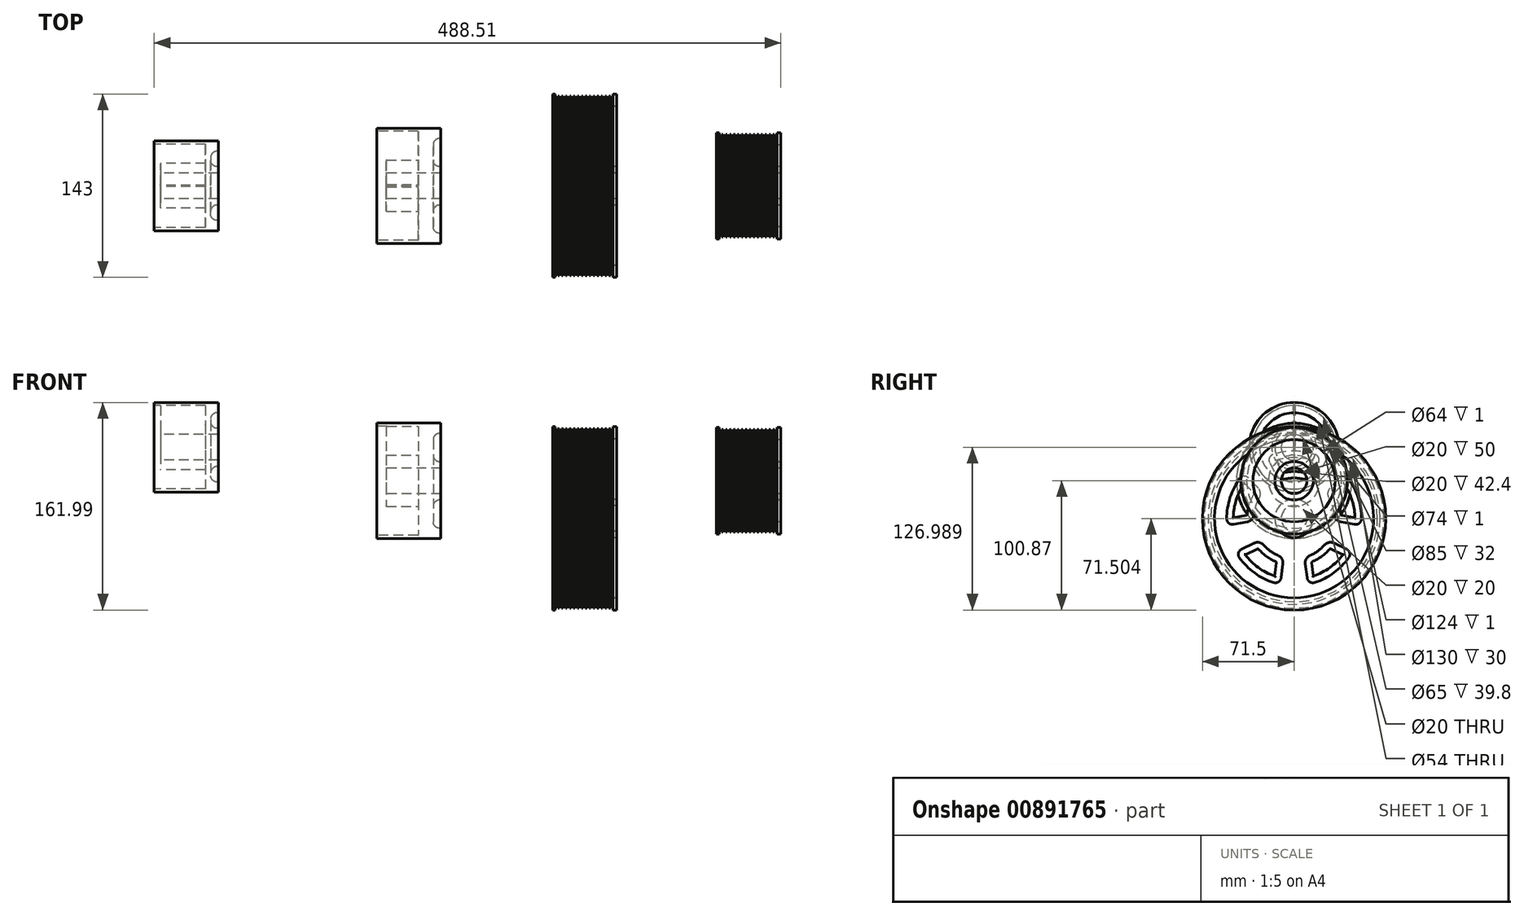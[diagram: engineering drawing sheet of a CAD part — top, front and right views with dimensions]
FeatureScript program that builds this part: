
annotation { "Feature Type Name" : "Feature", "Feature Type Description" : "" }
export const myFeature = defineFeature(function(context is Context, id is Id, definition is map)
    precondition{}
    {
        {
            var Q0;
            Q0=qCreatedBy(makeId("Front.planeOp"),FACE);
            var sketch = newSketch(context, id + "F0", { "sketchPlane" : qUnion([Q0])});
            skLineSegment(sketch, "E0", {"start": v(-106.98, 0) * mm, "end": v(107.53, 0) * mm, "construction": true});
            skLineSegment(sketch, "E1", {"start": v(107.53, 0) * mm, "end": v(107.53, 105.9) * mm, "construction": true});
            skPoint(sketch, "E2", {"position": v(107.53, 40) * mm});
            skPoint(sketch, "E3", {"position": v(57.53, 40) * mm});
            skPoint(sketch, "E4", {"position": v(107.53, 37) * mm});
            skPoint(sketch, "E5", {"position": v(57.53, 37) * mm});
            skPoint(sketch, "E6", {"position": v(107.53, 10) * mm});
            skPoint(sketch, "E7", {"position": v(57.53, 10) * mm});
            skLineSegment(sketch, "E8", {"start": v(57.53, 10) * mm, "end": v(107.53, 10) * mm});
            skLineSegment(sketch, "E9", {"start": v(57.53, 10) * mm, "end": v(57.53, 37) * mm});
            skLineSegment(sketch, "E10", {"start": v(107.53, 37) * mm, "end": v(57.53, 37) * mm});
            skLineSegment(sketch, "E11", {"start": v(57.53, 37) * mm, "end": v(57.53, 40) * mm});
            skLineSegment(sketch, "E12", {"start": v(107.53, 37) * mm, "end": v(107.53, 40) * mm});
            skPoint(sketch, "E13", {"position": v(101.53, 15) * mm});
            skPoint(sketch, "E14", {"position": v(101.53, 32) * mm});
            skLineSegment(sketch, "E15", {"start": v(106.53, 15) * mm, "end": v(107.53, 15) * mm});
            skLineSegment(sketch, "E16", {"start": v(107.53, 15) * mm, "end": v(107.53, 10) * mm});
            skLineSegment(sketch, "E17", {"start": v(101.53, 20) * mm, "end": v(101.53, 27) * mm});
            skLineSegment(sketch, "E18", {"start": v(107.53, 32) * mm, "end": v(107.53, 37) * mm});
            skLineSegment(sketch, "E19", {"start": v(106.53, 32) * mm, "end": v(107.53, 32) * mm});
            skArc(sketch, "E20.filletArc", {"start": v(106.53, 32) * mm, "mid": v(102.99, 30.54) * mm, "end": v(101.53, 27) * mm});
            skArc(sketch, "E21.filletArc", {"start": v(101.53, 20) * mm, "mid": v(102.99, 16.46) * mm, "end": v(106.53, 15) * mm});
            skLineSegment(sketch, "E22", {"start": v(59.53, 40) * mm, "end": v(59.94, 37) * mm});
            skLineSegment(sketch, "E23", {"start": v(59.94, 37) * mm, "end": v(60.94, 37) * mm});
            skLineSegment(sketch, "E24", {"start": v(105.64, 40) * mm, "end": v(105.53, 40) * mm});
            skLineSegment(sketch, "E25", {"start": v(60.94, 37) * mm, "end": v(61.6, 40) * mm});
            skPoint(sketch, "E25.endSnap0", {"position": v(58.53, 40) * mm});
            skLineSegment(sketch, "E26", {"start": v(61.6, 40) * mm, "end": v(62.6, 40) * mm});
            skLineSegment(sketch, "E27.1.0.0", {"start": v(62.6, 40) * mm, "end": v(63, 37) * mm});
            skLineSegment(sketch, "E27.1.0.1", {"start": v(63, 37) * mm, "end": v(64, 37) * mm});
            skLineSegment(sketch, "E27.1.0.2", {"start": v(64, 37) * mm, "end": v(64.67, 40) * mm});
            skLineSegment(sketch, "E27.1.0.3", {"start": v(64.67, 40) * mm, "end": v(65.67, 40) * mm});
            skLineSegment(sketch, "E27.2.0.0", {"start": v(65.67, 40) * mm, "end": v(66.08, 37) * mm});
            skLineSegment(sketch, "E27.2.0.1", {"start": v(66.08, 37) * mm, "end": v(67.08, 37) * mm});
            skLineSegment(sketch, "E27.2.0.2", {"start": v(67.08, 37) * mm, "end": v(67.75, 40) * mm});
            skLineSegment(sketch, "E27.2.0.3", {"start": v(67.75, 40) * mm, "end": v(68.75, 40) * mm});
            skLineSegment(sketch, "E27.3.0.0", {"start": v(68.75, 40) * mm, "end": v(69.16, 37) * mm});
            skLineSegment(sketch, "E27.3.0.1", {"start": v(69.16, 37) * mm, "end": v(70.16, 37) * mm});
            skLineSegment(sketch, "E27.3.0.2", {"start": v(70.16, 37) * mm, "end": v(70.82, 40) * mm});
            skLineSegment(sketch, "E27.3.0.3", {"start": v(70.82, 40) * mm, "end": v(71.82, 40) * mm});
            skLineSegment(sketch, "E27.4.0.0", {"start": v(71.82, 40) * mm, "end": v(72.23, 37) * mm});
            skLineSegment(sketch, "E27.4.0.1", {"start": v(72.23, 37) * mm, "end": v(73.23, 37) * mm});
            skLineSegment(sketch, "E27.4.0.2", {"start": v(73.23, 37) * mm, "end": v(73.9, 40) * mm});
            skLineSegment(sketch, "E27.4.0.3", {"start": v(73.9, 40) * mm, "end": v(74.9, 40) * mm});
            skLineSegment(sketch, "E27.5.0.0", {"start": v(74.9, 40) * mm, "end": v(75.3, 37) * mm});
            skLineSegment(sketch, "E27.5.0.1", {"start": v(75.3, 37) * mm, "end": v(76.3, 37) * mm});
            skLineSegment(sketch, "E27.5.0.2", {"start": v(76.3, 37) * mm, "end": v(76.97, 40) * mm});
            skLineSegment(sketch, "E27.5.0.3", {"start": v(76.97, 40) * mm, "end": v(77.97, 40) * mm});
            skLineSegment(sketch, "E27.6.0.0", {"start": v(77.97, 40) * mm, "end": v(78.38, 37) * mm});
            skLineSegment(sketch, "E27.6.0.1", {"start": v(78.38, 37) * mm, "end": v(79.38, 37) * mm});
            skLineSegment(sketch, "E27.6.0.2", {"start": v(79.38, 37) * mm, "end": v(80.05, 40) * mm});
            skLineSegment(sketch, "E27.6.0.3", {"start": v(80.05, 40) * mm, "end": v(81.05, 40) * mm});
            skLineSegment(sketch, "E27.7.0.0", {"start": v(81.05, 40) * mm, "end": v(81.46, 37) * mm});
            skLineSegment(sketch, "E27.7.0.1", {"start": v(81.46, 37) * mm, "end": v(82.46, 37) * mm});
            skLineSegment(sketch, "E27.7.0.2", {"start": v(82.46, 37) * mm, "end": v(83.12, 40) * mm});
            skLineSegment(sketch, "E27.7.0.3", {"start": v(83.12, 40) * mm, "end": v(84.12, 40) * mm});
            skLineSegment(sketch, "E27.8.0.0", {"start": v(84.12, 40) * mm, "end": v(84.53, 37) * mm});
            skLineSegment(sketch, "E27.8.0.1", {"start": v(84.53, 37) * mm, "end": v(85.53, 37) * mm});
            skLineSegment(sketch, "E27.8.0.2", {"start": v(85.53, 37) * mm, "end": v(86.2, 40) * mm});
            skLineSegment(sketch, "E27.8.0.3", {"start": v(86.2, 40) * mm, "end": v(87.2, 40) * mm});
            skLineSegment(sketch, "E27.9.0.0", {"start": v(87.2, 40) * mm, "end": v(87.6, 37) * mm});
            skLineSegment(sketch, "E27.9.0.1", {"start": v(87.6, 37) * mm, "end": v(88.6, 37) * mm});
            skLineSegment(sketch, "E27.9.0.2", {"start": v(88.6, 37) * mm, "end": v(89.27, 40) * mm});
            skLineSegment(sketch, "E27.9.0.3", {"start": v(89.27, 40) * mm, "end": v(90.27, 40) * mm});
            skLineSegment(sketch, "E27.10.0.0", {"start": v(90.27, 40) * mm, "end": v(90.68, 37) * mm});
            skLineSegment(sketch, "E27.10.0.1", {"start": v(90.68, 37) * mm, "end": v(91.68, 37) * mm});
            skLineSegment(sketch, "E27.10.0.2", {"start": v(91.68, 37) * mm, "end": v(92.34, 40) * mm});
            skLineSegment(sketch, "E27.10.0.3", {"start": v(92.34, 40) * mm, "end": v(93.34, 40) * mm});
            skLineSegment(sketch, "E27.11.0.0", {"start": v(93.34, 40) * mm, "end": v(93.75, 37) * mm});
            skLineSegment(sketch, "E27.11.0.1", {"start": v(93.75, 37) * mm, "end": v(94.75, 37) * mm});
            skLineSegment(sketch, "E27.11.0.2", {"start": v(94.75, 37) * mm, "end": v(95.42, 40) * mm});
            skLineSegment(sketch, "E27.11.0.3", {"start": v(95.42, 40) * mm, "end": v(96.42, 40) * mm});
            skLineSegment(sketch, "E27.12.0.0", {"start": v(96.42, 40) * mm, "end": v(96.83, 37) * mm});
            skLineSegment(sketch, "E27.12.0.1", {"start": v(96.83, 37) * mm, "end": v(97.83, 37) * mm});
            skLineSegment(sketch, "E27.12.0.2", {"start": v(97.83, 37) * mm, "end": v(98.5, 40) * mm});
            skLineSegment(sketch, "E27.12.0.3", {"start": v(98.5, 40) * mm, "end": v(99.5, 40) * mm});
            skLineSegment(sketch, "E27.13.0.0", {"start": v(99.5, 40) * mm, "end": v(99.9, 37) * mm});
            skLineSegment(sketch, "E27.13.0.1", {"start": v(99.9, 37) * mm, "end": v(100.9, 37) * mm});
            skLineSegment(sketch, "E27.13.0.2", {"start": v(100.9, 37) * mm, "end": v(101.57, 40) * mm});
            skLineSegment(sketch, "E27.13.0.3", {"start": v(101.57, 40) * mm, "end": v(102.57, 40) * mm});
            skLineSegment(sketch, "E27.14.0.0", {"start": v(102.57, 40) * mm, "end": v(102.98, 37) * mm});
            skLineSegment(sketch, "E27.14.0.1", {"start": v(102.98, 37) * mm, "end": v(103.98, 37) * mm});
            skLineSegment(sketch, "E27.14.0.2", {"start": v(103.98, 37) * mm, "end": v(104.64, 40) * mm});
            skLineSegment(sketch, "E27.14.0.3", {"start": v(105.53, 40) * mm, "end": v(105.64, 40) * mm});
            skLineSegment(sketch, "E27.direction1", {"start": v(59.94, 37) * mm, "end": v(63, 37) * mm, "construction": true});
            skLineSegment(sketch, "E28", {"start": v(-234.84, -29.37) * mm, "end": v(-20.34, -29.37) * mm, "construction": true});
            skLineSegment(sketch, "E29", {"start": v(-20.34, -29.37) * mm, "end": v(-20.34, 106.53) * mm, "construction": true});
            skPoint(sketch, "E30", {"position": v(-20.34, 40.63) * mm});
            skPoint(sketch, "E31", {"position": v(-70.34, 40.63) * mm});
            skPoint(sketch, "E32", {"position": v(-20.34, 37.63) * mm});
            skPoint(sketch, "E33", {"position": v(-70.34, 37.63) * mm});
            skPoint(sketch, "E34", {"position": v(-20.34, -19.37) * mm});
            skPoint(sketch, "E35", {"position": v(-70.34, -19.37) * mm});
            skLineSegment(sketch, "E36", {"start": v(-70.34, -19.37) * mm, "end": v(-20.34, -19.37) * mm});
            skLineSegment(sketch, "E37", {"start": v(-70.34, -19.37) * mm, "end": v(-70.34, 37.63) * mm});
            skLineSegment(sketch, "E38", {"start": v(-20.34, 37.63) * mm, "end": v(-70.34, 37.63) * mm});
            skLineSegment(sketch, "E39", {"start": v(-70.34, 37.63) * mm, "end": v(-70.34, 40.63) * mm});
            skLineSegment(sketch, "E40", {"start": v(-20.34, 37.63) * mm, "end": v(-20.34, 40.63) * mm});
            skPoint(sketch, "E41", {"position": v(-26.34, -14.37) * mm});
            skPoint(sketch, "E42", {"position": v(-26.34, 32.63) * mm});
            skLineSegment(sketch, "E43", {"start": v(-21.34, -14.37) * mm, "end": v(-20.34, -14.37) * mm});
            skLineSegment(sketch, "E44", {"start": v(-20.34, -14.37) * mm, "end": v(-20.34, -19.37) * mm});
            skLineSegment(sketch, "E45", {"start": v(-26.34, -9.37) * mm, "end": v(-26.34, 27.63) * mm});
            skLineSegment(sketch, "E46", {"start": v(-20.34, 32.63) * mm, "end": v(-20.34, 37.63) * mm});
            skLineSegment(sketch, "E47", {"start": v(-21.34, 32.63) * mm, "end": v(-20.34, 32.63) * mm});
            skArc(sketch, "E48.filletArc", {"start": v(-21.34, 32.63) * mm, "mid": v(-24.87, 31.17) * mm, "end": v(-26.34, 27.63) * mm});
            skArc(sketch, "E49.filletArc", {"start": v(-26.34, -9.37) * mm, "mid": v(-24.87, -12.9) * mm, "end": v(-21.34, -14.37) * mm});
            skLineSegment(sketch, "E50", {"start": v(-68.34, 40.63) * mm, "end": v(-67.93, 37.63) * mm});
            skLineSegment(sketch, "E51", {"start": v(-67.93, 37.63) * mm, "end": v(-66.93, 37.63) * mm});
            skLineSegment(sketch, "E52", {"start": v(-22.22, 40.63) * mm, "end": v(-22.34, 40.63) * mm});
            skLineSegment(sketch, "E53", {"start": v(-66.93, 37.63) * mm, "end": v(-66.26, 40.63) * mm});
            skPoint(sketch, "E53.endSnap0", {"position": v(-69.34, 40.63) * mm});
            skLineSegment(sketch, "E54", {"start": v(-66.26, 40.63) * mm, "end": v(-65.26, 40.63) * mm});
            skLineSegment(sketch, "E55.1.0.0", {"start": v(-65.26, 40.63) * mm, "end": v(-64.85, 37.63) * mm});
            skLineSegment(sketch, "E55.1.0.1", {"start": v(-64.85, 37.63) * mm, "end": v(-63.85, 37.63) * mm});
            skLineSegment(sketch, "E55.1.0.2", {"start": v(-63.85, 37.63) * mm, "end": v(-63.19, 40.63) * mm});
            skLineSegment(sketch, "E55.1.0.3", {"start": v(-63.19, 40.63) * mm, "end": v(-62.19, 40.63) * mm});
            skLineSegment(sketch, "E55.2.0.0", {"start": v(-62.19, 40.63) * mm, "end": v(-61.78, 37.63) * mm});
            skLineSegment(sketch, "E55.2.0.1", {"start": v(-61.78, 37.63) * mm, "end": v(-60.78, 37.63) * mm});
            skLineSegment(sketch, "E55.2.0.2", {"start": v(-60.78, 37.63) * mm, "end": v(-60.11, 40.63) * mm});
            skLineSegment(sketch, "E55.2.0.3", {"start": v(-60.11, 40.63) * mm, "end": v(-59.11, 40.63) * mm});
            skLineSegment(sketch, "E55.3.0.0", {"start": v(-59.11, 40.63) * mm, "end": v(-58.7, 37.63) * mm});
            skLineSegment(sketch, "E55.3.0.1", {"start": v(-58.7, 37.63) * mm, "end": v(-57.7, 37.63) * mm});
            skLineSegment(sketch, "E55.3.0.2", {"start": v(-57.7, 37.63) * mm, "end": v(-57.04, 40.63) * mm});
            skLineSegment(sketch, "E55.3.0.3", {"start": v(-57.04, 40.63) * mm, "end": v(-56.04, 40.63) * mm});
            skLineSegment(sketch, "E55.4.0.0", {"start": v(-56.04, 40.63) * mm, "end": v(-55.63, 37.63) * mm});
            skLineSegment(sketch, "E55.4.0.1", {"start": v(-55.63, 37.63) * mm, "end": v(-54.63, 37.63) * mm});
            skLineSegment(sketch, "E55.4.0.2", {"start": v(-54.63, 37.63) * mm, "end": v(-53.96, 40.63) * mm});
            skLineSegment(sketch, "E55.4.0.3", {"start": v(-53.96, 40.63) * mm, "end": v(-52.96, 40.63) * mm});
            skLineSegment(sketch, "E55.5.0.0", {"start": v(-52.96, 40.63) * mm, "end": v(-52.55, 37.63) * mm});
            skLineSegment(sketch, "E55.5.0.1", {"start": v(-52.55, 37.63) * mm, "end": v(-51.55, 37.63) * mm});
            skLineSegment(sketch, "E55.5.0.2", {"start": v(-51.55, 37.63) * mm, "end": v(-50.89, 40.63) * mm});
            skLineSegment(sketch, "E55.5.0.3", {"start": v(-50.89, 40.63) * mm, "end": v(-49.89, 40.63) * mm});
            skLineSegment(sketch, "E55.6.0.0", {"start": v(-49.89, 40.63) * mm, "end": v(-49.48, 37.63) * mm});
            skLineSegment(sketch, "E55.6.0.1", {"start": v(-49.48, 37.63) * mm, "end": v(-48.48, 37.63) * mm});
            skLineSegment(sketch, "E55.6.0.2", {"start": v(-48.48, 37.63) * mm, "end": v(-47.81, 40.63) * mm});
            skLineSegment(sketch, "E55.6.0.3", {"start": v(-47.81, 40.63) * mm, "end": v(-46.81, 40.63) * mm});
            skLineSegment(sketch, "E55.7.0.0", {"start": v(-46.81, 40.63) * mm, "end": v(-46.4, 37.63) * mm});
            skLineSegment(sketch, "E55.7.0.1", {"start": v(-46.4, 37.63) * mm, "end": v(-45.4, 37.63) * mm});
            skLineSegment(sketch, "E55.7.0.2", {"start": v(-45.4, 37.63) * mm, "end": v(-44.74, 40.63) * mm});
            skLineSegment(sketch, "E55.7.0.3", {"start": v(-44.74, 40.63) * mm, "end": v(-43.74, 40.63) * mm});
            skLineSegment(sketch, "E55.8.0.0", {"start": v(-43.74, 40.63) * mm, "end": v(-43.33, 37.63) * mm});
            skLineSegment(sketch, "E55.8.0.1", {"start": v(-43.33, 37.63) * mm, "end": v(-42.33, 37.63) * mm});
            skLineSegment(sketch, "E55.8.0.2", {"start": v(-42.33, 37.63) * mm, "end": v(-41.67, 40.63) * mm});
            skLineSegment(sketch, "E55.8.0.3", {"start": v(-41.67, 40.63) * mm, "end": v(-40.67, 40.63) * mm});
            skLineSegment(sketch, "E55.9.0.0", {"start": v(-40.67, 40.63) * mm, "end": v(-40.26, 37.63) * mm});
            skLineSegment(sketch, "E55.9.0.1", {"start": v(-40.26, 37.63) * mm, "end": v(-39.26, 37.63) * mm});
            skLineSegment(sketch, "E55.9.0.2", {"start": v(-39.26, 37.63) * mm, "end": v(-38.6, 40.63) * mm});
            skLineSegment(sketch, "E55.9.0.3", {"start": v(-38.6, 40.63) * mm, "end": v(-37.6, 40.63) * mm});
            skLineSegment(sketch, "E55.10.0.0", {"start": v(-37.6, 40.63) * mm, "end": v(-37.18, 37.63) * mm});
            skLineSegment(sketch, "E55.10.0.1", {"start": v(-37.18, 37.63) * mm, "end": v(-36.18, 37.63) * mm});
            skLineSegment(sketch, "E55.10.0.2", {"start": v(-36.18, 37.63) * mm, "end": v(-35.52, 40.63) * mm});
            skLineSegment(sketch, "E55.10.0.3", {"start": v(-35.52, 40.63) * mm, "end": v(-34.52, 40.63) * mm});
            skLineSegment(sketch, "E55.11.0.0", {"start": v(-34.52, 40.63) * mm, "end": v(-34.1, 37.63) * mm});
            skLineSegment(sketch, "E55.11.0.1", {"start": v(-34.1, 37.63) * mm, "end": v(-33.1, 37.63) * mm});
            skLineSegment(sketch, "E55.11.0.2", {"start": v(-33.1, 37.63) * mm, "end": v(-32.44, 40.63) * mm});
            skLineSegment(sketch, "E55.11.0.3", {"start": v(-32.44, 40.63) * mm, "end": v(-31.44, 40.63) * mm});
            skLineSegment(sketch, "E55.12.0.0", {"start": v(-31.44, 40.63) * mm, "end": v(-31.03, 37.63) * mm});
            skLineSegment(sketch, "E55.12.0.1", {"start": v(-31.03, 37.63) * mm, "end": v(-30.03, 37.63) * mm});
            skLineSegment(sketch, "E55.12.0.2", {"start": v(-30.03, 37.63) * mm, "end": v(-29.37, 40.63) * mm});
            skLineSegment(sketch, "E55.12.0.3", {"start": v(-29.37, 40.63) * mm, "end": v(-28.37, 40.63) * mm});
            skLineSegment(sketch, "E55.13.0.0", {"start": v(-28.37, 40.63) * mm, "end": v(-27.96, 37.63) * mm});
            skLineSegment(sketch, "E55.13.0.1", {"start": v(-27.96, 37.63) * mm, "end": v(-26.96, 37.63) * mm});
            skLineSegment(sketch, "E55.13.0.2", {"start": v(-26.96, 37.63) * mm, "end": v(-26.3, 40.63) * mm});
            skLineSegment(sketch, "E55.13.0.3", {"start": v(-26.3, 40.63) * mm, "end": v(-25.3, 40.63) * mm});
            skLineSegment(sketch, "E55.14.0.0", {"start": v(-25.3, 40.63) * mm, "end": v(-24.88, 37.63) * mm});
            skLineSegment(sketch, "E55.14.0.1", {"start": v(-24.88, 37.63) * mm, "end": v(-23.88, 37.63) * mm});
            skLineSegment(sketch, "E55.14.0.2", {"start": v(-23.88, 37.63) * mm, "end": v(-23.22, 40.63) * mm});
            skLineSegment(sketch, "E55.14.0.3", {"start": v(-22.34, 40.63) * mm, "end": v(-22.22, 40.63) * mm});
            skLineSegment(sketch, "E55.direction1", {"start": v(-67.93, 37.63) * mm, "end": v(-64.85, 37.63) * mm, "construction": true});
            skLineSegment(sketch, "E56", {"start": v(-371.94, 0) * mm, "end": v(-157.43, 0) * mm, "construction": true});
            skLineSegment(sketch, "E57", {"start": v(-157.43, 0) * mm, "end": v(-157.43, 105.9) * mm, "construction": true});
            skPoint(sketch, "E58", {"position": v(-157.43, 45) * mm});
            skPoint(sketch, "E59", {"position": v(-207.43, 45) * mm});
            skPoint(sketch, "E60", {"position": v(-157.43, 42) * mm});
            skPoint(sketch, "E61", {"position": v(-207.43, 42) * mm});
            skPoint(sketch, "E62", {"position": v(-157.43, 10) * mm});
            skPoint(sketch, "E63", {"position": v(-207.43, 10) * mm});
            skLineSegment(sketch, "E64", {"start": v(-207.43, 10) * mm, "end": v(-157.43, 10) * mm});
            skLineSegment(sketch, "E65", {"start": v(-207.43, 10) * mm, "end": v(-207.43, 42) * mm});
            skLineSegment(sketch, "E66", {"start": v(-157.43, 42) * mm, "end": v(-207.43, 42) * mm});
            skLineSegment(sketch, "E67", {"start": v(-207.43, 42) * mm, "end": v(-207.43, 45) * mm});
            skLineSegment(sketch, "E68", {"start": v(-157.43, 42) * mm, "end": v(-157.43, 45) * mm});
            skPoint(sketch, "E69", {"position": v(-163.43, 15) * mm});
            skPoint(sketch, "E70", {"position": v(-163.43, 37) * mm});
            skLineSegment(sketch, "E71", {"start": v(-158.43, 15) * mm, "end": v(-157.43, 15) * mm});
            skLineSegment(sketch, "E72", {"start": v(-157.43, 15) * mm, "end": v(-157.43, 10) * mm});
            skLineSegment(sketch, "E73", {"start": v(-163.43, 20) * mm, "end": v(-163.43, 32) * mm});
            skLineSegment(sketch, "E74", {"start": v(-157.43, 37) * mm, "end": v(-157.43, 42) * mm});
            skLineSegment(sketch, "E75", {"start": v(-158.43, 37) * mm, "end": v(-157.43, 37) * mm});
            skArc(sketch, "E76.filletArc", {"start": v(-158.43, 37) * mm, "mid": v(-161.97, 35.54) * mm, "end": v(-163.43, 32) * mm});
            skArc(sketch, "E77.filletArc", {"start": v(-163.43, 20) * mm, "mid": v(-161.97, 16.46) * mm, "end": v(-158.43, 15) * mm});
            skLineSegment(sketch, "E78", {"start": v(-207.43, 45) * mm, "end": v(-205.43, 45) * mm});
            skLineSegment(sketch, "E79", {"start": v(-205.43, 45) * mm, "end": v(-205.02, 42) * mm});
            skLineSegment(sketch, "E80", {"start": v(-205.02, 42) * mm, "end": v(-204.02, 42) * mm});
            skLineSegment(sketch, "E81", {"start": v(-157.43, 45) * mm, "end": v(-159.43, 45) * mm});
            skLineSegment(sketch, "E82", {"start": v(-204.02, 42) * mm, "end": v(-203.36, 45) * mm});
            skPoint(sketch, "E82.endSnap0", {"position": v(-206.43, 45) * mm});
            skLineSegment(sketch, "E83", {"start": v(-203.36, 45) * mm, "end": v(-202.36, 45) * mm});
            skLineSegment(sketch, "E84.1.0.0", {"start": v(-202.36, 45) * mm, "end": v(-201.95, 42) * mm});
            skLineSegment(sketch, "E84.1.0.1", {"start": v(-201.95, 42) * mm, "end": v(-200.95, 42) * mm});
            skLineSegment(sketch, "E84.1.0.2", {"start": v(-200.95, 42) * mm, "end": v(-200.29, 45) * mm});
            skLineSegment(sketch, "E84.1.0.3", {"start": v(-200.29, 45) * mm, "end": v(-199.29, 45) * mm});
            skLineSegment(sketch, "E84.2.0.0", {"start": v(-199.29, 45) * mm, "end": v(-198.88, 42) * mm});
            skLineSegment(sketch, "E84.2.0.1", {"start": v(-198.88, 42) * mm, "end": v(-197.88, 42) * mm});
            skLineSegment(sketch, "E84.2.0.2", {"start": v(-197.88, 42) * mm, "end": v(-197.21, 45) * mm});
            skLineSegment(sketch, "E84.2.0.3", {"start": v(-197.21, 45) * mm, "end": v(-196.21, 45) * mm});
            skLineSegment(sketch, "E84.3.0.0", {"start": v(-196.21, 45) * mm, "end": v(-195.8, 42) * mm});
            skLineSegment(sketch, "E84.3.0.1", {"start": v(-195.8, 42) * mm, "end": v(-194.8, 42) * mm});
            skLineSegment(sketch, "E84.3.0.2", {"start": v(-194.8, 42) * mm, "end": v(-194.14, 45) * mm});
            skLineSegment(sketch, "E84.3.0.3", {"start": v(-194.14, 45) * mm, "end": v(-193.14, 45) * mm});
            skLineSegment(sketch, "E84.4.0.0", {"start": v(-193.14, 45) * mm, "end": v(-192.73, 42) * mm});
            skLineSegment(sketch, "E84.4.0.1", {"start": v(-192.73, 42) * mm, "end": v(-191.73, 42) * mm});
            skLineSegment(sketch, "E84.4.0.2", {"start": v(-191.73, 42) * mm, "end": v(-191.06, 45) * mm});
            skLineSegment(sketch, "E84.4.0.3", {"start": v(-191.06, 45) * mm, "end": v(-190.06, 45) * mm});
            skLineSegment(sketch, "E84.5.0.0", {"start": v(-190.06, 45) * mm, "end": v(-189.65, 42) * mm});
            skLineSegment(sketch, "E84.5.0.1", {"start": v(-189.65, 42) * mm, "end": v(-188.65, 42) * mm});
            skLineSegment(sketch, "E84.5.0.2", {"start": v(-188.65, 42) * mm, "end": v(-187.99, 45) * mm});
            skLineSegment(sketch, "E84.5.0.3", {"start": v(-187.99, 45) * mm, "end": v(-186.99, 45) * mm});
            skLineSegment(sketch, "E84.6.0.0", {"start": v(-186.99, 45) * mm, "end": v(-186.58, 42) * mm});
            skLineSegment(sketch, "E84.6.0.1", {"start": v(-186.58, 42) * mm, "end": v(-185.58, 42) * mm});
            skLineSegment(sketch, "E84.6.0.2", {"start": v(-185.58, 42) * mm, "end": v(-184.91, 45) * mm});
            skLineSegment(sketch, "E84.6.0.3", {"start": v(-184.91, 45) * mm, "end": v(-183.91, 45) * mm});
            skLineSegment(sketch, "E84.7.0.0", {"start": v(-183.91, 45) * mm, "end": v(-183.5, 42) * mm});
            skLineSegment(sketch, "E84.7.0.1", {"start": v(-183.5, 42) * mm, "end": v(-182.5, 42) * mm});
            skLineSegment(sketch, "E84.7.0.2", {"start": v(-182.5, 42) * mm, "end": v(-181.84, 45) * mm});
            skLineSegment(sketch, "E84.7.0.3", {"start": v(-181.84, 45) * mm, "end": v(-180.84, 45) * mm});
            skLineSegment(sketch, "E84.8.0.0", {"start": v(-180.84, 45) * mm, "end": v(-180.43, 42) * mm});
            skLineSegment(sketch, "E84.8.0.1", {"start": v(-180.43, 42) * mm, "end": v(-179.43, 42) * mm});
            skLineSegment(sketch, "E84.8.0.2", {"start": v(-179.43, 42) * mm, "end": v(-178.76, 45) * mm});
            skLineSegment(sketch, "E84.8.0.3", {"start": v(-178.76, 45) * mm, "end": v(-177.76, 45) * mm});
            skLineSegment(sketch, "E84.9.0.0", {"start": v(-177.76, 45) * mm, "end": v(-177.35, 42) * mm});
            skLineSegment(sketch, "E84.9.0.1", {"start": v(-177.35, 42) * mm, "end": v(-176.35, 42) * mm});
            skLineSegment(sketch, "E84.9.0.2", {"start": v(-176.35, 42) * mm, "end": v(-175.7, 45) * mm});
            skLineSegment(sketch, "E84.9.0.3", {"start": v(-175.7, 45) * mm, "end": v(-174.7, 45) * mm});
            skLineSegment(sketch, "E84.10.0.0", {"start": v(-174.7, 45) * mm, "end": v(-174.28, 42) * mm});
            skLineSegment(sketch, "E84.10.0.1", {"start": v(-174.28, 42) * mm, "end": v(-173.28, 42) * mm});
            skLineSegment(sketch, "E84.10.0.2", {"start": v(-173.28, 42) * mm, "end": v(-172.62, 45) * mm});
            skLineSegment(sketch, "E84.10.0.3", {"start": v(-172.62, 45) * mm, "end": v(-171.62, 45) * mm});
            skLineSegment(sketch, "E84.11.0.0", {"start": v(-171.62, 45) * mm, "end": v(-171.2, 42) * mm});
            skLineSegment(sketch, "E84.11.0.1", {"start": v(-171.2, 42) * mm, "end": v(-170.2, 42) * mm});
            skLineSegment(sketch, "E84.11.0.2", {"start": v(-170.2, 42) * mm, "end": v(-169.54, 45) * mm});
            skLineSegment(sketch, "E84.11.0.3", {"start": v(-169.54, 45) * mm, "end": v(-168.54, 45) * mm});
            skLineSegment(sketch, "E84.12.0.0", {"start": v(-168.54, 45) * mm, "end": v(-168.13, 42) * mm});
            skLineSegment(sketch, "E84.12.0.1", {"start": v(-168.13, 42) * mm, "end": v(-167.13, 42) * mm});
            skLineSegment(sketch, "E84.12.0.2", {"start": v(-167.13, 42) * mm, "end": v(-166.47, 45) * mm});
            skLineSegment(sketch, "E84.12.0.3", {"start": v(-166.47, 45) * mm, "end": v(-165.47, 45) * mm});
            skLineSegment(sketch, "E84.13.0.0", {"start": v(-165.47, 45) * mm, "end": v(-165.06, 42) * mm});
            skLineSegment(sketch, "E84.13.0.1", {"start": v(-165.06, 42) * mm, "end": v(-164.06, 42) * mm});
            skLineSegment(sketch, "E84.13.0.2", {"start": v(-164.06, 42) * mm, "end": v(-163.4, 45) * mm});
            skLineSegment(sketch, "E84.13.0.3", {"start": v(-163.4, 45) * mm, "end": v(-162.4, 45) * mm});
            skLineSegment(sketch, "E84.14.0.0", {"start": v(-162.4, 45) * mm, "end": v(-161.98, 42) * mm});
            skLineSegment(sketch, "E84.14.0.1", {"start": v(-161.98, 42) * mm, "end": v(-160.98, 42) * mm});
            skLineSegment(sketch, "E84.14.0.2", {"start": v(-160.98, 42) * mm, "end": v(-160.32, 45) * mm});
            skLineSegment(sketch, "E84.14.0.3", {"start": v(-160.32, 45) * mm, "end": v(-159.32, 45) * mm});
            skLineSegment(sketch, "E84.direction1", {"start": v(-205.02, 42) * mm, "end": v(-201.95, 42) * mm, "construction": true});
            skLineSegment(sketch, "E85", {"start": v(-207.43, 45) * mm, "end": v(-160.32, 45) * mm});
            skLineSegment(sketch, "E86", {"start": v(-545.5, 26.12) * mm, "end": v(-330.98, 26.12) * mm, "construction": true});
            skLineSegment(sketch, "E87", {"start": v(-330.98, 26.12) * mm, "end": v(-330.98, 127.02) * mm, "construction": true});
            skPoint(sketch, "E88", {"position": v(-330.98, 61.12) * mm});
            skPoint(sketch, "E89", {"position": v(-380.98, 61.12) * mm});
            skPoint(sketch, "E90", {"position": v(-330.98, 58.12) * mm});
            skPoint(sketch, "E91", {"position": v(-380.98, 58.12) * mm});
            skPoint(sketch, "E92", {"position": v(-330.98, 36.12) * mm});
            skPoint(sketch, "E93", {"position": v(-380.98, 36.12) * mm});
            skLineSegment(sketch, "E94", {"start": v(-380.98, 36.12) * mm, "end": v(-330.98, 36.12) * mm});
            skLineSegment(sketch, "E95", {"start": v(-380.98, 36.12) * mm, "end": v(-380.98, 58.12) * mm});
            skLineSegment(sketch, "E96", {"start": v(-330.98, 58.12) * mm, "end": v(-380.98, 58.12) * mm});
            skLineSegment(sketch, "E97", {"start": v(-380.98, 58.12) * mm, "end": v(-380.98, 61.12) * mm});
            skLineSegment(sketch, "E98", {"start": v(-330.98, 58.12) * mm, "end": v(-330.98, 61.12) * mm});
            skPoint(sketch, "E99", {"position": v(-336.98, 41.12) * mm});
            skPoint(sketch, "E100", {"position": v(-336.98, 53.12) * mm});
            skLineSegment(sketch, "E101", {"start": v(-331.98, 41.12) * mm, "end": v(-330.98, 41.12) * mm});
            skLineSegment(sketch, "E102", {"start": v(-330.98, 41.12) * mm, "end": v(-330.98, 36.12) * mm});
            skLineSegment(sketch, "E103", {"start": v(-336.98, 46.12) * mm, "end": v(-336.98, 48.12) * mm});
            skLineSegment(sketch, "E104", {"start": v(-330.98, 53.12) * mm, "end": v(-330.98, 58.12) * mm});
            skLineSegment(sketch, "E105", {"start": v(-331.98, 53.12) * mm, "end": v(-330.98, 53.12) * mm});
            skArc(sketch, "E106.filletArc", {"start": v(-331.98, 53.12) * mm, "mid": v(-335.52, 51.65) * mm, "end": v(-336.98, 48.12) * mm});
            skArc(sketch, "E107.filletArc", {"start": v(-336.98, 46.12) * mm, "mid": v(-335.52, 42.58) * mm, "end": v(-331.98, 41.12) * mm});
            skLineSegment(sketch, "E108", {"start": v(-380.98, 61.12) * mm, "end": v(-378.98, 61.12) * mm});
            skLineSegment(sketch, "E109", {"start": v(-378.98, 61.12) * mm, "end": v(-378.57, 58.12) * mm});
            skLineSegment(sketch, "E110", {"start": v(-378.57, 58.12) * mm, "end": v(-377.57, 58.12) * mm});
            skLineSegment(sketch, "E111", {"start": v(-330.98, 61.12) * mm, "end": v(-332.98, 61.12) * mm});
            skLineSegment(sketch, "E112", {"start": v(-377.57, 58.12) * mm, "end": v(-376.9, 61.12) * mm});
            skPoint(sketch, "E112.endSnap0", {"position": v(-379.98, 61.12) * mm});
            skLineSegment(sketch, "E113", {"start": v(-376.9, 61.12) * mm, "end": v(-375.9, 61.12) * mm});
            skLineSegment(sketch, "E114.1.0.0", {"start": v(-375.9, 61.12) * mm, "end": v(-375.5, 58.12) * mm});
            skLineSegment(sketch, "E114.1.0.1", {"start": v(-375.5, 58.12) * mm, "end": v(-374.5, 58.12) * mm});
            skLineSegment(sketch, "E114.1.0.2", {"start": v(-374.5, 58.12) * mm, "end": v(-373.83, 61.12) * mm});
            skLineSegment(sketch, "E114.1.0.3", {"start": v(-373.83, 61.12) * mm, "end": v(-372.83, 61.12) * mm});
            skLineSegment(sketch, "E114.2.0.0", {"start": v(-372.83, 61.12) * mm, "end": v(-372.42, 58.12) * mm});
            skLineSegment(sketch, "E114.2.0.1", {"start": v(-372.42, 58.12) * mm, "end": v(-371.42, 58.12) * mm});
            skLineSegment(sketch, "E114.2.0.2", {"start": v(-371.42, 58.12) * mm, "end": v(-370.76, 61.12) * mm});
            skLineSegment(sketch, "E114.2.0.3", {"start": v(-370.76, 61.12) * mm, "end": v(-369.76, 61.12) * mm});
            skLineSegment(sketch, "E114.3.0.0", {"start": v(-369.76, 61.12) * mm, "end": v(-369.35, 58.12) * mm});
            skLineSegment(sketch, "E114.3.0.1", {"start": v(-369.35, 58.12) * mm, "end": v(-368.35, 58.12) * mm});
            skLineSegment(sketch, "E114.3.0.2", {"start": v(-368.35, 58.12) * mm, "end": v(-367.69, 61.12) * mm});
            skLineSegment(sketch, "E114.3.0.3", {"start": v(-367.69, 61.12) * mm, "end": v(-366.69, 61.12) * mm});
            skLineSegment(sketch, "E114.4.0.0", {"start": v(-366.69, 61.12) * mm, "end": v(-366.28, 58.12) * mm});
            skLineSegment(sketch, "E114.4.0.1", {"start": v(-366.28, 58.12) * mm, "end": v(-365.28, 58.12) * mm});
            skLineSegment(sketch, "E114.4.0.2", {"start": v(-365.28, 58.12) * mm, "end": v(-364.61, 61.12) * mm});
            skLineSegment(sketch, "E114.4.0.3", {"start": v(-364.61, 61.12) * mm, "end": v(-363.61, 61.12) * mm});
            skLineSegment(sketch, "E114.5.0.0", {"start": v(-363.61, 61.12) * mm, "end": v(-363.2, 58.12) * mm});
            skLineSegment(sketch, "E114.5.0.1", {"start": v(-363.2, 58.12) * mm, "end": v(-362.2, 58.12) * mm});
            skLineSegment(sketch, "E114.5.0.2", {"start": v(-362.2, 58.12) * mm, "end": v(-361.54, 61.12) * mm});
            skLineSegment(sketch, "E114.5.0.3", {"start": v(-361.54, 61.12) * mm, "end": v(-360.54, 61.12) * mm});
            skLineSegment(sketch, "E114.6.0.0", {"start": v(-360.54, 61.12) * mm, "end": v(-360.13, 58.12) * mm});
            skLineSegment(sketch, "E114.6.0.1", {"start": v(-360.13, 58.12) * mm, "end": v(-359.13, 58.12) * mm});
            skLineSegment(sketch, "E114.6.0.2", {"start": v(-359.13, 58.12) * mm, "end": v(-358.46, 61.12) * mm});
            skLineSegment(sketch, "E114.6.0.3", {"start": v(-358.46, 61.12) * mm, "end": v(-357.46, 61.12) * mm});
            skLineSegment(sketch, "E114.7.0.0", {"start": v(-357.46, 61.12) * mm, "end": v(-357.05, 58.12) * mm});
            skLineSegment(sketch, "E114.7.0.1", {"start": v(-357.05, 58.12) * mm, "end": v(-356.05, 58.12) * mm});
            skLineSegment(sketch, "E114.7.0.2", {"start": v(-356.05, 58.12) * mm, "end": v(-355.39, 61.12) * mm});
            skLineSegment(sketch, "E114.7.0.3", {"start": v(-355.39, 61.12) * mm, "end": v(-354.39, 61.12) * mm});
            skLineSegment(sketch, "E114.8.0.0", {"start": v(-354.39, 61.12) * mm, "end": v(-353.98, 58.12) * mm});
            skLineSegment(sketch, "E114.8.0.1", {"start": v(-353.98, 58.12) * mm, "end": v(-352.98, 58.12) * mm});
            skLineSegment(sketch, "E114.8.0.2", {"start": v(-352.98, 58.12) * mm, "end": v(-352.31, 61.12) * mm});
            skLineSegment(sketch, "E114.8.0.3", {"start": v(-352.31, 61.12) * mm, "end": v(-351.31, 61.12) * mm});
            skLineSegment(sketch, "E114.9.0.0", {"start": v(-351.31, 61.12) * mm, "end": v(-350.9, 58.12) * mm});
            skLineSegment(sketch, "E114.9.0.1", {"start": v(-350.9, 58.12) * mm, "end": v(-349.9, 58.12) * mm});
            skLineSegment(sketch, "E114.9.0.2", {"start": v(-349.9, 58.12) * mm, "end": v(-349.24, 61.12) * mm});
            skLineSegment(sketch, "E114.9.0.3", {"start": v(-349.24, 61.12) * mm, "end": v(-348.24, 61.12) * mm});
            skLineSegment(sketch, "E114.10.0.0", {"start": v(-348.24, 61.12) * mm, "end": v(-347.83, 58.12) * mm});
            skLineSegment(sketch, "E114.10.0.1", {"start": v(-347.83, 58.12) * mm, "end": v(-346.83, 58.12) * mm});
            skLineSegment(sketch, "E114.10.0.2", {"start": v(-346.83, 58.12) * mm, "end": v(-346.16, 61.12) * mm});
            skLineSegment(sketch, "E114.10.0.3", {"start": v(-346.16, 61.12) * mm, "end": v(-345.16, 61.12) * mm});
            skLineSegment(sketch, "E114.11.0.0", {"start": v(-345.16, 61.12) * mm, "end": v(-344.75, 58.12) * mm});
            skLineSegment(sketch, "E114.11.0.1", {"start": v(-344.75, 58.12) * mm, "end": v(-343.75, 58.12) * mm});
            skLineSegment(sketch, "E114.11.0.2", {"start": v(-343.75, 58.12) * mm, "end": v(-343.1, 61.12) * mm});
            skLineSegment(sketch, "E114.11.0.3", {"start": v(-343.1, 61.12) * mm, "end": v(-342.1, 61.12) * mm});
            skLineSegment(sketch, "E114.12.0.0", {"start": v(-342.1, 61.12) * mm, "end": v(-341.68, 58.12) * mm});
            skLineSegment(sketch, "E114.12.0.1", {"start": v(-341.68, 58.12) * mm, "end": v(-340.68, 58.12) * mm});
            skLineSegment(sketch, "E114.12.0.2", {"start": v(-340.68, 58.12) * mm, "end": v(-340.02, 61.12) * mm});
            skLineSegment(sketch, "E114.12.0.3", {"start": v(-340.02, 61.12) * mm, "end": v(-339.02, 61.12) * mm});
            skLineSegment(sketch, "E114.13.0.0", {"start": v(-339.02, 61.12) * mm, "end": v(-338.6, 58.12) * mm});
            skLineSegment(sketch, "E114.13.0.1", {"start": v(-338.6, 58.12) * mm, "end": v(-337.6, 58.12) * mm});
            skLineSegment(sketch, "E114.13.0.2", {"start": v(-337.6, 58.12) * mm, "end": v(-336.94, 61.12) * mm});
            skLineSegment(sketch, "E114.13.0.3", {"start": v(-336.94, 61.12) * mm, "end": v(-335.94, 61.12) * mm});
            skLineSegment(sketch, "E114.14.0.0", {"start": v(-335.94, 61.12) * mm, "end": v(-335.53, 58.12) * mm});
            skLineSegment(sketch, "E114.14.0.1", {"start": v(-335.53, 58.12) * mm, "end": v(-334.53, 58.12) * mm});
            skLineSegment(sketch, "E114.14.0.2", {"start": v(-334.53, 58.12) * mm, "end": v(-333.87, 61.12) * mm});
            skLineSegment(sketch, "E114.14.0.3", {"start": v(-333.87, 61.12) * mm, "end": v(-332.87, 61.12) * mm});
            skLineSegment(sketch, "E114.direction1", {"start": v(-378.57, 58.12) * mm, "end": v(-375.5, 58.12) * mm, "construction": true});
            skLineSegment(sketch, "E115", {"start": v(-380.98, 61.12) * mm, "end": v(-333.87, 61.12) * mm});
            skLineSegment(sketch, "E116", {"start": v(57.53, 40) * mm, "end": v(57.53, 41.5) * mm});
            skLineSegment(sketch, "E117", {"start": v(57.53, 41.5) * mm, "end": v(59.53, 41.5) * mm});
            skLineSegment(sketch, "E118", {"start": v(59.53, 41.5) * mm, "end": v(59.53, 40) * mm});
            skLineSegment(sketch, "E119", {"start": v(104.64, 40) * mm, "end": v(104.64, 41.5) * mm});
            skLineSegment(sketch, "E120", {"start": v(104.64, 41.5) * mm, "end": v(107.53, 41.5) * mm});
            skLineSegment(sketch, "E121", {"start": v(107.53, 41.5) * mm, "end": v(107.53, 40) * mm});
            skLineSegment(sketch, "E122", {"start": v(-70.34, 40.63) * mm, "end": v(-70.34, 42.13) * mm});
            skLineSegment(sketch, "E123", {"start": v(-70.34, 42.13) * mm, "end": v(-68.34, 42.13) * mm});
            skLineSegment(sketch, "E124", {"start": v(-68.34, 42.13) * mm, "end": v(-68.34, 40.63) * mm});
            skLineSegment(sketch, "E125", {"start": v(-23.22, 40.63) * mm, "end": v(-23.22, 42.13) * mm});
            skLineSegment(sketch, "E126", {"start": v(-23.22, 42.13) * mm, "end": v(-20.34, 42.13) * mm});
            skLineSegment(sketch, "E127", {"start": v(-20.34, 42.13) * mm, "end": v(-20.34, 40.63) * mm});
            skSolve(sketch);
        }
        {
            var Q0;
            Q0=makeQuery(id+"F0.imprint","IMPRINT",FACE,{"disambiguationData":[TD([[makeQuery(id+"F0.imprint","IMPRINT",EDGE,{"derivedFrom":sQuery(id+"F0.wireOp",EDGE,"E94")}),1.0]])]});
            var Q1;
            {var subQ4=sQuery(id+"F0.wireOp",EDGE,"E98");Q1=makeQuery(id+"F0.imprint","IMPRINT",FACE,{"disambiguationData":[TD([[makeQuery(id+"F0.imprint","IMPRINT",EDGE,{"derivedFrom":subQ4}),1.0]])]});}
            var Q2;
            {var subQ0=sQuery(id+"F0.wireOp",EDGE,"E114.14.0.0");Q2=makeQuery(id+"F0.imprint","IMPRINT",FACE,{"disambiguationData":[TD([[makeQuery(id+"F0.imprint","IMPRINT",EDGE,{"derivedFrom":subQ0}),1.0]])]});}
            var Q3;
            {var subQ0=sQuery(id+"F0.wireOp",EDGE,"E97");Q3=makeQuery(id+"F0.imprint","IMPRINT",FACE,{"disambiguationData":[TD([[makeQuery(id+"F0.imprint","IMPRINT",EDGE,{"derivedFrom":subQ0}),-1.0]])]});}
            var Q4;
            {var subQ0=sQuery(id+"F0.wireOp",EDGE,"E114.13.0.2");Q4=makeQuery(id+"F0.imprint","IMPRINT",FACE,{"disambiguationData":[TD([[makeQuery(id+"F0.imprint","IMPRINT",EDGE,{"derivedFrom":subQ0}),-1.0]])]});}
            var Q5;
            {var subQ0=sQuery(id+"F0.wireOp",EDGE,"E114.12.0.2");Q5=makeQuery(id+"F0.imprint","IMPRINT",FACE,{"disambiguationData":[TD([[makeQuery(id+"F0.imprint","IMPRINT",EDGE,{"derivedFrom":subQ0}),-1.0]])]});}
            var Q6;
            {var subQ0=sQuery(id+"F0.wireOp",EDGE,"E114.13.0.0");Q6=makeQuery(id+"F0.imprint","IMPRINT",FACE,{"disambiguationData":[TD([[makeQuery(id+"F0.imprint","IMPRINT",EDGE,{"derivedFrom":subQ0}),1.0]])]});}
            var Q7;
            {var subQ0=sQuery(id+"F0.wireOp",EDGE,"E109");Q7=makeQuery(id+"F0.imprint","IMPRINT",FACE,{"disambiguationData":[TD([[makeQuery(id+"F0.imprint","IMPRINT",EDGE,{"derivedFrom":subQ0}),1.0]])]});}
            var Q8;
            {var subQ0=sQuery(id+"F0.wireOp",EDGE,"E114.12.0.0");Q8=makeQuery(id+"F0.imprint","IMPRINT",FACE,{"disambiguationData":[TD([[makeQuery(id+"F0.imprint","IMPRINT",EDGE,{"derivedFrom":subQ0}),1.0]])]});}
            var Q9;
            {var subQ0=sQuery(id+"F0.wireOp",EDGE,"E112");Q9=makeQuery(id+"F0.imprint","IMPRINT",FACE,{"disambiguationData":[TD([[makeQuery(id+"F0.imprint","IMPRINT",EDGE,{"derivedFrom":subQ0}),-1.0]])]});}
            var Q10;
            {var subQ0=sQuery(id+"F0.wireOp",EDGE,"E114.6.0.2");Q10=makeQuery(id+"F0.imprint","IMPRINT",FACE,{"disambiguationData":[TD([[makeQuery(id+"F0.imprint","IMPRINT",EDGE,{"derivedFrom":subQ0}),-1.0]])]});}
            var Q11;
            {var subQ0=sQuery(id+"F0.wireOp",EDGE,"E114.11.0.2");Q11=makeQuery(id+"F0.imprint","IMPRINT",FACE,{"disambiguationData":[TD([[makeQuery(id+"F0.imprint","IMPRINT",EDGE,{"derivedFrom":subQ0}),-1.0]])]});}
            var Q12;
            {var subQ0=sQuery(id+"F0.wireOp",EDGE,"E114.1.0.0");Q12=makeQuery(id+"F0.imprint","IMPRINT",FACE,{"disambiguationData":[TD([[makeQuery(id+"F0.imprint","IMPRINT",EDGE,{"derivedFrom":subQ0}),1.0]])]});}
            var Q13;
            {var subQ0=sQuery(id+"F0.wireOp",EDGE,"E114.2.0.0");Q13=makeQuery(id+"F0.imprint","IMPRINT",FACE,{"disambiguationData":[TD([[makeQuery(id+"F0.imprint","IMPRINT",EDGE,{"derivedFrom":subQ0}),1.0]])]});}
            var Q14;
            {var subQ0=sQuery(id+"F0.wireOp",EDGE,"E114.10.0.2");Q14=makeQuery(id+"F0.imprint","IMPRINT",FACE,{"disambiguationData":[TD([[makeQuery(id+"F0.imprint","IMPRINT",EDGE,{"derivedFrom":subQ0}),-1.0]])]});}
            var Q15;
            {var subQ0=sQuery(id+"F0.wireOp",EDGE,"E114.8.0.2");Q15=makeQuery(id+"F0.imprint","IMPRINT",FACE,{"disambiguationData":[TD([[makeQuery(id+"F0.imprint","IMPRINT",EDGE,{"derivedFrom":subQ0}),-1.0]])]});}
            var Q16;
            {var subQ0=sQuery(id+"F0.wireOp",EDGE,"E114.5.0.2");Q16=makeQuery(id+"F0.imprint","IMPRINT",FACE,{"disambiguationData":[TD([[makeQuery(id+"F0.imprint","IMPRINT",EDGE,{"derivedFrom":subQ0}),-1.0]])]});}
            var Q17;
            {var subQ0=sQuery(id+"F0.wireOp",EDGE,"E114.10.0.0");Q17=makeQuery(id+"F0.imprint","IMPRINT",FACE,{"disambiguationData":[TD([[makeQuery(id+"F0.imprint","IMPRINT",EDGE,{"derivedFrom":subQ0}),1.0]])]});}
            var Q18;
            {var subQ0=sQuery(id+"F0.wireOp",EDGE,"E114.4.0.2");Q18=makeQuery(id+"F0.imprint","IMPRINT",FACE,{"disambiguationData":[TD([[makeQuery(id+"F0.imprint","IMPRINT",EDGE,{"derivedFrom":subQ0}),-1.0]])]});}
            var Q19;
            {var subQ0=sQuery(id+"F0.wireOp",EDGE,"E114.7.0.2");Q19=makeQuery(id+"F0.imprint","IMPRINT",FACE,{"disambiguationData":[TD([[makeQuery(id+"F0.imprint","IMPRINT",EDGE,{"derivedFrom":subQ0}),-1.0]])]});}
            var Q20;
            {var subQ0=sQuery(id+"F0.wireOp",EDGE,"E114.7.0.0");Q20=makeQuery(id+"F0.imprint","IMPRINT",FACE,{"disambiguationData":[TD([[makeQuery(id+"F0.imprint","IMPRINT",EDGE,{"derivedFrom":subQ0}),1.0]])]});}
            var Q21;
            {var subQ0=sQuery(id+"F0.wireOp",EDGE,"E114.9.0.2");Q21=makeQuery(id+"F0.imprint","IMPRINT",FACE,{"disambiguationData":[TD([[makeQuery(id+"F0.imprint","IMPRINT",EDGE,{"derivedFrom":subQ0}),-1.0]])]});}
            var Q22;
            {var subQ0=sQuery(id+"F0.wireOp",EDGE,"E114.4.0.0");Q22=makeQuery(id+"F0.imprint","IMPRINT",FACE,{"disambiguationData":[TD([[makeQuery(id+"F0.imprint","IMPRINT",EDGE,{"derivedFrom":subQ0}),1.0]])]});}
            var Q23;
            {var subQ0=sQuery(id+"F0.wireOp",EDGE,"E114.1.0.2");Q23=makeQuery(id+"F0.imprint","IMPRINT",FACE,{"disambiguationData":[TD([[makeQuery(id+"F0.imprint","IMPRINT",EDGE,{"derivedFrom":subQ0}),-1.0]])]});}
            var Q24;
            {var subQ0=sQuery(id+"F0.wireOp",EDGE,"E114.8.0.0");Q24=makeQuery(id+"F0.imprint","IMPRINT",FACE,{"disambiguationData":[TD([[makeQuery(id+"F0.imprint","IMPRINT",EDGE,{"derivedFrom":subQ0}),1.0]])]});}
            var Q25;
            {var subQ0=sQuery(id+"F0.wireOp",EDGE,"E114.6.0.0");Q25=makeQuery(id+"F0.imprint","IMPRINT",FACE,{"disambiguationData":[TD([[makeQuery(id+"F0.imprint","IMPRINT",EDGE,{"derivedFrom":subQ0}),1.0]])]});}
            var Q26;
            {var subQ0=sQuery(id+"F0.wireOp",EDGE,"E114.11.0.0");Q26=makeQuery(id+"F0.imprint","IMPRINT",FACE,{"disambiguationData":[TD([[makeQuery(id+"F0.imprint","IMPRINT",EDGE,{"derivedFrom":subQ0}),1.0]])]});}
            var Q27;
            {var subQ0=sQuery(id+"F0.wireOp",EDGE,"E114.3.0.2");Q27=makeQuery(id+"F0.imprint","IMPRINT",FACE,{"disambiguationData":[TD([[makeQuery(id+"F0.imprint","IMPRINT",EDGE,{"derivedFrom":subQ0}),-1.0]])]});}
            var Q28;
            {var subQ0=sQuery(id+"F0.wireOp",EDGE,"E114.5.0.0");Q28=makeQuery(id+"F0.imprint","IMPRINT",FACE,{"disambiguationData":[TD([[makeQuery(id+"F0.imprint","IMPRINT",EDGE,{"derivedFrom":subQ0}),1.0]])]});}
            var Q29;
            {var subQ0=sQuery(id+"F0.wireOp",EDGE,"E114.3.0.0");Q29=makeQuery(id+"F0.imprint","IMPRINT",FACE,{"disambiguationData":[TD([[makeQuery(id+"F0.imprint","IMPRINT",EDGE,{"derivedFrom":subQ0}),1.0]])]});}
            var Q30;
            {var subQ0=sQuery(id+"F0.wireOp",EDGE,"E114.9.0.0");Q30=makeQuery(id+"F0.imprint","IMPRINT",FACE,{"disambiguationData":[TD([[makeQuery(id+"F0.imprint","IMPRINT",EDGE,{"derivedFrom":subQ0}),1.0]])]});}
            var Q31;
            {var subQ0=sQuery(id+"F0.wireOp",EDGE,"E114.2.0.2");Q31=makeQuery(id+"F0.imprint","IMPRINT",FACE,{"disambiguationData":[TD([[makeQuery(id+"F0.imprint","IMPRINT",EDGE,{"derivedFrom":subQ0}),-1.0]])]});}
            var Q32;
            Q32=sQuery(id+"F0.wireOp",EDGE,"E86");
            revolve(context, id + "F1", {"surfaceOperationType" : NewSurfaceOperationType.NEW, "entities" : qUnion([Q0, Q1, Q2, Q3, Q4, Q5, Q6, Q7, Q8, Q9, Q10, Q11, Q12, Q13, Q14, Q15, Q16, Q17, Q18, Q19, Q20, Q21, Q22, Q23, Q24, Q25, Q26, Q27, Q28, Q29, Q30, Q31]), "axis" : qUnion([Q32]), "revolveType" : RevolveType.FULL});
        }
        {
            var Q0;
            Q0=makeQuery(id+"F0.imprint","IMPRINT",FACE,{"disambiguationData":[TD([[makeQuery(id+"F0.imprint","IMPRINT",EDGE,{"derivedFrom":sQuery(id+"F0.wireOp",EDGE,"E64")}),1.0]])]});
            var Q1;
            {var subQ4=sQuery(id+"F0.wireOp",EDGE,"E68");Q1=makeQuery(id+"F0.imprint","IMPRINT",FACE,{"disambiguationData":[TD([[makeQuery(id+"F0.imprint","IMPRINT",EDGE,{"derivedFrom":subQ4}),1.0]])]});}
            var Q2;
            {var subQ0=sQuery(id+"F0.wireOp",EDGE,"E84.14.0.0");Q2=makeQuery(id+"F0.imprint","IMPRINT",FACE,{"disambiguationData":[TD([[makeQuery(id+"F0.imprint","IMPRINT",EDGE,{"derivedFrom":subQ0}),1.0]])]});}
            var Q3;
            {var subQ0=sQuery(id+"F0.wireOp",EDGE,"E84.7.0.2");Q3=makeQuery(id+"F0.imprint","IMPRINT",FACE,{"disambiguationData":[TD([[makeQuery(id+"F0.imprint","IMPRINT",EDGE,{"derivedFrom":subQ0}),-1.0]])]});}
            var Q4;
            {var subQ0=sQuery(id+"F0.wireOp",EDGE,"E84.8.0.2");Q4=makeQuery(id+"F0.imprint","IMPRINT",FACE,{"disambiguationData":[TD([[makeQuery(id+"F0.imprint","IMPRINT",EDGE,{"derivedFrom":subQ0}),-1.0]])]});}
            var Q5;
            {var subQ0=sQuery(id+"F0.wireOp",EDGE,"E84.13.0.2");Q5=makeQuery(id+"F0.imprint","IMPRINT",FACE,{"disambiguationData":[TD([[makeQuery(id+"F0.imprint","IMPRINT",EDGE,{"derivedFrom":subQ0}),-1.0]])]});}
            var Q6;
            {var subQ0=sQuery(id+"F0.wireOp",EDGE,"E84.2.0.2");Q6=makeQuery(id+"F0.imprint","IMPRINT",FACE,{"disambiguationData":[TD([[makeQuery(id+"F0.imprint","IMPRINT",EDGE,{"derivedFrom":subQ0}),-1.0]])]});}
            var Q7;
            {var subQ0=sQuery(id+"F0.wireOp",EDGE,"E84.13.0.0");Q7=makeQuery(id+"F0.imprint","IMPRINT",FACE,{"disambiguationData":[TD([[makeQuery(id+"F0.imprint","IMPRINT",EDGE,{"derivedFrom":subQ0}),1.0]])]});}
            var Q8;
            {var subQ0=sQuery(id+"F0.wireOp",EDGE,"E84.9.0.2");Q8=makeQuery(id+"F0.imprint","IMPRINT",FACE,{"disambiguationData":[TD([[makeQuery(id+"F0.imprint","IMPRINT",EDGE,{"derivedFrom":subQ0}),-1.0]])]});}
            var Q9;
            {var subQ0=sQuery(id+"F0.wireOp",EDGE,"E84.9.0.0");Q9=makeQuery(id+"F0.imprint","IMPRINT",FACE,{"disambiguationData":[TD([[makeQuery(id+"F0.imprint","IMPRINT",EDGE,{"derivedFrom":subQ0}),1.0]])]});}
            var Q10;
            {var subQ0=sQuery(id+"F0.wireOp",EDGE,"E84.7.0.0");Q10=makeQuery(id+"F0.imprint","IMPRINT",FACE,{"disambiguationData":[TD([[makeQuery(id+"F0.imprint","IMPRINT",EDGE,{"derivedFrom":subQ0}),1.0]])]});}
            var Q11;
            {var subQ0=sQuery(id+"F0.wireOp",EDGE,"E84.8.0.0");Q11=makeQuery(id+"F0.imprint","IMPRINT",FACE,{"disambiguationData":[TD([[makeQuery(id+"F0.imprint","IMPRINT",EDGE,{"derivedFrom":subQ0}),1.0]])]});}
            var Q12;
            {var subQ0=sQuery(id+"F0.wireOp",EDGE,"E84.10.0.2");Q12=makeQuery(id+"F0.imprint","IMPRINT",FACE,{"disambiguationData":[TD([[makeQuery(id+"F0.imprint","IMPRINT",EDGE,{"derivedFrom":subQ0}),-1.0]])]});}
            var Q13;
            {var subQ0=sQuery(id+"F0.wireOp",EDGE,"E84.6.0.2");Q13=makeQuery(id+"F0.imprint","IMPRINT",FACE,{"disambiguationData":[TD([[makeQuery(id+"F0.imprint","IMPRINT",EDGE,{"derivedFrom":subQ0}),-1.0]])]});}
            var Q14;
            {var subQ0=sQuery(id+"F0.wireOp",EDGE,"E67");Q14=makeQuery(id+"F0.imprint","IMPRINT",FACE,{"disambiguationData":[TD([[makeQuery(id+"F0.imprint","IMPRINT",EDGE,{"derivedFrom":subQ0}),-1.0]])]});}
            var Q15;
            {var subQ0=sQuery(id+"F0.wireOp",EDGE,"E84.1.0.0");Q15=makeQuery(id+"F0.imprint","IMPRINT",FACE,{"disambiguationData":[TD([[makeQuery(id+"F0.imprint","IMPRINT",EDGE,{"derivedFrom":subQ0}),1.0]])]});}
            var Q16;
            {var subQ0=sQuery(id+"F0.wireOp",EDGE,"E84.4.0.0");Q16=makeQuery(id+"F0.imprint","IMPRINT",FACE,{"disambiguationData":[TD([[makeQuery(id+"F0.imprint","IMPRINT",EDGE,{"derivedFrom":subQ0}),1.0]])]});}
            var Q17;
            {var subQ0=sQuery(id+"F0.wireOp",EDGE,"E84.2.0.0");Q17=makeQuery(id+"F0.imprint","IMPRINT",FACE,{"disambiguationData":[TD([[makeQuery(id+"F0.imprint","IMPRINT",EDGE,{"derivedFrom":subQ0}),1.0]])]});}
            var Q18;
            {var subQ0=sQuery(id+"F0.wireOp",EDGE,"E84.11.0.2");Q18=makeQuery(id+"F0.imprint","IMPRINT",FACE,{"disambiguationData":[TD([[makeQuery(id+"F0.imprint","IMPRINT",EDGE,{"derivedFrom":subQ0}),-1.0]])]});}
            var Q19;
            {var subQ0=sQuery(id+"F0.wireOp",EDGE,"E84.10.0.0");Q19=makeQuery(id+"F0.imprint","IMPRINT",FACE,{"disambiguationData":[TD([[makeQuery(id+"F0.imprint","IMPRINT",EDGE,{"derivedFrom":subQ0}),1.0]])]});}
            var Q20;
            {var subQ0=sQuery(id+"F0.wireOp",EDGE,"E84.3.0.2");Q20=makeQuery(id+"F0.imprint","IMPRINT",FACE,{"disambiguationData":[TD([[makeQuery(id+"F0.imprint","IMPRINT",EDGE,{"derivedFrom":subQ0}),-1.0]])]});}
            var Q21;
            {var subQ0=sQuery(id+"F0.wireOp",EDGE,"E84.5.0.0");Q21=makeQuery(id+"F0.imprint","IMPRINT",FACE,{"disambiguationData":[TD([[makeQuery(id+"F0.imprint","IMPRINT",EDGE,{"derivedFrom":subQ0}),1.0]])]});}
            var Q22;
            {var subQ0=sQuery(id+"F0.wireOp",EDGE,"E84.12.0.2");Q22=makeQuery(id+"F0.imprint","IMPRINT",FACE,{"disambiguationData":[TD([[makeQuery(id+"F0.imprint","IMPRINT",EDGE,{"derivedFrom":subQ0}),-1.0]])]});}
            var Q23;
            {var subQ0=sQuery(id+"F0.wireOp",EDGE,"E79");Q23=makeQuery(id+"F0.imprint","IMPRINT",FACE,{"disambiguationData":[TD([[makeQuery(id+"F0.imprint","IMPRINT",EDGE,{"derivedFrom":subQ0}),1.0]])]});}
            var Q24;
            {var subQ0=sQuery(id+"F0.wireOp",EDGE,"E84.6.0.0");Q24=makeQuery(id+"F0.imprint","IMPRINT",FACE,{"disambiguationData":[TD([[makeQuery(id+"F0.imprint","IMPRINT",EDGE,{"derivedFrom":subQ0}),1.0]])]});}
            var Q25;
            {var subQ0=sQuery(id+"F0.wireOp",EDGE,"E84.3.0.0");Q25=makeQuery(id+"F0.imprint","IMPRINT",FACE,{"disambiguationData":[TD([[makeQuery(id+"F0.imprint","IMPRINT",EDGE,{"derivedFrom":subQ0}),1.0]])]});}
            var Q26;
            {var subQ0=sQuery(id+"F0.wireOp",EDGE,"E84.1.0.2");Q26=makeQuery(id+"F0.imprint","IMPRINT",FACE,{"disambiguationData":[TD([[makeQuery(id+"F0.imprint","IMPRINT",EDGE,{"derivedFrom":subQ0}),-1.0]])]});}
            var Q27;
            {var subQ0=sQuery(id+"F0.wireOp",EDGE,"E82");Q27=makeQuery(id+"F0.imprint","IMPRINT",FACE,{"disambiguationData":[TD([[makeQuery(id+"F0.imprint","IMPRINT",EDGE,{"derivedFrom":subQ0}),-1.0]])]});}
            var Q28;
            {var subQ0=sQuery(id+"F0.wireOp",EDGE,"E84.11.0.0");Q28=makeQuery(id+"F0.imprint","IMPRINT",FACE,{"disambiguationData":[TD([[makeQuery(id+"F0.imprint","IMPRINT",EDGE,{"derivedFrom":subQ0}),1.0]])]});}
            var Q29;
            {var subQ0=sQuery(id+"F0.wireOp",EDGE,"E84.12.0.0");Q29=makeQuery(id+"F0.imprint","IMPRINT",FACE,{"disambiguationData":[TD([[makeQuery(id+"F0.imprint","IMPRINT",EDGE,{"derivedFrom":subQ0}),1.0]])]});}
            var Q30;
            {var subQ0=sQuery(id+"F0.wireOp",EDGE,"E84.5.0.2");Q30=makeQuery(id+"F0.imprint","IMPRINT",FACE,{"disambiguationData":[TD([[makeQuery(id+"F0.imprint","IMPRINT",EDGE,{"derivedFrom":subQ0}),-1.0]])]});}
            var Q31;
            {var subQ0=sQuery(id+"F0.wireOp",EDGE,"E84.4.0.2");Q31=makeQuery(id+"F0.imprint","IMPRINT",FACE,{"disambiguationData":[TD([[makeQuery(id+"F0.imprint","IMPRINT",EDGE,{"derivedFrom":subQ0}),-1.0]])]});}
            var Q32;
            Q32=sQuery(id+"F0.wireOp",EDGE,"E56");
            revolve(context, id + "F2", {"surfaceOperationType" : NewSurfaceOperationType.NEW, "entities" : qUnion([Q0, Q1, Q2, Q3, Q4, Q5, Q6, Q7, Q8, Q9, Q10, Q11, Q12, Q13, Q14, Q15, Q16, Q17, Q18, Q19, Q20, Q21, Q22, Q23, Q24, Q25, Q26, Q27, Q28, Q29, Q30, Q31]), "axis" : qUnion([Q32]), "revolveType" : RevolveType.FULL});
        }
        {
            var Q0;
            Q0=makeQuery(id+"F0.imprint","IMPRINT",FACE,{"disambiguationData":[TD([[makeQuery(id+"F0.imprint","IMPRINT",EDGE,{"derivedFrom":sQuery(id+"F0.wireOp",EDGE,"E36")}),1.0]])]});
            var Q1;
            {var subQ1=sQuery(id+"F0.wireOp",EDGE,"E40");Q1=makeQuery(id+"F0.imprint","IMPRINT",FACE,{"disambiguationData":[TD([[makeQuery(id+"F0.imprint","IMPRINT",EDGE,{"derivedFrom":subQ1}),1.0]])]});}
            var Q2;
            {var subQ0=sQuery(id+"F0.wireOp",EDGE,"E55.10.0.2");Q2=makeQuery(id+"F0.imprint","IMPRINT",FACE,{"disambiguationData":[TD([[makeQuery(id+"F0.imprint","IMPRINT",EDGE,{"derivedFrom":subQ0}),-1.0]])]});}
            var Q3;
            {var subQ0=sQuery(id+"F0.wireOp",EDGE,"E55.13.0.2");Q3=makeQuery(id+"F0.imprint","IMPRINT",FACE,{"disambiguationData":[TD([[makeQuery(id+"F0.imprint","IMPRINT",EDGE,{"derivedFrom":subQ0}),-1.0]])]});}
            var Q4;
            {var subQ0=sQuery(id+"F0.wireOp",EDGE,"E55.12.0.2");Q4=makeQuery(id+"F0.imprint","IMPRINT",FACE,{"disambiguationData":[TD([[makeQuery(id+"F0.imprint","IMPRINT",EDGE,{"derivedFrom":subQ0}),-1.0]])]});}
            var Q5;
            {var subQ0=sQuery(id+"F0.wireOp",EDGE,"E39");Q5=makeQuery(id+"F0.imprint","IMPRINT",FACE,{"disambiguationData":[TD([[makeQuery(id+"F0.imprint","IMPRINT",EDGE,{"derivedFrom":subQ0}),-1.0]])]});}
            var Q6;
            {var subQ0=sQuery(id+"F0.wireOp",EDGE,"E55.11.0.2");Q6=makeQuery(id+"F0.imprint","IMPRINT",FACE,{"disambiguationData":[TD([[makeQuery(id+"F0.imprint","IMPRINT",EDGE,{"derivedFrom":subQ0}),-1.0]])]});}
            var Q7;
            {var subQ0=sQuery(id+"F0.wireOp",EDGE,"E55.4.0.2");Q7=makeQuery(id+"F0.imprint","IMPRINT",FACE,{"disambiguationData":[TD([[makeQuery(id+"F0.imprint","IMPRINT",EDGE,{"derivedFrom":subQ0}),-1.0]])]});}
            var Q8;
            {var subQ0=sQuery(id+"F0.wireOp",EDGE,"E55.8.0.2");Q8=makeQuery(id+"F0.imprint","IMPRINT",FACE,{"disambiguationData":[TD([[makeQuery(id+"F0.imprint","IMPRINT",EDGE,{"derivedFrom":subQ0}),-1.0]])]});}
            var Q9;
            {var subQ0=sQuery(id+"F0.wireOp",EDGE,"E55.9.0.2");Q9=makeQuery(id+"F0.imprint","IMPRINT",FACE,{"disambiguationData":[TD([[makeQuery(id+"F0.imprint","IMPRINT",EDGE,{"derivedFrom":subQ0}),-1.0]])]});}
            var Q10;
            {var subQ0=sQuery(id+"F0.wireOp",EDGE,"E55.7.0.2");Q10=makeQuery(id+"F0.imprint","IMPRINT",FACE,{"disambiguationData":[TD([[makeQuery(id+"F0.imprint","IMPRINT",EDGE,{"derivedFrom":subQ0}),-1.0]])]});}
            var Q11;
            {var subQ0=sQuery(id+"F0.wireOp",EDGE,"E55.5.0.2");Q11=makeQuery(id+"F0.imprint","IMPRINT",FACE,{"disambiguationData":[TD([[makeQuery(id+"F0.imprint","IMPRINT",EDGE,{"derivedFrom":subQ0}),-1.0]])]});}
            var Q12;
            {var subQ0=sQuery(id+"F0.wireOp",EDGE,"E55.6.0.2");Q12=makeQuery(id+"F0.imprint","IMPRINT",FACE,{"disambiguationData":[TD([[makeQuery(id+"F0.imprint","IMPRINT",EDGE,{"derivedFrom":subQ0}),-1.0]])]});}
            var Q13;
            {var subQ0=sQuery(id+"F0.wireOp",EDGE,"E55.3.0.2");Q13=makeQuery(id+"F0.imprint","IMPRINT",FACE,{"disambiguationData":[TD([[makeQuery(id+"F0.imprint","IMPRINT",EDGE,{"derivedFrom":subQ0}),-1.0]])]});}
            var Q14;
            {var subQ0=sQuery(id+"F0.wireOp",EDGE,"E55.1.0.2");Q14=makeQuery(id+"F0.imprint","IMPRINT",FACE,{"disambiguationData":[TD([[makeQuery(id+"F0.imprint","IMPRINT",EDGE,{"derivedFrom":subQ0}),-1.0]])]});}
            var Q15;
            {var subQ0=sQuery(id+"F0.wireOp",EDGE,"E53");Q15=makeQuery(id+"F0.imprint","IMPRINT",FACE,{"disambiguationData":[TD([[makeQuery(id+"F0.imprint","IMPRINT",EDGE,{"derivedFrom":subQ0}),-1.0]])]});}
            var Q16;
            {var subQ0=sQuery(id+"F0.wireOp",EDGE,"E55.2.0.2");Q16=makeQuery(id+"F0.imprint","IMPRINT",FACE,{"disambiguationData":[TD([[makeQuery(id+"F0.imprint","IMPRINT",EDGE,{"derivedFrom":subQ0}),-1.0]])]});}
            var Q17;
            Q17=sQuery(id+"F0.wireOp",EDGE,"E28");
            revolve(context, id + "F3", {"surfaceOperationType" : NewSurfaceOperationType.NEW, "entities" : qUnion([Q0, Q1, Q2, Q3, Q4, Q5, Q6, Q7, Q8, Q9, Q10, Q11, Q12, Q13, Q14, Q15, Q16]), "axis" : qUnion([Q17]), "revolveType" : RevolveType.FULL});
        }
        {
            var Q0;
            Q0=makeQuery(id+"F0.imprint","IMPRINT",FACE,{"disambiguationData":[TD([[makeQuery(id+"F0.imprint","IMPRINT",EDGE,{"derivedFrom":sQuery(id+"F0.wireOp",EDGE,"E8")}),1.0]])]});
            var Q1;
            {var subQ0=sQuery(id+"F0.wireOp",EDGE,"E11");Q1=makeQuery(id+"F0.imprint","IMPRINT",FACE,{"disambiguationData":[TD([[makeQuery(id+"F0.imprint","IMPRINT",EDGE,{"derivedFrom":subQ0}),-1.0]])]});}
            var Q2;
            {var subQ1=sQuery(id+"F0.wireOp",EDGE,"E12");Q2=makeQuery(id+"F0.imprint","IMPRINT",FACE,{"disambiguationData":[TD([[makeQuery(id+"F0.imprint","IMPRINT",EDGE,{"derivedFrom":subQ1}),1.0]])]});}
            var Q3;
            {var subQ0=sQuery(id+"F0.wireOp",EDGE,"E27.12.0.2");Q3=makeQuery(id+"F0.imprint","IMPRINT",FACE,{"disambiguationData":[TD([[makeQuery(id+"F0.imprint","IMPRINT",EDGE,{"derivedFrom":subQ0}),-1.0]])]});}
            var Q4;
            {var subQ0=sQuery(id+"F0.wireOp",EDGE,"E27.13.0.2");Q4=makeQuery(id+"F0.imprint","IMPRINT",FACE,{"disambiguationData":[TD([[makeQuery(id+"F0.imprint","IMPRINT",EDGE,{"derivedFrom":subQ0}),-1.0]])]});}
            var Q5;
            {var subQ0=sQuery(id+"F0.wireOp",EDGE,"E27.5.0.2");Q5=makeQuery(id+"F0.imprint","IMPRINT",FACE,{"disambiguationData":[TD([[makeQuery(id+"F0.imprint","IMPRINT",EDGE,{"derivedFrom":subQ0}),-1.0]])]});}
            var Q6;
            {var subQ0=sQuery(id+"F0.wireOp",EDGE,"E27.11.0.2");Q6=makeQuery(id+"F0.imprint","IMPRINT",FACE,{"disambiguationData":[TD([[makeQuery(id+"F0.imprint","IMPRINT",EDGE,{"derivedFrom":subQ0}),-1.0]])]});}
            var Q7;
            {var subQ0=sQuery(id+"F0.wireOp",EDGE,"E27.9.0.2");Q7=makeQuery(id+"F0.imprint","IMPRINT",FACE,{"disambiguationData":[TD([[makeQuery(id+"F0.imprint","IMPRINT",EDGE,{"derivedFrom":subQ0}),-1.0]])]});}
            var Q8;
            {var subQ0=sQuery(id+"F0.wireOp",EDGE,"E25");Q8=makeQuery(id+"F0.imprint","IMPRINT",FACE,{"disambiguationData":[TD([[makeQuery(id+"F0.imprint","IMPRINT",EDGE,{"derivedFrom":subQ0}),-1.0]])]});}
            var Q9;
            {var subQ0=sQuery(id+"F0.wireOp",EDGE,"E27.7.0.2");Q9=makeQuery(id+"F0.imprint","IMPRINT",FACE,{"disambiguationData":[TD([[makeQuery(id+"F0.imprint","IMPRINT",EDGE,{"derivedFrom":subQ0}),-1.0]])]});}
            var Q10;
            {var subQ0=sQuery(id+"F0.wireOp",EDGE,"E27.3.0.2");Q10=makeQuery(id+"F0.imprint","IMPRINT",FACE,{"disambiguationData":[TD([[makeQuery(id+"F0.imprint","IMPRINT",EDGE,{"derivedFrom":subQ0}),-1.0]])]});}
            var Q11;
            {var subQ0=sQuery(id+"F0.wireOp",EDGE,"E27.1.0.2");Q11=makeQuery(id+"F0.imprint","IMPRINT",FACE,{"disambiguationData":[TD([[makeQuery(id+"F0.imprint","IMPRINT",EDGE,{"derivedFrom":subQ0}),-1.0]])]});}
            var Q12;
            {var subQ0=sQuery(id+"F0.wireOp",EDGE,"E27.4.0.2");Q12=makeQuery(id+"F0.imprint","IMPRINT",FACE,{"disambiguationData":[TD([[makeQuery(id+"F0.imprint","IMPRINT",EDGE,{"derivedFrom":subQ0}),-1.0]])]});}
            var Q13;
            {var subQ0=sQuery(id+"F0.wireOp",EDGE,"E27.8.0.2");Q13=makeQuery(id+"F0.imprint","IMPRINT",FACE,{"disambiguationData":[TD([[makeQuery(id+"F0.imprint","IMPRINT",EDGE,{"derivedFrom":subQ0}),-1.0]])]});}
            var Q14;
            {var subQ0=sQuery(id+"F0.wireOp",EDGE,"E27.6.0.2");Q14=makeQuery(id+"F0.imprint","IMPRINT",FACE,{"disambiguationData":[TD([[makeQuery(id+"F0.imprint","IMPRINT",EDGE,{"derivedFrom":subQ0}),-1.0]])]});}
            var Q15;
            {var subQ0=sQuery(id+"F0.wireOp",EDGE,"E27.10.0.2");Q15=makeQuery(id+"F0.imprint","IMPRINT",FACE,{"disambiguationData":[TD([[makeQuery(id+"F0.imprint","IMPRINT",EDGE,{"derivedFrom":subQ0}),-1.0]])]});}
            var Q16;
            {var subQ0=sQuery(id+"F0.wireOp",EDGE,"E27.2.0.2");Q16=makeQuery(id+"F0.imprint","IMPRINT",FACE,{"disambiguationData":[TD([[makeQuery(id+"F0.imprint","IMPRINT",EDGE,{"derivedFrom":subQ0}),-1.0]])]});}
            var Q17;
            Q17=sQuery(id+"F0.wireOp",EDGE,"E0");
            revolve(context, id + "F4", {"surfaceOperationType" : NewSurfaceOperationType.NEW, "entities" : qUnion([Q0, Q1, Q2, Q3, Q4, Q5, Q6, Q7, Q8, Q9, Q10, Q11, Q12, Q13, Q14, Q15, Q16]), "axis" : qUnion([Q17]), "revolveType" : RevolveType.FULL});
        }
        {
            var Q0;
            Q0=makeQuery(id+"F3.opRevolve","SWEPT_FACE",FACE,{"disambiguationData":[OSD([sQuery(id+"F0.wireOp",EDGE,"E37"),sQuery(id+"F0.wireOp",EDGE,"E39")])]});
            var sketch = newSketch(context, id + "F5", { "sketchPlane" : qUnion([Q0])});
            skCircle(sketch, "E128.0", {"center": v(0, -29.37) * mm, "radius": 10 * mm});
            skCircle(sketch, "E129", {"center": v(0, -29.37) * mm, "radius": 65 * mm});
            skSolve(sketch);
        }
        {
            var Q0;
            Q0 = qSketchRegion(id + "F5", true);
            extrude(context, id + "F6", {"entities" : qUnion([Q0]), "operationType" : NewBodyOperationType.REMOVE, "oppositeDirection" : true, "depth" : 30 * mm, "offsetDistance" : 25 * mm});
        }
        {
            var Q0;
            Q0=makeQuery(id+"F3.opRevolve","SWEPT_FACE",FACE,{"disambiguationData":[OSD([sQuery(id+"F0.wireOp",EDGE,"E45")])]});
            var sketch = newSketch(context, id + "F7", { "sketchPlane" : qUnion([Q0])});
            skLineSegment(sketch, "E130", {"start": v(0, 27.63) * mm, "end": v(0, -86.37) * mm, "construction": true});
            skLineSegment(sketch, "E131", {"start": v(-57, -29.37) * mm, "end": v(57, -29.37) * mm, "construction": true});
            skPoint(sketch, "E131.startSnap0", {"position": v(0, -29.37) * mm});
            skCircle(sketch, "E132", {"center": v(0, -29.37) * mm, "radius": 52.5 * mm});
            skCircle(sketch, "E133", {"center": v(0, -29.37) * mm, "radius": 31.5 * mm});
            skLineSegment(sketch, "E134", {"start": v(-19.01, 14.05) * mm, "end": v(-13.83, 4.51) * mm});
            skArc(sketch, "E135", {"start": v(-16.47, 20.48) * mm, "mid": v(-19.25, 17.86) * mm, "end": v(-19.01, 14.05) * mm});
            skArc(sketch, "E136", {"start": v(-13.83, 4.51) * mm, "mid": v(-10.88, 1.78) * mm, "end": v(-6.89, 1.36) * mm});
            skPoint(sketch, "E137.orphan", {"position": v(-11.37, 0) * mm});
            skLineSegment(sketch, "E138.MirrorCS", {"start": v(19.01, 14.05) * mm, "end": v(13.83, 4.51) * mm});
            skArc(sketch, "E139.MirrorCS", {"start": v(16.47, 20.48) * mm, "mid": v(19.25, 17.86) * mm, "end": v(19.01, 14.05) * mm});
            skArc(sketch, "E140.MirrorCS", {"start": v(13.83, 4.51) * mm, "mid": v(10.88, 1.78) * mm, "end": v(6.89, 1.36) * mm});
            skLineSegment(sketch, "E141.1.0", {"start": v(-47.17, -34.03) * mm, "end": v(-36.5, -32.05) * mm});
            skArc(sketch, "E141.1.1", {"start": v(-52.5, -29.62) * mm, "mid": v(-50.87, -33.07) * mm, "end": v(-47.17, -34.03) * mm});
            skArc(sketch, "E141.1.2", {"start": v(-36.5, -32.05) * mm, "mid": v(-32.98, -30.1) * mm, "end": v(-31.35, -26.42) * mm});
            skArc(sketch, "E141.1.3", {"start": v(-27.95, -5.75) * mm, "mid": v(-26.25, -9.4) * mm, "end": v(-27.1, -13.32) * mm});
            skLineSegment(sketch, "E141.1.4", {"start": v(-35.42, 2.14) * mm, "end": v(-27.95, -5.75) * mm});
            skArc(sketch, "E141.1.5", {"start": v(-42.32, 1.7) * mm, "mid": v(-38.97, 3.53) * mm, "end": v(-35.42, 2.14) * mm});
            skLineSegment(sketch, "E141.2.0", {"start": v(-10.14, -75.67) * mm, "end": v(-8.73, -64.9) * mm});
            skArc(sketch, "E141.2.1", {"start": v(-15.98, -79.38) * mm, "mid": v(-12.2, -78.89) * mm, "end": v(-10.14, -75.67) * mm});
            skArc(sketch, "E141.2.2", {"start": v(-8.73, -64.9) * mm, "mid": v(-9.5, -60.96) * mm, "end": v(-12.5, -58.27) * mm});
            skArc(sketch, "E141.2.3", {"start": v(-31.1, -48.65) * mm, "mid": v(-27.1, -48.16) * mm, "end": v(-23.63, -50.18) * mm});
            skLineSegment(sketch, "E141.2.4", {"start": v(-40.9, -53.32) * mm, "end": v(-31.1, -48.65) * mm});
            skArc(sketch, "E141.2.5", {"start": v(-42.63, -60.01) * mm, "mid": v(-43.33, -56.26) * mm, "end": v(-40.9, -53.32) * mm});
            skLineSegment(sketch, "E141.3.0", {"start": v(40.9, -53.32) * mm, "end": v(31.1, -48.65) * mm});
            skArc(sketch, "E141.3.1", {"start": v(42.63, -60.01) * mm, "mid": v(43.33, -56.26) * mm, "end": v(40.9, -53.32) * mm});
            skArc(sketch, "E141.3.2", {"start": v(31.1, -48.65) * mm, "mid": v(27.1, -48.16) * mm, "end": v(23.63, -50.18) * mm});
            skArc(sketch, "E141.3.3", {"start": v(8.73, -64.9) * mm, "mid": v(9.5, -60.96) * mm, "end": v(12.5, -58.27) * mm});
            skLineSegment(sketch, "E141.3.4", {"start": v(10.14, -75.67) * mm, "end": v(8.73, -64.9) * mm});
            skArc(sketch, "E141.3.5", {"start": v(15.98, -79.38) * mm, "mid": v(12.2, -78.89) * mm, "end": v(10.14, -75.67) * mm});
            skLineSegment(sketch, "E141.4.0", {"start": v(35.42, 2.14) * mm, "end": v(27.95, -5.75) * mm});
            skArc(sketch, "E141.4.1", {"start": v(42.32, 1.7) * mm, "mid": v(38.97, 3.53) * mm, "end": v(35.42, 2.14) * mm});
            skArc(sketch, "E141.4.2", {"start": v(27.95, -5.75) * mm, "mid": v(26.25, -9.4) * mm, "end": v(27.1, -13.32) * mm});
            skArc(sketch, "E141.4.3", {"start": v(36.5, -32.05) * mm, "mid": v(32.98, -30.1) * mm, "end": v(31.35, -26.42) * mm});
            skLineSegment(sketch, "E141.4.4", {"start": v(47.17, -34.03) * mm, "end": v(36.5, -32.05) * mm});
            skArc(sketch, "E141.4.5", {"start": v(52.5, -29.62) * mm, "mid": v(50.87, -33.07) * mm, "end": v(47.17, -34.03) * mm});
            skSolve(sketch);
        }
        {
            var Q0;
            Q0=makeQuery(id+"F7.imprint","IMPRINT",FACE,{"disambiguationData":[TD([[makeQuery(id+"F7.imprint","IMPRINT",EDGE,{"derivedFrom":sQuery(id+"F7.wireOp",EDGE,"E134")}),1.0]])]});
            var Q1;
            Q1=makeQuery(id+"F7.imprint","IMPRINT",FACE,{"disambiguationData":[TD([[makeQuery(id+"F7.imprint","IMPRINT",EDGE,{"derivedFrom":sQuery(id+"F7.wireOp",EDGE,"E141.4.0")}),1.0]])]});
            var Q2;
            Q2=makeQuery(id+"F7.imprint","IMPRINT",FACE,{"disambiguationData":[TD([[makeQuery(id+"F7.imprint","IMPRINT",EDGE,{"derivedFrom":sQuery(id+"F7.wireOp",EDGE,"E141.3.0")}),1.0]])]});
            var Q3;
            Q3=makeQuery(id+"F7.imprint","IMPRINT",FACE,{"disambiguationData":[TD([[makeQuery(id+"F7.imprint","IMPRINT",EDGE,{"derivedFrom":sQuery(id+"F7.wireOp",EDGE,"E141.2.0")}),1.0]])]});
            var Q4;
            Q4=makeQuery(id+"F7.imprint","IMPRINT",FACE,{"disambiguationData":[TD([[makeQuery(id+"F7.imprint","IMPRINT",EDGE,{"derivedFrom":sQuery(id+"F7.wireOp",EDGE,"E141.1.0")}),1.0]])]});
            extrude(context, id + "F8", {"entities" : qUnion([Q0, Q1, Q2, Q3, Q4]), "operationType" : NewBodyOperationType.REMOVE, "oppositeDirection" : true, "depth" : 36.5 * mm, "offsetDistance" : 25 * mm, "hasDraft" : true, "draftAngle" : 20 * degree, "draftPullDirection" : true});
        }
        {
            var Q0;
            Q0=makeQuery(id+"F2.opRevolve","SWEPT_FACE",FACE,{"disambiguationData":[OSD([sQuery(id+"F0.wireOp",EDGE,"E65"),sQuery(id+"F0.wireOp",EDGE,"E67")])]});
            var sketch = newSketch(context, id + "F9", { "sketchPlane" : qUnion([Q0])});
            skCircle(sketch, "E142", {"center": v(0, 0) * mm, "radius": 42.5 * mm});
            skSolve(sketch);
        }
        {
            var Q0;
            Q0 = qSketchRegion(id + "F9", true);
            extrude(context, id + "F10", {"entities" : qUnion([Q0]), "operationType" : NewBodyOperationType.REMOVE, "oppositeDirection" : true, "depth" : 32.3 * mm, "offsetDistance" : 25 * mm});
        }
        {
            var Q0;
            Q0=makeQuery(id+"F10.boolean.opBoolean","COPY",FACE,{"derivedFrom":makeQuery(id+"F10.opExtrude","CAP_FACE",FACE,{"disambiguationData":[OSD([sQuery(id+"F9.wireOp",EDGE,"E142")])],"isStart":false})});
            var sketch = newSketch(context, id + "F11", { "sketchPlane" : qUnion([Q0])});
            skCircle(sketch, "E143", {"center": v(0, 0) * mm, "radius": 20 * mm});
            skCircle(sketch, "E144.0", {"center": v(0, 0) * mm, "radius": 10 * mm});
            skSolve(sketch);
        }
        {
            var Q0;
            Q0 = qSketchRegion(id + "F11", true);
            extrude(context, id + "F12", {"entities" : qUnion([Q0]), "operationType" : NewBodyOperationType.ADD, "depth" : 25 * mm, "offsetDistance" : 25 * mm});
        }
        {
            var Q0;
            Q0=makeQuery(id+"F10.boolean.opBoolean","COPY",FACE,{"derivedFrom":makeQuery(id+"F10.opExtrude","CAP_FACE",FACE,{"disambiguationData":[OSD([sQuery(id+"F9.wireOp",EDGE,"E142")])],"isStart":false})});
            var sketch = newSketch(context, id + "F13", { "sketchPlane" : qUnion([Q0])});
            skLineSegment(sketch, "E145", {"start": v(0, 42.5) * mm, "end": v(0, -42.5) * mm, "construction": true});
            skLineSegment(sketch, "E146", {"start": v(-42.5, 0) * mm, "end": v(42.5, 0) * mm, "construction": true});
            skLineSegment(sketch, "E147", {"start": v(-1, 42.49) * mm, "end": v(-0.37, 20) * mm});
            skLineSegment(sketch, "E148.MirrorCS", {"start": v(1, 42.49) * mm, "end": v(0.38, 20) * mm});
            skSolve(sketch);
        }
        {
            var Q0;
            {var subQ0=sQuery(id+"F13.wireOp",EDGE,"E147");Q0=makeQuery(id+"F13.imprint","IMPRINT",FACE,{"disambiguationData":[TD([[makeQuery(id+"F13.imprint","IMPRINT",EDGE,{"derivedFrom":subQ0}),1.0]])]});}
            var Q1;
            Q1=makeQuery(id+"F12.opExtrude","CAP_FACE",FACE,{"disambiguationData":[OSD([sQuery(id+"F11.wireOp",EDGE,"E143"),sQuery(id+"F11.wireOp",EDGE,"E144.0")])],"isStart":false});
            var Q2;
            Q2=makeQuery(id+"F2.opRevolve","SWEPT_BODY",BODY,{"disambiguationData":[OSD([sQuery(id+"F0.wireOp",EDGE,"E64"),sQuery(id+"F0.wireOp",EDGE,"E65"),sQuery(id+"F0.wireOp",EDGE,"E67"),sQuery(id+"F0.wireOp",EDGE,"E68"),sQuery(id+"F0.wireOp",EDGE,"E71"),sQuery(id+"F0.wireOp",EDGE,"E73"),sQuery(id+"F0.wireOp",EDGE,"E74"),sQuery(id+"F0.wireOp",EDGE,"E72"),sQuery(id+"F0.wireOp",EDGE,"E75"),sQuery(id+"F0.wireOp",EDGE,"E76.filletArc"),sQuery(id+"F0.wireOp",EDGE,"E77.filletArc"),sQuery(id+"F0.wireOp",EDGE,"E81"),sQuery(id+"F0.wireOp",EDGE,"E84.14.0.3"),sQuery(id+"F0.wireOp",EDGE,"E85")])]});
            extrude(context, id + "F14", {"entities" : qUnion([Q0]), "operationType" : NewBodyOperationType.ADD, "endBound" : BoundingType.UP_TO_SURFACE, "depth" : 25 * mm, "endBoundEntityFace" : qUnion([Q1]), "endBoundEntityBody" : qUnion([Q2]), "offsetDistance" : 25 * mm});
        }
        {
            var Q0;
            {var subQ0=sQuery(id+"F13.wireOp",EDGE,"E148.MirrorCS");var subQ1=sQuery(id+"F13.wireOp",EDGE,"E147");var subQ2=sQuery(id+"F11.wireOp",EDGE,"E143");var subQ3=sQuery(id+"F9.wireOp",EDGE,"E142");Q0=makeQuery(id+"FyYUAefgu6xEfva_4.49.F14.boolean.opBoolean","MERGE",FACE,{"derivedFrom":[makeQuery(id+"FyYUAefgu6xEfva_4.48.F14.boolean.opBoolean","MERGE",FACE,{"derivedFrom":[makeQuery(id+"FyYUAefgu6xEfva_4.47.F14.boolean.opBoolean","MERGE",FACE,{"derivedFrom":[makeQuery(id+"FyYUAefgu6xEfva_4.46.F14.boolean.opBoolean","MERGE",FACE,{"derivedFrom":[makeQuery(id+"FyYUAefgu6xEfva_4.45.F14.boolean.opBoolean","MERGE",FACE,{"derivedFrom":[makeQuery(id+"FyYUAefgu6xEfva_4.44.F14.boolean.opBoolean","MERGE",FACE,{"derivedFrom":[makeQuery(id+"FyYUAefgu6xEfva_4.43.F14.boolean.opBoolean","MERGE",FACE,{"derivedFrom":[makeQuery(id+"FyYUAefgu6xEfva_4.42.F14.boolean.opBoolean","MERGE",FACE,{"derivedFrom":[makeQuery(id+"FyYUAefgu6xEfva_4.41.F14.boolean.opBoolean","MERGE",FACE,{"derivedFrom":[makeQuery(id+"FyYUAefgu6xEfva_4.40.F14.boolean.opBoolean","MERGE",FACE,{"derivedFrom":[makeQuery(id+"FyYUAefgu6xEfva_4.39.F14.boolean.opBoolean","MERGE",FACE,{"derivedFrom":[makeQuery(id+"FyYUAefgu6xEfva_4.38.F14.boolean.opBoolean","MERGE",FACE,{"derivedFrom":[makeQuery(id+"FyYUAefgu6xEfva_4.37.F14.boolean.opBoolean","MERGE",FACE,{"derivedFrom":[makeQuery(id+"FyYUAefgu6xEfva_4.36.F14.boolean.opBoolean","MERGE",FACE,{"derivedFrom":[makeQuery(id+"FyYUAefgu6xEfva_4.35.F14.boolean.opBoolean","MERGE",FACE,{"derivedFrom":[makeQuery(id+"FyYUAefgu6xEfva_4.34.F14.boolean.opBoolean","MERGE",FACE,{"derivedFrom":[makeQuery(id+"FyYUAefgu6xEfva_4.33.F14.boolean.opBoolean","MERGE",FACE,{"derivedFrom":[makeQuery(id+"FyYUAefgu6xEfva_4.32.F14.boolean.opBoolean","MERGE",FACE,{"derivedFrom":[makeQuery(id+"FyYUAefgu6xEfva_4.31.F14.boolean.opBoolean","MERGE",FACE,{"derivedFrom":[makeQuery(id+"FyYUAefgu6xEfva_4.30.F14.boolean.opBoolean","MERGE",FACE,{"derivedFrom":[makeQuery(id+"FyYUAefgu6xEfva_4.29.F14.boolean.opBoolean","MERGE",FACE,{"derivedFrom":[makeQuery(id+"FyYUAefgu6xEfva_4.28.F14.boolean.opBoolean","MERGE",FACE,{"derivedFrom":[makeQuery(id+"FyYUAefgu6xEfva_4.27.F14.boolean.opBoolean","MERGE",FACE,{"derivedFrom":[makeQuery(id+"FyYUAefgu6xEfva_4.26.F14.boolean.opBoolean","MERGE",FACE,{"derivedFrom":[makeQuery(id+"FyYUAefgu6xEfva_4.25.F14.boolean.opBoolean","MERGE",FACE,{"derivedFrom":[makeQuery(id+"FyYUAefgu6xEfva_4.24.F14.boolean.opBoolean","MERGE",FACE,{"derivedFrom":[makeQuery(id+"FyYUAefgu6xEfva_4.23.F14.boolean.opBoolean","MERGE",FACE,{"derivedFrom":[makeQuery(id+"FyYUAefgu6xEfva_4.22.F14.boolean.opBoolean","MERGE",FACE,{"derivedFrom":[makeQuery(id+"FyYUAefgu6xEfva_4.21.F14.boolean.opBoolean","MERGE",FACE,{"derivedFrom":[makeQuery(id+"FyYUAefgu6xEfva_4.20.F14.boolean.opBoolean","MERGE",FACE,{"derivedFrom":[makeQuery(id+"FyYUAefgu6xEfva_4.19.F14.boolean.opBoolean","MERGE",FACE,{"derivedFrom":[makeQuery(id+"FyYUAefgu6xEfva_4.18.F14.boolean.opBoolean","MERGE",FACE,{"derivedFrom":[makeQuery(id+"FyYUAefgu6xEfva_4.17.F14.boolean.opBoolean","MERGE",FACE,{"derivedFrom":[makeQuery(id+"FyYUAefgu6xEfva_4.16.F14.boolean.opBoolean","MERGE",FACE,{"derivedFrom":[makeQuery(id+"FyYUAefgu6xEfva_4.15.F14.boolean.opBoolean","MERGE",FACE,{"derivedFrom":[makeQuery(id+"FyYUAefgu6xEfva_4.14.F14.boolean.opBoolean","MERGE",FACE,{"derivedFrom":[makeQuery(id+"FyYUAefgu6xEfva_4.13.F14.boolean.opBoolean","MERGE",FACE,{"derivedFrom":[makeQuery(id+"FyYUAefgu6xEfva_4.12.F14.boolean.opBoolean","MERGE",FACE,{"derivedFrom":[makeQuery(id+"FyYUAefgu6xEfva_4.11.F14.boolean.opBoolean","MERGE",FACE,{"derivedFrom":[makeQuery(id+"FyYUAefgu6xEfva_4.10.F14.boolean.opBoolean","MERGE",FACE,{"derivedFrom":[makeQuery(id+"FyYUAefgu6xEfva_4.9.F14.boolean.opBoolean","MERGE",FACE,{"derivedFrom":[makeQuery(id+"FyYUAefgu6xEfva_4.8.F14.boolean.opBoolean","MERGE",FACE,{"derivedFrom":[makeQuery(id+"FyYUAefgu6xEfva_4.7.F14.boolean.opBoolean","MERGE",FACE,{"derivedFrom":[makeQuery(id+"FyYUAefgu6xEfva_4.6.F14.boolean.opBoolean","MERGE",FACE,{"derivedFrom":[makeQuery(id+"FyYUAefgu6xEfva_4.5.F14.boolean.opBoolean","MERGE",FACE,{"derivedFrom":[makeQuery(id+"FyYUAefgu6xEfva_4.4.F14.boolean.opBoolean","MERGE",FACE,{"derivedFrom":[makeQuery(id+"FyYUAefgu6xEfva_4.3.F14.boolean.opBoolean","MERGE",FACE,{"derivedFrom":[makeQuery(id+"FyYUAefgu6xEfva_4.2.F14.boolean.opBoolean","MERGE",FACE,{"derivedFrom":[makeQuery(id+"FyYUAefgu6xEfva_4.1.F14.boolean.opBoolean","MERGE",FACE,{"derivedFrom":[makeQuery(id+"F14.boolean.opBoolean","MERGE",FACE,{"derivedFrom":[makeQuery(id+"F12.opExtrude","CAP_FACE",FACE,{"disambiguationData":[OSD([subQ2,sQuery(id+"F11.wireOp",EDGE,"E144.0")])],"isStart":false}),makeQuery(id+"F14.opExtrude","CAP_FACE",FACE,{"disambiguationData":[OSD([subQ3,subQ2,subQ1,subQ0])],"isStart":false})]}),makeQuery(id+"FyYUAefgu6xEfva_4.1.F14.opExtrude","CAP_FACE",FACE,{"disambiguationData":[OSD([subQ3,subQ2,subQ1,subQ0])],"isStart":false})]}),makeQuery(id+"FyYUAefgu6xEfva_4.2.F14.opExtrude","CAP_FACE",FACE,{"disambiguationData":[OSD([subQ3,subQ2,subQ1,subQ0])],"isStart":false})]}),makeQuery(id+"FyYUAefgu6xEfva_4.3.F14.opExtrude","CAP_FACE",FACE,{"disambiguationData":[OSD([subQ3,subQ2,subQ1,subQ0])],"isStart":false})]}),makeQuery(id+"FyYUAefgu6xEfva_4.4.F14.opExtrude","CAP_FACE",FACE,{"disambiguationData":[OSD([subQ3,subQ2,subQ1,subQ0])],"isStart":false})]}),makeQuery(id+"FyYUAefgu6xEfva_4.5.F14.opExtrude","CAP_FACE",FACE,{"disambiguationData":[OSD([subQ3,subQ2,subQ1,subQ0])],"isStart":false})]}),makeQuery(id+"FyYUAefgu6xEfva_4.6.F14.opExtrude","CAP_FACE",FACE,{"disambiguationData":[OSD([subQ3,subQ2,subQ1,subQ0])],"isStart":false})]}),makeQuery(id+"FyYUAefgu6xEfva_4.7.F14.opExtrude","CAP_FACE",FACE,{"disambiguationData":[OSD([subQ3,subQ2,subQ1,subQ0])],"isStart":false})]}),makeQuery(id+"FyYUAefgu6xEfva_4.8.F14.opExtrude","CAP_FACE",FACE,{"disambiguationData":[OSD([subQ3,subQ2,subQ1,subQ0])],"isStart":false})]}),makeQuery(id+"FyYUAefgu6xEfva_4.9.F14.opExtrude","CAP_FACE",FACE,{"disambiguationData":[OSD([subQ3,subQ2,subQ1,subQ0])],"isStart":false})]}),makeQuery(id+"FyYUAefgu6xEfva_4.10.F14.opExtrude","CAP_FACE",FACE,{"disambiguationData":[OSD([subQ3,subQ2,subQ1,subQ0])],"isStart":false})]}),makeQuery(id+"FyYUAefgu6xEfva_4.11.F14.opExtrude","CAP_FACE",FACE,{"disambiguationData":[OSD([subQ3,subQ2,subQ1,subQ0])],"isStart":false})]}),makeQuery(id+"FyYUAefgu6xEfva_4.12.F14.opExtrude","CAP_FACE",FACE,{"disambiguationData":[OSD([subQ3,subQ2,subQ1,subQ0])],"isStart":false})]}),makeQuery(id+"FyYUAefgu6xEfva_4.13.F14.opExtrude","CAP_FACE",FACE,{"disambiguationData":[OSD([subQ3,subQ2,subQ1,subQ0])],"isStart":false})]}),makeQuery(id+"FyYUAefgu6xEfva_4.14.F14.opExtrude","CAP_FACE",FACE,{"disambiguationData":[OSD([subQ3,subQ2,subQ1,subQ0])],"isStart":false})]}),makeQuery(id+"FyYUAefgu6xEfva_4.15.F14.opExtrude","CAP_FACE",FACE,{"disambiguationData":[OSD([subQ3,subQ2,subQ1,subQ0])],"isStart":false})]}),makeQuery(id+"FyYUAefgu6xEfva_4.16.F14.opExtrude","CAP_FACE",FACE,{"disambiguationData":[OSD([subQ3,subQ2,subQ1,subQ0])],"isStart":false})]}),makeQuery(id+"FyYUAefgu6xEfva_4.17.F14.opExtrude","CAP_FACE",FACE,{"disambiguationData":[OSD([subQ3,subQ2,subQ1,subQ0])],"isStart":false})]}),makeQuery(id+"FyYUAefgu6xEfva_4.18.F14.opExtrude","CAP_FACE",FACE,{"disambiguationData":[OSD([subQ3,subQ2,subQ1,subQ0])],"isStart":false})]}),makeQuery(id+"FyYUAefgu6xEfva_4.19.F14.opExtrude","CAP_FACE",FACE,{"disambiguationData":[OSD([subQ3,subQ2,subQ1,subQ0])],"isStart":false})]}),makeQuery(id+"FyYUAefgu6xEfva_4.20.F14.opExtrude","CAP_FACE",FACE,{"disambiguationData":[OSD([subQ3,subQ2,subQ1,subQ0])],"isStart":false})]}),makeQuery(id+"FyYUAefgu6xEfva_4.21.F14.opExtrude","CAP_FACE",FACE,{"disambiguationData":[OSD([subQ3,subQ2,subQ1,subQ0])],"isStart":false})]}),makeQuery(id+"FyYUAefgu6xEfva_4.22.F14.opExtrude","CAP_FACE",FACE,{"disambiguationData":[OSD([subQ3,subQ2,subQ1,subQ0])],"isStart":false})]}),makeQuery(id+"FyYUAefgu6xEfva_4.23.F14.opExtrude","CAP_FACE",FACE,{"disambiguationData":[OSD([subQ3,subQ2,subQ1,subQ0])],"isStart":false})]}),makeQuery(id+"FyYUAefgu6xEfva_4.24.F14.opExtrude","CAP_FACE",FACE,{"disambiguationData":[OSD([subQ3,subQ2,subQ1,subQ0])],"isStart":false})]}),makeQuery(id+"FyYUAefgu6xEfva_4.25.F14.opExtrude","CAP_FACE",FACE,{"disambiguationData":[OSD([subQ3,subQ2,subQ1,subQ0])],"isStart":false})]}),makeQuery(id+"FyYUAefgu6xEfva_4.26.F14.opExtrude","CAP_FACE",FACE,{"disambiguationData":[OSD([subQ3,subQ2,subQ1,subQ0])],"isStart":false})]}),makeQuery(id+"FyYUAefgu6xEfva_4.27.F14.opExtrude","CAP_FACE",FACE,{"disambiguationData":[OSD([subQ3,subQ2,subQ1,subQ0])],"isStart":false})]}),makeQuery(id+"FyYUAefgu6xEfva_4.28.F14.opExtrude","CAP_FACE",FACE,{"disambiguationData":[OSD([subQ3,subQ2,subQ1,subQ0])],"isStart":false})]}),makeQuery(id+"FyYUAefgu6xEfva_4.29.F14.opExtrude","CAP_FACE",FACE,{"disambiguationData":[OSD([subQ3,subQ2,subQ1,subQ0])],"isStart":false})]}),makeQuery(id+"FyYUAefgu6xEfva_4.30.F14.opExtrude","CAP_FACE",FACE,{"disambiguationData":[OSD([subQ3,subQ2,subQ1,subQ0])],"isStart":false})]}),makeQuery(id+"FyYUAefgu6xEfva_4.31.F14.opExtrude","CAP_FACE",FACE,{"disambiguationData":[OSD([subQ3,subQ2,subQ1,subQ0])],"isStart":false})]}),makeQuery(id+"FyYUAefgu6xEfva_4.32.F14.opExtrude","CAP_FACE",FACE,{"disambiguationData":[OSD([subQ3,subQ2,subQ1,subQ0])],"isStart":false})]}),makeQuery(id+"FyYUAefgu6xEfva_4.33.F14.opExtrude","CAP_FACE",FACE,{"disambiguationData":[OSD([subQ3,subQ2,subQ1,subQ0])],"isStart":false})]}),makeQuery(id+"FyYUAefgu6xEfva_4.34.F14.opExtrude","CAP_FACE",FACE,{"disambiguationData":[OSD([subQ3,subQ2,subQ1,subQ0])],"isStart":false})]}),makeQuery(id+"FyYUAefgu6xEfva_4.35.F14.opExtrude","CAP_FACE",FACE,{"disambiguationData":[OSD([subQ3,subQ2,subQ1,subQ0])],"isStart":false})]}),makeQuery(id+"FyYUAefgu6xEfva_4.36.F14.opExtrude","CAP_FACE",FACE,{"disambiguationData":[OSD([subQ3,subQ2,subQ1,subQ0])],"isStart":false})]}),makeQuery(id+"FyYUAefgu6xEfva_4.37.F14.opExtrude","CAP_FACE",FACE,{"disambiguationData":[OSD([subQ3,subQ2,subQ1,subQ0])],"isStart":false})]}),makeQuery(id+"FyYUAefgu6xEfva_4.38.F14.opExtrude","CAP_FACE",FACE,{"disambiguationData":[OSD([subQ3,subQ2,subQ1,subQ0])],"isStart":false})]}),makeQuery(id+"FyYUAefgu6xEfva_4.39.F14.opExtrude","CAP_FACE",FACE,{"disambiguationData":[OSD([subQ3,subQ2,subQ1,subQ0])],"isStart":false})]}),makeQuery(id+"FyYUAefgu6xEfva_4.40.F14.opExtrude","CAP_FACE",FACE,{"disambiguationData":[OSD([subQ3,subQ2,subQ1,subQ0])],"isStart":false})]}),makeQuery(id+"FyYUAefgu6xEfva_4.41.F14.opExtrude","CAP_FACE",FACE,{"disambiguationData":[OSD([subQ3,subQ2,subQ1,subQ0])],"isStart":false})]}),makeQuery(id+"FyYUAefgu6xEfva_4.42.F14.opExtrude","CAP_FACE",FACE,{"disambiguationData":[OSD([subQ3,subQ2,subQ1,subQ0])],"isStart":false})]}),makeQuery(id+"FyYUAefgu6xEfva_4.43.F14.opExtrude","CAP_FACE",FACE,{"disambiguationData":[OSD([subQ3,subQ2,subQ1,subQ0])],"isStart":false})]}),makeQuery(id+"FyYUAefgu6xEfva_4.44.F14.opExtrude","CAP_FACE",FACE,{"disambiguationData":[OSD([subQ3,subQ2,subQ1,subQ0])],"isStart":false})]}),makeQuery(id+"FyYUAefgu6xEfva_4.45.F14.opExtrude","CAP_FACE",FACE,{"disambiguationData":[OSD([subQ3,subQ2,subQ1,subQ0])],"isStart":false})]}),makeQuery(id+"FyYUAefgu6xEfva_4.46.F14.opExtrude","CAP_FACE",FACE,{"disambiguationData":[OSD([subQ3,subQ2,subQ1,subQ0])],"isStart":false})]}),makeQuery(id+"FyYUAefgu6xEfva_4.47.F14.opExtrude","CAP_FACE",FACE,{"disambiguationData":[OSD([subQ3,subQ2,subQ1,subQ0])],"isStart":false})]}),makeQuery(id+"FyYUAefgu6xEfva_4.48.F14.opExtrude","CAP_FACE",FACE,{"disambiguationData":[OSD([subQ3,subQ2,subQ1,subQ0])],"isStart":false})]}),makeQuery(id+"FyYUAefgu6xEfva_4.49.F14.opExtrude","CAP_FACE",FACE,{"disambiguationData":[OSD([subQ3,subQ2,subQ1,subQ0])],"isStart":false})]});}
            var Q1;
            Q1=makeQuery(id+"FyYUAefgu6xEfva_4.47.F14.opExtrude","CAP_EDGE",EDGE,{"disambiguationData":[OSD([sQuery(id+"F13.wireOp",EDGE,"E148.MirrorCS")])],"isStart":true});
            var Q2;
            {var subQ1=sQuery(id+"F11.wireOp",EDGE,"E143");var subQ4=makeQuery(id+"F14.opExtrude","SWEPT_FACE",FACE,{"disambiguationData":[OSD([sQuery(id+"F13.wireOp",EDGE,"E147")])]});Q2=makeQuery(id+"FyYUAefgu6xEfva_4.49.F14.boolean.opBoolean","SPLIT",EDGE,{"disambiguationData":[TD([subQ4])],"derivedFrom":makeQuery(id+"FyYUAefgu6xEfva_4.48.F14.boolean.opBoolean","SPLIT",EDGE,{"disambiguationData":[TD([subQ4])],"derivedFrom":makeQuery(id+"FyYUAefgu6xEfva_4.47.F14.boolean.opBoolean","SPLIT",EDGE,{"disambiguationData":[TD([subQ4])],"derivedFrom":makeQuery(id+"FyYUAefgu6xEfva_4.46.F14.boolean.opBoolean","SPLIT",EDGE,{"disambiguationData":[TD([subQ4])],"derivedFrom":makeQuery(id+"FyYUAefgu6xEfva_4.45.F14.boolean.opBoolean","SPLIT",EDGE,{"disambiguationData":[TD([subQ4])],"derivedFrom":makeQuery(id+"FyYUAefgu6xEfva_4.44.F14.boolean.opBoolean","SPLIT",EDGE,{"disambiguationData":[TD([subQ4])],"derivedFrom":makeQuery(id+"FyYUAefgu6xEfva_4.43.F14.boolean.opBoolean","SPLIT",EDGE,{"disambiguationData":[TD([subQ4])],"derivedFrom":makeQuery(id+"FyYUAefgu6xEfva_4.42.F14.boolean.opBoolean","SPLIT",EDGE,{"disambiguationData":[TD([subQ4])],"derivedFrom":makeQuery(id+"FyYUAefgu6xEfva_4.41.F14.boolean.opBoolean","SPLIT",EDGE,{"disambiguationData":[TD([subQ4])],"derivedFrom":makeQuery(id+"FyYUAefgu6xEfva_4.40.F14.boolean.opBoolean","SPLIT",EDGE,{"disambiguationData":[TD([subQ4])],"derivedFrom":makeQuery(id+"FyYUAefgu6xEfva_4.39.F14.boolean.opBoolean","SPLIT",EDGE,{"disambiguationData":[TD([subQ4])],"derivedFrom":makeQuery(id+"FyYUAefgu6xEfva_4.38.F14.boolean.opBoolean","SPLIT",EDGE,{"disambiguationData":[TD([subQ4])],"derivedFrom":makeQuery(id+"FyYUAefgu6xEfva_4.37.F14.boolean.opBoolean","SPLIT",EDGE,{"disambiguationData":[TD([subQ4])],"derivedFrom":makeQuery(id+"FyYUAefgu6xEfva_4.36.F14.boolean.opBoolean","SPLIT",EDGE,{"disambiguationData":[TD([subQ4])],"derivedFrom":makeQuery(id+"FyYUAefgu6xEfva_4.35.F14.boolean.opBoolean","SPLIT",EDGE,{"disambiguationData":[TD([subQ4])],"derivedFrom":makeQuery(id+"FyYUAefgu6xEfva_4.34.F14.boolean.opBoolean","SPLIT",EDGE,{"disambiguationData":[TD([subQ4])],"derivedFrom":makeQuery(id+"FyYUAefgu6xEfva_4.33.F14.boolean.opBoolean","SPLIT",EDGE,{"disambiguationData":[TD([subQ4])],"derivedFrom":makeQuery(id+"FyYUAefgu6xEfva_4.32.F14.boolean.opBoolean","SPLIT",EDGE,{"disambiguationData":[TD([subQ4])],"derivedFrom":makeQuery(id+"FyYUAefgu6xEfva_4.31.F14.boolean.opBoolean","SPLIT",EDGE,{"disambiguationData":[TD([subQ4])],"derivedFrom":makeQuery(id+"FyYUAefgu6xEfva_4.30.F14.boolean.opBoolean","SPLIT",EDGE,{"disambiguationData":[TD([subQ4])],"derivedFrom":makeQuery(id+"FyYUAefgu6xEfva_4.29.F14.boolean.opBoolean","SPLIT",EDGE,{"disambiguationData":[TD([subQ4])],"derivedFrom":makeQuery(id+"FyYUAefgu6xEfva_4.28.F14.boolean.opBoolean","SPLIT",EDGE,{"disambiguationData":[TD([subQ4])],"derivedFrom":makeQuery(id+"FyYUAefgu6xEfva_4.27.F14.boolean.opBoolean","SPLIT",EDGE,{"disambiguationData":[TD([subQ4])],"derivedFrom":makeQuery(id+"FyYUAefgu6xEfva_4.26.F14.boolean.opBoolean","SPLIT",EDGE,{"disambiguationData":[TD([subQ4])],"derivedFrom":makeQuery(id+"FyYUAefgu6xEfva_4.25.F14.boolean.opBoolean","SPLIT",EDGE,{"disambiguationData":[TD([subQ4])],"derivedFrom":makeQuery(id+"FyYUAefgu6xEfva_4.24.F14.boolean.opBoolean","SPLIT",EDGE,{"disambiguationData":[TD([subQ4])],"derivedFrom":makeQuery(id+"FyYUAefgu6xEfva_4.23.F14.boolean.opBoolean","SPLIT",EDGE,{"disambiguationData":[TD([subQ4])],"derivedFrom":makeQuery(id+"FyYUAefgu6xEfva_4.22.F14.boolean.opBoolean","SPLIT",EDGE,{"disambiguationData":[TD([subQ4])],"derivedFrom":makeQuery(id+"FyYUAefgu6xEfva_4.21.F14.boolean.opBoolean","SPLIT",EDGE,{"disambiguationData":[TD([subQ4])],"derivedFrom":makeQuery(id+"FyYUAefgu6xEfva_4.20.F14.boolean.opBoolean","SPLIT",EDGE,{"disambiguationData":[TD([subQ4])],"derivedFrom":makeQuery(id+"FyYUAefgu6xEfva_4.19.F14.boolean.opBoolean","SPLIT",EDGE,{"disambiguationData":[TD([subQ4])],"derivedFrom":makeQuery(id+"FyYUAefgu6xEfva_4.18.F14.boolean.opBoolean","SPLIT",EDGE,{"disambiguationData":[TD([subQ4])],"derivedFrom":makeQuery(id+"FyYUAefgu6xEfva_4.17.F14.boolean.opBoolean","SPLIT",EDGE,{"disambiguationData":[TD([subQ4])],"derivedFrom":makeQuery(id+"FyYUAefgu6xEfva_4.16.F14.boolean.opBoolean","SPLIT",EDGE,{"disambiguationData":[TD([subQ4])],"derivedFrom":makeQuery(id+"FyYUAefgu6xEfva_4.15.F14.boolean.opBoolean","SPLIT",EDGE,{"disambiguationData":[TD([subQ4])],"derivedFrom":makeQuery(id+"FyYUAefgu6xEfva_4.14.F14.boolean.opBoolean","SPLIT",EDGE,{"disambiguationData":[TD([subQ4])],"derivedFrom":makeQuery(id+"FyYUAefgu6xEfva_4.13.F14.boolean.opBoolean","SPLIT",EDGE,{"disambiguationData":[TD([subQ4])],"derivedFrom":makeQuery(id+"FyYUAefgu6xEfva_4.12.F14.boolean.opBoolean","SPLIT",EDGE,{"disambiguationData":[TD([subQ4])],"derivedFrom":makeQuery(id+"FyYUAefgu6xEfva_4.11.F14.boolean.opBoolean","SPLIT",EDGE,{"disambiguationData":[TD([subQ4])],"derivedFrom":makeQuery(id+"FyYUAefgu6xEfva_4.10.F14.boolean.opBoolean","SPLIT",EDGE,{"disambiguationData":[TD([subQ4])],"derivedFrom":makeQuery(id+"FyYUAefgu6xEfva_4.9.F14.boolean.opBoolean","SPLIT",EDGE,{"disambiguationData":[TD([subQ4])],"derivedFrom":makeQuery(id+"FyYUAefgu6xEfva_4.8.F14.boolean.opBoolean","SPLIT",EDGE,{"disambiguationData":[TD([subQ4])],"derivedFrom":makeQuery(id+"FyYUAefgu6xEfva_4.7.F14.boolean.opBoolean","SPLIT",EDGE,{"disambiguationData":[TD([subQ4])],"derivedFrom":makeQuery(id+"FyYUAefgu6xEfva_4.6.F14.boolean.opBoolean","SPLIT",EDGE,{"disambiguationData":[TD([subQ4])],"derivedFrom":makeQuery(id+"FyYUAefgu6xEfva_4.5.F14.boolean.opBoolean","SPLIT",EDGE,{"disambiguationData":[TD([subQ4])],"derivedFrom":makeQuery(id+"FyYUAefgu6xEfva_4.4.F14.boolean.opBoolean","SPLIT",EDGE,{"disambiguationData":[TD([subQ4])],"derivedFrom":makeQuery(id+"FyYUAefgu6xEfva_4.3.F14.boolean.opBoolean","SPLIT",EDGE,{"disambiguationData":[TD([subQ4])],"derivedFrom":makeQuery(id+"FyYUAefgu6xEfva_4.2.F14.boolean.opBoolean","SPLIT",EDGE,{"disambiguationData":[TD([subQ4])],"derivedFrom":makeQuery(id+"FyYUAefgu6xEfva_4.1.F14.boolean.opBoolean","SPLIT",EDGE,{"disambiguationData":[TD([subQ4])],"derivedFrom":makeQuery(id+"F12.opExtrude","CAP_EDGE",EDGE,{"disambiguationData":[OSD([subQ1])],"isStart":true})})})})})})})})})})})})})})})})})})})})})})})})})})})})})})})})})})})})})})})})})})})})})})})})})});}
            var Q3;
            {var subQ0=sQuery(id+"F9.wireOp",EDGE,"E142");var subQ4=makeQuery(id+"F14.opExtrude","SWEPT_FACE",FACE,{"disambiguationData":[OSD([sQuery(id+"F13.wireOp",EDGE,"E147")])]});Q3=makeQuery(id+"FyYUAefgu6xEfva_4.49.F14.boolean.opBoolean","SPLIT",FACE,{"disambiguationData":[TD([subQ4])],"derivedFrom":makeQuery(id+"FyYUAefgu6xEfva_4.48.F14.boolean.opBoolean","SPLIT",FACE,{"disambiguationData":[TD([subQ4])],"derivedFrom":makeQuery(id+"FyYUAefgu6xEfva_4.47.F14.boolean.opBoolean","SPLIT",FACE,{"disambiguationData":[TD([subQ4])],"derivedFrom":makeQuery(id+"FyYUAefgu6xEfva_4.46.F14.boolean.opBoolean","SPLIT",FACE,{"disambiguationData":[TD([subQ4])],"derivedFrom":makeQuery(id+"FyYUAefgu6xEfva_4.45.F14.boolean.opBoolean","SPLIT",FACE,{"disambiguationData":[TD([subQ4])],"derivedFrom":makeQuery(id+"FyYUAefgu6xEfva_4.44.F14.boolean.opBoolean","SPLIT",FACE,{"disambiguationData":[TD([subQ4])],"derivedFrom":makeQuery(id+"FyYUAefgu6xEfva_4.43.F14.boolean.opBoolean","SPLIT",FACE,{"disambiguationData":[TD([subQ4])],"derivedFrom":makeQuery(id+"FyYUAefgu6xEfva_4.42.F14.boolean.opBoolean","SPLIT",FACE,{"disambiguationData":[TD([subQ4])],"derivedFrom":makeQuery(id+"FyYUAefgu6xEfva_4.41.F14.boolean.opBoolean","SPLIT",FACE,{"disambiguationData":[TD([subQ4])],"derivedFrom":makeQuery(id+"FyYUAefgu6xEfva_4.40.F14.boolean.opBoolean","SPLIT",FACE,{"disambiguationData":[TD([subQ4])],"derivedFrom":makeQuery(id+"FyYUAefgu6xEfva_4.39.F14.boolean.opBoolean","SPLIT",FACE,{"disambiguationData":[TD([subQ4])],"derivedFrom":makeQuery(id+"FyYUAefgu6xEfva_4.38.F14.boolean.opBoolean","SPLIT",FACE,{"disambiguationData":[TD([subQ4])],"derivedFrom":makeQuery(id+"FyYUAefgu6xEfva_4.37.F14.boolean.opBoolean","SPLIT",FACE,{"disambiguationData":[TD([subQ4])],"derivedFrom":makeQuery(id+"FyYUAefgu6xEfva_4.36.F14.boolean.opBoolean","SPLIT",FACE,{"disambiguationData":[TD([subQ4])],"derivedFrom":makeQuery(id+"FyYUAefgu6xEfva_4.35.F14.boolean.opBoolean","SPLIT",FACE,{"disambiguationData":[TD([subQ4])],"derivedFrom":makeQuery(id+"FyYUAefgu6xEfva_4.34.F14.boolean.opBoolean","SPLIT",FACE,{"disambiguationData":[TD([subQ4])],"derivedFrom":makeQuery(id+"FyYUAefgu6xEfva_4.33.F14.boolean.opBoolean","SPLIT",FACE,{"disambiguationData":[TD([subQ4])],"derivedFrom":makeQuery(id+"FyYUAefgu6xEfva_4.32.F14.boolean.opBoolean","SPLIT",FACE,{"disambiguationData":[TD([subQ4])],"derivedFrom":makeQuery(id+"FyYUAefgu6xEfva_4.31.F14.boolean.opBoolean","SPLIT",FACE,{"disambiguationData":[TD([subQ4])],"derivedFrom":makeQuery(id+"FyYUAefgu6xEfva_4.30.F14.boolean.opBoolean","SPLIT",FACE,{"disambiguationData":[TD([subQ4])],"derivedFrom":makeQuery(id+"FyYUAefgu6xEfva_4.29.F14.boolean.opBoolean","SPLIT",FACE,{"disambiguationData":[TD([subQ4])],"derivedFrom":makeQuery(id+"FyYUAefgu6xEfva_4.28.F14.boolean.opBoolean","SPLIT",FACE,{"disambiguationData":[TD([subQ4])],"derivedFrom":makeQuery(id+"FyYUAefgu6xEfva_4.27.F14.boolean.opBoolean","SPLIT",FACE,{"disambiguationData":[TD([subQ4])],"derivedFrom":makeQuery(id+"FyYUAefgu6xEfva_4.26.F14.boolean.opBoolean","SPLIT",FACE,{"disambiguationData":[TD([subQ4])],"derivedFrom":makeQuery(id+"FyYUAefgu6xEfva_4.25.F14.boolean.opBoolean","SPLIT",FACE,{"disambiguationData":[TD([subQ4])],"derivedFrom":makeQuery(id+"FyYUAefgu6xEfva_4.24.F14.boolean.opBoolean","SPLIT",FACE,{"disambiguationData":[TD([subQ4])],"derivedFrom":makeQuery(id+"FyYUAefgu6xEfva_4.23.F14.boolean.opBoolean","SPLIT",FACE,{"disambiguationData":[TD([subQ4])],"derivedFrom":makeQuery(id+"FyYUAefgu6xEfva_4.22.F14.boolean.opBoolean","SPLIT",FACE,{"disambiguationData":[TD([subQ4])],"derivedFrom":makeQuery(id+"FyYUAefgu6xEfva_4.21.F14.boolean.opBoolean","SPLIT",FACE,{"disambiguationData":[TD([subQ4])],"derivedFrom":makeQuery(id+"FyYUAefgu6xEfva_4.20.F14.boolean.opBoolean","SPLIT",FACE,{"disambiguationData":[TD([subQ4])],"derivedFrom":makeQuery(id+"FyYUAefgu6xEfva_4.19.F14.boolean.opBoolean","SPLIT",FACE,{"disambiguationData":[TD([subQ4])],"derivedFrom":makeQuery(id+"FyYUAefgu6xEfva_4.18.F14.boolean.opBoolean","SPLIT",FACE,{"disambiguationData":[TD([subQ4])],"derivedFrom":makeQuery(id+"FyYUAefgu6xEfva_4.17.F14.boolean.opBoolean","SPLIT",FACE,{"disambiguationData":[TD([subQ4])],"derivedFrom":makeQuery(id+"FyYUAefgu6xEfva_4.16.F14.boolean.opBoolean","SPLIT",FACE,{"disambiguationData":[TD([subQ4])],"derivedFrom":makeQuery(id+"FyYUAefgu6xEfva_4.15.F14.boolean.opBoolean","SPLIT",FACE,{"disambiguationData":[TD([subQ4])],"derivedFrom":makeQuery(id+"FyYUAefgu6xEfva_4.14.F14.boolean.opBoolean","SPLIT",FACE,{"disambiguationData":[TD([subQ4])],"derivedFrom":makeQuery(id+"FyYUAefgu6xEfva_4.13.F14.boolean.opBoolean","SPLIT",FACE,{"disambiguationData":[TD([subQ4])],"derivedFrom":makeQuery(id+"FyYUAefgu6xEfva_4.12.F14.boolean.opBoolean","SPLIT",FACE,{"disambiguationData":[TD([subQ4])],"derivedFrom":makeQuery(id+"FyYUAefgu6xEfva_4.11.F14.boolean.opBoolean","SPLIT",FACE,{"disambiguationData":[TD([subQ4])],"derivedFrom":makeQuery(id+"FyYUAefgu6xEfva_4.10.F14.boolean.opBoolean","SPLIT",FACE,{"disambiguationData":[TD([subQ4])],"derivedFrom":makeQuery(id+"FyYUAefgu6xEfva_4.9.F14.boolean.opBoolean","SPLIT",FACE,{"disambiguationData":[TD([subQ4])],"derivedFrom":makeQuery(id+"FyYUAefgu6xEfva_4.8.F14.boolean.opBoolean","SPLIT",FACE,{"disambiguationData":[TD([subQ4])],"derivedFrom":makeQuery(id+"FyYUAefgu6xEfva_4.7.F14.boolean.opBoolean","SPLIT",FACE,{"disambiguationData":[TD([subQ4])],"derivedFrom":makeQuery(id+"FyYUAefgu6xEfva_4.6.F14.boolean.opBoolean","SPLIT",FACE,{"disambiguationData":[TD([subQ4])],"derivedFrom":makeQuery(id+"FyYUAefgu6xEfva_4.5.F14.boolean.opBoolean","SPLIT",FACE,{"disambiguationData":[TD([subQ4])],"derivedFrom":makeQuery(id+"FyYUAefgu6xEfva_4.4.F14.boolean.opBoolean","SPLIT",FACE,{"disambiguationData":[TD([subQ4])],"derivedFrom":makeQuery(id+"FyYUAefgu6xEfva_4.3.F14.boolean.opBoolean","SPLIT",FACE,{"disambiguationData":[TD([subQ4])],"derivedFrom":makeQuery(id+"FyYUAefgu6xEfva_4.2.F14.boolean.opBoolean","SPLIT",FACE,{"disambiguationData":[TD([subQ4])],"derivedFrom":makeQuery(id+"FyYUAefgu6xEfva_4.1.F14.boolean.opBoolean","SPLIT",FACE,{"disambiguationData":[TD([subQ4])],"derivedFrom":makeQuery(id+"F10.boolean.opBoolean","COPY",FACE,{"derivedFrom":makeQuery(id+"F10.opExtrude","CAP_FACE",FACE,{"disambiguationData":[OSD([subQ0])],"isStart":false})})})})})})})})})})})})})})})})})})})})})})})})})})})})})})})})})})})})})})})})})})})})})})})})})})});}
            var Q4;
            {var subQ0=sQuery(id+"F9.wireOp",EDGE,"E142");var subQ2=sQuery(id+"F13.wireOp",EDGE,"E147");var subQ4=sQuery(id+"F13.wireOp",EDGE,"E148.MirrorCS");var subQ5=makeQuery(id+"FyYUAefgu6xEfva_4.48.F14.opExtrude","SWEPT_FACE",FACE,{"disambiguationData":[OSD([subQ4])]});var subQ6=makeQuery(id+"F14.opExtrude","SWEPT_FACE",FACE,{"disambiguationData":[OSD([subQ2])]});Q4=makeQuery(id+"FyYUAefgu6xEfva_4.49.F14.boolean.opBoolean","SPLIT",FACE,{"disambiguationData":[TD([subQ5])],"derivedFrom":makeQuery(id+"FyYUAefgu6xEfva_4.48.F14.boolean.opBoolean","SPLIT",FACE,{"disambiguationData":[TD([subQ6])],"derivedFrom":makeQuery(id+"FyYUAefgu6xEfva_4.47.F14.boolean.opBoolean","SPLIT",FACE,{"disambiguationData":[TD([subQ6])],"derivedFrom":makeQuery(id+"FyYUAefgu6xEfva_4.46.F14.boolean.opBoolean","SPLIT",FACE,{"disambiguationData":[TD([subQ6])],"derivedFrom":makeQuery(id+"FyYUAefgu6xEfva_4.45.F14.boolean.opBoolean","SPLIT",FACE,{"disambiguationData":[TD([subQ6])],"derivedFrom":makeQuery(id+"FyYUAefgu6xEfva_4.44.F14.boolean.opBoolean","SPLIT",FACE,{"disambiguationData":[TD([subQ6])],"derivedFrom":makeQuery(id+"FyYUAefgu6xEfva_4.43.F14.boolean.opBoolean","SPLIT",FACE,{"disambiguationData":[TD([subQ6])],"derivedFrom":makeQuery(id+"FyYUAefgu6xEfva_4.42.F14.boolean.opBoolean","SPLIT",FACE,{"disambiguationData":[TD([subQ6])],"derivedFrom":makeQuery(id+"FyYUAefgu6xEfva_4.41.F14.boolean.opBoolean","SPLIT",FACE,{"disambiguationData":[TD([subQ6])],"derivedFrom":makeQuery(id+"FyYUAefgu6xEfva_4.40.F14.boolean.opBoolean","SPLIT",FACE,{"disambiguationData":[TD([subQ6])],"derivedFrom":makeQuery(id+"FyYUAefgu6xEfva_4.39.F14.boolean.opBoolean","SPLIT",FACE,{"disambiguationData":[TD([subQ6])],"derivedFrom":makeQuery(id+"FyYUAefgu6xEfva_4.38.F14.boolean.opBoolean","SPLIT",FACE,{"disambiguationData":[TD([subQ6])],"derivedFrom":makeQuery(id+"FyYUAefgu6xEfva_4.37.F14.boolean.opBoolean","SPLIT",FACE,{"disambiguationData":[TD([subQ6])],"derivedFrom":makeQuery(id+"FyYUAefgu6xEfva_4.36.F14.boolean.opBoolean","SPLIT",FACE,{"disambiguationData":[TD([subQ6])],"derivedFrom":makeQuery(id+"FyYUAefgu6xEfva_4.35.F14.boolean.opBoolean","SPLIT",FACE,{"disambiguationData":[TD([subQ6])],"derivedFrom":makeQuery(id+"FyYUAefgu6xEfva_4.34.F14.boolean.opBoolean","SPLIT",FACE,{"disambiguationData":[TD([subQ6])],"derivedFrom":makeQuery(id+"FyYUAefgu6xEfva_4.33.F14.boolean.opBoolean","SPLIT",FACE,{"disambiguationData":[TD([subQ6])],"derivedFrom":makeQuery(id+"FyYUAefgu6xEfva_4.32.F14.boolean.opBoolean","SPLIT",FACE,{"disambiguationData":[TD([subQ6])],"derivedFrom":makeQuery(id+"FyYUAefgu6xEfva_4.31.F14.boolean.opBoolean","SPLIT",FACE,{"disambiguationData":[TD([subQ6])],"derivedFrom":makeQuery(id+"FyYUAefgu6xEfva_4.30.F14.boolean.opBoolean","SPLIT",FACE,{"disambiguationData":[TD([subQ6])],"derivedFrom":makeQuery(id+"FyYUAefgu6xEfva_4.29.F14.boolean.opBoolean","SPLIT",FACE,{"disambiguationData":[TD([subQ6])],"derivedFrom":makeQuery(id+"FyYUAefgu6xEfva_4.28.F14.boolean.opBoolean","SPLIT",FACE,{"disambiguationData":[TD([subQ6])],"derivedFrom":makeQuery(id+"FyYUAefgu6xEfva_4.27.F14.boolean.opBoolean","SPLIT",FACE,{"disambiguationData":[TD([subQ6])],"derivedFrom":makeQuery(id+"FyYUAefgu6xEfva_4.26.F14.boolean.opBoolean","SPLIT",FACE,{"disambiguationData":[TD([subQ6])],"derivedFrom":makeQuery(id+"FyYUAefgu6xEfva_4.25.F14.boolean.opBoolean","SPLIT",FACE,{"disambiguationData":[TD([subQ6])],"derivedFrom":makeQuery(id+"FyYUAefgu6xEfva_4.24.F14.boolean.opBoolean","SPLIT",FACE,{"disambiguationData":[TD([subQ6])],"derivedFrom":makeQuery(id+"FyYUAefgu6xEfva_4.23.F14.boolean.opBoolean","SPLIT",FACE,{"disambiguationData":[TD([subQ6])],"derivedFrom":makeQuery(id+"FyYUAefgu6xEfva_4.22.F14.boolean.opBoolean","SPLIT",FACE,{"disambiguationData":[TD([subQ6])],"derivedFrom":makeQuery(id+"FyYUAefgu6xEfva_4.21.F14.boolean.opBoolean","SPLIT",FACE,{"disambiguationData":[TD([subQ6])],"derivedFrom":makeQuery(id+"FyYUAefgu6xEfva_4.20.F14.boolean.opBoolean","SPLIT",FACE,{"disambiguationData":[TD([subQ6])],"derivedFrom":makeQuery(id+"FyYUAefgu6xEfva_4.19.F14.boolean.opBoolean","SPLIT",FACE,{"disambiguationData":[TD([subQ6])],"derivedFrom":makeQuery(id+"FyYUAefgu6xEfva_4.18.F14.boolean.opBoolean","SPLIT",FACE,{"disambiguationData":[TD([subQ6])],"derivedFrom":makeQuery(id+"FyYUAefgu6xEfva_4.17.F14.boolean.opBoolean","SPLIT",FACE,{"disambiguationData":[TD([subQ6])],"derivedFrom":makeQuery(id+"FyYUAefgu6xEfva_4.16.F14.boolean.opBoolean","SPLIT",FACE,{"disambiguationData":[TD([subQ6])],"derivedFrom":makeQuery(id+"FyYUAefgu6xEfva_4.15.F14.boolean.opBoolean","SPLIT",FACE,{"disambiguationData":[TD([subQ6])],"derivedFrom":makeQuery(id+"FyYUAefgu6xEfva_4.14.F14.boolean.opBoolean","SPLIT",FACE,{"disambiguationData":[TD([subQ6])],"derivedFrom":makeQuery(id+"FyYUAefgu6xEfva_4.13.F14.boolean.opBoolean","SPLIT",FACE,{"disambiguationData":[TD([subQ6])],"derivedFrom":makeQuery(id+"FyYUAefgu6xEfva_4.12.F14.boolean.opBoolean","SPLIT",FACE,{"disambiguationData":[TD([subQ6])],"derivedFrom":makeQuery(id+"FyYUAefgu6xEfva_4.11.F14.boolean.opBoolean","SPLIT",FACE,{"disambiguationData":[TD([subQ6])],"derivedFrom":makeQuery(id+"FyYUAefgu6xEfva_4.10.F14.boolean.opBoolean","SPLIT",FACE,{"disambiguationData":[TD([subQ6])],"derivedFrom":makeQuery(id+"FyYUAefgu6xEfva_4.9.F14.boolean.opBoolean","SPLIT",FACE,{"disambiguationData":[TD([subQ6])],"derivedFrom":makeQuery(id+"FyYUAefgu6xEfva_4.8.F14.boolean.opBoolean","SPLIT",FACE,{"disambiguationData":[TD([subQ6])],"derivedFrom":makeQuery(id+"FyYUAefgu6xEfva_4.7.F14.boolean.opBoolean","SPLIT",FACE,{"disambiguationData":[TD([subQ6])],"derivedFrom":makeQuery(id+"FyYUAefgu6xEfva_4.6.F14.boolean.opBoolean","SPLIT",FACE,{"disambiguationData":[TD([subQ6])],"derivedFrom":makeQuery(id+"FyYUAefgu6xEfva_4.5.F14.boolean.opBoolean","SPLIT",FACE,{"disambiguationData":[TD([subQ6])],"derivedFrom":makeQuery(id+"FyYUAefgu6xEfva_4.4.F14.boolean.opBoolean","SPLIT",FACE,{"disambiguationData":[TD([subQ6])],"derivedFrom":makeQuery(id+"FyYUAefgu6xEfva_4.3.F14.boolean.opBoolean","SPLIT",FACE,{"disambiguationData":[TD([subQ6])],"derivedFrom":makeQuery(id+"FyYUAefgu6xEfva_4.2.F14.boolean.opBoolean","SPLIT",FACE,{"disambiguationData":[TD([subQ6])],"derivedFrom":makeQuery(id+"FyYUAefgu6xEfva_4.1.F14.boolean.opBoolean","SPLIT",FACE,{"disambiguationData":[TD([subQ6])],"derivedFrom":makeQuery(id+"F10.boolean.opBoolean","COPY",FACE,{"derivedFrom":makeQuery(id+"F10.opExtrude","CAP_FACE",FACE,{"disambiguationData":[OSD([subQ0])],"isStart":false})})})})})})})})})})})})})})})})})})})})})})})})})})})})})})})})})})})})})})})})})})})})})})})})})})});}
            var Q5;
            Q5=makeQuery(id+"F12.opExtrude","CAP_EDGE",EDGE,{"disambiguationData":[OSD([sQuery(id+"F11.wireOp",EDGE,"E144.0")])],"isStart":false});
            var Q6;
            Q6=makeQuery(id+"FyYUAefgu6xEfva_4.39.F14.opExtrude","CAP_EDGE",EDGE,{"disambiguationData":[OSD([sQuery(id+"F13.wireOp",EDGE,"E148.MirrorCS")])],"isStart":false});
            var Q7;
            Q7=makeQuery(id+"FyYUAefgu6xEfva_4.39.F14.opExtrude","CAP_EDGE",EDGE,{"disambiguationData":[OSD([sQuery(id+"F13.wireOp",EDGE,"E147")])],"isStart":false});
            var Q8;
            Q8=makeQuery(id+"FyYUAefgu6xEfva_4.38.F14.opExtrude","CAP_EDGE",EDGE,{"disambiguationData":[OSD([sQuery(id+"F13.wireOp",EDGE,"E148.MirrorCS")])],"isStart":false});
            var Q9;
            Q9=makeQuery(id+"FyYUAefgu6xEfva_4.37.F14.opExtrude","CAP_EDGE",EDGE,{"disambiguationData":[OSD([sQuery(id+"F13.wireOp",EDGE,"E148.MirrorCS")])],"isStart":false});
            var Q10;
            {var subQ0=sQuery(id+"F13.wireOp",EDGE,"E148.MirrorCS");var subQ1=sQuery(id+"F13.wireOp",EDGE,"E147");var subQ2=sQuery(id+"F11.wireOp",EDGE,"E143");var subQ24=makeQuery(id+"FyYUAefgu6xEfva_4.35.F14.opExtrude","SWEPT_FACE",FACE,{"disambiguationData":[OSD([subQ0])]});var subQ43=makeQuery(id+"F14.opExtrude","SWEPT_FACE",FACE,{"disambiguationData":[OSD([subQ1])]});Q10=makeQuery(id+"FyYUAefgu6xEfva_4.36.F14.boolean.opBoolean","SPLIT",EDGE,{"disambiguationData":[TD([subQ24])],"derivedFrom":makeQuery(id+"FyYUAefgu6xEfva_4.35.F14.boolean.opBoolean","SPLIT",EDGE,{"disambiguationData":[TD([subQ43])],"derivedFrom":makeQuery(id+"FyYUAefgu6xEfva_4.34.F14.boolean.opBoolean","SPLIT",EDGE,{"disambiguationData":[TD([subQ43])],"derivedFrom":makeQuery(id+"FyYUAefgu6xEfva_4.33.F14.boolean.opBoolean","SPLIT",EDGE,{"disambiguationData":[TD([subQ43])],"derivedFrom":makeQuery(id+"FyYUAefgu6xEfva_4.32.F14.boolean.opBoolean","SPLIT",EDGE,{"disambiguationData":[TD([subQ43])],"derivedFrom":makeQuery(id+"FyYUAefgu6xEfva_4.31.F14.boolean.opBoolean","SPLIT",EDGE,{"disambiguationData":[TD([subQ43])],"derivedFrom":makeQuery(id+"FyYUAefgu6xEfva_4.30.F14.boolean.opBoolean","SPLIT",EDGE,{"disambiguationData":[TD([subQ43])],"derivedFrom":makeQuery(id+"FyYUAefgu6xEfva_4.29.F14.boolean.opBoolean","SPLIT",EDGE,{"disambiguationData":[TD([subQ43])],"derivedFrom":makeQuery(id+"FyYUAefgu6xEfva_4.28.F14.boolean.opBoolean","SPLIT",EDGE,{"disambiguationData":[TD([subQ43])],"derivedFrom":makeQuery(id+"FyYUAefgu6xEfva_4.27.F14.boolean.opBoolean","SPLIT",EDGE,{"disambiguationData":[TD([subQ43])],"derivedFrom":makeQuery(id+"FyYUAefgu6xEfva_4.26.F14.boolean.opBoolean","SPLIT",EDGE,{"disambiguationData":[TD([subQ43])],"derivedFrom":makeQuery(id+"FyYUAefgu6xEfva_4.25.F14.boolean.opBoolean","SPLIT",EDGE,{"disambiguationData":[TD([subQ43])],"derivedFrom":makeQuery(id+"FyYUAefgu6xEfva_4.24.F14.boolean.opBoolean","SPLIT",EDGE,{"disambiguationData":[TD([subQ43])],"derivedFrom":makeQuery(id+"FyYUAefgu6xEfva_4.23.F14.boolean.opBoolean","SPLIT",EDGE,{"disambiguationData":[TD([subQ43])],"derivedFrom":makeQuery(id+"FyYUAefgu6xEfva_4.22.F14.boolean.opBoolean","SPLIT",EDGE,{"disambiguationData":[TD([subQ43])],"derivedFrom":makeQuery(id+"FyYUAefgu6xEfva_4.21.F14.boolean.opBoolean","SPLIT",EDGE,{"disambiguationData":[TD([subQ43])],"derivedFrom":makeQuery(id+"FyYUAefgu6xEfva_4.20.F14.boolean.opBoolean","SPLIT",EDGE,{"disambiguationData":[TD([subQ43])],"derivedFrom":makeQuery(id+"FyYUAefgu6xEfva_4.19.F14.boolean.opBoolean","SPLIT",EDGE,{"disambiguationData":[TD([subQ43])],"derivedFrom":makeQuery(id+"FyYUAefgu6xEfva_4.18.F14.boolean.opBoolean","SPLIT",EDGE,{"disambiguationData":[TD([subQ43])],"derivedFrom":makeQuery(id+"FyYUAefgu6xEfva_4.17.F14.boolean.opBoolean","SPLIT",EDGE,{"disambiguationData":[TD([subQ43])],"derivedFrom":makeQuery(id+"FyYUAefgu6xEfva_4.16.F14.boolean.opBoolean","SPLIT",EDGE,{"disambiguationData":[TD([subQ43])],"derivedFrom":makeQuery(id+"FyYUAefgu6xEfva_4.15.F14.boolean.opBoolean","SPLIT",EDGE,{"disambiguationData":[TD([subQ43])],"derivedFrom":makeQuery(id+"FyYUAefgu6xEfva_4.14.F14.boolean.opBoolean","SPLIT",EDGE,{"disambiguationData":[TD([subQ43])],"derivedFrom":makeQuery(id+"FyYUAefgu6xEfva_4.13.F14.boolean.opBoolean","SPLIT",EDGE,{"disambiguationData":[TD([subQ43])],"derivedFrom":makeQuery(id+"FyYUAefgu6xEfva_4.12.F14.boolean.opBoolean","SPLIT",EDGE,{"disambiguationData":[TD([subQ43])],"derivedFrom":makeQuery(id+"FyYUAefgu6xEfva_4.11.F14.boolean.opBoolean","SPLIT",EDGE,{"disambiguationData":[TD([subQ43])],"derivedFrom":makeQuery(id+"FyYUAefgu6xEfva_4.10.F14.boolean.opBoolean","SPLIT",EDGE,{"disambiguationData":[TD([subQ43])],"derivedFrom":makeQuery(id+"FyYUAefgu6xEfva_4.9.F14.boolean.opBoolean","SPLIT",EDGE,{"disambiguationData":[TD([subQ43])],"derivedFrom":makeQuery(id+"FyYUAefgu6xEfva_4.8.F14.boolean.opBoolean","SPLIT",EDGE,{"disambiguationData":[TD([subQ43])],"derivedFrom":makeQuery(id+"FyYUAefgu6xEfva_4.7.F14.boolean.opBoolean","SPLIT",EDGE,{"disambiguationData":[TD([subQ43])],"derivedFrom":makeQuery(id+"FyYUAefgu6xEfva_4.6.F14.boolean.opBoolean","SPLIT",EDGE,{"disambiguationData":[TD([subQ43])],"derivedFrom":makeQuery(id+"FyYUAefgu6xEfva_4.5.F14.boolean.opBoolean","SPLIT",EDGE,{"disambiguationData":[TD([subQ43])],"derivedFrom":makeQuery(id+"FyYUAefgu6xEfva_4.4.F14.boolean.opBoolean","SPLIT",EDGE,{"disambiguationData":[TD([subQ43])],"derivedFrom":makeQuery(id+"FyYUAefgu6xEfva_4.3.F14.boolean.opBoolean","SPLIT",EDGE,{"disambiguationData":[TD([subQ43])],"derivedFrom":makeQuery(id+"FyYUAefgu6xEfva_4.2.F14.boolean.opBoolean","SPLIT",EDGE,{"disambiguationData":[TD([subQ43])],"derivedFrom":makeQuery(id+"FyYUAefgu6xEfva_4.1.F14.boolean.opBoolean","SPLIT",EDGE,{"disambiguationData":[TD([subQ43])],"derivedFrom":makeQuery(id+"F12.opExtrude","CAP_EDGE",EDGE,{"disambiguationData":[OSD([subQ2])],"isStart":false})})})})})})})})})})})})})})})})})})})})})})})})})})})})})})})})})})})})});}
            var Q11;
            Q11=makeQuery(id+"FyYUAefgu6xEfva_4.41.F14.opExtrude","CAP_EDGE",EDGE,{"disambiguationData":[OSD([sQuery(id+"F13.wireOp",EDGE,"E148.MirrorCS")])],"isStart":false});
            var Q12;
            Q12=makeQuery(id+"FyYUAefgu6xEfva_4.41.F14.opExtrude","CAP_EDGE",EDGE,{"disambiguationData":[OSD([sQuery(id+"F13.wireOp",EDGE,"E147")])],"isStart":false});
            var Q13;
            Q13=makeQuery(id+"FyYUAefgu6xEfva_4.3.F14.opExtrude","CAP_EDGE",EDGE,{"disambiguationData":[OSD([sQuery(id+"F13.wireOp",EDGE,"E148.MirrorCS")])],"isStart":false});
            var Q14;
            Q14=makeQuery(id+"FyYUAefgu6xEfva_4.3.F14.opExtrude","CAP_EDGE",EDGE,{"disambiguationData":[OSD([sQuery(id+"F13.wireOp",EDGE,"E147")])],"isStart":false});
            var Q15;
            Q15=makeQuery(id+"FyYUAefgu6xEfva_4.2.F14.opExtrude","CAP_EDGE",EDGE,{"disambiguationData":[OSD([sQuery(id+"F13.wireOp",EDGE,"E148.MirrorCS")])],"isStart":false});
            var Q16;
            Q16=makeQuery(id+"FyYUAefgu6xEfva_4.2.F14.opExtrude","CAP_EDGE",EDGE,{"disambiguationData":[OSD([sQuery(id+"F13.wireOp",EDGE,"E147")])],"isStart":false});
            var Q17;
            {var subQ0=sQuery(id+"F13.wireOp",EDGE,"E148.MirrorCS");var subQ2=sQuery(id+"F11.wireOp",EDGE,"E143");Q17=makeQuery(id+"FyYUAefgu6xEfva_4.1.F14.boolean.opBoolean","SPLIT",EDGE,{"disambiguationData":[TD([makeQuery(id+"F14.opExtrude","SWEPT_FACE",FACE,{"disambiguationData":[OSD([subQ0])]})])],"derivedFrom":makeQuery(id+"F12.opExtrude","CAP_EDGE",EDGE,{"disambiguationData":[OSD([subQ2])],"isStart":false})});}
            var Q18;
            Q18=makeQuery(id+"FyYUAefgu6xEfva_4.40.F14.opExtrude","CAP_EDGE",EDGE,{"disambiguationData":[OSD([sQuery(id+"F13.wireOp",EDGE,"E148.MirrorCS")])],"isStart":false});
            var Q19;
            Q19=makeQuery(id+"FyYUAefgu6xEfva_4.8.F14.opExtrude","CAP_EDGE",EDGE,{"disambiguationData":[OSD([sQuery(id+"F13.wireOp",EDGE,"E148.MirrorCS")])],"isStart":false});
            var Q20;
            Q20=makeQuery(id+"FyYUAefgu6xEfva_4.8.F14.opExtrude","CAP_EDGE",EDGE,{"disambiguationData":[OSD([sQuery(id+"F13.wireOp",EDGE,"E147")])],"isStart":false});
            var Q21;
            Q21=makeQuery(id+"FyYUAefgu6xEfva_4.7.F14.opExtrude","CAP_EDGE",EDGE,{"disambiguationData":[OSD([sQuery(id+"F13.wireOp",EDGE,"E148.MirrorCS")])],"isStart":false});
            var Q22;
            Q22=makeQuery(id+"FyYUAefgu6xEfva_4.7.F14.opExtrude","CAP_EDGE",EDGE,{"disambiguationData":[OSD([sQuery(id+"F13.wireOp",EDGE,"E147")])],"isStart":false});
            var Q23;
            Q23=makeQuery(id+"FyYUAefgu6xEfva_4.6.F14.opExtrude","CAP_EDGE",EDGE,{"disambiguationData":[OSD([sQuery(id+"F13.wireOp",EDGE,"E148.MirrorCS")])],"isStart":false});
            var Q24;
            Q24=makeQuery(id+"FyYUAefgu6xEfva_4.6.F14.opExtrude","CAP_EDGE",EDGE,{"disambiguationData":[OSD([sQuery(id+"F13.wireOp",EDGE,"E147")])],"isStart":false});
            var Q25;
            Q25=makeQuery(id+"FyYUAefgu6xEfva_4.5.F14.opExtrude","CAP_EDGE",EDGE,{"disambiguationData":[OSD([sQuery(id+"F13.wireOp",EDGE,"E148.MirrorCS")])],"isStart":false});
            var Q26;
            Q26=makeQuery(id+"FyYUAefgu6xEfva_4.5.F14.opExtrude","CAP_EDGE",EDGE,{"disambiguationData":[OSD([sQuery(id+"F13.wireOp",EDGE,"E147")])],"isStart":false});
            var Q27;
            Q27=makeQuery(id+"FyYUAefgu6xEfva_4.4.F14.opExtrude","CAP_EDGE",EDGE,{"disambiguationData":[OSD([sQuery(id+"F13.wireOp",EDGE,"E148.MirrorCS")])],"isStart":false});
            var Q28;
            Q28=makeQuery(id+"FyYUAefgu6xEfva_4.4.F14.opExtrude","CAP_EDGE",EDGE,{"disambiguationData":[OSD([sQuery(id+"F13.wireOp",EDGE,"E147")])],"isStart":false});
            var Q29;
            Q29=makeQuery(id+"FyYUAefgu6xEfva_4.9.F14.opExtrude","CAP_EDGE",EDGE,{"disambiguationData":[OSD([sQuery(id+"F13.wireOp",EDGE,"E148.MirrorCS")])],"isStart":false});
            var Q30;
            Q30=makeQuery(id+"FyYUAefgu6xEfva_4.9.F14.opExtrude","CAP_EDGE",EDGE,{"disambiguationData":[OSD([sQuery(id+"F13.wireOp",EDGE,"E147")])],"isStart":false});
            var Q31;
            Q31=makeQuery(id+"FyYUAefgu6xEfva_4.10.F14.opExtrude","CAP_EDGE",EDGE,{"disambiguationData":[OSD([sQuery(id+"F13.wireOp",EDGE,"E147")])],"isStart":false});
            var Q32;
            Q32=makeQuery(id+"FyYUAefgu6xEfva_4.10.F14.opExtrude","CAP_EDGE",EDGE,{"disambiguationData":[OSD([sQuery(id+"F13.wireOp",EDGE,"E148.MirrorCS")])],"isStart":false});
            var Q33;
            Q33=makeQuery(id+"FyYUAefgu6xEfva_4.42.F14.opExtrude","CAP_EDGE",EDGE,{"disambiguationData":[OSD([sQuery(id+"F13.wireOp",EDGE,"E147")])],"isStart":false});
            var Q34;
            Q34=makeQuery(id+"FyYUAefgu6xEfva_4.42.F14.opExtrude","CAP_EDGE",EDGE,{"disambiguationData":[OSD([sQuery(id+"F13.wireOp",EDGE,"E148.MirrorCS")])],"isStart":false});
            var Q35;
            Q35=makeQuery(id+"FyYUAefgu6xEfva_4.11.F14.opExtrude","CAP_EDGE",EDGE,{"disambiguationData":[OSD([sQuery(id+"F13.wireOp",EDGE,"E147")])],"isStart":false});
            var Q36;
            Q36=makeQuery(id+"FyYUAefgu6xEfva_4.43.F14.opExtrude","CAP_EDGE",EDGE,{"disambiguationData":[OSD([sQuery(id+"F13.wireOp",EDGE,"E147")])],"isStart":false});
            var Q37;
            Q37=makeQuery(id+"FyYUAefgu6xEfva_4.43.F14.opExtrude","CAP_EDGE",EDGE,{"disambiguationData":[OSD([sQuery(id+"F13.wireOp",EDGE,"E148.MirrorCS")])],"isStart":false});
            var Q38;
            Q38=makeQuery(id+"FyYUAefgu6xEfva_4.44.F14.opExtrude","CAP_EDGE",EDGE,{"disambiguationData":[OSD([sQuery(id+"F13.wireOp",EDGE,"E147")])],"isStart":false});
            var Q39;
            Q39=makeQuery(id+"FyYUAefgu6xEfva_4.44.F14.opExtrude","CAP_EDGE",EDGE,{"disambiguationData":[OSD([sQuery(id+"F13.wireOp",EDGE,"E148.MirrorCS")])],"isStart":false});
            var Q40;
            Q40=makeQuery(id+"FyYUAefgu6xEfva_4.13.F14.opExtrude","CAP_EDGE",EDGE,{"disambiguationData":[OSD([sQuery(id+"F13.wireOp",EDGE,"E148.MirrorCS")])],"isStart":false});
            var Q41;
            Q41=makeQuery(id+"FyYUAefgu6xEfva_4.45.F14.opExtrude","CAP_EDGE",EDGE,{"disambiguationData":[OSD([sQuery(id+"F13.wireOp",EDGE,"E147")])],"isStart":false});
            var Q42;
            Q42=makeQuery(id+"FyYUAefgu6xEfva_4.45.F14.opExtrude","CAP_EDGE",EDGE,{"disambiguationData":[OSD([sQuery(id+"F13.wireOp",EDGE,"E148.MirrorCS")])],"isStart":false});
            var Q43;
            Q43=makeQuery(id+"FyYUAefgu6xEfva_4.45.F14.opExtrude","CAP_EDGE",EDGE,{"disambiguationData":[OSD([sQuery(id+"F13.wireOp",EDGE,"E148.MirrorCS")])],"isStart":true});
            var Q44;
            Q44=makeQuery(id+"FyYUAefgu6xEfva_4.46.F14.opExtrude","CAP_EDGE",EDGE,{"disambiguationData":[OSD([sQuery(id+"F13.wireOp",EDGE,"E148.MirrorCS")])],"isStart":false});
            var Q45;
            Q45=makeQuery(id+"FyYUAefgu6xEfva_4.15.F14.opExtrude","CAP_EDGE",EDGE,{"disambiguationData":[OSD([sQuery(id+"F13.wireOp",EDGE,"E147")])],"isStart":false});
            var Q46;
            Q46=makeQuery(id+"FyYUAefgu6xEfva_4.15.F14.opExtrude","CAP_EDGE",EDGE,{"disambiguationData":[OSD([sQuery(id+"F13.wireOp",EDGE,"E148.MirrorCS")])],"isStart":false});
            var Q47;
            Q47=makeQuery(id+"FyYUAefgu6xEfva_4.47.F14.opExtrude","CAP_EDGE",EDGE,{"disambiguationData":[OSD([sQuery(id+"F13.wireOp",EDGE,"E147")])],"isStart":false});
            var Q48;
            Q48=makeQuery(id+"FyYUAefgu6xEfva_4.47.F14.opExtrude","CAP_EDGE",EDGE,{"disambiguationData":[OSD([sQuery(id+"F13.wireOp",EDGE,"E148.MirrorCS")])],"isStart":false});
            var Q49;
            Q49=makeQuery(id+"FyYUAefgu6xEfva_4.16.F14.opExtrude","CAP_EDGE",EDGE,{"disambiguationData":[OSD([sQuery(id+"F13.wireOp",EDGE,"E147")])],"isStart":false});
            var Q50;
            Q50=makeQuery(id+"FyYUAefgu6xEfva_4.16.F14.opExtrude","CAP_EDGE",EDGE,{"disambiguationData":[OSD([sQuery(id+"F13.wireOp",EDGE,"E148.MirrorCS")])],"isStart":false});
            var Q51;
            Q51=makeQuery(id+"FyYUAefgu6xEfva_4.48.F14.opExtrude","CAP_EDGE",EDGE,{"disambiguationData":[OSD([sQuery(id+"F13.wireOp",EDGE,"E147")])],"isStart":false});
            var Q52;
            Q52=makeQuery(id+"FyYUAefgu6xEfva_4.48.F14.opExtrude","CAP_EDGE",EDGE,{"disambiguationData":[OSD([sQuery(id+"F13.wireOp",EDGE,"E148.MirrorCS")])],"isStart":false});
            var Q53;
            Q53=makeQuery(id+"FyYUAefgu6xEfva_4.16.F14.opExtrude","SWEPT_EDGE",EDGE,{"disambiguationData":[OSD([sQuery(id+"F9.wireOp",EDGE,"E142"),sQuery(id+"F13.wireOp",EDGE,"E147")])]});
            var Q54;
            Q54=makeQuery(id+"FyYUAefgu6xEfva_4.17.F14.opExtrude","CAP_EDGE",EDGE,{"disambiguationData":[OSD([sQuery(id+"F13.wireOp",EDGE,"E147")])],"isStart":false});
            var Q55;
            Q55=makeQuery(id+"FyYUAefgu6xEfva_4.17.F14.opExtrude","CAP_EDGE",EDGE,{"disambiguationData":[OSD([sQuery(id+"F13.wireOp",EDGE,"E148.MirrorCS")])],"isStart":false});
            var Q56;
            Q56=makeQuery(id+"FyYUAefgu6xEfva_4.49.F14.opExtrude","CAP_EDGE",EDGE,{"disambiguationData":[OSD([sQuery(id+"F13.wireOp",EDGE,"E148.MirrorCS")])],"isStart":false});
            var Q57;
            {var subQ0=sQuery(id+"F13.wireOp",EDGE,"E148.MirrorCS");var subQ1=sQuery(id+"F13.wireOp",EDGE,"E147");var subQ2=sQuery(id+"F11.wireOp",EDGE,"E143");var subQ8=makeQuery(id+"FyYUAefgu6xEfva_4.48.F14.opExtrude","SWEPT_FACE",FACE,{"disambiguationData":[OSD([subQ0])]});var subQ56=makeQuery(id+"F14.opExtrude","SWEPT_FACE",FACE,{"disambiguationData":[OSD([subQ1])]});Q57=makeQuery(id+"FyYUAefgu6xEfva_4.49.F14.boolean.opBoolean","SPLIT",EDGE,{"disambiguationData":[TD([subQ8])],"derivedFrom":makeQuery(id+"FyYUAefgu6xEfva_4.48.F14.boolean.opBoolean","SPLIT",EDGE,{"disambiguationData":[TD([subQ56])],"derivedFrom":makeQuery(id+"FyYUAefgu6xEfva_4.47.F14.boolean.opBoolean","SPLIT",EDGE,{"disambiguationData":[TD([subQ56])],"derivedFrom":makeQuery(id+"FyYUAefgu6xEfva_4.46.F14.boolean.opBoolean","SPLIT",EDGE,{"disambiguationData":[TD([subQ56])],"derivedFrom":makeQuery(id+"FyYUAefgu6xEfva_4.45.F14.boolean.opBoolean","SPLIT",EDGE,{"disambiguationData":[TD([subQ56])],"derivedFrom":makeQuery(id+"FyYUAefgu6xEfva_4.44.F14.boolean.opBoolean","SPLIT",EDGE,{"disambiguationData":[TD([subQ56])],"derivedFrom":makeQuery(id+"FyYUAefgu6xEfva_4.43.F14.boolean.opBoolean","SPLIT",EDGE,{"disambiguationData":[TD([subQ56])],"derivedFrom":makeQuery(id+"FyYUAefgu6xEfva_4.42.F14.boolean.opBoolean","SPLIT",EDGE,{"disambiguationData":[TD([subQ56])],"derivedFrom":makeQuery(id+"FyYUAefgu6xEfva_4.41.F14.boolean.opBoolean","SPLIT",EDGE,{"disambiguationData":[TD([subQ56])],"derivedFrom":makeQuery(id+"FyYUAefgu6xEfva_4.40.F14.boolean.opBoolean","SPLIT",EDGE,{"disambiguationData":[TD([subQ56])],"derivedFrom":makeQuery(id+"FyYUAefgu6xEfva_4.39.F14.boolean.opBoolean","SPLIT",EDGE,{"disambiguationData":[TD([subQ56])],"derivedFrom":makeQuery(id+"FyYUAefgu6xEfva_4.38.F14.boolean.opBoolean","SPLIT",EDGE,{"disambiguationData":[TD([subQ56])],"derivedFrom":makeQuery(id+"FyYUAefgu6xEfva_4.37.F14.boolean.opBoolean","SPLIT",EDGE,{"disambiguationData":[TD([subQ56])],"derivedFrom":makeQuery(id+"FyYUAefgu6xEfva_4.36.F14.boolean.opBoolean","SPLIT",EDGE,{"disambiguationData":[TD([subQ56])],"derivedFrom":makeQuery(id+"FyYUAefgu6xEfva_4.35.F14.boolean.opBoolean","SPLIT",EDGE,{"disambiguationData":[TD([subQ56])],"derivedFrom":makeQuery(id+"FyYUAefgu6xEfva_4.34.F14.boolean.opBoolean","SPLIT",EDGE,{"disambiguationData":[TD([subQ56])],"derivedFrom":makeQuery(id+"FyYUAefgu6xEfva_4.33.F14.boolean.opBoolean","SPLIT",EDGE,{"disambiguationData":[TD([subQ56])],"derivedFrom":makeQuery(id+"FyYUAefgu6xEfva_4.32.F14.boolean.opBoolean","SPLIT",EDGE,{"disambiguationData":[TD([subQ56])],"derivedFrom":makeQuery(id+"FyYUAefgu6xEfva_4.31.F14.boolean.opBoolean","SPLIT",EDGE,{"disambiguationData":[TD([subQ56])],"derivedFrom":makeQuery(id+"FyYUAefgu6xEfva_4.30.F14.boolean.opBoolean","SPLIT",EDGE,{"disambiguationData":[TD([subQ56])],"derivedFrom":makeQuery(id+"FyYUAefgu6xEfva_4.29.F14.boolean.opBoolean","SPLIT",EDGE,{"disambiguationData":[TD([subQ56])],"derivedFrom":makeQuery(id+"FyYUAefgu6xEfva_4.28.F14.boolean.opBoolean","SPLIT",EDGE,{"disambiguationData":[TD([subQ56])],"derivedFrom":makeQuery(id+"FyYUAefgu6xEfva_4.27.F14.boolean.opBoolean","SPLIT",EDGE,{"disambiguationData":[TD([subQ56])],"derivedFrom":makeQuery(id+"FyYUAefgu6xEfva_4.26.F14.boolean.opBoolean","SPLIT",EDGE,{"disambiguationData":[TD([subQ56])],"derivedFrom":makeQuery(id+"FyYUAefgu6xEfva_4.25.F14.boolean.opBoolean","SPLIT",EDGE,{"disambiguationData":[TD([subQ56])],"derivedFrom":makeQuery(id+"FyYUAefgu6xEfva_4.24.F14.boolean.opBoolean","SPLIT",EDGE,{"disambiguationData":[TD([subQ56])],"derivedFrom":makeQuery(id+"FyYUAefgu6xEfva_4.23.F14.boolean.opBoolean","SPLIT",EDGE,{"disambiguationData":[TD([subQ56])],"derivedFrom":makeQuery(id+"FyYUAefgu6xEfva_4.22.F14.boolean.opBoolean","SPLIT",EDGE,{"disambiguationData":[TD([subQ56])],"derivedFrom":makeQuery(id+"FyYUAefgu6xEfva_4.21.F14.boolean.opBoolean","SPLIT",EDGE,{"disambiguationData":[TD([subQ56])],"derivedFrom":makeQuery(id+"FyYUAefgu6xEfva_4.20.F14.boolean.opBoolean","SPLIT",EDGE,{"disambiguationData":[TD([subQ56])],"derivedFrom":makeQuery(id+"FyYUAefgu6xEfva_4.19.F14.boolean.opBoolean","SPLIT",EDGE,{"disambiguationData":[TD([subQ56])],"derivedFrom":makeQuery(id+"FyYUAefgu6xEfva_4.18.F14.boolean.opBoolean","SPLIT",EDGE,{"disambiguationData":[TD([subQ56])],"derivedFrom":makeQuery(id+"FyYUAefgu6xEfva_4.17.F14.boolean.opBoolean","SPLIT",EDGE,{"disambiguationData":[TD([subQ56])],"derivedFrom":makeQuery(id+"FyYUAefgu6xEfva_4.16.F14.boolean.opBoolean","SPLIT",EDGE,{"disambiguationData":[TD([subQ56])],"derivedFrom":makeQuery(id+"FyYUAefgu6xEfva_4.15.F14.boolean.opBoolean","SPLIT",EDGE,{"disambiguationData":[TD([subQ56])],"derivedFrom":makeQuery(id+"FyYUAefgu6xEfva_4.14.F14.boolean.opBoolean","SPLIT",EDGE,{"disambiguationData":[TD([subQ56])],"derivedFrom":makeQuery(id+"FyYUAefgu6xEfva_4.13.F14.boolean.opBoolean","SPLIT",EDGE,{"disambiguationData":[TD([subQ56])],"derivedFrom":makeQuery(id+"FyYUAefgu6xEfva_4.12.F14.boolean.opBoolean","SPLIT",EDGE,{"disambiguationData":[TD([subQ56])],"derivedFrom":makeQuery(id+"FyYUAefgu6xEfva_4.11.F14.boolean.opBoolean","SPLIT",EDGE,{"disambiguationData":[TD([subQ56])],"derivedFrom":makeQuery(id+"FyYUAefgu6xEfva_4.10.F14.boolean.opBoolean","SPLIT",EDGE,{"disambiguationData":[TD([subQ56])],"derivedFrom":makeQuery(id+"FyYUAefgu6xEfva_4.9.F14.boolean.opBoolean","SPLIT",EDGE,{"disambiguationData":[TD([subQ56])],"derivedFrom":makeQuery(id+"FyYUAefgu6xEfva_4.8.F14.boolean.opBoolean","SPLIT",EDGE,{"disambiguationData":[TD([subQ56])],"derivedFrom":makeQuery(id+"FyYUAefgu6xEfva_4.7.F14.boolean.opBoolean","SPLIT",EDGE,{"disambiguationData":[TD([subQ56])],"derivedFrom":makeQuery(id+"FyYUAefgu6xEfva_4.6.F14.boolean.opBoolean","SPLIT",EDGE,{"disambiguationData":[TD([subQ56])],"derivedFrom":makeQuery(id+"FyYUAefgu6xEfva_4.5.F14.boolean.opBoolean","SPLIT",EDGE,{"disambiguationData":[TD([subQ56])],"derivedFrom":makeQuery(id+"FyYUAefgu6xEfva_4.4.F14.boolean.opBoolean","SPLIT",EDGE,{"disambiguationData":[TD([subQ56])],"derivedFrom":makeQuery(id+"FyYUAefgu6xEfva_4.3.F14.boolean.opBoolean","SPLIT",EDGE,{"disambiguationData":[TD([subQ56])],"derivedFrom":makeQuery(id+"FyYUAefgu6xEfva_4.2.F14.boolean.opBoolean","SPLIT",EDGE,{"disambiguationData":[TD([subQ56])],"derivedFrom":makeQuery(id+"FyYUAefgu6xEfva_4.1.F14.boolean.opBoolean","SPLIT",EDGE,{"disambiguationData":[TD([subQ56])],"derivedFrom":makeQuery(id+"F12.opExtrude","CAP_EDGE",EDGE,{"disambiguationData":[OSD([subQ2])],"isStart":false})})})})})})})})})})})})})})})})})})})})})})})})})})})})})})})})})})})})})})})})})})})})})})})})})});}
            var Q58;
            Q58=makeQuery(id+"FyYUAefgu6xEfva_4.18.F14.opExtrude","CAP_EDGE",EDGE,{"disambiguationData":[OSD([sQuery(id+"F13.wireOp",EDGE,"E147")])],"isStart":false});
            var Q59;
            Q59=makeQuery(id+"FyYUAefgu6xEfva_4.18.F14.opExtrude","CAP_EDGE",EDGE,{"disambiguationData":[OSD([sQuery(id+"F13.wireOp",EDGE,"E148.MirrorCS")])],"isStart":false});
            var Q60;
            Q60=makeQuery(id+"FyYUAefgu6xEfva_4.18.F14.opExtrude","SWEPT_EDGE",EDGE,{"disambiguationData":[OSD([sQuery(id+"F9.wireOp",EDGE,"E142"),sQuery(id+"F13.wireOp",EDGE,"E147")])]});
            var Q61;
            Q61=makeQuery(id+"FyYUAefgu6xEfva_4.19.F14.opExtrude","CAP_EDGE",EDGE,{"disambiguationData":[OSD([sQuery(id+"F13.wireOp",EDGE,"E147")])],"isStart":false});
            var Q62;
            Q62=makeQuery(id+"FyYUAefgu6xEfva_4.19.F14.opExtrude","CAP_EDGE",EDGE,{"disambiguationData":[OSD([sQuery(id+"F13.wireOp",EDGE,"E148.MirrorCS")])],"isStart":false});
            var Q63;
            Q63=makeQuery(id+"FyYUAefgu6xEfva_4.20.F14.opExtrude","CAP_EDGE",EDGE,{"disambiguationData":[OSD([sQuery(id+"F13.wireOp",EDGE,"E147")])],"isStart":false});
            var Q64;
            Q64=makeQuery(id+"FyYUAefgu6xEfva_4.20.F14.opExtrude","CAP_EDGE",EDGE,{"disambiguationData":[OSD([sQuery(id+"F13.wireOp",EDGE,"E148.MirrorCS")])],"isStart":false});
            var Q65;
            Q65=makeQuery(id+"FyYUAefgu6xEfva_4.21.F14.opExtrude","CAP_EDGE",EDGE,{"disambiguationData":[OSD([sQuery(id+"F13.wireOp",EDGE,"E148.MirrorCS")])],"isStart":false});
            var Q66;
            Q66=makeQuery(id+"FyYUAefgu6xEfva_4.21.F14.opExtrude","CAP_EDGE",EDGE,{"disambiguationData":[OSD([sQuery(id+"F9.wireOp",EDGE,"E142")])],"isStart":false});
            var Q67;
            Q67=makeQuery(id+"FyYUAefgu6xEfva_4.22.F14.opExtrude","CAP_EDGE",EDGE,{"disambiguationData":[OSD([sQuery(id+"F13.wireOp",EDGE,"E147")])],"isStart":false});
            var Q68;
            Q68=makeQuery(id+"FyYUAefgu6xEfva_4.22.F14.opExtrude","CAP_EDGE",EDGE,{"disambiguationData":[OSD([sQuery(id+"F13.wireOp",EDGE,"E148.MirrorCS")])],"isStart":false});
            var Q69;
            Q69=makeQuery(id+"FyYUAefgu6xEfva_4.23.F14.opExtrude","SWEPT_EDGE",EDGE,{"disambiguationData":[OSD([sQuery(id+"F9.wireOp",EDGE,"E142"),sQuery(id+"F13.wireOp",EDGE,"E147")])]});
            var Q70;
            Q70=makeQuery(id+"FyYUAefgu6xEfva_4.24.F14.opExtrude","CAP_EDGE",EDGE,{"disambiguationData":[OSD([sQuery(id+"F13.wireOp",EDGE,"E148.MirrorCS")])],"isStart":false});
            var Q71;
            Q71=makeQuery(id+"FyYUAefgu6xEfva_4.25.F14.opExtrude","CAP_EDGE",EDGE,{"disambiguationData":[OSD([sQuery(id+"F13.wireOp",EDGE,"E147")])],"isStart":false});
            var Q72;
            Q72=makeQuery(id+"FyYUAefgu6xEfva_4.25.F14.opExtrude","CAP_EDGE",EDGE,{"disambiguationData":[OSD([sQuery(id+"F13.wireOp",EDGE,"E148.MirrorCS")])],"isStart":false});
            var Q73;
            Q73=makeQuery(id+"FyYUAefgu6xEfva_4.26.F14.opExtrude","CAP_EDGE",EDGE,{"disambiguationData":[OSD([sQuery(id+"F13.wireOp",EDGE,"E148.MirrorCS")])],"isStart":false});
            var Q74;
            Q74=makeQuery(id+"FyYUAefgu6xEfva_4.27.F14.opExtrude","CAP_EDGE",EDGE,{"disambiguationData":[OSD([sQuery(id+"F13.wireOp",EDGE,"E147")])],"isStart":false});
            var Q75;
            Q75=makeQuery(id+"FyYUAefgu6xEfva_4.27.F14.opExtrude","CAP_EDGE",EDGE,{"disambiguationData":[OSD([sQuery(id+"F13.wireOp",EDGE,"E148.MirrorCS")])],"isStart":false});
            var Q76;
            Q76=makeQuery(id+"FyYUAefgu6xEfva_4.28.F14.opExtrude","CAP_EDGE",EDGE,{"disambiguationData":[OSD([sQuery(id+"F13.wireOp",EDGE,"E147")])],"isStart":false});
            var Q77;
            Q77=makeQuery(id+"FyYUAefgu6xEfva_4.28.F14.opExtrude","CAP_EDGE",EDGE,{"disambiguationData":[OSD([sQuery(id+"F13.wireOp",EDGE,"E148.MirrorCS")])],"isStart":false});
            var Q78;
            Q78=makeQuery(id+"FyYUAefgu6xEfva_4.29.F14.opExtrude","CAP_EDGE",EDGE,{"disambiguationData":[OSD([sQuery(id+"F13.wireOp",EDGE,"E147")])],"isStart":false});
            var Q79;
            Q79=makeQuery(id+"FyYUAefgu6xEfva_4.29.F14.opExtrude","CAP_EDGE",EDGE,{"disambiguationData":[OSD([sQuery(id+"F13.wireOp",EDGE,"E148.MirrorCS")])],"isStart":false});
            var Q80;
            Q80=makeQuery(id+"FyYUAefgu6xEfva_4.30.F14.opExtrude","CAP_EDGE",EDGE,{"disambiguationData":[OSD([sQuery(id+"F13.wireOp",EDGE,"E147")])],"isStart":false});
            var Q81;
            Q81=makeQuery(id+"FyYUAefgu6xEfva_4.30.F14.opExtrude","CAP_EDGE",EDGE,{"disambiguationData":[OSD([sQuery(id+"F13.wireOp",EDGE,"E148.MirrorCS")])],"isStart":false});
            var Q82;
            Q82=makeQuery(id+"FyYUAefgu6xEfva_4.31.F14.opExtrude","CAP_EDGE",EDGE,{"disambiguationData":[OSD([sQuery(id+"F13.wireOp",EDGE,"E147")])],"isStart":false});
            var Q83;
            Q83=makeQuery(id+"FyYUAefgu6xEfva_4.31.F14.opExtrude","CAP_EDGE",EDGE,{"disambiguationData":[OSD([sQuery(id+"F13.wireOp",EDGE,"E148.MirrorCS")])],"isStart":false});
            var Q84;
            Q84=makeQuery(id+"FyYUAefgu6xEfva_4.32.F14.opExtrude","CAP_EDGE",EDGE,{"disambiguationData":[OSD([sQuery(id+"F13.wireOp",EDGE,"E147")])],"isStart":false});
            var Q85;
            Q85=makeQuery(id+"FyYUAefgu6xEfva_4.32.F14.opExtrude","CAP_EDGE",EDGE,{"disambiguationData":[OSD([sQuery(id+"F13.wireOp",EDGE,"E148.MirrorCS")])],"isStart":false});
            var Q86;
            Q86=makeQuery(id+"FyYUAefgu6xEfva_4.33.F14.opExtrude","CAP_EDGE",EDGE,{"disambiguationData":[OSD([sQuery(id+"F13.wireOp",EDGE,"E147")])],"isStart":false});
            var Q87;
            Q87=makeQuery(id+"FyYUAefgu6xEfva_4.33.F14.opExtrude","CAP_EDGE",EDGE,{"disambiguationData":[OSD([sQuery(id+"F13.wireOp",EDGE,"E148.MirrorCS")])],"isStart":false});
            var Q88;
            Q88=makeQuery(id+"FyYUAefgu6xEfva_4.34.F14.opExtrude","CAP_EDGE",EDGE,{"disambiguationData":[OSD([sQuery(id+"F13.wireOp",EDGE,"E148.MirrorCS")])],"isStart":false});
            var Q89;
            Q89=makeQuery(id+"FyYUAefgu6xEfva_4.35.F14.opExtrude","CAP_EDGE",EDGE,{"disambiguationData":[OSD([sQuery(id+"F13.wireOp",EDGE,"E148.MirrorCS")])],"isStart":false});
            var Q90;
            Q90=makeQuery(id+"F14.opExtrude","CAP_EDGE",EDGE,{"disambiguationData":[OSD([sQuery(id+"F13.wireOp",EDGE,"E147")])],"isStart":false});
            var Q91;
            Q91=makeQuery(id+"F2.opRevolve","SWEPT_EDGE",EDGE,{"disambiguationData":[OSD([sQuery(id+"F0.wireOp",EDGE,"E73"),sQuery(id+"F0.wireOp",EDGE,"E77.filletArc")])]});
            var Q92;
            Q92=makeQuery(id+"F14.opExtrude","CAP_EDGE",EDGE,{"disambiguationData":[OSD([sQuery(id+"F13.wireOp",EDGE,"E148.MirrorCS")])],"isStart":false});
            var Q93;
            Q93=makeQuery(id+"FyYUAefgu6xEfva_4.39.F14.opExtrude","SWEPT_EDGE",EDGE,{"disambiguationData":[OSD([sQuery(id+"F11.wireOp",EDGE,"E143"),sQuery(id+"F13.wireOp",EDGE,"E147")])]});
            var Q94;
            Q94=makeQuery(id+"FyYUAefgu6xEfva_4.39.F14.opExtrude","SWEPT_EDGE",EDGE,{"disambiguationData":[OSD([sQuery(id+"F9.wireOp",EDGE,"E142"),sQuery(id+"F13.wireOp",EDGE,"E148.MirrorCS")])]});
            var Q95;
            Q95=makeQuery(id+"FyYUAefgu6xEfva_4.39.F14.opExtrude","SWEPT_EDGE",EDGE,{"disambiguationData":[OSD([sQuery(id+"F11.wireOp",EDGE,"E143"),sQuery(id+"F13.wireOp",EDGE,"E148.MirrorCS")])]});
            var Q96;
            Q96=makeQuery(id+"FyYUAefgu6xEfva_4.39.F14.opExtrude","SWEPT_EDGE",EDGE,{"disambiguationData":[OSD([sQuery(id+"F9.wireOp",EDGE,"E142"),sQuery(id+"F13.wireOp",EDGE,"E147")])]});
            var Q97;
            {var subQ0=sQuery(id+"F13.wireOp",EDGE,"E148.MirrorCS");var subQ1=sQuery(id+"F13.wireOp",EDGE,"E147");var subQ2=sQuery(id+"F11.wireOp",EDGE,"E143");var subQ21=makeQuery(id+"FyYUAefgu6xEfva_4.37.F14.opExtrude","SWEPT_FACE",FACE,{"disambiguationData":[OSD([subQ0])]});var subQ45=makeQuery(id+"F14.opExtrude","SWEPT_FACE",FACE,{"disambiguationData":[OSD([subQ1])]});Q97=makeQuery(id+"FyYUAefgu6xEfva_4.38.F14.boolean.opBoolean","SPLIT",EDGE,{"disambiguationData":[TD([subQ21])],"derivedFrom":makeQuery(id+"FyYUAefgu6xEfva_4.37.F14.boolean.opBoolean","SPLIT",EDGE,{"disambiguationData":[TD([subQ45])],"derivedFrom":makeQuery(id+"FyYUAefgu6xEfva_4.36.F14.boolean.opBoolean","SPLIT",EDGE,{"disambiguationData":[TD([subQ45])],"derivedFrom":makeQuery(id+"FyYUAefgu6xEfva_4.35.F14.boolean.opBoolean","SPLIT",EDGE,{"disambiguationData":[TD([subQ45])],"derivedFrom":makeQuery(id+"FyYUAefgu6xEfva_4.34.F14.boolean.opBoolean","SPLIT",EDGE,{"disambiguationData":[TD([subQ45])],"derivedFrom":makeQuery(id+"FyYUAefgu6xEfva_4.33.F14.boolean.opBoolean","SPLIT",EDGE,{"disambiguationData":[TD([subQ45])],"derivedFrom":makeQuery(id+"FyYUAefgu6xEfva_4.32.F14.boolean.opBoolean","SPLIT",EDGE,{"disambiguationData":[TD([subQ45])],"derivedFrom":makeQuery(id+"FyYUAefgu6xEfva_4.31.F14.boolean.opBoolean","SPLIT",EDGE,{"disambiguationData":[TD([subQ45])],"derivedFrom":makeQuery(id+"FyYUAefgu6xEfva_4.30.F14.boolean.opBoolean","SPLIT",EDGE,{"disambiguationData":[TD([subQ45])],"derivedFrom":makeQuery(id+"FyYUAefgu6xEfva_4.29.F14.boolean.opBoolean","SPLIT",EDGE,{"disambiguationData":[TD([subQ45])],"derivedFrom":makeQuery(id+"FyYUAefgu6xEfva_4.28.F14.boolean.opBoolean","SPLIT",EDGE,{"disambiguationData":[TD([subQ45])],"derivedFrom":makeQuery(id+"FyYUAefgu6xEfva_4.27.F14.boolean.opBoolean","SPLIT",EDGE,{"disambiguationData":[TD([subQ45])],"derivedFrom":makeQuery(id+"FyYUAefgu6xEfva_4.26.F14.boolean.opBoolean","SPLIT",EDGE,{"disambiguationData":[TD([subQ45])],"derivedFrom":makeQuery(id+"FyYUAefgu6xEfva_4.25.F14.boolean.opBoolean","SPLIT",EDGE,{"disambiguationData":[TD([subQ45])],"derivedFrom":makeQuery(id+"FyYUAefgu6xEfva_4.24.F14.boolean.opBoolean","SPLIT",EDGE,{"disambiguationData":[TD([subQ45])],"derivedFrom":makeQuery(id+"FyYUAefgu6xEfva_4.23.F14.boolean.opBoolean","SPLIT",EDGE,{"disambiguationData":[TD([subQ45])],"derivedFrom":makeQuery(id+"FyYUAefgu6xEfva_4.22.F14.boolean.opBoolean","SPLIT",EDGE,{"disambiguationData":[TD([subQ45])],"derivedFrom":makeQuery(id+"FyYUAefgu6xEfva_4.21.F14.boolean.opBoolean","SPLIT",EDGE,{"disambiguationData":[TD([subQ45])],"derivedFrom":makeQuery(id+"FyYUAefgu6xEfva_4.20.F14.boolean.opBoolean","SPLIT",EDGE,{"disambiguationData":[TD([subQ45])],"derivedFrom":makeQuery(id+"FyYUAefgu6xEfva_4.19.F14.boolean.opBoolean","SPLIT",EDGE,{"disambiguationData":[TD([subQ45])],"derivedFrom":makeQuery(id+"FyYUAefgu6xEfva_4.18.F14.boolean.opBoolean","SPLIT",EDGE,{"disambiguationData":[TD([subQ45])],"derivedFrom":makeQuery(id+"FyYUAefgu6xEfva_4.17.F14.boolean.opBoolean","SPLIT",EDGE,{"disambiguationData":[TD([subQ45])],"derivedFrom":makeQuery(id+"FyYUAefgu6xEfva_4.16.F14.boolean.opBoolean","SPLIT",EDGE,{"disambiguationData":[TD([subQ45])],"derivedFrom":makeQuery(id+"FyYUAefgu6xEfva_4.15.F14.boolean.opBoolean","SPLIT",EDGE,{"disambiguationData":[TD([subQ45])],"derivedFrom":makeQuery(id+"FyYUAefgu6xEfva_4.14.F14.boolean.opBoolean","SPLIT",EDGE,{"disambiguationData":[TD([subQ45])],"derivedFrom":makeQuery(id+"FyYUAefgu6xEfva_4.13.F14.boolean.opBoolean","SPLIT",EDGE,{"disambiguationData":[TD([subQ45])],"derivedFrom":makeQuery(id+"FyYUAefgu6xEfva_4.12.F14.boolean.opBoolean","SPLIT",EDGE,{"disambiguationData":[TD([subQ45])],"derivedFrom":makeQuery(id+"FyYUAefgu6xEfva_4.11.F14.boolean.opBoolean","SPLIT",EDGE,{"disambiguationData":[TD([subQ45])],"derivedFrom":makeQuery(id+"FyYUAefgu6xEfva_4.10.F14.boolean.opBoolean","SPLIT",EDGE,{"disambiguationData":[TD([subQ45])],"derivedFrom":makeQuery(id+"FyYUAefgu6xEfva_4.9.F14.boolean.opBoolean","SPLIT",EDGE,{"disambiguationData":[TD([subQ45])],"derivedFrom":makeQuery(id+"FyYUAefgu6xEfva_4.8.F14.boolean.opBoolean","SPLIT",EDGE,{"disambiguationData":[TD([subQ45])],"derivedFrom":makeQuery(id+"FyYUAefgu6xEfva_4.7.F14.boolean.opBoolean","SPLIT",EDGE,{"disambiguationData":[TD([subQ45])],"derivedFrom":makeQuery(id+"FyYUAefgu6xEfva_4.6.F14.boolean.opBoolean","SPLIT",EDGE,{"disambiguationData":[TD([subQ45])],"derivedFrom":makeQuery(id+"FyYUAefgu6xEfva_4.5.F14.boolean.opBoolean","SPLIT",EDGE,{"disambiguationData":[TD([subQ45])],"derivedFrom":makeQuery(id+"FyYUAefgu6xEfva_4.4.F14.boolean.opBoolean","SPLIT",EDGE,{"disambiguationData":[TD([subQ45])],"derivedFrom":makeQuery(id+"FyYUAefgu6xEfva_4.3.F14.boolean.opBoolean","SPLIT",EDGE,{"disambiguationData":[TD([subQ45])],"derivedFrom":makeQuery(id+"FyYUAefgu6xEfva_4.2.F14.boolean.opBoolean","SPLIT",EDGE,{"disambiguationData":[TD([subQ45])],"derivedFrom":makeQuery(id+"FyYUAefgu6xEfva_4.1.F14.boolean.opBoolean","SPLIT",EDGE,{"disambiguationData":[TD([subQ45])],"derivedFrom":makeQuery(id+"F12.opExtrude","CAP_EDGE",EDGE,{"disambiguationData":[OSD([subQ2])],"isStart":false})})})})})})})})})})})})})})})})})})})})})})})})})})})})})})})})})})})})})})});}
            var Q98;
            {var subQ0=sQuery(id+"F9.wireOp",EDGE,"E142");var subQ3=sQuery(id+"F13.wireOp",EDGE,"E148.MirrorCS");var subQ4=makeQuery(id+"FyYUAefgu6xEfva_4.37.F14.opExtrude","SWEPT_FACE",FACE,{"disambiguationData":[OSD([subQ3])]});var subQ5=sQuery(id+"F13.wireOp",EDGE,"E147");var subQ6=makeQuery(id+"F14.opExtrude","SWEPT_FACE",FACE,{"disambiguationData":[OSD([subQ5])]});Q98=makeQuery(id+"FyYUAefgu6xEfva_4.38.F14.boolean.opBoolean","SPLIT",EDGE,{"disambiguationData":[TD([subQ4])],"derivedFrom":makeQuery(id+"FyYUAefgu6xEfva_4.37.F14.boolean.opBoolean","SPLIT",EDGE,{"disambiguationData":[TD([subQ6])],"derivedFrom":makeQuery(id+"FyYUAefgu6xEfva_4.36.F14.boolean.opBoolean","SPLIT",EDGE,{"disambiguationData":[TD([subQ6])],"derivedFrom":makeQuery(id+"FyYUAefgu6xEfva_4.35.F14.boolean.opBoolean","SPLIT",EDGE,{"disambiguationData":[TD([subQ6])],"derivedFrom":makeQuery(id+"FyYUAefgu6xEfva_4.34.F14.boolean.opBoolean","SPLIT",EDGE,{"disambiguationData":[TD([subQ6])],"derivedFrom":makeQuery(id+"FyYUAefgu6xEfva_4.33.F14.boolean.opBoolean","SPLIT",EDGE,{"disambiguationData":[TD([subQ6])],"derivedFrom":makeQuery(id+"FyYUAefgu6xEfva_4.32.F14.boolean.opBoolean","SPLIT",EDGE,{"disambiguationData":[TD([subQ6])],"derivedFrom":makeQuery(id+"FyYUAefgu6xEfva_4.31.F14.boolean.opBoolean","SPLIT",EDGE,{"disambiguationData":[TD([subQ6])],"derivedFrom":makeQuery(id+"FyYUAefgu6xEfva_4.30.F14.boolean.opBoolean","SPLIT",EDGE,{"disambiguationData":[TD([subQ6])],"derivedFrom":makeQuery(id+"FyYUAefgu6xEfva_4.29.F14.boolean.opBoolean","SPLIT",EDGE,{"disambiguationData":[TD([subQ6])],"derivedFrom":makeQuery(id+"FyYUAefgu6xEfva_4.28.F14.boolean.opBoolean","SPLIT",EDGE,{"disambiguationData":[TD([subQ6])],"derivedFrom":makeQuery(id+"FyYUAefgu6xEfva_4.27.F14.boolean.opBoolean","SPLIT",EDGE,{"disambiguationData":[TD([subQ6])],"derivedFrom":makeQuery(id+"FyYUAefgu6xEfva_4.26.F14.boolean.opBoolean","SPLIT",EDGE,{"disambiguationData":[TD([subQ6])],"derivedFrom":makeQuery(id+"FyYUAefgu6xEfva_4.25.F14.boolean.opBoolean","SPLIT",EDGE,{"disambiguationData":[TD([subQ6])],"derivedFrom":makeQuery(id+"FyYUAefgu6xEfva_4.24.F14.boolean.opBoolean","SPLIT",EDGE,{"disambiguationData":[TD([subQ6])],"derivedFrom":makeQuery(id+"FyYUAefgu6xEfva_4.23.F14.boolean.opBoolean","SPLIT",EDGE,{"disambiguationData":[TD([subQ6])],"derivedFrom":makeQuery(id+"FyYUAefgu6xEfva_4.22.F14.boolean.opBoolean","SPLIT",EDGE,{"disambiguationData":[TD([subQ6])],"derivedFrom":makeQuery(id+"FyYUAefgu6xEfva_4.21.F14.boolean.opBoolean","SPLIT",EDGE,{"disambiguationData":[TD([subQ6])],"derivedFrom":makeQuery(id+"FyYUAefgu6xEfva_4.20.F14.boolean.opBoolean","SPLIT",EDGE,{"disambiguationData":[TD([subQ6])],"derivedFrom":makeQuery(id+"FyYUAefgu6xEfva_4.19.F14.boolean.opBoolean","SPLIT",EDGE,{"disambiguationData":[TD([subQ6])],"derivedFrom":makeQuery(id+"FyYUAefgu6xEfva_4.18.F14.boolean.opBoolean","SPLIT",EDGE,{"disambiguationData":[TD([subQ6])],"derivedFrom":makeQuery(id+"FyYUAefgu6xEfva_4.17.F14.boolean.opBoolean","SPLIT",EDGE,{"disambiguationData":[TD([subQ6])],"derivedFrom":makeQuery(id+"FyYUAefgu6xEfva_4.16.F14.boolean.opBoolean","SPLIT",EDGE,{"disambiguationData":[TD([subQ6])],"derivedFrom":makeQuery(id+"FyYUAefgu6xEfva_4.15.F14.boolean.opBoolean","SPLIT",EDGE,{"disambiguationData":[TD([subQ6])],"derivedFrom":makeQuery(id+"FyYUAefgu6xEfva_4.14.F14.boolean.opBoolean","SPLIT",EDGE,{"disambiguationData":[TD([subQ6])],"derivedFrom":makeQuery(id+"FyYUAefgu6xEfva_4.13.F14.boolean.opBoolean","SPLIT",EDGE,{"disambiguationData":[TD([subQ6])],"derivedFrom":makeQuery(id+"FyYUAefgu6xEfva_4.12.F14.boolean.opBoolean","SPLIT",EDGE,{"disambiguationData":[TD([subQ6])],"derivedFrom":makeQuery(id+"FyYUAefgu6xEfva_4.11.F14.boolean.opBoolean","SPLIT",EDGE,{"disambiguationData":[TD([subQ6])],"derivedFrom":makeQuery(id+"FyYUAefgu6xEfva_4.10.F14.boolean.opBoolean","SPLIT",EDGE,{"disambiguationData":[TD([subQ6])],"derivedFrom":makeQuery(id+"FyYUAefgu6xEfva_4.9.F14.boolean.opBoolean","SPLIT",EDGE,{"disambiguationData":[TD([subQ6])],"derivedFrom":makeQuery(id+"FyYUAefgu6xEfva_4.8.F14.boolean.opBoolean","SPLIT",EDGE,{"disambiguationData":[TD([subQ6])],"derivedFrom":makeQuery(id+"FyYUAefgu6xEfva_4.7.F14.boolean.opBoolean","SPLIT",EDGE,{"disambiguationData":[TD([subQ6])],"derivedFrom":makeQuery(id+"FyYUAefgu6xEfva_4.6.F14.boolean.opBoolean","SPLIT",EDGE,{"disambiguationData":[TD([subQ6])],"derivedFrom":makeQuery(id+"FyYUAefgu6xEfva_4.5.F14.boolean.opBoolean","SPLIT",EDGE,{"disambiguationData":[TD([subQ6])],"derivedFrom":makeQuery(id+"FyYUAefgu6xEfva_4.4.F14.boolean.opBoolean","SPLIT",EDGE,{"disambiguationData":[TD([subQ6])],"derivedFrom":makeQuery(id+"FyYUAefgu6xEfva_4.3.F14.boolean.opBoolean","SPLIT",EDGE,{"disambiguationData":[TD([subQ6])],"derivedFrom":makeQuery(id+"FyYUAefgu6xEfva_4.2.F14.boolean.opBoolean","SPLIT",EDGE,{"disambiguationData":[TD([subQ6])],"derivedFrom":makeQuery(id+"FyYUAefgu6xEfva_4.1.F14.boolean.opBoolean","SPLIT",EDGE,{"disambiguationData":[TD([subQ6])],"derivedFrom":makeQuery(id+"F10.boolean.opBoolean","COPY",EDGE,{"derivedFrom":makeQuery(id+"F10.opExtrude","CAP_EDGE",EDGE,{"disambiguationData":[OSD([subQ0])],"isStart":false})})})})})})})})})})})})})})})})})})})})})})})})})})})})})})})})})})})})})})})});}
            var Q99;
            Q99=makeQuery(id+"FyYUAefgu6xEfva_4.38.F14.opExtrude","CAP_EDGE",EDGE,{"disambiguationData":[OSD([sQuery(id+"F9.wireOp",EDGE,"E142")])],"isStart":false});
            var Q100;
            Q100=makeQuery(id+"FyYUAefgu6xEfva_4.38.F14.opExtrude","SWEPT_EDGE",EDGE,{"disambiguationData":[OSD([sQuery(id+"F11.wireOp",EDGE,"E143"),sQuery(id+"F13.wireOp",EDGE,"E148.MirrorCS")])]});
            var Q101;
            Q101=makeQuery(id+"FyYUAefgu6xEfva_4.38.F14.opExtrude","SWEPT_EDGE",EDGE,{"disambiguationData":[OSD([sQuery(id+"F9.wireOp",EDGE,"E142"),sQuery(id+"F13.wireOp",EDGE,"E148.MirrorCS")])]});
            var Q102;
            Q102=makeQuery(id+"FyYUAefgu6xEfva_4.38.F14.opExtrude","SWEPT_EDGE",EDGE,{"disambiguationData":[OSD([sQuery(id+"F9.wireOp",EDGE,"E142"),sQuery(id+"F13.wireOp",EDGE,"E147")])]});
            var Q103;
            Q103=makeQuery(id+"FyYUAefgu6xEfva_4.38.F14.opExtrude","CAP_EDGE",EDGE,{"disambiguationData":[OSD([sQuery(id+"F13.wireOp",EDGE,"E147")])],"isStart":false});
            var Q104;
            {var subQ0=sQuery(id+"F13.wireOp",EDGE,"E148.MirrorCS");var subQ1=sQuery(id+"F13.wireOp",EDGE,"E147");var subQ2=sQuery(id+"F11.wireOp",EDGE,"E143");var subQ25=makeQuery(id+"FyYUAefgu6xEfva_4.36.F14.opExtrude","SWEPT_FACE",FACE,{"disambiguationData":[OSD([subQ0])]});var subQ44=makeQuery(id+"F14.opExtrude","SWEPT_FACE",FACE,{"disambiguationData":[OSD([subQ1])]});Q104=makeQuery(id+"FyYUAefgu6xEfva_4.37.F14.boolean.opBoolean","SPLIT",EDGE,{"disambiguationData":[TD([subQ25])],"derivedFrom":makeQuery(id+"FyYUAefgu6xEfva_4.36.F14.boolean.opBoolean","SPLIT",EDGE,{"disambiguationData":[TD([subQ44])],"derivedFrom":makeQuery(id+"FyYUAefgu6xEfva_4.35.F14.boolean.opBoolean","SPLIT",EDGE,{"disambiguationData":[TD([subQ44])],"derivedFrom":makeQuery(id+"FyYUAefgu6xEfva_4.34.F14.boolean.opBoolean","SPLIT",EDGE,{"disambiguationData":[TD([subQ44])],"derivedFrom":makeQuery(id+"FyYUAefgu6xEfva_4.33.F14.boolean.opBoolean","SPLIT",EDGE,{"disambiguationData":[TD([subQ44])],"derivedFrom":makeQuery(id+"FyYUAefgu6xEfva_4.32.F14.boolean.opBoolean","SPLIT",EDGE,{"disambiguationData":[TD([subQ44])],"derivedFrom":makeQuery(id+"FyYUAefgu6xEfva_4.31.F14.boolean.opBoolean","SPLIT",EDGE,{"disambiguationData":[TD([subQ44])],"derivedFrom":makeQuery(id+"FyYUAefgu6xEfva_4.30.F14.boolean.opBoolean","SPLIT",EDGE,{"disambiguationData":[TD([subQ44])],"derivedFrom":makeQuery(id+"FyYUAefgu6xEfva_4.29.F14.boolean.opBoolean","SPLIT",EDGE,{"disambiguationData":[TD([subQ44])],"derivedFrom":makeQuery(id+"FyYUAefgu6xEfva_4.28.F14.boolean.opBoolean","SPLIT",EDGE,{"disambiguationData":[TD([subQ44])],"derivedFrom":makeQuery(id+"FyYUAefgu6xEfva_4.27.F14.boolean.opBoolean","SPLIT",EDGE,{"disambiguationData":[TD([subQ44])],"derivedFrom":makeQuery(id+"FyYUAefgu6xEfva_4.26.F14.boolean.opBoolean","SPLIT",EDGE,{"disambiguationData":[TD([subQ44])],"derivedFrom":makeQuery(id+"FyYUAefgu6xEfva_4.25.F14.boolean.opBoolean","SPLIT",EDGE,{"disambiguationData":[TD([subQ44])],"derivedFrom":makeQuery(id+"FyYUAefgu6xEfva_4.24.F14.boolean.opBoolean","SPLIT",EDGE,{"disambiguationData":[TD([subQ44])],"derivedFrom":makeQuery(id+"FyYUAefgu6xEfva_4.23.F14.boolean.opBoolean","SPLIT",EDGE,{"disambiguationData":[TD([subQ44])],"derivedFrom":makeQuery(id+"FyYUAefgu6xEfva_4.22.F14.boolean.opBoolean","SPLIT",EDGE,{"disambiguationData":[TD([subQ44])],"derivedFrom":makeQuery(id+"FyYUAefgu6xEfva_4.21.F14.boolean.opBoolean","SPLIT",EDGE,{"disambiguationData":[TD([subQ44])],"derivedFrom":makeQuery(id+"FyYUAefgu6xEfva_4.20.F14.boolean.opBoolean","SPLIT",EDGE,{"disambiguationData":[TD([subQ44])],"derivedFrom":makeQuery(id+"FyYUAefgu6xEfva_4.19.F14.boolean.opBoolean","SPLIT",EDGE,{"disambiguationData":[TD([subQ44])],"derivedFrom":makeQuery(id+"FyYUAefgu6xEfva_4.18.F14.boolean.opBoolean","SPLIT",EDGE,{"disambiguationData":[TD([subQ44])],"derivedFrom":makeQuery(id+"FyYUAefgu6xEfva_4.17.F14.boolean.opBoolean","SPLIT",EDGE,{"disambiguationData":[TD([subQ44])],"derivedFrom":makeQuery(id+"FyYUAefgu6xEfva_4.16.F14.boolean.opBoolean","SPLIT",EDGE,{"disambiguationData":[TD([subQ44])],"derivedFrom":makeQuery(id+"FyYUAefgu6xEfva_4.15.F14.boolean.opBoolean","SPLIT",EDGE,{"disambiguationData":[TD([subQ44])],"derivedFrom":makeQuery(id+"FyYUAefgu6xEfva_4.14.F14.boolean.opBoolean","SPLIT",EDGE,{"disambiguationData":[TD([subQ44])],"derivedFrom":makeQuery(id+"FyYUAefgu6xEfva_4.13.F14.boolean.opBoolean","SPLIT",EDGE,{"disambiguationData":[TD([subQ44])],"derivedFrom":makeQuery(id+"FyYUAefgu6xEfva_4.12.F14.boolean.opBoolean","SPLIT",EDGE,{"disambiguationData":[TD([subQ44])],"derivedFrom":makeQuery(id+"FyYUAefgu6xEfva_4.11.F14.boolean.opBoolean","SPLIT",EDGE,{"disambiguationData":[TD([subQ44])],"derivedFrom":makeQuery(id+"FyYUAefgu6xEfva_4.10.F14.boolean.opBoolean","SPLIT",EDGE,{"disambiguationData":[TD([subQ44])],"derivedFrom":makeQuery(id+"FyYUAefgu6xEfva_4.9.F14.boolean.opBoolean","SPLIT",EDGE,{"disambiguationData":[TD([subQ44])],"derivedFrom":makeQuery(id+"FyYUAefgu6xEfva_4.8.F14.boolean.opBoolean","SPLIT",EDGE,{"disambiguationData":[TD([subQ44])],"derivedFrom":makeQuery(id+"FyYUAefgu6xEfva_4.7.F14.boolean.opBoolean","SPLIT",EDGE,{"disambiguationData":[TD([subQ44])],"derivedFrom":makeQuery(id+"FyYUAefgu6xEfva_4.6.F14.boolean.opBoolean","SPLIT",EDGE,{"disambiguationData":[TD([subQ44])],"derivedFrom":makeQuery(id+"FyYUAefgu6xEfva_4.5.F14.boolean.opBoolean","SPLIT",EDGE,{"disambiguationData":[TD([subQ44])],"derivedFrom":makeQuery(id+"FyYUAefgu6xEfva_4.4.F14.boolean.opBoolean","SPLIT",EDGE,{"disambiguationData":[TD([subQ44])],"derivedFrom":makeQuery(id+"FyYUAefgu6xEfva_4.3.F14.boolean.opBoolean","SPLIT",EDGE,{"disambiguationData":[TD([subQ44])],"derivedFrom":makeQuery(id+"FyYUAefgu6xEfva_4.2.F14.boolean.opBoolean","SPLIT",EDGE,{"disambiguationData":[TD([subQ44])],"derivedFrom":makeQuery(id+"FyYUAefgu6xEfva_4.1.F14.boolean.opBoolean","SPLIT",EDGE,{"disambiguationData":[TD([subQ44])],"derivedFrom":makeQuery(id+"F12.opExtrude","CAP_EDGE",EDGE,{"disambiguationData":[OSD([subQ2])],"isStart":false})})})})})})})})})})})})})})})})})})})})})})})})})})})})})})})})})})})})})});}
            var Q105;
            {var subQ0=sQuery(id+"F9.wireOp",EDGE,"E142");var subQ3=sQuery(id+"F13.wireOp",EDGE,"E147");var subQ4=sQuery(id+"F13.wireOp",EDGE,"E148.MirrorCS");var subQ5=makeQuery(id+"FyYUAefgu6xEfva_4.36.F14.opExtrude","SWEPT_FACE",FACE,{"disambiguationData":[OSD([subQ4])]});var subQ6=makeQuery(id+"F14.opExtrude","SWEPT_FACE",FACE,{"disambiguationData":[OSD([subQ3])]});Q105=makeQuery(id+"FyYUAefgu6xEfva_4.37.F14.boolean.opBoolean","SPLIT",EDGE,{"disambiguationData":[TD([subQ5])],"derivedFrom":makeQuery(id+"FyYUAefgu6xEfva_4.36.F14.boolean.opBoolean","SPLIT",EDGE,{"disambiguationData":[TD([subQ6])],"derivedFrom":makeQuery(id+"FyYUAefgu6xEfva_4.35.F14.boolean.opBoolean","SPLIT",EDGE,{"disambiguationData":[TD([subQ6])],"derivedFrom":makeQuery(id+"FyYUAefgu6xEfva_4.34.F14.boolean.opBoolean","SPLIT",EDGE,{"disambiguationData":[TD([subQ6])],"derivedFrom":makeQuery(id+"FyYUAefgu6xEfva_4.33.F14.boolean.opBoolean","SPLIT",EDGE,{"disambiguationData":[TD([subQ6])],"derivedFrom":makeQuery(id+"FyYUAefgu6xEfva_4.32.F14.boolean.opBoolean","SPLIT",EDGE,{"disambiguationData":[TD([subQ6])],"derivedFrom":makeQuery(id+"FyYUAefgu6xEfva_4.31.F14.boolean.opBoolean","SPLIT",EDGE,{"disambiguationData":[TD([subQ6])],"derivedFrom":makeQuery(id+"FyYUAefgu6xEfva_4.30.F14.boolean.opBoolean","SPLIT",EDGE,{"disambiguationData":[TD([subQ6])],"derivedFrom":makeQuery(id+"FyYUAefgu6xEfva_4.29.F14.boolean.opBoolean","SPLIT",EDGE,{"disambiguationData":[TD([subQ6])],"derivedFrom":makeQuery(id+"FyYUAefgu6xEfva_4.28.F14.boolean.opBoolean","SPLIT",EDGE,{"disambiguationData":[TD([subQ6])],"derivedFrom":makeQuery(id+"FyYUAefgu6xEfva_4.27.F14.boolean.opBoolean","SPLIT",EDGE,{"disambiguationData":[TD([subQ6])],"derivedFrom":makeQuery(id+"FyYUAefgu6xEfva_4.26.F14.boolean.opBoolean","SPLIT",EDGE,{"disambiguationData":[TD([subQ6])],"derivedFrom":makeQuery(id+"FyYUAefgu6xEfva_4.25.F14.boolean.opBoolean","SPLIT",EDGE,{"disambiguationData":[TD([subQ6])],"derivedFrom":makeQuery(id+"FyYUAefgu6xEfva_4.24.F14.boolean.opBoolean","SPLIT",EDGE,{"disambiguationData":[TD([subQ6])],"derivedFrom":makeQuery(id+"FyYUAefgu6xEfva_4.23.F14.boolean.opBoolean","SPLIT",EDGE,{"disambiguationData":[TD([subQ6])],"derivedFrom":makeQuery(id+"FyYUAefgu6xEfva_4.22.F14.boolean.opBoolean","SPLIT",EDGE,{"disambiguationData":[TD([subQ6])],"derivedFrom":makeQuery(id+"FyYUAefgu6xEfva_4.21.F14.boolean.opBoolean","SPLIT",EDGE,{"disambiguationData":[TD([subQ6])],"derivedFrom":makeQuery(id+"FyYUAefgu6xEfva_4.20.F14.boolean.opBoolean","SPLIT",EDGE,{"disambiguationData":[TD([subQ6])],"derivedFrom":makeQuery(id+"FyYUAefgu6xEfva_4.19.F14.boolean.opBoolean","SPLIT",EDGE,{"disambiguationData":[TD([subQ6])],"derivedFrom":makeQuery(id+"FyYUAefgu6xEfva_4.18.F14.boolean.opBoolean","SPLIT",EDGE,{"disambiguationData":[TD([subQ6])],"derivedFrom":makeQuery(id+"FyYUAefgu6xEfva_4.17.F14.boolean.opBoolean","SPLIT",EDGE,{"disambiguationData":[TD([subQ6])],"derivedFrom":makeQuery(id+"FyYUAefgu6xEfva_4.16.F14.boolean.opBoolean","SPLIT",EDGE,{"disambiguationData":[TD([subQ6])],"derivedFrom":makeQuery(id+"FyYUAefgu6xEfva_4.15.F14.boolean.opBoolean","SPLIT",EDGE,{"disambiguationData":[TD([subQ6])],"derivedFrom":makeQuery(id+"FyYUAefgu6xEfva_4.14.F14.boolean.opBoolean","SPLIT",EDGE,{"disambiguationData":[TD([subQ6])],"derivedFrom":makeQuery(id+"FyYUAefgu6xEfva_4.13.F14.boolean.opBoolean","SPLIT",EDGE,{"disambiguationData":[TD([subQ6])],"derivedFrom":makeQuery(id+"FyYUAefgu6xEfva_4.12.F14.boolean.opBoolean","SPLIT",EDGE,{"disambiguationData":[TD([subQ6])],"derivedFrom":makeQuery(id+"FyYUAefgu6xEfva_4.11.F14.boolean.opBoolean","SPLIT",EDGE,{"disambiguationData":[TD([subQ6])],"derivedFrom":makeQuery(id+"FyYUAefgu6xEfva_4.10.F14.boolean.opBoolean","SPLIT",EDGE,{"disambiguationData":[TD([subQ6])],"derivedFrom":makeQuery(id+"FyYUAefgu6xEfva_4.9.F14.boolean.opBoolean","SPLIT",EDGE,{"disambiguationData":[TD([subQ6])],"derivedFrom":makeQuery(id+"FyYUAefgu6xEfva_4.8.F14.boolean.opBoolean","SPLIT",EDGE,{"disambiguationData":[TD([subQ6])],"derivedFrom":makeQuery(id+"FyYUAefgu6xEfva_4.7.F14.boolean.opBoolean","SPLIT",EDGE,{"disambiguationData":[TD([subQ6])],"derivedFrom":makeQuery(id+"FyYUAefgu6xEfva_4.6.F14.boolean.opBoolean","SPLIT",EDGE,{"disambiguationData":[TD([subQ6])],"derivedFrom":makeQuery(id+"FyYUAefgu6xEfva_4.5.F14.boolean.opBoolean","SPLIT",EDGE,{"disambiguationData":[TD([subQ6])],"derivedFrom":makeQuery(id+"FyYUAefgu6xEfva_4.4.F14.boolean.opBoolean","SPLIT",EDGE,{"disambiguationData":[TD([subQ6])],"derivedFrom":makeQuery(id+"FyYUAefgu6xEfva_4.3.F14.boolean.opBoolean","SPLIT",EDGE,{"disambiguationData":[TD([subQ6])],"derivedFrom":makeQuery(id+"FyYUAefgu6xEfva_4.2.F14.boolean.opBoolean","SPLIT",EDGE,{"disambiguationData":[TD([subQ6])],"derivedFrom":makeQuery(id+"FyYUAefgu6xEfva_4.1.F14.boolean.opBoolean","SPLIT",EDGE,{"disambiguationData":[TD([subQ6])],"derivedFrom":makeQuery(id+"F10.boolean.opBoolean","COPY",EDGE,{"derivedFrom":makeQuery(id+"F10.opExtrude","CAP_EDGE",EDGE,{"disambiguationData":[OSD([subQ0])],"isStart":false})})})})})})})})})})})})})})})})})})})})})})})})})})})})})})})})})})})})})})});}
            var Q106;
            Q106=makeQuery(id+"FyYUAefgu6xEfva_4.37.F14.opExtrude","CAP_EDGE",EDGE,{"disambiguationData":[OSD([sQuery(id+"F9.wireOp",EDGE,"E142")])],"isStart":false});
            var Q107;
            Q107=makeQuery(id+"FyYUAefgu6xEfva_4.37.F14.opExtrude","SWEPT_EDGE",EDGE,{"disambiguationData":[OSD([sQuery(id+"F11.wireOp",EDGE,"E143"),sQuery(id+"F13.wireOp",EDGE,"E148.MirrorCS")])]});
            var Q108;
            Q108=makeQuery(id+"FyYUAefgu6xEfva_4.37.F14.opExtrude","SWEPT_EDGE",EDGE,{"disambiguationData":[OSD([sQuery(id+"F9.wireOp",EDGE,"E142"),sQuery(id+"F13.wireOp",EDGE,"E148.MirrorCS")])]});
            var Q109;
            Q109=makeQuery(id+"FyYUAefgu6xEfva_4.37.F14.opExtrude","SWEPT_EDGE",EDGE,{"disambiguationData":[OSD([sQuery(id+"F9.wireOp",EDGE,"E142"),sQuery(id+"F13.wireOp",EDGE,"E147")])]});
            var Q110;
            Q110=makeQuery(id+"FyYUAefgu6xEfva_4.37.F14.opExtrude","CAP_EDGE",EDGE,{"disambiguationData":[OSD([sQuery(id+"F13.wireOp",EDGE,"E147")])],"isStart":false});
            var Q111;
            Q111=makeQuery(id+"FyYUAefgu6xEfva_4.36.F14.opExtrude","CAP_EDGE",EDGE,{"disambiguationData":[OSD([sQuery(id+"F9.wireOp",EDGE,"E142")])],"isStart":false});
            var Q112;
            Q112=makeQuery(id+"FyYUAefgu6xEfva_4.36.F14.opExtrude","SWEPT_EDGE",EDGE,{"disambiguationData":[OSD([sQuery(id+"F9.wireOp",EDGE,"E142"),sQuery(id+"F13.wireOp",EDGE,"E148.MirrorCS")])]});
            var Q113;
            Q113=makeQuery(id+"FyYUAefgu6xEfva_4.36.F14.opExtrude","SWEPT_EDGE",EDGE,{"disambiguationData":[OSD([sQuery(id+"F9.wireOp",EDGE,"E142"),sQuery(id+"F13.wireOp",EDGE,"E147")])]});
            var Q114;
            Q114=makeQuery(id+"FyYUAefgu6xEfva_4.36.F14.opExtrude","CAP_EDGE",EDGE,{"disambiguationData":[OSD([sQuery(id+"F13.wireOp",EDGE,"E148.MirrorCS")])],"isStart":false});
            var Q115;
            Q115=makeQuery(id+"FyYUAefgu6xEfva_4.36.F14.opExtrude","CAP_EDGE",EDGE,{"disambiguationData":[OSD([sQuery(id+"F13.wireOp",EDGE,"E147")])],"isStart":false});
            var Q116;
            {var subQ0=sQuery(id+"F13.wireOp",EDGE,"E148.MirrorCS");var subQ1=sQuery(id+"F13.wireOp",EDGE,"E147");var subQ2=sQuery(id+"F11.wireOp",EDGE,"E143");var subQ16=makeQuery(id+"FyYUAefgu6xEfva_4.40.F14.opExtrude","SWEPT_FACE",FACE,{"disambiguationData":[OSD([subQ0])]});var subQ48=makeQuery(id+"F14.opExtrude","SWEPT_FACE",FACE,{"disambiguationData":[OSD([subQ1])]});Q116=makeQuery(id+"FyYUAefgu6xEfva_4.41.F14.boolean.opBoolean","SPLIT",EDGE,{"disambiguationData":[TD([subQ16])],"derivedFrom":makeQuery(id+"FyYUAefgu6xEfva_4.40.F14.boolean.opBoolean","SPLIT",EDGE,{"disambiguationData":[TD([subQ48])],"derivedFrom":makeQuery(id+"FyYUAefgu6xEfva_4.39.F14.boolean.opBoolean","SPLIT",EDGE,{"disambiguationData":[TD([subQ48])],"derivedFrom":makeQuery(id+"FyYUAefgu6xEfva_4.38.F14.boolean.opBoolean","SPLIT",EDGE,{"disambiguationData":[TD([subQ48])],"derivedFrom":makeQuery(id+"FyYUAefgu6xEfva_4.37.F14.boolean.opBoolean","SPLIT",EDGE,{"disambiguationData":[TD([subQ48])],"derivedFrom":makeQuery(id+"FyYUAefgu6xEfva_4.36.F14.boolean.opBoolean","SPLIT",EDGE,{"disambiguationData":[TD([subQ48])],"derivedFrom":makeQuery(id+"FyYUAefgu6xEfva_4.35.F14.boolean.opBoolean","SPLIT",EDGE,{"disambiguationData":[TD([subQ48])],"derivedFrom":makeQuery(id+"FyYUAefgu6xEfva_4.34.F14.boolean.opBoolean","SPLIT",EDGE,{"disambiguationData":[TD([subQ48])],"derivedFrom":makeQuery(id+"FyYUAefgu6xEfva_4.33.F14.boolean.opBoolean","SPLIT",EDGE,{"disambiguationData":[TD([subQ48])],"derivedFrom":makeQuery(id+"FyYUAefgu6xEfva_4.32.F14.boolean.opBoolean","SPLIT",EDGE,{"disambiguationData":[TD([subQ48])],"derivedFrom":makeQuery(id+"FyYUAefgu6xEfva_4.31.F14.boolean.opBoolean","SPLIT",EDGE,{"disambiguationData":[TD([subQ48])],"derivedFrom":makeQuery(id+"FyYUAefgu6xEfva_4.30.F14.boolean.opBoolean","SPLIT",EDGE,{"disambiguationData":[TD([subQ48])],"derivedFrom":makeQuery(id+"FyYUAefgu6xEfva_4.29.F14.boolean.opBoolean","SPLIT",EDGE,{"disambiguationData":[TD([subQ48])],"derivedFrom":makeQuery(id+"FyYUAefgu6xEfva_4.28.F14.boolean.opBoolean","SPLIT",EDGE,{"disambiguationData":[TD([subQ48])],"derivedFrom":makeQuery(id+"FyYUAefgu6xEfva_4.27.F14.boolean.opBoolean","SPLIT",EDGE,{"disambiguationData":[TD([subQ48])],"derivedFrom":makeQuery(id+"FyYUAefgu6xEfva_4.26.F14.boolean.opBoolean","SPLIT",EDGE,{"disambiguationData":[TD([subQ48])],"derivedFrom":makeQuery(id+"FyYUAefgu6xEfva_4.25.F14.boolean.opBoolean","SPLIT",EDGE,{"disambiguationData":[TD([subQ48])],"derivedFrom":makeQuery(id+"FyYUAefgu6xEfva_4.24.F14.boolean.opBoolean","SPLIT",EDGE,{"disambiguationData":[TD([subQ48])],"derivedFrom":makeQuery(id+"FyYUAefgu6xEfva_4.23.F14.boolean.opBoolean","SPLIT",EDGE,{"disambiguationData":[TD([subQ48])],"derivedFrom":makeQuery(id+"FyYUAefgu6xEfva_4.22.F14.boolean.opBoolean","SPLIT",EDGE,{"disambiguationData":[TD([subQ48])],"derivedFrom":makeQuery(id+"FyYUAefgu6xEfva_4.21.F14.boolean.opBoolean","SPLIT",EDGE,{"disambiguationData":[TD([subQ48])],"derivedFrom":makeQuery(id+"FyYUAefgu6xEfva_4.20.F14.boolean.opBoolean","SPLIT",EDGE,{"disambiguationData":[TD([subQ48])],"derivedFrom":makeQuery(id+"FyYUAefgu6xEfva_4.19.F14.boolean.opBoolean","SPLIT",EDGE,{"disambiguationData":[TD([subQ48])],"derivedFrom":makeQuery(id+"FyYUAefgu6xEfva_4.18.F14.boolean.opBoolean","SPLIT",EDGE,{"disambiguationData":[TD([subQ48])],"derivedFrom":makeQuery(id+"FyYUAefgu6xEfva_4.17.F14.boolean.opBoolean","SPLIT",EDGE,{"disambiguationData":[TD([subQ48])],"derivedFrom":makeQuery(id+"FyYUAefgu6xEfva_4.16.F14.boolean.opBoolean","SPLIT",EDGE,{"disambiguationData":[TD([subQ48])],"derivedFrom":makeQuery(id+"FyYUAefgu6xEfva_4.15.F14.boolean.opBoolean","SPLIT",EDGE,{"disambiguationData":[TD([subQ48])],"derivedFrom":makeQuery(id+"FyYUAefgu6xEfva_4.14.F14.boolean.opBoolean","SPLIT",EDGE,{"disambiguationData":[TD([subQ48])],"derivedFrom":makeQuery(id+"FyYUAefgu6xEfva_4.13.F14.boolean.opBoolean","SPLIT",EDGE,{"disambiguationData":[TD([subQ48])],"derivedFrom":makeQuery(id+"FyYUAefgu6xEfva_4.12.F14.boolean.opBoolean","SPLIT",EDGE,{"disambiguationData":[TD([subQ48])],"derivedFrom":makeQuery(id+"FyYUAefgu6xEfva_4.11.F14.boolean.opBoolean","SPLIT",EDGE,{"disambiguationData":[TD([subQ48])],"derivedFrom":makeQuery(id+"FyYUAefgu6xEfva_4.10.F14.boolean.opBoolean","SPLIT",EDGE,{"disambiguationData":[TD([subQ48])],"derivedFrom":makeQuery(id+"FyYUAefgu6xEfva_4.9.F14.boolean.opBoolean","SPLIT",EDGE,{"disambiguationData":[TD([subQ48])],"derivedFrom":makeQuery(id+"FyYUAefgu6xEfva_4.8.F14.boolean.opBoolean","SPLIT",EDGE,{"disambiguationData":[TD([subQ48])],"derivedFrom":makeQuery(id+"FyYUAefgu6xEfva_4.7.F14.boolean.opBoolean","SPLIT",EDGE,{"disambiguationData":[TD([subQ48])],"derivedFrom":makeQuery(id+"FyYUAefgu6xEfva_4.6.F14.boolean.opBoolean","SPLIT",EDGE,{"disambiguationData":[TD([subQ48])],"derivedFrom":makeQuery(id+"FyYUAefgu6xEfva_4.5.F14.boolean.opBoolean","SPLIT",EDGE,{"disambiguationData":[TD([subQ48])],"derivedFrom":makeQuery(id+"FyYUAefgu6xEfva_4.4.F14.boolean.opBoolean","SPLIT",EDGE,{"disambiguationData":[TD([subQ48])],"derivedFrom":makeQuery(id+"FyYUAefgu6xEfva_4.3.F14.boolean.opBoolean","SPLIT",EDGE,{"disambiguationData":[TD([subQ48])],"derivedFrom":makeQuery(id+"FyYUAefgu6xEfva_4.2.F14.boolean.opBoolean","SPLIT",EDGE,{"disambiguationData":[TD([subQ48])],"derivedFrom":makeQuery(id+"FyYUAefgu6xEfva_4.1.F14.boolean.opBoolean","SPLIT",EDGE,{"disambiguationData":[TD([subQ48])],"derivedFrom":makeQuery(id+"F12.opExtrude","CAP_EDGE",EDGE,{"disambiguationData":[OSD([subQ2])],"isStart":false})})})})})})})})})})})})})})})})})})})})})})})})})})})})})})})})})})})})})})})})})});}
            var Q117;
            {var subQ0=sQuery(id+"F9.wireOp",EDGE,"E142");var subQ2=sQuery(id+"F13.wireOp",EDGE,"E148.MirrorCS");var subQ3=makeQuery(id+"FyYUAefgu6xEfva_4.40.F14.opExtrude","SWEPT_FACE",FACE,{"disambiguationData":[OSD([subQ2])]});var subQ5=sQuery(id+"F13.wireOp",EDGE,"E147");var subQ6=makeQuery(id+"F14.opExtrude","SWEPT_FACE",FACE,{"disambiguationData":[OSD([subQ5])]});Q117=makeQuery(id+"FyYUAefgu6xEfva_4.41.F14.boolean.opBoolean","SPLIT",EDGE,{"disambiguationData":[TD([subQ3])],"derivedFrom":makeQuery(id+"FyYUAefgu6xEfva_4.40.F14.boolean.opBoolean","SPLIT",EDGE,{"disambiguationData":[TD([subQ6])],"derivedFrom":makeQuery(id+"FyYUAefgu6xEfva_4.39.F14.boolean.opBoolean","SPLIT",EDGE,{"disambiguationData":[TD([subQ6])],"derivedFrom":makeQuery(id+"FyYUAefgu6xEfva_4.38.F14.boolean.opBoolean","SPLIT",EDGE,{"disambiguationData":[TD([subQ6])],"derivedFrom":makeQuery(id+"FyYUAefgu6xEfva_4.37.F14.boolean.opBoolean","SPLIT",EDGE,{"disambiguationData":[TD([subQ6])],"derivedFrom":makeQuery(id+"FyYUAefgu6xEfva_4.36.F14.boolean.opBoolean","SPLIT",EDGE,{"disambiguationData":[TD([subQ6])],"derivedFrom":makeQuery(id+"FyYUAefgu6xEfva_4.35.F14.boolean.opBoolean","SPLIT",EDGE,{"disambiguationData":[TD([subQ6])],"derivedFrom":makeQuery(id+"FyYUAefgu6xEfva_4.34.F14.boolean.opBoolean","SPLIT",EDGE,{"disambiguationData":[TD([subQ6])],"derivedFrom":makeQuery(id+"FyYUAefgu6xEfva_4.33.F14.boolean.opBoolean","SPLIT",EDGE,{"disambiguationData":[TD([subQ6])],"derivedFrom":makeQuery(id+"FyYUAefgu6xEfva_4.32.F14.boolean.opBoolean","SPLIT",EDGE,{"disambiguationData":[TD([subQ6])],"derivedFrom":makeQuery(id+"FyYUAefgu6xEfva_4.31.F14.boolean.opBoolean","SPLIT",EDGE,{"disambiguationData":[TD([subQ6])],"derivedFrom":makeQuery(id+"FyYUAefgu6xEfva_4.30.F14.boolean.opBoolean","SPLIT",EDGE,{"disambiguationData":[TD([subQ6])],"derivedFrom":makeQuery(id+"FyYUAefgu6xEfva_4.29.F14.boolean.opBoolean","SPLIT",EDGE,{"disambiguationData":[TD([subQ6])],"derivedFrom":makeQuery(id+"FyYUAefgu6xEfva_4.28.F14.boolean.opBoolean","SPLIT",EDGE,{"disambiguationData":[TD([subQ6])],"derivedFrom":makeQuery(id+"FyYUAefgu6xEfva_4.27.F14.boolean.opBoolean","SPLIT",EDGE,{"disambiguationData":[TD([subQ6])],"derivedFrom":makeQuery(id+"FyYUAefgu6xEfva_4.26.F14.boolean.opBoolean","SPLIT",EDGE,{"disambiguationData":[TD([subQ6])],"derivedFrom":makeQuery(id+"FyYUAefgu6xEfva_4.25.F14.boolean.opBoolean","SPLIT",EDGE,{"disambiguationData":[TD([subQ6])],"derivedFrom":makeQuery(id+"FyYUAefgu6xEfva_4.24.F14.boolean.opBoolean","SPLIT",EDGE,{"disambiguationData":[TD([subQ6])],"derivedFrom":makeQuery(id+"FyYUAefgu6xEfva_4.23.F14.boolean.opBoolean","SPLIT",EDGE,{"disambiguationData":[TD([subQ6])],"derivedFrom":makeQuery(id+"FyYUAefgu6xEfva_4.22.F14.boolean.opBoolean","SPLIT",EDGE,{"disambiguationData":[TD([subQ6])],"derivedFrom":makeQuery(id+"FyYUAefgu6xEfva_4.21.F14.boolean.opBoolean","SPLIT",EDGE,{"disambiguationData":[TD([subQ6])],"derivedFrom":makeQuery(id+"FyYUAefgu6xEfva_4.20.F14.boolean.opBoolean","SPLIT",EDGE,{"disambiguationData":[TD([subQ6])],"derivedFrom":makeQuery(id+"FyYUAefgu6xEfva_4.19.F14.boolean.opBoolean","SPLIT",EDGE,{"disambiguationData":[TD([subQ6])],"derivedFrom":makeQuery(id+"FyYUAefgu6xEfva_4.18.F14.boolean.opBoolean","SPLIT",EDGE,{"disambiguationData":[TD([subQ6])],"derivedFrom":makeQuery(id+"FyYUAefgu6xEfva_4.17.F14.boolean.opBoolean","SPLIT",EDGE,{"disambiguationData":[TD([subQ6])],"derivedFrom":makeQuery(id+"FyYUAefgu6xEfva_4.16.F14.boolean.opBoolean","SPLIT",EDGE,{"disambiguationData":[TD([subQ6])],"derivedFrom":makeQuery(id+"FyYUAefgu6xEfva_4.15.F14.boolean.opBoolean","SPLIT",EDGE,{"disambiguationData":[TD([subQ6])],"derivedFrom":makeQuery(id+"FyYUAefgu6xEfva_4.14.F14.boolean.opBoolean","SPLIT",EDGE,{"disambiguationData":[TD([subQ6])],"derivedFrom":makeQuery(id+"FyYUAefgu6xEfva_4.13.F14.boolean.opBoolean","SPLIT",EDGE,{"disambiguationData":[TD([subQ6])],"derivedFrom":makeQuery(id+"FyYUAefgu6xEfva_4.12.F14.boolean.opBoolean","SPLIT",EDGE,{"disambiguationData":[TD([subQ6])],"derivedFrom":makeQuery(id+"FyYUAefgu6xEfva_4.11.F14.boolean.opBoolean","SPLIT",EDGE,{"disambiguationData":[TD([subQ6])],"derivedFrom":makeQuery(id+"FyYUAefgu6xEfva_4.10.F14.boolean.opBoolean","SPLIT",EDGE,{"disambiguationData":[TD([subQ6])],"derivedFrom":makeQuery(id+"FyYUAefgu6xEfva_4.9.F14.boolean.opBoolean","SPLIT",EDGE,{"disambiguationData":[TD([subQ6])],"derivedFrom":makeQuery(id+"FyYUAefgu6xEfva_4.8.F14.boolean.opBoolean","SPLIT",EDGE,{"disambiguationData":[TD([subQ6])],"derivedFrom":makeQuery(id+"FyYUAefgu6xEfva_4.7.F14.boolean.opBoolean","SPLIT",EDGE,{"disambiguationData":[TD([subQ6])],"derivedFrom":makeQuery(id+"FyYUAefgu6xEfva_4.6.F14.boolean.opBoolean","SPLIT",EDGE,{"disambiguationData":[TD([subQ6])],"derivedFrom":makeQuery(id+"FyYUAefgu6xEfva_4.5.F14.boolean.opBoolean","SPLIT",EDGE,{"disambiguationData":[TD([subQ6])],"derivedFrom":makeQuery(id+"FyYUAefgu6xEfva_4.4.F14.boolean.opBoolean","SPLIT",EDGE,{"disambiguationData":[TD([subQ6])],"derivedFrom":makeQuery(id+"FyYUAefgu6xEfva_4.3.F14.boolean.opBoolean","SPLIT",EDGE,{"disambiguationData":[TD([subQ6])],"derivedFrom":makeQuery(id+"FyYUAefgu6xEfva_4.2.F14.boolean.opBoolean","SPLIT",EDGE,{"disambiguationData":[TD([subQ6])],"derivedFrom":makeQuery(id+"FyYUAefgu6xEfva_4.1.F14.boolean.opBoolean","SPLIT",EDGE,{"disambiguationData":[TD([subQ6])],"derivedFrom":makeQuery(id+"F10.boolean.opBoolean","COPY",EDGE,{"derivedFrom":makeQuery(id+"F10.opExtrude","CAP_EDGE",EDGE,{"disambiguationData":[OSD([subQ0])],"isStart":false})})})})})})})})})})})})})})})})})})})})})})})})})})})})})})})})})})})})})})})})})})});}
            var Q118;
            Q118=makeQuery(id+"FyYUAefgu6xEfva_4.41.F14.opExtrude","CAP_EDGE",EDGE,{"disambiguationData":[OSD([sQuery(id+"F9.wireOp",EDGE,"E142")])],"isStart":false});
            var Q119;
            Q119=makeQuery(id+"FyYUAefgu6xEfva_4.41.F14.opExtrude","CAP_EDGE",EDGE,{"disambiguationData":[OSD([sQuery(id+"F13.wireOp",EDGE,"E148.MirrorCS")])],"isStart":true});
            var Q120;
            Q120=makeQuery(id+"FyYUAefgu6xEfva_4.41.F14.opExtrude","CAP_EDGE",EDGE,{"disambiguationData":[OSD([sQuery(id+"F13.wireOp",EDGE,"E147")])],"isStart":true});
            var Q121;
            Q121=makeQuery(id+"FyYUAefgu6xEfva_4.41.F14.opExtrude","SWEPT_EDGE",EDGE,{"disambiguationData":[OSD([sQuery(id+"F11.wireOp",EDGE,"E143"),sQuery(id+"F13.wireOp",EDGE,"E148.MirrorCS")])]});
            var Q122;
            Q122=makeQuery(id+"FyYUAefgu6xEfva_4.41.F14.opExtrude","SWEPT_EDGE",EDGE,{"disambiguationData":[OSD([sQuery(id+"F9.wireOp",EDGE,"E142"),sQuery(id+"F13.wireOp",EDGE,"E148.MirrorCS")])]});
            var Q123;
            Q123=makeQuery(id+"FyYUAefgu6xEfva_4.41.F14.opExtrude","SWEPT_EDGE",EDGE,{"disambiguationData":[OSD([sQuery(id+"F11.wireOp",EDGE,"E143"),sQuery(id+"F13.wireOp",EDGE,"E147")])]});
            var Q124;
            Q124=makeQuery(id+"FyYUAefgu6xEfva_4.41.F14.opExtrude","SWEPT_EDGE",EDGE,{"disambiguationData":[OSD([sQuery(id+"F9.wireOp",EDGE,"E142"),sQuery(id+"F13.wireOp",EDGE,"E147")])]});
            var Q125;
            {var subQ1=sQuery(id+"F11.wireOp",EDGE,"E143");var subQ3=sQuery(id+"F13.wireOp",EDGE,"E147");var subQ4=sQuery(id+"F13.wireOp",EDGE,"E148.MirrorCS");var subQ5=makeQuery(id+"FyYUAefgu6xEfva_4.2.F14.opExtrude","SWEPT_FACE",FACE,{"disambiguationData":[OSD([subQ4])]});var subQ6=makeQuery(id+"F14.opExtrude","SWEPT_FACE",FACE,{"disambiguationData":[OSD([subQ3])]});Q125=makeQuery(id+"FyYUAefgu6xEfva_4.3.F14.boolean.opBoolean","SPLIT",EDGE,{"disambiguationData":[TD([subQ5])],"derivedFrom":makeQuery(id+"FyYUAefgu6xEfva_4.2.F14.boolean.opBoolean","SPLIT",EDGE,{"disambiguationData":[TD([subQ6])],"derivedFrom":makeQuery(id+"FyYUAefgu6xEfva_4.1.F14.boolean.opBoolean","SPLIT",EDGE,{"disambiguationData":[TD([subQ6])],"derivedFrom":makeQuery(id+"F12.opExtrude","CAP_EDGE",EDGE,{"disambiguationData":[OSD([subQ1])],"isStart":true})})})});}
            var Q126;
            {var subQ0=sQuery(id+"F13.wireOp",EDGE,"E148.MirrorCS");var subQ1=sQuery(id+"F13.wireOp",EDGE,"E147");var subQ2=sQuery(id+"F11.wireOp",EDGE,"E143");var subQ7=makeQuery(id+"FyYUAefgu6xEfva_4.2.F14.opExtrude","SWEPT_FACE",FACE,{"disambiguationData":[OSD([subQ0])]});var subQ10=makeQuery(id+"F14.opExtrude","SWEPT_FACE",FACE,{"disambiguationData":[OSD([subQ1])]});Q126=makeQuery(id+"FyYUAefgu6xEfva_4.3.F14.boolean.opBoolean","SPLIT",EDGE,{"disambiguationData":[TD([subQ7])],"derivedFrom":makeQuery(id+"FyYUAefgu6xEfva_4.2.F14.boolean.opBoolean","SPLIT",EDGE,{"disambiguationData":[TD([subQ10])],"derivedFrom":makeQuery(id+"FyYUAefgu6xEfva_4.1.F14.boolean.opBoolean","SPLIT",EDGE,{"disambiguationData":[TD([subQ10])],"derivedFrom":makeQuery(id+"F12.opExtrude","CAP_EDGE",EDGE,{"disambiguationData":[OSD([subQ2])],"isStart":false})})})});}
            var Q127;
            {var subQ0=sQuery(id+"F9.wireOp",EDGE,"E142");var subQ3=sQuery(id+"F13.wireOp",EDGE,"E148.MirrorCS");var subQ4=makeQuery(id+"FyYUAefgu6xEfva_4.2.F14.opExtrude","SWEPT_FACE",FACE,{"disambiguationData":[OSD([subQ3])]});var subQ5=sQuery(id+"F13.wireOp",EDGE,"E147");var subQ6=makeQuery(id+"F14.opExtrude","SWEPT_FACE",FACE,{"disambiguationData":[OSD([subQ5])]});Q127=makeQuery(id+"FyYUAefgu6xEfva_4.3.F14.boolean.opBoolean","SPLIT",EDGE,{"disambiguationData":[TD([subQ4])],"derivedFrom":makeQuery(id+"FyYUAefgu6xEfva_4.2.F14.boolean.opBoolean","SPLIT",EDGE,{"disambiguationData":[TD([subQ6])],"derivedFrom":makeQuery(id+"FyYUAefgu6xEfva_4.1.F14.boolean.opBoolean","SPLIT",EDGE,{"disambiguationData":[TD([subQ6])],"derivedFrom":makeQuery(id+"F10.boolean.opBoolean","COPY",EDGE,{"derivedFrom":makeQuery(id+"F10.opExtrude","CAP_EDGE",EDGE,{"disambiguationData":[OSD([subQ0])],"isStart":false})})})})});}
            var Q128;
            Q128=makeQuery(id+"FyYUAefgu6xEfva_4.3.F14.opExtrude","CAP_EDGE",EDGE,{"disambiguationData":[OSD([sQuery(id+"F13.wireOp",EDGE,"E148.MirrorCS")])],"isStart":true});
            var Q129;
            Q129=makeQuery(id+"FyYUAefgu6xEfva_4.3.F14.opExtrude","CAP_EDGE",EDGE,{"disambiguationData":[OSD([sQuery(id+"F13.wireOp",EDGE,"E147")])],"isStart":true});
            var Q130;
            Q130=makeQuery(id+"FyYUAefgu6xEfva_4.3.F14.opExtrude","SWEPT_EDGE",EDGE,{"disambiguationData":[OSD([sQuery(id+"F11.wireOp",EDGE,"E143"),sQuery(id+"F13.wireOp",EDGE,"E148.MirrorCS")])]});
            var Q131;
            Q131=makeQuery(id+"FyYUAefgu6xEfva_4.3.F14.opExtrude","SWEPT_EDGE",EDGE,{"disambiguationData":[OSD([sQuery(id+"F9.wireOp",EDGE,"E142"),sQuery(id+"F13.wireOp",EDGE,"E148.MirrorCS")])]});
            var Q132;
            Q132=makeQuery(id+"FyYUAefgu6xEfva_4.3.F14.opExtrude","SWEPT_EDGE",EDGE,{"disambiguationData":[OSD([sQuery(id+"F11.wireOp",EDGE,"E143"),sQuery(id+"F13.wireOp",EDGE,"E147")])]});
            var Q133;
            Q133=makeQuery(id+"FyYUAefgu6xEfva_4.3.F14.opExtrude","SWEPT_EDGE",EDGE,{"disambiguationData":[OSD([sQuery(id+"F9.wireOp",EDGE,"E142"),sQuery(id+"F13.wireOp",EDGE,"E147")])]});
            var Q134;
            {var subQ0=sQuery(id+"F13.wireOp",EDGE,"E148.MirrorCS");var subQ1=sQuery(id+"F13.wireOp",EDGE,"E147");var subQ2=sQuery(id+"F11.wireOp",EDGE,"E143");var subQ8=makeQuery(id+"FyYUAefgu6xEfva_4.1.F14.opExtrude","SWEPT_FACE",FACE,{"disambiguationData":[OSD([subQ0])]});Q134=makeQuery(id+"FyYUAefgu6xEfva_4.2.F14.boolean.opBoolean","SPLIT",EDGE,{"disambiguationData":[TD([subQ8])],"derivedFrom":makeQuery(id+"FyYUAefgu6xEfva_4.1.F14.boolean.opBoolean","SPLIT",EDGE,{"disambiguationData":[TD([makeQuery(id+"F14.opExtrude","SWEPT_FACE",FACE,{"disambiguationData":[OSD([subQ1])]})])],"derivedFrom":makeQuery(id+"F12.opExtrude","CAP_EDGE",EDGE,{"disambiguationData":[OSD([subQ2])],"isStart":false})})});}
            var Q135;
            {var subQ0=sQuery(id+"F9.wireOp",EDGE,"E142");var subQ3=sQuery(id+"F13.wireOp",EDGE,"E147");var subQ4=makeQuery(id+"FyYUAefgu6xEfva_4.1.F14.opExtrude","SWEPT_FACE",FACE,{"disambiguationData":[OSD([sQuery(id+"F13.wireOp",EDGE,"E148.MirrorCS")])]});Q135=makeQuery(id+"FyYUAefgu6xEfva_4.2.F14.boolean.opBoolean","SPLIT",EDGE,{"disambiguationData":[TD([subQ4])],"derivedFrom":makeQuery(id+"FyYUAefgu6xEfva_4.1.F14.boolean.opBoolean","SPLIT",EDGE,{"disambiguationData":[TD([makeQuery(id+"F14.opExtrude","SWEPT_FACE",FACE,{"disambiguationData":[OSD([subQ3])]})])],"derivedFrom":makeQuery(id+"F10.boolean.opBoolean","COPY",EDGE,{"derivedFrom":makeQuery(id+"F10.opExtrude","CAP_EDGE",EDGE,{"disambiguationData":[OSD([subQ0])],"isStart":false})})})});}
            var Q136;
            Q136=makeQuery(id+"FyYUAefgu6xEfva_4.2.F14.opExtrude","CAP_EDGE",EDGE,{"disambiguationData":[OSD([sQuery(id+"F9.wireOp",EDGE,"E142")])],"isStart":false});
            var Q137;
            Q137=makeQuery(id+"FyYUAefgu6xEfva_4.2.F14.opExtrude","CAP_EDGE",EDGE,{"disambiguationData":[OSD([sQuery(id+"F13.wireOp",EDGE,"E148.MirrorCS")])],"isStart":true});
            var Q138;
            Q138=makeQuery(id+"FyYUAefgu6xEfva_4.2.F14.opExtrude","SWEPT_EDGE",EDGE,{"disambiguationData":[OSD([sQuery(id+"F11.wireOp",EDGE,"E143"),sQuery(id+"F13.wireOp",EDGE,"E148.MirrorCS")])]});
            var Q139;
            Q139=makeQuery(id+"FyYUAefgu6xEfva_4.2.F14.opExtrude","SWEPT_EDGE",EDGE,{"disambiguationData":[OSD([sQuery(id+"F9.wireOp",EDGE,"E142"),sQuery(id+"F13.wireOp",EDGE,"E148.MirrorCS")])]});
            var Q140;
            Q140=makeQuery(id+"FyYUAefgu6xEfva_4.2.F14.opExtrude","SWEPT_EDGE",EDGE,{"disambiguationData":[OSD([sQuery(id+"F11.wireOp",EDGE,"E143"),sQuery(id+"F13.wireOp",EDGE,"E147")])]});
            var Q141;
            Q141=makeQuery(id+"FyYUAefgu6xEfva_4.2.F14.opExtrude","SWEPT_EDGE",EDGE,{"disambiguationData":[OSD([sQuery(id+"F9.wireOp",EDGE,"E142"),sQuery(id+"F13.wireOp",EDGE,"E147")])]});
            var Q142;
            Q142=makeQuery(id+"FyYUAefgu6xEfva_4.40.F14.opExtrude","SWEPT_EDGE",EDGE,{"disambiguationData":[OSD([sQuery(id+"F9.wireOp",EDGE,"E142"),sQuery(id+"F13.wireOp",EDGE,"E148.MirrorCS")])]});
            var Q143;
            {var subQ0=sQuery(id+"F9.wireOp",EDGE,"E142");Q143=makeQuery(id+"FyYUAefgu6xEfva_4.1.F14.boolean.opBoolean","SPLIT",EDGE,{"disambiguationData":[TD([makeQuery(id+"F14.opExtrude","SWEPT_FACE",FACE,{"disambiguationData":[OSD([sQuery(id+"F13.wireOp",EDGE,"E148.MirrorCS")])]})])],"derivedFrom":makeQuery(id+"F10.boolean.opBoolean","COPY",EDGE,{"derivedFrom":makeQuery(id+"F10.opExtrude","CAP_EDGE",EDGE,{"disambiguationData":[OSD([subQ0])],"isStart":false})})});}
            var Q144;
            Q144=makeQuery(id+"FyYUAefgu6xEfva_4.1.F14.opExtrude","CAP_EDGE",EDGE,{"disambiguationData":[OSD([sQuery(id+"F9.wireOp",EDGE,"E142")])],"isStart":false});
            var Q145;
            Q145=makeQuery(id+"FyYUAefgu6xEfva_4.40.F14.opExtrude","SWEPT_EDGE",EDGE,{"disambiguationData":[OSD([sQuery(id+"F9.wireOp",EDGE,"E142"),sQuery(id+"F13.wireOp",EDGE,"E147")])]});
            var Q146;
            Q146=makeQuery(id+"FyYUAefgu6xEfva_4.40.F14.opExtrude","CAP_EDGE",EDGE,{"disambiguationData":[OSD([sQuery(id+"F13.wireOp",EDGE,"E147")])],"isStart":false});
            var Q147;
            {var subQ0=sQuery(id+"F9.wireOp",EDGE,"E142");var subQ2=sQuery(id+"F13.wireOp",EDGE,"E147");var subQ4=sQuery(id+"F13.wireOp",EDGE,"E148.MirrorCS");var subQ5=makeQuery(id+"FyYUAefgu6xEfva_4.38.F14.opExtrude","SWEPT_FACE",FACE,{"disambiguationData":[OSD([subQ4])]});var subQ6=makeQuery(id+"F14.opExtrude","SWEPT_FACE",FACE,{"disambiguationData":[OSD([subQ2])]});Q147=makeQuery(id+"FyYUAefgu6xEfva_4.39.F14.boolean.opBoolean","SPLIT",EDGE,{"disambiguationData":[TD([subQ5])],"derivedFrom":makeQuery(id+"FyYUAefgu6xEfva_4.38.F14.boolean.opBoolean","SPLIT",EDGE,{"disambiguationData":[TD([subQ6])],"derivedFrom":makeQuery(id+"FyYUAefgu6xEfva_4.37.F14.boolean.opBoolean","SPLIT",EDGE,{"disambiguationData":[TD([subQ6])],"derivedFrom":makeQuery(id+"FyYUAefgu6xEfva_4.36.F14.boolean.opBoolean","SPLIT",EDGE,{"disambiguationData":[TD([subQ6])],"derivedFrom":makeQuery(id+"FyYUAefgu6xEfva_4.35.F14.boolean.opBoolean","SPLIT",EDGE,{"disambiguationData":[TD([subQ6])],"derivedFrom":makeQuery(id+"FyYUAefgu6xEfva_4.34.F14.boolean.opBoolean","SPLIT",EDGE,{"disambiguationData":[TD([subQ6])],"derivedFrom":makeQuery(id+"FyYUAefgu6xEfva_4.33.F14.boolean.opBoolean","SPLIT",EDGE,{"disambiguationData":[TD([subQ6])],"derivedFrom":makeQuery(id+"FyYUAefgu6xEfva_4.32.F14.boolean.opBoolean","SPLIT",EDGE,{"disambiguationData":[TD([subQ6])],"derivedFrom":makeQuery(id+"FyYUAefgu6xEfva_4.31.F14.boolean.opBoolean","SPLIT",EDGE,{"disambiguationData":[TD([subQ6])],"derivedFrom":makeQuery(id+"FyYUAefgu6xEfva_4.30.F14.boolean.opBoolean","SPLIT",EDGE,{"disambiguationData":[TD([subQ6])],"derivedFrom":makeQuery(id+"FyYUAefgu6xEfva_4.29.F14.boolean.opBoolean","SPLIT",EDGE,{"disambiguationData":[TD([subQ6])],"derivedFrom":makeQuery(id+"FyYUAefgu6xEfva_4.28.F14.boolean.opBoolean","SPLIT",EDGE,{"disambiguationData":[TD([subQ6])],"derivedFrom":makeQuery(id+"FyYUAefgu6xEfva_4.27.F14.boolean.opBoolean","SPLIT",EDGE,{"disambiguationData":[TD([subQ6])],"derivedFrom":makeQuery(id+"FyYUAefgu6xEfva_4.26.F14.boolean.opBoolean","SPLIT",EDGE,{"disambiguationData":[TD([subQ6])],"derivedFrom":makeQuery(id+"FyYUAefgu6xEfva_4.25.F14.boolean.opBoolean","SPLIT",EDGE,{"disambiguationData":[TD([subQ6])],"derivedFrom":makeQuery(id+"FyYUAefgu6xEfva_4.24.F14.boolean.opBoolean","SPLIT",EDGE,{"disambiguationData":[TD([subQ6])],"derivedFrom":makeQuery(id+"FyYUAefgu6xEfva_4.23.F14.boolean.opBoolean","SPLIT",EDGE,{"disambiguationData":[TD([subQ6])],"derivedFrom":makeQuery(id+"FyYUAefgu6xEfva_4.22.F14.boolean.opBoolean","SPLIT",EDGE,{"disambiguationData":[TD([subQ6])],"derivedFrom":makeQuery(id+"FyYUAefgu6xEfva_4.21.F14.boolean.opBoolean","SPLIT",EDGE,{"disambiguationData":[TD([subQ6])],"derivedFrom":makeQuery(id+"FyYUAefgu6xEfva_4.20.F14.boolean.opBoolean","SPLIT",EDGE,{"disambiguationData":[TD([subQ6])],"derivedFrom":makeQuery(id+"FyYUAefgu6xEfva_4.19.F14.boolean.opBoolean","SPLIT",EDGE,{"disambiguationData":[TD([subQ6])],"derivedFrom":makeQuery(id+"FyYUAefgu6xEfva_4.18.F14.boolean.opBoolean","SPLIT",EDGE,{"disambiguationData":[TD([subQ6])],"derivedFrom":makeQuery(id+"FyYUAefgu6xEfva_4.17.F14.boolean.opBoolean","SPLIT",EDGE,{"disambiguationData":[TD([subQ6])],"derivedFrom":makeQuery(id+"FyYUAefgu6xEfva_4.16.F14.boolean.opBoolean","SPLIT",EDGE,{"disambiguationData":[TD([subQ6])],"derivedFrom":makeQuery(id+"FyYUAefgu6xEfva_4.15.F14.boolean.opBoolean","SPLIT",EDGE,{"disambiguationData":[TD([subQ6])],"derivedFrom":makeQuery(id+"FyYUAefgu6xEfva_4.14.F14.boolean.opBoolean","SPLIT",EDGE,{"disambiguationData":[TD([subQ6])],"derivedFrom":makeQuery(id+"FyYUAefgu6xEfva_4.13.F14.boolean.opBoolean","SPLIT",EDGE,{"disambiguationData":[TD([subQ6])],"derivedFrom":makeQuery(id+"FyYUAefgu6xEfva_4.12.F14.boolean.opBoolean","SPLIT",EDGE,{"disambiguationData":[TD([subQ6])],"derivedFrom":makeQuery(id+"FyYUAefgu6xEfva_4.11.F14.boolean.opBoolean","SPLIT",EDGE,{"disambiguationData":[TD([subQ6])],"derivedFrom":makeQuery(id+"FyYUAefgu6xEfva_4.10.F14.boolean.opBoolean","SPLIT",EDGE,{"disambiguationData":[TD([subQ6])],"derivedFrom":makeQuery(id+"FyYUAefgu6xEfva_4.9.F14.boolean.opBoolean","SPLIT",EDGE,{"disambiguationData":[TD([subQ6])],"derivedFrom":makeQuery(id+"FyYUAefgu6xEfva_4.8.F14.boolean.opBoolean","SPLIT",EDGE,{"disambiguationData":[TD([subQ6])],"derivedFrom":makeQuery(id+"FyYUAefgu6xEfva_4.7.F14.boolean.opBoolean","SPLIT",EDGE,{"disambiguationData":[TD([subQ6])],"derivedFrom":makeQuery(id+"FyYUAefgu6xEfva_4.6.F14.boolean.opBoolean","SPLIT",EDGE,{"disambiguationData":[TD([subQ6])],"derivedFrom":makeQuery(id+"FyYUAefgu6xEfva_4.5.F14.boolean.opBoolean","SPLIT",EDGE,{"disambiguationData":[TD([subQ6])],"derivedFrom":makeQuery(id+"FyYUAefgu6xEfva_4.4.F14.boolean.opBoolean","SPLIT",EDGE,{"disambiguationData":[TD([subQ6])],"derivedFrom":makeQuery(id+"FyYUAefgu6xEfva_4.3.F14.boolean.opBoolean","SPLIT",EDGE,{"disambiguationData":[TD([subQ6])],"derivedFrom":makeQuery(id+"FyYUAefgu6xEfva_4.2.F14.boolean.opBoolean","SPLIT",EDGE,{"disambiguationData":[TD([subQ6])],"derivedFrom":makeQuery(id+"FyYUAefgu6xEfva_4.1.F14.boolean.opBoolean","SPLIT",EDGE,{"disambiguationData":[TD([subQ6])],"derivedFrom":makeQuery(id+"F10.boolean.opBoolean","COPY",EDGE,{"derivedFrom":makeQuery(id+"F10.opExtrude","CAP_EDGE",EDGE,{"disambiguationData":[OSD([subQ0])],"isStart":false})})})})})})})})})})})})})})})})})})})})})})})})})})})})})})})})})})})})})})})})});}
            var Q148;
            Q148=makeQuery(id+"FyYUAefgu6xEfva_4.1.F14.opExtrude","CAP_EDGE",EDGE,{"disambiguationData":[OSD([sQuery(id+"F13.wireOp",EDGE,"E148.MirrorCS")])],"isStart":true});
            var Q149;
            Q149=makeQuery(id+"FyYUAefgu6xEfva_4.1.F14.opExtrude","CAP_EDGE",EDGE,{"disambiguationData":[OSD([sQuery(id+"F13.wireOp",EDGE,"E147")])],"isStart":true});
            var Q150;
            Q150=makeQuery(id+"FyYUAefgu6xEfva_4.1.F14.opExtrude","SWEPT_EDGE",EDGE,{"disambiguationData":[OSD([sQuery(id+"F11.wireOp",EDGE,"E143"),sQuery(id+"F13.wireOp",EDGE,"E148.MirrorCS")])]});
            var Q151;
            Q151=makeQuery(id+"FyYUAefgu6xEfva_4.1.F14.opExtrude","SWEPT_EDGE",EDGE,{"disambiguationData":[OSD([sQuery(id+"F9.wireOp",EDGE,"E142"),sQuery(id+"F13.wireOp",EDGE,"E148.MirrorCS")])]});
            var Q152;
            Q152=makeQuery(id+"FyYUAefgu6xEfva_4.1.F14.opExtrude","SWEPT_EDGE",EDGE,{"disambiguationData":[OSD([sQuery(id+"F11.wireOp",EDGE,"E143"),sQuery(id+"F13.wireOp",EDGE,"E147")])]});
            var Q153;
            Q153=makeQuery(id+"FyYUAefgu6xEfva_4.1.F14.opExtrude","SWEPT_EDGE",EDGE,{"disambiguationData":[OSD([sQuery(id+"F9.wireOp",EDGE,"E142"),sQuery(id+"F13.wireOp",EDGE,"E147")])]});
            var Q154;
            Q154=makeQuery(id+"FyYUAefgu6xEfva_4.1.F14.opExtrude","CAP_EDGE",EDGE,{"disambiguationData":[OSD([sQuery(id+"F13.wireOp",EDGE,"E148.MirrorCS")])],"isStart":false});
            var Q155;
            Q155=makeQuery(id+"FyYUAefgu6xEfva_4.1.F14.opExtrude","CAP_EDGE",EDGE,{"disambiguationData":[OSD([sQuery(id+"F13.wireOp",EDGE,"E147")])],"isStart":false});
            var Q156;
            {var subQ0=sQuery(id+"F13.wireOp",EDGE,"E148.MirrorCS");var subQ1=sQuery(id+"F13.wireOp",EDGE,"E147");var subQ2=sQuery(id+"F11.wireOp",EDGE,"E143");var subQ14=makeQuery(id+"FyYUAefgu6xEfva_4.7.F14.opExtrude","SWEPT_FACE",FACE,{"disambiguationData":[OSD([subQ0])]});var subQ15=makeQuery(id+"F14.opExtrude","SWEPT_FACE",FACE,{"disambiguationData":[OSD([subQ1])]});Q156=makeQuery(id+"FyYUAefgu6xEfva_4.8.F14.boolean.opBoolean","SPLIT",EDGE,{"disambiguationData":[TD([subQ14])],"derivedFrom":makeQuery(id+"FyYUAefgu6xEfva_4.7.F14.boolean.opBoolean","SPLIT",EDGE,{"disambiguationData":[TD([subQ15])],"derivedFrom":makeQuery(id+"FyYUAefgu6xEfva_4.6.F14.boolean.opBoolean","SPLIT",EDGE,{"disambiguationData":[TD([subQ15])],"derivedFrom":makeQuery(id+"FyYUAefgu6xEfva_4.5.F14.boolean.opBoolean","SPLIT",EDGE,{"disambiguationData":[TD([subQ15])],"derivedFrom":makeQuery(id+"FyYUAefgu6xEfva_4.4.F14.boolean.opBoolean","SPLIT",EDGE,{"disambiguationData":[TD([subQ15])],"derivedFrom":makeQuery(id+"FyYUAefgu6xEfva_4.3.F14.boolean.opBoolean","SPLIT",EDGE,{"disambiguationData":[TD([subQ15])],"derivedFrom":makeQuery(id+"FyYUAefgu6xEfva_4.2.F14.boolean.opBoolean","SPLIT",EDGE,{"disambiguationData":[TD([subQ15])],"derivedFrom":makeQuery(id+"FyYUAefgu6xEfva_4.1.F14.boolean.opBoolean","SPLIT",EDGE,{"disambiguationData":[TD([subQ15])],"derivedFrom":makeQuery(id+"F12.opExtrude","CAP_EDGE",EDGE,{"disambiguationData":[OSD([subQ2])],"isStart":false})})})})})})})})});}
            var Q157;
            {var subQ0=sQuery(id+"F9.wireOp",EDGE,"E142");var subQ3=sQuery(id+"F13.wireOp",EDGE,"E148.MirrorCS");var subQ4=makeQuery(id+"FyYUAefgu6xEfva_4.7.F14.opExtrude","SWEPT_FACE",FACE,{"disambiguationData":[OSD([subQ3])]});var subQ5=sQuery(id+"F13.wireOp",EDGE,"E147");var subQ6=makeQuery(id+"F14.opExtrude","SWEPT_FACE",FACE,{"disambiguationData":[OSD([subQ5])]});Q157=makeQuery(id+"FyYUAefgu6xEfva_4.8.F14.boolean.opBoolean","SPLIT",EDGE,{"disambiguationData":[TD([subQ4])],"derivedFrom":makeQuery(id+"FyYUAefgu6xEfva_4.7.F14.boolean.opBoolean","SPLIT",EDGE,{"disambiguationData":[TD([subQ6])],"derivedFrom":makeQuery(id+"FyYUAefgu6xEfva_4.6.F14.boolean.opBoolean","SPLIT",EDGE,{"disambiguationData":[TD([subQ6])],"derivedFrom":makeQuery(id+"FyYUAefgu6xEfva_4.5.F14.boolean.opBoolean","SPLIT",EDGE,{"disambiguationData":[TD([subQ6])],"derivedFrom":makeQuery(id+"FyYUAefgu6xEfva_4.4.F14.boolean.opBoolean","SPLIT",EDGE,{"disambiguationData":[TD([subQ6])],"derivedFrom":makeQuery(id+"FyYUAefgu6xEfva_4.3.F14.boolean.opBoolean","SPLIT",EDGE,{"disambiguationData":[TD([subQ6])],"derivedFrom":makeQuery(id+"FyYUAefgu6xEfva_4.2.F14.boolean.opBoolean","SPLIT",EDGE,{"disambiguationData":[TD([subQ6])],"derivedFrom":makeQuery(id+"FyYUAefgu6xEfva_4.1.F14.boolean.opBoolean","SPLIT",EDGE,{"disambiguationData":[TD([subQ6])],"derivedFrom":makeQuery(id+"F10.boolean.opBoolean","COPY",EDGE,{"derivedFrom":makeQuery(id+"F10.opExtrude","CAP_EDGE",EDGE,{"disambiguationData":[OSD([subQ0])],"isStart":false})})})})})})})})})});}
            var Q158;
            Q158=makeQuery(id+"FyYUAefgu6xEfva_4.8.F14.opExtrude","CAP_EDGE",EDGE,{"disambiguationData":[OSD([sQuery(id+"F9.wireOp",EDGE,"E142")])],"isStart":false});
            var Q159;
            Q159=makeQuery(id+"FyYUAefgu6xEfva_4.8.F14.opExtrude","SWEPT_EDGE",EDGE,{"disambiguationData":[OSD([sQuery(id+"F11.wireOp",EDGE,"E143"),sQuery(id+"F13.wireOp",EDGE,"E147")])]});
            var Q160;
            Q160=makeQuery(id+"FyYUAefgu6xEfva_4.8.F14.opExtrude","SWEPT_EDGE",EDGE,{"disambiguationData":[OSD([sQuery(id+"F9.wireOp",EDGE,"E142"),sQuery(id+"F13.wireOp",EDGE,"E147")])]});
            var Q161;
            {var subQ0=sQuery(id+"F13.wireOp",EDGE,"E148.MirrorCS");var subQ1=sQuery(id+"F13.wireOp",EDGE,"E147");var subQ2=sQuery(id+"F11.wireOp",EDGE,"E143");var subQ8=makeQuery(id+"FyYUAefgu6xEfva_4.6.F14.opExtrude","SWEPT_FACE",FACE,{"disambiguationData":[OSD([subQ0])]});var subQ14=makeQuery(id+"F14.opExtrude","SWEPT_FACE",FACE,{"disambiguationData":[OSD([subQ1])]});Q161=makeQuery(id+"FyYUAefgu6xEfva_4.7.F14.boolean.opBoolean","SPLIT",EDGE,{"disambiguationData":[TD([subQ8])],"derivedFrom":makeQuery(id+"FyYUAefgu6xEfva_4.6.F14.boolean.opBoolean","SPLIT",EDGE,{"disambiguationData":[TD([subQ14])],"derivedFrom":makeQuery(id+"FyYUAefgu6xEfva_4.5.F14.boolean.opBoolean","SPLIT",EDGE,{"disambiguationData":[TD([subQ14])],"derivedFrom":makeQuery(id+"FyYUAefgu6xEfva_4.4.F14.boolean.opBoolean","SPLIT",EDGE,{"disambiguationData":[TD([subQ14])],"derivedFrom":makeQuery(id+"FyYUAefgu6xEfva_4.3.F14.boolean.opBoolean","SPLIT",EDGE,{"disambiguationData":[TD([subQ14])],"derivedFrom":makeQuery(id+"FyYUAefgu6xEfva_4.2.F14.boolean.opBoolean","SPLIT",EDGE,{"disambiguationData":[TD([subQ14])],"derivedFrom":makeQuery(id+"FyYUAefgu6xEfva_4.1.F14.boolean.opBoolean","SPLIT",EDGE,{"disambiguationData":[TD([subQ14])],"derivedFrom":makeQuery(id+"F12.opExtrude","CAP_EDGE",EDGE,{"disambiguationData":[OSD([subQ2])],"isStart":false})})})})})})})});}
            var Q162;
            {var subQ0=sQuery(id+"F9.wireOp",EDGE,"E142");var subQ3=sQuery(id+"F13.wireOp",EDGE,"E147");var subQ4=sQuery(id+"F13.wireOp",EDGE,"E148.MirrorCS");var subQ5=makeQuery(id+"FyYUAefgu6xEfva_4.6.F14.opExtrude","SWEPT_FACE",FACE,{"disambiguationData":[OSD([subQ4])]});var subQ6=makeQuery(id+"F14.opExtrude","SWEPT_FACE",FACE,{"disambiguationData":[OSD([subQ3])]});Q162=makeQuery(id+"FyYUAefgu6xEfva_4.7.F14.boolean.opBoolean","SPLIT",EDGE,{"disambiguationData":[TD([subQ5])],"derivedFrom":makeQuery(id+"FyYUAefgu6xEfva_4.6.F14.boolean.opBoolean","SPLIT",EDGE,{"disambiguationData":[TD([subQ6])],"derivedFrom":makeQuery(id+"FyYUAefgu6xEfva_4.5.F14.boolean.opBoolean","SPLIT",EDGE,{"disambiguationData":[TD([subQ6])],"derivedFrom":makeQuery(id+"FyYUAefgu6xEfva_4.4.F14.boolean.opBoolean","SPLIT",EDGE,{"disambiguationData":[TD([subQ6])],"derivedFrom":makeQuery(id+"FyYUAefgu6xEfva_4.3.F14.boolean.opBoolean","SPLIT",EDGE,{"disambiguationData":[TD([subQ6])],"derivedFrom":makeQuery(id+"FyYUAefgu6xEfva_4.2.F14.boolean.opBoolean","SPLIT",EDGE,{"disambiguationData":[TD([subQ6])],"derivedFrom":makeQuery(id+"FyYUAefgu6xEfva_4.1.F14.boolean.opBoolean","SPLIT",EDGE,{"disambiguationData":[TD([subQ6])],"derivedFrom":makeQuery(id+"F10.boolean.opBoolean","COPY",EDGE,{"derivedFrom":makeQuery(id+"F10.opExtrude","CAP_EDGE",EDGE,{"disambiguationData":[OSD([subQ0])],"isStart":false})})})})})})})})});}
            var Q163;
            Q163=makeQuery(id+"FyYUAefgu6xEfva_4.7.F14.opExtrude","CAP_EDGE",EDGE,{"disambiguationData":[OSD([sQuery(id+"F9.wireOp",EDGE,"E142")])],"isStart":false});
            var Q164;
            Q164=makeQuery(id+"FyYUAefgu6xEfva_4.7.F14.opExtrude","CAP_EDGE",EDGE,{"disambiguationData":[OSD([sQuery(id+"F13.wireOp",EDGE,"E148.MirrorCS")])],"isStart":true});
            var Q165;
            Q165=makeQuery(id+"FyYUAefgu6xEfva_4.7.F14.opExtrude","CAP_EDGE",EDGE,{"disambiguationData":[OSD([sQuery(id+"F13.wireOp",EDGE,"E147")])],"isStart":true});
            var Q166;
            Q166=makeQuery(id+"FyYUAefgu6xEfva_4.7.F14.opExtrude","SWEPT_EDGE",EDGE,{"disambiguationData":[OSD([sQuery(id+"F11.wireOp",EDGE,"E143"),sQuery(id+"F13.wireOp",EDGE,"E148.MirrorCS")])]});
            var Q167;
            Q167=makeQuery(id+"FyYUAefgu6xEfva_4.7.F14.opExtrude","SWEPT_EDGE",EDGE,{"disambiguationData":[OSD([sQuery(id+"F11.wireOp",EDGE,"E143"),sQuery(id+"F13.wireOp",EDGE,"E147")])]});
            var Q168;
            Q168=makeQuery(id+"FyYUAefgu6xEfva_4.7.F14.opExtrude","SWEPT_EDGE",EDGE,{"disambiguationData":[OSD([sQuery(id+"F9.wireOp",EDGE,"E142"),sQuery(id+"F13.wireOp",EDGE,"E147")])]});
            var Q169;
            {var subQ0=sQuery(id+"F13.wireOp",EDGE,"E148.MirrorCS");var subQ1=sQuery(id+"F13.wireOp",EDGE,"E147");var subQ2=sQuery(id+"F11.wireOp",EDGE,"E143");var subQ26=makeQuery(id+"FyYUAefgu6xEfva_4.38.F14.opExtrude","SWEPT_FACE",FACE,{"disambiguationData":[OSD([subQ0])]});var subQ46=makeQuery(id+"F14.opExtrude","SWEPT_FACE",FACE,{"disambiguationData":[OSD([subQ1])]});Q169=makeQuery(id+"FyYUAefgu6xEfva_4.39.F14.boolean.opBoolean","SPLIT",EDGE,{"disambiguationData":[TD([subQ26])],"derivedFrom":makeQuery(id+"FyYUAefgu6xEfva_4.38.F14.boolean.opBoolean","SPLIT",EDGE,{"disambiguationData":[TD([subQ46])],"derivedFrom":makeQuery(id+"FyYUAefgu6xEfva_4.37.F14.boolean.opBoolean","SPLIT",EDGE,{"disambiguationData":[TD([subQ46])],"derivedFrom":makeQuery(id+"FyYUAefgu6xEfva_4.36.F14.boolean.opBoolean","SPLIT",EDGE,{"disambiguationData":[TD([subQ46])],"derivedFrom":makeQuery(id+"FyYUAefgu6xEfva_4.35.F14.boolean.opBoolean","SPLIT",EDGE,{"disambiguationData":[TD([subQ46])],"derivedFrom":makeQuery(id+"FyYUAefgu6xEfva_4.34.F14.boolean.opBoolean","SPLIT",EDGE,{"disambiguationData":[TD([subQ46])],"derivedFrom":makeQuery(id+"FyYUAefgu6xEfva_4.33.F14.boolean.opBoolean","SPLIT",EDGE,{"disambiguationData":[TD([subQ46])],"derivedFrom":makeQuery(id+"FyYUAefgu6xEfva_4.32.F14.boolean.opBoolean","SPLIT",EDGE,{"disambiguationData":[TD([subQ46])],"derivedFrom":makeQuery(id+"FyYUAefgu6xEfva_4.31.F14.boolean.opBoolean","SPLIT",EDGE,{"disambiguationData":[TD([subQ46])],"derivedFrom":makeQuery(id+"FyYUAefgu6xEfva_4.30.F14.boolean.opBoolean","SPLIT",EDGE,{"disambiguationData":[TD([subQ46])],"derivedFrom":makeQuery(id+"FyYUAefgu6xEfva_4.29.F14.boolean.opBoolean","SPLIT",EDGE,{"disambiguationData":[TD([subQ46])],"derivedFrom":makeQuery(id+"FyYUAefgu6xEfva_4.28.F14.boolean.opBoolean","SPLIT",EDGE,{"disambiguationData":[TD([subQ46])],"derivedFrom":makeQuery(id+"FyYUAefgu6xEfva_4.27.F14.boolean.opBoolean","SPLIT",EDGE,{"disambiguationData":[TD([subQ46])],"derivedFrom":makeQuery(id+"FyYUAefgu6xEfva_4.26.F14.boolean.opBoolean","SPLIT",EDGE,{"disambiguationData":[TD([subQ46])],"derivedFrom":makeQuery(id+"FyYUAefgu6xEfva_4.25.F14.boolean.opBoolean","SPLIT",EDGE,{"disambiguationData":[TD([subQ46])],"derivedFrom":makeQuery(id+"FyYUAefgu6xEfva_4.24.F14.boolean.opBoolean","SPLIT",EDGE,{"disambiguationData":[TD([subQ46])],"derivedFrom":makeQuery(id+"FyYUAefgu6xEfva_4.23.F14.boolean.opBoolean","SPLIT",EDGE,{"disambiguationData":[TD([subQ46])],"derivedFrom":makeQuery(id+"FyYUAefgu6xEfva_4.22.F14.boolean.opBoolean","SPLIT",EDGE,{"disambiguationData":[TD([subQ46])],"derivedFrom":makeQuery(id+"FyYUAefgu6xEfva_4.21.F14.boolean.opBoolean","SPLIT",EDGE,{"disambiguationData":[TD([subQ46])],"derivedFrom":makeQuery(id+"FyYUAefgu6xEfva_4.20.F14.boolean.opBoolean","SPLIT",EDGE,{"disambiguationData":[TD([subQ46])],"derivedFrom":makeQuery(id+"FyYUAefgu6xEfva_4.19.F14.boolean.opBoolean","SPLIT",EDGE,{"disambiguationData":[TD([subQ46])],"derivedFrom":makeQuery(id+"FyYUAefgu6xEfva_4.18.F14.boolean.opBoolean","SPLIT",EDGE,{"disambiguationData":[TD([subQ46])],"derivedFrom":makeQuery(id+"FyYUAefgu6xEfva_4.17.F14.boolean.opBoolean","SPLIT",EDGE,{"disambiguationData":[TD([subQ46])],"derivedFrom":makeQuery(id+"FyYUAefgu6xEfva_4.16.F14.boolean.opBoolean","SPLIT",EDGE,{"disambiguationData":[TD([subQ46])],"derivedFrom":makeQuery(id+"FyYUAefgu6xEfva_4.15.F14.boolean.opBoolean","SPLIT",EDGE,{"disambiguationData":[TD([subQ46])],"derivedFrom":makeQuery(id+"FyYUAefgu6xEfva_4.14.F14.boolean.opBoolean","SPLIT",EDGE,{"disambiguationData":[TD([subQ46])],"derivedFrom":makeQuery(id+"FyYUAefgu6xEfva_4.13.F14.boolean.opBoolean","SPLIT",EDGE,{"disambiguationData":[TD([subQ46])],"derivedFrom":makeQuery(id+"FyYUAefgu6xEfva_4.12.F14.boolean.opBoolean","SPLIT",EDGE,{"disambiguationData":[TD([subQ46])],"derivedFrom":makeQuery(id+"FyYUAefgu6xEfva_4.11.F14.boolean.opBoolean","SPLIT",EDGE,{"disambiguationData":[TD([subQ46])],"derivedFrom":makeQuery(id+"FyYUAefgu6xEfva_4.10.F14.boolean.opBoolean","SPLIT",EDGE,{"disambiguationData":[TD([subQ46])],"derivedFrom":makeQuery(id+"FyYUAefgu6xEfva_4.9.F14.boolean.opBoolean","SPLIT",EDGE,{"disambiguationData":[TD([subQ46])],"derivedFrom":makeQuery(id+"FyYUAefgu6xEfva_4.8.F14.boolean.opBoolean","SPLIT",EDGE,{"disambiguationData":[TD([subQ46])],"derivedFrom":makeQuery(id+"FyYUAefgu6xEfva_4.7.F14.boolean.opBoolean","SPLIT",EDGE,{"disambiguationData":[TD([subQ46])],"derivedFrom":makeQuery(id+"FyYUAefgu6xEfva_4.6.F14.boolean.opBoolean","SPLIT",EDGE,{"disambiguationData":[TD([subQ46])],"derivedFrom":makeQuery(id+"FyYUAefgu6xEfva_4.5.F14.boolean.opBoolean","SPLIT",EDGE,{"disambiguationData":[TD([subQ46])],"derivedFrom":makeQuery(id+"FyYUAefgu6xEfva_4.4.F14.boolean.opBoolean","SPLIT",EDGE,{"disambiguationData":[TD([subQ46])],"derivedFrom":makeQuery(id+"FyYUAefgu6xEfva_4.3.F14.boolean.opBoolean","SPLIT",EDGE,{"disambiguationData":[TD([subQ46])],"derivedFrom":makeQuery(id+"FyYUAefgu6xEfva_4.2.F14.boolean.opBoolean","SPLIT",EDGE,{"disambiguationData":[TD([subQ46])],"derivedFrom":makeQuery(id+"FyYUAefgu6xEfva_4.1.F14.boolean.opBoolean","SPLIT",EDGE,{"disambiguationData":[TD([subQ46])],"derivedFrom":makeQuery(id+"F12.opExtrude","CAP_EDGE",EDGE,{"disambiguationData":[OSD([subQ2])],"isStart":false})})})})})})})})})})})})})})})})})})})})})})})})})})})})})})})})})})})})})})})});}
            var Q170;
            Q170=makeQuery(id+"FyYUAefgu6xEfva_4.39.F14.opExtrude","CAP_EDGE",EDGE,{"disambiguationData":[OSD([sQuery(id+"F9.wireOp",EDGE,"E142")])],"isStart":false});
            var Q171;
            {var subQ0=sQuery(id+"F13.wireOp",EDGE,"E148.MirrorCS");var subQ1=sQuery(id+"F13.wireOp",EDGE,"E147");var subQ2=sQuery(id+"F11.wireOp",EDGE,"E143");var subQ11=makeQuery(id+"FyYUAefgu6xEfva_4.5.F14.opExtrude","SWEPT_FACE",FACE,{"disambiguationData":[OSD([subQ0])]});var subQ13=makeQuery(id+"F14.opExtrude","SWEPT_FACE",FACE,{"disambiguationData":[OSD([subQ1])]});Q171=makeQuery(id+"FyYUAefgu6xEfva_4.6.F14.boolean.opBoolean","SPLIT",EDGE,{"disambiguationData":[TD([subQ11])],"derivedFrom":makeQuery(id+"FyYUAefgu6xEfva_4.5.F14.boolean.opBoolean","SPLIT",EDGE,{"disambiguationData":[TD([subQ13])],"derivedFrom":makeQuery(id+"FyYUAefgu6xEfva_4.4.F14.boolean.opBoolean","SPLIT",EDGE,{"disambiguationData":[TD([subQ13])],"derivedFrom":makeQuery(id+"FyYUAefgu6xEfva_4.3.F14.boolean.opBoolean","SPLIT",EDGE,{"disambiguationData":[TD([subQ13])],"derivedFrom":makeQuery(id+"FyYUAefgu6xEfva_4.2.F14.boolean.opBoolean","SPLIT",EDGE,{"disambiguationData":[TD([subQ13])],"derivedFrom":makeQuery(id+"FyYUAefgu6xEfva_4.1.F14.boolean.opBoolean","SPLIT",EDGE,{"disambiguationData":[TD([subQ13])],"derivedFrom":makeQuery(id+"F12.opExtrude","CAP_EDGE",EDGE,{"disambiguationData":[OSD([subQ2])],"isStart":false})})})})})})});}
            var Q172;
            {var subQ0=sQuery(id+"F9.wireOp",EDGE,"E142");var subQ2=sQuery(id+"F13.wireOp",EDGE,"E148.MirrorCS");var subQ3=makeQuery(id+"FyYUAefgu6xEfva_4.5.F14.opExtrude","SWEPT_FACE",FACE,{"disambiguationData":[OSD([subQ2])]});var subQ5=sQuery(id+"F13.wireOp",EDGE,"E147");var subQ6=makeQuery(id+"F14.opExtrude","SWEPT_FACE",FACE,{"disambiguationData":[OSD([subQ5])]});Q172=makeQuery(id+"FyYUAefgu6xEfva_4.6.F14.boolean.opBoolean","SPLIT",EDGE,{"disambiguationData":[TD([subQ3])],"derivedFrom":makeQuery(id+"FyYUAefgu6xEfva_4.5.F14.boolean.opBoolean","SPLIT",EDGE,{"disambiguationData":[TD([subQ6])],"derivedFrom":makeQuery(id+"FyYUAefgu6xEfva_4.4.F14.boolean.opBoolean","SPLIT",EDGE,{"disambiguationData":[TD([subQ6])],"derivedFrom":makeQuery(id+"FyYUAefgu6xEfva_4.3.F14.boolean.opBoolean","SPLIT",EDGE,{"disambiguationData":[TD([subQ6])],"derivedFrom":makeQuery(id+"FyYUAefgu6xEfva_4.2.F14.boolean.opBoolean","SPLIT",EDGE,{"disambiguationData":[TD([subQ6])],"derivedFrom":makeQuery(id+"FyYUAefgu6xEfva_4.1.F14.boolean.opBoolean","SPLIT",EDGE,{"disambiguationData":[TD([subQ6])],"derivedFrom":makeQuery(id+"F10.boolean.opBoolean","COPY",EDGE,{"derivedFrom":makeQuery(id+"F10.opExtrude","CAP_EDGE",EDGE,{"disambiguationData":[OSD([subQ0])],"isStart":false})})})})})})})});}
            var Q173;
            Q173=makeQuery(id+"FyYUAefgu6xEfva_4.6.F14.opExtrude","CAP_EDGE",EDGE,{"disambiguationData":[OSD([sQuery(id+"F9.wireOp",EDGE,"E142")])],"isStart":false});
            var Q174;
            Q174=makeQuery(id+"FyYUAefgu6xEfva_4.6.F14.opExtrude","CAP_EDGE",EDGE,{"disambiguationData":[OSD([sQuery(id+"F13.wireOp",EDGE,"E148.MirrorCS")])],"isStart":true});
            var Q175;
            Q175=makeQuery(id+"FyYUAefgu6xEfva_4.6.F14.opExtrude","SWEPT_EDGE",EDGE,{"disambiguationData":[OSD([sQuery(id+"F11.wireOp",EDGE,"E143"),sQuery(id+"F13.wireOp",EDGE,"E148.MirrorCS")])]});
            var Q176;
            Q176=makeQuery(id+"FyYUAefgu6xEfva_4.6.F14.opExtrude","SWEPT_EDGE",EDGE,{"disambiguationData":[OSD([sQuery(id+"F9.wireOp",EDGE,"E142"),sQuery(id+"F13.wireOp",EDGE,"E148.MirrorCS")])]});
            var Q177;
            Q177=makeQuery(id+"FyYUAefgu6xEfva_4.6.F14.opExtrude","SWEPT_EDGE",EDGE,{"disambiguationData":[OSD([sQuery(id+"F9.wireOp",EDGE,"E142"),sQuery(id+"F13.wireOp",EDGE,"E147")])]});
            var Q178;
            {var subQ0=sQuery(id+"F13.wireOp",EDGE,"E148.MirrorCS");var subQ1=sQuery(id+"F13.wireOp",EDGE,"E147");var subQ2=sQuery(id+"F11.wireOp",EDGE,"E143");var subQ6=makeQuery(id+"FyYUAefgu6xEfva_4.4.F14.opExtrude","SWEPT_FACE",FACE,{"disambiguationData":[OSD([subQ0])]});var subQ12=makeQuery(id+"F14.opExtrude","SWEPT_FACE",FACE,{"disambiguationData":[OSD([subQ1])]});Q178=makeQuery(id+"FyYUAefgu6xEfva_4.5.F14.boolean.opBoolean","SPLIT",EDGE,{"disambiguationData":[TD([subQ6])],"derivedFrom":makeQuery(id+"FyYUAefgu6xEfva_4.4.F14.boolean.opBoolean","SPLIT",EDGE,{"disambiguationData":[TD([subQ12])],"derivedFrom":makeQuery(id+"FyYUAefgu6xEfva_4.3.F14.boolean.opBoolean","SPLIT",EDGE,{"disambiguationData":[TD([subQ12])],"derivedFrom":makeQuery(id+"FyYUAefgu6xEfva_4.2.F14.boolean.opBoolean","SPLIT",EDGE,{"disambiguationData":[TD([subQ12])],"derivedFrom":makeQuery(id+"FyYUAefgu6xEfva_4.1.F14.boolean.opBoolean","SPLIT",EDGE,{"disambiguationData":[TD([subQ12])],"derivedFrom":makeQuery(id+"F12.opExtrude","CAP_EDGE",EDGE,{"disambiguationData":[OSD([subQ2])],"isStart":false})})})})})});}
            var Q179;
            {var subQ0=sQuery(id+"F9.wireOp",EDGE,"E142");var subQ3=sQuery(id+"F13.wireOp",EDGE,"E148.MirrorCS");var subQ4=makeQuery(id+"FyYUAefgu6xEfva_4.4.F14.opExtrude","SWEPT_FACE",FACE,{"disambiguationData":[OSD([subQ3])]});var subQ5=sQuery(id+"F13.wireOp",EDGE,"E147");var subQ6=makeQuery(id+"F14.opExtrude","SWEPT_FACE",FACE,{"disambiguationData":[OSD([subQ5])]});Q179=makeQuery(id+"FyYUAefgu6xEfva_4.5.F14.boolean.opBoolean","SPLIT",EDGE,{"disambiguationData":[TD([subQ4])],"derivedFrom":makeQuery(id+"FyYUAefgu6xEfva_4.4.F14.boolean.opBoolean","SPLIT",EDGE,{"disambiguationData":[TD([subQ6])],"derivedFrom":makeQuery(id+"FyYUAefgu6xEfva_4.3.F14.boolean.opBoolean","SPLIT",EDGE,{"disambiguationData":[TD([subQ6])],"derivedFrom":makeQuery(id+"FyYUAefgu6xEfva_4.2.F14.boolean.opBoolean","SPLIT",EDGE,{"disambiguationData":[TD([subQ6])],"derivedFrom":makeQuery(id+"FyYUAefgu6xEfva_4.1.F14.boolean.opBoolean","SPLIT",EDGE,{"disambiguationData":[TD([subQ6])],"derivedFrom":makeQuery(id+"F10.boolean.opBoolean","COPY",EDGE,{"derivedFrom":makeQuery(id+"F10.opExtrude","CAP_EDGE",EDGE,{"disambiguationData":[OSD([subQ0])],"isStart":false})})})})})})});}
            var Q180;
            Q180=makeQuery(id+"FyYUAefgu6xEfva_4.5.F14.opExtrude","CAP_EDGE",EDGE,{"disambiguationData":[OSD([sQuery(id+"F13.wireOp",EDGE,"E148.MirrorCS")])],"isStart":true});
            var Q181;
            Q181=makeQuery(id+"FyYUAefgu6xEfva_4.5.F14.opExtrude","CAP_EDGE",EDGE,{"disambiguationData":[OSD([sQuery(id+"F13.wireOp",EDGE,"E147")])],"isStart":true});
            var Q182;
            Q182=makeQuery(id+"FyYUAefgu6xEfva_4.5.F14.opExtrude","SWEPT_EDGE",EDGE,{"disambiguationData":[OSD([sQuery(id+"F11.wireOp",EDGE,"E143"),sQuery(id+"F13.wireOp",EDGE,"E148.MirrorCS")])]});
            var Q183;
            Q183=makeQuery(id+"FyYUAefgu6xEfva_4.5.F14.opExtrude","SWEPT_EDGE",EDGE,{"disambiguationData":[OSD([sQuery(id+"F9.wireOp",EDGE,"E142"),sQuery(id+"F13.wireOp",EDGE,"E147")])]});
            var Q184;
            {var subQ0=sQuery(id+"F13.wireOp",EDGE,"E148.MirrorCS");var subQ1=sQuery(id+"F13.wireOp",EDGE,"E147");var subQ2=sQuery(id+"F11.wireOp",EDGE,"E143");var subQ10=makeQuery(id+"FyYUAefgu6xEfva_4.3.F14.opExtrude","SWEPT_FACE",FACE,{"disambiguationData":[OSD([subQ0])]});var subQ11=makeQuery(id+"F14.opExtrude","SWEPT_FACE",FACE,{"disambiguationData":[OSD([subQ1])]});Q184=makeQuery(id+"FyYUAefgu6xEfva_4.4.F14.boolean.opBoolean","SPLIT",EDGE,{"disambiguationData":[TD([subQ10])],"derivedFrom":makeQuery(id+"FyYUAefgu6xEfva_4.3.F14.boolean.opBoolean","SPLIT",EDGE,{"disambiguationData":[TD([subQ11])],"derivedFrom":makeQuery(id+"FyYUAefgu6xEfva_4.2.F14.boolean.opBoolean","SPLIT",EDGE,{"disambiguationData":[TD([subQ11])],"derivedFrom":makeQuery(id+"FyYUAefgu6xEfva_4.1.F14.boolean.opBoolean","SPLIT",EDGE,{"disambiguationData":[TD([subQ11])],"derivedFrom":makeQuery(id+"F12.opExtrude","CAP_EDGE",EDGE,{"disambiguationData":[OSD([subQ2])],"isStart":false})})})})});}
            var Q185;
            {var subQ0=sQuery(id+"F9.wireOp",EDGE,"E142");var subQ2=sQuery(id+"F13.wireOp",EDGE,"E147");var subQ4=sQuery(id+"F13.wireOp",EDGE,"E148.MirrorCS");var subQ5=makeQuery(id+"FyYUAefgu6xEfva_4.3.F14.opExtrude","SWEPT_FACE",FACE,{"disambiguationData":[OSD([subQ4])]});var subQ6=makeQuery(id+"F14.opExtrude","SWEPT_FACE",FACE,{"disambiguationData":[OSD([subQ2])]});Q185=makeQuery(id+"FyYUAefgu6xEfva_4.4.F14.boolean.opBoolean","SPLIT",EDGE,{"disambiguationData":[TD([subQ5])],"derivedFrom":makeQuery(id+"FyYUAefgu6xEfva_4.3.F14.boolean.opBoolean","SPLIT",EDGE,{"disambiguationData":[TD([subQ6])],"derivedFrom":makeQuery(id+"FyYUAefgu6xEfva_4.2.F14.boolean.opBoolean","SPLIT",EDGE,{"disambiguationData":[TD([subQ6])],"derivedFrom":makeQuery(id+"FyYUAefgu6xEfva_4.1.F14.boolean.opBoolean","SPLIT",EDGE,{"disambiguationData":[TD([subQ6])],"derivedFrom":makeQuery(id+"F10.boolean.opBoolean","COPY",EDGE,{"derivedFrom":makeQuery(id+"F10.opExtrude","CAP_EDGE",EDGE,{"disambiguationData":[OSD([subQ0])],"isStart":false})})})})})});}
            var Q186;
            Q186=makeQuery(id+"FyYUAefgu6xEfva_4.4.F14.opExtrude","CAP_EDGE",EDGE,{"disambiguationData":[OSD([sQuery(id+"F9.wireOp",EDGE,"E142")])],"isStart":false});
            var Q187;
            Q187=makeQuery(id+"FyYUAefgu6xEfva_4.4.F14.opExtrude","CAP_EDGE",EDGE,{"disambiguationData":[OSD([sQuery(id+"F13.wireOp",EDGE,"E148.MirrorCS")])],"isStart":true});
            var Q188;
            Q188=makeQuery(id+"FyYUAefgu6xEfva_4.4.F14.opExtrude","CAP_EDGE",EDGE,{"disambiguationData":[OSD([sQuery(id+"F13.wireOp",EDGE,"E147")])],"isStart":true});
            var Q189;
            Q189=makeQuery(id+"FyYUAefgu6xEfva_4.4.F14.opExtrude","SWEPT_EDGE",EDGE,{"disambiguationData":[OSD([sQuery(id+"F11.wireOp",EDGE,"E143"),sQuery(id+"F13.wireOp",EDGE,"E148.MirrorCS")])]});
            var Q190;
            Q190=makeQuery(id+"FyYUAefgu6xEfva_4.4.F14.opExtrude","SWEPT_EDGE",EDGE,{"disambiguationData":[OSD([sQuery(id+"F9.wireOp",EDGE,"E142"),sQuery(id+"F13.wireOp",EDGE,"E148.MirrorCS")])]});
            var Q191;
            Q191=makeQuery(id+"FyYUAefgu6xEfva_4.4.F14.opExtrude","SWEPT_EDGE",EDGE,{"disambiguationData":[OSD([sQuery(id+"F11.wireOp",EDGE,"E143"),sQuery(id+"F13.wireOp",EDGE,"E147")])]});
            var Q192;
            Q192=makeQuery(id+"FyYUAefgu6xEfva_4.4.F14.opExtrude","SWEPT_EDGE",EDGE,{"disambiguationData":[OSD([sQuery(id+"F9.wireOp",EDGE,"E142"),sQuery(id+"F13.wireOp",EDGE,"E147")])]});
            var Q193;
            {var subQ0=sQuery(id+"F13.wireOp",EDGE,"E148.MirrorCS");var subQ1=sQuery(id+"F13.wireOp",EDGE,"E147");var subQ2=sQuery(id+"F11.wireOp",EDGE,"E143");var subQ15=makeQuery(id+"FyYUAefgu6xEfva_4.8.F14.opExtrude","SWEPT_FACE",FACE,{"disambiguationData":[OSD([subQ0])]});var subQ16=makeQuery(id+"F14.opExtrude","SWEPT_FACE",FACE,{"disambiguationData":[OSD([subQ1])]});Q193=makeQuery(id+"FyYUAefgu6xEfva_4.9.F14.boolean.opBoolean","SPLIT",EDGE,{"disambiguationData":[TD([subQ15])],"derivedFrom":makeQuery(id+"FyYUAefgu6xEfva_4.8.F14.boolean.opBoolean","SPLIT",EDGE,{"disambiguationData":[TD([subQ16])],"derivedFrom":makeQuery(id+"FyYUAefgu6xEfva_4.7.F14.boolean.opBoolean","SPLIT",EDGE,{"disambiguationData":[TD([subQ16])],"derivedFrom":makeQuery(id+"FyYUAefgu6xEfva_4.6.F14.boolean.opBoolean","SPLIT",EDGE,{"disambiguationData":[TD([subQ16])],"derivedFrom":makeQuery(id+"FyYUAefgu6xEfva_4.5.F14.boolean.opBoolean","SPLIT",EDGE,{"disambiguationData":[TD([subQ16])],"derivedFrom":makeQuery(id+"FyYUAefgu6xEfva_4.4.F14.boolean.opBoolean","SPLIT",EDGE,{"disambiguationData":[TD([subQ16])],"derivedFrom":makeQuery(id+"FyYUAefgu6xEfva_4.3.F14.boolean.opBoolean","SPLIT",EDGE,{"disambiguationData":[TD([subQ16])],"derivedFrom":makeQuery(id+"FyYUAefgu6xEfva_4.2.F14.boolean.opBoolean","SPLIT",EDGE,{"disambiguationData":[TD([subQ16])],"derivedFrom":makeQuery(id+"FyYUAefgu6xEfva_4.1.F14.boolean.opBoolean","SPLIT",EDGE,{"disambiguationData":[TD([subQ16])],"derivedFrom":makeQuery(id+"F12.opExtrude","CAP_EDGE",EDGE,{"disambiguationData":[OSD([subQ2])],"isStart":false})})})})})})})})})});}
            var Q194;
            {var subQ0=sQuery(id+"F9.wireOp",EDGE,"E142");var subQ2=sQuery(id+"F13.wireOp",EDGE,"E147");var subQ4=sQuery(id+"F13.wireOp",EDGE,"E148.MirrorCS");var subQ5=makeQuery(id+"FyYUAefgu6xEfva_4.8.F14.opExtrude","SWEPT_FACE",FACE,{"disambiguationData":[OSD([subQ4])]});var subQ6=makeQuery(id+"F14.opExtrude","SWEPT_FACE",FACE,{"disambiguationData":[OSD([subQ2])]});Q194=makeQuery(id+"FyYUAefgu6xEfva_4.9.F14.boolean.opBoolean","SPLIT",EDGE,{"disambiguationData":[TD([subQ5])],"derivedFrom":makeQuery(id+"FyYUAefgu6xEfva_4.8.F14.boolean.opBoolean","SPLIT",EDGE,{"disambiguationData":[TD([subQ6])],"derivedFrom":makeQuery(id+"FyYUAefgu6xEfva_4.7.F14.boolean.opBoolean","SPLIT",EDGE,{"disambiguationData":[TD([subQ6])],"derivedFrom":makeQuery(id+"FyYUAefgu6xEfva_4.6.F14.boolean.opBoolean","SPLIT",EDGE,{"disambiguationData":[TD([subQ6])],"derivedFrom":makeQuery(id+"FyYUAefgu6xEfva_4.5.F14.boolean.opBoolean","SPLIT",EDGE,{"disambiguationData":[TD([subQ6])],"derivedFrom":makeQuery(id+"FyYUAefgu6xEfva_4.4.F14.boolean.opBoolean","SPLIT",EDGE,{"disambiguationData":[TD([subQ6])],"derivedFrom":makeQuery(id+"FyYUAefgu6xEfva_4.3.F14.boolean.opBoolean","SPLIT",EDGE,{"disambiguationData":[TD([subQ6])],"derivedFrom":makeQuery(id+"FyYUAefgu6xEfva_4.2.F14.boolean.opBoolean","SPLIT",EDGE,{"disambiguationData":[TD([subQ6])],"derivedFrom":makeQuery(id+"FyYUAefgu6xEfva_4.1.F14.boolean.opBoolean","SPLIT",EDGE,{"disambiguationData":[TD([subQ6])],"derivedFrom":makeQuery(id+"F10.boolean.opBoolean","COPY",EDGE,{"derivedFrom":makeQuery(id+"F10.opExtrude","CAP_EDGE",EDGE,{"disambiguationData":[OSD([subQ0])],"isStart":false})})})})})})})})})})});}
            var Q195;
            Q195=makeQuery(id+"FyYUAefgu6xEfva_4.9.F14.opExtrude","CAP_EDGE",EDGE,{"disambiguationData":[OSD([sQuery(id+"F9.wireOp",EDGE,"E142")])],"isStart":false});
            var Q196;
            Q196=makeQuery(id+"FyYUAefgu6xEfva_4.9.F14.opExtrude","SWEPT_EDGE",EDGE,{"disambiguationData":[OSD([sQuery(id+"F11.wireOp",EDGE,"E143"),sQuery(id+"F13.wireOp",EDGE,"E148.MirrorCS")])]});
            var Q197;
            Q197=makeQuery(id+"FyYUAefgu6xEfva_4.9.F14.opExtrude","SWEPT_EDGE",EDGE,{"disambiguationData":[OSD([sQuery(id+"F9.wireOp",EDGE,"E142"),sQuery(id+"F13.wireOp",EDGE,"E148.MirrorCS")])]});
            var Q198;
            Q198=makeQuery(id+"FyYUAefgu6xEfva_4.9.F14.opExtrude","SWEPT_EDGE",EDGE,{"disambiguationData":[OSD([sQuery(id+"F11.wireOp",EDGE,"E143"),sQuery(id+"F13.wireOp",EDGE,"E147")])]});
            var Q199;
            Q199=makeQuery(id+"FyYUAefgu6xEfva_4.9.F14.opExtrude","SWEPT_EDGE",EDGE,{"disambiguationData":[OSD([sQuery(id+"F9.wireOp",EDGE,"E142"),sQuery(id+"F13.wireOp",EDGE,"E147")])]});
            var Q200;
            Q200=makeQuery(id+"F14.opExtrude","CAP_EDGE",EDGE,{"disambiguationData":[OSD([sQuery(id+"F9.wireOp",EDGE,"E142")])],"isStart":false});
            var Q201;
            Q201=makeQuery(id+"F14.opExtrude","CAP_EDGE",EDGE,{"disambiguationData":[OSD([sQuery(id+"F13.wireOp",EDGE,"E148.MirrorCS")])],"isStart":true});
            var Q202;
            Q202=makeQuery(id+"F14.opExtrude","CAP_EDGE",EDGE,{"disambiguationData":[OSD([sQuery(id+"F13.wireOp",EDGE,"E147")])],"isStart":true});
            var Q203;
            Q203=makeQuery(id+"F14.opExtrude","SWEPT_EDGE",EDGE,{"disambiguationData":[OSD([sQuery(id+"F9.wireOp",EDGE,"E142"),sQuery(id+"F13.wireOp",EDGE,"E148.MirrorCS")])]});
            var Q204;
            Q204=makeQuery(id+"F14.opExtrude","SWEPT_EDGE",EDGE,{"disambiguationData":[OSD([sQuery(id+"F11.wireOp",EDGE,"E143"),sQuery(id+"F13.wireOp",EDGE,"E147")])]});
            var Q205;
            Q205=makeQuery(id+"F14.opExtrude","SWEPT_EDGE",EDGE,{"disambiguationData":[OSD([sQuery(id+"F9.wireOp",EDGE,"E142"),sQuery(id+"F13.wireOp",EDGE,"E147")])]});
            var Q206;
            Q206=makeQuery(id+"FyYUAefgu6xEfva_4.40.F14.opExtrude","SWEPT_EDGE",EDGE,{"disambiguationData":[OSD([sQuery(id+"F11.wireOp",EDGE,"E143"),sQuery(id+"F13.wireOp",EDGE,"E148.MirrorCS")])]});
            var Q207;
            Q207=makeQuery(id+"FyYUAefgu6xEfva_4.40.F14.opExtrude","CAP_EDGE",EDGE,{"disambiguationData":[OSD([sQuery(id+"F13.wireOp",EDGE,"E147")])],"isStart":true});
            var Q208;
            Q208=makeQuery(id+"FyYUAefgu6xEfva_4.40.F14.opExtrude","CAP_EDGE",EDGE,{"disambiguationData":[OSD([sQuery(id+"F9.wireOp",EDGE,"E142")])],"isStart":false});
            var Q209;
            {var subQ0=sQuery(id+"F9.wireOp",EDGE,"E142");var subQ3=sQuery(id+"F13.wireOp",EDGE,"E148.MirrorCS");var subQ4=makeQuery(id+"FyYUAefgu6xEfva_4.39.F14.opExtrude","SWEPT_FACE",FACE,{"disambiguationData":[OSD([subQ3])]});var subQ5=sQuery(id+"F13.wireOp",EDGE,"E147");var subQ6=makeQuery(id+"F14.opExtrude","SWEPT_FACE",FACE,{"disambiguationData":[OSD([subQ5])]});Q209=makeQuery(id+"FyYUAefgu6xEfva_4.40.F14.boolean.opBoolean","SPLIT",EDGE,{"disambiguationData":[TD([subQ4])],"derivedFrom":makeQuery(id+"FyYUAefgu6xEfva_4.39.F14.boolean.opBoolean","SPLIT",EDGE,{"disambiguationData":[TD([subQ6])],"derivedFrom":makeQuery(id+"FyYUAefgu6xEfva_4.38.F14.boolean.opBoolean","SPLIT",EDGE,{"disambiguationData":[TD([subQ6])],"derivedFrom":makeQuery(id+"FyYUAefgu6xEfva_4.37.F14.boolean.opBoolean","SPLIT",EDGE,{"disambiguationData":[TD([subQ6])],"derivedFrom":makeQuery(id+"FyYUAefgu6xEfva_4.36.F14.boolean.opBoolean","SPLIT",EDGE,{"disambiguationData":[TD([subQ6])],"derivedFrom":makeQuery(id+"FyYUAefgu6xEfva_4.35.F14.boolean.opBoolean","SPLIT",EDGE,{"disambiguationData":[TD([subQ6])],"derivedFrom":makeQuery(id+"FyYUAefgu6xEfva_4.34.F14.boolean.opBoolean","SPLIT",EDGE,{"disambiguationData":[TD([subQ6])],"derivedFrom":makeQuery(id+"FyYUAefgu6xEfva_4.33.F14.boolean.opBoolean","SPLIT",EDGE,{"disambiguationData":[TD([subQ6])],"derivedFrom":makeQuery(id+"FyYUAefgu6xEfva_4.32.F14.boolean.opBoolean","SPLIT",EDGE,{"disambiguationData":[TD([subQ6])],"derivedFrom":makeQuery(id+"FyYUAefgu6xEfva_4.31.F14.boolean.opBoolean","SPLIT",EDGE,{"disambiguationData":[TD([subQ6])],"derivedFrom":makeQuery(id+"FyYUAefgu6xEfva_4.30.F14.boolean.opBoolean","SPLIT",EDGE,{"disambiguationData":[TD([subQ6])],"derivedFrom":makeQuery(id+"FyYUAefgu6xEfva_4.29.F14.boolean.opBoolean","SPLIT",EDGE,{"disambiguationData":[TD([subQ6])],"derivedFrom":makeQuery(id+"FyYUAefgu6xEfva_4.28.F14.boolean.opBoolean","SPLIT",EDGE,{"disambiguationData":[TD([subQ6])],"derivedFrom":makeQuery(id+"FyYUAefgu6xEfva_4.27.F14.boolean.opBoolean","SPLIT",EDGE,{"disambiguationData":[TD([subQ6])],"derivedFrom":makeQuery(id+"FyYUAefgu6xEfva_4.26.F14.boolean.opBoolean","SPLIT",EDGE,{"disambiguationData":[TD([subQ6])],"derivedFrom":makeQuery(id+"FyYUAefgu6xEfva_4.25.F14.boolean.opBoolean","SPLIT",EDGE,{"disambiguationData":[TD([subQ6])],"derivedFrom":makeQuery(id+"FyYUAefgu6xEfva_4.24.F14.boolean.opBoolean","SPLIT",EDGE,{"disambiguationData":[TD([subQ6])],"derivedFrom":makeQuery(id+"FyYUAefgu6xEfva_4.23.F14.boolean.opBoolean","SPLIT",EDGE,{"disambiguationData":[TD([subQ6])],"derivedFrom":makeQuery(id+"FyYUAefgu6xEfva_4.22.F14.boolean.opBoolean","SPLIT",EDGE,{"disambiguationData":[TD([subQ6])],"derivedFrom":makeQuery(id+"FyYUAefgu6xEfva_4.21.F14.boolean.opBoolean","SPLIT",EDGE,{"disambiguationData":[TD([subQ6])],"derivedFrom":makeQuery(id+"FyYUAefgu6xEfva_4.20.F14.boolean.opBoolean","SPLIT",EDGE,{"disambiguationData":[TD([subQ6])],"derivedFrom":makeQuery(id+"FyYUAefgu6xEfva_4.19.F14.boolean.opBoolean","SPLIT",EDGE,{"disambiguationData":[TD([subQ6])],"derivedFrom":makeQuery(id+"FyYUAefgu6xEfva_4.18.F14.boolean.opBoolean","SPLIT",EDGE,{"disambiguationData":[TD([subQ6])],"derivedFrom":makeQuery(id+"FyYUAefgu6xEfva_4.17.F14.boolean.opBoolean","SPLIT",EDGE,{"disambiguationData":[TD([subQ6])],"derivedFrom":makeQuery(id+"FyYUAefgu6xEfva_4.16.F14.boolean.opBoolean","SPLIT",EDGE,{"disambiguationData":[TD([subQ6])],"derivedFrom":makeQuery(id+"FyYUAefgu6xEfva_4.15.F14.boolean.opBoolean","SPLIT",EDGE,{"disambiguationData":[TD([subQ6])],"derivedFrom":makeQuery(id+"FyYUAefgu6xEfva_4.14.F14.boolean.opBoolean","SPLIT",EDGE,{"disambiguationData":[TD([subQ6])],"derivedFrom":makeQuery(id+"FyYUAefgu6xEfva_4.13.F14.boolean.opBoolean","SPLIT",EDGE,{"disambiguationData":[TD([subQ6])],"derivedFrom":makeQuery(id+"FyYUAefgu6xEfva_4.12.F14.boolean.opBoolean","SPLIT",EDGE,{"disambiguationData":[TD([subQ6])],"derivedFrom":makeQuery(id+"FyYUAefgu6xEfva_4.11.F14.boolean.opBoolean","SPLIT",EDGE,{"disambiguationData":[TD([subQ6])],"derivedFrom":makeQuery(id+"FyYUAefgu6xEfva_4.10.F14.boolean.opBoolean","SPLIT",EDGE,{"disambiguationData":[TD([subQ6])],"derivedFrom":makeQuery(id+"FyYUAefgu6xEfva_4.9.F14.boolean.opBoolean","SPLIT",EDGE,{"disambiguationData":[TD([subQ6])],"derivedFrom":makeQuery(id+"FyYUAefgu6xEfva_4.8.F14.boolean.opBoolean","SPLIT",EDGE,{"disambiguationData":[TD([subQ6])],"derivedFrom":makeQuery(id+"FyYUAefgu6xEfva_4.7.F14.boolean.opBoolean","SPLIT",EDGE,{"disambiguationData":[TD([subQ6])],"derivedFrom":makeQuery(id+"FyYUAefgu6xEfva_4.6.F14.boolean.opBoolean","SPLIT",EDGE,{"disambiguationData":[TD([subQ6])],"derivedFrom":makeQuery(id+"FyYUAefgu6xEfva_4.5.F14.boolean.opBoolean","SPLIT",EDGE,{"disambiguationData":[TD([subQ6])],"derivedFrom":makeQuery(id+"FyYUAefgu6xEfva_4.4.F14.boolean.opBoolean","SPLIT",EDGE,{"disambiguationData":[TD([subQ6])],"derivedFrom":makeQuery(id+"FyYUAefgu6xEfva_4.3.F14.boolean.opBoolean","SPLIT",EDGE,{"disambiguationData":[TD([subQ6])],"derivedFrom":makeQuery(id+"FyYUAefgu6xEfva_4.2.F14.boolean.opBoolean","SPLIT",EDGE,{"disambiguationData":[TD([subQ6])],"derivedFrom":makeQuery(id+"FyYUAefgu6xEfva_4.1.F14.boolean.opBoolean","SPLIT",EDGE,{"disambiguationData":[TD([subQ6])],"derivedFrom":makeQuery(id+"F10.boolean.opBoolean","COPY",EDGE,{"derivedFrom":makeQuery(id+"F10.opExtrude","CAP_EDGE",EDGE,{"disambiguationData":[OSD([subQ0])],"isStart":false})})})})})})})})})})})})})})})})})})})})})})})})})})})})})})})})})})})})})})})})})});}
            var Q210;
            {var subQ0=sQuery(id+"F13.wireOp",EDGE,"E148.MirrorCS");var subQ1=sQuery(id+"F13.wireOp",EDGE,"E147");var subQ2=sQuery(id+"F11.wireOp",EDGE,"E143");var subQ17=makeQuery(id+"FyYUAefgu6xEfva_4.39.F14.opExtrude","SWEPT_FACE",FACE,{"disambiguationData":[OSD([subQ0])]});var subQ47=makeQuery(id+"F14.opExtrude","SWEPT_FACE",FACE,{"disambiguationData":[OSD([subQ1])]});Q210=makeQuery(id+"FyYUAefgu6xEfva_4.40.F14.boolean.opBoolean","SPLIT",EDGE,{"disambiguationData":[TD([subQ17])],"derivedFrom":makeQuery(id+"FyYUAefgu6xEfva_4.39.F14.boolean.opBoolean","SPLIT",EDGE,{"disambiguationData":[TD([subQ47])],"derivedFrom":makeQuery(id+"FyYUAefgu6xEfva_4.38.F14.boolean.opBoolean","SPLIT",EDGE,{"disambiguationData":[TD([subQ47])],"derivedFrom":makeQuery(id+"FyYUAefgu6xEfva_4.37.F14.boolean.opBoolean","SPLIT",EDGE,{"disambiguationData":[TD([subQ47])],"derivedFrom":makeQuery(id+"FyYUAefgu6xEfva_4.36.F14.boolean.opBoolean","SPLIT",EDGE,{"disambiguationData":[TD([subQ47])],"derivedFrom":makeQuery(id+"FyYUAefgu6xEfva_4.35.F14.boolean.opBoolean","SPLIT",EDGE,{"disambiguationData":[TD([subQ47])],"derivedFrom":makeQuery(id+"FyYUAefgu6xEfva_4.34.F14.boolean.opBoolean","SPLIT",EDGE,{"disambiguationData":[TD([subQ47])],"derivedFrom":makeQuery(id+"FyYUAefgu6xEfva_4.33.F14.boolean.opBoolean","SPLIT",EDGE,{"disambiguationData":[TD([subQ47])],"derivedFrom":makeQuery(id+"FyYUAefgu6xEfva_4.32.F14.boolean.opBoolean","SPLIT",EDGE,{"disambiguationData":[TD([subQ47])],"derivedFrom":makeQuery(id+"FyYUAefgu6xEfva_4.31.F14.boolean.opBoolean","SPLIT",EDGE,{"disambiguationData":[TD([subQ47])],"derivedFrom":makeQuery(id+"FyYUAefgu6xEfva_4.30.F14.boolean.opBoolean","SPLIT",EDGE,{"disambiguationData":[TD([subQ47])],"derivedFrom":makeQuery(id+"FyYUAefgu6xEfva_4.29.F14.boolean.opBoolean","SPLIT",EDGE,{"disambiguationData":[TD([subQ47])],"derivedFrom":makeQuery(id+"FyYUAefgu6xEfva_4.28.F14.boolean.opBoolean","SPLIT",EDGE,{"disambiguationData":[TD([subQ47])],"derivedFrom":makeQuery(id+"FyYUAefgu6xEfva_4.27.F14.boolean.opBoolean","SPLIT",EDGE,{"disambiguationData":[TD([subQ47])],"derivedFrom":makeQuery(id+"FyYUAefgu6xEfva_4.26.F14.boolean.opBoolean","SPLIT",EDGE,{"disambiguationData":[TD([subQ47])],"derivedFrom":makeQuery(id+"FyYUAefgu6xEfva_4.25.F14.boolean.opBoolean","SPLIT",EDGE,{"disambiguationData":[TD([subQ47])],"derivedFrom":makeQuery(id+"FyYUAefgu6xEfva_4.24.F14.boolean.opBoolean","SPLIT",EDGE,{"disambiguationData":[TD([subQ47])],"derivedFrom":makeQuery(id+"FyYUAefgu6xEfva_4.23.F14.boolean.opBoolean","SPLIT",EDGE,{"disambiguationData":[TD([subQ47])],"derivedFrom":makeQuery(id+"FyYUAefgu6xEfva_4.22.F14.boolean.opBoolean","SPLIT",EDGE,{"disambiguationData":[TD([subQ47])],"derivedFrom":makeQuery(id+"FyYUAefgu6xEfva_4.21.F14.boolean.opBoolean","SPLIT",EDGE,{"disambiguationData":[TD([subQ47])],"derivedFrom":makeQuery(id+"FyYUAefgu6xEfva_4.20.F14.boolean.opBoolean","SPLIT",EDGE,{"disambiguationData":[TD([subQ47])],"derivedFrom":makeQuery(id+"FyYUAefgu6xEfva_4.19.F14.boolean.opBoolean","SPLIT",EDGE,{"disambiguationData":[TD([subQ47])],"derivedFrom":makeQuery(id+"FyYUAefgu6xEfva_4.18.F14.boolean.opBoolean","SPLIT",EDGE,{"disambiguationData":[TD([subQ47])],"derivedFrom":makeQuery(id+"FyYUAefgu6xEfva_4.17.F14.boolean.opBoolean","SPLIT",EDGE,{"disambiguationData":[TD([subQ47])],"derivedFrom":makeQuery(id+"FyYUAefgu6xEfva_4.16.F14.boolean.opBoolean","SPLIT",EDGE,{"disambiguationData":[TD([subQ47])],"derivedFrom":makeQuery(id+"FyYUAefgu6xEfva_4.15.F14.boolean.opBoolean","SPLIT",EDGE,{"disambiguationData":[TD([subQ47])],"derivedFrom":makeQuery(id+"FyYUAefgu6xEfva_4.14.F14.boolean.opBoolean","SPLIT",EDGE,{"disambiguationData":[TD([subQ47])],"derivedFrom":makeQuery(id+"FyYUAefgu6xEfva_4.13.F14.boolean.opBoolean","SPLIT",EDGE,{"disambiguationData":[TD([subQ47])],"derivedFrom":makeQuery(id+"FyYUAefgu6xEfva_4.12.F14.boolean.opBoolean","SPLIT",EDGE,{"disambiguationData":[TD([subQ47])],"derivedFrom":makeQuery(id+"FyYUAefgu6xEfva_4.11.F14.boolean.opBoolean","SPLIT",EDGE,{"disambiguationData":[TD([subQ47])],"derivedFrom":makeQuery(id+"FyYUAefgu6xEfva_4.10.F14.boolean.opBoolean","SPLIT",EDGE,{"disambiguationData":[TD([subQ47])],"derivedFrom":makeQuery(id+"FyYUAefgu6xEfva_4.9.F14.boolean.opBoolean","SPLIT",EDGE,{"disambiguationData":[TD([subQ47])],"derivedFrom":makeQuery(id+"FyYUAefgu6xEfva_4.8.F14.boolean.opBoolean","SPLIT",EDGE,{"disambiguationData":[TD([subQ47])],"derivedFrom":makeQuery(id+"FyYUAefgu6xEfva_4.7.F14.boolean.opBoolean","SPLIT",EDGE,{"disambiguationData":[TD([subQ47])],"derivedFrom":makeQuery(id+"FyYUAefgu6xEfva_4.6.F14.boolean.opBoolean","SPLIT",EDGE,{"disambiguationData":[TD([subQ47])],"derivedFrom":makeQuery(id+"FyYUAefgu6xEfva_4.5.F14.boolean.opBoolean","SPLIT",EDGE,{"disambiguationData":[TD([subQ47])],"derivedFrom":makeQuery(id+"FyYUAefgu6xEfva_4.4.F14.boolean.opBoolean","SPLIT",EDGE,{"disambiguationData":[TD([subQ47])],"derivedFrom":makeQuery(id+"FyYUAefgu6xEfva_4.3.F14.boolean.opBoolean","SPLIT",EDGE,{"disambiguationData":[TD([subQ47])],"derivedFrom":makeQuery(id+"FyYUAefgu6xEfva_4.2.F14.boolean.opBoolean","SPLIT",EDGE,{"disambiguationData":[TD([subQ47])],"derivedFrom":makeQuery(id+"FyYUAefgu6xEfva_4.1.F14.boolean.opBoolean","SPLIT",EDGE,{"disambiguationData":[TD([subQ47])],"derivedFrom":makeQuery(id+"F12.opExtrude","CAP_EDGE",EDGE,{"disambiguationData":[OSD([subQ2])],"isStart":false})})})})})})})})})})})})})})})})})})})})})})})})})})})})})})})})})})})})})})})})});}
            var Q211;
            Q211=makeQuery(id+"FyYUAefgu6xEfva_4.10.F14.opExtrude","SWEPT_EDGE",EDGE,{"disambiguationData":[OSD([sQuery(id+"F9.wireOp",EDGE,"E142"),sQuery(id+"F13.wireOp",EDGE,"E147")])]});
            var Q212;
            Q212=makeQuery(id+"FyYUAefgu6xEfva_4.10.F14.opExtrude","SWEPT_EDGE",EDGE,{"disambiguationData":[OSD([sQuery(id+"F11.wireOp",EDGE,"E143"),sQuery(id+"F13.wireOp",EDGE,"E147")])]});
            var Q213;
            Q213=makeQuery(id+"FyYUAefgu6xEfva_4.10.F14.opExtrude","SWEPT_EDGE",EDGE,{"disambiguationData":[OSD([sQuery(id+"F11.wireOp",EDGE,"E143"),sQuery(id+"F13.wireOp",EDGE,"E148.MirrorCS")])]});
            var Q214;
            Q214=makeQuery(id+"FyYUAefgu6xEfva_4.10.F14.opExtrude","CAP_EDGE",EDGE,{"disambiguationData":[OSD([sQuery(id+"F9.wireOp",EDGE,"E142")])],"isStart":false});
            var Q215;
            {var subQ0=sQuery(id+"F9.wireOp",EDGE,"E142");var subQ3=sQuery(id+"F13.wireOp",EDGE,"E148.MirrorCS");var subQ4=makeQuery(id+"FyYUAefgu6xEfva_4.9.F14.opExtrude","SWEPT_FACE",FACE,{"disambiguationData":[OSD([subQ3])]});var subQ5=sQuery(id+"F13.wireOp",EDGE,"E147");var subQ6=makeQuery(id+"F14.opExtrude","SWEPT_FACE",FACE,{"disambiguationData":[OSD([subQ5])]});Q215=makeQuery(id+"FyYUAefgu6xEfva_4.10.F14.boolean.opBoolean","SPLIT",EDGE,{"disambiguationData":[TD([subQ4])],"derivedFrom":makeQuery(id+"FyYUAefgu6xEfva_4.9.F14.boolean.opBoolean","SPLIT",EDGE,{"disambiguationData":[TD([subQ6])],"derivedFrom":makeQuery(id+"FyYUAefgu6xEfva_4.8.F14.boolean.opBoolean","SPLIT",EDGE,{"disambiguationData":[TD([subQ6])],"derivedFrom":makeQuery(id+"FyYUAefgu6xEfva_4.7.F14.boolean.opBoolean","SPLIT",EDGE,{"disambiguationData":[TD([subQ6])],"derivedFrom":makeQuery(id+"FyYUAefgu6xEfva_4.6.F14.boolean.opBoolean","SPLIT",EDGE,{"disambiguationData":[TD([subQ6])],"derivedFrom":makeQuery(id+"FyYUAefgu6xEfva_4.5.F14.boolean.opBoolean","SPLIT",EDGE,{"disambiguationData":[TD([subQ6])],"derivedFrom":makeQuery(id+"FyYUAefgu6xEfva_4.4.F14.boolean.opBoolean","SPLIT",EDGE,{"disambiguationData":[TD([subQ6])],"derivedFrom":makeQuery(id+"FyYUAefgu6xEfva_4.3.F14.boolean.opBoolean","SPLIT",EDGE,{"disambiguationData":[TD([subQ6])],"derivedFrom":makeQuery(id+"FyYUAefgu6xEfva_4.2.F14.boolean.opBoolean","SPLIT",EDGE,{"disambiguationData":[TD([subQ6])],"derivedFrom":makeQuery(id+"FyYUAefgu6xEfva_4.1.F14.boolean.opBoolean","SPLIT",EDGE,{"disambiguationData":[TD([subQ6])],"derivedFrom":makeQuery(id+"F10.boolean.opBoolean","COPY",EDGE,{"derivedFrom":makeQuery(id+"F10.opExtrude","CAP_EDGE",EDGE,{"disambiguationData":[OSD([subQ0])],"isStart":false})})})})})})})})})})})});}
            var Q216;
            {var subQ0=sQuery(id+"F13.wireOp",EDGE,"E148.MirrorCS");var subQ1=sQuery(id+"F13.wireOp",EDGE,"E147");var subQ2=sQuery(id+"F11.wireOp",EDGE,"E143");var subQ16=makeQuery(id+"FyYUAefgu6xEfva_4.9.F14.opExtrude","SWEPT_FACE",FACE,{"disambiguationData":[OSD([subQ0])]});var subQ17=makeQuery(id+"F14.opExtrude","SWEPT_FACE",FACE,{"disambiguationData":[OSD([subQ1])]});Q216=makeQuery(id+"FyYUAefgu6xEfva_4.10.F14.boolean.opBoolean","SPLIT",EDGE,{"disambiguationData":[TD([subQ16])],"derivedFrom":makeQuery(id+"FyYUAefgu6xEfva_4.9.F14.boolean.opBoolean","SPLIT",EDGE,{"disambiguationData":[TD([subQ17])],"derivedFrom":makeQuery(id+"FyYUAefgu6xEfva_4.8.F14.boolean.opBoolean","SPLIT",EDGE,{"disambiguationData":[TD([subQ17])],"derivedFrom":makeQuery(id+"FyYUAefgu6xEfva_4.7.F14.boolean.opBoolean","SPLIT",EDGE,{"disambiguationData":[TD([subQ17])],"derivedFrom":makeQuery(id+"FyYUAefgu6xEfva_4.6.F14.boolean.opBoolean","SPLIT",EDGE,{"disambiguationData":[TD([subQ17])],"derivedFrom":makeQuery(id+"FyYUAefgu6xEfva_4.5.F14.boolean.opBoolean","SPLIT",EDGE,{"disambiguationData":[TD([subQ17])],"derivedFrom":makeQuery(id+"FyYUAefgu6xEfva_4.4.F14.boolean.opBoolean","SPLIT",EDGE,{"disambiguationData":[TD([subQ17])],"derivedFrom":makeQuery(id+"FyYUAefgu6xEfva_4.3.F14.boolean.opBoolean","SPLIT",EDGE,{"disambiguationData":[TD([subQ17])],"derivedFrom":makeQuery(id+"FyYUAefgu6xEfva_4.2.F14.boolean.opBoolean","SPLIT",EDGE,{"disambiguationData":[TD([subQ17])],"derivedFrom":makeQuery(id+"FyYUAefgu6xEfva_4.1.F14.boolean.opBoolean","SPLIT",EDGE,{"disambiguationData":[TD([subQ17])],"derivedFrom":makeQuery(id+"F12.opExtrude","CAP_EDGE",EDGE,{"disambiguationData":[OSD([subQ2])],"isStart":false})})})})})})})})})})});}
            var Q217;
            Q217=makeQuery(id+"FyYUAefgu6xEfva_4.42.F14.opExtrude","SWEPT_EDGE",EDGE,{"disambiguationData":[OSD([sQuery(id+"F9.wireOp",EDGE,"E142"),sQuery(id+"F13.wireOp",EDGE,"E147")])]});
            var Q218;
            Q218=makeQuery(id+"FyYUAefgu6xEfva_4.42.F14.opExtrude","SWEPT_EDGE",EDGE,{"disambiguationData":[OSD([sQuery(id+"F11.wireOp",EDGE,"E143"),sQuery(id+"F13.wireOp",EDGE,"E147")])]});
            var Q219;
            Q219=makeQuery(id+"FyYUAefgu6xEfva_4.42.F14.opExtrude","SWEPT_EDGE",EDGE,{"disambiguationData":[OSD([sQuery(id+"F9.wireOp",EDGE,"E142"),sQuery(id+"F13.wireOp",EDGE,"E148.MirrorCS")])]});
            var Q220;
            Q220=makeQuery(id+"FyYUAefgu6xEfva_4.42.F14.opExtrude","SWEPT_EDGE",EDGE,{"disambiguationData":[OSD([sQuery(id+"F11.wireOp",EDGE,"E143"),sQuery(id+"F13.wireOp",EDGE,"E148.MirrorCS")])]});
            var Q221;
            Q221=makeQuery(id+"FyYUAefgu6xEfva_4.42.F14.opExtrude","CAP_EDGE",EDGE,{"disambiguationData":[OSD([sQuery(id+"F13.wireOp",EDGE,"E147")])],"isStart":true});
            var Q222;
            Q222=makeQuery(id+"FyYUAefgu6xEfva_4.42.F14.opExtrude","CAP_EDGE",EDGE,{"disambiguationData":[OSD([sQuery(id+"F13.wireOp",EDGE,"E148.MirrorCS")])],"isStart":true});
            var Q223;
            {var subQ0=sQuery(id+"F9.wireOp",EDGE,"E142");var subQ3=sQuery(id+"F13.wireOp",EDGE,"E147");var subQ4=sQuery(id+"F13.wireOp",EDGE,"E148.MirrorCS");var subQ5=makeQuery(id+"FyYUAefgu6xEfva_4.41.F14.opExtrude","SWEPT_FACE",FACE,{"disambiguationData":[OSD([subQ4])]});var subQ6=makeQuery(id+"F14.opExtrude","SWEPT_FACE",FACE,{"disambiguationData":[OSD([subQ3])]});Q223=makeQuery(id+"FyYUAefgu6xEfva_4.42.F14.boolean.opBoolean","SPLIT",EDGE,{"disambiguationData":[TD([subQ5])],"derivedFrom":makeQuery(id+"FyYUAefgu6xEfva_4.41.F14.boolean.opBoolean","SPLIT",EDGE,{"disambiguationData":[TD([subQ6])],"derivedFrom":makeQuery(id+"FyYUAefgu6xEfva_4.40.F14.boolean.opBoolean","SPLIT",EDGE,{"disambiguationData":[TD([subQ6])],"derivedFrom":makeQuery(id+"FyYUAefgu6xEfva_4.39.F14.boolean.opBoolean","SPLIT",EDGE,{"disambiguationData":[TD([subQ6])],"derivedFrom":makeQuery(id+"FyYUAefgu6xEfva_4.38.F14.boolean.opBoolean","SPLIT",EDGE,{"disambiguationData":[TD([subQ6])],"derivedFrom":makeQuery(id+"FyYUAefgu6xEfva_4.37.F14.boolean.opBoolean","SPLIT",EDGE,{"disambiguationData":[TD([subQ6])],"derivedFrom":makeQuery(id+"FyYUAefgu6xEfva_4.36.F14.boolean.opBoolean","SPLIT",EDGE,{"disambiguationData":[TD([subQ6])],"derivedFrom":makeQuery(id+"FyYUAefgu6xEfva_4.35.F14.boolean.opBoolean","SPLIT",EDGE,{"disambiguationData":[TD([subQ6])],"derivedFrom":makeQuery(id+"FyYUAefgu6xEfva_4.34.F14.boolean.opBoolean","SPLIT",EDGE,{"disambiguationData":[TD([subQ6])],"derivedFrom":makeQuery(id+"FyYUAefgu6xEfva_4.33.F14.boolean.opBoolean","SPLIT",EDGE,{"disambiguationData":[TD([subQ6])],"derivedFrom":makeQuery(id+"FyYUAefgu6xEfva_4.32.F14.boolean.opBoolean","SPLIT",EDGE,{"disambiguationData":[TD([subQ6])],"derivedFrom":makeQuery(id+"FyYUAefgu6xEfva_4.31.F14.boolean.opBoolean","SPLIT",EDGE,{"disambiguationData":[TD([subQ6])],"derivedFrom":makeQuery(id+"FyYUAefgu6xEfva_4.30.F14.boolean.opBoolean","SPLIT",EDGE,{"disambiguationData":[TD([subQ6])],"derivedFrom":makeQuery(id+"FyYUAefgu6xEfva_4.29.F14.boolean.opBoolean","SPLIT",EDGE,{"disambiguationData":[TD([subQ6])],"derivedFrom":makeQuery(id+"FyYUAefgu6xEfva_4.28.F14.boolean.opBoolean","SPLIT",EDGE,{"disambiguationData":[TD([subQ6])],"derivedFrom":makeQuery(id+"FyYUAefgu6xEfva_4.27.F14.boolean.opBoolean","SPLIT",EDGE,{"disambiguationData":[TD([subQ6])],"derivedFrom":makeQuery(id+"FyYUAefgu6xEfva_4.26.F14.boolean.opBoolean","SPLIT",EDGE,{"disambiguationData":[TD([subQ6])],"derivedFrom":makeQuery(id+"FyYUAefgu6xEfva_4.25.F14.boolean.opBoolean","SPLIT",EDGE,{"disambiguationData":[TD([subQ6])],"derivedFrom":makeQuery(id+"FyYUAefgu6xEfva_4.24.F14.boolean.opBoolean","SPLIT",EDGE,{"disambiguationData":[TD([subQ6])],"derivedFrom":makeQuery(id+"FyYUAefgu6xEfva_4.23.F14.boolean.opBoolean","SPLIT",EDGE,{"disambiguationData":[TD([subQ6])],"derivedFrom":makeQuery(id+"FyYUAefgu6xEfva_4.22.F14.boolean.opBoolean","SPLIT",EDGE,{"disambiguationData":[TD([subQ6])],"derivedFrom":makeQuery(id+"FyYUAefgu6xEfva_4.21.F14.boolean.opBoolean","SPLIT",EDGE,{"disambiguationData":[TD([subQ6])],"derivedFrom":makeQuery(id+"FyYUAefgu6xEfva_4.20.F14.boolean.opBoolean","SPLIT",EDGE,{"disambiguationData":[TD([subQ6])],"derivedFrom":makeQuery(id+"FyYUAefgu6xEfva_4.19.F14.boolean.opBoolean","SPLIT",EDGE,{"disambiguationData":[TD([subQ6])],"derivedFrom":makeQuery(id+"FyYUAefgu6xEfva_4.18.F14.boolean.opBoolean","SPLIT",EDGE,{"disambiguationData":[TD([subQ6])],"derivedFrom":makeQuery(id+"FyYUAefgu6xEfva_4.17.F14.boolean.opBoolean","SPLIT",EDGE,{"disambiguationData":[TD([subQ6])],"derivedFrom":makeQuery(id+"FyYUAefgu6xEfva_4.16.F14.boolean.opBoolean","SPLIT",EDGE,{"disambiguationData":[TD([subQ6])],"derivedFrom":makeQuery(id+"FyYUAefgu6xEfva_4.15.F14.boolean.opBoolean","SPLIT",EDGE,{"disambiguationData":[TD([subQ6])],"derivedFrom":makeQuery(id+"FyYUAefgu6xEfva_4.14.F14.boolean.opBoolean","SPLIT",EDGE,{"disambiguationData":[TD([subQ6])],"derivedFrom":makeQuery(id+"FyYUAefgu6xEfva_4.13.F14.boolean.opBoolean","SPLIT",EDGE,{"disambiguationData":[TD([subQ6])],"derivedFrom":makeQuery(id+"FyYUAefgu6xEfva_4.12.F14.boolean.opBoolean","SPLIT",EDGE,{"disambiguationData":[TD([subQ6])],"derivedFrom":makeQuery(id+"FyYUAefgu6xEfva_4.11.F14.boolean.opBoolean","SPLIT",EDGE,{"disambiguationData":[TD([subQ6])],"derivedFrom":makeQuery(id+"FyYUAefgu6xEfva_4.10.F14.boolean.opBoolean","SPLIT",EDGE,{"disambiguationData":[TD([subQ6])],"derivedFrom":makeQuery(id+"FyYUAefgu6xEfva_4.9.F14.boolean.opBoolean","SPLIT",EDGE,{"disambiguationData":[TD([subQ6])],"derivedFrom":makeQuery(id+"FyYUAefgu6xEfva_4.8.F14.boolean.opBoolean","SPLIT",EDGE,{"disambiguationData":[TD([subQ6])],"derivedFrom":makeQuery(id+"FyYUAefgu6xEfva_4.7.F14.boolean.opBoolean","SPLIT",EDGE,{"disambiguationData":[TD([subQ6])],"derivedFrom":makeQuery(id+"FyYUAefgu6xEfva_4.6.F14.boolean.opBoolean","SPLIT",EDGE,{"disambiguationData":[TD([subQ6])],"derivedFrom":makeQuery(id+"FyYUAefgu6xEfva_4.5.F14.boolean.opBoolean","SPLIT",EDGE,{"disambiguationData":[TD([subQ6])],"derivedFrom":makeQuery(id+"FyYUAefgu6xEfva_4.4.F14.boolean.opBoolean","SPLIT",EDGE,{"disambiguationData":[TD([subQ6])],"derivedFrom":makeQuery(id+"FyYUAefgu6xEfva_4.3.F14.boolean.opBoolean","SPLIT",EDGE,{"disambiguationData":[TD([subQ6])],"derivedFrom":makeQuery(id+"FyYUAefgu6xEfva_4.2.F14.boolean.opBoolean","SPLIT",EDGE,{"disambiguationData":[TD([subQ6])],"derivedFrom":makeQuery(id+"FyYUAefgu6xEfva_4.1.F14.boolean.opBoolean","SPLIT",EDGE,{"disambiguationData":[TD([subQ6])],"derivedFrom":makeQuery(id+"F10.boolean.opBoolean","COPY",EDGE,{"derivedFrom":makeQuery(id+"F10.opExtrude","CAP_EDGE",EDGE,{"disambiguationData":[OSD([subQ0])],"isStart":false})})})})})})})})})})})})})})})})})})})})})})})})})})})})})})})})})})})})})})})})})})})});}
            var Q224;
            {var subQ0=sQuery(id+"F13.wireOp",EDGE,"E148.MirrorCS");var subQ1=sQuery(id+"F13.wireOp",EDGE,"E147");var subQ2=sQuery(id+"F11.wireOp",EDGE,"E143");var subQ13=makeQuery(id+"FyYUAefgu6xEfva_4.41.F14.opExtrude","SWEPT_FACE",FACE,{"disambiguationData":[OSD([subQ0])]});var subQ49=makeQuery(id+"F14.opExtrude","SWEPT_FACE",FACE,{"disambiguationData":[OSD([subQ1])]});Q224=makeQuery(id+"FyYUAefgu6xEfva_4.42.F14.boolean.opBoolean","SPLIT",EDGE,{"disambiguationData":[TD([subQ13])],"derivedFrom":makeQuery(id+"FyYUAefgu6xEfva_4.41.F14.boolean.opBoolean","SPLIT",EDGE,{"disambiguationData":[TD([subQ49])],"derivedFrom":makeQuery(id+"FyYUAefgu6xEfva_4.40.F14.boolean.opBoolean","SPLIT",EDGE,{"disambiguationData":[TD([subQ49])],"derivedFrom":makeQuery(id+"FyYUAefgu6xEfva_4.39.F14.boolean.opBoolean","SPLIT",EDGE,{"disambiguationData":[TD([subQ49])],"derivedFrom":makeQuery(id+"FyYUAefgu6xEfva_4.38.F14.boolean.opBoolean","SPLIT",EDGE,{"disambiguationData":[TD([subQ49])],"derivedFrom":makeQuery(id+"FyYUAefgu6xEfva_4.37.F14.boolean.opBoolean","SPLIT",EDGE,{"disambiguationData":[TD([subQ49])],"derivedFrom":makeQuery(id+"FyYUAefgu6xEfva_4.36.F14.boolean.opBoolean","SPLIT",EDGE,{"disambiguationData":[TD([subQ49])],"derivedFrom":makeQuery(id+"FyYUAefgu6xEfva_4.35.F14.boolean.opBoolean","SPLIT",EDGE,{"disambiguationData":[TD([subQ49])],"derivedFrom":makeQuery(id+"FyYUAefgu6xEfva_4.34.F14.boolean.opBoolean","SPLIT",EDGE,{"disambiguationData":[TD([subQ49])],"derivedFrom":makeQuery(id+"FyYUAefgu6xEfva_4.33.F14.boolean.opBoolean","SPLIT",EDGE,{"disambiguationData":[TD([subQ49])],"derivedFrom":makeQuery(id+"FyYUAefgu6xEfva_4.32.F14.boolean.opBoolean","SPLIT",EDGE,{"disambiguationData":[TD([subQ49])],"derivedFrom":makeQuery(id+"FyYUAefgu6xEfva_4.31.F14.boolean.opBoolean","SPLIT",EDGE,{"disambiguationData":[TD([subQ49])],"derivedFrom":makeQuery(id+"FyYUAefgu6xEfva_4.30.F14.boolean.opBoolean","SPLIT",EDGE,{"disambiguationData":[TD([subQ49])],"derivedFrom":makeQuery(id+"FyYUAefgu6xEfva_4.29.F14.boolean.opBoolean","SPLIT",EDGE,{"disambiguationData":[TD([subQ49])],"derivedFrom":makeQuery(id+"FyYUAefgu6xEfva_4.28.F14.boolean.opBoolean","SPLIT",EDGE,{"disambiguationData":[TD([subQ49])],"derivedFrom":makeQuery(id+"FyYUAefgu6xEfva_4.27.F14.boolean.opBoolean","SPLIT",EDGE,{"disambiguationData":[TD([subQ49])],"derivedFrom":makeQuery(id+"FyYUAefgu6xEfva_4.26.F14.boolean.opBoolean","SPLIT",EDGE,{"disambiguationData":[TD([subQ49])],"derivedFrom":makeQuery(id+"FyYUAefgu6xEfva_4.25.F14.boolean.opBoolean","SPLIT",EDGE,{"disambiguationData":[TD([subQ49])],"derivedFrom":makeQuery(id+"FyYUAefgu6xEfva_4.24.F14.boolean.opBoolean","SPLIT",EDGE,{"disambiguationData":[TD([subQ49])],"derivedFrom":makeQuery(id+"FyYUAefgu6xEfva_4.23.F14.boolean.opBoolean","SPLIT",EDGE,{"disambiguationData":[TD([subQ49])],"derivedFrom":makeQuery(id+"FyYUAefgu6xEfva_4.22.F14.boolean.opBoolean","SPLIT",EDGE,{"disambiguationData":[TD([subQ49])],"derivedFrom":makeQuery(id+"FyYUAefgu6xEfva_4.21.F14.boolean.opBoolean","SPLIT",EDGE,{"disambiguationData":[TD([subQ49])],"derivedFrom":makeQuery(id+"FyYUAefgu6xEfva_4.20.F14.boolean.opBoolean","SPLIT",EDGE,{"disambiguationData":[TD([subQ49])],"derivedFrom":makeQuery(id+"FyYUAefgu6xEfva_4.19.F14.boolean.opBoolean","SPLIT",EDGE,{"disambiguationData":[TD([subQ49])],"derivedFrom":makeQuery(id+"FyYUAefgu6xEfva_4.18.F14.boolean.opBoolean","SPLIT",EDGE,{"disambiguationData":[TD([subQ49])],"derivedFrom":makeQuery(id+"FyYUAefgu6xEfva_4.17.F14.boolean.opBoolean","SPLIT",EDGE,{"disambiguationData":[TD([subQ49])],"derivedFrom":makeQuery(id+"FyYUAefgu6xEfva_4.16.F14.boolean.opBoolean","SPLIT",EDGE,{"disambiguationData":[TD([subQ49])],"derivedFrom":makeQuery(id+"FyYUAefgu6xEfva_4.15.F14.boolean.opBoolean","SPLIT",EDGE,{"disambiguationData":[TD([subQ49])],"derivedFrom":makeQuery(id+"FyYUAefgu6xEfva_4.14.F14.boolean.opBoolean","SPLIT",EDGE,{"disambiguationData":[TD([subQ49])],"derivedFrom":makeQuery(id+"FyYUAefgu6xEfva_4.13.F14.boolean.opBoolean","SPLIT",EDGE,{"disambiguationData":[TD([subQ49])],"derivedFrom":makeQuery(id+"FyYUAefgu6xEfva_4.12.F14.boolean.opBoolean","SPLIT",EDGE,{"disambiguationData":[TD([subQ49])],"derivedFrom":makeQuery(id+"FyYUAefgu6xEfva_4.11.F14.boolean.opBoolean","SPLIT",EDGE,{"disambiguationData":[TD([subQ49])],"derivedFrom":makeQuery(id+"FyYUAefgu6xEfva_4.10.F14.boolean.opBoolean","SPLIT",EDGE,{"disambiguationData":[TD([subQ49])],"derivedFrom":makeQuery(id+"FyYUAefgu6xEfva_4.9.F14.boolean.opBoolean","SPLIT",EDGE,{"disambiguationData":[TD([subQ49])],"derivedFrom":makeQuery(id+"FyYUAefgu6xEfva_4.8.F14.boolean.opBoolean","SPLIT",EDGE,{"disambiguationData":[TD([subQ49])],"derivedFrom":makeQuery(id+"FyYUAefgu6xEfva_4.7.F14.boolean.opBoolean","SPLIT",EDGE,{"disambiguationData":[TD([subQ49])],"derivedFrom":makeQuery(id+"FyYUAefgu6xEfva_4.6.F14.boolean.opBoolean","SPLIT",EDGE,{"disambiguationData":[TD([subQ49])],"derivedFrom":makeQuery(id+"FyYUAefgu6xEfva_4.5.F14.boolean.opBoolean","SPLIT",EDGE,{"disambiguationData":[TD([subQ49])],"derivedFrom":makeQuery(id+"FyYUAefgu6xEfva_4.4.F14.boolean.opBoolean","SPLIT",EDGE,{"disambiguationData":[TD([subQ49])],"derivedFrom":makeQuery(id+"FyYUAefgu6xEfva_4.3.F14.boolean.opBoolean","SPLIT",EDGE,{"disambiguationData":[TD([subQ49])],"derivedFrom":makeQuery(id+"FyYUAefgu6xEfva_4.2.F14.boolean.opBoolean","SPLIT",EDGE,{"disambiguationData":[TD([subQ49])],"derivedFrom":makeQuery(id+"FyYUAefgu6xEfva_4.1.F14.boolean.opBoolean","SPLIT",EDGE,{"disambiguationData":[TD([subQ49])],"derivedFrom":makeQuery(id+"F12.opExtrude","CAP_EDGE",EDGE,{"disambiguationData":[OSD([subQ2])],"isStart":false})})})})})})})})})})})})})})})})})})})})})})})})})})})})})})})})})})})})})})})})})})});}
            var Q225;
            Q225=makeQuery(id+"FyYUAefgu6xEfva_4.11.F14.opExtrude","CAP_EDGE",EDGE,{"disambiguationData":[OSD([sQuery(id+"F13.wireOp",EDGE,"E148.MirrorCS")])],"isStart":false});
            var Q226;
            Q226=makeQuery(id+"FyYUAefgu6xEfva_4.11.F14.opExtrude","SWEPT_EDGE",EDGE,{"disambiguationData":[OSD([sQuery(id+"F9.wireOp",EDGE,"E142"),sQuery(id+"F13.wireOp",EDGE,"E147")])]});
            var Q227;
            Q227=makeQuery(id+"FyYUAefgu6xEfva_4.11.F14.opExtrude","SWEPT_EDGE",EDGE,{"disambiguationData":[OSD([sQuery(id+"F11.wireOp",EDGE,"E143"),sQuery(id+"F13.wireOp",EDGE,"E147")])]});
            var Q228;
            Q228=makeQuery(id+"FyYUAefgu6xEfva_4.11.F14.opExtrude","CAP_EDGE",EDGE,{"disambiguationData":[OSD([sQuery(id+"F9.wireOp",EDGE,"E142")])],"isStart":false});
            var Q229;
            {var subQ0=sQuery(id+"F9.wireOp",EDGE,"E142");var subQ2=sQuery(id+"F13.wireOp",EDGE,"E148.MirrorCS");var subQ3=makeQuery(id+"FyYUAefgu6xEfva_4.10.F14.opExtrude","SWEPT_FACE",FACE,{"disambiguationData":[OSD([subQ2])]});var subQ5=sQuery(id+"F13.wireOp",EDGE,"E147");var subQ6=makeQuery(id+"F14.opExtrude","SWEPT_FACE",FACE,{"disambiguationData":[OSD([subQ5])]});Q229=makeQuery(id+"FyYUAefgu6xEfva_4.11.F14.boolean.opBoolean","SPLIT",EDGE,{"disambiguationData":[TD([subQ3])],"derivedFrom":makeQuery(id+"FyYUAefgu6xEfva_4.10.F14.boolean.opBoolean","SPLIT",EDGE,{"disambiguationData":[TD([subQ6])],"derivedFrom":makeQuery(id+"FyYUAefgu6xEfva_4.9.F14.boolean.opBoolean","SPLIT",EDGE,{"disambiguationData":[TD([subQ6])],"derivedFrom":makeQuery(id+"FyYUAefgu6xEfva_4.8.F14.boolean.opBoolean","SPLIT",EDGE,{"disambiguationData":[TD([subQ6])],"derivedFrom":makeQuery(id+"FyYUAefgu6xEfva_4.7.F14.boolean.opBoolean","SPLIT",EDGE,{"disambiguationData":[TD([subQ6])],"derivedFrom":makeQuery(id+"FyYUAefgu6xEfva_4.6.F14.boolean.opBoolean","SPLIT",EDGE,{"disambiguationData":[TD([subQ6])],"derivedFrom":makeQuery(id+"FyYUAefgu6xEfva_4.5.F14.boolean.opBoolean","SPLIT",EDGE,{"disambiguationData":[TD([subQ6])],"derivedFrom":makeQuery(id+"FyYUAefgu6xEfva_4.4.F14.boolean.opBoolean","SPLIT",EDGE,{"disambiguationData":[TD([subQ6])],"derivedFrom":makeQuery(id+"FyYUAefgu6xEfva_4.3.F14.boolean.opBoolean","SPLIT",EDGE,{"disambiguationData":[TD([subQ6])],"derivedFrom":makeQuery(id+"FyYUAefgu6xEfva_4.2.F14.boolean.opBoolean","SPLIT",EDGE,{"disambiguationData":[TD([subQ6])],"derivedFrom":makeQuery(id+"FyYUAefgu6xEfva_4.1.F14.boolean.opBoolean","SPLIT",EDGE,{"disambiguationData":[TD([subQ6])],"derivedFrom":makeQuery(id+"F10.boolean.opBoolean","COPY",EDGE,{"derivedFrom":makeQuery(id+"F10.opExtrude","CAP_EDGE",EDGE,{"disambiguationData":[OSD([subQ0])],"isStart":false})})})})})})})})})})})})});}
            var Q230;
            {var subQ0=sQuery(id+"F13.wireOp",EDGE,"E148.MirrorCS");var subQ1=sQuery(id+"F13.wireOp",EDGE,"E147");var subQ2=sQuery(id+"F11.wireOp",EDGE,"E143");var subQ17=makeQuery(id+"FyYUAefgu6xEfva_4.10.F14.opExtrude","SWEPT_FACE",FACE,{"disambiguationData":[OSD([subQ0])]});var subQ18=makeQuery(id+"F14.opExtrude","SWEPT_FACE",FACE,{"disambiguationData":[OSD([subQ1])]});Q230=makeQuery(id+"FyYUAefgu6xEfva_4.11.F14.boolean.opBoolean","SPLIT",EDGE,{"disambiguationData":[TD([subQ17])],"derivedFrom":makeQuery(id+"FyYUAefgu6xEfva_4.10.F14.boolean.opBoolean","SPLIT",EDGE,{"disambiguationData":[TD([subQ18])],"derivedFrom":makeQuery(id+"FyYUAefgu6xEfva_4.9.F14.boolean.opBoolean","SPLIT",EDGE,{"disambiguationData":[TD([subQ18])],"derivedFrom":makeQuery(id+"FyYUAefgu6xEfva_4.8.F14.boolean.opBoolean","SPLIT",EDGE,{"disambiguationData":[TD([subQ18])],"derivedFrom":makeQuery(id+"FyYUAefgu6xEfva_4.7.F14.boolean.opBoolean","SPLIT",EDGE,{"disambiguationData":[TD([subQ18])],"derivedFrom":makeQuery(id+"FyYUAefgu6xEfva_4.6.F14.boolean.opBoolean","SPLIT",EDGE,{"disambiguationData":[TD([subQ18])],"derivedFrom":makeQuery(id+"FyYUAefgu6xEfva_4.5.F14.boolean.opBoolean","SPLIT",EDGE,{"disambiguationData":[TD([subQ18])],"derivedFrom":makeQuery(id+"FyYUAefgu6xEfva_4.4.F14.boolean.opBoolean","SPLIT",EDGE,{"disambiguationData":[TD([subQ18])],"derivedFrom":makeQuery(id+"FyYUAefgu6xEfva_4.3.F14.boolean.opBoolean","SPLIT",EDGE,{"disambiguationData":[TD([subQ18])],"derivedFrom":makeQuery(id+"FyYUAefgu6xEfva_4.2.F14.boolean.opBoolean","SPLIT",EDGE,{"disambiguationData":[TD([subQ18])],"derivedFrom":makeQuery(id+"FyYUAefgu6xEfva_4.1.F14.boolean.opBoolean","SPLIT",EDGE,{"disambiguationData":[TD([subQ18])],"derivedFrom":makeQuery(id+"F12.opExtrude","CAP_EDGE",EDGE,{"disambiguationData":[OSD([subQ2])],"isStart":false})})})})})})})})})})})});}
            var Q231;
            Q231=makeQuery(id+"FyYUAefgu6xEfva_4.43.F14.opExtrude","SWEPT_EDGE",EDGE,{"disambiguationData":[OSD([sQuery(id+"F9.wireOp",EDGE,"E142"),sQuery(id+"F13.wireOp",EDGE,"E147")])]});
            var Q232;
            Q232=makeQuery(id+"FyYUAefgu6xEfva_4.43.F14.opExtrude","SWEPT_EDGE",EDGE,{"disambiguationData":[OSD([sQuery(id+"F11.wireOp",EDGE,"E143"),sQuery(id+"F13.wireOp",EDGE,"E147")])]});
            var Q233;
            Q233=makeQuery(id+"FyYUAefgu6xEfva_4.43.F14.opExtrude","SWEPT_EDGE",EDGE,{"disambiguationData":[OSD([sQuery(id+"F9.wireOp",EDGE,"E142"),sQuery(id+"F13.wireOp",EDGE,"E148.MirrorCS")])]});
            var Q234;
            Q234=makeQuery(id+"FyYUAefgu6xEfva_4.43.F14.opExtrude","SWEPT_EDGE",EDGE,{"disambiguationData":[OSD([sQuery(id+"F11.wireOp",EDGE,"E143"),sQuery(id+"F13.wireOp",EDGE,"E148.MirrorCS")])]});
            var Q235;
            Q235=makeQuery(id+"FyYUAefgu6xEfva_4.43.F14.opExtrude","CAP_EDGE",EDGE,{"disambiguationData":[OSD([sQuery(id+"F13.wireOp",EDGE,"E147")])],"isStart":true});
            var Q236;
            {var subQ0=sQuery(id+"F9.wireOp",EDGE,"E142");var subQ3=sQuery(id+"F13.wireOp",EDGE,"E148.MirrorCS");var subQ4=makeQuery(id+"FyYUAefgu6xEfva_4.42.F14.opExtrude","SWEPT_FACE",FACE,{"disambiguationData":[OSD([subQ3])]});var subQ5=sQuery(id+"F13.wireOp",EDGE,"E147");var subQ6=makeQuery(id+"F14.opExtrude","SWEPT_FACE",FACE,{"disambiguationData":[OSD([subQ5])]});Q236=makeQuery(id+"FyYUAefgu6xEfva_4.43.F14.boolean.opBoolean","SPLIT",EDGE,{"disambiguationData":[TD([subQ4])],"derivedFrom":makeQuery(id+"FyYUAefgu6xEfva_4.42.F14.boolean.opBoolean","SPLIT",EDGE,{"disambiguationData":[TD([subQ6])],"derivedFrom":makeQuery(id+"FyYUAefgu6xEfva_4.41.F14.boolean.opBoolean","SPLIT",EDGE,{"disambiguationData":[TD([subQ6])],"derivedFrom":makeQuery(id+"FyYUAefgu6xEfva_4.40.F14.boolean.opBoolean","SPLIT",EDGE,{"disambiguationData":[TD([subQ6])],"derivedFrom":makeQuery(id+"FyYUAefgu6xEfva_4.39.F14.boolean.opBoolean","SPLIT",EDGE,{"disambiguationData":[TD([subQ6])],"derivedFrom":makeQuery(id+"FyYUAefgu6xEfva_4.38.F14.boolean.opBoolean","SPLIT",EDGE,{"disambiguationData":[TD([subQ6])],"derivedFrom":makeQuery(id+"FyYUAefgu6xEfva_4.37.F14.boolean.opBoolean","SPLIT",EDGE,{"disambiguationData":[TD([subQ6])],"derivedFrom":makeQuery(id+"FyYUAefgu6xEfva_4.36.F14.boolean.opBoolean","SPLIT",EDGE,{"disambiguationData":[TD([subQ6])],"derivedFrom":makeQuery(id+"FyYUAefgu6xEfva_4.35.F14.boolean.opBoolean","SPLIT",EDGE,{"disambiguationData":[TD([subQ6])],"derivedFrom":makeQuery(id+"FyYUAefgu6xEfva_4.34.F14.boolean.opBoolean","SPLIT",EDGE,{"disambiguationData":[TD([subQ6])],"derivedFrom":makeQuery(id+"FyYUAefgu6xEfva_4.33.F14.boolean.opBoolean","SPLIT",EDGE,{"disambiguationData":[TD([subQ6])],"derivedFrom":makeQuery(id+"FyYUAefgu6xEfva_4.32.F14.boolean.opBoolean","SPLIT",EDGE,{"disambiguationData":[TD([subQ6])],"derivedFrom":makeQuery(id+"FyYUAefgu6xEfva_4.31.F14.boolean.opBoolean","SPLIT",EDGE,{"disambiguationData":[TD([subQ6])],"derivedFrom":makeQuery(id+"FyYUAefgu6xEfva_4.30.F14.boolean.opBoolean","SPLIT",EDGE,{"disambiguationData":[TD([subQ6])],"derivedFrom":makeQuery(id+"FyYUAefgu6xEfva_4.29.F14.boolean.opBoolean","SPLIT",EDGE,{"disambiguationData":[TD([subQ6])],"derivedFrom":makeQuery(id+"FyYUAefgu6xEfva_4.28.F14.boolean.opBoolean","SPLIT",EDGE,{"disambiguationData":[TD([subQ6])],"derivedFrom":makeQuery(id+"FyYUAefgu6xEfva_4.27.F14.boolean.opBoolean","SPLIT",EDGE,{"disambiguationData":[TD([subQ6])],"derivedFrom":makeQuery(id+"FyYUAefgu6xEfva_4.26.F14.boolean.opBoolean","SPLIT",EDGE,{"disambiguationData":[TD([subQ6])],"derivedFrom":makeQuery(id+"FyYUAefgu6xEfva_4.25.F14.boolean.opBoolean","SPLIT",EDGE,{"disambiguationData":[TD([subQ6])],"derivedFrom":makeQuery(id+"FyYUAefgu6xEfva_4.24.F14.boolean.opBoolean","SPLIT",EDGE,{"disambiguationData":[TD([subQ6])],"derivedFrom":makeQuery(id+"FyYUAefgu6xEfva_4.23.F14.boolean.opBoolean","SPLIT",EDGE,{"disambiguationData":[TD([subQ6])],"derivedFrom":makeQuery(id+"FyYUAefgu6xEfva_4.22.F14.boolean.opBoolean","SPLIT",EDGE,{"disambiguationData":[TD([subQ6])],"derivedFrom":makeQuery(id+"FyYUAefgu6xEfva_4.21.F14.boolean.opBoolean","SPLIT",EDGE,{"disambiguationData":[TD([subQ6])],"derivedFrom":makeQuery(id+"FyYUAefgu6xEfva_4.20.F14.boolean.opBoolean","SPLIT",EDGE,{"disambiguationData":[TD([subQ6])],"derivedFrom":makeQuery(id+"FyYUAefgu6xEfva_4.19.F14.boolean.opBoolean","SPLIT",EDGE,{"disambiguationData":[TD([subQ6])],"derivedFrom":makeQuery(id+"FyYUAefgu6xEfva_4.18.F14.boolean.opBoolean","SPLIT",EDGE,{"disambiguationData":[TD([subQ6])],"derivedFrom":makeQuery(id+"FyYUAefgu6xEfva_4.17.F14.boolean.opBoolean","SPLIT",EDGE,{"disambiguationData":[TD([subQ6])],"derivedFrom":makeQuery(id+"FyYUAefgu6xEfva_4.16.F14.boolean.opBoolean","SPLIT",EDGE,{"disambiguationData":[TD([subQ6])],"derivedFrom":makeQuery(id+"FyYUAefgu6xEfva_4.15.F14.boolean.opBoolean","SPLIT",EDGE,{"disambiguationData":[TD([subQ6])],"derivedFrom":makeQuery(id+"FyYUAefgu6xEfva_4.14.F14.boolean.opBoolean","SPLIT",EDGE,{"disambiguationData":[TD([subQ6])],"derivedFrom":makeQuery(id+"FyYUAefgu6xEfva_4.13.F14.boolean.opBoolean","SPLIT",EDGE,{"disambiguationData":[TD([subQ6])],"derivedFrom":makeQuery(id+"FyYUAefgu6xEfva_4.12.F14.boolean.opBoolean","SPLIT",EDGE,{"disambiguationData":[TD([subQ6])],"derivedFrom":makeQuery(id+"FyYUAefgu6xEfva_4.11.F14.boolean.opBoolean","SPLIT",EDGE,{"disambiguationData":[TD([subQ6])],"derivedFrom":makeQuery(id+"FyYUAefgu6xEfva_4.10.F14.boolean.opBoolean","SPLIT",EDGE,{"disambiguationData":[TD([subQ6])],"derivedFrom":makeQuery(id+"FyYUAefgu6xEfva_4.9.F14.boolean.opBoolean","SPLIT",EDGE,{"disambiguationData":[TD([subQ6])],"derivedFrom":makeQuery(id+"FyYUAefgu6xEfva_4.8.F14.boolean.opBoolean","SPLIT",EDGE,{"disambiguationData":[TD([subQ6])],"derivedFrom":makeQuery(id+"FyYUAefgu6xEfva_4.7.F14.boolean.opBoolean","SPLIT",EDGE,{"disambiguationData":[TD([subQ6])],"derivedFrom":makeQuery(id+"FyYUAefgu6xEfva_4.6.F14.boolean.opBoolean","SPLIT",EDGE,{"disambiguationData":[TD([subQ6])],"derivedFrom":makeQuery(id+"FyYUAefgu6xEfva_4.5.F14.boolean.opBoolean","SPLIT",EDGE,{"disambiguationData":[TD([subQ6])],"derivedFrom":makeQuery(id+"FyYUAefgu6xEfva_4.4.F14.boolean.opBoolean","SPLIT",EDGE,{"disambiguationData":[TD([subQ6])],"derivedFrom":makeQuery(id+"FyYUAefgu6xEfva_4.3.F14.boolean.opBoolean","SPLIT",EDGE,{"disambiguationData":[TD([subQ6])],"derivedFrom":makeQuery(id+"FyYUAefgu6xEfva_4.2.F14.boolean.opBoolean","SPLIT",EDGE,{"disambiguationData":[TD([subQ6])],"derivedFrom":makeQuery(id+"FyYUAefgu6xEfva_4.1.F14.boolean.opBoolean","SPLIT",EDGE,{"disambiguationData":[TD([subQ6])],"derivedFrom":makeQuery(id+"F10.boolean.opBoolean","COPY",EDGE,{"derivedFrom":makeQuery(id+"F10.opExtrude","CAP_EDGE",EDGE,{"disambiguationData":[OSD([subQ0])],"isStart":false})})})})})})})})})})})})})})})})})})})})})})})})})})})})})})})})})})})})})})})})})})})})});}
            var Q237;
            {var subQ0=sQuery(id+"F13.wireOp",EDGE,"E148.MirrorCS");var subQ1=sQuery(id+"F13.wireOp",EDGE,"E147");var subQ2=sQuery(id+"F11.wireOp",EDGE,"E143");var subQ13=makeQuery(id+"FyYUAefgu6xEfva_4.42.F14.opExtrude","SWEPT_FACE",FACE,{"disambiguationData":[OSD([subQ0])]});var subQ50=makeQuery(id+"F14.opExtrude","SWEPT_FACE",FACE,{"disambiguationData":[OSD([subQ1])]});Q237=makeQuery(id+"FyYUAefgu6xEfva_4.43.F14.boolean.opBoolean","SPLIT",EDGE,{"disambiguationData":[TD([subQ13])],"derivedFrom":makeQuery(id+"FyYUAefgu6xEfva_4.42.F14.boolean.opBoolean","SPLIT",EDGE,{"disambiguationData":[TD([subQ50])],"derivedFrom":makeQuery(id+"FyYUAefgu6xEfva_4.41.F14.boolean.opBoolean","SPLIT",EDGE,{"disambiguationData":[TD([subQ50])],"derivedFrom":makeQuery(id+"FyYUAefgu6xEfva_4.40.F14.boolean.opBoolean","SPLIT",EDGE,{"disambiguationData":[TD([subQ50])],"derivedFrom":makeQuery(id+"FyYUAefgu6xEfva_4.39.F14.boolean.opBoolean","SPLIT",EDGE,{"disambiguationData":[TD([subQ50])],"derivedFrom":makeQuery(id+"FyYUAefgu6xEfva_4.38.F14.boolean.opBoolean","SPLIT",EDGE,{"disambiguationData":[TD([subQ50])],"derivedFrom":makeQuery(id+"FyYUAefgu6xEfva_4.37.F14.boolean.opBoolean","SPLIT",EDGE,{"disambiguationData":[TD([subQ50])],"derivedFrom":makeQuery(id+"FyYUAefgu6xEfva_4.36.F14.boolean.opBoolean","SPLIT",EDGE,{"disambiguationData":[TD([subQ50])],"derivedFrom":makeQuery(id+"FyYUAefgu6xEfva_4.35.F14.boolean.opBoolean","SPLIT",EDGE,{"disambiguationData":[TD([subQ50])],"derivedFrom":makeQuery(id+"FyYUAefgu6xEfva_4.34.F14.boolean.opBoolean","SPLIT",EDGE,{"disambiguationData":[TD([subQ50])],"derivedFrom":makeQuery(id+"FyYUAefgu6xEfva_4.33.F14.boolean.opBoolean","SPLIT",EDGE,{"disambiguationData":[TD([subQ50])],"derivedFrom":makeQuery(id+"FyYUAefgu6xEfva_4.32.F14.boolean.opBoolean","SPLIT",EDGE,{"disambiguationData":[TD([subQ50])],"derivedFrom":makeQuery(id+"FyYUAefgu6xEfva_4.31.F14.boolean.opBoolean","SPLIT",EDGE,{"disambiguationData":[TD([subQ50])],"derivedFrom":makeQuery(id+"FyYUAefgu6xEfva_4.30.F14.boolean.opBoolean","SPLIT",EDGE,{"disambiguationData":[TD([subQ50])],"derivedFrom":makeQuery(id+"FyYUAefgu6xEfva_4.29.F14.boolean.opBoolean","SPLIT",EDGE,{"disambiguationData":[TD([subQ50])],"derivedFrom":makeQuery(id+"FyYUAefgu6xEfva_4.28.F14.boolean.opBoolean","SPLIT",EDGE,{"disambiguationData":[TD([subQ50])],"derivedFrom":makeQuery(id+"FyYUAefgu6xEfva_4.27.F14.boolean.opBoolean","SPLIT",EDGE,{"disambiguationData":[TD([subQ50])],"derivedFrom":makeQuery(id+"FyYUAefgu6xEfva_4.26.F14.boolean.opBoolean","SPLIT",EDGE,{"disambiguationData":[TD([subQ50])],"derivedFrom":makeQuery(id+"FyYUAefgu6xEfva_4.25.F14.boolean.opBoolean","SPLIT",EDGE,{"disambiguationData":[TD([subQ50])],"derivedFrom":makeQuery(id+"FyYUAefgu6xEfva_4.24.F14.boolean.opBoolean","SPLIT",EDGE,{"disambiguationData":[TD([subQ50])],"derivedFrom":makeQuery(id+"FyYUAefgu6xEfva_4.23.F14.boolean.opBoolean","SPLIT",EDGE,{"disambiguationData":[TD([subQ50])],"derivedFrom":makeQuery(id+"FyYUAefgu6xEfva_4.22.F14.boolean.opBoolean","SPLIT",EDGE,{"disambiguationData":[TD([subQ50])],"derivedFrom":makeQuery(id+"FyYUAefgu6xEfva_4.21.F14.boolean.opBoolean","SPLIT",EDGE,{"disambiguationData":[TD([subQ50])],"derivedFrom":makeQuery(id+"FyYUAefgu6xEfva_4.20.F14.boolean.opBoolean","SPLIT",EDGE,{"disambiguationData":[TD([subQ50])],"derivedFrom":makeQuery(id+"FyYUAefgu6xEfva_4.19.F14.boolean.opBoolean","SPLIT",EDGE,{"disambiguationData":[TD([subQ50])],"derivedFrom":makeQuery(id+"FyYUAefgu6xEfva_4.18.F14.boolean.opBoolean","SPLIT",EDGE,{"disambiguationData":[TD([subQ50])],"derivedFrom":makeQuery(id+"FyYUAefgu6xEfva_4.17.F14.boolean.opBoolean","SPLIT",EDGE,{"disambiguationData":[TD([subQ50])],"derivedFrom":makeQuery(id+"FyYUAefgu6xEfva_4.16.F14.boolean.opBoolean","SPLIT",EDGE,{"disambiguationData":[TD([subQ50])],"derivedFrom":makeQuery(id+"FyYUAefgu6xEfva_4.15.F14.boolean.opBoolean","SPLIT",EDGE,{"disambiguationData":[TD([subQ50])],"derivedFrom":makeQuery(id+"FyYUAefgu6xEfva_4.14.F14.boolean.opBoolean","SPLIT",EDGE,{"disambiguationData":[TD([subQ50])],"derivedFrom":makeQuery(id+"FyYUAefgu6xEfva_4.13.F14.boolean.opBoolean","SPLIT",EDGE,{"disambiguationData":[TD([subQ50])],"derivedFrom":makeQuery(id+"FyYUAefgu6xEfva_4.12.F14.boolean.opBoolean","SPLIT",EDGE,{"disambiguationData":[TD([subQ50])],"derivedFrom":makeQuery(id+"FyYUAefgu6xEfva_4.11.F14.boolean.opBoolean","SPLIT",EDGE,{"disambiguationData":[TD([subQ50])],"derivedFrom":makeQuery(id+"FyYUAefgu6xEfva_4.10.F14.boolean.opBoolean","SPLIT",EDGE,{"disambiguationData":[TD([subQ50])],"derivedFrom":makeQuery(id+"FyYUAefgu6xEfva_4.9.F14.boolean.opBoolean","SPLIT",EDGE,{"disambiguationData":[TD([subQ50])],"derivedFrom":makeQuery(id+"FyYUAefgu6xEfva_4.8.F14.boolean.opBoolean","SPLIT",EDGE,{"disambiguationData":[TD([subQ50])],"derivedFrom":makeQuery(id+"FyYUAefgu6xEfva_4.7.F14.boolean.opBoolean","SPLIT",EDGE,{"disambiguationData":[TD([subQ50])],"derivedFrom":makeQuery(id+"FyYUAefgu6xEfva_4.6.F14.boolean.opBoolean","SPLIT",EDGE,{"disambiguationData":[TD([subQ50])],"derivedFrom":makeQuery(id+"FyYUAefgu6xEfva_4.5.F14.boolean.opBoolean","SPLIT",EDGE,{"disambiguationData":[TD([subQ50])],"derivedFrom":makeQuery(id+"FyYUAefgu6xEfva_4.4.F14.boolean.opBoolean","SPLIT",EDGE,{"disambiguationData":[TD([subQ50])],"derivedFrom":makeQuery(id+"FyYUAefgu6xEfva_4.3.F14.boolean.opBoolean","SPLIT",EDGE,{"disambiguationData":[TD([subQ50])],"derivedFrom":makeQuery(id+"FyYUAefgu6xEfva_4.2.F14.boolean.opBoolean","SPLIT",EDGE,{"disambiguationData":[TD([subQ50])],"derivedFrom":makeQuery(id+"FyYUAefgu6xEfva_4.1.F14.boolean.opBoolean","SPLIT",EDGE,{"disambiguationData":[TD([subQ50])],"derivedFrom":makeQuery(id+"F12.opExtrude","CAP_EDGE",EDGE,{"disambiguationData":[OSD([subQ2])],"isStart":false})})})})})})})})})})})})})})})})})})})})})})})})})})})})})})})})})})})})})})})})})})})});}
            var Q238;
            Q238=makeQuery(id+"FyYUAefgu6xEfva_4.12.F14.opExtrude","CAP_EDGE",EDGE,{"disambiguationData":[OSD([sQuery(id+"F13.wireOp",EDGE,"E147")])],"isStart":false});
            var Q239;
            Q239=makeQuery(id+"FyYUAefgu6xEfva_4.12.F14.opExtrude","CAP_EDGE",EDGE,{"disambiguationData":[OSD([sQuery(id+"F13.wireOp",EDGE,"E148.MirrorCS")])],"isStart":false});
            var Q240;
            Q240=makeQuery(id+"FyYUAefgu6xEfva_4.12.F14.opExtrude","SWEPT_EDGE",EDGE,{"disambiguationData":[OSD([sQuery(id+"F9.wireOp",EDGE,"E142"),sQuery(id+"F13.wireOp",EDGE,"E147")])]});
            var Q241;
            Q241=makeQuery(id+"FyYUAefgu6xEfva_4.12.F14.opExtrude","CAP_EDGE",EDGE,{"disambiguationData":[OSD([sQuery(id+"F9.wireOp",EDGE,"E142")])],"isStart":false});
            var Q242;
            {var subQ0=sQuery(id+"F13.wireOp",EDGE,"E148.MirrorCS");var subQ1=sQuery(id+"F13.wireOp",EDGE,"E147");var subQ2=sQuery(id+"F11.wireOp",EDGE,"E143");var subQ18=makeQuery(id+"FyYUAefgu6xEfva_4.11.F14.opExtrude","SWEPT_FACE",FACE,{"disambiguationData":[OSD([subQ0])]});var subQ19=makeQuery(id+"F14.opExtrude","SWEPT_FACE",FACE,{"disambiguationData":[OSD([subQ1])]});Q242=makeQuery(id+"FyYUAefgu6xEfva_4.12.F14.boolean.opBoolean","SPLIT",EDGE,{"disambiguationData":[TD([subQ18])],"derivedFrom":makeQuery(id+"FyYUAefgu6xEfva_4.11.F14.boolean.opBoolean","SPLIT",EDGE,{"disambiguationData":[TD([subQ19])],"derivedFrom":makeQuery(id+"FyYUAefgu6xEfva_4.10.F14.boolean.opBoolean","SPLIT",EDGE,{"disambiguationData":[TD([subQ19])],"derivedFrom":makeQuery(id+"FyYUAefgu6xEfva_4.9.F14.boolean.opBoolean","SPLIT",EDGE,{"disambiguationData":[TD([subQ19])],"derivedFrom":makeQuery(id+"FyYUAefgu6xEfva_4.8.F14.boolean.opBoolean","SPLIT",EDGE,{"disambiguationData":[TD([subQ19])],"derivedFrom":makeQuery(id+"FyYUAefgu6xEfva_4.7.F14.boolean.opBoolean","SPLIT",EDGE,{"disambiguationData":[TD([subQ19])],"derivedFrom":makeQuery(id+"FyYUAefgu6xEfva_4.6.F14.boolean.opBoolean","SPLIT",EDGE,{"disambiguationData":[TD([subQ19])],"derivedFrom":makeQuery(id+"FyYUAefgu6xEfva_4.5.F14.boolean.opBoolean","SPLIT",EDGE,{"disambiguationData":[TD([subQ19])],"derivedFrom":makeQuery(id+"FyYUAefgu6xEfva_4.4.F14.boolean.opBoolean","SPLIT",EDGE,{"disambiguationData":[TD([subQ19])],"derivedFrom":makeQuery(id+"FyYUAefgu6xEfva_4.3.F14.boolean.opBoolean","SPLIT",EDGE,{"disambiguationData":[TD([subQ19])],"derivedFrom":makeQuery(id+"FyYUAefgu6xEfva_4.2.F14.boolean.opBoolean","SPLIT",EDGE,{"disambiguationData":[TD([subQ19])],"derivedFrom":makeQuery(id+"FyYUAefgu6xEfva_4.1.F14.boolean.opBoolean","SPLIT",EDGE,{"disambiguationData":[TD([subQ19])],"derivedFrom":makeQuery(id+"F12.opExtrude","CAP_EDGE",EDGE,{"disambiguationData":[OSD([subQ2])],"isStart":false})})})})})})})})})})})})});}
            var Q243;
            Q243=makeQuery(id+"FyYUAefgu6xEfva_4.44.F14.opExtrude","SWEPT_EDGE",EDGE,{"disambiguationData":[OSD([sQuery(id+"F9.wireOp",EDGE,"E142"),sQuery(id+"F13.wireOp",EDGE,"E147")])]});
            var Q244;
            Q244=makeQuery(id+"FyYUAefgu6xEfva_4.44.F14.opExtrude","SWEPT_EDGE",EDGE,{"disambiguationData":[OSD([sQuery(id+"F11.wireOp",EDGE,"E143"),sQuery(id+"F13.wireOp",EDGE,"E147")])]});
            var Q245;
            Q245=makeQuery(id+"FyYUAefgu6xEfva_4.44.F14.opExtrude","SWEPT_EDGE",EDGE,{"disambiguationData":[OSD([sQuery(id+"F9.wireOp",EDGE,"E142"),sQuery(id+"F13.wireOp",EDGE,"E148.MirrorCS")])]});
            var Q246;
            Q246=makeQuery(id+"FyYUAefgu6xEfva_4.44.F14.opExtrude","SWEPT_EDGE",EDGE,{"disambiguationData":[OSD([sQuery(id+"F11.wireOp",EDGE,"E143"),sQuery(id+"F13.wireOp",EDGE,"E148.MirrorCS")])]});
            var Q247;
            Q247=makeQuery(id+"FyYUAefgu6xEfva_4.44.F14.opExtrude","CAP_EDGE",EDGE,{"disambiguationData":[OSD([sQuery(id+"F13.wireOp",EDGE,"E147")])],"isStart":true});
            var Q248;
            Q248=makeQuery(id+"FyYUAefgu6xEfva_4.44.F14.opExtrude","CAP_EDGE",EDGE,{"disambiguationData":[OSD([sQuery(id+"F13.wireOp",EDGE,"E148.MirrorCS")])],"isStart":true});
            var Q249;
            {var subQ0=sQuery(id+"F9.wireOp",EDGE,"E142");var subQ2=sQuery(id+"F13.wireOp",EDGE,"E147");var subQ4=sQuery(id+"F13.wireOp",EDGE,"E148.MirrorCS");var subQ5=makeQuery(id+"FyYUAefgu6xEfva_4.43.F14.opExtrude","SWEPT_FACE",FACE,{"disambiguationData":[OSD([subQ4])]});var subQ6=makeQuery(id+"F14.opExtrude","SWEPT_FACE",FACE,{"disambiguationData":[OSD([subQ2])]});Q249=makeQuery(id+"FyYUAefgu6xEfva_4.44.F14.boolean.opBoolean","SPLIT",EDGE,{"disambiguationData":[TD([subQ5])],"derivedFrom":makeQuery(id+"FyYUAefgu6xEfva_4.43.F14.boolean.opBoolean","SPLIT",EDGE,{"disambiguationData":[TD([subQ6])],"derivedFrom":makeQuery(id+"FyYUAefgu6xEfva_4.42.F14.boolean.opBoolean","SPLIT",EDGE,{"disambiguationData":[TD([subQ6])],"derivedFrom":makeQuery(id+"FyYUAefgu6xEfva_4.41.F14.boolean.opBoolean","SPLIT",EDGE,{"disambiguationData":[TD([subQ6])],"derivedFrom":makeQuery(id+"FyYUAefgu6xEfva_4.40.F14.boolean.opBoolean","SPLIT",EDGE,{"disambiguationData":[TD([subQ6])],"derivedFrom":makeQuery(id+"FyYUAefgu6xEfva_4.39.F14.boolean.opBoolean","SPLIT",EDGE,{"disambiguationData":[TD([subQ6])],"derivedFrom":makeQuery(id+"FyYUAefgu6xEfva_4.38.F14.boolean.opBoolean","SPLIT",EDGE,{"disambiguationData":[TD([subQ6])],"derivedFrom":makeQuery(id+"FyYUAefgu6xEfva_4.37.F14.boolean.opBoolean","SPLIT",EDGE,{"disambiguationData":[TD([subQ6])],"derivedFrom":makeQuery(id+"FyYUAefgu6xEfva_4.36.F14.boolean.opBoolean","SPLIT",EDGE,{"disambiguationData":[TD([subQ6])],"derivedFrom":makeQuery(id+"FyYUAefgu6xEfva_4.35.F14.boolean.opBoolean","SPLIT",EDGE,{"disambiguationData":[TD([subQ6])],"derivedFrom":makeQuery(id+"FyYUAefgu6xEfva_4.34.F14.boolean.opBoolean","SPLIT",EDGE,{"disambiguationData":[TD([subQ6])],"derivedFrom":makeQuery(id+"FyYUAefgu6xEfva_4.33.F14.boolean.opBoolean","SPLIT",EDGE,{"disambiguationData":[TD([subQ6])],"derivedFrom":makeQuery(id+"FyYUAefgu6xEfva_4.32.F14.boolean.opBoolean","SPLIT",EDGE,{"disambiguationData":[TD([subQ6])],"derivedFrom":makeQuery(id+"FyYUAefgu6xEfva_4.31.F14.boolean.opBoolean","SPLIT",EDGE,{"disambiguationData":[TD([subQ6])],"derivedFrom":makeQuery(id+"FyYUAefgu6xEfva_4.30.F14.boolean.opBoolean","SPLIT",EDGE,{"disambiguationData":[TD([subQ6])],"derivedFrom":makeQuery(id+"FyYUAefgu6xEfva_4.29.F14.boolean.opBoolean","SPLIT",EDGE,{"disambiguationData":[TD([subQ6])],"derivedFrom":makeQuery(id+"FyYUAefgu6xEfva_4.28.F14.boolean.opBoolean","SPLIT",EDGE,{"disambiguationData":[TD([subQ6])],"derivedFrom":makeQuery(id+"FyYUAefgu6xEfva_4.27.F14.boolean.opBoolean","SPLIT",EDGE,{"disambiguationData":[TD([subQ6])],"derivedFrom":makeQuery(id+"FyYUAefgu6xEfva_4.26.F14.boolean.opBoolean","SPLIT",EDGE,{"disambiguationData":[TD([subQ6])],"derivedFrom":makeQuery(id+"FyYUAefgu6xEfva_4.25.F14.boolean.opBoolean","SPLIT",EDGE,{"disambiguationData":[TD([subQ6])],"derivedFrom":makeQuery(id+"FyYUAefgu6xEfva_4.24.F14.boolean.opBoolean","SPLIT",EDGE,{"disambiguationData":[TD([subQ6])],"derivedFrom":makeQuery(id+"FyYUAefgu6xEfva_4.23.F14.boolean.opBoolean","SPLIT",EDGE,{"disambiguationData":[TD([subQ6])],"derivedFrom":makeQuery(id+"FyYUAefgu6xEfva_4.22.F14.boolean.opBoolean","SPLIT",EDGE,{"disambiguationData":[TD([subQ6])],"derivedFrom":makeQuery(id+"FyYUAefgu6xEfva_4.21.F14.boolean.opBoolean","SPLIT",EDGE,{"disambiguationData":[TD([subQ6])],"derivedFrom":makeQuery(id+"FyYUAefgu6xEfva_4.20.F14.boolean.opBoolean","SPLIT",EDGE,{"disambiguationData":[TD([subQ6])],"derivedFrom":makeQuery(id+"FyYUAefgu6xEfva_4.19.F14.boolean.opBoolean","SPLIT",EDGE,{"disambiguationData":[TD([subQ6])],"derivedFrom":makeQuery(id+"FyYUAefgu6xEfva_4.18.F14.boolean.opBoolean","SPLIT",EDGE,{"disambiguationData":[TD([subQ6])],"derivedFrom":makeQuery(id+"FyYUAefgu6xEfva_4.17.F14.boolean.opBoolean","SPLIT",EDGE,{"disambiguationData":[TD([subQ6])],"derivedFrom":makeQuery(id+"FyYUAefgu6xEfva_4.16.F14.boolean.opBoolean","SPLIT",EDGE,{"disambiguationData":[TD([subQ6])],"derivedFrom":makeQuery(id+"FyYUAefgu6xEfva_4.15.F14.boolean.opBoolean","SPLIT",EDGE,{"disambiguationData":[TD([subQ6])],"derivedFrom":makeQuery(id+"FyYUAefgu6xEfva_4.14.F14.boolean.opBoolean","SPLIT",EDGE,{"disambiguationData":[TD([subQ6])],"derivedFrom":makeQuery(id+"FyYUAefgu6xEfva_4.13.F14.boolean.opBoolean","SPLIT",EDGE,{"disambiguationData":[TD([subQ6])],"derivedFrom":makeQuery(id+"FyYUAefgu6xEfva_4.12.F14.boolean.opBoolean","SPLIT",EDGE,{"disambiguationData":[TD([subQ6])],"derivedFrom":makeQuery(id+"FyYUAefgu6xEfva_4.11.F14.boolean.opBoolean","SPLIT",EDGE,{"disambiguationData":[TD([subQ6])],"derivedFrom":makeQuery(id+"FyYUAefgu6xEfva_4.10.F14.boolean.opBoolean","SPLIT",EDGE,{"disambiguationData":[TD([subQ6])],"derivedFrom":makeQuery(id+"FyYUAefgu6xEfva_4.9.F14.boolean.opBoolean","SPLIT",EDGE,{"disambiguationData":[TD([subQ6])],"derivedFrom":makeQuery(id+"FyYUAefgu6xEfva_4.8.F14.boolean.opBoolean","SPLIT",EDGE,{"disambiguationData":[TD([subQ6])],"derivedFrom":makeQuery(id+"FyYUAefgu6xEfva_4.7.F14.boolean.opBoolean","SPLIT",EDGE,{"disambiguationData":[TD([subQ6])],"derivedFrom":makeQuery(id+"FyYUAefgu6xEfva_4.6.F14.boolean.opBoolean","SPLIT",EDGE,{"disambiguationData":[TD([subQ6])],"derivedFrom":makeQuery(id+"FyYUAefgu6xEfva_4.5.F14.boolean.opBoolean","SPLIT",EDGE,{"disambiguationData":[TD([subQ6])],"derivedFrom":makeQuery(id+"FyYUAefgu6xEfva_4.4.F14.boolean.opBoolean","SPLIT",EDGE,{"disambiguationData":[TD([subQ6])],"derivedFrom":makeQuery(id+"FyYUAefgu6xEfva_4.3.F14.boolean.opBoolean","SPLIT",EDGE,{"disambiguationData":[TD([subQ6])],"derivedFrom":makeQuery(id+"FyYUAefgu6xEfva_4.2.F14.boolean.opBoolean","SPLIT",EDGE,{"disambiguationData":[TD([subQ6])],"derivedFrom":makeQuery(id+"FyYUAefgu6xEfva_4.1.F14.boolean.opBoolean","SPLIT",EDGE,{"disambiguationData":[TD([subQ6])],"derivedFrom":makeQuery(id+"F10.boolean.opBoolean","COPY",EDGE,{"derivedFrom":makeQuery(id+"F10.opExtrude","CAP_EDGE",EDGE,{"disambiguationData":[OSD([subQ0])],"isStart":false})})})})})})})})})})})})})})})})})})})})})})})})})})})})})})})})})})})})})})})})})})})})})});}
            var Q250;
            {var subQ0=sQuery(id+"F13.wireOp",EDGE,"E148.MirrorCS");var subQ1=sQuery(id+"F13.wireOp",EDGE,"E147");var subQ2=sQuery(id+"F11.wireOp",EDGE,"E143");var subQ13=makeQuery(id+"FyYUAefgu6xEfva_4.43.F14.opExtrude","SWEPT_FACE",FACE,{"disambiguationData":[OSD([subQ0])]});var subQ51=makeQuery(id+"F14.opExtrude","SWEPT_FACE",FACE,{"disambiguationData":[OSD([subQ1])]});Q250=makeQuery(id+"FyYUAefgu6xEfva_4.44.F14.boolean.opBoolean","SPLIT",EDGE,{"disambiguationData":[TD([subQ13])],"derivedFrom":makeQuery(id+"FyYUAefgu6xEfva_4.43.F14.boolean.opBoolean","SPLIT",EDGE,{"disambiguationData":[TD([subQ51])],"derivedFrom":makeQuery(id+"FyYUAefgu6xEfva_4.42.F14.boolean.opBoolean","SPLIT",EDGE,{"disambiguationData":[TD([subQ51])],"derivedFrom":makeQuery(id+"FyYUAefgu6xEfva_4.41.F14.boolean.opBoolean","SPLIT",EDGE,{"disambiguationData":[TD([subQ51])],"derivedFrom":makeQuery(id+"FyYUAefgu6xEfva_4.40.F14.boolean.opBoolean","SPLIT",EDGE,{"disambiguationData":[TD([subQ51])],"derivedFrom":makeQuery(id+"FyYUAefgu6xEfva_4.39.F14.boolean.opBoolean","SPLIT",EDGE,{"disambiguationData":[TD([subQ51])],"derivedFrom":makeQuery(id+"FyYUAefgu6xEfva_4.38.F14.boolean.opBoolean","SPLIT",EDGE,{"disambiguationData":[TD([subQ51])],"derivedFrom":makeQuery(id+"FyYUAefgu6xEfva_4.37.F14.boolean.opBoolean","SPLIT",EDGE,{"disambiguationData":[TD([subQ51])],"derivedFrom":makeQuery(id+"FyYUAefgu6xEfva_4.36.F14.boolean.opBoolean","SPLIT",EDGE,{"disambiguationData":[TD([subQ51])],"derivedFrom":makeQuery(id+"FyYUAefgu6xEfva_4.35.F14.boolean.opBoolean","SPLIT",EDGE,{"disambiguationData":[TD([subQ51])],"derivedFrom":makeQuery(id+"FyYUAefgu6xEfva_4.34.F14.boolean.opBoolean","SPLIT",EDGE,{"disambiguationData":[TD([subQ51])],"derivedFrom":makeQuery(id+"FyYUAefgu6xEfva_4.33.F14.boolean.opBoolean","SPLIT",EDGE,{"disambiguationData":[TD([subQ51])],"derivedFrom":makeQuery(id+"FyYUAefgu6xEfva_4.32.F14.boolean.opBoolean","SPLIT",EDGE,{"disambiguationData":[TD([subQ51])],"derivedFrom":makeQuery(id+"FyYUAefgu6xEfva_4.31.F14.boolean.opBoolean","SPLIT",EDGE,{"disambiguationData":[TD([subQ51])],"derivedFrom":makeQuery(id+"FyYUAefgu6xEfva_4.30.F14.boolean.opBoolean","SPLIT",EDGE,{"disambiguationData":[TD([subQ51])],"derivedFrom":makeQuery(id+"FyYUAefgu6xEfva_4.29.F14.boolean.opBoolean","SPLIT",EDGE,{"disambiguationData":[TD([subQ51])],"derivedFrom":makeQuery(id+"FyYUAefgu6xEfva_4.28.F14.boolean.opBoolean","SPLIT",EDGE,{"disambiguationData":[TD([subQ51])],"derivedFrom":makeQuery(id+"FyYUAefgu6xEfva_4.27.F14.boolean.opBoolean","SPLIT",EDGE,{"disambiguationData":[TD([subQ51])],"derivedFrom":makeQuery(id+"FyYUAefgu6xEfva_4.26.F14.boolean.opBoolean","SPLIT",EDGE,{"disambiguationData":[TD([subQ51])],"derivedFrom":makeQuery(id+"FyYUAefgu6xEfva_4.25.F14.boolean.opBoolean","SPLIT",EDGE,{"disambiguationData":[TD([subQ51])],"derivedFrom":makeQuery(id+"FyYUAefgu6xEfva_4.24.F14.boolean.opBoolean","SPLIT",EDGE,{"disambiguationData":[TD([subQ51])],"derivedFrom":makeQuery(id+"FyYUAefgu6xEfva_4.23.F14.boolean.opBoolean","SPLIT",EDGE,{"disambiguationData":[TD([subQ51])],"derivedFrom":makeQuery(id+"FyYUAefgu6xEfva_4.22.F14.boolean.opBoolean","SPLIT",EDGE,{"disambiguationData":[TD([subQ51])],"derivedFrom":makeQuery(id+"FyYUAefgu6xEfva_4.21.F14.boolean.opBoolean","SPLIT",EDGE,{"disambiguationData":[TD([subQ51])],"derivedFrom":makeQuery(id+"FyYUAefgu6xEfva_4.20.F14.boolean.opBoolean","SPLIT",EDGE,{"disambiguationData":[TD([subQ51])],"derivedFrom":makeQuery(id+"FyYUAefgu6xEfva_4.19.F14.boolean.opBoolean","SPLIT",EDGE,{"disambiguationData":[TD([subQ51])],"derivedFrom":makeQuery(id+"FyYUAefgu6xEfva_4.18.F14.boolean.opBoolean","SPLIT",EDGE,{"disambiguationData":[TD([subQ51])],"derivedFrom":makeQuery(id+"FyYUAefgu6xEfva_4.17.F14.boolean.opBoolean","SPLIT",EDGE,{"disambiguationData":[TD([subQ51])],"derivedFrom":makeQuery(id+"FyYUAefgu6xEfva_4.16.F14.boolean.opBoolean","SPLIT",EDGE,{"disambiguationData":[TD([subQ51])],"derivedFrom":makeQuery(id+"FyYUAefgu6xEfva_4.15.F14.boolean.opBoolean","SPLIT",EDGE,{"disambiguationData":[TD([subQ51])],"derivedFrom":makeQuery(id+"FyYUAefgu6xEfva_4.14.F14.boolean.opBoolean","SPLIT",EDGE,{"disambiguationData":[TD([subQ51])],"derivedFrom":makeQuery(id+"FyYUAefgu6xEfva_4.13.F14.boolean.opBoolean","SPLIT",EDGE,{"disambiguationData":[TD([subQ51])],"derivedFrom":makeQuery(id+"FyYUAefgu6xEfva_4.12.F14.boolean.opBoolean","SPLIT",EDGE,{"disambiguationData":[TD([subQ51])],"derivedFrom":makeQuery(id+"FyYUAefgu6xEfva_4.11.F14.boolean.opBoolean","SPLIT",EDGE,{"disambiguationData":[TD([subQ51])],"derivedFrom":makeQuery(id+"FyYUAefgu6xEfva_4.10.F14.boolean.opBoolean","SPLIT",EDGE,{"disambiguationData":[TD([subQ51])],"derivedFrom":makeQuery(id+"FyYUAefgu6xEfva_4.9.F14.boolean.opBoolean","SPLIT",EDGE,{"disambiguationData":[TD([subQ51])],"derivedFrom":makeQuery(id+"FyYUAefgu6xEfva_4.8.F14.boolean.opBoolean","SPLIT",EDGE,{"disambiguationData":[TD([subQ51])],"derivedFrom":makeQuery(id+"FyYUAefgu6xEfva_4.7.F14.boolean.opBoolean","SPLIT",EDGE,{"disambiguationData":[TD([subQ51])],"derivedFrom":makeQuery(id+"FyYUAefgu6xEfva_4.6.F14.boolean.opBoolean","SPLIT",EDGE,{"disambiguationData":[TD([subQ51])],"derivedFrom":makeQuery(id+"FyYUAefgu6xEfva_4.5.F14.boolean.opBoolean","SPLIT",EDGE,{"disambiguationData":[TD([subQ51])],"derivedFrom":makeQuery(id+"FyYUAefgu6xEfva_4.4.F14.boolean.opBoolean","SPLIT",EDGE,{"disambiguationData":[TD([subQ51])],"derivedFrom":makeQuery(id+"FyYUAefgu6xEfva_4.3.F14.boolean.opBoolean","SPLIT",EDGE,{"disambiguationData":[TD([subQ51])],"derivedFrom":makeQuery(id+"FyYUAefgu6xEfva_4.2.F14.boolean.opBoolean","SPLIT",EDGE,{"disambiguationData":[TD([subQ51])],"derivedFrom":makeQuery(id+"FyYUAefgu6xEfva_4.1.F14.boolean.opBoolean","SPLIT",EDGE,{"disambiguationData":[TD([subQ51])],"derivedFrom":makeQuery(id+"F12.opExtrude","CAP_EDGE",EDGE,{"disambiguationData":[OSD([subQ2])],"isStart":false})})})})})})})})})})})})})})})})})})})})})})})})})})})})})})})})})})})})})})})})})})})})});}
            var Q251;
            Q251=makeQuery(id+"FyYUAefgu6xEfva_4.13.F14.opExtrude","CAP_EDGE",EDGE,{"disambiguationData":[OSD([sQuery(id+"F13.wireOp",EDGE,"E147")])],"isStart":false});
            var Q252;
            Q252=makeQuery(id+"FyYUAefgu6xEfva_4.13.F14.opExtrude","SWEPT_EDGE",EDGE,{"disambiguationData":[OSD([sQuery(id+"F9.wireOp",EDGE,"E142"),sQuery(id+"F13.wireOp",EDGE,"E147")])]});
            var Q253;
            Q253=makeQuery(id+"FyYUAefgu6xEfva_4.13.F14.opExtrude","SWEPT_EDGE",EDGE,{"disambiguationData":[OSD([sQuery(id+"F9.wireOp",EDGE,"E142"),sQuery(id+"F13.wireOp",EDGE,"E148.MirrorCS")])]});
            var Q254;
            Q254=makeQuery(id+"FyYUAefgu6xEfva_4.13.F14.opExtrude","SWEPT_EDGE",EDGE,{"disambiguationData":[OSD([sQuery(id+"F11.wireOp",EDGE,"E143"),sQuery(id+"F13.wireOp",EDGE,"E148.MirrorCS")])]});
            var Q255;
            Q255=makeQuery(id+"FyYUAefgu6xEfva_4.13.F14.opExtrude","CAP_EDGE",EDGE,{"disambiguationData":[OSD([sQuery(id+"F9.wireOp",EDGE,"E142")])],"isStart":false});
            var Q256;
            {var subQ0=sQuery(id+"F13.wireOp",EDGE,"E148.MirrorCS");var subQ1=sQuery(id+"F13.wireOp",EDGE,"E147");var subQ2=sQuery(id+"F11.wireOp",EDGE,"E143");var subQ12=makeQuery(id+"FyYUAefgu6xEfva_4.12.F14.opExtrude","SWEPT_FACE",FACE,{"disambiguationData":[OSD([subQ0])]});var subQ20=makeQuery(id+"F14.opExtrude","SWEPT_FACE",FACE,{"disambiguationData":[OSD([subQ1])]});Q256=makeQuery(id+"FyYUAefgu6xEfva_4.13.F14.boolean.opBoolean","SPLIT",EDGE,{"disambiguationData":[TD([subQ12])],"derivedFrom":makeQuery(id+"FyYUAefgu6xEfva_4.12.F14.boolean.opBoolean","SPLIT",EDGE,{"disambiguationData":[TD([subQ20])],"derivedFrom":makeQuery(id+"FyYUAefgu6xEfva_4.11.F14.boolean.opBoolean","SPLIT",EDGE,{"disambiguationData":[TD([subQ20])],"derivedFrom":makeQuery(id+"FyYUAefgu6xEfva_4.10.F14.boolean.opBoolean","SPLIT",EDGE,{"disambiguationData":[TD([subQ20])],"derivedFrom":makeQuery(id+"FyYUAefgu6xEfva_4.9.F14.boolean.opBoolean","SPLIT",EDGE,{"disambiguationData":[TD([subQ20])],"derivedFrom":makeQuery(id+"FyYUAefgu6xEfva_4.8.F14.boolean.opBoolean","SPLIT",EDGE,{"disambiguationData":[TD([subQ20])],"derivedFrom":makeQuery(id+"FyYUAefgu6xEfva_4.7.F14.boolean.opBoolean","SPLIT",EDGE,{"disambiguationData":[TD([subQ20])],"derivedFrom":makeQuery(id+"FyYUAefgu6xEfva_4.6.F14.boolean.opBoolean","SPLIT",EDGE,{"disambiguationData":[TD([subQ20])],"derivedFrom":makeQuery(id+"FyYUAefgu6xEfva_4.5.F14.boolean.opBoolean","SPLIT",EDGE,{"disambiguationData":[TD([subQ20])],"derivedFrom":makeQuery(id+"FyYUAefgu6xEfva_4.4.F14.boolean.opBoolean","SPLIT",EDGE,{"disambiguationData":[TD([subQ20])],"derivedFrom":makeQuery(id+"FyYUAefgu6xEfva_4.3.F14.boolean.opBoolean","SPLIT",EDGE,{"disambiguationData":[TD([subQ20])],"derivedFrom":makeQuery(id+"FyYUAefgu6xEfva_4.2.F14.boolean.opBoolean","SPLIT",EDGE,{"disambiguationData":[TD([subQ20])],"derivedFrom":makeQuery(id+"FyYUAefgu6xEfva_4.1.F14.boolean.opBoolean","SPLIT",EDGE,{"disambiguationData":[TD([subQ20])],"derivedFrom":makeQuery(id+"F12.opExtrude","CAP_EDGE",EDGE,{"disambiguationData":[OSD([subQ2])],"isStart":false})})})})})})})})})})})})})});}
            var Q257;
            Q257=makeQuery(id+"FyYUAefgu6xEfva_4.45.F14.opExtrude","SWEPT_EDGE",EDGE,{"disambiguationData":[OSD([sQuery(id+"F9.wireOp",EDGE,"E142"),sQuery(id+"F13.wireOp",EDGE,"E147")])]});
            var Q258;
            Q258=makeQuery(id+"FyYUAefgu6xEfva_4.45.F14.opExtrude","SWEPT_EDGE",EDGE,{"disambiguationData":[OSD([sQuery(id+"F11.wireOp",EDGE,"E143"),sQuery(id+"F13.wireOp",EDGE,"E147")])]});
            var Q259;
            Q259=makeQuery(id+"FyYUAefgu6xEfva_4.45.F14.opExtrude","SWEPT_EDGE",EDGE,{"disambiguationData":[OSD([sQuery(id+"F9.wireOp",EDGE,"E142"),sQuery(id+"F13.wireOp",EDGE,"E148.MirrorCS")])]});
            var Q260;
            Q260=makeQuery(id+"FyYUAefgu6xEfva_4.45.F14.opExtrude","SWEPT_EDGE",EDGE,{"disambiguationData":[OSD([sQuery(id+"F11.wireOp",EDGE,"E143"),sQuery(id+"F13.wireOp",EDGE,"E148.MirrorCS")])]});
            var Q261;
            Q261=makeQuery(id+"FyYUAefgu6xEfva_4.45.F14.opExtrude","CAP_EDGE",EDGE,{"disambiguationData":[OSD([sQuery(id+"F13.wireOp",EDGE,"E147")])],"isStart":true});
            var Q262;
            {var subQ0=sQuery(id+"F9.wireOp",EDGE,"E142");var subQ3=sQuery(id+"F13.wireOp",EDGE,"E148.MirrorCS");var subQ4=makeQuery(id+"FyYUAefgu6xEfva_4.44.F14.opExtrude","SWEPT_FACE",FACE,{"disambiguationData":[OSD([subQ3])]});var subQ5=sQuery(id+"F13.wireOp",EDGE,"E147");var subQ6=makeQuery(id+"F14.opExtrude","SWEPT_FACE",FACE,{"disambiguationData":[OSD([subQ5])]});Q262=makeQuery(id+"FyYUAefgu6xEfva_4.45.F14.boolean.opBoolean","SPLIT",EDGE,{"disambiguationData":[TD([subQ4])],"derivedFrom":makeQuery(id+"FyYUAefgu6xEfva_4.44.F14.boolean.opBoolean","SPLIT",EDGE,{"disambiguationData":[TD([subQ6])],"derivedFrom":makeQuery(id+"FyYUAefgu6xEfva_4.43.F14.boolean.opBoolean","SPLIT",EDGE,{"disambiguationData":[TD([subQ6])],"derivedFrom":makeQuery(id+"FyYUAefgu6xEfva_4.42.F14.boolean.opBoolean","SPLIT",EDGE,{"disambiguationData":[TD([subQ6])],"derivedFrom":makeQuery(id+"FyYUAefgu6xEfva_4.41.F14.boolean.opBoolean","SPLIT",EDGE,{"disambiguationData":[TD([subQ6])],"derivedFrom":makeQuery(id+"FyYUAefgu6xEfva_4.40.F14.boolean.opBoolean","SPLIT",EDGE,{"disambiguationData":[TD([subQ6])],"derivedFrom":makeQuery(id+"FyYUAefgu6xEfva_4.39.F14.boolean.opBoolean","SPLIT",EDGE,{"disambiguationData":[TD([subQ6])],"derivedFrom":makeQuery(id+"FyYUAefgu6xEfva_4.38.F14.boolean.opBoolean","SPLIT",EDGE,{"disambiguationData":[TD([subQ6])],"derivedFrom":makeQuery(id+"FyYUAefgu6xEfva_4.37.F14.boolean.opBoolean","SPLIT",EDGE,{"disambiguationData":[TD([subQ6])],"derivedFrom":makeQuery(id+"FyYUAefgu6xEfva_4.36.F14.boolean.opBoolean","SPLIT",EDGE,{"disambiguationData":[TD([subQ6])],"derivedFrom":makeQuery(id+"FyYUAefgu6xEfva_4.35.F14.boolean.opBoolean","SPLIT",EDGE,{"disambiguationData":[TD([subQ6])],"derivedFrom":makeQuery(id+"FyYUAefgu6xEfva_4.34.F14.boolean.opBoolean","SPLIT",EDGE,{"disambiguationData":[TD([subQ6])],"derivedFrom":makeQuery(id+"FyYUAefgu6xEfva_4.33.F14.boolean.opBoolean","SPLIT",EDGE,{"disambiguationData":[TD([subQ6])],"derivedFrom":makeQuery(id+"FyYUAefgu6xEfva_4.32.F14.boolean.opBoolean","SPLIT",EDGE,{"disambiguationData":[TD([subQ6])],"derivedFrom":makeQuery(id+"FyYUAefgu6xEfva_4.31.F14.boolean.opBoolean","SPLIT",EDGE,{"disambiguationData":[TD([subQ6])],"derivedFrom":makeQuery(id+"FyYUAefgu6xEfva_4.30.F14.boolean.opBoolean","SPLIT",EDGE,{"disambiguationData":[TD([subQ6])],"derivedFrom":makeQuery(id+"FyYUAefgu6xEfva_4.29.F14.boolean.opBoolean","SPLIT",EDGE,{"disambiguationData":[TD([subQ6])],"derivedFrom":makeQuery(id+"FyYUAefgu6xEfva_4.28.F14.boolean.opBoolean","SPLIT",EDGE,{"disambiguationData":[TD([subQ6])],"derivedFrom":makeQuery(id+"FyYUAefgu6xEfva_4.27.F14.boolean.opBoolean","SPLIT",EDGE,{"disambiguationData":[TD([subQ6])],"derivedFrom":makeQuery(id+"FyYUAefgu6xEfva_4.26.F14.boolean.opBoolean","SPLIT",EDGE,{"disambiguationData":[TD([subQ6])],"derivedFrom":makeQuery(id+"FyYUAefgu6xEfva_4.25.F14.boolean.opBoolean","SPLIT",EDGE,{"disambiguationData":[TD([subQ6])],"derivedFrom":makeQuery(id+"FyYUAefgu6xEfva_4.24.F14.boolean.opBoolean","SPLIT",EDGE,{"disambiguationData":[TD([subQ6])],"derivedFrom":makeQuery(id+"FyYUAefgu6xEfva_4.23.F14.boolean.opBoolean","SPLIT",EDGE,{"disambiguationData":[TD([subQ6])],"derivedFrom":makeQuery(id+"FyYUAefgu6xEfva_4.22.F14.boolean.opBoolean","SPLIT",EDGE,{"disambiguationData":[TD([subQ6])],"derivedFrom":makeQuery(id+"FyYUAefgu6xEfva_4.21.F14.boolean.opBoolean","SPLIT",EDGE,{"disambiguationData":[TD([subQ6])],"derivedFrom":makeQuery(id+"FyYUAefgu6xEfva_4.20.F14.boolean.opBoolean","SPLIT",EDGE,{"disambiguationData":[TD([subQ6])],"derivedFrom":makeQuery(id+"FyYUAefgu6xEfva_4.19.F14.boolean.opBoolean","SPLIT",EDGE,{"disambiguationData":[TD([subQ6])],"derivedFrom":makeQuery(id+"FyYUAefgu6xEfva_4.18.F14.boolean.opBoolean","SPLIT",EDGE,{"disambiguationData":[TD([subQ6])],"derivedFrom":makeQuery(id+"FyYUAefgu6xEfva_4.17.F14.boolean.opBoolean","SPLIT",EDGE,{"disambiguationData":[TD([subQ6])],"derivedFrom":makeQuery(id+"FyYUAefgu6xEfva_4.16.F14.boolean.opBoolean","SPLIT",EDGE,{"disambiguationData":[TD([subQ6])],"derivedFrom":makeQuery(id+"FyYUAefgu6xEfva_4.15.F14.boolean.opBoolean","SPLIT",EDGE,{"disambiguationData":[TD([subQ6])],"derivedFrom":makeQuery(id+"FyYUAefgu6xEfva_4.14.F14.boolean.opBoolean","SPLIT",EDGE,{"disambiguationData":[TD([subQ6])],"derivedFrom":makeQuery(id+"FyYUAefgu6xEfva_4.13.F14.boolean.opBoolean","SPLIT",EDGE,{"disambiguationData":[TD([subQ6])],"derivedFrom":makeQuery(id+"FyYUAefgu6xEfva_4.12.F14.boolean.opBoolean","SPLIT",EDGE,{"disambiguationData":[TD([subQ6])],"derivedFrom":makeQuery(id+"FyYUAefgu6xEfva_4.11.F14.boolean.opBoolean","SPLIT",EDGE,{"disambiguationData":[TD([subQ6])],"derivedFrom":makeQuery(id+"FyYUAefgu6xEfva_4.10.F14.boolean.opBoolean","SPLIT",EDGE,{"disambiguationData":[TD([subQ6])],"derivedFrom":makeQuery(id+"FyYUAefgu6xEfva_4.9.F14.boolean.opBoolean","SPLIT",EDGE,{"disambiguationData":[TD([subQ6])],"derivedFrom":makeQuery(id+"FyYUAefgu6xEfva_4.8.F14.boolean.opBoolean","SPLIT",EDGE,{"disambiguationData":[TD([subQ6])],"derivedFrom":makeQuery(id+"FyYUAefgu6xEfva_4.7.F14.boolean.opBoolean","SPLIT",EDGE,{"disambiguationData":[TD([subQ6])],"derivedFrom":makeQuery(id+"FyYUAefgu6xEfva_4.6.F14.boolean.opBoolean","SPLIT",EDGE,{"disambiguationData":[TD([subQ6])],"derivedFrom":makeQuery(id+"FyYUAefgu6xEfva_4.5.F14.boolean.opBoolean","SPLIT",EDGE,{"disambiguationData":[TD([subQ6])],"derivedFrom":makeQuery(id+"FyYUAefgu6xEfva_4.4.F14.boolean.opBoolean","SPLIT",EDGE,{"disambiguationData":[TD([subQ6])],"derivedFrom":makeQuery(id+"FyYUAefgu6xEfva_4.3.F14.boolean.opBoolean","SPLIT",EDGE,{"disambiguationData":[TD([subQ6])],"derivedFrom":makeQuery(id+"FyYUAefgu6xEfva_4.2.F14.boolean.opBoolean","SPLIT",EDGE,{"disambiguationData":[TD([subQ6])],"derivedFrom":makeQuery(id+"FyYUAefgu6xEfva_4.1.F14.boolean.opBoolean","SPLIT",EDGE,{"disambiguationData":[TD([subQ6])],"derivedFrom":makeQuery(id+"F10.boolean.opBoolean","COPY",EDGE,{"derivedFrom":makeQuery(id+"F10.opExtrude","CAP_EDGE",EDGE,{"disambiguationData":[OSD([subQ0])],"isStart":false})})})})})})})})})})})})})})})})})})})})})})})})})})})})})})})})})})})})})})})})})})})})})})});}
            var Q263;
            {var subQ0=sQuery(id+"F13.wireOp",EDGE,"E148.MirrorCS");var subQ1=sQuery(id+"F13.wireOp",EDGE,"E147");var subQ2=sQuery(id+"F11.wireOp",EDGE,"E143");var subQ12=makeQuery(id+"FyYUAefgu6xEfva_4.44.F14.opExtrude","SWEPT_FACE",FACE,{"disambiguationData":[OSD([subQ0])]});var subQ52=makeQuery(id+"F14.opExtrude","SWEPT_FACE",FACE,{"disambiguationData":[OSD([subQ1])]});Q263=makeQuery(id+"FyYUAefgu6xEfva_4.45.F14.boolean.opBoolean","SPLIT",EDGE,{"disambiguationData":[TD([subQ12])],"derivedFrom":makeQuery(id+"FyYUAefgu6xEfva_4.44.F14.boolean.opBoolean","SPLIT",EDGE,{"disambiguationData":[TD([subQ52])],"derivedFrom":makeQuery(id+"FyYUAefgu6xEfva_4.43.F14.boolean.opBoolean","SPLIT",EDGE,{"disambiguationData":[TD([subQ52])],"derivedFrom":makeQuery(id+"FyYUAefgu6xEfva_4.42.F14.boolean.opBoolean","SPLIT",EDGE,{"disambiguationData":[TD([subQ52])],"derivedFrom":makeQuery(id+"FyYUAefgu6xEfva_4.41.F14.boolean.opBoolean","SPLIT",EDGE,{"disambiguationData":[TD([subQ52])],"derivedFrom":makeQuery(id+"FyYUAefgu6xEfva_4.40.F14.boolean.opBoolean","SPLIT",EDGE,{"disambiguationData":[TD([subQ52])],"derivedFrom":makeQuery(id+"FyYUAefgu6xEfva_4.39.F14.boolean.opBoolean","SPLIT",EDGE,{"disambiguationData":[TD([subQ52])],"derivedFrom":makeQuery(id+"FyYUAefgu6xEfva_4.38.F14.boolean.opBoolean","SPLIT",EDGE,{"disambiguationData":[TD([subQ52])],"derivedFrom":makeQuery(id+"FyYUAefgu6xEfva_4.37.F14.boolean.opBoolean","SPLIT",EDGE,{"disambiguationData":[TD([subQ52])],"derivedFrom":makeQuery(id+"FyYUAefgu6xEfva_4.36.F14.boolean.opBoolean","SPLIT",EDGE,{"disambiguationData":[TD([subQ52])],"derivedFrom":makeQuery(id+"FyYUAefgu6xEfva_4.35.F14.boolean.opBoolean","SPLIT",EDGE,{"disambiguationData":[TD([subQ52])],"derivedFrom":makeQuery(id+"FyYUAefgu6xEfva_4.34.F14.boolean.opBoolean","SPLIT",EDGE,{"disambiguationData":[TD([subQ52])],"derivedFrom":makeQuery(id+"FyYUAefgu6xEfva_4.33.F14.boolean.opBoolean","SPLIT",EDGE,{"disambiguationData":[TD([subQ52])],"derivedFrom":makeQuery(id+"FyYUAefgu6xEfva_4.32.F14.boolean.opBoolean","SPLIT",EDGE,{"disambiguationData":[TD([subQ52])],"derivedFrom":makeQuery(id+"FyYUAefgu6xEfva_4.31.F14.boolean.opBoolean","SPLIT",EDGE,{"disambiguationData":[TD([subQ52])],"derivedFrom":makeQuery(id+"FyYUAefgu6xEfva_4.30.F14.boolean.opBoolean","SPLIT",EDGE,{"disambiguationData":[TD([subQ52])],"derivedFrom":makeQuery(id+"FyYUAefgu6xEfva_4.29.F14.boolean.opBoolean","SPLIT",EDGE,{"disambiguationData":[TD([subQ52])],"derivedFrom":makeQuery(id+"FyYUAefgu6xEfva_4.28.F14.boolean.opBoolean","SPLIT",EDGE,{"disambiguationData":[TD([subQ52])],"derivedFrom":makeQuery(id+"FyYUAefgu6xEfva_4.27.F14.boolean.opBoolean","SPLIT",EDGE,{"disambiguationData":[TD([subQ52])],"derivedFrom":makeQuery(id+"FyYUAefgu6xEfva_4.26.F14.boolean.opBoolean","SPLIT",EDGE,{"disambiguationData":[TD([subQ52])],"derivedFrom":makeQuery(id+"FyYUAefgu6xEfva_4.25.F14.boolean.opBoolean","SPLIT",EDGE,{"disambiguationData":[TD([subQ52])],"derivedFrom":makeQuery(id+"FyYUAefgu6xEfva_4.24.F14.boolean.opBoolean","SPLIT",EDGE,{"disambiguationData":[TD([subQ52])],"derivedFrom":makeQuery(id+"FyYUAefgu6xEfva_4.23.F14.boolean.opBoolean","SPLIT",EDGE,{"disambiguationData":[TD([subQ52])],"derivedFrom":makeQuery(id+"FyYUAefgu6xEfva_4.22.F14.boolean.opBoolean","SPLIT",EDGE,{"disambiguationData":[TD([subQ52])],"derivedFrom":makeQuery(id+"FyYUAefgu6xEfva_4.21.F14.boolean.opBoolean","SPLIT",EDGE,{"disambiguationData":[TD([subQ52])],"derivedFrom":makeQuery(id+"FyYUAefgu6xEfva_4.20.F14.boolean.opBoolean","SPLIT",EDGE,{"disambiguationData":[TD([subQ52])],"derivedFrom":makeQuery(id+"FyYUAefgu6xEfva_4.19.F14.boolean.opBoolean","SPLIT",EDGE,{"disambiguationData":[TD([subQ52])],"derivedFrom":makeQuery(id+"FyYUAefgu6xEfva_4.18.F14.boolean.opBoolean","SPLIT",EDGE,{"disambiguationData":[TD([subQ52])],"derivedFrom":makeQuery(id+"FyYUAefgu6xEfva_4.17.F14.boolean.opBoolean","SPLIT",EDGE,{"disambiguationData":[TD([subQ52])],"derivedFrom":makeQuery(id+"FyYUAefgu6xEfva_4.16.F14.boolean.opBoolean","SPLIT",EDGE,{"disambiguationData":[TD([subQ52])],"derivedFrom":makeQuery(id+"FyYUAefgu6xEfva_4.15.F14.boolean.opBoolean","SPLIT",EDGE,{"disambiguationData":[TD([subQ52])],"derivedFrom":makeQuery(id+"FyYUAefgu6xEfva_4.14.F14.boolean.opBoolean","SPLIT",EDGE,{"disambiguationData":[TD([subQ52])],"derivedFrom":makeQuery(id+"FyYUAefgu6xEfva_4.13.F14.boolean.opBoolean","SPLIT",EDGE,{"disambiguationData":[TD([subQ52])],"derivedFrom":makeQuery(id+"FyYUAefgu6xEfva_4.12.F14.boolean.opBoolean","SPLIT",EDGE,{"disambiguationData":[TD([subQ52])],"derivedFrom":makeQuery(id+"FyYUAefgu6xEfva_4.11.F14.boolean.opBoolean","SPLIT",EDGE,{"disambiguationData":[TD([subQ52])],"derivedFrom":makeQuery(id+"FyYUAefgu6xEfva_4.10.F14.boolean.opBoolean","SPLIT",EDGE,{"disambiguationData":[TD([subQ52])],"derivedFrom":makeQuery(id+"FyYUAefgu6xEfva_4.9.F14.boolean.opBoolean","SPLIT",EDGE,{"disambiguationData":[TD([subQ52])],"derivedFrom":makeQuery(id+"FyYUAefgu6xEfva_4.8.F14.boolean.opBoolean","SPLIT",EDGE,{"disambiguationData":[TD([subQ52])],"derivedFrom":makeQuery(id+"FyYUAefgu6xEfva_4.7.F14.boolean.opBoolean","SPLIT",EDGE,{"disambiguationData":[TD([subQ52])],"derivedFrom":makeQuery(id+"FyYUAefgu6xEfva_4.6.F14.boolean.opBoolean","SPLIT",EDGE,{"disambiguationData":[TD([subQ52])],"derivedFrom":makeQuery(id+"FyYUAefgu6xEfva_4.5.F14.boolean.opBoolean","SPLIT",EDGE,{"disambiguationData":[TD([subQ52])],"derivedFrom":makeQuery(id+"FyYUAefgu6xEfva_4.4.F14.boolean.opBoolean","SPLIT",EDGE,{"disambiguationData":[TD([subQ52])],"derivedFrom":makeQuery(id+"FyYUAefgu6xEfva_4.3.F14.boolean.opBoolean","SPLIT",EDGE,{"disambiguationData":[TD([subQ52])],"derivedFrom":makeQuery(id+"FyYUAefgu6xEfva_4.2.F14.boolean.opBoolean","SPLIT",EDGE,{"disambiguationData":[TD([subQ52])],"derivedFrom":makeQuery(id+"FyYUAefgu6xEfva_4.1.F14.boolean.opBoolean","SPLIT",EDGE,{"disambiguationData":[TD([subQ52])],"derivedFrom":makeQuery(id+"F12.opExtrude","CAP_EDGE",EDGE,{"disambiguationData":[OSD([subQ2])],"isStart":false})})})})})})})})})})})})})})})})})})})})})})})})})})})})})})})})})})})})})})})})})})})})})});}
            var Q264;
            Q264=makeQuery(id+"FyYUAefgu6xEfva_4.14.F14.opExtrude","CAP_EDGE",EDGE,{"disambiguationData":[OSD([sQuery(id+"F13.wireOp",EDGE,"E147")])],"isStart":false});
            var Q265;
            Q265=makeQuery(id+"FyYUAefgu6xEfva_4.14.F14.opExtrude","CAP_EDGE",EDGE,{"disambiguationData":[OSD([sQuery(id+"F13.wireOp",EDGE,"E148.MirrorCS")])],"isStart":false});
            var Q266;
            Q266=makeQuery(id+"FyYUAefgu6xEfva_4.46.F14.opExtrude","CAP_EDGE",EDGE,{"disambiguationData":[OSD([sQuery(id+"F13.wireOp",EDGE,"E147")])],"isStart":false});
            var Q267;
            Q267=makeQuery(id+"FyYUAefgu6xEfva_4.14.F14.opExtrude","SWEPT_EDGE",EDGE,{"disambiguationData":[OSD([sQuery(id+"F9.wireOp",EDGE,"E142"),sQuery(id+"F13.wireOp",EDGE,"E147")])]});
            var Q268;
            Q268=makeQuery(id+"FyYUAefgu6xEfva_4.14.F14.opExtrude","SWEPT_EDGE",EDGE,{"disambiguationData":[OSD([sQuery(id+"F11.wireOp",EDGE,"E143"),sQuery(id+"F13.wireOp",EDGE,"E147")])]});
            var Q269;
            Q269=makeQuery(id+"FyYUAefgu6xEfva_4.14.F14.opExtrude","CAP_EDGE",EDGE,{"disambiguationData":[OSD([sQuery(id+"F9.wireOp",EDGE,"E142")])],"isStart":false});
            var Q270;
            {var subQ0=sQuery(id+"F13.wireOp",EDGE,"E148.MirrorCS");var subQ1=sQuery(id+"F13.wireOp",EDGE,"E147");var subQ2=sQuery(id+"F11.wireOp",EDGE,"E143");var subQ20=makeQuery(id+"FyYUAefgu6xEfva_4.13.F14.opExtrude","SWEPT_FACE",FACE,{"disambiguationData":[OSD([subQ0])]});var subQ21=makeQuery(id+"F14.opExtrude","SWEPT_FACE",FACE,{"disambiguationData":[OSD([subQ1])]});Q270=makeQuery(id+"FyYUAefgu6xEfva_4.14.F14.boolean.opBoolean","SPLIT",EDGE,{"disambiguationData":[TD([subQ20])],"derivedFrom":makeQuery(id+"FyYUAefgu6xEfva_4.13.F14.boolean.opBoolean","SPLIT",EDGE,{"disambiguationData":[TD([subQ21])],"derivedFrom":makeQuery(id+"FyYUAefgu6xEfva_4.12.F14.boolean.opBoolean","SPLIT",EDGE,{"disambiguationData":[TD([subQ21])],"derivedFrom":makeQuery(id+"FyYUAefgu6xEfva_4.11.F14.boolean.opBoolean","SPLIT",EDGE,{"disambiguationData":[TD([subQ21])],"derivedFrom":makeQuery(id+"FyYUAefgu6xEfva_4.10.F14.boolean.opBoolean","SPLIT",EDGE,{"disambiguationData":[TD([subQ21])],"derivedFrom":makeQuery(id+"FyYUAefgu6xEfva_4.9.F14.boolean.opBoolean","SPLIT",EDGE,{"disambiguationData":[TD([subQ21])],"derivedFrom":makeQuery(id+"FyYUAefgu6xEfva_4.8.F14.boolean.opBoolean","SPLIT",EDGE,{"disambiguationData":[TD([subQ21])],"derivedFrom":makeQuery(id+"FyYUAefgu6xEfva_4.7.F14.boolean.opBoolean","SPLIT",EDGE,{"disambiguationData":[TD([subQ21])],"derivedFrom":makeQuery(id+"FyYUAefgu6xEfva_4.6.F14.boolean.opBoolean","SPLIT",EDGE,{"disambiguationData":[TD([subQ21])],"derivedFrom":makeQuery(id+"FyYUAefgu6xEfva_4.5.F14.boolean.opBoolean","SPLIT",EDGE,{"disambiguationData":[TD([subQ21])],"derivedFrom":makeQuery(id+"FyYUAefgu6xEfva_4.4.F14.boolean.opBoolean","SPLIT",EDGE,{"disambiguationData":[TD([subQ21])],"derivedFrom":makeQuery(id+"FyYUAefgu6xEfva_4.3.F14.boolean.opBoolean","SPLIT",EDGE,{"disambiguationData":[TD([subQ21])],"derivedFrom":makeQuery(id+"FyYUAefgu6xEfva_4.2.F14.boolean.opBoolean","SPLIT",EDGE,{"disambiguationData":[TD([subQ21])],"derivedFrom":makeQuery(id+"FyYUAefgu6xEfva_4.1.F14.boolean.opBoolean","SPLIT",EDGE,{"disambiguationData":[TD([subQ21])],"derivedFrom":makeQuery(id+"F12.opExtrude","CAP_EDGE",EDGE,{"disambiguationData":[OSD([subQ2])],"isStart":false})})})})})})})})})})})})})})});}
            var Q271;
            Q271=makeQuery(id+"FyYUAefgu6xEfva_4.46.F14.opExtrude","SWEPT_EDGE",EDGE,{"disambiguationData":[OSD([sQuery(id+"F9.wireOp",EDGE,"E142"),sQuery(id+"F13.wireOp",EDGE,"E147")])]});
            var Q272;
            Q272=makeQuery(id+"FyYUAefgu6xEfva_4.46.F14.opExtrude","SWEPT_EDGE",EDGE,{"disambiguationData":[OSD([sQuery(id+"F11.wireOp",EDGE,"E143"),sQuery(id+"F13.wireOp",EDGE,"E147")])]});
            var Q273;
            Q273=makeQuery(id+"FyYUAefgu6xEfva_4.46.F14.opExtrude","SWEPT_EDGE",EDGE,{"disambiguationData":[OSD([sQuery(id+"F9.wireOp",EDGE,"E142"),sQuery(id+"F13.wireOp",EDGE,"E148.MirrorCS")])]});
            var Q274;
            Q274=makeQuery(id+"FyYUAefgu6xEfva_4.46.F14.opExtrude","SWEPT_EDGE",EDGE,{"disambiguationData":[OSD([sQuery(id+"F11.wireOp",EDGE,"E143"),sQuery(id+"F13.wireOp",EDGE,"E148.MirrorCS")])]});
            var Q275;
            Q275=makeQuery(id+"FyYUAefgu6xEfva_4.46.F14.opExtrude","CAP_EDGE",EDGE,{"disambiguationData":[OSD([sQuery(id+"F13.wireOp",EDGE,"E147")])],"isStart":true});
            var Q276;
            Q276=makeQuery(id+"FyYUAefgu6xEfva_4.46.F14.opExtrude","CAP_EDGE",EDGE,{"disambiguationData":[OSD([sQuery(id+"F13.wireOp",EDGE,"E148.MirrorCS")])],"isStart":true});
            var Q277;
            Q277=makeQuery(id+"FyYUAefgu6xEfva_4.46.F14.opExtrude","CAP_EDGE",EDGE,{"disambiguationData":[OSD([sQuery(id+"F9.wireOp",EDGE,"E142")])],"isStart":false});
            var Q278;
            {var subQ0=sQuery(id+"F9.wireOp",EDGE,"E142");var subQ2=sQuery(id+"F13.wireOp",EDGE,"E148.MirrorCS");var subQ3=makeQuery(id+"FyYUAefgu6xEfva_4.45.F14.opExtrude","SWEPT_FACE",FACE,{"disambiguationData":[OSD([subQ2])]});var subQ5=sQuery(id+"F13.wireOp",EDGE,"E147");var subQ6=makeQuery(id+"F14.opExtrude","SWEPT_FACE",FACE,{"disambiguationData":[OSD([subQ5])]});Q278=makeQuery(id+"FyYUAefgu6xEfva_4.46.F14.boolean.opBoolean","SPLIT",EDGE,{"disambiguationData":[TD([subQ3])],"derivedFrom":makeQuery(id+"FyYUAefgu6xEfva_4.45.F14.boolean.opBoolean","SPLIT",EDGE,{"disambiguationData":[TD([subQ6])],"derivedFrom":makeQuery(id+"FyYUAefgu6xEfva_4.44.F14.boolean.opBoolean","SPLIT",EDGE,{"disambiguationData":[TD([subQ6])],"derivedFrom":makeQuery(id+"FyYUAefgu6xEfva_4.43.F14.boolean.opBoolean","SPLIT",EDGE,{"disambiguationData":[TD([subQ6])],"derivedFrom":makeQuery(id+"FyYUAefgu6xEfva_4.42.F14.boolean.opBoolean","SPLIT",EDGE,{"disambiguationData":[TD([subQ6])],"derivedFrom":makeQuery(id+"FyYUAefgu6xEfva_4.41.F14.boolean.opBoolean","SPLIT",EDGE,{"disambiguationData":[TD([subQ6])],"derivedFrom":makeQuery(id+"FyYUAefgu6xEfva_4.40.F14.boolean.opBoolean","SPLIT",EDGE,{"disambiguationData":[TD([subQ6])],"derivedFrom":makeQuery(id+"FyYUAefgu6xEfva_4.39.F14.boolean.opBoolean","SPLIT",EDGE,{"disambiguationData":[TD([subQ6])],"derivedFrom":makeQuery(id+"FyYUAefgu6xEfva_4.38.F14.boolean.opBoolean","SPLIT",EDGE,{"disambiguationData":[TD([subQ6])],"derivedFrom":makeQuery(id+"FyYUAefgu6xEfva_4.37.F14.boolean.opBoolean","SPLIT",EDGE,{"disambiguationData":[TD([subQ6])],"derivedFrom":makeQuery(id+"FyYUAefgu6xEfva_4.36.F14.boolean.opBoolean","SPLIT",EDGE,{"disambiguationData":[TD([subQ6])],"derivedFrom":makeQuery(id+"FyYUAefgu6xEfva_4.35.F14.boolean.opBoolean","SPLIT",EDGE,{"disambiguationData":[TD([subQ6])],"derivedFrom":makeQuery(id+"FyYUAefgu6xEfva_4.34.F14.boolean.opBoolean","SPLIT",EDGE,{"disambiguationData":[TD([subQ6])],"derivedFrom":makeQuery(id+"FyYUAefgu6xEfva_4.33.F14.boolean.opBoolean","SPLIT",EDGE,{"disambiguationData":[TD([subQ6])],"derivedFrom":makeQuery(id+"FyYUAefgu6xEfva_4.32.F14.boolean.opBoolean","SPLIT",EDGE,{"disambiguationData":[TD([subQ6])],"derivedFrom":makeQuery(id+"FyYUAefgu6xEfva_4.31.F14.boolean.opBoolean","SPLIT",EDGE,{"disambiguationData":[TD([subQ6])],"derivedFrom":makeQuery(id+"FyYUAefgu6xEfva_4.30.F14.boolean.opBoolean","SPLIT",EDGE,{"disambiguationData":[TD([subQ6])],"derivedFrom":makeQuery(id+"FyYUAefgu6xEfva_4.29.F14.boolean.opBoolean","SPLIT",EDGE,{"disambiguationData":[TD([subQ6])],"derivedFrom":makeQuery(id+"FyYUAefgu6xEfva_4.28.F14.boolean.opBoolean","SPLIT",EDGE,{"disambiguationData":[TD([subQ6])],"derivedFrom":makeQuery(id+"FyYUAefgu6xEfva_4.27.F14.boolean.opBoolean","SPLIT",EDGE,{"disambiguationData":[TD([subQ6])],"derivedFrom":makeQuery(id+"FyYUAefgu6xEfva_4.26.F14.boolean.opBoolean","SPLIT",EDGE,{"disambiguationData":[TD([subQ6])],"derivedFrom":makeQuery(id+"FyYUAefgu6xEfva_4.25.F14.boolean.opBoolean","SPLIT",EDGE,{"disambiguationData":[TD([subQ6])],"derivedFrom":makeQuery(id+"FyYUAefgu6xEfva_4.24.F14.boolean.opBoolean","SPLIT",EDGE,{"disambiguationData":[TD([subQ6])],"derivedFrom":makeQuery(id+"FyYUAefgu6xEfva_4.23.F14.boolean.opBoolean","SPLIT",EDGE,{"disambiguationData":[TD([subQ6])],"derivedFrom":makeQuery(id+"FyYUAefgu6xEfva_4.22.F14.boolean.opBoolean","SPLIT",EDGE,{"disambiguationData":[TD([subQ6])],"derivedFrom":makeQuery(id+"FyYUAefgu6xEfva_4.21.F14.boolean.opBoolean","SPLIT",EDGE,{"disambiguationData":[TD([subQ6])],"derivedFrom":makeQuery(id+"FyYUAefgu6xEfva_4.20.F14.boolean.opBoolean","SPLIT",EDGE,{"disambiguationData":[TD([subQ6])],"derivedFrom":makeQuery(id+"FyYUAefgu6xEfva_4.19.F14.boolean.opBoolean","SPLIT",EDGE,{"disambiguationData":[TD([subQ6])],"derivedFrom":makeQuery(id+"FyYUAefgu6xEfva_4.18.F14.boolean.opBoolean","SPLIT",EDGE,{"disambiguationData":[TD([subQ6])],"derivedFrom":makeQuery(id+"FyYUAefgu6xEfva_4.17.F14.boolean.opBoolean","SPLIT",EDGE,{"disambiguationData":[TD([subQ6])],"derivedFrom":makeQuery(id+"FyYUAefgu6xEfva_4.16.F14.boolean.opBoolean","SPLIT",EDGE,{"disambiguationData":[TD([subQ6])],"derivedFrom":makeQuery(id+"FyYUAefgu6xEfva_4.15.F14.boolean.opBoolean","SPLIT",EDGE,{"disambiguationData":[TD([subQ6])],"derivedFrom":makeQuery(id+"FyYUAefgu6xEfva_4.14.F14.boolean.opBoolean","SPLIT",EDGE,{"disambiguationData":[TD([subQ6])],"derivedFrom":makeQuery(id+"FyYUAefgu6xEfva_4.13.F14.boolean.opBoolean","SPLIT",EDGE,{"disambiguationData":[TD([subQ6])],"derivedFrom":makeQuery(id+"FyYUAefgu6xEfva_4.12.F14.boolean.opBoolean","SPLIT",EDGE,{"disambiguationData":[TD([subQ6])],"derivedFrom":makeQuery(id+"FyYUAefgu6xEfva_4.11.F14.boolean.opBoolean","SPLIT",EDGE,{"disambiguationData":[TD([subQ6])],"derivedFrom":makeQuery(id+"FyYUAefgu6xEfva_4.10.F14.boolean.opBoolean","SPLIT",EDGE,{"disambiguationData":[TD([subQ6])],"derivedFrom":makeQuery(id+"FyYUAefgu6xEfva_4.9.F14.boolean.opBoolean","SPLIT",EDGE,{"disambiguationData":[TD([subQ6])],"derivedFrom":makeQuery(id+"FyYUAefgu6xEfva_4.8.F14.boolean.opBoolean","SPLIT",EDGE,{"disambiguationData":[TD([subQ6])],"derivedFrom":makeQuery(id+"FyYUAefgu6xEfva_4.7.F14.boolean.opBoolean","SPLIT",EDGE,{"disambiguationData":[TD([subQ6])],"derivedFrom":makeQuery(id+"FyYUAefgu6xEfva_4.6.F14.boolean.opBoolean","SPLIT",EDGE,{"disambiguationData":[TD([subQ6])],"derivedFrom":makeQuery(id+"FyYUAefgu6xEfva_4.5.F14.boolean.opBoolean","SPLIT",EDGE,{"disambiguationData":[TD([subQ6])],"derivedFrom":makeQuery(id+"FyYUAefgu6xEfva_4.4.F14.boolean.opBoolean","SPLIT",EDGE,{"disambiguationData":[TD([subQ6])],"derivedFrom":makeQuery(id+"FyYUAefgu6xEfva_4.3.F14.boolean.opBoolean","SPLIT",EDGE,{"disambiguationData":[TD([subQ6])],"derivedFrom":makeQuery(id+"FyYUAefgu6xEfva_4.2.F14.boolean.opBoolean","SPLIT",EDGE,{"disambiguationData":[TD([subQ6])],"derivedFrom":makeQuery(id+"FyYUAefgu6xEfva_4.1.F14.boolean.opBoolean","SPLIT",EDGE,{"disambiguationData":[TD([subQ6])],"derivedFrom":makeQuery(id+"F10.boolean.opBoolean","COPY",EDGE,{"derivedFrom":makeQuery(id+"F10.opExtrude","CAP_EDGE",EDGE,{"disambiguationData":[OSD([subQ0])],"isStart":false})})})})})})})})})})})})})})})})})})})})})})})})})})})})})})})})})})})})})})})})})})})})})})})});}
            var Q279;
            {var subQ0=sQuery(id+"F13.wireOp",EDGE,"E148.MirrorCS");var subQ1=sQuery(id+"F13.wireOp",EDGE,"E147");var subQ2=sQuery(id+"F11.wireOp",EDGE,"E143");var subQ11=makeQuery(id+"FyYUAefgu6xEfva_4.45.F14.opExtrude","SWEPT_FACE",FACE,{"disambiguationData":[OSD([subQ0])]});var subQ53=makeQuery(id+"F14.opExtrude","SWEPT_FACE",FACE,{"disambiguationData":[OSD([subQ1])]});Q279=makeQuery(id+"FyYUAefgu6xEfva_4.46.F14.boolean.opBoolean","SPLIT",EDGE,{"disambiguationData":[TD([subQ11])],"derivedFrom":makeQuery(id+"FyYUAefgu6xEfva_4.45.F14.boolean.opBoolean","SPLIT",EDGE,{"disambiguationData":[TD([subQ53])],"derivedFrom":makeQuery(id+"FyYUAefgu6xEfva_4.44.F14.boolean.opBoolean","SPLIT",EDGE,{"disambiguationData":[TD([subQ53])],"derivedFrom":makeQuery(id+"FyYUAefgu6xEfva_4.43.F14.boolean.opBoolean","SPLIT",EDGE,{"disambiguationData":[TD([subQ53])],"derivedFrom":makeQuery(id+"FyYUAefgu6xEfva_4.42.F14.boolean.opBoolean","SPLIT",EDGE,{"disambiguationData":[TD([subQ53])],"derivedFrom":makeQuery(id+"FyYUAefgu6xEfva_4.41.F14.boolean.opBoolean","SPLIT",EDGE,{"disambiguationData":[TD([subQ53])],"derivedFrom":makeQuery(id+"FyYUAefgu6xEfva_4.40.F14.boolean.opBoolean","SPLIT",EDGE,{"disambiguationData":[TD([subQ53])],"derivedFrom":makeQuery(id+"FyYUAefgu6xEfva_4.39.F14.boolean.opBoolean","SPLIT",EDGE,{"disambiguationData":[TD([subQ53])],"derivedFrom":makeQuery(id+"FyYUAefgu6xEfva_4.38.F14.boolean.opBoolean","SPLIT",EDGE,{"disambiguationData":[TD([subQ53])],"derivedFrom":makeQuery(id+"FyYUAefgu6xEfva_4.37.F14.boolean.opBoolean","SPLIT",EDGE,{"disambiguationData":[TD([subQ53])],"derivedFrom":makeQuery(id+"FyYUAefgu6xEfva_4.36.F14.boolean.opBoolean","SPLIT",EDGE,{"disambiguationData":[TD([subQ53])],"derivedFrom":makeQuery(id+"FyYUAefgu6xEfva_4.35.F14.boolean.opBoolean","SPLIT",EDGE,{"disambiguationData":[TD([subQ53])],"derivedFrom":makeQuery(id+"FyYUAefgu6xEfva_4.34.F14.boolean.opBoolean","SPLIT",EDGE,{"disambiguationData":[TD([subQ53])],"derivedFrom":makeQuery(id+"FyYUAefgu6xEfva_4.33.F14.boolean.opBoolean","SPLIT",EDGE,{"disambiguationData":[TD([subQ53])],"derivedFrom":makeQuery(id+"FyYUAefgu6xEfva_4.32.F14.boolean.opBoolean","SPLIT",EDGE,{"disambiguationData":[TD([subQ53])],"derivedFrom":makeQuery(id+"FyYUAefgu6xEfva_4.31.F14.boolean.opBoolean","SPLIT",EDGE,{"disambiguationData":[TD([subQ53])],"derivedFrom":makeQuery(id+"FyYUAefgu6xEfva_4.30.F14.boolean.opBoolean","SPLIT",EDGE,{"disambiguationData":[TD([subQ53])],"derivedFrom":makeQuery(id+"FyYUAefgu6xEfva_4.29.F14.boolean.opBoolean","SPLIT",EDGE,{"disambiguationData":[TD([subQ53])],"derivedFrom":makeQuery(id+"FyYUAefgu6xEfva_4.28.F14.boolean.opBoolean","SPLIT",EDGE,{"disambiguationData":[TD([subQ53])],"derivedFrom":makeQuery(id+"FyYUAefgu6xEfva_4.27.F14.boolean.opBoolean","SPLIT",EDGE,{"disambiguationData":[TD([subQ53])],"derivedFrom":makeQuery(id+"FyYUAefgu6xEfva_4.26.F14.boolean.opBoolean","SPLIT",EDGE,{"disambiguationData":[TD([subQ53])],"derivedFrom":makeQuery(id+"FyYUAefgu6xEfva_4.25.F14.boolean.opBoolean","SPLIT",EDGE,{"disambiguationData":[TD([subQ53])],"derivedFrom":makeQuery(id+"FyYUAefgu6xEfva_4.24.F14.boolean.opBoolean","SPLIT",EDGE,{"disambiguationData":[TD([subQ53])],"derivedFrom":makeQuery(id+"FyYUAefgu6xEfva_4.23.F14.boolean.opBoolean","SPLIT",EDGE,{"disambiguationData":[TD([subQ53])],"derivedFrom":makeQuery(id+"FyYUAefgu6xEfva_4.22.F14.boolean.opBoolean","SPLIT",EDGE,{"disambiguationData":[TD([subQ53])],"derivedFrom":makeQuery(id+"FyYUAefgu6xEfva_4.21.F14.boolean.opBoolean","SPLIT",EDGE,{"disambiguationData":[TD([subQ53])],"derivedFrom":makeQuery(id+"FyYUAefgu6xEfva_4.20.F14.boolean.opBoolean","SPLIT",EDGE,{"disambiguationData":[TD([subQ53])],"derivedFrom":makeQuery(id+"FyYUAefgu6xEfva_4.19.F14.boolean.opBoolean","SPLIT",EDGE,{"disambiguationData":[TD([subQ53])],"derivedFrom":makeQuery(id+"FyYUAefgu6xEfva_4.18.F14.boolean.opBoolean","SPLIT",EDGE,{"disambiguationData":[TD([subQ53])],"derivedFrom":makeQuery(id+"FyYUAefgu6xEfva_4.17.F14.boolean.opBoolean","SPLIT",EDGE,{"disambiguationData":[TD([subQ53])],"derivedFrom":makeQuery(id+"FyYUAefgu6xEfva_4.16.F14.boolean.opBoolean","SPLIT",EDGE,{"disambiguationData":[TD([subQ53])],"derivedFrom":makeQuery(id+"FyYUAefgu6xEfva_4.15.F14.boolean.opBoolean","SPLIT",EDGE,{"disambiguationData":[TD([subQ53])],"derivedFrom":makeQuery(id+"FyYUAefgu6xEfva_4.14.F14.boolean.opBoolean","SPLIT",EDGE,{"disambiguationData":[TD([subQ53])],"derivedFrom":makeQuery(id+"FyYUAefgu6xEfva_4.13.F14.boolean.opBoolean","SPLIT",EDGE,{"disambiguationData":[TD([subQ53])],"derivedFrom":makeQuery(id+"FyYUAefgu6xEfva_4.12.F14.boolean.opBoolean","SPLIT",EDGE,{"disambiguationData":[TD([subQ53])],"derivedFrom":makeQuery(id+"FyYUAefgu6xEfva_4.11.F14.boolean.opBoolean","SPLIT",EDGE,{"disambiguationData":[TD([subQ53])],"derivedFrom":makeQuery(id+"FyYUAefgu6xEfva_4.10.F14.boolean.opBoolean","SPLIT",EDGE,{"disambiguationData":[TD([subQ53])],"derivedFrom":makeQuery(id+"FyYUAefgu6xEfva_4.9.F14.boolean.opBoolean","SPLIT",EDGE,{"disambiguationData":[TD([subQ53])],"derivedFrom":makeQuery(id+"FyYUAefgu6xEfva_4.8.F14.boolean.opBoolean","SPLIT",EDGE,{"disambiguationData":[TD([subQ53])],"derivedFrom":makeQuery(id+"FyYUAefgu6xEfva_4.7.F14.boolean.opBoolean","SPLIT",EDGE,{"disambiguationData":[TD([subQ53])],"derivedFrom":makeQuery(id+"FyYUAefgu6xEfva_4.6.F14.boolean.opBoolean","SPLIT",EDGE,{"disambiguationData":[TD([subQ53])],"derivedFrom":makeQuery(id+"FyYUAefgu6xEfva_4.5.F14.boolean.opBoolean","SPLIT",EDGE,{"disambiguationData":[TD([subQ53])],"derivedFrom":makeQuery(id+"FyYUAefgu6xEfva_4.4.F14.boolean.opBoolean","SPLIT",EDGE,{"disambiguationData":[TD([subQ53])],"derivedFrom":makeQuery(id+"FyYUAefgu6xEfva_4.3.F14.boolean.opBoolean","SPLIT",EDGE,{"disambiguationData":[TD([subQ53])],"derivedFrom":makeQuery(id+"FyYUAefgu6xEfva_4.2.F14.boolean.opBoolean","SPLIT",EDGE,{"disambiguationData":[TD([subQ53])],"derivedFrom":makeQuery(id+"FyYUAefgu6xEfva_4.1.F14.boolean.opBoolean","SPLIT",EDGE,{"disambiguationData":[TD([subQ53])],"derivedFrom":makeQuery(id+"F12.opExtrude","CAP_EDGE",EDGE,{"disambiguationData":[OSD([subQ2])],"isStart":false})})})})})})})})})})})})})})})})})})})})})})})})})})})})})})})})})})})})})})})})})})})})})})});}
            var Q280;
            Q280=makeQuery(id+"FyYUAefgu6xEfva_4.15.F14.opExtrude","SWEPT_EDGE",EDGE,{"disambiguationData":[OSD([sQuery(id+"F9.wireOp",EDGE,"E142"),sQuery(id+"F13.wireOp",EDGE,"E147")])]});
            var Q281;
            Q281=makeQuery(id+"FyYUAefgu6xEfva_4.15.F14.opExtrude","SWEPT_EDGE",EDGE,{"disambiguationData":[OSD([sQuery(id+"F11.wireOp",EDGE,"E143"),sQuery(id+"F13.wireOp",EDGE,"E147")])]});
            var Q282;
            Q282=makeQuery(id+"FyYUAefgu6xEfva_4.15.F14.opExtrude","SWEPT_EDGE",EDGE,{"disambiguationData":[OSD([sQuery(id+"F9.wireOp",EDGE,"E142"),sQuery(id+"F13.wireOp",EDGE,"E148.MirrorCS")])]});
            var Q283;
            Q283=makeQuery(id+"FyYUAefgu6xEfva_4.15.F14.opExtrude","SWEPT_EDGE",EDGE,{"disambiguationData":[OSD([sQuery(id+"F11.wireOp",EDGE,"E143"),sQuery(id+"F13.wireOp",EDGE,"E148.MirrorCS")])]});
            var Q284;
            Q284=makeQuery(id+"FyYUAefgu6xEfva_4.15.F14.opExtrude","CAP_EDGE",EDGE,{"disambiguationData":[OSD([sQuery(id+"F9.wireOp",EDGE,"E142")])],"isStart":false});
            var Q285;
            {var subQ0=sQuery(id+"F13.wireOp",EDGE,"E148.MirrorCS");var subQ1=sQuery(id+"F13.wireOp",EDGE,"E147");var subQ2=sQuery(id+"F11.wireOp",EDGE,"E143");var subQ13=makeQuery(id+"FyYUAefgu6xEfva_4.14.F14.opExtrude","SWEPT_FACE",FACE,{"disambiguationData":[OSD([subQ0])]});var subQ22=makeQuery(id+"F14.opExtrude","SWEPT_FACE",FACE,{"disambiguationData":[OSD([subQ1])]});Q285=makeQuery(id+"FyYUAefgu6xEfva_4.15.F14.boolean.opBoolean","SPLIT",EDGE,{"disambiguationData":[TD([subQ13])],"derivedFrom":makeQuery(id+"FyYUAefgu6xEfva_4.14.F14.boolean.opBoolean","SPLIT",EDGE,{"disambiguationData":[TD([subQ22])],"derivedFrom":makeQuery(id+"FyYUAefgu6xEfva_4.13.F14.boolean.opBoolean","SPLIT",EDGE,{"disambiguationData":[TD([subQ22])],"derivedFrom":makeQuery(id+"FyYUAefgu6xEfva_4.12.F14.boolean.opBoolean","SPLIT",EDGE,{"disambiguationData":[TD([subQ22])],"derivedFrom":makeQuery(id+"FyYUAefgu6xEfva_4.11.F14.boolean.opBoolean","SPLIT",EDGE,{"disambiguationData":[TD([subQ22])],"derivedFrom":makeQuery(id+"FyYUAefgu6xEfva_4.10.F14.boolean.opBoolean","SPLIT",EDGE,{"disambiguationData":[TD([subQ22])],"derivedFrom":makeQuery(id+"FyYUAefgu6xEfva_4.9.F14.boolean.opBoolean","SPLIT",EDGE,{"disambiguationData":[TD([subQ22])],"derivedFrom":makeQuery(id+"FyYUAefgu6xEfva_4.8.F14.boolean.opBoolean","SPLIT",EDGE,{"disambiguationData":[TD([subQ22])],"derivedFrom":makeQuery(id+"FyYUAefgu6xEfva_4.7.F14.boolean.opBoolean","SPLIT",EDGE,{"disambiguationData":[TD([subQ22])],"derivedFrom":makeQuery(id+"FyYUAefgu6xEfva_4.6.F14.boolean.opBoolean","SPLIT",EDGE,{"disambiguationData":[TD([subQ22])],"derivedFrom":makeQuery(id+"FyYUAefgu6xEfva_4.5.F14.boolean.opBoolean","SPLIT",EDGE,{"disambiguationData":[TD([subQ22])],"derivedFrom":makeQuery(id+"FyYUAefgu6xEfva_4.4.F14.boolean.opBoolean","SPLIT",EDGE,{"disambiguationData":[TD([subQ22])],"derivedFrom":makeQuery(id+"FyYUAefgu6xEfva_4.3.F14.boolean.opBoolean","SPLIT",EDGE,{"disambiguationData":[TD([subQ22])],"derivedFrom":makeQuery(id+"FyYUAefgu6xEfva_4.2.F14.boolean.opBoolean","SPLIT",EDGE,{"disambiguationData":[TD([subQ22])],"derivedFrom":makeQuery(id+"FyYUAefgu6xEfva_4.1.F14.boolean.opBoolean","SPLIT",EDGE,{"disambiguationData":[TD([subQ22])],"derivedFrom":makeQuery(id+"F12.opExtrude","CAP_EDGE",EDGE,{"disambiguationData":[OSD([subQ2])],"isStart":false})})})})})})})})})})})})})})})});}
            var Q286;
            Q286=makeQuery(id+"FyYUAefgu6xEfva_4.47.F14.opExtrude","SWEPT_EDGE",EDGE,{"disambiguationData":[OSD([sQuery(id+"F9.wireOp",EDGE,"E142"),sQuery(id+"F13.wireOp",EDGE,"E147")])]});
            var Q287;
            Q287=makeQuery(id+"FyYUAefgu6xEfva_4.47.F14.opExtrude","SWEPT_EDGE",EDGE,{"disambiguationData":[OSD([sQuery(id+"F11.wireOp",EDGE,"E143"),sQuery(id+"F13.wireOp",EDGE,"E147")])]});
            var Q288;
            Q288=makeQuery(id+"FyYUAefgu6xEfva_4.47.F14.opExtrude","SWEPT_EDGE",EDGE,{"disambiguationData":[OSD([sQuery(id+"F9.wireOp",EDGE,"E142"),sQuery(id+"F13.wireOp",EDGE,"E148.MirrorCS")])]});
            var Q289;
            Q289=makeQuery(id+"FyYUAefgu6xEfva_4.47.F14.opExtrude","SWEPT_EDGE",EDGE,{"disambiguationData":[OSD([sQuery(id+"F11.wireOp",EDGE,"E143"),sQuery(id+"F13.wireOp",EDGE,"E148.MirrorCS")])]});
            var Q290;
            Q290=makeQuery(id+"FyYUAefgu6xEfva_4.47.F14.opExtrude","CAP_EDGE",EDGE,{"disambiguationData":[OSD([sQuery(id+"F13.wireOp",EDGE,"E147")])],"isStart":true});
            var Q291;
            {var subQ0=sQuery(id+"F9.wireOp",EDGE,"E142");var subQ3=sQuery(id+"F13.wireOp",EDGE,"E147");var subQ4=sQuery(id+"F13.wireOp",EDGE,"E148.MirrorCS");var subQ5=makeQuery(id+"FyYUAefgu6xEfva_4.46.F14.opExtrude","SWEPT_FACE",FACE,{"disambiguationData":[OSD([subQ4])]});var subQ6=makeQuery(id+"F14.opExtrude","SWEPT_FACE",FACE,{"disambiguationData":[OSD([subQ3])]});Q291=makeQuery(id+"FyYUAefgu6xEfva_4.47.F14.boolean.opBoolean","SPLIT",EDGE,{"disambiguationData":[TD([subQ5])],"derivedFrom":makeQuery(id+"FyYUAefgu6xEfva_4.46.F14.boolean.opBoolean","SPLIT",EDGE,{"disambiguationData":[TD([subQ6])],"derivedFrom":makeQuery(id+"FyYUAefgu6xEfva_4.45.F14.boolean.opBoolean","SPLIT",EDGE,{"disambiguationData":[TD([subQ6])],"derivedFrom":makeQuery(id+"FyYUAefgu6xEfva_4.44.F14.boolean.opBoolean","SPLIT",EDGE,{"disambiguationData":[TD([subQ6])],"derivedFrom":makeQuery(id+"FyYUAefgu6xEfva_4.43.F14.boolean.opBoolean","SPLIT",EDGE,{"disambiguationData":[TD([subQ6])],"derivedFrom":makeQuery(id+"FyYUAefgu6xEfva_4.42.F14.boolean.opBoolean","SPLIT",EDGE,{"disambiguationData":[TD([subQ6])],"derivedFrom":makeQuery(id+"FyYUAefgu6xEfva_4.41.F14.boolean.opBoolean","SPLIT",EDGE,{"disambiguationData":[TD([subQ6])],"derivedFrom":makeQuery(id+"FyYUAefgu6xEfva_4.40.F14.boolean.opBoolean","SPLIT",EDGE,{"disambiguationData":[TD([subQ6])],"derivedFrom":makeQuery(id+"FyYUAefgu6xEfva_4.39.F14.boolean.opBoolean","SPLIT",EDGE,{"disambiguationData":[TD([subQ6])],"derivedFrom":makeQuery(id+"FyYUAefgu6xEfva_4.38.F14.boolean.opBoolean","SPLIT",EDGE,{"disambiguationData":[TD([subQ6])],"derivedFrom":makeQuery(id+"FyYUAefgu6xEfva_4.37.F14.boolean.opBoolean","SPLIT",EDGE,{"disambiguationData":[TD([subQ6])],"derivedFrom":makeQuery(id+"FyYUAefgu6xEfva_4.36.F14.boolean.opBoolean","SPLIT",EDGE,{"disambiguationData":[TD([subQ6])],"derivedFrom":makeQuery(id+"FyYUAefgu6xEfva_4.35.F14.boolean.opBoolean","SPLIT",EDGE,{"disambiguationData":[TD([subQ6])],"derivedFrom":makeQuery(id+"FyYUAefgu6xEfva_4.34.F14.boolean.opBoolean","SPLIT",EDGE,{"disambiguationData":[TD([subQ6])],"derivedFrom":makeQuery(id+"FyYUAefgu6xEfva_4.33.F14.boolean.opBoolean","SPLIT",EDGE,{"disambiguationData":[TD([subQ6])],"derivedFrom":makeQuery(id+"FyYUAefgu6xEfva_4.32.F14.boolean.opBoolean","SPLIT",EDGE,{"disambiguationData":[TD([subQ6])],"derivedFrom":makeQuery(id+"FyYUAefgu6xEfva_4.31.F14.boolean.opBoolean","SPLIT",EDGE,{"disambiguationData":[TD([subQ6])],"derivedFrom":makeQuery(id+"FyYUAefgu6xEfva_4.30.F14.boolean.opBoolean","SPLIT",EDGE,{"disambiguationData":[TD([subQ6])],"derivedFrom":makeQuery(id+"FyYUAefgu6xEfva_4.29.F14.boolean.opBoolean","SPLIT",EDGE,{"disambiguationData":[TD([subQ6])],"derivedFrom":makeQuery(id+"FyYUAefgu6xEfva_4.28.F14.boolean.opBoolean","SPLIT",EDGE,{"disambiguationData":[TD([subQ6])],"derivedFrom":makeQuery(id+"FyYUAefgu6xEfva_4.27.F14.boolean.opBoolean","SPLIT",EDGE,{"disambiguationData":[TD([subQ6])],"derivedFrom":makeQuery(id+"FyYUAefgu6xEfva_4.26.F14.boolean.opBoolean","SPLIT",EDGE,{"disambiguationData":[TD([subQ6])],"derivedFrom":makeQuery(id+"FyYUAefgu6xEfva_4.25.F14.boolean.opBoolean","SPLIT",EDGE,{"disambiguationData":[TD([subQ6])],"derivedFrom":makeQuery(id+"FyYUAefgu6xEfva_4.24.F14.boolean.opBoolean","SPLIT",EDGE,{"disambiguationData":[TD([subQ6])],"derivedFrom":makeQuery(id+"FyYUAefgu6xEfva_4.23.F14.boolean.opBoolean","SPLIT",EDGE,{"disambiguationData":[TD([subQ6])],"derivedFrom":makeQuery(id+"FyYUAefgu6xEfva_4.22.F14.boolean.opBoolean","SPLIT",EDGE,{"disambiguationData":[TD([subQ6])],"derivedFrom":makeQuery(id+"FyYUAefgu6xEfva_4.21.F14.boolean.opBoolean","SPLIT",EDGE,{"disambiguationData":[TD([subQ6])],"derivedFrom":makeQuery(id+"FyYUAefgu6xEfva_4.20.F14.boolean.opBoolean","SPLIT",EDGE,{"disambiguationData":[TD([subQ6])],"derivedFrom":makeQuery(id+"FyYUAefgu6xEfva_4.19.F14.boolean.opBoolean","SPLIT",EDGE,{"disambiguationData":[TD([subQ6])],"derivedFrom":makeQuery(id+"FyYUAefgu6xEfva_4.18.F14.boolean.opBoolean","SPLIT",EDGE,{"disambiguationData":[TD([subQ6])],"derivedFrom":makeQuery(id+"FyYUAefgu6xEfva_4.17.F14.boolean.opBoolean","SPLIT",EDGE,{"disambiguationData":[TD([subQ6])],"derivedFrom":makeQuery(id+"FyYUAefgu6xEfva_4.16.F14.boolean.opBoolean","SPLIT",EDGE,{"disambiguationData":[TD([subQ6])],"derivedFrom":makeQuery(id+"FyYUAefgu6xEfva_4.15.F14.boolean.opBoolean","SPLIT",EDGE,{"disambiguationData":[TD([subQ6])],"derivedFrom":makeQuery(id+"FyYUAefgu6xEfva_4.14.F14.boolean.opBoolean","SPLIT",EDGE,{"disambiguationData":[TD([subQ6])],"derivedFrom":makeQuery(id+"FyYUAefgu6xEfva_4.13.F14.boolean.opBoolean","SPLIT",EDGE,{"disambiguationData":[TD([subQ6])],"derivedFrom":makeQuery(id+"FyYUAefgu6xEfva_4.12.F14.boolean.opBoolean","SPLIT",EDGE,{"disambiguationData":[TD([subQ6])],"derivedFrom":makeQuery(id+"FyYUAefgu6xEfva_4.11.F14.boolean.opBoolean","SPLIT",EDGE,{"disambiguationData":[TD([subQ6])],"derivedFrom":makeQuery(id+"FyYUAefgu6xEfva_4.10.F14.boolean.opBoolean","SPLIT",EDGE,{"disambiguationData":[TD([subQ6])],"derivedFrom":makeQuery(id+"FyYUAefgu6xEfva_4.9.F14.boolean.opBoolean","SPLIT",EDGE,{"disambiguationData":[TD([subQ6])],"derivedFrom":makeQuery(id+"FyYUAefgu6xEfva_4.8.F14.boolean.opBoolean","SPLIT",EDGE,{"disambiguationData":[TD([subQ6])],"derivedFrom":makeQuery(id+"FyYUAefgu6xEfva_4.7.F14.boolean.opBoolean","SPLIT",EDGE,{"disambiguationData":[TD([subQ6])],"derivedFrom":makeQuery(id+"FyYUAefgu6xEfva_4.6.F14.boolean.opBoolean","SPLIT",EDGE,{"disambiguationData":[TD([subQ6])],"derivedFrom":makeQuery(id+"FyYUAefgu6xEfva_4.5.F14.boolean.opBoolean","SPLIT",EDGE,{"disambiguationData":[TD([subQ6])],"derivedFrom":makeQuery(id+"FyYUAefgu6xEfva_4.4.F14.boolean.opBoolean","SPLIT",EDGE,{"disambiguationData":[TD([subQ6])],"derivedFrom":makeQuery(id+"FyYUAefgu6xEfva_4.3.F14.boolean.opBoolean","SPLIT",EDGE,{"disambiguationData":[TD([subQ6])],"derivedFrom":makeQuery(id+"FyYUAefgu6xEfva_4.2.F14.boolean.opBoolean","SPLIT",EDGE,{"disambiguationData":[TD([subQ6])],"derivedFrom":makeQuery(id+"FyYUAefgu6xEfva_4.1.F14.boolean.opBoolean","SPLIT",EDGE,{"disambiguationData":[TD([subQ6])],"derivedFrom":makeQuery(id+"F10.boolean.opBoolean","COPY",EDGE,{"derivedFrom":makeQuery(id+"F10.opExtrude","CAP_EDGE",EDGE,{"disambiguationData":[OSD([subQ0])],"isStart":false})})})})})})})})})})})})})})})})})})})})})})})})})})})})})})})})})})})})})})})})})})})})})})})})});}
            var Q292;
            {var subQ0=sQuery(id+"F13.wireOp",EDGE,"E148.MirrorCS");var subQ1=sQuery(id+"F13.wireOp",EDGE,"E147");var subQ2=sQuery(id+"F11.wireOp",EDGE,"E143");var subQ10=makeQuery(id+"FyYUAefgu6xEfva_4.46.F14.opExtrude","SWEPT_FACE",FACE,{"disambiguationData":[OSD([subQ0])]});var subQ54=makeQuery(id+"F14.opExtrude","SWEPT_FACE",FACE,{"disambiguationData":[OSD([subQ1])]});Q292=makeQuery(id+"FyYUAefgu6xEfva_4.47.F14.boolean.opBoolean","SPLIT",EDGE,{"disambiguationData":[TD([subQ10])],"derivedFrom":makeQuery(id+"FyYUAefgu6xEfva_4.46.F14.boolean.opBoolean","SPLIT",EDGE,{"disambiguationData":[TD([subQ54])],"derivedFrom":makeQuery(id+"FyYUAefgu6xEfva_4.45.F14.boolean.opBoolean","SPLIT",EDGE,{"disambiguationData":[TD([subQ54])],"derivedFrom":makeQuery(id+"FyYUAefgu6xEfva_4.44.F14.boolean.opBoolean","SPLIT",EDGE,{"disambiguationData":[TD([subQ54])],"derivedFrom":makeQuery(id+"FyYUAefgu6xEfva_4.43.F14.boolean.opBoolean","SPLIT",EDGE,{"disambiguationData":[TD([subQ54])],"derivedFrom":makeQuery(id+"FyYUAefgu6xEfva_4.42.F14.boolean.opBoolean","SPLIT",EDGE,{"disambiguationData":[TD([subQ54])],"derivedFrom":makeQuery(id+"FyYUAefgu6xEfva_4.41.F14.boolean.opBoolean","SPLIT",EDGE,{"disambiguationData":[TD([subQ54])],"derivedFrom":makeQuery(id+"FyYUAefgu6xEfva_4.40.F14.boolean.opBoolean","SPLIT",EDGE,{"disambiguationData":[TD([subQ54])],"derivedFrom":makeQuery(id+"FyYUAefgu6xEfva_4.39.F14.boolean.opBoolean","SPLIT",EDGE,{"disambiguationData":[TD([subQ54])],"derivedFrom":makeQuery(id+"FyYUAefgu6xEfva_4.38.F14.boolean.opBoolean","SPLIT",EDGE,{"disambiguationData":[TD([subQ54])],"derivedFrom":makeQuery(id+"FyYUAefgu6xEfva_4.37.F14.boolean.opBoolean","SPLIT",EDGE,{"disambiguationData":[TD([subQ54])],"derivedFrom":makeQuery(id+"FyYUAefgu6xEfva_4.36.F14.boolean.opBoolean","SPLIT",EDGE,{"disambiguationData":[TD([subQ54])],"derivedFrom":makeQuery(id+"FyYUAefgu6xEfva_4.35.F14.boolean.opBoolean","SPLIT",EDGE,{"disambiguationData":[TD([subQ54])],"derivedFrom":makeQuery(id+"FyYUAefgu6xEfva_4.34.F14.boolean.opBoolean","SPLIT",EDGE,{"disambiguationData":[TD([subQ54])],"derivedFrom":makeQuery(id+"FyYUAefgu6xEfva_4.33.F14.boolean.opBoolean","SPLIT",EDGE,{"disambiguationData":[TD([subQ54])],"derivedFrom":makeQuery(id+"FyYUAefgu6xEfva_4.32.F14.boolean.opBoolean","SPLIT",EDGE,{"disambiguationData":[TD([subQ54])],"derivedFrom":makeQuery(id+"FyYUAefgu6xEfva_4.31.F14.boolean.opBoolean","SPLIT",EDGE,{"disambiguationData":[TD([subQ54])],"derivedFrom":makeQuery(id+"FyYUAefgu6xEfva_4.30.F14.boolean.opBoolean","SPLIT",EDGE,{"disambiguationData":[TD([subQ54])],"derivedFrom":makeQuery(id+"FyYUAefgu6xEfva_4.29.F14.boolean.opBoolean","SPLIT",EDGE,{"disambiguationData":[TD([subQ54])],"derivedFrom":makeQuery(id+"FyYUAefgu6xEfva_4.28.F14.boolean.opBoolean","SPLIT",EDGE,{"disambiguationData":[TD([subQ54])],"derivedFrom":makeQuery(id+"FyYUAefgu6xEfva_4.27.F14.boolean.opBoolean","SPLIT",EDGE,{"disambiguationData":[TD([subQ54])],"derivedFrom":makeQuery(id+"FyYUAefgu6xEfva_4.26.F14.boolean.opBoolean","SPLIT",EDGE,{"disambiguationData":[TD([subQ54])],"derivedFrom":makeQuery(id+"FyYUAefgu6xEfva_4.25.F14.boolean.opBoolean","SPLIT",EDGE,{"disambiguationData":[TD([subQ54])],"derivedFrom":makeQuery(id+"FyYUAefgu6xEfva_4.24.F14.boolean.opBoolean","SPLIT",EDGE,{"disambiguationData":[TD([subQ54])],"derivedFrom":makeQuery(id+"FyYUAefgu6xEfva_4.23.F14.boolean.opBoolean","SPLIT",EDGE,{"disambiguationData":[TD([subQ54])],"derivedFrom":makeQuery(id+"FyYUAefgu6xEfva_4.22.F14.boolean.opBoolean","SPLIT",EDGE,{"disambiguationData":[TD([subQ54])],"derivedFrom":makeQuery(id+"FyYUAefgu6xEfva_4.21.F14.boolean.opBoolean","SPLIT",EDGE,{"disambiguationData":[TD([subQ54])],"derivedFrom":makeQuery(id+"FyYUAefgu6xEfva_4.20.F14.boolean.opBoolean","SPLIT",EDGE,{"disambiguationData":[TD([subQ54])],"derivedFrom":makeQuery(id+"FyYUAefgu6xEfva_4.19.F14.boolean.opBoolean","SPLIT",EDGE,{"disambiguationData":[TD([subQ54])],"derivedFrom":makeQuery(id+"FyYUAefgu6xEfva_4.18.F14.boolean.opBoolean","SPLIT",EDGE,{"disambiguationData":[TD([subQ54])],"derivedFrom":makeQuery(id+"FyYUAefgu6xEfva_4.17.F14.boolean.opBoolean","SPLIT",EDGE,{"disambiguationData":[TD([subQ54])],"derivedFrom":makeQuery(id+"FyYUAefgu6xEfva_4.16.F14.boolean.opBoolean","SPLIT",EDGE,{"disambiguationData":[TD([subQ54])],"derivedFrom":makeQuery(id+"FyYUAefgu6xEfva_4.15.F14.boolean.opBoolean","SPLIT",EDGE,{"disambiguationData":[TD([subQ54])],"derivedFrom":makeQuery(id+"FyYUAefgu6xEfva_4.14.F14.boolean.opBoolean","SPLIT",EDGE,{"disambiguationData":[TD([subQ54])],"derivedFrom":makeQuery(id+"FyYUAefgu6xEfva_4.13.F14.boolean.opBoolean","SPLIT",EDGE,{"disambiguationData":[TD([subQ54])],"derivedFrom":makeQuery(id+"FyYUAefgu6xEfva_4.12.F14.boolean.opBoolean","SPLIT",EDGE,{"disambiguationData":[TD([subQ54])],"derivedFrom":makeQuery(id+"FyYUAefgu6xEfva_4.11.F14.boolean.opBoolean","SPLIT",EDGE,{"disambiguationData":[TD([subQ54])],"derivedFrom":makeQuery(id+"FyYUAefgu6xEfva_4.10.F14.boolean.opBoolean","SPLIT",EDGE,{"disambiguationData":[TD([subQ54])],"derivedFrom":makeQuery(id+"FyYUAefgu6xEfva_4.9.F14.boolean.opBoolean","SPLIT",EDGE,{"disambiguationData":[TD([subQ54])],"derivedFrom":makeQuery(id+"FyYUAefgu6xEfva_4.8.F14.boolean.opBoolean","SPLIT",EDGE,{"disambiguationData":[TD([subQ54])],"derivedFrom":makeQuery(id+"FyYUAefgu6xEfva_4.7.F14.boolean.opBoolean","SPLIT",EDGE,{"disambiguationData":[TD([subQ54])],"derivedFrom":makeQuery(id+"FyYUAefgu6xEfva_4.6.F14.boolean.opBoolean","SPLIT",EDGE,{"disambiguationData":[TD([subQ54])],"derivedFrom":makeQuery(id+"FyYUAefgu6xEfva_4.5.F14.boolean.opBoolean","SPLIT",EDGE,{"disambiguationData":[TD([subQ54])],"derivedFrom":makeQuery(id+"FyYUAefgu6xEfva_4.4.F14.boolean.opBoolean","SPLIT",EDGE,{"disambiguationData":[TD([subQ54])],"derivedFrom":makeQuery(id+"FyYUAefgu6xEfva_4.3.F14.boolean.opBoolean","SPLIT",EDGE,{"disambiguationData":[TD([subQ54])],"derivedFrom":makeQuery(id+"FyYUAefgu6xEfva_4.2.F14.boolean.opBoolean","SPLIT",EDGE,{"disambiguationData":[TD([subQ54])],"derivedFrom":makeQuery(id+"FyYUAefgu6xEfva_4.1.F14.boolean.opBoolean","SPLIT",EDGE,{"disambiguationData":[TD([subQ54])],"derivedFrom":makeQuery(id+"F12.opExtrude","CAP_EDGE",EDGE,{"disambiguationData":[OSD([subQ2])],"isStart":false})})})})})})})})})})})})})})})})})})})})})})})})})})})})})})})})})})})})})})})})})})})})})})})});}
            var Q293;
            Q293=makeQuery(id+"FyYUAefgu6xEfva_4.16.F14.opExtrude","SWEPT_EDGE",EDGE,{"disambiguationData":[OSD([sQuery(id+"F11.wireOp",EDGE,"E143"),sQuery(id+"F13.wireOp",EDGE,"E147")])]});
            var Q294;
            Q294=makeQuery(id+"FyYUAefgu6xEfva_4.16.F14.opExtrude","SWEPT_EDGE",EDGE,{"disambiguationData":[OSD([sQuery(id+"F9.wireOp",EDGE,"E142"),sQuery(id+"F13.wireOp",EDGE,"E148.MirrorCS")])]});
            var Q295;
            Q295=makeQuery(id+"FyYUAefgu6xEfva_4.16.F14.opExtrude","SWEPT_EDGE",EDGE,{"disambiguationData":[OSD([sQuery(id+"F11.wireOp",EDGE,"E143"),sQuery(id+"F13.wireOp",EDGE,"E148.MirrorCS")])]});
            var Q296;
            Q296=makeQuery(id+"FyYUAefgu6xEfva_4.16.F14.opExtrude","CAP_EDGE",EDGE,{"disambiguationData":[OSD([sQuery(id+"F13.wireOp",EDGE,"E148.MirrorCS")])],"isStart":true});
            var Q297;
            Q297=makeQuery(id+"FyYUAefgu6xEfva_4.16.F14.opExtrude","CAP_EDGE",EDGE,{"disambiguationData":[OSD([sQuery(id+"F9.wireOp",EDGE,"E142")])],"isStart":false});
            var Q298;
            {var subQ0=sQuery(id+"F9.wireOp",EDGE,"E142");var subQ2=sQuery(id+"F13.wireOp",EDGE,"E148.MirrorCS");var subQ3=makeQuery(id+"FyYUAefgu6xEfva_4.15.F14.opExtrude","SWEPT_FACE",FACE,{"disambiguationData":[OSD([subQ2])]});var subQ5=sQuery(id+"F13.wireOp",EDGE,"E147");var subQ6=makeQuery(id+"F14.opExtrude","SWEPT_FACE",FACE,{"disambiguationData":[OSD([subQ5])]});Q298=makeQuery(id+"FyYUAefgu6xEfva_4.16.F14.boolean.opBoolean","SPLIT",EDGE,{"disambiguationData":[TD([subQ3])],"derivedFrom":makeQuery(id+"FyYUAefgu6xEfva_4.15.F14.boolean.opBoolean","SPLIT",EDGE,{"disambiguationData":[TD([subQ6])],"derivedFrom":makeQuery(id+"FyYUAefgu6xEfva_4.14.F14.boolean.opBoolean","SPLIT",EDGE,{"disambiguationData":[TD([subQ6])],"derivedFrom":makeQuery(id+"FyYUAefgu6xEfva_4.13.F14.boolean.opBoolean","SPLIT",EDGE,{"disambiguationData":[TD([subQ6])],"derivedFrom":makeQuery(id+"FyYUAefgu6xEfva_4.12.F14.boolean.opBoolean","SPLIT",EDGE,{"disambiguationData":[TD([subQ6])],"derivedFrom":makeQuery(id+"FyYUAefgu6xEfva_4.11.F14.boolean.opBoolean","SPLIT",EDGE,{"disambiguationData":[TD([subQ6])],"derivedFrom":makeQuery(id+"FyYUAefgu6xEfva_4.10.F14.boolean.opBoolean","SPLIT",EDGE,{"disambiguationData":[TD([subQ6])],"derivedFrom":makeQuery(id+"FyYUAefgu6xEfva_4.9.F14.boolean.opBoolean","SPLIT",EDGE,{"disambiguationData":[TD([subQ6])],"derivedFrom":makeQuery(id+"FyYUAefgu6xEfva_4.8.F14.boolean.opBoolean","SPLIT",EDGE,{"disambiguationData":[TD([subQ6])],"derivedFrom":makeQuery(id+"FyYUAefgu6xEfva_4.7.F14.boolean.opBoolean","SPLIT",EDGE,{"disambiguationData":[TD([subQ6])],"derivedFrom":makeQuery(id+"FyYUAefgu6xEfva_4.6.F14.boolean.opBoolean","SPLIT",EDGE,{"disambiguationData":[TD([subQ6])],"derivedFrom":makeQuery(id+"FyYUAefgu6xEfva_4.5.F14.boolean.opBoolean","SPLIT",EDGE,{"disambiguationData":[TD([subQ6])],"derivedFrom":makeQuery(id+"FyYUAefgu6xEfva_4.4.F14.boolean.opBoolean","SPLIT",EDGE,{"disambiguationData":[TD([subQ6])],"derivedFrom":makeQuery(id+"FyYUAefgu6xEfva_4.3.F14.boolean.opBoolean","SPLIT",EDGE,{"disambiguationData":[TD([subQ6])],"derivedFrom":makeQuery(id+"FyYUAefgu6xEfva_4.2.F14.boolean.opBoolean","SPLIT",EDGE,{"disambiguationData":[TD([subQ6])],"derivedFrom":makeQuery(id+"FyYUAefgu6xEfva_4.1.F14.boolean.opBoolean","SPLIT",EDGE,{"disambiguationData":[TD([subQ6])],"derivedFrom":makeQuery(id+"F10.boolean.opBoolean","COPY",EDGE,{"derivedFrom":makeQuery(id+"F10.opExtrude","CAP_EDGE",EDGE,{"disambiguationData":[OSD([subQ0])],"isStart":false})})})})})})})})})})})})})})})})})});}
            var Q299;
            {var subQ0=sQuery(id+"F13.wireOp",EDGE,"E148.MirrorCS");var subQ1=sQuery(id+"F13.wireOp",EDGE,"E147");var subQ2=sQuery(id+"F11.wireOp",EDGE,"E143");var subQ14=makeQuery(id+"FyYUAefgu6xEfva_4.15.F14.opExtrude","SWEPT_FACE",FACE,{"disambiguationData":[OSD([subQ0])]});var subQ23=makeQuery(id+"F14.opExtrude","SWEPT_FACE",FACE,{"disambiguationData":[OSD([subQ1])]});Q299=makeQuery(id+"FyYUAefgu6xEfva_4.16.F14.boolean.opBoolean","SPLIT",EDGE,{"disambiguationData":[TD([subQ14])],"derivedFrom":makeQuery(id+"FyYUAefgu6xEfva_4.15.F14.boolean.opBoolean","SPLIT",EDGE,{"disambiguationData":[TD([subQ23])],"derivedFrom":makeQuery(id+"FyYUAefgu6xEfva_4.14.F14.boolean.opBoolean","SPLIT",EDGE,{"disambiguationData":[TD([subQ23])],"derivedFrom":makeQuery(id+"FyYUAefgu6xEfva_4.13.F14.boolean.opBoolean","SPLIT",EDGE,{"disambiguationData":[TD([subQ23])],"derivedFrom":makeQuery(id+"FyYUAefgu6xEfva_4.12.F14.boolean.opBoolean","SPLIT",EDGE,{"disambiguationData":[TD([subQ23])],"derivedFrom":makeQuery(id+"FyYUAefgu6xEfva_4.11.F14.boolean.opBoolean","SPLIT",EDGE,{"disambiguationData":[TD([subQ23])],"derivedFrom":makeQuery(id+"FyYUAefgu6xEfva_4.10.F14.boolean.opBoolean","SPLIT",EDGE,{"disambiguationData":[TD([subQ23])],"derivedFrom":makeQuery(id+"FyYUAefgu6xEfva_4.9.F14.boolean.opBoolean","SPLIT",EDGE,{"disambiguationData":[TD([subQ23])],"derivedFrom":makeQuery(id+"FyYUAefgu6xEfva_4.8.F14.boolean.opBoolean","SPLIT",EDGE,{"disambiguationData":[TD([subQ23])],"derivedFrom":makeQuery(id+"FyYUAefgu6xEfva_4.7.F14.boolean.opBoolean","SPLIT",EDGE,{"disambiguationData":[TD([subQ23])],"derivedFrom":makeQuery(id+"FyYUAefgu6xEfva_4.6.F14.boolean.opBoolean","SPLIT",EDGE,{"disambiguationData":[TD([subQ23])],"derivedFrom":makeQuery(id+"FyYUAefgu6xEfva_4.5.F14.boolean.opBoolean","SPLIT",EDGE,{"disambiguationData":[TD([subQ23])],"derivedFrom":makeQuery(id+"FyYUAefgu6xEfva_4.4.F14.boolean.opBoolean","SPLIT",EDGE,{"disambiguationData":[TD([subQ23])],"derivedFrom":makeQuery(id+"FyYUAefgu6xEfva_4.3.F14.boolean.opBoolean","SPLIT",EDGE,{"disambiguationData":[TD([subQ23])],"derivedFrom":makeQuery(id+"FyYUAefgu6xEfva_4.2.F14.boolean.opBoolean","SPLIT",EDGE,{"disambiguationData":[TD([subQ23])],"derivedFrom":makeQuery(id+"FyYUAefgu6xEfva_4.1.F14.boolean.opBoolean","SPLIT",EDGE,{"disambiguationData":[TD([subQ23])],"derivedFrom":makeQuery(id+"F12.opExtrude","CAP_EDGE",EDGE,{"disambiguationData":[OSD([subQ2])],"isStart":false})})})})})})})})})})})})})})})})});}
            var Q300;
            Q300=makeQuery(id+"FyYUAefgu6xEfva_4.48.F14.opExtrude","SWEPT_EDGE",EDGE,{"disambiguationData":[OSD([sQuery(id+"F9.wireOp",EDGE,"E142"),sQuery(id+"F13.wireOp",EDGE,"E147")])]});
            var Q301;
            Q301=makeQuery(id+"FyYUAefgu6xEfva_4.48.F14.opExtrude","SWEPT_EDGE",EDGE,{"disambiguationData":[OSD([sQuery(id+"F11.wireOp",EDGE,"E143"),sQuery(id+"F13.wireOp",EDGE,"E147")])]});
            var Q302;
            Q302=makeQuery(id+"FyYUAefgu6xEfva_4.48.F14.opExtrude","SWEPT_EDGE",EDGE,{"disambiguationData":[OSD([sQuery(id+"F9.wireOp",EDGE,"E142"),sQuery(id+"F13.wireOp",EDGE,"E148.MirrorCS")])]});
            var Q303;
            Q303=makeQuery(id+"FyYUAefgu6xEfva_4.48.F14.opExtrude","SWEPT_EDGE",EDGE,{"disambiguationData":[OSD([sQuery(id+"F11.wireOp",EDGE,"E143"),sQuery(id+"F13.wireOp",EDGE,"E148.MirrorCS")])]});
            var Q304;
            Q304=makeQuery(id+"FyYUAefgu6xEfva_4.48.F14.opExtrude","CAP_EDGE",EDGE,{"disambiguationData":[OSD([sQuery(id+"F13.wireOp",EDGE,"E147")])],"isStart":true});
            var Q305;
            Q305=makeQuery(id+"FyYUAefgu6xEfva_4.48.F14.opExtrude","CAP_EDGE",EDGE,{"disambiguationData":[OSD([sQuery(id+"F13.wireOp",EDGE,"E148.MirrorCS")])],"isStart":true});
            var Q306;
            Q306=makeQuery(id+"FyYUAefgu6xEfva_4.48.F14.opExtrude","CAP_EDGE",EDGE,{"disambiguationData":[OSD([sQuery(id+"F9.wireOp",EDGE,"E142")])],"isStart":false});
            var Q307;
            {var subQ0=sQuery(id+"F9.wireOp",EDGE,"E142");var subQ3=sQuery(id+"F13.wireOp",EDGE,"E148.MirrorCS");var subQ4=makeQuery(id+"FyYUAefgu6xEfva_4.47.F14.opExtrude","SWEPT_FACE",FACE,{"disambiguationData":[OSD([subQ3])]});var subQ5=sQuery(id+"F13.wireOp",EDGE,"E147");var subQ6=makeQuery(id+"F14.opExtrude","SWEPT_FACE",FACE,{"disambiguationData":[OSD([subQ5])]});Q307=makeQuery(id+"FyYUAefgu6xEfva_4.48.F14.boolean.opBoolean","SPLIT",EDGE,{"disambiguationData":[TD([subQ4])],"derivedFrom":makeQuery(id+"FyYUAefgu6xEfva_4.47.F14.boolean.opBoolean","SPLIT",EDGE,{"disambiguationData":[TD([subQ6])],"derivedFrom":makeQuery(id+"FyYUAefgu6xEfva_4.46.F14.boolean.opBoolean","SPLIT",EDGE,{"disambiguationData":[TD([subQ6])],"derivedFrom":makeQuery(id+"FyYUAefgu6xEfva_4.45.F14.boolean.opBoolean","SPLIT",EDGE,{"disambiguationData":[TD([subQ6])],"derivedFrom":makeQuery(id+"FyYUAefgu6xEfva_4.44.F14.boolean.opBoolean","SPLIT",EDGE,{"disambiguationData":[TD([subQ6])],"derivedFrom":makeQuery(id+"FyYUAefgu6xEfva_4.43.F14.boolean.opBoolean","SPLIT",EDGE,{"disambiguationData":[TD([subQ6])],"derivedFrom":makeQuery(id+"FyYUAefgu6xEfva_4.42.F14.boolean.opBoolean","SPLIT",EDGE,{"disambiguationData":[TD([subQ6])],"derivedFrom":makeQuery(id+"FyYUAefgu6xEfva_4.41.F14.boolean.opBoolean","SPLIT",EDGE,{"disambiguationData":[TD([subQ6])],"derivedFrom":makeQuery(id+"FyYUAefgu6xEfva_4.40.F14.boolean.opBoolean","SPLIT",EDGE,{"disambiguationData":[TD([subQ6])],"derivedFrom":makeQuery(id+"FyYUAefgu6xEfva_4.39.F14.boolean.opBoolean","SPLIT",EDGE,{"disambiguationData":[TD([subQ6])],"derivedFrom":makeQuery(id+"FyYUAefgu6xEfva_4.38.F14.boolean.opBoolean","SPLIT",EDGE,{"disambiguationData":[TD([subQ6])],"derivedFrom":makeQuery(id+"FyYUAefgu6xEfva_4.37.F14.boolean.opBoolean","SPLIT",EDGE,{"disambiguationData":[TD([subQ6])],"derivedFrom":makeQuery(id+"FyYUAefgu6xEfva_4.36.F14.boolean.opBoolean","SPLIT",EDGE,{"disambiguationData":[TD([subQ6])],"derivedFrom":makeQuery(id+"FyYUAefgu6xEfva_4.35.F14.boolean.opBoolean","SPLIT",EDGE,{"disambiguationData":[TD([subQ6])],"derivedFrom":makeQuery(id+"FyYUAefgu6xEfva_4.34.F14.boolean.opBoolean","SPLIT",EDGE,{"disambiguationData":[TD([subQ6])],"derivedFrom":makeQuery(id+"FyYUAefgu6xEfva_4.33.F14.boolean.opBoolean","SPLIT",EDGE,{"disambiguationData":[TD([subQ6])],"derivedFrom":makeQuery(id+"FyYUAefgu6xEfva_4.32.F14.boolean.opBoolean","SPLIT",EDGE,{"disambiguationData":[TD([subQ6])],"derivedFrom":makeQuery(id+"FyYUAefgu6xEfva_4.31.F14.boolean.opBoolean","SPLIT",EDGE,{"disambiguationData":[TD([subQ6])],"derivedFrom":makeQuery(id+"FyYUAefgu6xEfva_4.30.F14.boolean.opBoolean","SPLIT",EDGE,{"disambiguationData":[TD([subQ6])],"derivedFrom":makeQuery(id+"FyYUAefgu6xEfva_4.29.F14.boolean.opBoolean","SPLIT",EDGE,{"disambiguationData":[TD([subQ6])],"derivedFrom":makeQuery(id+"FyYUAefgu6xEfva_4.28.F14.boolean.opBoolean","SPLIT",EDGE,{"disambiguationData":[TD([subQ6])],"derivedFrom":makeQuery(id+"FyYUAefgu6xEfva_4.27.F14.boolean.opBoolean","SPLIT",EDGE,{"disambiguationData":[TD([subQ6])],"derivedFrom":makeQuery(id+"FyYUAefgu6xEfva_4.26.F14.boolean.opBoolean","SPLIT",EDGE,{"disambiguationData":[TD([subQ6])],"derivedFrom":makeQuery(id+"FyYUAefgu6xEfva_4.25.F14.boolean.opBoolean","SPLIT",EDGE,{"disambiguationData":[TD([subQ6])],"derivedFrom":makeQuery(id+"FyYUAefgu6xEfva_4.24.F14.boolean.opBoolean","SPLIT",EDGE,{"disambiguationData":[TD([subQ6])],"derivedFrom":makeQuery(id+"FyYUAefgu6xEfva_4.23.F14.boolean.opBoolean","SPLIT",EDGE,{"disambiguationData":[TD([subQ6])],"derivedFrom":makeQuery(id+"FyYUAefgu6xEfva_4.22.F14.boolean.opBoolean","SPLIT",EDGE,{"disambiguationData":[TD([subQ6])],"derivedFrom":makeQuery(id+"FyYUAefgu6xEfva_4.21.F14.boolean.opBoolean","SPLIT",EDGE,{"disambiguationData":[TD([subQ6])],"derivedFrom":makeQuery(id+"FyYUAefgu6xEfva_4.20.F14.boolean.opBoolean","SPLIT",EDGE,{"disambiguationData":[TD([subQ6])],"derivedFrom":makeQuery(id+"FyYUAefgu6xEfva_4.19.F14.boolean.opBoolean","SPLIT",EDGE,{"disambiguationData":[TD([subQ6])],"derivedFrom":makeQuery(id+"FyYUAefgu6xEfva_4.18.F14.boolean.opBoolean","SPLIT",EDGE,{"disambiguationData":[TD([subQ6])],"derivedFrom":makeQuery(id+"FyYUAefgu6xEfva_4.17.F14.boolean.opBoolean","SPLIT",EDGE,{"disambiguationData":[TD([subQ6])],"derivedFrom":makeQuery(id+"FyYUAefgu6xEfva_4.16.F14.boolean.opBoolean","SPLIT",EDGE,{"disambiguationData":[TD([subQ6])],"derivedFrom":makeQuery(id+"FyYUAefgu6xEfva_4.15.F14.boolean.opBoolean","SPLIT",EDGE,{"disambiguationData":[TD([subQ6])],"derivedFrom":makeQuery(id+"FyYUAefgu6xEfva_4.14.F14.boolean.opBoolean","SPLIT",EDGE,{"disambiguationData":[TD([subQ6])],"derivedFrom":makeQuery(id+"FyYUAefgu6xEfva_4.13.F14.boolean.opBoolean","SPLIT",EDGE,{"disambiguationData":[TD([subQ6])],"derivedFrom":makeQuery(id+"FyYUAefgu6xEfva_4.12.F14.boolean.opBoolean","SPLIT",EDGE,{"disambiguationData":[TD([subQ6])],"derivedFrom":makeQuery(id+"FyYUAefgu6xEfva_4.11.F14.boolean.opBoolean","SPLIT",EDGE,{"disambiguationData":[TD([subQ6])],"derivedFrom":makeQuery(id+"FyYUAefgu6xEfva_4.10.F14.boolean.opBoolean","SPLIT",EDGE,{"disambiguationData":[TD([subQ6])],"derivedFrom":makeQuery(id+"FyYUAefgu6xEfva_4.9.F14.boolean.opBoolean","SPLIT",EDGE,{"disambiguationData":[TD([subQ6])],"derivedFrom":makeQuery(id+"FyYUAefgu6xEfva_4.8.F14.boolean.opBoolean","SPLIT",EDGE,{"disambiguationData":[TD([subQ6])],"derivedFrom":makeQuery(id+"FyYUAefgu6xEfva_4.7.F14.boolean.opBoolean","SPLIT",EDGE,{"disambiguationData":[TD([subQ6])],"derivedFrom":makeQuery(id+"FyYUAefgu6xEfva_4.6.F14.boolean.opBoolean","SPLIT",EDGE,{"disambiguationData":[TD([subQ6])],"derivedFrom":makeQuery(id+"FyYUAefgu6xEfva_4.5.F14.boolean.opBoolean","SPLIT",EDGE,{"disambiguationData":[TD([subQ6])],"derivedFrom":makeQuery(id+"FyYUAefgu6xEfva_4.4.F14.boolean.opBoolean","SPLIT",EDGE,{"disambiguationData":[TD([subQ6])],"derivedFrom":makeQuery(id+"FyYUAefgu6xEfva_4.3.F14.boolean.opBoolean","SPLIT",EDGE,{"disambiguationData":[TD([subQ6])],"derivedFrom":makeQuery(id+"FyYUAefgu6xEfva_4.2.F14.boolean.opBoolean","SPLIT",EDGE,{"disambiguationData":[TD([subQ6])],"derivedFrom":makeQuery(id+"FyYUAefgu6xEfva_4.1.F14.boolean.opBoolean","SPLIT",EDGE,{"disambiguationData":[TD([subQ6])],"derivedFrom":makeQuery(id+"F10.boolean.opBoolean","COPY",EDGE,{"derivedFrom":makeQuery(id+"F10.opExtrude","CAP_EDGE",EDGE,{"disambiguationData":[OSD([subQ0])],"isStart":false})})})})})})})})})})})})})})})})})})})})})})})})})})})})})})})})})})})})})})})})})})})})})})})})})});}
            var Q308;
            {var subQ0=sQuery(id+"F13.wireOp",EDGE,"E148.MirrorCS");var subQ1=sQuery(id+"F13.wireOp",EDGE,"E147");var subQ2=sQuery(id+"F11.wireOp",EDGE,"E143");var subQ9=makeQuery(id+"FyYUAefgu6xEfva_4.47.F14.opExtrude","SWEPT_FACE",FACE,{"disambiguationData":[OSD([subQ0])]});var subQ55=makeQuery(id+"F14.opExtrude","SWEPT_FACE",FACE,{"disambiguationData":[OSD([subQ1])]});Q308=makeQuery(id+"FyYUAefgu6xEfva_4.48.F14.boolean.opBoolean","SPLIT",EDGE,{"disambiguationData":[TD([subQ9])],"derivedFrom":makeQuery(id+"FyYUAefgu6xEfva_4.47.F14.boolean.opBoolean","SPLIT",EDGE,{"disambiguationData":[TD([subQ55])],"derivedFrom":makeQuery(id+"FyYUAefgu6xEfva_4.46.F14.boolean.opBoolean","SPLIT",EDGE,{"disambiguationData":[TD([subQ55])],"derivedFrom":makeQuery(id+"FyYUAefgu6xEfva_4.45.F14.boolean.opBoolean","SPLIT",EDGE,{"disambiguationData":[TD([subQ55])],"derivedFrom":makeQuery(id+"FyYUAefgu6xEfva_4.44.F14.boolean.opBoolean","SPLIT",EDGE,{"disambiguationData":[TD([subQ55])],"derivedFrom":makeQuery(id+"FyYUAefgu6xEfva_4.43.F14.boolean.opBoolean","SPLIT",EDGE,{"disambiguationData":[TD([subQ55])],"derivedFrom":makeQuery(id+"FyYUAefgu6xEfva_4.42.F14.boolean.opBoolean","SPLIT",EDGE,{"disambiguationData":[TD([subQ55])],"derivedFrom":makeQuery(id+"FyYUAefgu6xEfva_4.41.F14.boolean.opBoolean","SPLIT",EDGE,{"disambiguationData":[TD([subQ55])],"derivedFrom":makeQuery(id+"FyYUAefgu6xEfva_4.40.F14.boolean.opBoolean","SPLIT",EDGE,{"disambiguationData":[TD([subQ55])],"derivedFrom":makeQuery(id+"FyYUAefgu6xEfva_4.39.F14.boolean.opBoolean","SPLIT",EDGE,{"disambiguationData":[TD([subQ55])],"derivedFrom":makeQuery(id+"FyYUAefgu6xEfva_4.38.F14.boolean.opBoolean","SPLIT",EDGE,{"disambiguationData":[TD([subQ55])],"derivedFrom":makeQuery(id+"FyYUAefgu6xEfva_4.37.F14.boolean.opBoolean","SPLIT",EDGE,{"disambiguationData":[TD([subQ55])],"derivedFrom":makeQuery(id+"FyYUAefgu6xEfva_4.36.F14.boolean.opBoolean","SPLIT",EDGE,{"disambiguationData":[TD([subQ55])],"derivedFrom":makeQuery(id+"FyYUAefgu6xEfva_4.35.F14.boolean.opBoolean","SPLIT",EDGE,{"disambiguationData":[TD([subQ55])],"derivedFrom":makeQuery(id+"FyYUAefgu6xEfva_4.34.F14.boolean.opBoolean","SPLIT",EDGE,{"disambiguationData":[TD([subQ55])],"derivedFrom":makeQuery(id+"FyYUAefgu6xEfva_4.33.F14.boolean.opBoolean","SPLIT",EDGE,{"disambiguationData":[TD([subQ55])],"derivedFrom":makeQuery(id+"FyYUAefgu6xEfva_4.32.F14.boolean.opBoolean","SPLIT",EDGE,{"disambiguationData":[TD([subQ55])],"derivedFrom":makeQuery(id+"FyYUAefgu6xEfva_4.31.F14.boolean.opBoolean","SPLIT",EDGE,{"disambiguationData":[TD([subQ55])],"derivedFrom":makeQuery(id+"FyYUAefgu6xEfva_4.30.F14.boolean.opBoolean","SPLIT",EDGE,{"disambiguationData":[TD([subQ55])],"derivedFrom":makeQuery(id+"FyYUAefgu6xEfva_4.29.F14.boolean.opBoolean","SPLIT",EDGE,{"disambiguationData":[TD([subQ55])],"derivedFrom":makeQuery(id+"FyYUAefgu6xEfva_4.28.F14.boolean.opBoolean","SPLIT",EDGE,{"disambiguationData":[TD([subQ55])],"derivedFrom":makeQuery(id+"FyYUAefgu6xEfva_4.27.F14.boolean.opBoolean","SPLIT",EDGE,{"disambiguationData":[TD([subQ55])],"derivedFrom":makeQuery(id+"FyYUAefgu6xEfva_4.26.F14.boolean.opBoolean","SPLIT",EDGE,{"disambiguationData":[TD([subQ55])],"derivedFrom":makeQuery(id+"FyYUAefgu6xEfva_4.25.F14.boolean.opBoolean","SPLIT",EDGE,{"disambiguationData":[TD([subQ55])],"derivedFrom":makeQuery(id+"FyYUAefgu6xEfva_4.24.F14.boolean.opBoolean","SPLIT",EDGE,{"disambiguationData":[TD([subQ55])],"derivedFrom":makeQuery(id+"FyYUAefgu6xEfva_4.23.F14.boolean.opBoolean","SPLIT",EDGE,{"disambiguationData":[TD([subQ55])],"derivedFrom":makeQuery(id+"FyYUAefgu6xEfva_4.22.F14.boolean.opBoolean","SPLIT",EDGE,{"disambiguationData":[TD([subQ55])],"derivedFrom":makeQuery(id+"FyYUAefgu6xEfva_4.21.F14.boolean.opBoolean","SPLIT",EDGE,{"disambiguationData":[TD([subQ55])],"derivedFrom":makeQuery(id+"FyYUAefgu6xEfva_4.20.F14.boolean.opBoolean","SPLIT",EDGE,{"disambiguationData":[TD([subQ55])],"derivedFrom":makeQuery(id+"FyYUAefgu6xEfva_4.19.F14.boolean.opBoolean","SPLIT",EDGE,{"disambiguationData":[TD([subQ55])],"derivedFrom":makeQuery(id+"FyYUAefgu6xEfva_4.18.F14.boolean.opBoolean","SPLIT",EDGE,{"disambiguationData":[TD([subQ55])],"derivedFrom":makeQuery(id+"FyYUAefgu6xEfva_4.17.F14.boolean.opBoolean","SPLIT",EDGE,{"disambiguationData":[TD([subQ55])],"derivedFrom":makeQuery(id+"FyYUAefgu6xEfva_4.16.F14.boolean.opBoolean","SPLIT",EDGE,{"disambiguationData":[TD([subQ55])],"derivedFrom":makeQuery(id+"FyYUAefgu6xEfva_4.15.F14.boolean.opBoolean","SPLIT",EDGE,{"disambiguationData":[TD([subQ55])],"derivedFrom":makeQuery(id+"FyYUAefgu6xEfva_4.14.F14.boolean.opBoolean","SPLIT",EDGE,{"disambiguationData":[TD([subQ55])],"derivedFrom":makeQuery(id+"FyYUAefgu6xEfva_4.13.F14.boolean.opBoolean","SPLIT",EDGE,{"disambiguationData":[TD([subQ55])],"derivedFrom":makeQuery(id+"FyYUAefgu6xEfva_4.12.F14.boolean.opBoolean","SPLIT",EDGE,{"disambiguationData":[TD([subQ55])],"derivedFrom":makeQuery(id+"FyYUAefgu6xEfva_4.11.F14.boolean.opBoolean","SPLIT",EDGE,{"disambiguationData":[TD([subQ55])],"derivedFrom":makeQuery(id+"FyYUAefgu6xEfva_4.10.F14.boolean.opBoolean","SPLIT",EDGE,{"disambiguationData":[TD([subQ55])],"derivedFrom":makeQuery(id+"FyYUAefgu6xEfva_4.9.F14.boolean.opBoolean","SPLIT",EDGE,{"disambiguationData":[TD([subQ55])],"derivedFrom":makeQuery(id+"FyYUAefgu6xEfva_4.8.F14.boolean.opBoolean","SPLIT",EDGE,{"disambiguationData":[TD([subQ55])],"derivedFrom":makeQuery(id+"FyYUAefgu6xEfva_4.7.F14.boolean.opBoolean","SPLIT",EDGE,{"disambiguationData":[TD([subQ55])],"derivedFrom":makeQuery(id+"FyYUAefgu6xEfva_4.6.F14.boolean.opBoolean","SPLIT",EDGE,{"disambiguationData":[TD([subQ55])],"derivedFrom":makeQuery(id+"FyYUAefgu6xEfva_4.5.F14.boolean.opBoolean","SPLIT",EDGE,{"disambiguationData":[TD([subQ55])],"derivedFrom":makeQuery(id+"FyYUAefgu6xEfva_4.4.F14.boolean.opBoolean","SPLIT",EDGE,{"disambiguationData":[TD([subQ55])],"derivedFrom":makeQuery(id+"FyYUAefgu6xEfva_4.3.F14.boolean.opBoolean","SPLIT",EDGE,{"disambiguationData":[TD([subQ55])],"derivedFrom":makeQuery(id+"FyYUAefgu6xEfva_4.2.F14.boolean.opBoolean","SPLIT",EDGE,{"disambiguationData":[TD([subQ55])],"derivedFrom":makeQuery(id+"FyYUAefgu6xEfva_4.1.F14.boolean.opBoolean","SPLIT",EDGE,{"disambiguationData":[TD([subQ55])],"derivedFrom":makeQuery(id+"F12.opExtrude","CAP_EDGE",EDGE,{"disambiguationData":[OSD([subQ2])],"isStart":false})})})})})})})})})})})})})})})})})})})})})})})})})})})})})})})})})})})})})})})})})})})})})})})})});}
            var Q309;
            Q309=makeQuery(id+"FyYUAefgu6xEfva_4.49.F14.opExtrude","CAP_EDGE",EDGE,{"disambiguationData":[OSD([sQuery(id+"F13.wireOp",EDGE,"E147")])],"isStart":false});
            var Q310;
            Q310=makeQuery(id+"FyYUAefgu6xEfva_4.17.F14.opExtrude","SWEPT_EDGE",EDGE,{"disambiguationData":[OSD([sQuery(id+"F9.wireOp",EDGE,"E142"),sQuery(id+"F13.wireOp",EDGE,"E147")])]});
            var Q311;
            Q311=makeQuery(id+"FyYUAefgu6xEfva_4.17.F14.opExtrude","SWEPT_EDGE",EDGE,{"disambiguationData":[OSD([sQuery(id+"F9.wireOp",EDGE,"E142"),sQuery(id+"F13.wireOp",EDGE,"E148.MirrorCS")])]});
            var Q312;
            Q312=makeQuery(id+"FyYUAefgu6xEfva_4.17.F14.opExtrude","SWEPT_EDGE",EDGE,{"disambiguationData":[OSD([sQuery(id+"F11.wireOp",EDGE,"E143"),sQuery(id+"F13.wireOp",EDGE,"E148.MirrorCS")])]});
            var Q313;
            Q313=makeQuery(id+"FyYUAefgu6xEfva_4.17.F14.opExtrude","CAP_EDGE",EDGE,{"disambiguationData":[OSD([sQuery(id+"F13.wireOp",EDGE,"E148.MirrorCS")])],"isStart":true});
            var Q314;
            Q314=makeQuery(id+"FyYUAefgu6xEfva_4.17.F14.opExtrude","CAP_EDGE",EDGE,{"disambiguationData":[OSD([sQuery(id+"F9.wireOp",EDGE,"E142")])],"isStart":false});
            var Q315;
            {var subQ0=sQuery(id+"F13.wireOp",EDGE,"E148.MirrorCS");var subQ1=sQuery(id+"F13.wireOp",EDGE,"E147");var subQ2=sQuery(id+"F11.wireOp",EDGE,"E143");var subQ10=makeQuery(id+"FyYUAefgu6xEfva_4.16.F14.opExtrude","SWEPT_FACE",FACE,{"disambiguationData":[OSD([subQ0])]});var subQ24=makeQuery(id+"F14.opExtrude","SWEPT_FACE",FACE,{"disambiguationData":[OSD([subQ1])]});Q315=makeQuery(id+"FyYUAefgu6xEfva_4.17.F14.boolean.opBoolean","SPLIT",EDGE,{"disambiguationData":[TD([subQ10])],"derivedFrom":makeQuery(id+"FyYUAefgu6xEfva_4.16.F14.boolean.opBoolean","SPLIT",EDGE,{"disambiguationData":[TD([subQ24])],"derivedFrom":makeQuery(id+"FyYUAefgu6xEfva_4.15.F14.boolean.opBoolean","SPLIT",EDGE,{"disambiguationData":[TD([subQ24])],"derivedFrom":makeQuery(id+"FyYUAefgu6xEfva_4.14.F14.boolean.opBoolean","SPLIT",EDGE,{"disambiguationData":[TD([subQ24])],"derivedFrom":makeQuery(id+"FyYUAefgu6xEfva_4.13.F14.boolean.opBoolean","SPLIT",EDGE,{"disambiguationData":[TD([subQ24])],"derivedFrom":makeQuery(id+"FyYUAefgu6xEfva_4.12.F14.boolean.opBoolean","SPLIT",EDGE,{"disambiguationData":[TD([subQ24])],"derivedFrom":makeQuery(id+"FyYUAefgu6xEfva_4.11.F14.boolean.opBoolean","SPLIT",EDGE,{"disambiguationData":[TD([subQ24])],"derivedFrom":makeQuery(id+"FyYUAefgu6xEfva_4.10.F14.boolean.opBoolean","SPLIT",EDGE,{"disambiguationData":[TD([subQ24])],"derivedFrom":makeQuery(id+"FyYUAefgu6xEfva_4.9.F14.boolean.opBoolean","SPLIT",EDGE,{"disambiguationData":[TD([subQ24])],"derivedFrom":makeQuery(id+"FyYUAefgu6xEfva_4.8.F14.boolean.opBoolean","SPLIT",EDGE,{"disambiguationData":[TD([subQ24])],"derivedFrom":makeQuery(id+"FyYUAefgu6xEfva_4.7.F14.boolean.opBoolean","SPLIT",EDGE,{"disambiguationData":[TD([subQ24])],"derivedFrom":makeQuery(id+"FyYUAefgu6xEfva_4.6.F14.boolean.opBoolean","SPLIT",EDGE,{"disambiguationData":[TD([subQ24])],"derivedFrom":makeQuery(id+"FyYUAefgu6xEfva_4.5.F14.boolean.opBoolean","SPLIT",EDGE,{"disambiguationData":[TD([subQ24])],"derivedFrom":makeQuery(id+"FyYUAefgu6xEfva_4.4.F14.boolean.opBoolean","SPLIT",EDGE,{"disambiguationData":[TD([subQ24])],"derivedFrom":makeQuery(id+"FyYUAefgu6xEfva_4.3.F14.boolean.opBoolean","SPLIT",EDGE,{"disambiguationData":[TD([subQ24])],"derivedFrom":makeQuery(id+"FyYUAefgu6xEfva_4.2.F14.boolean.opBoolean","SPLIT",EDGE,{"disambiguationData":[TD([subQ24])],"derivedFrom":makeQuery(id+"FyYUAefgu6xEfva_4.1.F14.boolean.opBoolean","SPLIT",EDGE,{"disambiguationData":[TD([subQ24])],"derivedFrom":makeQuery(id+"F12.opExtrude","CAP_EDGE",EDGE,{"disambiguationData":[OSD([subQ2])],"isStart":false})})})})})})})})})})})})})})})})})});}
            var Q316;
            Q316=makeQuery(id+"FyYUAefgu6xEfva_4.49.F14.opExtrude","SWEPT_EDGE",EDGE,{"disambiguationData":[OSD([sQuery(id+"F9.wireOp",EDGE,"E142"),sQuery(id+"F13.wireOp",EDGE,"E147")])]});
            var Q317;
            Q317=makeQuery(id+"FyYUAefgu6xEfva_4.49.F14.opExtrude","SWEPT_EDGE",EDGE,{"disambiguationData":[OSD([sQuery(id+"F11.wireOp",EDGE,"E143"),sQuery(id+"F13.wireOp",EDGE,"E147")])]});
            var Q318;
            Q318=makeQuery(id+"FyYUAefgu6xEfva_4.49.F14.opExtrude","SWEPT_EDGE",EDGE,{"disambiguationData":[OSD([sQuery(id+"F9.wireOp",EDGE,"E142"),sQuery(id+"F13.wireOp",EDGE,"E148.MirrorCS")])]});
            var Q319;
            Q319=makeQuery(id+"FyYUAefgu6xEfva_4.49.F14.opExtrude","SWEPT_EDGE",EDGE,{"disambiguationData":[OSD([sQuery(id+"F11.wireOp",EDGE,"E143"),sQuery(id+"F13.wireOp",EDGE,"E148.MirrorCS")])]});
            var Q320;
            Q320=makeQuery(id+"FyYUAefgu6xEfva_4.49.F14.opExtrude","CAP_EDGE",EDGE,{"disambiguationData":[OSD([sQuery(id+"F13.wireOp",EDGE,"E147")])],"isStart":true});
            var Q321;
            Q321=makeQuery(id+"FyYUAefgu6xEfva_4.49.F14.opExtrude","CAP_EDGE",EDGE,{"disambiguationData":[OSD([sQuery(id+"F13.wireOp",EDGE,"E148.MirrorCS")])],"isStart":true});
            var Q322;
            {var subQ0=sQuery(id+"F9.wireOp",EDGE,"E142");var subQ3=makeQuery(id+"F14.opExtrude","SWEPT_FACE",FACE,{"disambiguationData":[OSD([sQuery(id+"F13.wireOp",EDGE,"E147")])]});Q322=makeQuery(id+"FyYUAefgu6xEfva_4.49.F14.boolean.opBoolean","SPLIT",EDGE,{"disambiguationData":[TD([subQ3])],"derivedFrom":makeQuery(id+"FyYUAefgu6xEfva_4.48.F14.boolean.opBoolean","SPLIT",EDGE,{"disambiguationData":[TD([subQ3])],"derivedFrom":makeQuery(id+"FyYUAefgu6xEfva_4.47.F14.boolean.opBoolean","SPLIT",EDGE,{"disambiguationData":[TD([subQ3])],"derivedFrom":makeQuery(id+"FyYUAefgu6xEfva_4.46.F14.boolean.opBoolean","SPLIT",EDGE,{"disambiguationData":[TD([subQ3])],"derivedFrom":makeQuery(id+"FyYUAefgu6xEfva_4.45.F14.boolean.opBoolean","SPLIT",EDGE,{"disambiguationData":[TD([subQ3])],"derivedFrom":makeQuery(id+"FyYUAefgu6xEfva_4.44.F14.boolean.opBoolean","SPLIT",EDGE,{"disambiguationData":[TD([subQ3])],"derivedFrom":makeQuery(id+"FyYUAefgu6xEfva_4.43.F14.boolean.opBoolean","SPLIT",EDGE,{"disambiguationData":[TD([subQ3])],"derivedFrom":makeQuery(id+"FyYUAefgu6xEfva_4.42.F14.boolean.opBoolean","SPLIT",EDGE,{"disambiguationData":[TD([subQ3])],"derivedFrom":makeQuery(id+"FyYUAefgu6xEfva_4.41.F14.boolean.opBoolean","SPLIT",EDGE,{"disambiguationData":[TD([subQ3])],"derivedFrom":makeQuery(id+"FyYUAefgu6xEfva_4.40.F14.boolean.opBoolean","SPLIT",EDGE,{"disambiguationData":[TD([subQ3])],"derivedFrom":makeQuery(id+"FyYUAefgu6xEfva_4.39.F14.boolean.opBoolean","SPLIT",EDGE,{"disambiguationData":[TD([subQ3])],"derivedFrom":makeQuery(id+"FyYUAefgu6xEfva_4.38.F14.boolean.opBoolean","SPLIT",EDGE,{"disambiguationData":[TD([subQ3])],"derivedFrom":makeQuery(id+"FyYUAefgu6xEfva_4.37.F14.boolean.opBoolean","SPLIT",EDGE,{"disambiguationData":[TD([subQ3])],"derivedFrom":makeQuery(id+"FyYUAefgu6xEfva_4.36.F14.boolean.opBoolean","SPLIT",EDGE,{"disambiguationData":[TD([subQ3])],"derivedFrom":makeQuery(id+"FyYUAefgu6xEfva_4.35.F14.boolean.opBoolean","SPLIT",EDGE,{"disambiguationData":[TD([subQ3])],"derivedFrom":makeQuery(id+"FyYUAefgu6xEfva_4.34.F14.boolean.opBoolean","SPLIT",EDGE,{"disambiguationData":[TD([subQ3])],"derivedFrom":makeQuery(id+"FyYUAefgu6xEfva_4.33.F14.boolean.opBoolean","SPLIT",EDGE,{"disambiguationData":[TD([subQ3])],"derivedFrom":makeQuery(id+"FyYUAefgu6xEfva_4.32.F14.boolean.opBoolean","SPLIT",EDGE,{"disambiguationData":[TD([subQ3])],"derivedFrom":makeQuery(id+"FyYUAefgu6xEfva_4.31.F14.boolean.opBoolean","SPLIT",EDGE,{"disambiguationData":[TD([subQ3])],"derivedFrom":makeQuery(id+"FyYUAefgu6xEfva_4.30.F14.boolean.opBoolean","SPLIT",EDGE,{"disambiguationData":[TD([subQ3])],"derivedFrom":makeQuery(id+"FyYUAefgu6xEfva_4.29.F14.boolean.opBoolean","SPLIT",EDGE,{"disambiguationData":[TD([subQ3])],"derivedFrom":makeQuery(id+"FyYUAefgu6xEfva_4.28.F14.boolean.opBoolean","SPLIT",EDGE,{"disambiguationData":[TD([subQ3])],"derivedFrom":makeQuery(id+"FyYUAefgu6xEfva_4.27.F14.boolean.opBoolean","SPLIT",EDGE,{"disambiguationData":[TD([subQ3])],"derivedFrom":makeQuery(id+"FyYUAefgu6xEfva_4.26.F14.boolean.opBoolean","SPLIT",EDGE,{"disambiguationData":[TD([subQ3])],"derivedFrom":makeQuery(id+"FyYUAefgu6xEfva_4.25.F14.boolean.opBoolean","SPLIT",EDGE,{"disambiguationData":[TD([subQ3])],"derivedFrom":makeQuery(id+"FyYUAefgu6xEfva_4.24.F14.boolean.opBoolean","SPLIT",EDGE,{"disambiguationData":[TD([subQ3])],"derivedFrom":makeQuery(id+"FyYUAefgu6xEfva_4.23.F14.boolean.opBoolean","SPLIT",EDGE,{"disambiguationData":[TD([subQ3])],"derivedFrom":makeQuery(id+"FyYUAefgu6xEfva_4.22.F14.boolean.opBoolean","SPLIT",EDGE,{"disambiguationData":[TD([subQ3])],"derivedFrom":makeQuery(id+"FyYUAefgu6xEfva_4.21.F14.boolean.opBoolean","SPLIT",EDGE,{"disambiguationData":[TD([subQ3])],"derivedFrom":makeQuery(id+"FyYUAefgu6xEfva_4.20.F14.boolean.opBoolean","SPLIT",EDGE,{"disambiguationData":[TD([subQ3])],"derivedFrom":makeQuery(id+"FyYUAefgu6xEfva_4.19.F14.boolean.opBoolean","SPLIT",EDGE,{"disambiguationData":[TD([subQ3])],"derivedFrom":makeQuery(id+"FyYUAefgu6xEfva_4.18.F14.boolean.opBoolean","SPLIT",EDGE,{"disambiguationData":[TD([subQ3])],"derivedFrom":makeQuery(id+"FyYUAefgu6xEfva_4.17.F14.boolean.opBoolean","SPLIT",EDGE,{"disambiguationData":[TD([subQ3])],"derivedFrom":makeQuery(id+"FyYUAefgu6xEfva_4.16.F14.boolean.opBoolean","SPLIT",EDGE,{"disambiguationData":[TD([subQ3])],"derivedFrom":makeQuery(id+"FyYUAefgu6xEfva_4.15.F14.boolean.opBoolean","SPLIT",EDGE,{"disambiguationData":[TD([subQ3])],"derivedFrom":makeQuery(id+"FyYUAefgu6xEfva_4.14.F14.boolean.opBoolean","SPLIT",EDGE,{"disambiguationData":[TD([subQ3])],"derivedFrom":makeQuery(id+"FyYUAefgu6xEfva_4.13.F14.boolean.opBoolean","SPLIT",EDGE,{"disambiguationData":[TD([subQ3])],"derivedFrom":makeQuery(id+"FyYUAefgu6xEfva_4.12.F14.boolean.opBoolean","SPLIT",EDGE,{"disambiguationData":[TD([subQ3])],"derivedFrom":makeQuery(id+"FyYUAefgu6xEfva_4.11.F14.boolean.opBoolean","SPLIT",EDGE,{"disambiguationData":[TD([subQ3])],"derivedFrom":makeQuery(id+"FyYUAefgu6xEfva_4.10.F14.boolean.opBoolean","SPLIT",EDGE,{"disambiguationData":[TD([subQ3])],"derivedFrom":makeQuery(id+"FyYUAefgu6xEfva_4.9.F14.boolean.opBoolean","SPLIT",EDGE,{"disambiguationData":[TD([subQ3])],"derivedFrom":makeQuery(id+"FyYUAefgu6xEfva_4.8.F14.boolean.opBoolean","SPLIT",EDGE,{"disambiguationData":[TD([subQ3])],"derivedFrom":makeQuery(id+"FyYUAefgu6xEfva_4.7.F14.boolean.opBoolean","SPLIT",EDGE,{"disambiguationData":[TD([subQ3])],"derivedFrom":makeQuery(id+"FyYUAefgu6xEfva_4.6.F14.boolean.opBoolean","SPLIT",EDGE,{"disambiguationData":[TD([subQ3])],"derivedFrom":makeQuery(id+"FyYUAefgu6xEfva_4.5.F14.boolean.opBoolean","SPLIT",EDGE,{"disambiguationData":[TD([subQ3])],"derivedFrom":makeQuery(id+"FyYUAefgu6xEfva_4.4.F14.boolean.opBoolean","SPLIT",EDGE,{"disambiguationData":[TD([subQ3])],"derivedFrom":makeQuery(id+"FyYUAefgu6xEfva_4.3.F14.boolean.opBoolean","SPLIT",EDGE,{"disambiguationData":[TD([subQ3])],"derivedFrom":makeQuery(id+"FyYUAefgu6xEfva_4.2.F14.boolean.opBoolean","SPLIT",EDGE,{"disambiguationData":[TD([subQ3])],"derivedFrom":makeQuery(id+"FyYUAefgu6xEfva_4.1.F14.boolean.opBoolean","SPLIT",EDGE,{"disambiguationData":[TD([subQ3])],"derivedFrom":makeQuery(id+"F10.boolean.opBoolean","COPY",EDGE,{"derivedFrom":makeQuery(id+"F10.opExtrude","CAP_EDGE",EDGE,{"disambiguationData":[OSD([subQ0])],"isStart":false})})})})})})})})})})})})})})})})})})})})})})})})})})})})})})})})})})})})})})})})})})})})})})})})})})});}
            var Q323;
            {var subQ0=sQuery(id+"F9.wireOp",EDGE,"E142");var subQ2=sQuery(id+"F13.wireOp",EDGE,"E147");var subQ4=sQuery(id+"F13.wireOp",EDGE,"E148.MirrorCS");var subQ5=makeQuery(id+"FyYUAefgu6xEfva_4.48.F14.opExtrude","SWEPT_FACE",FACE,{"disambiguationData":[OSD([subQ4])]});var subQ6=makeQuery(id+"F14.opExtrude","SWEPT_FACE",FACE,{"disambiguationData":[OSD([subQ2])]});Q323=makeQuery(id+"FyYUAefgu6xEfva_4.49.F14.boolean.opBoolean","SPLIT",EDGE,{"disambiguationData":[TD([subQ5])],"derivedFrom":makeQuery(id+"FyYUAefgu6xEfva_4.48.F14.boolean.opBoolean","SPLIT",EDGE,{"disambiguationData":[TD([subQ6])],"derivedFrom":makeQuery(id+"FyYUAefgu6xEfva_4.47.F14.boolean.opBoolean","SPLIT",EDGE,{"disambiguationData":[TD([subQ6])],"derivedFrom":makeQuery(id+"FyYUAefgu6xEfva_4.46.F14.boolean.opBoolean","SPLIT",EDGE,{"disambiguationData":[TD([subQ6])],"derivedFrom":makeQuery(id+"FyYUAefgu6xEfva_4.45.F14.boolean.opBoolean","SPLIT",EDGE,{"disambiguationData":[TD([subQ6])],"derivedFrom":makeQuery(id+"FyYUAefgu6xEfva_4.44.F14.boolean.opBoolean","SPLIT",EDGE,{"disambiguationData":[TD([subQ6])],"derivedFrom":makeQuery(id+"FyYUAefgu6xEfva_4.43.F14.boolean.opBoolean","SPLIT",EDGE,{"disambiguationData":[TD([subQ6])],"derivedFrom":makeQuery(id+"FyYUAefgu6xEfva_4.42.F14.boolean.opBoolean","SPLIT",EDGE,{"disambiguationData":[TD([subQ6])],"derivedFrom":makeQuery(id+"FyYUAefgu6xEfva_4.41.F14.boolean.opBoolean","SPLIT",EDGE,{"disambiguationData":[TD([subQ6])],"derivedFrom":makeQuery(id+"FyYUAefgu6xEfva_4.40.F14.boolean.opBoolean","SPLIT",EDGE,{"disambiguationData":[TD([subQ6])],"derivedFrom":makeQuery(id+"FyYUAefgu6xEfva_4.39.F14.boolean.opBoolean","SPLIT",EDGE,{"disambiguationData":[TD([subQ6])],"derivedFrom":makeQuery(id+"FyYUAefgu6xEfva_4.38.F14.boolean.opBoolean","SPLIT",EDGE,{"disambiguationData":[TD([subQ6])],"derivedFrom":makeQuery(id+"FyYUAefgu6xEfva_4.37.F14.boolean.opBoolean","SPLIT",EDGE,{"disambiguationData":[TD([subQ6])],"derivedFrom":makeQuery(id+"FyYUAefgu6xEfva_4.36.F14.boolean.opBoolean","SPLIT",EDGE,{"disambiguationData":[TD([subQ6])],"derivedFrom":makeQuery(id+"FyYUAefgu6xEfva_4.35.F14.boolean.opBoolean","SPLIT",EDGE,{"disambiguationData":[TD([subQ6])],"derivedFrom":makeQuery(id+"FyYUAefgu6xEfva_4.34.F14.boolean.opBoolean","SPLIT",EDGE,{"disambiguationData":[TD([subQ6])],"derivedFrom":makeQuery(id+"FyYUAefgu6xEfva_4.33.F14.boolean.opBoolean","SPLIT",EDGE,{"disambiguationData":[TD([subQ6])],"derivedFrom":makeQuery(id+"FyYUAefgu6xEfva_4.32.F14.boolean.opBoolean","SPLIT",EDGE,{"disambiguationData":[TD([subQ6])],"derivedFrom":makeQuery(id+"FyYUAefgu6xEfva_4.31.F14.boolean.opBoolean","SPLIT",EDGE,{"disambiguationData":[TD([subQ6])],"derivedFrom":makeQuery(id+"FyYUAefgu6xEfva_4.30.F14.boolean.opBoolean","SPLIT",EDGE,{"disambiguationData":[TD([subQ6])],"derivedFrom":makeQuery(id+"FyYUAefgu6xEfva_4.29.F14.boolean.opBoolean","SPLIT",EDGE,{"disambiguationData":[TD([subQ6])],"derivedFrom":makeQuery(id+"FyYUAefgu6xEfva_4.28.F14.boolean.opBoolean","SPLIT",EDGE,{"disambiguationData":[TD([subQ6])],"derivedFrom":makeQuery(id+"FyYUAefgu6xEfva_4.27.F14.boolean.opBoolean","SPLIT",EDGE,{"disambiguationData":[TD([subQ6])],"derivedFrom":makeQuery(id+"FyYUAefgu6xEfva_4.26.F14.boolean.opBoolean","SPLIT",EDGE,{"disambiguationData":[TD([subQ6])],"derivedFrom":makeQuery(id+"FyYUAefgu6xEfva_4.25.F14.boolean.opBoolean","SPLIT",EDGE,{"disambiguationData":[TD([subQ6])],"derivedFrom":makeQuery(id+"FyYUAefgu6xEfva_4.24.F14.boolean.opBoolean","SPLIT",EDGE,{"disambiguationData":[TD([subQ6])],"derivedFrom":makeQuery(id+"FyYUAefgu6xEfva_4.23.F14.boolean.opBoolean","SPLIT",EDGE,{"disambiguationData":[TD([subQ6])],"derivedFrom":makeQuery(id+"FyYUAefgu6xEfva_4.22.F14.boolean.opBoolean","SPLIT",EDGE,{"disambiguationData":[TD([subQ6])],"derivedFrom":makeQuery(id+"FyYUAefgu6xEfva_4.21.F14.boolean.opBoolean","SPLIT",EDGE,{"disambiguationData":[TD([subQ6])],"derivedFrom":makeQuery(id+"FyYUAefgu6xEfva_4.20.F14.boolean.opBoolean","SPLIT",EDGE,{"disambiguationData":[TD([subQ6])],"derivedFrom":makeQuery(id+"FyYUAefgu6xEfva_4.19.F14.boolean.opBoolean","SPLIT",EDGE,{"disambiguationData":[TD([subQ6])],"derivedFrom":makeQuery(id+"FyYUAefgu6xEfva_4.18.F14.boolean.opBoolean","SPLIT",EDGE,{"disambiguationData":[TD([subQ6])],"derivedFrom":makeQuery(id+"FyYUAefgu6xEfva_4.17.F14.boolean.opBoolean","SPLIT",EDGE,{"disambiguationData":[TD([subQ6])],"derivedFrom":makeQuery(id+"FyYUAefgu6xEfva_4.16.F14.boolean.opBoolean","SPLIT",EDGE,{"disambiguationData":[TD([subQ6])],"derivedFrom":makeQuery(id+"FyYUAefgu6xEfva_4.15.F14.boolean.opBoolean","SPLIT",EDGE,{"disambiguationData":[TD([subQ6])],"derivedFrom":makeQuery(id+"FyYUAefgu6xEfva_4.14.F14.boolean.opBoolean","SPLIT",EDGE,{"disambiguationData":[TD([subQ6])],"derivedFrom":makeQuery(id+"FyYUAefgu6xEfva_4.13.F14.boolean.opBoolean","SPLIT",EDGE,{"disambiguationData":[TD([subQ6])],"derivedFrom":makeQuery(id+"FyYUAefgu6xEfva_4.12.F14.boolean.opBoolean","SPLIT",EDGE,{"disambiguationData":[TD([subQ6])],"derivedFrom":makeQuery(id+"FyYUAefgu6xEfva_4.11.F14.boolean.opBoolean","SPLIT",EDGE,{"disambiguationData":[TD([subQ6])],"derivedFrom":makeQuery(id+"FyYUAefgu6xEfva_4.10.F14.boolean.opBoolean","SPLIT",EDGE,{"disambiguationData":[TD([subQ6])],"derivedFrom":makeQuery(id+"FyYUAefgu6xEfva_4.9.F14.boolean.opBoolean","SPLIT",EDGE,{"disambiguationData":[TD([subQ6])],"derivedFrom":makeQuery(id+"FyYUAefgu6xEfva_4.8.F14.boolean.opBoolean","SPLIT",EDGE,{"disambiguationData":[TD([subQ6])],"derivedFrom":makeQuery(id+"FyYUAefgu6xEfva_4.7.F14.boolean.opBoolean","SPLIT",EDGE,{"disambiguationData":[TD([subQ6])],"derivedFrom":makeQuery(id+"FyYUAefgu6xEfva_4.6.F14.boolean.opBoolean","SPLIT",EDGE,{"disambiguationData":[TD([subQ6])],"derivedFrom":makeQuery(id+"FyYUAefgu6xEfva_4.5.F14.boolean.opBoolean","SPLIT",EDGE,{"disambiguationData":[TD([subQ6])],"derivedFrom":makeQuery(id+"FyYUAefgu6xEfva_4.4.F14.boolean.opBoolean","SPLIT",EDGE,{"disambiguationData":[TD([subQ6])],"derivedFrom":makeQuery(id+"FyYUAefgu6xEfva_4.3.F14.boolean.opBoolean","SPLIT",EDGE,{"disambiguationData":[TD([subQ6])],"derivedFrom":makeQuery(id+"FyYUAefgu6xEfva_4.2.F14.boolean.opBoolean","SPLIT",EDGE,{"disambiguationData":[TD([subQ6])],"derivedFrom":makeQuery(id+"FyYUAefgu6xEfva_4.1.F14.boolean.opBoolean","SPLIT",EDGE,{"disambiguationData":[TD([subQ6])],"derivedFrom":makeQuery(id+"F10.boolean.opBoolean","COPY",EDGE,{"derivedFrom":makeQuery(id+"F10.opExtrude","CAP_EDGE",EDGE,{"disambiguationData":[OSD([subQ0])],"isStart":false})})})})})})})})})})})})})})})})})})})})})})})})})})})})})})})})})})})})})})})})})})})})})})})})})})});}
            var Q324;
            {var subQ1=sQuery(id+"F13.wireOp",EDGE,"E147");var subQ2=sQuery(id+"F11.wireOp",EDGE,"E143");var subQ45=makeQuery(id+"F14.opExtrude","SWEPT_FACE",FACE,{"disambiguationData":[OSD([subQ1])]});Q324=makeQuery(id+"FyYUAefgu6xEfva_4.49.F14.boolean.opBoolean","SPLIT",EDGE,{"disambiguationData":[TD([subQ45])],"derivedFrom":makeQuery(id+"FyYUAefgu6xEfva_4.48.F14.boolean.opBoolean","SPLIT",EDGE,{"disambiguationData":[TD([subQ45])],"derivedFrom":makeQuery(id+"FyYUAefgu6xEfva_4.47.F14.boolean.opBoolean","SPLIT",EDGE,{"disambiguationData":[TD([subQ45])],"derivedFrom":makeQuery(id+"FyYUAefgu6xEfva_4.46.F14.boolean.opBoolean","SPLIT",EDGE,{"disambiguationData":[TD([subQ45])],"derivedFrom":makeQuery(id+"FyYUAefgu6xEfva_4.45.F14.boolean.opBoolean","SPLIT",EDGE,{"disambiguationData":[TD([subQ45])],"derivedFrom":makeQuery(id+"FyYUAefgu6xEfva_4.44.F14.boolean.opBoolean","SPLIT",EDGE,{"disambiguationData":[TD([subQ45])],"derivedFrom":makeQuery(id+"FyYUAefgu6xEfva_4.43.F14.boolean.opBoolean","SPLIT",EDGE,{"disambiguationData":[TD([subQ45])],"derivedFrom":makeQuery(id+"FyYUAefgu6xEfva_4.42.F14.boolean.opBoolean","SPLIT",EDGE,{"disambiguationData":[TD([subQ45])],"derivedFrom":makeQuery(id+"FyYUAefgu6xEfva_4.41.F14.boolean.opBoolean","SPLIT",EDGE,{"disambiguationData":[TD([subQ45])],"derivedFrom":makeQuery(id+"FyYUAefgu6xEfva_4.40.F14.boolean.opBoolean","SPLIT",EDGE,{"disambiguationData":[TD([subQ45])],"derivedFrom":makeQuery(id+"FyYUAefgu6xEfva_4.39.F14.boolean.opBoolean","SPLIT",EDGE,{"disambiguationData":[TD([subQ45])],"derivedFrom":makeQuery(id+"FyYUAefgu6xEfva_4.38.F14.boolean.opBoolean","SPLIT",EDGE,{"disambiguationData":[TD([subQ45])],"derivedFrom":makeQuery(id+"FyYUAefgu6xEfva_4.37.F14.boolean.opBoolean","SPLIT",EDGE,{"disambiguationData":[TD([subQ45])],"derivedFrom":makeQuery(id+"FyYUAefgu6xEfva_4.36.F14.boolean.opBoolean","SPLIT",EDGE,{"disambiguationData":[TD([subQ45])],"derivedFrom":makeQuery(id+"FyYUAefgu6xEfva_4.35.F14.boolean.opBoolean","SPLIT",EDGE,{"disambiguationData":[TD([subQ45])],"derivedFrom":makeQuery(id+"FyYUAefgu6xEfva_4.34.F14.boolean.opBoolean","SPLIT",EDGE,{"disambiguationData":[TD([subQ45])],"derivedFrom":makeQuery(id+"FyYUAefgu6xEfva_4.33.F14.boolean.opBoolean","SPLIT",EDGE,{"disambiguationData":[TD([subQ45])],"derivedFrom":makeQuery(id+"FyYUAefgu6xEfva_4.32.F14.boolean.opBoolean","SPLIT",EDGE,{"disambiguationData":[TD([subQ45])],"derivedFrom":makeQuery(id+"FyYUAefgu6xEfva_4.31.F14.boolean.opBoolean","SPLIT",EDGE,{"disambiguationData":[TD([subQ45])],"derivedFrom":makeQuery(id+"FyYUAefgu6xEfva_4.30.F14.boolean.opBoolean","SPLIT",EDGE,{"disambiguationData":[TD([subQ45])],"derivedFrom":makeQuery(id+"FyYUAefgu6xEfva_4.29.F14.boolean.opBoolean","SPLIT",EDGE,{"disambiguationData":[TD([subQ45])],"derivedFrom":makeQuery(id+"FyYUAefgu6xEfva_4.28.F14.boolean.opBoolean","SPLIT",EDGE,{"disambiguationData":[TD([subQ45])],"derivedFrom":makeQuery(id+"FyYUAefgu6xEfva_4.27.F14.boolean.opBoolean","SPLIT",EDGE,{"disambiguationData":[TD([subQ45])],"derivedFrom":makeQuery(id+"FyYUAefgu6xEfva_4.26.F14.boolean.opBoolean","SPLIT",EDGE,{"disambiguationData":[TD([subQ45])],"derivedFrom":makeQuery(id+"FyYUAefgu6xEfva_4.25.F14.boolean.opBoolean","SPLIT",EDGE,{"disambiguationData":[TD([subQ45])],"derivedFrom":makeQuery(id+"FyYUAefgu6xEfva_4.24.F14.boolean.opBoolean","SPLIT",EDGE,{"disambiguationData":[TD([subQ45])],"derivedFrom":makeQuery(id+"FyYUAefgu6xEfva_4.23.F14.boolean.opBoolean","SPLIT",EDGE,{"disambiguationData":[TD([subQ45])],"derivedFrom":makeQuery(id+"FyYUAefgu6xEfva_4.22.F14.boolean.opBoolean","SPLIT",EDGE,{"disambiguationData":[TD([subQ45])],"derivedFrom":makeQuery(id+"FyYUAefgu6xEfva_4.21.F14.boolean.opBoolean","SPLIT",EDGE,{"disambiguationData":[TD([subQ45])],"derivedFrom":makeQuery(id+"FyYUAefgu6xEfva_4.20.F14.boolean.opBoolean","SPLIT",EDGE,{"disambiguationData":[TD([subQ45])],"derivedFrom":makeQuery(id+"FyYUAefgu6xEfva_4.19.F14.boolean.opBoolean","SPLIT",EDGE,{"disambiguationData":[TD([subQ45])],"derivedFrom":makeQuery(id+"FyYUAefgu6xEfva_4.18.F14.boolean.opBoolean","SPLIT",EDGE,{"disambiguationData":[TD([subQ45])],"derivedFrom":makeQuery(id+"FyYUAefgu6xEfva_4.17.F14.boolean.opBoolean","SPLIT",EDGE,{"disambiguationData":[TD([subQ45])],"derivedFrom":makeQuery(id+"FyYUAefgu6xEfva_4.16.F14.boolean.opBoolean","SPLIT",EDGE,{"disambiguationData":[TD([subQ45])],"derivedFrom":makeQuery(id+"FyYUAefgu6xEfva_4.15.F14.boolean.opBoolean","SPLIT",EDGE,{"disambiguationData":[TD([subQ45])],"derivedFrom":makeQuery(id+"FyYUAefgu6xEfva_4.14.F14.boolean.opBoolean","SPLIT",EDGE,{"disambiguationData":[TD([subQ45])],"derivedFrom":makeQuery(id+"FyYUAefgu6xEfva_4.13.F14.boolean.opBoolean","SPLIT",EDGE,{"disambiguationData":[TD([subQ45])],"derivedFrom":makeQuery(id+"FyYUAefgu6xEfva_4.12.F14.boolean.opBoolean","SPLIT",EDGE,{"disambiguationData":[TD([subQ45])],"derivedFrom":makeQuery(id+"FyYUAefgu6xEfva_4.11.F14.boolean.opBoolean","SPLIT",EDGE,{"disambiguationData":[TD([subQ45])],"derivedFrom":makeQuery(id+"FyYUAefgu6xEfva_4.10.F14.boolean.opBoolean","SPLIT",EDGE,{"disambiguationData":[TD([subQ45])],"derivedFrom":makeQuery(id+"FyYUAefgu6xEfva_4.9.F14.boolean.opBoolean","SPLIT",EDGE,{"disambiguationData":[TD([subQ45])],"derivedFrom":makeQuery(id+"FyYUAefgu6xEfva_4.8.F14.boolean.opBoolean","SPLIT",EDGE,{"disambiguationData":[TD([subQ45])],"derivedFrom":makeQuery(id+"FyYUAefgu6xEfva_4.7.F14.boolean.opBoolean","SPLIT",EDGE,{"disambiguationData":[TD([subQ45])],"derivedFrom":makeQuery(id+"FyYUAefgu6xEfva_4.6.F14.boolean.opBoolean","SPLIT",EDGE,{"disambiguationData":[TD([subQ45])],"derivedFrom":makeQuery(id+"FyYUAefgu6xEfva_4.5.F14.boolean.opBoolean","SPLIT",EDGE,{"disambiguationData":[TD([subQ45])],"derivedFrom":makeQuery(id+"FyYUAefgu6xEfva_4.4.F14.boolean.opBoolean","SPLIT",EDGE,{"disambiguationData":[TD([subQ45])],"derivedFrom":makeQuery(id+"FyYUAefgu6xEfva_4.3.F14.boolean.opBoolean","SPLIT",EDGE,{"disambiguationData":[TD([subQ45])],"derivedFrom":makeQuery(id+"FyYUAefgu6xEfva_4.2.F14.boolean.opBoolean","SPLIT",EDGE,{"disambiguationData":[TD([subQ45])],"derivedFrom":makeQuery(id+"FyYUAefgu6xEfva_4.1.F14.boolean.opBoolean","SPLIT",EDGE,{"disambiguationData":[TD([subQ45])],"derivedFrom":makeQuery(id+"F12.opExtrude","CAP_EDGE",EDGE,{"disambiguationData":[OSD([subQ2])],"isStart":false})})})})})})})})})})})})})})})})})})})})})})})})})})})})})})})})})})})})})})})})})})})})})})})})})});}
            var Q325;
            Q325=makeQuery(id+"FyYUAefgu6xEfva_4.18.F14.opExtrude","SWEPT_EDGE",EDGE,{"disambiguationData":[OSD([sQuery(id+"F11.wireOp",EDGE,"E143"),sQuery(id+"F13.wireOp",EDGE,"E147")])]});
            var Q326;
            Q326=makeQuery(id+"FyYUAefgu6xEfva_4.18.F14.opExtrude","SWEPT_EDGE",EDGE,{"disambiguationData":[OSD([sQuery(id+"F9.wireOp",EDGE,"E142"),sQuery(id+"F13.wireOp",EDGE,"E148.MirrorCS")])]});
            var Q327;
            Q327=makeQuery(id+"FyYUAefgu6xEfva_4.18.F14.opExtrude","SWEPT_EDGE",EDGE,{"disambiguationData":[OSD([sQuery(id+"F11.wireOp",EDGE,"E143"),sQuery(id+"F13.wireOp",EDGE,"E148.MirrorCS")])]});
            var Q328;
            Q328=makeQuery(id+"FyYUAefgu6xEfva_4.18.F14.opExtrude","CAP_EDGE",EDGE,{"disambiguationData":[OSD([sQuery(id+"F9.wireOp",EDGE,"E142")])],"isStart":false});
            var Q329;
            {var subQ0=sQuery(id+"F13.wireOp",EDGE,"E148.MirrorCS");var subQ1=sQuery(id+"F13.wireOp",EDGE,"E147");var subQ2=sQuery(id+"F11.wireOp",EDGE,"E143");var subQ16=makeQuery(id+"FyYUAefgu6xEfva_4.17.F14.opExtrude","SWEPT_FACE",FACE,{"disambiguationData":[OSD([subQ0])]});var subQ25=makeQuery(id+"F14.opExtrude","SWEPT_FACE",FACE,{"disambiguationData":[OSD([subQ1])]});Q329=makeQuery(id+"FyYUAefgu6xEfva_4.18.F14.boolean.opBoolean","SPLIT",EDGE,{"disambiguationData":[TD([subQ16])],"derivedFrom":makeQuery(id+"FyYUAefgu6xEfva_4.17.F14.boolean.opBoolean","SPLIT",EDGE,{"disambiguationData":[TD([subQ25])],"derivedFrom":makeQuery(id+"FyYUAefgu6xEfva_4.16.F14.boolean.opBoolean","SPLIT",EDGE,{"disambiguationData":[TD([subQ25])],"derivedFrom":makeQuery(id+"FyYUAefgu6xEfva_4.15.F14.boolean.opBoolean","SPLIT",EDGE,{"disambiguationData":[TD([subQ25])],"derivedFrom":makeQuery(id+"FyYUAefgu6xEfva_4.14.F14.boolean.opBoolean","SPLIT",EDGE,{"disambiguationData":[TD([subQ25])],"derivedFrom":makeQuery(id+"FyYUAefgu6xEfva_4.13.F14.boolean.opBoolean","SPLIT",EDGE,{"disambiguationData":[TD([subQ25])],"derivedFrom":makeQuery(id+"FyYUAefgu6xEfva_4.12.F14.boolean.opBoolean","SPLIT",EDGE,{"disambiguationData":[TD([subQ25])],"derivedFrom":makeQuery(id+"FyYUAefgu6xEfva_4.11.F14.boolean.opBoolean","SPLIT",EDGE,{"disambiguationData":[TD([subQ25])],"derivedFrom":makeQuery(id+"FyYUAefgu6xEfva_4.10.F14.boolean.opBoolean","SPLIT",EDGE,{"disambiguationData":[TD([subQ25])],"derivedFrom":makeQuery(id+"FyYUAefgu6xEfva_4.9.F14.boolean.opBoolean","SPLIT",EDGE,{"disambiguationData":[TD([subQ25])],"derivedFrom":makeQuery(id+"FyYUAefgu6xEfva_4.8.F14.boolean.opBoolean","SPLIT",EDGE,{"disambiguationData":[TD([subQ25])],"derivedFrom":makeQuery(id+"FyYUAefgu6xEfva_4.7.F14.boolean.opBoolean","SPLIT",EDGE,{"disambiguationData":[TD([subQ25])],"derivedFrom":makeQuery(id+"FyYUAefgu6xEfva_4.6.F14.boolean.opBoolean","SPLIT",EDGE,{"disambiguationData":[TD([subQ25])],"derivedFrom":makeQuery(id+"FyYUAefgu6xEfva_4.5.F14.boolean.opBoolean","SPLIT",EDGE,{"disambiguationData":[TD([subQ25])],"derivedFrom":makeQuery(id+"FyYUAefgu6xEfva_4.4.F14.boolean.opBoolean","SPLIT",EDGE,{"disambiguationData":[TD([subQ25])],"derivedFrom":makeQuery(id+"FyYUAefgu6xEfva_4.3.F14.boolean.opBoolean","SPLIT",EDGE,{"disambiguationData":[TD([subQ25])],"derivedFrom":makeQuery(id+"FyYUAefgu6xEfva_4.2.F14.boolean.opBoolean","SPLIT",EDGE,{"disambiguationData":[TD([subQ25])],"derivedFrom":makeQuery(id+"FyYUAefgu6xEfva_4.1.F14.boolean.opBoolean","SPLIT",EDGE,{"disambiguationData":[TD([subQ25])],"derivedFrom":makeQuery(id+"F12.opExtrude","CAP_EDGE",EDGE,{"disambiguationData":[OSD([subQ2])],"isStart":false})})})})})})})})})})})})})})})})})})});}
            var Q330;
            Q330=makeQuery(id+"FyYUAefgu6xEfva_4.19.F14.opExtrude","SWEPT_EDGE",EDGE,{"disambiguationData":[OSD([sQuery(id+"F9.wireOp",EDGE,"E142"),sQuery(id+"F13.wireOp",EDGE,"E147")])]});
            var Q331;
            Q331=makeQuery(id+"FyYUAefgu6xEfva_4.19.F14.opExtrude","SWEPT_EDGE",EDGE,{"disambiguationData":[OSD([sQuery(id+"F11.wireOp",EDGE,"E143"),sQuery(id+"F13.wireOp",EDGE,"E147")])]});
            var Q332;
            Q332=makeQuery(id+"FyYUAefgu6xEfva_4.19.F14.opExtrude","SWEPT_EDGE",EDGE,{"disambiguationData":[OSD([sQuery(id+"F9.wireOp",EDGE,"E142"),sQuery(id+"F13.wireOp",EDGE,"E148.MirrorCS")])]});
            var Q333;
            Q333=makeQuery(id+"FyYUAefgu6xEfva_4.19.F14.opExtrude","SWEPT_EDGE",EDGE,{"disambiguationData":[OSD([sQuery(id+"F11.wireOp",EDGE,"E143"),sQuery(id+"F13.wireOp",EDGE,"E148.MirrorCS")])]});
            var Q334;
            Q334=makeQuery(id+"FyYUAefgu6xEfva_4.19.F14.opExtrude","CAP_EDGE",EDGE,{"disambiguationData":[OSD([sQuery(id+"F13.wireOp",EDGE,"E148.MirrorCS")])],"isStart":true});
            var Q335;
            Q335=makeQuery(id+"FyYUAefgu6xEfva_4.19.F14.opExtrude","CAP_EDGE",EDGE,{"disambiguationData":[OSD([sQuery(id+"F9.wireOp",EDGE,"E142")])],"isStart":false});
            var Q336;
            {var subQ0=sQuery(id+"F13.wireOp",EDGE,"E148.MirrorCS");var subQ1=sQuery(id+"F13.wireOp",EDGE,"E147");var subQ2=sQuery(id+"F11.wireOp",EDGE,"E143");var subQ22=makeQuery(id+"FyYUAefgu6xEfva_4.18.F14.opExtrude","SWEPT_FACE",FACE,{"disambiguationData":[OSD([subQ0])]});var subQ26=makeQuery(id+"F14.opExtrude","SWEPT_FACE",FACE,{"disambiguationData":[OSD([subQ1])]});Q336=makeQuery(id+"FyYUAefgu6xEfva_4.19.F14.boolean.opBoolean","SPLIT",EDGE,{"disambiguationData":[TD([subQ22])],"derivedFrom":makeQuery(id+"FyYUAefgu6xEfva_4.18.F14.boolean.opBoolean","SPLIT",EDGE,{"disambiguationData":[TD([subQ26])],"derivedFrom":makeQuery(id+"FyYUAefgu6xEfva_4.17.F14.boolean.opBoolean","SPLIT",EDGE,{"disambiguationData":[TD([subQ26])],"derivedFrom":makeQuery(id+"FyYUAefgu6xEfva_4.16.F14.boolean.opBoolean","SPLIT",EDGE,{"disambiguationData":[TD([subQ26])],"derivedFrom":makeQuery(id+"FyYUAefgu6xEfva_4.15.F14.boolean.opBoolean","SPLIT",EDGE,{"disambiguationData":[TD([subQ26])],"derivedFrom":makeQuery(id+"FyYUAefgu6xEfva_4.14.F14.boolean.opBoolean","SPLIT",EDGE,{"disambiguationData":[TD([subQ26])],"derivedFrom":makeQuery(id+"FyYUAefgu6xEfva_4.13.F14.boolean.opBoolean","SPLIT",EDGE,{"disambiguationData":[TD([subQ26])],"derivedFrom":makeQuery(id+"FyYUAefgu6xEfva_4.12.F14.boolean.opBoolean","SPLIT",EDGE,{"disambiguationData":[TD([subQ26])],"derivedFrom":makeQuery(id+"FyYUAefgu6xEfva_4.11.F14.boolean.opBoolean","SPLIT",EDGE,{"disambiguationData":[TD([subQ26])],"derivedFrom":makeQuery(id+"FyYUAefgu6xEfva_4.10.F14.boolean.opBoolean","SPLIT",EDGE,{"disambiguationData":[TD([subQ26])],"derivedFrom":makeQuery(id+"FyYUAefgu6xEfva_4.9.F14.boolean.opBoolean","SPLIT",EDGE,{"disambiguationData":[TD([subQ26])],"derivedFrom":makeQuery(id+"FyYUAefgu6xEfva_4.8.F14.boolean.opBoolean","SPLIT",EDGE,{"disambiguationData":[TD([subQ26])],"derivedFrom":makeQuery(id+"FyYUAefgu6xEfva_4.7.F14.boolean.opBoolean","SPLIT",EDGE,{"disambiguationData":[TD([subQ26])],"derivedFrom":makeQuery(id+"FyYUAefgu6xEfva_4.6.F14.boolean.opBoolean","SPLIT",EDGE,{"disambiguationData":[TD([subQ26])],"derivedFrom":makeQuery(id+"FyYUAefgu6xEfva_4.5.F14.boolean.opBoolean","SPLIT",EDGE,{"disambiguationData":[TD([subQ26])],"derivedFrom":makeQuery(id+"FyYUAefgu6xEfva_4.4.F14.boolean.opBoolean","SPLIT",EDGE,{"disambiguationData":[TD([subQ26])],"derivedFrom":makeQuery(id+"FyYUAefgu6xEfva_4.3.F14.boolean.opBoolean","SPLIT",EDGE,{"disambiguationData":[TD([subQ26])],"derivedFrom":makeQuery(id+"FyYUAefgu6xEfva_4.2.F14.boolean.opBoolean","SPLIT",EDGE,{"disambiguationData":[TD([subQ26])],"derivedFrom":makeQuery(id+"FyYUAefgu6xEfva_4.1.F14.boolean.opBoolean","SPLIT",EDGE,{"disambiguationData":[TD([subQ26])],"derivedFrom":makeQuery(id+"F12.opExtrude","CAP_EDGE",EDGE,{"disambiguationData":[OSD([subQ2])],"isStart":false})})})})})})})})})})})})})})})})})})})});}
            var Q337;
            Q337=makeQuery(id+"FyYUAefgu6xEfva_4.20.F14.opExtrude","SWEPT_EDGE",EDGE,{"disambiguationData":[OSD([sQuery(id+"F9.wireOp",EDGE,"E142"),sQuery(id+"F13.wireOp",EDGE,"E147")])]});
            var Q338;
            Q338=makeQuery(id+"FyYUAefgu6xEfva_4.20.F14.opExtrude","SWEPT_EDGE",EDGE,{"disambiguationData":[OSD([sQuery(id+"F11.wireOp",EDGE,"E143"),sQuery(id+"F13.wireOp",EDGE,"E147")])]});
            var Q339;
            Q339=makeQuery(id+"FyYUAefgu6xEfva_4.20.F14.opExtrude","SWEPT_EDGE",EDGE,{"disambiguationData":[OSD([sQuery(id+"F9.wireOp",EDGE,"E142"),sQuery(id+"F13.wireOp",EDGE,"E148.MirrorCS")])]});
            var Q340;
            Q340=makeQuery(id+"FyYUAefgu6xEfva_4.20.F14.opExtrude","SWEPT_EDGE",EDGE,{"disambiguationData":[OSD([sQuery(id+"F11.wireOp",EDGE,"E143"),sQuery(id+"F13.wireOp",EDGE,"E148.MirrorCS")])]});
            var Q341;
            Q341=makeQuery(id+"FyYUAefgu6xEfva_4.20.F14.opExtrude","CAP_EDGE",EDGE,{"disambiguationData":[OSD([sQuery(id+"F13.wireOp",EDGE,"E147")])],"isStart":true});
            var Q342;
            Q342=makeQuery(id+"FyYUAefgu6xEfva_4.20.F14.opExtrude","CAP_EDGE",EDGE,{"disambiguationData":[OSD([sQuery(id+"F13.wireOp",EDGE,"E148.MirrorCS")])],"isStart":true});
            var Q343;
            Q343=makeQuery(id+"FyYUAefgu6xEfva_4.20.F14.opExtrude","CAP_EDGE",EDGE,{"disambiguationData":[OSD([sQuery(id+"F9.wireOp",EDGE,"E142")])],"isStart":false});
            var Q344;
            {var subQ0=sQuery(id+"F13.wireOp",EDGE,"E148.MirrorCS");var subQ1=sQuery(id+"F13.wireOp",EDGE,"E147");var subQ2=sQuery(id+"F11.wireOp",EDGE,"E143");var subQ26=makeQuery(id+"FyYUAefgu6xEfva_4.19.F14.opExtrude","SWEPT_FACE",FACE,{"disambiguationData":[OSD([subQ0])]});var subQ27=makeQuery(id+"F14.opExtrude","SWEPT_FACE",FACE,{"disambiguationData":[OSD([subQ1])]});Q344=makeQuery(id+"FyYUAefgu6xEfva_4.20.F14.boolean.opBoolean","SPLIT",EDGE,{"disambiguationData":[TD([subQ26])],"derivedFrom":makeQuery(id+"FyYUAefgu6xEfva_4.19.F14.boolean.opBoolean","SPLIT",EDGE,{"disambiguationData":[TD([subQ27])],"derivedFrom":makeQuery(id+"FyYUAefgu6xEfva_4.18.F14.boolean.opBoolean","SPLIT",EDGE,{"disambiguationData":[TD([subQ27])],"derivedFrom":makeQuery(id+"FyYUAefgu6xEfva_4.17.F14.boolean.opBoolean","SPLIT",EDGE,{"disambiguationData":[TD([subQ27])],"derivedFrom":makeQuery(id+"FyYUAefgu6xEfva_4.16.F14.boolean.opBoolean","SPLIT",EDGE,{"disambiguationData":[TD([subQ27])],"derivedFrom":makeQuery(id+"FyYUAefgu6xEfva_4.15.F14.boolean.opBoolean","SPLIT",EDGE,{"disambiguationData":[TD([subQ27])],"derivedFrom":makeQuery(id+"FyYUAefgu6xEfva_4.14.F14.boolean.opBoolean","SPLIT",EDGE,{"disambiguationData":[TD([subQ27])],"derivedFrom":makeQuery(id+"FyYUAefgu6xEfva_4.13.F14.boolean.opBoolean","SPLIT",EDGE,{"disambiguationData":[TD([subQ27])],"derivedFrom":makeQuery(id+"FyYUAefgu6xEfva_4.12.F14.boolean.opBoolean","SPLIT",EDGE,{"disambiguationData":[TD([subQ27])],"derivedFrom":makeQuery(id+"FyYUAefgu6xEfva_4.11.F14.boolean.opBoolean","SPLIT",EDGE,{"disambiguationData":[TD([subQ27])],"derivedFrom":makeQuery(id+"FyYUAefgu6xEfva_4.10.F14.boolean.opBoolean","SPLIT",EDGE,{"disambiguationData":[TD([subQ27])],"derivedFrom":makeQuery(id+"FyYUAefgu6xEfva_4.9.F14.boolean.opBoolean","SPLIT",EDGE,{"disambiguationData":[TD([subQ27])],"derivedFrom":makeQuery(id+"FyYUAefgu6xEfva_4.8.F14.boolean.opBoolean","SPLIT",EDGE,{"disambiguationData":[TD([subQ27])],"derivedFrom":makeQuery(id+"FyYUAefgu6xEfva_4.7.F14.boolean.opBoolean","SPLIT",EDGE,{"disambiguationData":[TD([subQ27])],"derivedFrom":makeQuery(id+"FyYUAefgu6xEfva_4.6.F14.boolean.opBoolean","SPLIT",EDGE,{"disambiguationData":[TD([subQ27])],"derivedFrom":makeQuery(id+"FyYUAefgu6xEfva_4.5.F14.boolean.opBoolean","SPLIT",EDGE,{"disambiguationData":[TD([subQ27])],"derivedFrom":makeQuery(id+"FyYUAefgu6xEfva_4.4.F14.boolean.opBoolean","SPLIT",EDGE,{"disambiguationData":[TD([subQ27])],"derivedFrom":makeQuery(id+"FyYUAefgu6xEfva_4.3.F14.boolean.opBoolean","SPLIT",EDGE,{"disambiguationData":[TD([subQ27])],"derivedFrom":makeQuery(id+"FyYUAefgu6xEfva_4.2.F14.boolean.opBoolean","SPLIT",EDGE,{"disambiguationData":[TD([subQ27])],"derivedFrom":makeQuery(id+"FyYUAefgu6xEfva_4.1.F14.boolean.opBoolean","SPLIT",EDGE,{"disambiguationData":[TD([subQ27])],"derivedFrom":makeQuery(id+"F12.opExtrude","CAP_EDGE",EDGE,{"disambiguationData":[OSD([subQ2])],"isStart":false})})})})})})})})})})})})})})})})})})})})});}
            var Q345;
            Q345=makeQuery(id+"FyYUAefgu6xEfva_4.21.F14.opExtrude","CAP_EDGE",EDGE,{"disambiguationData":[OSD([sQuery(id+"F13.wireOp",EDGE,"E147")])],"isStart":false});
            var Q346;
            Q346=makeQuery(id+"FyYUAefgu6xEfva_4.21.F14.opExtrude","SWEPT_EDGE",EDGE,{"disambiguationData":[OSD([sQuery(id+"F9.wireOp",EDGE,"E142"),sQuery(id+"F13.wireOp",EDGE,"E147")])]});
            var Q347;
            Q347=makeQuery(id+"FyYUAefgu6xEfva_4.21.F14.opExtrude","SWEPT_EDGE",EDGE,{"disambiguationData":[OSD([sQuery(id+"F11.wireOp",EDGE,"E143"),sQuery(id+"F13.wireOp",EDGE,"E148.MirrorCS")])]});
            var Q348;
            Q348=makeQuery(id+"FyYUAefgu6xEfva_4.21.F14.opExtrude","CAP_EDGE",EDGE,{"disambiguationData":[OSD([sQuery(id+"F13.wireOp",EDGE,"E147")])],"isStart":true});
            var Q349;
            Q349=makeQuery(id+"FyYUAefgu6xEfva_4.21.F14.opExtrude","CAP_EDGE",EDGE,{"disambiguationData":[OSD([sQuery(id+"F13.wireOp",EDGE,"E148.MirrorCS")])],"isStart":true});
            var Q350;
            {var subQ0=sQuery(id+"F9.wireOp",EDGE,"E142");var subQ2=sQuery(id+"F13.wireOp",EDGE,"E148.MirrorCS");var subQ3=makeQuery(id+"FyYUAefgu6xEfva_4.20.F14.opExtrude","SWEPT_FACE",FACE,{"disambiguationData":[OSD([subQ2])]});var subQ5=sQuery(id+"F13.wireOp",EDGE,"E147");var subQ6=makeQuery(id+"F14.opExtrude","SWEPT_FACE",FACE,{"disambiguationData":[OSD([subQ5])]});Q350=makeQuery(id+"FyYUAefgu6xEfva_4.21.F14.boolean.opBoolean","SPLIT",EDGE,{"disambiguationData":[TD([subQ3])],"derivedFrom":makeQuery(id+"FyYUAefgu6xEfva_4.20.F14.boolean.opBoolean","SPLIT",EDGE,{"disambiguationData":[TD([subQ6])],"derivedFrom":makeQuery(id+"FyYUAefgu6xEfva_4.19.F14.boolean.opBoolean","SPLIT",EDGE,{"disambiguationData":[TD([subQ6])],"derivedFrom":makeQuery(id+"FyYUAefgu6xEfva_4.18.F14.boolean.opBoolean","SPLIT",EDGE,{"disambiguationData":[TD([subQ6])],"derivedFrom":makeQuery(id+"FyYUAefgu6xEfva_4.17.F14.boolean.opBoolean","SPLIT",EDGE,{"disambiguationData":[TD([subQ6])],"derivedFrom":makeQuery(id+"FyYUAefgu6xEfva_4.16.F14.boolean.opBoolean","SPLIT",EDGE,{"disambiguationData":[TD([subQ6])],"derivedFrom":makeQuery(id+"FyYUAefgu6xEfva_4.15.F14.boolean.opBoolean","SPLIT",EDGE,{"disambiguationData":[TD([subQ6])],"derivedFrom":makeQuery(id+"FyYUAefgu6xEfva_4.14.F14.boolean.opBoolean","SPLIT",EDGE,{"disambiguationData":[TD([subQ6])],"derivedFrom":makeQuery(id+"FyYUAefgu6xEfva_4.13.F14.boolean.opBoolean","SPLIT",EDGE,{"disambiguationData":[TD([subQ6])],"derivedFrom":makeQuery(id+"FyYUAefgu6xEfva_4.12.F14.boolean.opBoolean","SPLIT",EDGE,{"disambiguationData":[TD([subQ6])],"derivedFrom":makeQuery(id+"FyYUAefgu6xEfva_4.11.F14.boolean.opBoolean","SPLIT",EDGE,{"disambiguationData":[TD([subQ6])],"derivedFrom":makeQuery(id+"FyYUAefgu6xEfva_4.10.F14.boolean.opBoolean","SPLIT",EDGE,{"disambiguationData":[TD([subQ6])],"derivedFrom":makeQuery(id+"FyYUAefgu6xEfva_4.9.F14.boolean.opBoolean","SPLIT",EDGE,{"disambiguationData":[TD([subQ6])],"derivedFrom":makeQuery(id+"FyYUAefgu6xEfva_4.8.F14.boolean.opBoolean","SPLIT",EDGE,{"disambiguationData":[TD([subQ6])],"derivedFrom":makeQuery(id+"FyYUAefgu6xEfva_4.7.F14.boolean.opBoolean","SPLIT",EDGE,{"disambiguationData":[TD([subQ6])],"derivedFrom":makeQuery(id+"FyYUAefgu6xEfva_4.6.F14.boolean.opBoolean","SPLIT",EDGE,{"disambiguationData":[TD([subQ6])],"derivedFrom":makeQuery(id+"FyYUAefgu6xEfva_4.5.F14.boolean.opBoolean","SPLIT",EDGE,{"disambiguationData":[TD([subQ6])],"derivedFrom":makeQuery(id+"FyYUAefgu6xEfva_4.4.F14.boolean.opBoolean","SPLIT",EDGE,{"disambiguationData":[TD([subQ6])],"derivedFrom":makeQuery(id+"FyYUAefgu6xEfva_4.3.F14.boolean.opBoolean","SPLIT",EDGE,{"disambiguationData":[TD([subQ6])],"derivedFrom":makeQuery(id+"FyYUAefgu6xEfva_4.2.F14.boolean.opBoolean","SPLIT",EDGE,{"disambiguationData":[TD([subQ6])],"derivedFrom":makeQuery(id+"FyYUAefgu6xEfva_4.1.F14.boolean.opBoolean","SPLIT",EDGE,{"disambiguationData":[TD([subQ6])],"derivedFrom":makeQuery(id+"F10.boolean.opBoolean","COPY",EDGE,{"derivedFrom":makeQuery(id+"F10.opExtrude","CAP_EDGE",EDGE,{"disambiguationData":[OSD([subQ0])],"isStart":false})})})})})})})})})})})})})})})})})})})})})})});}
            var Q351;
            {var subQ0=sQuery(id+"F13.wireOp",EDGE,"E148.MirrorCS");var subQ1=sQuery(id+"F13.wireOp",EDGE,"E147");var subQ2=sQuery(id+"F11.wireOp",EDGE,"E143");var subQ27=makeQuery(id+"FyYUAefgu6xEfva_4.20.F14.opExtrude","SWEPT_FACE",FACE,{"disambiguationData":[OSD([subQ0])]});var subQ28=makeQuery(id+"F14.opExtrude","SWEPT_FACE",FACE,{"disambiguationData":[OSD([subQ1])]});Q351=makeQuery(id+"FyYUAefgu6xEfva_4.21.F14.boolean.opBoolean","SPLIT",EDGE,{"disambiguationData":[TD([subQ27])],"derivedFrom":makeQuery(id+"FyYUAefgu6xEfva_4.20.F14.boolean.opBoolean","SPLIT",EDGE,{"disambiguationData":[TD([subQ28])],"derivedFrom":makeQuery(id+"FyYUAefgu6xEfva_4.19.F14.boolean.opBoolean","SPLIT",EDGE,{"disambiguationData":[TD([subQ28])],"derivedFrom":makeQuery(id+"FyYUAefgu6xEfva_4.18.F14.boolean.opBoolean","SPLIT",EDGE,{"disambiguationData":[TD([subQ28])],"derivedFrom":makeQuery(id+"FyYUAefgu6xEfva_4.17.F14.boolean.opBoolean","SPLIT",EDGE,{"disambiguationData":[TD([subQ28])],"derivedFrom":makeQuery(id+"FyYUAefgu6xEfva_4.16.F14.boolean.opBoolean","SPLIT",EDGE,{"disambiguationData":[TD([subQ28])],"derivedFrom":makeQuery(id+"FyYUAefgu6xEfva_4.15.F14.boolean.opBoolean","SPLIT",EDGE,{"disambiguationData":[TD([subQ28])],"derivedFrom":makeQuery(id+"FyYUAefgu6xEfva_4.14.F14.boolean.opBoolean","SPLIT",EDGE,{"disambiguationData":[TD([subQ28])],"derivedFrom":makeQuery(id+"FyYUAefgu6xEfva_4.13.F14.boolean.opBoolean","SPLIT",EDGE,{"disambiguationData":[TD([subQ28])],"derivedFrom":makeQuery(id+"FyYUAefgu6xEfva_4.12.F14.boolean.opBoolean","SPLIT",EDGE,{"disambiguationData":[TD([subQ28])],"derivedFrom":makeQuery(id+"FyYUAefgu6xEfva_4.11.F14.boolean.opBoolean","SPLIT",EDGE,{"disambiguationData":[TD([subQ28])],"derivedFrom":makeQuery(id+"FyYUAefgu6xEfva_4.10.F14.boolean.opBoolean","SPLIT",EDGE,{"disambiguationData":[TD([subQ28])],"derivedFrom":makeQuery(id+"FyYUAefgu6xEfva_4.9.F14.boolean.opBoolean","SPLIT",EDGE,{"disambiguationData":[TD([subQ28])],"derivedFrom":makeQuery(id+"FyYUAefgu6xEfva_4.8.F14.boolean.opBoolean","SPLIT",EDGE,{"disambiguationData":[TD([subQ28])],"derivedFrom":makeQuery(id+"FyYUAefgu6xEfva_4.7.F14.boolean.opBoolean","SPLIT",EDGE,{"disambiguationData":[TD([subQ28])],"derivedFrom":makeQuery(id+"FyYUAefgu6xEfva_4.6.F14.boolean.opBoolean","SPLIT",EDGE,{"disambiguationData":[TD([subQ28])],"derivedFrom":makeQuery(id+"FyYUAefgu6xEfva_4.5.F14.boolean.opBoolean","SPLIT",EDGE,{"disambiguationData":[TD([subQ28])],"derivedFrom":makeQuery(id+"FyYUAefgu6xEfva_4.4.F14.boolean.opBoolean","SPLIT",EDGE,{"disambiguationData":[TD([subQ28])],"derivedFrom":makeQuery(id+"FyYUAefgu6xEfva_4.3.F14.boolean.opBoolean","SPLIT",EDGE,{"disambiguationData":[TD([subQ28])],"derivedFrom":makeQuery(id+"FyYUAefgu6xEfva_4.2.F14.boolean.opBoolean","SPLIT",EDGE,{"disambiguationData":[TD([subQ28])],"derivedFrom":makeQuery(id+"FyYUAefgu6xEfva_4.1.F14.boolean.opBoolean","SPLIT",EDGE,{"disambiguationData":[TD([subQ28])],"derivedFrom":makeQuery(id+"F12.opExtrude","CAP_EDGE",EDGE,{"disambiguationData":[OSD([subQ2])],"isStart":false})})})})})})})})})})})})})})})})})})})})})});}
            var Q352;
            Q352=makeQuery(id+"FyYUAefgu6xEfva_4.22.F14.opExtrude","SWEPT_EDGE",EDGE,{"disambiguationData":[OSD([sQuery(id+"F9.wireOp",EDGE,"E142"),sQuery(id+"F13.wireOp",EDGE,"E147")])]});
            var Q353;
            Q353=makeQuery(id+"FyYUAefgu6xEfva_4.22.F14.opExtrude","SWEPT_EDGE",EDGE,{"disambiguationData":[OSD([sQuery(id+"F11.wireOp",EDGE,"E143"),sQuery(id+"F13.wireOp",EDGE,"E147")])]});
            var Q354;
            Q354=makeQuery(id+"FyYUAefgu6xEfva_4.22.F14.opExtrude","SWEPT_EDGE",EDGE,{"disambiguationData":[OSD([sQuery(id+"F9.wireOp",EDGE,"E142"),sQuery(id+"F13.wireOp",EDGE,"E148.MirrorCS")])]});
            var Q355;
            Q355=makeQuery(id+"FyYUAefgu6xEfva_4.22.F14.opExtrude","SWEPT_EDGE",EDGE,{"disambiguationData":[OSD([sQuery(id+"F11.wireOp",EDGE,"E143"),sQuery(id+"F13.wireOp",EDGE,"E148.MirrorCS")])]});
            var Q356;
            Q356=makeQuery(id+"FyYUAefgu6xEfva_4.22.F14.opExtrude","CAP_EDGE",EDGE,{"disambiguationData":[OSD([sQuery(id+"F13.wireOp",EDGE,"E147")])],"isStart":true});
            var Q357;
            Q357=makeQuery(id+"FyYUAefgu6xEfva_4.22.F14.opExtrude","CAP_EDGE",EDGE,{"disambiguationData":[OSD([sQuery(id+"F13.wireOp",EDGE,"E148.MirrorCS")])],"isStart":true});
            var Q358;
            Q358=makeQuery(id+"FyYUAefgu6xEfva_4.22.F14.opExtrude","CAP_EDGE",EDGE,{"disambiguationData":[OSD([sQuery(id+"F9.wireOp",EDGE,"E142")])],"isStart":false});
            var Q359;
            {var subQ0=sQuery(id+"F9.wireOp",EDGE,"E142");var subQ3=sQuery(id+"F13.wireOp",EDGE,"E147");var subQ4=sQuery(id+"F13.wireOp",EDGE,"E148.MirrorCS");var subQ5=makeQuery(id+"FyYUAefgu6xEfva_4.21.F14.opExtrude","SWEPT_FACE",FACE,{"disambiguationData":[OSD([subQ4])]});var subQ6=makeQuery(id+"F14.opExtrude","SWEPT_FACE",FACE,{"disambiguationData":[OSD([subQ3])]});Q359=makeQuery(id+"FyYUAefgu6xEfva_4.22.F14.boolean.opBoolean","SPLIT",EDGE,{"disambiguationData":[TD([subQ5])],"derivedFrom":makeQuery(id+"FyYUAefgu6xEfva_4.21.F14.boolean.opBoolean","SPLIT",EDGE,{"disambiguationData":[TD([subQ6])],"derivedFrom":makeQuery(id+"FyYUAefgu6xEfva_4.20.F14.boolean.opBoolean","SPLIT",EDGE,{"disambiguationData":[TD([subQ6])],"derivedFrom":makeQuery(id+"FyYUAefgu6xEfva_4.19.F14.boolean.opBoolean","SPLIT",EDGE,{"disambiguationData":[TD([subQ6])],"derivedFrom":makeQuery(id+"FyYUAefgu6xEfva_4.18.F14.boolean.opBoolean","SPLIT",EDGE,{"disambiguationData":[TD([subQ6])],"derivedFrom":makeQuery(id+"FyYUAefgu6xEfva_4.17.F14.boolean.opBoolean","SPLIT",EDGE,{"disambiguationData":[TD([subQ6])],"derivedFrom":makeQuery(id+"FyYUAefgu6xEfva_4.16.F14.boolean.opBoolean","SPLIT",EDGE,{"disambiguationData":[TD([subQ6])],"derivedFrom":makeQuery(id+"FyYUAefgu6xEfva_4.15.F14.boolean.opBoolean","SPLIT",EDGE,{"disambiguationData":[TD([subQ6])],"derivedFrom":makeQuery(id+"FyYUAefgu6xEfva_4.14.F14.boolean.opBoolean","SPLIT",EDGE,{"disambiguationData":[TD([subQ6])],"derivedFrom":makeQuery(id+"FyYUAefgu6xEfva_4.13.F14.boolean.opBoolean","SPLIT",EDGE,{"disambiguationData":[TD([subQ6])],"derivedFrom":makeQuery(id+"FyYUAefgu6xEfva_4.12.F14.boolean.opBoolean","SPLIT",EDGE,{"disambiguationData":[TD([subQ6])],"derivedFrom":makeQuery(id+"FyYUAefgu6xEfva_4.11.F14.boolean.opBoolean","SPLIT",EDGE,{"disambiguationData":[TD([subQ6])],"derivedFrom":makeQuery(id+"FyYUAefgu6xEfva_4.10.F14.boolean.opBoolean","SPLIT",EDGE,{"disambiguationData":[TD([subQ6])],"derivedFrom":makeQuery(id+"FyYUAefgu6xEfva_4.9.F14.boolean.opBoolean","SPLIT",EDGE,{"disambiguationData":[TD([subQ6])],"derivedFrom":makeQuery(id+"FyYUAefgu6xEfva_4.8.F14.boolean.opBoolean","SPLIT",EDGE,{"disambiguationData":[TD([subQ6])],"derivedFrom":makeQuery(id+"FyYUAefgu6xEfva_4.7.F14.boolean.opBoolean","SPLIT",EDGE,{"disambiguationData":[TD([subQ6])],"derivedFrom":makeQuery(id+"FyYUAefgu6xEfva_4.6.F14.boolean.opBoolean","SPLIT",EDGE,{"disambiguationData":[TD([subQ6])],"derivedFrom":makeQuery(id+"FyYUAefgu6xEfva_4.5.F14.boolean.opBoolean","SPLIT",EDGE,{"disambiguationData":[TD([subQ6])],"derivedFrom":makeQuery(id+"FyYUAefgu6xEfva_4.4.F14.boolean.opBoolean","SPLIT",EDGE,{"disambiguationData":[TD([subQ6])],"derivedFrom":makeQuery(id+"FyYUAefgu6xEfva_4.3.F14.boolean.opBoolean","SPLIT",EDGE,{"disambiguationData":[TD([subQ6])],"derivedFrom":makeQuery(id+"FyYUAefgu6xEfva_4.2.F14.boolean.opBoolean","SPLIT",EDGE,{"disambiguationData":[TD([subQ6])],"derivedFrom":makeQuery(id+"FyYUAefgu6xEfva_4.1.F14.boolean.opBoolean","SPLIT",EDGE,{"disambiguationData":[TD([subQ6])],"derivedFrom":makeQuery(id+"F10.boolean.opBoolean","COPY",EDGE,{"derivedFrom":makeQuery(id+"F10.opExtrude","CAP_EDGE",EDGE,{"disambiguationData":[OSD([subQ0])],"isStart":false})})})})})})})})})})})})})})})})})})})})})})})});}
            var Q360;
            {var subQ0=sQuery(id+"F13.wireOp",EDGE,"E148.MirrorCS");var subQ1=sQuery(id+"F13.wireOp",EDGE,"E147");var subQ2=sQuery(id+"F11.wireOp",EDGE,"E143");var subQ28=makeQuery(id+"FyYUAefgu6xEfva_4.21.F14.opExtrude","SWEPT_FACE",FACE,{"disambiguationData":[OSD([subQ0])]});var subQ29=makeQuery(id+"F14.opExtrude","SWEPT_FACE",FACE,{"disambiguationData":[OSD([subQ1])]});Q360=makeQuery(id+"FyYUAefgu6xEfva_4.22.F14.boolean.opBoolean","SPLIT",EDGE,{"disambiguationData":[TD([subQ28])],"derivedFrom":makeQuery(id+"FyYUAefgu6xEfva_4.21.F14.boolean.opBoolean","SPLIT",EDGE,{"disambiguationData":[TD([subQ29])],"derivedFrom":makeQuery(id+"FyYUAefgu6xEfva_4.20.F14.boolean.opBoolean","SPLIT",EDGE,{"disambiguationData":[TD([subQ29])],"derivedFrom":makeQuery(id+"FyYUAefgu6xEfva_4.19.F14.boolean.opBoolean","SPLIT",EDGE,{"disambiguationData":[TD([subQ29])],"derivedFrom":makeQuery(id+"FyYUAefgu6xEfva_4.18.F14.boolean.opBoolean","SPLIT",EDGE,{"disambiguationData":[TD([subQ29])],"derivedFrom":makeQuery(id+"FyYUAefgu6xEfva_4.17.F14.boolean.opBoolean","SPLIT",EDGE,{"disambiguationData":[TD([subQ29])],"derivedFrom":makeQuery(id+"FyYUAefgu6xEfva_4.16.F14.boolean.opBoolean","SPLIT",EDGE,{"disambiguationData":[TD([subQ29])],"derivedFrom":makeQuery(id+"FyYUAefgu6xEfva_4.15.F14.boolean.opBoolean","SPLIT",EDGE,{"disambiguationData":[TD([subQ29])],"derivedFrom":makeQuery(id+"FyYUAefgu6xEfva_4.14.F14.boolean.opBoolean","SPLIT",EDGE,{"disambiguationData":[TD([subQ29])],"derivedFrom":makeQuery(id+"FyYUAefgu6xEfva_4.13.F14.boolean.opBoolean","SPLIT",EDGE,{"disambiguationData":[TD([subQ29])],"derivedFrom":makeQuery(id+"FyYUAefgu6xEfva_4.12.F14.boolean.opBoolean","SPLIT",EDGE,{"disambiguationData":[TD([subQ29])],"derivedFrom":makeQuery(id+"FyYUAefgu6xEfva_4.11.F14.boolean.opBoolean","SPLIT",EDGE,{"disambiguationData":[TD([subQ29])],"derivedFrom":makeQuery(id+"FyYUAefgu6xEfva_4.10.F14.boolean.opBoolean","SPLIT",EDGE,{"disambiguationData":[TD([subQ29])],"derivedFrom":makeQuery(id+"FyYUAefgu6xEfva_4.9.F14.boolean.opBoolean","SPLIT",EDGE,{"disambiguationData":[TD([subQ29])],"derivedFrom":makeQuery(id+"FyYUAefgu6xEfva_4.8.F14.boolean.opBoolean","SPLIT",EDGE,{"disambiguationData":[TD([subQ29])],"derivedFrom":makeQuery(id+"FyYUAefgu6xEfva_4.7.F14.boolean.opBoolean","SPLIT",EDGE,{"disambiguationData":[TD([subQ29])],"derivedFrom":makeQuery(id+"FyYUAefgu6xEfva_4.6.F14.boolean.opBoolean","SPLIT",EDGE,{"disambiguationData":[TD([subQ29])],"derivedFrom":makeQuery(id+"FyYUAefgu6xEfva_4.5.F14.boolean.opBoolean","SPLIT",EDGE,{"disambiguationData":[TD([subQ29])],"derivedFrom":makeQuery(id+"FyYUAefgu6xEfva_4.4.F14.boolean.opBoolean","SPLIT",EDGE,{"disambiguationData":[TD([subQ29])],"derivedFrom":makeQuery(id+"FyYUAefgu6xEfva_4.3.F14.boolean.opBoolean","SPLIT",EDGE,{"disambiguationData":[TD([subQ29])],"derivedFrom":makeQuery(id+"FyYUAefgu6xEfva_4.2.F14.boolean.opBoolean","SPLIT",EDGE,{"disambiguationData":[TD([subQ29])],"derivedFrom":makeQuery(id+"FyYUAefgu6xEfva_4.1.F14.boolean.opBoolean","SPLIT",EDGE,{"disambiguationData":[TD([subQ29])],"derivedFrom":makeQuery(id+"F12.opExtrude","CAP_EDGE",EDGE,{"disambiguationData":[OSD([subQ2])],"isStart":false})})})})})})})})})})})})})})})})})})})})})})});}
            var Q361;
            Q361=makeQuery(id+"FyYUAefgu6xEfva_4.23.F14.opExtrude","CAP_EDGE",EDGE,{"disambiguationData":[OSD([sQuery(id+"F13.wireOp",EDGE,"E147")])],"isStart":false});
            var Q362;
            Q362=makeQuery(id+"FyYUAefgu6xEfva_4.23.F14.opExtrude","CAP_EDGE",EDGE,{"disambiguationData":[OSD([sQuery(id+"F13.wireOp",EDGE,"E148.MirrorCS")])],"isStart":false});
            var Q363;
            Q363=makeQuery(id+"FyYUAefgu6xEfva_4.23.F14.opExtrude","CAP_EDGE",EDGE,{"disambiguationData":[OSD([sQuery(id+"F13.wireOp",EDGE,"E147")])],"isStart":true});
            var Q364;
            Q364=makeQuery(id+"FyYUAefgu6xEfva_4.23.F14.opExtrude","CAP_EDGE",EDGE,{"disambiguationData":[OSD([sQuery(id+"F9.wireOp",EDGE,"E142")])],"isStart":false});
            var Q365;
            {var subQ0=sQuery(id+"F9.wireOp",EDGE,"E142");var subQ3=sQuery(id+"F13.wireOp",EDGE,"E148.MirrorCS");var subQ4=makeQuery(id+"FyYUAefgu6xEfva_4.22.F14.opExtrude","SWEPT_FACE",FACE,{"disambiguationData":[OSD([subQ3])]});var subQ5=sQuery(id+"F13.wireOp",EDGE,"E147");var subQ6=makeQuery(id+"F14.opExtrude","SWEPT_FACE",FACE,{"disambiguationData":[OSD([subQ5])]});Q365=makeQuery(id+"FyYUAefgu6xEfva_4.23.F14.boolean.opBoolean","SPLIT",EDGE,{"disambiguationData":[TD([subQ4])],"derivedFrom":makeQuery(id+"FyYUAefgu6xEfva_4.22.F14.boolean.opBoolean","SPLIT",EDGE,{"disambiguationData":[TD([subQ6])],"derivedFrom":makeQuery(id+"FyYUAefgu6xEfva_4.21.F14.boolean.opBoolean","SPLIT",EDGE,{"disambiguationData":[TD([subQ6])],"derivedFrom":makeQuery(id+"FyYUAefgu6xEfva_4.20.F14.boolean.opBoolean","SPLIT",EDGE,{"disambiguationData":[TD([subQ6])],"derivedFrom":makeQuery(id+"FyYUAefgu6xEfva_4.19.F14.boolean.opBoolean","SPLIT",EDGE,{"disambiguationData":[TD([subQ6])],"derivedFrom":makeQuery(id+"FyYUAefgu6xEfva_4.18.F14.boolean.opBoolean","SPLIT",EDGE,{"disambiguationData":[TD([subQ6])],"derivedFrom":makeQuery(id+"FyYUAefgu6xEfva_4.17.F14.boolean.opBoolean","SPLIT",EDGE,{"disambiguationData":[TD([subQ6])],"derivedFrom":makeQuery(id+"FyYUAefgu6xEfva_4.16.F14.boolean.opBoolean","SPLIT",EDGE,{"disambiguationData":[TD([subQ6])],"derivedFrom":makeQuery(id+"FyYUAefgu6xEfva_4.15.F14.boolean.opBoolean","SPLIT",EDGE,{"disambiguationData":[TD([subQ6])],"derivedFrom":makeQuery(id+"FyYUAefgu6xEfva_4.14.F14.boolean.opBoolean","SPLIT",EDGE,{"disambiguationData":[TD([subQ6])],"derivedFrom":makeQuery(id+"FyYUAefgu6xEfva_4.13.F14.boolean.opBoolean","SPLIT",EDGE,{"disambiguationData":[TD([subQ6])],"derivedFrom":makeQuery(id+"FyYUAefgu6xEfva_4.12.F14.boolean.opBoolean","SPLIT",EDGE,{"disambiguationData":[TD([subQ6])],"derivedFrom":makeQuery(id+"FyYUAefgu6xEfva_4.11.F14.boolean.opBoolean","SPLIT",EDGE,{"disambiguationData":[TD([subQ6])],"derivedFrom":makeQuery(id+"FyYUAefgu6xEfva_4.10.F14.boolean.opBoolean","SPLIT",EDGE,{"disambiguationData":[TD([subQ6])],"derivedFrom":makeQuery(id+"FyYUAefgu6xEfva_4.9.F14.boolean.opBoolean","SPLIT",EDGE,{"disambiguationData":[TD([subQ6])],"derivedFrom":makeQuery(id+"FyYUAefgu6xEfva_4.8.F14.boolean.opBoolean","SPLIT",EDGE,{"disambiguationData":[TD([subQ6])],"derivedFrom":makeQuery(id+"FyYUAefgu6xEfva_4.7.F14.boolean.opBoolean","SPLIT",EDGE,{"disambiguationData":[TD([subQ6])],"derivedFrom":makeQuery(id+"FyYUAefgu6xEfva_4.6.F14.boolean.opBoolean","SPLIT",EDGE,{"disambiguationData":[TD([subQ6])],"derivedFrom":makeQuery(id+"FyYUAefgu6xEfva_4.5.F14.boolean.opBoolean","SPLIT",EDGE,{"disambiguationData":[TD([subQ6])],"derivedFrom":makeQuery(id+"FyYUAefgu6xEfva_4.4.F14.boolean.opBoolean","SPLIT",EDGE,{"disambiguationData":[TD([subQ6])],"derivedFrom":makeQuery(id+"FyYUAefgu6xEfva_4.3.F14.boolean.opBoolean","SPLIT",EDGE,{"disambiguationData":[TD([subQ6])],"derivedFrom":makeQuery(id+"FyYUAefgu6xEfva_4.2.F14.boolean.opBoolean","SPLIT",EDGE,{"disambiguationData":[TD([subQ6])],"derivedFrom":makeQuery(id+"FyYUAefgu6xEfva_4.1.F14.boolean.opBoolean","SPLIT",EDGE,{"disambiguationData":[TD([subQ6])],"derivedFrom":makeQuery(id+"F10.boolean.opBoolean","COPY",EDGE,{"derivedFrom":makeQuery(id+"F10.opExtrude","CAP_EDGE",EDGE,{"disambiguationData":[OSD([subQ0])],"isStart":false})})})})})})})})})})})})})})})})})})})})})})})})});}
            var Q366;
            {var subQ0=sQuery(id+"F13.wireOp",EDGE,"E148.MirrorCS");var subQ1=sQuery(id+"F13.wireOp",EDGE,"E147");var subQ2=sQuery(id+"F11.wireOp",EDGE,"E143");var subQ29=makeQuery(id+"FyYUAefgu6xEfva_4.22.F14.opExtrude","SWEPT_FACE",FACE,{"disambiguationData":[OSD([subQ0])]});var subQ30=makeQuery(id+"F14.opExtrude","SWEPT_FACE",FACE,{"disambiguationData":[OSD([subQ1])]});Q366=makeQuery(id+"FyYUAefgu6xEfva_4.23.F14.boolean.opBoolean","SPLIT",EDGE,{"disambiguationData":[TD([subQ29])],"derivedFrom":makeQuery(id+"FyYUAefgu6xEfva_4.22.F14.boolean.opBoolean","SPLIT",EDGE,{"disambiguationData":[TD([subQ30])],"derivedFrom":makeQuery(id+"FyYUAefgu6xEfva_4.21.F14.boolean.opBoolean","SPLIT",EDGE,{"disambiguationData":[TD([subQ30])],"derivedFrom":makeQuery(id+"FyYUAefgu6xEfva_4.20.F14.boolean.opBoolean","SPLIT",EDGE,{"disambiguationData":[TD([subQ30])],"derivedFrom":makeQuery(id+"FyYUAefgu6xEfva_4.19.F14.boolean.opBoolean","SPLIT",EDGE,{"disambiguationData":[TD([subQ30])],"derivedFrom":makeQuery(id+"FyYUAefgu6xEfva_4.18.F14.boolean.opBoolean","SPLIT",EDGE,{"disambiguationData":[TD([subQ30])],"derivedFrom":makeQuery(id+"FyYUAefgu6xEfva_4.17.F14.boolean.opBoolean","SPLIT",EDGE,{"disambiguationData":[TD([subQ30])],"derivedFrom":makeQuery(id+"FyYUAefgu6xEfva_4.16.F14.boolean.opBoolean","SPLIT",EDGE,{"disambiguationData":[TD([subQ30])],"derivedFrom":makeQuery(id+"FyYUAefgu6xEfva_4.15.F14.boolean.opBoolean","SPLIT",EDGE,{"disambiguationData":[TD([subQ30])],"derivedFrom":makeQuery(id+"FyYUAefgu6xEfva_4.14.F14.boolean.opBoolean","SPLIT",EDGE,{"disambiguationData":[TD([subQ30])],"derivedFrom":makeQuery(id+"FyYUAefgu6xEfva_4.13.F14.boolean.opBoolean","SPLIT",EDGE,{"disambiguationData":[TD([subQ30])],"derivedFrom":makeQuery(id+"FyYUAefgu6xEfva_4.12.F14.boolean.opBoolean","SPLIT",EDGE,{"disambiguationData":[TD([subQ30])],"derivedFrom":makeQuery(id+"FyYUAefgu6xEfva_4.11.F14.boolean.opBoolean","SPLIT",EDGE,{"disambiguationData":[TD([subQ30])],"derivedFrom":makeQuery(id+"FyYUAefgu6xEfva_4.10.F14.boolean.opBoolean","SPLIT",EDGE,{"disambiguationData":[TD([subQ30])],"derivedFrom":makeQuery(id+"FyYUAefgu6xEfva_4.9.F14.boolean.opBoolean","SPLIT",EDGE,{"disambiguationData":[TD([subQ30])],"derivedFrom":makeQuery(id+"FyYUAefgu6xEfva_4.8.F14.boolean.opBoolean","SPLIT",EDGE,{"disambiguationData":[TD([subQ30])],"derivedFrom":makeQuery(id+"FyYUAefgu6xEfva_4.7.F14.boolean.opBoolean","SPLIT",EDGE,{"disambiguationData":[TD([subQ30])],"derivedFrom":makeQuery(id+"FyYUAefgu6xEfva_4.6.F14.boolean.opBoolean","SPLIT",EDGE,{"disambiguationData":[TD([subQ30])],"derivedFrom":makeQuery(id+"FyYUAefgu6xEfva_4.5.F14.boolean.opBoolean","SPLIT",EDGE,{"disambiguationData":[TD([subQ30])],"derivedFrom":makeQuery(id+"FyYUAefgu6xEfva_4.4.F14.boolean.opBoolean","SPLIT",EDGE,{"disambiguationData":[TD([subQ30])],"derivedFrom":makeQuery(id+"FyYUAefgu6xEfva_4.3.F14.boolean.opBoolean","SPLIT",EDGE,{"disambiguationData":[TD([subQ30])],"derivedFrom":makeQuery(id+"FyYUAefgu6xEfva_4.2.F14.boolean.opBoolean","SPLIT",EDGE,{"disambiguationData":[TD([subQ30])],"derivedFrom":makeQuery(id+"FyYUAefgu6xEfva_4.1.F14.boolean.opBoolean","SPLIT",EDGE,{"disambiguationData":[TD([subQ30])],"derivedFrom":makeQuery(id+"F12.opExtrude","CAP_EDGE",EDGE,{"disambiguationData":[OSD([subQ2])],"isStart":false})})})})})})})})})})})})})})})})})})})})})})})});}
            var Q367;
            Q367=makeQuery(id+"FyYUAefgu6xEfva_4.24.F14.opExtrude","CAP_EDGE",EDGE,{"disambiguationData":[OSD([sQuery(id+"F13.wireOp",EDGE,"E147")])],"isStart":false});
            var Q368;
            Q368=makeQuery(id+"FyYUAefgu6xEfva_4.24.F14.opExtrude","SWEPT_EDGE",EDGE,{"disambiguationData":[OSD([sQuery(id+"F9.wireOp",EDGE,"E142"),sQuery(id+"F13.wireOp",EDGE,"E147")])]});
            var Q369;
            Q369=makeQuery(id+"FyYUAefgu6xEfva_4.24.F14.opExtrude","SWEPT_EDGE",EDGE,{"disambiguationData":[OSD([sQuery(id+"F11.wireOp",EDGE,"E143"),sQuery(id+"F13.wireOp",EDGE,"E147")])]});
            var Q370;
            Q370=makeQuery(id+"FyYUAefgu6xEfva_4.24.F14.opExtrude","SWEPT_EDGE",EDGE,{"disambiguationData":[OSD([sQuery(id+"F9.wireOp",EDGE,"E142"),sQuery(id+"F13.wireOp",EDGE,"E148.MirrorCS")])]});
            var Q371;
            Q371=makeQuery(id+"FyYUAefgu6xEfva_4.24.F14.opExtrude","SWEPT_EDGE",EDGE,{"disambiguationData":[OSD([sQuery(id+"F11.wireOp",EDGE,"E143"),sQuery(id+"F13.wireOp",EDGE,"E148.MirrorCS")])]});
            var Q372;
            Q372=makeQuery(id+"FyYUAefgu6xEfva_4.24.F14.opExtrude","CAP_EDGE",EDGE,{"disambiguationData":[OSD([sQuery(id+"F13.wireOp",EDGE,"E147")])],"isStart":true});
            var Q373;
            Q373=makeQuery(id+"FyYUAefgu6xEfva_4.24.F14.opExtrude","CAP_EDGE",EDGE,{"disambiguationData":[OSD([sQuery(id+"F13.wireOp",EDGE,"E148.MirrorCS")])],"isStart":true});
            var Q374;
            Q374=makeQuery(id+"FyYUAefgu6xEfva_4.24.F14.opExtrude","CAP_EDGE",EDGE,{"disambiguationData":[OSD([sQuery(id+"F9.wireOp",EDGE,"E142")])],"isStart":false});
            var Q375;
            {var subQ0=sQuery(id+"F9.wireOp",EDGE,"E142");var subQ2=sQuery(id+"F13.wireOp",EDGE,"E147");var subQ4=sQuery(id+"F13.wireOp",EDGE,"E148.MirrorCS");var subQ5=makeQuery(id+"FyYUAefgu6xEfva_4.23.F14.opExtrude","SWEPT_FACE",FACE,{"disambiguationData":[OSD([subQ4])]});var subQ6=makeQuery(id+"F14.opExtrude","SWEPT_FACE",FACE,{"disambiguationData":[OSD([subQ2])]});Q375=makeQuery(id+"FyYUAefgu6xEfva_4.24.F14.boolean.opBoolean","SPLIT",EDGE,{"disambiguationData":[TD([subQ5])],"derivedFrom":makeQuery(id+"FyYUAefgu6xEfva_4.23.F14.boolean.opBoolean","SPLIT",EDGE,{"disambiguationData":[TD([subQ6])],"derivedFrom":makeQuery(id+"FyYUAefgu6xEfva_4.22.F14.boolean.opBoolean","SPLIT",EDGE,{"disambiguationData":[TD([subQ6])],"derivedFrom":makeQuery(id+"FyYUAefgu6xEfva_4.21.F14.boolean.opBoolean","SPLIT",EDGE,{"disambiguationData":[TD([subQ6])],"derivedFrom":makeQuery(id+"FyYUAefgu6xEfva_4.20.F14.boolean.opBoolean","SPLIT",EDGE,{"disambiguationData":[TD([subQ6])],"derivedFrom":makeQuery(id+"FyYUAefgu6xEfva_4.19.F14.boolean.opBoolean","SPLIT",EDGE,{"disambiguationData":[TD([subQ6])],"derivedFrom":makeQuery(id+"FyYUAefgu6xEfva_4.18.F14.boolean.opBoolean","SPLIT",EDGE,{"disambiguationData":[TD([subQ6])],"derivedFrom":makeQuery(id+"FyYUAefgu6xEfva_4.17.F14.boolean.opBoolean","SPLIT",EDGE,{"disambiguationData":[TD([subQ6])],"derivedFrom":makeQuery(id+"FyYUAefgu6xEfva_4.16.F14.boolean.opBoolean","SPLIT",EDGE,{"disambiguationData":[TD([subQ6])],"derivedFrom":makeQuery(id+"FyYUAefgu6xEfva_4.15.F14.boolean.opBoolean","SPLIT",EDGE,{"disambiguationData":[TD([subQ6])],"derivedFrom":makeQuery(id+"FyYUAefgu6xEfva_4.14.F14.boolean.opBoolean","SPLIT",EDGE,{"disambiguationData":[TD([subQ6])],"derivedFrom":makeQuery(id+"FyYUAefgu6xEfva_4.13.F14.boolean.opBoolean","SPLIT",EDGE,{"disambiguationData":[TD([subQ6])],"derivedFrom":makeQuery(id+"FyYUAefgu6xEfva_4.12.F14.boolean.opBoolean","SPLIT",EDGE,{"disambiguationData":[TD([subQ6])],"derivedFrom":makeQuery(id+"FyYUAefgu6xEfva_4.11.F14.boolean.opBoolean","SPLIT",EDGE,{"disambiguationData":[TD([subQ6])],"derivedFrom":makeQuery(id+"FyYUAefgu6xEfva_4.10.F14.boolean.opBoolean","SPLIT",EDGE,{"disambiguationData":[TD([subQ6])],"derivedFrom":makeQuery(id+"FyYUAefgu6xEfva_4.9.F14.boolean.opBoolean","SPLIT",EDGE,{"disambiguationData":[TD([subQ6])],"derivedFrom":makeQuery(id+"FyYUAefgu6xEfva_4.8.F14.boolean.opBoolean","SPLIT",EDGE,{"disambiguationData":[TD([subQ6])],"derivedFrom":makeQuery(id+"FyYUAefgu6xEfva_4.7.F14.boolean.opBoolean","SPLIT",EDGE,{"disambiguationData":[TD([subQ6])],"derivedFrom":makeQuery(id+"FyYUAefgu6xEfva_4.6.F14.boolean.opBoolean","SPLIT",EDGE,{"disambiguationData":[TD([subQ6])],"derivedFrom":makeQuery(id+"FyYUAefgu6xEfva_4.5.F14.boolean.opBoolean","SPLIT",EDGE,{"disambiguationData":[TD([subQ6])],"derivedFrom":makeQuery(id+"FyYUAefgu6xEfva_4.4.F14.boolean.opBoolean","SPLIT",EDGE,{"disambiguationData":[TD([subQ6])],"derivedFrom":makeQuery(id+"FyYUAefgu6xEfva_4.3.F14.boolean.opBoolean","SPLIT",EDGE,{"disambiguationData":[TD([subQ6])],"derivedFrom":makeQuery(id+"FyYUAefgu6xEfva_4.2.F14.boolean.opBoolean","SPLIT",EDGE,{"disambiguationData":[TD([subQ6])],"derivedFrom":makeQuery(id+"FyYUAefgu6xEfva_4.1.F14.boolean.opBoolean","SPLIT",EDGE,{"disambiguationData":[TD([subQ6])],"derivedFrom":makeQuery(id+"F10.boolean.opBoolean","COPY",EDGE,{"derivedFrom":makeQuery(id+"F10.opExtrude","CAP_EDGE",EDGE,{"disambiguationData":[OSD([subQ0])],"isStart":false})})})})})})})})})})})})})})})})})})})})})})})})})});}
            var Q376;
            {var subQ0=sQuery(id+"F13.wireOp",EDGE,"E148.MirrorCS");var subQ1=sQuery(id+"F13.wireOp",EDGE,"E147");var subQ2=sQuery(id+"F11.wireOp",EDGE,"E143");var subQ30=makeQuery(id+"FyYUAefgu6xEfva_4.23.F14.opExtrude","SWEPT_FACE",FACE,{"disambiguationData":[OSD([subQ0])]});var subQ31=makeQuery(id+"F14.opExtrude","SWEPT_FACE",FACE,{"disambiguationData":[OSD([subQ1])]});Q376=makeQuery(id+"FyYUAefgu6xEfva_4.24.F14.boolean.opBoolean","SPLIT",EDGE,{"disambiguationData":[TD([subQ30])],"derivedFrom":makeQuery(id+"FyYUAefgu6xEfva_4.23.F14.boolean.opBoolean","SPLIT",EDGE,{"disambiguationData":[TD([subQ31])],"derivedFrom":makeQuery(id+"FyYUAefgu6xEfva_4.22.F14.boolean.opBoolean","SPLIT",EDGE,{"disambiguationData":[TD([subQ31])],"derivedFrom":makeQuery(id+"FyYUAefgu6xEfva_4.21.F14.boolean.opBoolean","SPLIT",EDGE,{"disambiguationData":[TD([subQ31])],"derivedFrom":makeQuery(id+"FyYUAefgu6xEfva_4.20.F14.boolean.opBoolean","SPLIT",EDGE,{"disambiguationData":[TD([subQ31])],"derivedFrom":makeQuery(id+"FyYUAefgu6xEfva_4.19.F14.boolean.opBoolean","SPLIT",EDGE,{"disambiguationData":[TD([subQ31])],"derivedFrom":makeQuery(id+"FyYUAefgu6xEfva_4.18.F14.boolean.opBoolean","SPLIT",EDGE,{"disambiguationData":[TD([subQ31])],"derivedFrom":makeQuery(id+"FyYUAefgu6xEfva_4.17.F14.boolean.opBoolean","SPLIT",EDGE,{"disambiguationData":[TD([subQ31])],"derivedFrom":makeQuery(id+"FyYUAefgu6xEfva_4.16.F14.boolean.opBoolean","SPLIT",EDGE,{"disambiguationData":[TD([subQ31])],"derivedFrom":makeQuery(id+"FyYUAefgu6xEfva_4.15.F14.boolean.opBoolean","SPLIT",EDGE,{"disambiguationData":[TD([subQ31])],"derivedFrom":makeQuery(id+"FyYUAefgu6xEfva_4.14.F14.boolean.opBoolean","SPLIT",EDGE,{"disambiguationData":[TD([subQ31])],"derivedFrom":makeQuery(id+"FyYUAefgu6xEfva_4.13.F14.boolean.opBoolean","SPLIT",EDGE,{"disambiguationData":[TD([subQ31])],"derivedFrom":makeQuery(id+"FyYUAefgu6xEfva_4.12.F14.boolean.opBoolean","SPLIT",EDGE,{"disambiguationData":[TD([subQ31])],"derivedFrom":makeQuery(id+"FyYUAefgu6xEfva_4.11.F14.boolean.opBoolean","SPLIT",EDGE,{"disambiguationData":[TD([subQ31])],"derivedFrom":makeQuery(id+"FyYUAefgu6xEfva_4.10.F14.boolean.opBoolean","SPLIT",EDGE,{"disambiguationData":[TD([subQ31])],"derivedFrom":makeQuery(id+"FyYUAefgu6xEfva_4.9.F14.boolean.opBoolean","SPLIT",EDGE,{"disambiguationData":[TD([subQ31])],"derivedFrom":makeQuery(id+"FyYUAefgu6xEfva_4.8.F14.boolean.opBoolean","SPLIT",EDGE,{"disambiguationData":[TD([subQ31])],"derivedFrom":makeQuery(id+"FyYUAefgu6xEfva_4.7.F14.boolean.opBoolean","SPLIT",EDGE,{"disambiguationData":[TD([subQ31])],"derivedFrom":makeQuery(id+"FyYUAefgu6xEfva_4.6.F14.boolean.opBoolean","SPLIT",EDGE,{"disambiguationData":[TD([subQ31])],"derivedFrom":makeQuery(id+"FyYUAefgu6xEfva_4.5.F14.boolean.opBoolean","SPLIT",EDGE,{"disambiguationData":[TD([subQ31])],"derivedFrom":makeQuery(id+"FyYUAefgu6xEfva_4.4.F14.boolean.opBoolean","SPLIT",EDGE,{"disambiguationData":[TD([subQ31])],"derivedFrom":makeQuery(id+"FyYUAefgu6xEfva_4.3.F14.boolean.opBoolean","SPLIT",EDGE,{"disambiguationData":[TD([subQ31])],"derivedFrom":makeQuery(id+"FyYUAefgu6xEfva_4.2.F14.boolean.opBoolean","SPLIT",EDGE,{"disambiguationData":[TD([subQ31])],"derivedFrom":makeQuery(id+"FyYUAefgu6xEfva_4.1.F14.boolean.opBoolean","SPLIT",EDGE,{"disambiguationData":[TD([subQ31])],"derivedFrom":makeQuery(id+"F12.opExtrude","CAP_EDGE",EDGE,{"disambiguationData":[OSD([subQ2])],"isStart":false})})})})})})})})})})})})})})})})})})})})})})})})});}
            var Q377;
            Q377=makeQuery(id+"FyYUAefgu6xEfva_4.25.F14.opExtrude","SWEPT_EDGE",EDGE,{"disambiguationData":[OSD([sQuery(id+"F9.wireOp",EDGE,"E142"),sQuery(id+"F13.wireOp",EDGE,"E147")])]});
            var Q378;
            Q378=makeQuery(id+"FyYUAefgu6xEfva_4.25.F14.opExtrude","SWEPT_EDGE",EDGE,{"disambiguationData":[OSD([sQuery(id+"F11.wireOp",EDGE,"E143"),sQuery(id+"F13.wireOp",EDGE,"E147")])]});
            var Q379;
            Q379=makeQuery(id+"FyYUAefgu6xEfva_4.25.F14.opExtrude","SWEPT_EDGE",EDGE,{"disambiguationData":[OSD([sQuery(id+"F9.wireOp",EDGE,"E142"),sQuery(id+"F13.wireOp",EDGE,"E148.MirrorCS")])]});
            var Q380;
            Q380=makeQuery(id+"FyYUAefgu6xEfva_4.25.F14.opExtrude","SWEPT_EDGE",EDGE,{"disambiguationData":[OSD([sQuery(id+"F11.wireOp",EDGE,"E143"),sQuery(id+"F13.wireOp",EDGE,"E148.MirrorCS")])]});
            var Q381;
            Q381=makeQuery(id+"FyYUAefgu6xEfva_4.25.F14.opExtrude","CAP_EDGE",EDGE,{"disambiguationData":[OSD([sQuery(id+"F13.wireOp",EDGE,"E148.MirrorCS")])],"isStart":true});
            var Q382;
            Q382=makeQuery(id+"FyYUAefgu6xEfva_4.25.F14.opExtrude","CAP_EDGE",EDGE,{"disambiguationData":[OSD([sQuery(id+"F9.wireOp",EDGE,"E142")])],"isStart":false});
            var Q383;
            {var subQ0=sQuery(id+"F9.wireOp",EDGE,"E142");var subQ3=sQuery(id+"F13.wireOp",EDGE,"E148.MirrorCS");var subQ4=makeQuery(id+"FyYUAefgu6xEfva_4.24.F14.opExtrude","SWEPT_FACE",FACE,{"disambiguationData":[OSD([subQ3])]});var subQ5=sQuery(id+"F13.wireOp",EDGE,"E147");var subQ6=makeQuery(id+"F14.opExtrude","SWEPT_FACE",FACE,{"disambiguationData":[OSD([subQ5])]});Q383=makeQuery(id+"FyYUAefgu6xEfva_4.25.F14.boolean.opBoolean","SPLIT",EDGE,{"disambiguationData":[TD([subQ4])],"derivedFrom":makeQuery(id+"FyYUAefgu6xEfva_4.24.F14.boolean.opBoolean","SPLIT",EDGE,{"disambiguationData":[TD([subQ6])],"derivedFrom":makeQuery(id+"FyYUAefgu6xEfva_4.23.F14.boolean.opBoolean","SPLIT",EDGE,{"disambiguationData":[TD([subQ6])],"derivedFrom":makeQuery(id+"FyYUAefgu6xEfva_4.22.F14.boolean.opBoolean","SPLIT",EDGE,{"disambiguationData":[TD([subQ6])],"derivedFrom":makeQuery(id+"FyYUAefgu6xEfva_4.21.F14.boolean.opBoolean","SPLIT",EDGE,{"disambiguationData":[TD([subQ6])],"derivedFrom":makeQuery(id+"FyYUAefgu6xEfva_4.20.F14.boolean.opBoolean","SPLIT",EDGE,{"disambiguationData":[TD([subQ6])],"derivedFrom":makeQuery(id+"FyYUAefgu6xEfva_4.19.F14.boolean.opBoolean","SPLIT",EDGE,{"disambiguationData":[TD([subQ6])],"derivedFrom":makeQuery(id+"FyYUAefgu6xEfva_4.18.F14.boolean.opBoolean","SPLIT",EDGE,{"disambiguationData":[TD([subQ6])],"derivedFrom":makeQuery(id+"FyYUAefgu6xEfva_4.17.F14.boolean.opBoolean","SPLIT",EDGE,{"disambiguationData":[TD([subQ6])],"derivedFrom":makeQuery(id+"FyYUAefgu6xEfva_4.16.F14.boolean.opBoolean","SPLIT",EDGE,{"disambiguationData":[TD([subQ6])],"derivedFrom":makeQuery(id+"FyYUAefgu6xEfva_4.15.F14.boolean.opBoolean","SPLIT",EDGE,{"disambiguationData":[TD([subQ6])],"derivedFrom":makeQuery(id+"FyYUAefgu6xEfva_4.14.F14.boolean.opBoolean","SPLIT",EDGE,{"disambiguationData":[TD([subQ6])],"derivedFrom":makeQuery(id+"FyYUAefgu6xEfva_4.13.F14.boolean.opBoolean","SPLIT",EDGE,{"disambiguationData":[TD([subQ6])],"derivedFrom":makeQuery(id+"FyYUAefgu6xEfva_4.12.F14.boolean.opBoolean","SPLIT",EDGE,{"disambiguationData":[TD([subQ6])],"derivedFrom":makeQuery(id+"FyYUAefgu6xEfva_4.11.F14.boolean.opBoolean","SPLIT",EDGE,{"disambiguationData":[TD([subQ6])],"derivedFrom":makeQuery(id+"FyYUAefgu6xEfva_4.10.F14.boolean.opBoolean","SPLIT",EDGE,{"disambiguationData":[TD([subQ6])],"derivedFrom":makeQuery(id+"FyYUAefgu6xEfva_4.9.F14.boolean.opBoolean","SPLIT",EDGE,{"disambiguationData":[TD([subQ6])],"derivedFrom":makeQuery(id+"FyYUAefgu6xEfva_4.8.F14.boolean.opBoolean","SPLIT",EDGE,{"disambiguationData":[TD([subQ6])],"derivedFrom":makeQuery(id+"FyYUAefgu6xEfva_4.7.F14.boolean.opBoolean","SPLIT",EDGE,{"disambiguationData":[TD([subQ6])],"derivedFrom":makeQuery(id+"FyYUAefgu6xEfva_4.6.F14.boolean.opBoolean","SPLIT",EDGE,{"disambiguationData":[TD([subQ6])],"derivedFrom":makeQuery(id+"FyYUAefgu6xEfva_4.5.F14.boolean.opBoolean","SPLIT",EDGE,{"disambiguationData":[TD([subQ6])],"derivedFrom":makeQuery(id+"FyYUAefgu6xEfva_4.4.F14.boolean.opBoolean","SPLIT",EDGE,{"disambiguationData":[TD([subQ6])],"derivedFrom":makeQuery(id+"FyYUAefgu6xEfva_4.3.F14.boolean.opBoolean","SPLIT",EDGE,{"disambiguationData":[TD([subQ6])],"derivedFrom":makeQuery(id+"FyYUAefgu6xEfva_4.2.F14.boolean.opBoolean","SPLIT",EDGE,{"disambiguationData":[TD([subQ6])],"derivedFrom":makeQuery(id+"FyYUAefgu6xEfva_4.1.F14.boolean.opBoolean","SPLIT",EDGE,{"disambiguationData":[TD([subQ6])],"derivedFrom":makeQuery(id+"F10.boolean.opBoolean","COPY",EDGE,{"derivedFrom":makeQuery(id+"F10.opExtrude","CAP_EDGE",EDGE,{"disambiguationData":[OSD([subQ0])],"isStart":false})})})})})})})})})})})})})})})})})})})})})})})})})})});}
            var Q384;
            {var subQ0=sQuery(id+"F13.wireOp",EDGE,"E148.MirrorCS");var subQ1=sQuery(id+"F13.wireOp",EDGE,"E147");var subQ2=sQuery(id+"F11.wireOp",EDGE,"E143");var subQ31=makeQuery(id+"FyYUAefgu6xEfva_4.24.F14.opExtrude","SWEPT_FACE",FACE,{"disambiguationData":[OSD([subQ0])]});var subQ32=makeQuery(id+"F14.opExtrude","SWEPT_FACE",FACE,{"disambiguationData":[OSD([subQ1])]});Q384=makeQuery(id+"FyYUAefgu6xEfva_4.25.F14.boolean.opBoolean","SPLIT",EDGE,{"disambiguationData":[TD([subQ31])],"derivedFrom":makeQuery(id+"FyYUAefgu6xEfva_4.24.F14.boolean.opBoolean","SPLIT",EDGE,{"disambiguationData":[TD([subQ32])],"derivedFrom":makeQuery(id+"FyYUAefgu6xEfva_4.23.F14.boolean.opBoolean","SPLIT",EDGE,{"disambiguationData":[TD([subQ32])],"derivedFrom":makeQuery(id+"FyYUAefgu6xEfva_4.22.F14.boolean.opBoolean","SPLIT",EDGE,{"disambiguationData":[TD([subQ32])],"derivedFrom":makeQuery(id+"FyYUAefgu6xEfva_4.21.F14.boolean.opBoolean","SPLIT",EDGE,{"disambiguationData":[TD([subQ32])],"derivedFrom":makeQuery(id+"FyYUAefgu6xEfva_4.20.F14.boolean.opBoolean","SPLIT",EDGE,{"disambiguationData":[TD([subQ32])],"derivedFrom":makeQuery(id+"FyYUAefgu6xEfva_4.19.F14.boolean.opBoolean","SPLIT",EDGE,{"disambiguationData":[TD([subQ32])],"derivedFrom":makeQuery(id+"FyYUAefgu6xEfva_4.18.F14.boolean.opBoolean","SPLIT",EDGE,{"disambiguationData":[TD([subQ32])],"derivedFrom":makeQuery(id+"FyYUAefgu6xEfva_4.17.F14.boolean.opBoolean","SPLIT",EDGE,{"disambiguationData":[TD([subQ32])],"derivedFrom":makeQuery(id+"FyYUAefgu6xEfva_4.16.F14.boolean.opBoolean","SPLIT",EDGE,{"disambiguationData":[TD([subQ32])],"derivedFrom":makeQuery(id+"FyYUAefgu6xEfva_4.15.F14.boolean.opBoolean","SPLIT",EDGE,{"disambiguationData":[TD([subQ32])],"derivedFrom":makeQuery(id+"FyYUAefgu6xEfva_4.14.F14.boolean.opBoolean","SPLIT",EDGE,{"disambiguationData":[TD([subQ32])],"derivedFrom":makeQuery(id+"FyYUAefgu6xEfva_4.13.F14.boolean.opBoolean","SPLIT",EDGE,{"disambiguationData":[TD([subQ32])],"derivedFrom":makeQuery(id+"FyYUAefgu6xEfva_4.12.F14.boolean.opBoolean","SPLIT",EDGE,{"disambiguationData":[TD([subQ32])],"derivedFrom":makeQuery(id+"FyYUAefgu6xEfva_4.11.F14.boolean.opBoolean","SPLIT",EDGE,{"disambiguationData":[TD([subQ32])],"derivedFrom":makeQuery(id+"FyYUAefgu6xEfva_4.10.F14.boolean.opBoolean","SPLIT",EDGE,{"disambiguationData":[TD([subQ32])],"derivedFrom":makeQuery(id+"FyYUAefgu6xEfva_4.9.F14.boolean.opBoolean","SPLIT",EDGE,{"disambiguationData":[TD([subQ32])],"derivedFrom":makeQuery(id+"FyYUAefgu6xEfva_4.8.F14.boolean.opBoolean","SPLIT",EDGE,{"disambiguationData":[TD([subQ32])],"derivedFrom":makeQuery(id+"FyYUAefgu6xEfva_4.7.F14.boolean.opBoolean","SPLIT",EDGE,{"disambiguationData":[TD([subQ32])],"derivedFrom":makeQuery(id+"FyYUAefgu6xEfva_4.6.F14.boolean.opBoolean","SPLIT",EDGE,{"disambiguationData":[TD([subQ32])],"derivedFrom":makeQuery(id+"FyYUAefgu6xEfva_4.5.F14.boolean.opBoolean","SPLIT",EDGE,{"disambiguationData":[TD([subQ32])],"derivedFrom":makeQuery(id+"FyYUAefgu6xEfva_4.4.F14.boolean.opBoolean","SPLIT",EDGE,{"disambiguationData":[TD([subQ32])],"derivedFrom":makeQuery(id+"FyYUAefgu6xEfva_4.3.F14.boolean.opBoolean","SPLIT",EDGE,{"disambiguationData":[TD([subQ32])],"derivedFrom":makeQuery(id+"FyYUAefgu6xEfva_4.2.F14.boolean.opBoolean","SPLIT",EDGE,{"disambiguationData":[TD([subQ32])],"derivedFrom":makeQuery(id+"FyYUAefgu6xEfva_4.1.F14.boolean.opBoolean","SPLIT",EDGE,{"disambiguationData":[TD([subQ32])],"derivedFrom":makeQuery(id+"F12.opExtrude","CAP_EDGE",EDGE,{"disambiguationData":[OSD([subQ2])],"isStart":false})})})})})})})})})})})})})})})})})})})})})})})})})});}
            var Q385;
            Q385=makeQuery(id+"FyYUAefgu6xEfva_4.26.F14.opExtrude","CAP_EDGE",EDGE,{"disambiguationData":[OSD([sQuery(id+"F13.wireOp",EDGE,"E147")])],"isStart":false});
            var Q386;
            Q386=makeQuery(id+"FyYUAefgu6xEfva_4.26.F14.opExtrude","SWEPT_EDGE",EDGE,{"disambiguationData":[OSD([sQuery(id+"F9.wireOp",EDGE,"E142"),sQuery(id+"F13.wireOp",EDGE,"E147")])]});
            var Q387;
            Q387=makeQuery(id+"FyYUAefgu6xEfva_4.26.F14.opExtrude","SWEPT_EDGE",EDGE,{"disambiguationData":[OSD([sQuery(id+"F11.wireOp",EDGE,"E143"),sQuery(id+"F13.wireOp",EDGE,"E147")])]});
            var Q388;
            Q388=makeQuery(id+"FyYUAefgu6xEfva_4.26.F14.opExtrude","SWEPT_EDGE",EDGE,{"disambiguationData":[OSD([sQuery(id+"F9.wireOp",EDGE,"E142"),sQuery(id+"F13.wireOp",EDGE,"E148.MirrorCS")])]});
            var Q389;
            Q389=makeQuery(id+"FyYUAefgu6xEfva_4.26.F14.opExtrude","SWEPT_EDGE",EDGE,{"disambiguationData":[OSD([sQuery(id+"F11.wireOp",EDGE,"E143"),sQuery(id+"F13.wireOp",EDGE,"E148.MirrorCS")])]});
            var Q390;
            Q390=makeQuery(id+"FyYUAefgu6xEfva_4.26.F14.opExtrude","CAP_EDGE",EDGE,{"disambiguationData":[OSD([sQuery(id+"F13.wireOp",EDGE,"E147")])],"isStart":true});
            var Q391;
            Q391=makeQuery(id+"FyYUAefgu6xEfva_4.26.F14.opExtrude","CAP_EDGE",EDGE,{"disambiguationData":[OSD([sQuery(id+"F13.wireOp",EDGE,"E148.MirrorCS")])],"isStart":true});
            var Q392;
            Q392=makeQuery(id+"FyYUAefgu6xEfva_4.26.F14.opExtrude","CAP_EDGE",EDGE,{"disambiguationData":[OSD([sQuery(id+"F9.wireOp",EDGE,"E142")])],"isStart":false});
            var Q393;
            {var subQ0=sQuery(id+"F9.wireOp",EDGE,"E142");var subQ2=sQuery(id+"F13.wireOp",EDGE,"E148.MirrorCS");var subQ3=makeQuery(id+"FyYUAefgu6xEfva_4.25.F14.opExtrude","SWEPT_FACE",FACE,{"disambiguationData":[OSD([subQ2])]});var subQ5=sQuery(id+"F13.wireOp",EDGE,"E147");var subQ6=makeQuery(id+"F14.opExtrude","SWEPT_FACE",FACE,{"disambiguationData":[OSD([subQ5])]});Q393=makeQuery(id+"FyYUAefgu6xEfva_4.26.F14.boolean.opBoolean","SPLIT",EDGE,{"disambiguationData":[TD([subQ3])],"derivedFrom":makeQuery(id+"FyYUAefgu6xEfva_4.25.F14.boolean.opBoolean","SPLIT",EDGE,{"disambiguationData":[TD([subQ6])],"derivedFrom":makeQuery(id+"FyYUAefgu6xEfva_4.24.F14.boolean.opBoolean","SPLIT",EDGE,{"disambiguationData":[TD([subQ6])],"derivedFrom":makeQuery(id+"FyYUAefgu6xEfva_4.23.F14.boolean.opBoolean","SPLIT",EDGE,{"disambiguationData":[TD([subQ6])],"derivedFrom":makeQuery(id+"FyYUAefgu6xEfva_4.22.F14.boolean.opBoolean","SPLIT",EDGE,{"disambiguationData":[TD([subQ6])],"derivedFrom":makeQuery(id+"FyYUAefgu6xEfva_4.21.F14.boolean.opBoolean","SPLIT",EDGE,{"disambiguationData":[TD([subQ6])],"derivedFrom":makeQuery(id+"FyYUAefgu6xEfva_4.20.F14.boolean.opBoolean","SPLIT",EDGE,{"disambiguationData":[TD([subQ6])],"derivedFrom":makeQuery(id+"FyYUAefgu6xEfva_4.19.F14.boolean.opBoolean","SPLIT",EDGE,{"disambiguationData":[TD([subQ6])],"derivedFrom":makeQuery(id+"FyYUAefgu6xEfva_4.18.F14.boolean.opBoolean","SPLIT",EDGE,{"disambiguationData":[TD([subQ6])],"derivedFrom":makeQuery(id+"FyYUAefgu6xEfva_4.17.F14.boolean.opBoolean","SPLIT",EDGE,{"disambiguationData":[TD([subQ6])],"derivedFrom":makeQuery(id+"FyYUAefgu6xEfva_4.16.F14.boolean.opBoolean","SPLIT",EDGE,{"disambiguationData":[TD([subQ6])],"derivedFrom":makeQuery(id+"FyYUAefgu6xEfva_4.15.F14.boolean.opBoolean","SPLIT",EDGE,{"disambiguationData":[TD([subQ6])],"derivedFrom":makeQuery(id+"FyYUAefgu6xEfva_4.14.F14.boolean.opBoolean","SPLIT",EDGE,{"disambiguationData":[TD([subQ6])],"derivedFrom":makeQuery(id+"FyYUAefgu6xEfva_4.13.F14.boolean.opBoolean","SPLIT",EDGE,{"disambiguationData":[TD([subQ6])],"derivedFrom":makeQuery(id+"FyYUAefgu6xEfva_4.12.F14.boolean.opBoolean","SPLIT",EDGE,{"disambiguationData":[TD([subQ6])],"derivedFrom":makeQuery(id+"FyYUAefgu6xEfva_4.11.F14.boolean.opBoolean","SPLIT",EDGE,{"disambiguationData":[TD([subQ6])],"derivedFrom":makeQuery(id+"FyYUAefgu6xEfva_4.10.F14.boolean.opBoolean","SPLIT",EDGE,{"disambiguationData":[TD([subQ6])],"derivedFrom":makeQuery(id+"FyYUAefgu6xEfva_4.9.F14.boolean.opBoolean","SPLIT",EDGE,{"disambiguationData":[TD([subQ6])],"derivedFrom":makeQuery(id+"FyYUAefgu6xEfva_4.8.F14.boolean.opBoolean","SPLIT",EDGE,{"disambiguationData":[TD([subQ6])],"derivedFrom":makeQuery(id+"FyYUAefgu6xEfva_4.7.F14.boolean.opBoolean","SPLIT",EDGE,{"disambiguationData":[TD([subQ6])],"derivedFrom":makeQuery(id+"FyYUAefgu6xEfva_4.6.F14.boolean.opBoolean","SPLIT",EDGE,{"disambiguationData":[TD([subQ6])],"derivedFrom":makeQuery(id+"FyYUAefgu6xEfva_4.5.F14.boolean.opBoolean","SPLIT",EDGE,{"disambiguationData":[TD([subQ6])],"derivedFrom":makeQuery(id+"FyYUAefgu6xEfva_4.4.F14.boolean.opBoolean","SPLIT",EDGE,{"disambiguationData":[TD([subQ6])],"derivedFrom":makeQuery(id+"FyYUAefgu6xEfva_4.3.F14.boolean.opBoolean","SPLIT",EDGE,{"disambiguationData":[TD([subQ6])],"derivedFrom":makeQuery(id+"FyYUAefgu6xEfva_4.2.F14.boolean.opBoolean","SPLIT",EDGE,{"disambiguationData":[TD([subQ6])],"derivedFrom":makeQuery(id+"FyYUAefgu6xEfva_4.1.F14.boolean.opBoolean","SPLIT",EDGE,{"disambiguationData":[TD([subQ6])],"derivedFrom":makeQuery(id+"F10.boolean.opBoolean","COPY",EDGE,{"derivedFrom":makeQuery(id+"F10.opExtrude","CAP_EDGE",EDGE,{"disambiguationData":[OSD([subQ0])],"isStart":false})})})})})})})})})})})})})})})})})})})})})})})})})})})});}
            var Q394;
            {var subQ0=sQuery(id+"F13.wireOp",EDGE,"E148.MirrorCS");var subQ1=sQuery(id+"F13.wireOp",EDGE,"E147");var subQ2=sQuery(id+"F11.wireOp",EDGE,"E143");var subQ32=makeQuery(id+"FyYUAefgu6xEfva_4.25.F14.opExtrude","SWEPT_FACE",FACE,{"disambiguationData":[OSD([subQ0])]});var subQ33=makeQuery(id+"F14.opExtrude","SWEPT_FACE",FACE,{"disambiguationData":[OSD([subQ1])]});Q394=makeQuery(id+"FyYUAefgu6xEfva_4.26.F14.boolean.opBoolean","SPLIT",EDGE,{"disambiguationData":[TD([subQ32])],"derivedFrom":makeQuery(id+"FyYUAefgu6xEfva_4.25.F14.boolean.opBoolean","SPLIT",EDGE,{"disambiguationData":[TD([subQ33])],"derivedFrom":makeQuery(id+"FyYUAefgu6xEfva_4.24.F14.boolean.opBoolean","SPLIT",EDGE,{"disambiguationData":[TD([subQ33])],"derivedFrom":makeQuery(id+"FyYUAefgu6xEfva_4.23.F14.boolean.opBoolean","SPLIT",EDGE,{"disambiguationData":[TD([subQ33])],"derivedFrom":makeQuery(id+"FyYUAefgu6xEfva_4.22.F14.boolean.opBoolean","SPLIT",EDGE,{"disambiguationData":[TD([subQ33])],"derivedFrom":makeQuery(id+"FyYUAefgu6xEfva_4.21.F14.boolean.opBoolean","SPLIT",EDGE,{"disambiguationData":[TD([subQ33])],"derivedFrom":makeQuery(id+"FyYUAefgu6xEfva_4.20.F14.boolean.opBoolean","SPLIT",EDGE,{"disambiguationData":[TD([subQ33])],"derivedFrom":makeQuery(id+"FyYUAefgu6xEfva_4.19.F14.boolean.opBoolean","SPLIT",EDGE,{"disambiguationData":[TD([subQ33])],"derivedFrom":makeQuery(id+"FyYUAefgu6xEfva_4.18.F14.boolean.opBoolean","SPLIT",EDGE,{"disambiguationData":[TD([subQ33])],"derivedFrom":makeQuery(id+"FyYUAefgu6xEfva_4.17.F14.boolean.opBoolean","SPLIT",EDGE,{"disambiguationData":[TD([subQ33])],"derivedFrom":makeQuery(id+"FyYUAefgu6xEfva_4.16.F14.boolean.opBoolean","SPLIT",EDGE,{"disambiguationData":[TD([subQ33])],"derivedFrom":makeQuery(id+"FyYUAefgu6xEfva_4.15.F14.boolean.opBoolean","SPLIT",EDGE,{"disambiguationData":[TD([subQ33])],"derivedFrom":makeQuery(id+"FyYUAefgu6xEfva_4.14.F14.boolean.opBoolean","SPLIT",EDGE,{"disambiguationData":[TD([subQ33])],"derivedFrom":makeQuery(id+"FyYUAefgu6xEfva_4.13.F14.boolean.opBoolean","SPLIT",EDGE,{"disambiguationData":[TD([subQ33])],"derivedFrom":makeQuery(id+"FyYUAefgu6xEfva_4.12.F14.boolean.opBoolean","SPLIT",EDGE,{"disambiguationData":[TD([subQ33])],"derivedFrom":makeQuery(id+"FyYUAefgu6xEfva_4.11.F14.boolean.opBoolean","SPLIT",EDGE,{"disambiguationData":[TD([subQ33])],"derivedFrom":makeQuery(id+"FyYUAefgu6xEfva_4.10.F14.boolean.opBoolean","SPLIT",EDGE,{"disambiguationData":[TD([subQ33])],"derivedFrom":makeQuery(id+"FyYUAefgu6xEfva_4.9.F14.boolean.opBoolean","SPLIT",EDGE,{"disambiguationData":[TD([subQ33])],"derivedFrom":makeQuery(id+"FyYUAefgu6xEfva_4.8.F14.boolean.opBoolean","SPLIT",EDGE,{"disambiguationData":[TD([subQ33])],"derivedFrom":makeQuery(id+"FyYUAefgu6xEfva_4.7.F14.boolean.opBoolean","SPLIT",EDGE,{"disambiguationData":[TD([subQ33])],"derivedFrom":makeQuery(id+"FyYUAefgu6xEfva_4.6.F14.boolean.opBoolean","SPLIT",EDGE,{"disambiguationData":[TD([subQ33])],"derivedFrom":makeQuery(id+"FyYUAefgu6xEfva_4.5.F14.boolean.opBoolean","SPLIT",EDGE,{"disambiguationData":[TD([subQ33])],"derivedFrom":makeQuery(id+"FyYUAefgu6xEfva_4.4.F14.boolean.opBoolean","SPLIT",EDGE,{"disambiguationData":[TD([subQ33])],"derivedFrom":makeQuery(id+"FyYUAefgu6xEfva_4.3.F14.boolean.opBoolean","SPLIT",EDGE,{"disambiguationData":[TD([subQ33])],"derivedFrom":makeQuery(id+"FyYUAefgu6xEfva_4.2.F14.boolean.opBoolean","SPLIT",EDGE,{"disambiguationData":[TD([subQ33])],"derivedFrom":makeQuery(id+"FyYUAefgu6xEfva_4.1.F14.boolean.opBoolean","SPLIT",EDGE,{"disambiguationData":[TD([subQ33])],"derivedFrom":makeQuery(id+"F12.opExtrude","CAP_EDGE",EDGE,{"disambiguationData":[OSD([subQ2])],"isStart":false})})})})})})})})})})})})})})})})})})})})})})})})})})});}
            var Q395;
            Q395=makeQuery(id+"FyYUAefgu6xEfva_4.27.F14.opExtrude","SWEPT_EDGE",EDGE,{"disambiguationData":[OSD([sQuery(id+"F9.wireOp",EDGE,"E142"),sQuery(id+"F13.wireOp",EDGE,"E147")])]});
            var Q396;
            Q396=makeQuery(id+"FyYUAefgu6xEfva_4.27.F14.opExtrude","SWEPT_EDGE",EDGE,{"disambiguationData":[OSD([sQuery(id+"F11.wireOp",EDGE,"E143"),sQuery(id+"F13.wireOp",EDGE,"E147")])]});
            var Q397;
            Q397=makeQuery(id+"FyYUAefgu6xEfva_4.27.F14.opExtrude","SWEPT_EDGE",EDGE,{"disambiguationData":[OSD([sQuery(id+"F9.wireOp",EDGE,"E142"),sQuery(id+"F13.wireOp",EDGE,"E148.MirrorCS")])]});
            var Q398;
            Q398=makeQuery(id+"FyYUAefgu6xEfva_4.27.F14.opExtrude","SWEPT_EDGE",EDGE,{"disambiguationData":[OSD([sQuery(id+"F11.wireOp",EDGE,"E143"),sQuery(id+"F13.wireOp",EDGE,"E148.MirrorCS")])]});
            var Q399;
            Q399=makeQuery(id+"FyYUAefgu6xEfva_4.27.F14.opExtrude","CAP_EDGE",EDGE,{"disambiguationData":[OSD([sQuery(id+"F13.wireOp",EDGE,"E148.MirrorCS")])],"isStart":true});
            var Q400;
            Q400=makeQuery(id+"FyYUAefgu6xEfva_4.27.F14.opExtrude","CAP_EDGE",EDGE,{"disambiguationData":[OSD([sQuery(id+"F9.wireOp",EDGE,"E142")])],"isStart":false});
            var Q401;
            {var subQ0=sQuery(id+"F13.wireOp",EDGE,"E148.MirrorCS");var subQ1=sQuery(id+"F13.wireOp",EDGE,"E147");var subQ2=sQuery(id+"F11.wireOp",EDGE,"E143");var subQ33=makeQuery(id+"FyYUAefgu6xEfva_4.26.F14.opExtrude","SWEPT_FACE",FACE,{"disambiguationData":[OSD([subQ0])]});var subQ34=makeQuery(id+"F14.opExtrude","SWEPT_FACE",FACE,{"disambiguationData":[OSD([subQ1])]});Q401=makeQuery(id+"FyYUAefgu6xEfva_4.27.F14.boolean.opBoolean","SPLIT",EDGE,{"disambiguationData":[TD([subQ33])],"derivedFrom":makeQuery(id+"FyYUAefgu6xEfva_4.26.F14.boolean.opBoolean","SPLIT",EDGE,{"disambiguationData":[TD([subQ34])],"derivedFrom":makeQuery(id+"FyYUAefgu6xEfva_4.25.F14.boolean.opBoolean","SPLIT",EDGE,{"disambiguationData":[TD([subQ34])],"derivedFrom":makeQuery(id+"FyYUAefgu6xEfva_4.24.F14.boolean.opBoolean","SPLIT",EDGE,{"disambiguationData":[TD([subQ34])],"derivedFrom":makeQuery(id+"FyYUAefgu6xEfva_4.23.F14.boolean.opBoolean","SPLIT",EDGE,{"disambiguationData":[TD([subQ34])],"derivedFrom":makeQuery(id+"FyYUAefgu6xEfva_4.22.F14.boolean.opBoolean","SPLIT",EDGE,{"disambiguationData":[TD([subQ34])],"derivedFrom":makeQuery(id+"FyYUAefgu6xEfva_4.21.F14.boolean.opBoolean","SPLIT",EDGE,{"disambiguationData":[TD([subQ34])],"derivedFrom":makeQuery(id+"FyYUAefgu6xEfva_4.20.F14.boolean.opBoolean","SPLIT",EDGE,{"disambiguationData":[TD([subQ34])],"derivedFrom":makeQuery(id+"FyYUAefgu6xEfva_4.19.F14.boolean.opBoolean","SPLIT",EDGE,{"disambiguationData":[TD([subQ34])],"derivedFrom":makeQuery(id+"FyYUAefgu6xEfva_4.18.F14.boolean.opBoolean","SPLIT",EDGE,{"disambiguationData":[TD([subQ34])],"derivedFrom":makeQuery(id+"FyYUAefgu6xEfva_4.17.F14.boolean.opBoolean","SPLIT",EDGE,{"disambiguationData":[TD([subQ34])],"derivedFrom":makeQuery(id+"FyYUAefgu6xEfva_4.16.F14.boolean.opBoolean","SPLIT",EDGE,{"disambiguationData":[TD([subQ34])],"derivedFrom":makeQuery(id+"FyYUAefgu6xEfva_4.15.F14.boolean.opBoolean","SPLIT",EDGE,{"disambiguationData":[TD([subQ34])],"derivedFrom":makeQuery(id+"FyYUAefgu6xEfva_4.14.F14.boolean.opBoolean","SPLIT",EDGE,{"disambiguationData":[TD([subQ34])],"derivedFrom":makeQuery(id+"FyYUAefgu6xEfva_4.13.F14.boolean.opBoolean","SPLIT",EDGE,{"disambiguationData":[TD([subQ34])],"derivedFrom":makeQuery(id+"FyYUAefgu6xEfva_4.12.F14.boolean.opBoolean","SPLIT",EDGE,{"disambiguationData":[TD([subQ34])],"derivedFrom":makeQuery(id+"FyYUAefgu6xEfva_4.11.F14.boolean.opBoolean","SPLIT",EDGE,{"disambiguationData":[TD([subQ34])],"derivedFrom":makeQuery(id+"FyYUAefgu6xEfva_4.10.F14.boolean.opBoolean","SPLIT",EDGE,{"disambiguationData":[TD([subQ34])],"derivedFrom":makeQuery(id+"FyYUAefgu6xEfva_4.9.F14.boolean.opBoolean","SPLIT",EDGE,{"disambiguationData":[TD([subQ34])],"derivedFrom":makeQuery(id+"FyYUAefgu6xEfva_4.8.F14.boolean.opBoolean","SPLIT",EDGE,{"disambiguationData":[TD([subQ34])],"derivedFrom":makeQuery(id+"FyYUAefgu6xEfva_4.7.F14.boolean.opBoolean","SPLIT",EDGE,{"disambiguationData":[TD([subQ34])],"derivedFrom":makeQuery(id+"FyYUAefgu6xEfva_4.6.F14.boolean.opBoolean","SPLIT",EDGE,{"disambiguationData":[TD([subQ34])],"derivedFrom":makeQuery(id+"FyYUAefgu6xEfva_4.5.F14.boolean.opBoolean","SPLIT",EDGE,{"disambiguationData":[TD([subQ34])],"derivedFrom":makeQuery(id+"FyYUAefgu6xEfva_4.4.F14.boolean.opBoolean","SPLIT",EDGE,{"disambiguationData":[TD([subQ34])],"derivedFrom":makeQuery(id+"FyYUAefgu6xEfva_4.3.F14.boolean.opBoolean","SPLIT",EDGE,{"disambiguationData":[TD([subQ34])],"derivedFrom":makeQuery(id+"FyYUAefgu6xEfva_4.2.F14.boolean.opBoolean","SPLIT",EDGE,{"disambiguationData":[TD([subQ34])],"derivedFrom":makeQuery(id+"FyYUAefgu6xEfva_4.1.F14.boolean.opBoolean","SPLIT",EDGE,{"disambiguationData":[TD([subQ34])],"derivedFrom":makeQuery(id+"F12.opExtrude","CAP_EDGE",EDGE,{"disambiguationData":[OSD([subQ2])],"isStart":false})})})})})})})})})})})})})})})})})})})})})})})})})})})});}
            var Q402;
            Q402=makeQuery(id+"FyYUAefgu6xEfva_4.28.F14.opExtrude","SWEPT_EDGE",EDGE,{"disambiguationData":[OSD([sQuery(id+"F9.wireOp",EDGE,"E142"),sQuery(id+"F13.wireOp",EDGE,"E147")])]});
            var Q403;
            Q403=makeQuery(id+"FyYUAefgu6xEfva_4.28.F14.opExtrude","SWEPT_EDGE",EDGE,{"disambiguationData":[OSD([sQuery(id+"F11.wireOp",EDGE,"E143"),sQuery(id+"F13.wireOp",EDGE,"E147")])]});
            var Q404;
            Q404=makeQuery(id+"FyYUAefgu6xEfva_4.28.F14.opExtrude","SWEPT_EDGE",EDGE,{"disambiguationData":[OSD([sQuery(id+"F9.wireOp",EDGE,"E142"),sQuery(id+"F13.wireOp",EDGE,"E148.MirrorCS")])]});
            var Q405;
            Q405=makeQuery(id+"FyYUAefgu6xEfva_4.28.F14.opExtrude","SWEPT_EDGE",EDGE,{"disambiguationData":[OSD([sQuery(id+"F11.wireOp",EDGE,"E143"),sQuery(id+"F13.wireOp",EDGE,"E148.MirrorCS")])]});
            var Q406;
            Q406=makeQuery(id+"FyYUAefgu6xEfva_4.28.F14.opExtrude","CAP_EDGE",EDGE,{"disambiguationData":[OSD([sQuery(id+"F13.wireOp",EDGE,"E147")])],"isStart":true});
            var Q407;
            Q407=makeQuery(id+"FyYUAefgu6xEfva_4.28.F14.opExtrude","CAP_EDGE",EDGE,{"disambiguationData":[OSD([sQuery(id+"F13.wireOp",EDGE,"E148.MirrorCS")])],"isStart":true});
            var Q408;
            Q408=makeQuery(id+"FyYUAefgu6xEfva_4.28.F14.opExtrude","CAP_EDGE",EDGE,{"disambiguationData":[OSD([sQuery(id+"F9.wireOp",EDGE,"E142")])],"isStart":false});
            var Q409;
            {var subQ0=sQuery(id+"F9.wireOp",EDGE,"E142");var subQ3=sQuery(id+"F13.wireOp",EDGE,"E148.MirrorCS");var subQ4=makeQuery(id+"FyYUAefgu6xEfva_4.27.F14.opExtrude","SWEPT_FACE",FACE,{"disambiguationData":[OSD([subQ3])]});var subQ5=sQuery(id+"F13.wireOp",EDGE,"E147");var subQ6=makeQuery(id+"F14.opExtrude","SWEPT_FACE",FACE,{"disambiguationData":[OSD([subQ5])]});Q409=makeQuery(id+"FyYUAefgu6xEfva_4.28.F14.boolean.opBoolean","SPLIT",EDGE,{"disambiguationData":[TD([subQ4])],"derivedFrom":makeQuery(id+"FyYUAefgu6xEfva_4.27.F14.boolean.opBoolean","SPLIT",EDGE,{"disambiguationData":[TD([subQ6])],"derivedFrom":makeQuery(id+"FyYUAefgu6xEfva_4.26.F14.boolean.opBoolean","SPLIT",EDGE,{"disambiguationData":[TD([subQ6])],"derivedFrom":makeQuery(id+"FyYUAefgu6xEfva_4.25.F14.boolean.opBoolean","SPLIT",EDGE,{"disambiguationData":[TD([subQ6])],"derivedFrom":makeQuery(id+"FyYUAefgu6xEfva_4.24.F14.boolean.opBoolean","SPLIT",EDGE,{"disambiguationData":[TD([subQ6])],"derivedFrom":makeQuery(id+"FyYUAefgu6xEfva_4.23.F14.boolean.opBoolean","SPLIT",EDGE,{"disambiguationData":[TD([subQ6])],"derivedFrom":makeQuery(id+"FyYUAefgu6xEfva_4.22.F14.boolean.opBoolean","SPLIT",EDGE,{"disambiguationData":[TD([subQ6])],"derivedFrom":makeQuery(id+"FyYUAefgu6xEfva_4.21.F14.boolean.opBoolean","SPLIT",EDGE,{"disambiguationData":[TD([subQ6])],"derivedFrom":makeQuery(id+"FyYUAefgu6xEfva_4.20.F14.boolean.opBoolean","SPLIT",EDGE,{"disambiguationData":[TD([subQ6])],"derivedFrom":makeQuery(id+"FyYUAefgu6xEfva_4.19.F14.boolean.opBoolean","SPLIT",EDGE,{"disambiguationData":[TD([subQ6])],"derivedFrom":makeQuery(id+"FyYUAefgu6xEfva_4.18.F14.boolean.opBoolean","SPLIT",EDGE,{"disambiguationData":[TD([subQ6])],"derivedFrom":makeQuery(id+"FyYUAefgu6xEfva_4.17.F14.boolean.opBoolean","SPLIT",EDGE,{"disambiguationData":[TD([subQ6])],"derivedFrom":makeQuery(id+"FyYUAefgu6xEfva_4.16.F14.boolean.opBoolean","SPLIT",EDGE,{"disambiguationData":[TD([subQ6])],"derivedFrom":makeQuery(id+"FyYUAefgu6xEfva_4.15.F14.boolean.opBoolean","SPLIT",EDGE,{"disambiguationData":[TD([subQ6])],"derivedFrom":makeQuery(id+"FyYUAefgu6xEfva_4.14.F14.boolean.opBoolean","SPLIT",EDGE,{"disambiguationData":[TD([subQ6])],"derivedFrom":makeQuery(id+"FyYUAefgu6xEfva_4.13.F14.boolean.opBoolean","SPLIT",EDGE,{"disambiguationData":[TD([subQ6])],"derivedFrom":makeQuery(id+"FyYUAefgu6xEfva_4.12.F14.boolean.opBoolean","SPLIT",EDGE,{"disambiguationData":[TD([subQ6])],"derivedFrom":makeQuery(id+"FyYUAefgu6xEfva_4.11.F14.boolean.opBoolean","SPLIT",EDGE,{"disambiguationData":[TD([subQ6])],"derivedFrom":makeQuery(id+"FyYUAefgu6xEfva_4.10.F14.boolean.opBoolean","SPLIT",EDGE,{"disambiguationData":[TD([subQ6])],"derivedFrom":makeQuery(id+"FyYUAefgu6xEfva_4.9.F14.boolean.opBoolean","SPLIT",EDGE,{"disambiguationData":[TD([subQ6])],"derivedFrom":makeQuery(id+"FyYUAefgu6xEfva_4.8.F14.boolean.opBoolean","SPLIT",EDGE,{"disambiguationData":[TD([subQ6])],"derivedFrom":makeQuery(id+"FyYUAefgu6xEfva_4.7.F14.boolean.opBoolean","SPLIT",EDGE,{"disambiguationData":[TD([subQ6])],"derivedFrom":makeQuery(id+"FyYUAefgu6xEfva_4.6.F14.boolean.opBoolean","SPLIT",EDGE,{"disambiguationData":[TD([subQ6])],"derivedFrom":makeQuery(id+"FyYUAefgu6xEfva_4.5.F14.boolean.opBoolean","SPLIT",EDGE,{"disambiguationData":[TD([subQ6])],"derivedFrom":makeQuery(id+"FyYUAefgu6xEfva_4.4.F14.boolean.opBoolean","SPLIT",EDGE,{"disambiguationData":[TD([subQ6])],"derivedFrom":makeQuery(id+"FyYUAefgu6xEfva_4.3.F14.boolean.opBoolean","SPLIT",EDGE,{"disambiguationData":[TD([subQ6])],"derivedFrom":makeQuery(id+"FyYUAefgu6xEfva_4.2.F14.boolean.opBoolean","SPLIT",EDGE,{"disambiguationData":[TD([subQ6])],"derivedFrom":makeQuery(id+"FyYUAefgu6xEfva_4.1.F14.boolean.opBoolean","SPLIT",EDGE,{"disambiguationData":[TD([subQ6])],"derivedFrom":makeQuery(id+"F10.boolean.opBoolean","COPY",EDGE,{"derivedFrom":makeQuery(id+"F10.opExtrude","CAP_EDGE",EDGE,{"disambiguationData":[OSD([subQ0])],"isStart":false})})})})})})})})})})})})})})})})})})})})})})})})})})})})})});}
            var Q410;
            {var subQ0=sQuery(id+"F13.wireOp",EDGE,"E148.MirrorCS");var subQ1=sQuery(id+"F13.wireOp",EDGE,"E147");var subQ2=sQuery(id+"F11.wireOp",EDGE,"E143");var subQ34=makeQuery(id+"FyYUAefgu6xEfva_4.27.F14.opExtrude","SWEPT_FACE",FACE,{"disambiguationData":[OSD([subQ0])]});var subQ35=makeQuery(id+"F14.opExtrude","SWEPT_FACE",FACE,{"disambiguationData":[OSD([subQ1])]});Q410=makeQuery(id+"FyYUAefgu6xEfva_4.28.F14.boolean.opBoolean","SPLIT",EDGE,{"disambiguationData":[TD([subQ34])],"derivedFrom":makeQuery(id+"FyYUAefgu6xEfva_4.27.F14.boolean.opBoolean","SPLIT",EDGE,{"disambiguationData":[TD([subQ35])],"derivedFrom":makeQuery(id+"FyYUAefgu6xEfva_4.26.F14.boolean.opBoolean","SPLIT",EDGE,{"disambiguationData":[TD([subQ35])],"derivedFrom":makeQuery(id+"FyYUAefgu6xEfva_4.25.F14.boolean.opBoolean","SPLIT",EDGE,{"disambiguationData":[TD([subQ35])],"derivedFrom":makeQuery(id+"FyYUAefgu6xEfva_4.24.F14.boolean.opBoolean","SPLIT",EDGE,{"disambiguationData":[TD([subQ35])],"derivedFrom":makeQuery(id+"FyYUAefgu6xEfva_4.23.F14.boolean.opBoolean","SPLIT",EDGE,{"disambiguationData":[TD([subQ35])],"derivedFrom":makeQuery(id+"FyYUAefgu6xEfva_4.22.F14.boolean.opBoolean","SPLIT",EDGE,{"disambiguationData":[TD([subQ35])],"derivedFrom":makeQuery(id+"FyYUAefgu6xEfva_4.21.F14.boolean.opBoolean","SPLIT",EDGE,{"disambiguationData":[TD([subQ35])],"derivedFrom":makeQuery(id+"FyYUAefgu6xEfva_4.20.F14.boolean.opBoolean","SPLIT",EDGE,{"disambiguationData":[TD([subQ35])],"derivedFrom":makeQuery(id+"FyYUAefgu6xEfva_4.19.F14.boolean.opBoolean","SPLIT",EDGE,{"disambiguationData":[TD([subQ35])],"derivedFrom":makeQuery(id+"FyYUAefgu6xEfva_4.18.F14.boolean.opBoolean","SPLIT",EDGE,{"disambiguationData":[TD([subQ35])],"derivedFrom":makeQuery(id+"FyYUAefgu6xEfva_4.17.F14.boolean.opBoolean","SPLIT",EDGE,{"disambiguationData":[TD([subQ35])],"derivedFrom":makeQuery(id+"FyYUAefgu6xEfva_4.16.F14.boolean.opBoolean","SPLIT",EDGE,{"disambiguationData":[TD([subQ35])],"derivedFrom":makeQuery(id+"FyYUAefgu6xEfva_4.15.F14.boolean.opBoolean","SPLIT",EDGE,{"disambiguationData":[TD([subQ35])],"derivedFrom":makeQuery(id+"FyYUAefgu6xEfva_4.14.F14.boolean.opBoolean","SPLIT",EDGE,{"disambiguationData":[TD([subQ35])],"derivedFrom":makeQuery(id+"FyYUAefgu6xEfva_4.13.F14.boolean.opBoolean","SPLIT",EDGE,{"disambiguationData":[TD([subQ35])],"derivedFrom":makeQuery(id+"FyYUAefgu6xEfva_4.12.F14.boolean.opBoolean","SPLIT",EDGE,{"disambiguationData":[TD([subQ35])],"derivedFrom":makeQuery(id+"FyYUAefgu6xEfva_4.11.F14.boolean.opBoolean","SPLIT",EDGE,{"disambiguationData":[TD([subQ35])],"derivedFrom":makeQuery(id+"FyYUAefgu6xEfva_4.10.F14.boolean.opBoolean","SPLIT",EDGE,{"disambiguationData":[TD([subQ35])],"derivedFrom":makeQuery(id+"FyYUAefgu6xEfva_4.9.F14.boolean.opBoolean","SPLIT",EDGE,{"disambiguationData":[TD([subQ35])],"derivedFrom":makeQuery(id+"FyYUAefgu6xEfva_4.8.F14.boolean.opBoolean","SPLIT",EDGE,{"disambiguationData":[TD([subQ35])],"derivedFrom":makeQuery(id+"FyYUAefgu6xEfva_4.7.F14.boolean.opBoolean","SPLIT",EDGE,{"disambiguationData":[TD([subQ35])],"derivedFrom":makeQuery(id+"FyYUAefgu6xEfva_4.6.F14.boolean.opBoolean","SPLIT",EDGE,{"disambiguationData":[TD([subQ35])],"derivedFrom":makeQuery(id+"FyYUAefgu6xEfva_4.5.F14.boolean.opBoolean","SPLIT",EDGE,{"disambiguationData":[TD([subQ35])],"derivedFrom":makeQuery(id+"FyYUAefgu6xEfva_4.4.F14.boolean.opBoolean","SPLIT",EDGE,{"disambiguationData":[TD([subQ35])],"derivedFrom":makeQuery(id+"FyYUAefgu6xEfva_4.3.F14.boolean.opBoolean","SPLIT",EDGE,{"disambiguationData":[TD([subQ35])],"derivedFrom":makeQuery(id+"FyYUAefgu6xEfva_4.2.F14.boolean.opBoolean","SPLIT",EDGE,{"disambiguationData":[TD([subQ35])],"derivedFrom":makeQuery(id+"FyYUAefgu6xEfva_4.1.F14.boolean.opBoolean","SPLIT",EDGE,{"disambiguationData":[TD([subQ35])],"derivedFrom":makeQuery(id+"F12.opExtrude","CAP_EDGE",EDGE,{"disambiguationData":[OSD([subQ2])],"isStart":false})})})})})})})})})})})})})})})})})})})})})})})})})})})})});}
            var Q411;
            {var subQ1=sQuery(id+"F11.wireOp",EDGE,"E143");var subQ3=sQuery(id+"F13.wireOp",EDGE,"E147");var subQ4=sQuery(id+"F13.wireOp",EDGE,"E148.MirrorCS");var subQ5=makeQuery(id+"FyYUAefgu6xEfva_4.27.F14.opExtrude","SWEPT_FACE",FACE,{"disambiguationData":[OSD([subQ4])]});var subQ6=makeQuery(id+"F14.opExtrude","SWEPT_FACE",FACE,{"disambiguationData":[OSD([subQ3])]});Q411=makeQuery(id+"FyYUAefgu6xEfva_4.28.F14.boolean.opBoolean","SPLIT",EDGE,{"disambiguationData":[TD([subQ5])],"derivedFrom":makeQuery(id+"FyYUAefgu6xEfva_4.27.F14.boolean.opBoolean","SPLIT",EDGE,{"disambiguationData":[TD([subQ6])],"derivedFrom":makeQuery(id+"FyYUAefgu6xEfva_4.26.F14.boolean.opBoolean","SPLIT",EDGE,{"disambiguationData":[TD([subQ6])],"derivedFrom":makeQuery(id+"FyYUAefgu6xEfva_4.25.F14.boolean.opBoolean","SPLIT",EDGE,{"disambiguationData":[TD([subQ6])],"derivedFrom":makeQuery(id+"FyYUAefgu6xEfva_4.24.F14.boolean.opBoolean","SPLIT",EDGE,{"disambiguationData":[TD([subQ6])],"derivedFrom":makeQuery(id+"FyYUAefgu6xEfva_4.23.F14.boolean.opBoolean","SPLIT",EDGE,{"disambiguationData":[TD([subQ6])],"derivedFrom":makeQuery(id+"FyYUAefgu6xEfva_4.22.F14.boolean.opBoolean","SPLIT",EDGE,{"disambiguationData":[TD([subQ6])],"derivedFrom":makeQuery(id+"FyYUAefgu6xEfva_4.21.F14.boolean.opBoolean","SPLIT",EDGE,{"disambiguationData":[TD([subQ6])],"derivedFrom":makeQuery(id+"FyYUAefgu6xEfva_4.20.F14.boolean.opBoolean","SPLIT",EDGE,{"disambiguationData":[TD([subQ6])],"derivedFrom":makeQuery(id+"FyYUAefgu6xEfva_4.19.F14.boolean.opBoolean","SPLIT",EDGE,{"disambiguationData":[TD([subQ6])],"derivedFrom":makeQuery(id+"FyYUAefgu6xEfva_4.18.F14.boolean.opBoolean","SPLIT",EDGE,{"disambiguationData":[TD([subQ6])],"derivedFrom":makeQuery(id+"FyYUAefgu6xEfva_4.17.F14.boolean.opBoolean","SPLIT",EDGE,{"disambiguationData":[TD([subQ6])],"derivedFrom":makeQuery(id+"FyYUAefgu6xEfva_4.16.F14.boolean.opBoolean","SPLIT",EDGE,{"disambiguationData":[TD([subQ6])],"derivedFrom":makeQuery(id+"FyYUAefgu6xEfva_4.15.F14.boolean.opBoolean","SPLIT",EDGE,{"disambiguationData":[TD([subQ6])],"derivedFrom":makeQuery(id+"FyYUAefgu6xEfva_4.14.F14.boolean.opBoolean","SPLIT",EDGE,{"disambiguationData":[TD([subQ6])],"derivedFrom":makeQuery(id+"FyYUAefgu6xEfva_4.13.F14.boolean.opBoolean","SPLIT",EDGE,{"disambiguationData":[TD([subQ6])],"derivedFrom":makeQuery(id+"FyYUAefgu6xEfva_4.12.F14.boolean.opBoolean","SPLIT",EDGE,{"disambiguationData":[TD([subQ6])],"derivedFrom":makeQuery(id+"FyYUAefgu6xEfva_4.11.F14.boolean.opBoolean","SPLIT",EDGE,{"disambiguationData":[TD([subQ6])],"derivedFrom":makeQuery(id+"FyYUAefgu6xEfva_4.10.F14.boolean.opBoolean","SPLIT",EDGE,{"disambiguationData":[TD([subQ6])],"derivedFrom":makeQuery(id+"FyYUAefgu6xEfva_4.9.F14.boolean.opBoolean","SPLIT",EDGE,{"disambiguationData":[TD([subQ6])],"derivedFrom":makeQuery(id+"FyYUAefgu6xEfva_4.8.F14.boolean.opBoolean","SPLIT",EDGE,{"disambiguationData":[TD([subQ6])],"derivedFrom":makeQuery(id+"FyYUAefgu6xEfva_4.7.F14.boolean.opBoolean","SPLIT",EDGE,{"disambiguationData":[TD([subQ6])],"derivedFrom":makeQuery(id+"FyYUAefgu6xEfva_4.6.F14.boolean.opBoolean","SPLIT",EDGE,{"disambiguationData":[TD([subQ6])],"derivedFrom":makeQuery(id+"FyYUAefgu6xEfva_4.5.F14.boolean.opBoolean","SPLIT",EDGE,{"disambiguationData":[TD([subQ6])],"derivedFrom":makeQuery(id+"FyYUAefgu6xEfva_4.4.F14.boolean.opBoolean","SPLIT",EDGE,{"disambiguationData":[TD([subQ6])],"derivedFrom":makeQuery(id+"FyYUAefgu6xEfva_4.3.F14.boolean.opBoolean","SPLIT",EDGE,{"disambiguationData":[TD([subQ6])],"derivedFrom":makeQuery(id+"FyYUAefgu6xEfva_4.2.F14.boolean.opBoolean","SPLIT",EDGE,{"disambiguationData":[TD([subQ6])],"derivedFrom":makeQuery(id+"FyYUAefgu6xEfva_4.1.F14.boolean.opBoolean","SPLIT",EDGE,{"disambiguationData":[TD([subQ6])],"derivedFrom":makeQuery(id+"F12.opExtrude","CAP_EDGE",EDGE,{"disambiguationData":[OSD([subQ1])],"isStart":true})})})})})})})})})})})})})})})})})})})})})})})})})})})})});}
            var Q412;
            Q412=makeQuery(id+"FyYUAefgu6xEfva_4.29.F14.opExtrude","SWEPT_EDGE",EDGE,{"disambiguationData":[OSD([sQuery(id+"F9.wireOp",EDGE,"E142"),sQuery(id+"F13.wireOp",EDGE,"E147")])]});
            var Q413;
            Q413=makeQuery(id+"FyYUAefgu6xEfva_4.29.F14.opExtrude","SWEPT_EDGE",EDGE,{"disambiguationData":[OSD([sQuery(id+"F11.wireOp",EDGE,"E143"),sQuery(id+"F13.wireOp",EDGE,"E147")])]});
            var Q414;
            Q414=makeQuery(id+"FyYUAefgu6xEfva_4.29.F14.opExtrude","SWEPT_EDGE",EDGE,{"disambiguationData":[OSD([sQuery(id+"F9.wireOp",EDGE,"E142"),sQuery(id+"F13.wireOp",EDGE,"E148.MirrorCS")])]});
            var Q415;
            Q415=makeQuery(id+"FyYUAefgu6xEfva_4.29.F14.opExtrude","SWEPT_EDGE",EDGE,{"disambiguationData":[OSD([sQuery(id+"F11.wireOp",EDGE,"E143"),sQuery(id+"F13.wireOp",EDGE,"E148.MirrorCS")])]});
            var Q416;
            Q416=makeQuery(id+"FyYUAefgu6xEfva_4.29.F14.opExtrude","CAP_EDGE",EDGE,{"disambiguationData":[OSD([sQuery(id+"F13.wireOp",EDGE,"E147")])],"isStart":true});
            var Q417;
            Q417=makeQuery(id+"FyYUAefgu6xEfva_4.29.F14.opExtrude","CAP_EDGE",EDGE,{"disambiguationData":[OSD([sQuery(id+"F13.wireOp",EDGE,"E148.MirrorCS")])],"isStart":true});
            var Q418;
            Q418=makeQuery(id+"FyYUAefgu6xEfva_4.29.F14.opExtrude","CAP_EDGE",EDGE,{"disambiguationData":[OSD([sQuery(id+"F9.wireOp",EDGE,"E142")])],"isStart":false});
            var Q419;
            {var subQ0=sQuery(id+"F9.wireOp",EDGE,"E142");var subQ2=sQuery(id+"F13.wireOp",EDGE,"E147");var subQ4=sQuery(id+"F13.wireOp",EDGE,"E148.MirrorCS");var subQ5=makeQuery(id+"FyYUAefgu6xEfva_4.28.F14.opExtrude","SWEPT_FACE",FACE,{"disambiguationData":[OSD([subQ4])]});var subQ6=makeQuery(id+"F14.opExtrude","SWEPT_FACE",FACE,{"disambiguationData":[OSD([subQ2])]});Q419=makeQuery(id+"FyYUAefgu6xEfva_4.29.F14.boolean.opBoolean","SPLIT",EDGE,{"disambiguationData":[TD([subQ5])],"derivedFrom":makeQuery(id+"FyYUAefgu6xEfva_4.28.F14.boolean.opBoolean","SPLIT",EDGE,{"disambiguationData":[TD([subQ6])],"derivedFrom":makeQuery(id+"FyYUAefgu6xEfva_4.27.F14.boolean.opBoolean","SPLIT",EDGE,{"disambiguationData":[TD([subQ6])],"derivedFrom":makeQuery(id+"FyYUAefgu6xEfva_4.26.F14.boolean.opBoolean","SPLIT",EDGE,{"disambiguationData":[TD([subQ6])],"derivedFrom":makeQuery(id+"FyYUAefgu6xEfva_4.25.F14.boolean.opBoolean","SPLIT",EDGE,{"disambiguationData":[TD([subQ6])],"derivedFrom":makeQuery(id+"FyYUAefgu6xEfva_4.24.F14.boolean.opBoolean","SPLIT",EDGE,{"disambiguationData":[TD([subQ6])],"derivedFrom":makeQuery(id+"FyYUAefgu6xEfva_4.23.F14.boolean.opBoolean","SPLIT",EDGE,{"disambiguationData":[TD([subQ6])],"derivedFrom":makeQuery(id+"FyYUAefgu6xEfva_4.22.F14.boolean.opBoolean","SPLIT",EDGE,{"disambiguationData":[TD([subQ6])],"derivedFrom":makeQuery(id+"FyYUAefgu6xEfva_4.21.F14.boolean.opBoolean","SPLIT",EDGE,{"disambiguationData":[TD([subQ6])],"derivedFrom":makeQuery(id+"FyYUAefgu6xEfva_4.20.F14.boolean.opBoolean","SPLIT",EDGE,{"disambiguationData":[TD([subQ6])],"derivedFrom":makeQuery(id+"FyYUAefgu6xEfva_4.19.F14.boolean.opBoolean","SPLIT",EDGE,{"disambiguationData":[TD([subQ6])],"derivedFrom":makeQuery(id+"FyYUAefgu6xEfva_4.18.F14.boolean.opBoolean","SPLIT",EDGE,{"disambiguationData":[TD([subQ6])],"derivedFrom":makeQuery(id+"FyYUAefgu6xEfva_4.17.F14.boolean.opBoolean","SPLIT",EDGE,{"disambiguationData":[TD([subQ6])],"derivedFrom":makeQuery(id+"FyYUAefgu6xEfva_4.16.F14.boolean.opBoolean","SPLIT",EDGE,{"disambiguationData":[TD([subQ6])],"derivedFrom":makeQuery(id+"FyYUAefgu6xEfva_4.15.F14.boolean.opBoolean","SPLIT",EDGE,{"disambiguationData":[TD([subQ6])],"derivedFrom":makeQuery(id+"FyYUAefgu6xEfva_4.14.F14.boolean.opBoolean","SPLIT",EDGE,{"disambiguationData":[TD([subQ6])],"derivedFrom":makeQuery(id+"FyYUAefgu6xEfva_4.13.F14.boolean.opBoolean","SPLIT",EDGE,{"disambiguationData":[TD([subQ6])],"derivedFrom":makeQuery(id+"FyYUAefgu6xEfva_4.12.F14.boolean.opBoolean","SPLIT",EDGE,{"disambiguationData":[TD([subQ6])],"derivedFrom":makeQuery(id+"FyYUAefgu6xEfva_4.11.F14.boolean.opBoolean","SPLIT",EDGE,{"disambiguationData":[TD([subQ6])],"derivedFrom":makeQuery(id+"FyYUAefgu6xEfva_4.10.F14.boolean.opBoolean","SPLIT",EDGE,{"disambiguationData":[TD([subQ6])],"derivedFrom":makeQuery(id+"FyYUAefgu6xEfva_4.9.F14.boolean.opBoolean","SPLIT",EDGE,{"disambiguationData":[TD([subQ6])],"derivedFrom":makeQuery(id+"FyYUAefgu6xEfva_4.8.F14.boolean.opBoolean","SPLIT",EDGE,{"disambiguationData":[TD([subQ6])],"derivedFrom":makeQuery(id+"FyYUAefgu6xEfva_4.7.F14.boolean.opBoolean","SPLIT",EDGE,{"disambiguationData":[TD([subQ6])],"derivedFrom":makeQuery(id+"FyYUAefgu6xEfva_4.6.F14.boolean.opBoolean","SPLIT",EDGE,{"disambiguationData":[TD([subQ6])],"derivedFrom":makeQuery(id+"FyYUAefgu6xEfva_4.5.F14.boolean.opBoolean","SPLIT",EDGE,{"disambiguationData":[TD([subQ6])],"derivedFrom":makeQuery(id+"FyYUAefgu6xEfva_4.4.F14.boolean.opBoolean","SPLIT",EDGE,{"disambiguationData":[TD([subQ6])],"derivedFrom":makeQuery(id+"FyYUAefgu6xEfva_4.3.F14.boolean.opBoolean","SPLIT",EDGE,{"disambiguationData":[TD([subQ6])],"derivedFrom":makeQuery(id+"FyYUAefgu6xEfva_4.2.F14.boolean.opBoolean","SPLIT",EDGE,{"disambiguationData":[TD([subQ6])],"derivedFrom":makeQuery(id+"FyYUAefgu6xEfva_4.1.F14.boolean.opBoolean","SPLIT",EDGE,{"disambiguationData":[TD([subQ6])],"derivedFrom":makeQuery(id+"F10.boolean.opBoolean","COPY",EDGE,{"derivedFrom":makeQuery(id+"F10.opExtrude","CAP_EDGE",EDGE,{"disambiguationData":[OSD([subQ0])],"isStart":false})})})})})})})})})})})})})})})})})})})})})})})})})})})})})})});}
            var Q420;
            {var subQ0=sQuery(id+"F13.wireOp",EDGE,"E148.MirrorCS");var subQ1=sQuery(id+"F13.wireOp",EDGE,"E147");var subQ2=sQuery(id+"F11.wireOp",EDGE,"E143");var subQ35=makeQuery(id+"FyYUAefgu6xEfva_4.28.F14.opExtrude","SWEPT_FACE",FACE,{"disambiguationData":[OSD([subQ0])]});var subQ36=makeQuery(id+"F14.opExtrude","SWEPT_FACE",FACE,{"disambiguationData":[OSD([subQ1])]});Q420=makeQuery(id+"FyYUAefgu6xEfva_4.29.F14.boolean.opBoolean","SPLIT",EDGE,{"disambiguationData":[TD([subQ35])],"derivedFrom":makeQuery(id+"FyYUAefgu6xEfva_4.28.F14.boolean.opBoolean","SPLIT",EDGE,{"disambiguationData":[TD([subQ36])],"derivedFrom":makeQuery(id+"FyYUAefgu6xEfva_4.27.F14.boolean.opBoolean","SPLIT",EDGE,{"disambiguationData":[TD([subQ36])],"derivedFrom":makeQuery(id+"FyYUAefgu6xEfva_4.26.F14.boolean.opBoolean","SPLIT",EDGE,{"disambiguationData":[TD([subQ36])],"derivedFrom":makeQuery(id+"FyYUAefgu6xEfva_4.25.F14.boolean.opBoolean","SPLIT",EDGE,{"disambiguationData":[TD([subQ36])],"derivedFrom":makeQuery(id+"FyYUAefgu6xEfva_4.24.F14.boolean.opBoolean","SPLIT",EDGE,{"disambiguationData":[TD([subQ36])],"derivedFrom":makeQuery(id+"FyYUAefgu6xEfva_4.23.F14.boolean.opBoolean","SPLIT",EDGE,{"disambiguationData":[TD([subQ36])],"derivedFrom":makeQuery(id+"FyYUAefgu6xEfva_4.22.F14.boolean.opBoolean","SPLIT",EDGE,{"disambiguationData":[TD([subQ36])],"derivedFrom":makeQuery(id+"FyYUAefgu6xEfva_4.21.F14.boolean.opBoolean","SPLIT",EDGE,{"disambiguationData":[TD([subQ36])],"derivedFrom":makeQuery(id+"FyYUAefgu6xEfva_4.20.F14.boolean.opBoolean","SPLIT",EDGE,{"disambiguationData":[TD([subQ36])],"derivedFrom":makeQuery(id+"FyYUAefgu6xEfva_4.19.F14.boolean.opBoolean","SPLIT",EDGE,{"disambiguationData":[TD([subQ36])],"derivedFrom":makeQuery(id+"FyYUAefgu6xEfva_4.18.F14.boolean.opBoolean","SPLIT",EDGE,{"disambiguationData":[TD([subQ36])],"derivedFrom":makeQuery(id+"FyYUAefgu6xEfva_4.17.F14.boolean.opBoolean","SPLIT",EDGE,{"disambiguationData":[TD([subQ36])],"derivedFrom":makeQuery(id+"FyYUAefgu6xEfva_4.16.F14.boolean.opBoolean","SPLIT",EDGE,{"disambiguationData":[TD([subQ36])],"derivedFrom":makeQuery(id+"FyYUAefgu6xEfva_4.15.F14.boolean.opBoolean","SPLIT",EDGE,{"disambiguationData":[TD([subQ36])],"derivedFrom":makeQuery(id+"FyYUAefgu6xEfva_4.14.F14.boolean.opBoolean","SPLIT",EDGE,{"disambiguationData":[TD([subQ36])],"derivedFrom":makeQuery(id+"FyYUAefgu6xEfva_4.13.F14.boolean.opBoolean","SPLIT",EDGE,{"disambiguationData":[TD([subQ36])],"derivedFrom":makeQuery(id+"FyYUAefgu6xEfva_4.12.F14.boolean.opBoolean","SPLIT",EDGE,{"disambiguationData":[TD([subQ36])],"derivedFrom":makeQuery(id+"FyYUAefgu6xEfva_4.11.F14.boolean.opBoolean","SPLIT",EDGE,{"disambiguationData":[TD([subQ36])],"derivedFrom":makeQuery(id+"FyYUAefgu6xEfva_4.10.F14.boolean.opBoolean","SPLIT",EDGE,{"disambiguationData":[TD([subQ36])],"derivedFrom":makeQuery(id+"FyYUAefgu6xEfva_4.9.F14.boolean.opBoolean","SPLIT",EDGE,{"disambiguationData":[TD([subQ36])],"derivedFrom":makeQuery(id+"FyYUAefgu6xEfva_4.8.F14.boolean.opBoolean","SPLIT",EDGE,{"disambiguationData":[TD([subQ36])],"derivedFrom":makeQuery(id+"FyYUAefgu6xEfva_4.7.F14.boolean.opBoolean","SPLIT",EDGE,{"disambiguationData":[TD([subQ36])],"derivedFrom":makeQuery(id+"FyYUAefgu6xEfva_4.6.F14.boolean.opBoolean","SPLIT",EDGE,{"disambiguationData":[TD([subQ36])],"derivedFrom":makeQuery(id+"FyYUAefgu6xEfva_4.5.F14.boolean.opBoolean","SPLIT",EDGE,{"disambiguationData":[TD([subQ36])],"derivedFrom":makeQuery(id+"FyYUAefgu6xEfva_4.4.F14.boolean.opBoolean","SPLIT",EDGE,{"disambiguationData":[TD([subQ36])],"derivedFrom":makeQuery(id+"FyYUAefgu6xEfva_4.3.F14.boolean.opBoolean","SPLIT",EDGE,{"disambiguationData":[TD([subQ36])],"derivedFrom":makeQuery(id+"FyYUAefgu6xEfva_4.2.F14.boolean.opBoolean","SPLIT",EDGE,{"disambiguationData":[TD([subQ36])],"derivedFrom":makeQuery(id+"FyYUAefgu6xEfva_4.1.F14.boolean.opBoolean","SPLIT",EDGE,{"disambiguationData":[TD([subQ36])],"derivedFrom":makeQuery(id+"F12.opExtrude","CAP_EDGE",EDGE,{"disambiguationData":[OSD([subQ2])],"isStart":false})})})})})})})})})})})})})})})})})})})})})})})})})})})})})});}
            var Q421;
            Q421=makeQuery(id+"FyYUAefgu6xEfva_4.30.F14.opExtrude","SWEPT_EDGE",EDGE,{"disambiguationData":[OSD([sQuery(id+"F9.wireOp",EDGE,"E142"),sQuery(id+"F13.wireOp",EDGE,"E147")])]});
            var Q422;
            Q422=makeQuery(id+"FyYUAefgu6xEfva_4.30.F14.opExtrude","SWEPT_EDGE",EDGE,{"disambiguationData":[OSD([sQuery(id+"F11.wireOp",EDGE,"E143"),sQuery(id+"F13.wireOp",EDGE,"E147")])]});
            var Q423;
            Q423=makeQuery(id+"FyYUAefgu6xEfva_4.30.F14.opExtrude","SWEPT_EDGE",EDGE,{"disambiguationData":[OSD([sQuery(id+"F9.wireOp",EDGE,"E142"),sQuery(id+"F13.wireOp",EDGE,"E148.MirrorCS")])]});
            var Q424;
            Q424=makeQuery(id+"FyYUAefgu6xEfva_4.30.F14.opExtrude","SWEPT_EDGE",EDGE,{"disambiguationData":[OSD([sQuery(id+"F11.wireOp",EDGE,"E143"),sQuery(id+"F13.wireOp",EDGE,"E148.MirrorCS")])]});
            var Q425;
            Q425=makeQuery(id+"FyYUAefgu6xEfva_4.30.F14.opExtrude","CAP_EDGE",EDGE,{"disambiguationData":[OSD([sQuery(id+"F13.wireOp",EDGE,"E147")])],"isStart":true});
            var Q426;
            Q426=makeQuery(id+"FyYUAefgu6xEfva_4.30.F14.opExtrude","CAP_EDGE",EDGE,{"disambiguationData":[OSD([sQuery(id+"F13.wireOp",EDGE,"E148.MirrorCS")])],"isStart":true});
            var Q427;
            Q427=makeQuery(id+"FyYUAefgu6xEfva_4.30.F14.opExtrude","CAP_EDGE",EDGE,{"disambiguationData":[OSD([sQuery(id+"F9.wireOp",EDGE,"E142")])],"isStart":false});
            var Q428;
            {var subQ0=sQuery(id+"F9.wireOp",EDGE,"E142");var subQ3=sQuery(id+"F13.wireOp",EDGE,"E148.MirrorCS");var subQ4=makeQuery(id+"FyYUAefgu6xEfva_4.29.F14.opExtrude","SWEPT_FACE",FACE,{"disambiguationData":[OSD([subQ3])]});var subQ5=sQuery(id+"F13.wireOp",EDGE,"E147");var subQ6=makeQuery(id+"F14.opExtrude","SWEPT_FACE",FACE,{"disambiguationData":[OSD([subQ5])]});Q428=makeQuery(id+"FyYUAefgu6xEfva_4.30.F14.boolean.opBoolean","SPLIT",EDGE,{"disambiguationData":[TD([subQ4])],"derivedFrom":makeQuery(id+"FyYUAefgu6xEfva_4.29.F14.boolean.opBoolean","SPLIT",EDGE,{"disambiguationData":[TD([subQ6])],"derivedFrom":makeQuery(id+"FyYUAefgu6xEfva_4.28.F14.boolean.opBoolean","SPLIT",EDGE,{"disambiguationData":[TD([subQ6])],"derivedFrom":makeQuery(id+"FyYUAefgu6xEfva_4.27.F14.boolean.opBoolean","SPLIT",EDGE,{"disambiguationData":[TD([subQ6])],"derivedFrom":makeQuery(id+"FyYUAefgu6xEfva_4.26.F14.boolean.opBoolean","SPLIT",EDGE,{"disambiguationData":[TD([subQ6])],"derivedFrom":makeQuery(id+"FyYUAefgu6xEfva_4.25.F14.boolean.opBoolean","SPLIT",EDGE,{"disambiguationData":[TD([subQ6])],"derivedFrom":makeQuery(id+"FyYUAefgu6xEfva_4.24.F14.boolean.opBoolean","SPLIT",EDGE,{"disambiguationData":[TD([subQ6])],"derivedFrom":makeQuery(id+"FyYUAefgu6xEfva_4.23.F14.boolean.opBoolean","SPLIT",EDGE,{"disambiguationData":[TD([subQ6])],"derivedFrom":makeQuery(id+"FyYUAefgu6xEfva_4.22.F14.boolean.opBoolean","SPLIT",EDGE,{"disambiguationData":[TD([subQ6])],"derivedFrom":makeQuery(id+"FyYUAefgu6xEfva_4.21.F14.boolean.opBoolean","SPLIT",EDGE,{"disambiguationData":[TD([subQ6])],"derivedFrom":makeQuery(id+"FyYUAefgu6xEfva_4.20.F14.boolean.opBoolean","SPLIT",EDGE,{"disambiguationData":[TD([subQ6])],"derivedFrom":makeQuery(id+"FyYUAefgu6xEfva_4.19.F14.boolean.opBoolean","SPLIT",EDGE,{"disambiguationData":[TD([subQ6])],"derivedFrom":makeQuery(id+"FyYUAefgu6xEfva_4.18.F14.boolean.opBoolean","SPLIT",EDGE,{"disambiguationData":[TD([subQ6])],"derivedFrom":makeQuery(id+"FyYUAefgu6xEfva_4.17.F14.boolean.opBoolean","SPLIT",EDGE,{"disambiguationData":[TD([subQ6])],"derivedFrom":makeQuery(id+"FyYUAefgu6xEfva_4.16.F14.boolean.opBoolean","SPLIT",EDGE,{"disambiguationData":[TD([subQ6])],"derivedFrom":makeQuery(id+"FyYUAefgu6xEfva_4.15.F14.boolean.opBoolean","SPLIT",EDGE,{"disambiguationData":[TD([subQ6])],"derivedFrom":makeQuery(id+"FyYUAefgu6xEfva_4.14.F14.boolean.opBoolean","SPLIT",EDGE,{"disambiguationData":[TD([subQ6])],"derivedFrom":makeQuery(id+"FyYUAefgu6xEfva_4.13.F14.boolean.opBoolean","SPLIT",EDGE,{"disambiguationData":[TD([subQ6])],"derivedFrom":makeQuery(id+"FyYUAefgu6xEfva_4.12.F14.boolean.opBoolean","SPLIT",EDGE,{"disambiguationData":[TD([subQ6])],"derivedFrom":makeQuery(id+"FyYUAefgu6xEfva_4.11.F14.boolean.opBoolean","SPLIT",EDGE,{"disambiguationData":[TD([subQ6])],"derivedFrom":makeQuery(id+"FyYUAefgu6xEfva_4.10.F14.boolean.opBoolean","SPLIT",EDGE,{"disambiguationData":[TD([subQ6])],"derivedFrom":makeQuery(id+"FyYUAefgu6xEfva_4.9.F14.boolean.opBoolean","SPLIT",EDGE,{"disambiguationData":[TD([subQ6])],"derivedFrom":makeQuery(id+"FyYUAefgu6xEfva_4.8.F14.boolean.opBoolean","SPLIT",EDGE,{"disambiguationData":[TD([subQ6])],"derivedFrom":makeQuery(id+"FyYUAefgu6xEfva_4.7.F14.boolean.opBoolean","SPLIT",EDGE,{"disambiguationData":[TD([subQ6])],"derivedFrom":makeQuery(id+"FyYUAefgu6xEfva_4.6.F14.boolean.opBoolean","SPLIT",EDGE,{"disambiguationData":[TD([subQ6])],"derivedFrom":makeQuery(id+"FyYUAefgu6xEfva_4.5.F14.boolean.opBoolean","SPLIT",EDGE,{"disambiguationData":[TD([subQ6])],"derivedFrom":makeQuery(id+"FyYUAefgu6xEfva_4.4.F14.boolean.opBoolean","SPLIT",EDGE,{"disambiguationData":[TD([subQ6])],"derivedFrom":makeQuery(id+"FyYUAefgu6xEfva_4.3.F14.boolean.opBoolean","SPLIT",EDGE,{"disambiguationData":[TD([subQ6])],"derivedFrom":makeQuery(id+"FyYUAefgu6xEfva_4.2.F14.boolean.opBoolean","SPLIT",EDGE,{"disambiguationData":[TD([subQ6])],"derivedFrom":makeQuery(id+"FyYUAefgu6xEfva_4.1.F14.boolean.opBoolean","SPLIT",EDGE,{"disambiguationData":[TD([subQ6])],"derivedFrom":makeQuery(id+"F10.boolean.opBoolean","COPY",EDGE,{"derivedFrom":makeQuery(id+"F10.opExtrude","CAP_EDGE",EDGE,{"disambiguationData":[OSD([subQ0])],"isStart":false})})})})})})})})})})})})})})})})})})})})})})})})})})})})})})})});}
            var Q429;
            {var subQ0=sQuery(id+"F13.wireOp",EDGE,"E148.MirrorCS");var subQ1=sQuery(id+"F13.wireOp",EDGE,"E147");var subQ2=sQuery(id+"F11.wireOp",EDGE,"E143");var subQ20=makeQuery(id+"FyYUAefgu6xEfva_4.29.F14.opExtrude","SWEPT_FACE",FACE,{"disambiguationData":[OSD([subQ0])]});var subQ37=makeQuery(id+"F14.opExtrude","SWEPT_FACE",FACE,{"disambiguationData":[OSD([subQ1])]});Q429=makeQuery(id+"FyYUAefgu6xEfva_4.30.F14.boolean.opBoolean","SPLIT",EDGE,{"disambiguationData":[TD([subQ20])],"derivedFrom":makeQuery(id+"FyYUAefgu6xEfva_4.29.F14.boolean.opBoolean","SPLIT",EDGE,{"disambiguationData":[TD([subQ37])],"derivedFrom":makeQuery(id+"FyYUAefgu6xEfva_4.28.F14.boolean.opBoolean","SPLIT",EDGE,{"disambiguationData":[TD([subQ37])],"derivedFrom":makeQuery(id+"FyYUAefgu6xEfva_4.27.F14.boolean.opBoolean","SPLIT",EDGE,{"disambiguationData":[TD([subQ37])],"derivedFrom":makeQuery(id+"FyYUAefgu6xEfva_4.26.F14.boolean.opBoolean","SPLIT",EDGE,{"disambiguationData":[TD([subQ37])],"derivedFrom":makeQuery(id+"FyYUAefgu6xEfva_4.25.F14.boolean.opBoolean","SPLIT",EDGE,{"disambiguationData":[TD([subQ37])],"derivedFrom":makeQuery(id+"FyYUAefgu6xEfva_4.24.F14.boolean.opBoolean","SPLIT",EDGE,{"disambiguationData":[TD([subQ37])],"derivedFrom":makeQuery(id+"FyYUAefgu6xEfva_4.23.F14.boolean.opBoolean","SPLIT",EDGE,{"disambiguationData":[TD([subQ37])],"derivedFrom":makeQuery(id+"FyYUAefgu6xEfva_4.22.F14.boolean.opBoolean","SPLIT",EDGE,{"disambiguationData":[TD([subQ37])],"derivedFrom":makeQuery(id+"FyYUAefgu6xEfva_4.21.F14.boolean.opBoolean","SPLIT",EDGE,{"disambiguationData":[TD([subQ37])],"derivedFrom":makeQuery(id+"FyYUAefgu6xEfva_4.20.F14.boolean.opBoolean","SPLIT",EDGE,{"disambiguationData":[TD([subQ37])],"derivedFrom":makeQuery(id+"FyYUAefgu6xEfva_4.19.F14.boolean.opBoolean","SPLIT",EDGE,{"disambiguationData":[TD([subQ37])],"derivedFrom":makeQuery(id+"FyYUAefgu6xEfva_4.18.F14.boolean.opBoolean","SPLIT",EDGE,{"disambiguationData":[TD([subQ37])],"derivedFrom":makeQuery(id+"FyYUAefgu6xEfva_4.17.F14.boolean.opBoolean","SPLIT",EDGE,{"disambiguationData":[TD([subQ37])],"derivedFrom":makeQuery(id+"FyYUAefgu6xEfva_4.16.F14.boolean.opBoolean","SPLIT",EDGE,{"disambiguationData":[TD([subQ37])],"derivedFrom":makeQuery(id+"FyYUAefgu6xEfva_4.15.F14.boolean.opBoolean","SPLIT",EDGE,{"disambiguationData":[TD([subQ37])],"derivedFrom":makeQuery(id+"FyYUAefgu6xEfva_4.14.F14.boolean.opBoolean","SPLIT",EDGE,{"disambiguationData":[TD([subQ37])],"derivedFrom":makeQuery(id+"FyYUAefgu6xEfva_4.13.F14.boolean.opBoolean","SPLIT",EDGE,{"disambiguationData":[TD([subQ37])],"derivedFrom":makeQuery(id+"FyYUAefgu6xEfva_4.12.F14.boolean.opBoolean","SPLIT",EDGE,{"disambiguationData":[TD([subQ37])],"derivedFrom":makeQuery(id+"FyYUAefgu6xEfva_4.11.F14.boolean.opBoolean","SPLIT",EDGE,{"disambiguationData":[TD([subQ37])],"derivedFrom":makeQuery(id+"FyYUAefgu6xEfva_4.10.F14.boolean.opBoolean","SPLIT",EDGE,{"disambiguationData":[TD([subQ37])],"derivedFrom":makeQuery(id+"FyYUAefgu6xEfva_4.9.F14.boolean.opBoolean","SPLIT",EDGE,{"disambiguationData":[TD([subQ37])],"derivedFrom":makeQuery(id+"FyYUAefgu6xEfva_4.8.F14.boolean.opBoolean","SPLIT",EDGE,{"disambiguationData":[TD([subQ37])],"derivedFrom":makeQuery(id+"FyYUAefgu6xEfva_4.7.F14.boolean.opBoolean","SPLIT",EDGE,{"disambiguationData":[TD([subQ37])],"derivedFrom":makeQuery(id+"FyYUAefgu6xEfva_4.6.F14.boolean.opBoolean","SPLIT",EDGE,{"disambiguationData":[TD([subQ37])],"derivedFrom":makeQuery(id+"FyYUAefgu6xEfva_4.5.F14.boolean.opBoolean","SPLIT",EDGE,{"disambiguationData":[TD([subQ37])],"derivedFrom":makeQuery(id+"FyYUAefgu6xEfva_4.4.F14.boolean.opBoolean","SPLIT",EDGE,{"disambiguationData":[TD([subQ37])],"derivedFrom":makeQuery(id+"FyYUAefgu6xEfva_4.3.F14.boolean.opBoolean","SPLIT",EDGE,{"disambiguationData":[TD([subQ37])],"derivedFrom":makeQuery(id+"FyYUAefgu6xEfva_4.2.F14.boolean.opBoolean","SPLIT",EDGE,{"disambiguationData":[TD([subQ37])],"derivedFrom":makeQuery(id+"FyYUAefgu6xEfva_4.1.F14.boolean.opBoolean","SPLIT",EDGE,{"disambiguationData":[TD([subQ37])],"derivedFrom":makeQuery(id+"F12.opExtrude","CAP_EDGE",EDGE,{"disambiguationData":[OSD([subQ2])],"isStart":false})})})})})})})})})})})})})})})})})})})})})})})})})})})})})})});}
            var Q430;
            Q430=makeQuery(id+"FyYUAefgu6xEfva_4.31.F14.opExtrude","SWEPT_EDGE",EDGE,{"disambiguationData":[OSD([sQuery(id+"F9.wireOp",EDGE,"E142"),sQuery(id+"F13.wireOp",EDGE,"E147")])]});
            var Q431;
            Q431=makeQuery(id+"FyYUAefgu6xEfva_4.31.F14.opExtrude","SWEPT_EDGE",EDGE,{"disambiguationData":[OSD([sQuery(id+"F11.wireOp",EDGE,"E143"),sQuery(id+"F13.wireOp",EDGE,"E147")])]});
            var Q432;
            Q432=makeQuery(id+"FyYUAefgu6xEfva_4.31.F14.opExtrude","SWEPT_EDGE",EDGE,{"disambiguationData":[OSD([sQuery(id+"F9.wireOp",EDGE,"E142"),sQuery(id+"F13.wireOp",EDGE,"E148.MirrorCS")])]});
            var Q433;
            Q433=makeQuery(id+"FyYUAefgu6xEfva_4.31.F14.opExtrude","SWEPT_EDGE",EDGE,{"disambiguationData":[OSD([sQuery(id+"F11.wireOp",EDGE,"E143"),sQuery(id+"F13.wireOp",EDGE,"E148.MirrorCS")])]});
            var Q434;
            Q434=makeQuery(id+"FyYUAefgu6xEfva_4.31.F14.opExtrude","CAP_EDGE",EDGE,{"disambiguationData":[OSD([sQuery(id+"F9.wireOp",EDGE,"E142")])],"isStart":false});
            var Q435;
            {var subQ0=sQuery(id+"F9.wireOp",EDGE,"E142");var subQ2=sQuery(id+"F13.wireOp",EDGE,"E148.MirrorCS");var subQ3=makeQuery(id+"FyYUAefgu6xEfva_4.30.F14.opExtrude","SWEPT_FACE",FACE,{"disambiguationData":[OSD([subQ2])]});var subQ5=sQuery(id+"F13.wireOp",EDGE,"E147");var subQ6=makeQuery(id+"F14.opExtrude","SWEPT_FACE",FACE,{"disambiguationData":[OSD([subQ5])]});Q435=makeQuery(id+"FyYUAefgu6xEfva_4.31.F14.boolean.opBoolean","SPLIT",EDGE,{"disambiguationData":[TD([subQ3])],"derivedFrom":makeQuery(id+"FyYUAefgu6xEfva_4.30.F14.boolean.opBoolean","SPLIT",EDGE,{"disambiguationData":[TD([subQ6])],"derivedFrom":makeQuery(id+"FyYUAefgu6xEfva_4.29.F14.boolean.opBoolean","SPLIT",EDGE,{"disambiguationData":[TD([subQ6])],"derivedFrom":makeQuery(id+"FyYUAefgu6xEfva_4.28.F14.boolean.opBoolean","SPLIT",EDGE,{"disambiguationData":[TD([subQ6])],"derivedFrom":makeQuery(id+"FyYUAefgu6xEfva_4.27.F14.boolean.opBoolean","SPLIT",EDGE,{"disambiguationData":[TD([subQ6])],"derivedFrom":makeQuery(id+"FyYUAefgu6xEfva_4.26.F14.boolean.opBoolean","SPLIT",EDGE,{"disambiguationData":[TD([subQ6])],"derivedFrom":makeQuery(id+"FyYUAefgu6xEfva_4.25.F14.boolean.opBoolean","SPLIT",EDGE,{"disambiguationData":[TD([subQ6])],"derivedFrom":makeQuery(id+"FyYUAefgu6xEfva_4.24.F14.boolean.opBoolean","SPLIT",EDGE,{"disambiguationData":[TD([subQ6])],"derivedFrom":makeQuery(id+"FyYUAefgu6xEfva_4.23.F14.boolean.opBoolean","SPLIT",EDGE,{"disambiguationData":[TD([subQ6])],"derivedFrom":makeQuery(id+"FyYUAefgu6xEfva_4.22.F14.boolean.opBoolean","SPLIT",EDGE,{"disambiguationData":[TD([subQ6])],"derivedFrom":makeQuery(id+"FyYUAefgu6xEfva_4.21.F14.boolean.opBoolean","SPLIT",EDGE,{"disambiguationData":[TD([subQ6])],"derivedFrom":makeQuery(id+"FyYUAefgu6xEfva_4.20.F14.boolean.opBoolean","SPLIT",EDGE,{"disambiguationData":[TD([subQ6])],"derivedFrom":makeQuery(id+"FyYUAefgu6xEfva_4.19.F14.boolean.opBoolean","SPLIT",EDGE,{"disambiguationData":[TD([subQ6])],"derivedFrom":makeQuery(id+"FyYUAefgu6xEfva_4.18.F14.boolean.opBoolean","SPLIT",EDGE,{"disambiguationData":[TD([subQ6])],"derivedFrom":makeQuery(id+"FyYUAefgu6xEfva_4.17.F14.boolean.opBoolean","SPLIT",EDGE,{"disambiguationData":[TD([subQ6])],"derivedFrom":makeQuery(id+"FyYUAefgu6xEfva_4.16.F14.boolean.opBoolean","SPLIT",EDGE,{"disambiguationData":[TD([subQ6])],"derivedFrom":makeQuery(id+"FyYUAefgu6xEfva_4.15.F14.boolean.opBoolean","SPLIT",EDGE,{"disambiguationData":[TD([subQ6])],"derivedFrom":makeQuery(id+"FyYUAefgu6xEfva_4.14.F14.boolean.opBoolean","SPLIT",EDGE,{"disambiguationData":[TD([subQ6])],"derivedFrom":makeQuery(id+"FyYUAefgu6xEfva_4.13.F14.boolean.opBoolean","SPLIT",EDGE,{"disambiguationData":[TD([subQ6])],"derivedFrom":makeQuery(id+"FyYUAefgu6xEfva_4.12.F14.boolean.opBoolean","SPLIT",EDGE,{"disambiguationData":[TD([subQ6])],"derivedFrom":makeQuery(id+"FyYUAefgu6xEfva_4.11.F14.boolean.opBoolean","SPLIT",EDGE,{"disambiguationData":[TD([subQ6])],"derivedFrom":makeQuery(id+"FyYUAefgu6xEfva_4.10.F14.boolean.opBoolean","SPLIT",EDGE,{"disambiguationData":[TD([subQ6])],"derivedFrom":makeQuery(id+"FyYUAefgu6xEfva_4.9.F14.boolean.opBoolean","SPLIT",EDGE,{"disambiguationData":[TD([subQ6])],"derivedFrom":makeQuery(id+"FyYUAefgu6xEfva_4.8.F14.boolean.opBoolean","SPLIT",EDGE,{"disambiguationData":[TD([subQ6])],"derivedFrom":makeQuery(id+"FyYUAefgu6xEfva_4.7.F14.boolean.opBoolean","SPLIT",EDGE,{"disambiguationData":[TD([subQ6])],"derivedFrom":makeQuery(id+"FyYUAefgu6xEfva_4.6.F14.boolean.opBoolean","SPLIT",EDGE,{"disambiguationData":[TD([subQ6])],"derivedFrom":makeQuery(id+"FyYUAefgu6xEfva_4.5.F14.boolean.opBoolean","SPLIT",EDGE,{"disambiguationData":[TD([subQ6])],"derivedFrom":makeQuery(id+"FyYUAefgu6xEfva_4.4.F14.boolean.opBoolean","SPLIT",EDGE,{"disambiguationData":[TD([subQ6])],"derivedFrom":makeQuery(id+"FyYUAefgu6xEfva_4.3.F14.boolean.opBoolean","SPLIT",EDGE,{"disambiguationData":[TD([subQ6])],"derivedFrom":makeQuery(id+"FyYUAefgu6xEfva_4.2.F14.boolean.opBoolean","SPLIT",EDGE,{"disambiguationData":[TD([subQ6])],"derivedFrom":makeQuery(id+"FyYUAefgu6xEfva_4.1.F14.boolean.opBoolean","SPLIT",EDGE,{"disambiguationData":[TD([subQ6])],"derivedFrom":makeQuery(id+"F10.boolean.opBoolean","COPY",EDGE,{"derivedFrom":makeQuery(id+"F10.opExtrude","CAP_EDGE",EDGE,{"disambiguationData":[OSD([subQ0])],"isStart":false})})})})})})})})})})})})})})})})})})})})})})})})})})})})})})})})});}
            var Q436;
            {var subQ0=sQuery(id+"F13.wireOp",EDGE,"E148.MirrorCS");var subQ1=sQuery(id+"F13.wireOp",EDGE,"E147");var subQ2=sQuery(id+"F11.wireOp",EDGE,"E143");var subQ37=makeQuery(id+"FyYUAefgu6xEfva_4.30.F14.opExtrude","SWEPT_FACE",FACE,{"disambiguationData":[OSD([subQ0])]});var subQ38=makeQuery(id+"F14.opExtrude","SWEPT_FACE",FACE,{"disambiguationData":[OSD([subQ1])]});Q436=makeQuery(id+"FyYUAefgu6xEfva_4.31.F14.boolean.opBoolean","SPLIT",EDGE,{"disambiguationData":[TD([subQ37])],"derivedFrom":makeQuery(id+"FyYUAefgu6xEfva_4.30.F14.boolean.opBoolean","SPLIT",EDGE,{"disambiguationData":[TD([subQ38])],"derivedFrom":makeQuery(id+"FyYUAefgu6xEfva_4.29.F14.boolean.opBoolean","SPLIT",EDGE,{"disambiguationData":[TD([subQ38])],"derivedFrom":makeQuery(id+"FyYUAefgu6xEfva_4.28.F14.boolean.opBoolean","SPLIT",EDGE,{"disambiguationData":[TD([subQ38])],"derivedFrom":makeQuery(id+"FyYUAefgu6xEfva_4.27.F14.boolean.opBoolean","SPLIT",EDGE,{"disambiguationData":[TD([subQ38])],"derivedFrom":makeQuery(id+"FyYUAefgu6xEfva_4.26.F14.boolean.opBoolean","SPLIT",EDGE,{"disambiguationData":[TD([subQ38])],"derivedFrom":makeQuery(id+"FyYUAefgu6xEfva_4.25.F14.boolean.opBoolean","SPLIT",EDGE,{"disambiguationData":[TD([subQ38])],"derivedFrom":makeQuery(id+"FyYUAefgu6xEfva_4.24.F14.boolean.opBoolean","SPLIT",EDGE,{"disambiguationData":[TD([subQ38])],"derivedFrom":makeQuery(id+"FyYUAefgu6xEfva_4.23.F14.boolean.opBoolean","SPLIT",EDGE,{"disambiguationData":[TD([subQ38])],"derivedFrom":makeQuery(id+"FyYUAefgu6xEfva_4.22.F14.boolean.opBoolean","SPLIT",EDGE,{"disambiguationData":[TD([subQ38])],"derivedFrom":makeQuery(id+"FyYUAefgu6xEfva_4.21.F14.boolean.opBoolean","SPLIT",EDGE,{"disambiguationData":[TD([subQ38])],"derivedFrom":makeQuery(id+"FyYUAefgu6xEfva_4.20.F14.boolean.opBoolean","SPLIT",EDGE,{"disambiguationData":[TD([subQ38])],"derivedFrom":makeQuery(id+"FyYUAefgu6xEfva_4.19.F14.boolean.opBoolean","SPLIT",EDGE,{"disambiguationData":[TD([subQ38])],"derivedFrom":makeQuery(id+"FyYUAefgu6xEfva_4.18.F14.boolean.opBoolean","SPLIT",EDGE,{"disambiguationData":[TD([subQ38])],"derivedFrom":makeQuery(id+"FyYUAefgu6xEfva_4.17.F14.boolean.opBoolean","SPLIT",EDGE,{"disambiguationData":[TD([subQ38])],"derivedFrom":makeQuery(id+"FyYUAefgu6xEfva_4.16.F14.boolean.opBoolean","SPLIT",EDGE,{"disambiguationData":[TD([subQ38])],"derivedFrom":makeQuery(id+"FyYUAefgu6xEfva_4.15.F14.boolean.opBoolean","SPLIT",EDGE,{"disambiguationData":[TD([subQ38])],"derivedFrom":makeQuery(id+"FyYUAefgu6xEfva_4.14.F14.boolean.opBoolean","SPLIT",EDGE,{"disambiguationData":[TD([subQ38])],"derivedFrom":makeQuery(id+"FyYUAefgu6xEfva_4.13.F14.boolean.opBoolean","SPLIT",EDGE,{"disambiguationData":[TD([subQ38])],"derivedFrom":makeQuery(id+"FyYUAefgu6xEfva_4.12.F14.boolean.opBoolean","SPLIT",EDGE,{"disambiguationData":[TD([subQ38])],"derivedFrom":makeQuery(id+"FyYUAefgu6xEfva_4.11.F14.boolean.opBoolean","SPLIT",EDGE,{"disambiguationData":[TD([subQ38])],"derivedFrom":makeQuery(id+"FyYUAefgu6xEfva_4.10.F14.boolean.opBoolean","SPLIT",EDGE,{"disambiguationData":[TD([subQ38])],"derivedFrom":makeQuery(id+"FyYUAefgu6xEfva_4.9.F14.boolean.opBoolean","SPLIT",EDGE,{"disambiguationData":[TD([subQ38])],"derivedFrom":makeQuery(id+"FyYUAefgu6xEfva_4.8.F14.boolean.opBoolean","SPLIT",EDGE,{"disambiguationData":[TD([subQ38])],"derivedFrom":makeQuery(id+"FyYUAefgu6xEfva_4.7.F14.boolean.opBoolean","SPLIT",EDGE,{"disambiguationData":[TD([subQ38])],"derivedFrom":makeQuery(id+"FyYUAefgu6xEfva_4.6.F14.boolean.opBoolean","SPLIT",EDGE,{"disambiguationData":[TD([subQ38])],"derivedFrom":makeQuery(id+"FyYUAefgu6xEfva_4.5.F14.boolean.opBoolean","SPLIT",EDGE,{"disambiguationData":[TD([subQ38])],"derivedFrom":makeQuery(id+"FyYUAefgu6xEfva_4.4.F14.boolean.opBoolean","SPLIT",EDGE,{"disambiguationData":[TD([subQ38])],"derivedFrom":makeQuery(id+"FyYUAefgu6xEfva_4.3.F14.boolean.opBoolean","SPLIT",EDGE,{"disambiguationData":[TD([subQ38])],"derivedFrom":makeQuery(id+"FyYUAefgu6xEfva_4.2.F14.boolean.opBoolean","SPLIT",EDGE,{"disambiguationData":[TD([subQ38])],"derivedFrom":makeQuery(id+"FyYUAefgu6xEfva_4.1.F14.boolean.opBoolean","SPLIT",EDGE,{"disambiguationData":[TD([subQ38])],"derivedFrom":makeQuery(id+"F12.opExtrude","CAP_EDGE",EDGE,{"disambiguationData":[OSD([subQ2])],"isStart":false})})})})})})})})})})})})})})})})})})})})})})})})})})})})})})})});}
            var Q437;
            Q437=makeQuery(id+"FyYUAefgu6xEfva_4.32.F14.opExtrude","SWEPT_EDGE",EDGE,{"disambiguationData":[OSD([sQuery(id+"F9.wireOp",EDGE,"E142"),sQuery(id+"F13.wireOp",EDGE,"E147")])]});
            var Q438;
            Q438=makeQuery(id+"FyYUAefgu6xEfva_4.32.F14.opExtrude","SWEPT_EDGE",EDGE,{"disambiguationData":[OSD([sQuery(id+"F11.wireOp",EDGE,"E143"),sQuery(id+"F13.wireOp",EDGE,"E147")])]});
            var Q439;
            Q439=makeQuery(id+"FyYUAefgu6xEfva_4.32.F14.opExtrude","SWEPT_EDGE",EDGE,{"disambiguationData":[OSD([sQuery(id+"F9.wireOp",EDGE,"E142"),sQuery(id+"F13.wireOp",EDGE,"E148.MirrorCS")])]});
            var Q440;
            Q440=makeQuery(id+"FyYUAefgu6xEfva_4.32.F14.opExtrude","SWEPT_EDGE",EDGE,{"disambiguationData":[OSD([sQuery(id+"F11.wireOp",EDGE,"E143"),sQuery(id+"F13.wireOp",EDGE,"E148.MirrorCS")])]});
            var Q441;
            Q441=makeQuery(id+"FyYUAefgu6xEfva_4.32.F14.opExtrude","CAP_EDGE",EDGE,{"disambiguationData":[OSD([sQuery(id+"F13.wireOp",EDGE,"E147")])],"isStart":true});
            var Q442;
            Q442=makeQuery(id+"FyYUAefgu6xEfva_4.32.F14.opExtrude","CAP_EDGE",EDGE,{"disambiguationData":[OSD([sQuery(id+"F13.wireOp",EDGE,"E148.MirrorCS")])],"isStart":true});
            var Q443;
            Q443=makeQuery(id+"FyYUAefgu6xEfva_4.32.F14.opExtrude","CAP_EDGE",EDGE,{"disambiguationData":[OSD([sQuery(id+"F9.wireOp",EDGE,"E142")])],"isStart":false});
            var Q444;
            {var subQ0=sQuery(id+"F13.wireOp",EDGE,"E148.MirrorCS");var subQ1=sQuery(id+"F13.wireOp",EDGE,"E147");var subQ2=sQuery(id+"F11.wireOp",EDGE,"E143");var subQ19=makeQuery(id+"FyYUAefgu6xEfva_4.31.F14.opExtrude","SWEPT_FACE",FACE,{"disambiguationData":[OSD([subQ0])]});var subQ39=makeQuery(id+"F14.opExtrude","SWEPT_FACE",FACE,{"disambiguationData":[OSD([subQ1])]});Q444=makeQuery(id+"FyYUAefgu6xEfva_4.32.F14.boolean.opBoolean","SPLIT",EDGE,{"disambiguationData":[TD([subQ19])],"derivedFrom":makeQuery(id+"FyYUAefgu6xEfva_4.31.F14.boolean.opBoolean","SPLIT",EDGE,{"disambiguationData":[TD([subQ39])],"derivedFrom":makeQuery(id+"FyYUAefgu6xEfva_4.30.F14.boolean.opBoolean","SPLIT",EDGE,{"disambiguationData":[TD([subQ39])],"derivedFrom":makeQuery(id+"FyYUAefgu6xEfva_4.29.F14.boolean.opBoolean","SPLIT",EDGE,{"disambiguationData":[TD([subQ39])],"derivedFrom":makeQuery(id+"FyYUAefgu6xEfva_4.28.F14.boolean.opBoolean","SPLIT",EDGE,{"disambiguationData":[TD([subQ39])],"derivedFrom":makeQuery(id+"FyYUAefgu6xEfva_4.27.F14.boolean.opBoolean","SPLIT",EDGE,{"disambiguationData":[TD([subQ39])],"derivedFrom":makeQuery(id+"FyYUAefgu6xEfva_4.26.F14.boolean.opBoolean","SPLIT",EDGE,{"disambiguationData":[TD([subQ39])],"derivedFrom":makeQuery(id+"FyYUAefgu6xEfva_4.25.F14.boolean.opBoolean","SPLIT",EDGE,{"disambiguationData":[TD([subQ39])],"derivedFrom":makeQuery(id+"FyYUAefgu6xEfva_4.24.F14.boolean.opBoolean","SPLIT",EDGE,{"disambiguationData":[TD([subQ39])],"derivedFrom":makeQuery(id+"FyYUAefgu6xEfva_4.23.F14.boolean.opBoolean","SPLIT",EDGE,{"disambiguationData":[TD([subQ39])],"derivedFrom":makeQuery(id+"FyYUAefgu6xEfva_4.22.F14.boolean.opBoolean","SPLIT",EDGE,{"disambiguationData":[TD([subQ39])],"derivedFrom":makeQuery(id+"FyYUAefgu6xEfva_4.21.F14.boolean.opBoolean","SPLIT",EDGE,{"disambiguationData":[TD([subQ39])],"derivedFrom":makeQuery(id+"FyYUAefgu6xEfva_4.20.F14.boolean.opBoolean","SPLIT",EDGE,{"disambiguationData":[TD([subQ39])],"derivedFrom":makeQuery(id+"FyYUAefgu6xEfva_4.19.F14.boolean.opBoolean","SPLIT",EDGE,{"disambiguationData":[TD([subQ39])],"derivedFrom":makeQuery(id+"FyYUAefgu6xEfva_4.18.F14.boolean.opBoolean","SPLIT",EDGE,{"disambiguationData":[TD([subQ39])],"derivedFrom":makeQuery(id+"FyYUAefgu6xEfva_4.17.F14.boolean.opBoolean","SPLIT",EDGE,{"disambiguationData":[TD([subQ39])],"derivedFrom":makeQuery(id+"FyYUAefgu6xEfva_4.16.F14.boolean.opBoolean","SPLIT",EDGE,{"disambiguationData":[TD([subQ39])],"derivedFrom":makeQuery(id+"FyYUAefgu6xEfva_4.15.F14.boolean.opBoolean","SPLIT",EDGE,{"disambiguationData":[TD([subQ39])],"derivedFrom":makeQuery(id+"FyYUAefgu6xEfva_4.14.F14.boolean.opBoolean","SPLIT",EDGE,{"disambiguationData":[TD([subQ39])],"derivedFrom":makeQuery(id+"FyYUAefgu6xEfva_4.13.F14.boolean.opBoolean","SPLIT",EDGE,{"disambiguationData":[TD([subQ39])],"derivedFrom":makeQuery(id+"FyYUAefgu6xEfva_4.12.F14.boolean.opBoolean","SPLIT",EDGE,{"disambiguationData":[TD([subQ39])],"derivedFrom":makeQuery(id+"FyYUAefgu6xEfva_4.11.F14.boolean.opBoolean","SPLIT",EDGE,{"disambiguationData":[TD([subQ39])],"derivedFrom":makeQuery(id+"FyYUAefgu6xEfva_4.10.F14.boolean.opBoolean","SPLIT",EDGE,{"disambiguationData":[TD([subQ39])],"derivedFrom":makeQuery(id+"FyYUAefgu6xEfva_4.9.F14.boolean.opBoolean","SPLIT",EDGE,{"disambiguationData":[TD([subQ39])],"derivedFrom":makeQuery(id+"FyYUAefgu6xEfva_4.8.F14.boolean.opBoolean","SPLIT",EDGE,{"disambiguationData":[TD([subQ39])],"derivedFrom":makeQuery(id+"FyYUAefgu6xEfva_4.7.F14.boolean.opBoolean","SPLIT",EDGE,{"disambiguationData":[TD([subQ39])],"derivedFrom":makeQuery(id+"FyYUAefgu6xEfva_4.6.F14.boolean.opBoolean","SPLIT",EDGE,{"disambiguationData":[TD([subQ39])],"derivedFrom":makeQuery(id+"FyYUAefgu6xEfva_4.5.F14.boolean.opBoolean","SPLIT",EDGE,{"disambiguationData":[TD([subQ39])],"derivedFrom":makeQuery(id+"FyYUAefgu6xEfva_4.4.F14.boolean.opBoolean","SPLIT",EDGE,{"disambiguationData":[TD([subQ39])],"derivedFrom":makeQuery(id+"FyYUAefgu6xEfva_4.3.F14.boolean.opBoolean","SPLIT",EDGE,{"disambiguationData":[TD([subQ39])],"derivedFrom":makeQuery(id+"FyYUAefgu6xEfva_4.2.F14.boolean.opBoolean","SPLIT",EDGE,{"disambiguationData":[TD([subQ39])],"derivedFrom":makeQuery(id+"FyYUAefgu6xEfva_4.1.F14.boolean.opBoolean","SPLIT",EDGE,{"disambiguationData":[TD([subQ39])],"derivedFrom":makeQuery(id+"F12.opExtrude","CAP_EDGE",EDGE,{"disambiguationData":[OSD([subQ2])],"isStart":false})})})})})})})})})})})})})})})})})})})})})})})})})})})})})})})})});}
            var Q445;
            Q445=makeQuery(id+"FyYUAefgu6xEfva_4.33.F14.opExtrude","SWEPT_EDGE",EDGE,{"disambiguationData":[OSD([sQuery(id+"F9.wireOp",EDGE,"E142"),sQuery(id+"F13.wireOp",EDGE,"E147")])]});
            var Q446;
            Q446=makeQuery(id+"FyYUAefgu6xEfva_4.33.F14.opExtrude","SWEPT_EDGE",EDGE,{"disambiguationData":[OSD([sQuery(id+"F11.wireOp",EDGE,"E143"),sQuery(id+"F13.wireOp",EDGE,"E147")])]});
            var Q447;
            Q447=makeQuery(id+"FyYUAefgu6xEfva_4.33.F14.opExtrude","SWEPT_EDGE",EDGE,{"disambiguationData":[OSD([sQuery(id+"F9.wireOp",EDGE,"E142"),sQuery(id+"F13.wireOp",EDGE,"E148.MirrorCS")])]});
            var Q448;
            Q448=makeQuery(id+"FyYUAefgu6xEfva_4.33.F14.opExtrude","SWEPT_EDGE",EDGE,{"disambiguationData":[OSD([sQuery(id+"F11.wireOp",EDGE,"E143"),sQuery(id+"F13.wireOp",EDGE,"E148.MirrorCS")])]});
            var Q449;
            Q449=makeQuery(id+"FyYUAefgu6xEfva_4.33.F14.opExtrude","CAP_EDGE",EDGE,{"disambiguationData":[OSD([sQuery(id+"F9.wireOp",EDGE,"E142")])],"isStart":false});
            var Q450;
            {var subQ0=sQuery(id+"F9.wireOp",EDGE,"E142");var subQ3=sQuery(id+"F13.wireOp",EDGE,"E148.MirrorCS");var subQ4=makeQuery(id+"FyYUAefgu6xEfva_4.32.F14.opExtrude","SWEPT_FACE",FACE,{"disambiguationData":[OSD([subQ3])]});var subQ5=sQuery(id+"F13.wireOp",EDGE,"E147");var subQ6=makeQuery(id+"F14.opExtrude","SWEPT_FACE",FACE,{"disambiguationData":[OSD([subQ5])]});Q450=makeQuery(id+"FyYUAefgu6xEfva_4.33.F14.boolean.opBoolean","SPLIT",EDGE,{"disambiguationData":[TD([subQ4])],"derivedFrom":makeQuery(id+"FyYUAefgu6xEfva_4.32.F14.boolean.opBoolean","SPLIT",EDGE,{"disambiguationData":[TD([subQ6])],"derivedFrom":makeQuery(id+"FyYUAefgu6xEfva_4.31.F14.boolean.opBoolean","SPLIT",EDGE,{"disambiguationData":[TD([subQ6])],"derivedFrom":makeQuery(id+"FyYUAefgu6xEfva_4.30.F14.boolean.opBoolean","SPLIT",EDGE,{"disambiguationData":[TD([subQ6])],"derivedFrom":makeQuery(id+"FyYUAefgu6xEfva_4.29.F14.boolean.opBoolean","SPLIT",EDGE,{"disambiguationData":[TD([subQ6])],"derivedFrom":makeQuery(id+"FyYUAefgu6xEfva_4.28.F14.boolean.opBoolean","SPLIT",EDGE,{"disambiguationData":[TD([subQ6])],"derivedFrom":makeQuery(id+"FyYUAefgu6xEfva_4.27.F14.boolean.opBoolean","SPLIT",EDGE,{"disambiguationData":[TD([subQ6])],"derivedFrom":makeQuery(id+"FyYUAefgu6xEfva_4.26.F14.boolean.opBoolean","SPLIT",EDGE,{"disambiguationData":[TD([subQ6])],"derivedFrom":makeQuery(id+"FyYUAefgu6xEfva_4.25.F14.boolean.opBoolean","SPLIT",EDGE,{"disambiguationData":[TD([subQ6])],"derivedFrom":makeQuery(id+"FyYUAefgu6xEfva_4.24.F14.boolean.opBoolean","SPLIT",EDGE,{"disambiguationData":[TD([subQ6])],"derivedFrom":makeQuery(id+"FyYUAefgu6xEfva_4.23.F14.boolean.opBoolean","SPLIT",EDGE,{"disambiguationData":[TD([subQ6])],"derivedFrom":makeQuery(id+"FyYUAefgu6xEfva_4.22.F14.boolean.opBoolean","SPLIT",EDGE,{"disambiguationData":[TD([subQ6])],"derivedFrom":makeQuery(id+"FyYUAefgu6xEfva_4.21.F14.boolean.opBoolean","SPLIT",EDGE,{"disambiguationData":[TD([subQ6])],"derivedFrom":makeQuery(id+"FyYUAefgu6xEfva_4.20.F14.boolean.opBoolean","SPLIT",EDGE,{"disambiguationData":[TD([subQ6])],"derivedFrom":makeQuery(id+"FyYUAefgu6xEfva_4.19.F14.boolean.opBoolean","SPLIT",EDGE,{"disambiguationData":[TD([subQ6])],"derivedFrom":makeQuery(id+"FyYUAefgu6xEfva_4.18.F14.boolean.opBoolean","SPLIT",EDGE,{"disambiguationData":[TD([subQ6])],"derivedFrom":makeQuery(id+"FyYUAefgu6xEfva_4.17.F14.boolean.opBoolean","SPLIT",EDGE,{"disambiguationData":[TD([subQ6])],"derivedFrom":makeQuery(id+"FyYUAefgu6xEfva_4.16.F14.boolean.opBoolean","SPLIT",EDGE,{"disambiguationData":[TD([subQ6])],"derivedFrom":makeQuery(id+"FyYUAefgu6xEfva_4.15.F14.boolean.opBoolean","SPLIT",EDGE,{"disambiguationData":[TD([subQ6])],"derivedFrom":makeQuery(id+"FyYUAefgu6xEfva_4.14.F14.boolean.opBoolean","SPLIT",EDGE,{"disambiguationData":[TD([subQ6])],"derivedFrom":makeQuery(id+"FyYUAefgu6xEfva_4.13.F14.boolean.opBoolean","SPLIT",EDGE,{"disambiguationData":[TD([subQ6])],"derivedFrom":makeQuery(id+"FyYUAefgu6xEfva_4.12.F14.boolean.opBoolean","SPLIT",EDGE,{"disambiguationData":[TD([subQ6])],"derivedFrom":makeQuery(id+"FyYUAefgu6xEfva_4.11.F14.boolean.opBoolean","SPLIT",EDGE,{"disambiguationData":[TD([subQ6])],"derivedFrom":makeQuery(id+"FyYUAefgu6xEfva_4.10.F14.boolean.opBoolean","SPLIT",EDGE,{"disambiguationData":[TD([subQ6])],"derivedFrom":makeQuery(id+"FyYUAefgu6xEfva_4.9.F14.boolean.opBoolean","SPLIT",EDGE,{"disambiguationData":[TD([subQ6])],"derivedFrom":makeQuery(id+"FyYUAefgu6xEfva_4.8.F14.boolean.opBoolean","SPLIT",EDGE,{"disambiguationData":[TD([subQ6])],"derivedFrom":makeQuery(id+"FyYUAefgu6xEfva_4.7.F14.boolean.opBoolean","SPLIT",EDGE,{"disambiguationData":[TD([subQ6])],"derivedFrom":makeQuery(id+"FyYUAefgu6xEfva_4.6.F14.boolean.opBoolean","SPLIT",EDGE,{"disambiguationData":[TD([subQ6])],"derivedFrom":makeQuery(id+"FyYUAefgu6xEfva_4.5.F14.boolean.opBoolean","SPLIT",EDGE,{"disambiguationData":[TD([subQ6])],"derivedFrom":makeQuery(id+"FyYUAefgu6xEfva_4.4.F14.boolean.opBoolean","SPLIT",EDGE,{"disambiguationData":[TD([subQ6])],"derivedFrom":makeQuery(id+"FyYUAefgu6xEfva_4.3.F14.boolean.opBoolean","SPLIT",EDGE,{"disambiguationData":[TD([subQ6])],"derivedFrom":makeQuery(id+"FyYUAefgu6xEfva_4.2.F14.boolean.opBoolean","SPLIT",EDGE,{"disambiguationData":[TD([subQ6])],"derivedFrom":makeQuery(id+"FyYUAefgu6xEfva_4.1.F14.boolean.opBoolean","SPLIT",EDGE,{"disambiguationData":[TD([subQ6])],"derivedFrom":makeQuery(id+"F10.boolean.opBoolean","COPY",EDGE,{"derivedFrom":makeQuery(id+"F10.opExtrude","CAP_EDGE",EDGE,{"disambiguationData":[OSD([subQ0])],"isStart":false})})})})})})})})})})})})})})})})})})})})})})})})})})})})})})})})})})});}
            var Q451;
            {var subQ0=sQuery(id+"F13.wireOp",EDGE,"E148.MirrorCS");var subQ1=sQuery(id+"F13.wireOp",EDGE,"E147");var subQ2=sQuery(id+"F11.wireOp",EDGE,"E143");var subQ18=makeQuery(id+"FyYUAefgu6xEfva_4.32.F14.opExtrude","SWEPT_FACE",FACE,{"disambiguationData":[OSD([subQ0])]});var subQ40=makeQuery(id+"F14.opExtrude","SWEPT_FACE",FACE,{"disambiguationData":[OSD([subQ1])]});Q451=makeQuery(id+"FyYUAefgu6xEfva_4.33.F14.boolean.opBoolean","SPLIT",EDGE,{"disambiguationData":[TD([subQ18])],"derivedFrom":makeQuery(id+"FyYUAefgu6xEfva_4.32.F14.boolean.opBoolean","SPLIT",EDGE,{"disambiguationData":[TD([subQ40])],"derivedFrom":makeQuery(id+"FyYUAefgu6xEfva_4.31.F14.boolean.opBoolean","SPLIT",EDGE,{"disambiguationData":[TD([subQ40])],"derivedFrom":makeQuery(id+"FyYUAefgu6xEfva_4.30.F14.boolean.opBoolean","SPLIT",EDGE,{"disambiguationData":[TD([subQ40])],"derivedFrom":makeQuery(id+"FyYUAefgu6xEfva_4.29.F14.boolean.opBoolean","SPLIT",EDGE,{"disambiguationData":[TD([subQ40])],"derivedFrom":makeQuery(id+"FyYUAefgu6xEfva_4.28.F14.boolean.opBoolean","SPLIT",EDGE,{"disambiguationData":[TD([subQ40])],"derivedFrom":makeQuery(id+"FyYUAefgu6xEfva_4.27.F14.boolean.opBoolean","SPLIT",EDGE,{"disambiguationData":[TD([subQ40])],"derivedFrom":makeQuery(id+"FyYUAefgu6xEfva_4.26.F14.boolean.opBoolean","SPLIT",EDGE,{"disambiguationData":[TD([subQ40])],"derivedFrom":makeQuery(id+"FyYUAefgu6xEfva_4.25.F14.boolean.opBoolean","SPLIT",EDGE,{"disambiguationData":[TD([subQ40])],"derivedFrom":makeQuery(id+"FyYUAefgu6xEfva_4.24.F14.boolean.opBoolean","SPLIT",EDGE,{"disambiguationData":[TD([subQ40])],"derivedFrom":makeQuery(id+"FyYUAefgu6xEfva_4.23.F14.boolean.opBoolean","SPLIT",EDGE,{"disambiguationData":[TD([subQ40])],"derivedFrom":makeQuery(id+"FyYUAefgu6xEfva_4.22.F14.boolean.opBoolean","SPLIT",EDGE,{"disambiguationData":[TD([subQ40])],"derivedFrom":makeQuery(id+"FyYUAefgu6xEfva_4.21.F14.boolean.opBoolean","SPLIT",EDGE,{"disambiguationData":[TD([subQ40])],"derivedFrom":makeQuery(id+"FyYUAefgu6xEfva_4.20.F14.boolean.opBoolean","SPLIT",EDGE,{"disambiguationData":[TD([subQ40])],"derivedFrom":makeQuery(id+"FyYUAefgu6xEfva_4.19.F14.boolean.opBoolean","SPLIT",EDGE,{"disambiguationData":[TD([subQ40])],"derivedFrom":makeQuery(id+"FyYUAefgu6xEfva_4.18.F14.boolean.opBoolean","SPLIT",EDGE,{"disambiguationData":[TD([subQ40])],"derivedFrom":makeQuery(id+"FyYUAefgu6xEfva_4.17.F14.boolean.opBoolean","SPLIT",EDGE,{"disambiguationData":[TD([subQ40])],"derivedFrom":makeQuery(id+"FyYUAefgu6xEfva_4.16.F14.boolean.opBoolean","SPLIT",EDGE,{"disambiguationData":[TD([subQ40])],"derivedFrom":makeQuery(id+"FyYUAefgu6xEfva_4.15.F14.boolean.opBoolean","SPLIT",EDGE,{"disambiguationData":[TD([subQ40])],"derivedFrom":makeQuery(id+"FyYUAefgu6xEfva_4.14.F14.boolean.opBoolean","SPLIT",EDGE,{"disambiguationData":[TD([subQ40])],"derivedFrom":makeQuery(id+"FyYUAefgu6xEfva_4.13.F14.boolean.opBoolean","SPLIT",EDGE,{"disambiguationData":[TD([subQ40])],"derivedFrom":makeQuery(id+"FyYUAefgu6xEfva_4.12.F14.boolean.opBoolean","SPLIT",EDGE,{"disambiguationData":[TD([subQ40])],"derivedFrom":makeQuery(id+"FyYUAefgu6xEfva_4.11.F14.boolean.opBoolean","SPLIT",EDGE,{"disambiguationData":[TD([subQ40])],"derivedFrom":makeQuery(id+"FyYUAefgu6xEfva_4.10.F14.boolean.opBoolean","SPLIT",EDGE,{"disambiguationData":[TD([subQ40])],"derivedFrom":makeQuery(id+"FyYUAefgu6xEfva_4.9.F14.boolean.opBoolean","SPLIT",EDGE,{"disambiguationData":[TD([subQ40])],"derivedFrom":makeQuery(id+"FyYUAefgu6xEfva_4.8.F14.boolean.opBoolean","SPLIT",EDGE,{"disambiguationData":[TD([subQ40])],"derivedFrom":makeQuery(id+"FyYUAefgu6xEfva_4.7.F14.boolean.opBoolean","SPLIT",EDGE,{"disambiguationData":[TD([subQ40])],"derivedFrom":makeQuery(id+"FyYUAefgu6xEfva_4.6.F14.boolean.opBoolean","SPLIT",EDGE,{"disambiguationData":[TD([subQ40])],"derivedFrom":makeQuery(id+"FyYUAefgu6xEfva_4.5.F14.boolean.opBoolean","SPLIT",EDGE,{"disambiguationData":[TD([subQ40])],"derivedFrom":makeQuery(id+"FyYUAefgu6xEfva_4.4.F14.boolean.opBoolean","SPLIT",EDGE,{"disambiguationData":[TD([subQ40])],"derivedFrom":makeQuery(id+"FyYUAefgu6xEfva_4.3.F14.boolean.opBoolean","SPLIT",EDGE,{"disambiguationData":[TD([subQ40])],"derivedFrom":makeQuery(id+"FyYUAefgu6xEfva_4.2.F14.boolean.opBoolean","SPLIT",EDGE,{"disambiguationData":[TD([subQ40])],"derivedFrom":makeQuery(id+"FyYUAefgu6xEfva_4.1.F14.boolean.opBoolean","SPLIT",EDGE,{"disambiguationData":[TD([subQ40])],"derivedFrom":makeQuery(id+"F12.opExtrude","CAP_EDGE",EDGE,{"disambiguationData":[OSD([subQ2])],"isStart":false})})})})})})})})})})})})})})})})})})})})})})})})})})})})})})})})})});}
            var Q452;
            Q452=makeQuery(id+"FyYUAefgu6xEfva_4.34.F14.opExtrude","CAP_EDGE",EDGE,{"disambiguationData":[OSD([sQuery(id+"F13.wireOp",EDGE,"E147")])],"isStart":false});
            var Q453;
            Q453=makeQuery(id+"FyYUAefgu6xEfva_4.34.F14.opExtrude","SWEPT_EDGE",EDGE,{"disambiguationData":[OSD([sQuery(id+"F9.wireOp",EDGE,"E142"),sQuery(id+"F13.wireOp",EDGE,"E147")])]});
            var Q454;
            Q454=makeQuery(id+"FyYUAefgu6xEfva_4.34.F14.opExtrude","SWEPT_EDGE",EDGE,{"disambiguationData":[OSD([sQuery(id+"F9.wireOp",EDGE,"E142"),sQuery(id+"F13.wireOp",EDGE,"E148.MirrorCS")])]});
            var Q455;
            Q455=makeQuery(id+"FyYUAefgu6xEfva_4.34.F14.opExtrude","SWEPT_EDGE",EDGE,{"disambiguationData":[OSD([sQuery(id+"F11.wireOp",EDGE,"E143"),sQuery(id+"F13.wireOp",EDGE,"E148.MirrorCS")])]});
            var Q456;
            Q456=makeQuery(id+"FyYUAefgu6xEfva_4.34.F14.opExtrude","CAP_EDGE",EDGE,{"disambiguationData":[OSD([sQuery(id+"F13.wireOp",EDGE,"E147")])],"isStart":true});
            var Q457;
            Q457=makeQuery(id+"FyYUAefgu6xEfva_4.34.F14.opExtrude","CAP_EDGE",EDGE,{"disambiguationData":[OSD([sQuery(id+"F13.wireOp",EDGE,"E148.MirrorCS")])],"isStart":true});
            var Q458;
            Q458=makeQuery(id+"FyYUAefgu6xEfva_4.34.F14.opExtrude","CAP_EDGE",EDGE,{"disambiguationData":[OSD([sQuery(id+"F9.wireOp",EDGE,"E142")])],"isStart":false});
            var Q459;
            {var subQ0=sQuery(id+"F13.wireOp",EDGE,"E148.MirrorCS");var subQ1=sQuery(id+"F13.wireOp",EDGE,"E147");var subQ2=sQuery(id+"F11.wireOp",EDGE,"E143");var subQ22=makeQuery(id+"FyYUAefgu6xEfva_4.33.F14.opExtrude","SWEPT_FACE",FACE,{"disambiguationData":[OSD([subQ0])]});var subQ41=makeQuery(id+"F14.opExtrude","SWEPT_FACE",FACE,{"disambiguationData":[OSD([subQ1])]});Q459=makeQuery(id+"FyYUAefgu6xEfva_4.34.F14.boolean.opBoolean","SPLIT",EDGE,{"disambiguationData":[TD([subQ22])],"derivedFrom":makeQuery(id+"FyYUAefgu6xEfva_4.33.F14.boolean.opBoolean","SPLIT",EDGE,{"disambiguationData":[TD([subQ41])],"derivedFrom":makeQuery(id+"FyYUAefgu6xEfva_4.32.F14.boolean.opBoolean","SPLIT",EDGE,{"disambiguationData":[TD([subQ41])],"derivedFrom":makeQuery(id+"FyYUAefgu6xEfva_4.31.F14.boolean.opBoolean","SPLIT",EDGE,{"disambiguationData":[TD([subQ41])],"derivedFrom":makeQuery(id+"FyYUAefgu6xEfva_4.30.F14.boolean.opBoolean","SPLIT",EDGE,{"disambiguationData":[TD([subQ41])],"derivedFrom":makeQuery(id+"FyYUAefgu6xEfva_4.29.F14.boolean.opBoolean","SPLIT",EDGE,{"disambiguationData":[TD([subQ41])],"derivedFrom":makeQuery(id+"FyYUAefgu6xEfva_4.28.F14.boolean.opBoolean","SPLIT",EDGE,{"disambiguationData":[TD([subQ41])],"derivedFrom":makeQuery(id+"FyYUAefgu6xEfva_4.27.F14.boolean.opBoolean","SPLIT",EDGE,{"disambiguationData":[TD([subQ41])],"derivedFrom":makeQuery(id+"FyYUAefgu6xEfva_4.26.F14.boolean.opBoolean","SPLIT",EDGE,{"disambiguationData":[TD([subQ41])],"derivedFrom":makeQuery(id+"FyYUAefgu6xEfva_4.25.F14.boolean.opBoolean","SPLIT",EDGE,{"disambiguationData":[TD([subQ41])],"derivedFrom":makeQuery(id+"FyYUAefgu6xEfva_4.24.F14.boolean.opBoolean","SPLIT",EDGE,{"disambiguationData":[TD([subQ41])],"derivedFrom":makeQuery(id+"FyYUAefgu6xEfva_4.23.F14.boolean.opBoolean","SPLIT",EDGE,{"disambiguationData":[TD([subQ41])],"derivedFrom":makeQuery(id+"FyYUAefgu6xEfva_4.22.F14.boolean.opBoolean","SPLIT",EDGE,{"disambiguationData":[TD([subQ41])],"derivedFrom":makeQuery(id+"FyYUAefgu6xEfva_4.21.F14.boolean.opBoolean","SPLIT",EDGE,{"disambiguationData":[TD([subQ41])],"derivedFrom":makeQuery(id+"FyYUAefgu6xEfva_4.20.F14.boolean.opBoolean","SPLIT",EDGE,{"disambiguationData":[TD([subQ41])],"derivedFrom":makeQuery(id+"FyYUAefgu6xEfva_4.19.F14.boolean.opBoolean","SPLIT",EDGE,{"disambiguationData":[TD([subQ41])],"derivedFrom":makeQuery(id+"FyYUAefgu6xEfva_4.18.F14.boolean.opBoolean","SPLIT",EDGE,{"disambiguationData":[TD([subQ41])],"derivedFrom":makeQuery(id+"FyYUAefgu6xEfva_4.17.F14.boolean.opBoolean","SPLIT",EDGE,{"disambiguationData":[TD([subQ41])],"derivedFrom":makeQuery(id+"FyYUAefgu6xEfva_4.16.F14.boolean.opBoolean","SPLIT",EDGE,{"disambiguationData":[TD([subQ41])],"derivedFrom":makeQuery(id+"FyYUAefgu6xEfva_4.15.F14.boolean.opBoolean","SPLIT",EDGE,{"disambiguationData":[TD([subQ41])],"derivedFrom":makeQuery(id+"FyYUAefgu6xEfva_4.14.F14.boolean.opBoolean","SPLIT",EDGE,{"disambiguationData":[TD([subQ41])],"derivedFrom":makeQuery(id+"FyYUAefgu6xEfva_4.13.F14.boolean.opBoolean","SPLIT",EDGE,{"disambiguationData":[TD([subQ41])],"derivedFrom":makeQuery(id+"FyYUAefgu6xEfva_4.12.F14.boolean.opBoolean","SPLIT",EDGE,{"disambiguationData":[TD([subQ41])],"derivedFrom":makeQuery(id+"FyYUAefgu6xEfva_4.11.F14.boolean.opBoolean","SPLIT",EDGE,{"disambiguationData":[TD([subQ41])],"derivedFrom":makeQuery(id+"FyYUAefgu6xEfva_4.10.F14.boolean.opBoolean","SPLIT",EDGE,{"disambiguationData":[TD([subQ41])],"derivedFrom":makeQuery(id+"FyYUAefgu6xEfva_4.9.F14.boolean.opBoolean","SPLIT",EDGE,{"disambiguationData":[TD([subQ41])],"derivedFrom":makeQuery(id+"FyYUAefgu6xEfva_4.8.F14.boolean.opBoolean","SPLIT",EDGE,{"disambiguationData":[TD([subQ41])],"derivedFrom":makeQuery(id+"FyYUAefgu6xEfva_4.7.F14.boolean.opBoolean","SPLIT",EDGE,{"disambiguationData":[TD([subQ41])],"derivedFrom":makeQuery(id+"FyYUAefgu6xEfva_4.6.F14.boolean.opBoolean","SPLIT",EDGE,{"disambiguationData":[TD([subQ41])],"derivedFrom":makeQuery(id+"FyYUAefgu6xEfva_4.5.F14.boolean.opBoolean","SPLIT",EDGE,{"disambiguationData":[TD([subQ41])],"derivedFrom":makeQuery(id+"FyYUAefgu6xEfva_4.4.F14.boolean.opBoolean","SPLIT",EDGE,{"disambiguationData":[TD([subQ41])],"derivedFrom":makeQuery(id+"FyYUAefgu6xEfva_4.3.F14.boolean.opBoolean","SPLIT",EDGE,{"disambiguationData":[TD([subQ41])],"derivedFrom":makeQuery(id+"FyYUAefgu6xEfva_4.2.F14.boolean.opBoolean","SPLIT",EDGE,{"disambiguationData":[TD([subQ41])],"derivedFrom":makeQuery(id+"FyYUAefgu6xEfva_4.1.F14.boolean.opBoolean","SPLIT",EDGE,{"disambiguationData":[TD([subQ41])],"derivedFrom":makeQuery(id+"F12.opExtrude","CAP_EDGE",EDGE,{"disambiguationData":[OSD([subQ2])],"isStart":false})})})})})})})})})})})})})})})})})})})})})})})})})})})})})})})})})})});}
            var Q460;
            Q460=makeQuery(id+"FyYUAefgu6xEfva_4.35.F14.opExtrude","CAP_EDGE",EDGE,{"disambiguationData":[OSD([sQuery(id+"F13.wireOp",EDGE,"E147")])],"isStart":false});
            var Q461;
            Q461=makeQuery(id+"FyYUAefgu6xEfva_4.35.F14.opExtrude","SWEPT_EDGE",EDGE,{"disambiguationData":[OSD([sQuery(id+"F9.wireOp",EDGE,"E142"),sQuery(id+"F13.wireOp",EDGE,"E147")])]});
            var Q462;
            Q462=makeQuery(id+"FyYUAefgu6xEfva_4.35.F14.opExtrude","SWEPT_EDGE",EDGE,{"disambiguationData":[OSD([sQuery(id+"F9.wireOp",EDGE,"E142"),sQuery(id+"F13.wireOp",EDGE,"E148.MirrorCS")])]});
            var Q463;
            Q463=makeQuery(id+"FyYUAefgu6xEfva_4.35.F14.opExtrude","SWEPT_EDGE",EDGE,{"disambiguationData":[OSD([sQuery(id+"F11.wireOp",EDGE,"E143"),sQuery(id+"F13.wireOp",EDGE,"E148.MirrorCS")])]});
            var Q464;
            Q464=makeQuery(id+"FyYUAefgu6xEfva_4.35.F14.opExtrude","CAP_EDGE",EDGE,{"disambiguationData":[OSD([sQuery(id+"F13.wireOp",EDGE,"E147")])],"isStart":true});
            var Q465;
            Q465=makeQuery(id+"FyYUAefgu6xEfva_4.35.F14.opExtrude","CAP_EDGE",EDGE,{"disambiguationData":[OSD([sQuery(id+"F13.wireOp",EDGE,"E148.MirrorCS")])],"isStart":true});
            var Q466;
            Q466=makeQuery(id+"FyYUAefgu6xEfva_4.35.F14.opExtrude","CAP_EDGE",EDGE,{"disambiguationData":[OSD([sQuery(id+"F9.wireOp",EDGE,"E142")])],"isStart":false});
            var Q467;
            Q467=makeQuery(id+"FyYUAefgu6xEfva_4.39.F14.opExtrude","CAP_EDGE",EDGE,{"disambiguationData":[OSD([sQuery(id+"F13.wireOp",EDGE,"E148.MirrorCS")])],"isStart":true});
            var Q468;
            Q468=makeQuery(id+"FyYUAefgu6xEfva_4.39.F14.opExtrude","CAP_EDGE",EDGE,{"disambiguationData":[OSD([sQuery(id+"F13.wireOp",EDGE,"E147")])],"isStart":true});
            var Q469;
            {var subQ1=sQuery(id+"F11.wireOp",EDGE,"E143");var subQ3=sQuery(id+"F13.wireOp",EDGE,"E147");var subQ4=sQuery(id+"F13.wireOp",EDGE,"E148.MirrorCS");var subQ5=makeQuery(id+"FyYUAefgu6xEfva_4.37.F14.opExtrude","SWEPT_FACE",FACE,{"disambiguationData":[OSD([subQ4])]});var subQ6=makeQuery(id+"F14.opExtrude","SWEPT_FACE",FACE,{"disambiguationData":[OSD([subQ3])]});Q469=makeQuery(id+"FyYUAefgu6xEfva_4.38.F14.boolean.opBoolean","SPLIT",EDGE,{"disambiguationData":[TD([subQ5])],"derivedFrom":makeQuery(id+"FyYUAefgu6xEfva_4.37.F14.boolean.opBoolean","SPLIT",EDGE,{"disambiguationData":[TD([subQ6])],"derivedFrom":makeQuery(id+"FyYUAefgu6xEfva_4.36.F14.boolean.opBoolean","SPLIT",EDGE,{"disambiguationData":[TD([subQ6])],"derivedFrom":makeQuery(id+"FyYUAefgu6xEfva_4.35.F14.boolean.opBoolean","SPLIT",EDGE,{"disambiguationData":[TD([subQ6])],"derivedFrom":makeQuery(id+"FyYUAefgu6xEfva_4.34.F14.boolean.opBoolean","SPLIT",EDGE,{"disambiguationData":[TD([subQ6])],"derivedFrom":makeQuery(id+"FyYUAefgu6xEfva_4.33.F14.boolean.opBoolean","SPLIT",EDGE,{"disambiguationData":[TD([subQ6])],"derivedFrom":makeQuery(id+"FyYUAefgu6xEfva_4.32.F14.boolean.opBoolean","SPLIT",EDGE,{"disambiguationData":[TD([subQ6])],"derivedFrom":makeQuery(id+"FyYUAefgu6xEfva_4.31.F14.boolean.opBoolean","SPLIT",EDGE,{"disambiguationData":[TD([subQ6])],"derivedFrom":makeQuery(id+"FyYUAefgu6xEfva_4.30.F14.boolean.opBoolean","SPLIT",EDGE,{"disambiguationData":[TD([subQ6])],"derivedFrom":makeQuery(id+"FyYUAefgu6xEfva_4.29.F14.boolean.opBoolean","SPLIT",EDGE,{"disambiguationData":[TD([subQ6])],"derivedFrom":makeQuery(id+"FyYUAefgu6xEfva_4.28.F14.boolean.opBoolean","SPLIT",EDGE,{"disambiguationData":[TD([subQ6])],"derivedFrom":makeQuery(id+"FyYUAefgu6xEfva_4.27.F14.boolean.opBoolean","SPLIT",EDGE,{"disambiguationData":[TD([subQ6])],"derivedFrom":makeQuery(id+"FyYUAefgu6xEfva_4.26.F14.boolean.opBoolean","SPLIT",EDGE,{"disambiguationData":[TD([subQ6])],"derivedFrom":makeQuery(id+"FyYUAefgu6xEfva_4.25.F14.boolean.opBoolean","SPLIT",EDGE,{"disambiguationData":[TD([subQ6])],"derivedFrom":makeQuery(id+"FyYUAefgu6xEfva_4.24.F14.boolean.opBoolean","SPLIT",EDGE,{"disambiguationData":[TD([subQ6])],"derivedFrom":makeQuery(id+"FyYUAefgu6xEfva_4.23.F14.boolean.opBoolean","SPLIT",EDGE,{"disambiguationData":[TD([subQ6])],"derivedFrom":makeQuery(id+"FyYUAefgu6xEfva_4.22.F14.boolean.opBoolean","SPLIT",EDGE,{"disambiguationData":[TD([subQ6])],"derivedFrom":makeQuery(id+"FyYUAefgu6xEfva_4.21.F14.boolean.opBoolean","SPLIT",EDGE,{"disambiguationData":[TD([subQ6])],"derivedFrom":makeQuery(id+"FyYUAefgu6xEfva_4.20.F14.boolean.opBoolean","SPLIT",EDGE,{"disambiguationData":[TD([subQ6])],"derivedFrom":makeQuery(id+"FyYUAefgu6xEfva_4.19.F14.boolean.opBoolean","SPLIT",EDGE,{"disambiguationData":[TD([subQ6])],"derivedFrom":makeQuery(id+"FyYUAefgu6xEfva_4.18.F14.boolean.opBoolean","SPLIT",EDGE,{"disambiguationData":[TD([subQ6])],"derivedFrom":makeQuery(id+"FyYUAefgu6xEfva_4.17.F14.boolean.opBoolean","SPLIT",EDGE,{"disambiguationData":[TD([subQ6])],"derivedFrom":makeQuery(id+"FyYUAefgu6xEfva_4.16.F14.boolean.opBoolean","SPLIT",EDGE,{"disambiguationData":[TD([subQ6])],"derivedFrom":makeQuery(id+"FyYUAefgu6xEfva_4.15.F14.boolean.opBoolean","SPLIT",EDGE,{"disambiguationData":[TD([subQ6])],"derivedFrom":makeQuery(id+"FyYUAefgu6xEfva_4.14.F14.boolean.opBoolean","SPLIT",EDGE,{"disambiguationData":[TD([subQ6])],"derivedFrom":makeQuery(id+"FyYUAefgu6xEfva_4.13.F14.boolean.opBoolean","SPLIT",EDGE,{"disambiguationData":[TD([subQ6])],"derivedFrom":makeQuery(id+"FyYUAefgu6xEfva_4.12.F14.boolean.opBoolean","SPLIT",EDGE,{"disambiguationData":[TD([subQ6])],"derivedFrom":makeQuery(id+"FyYUAefgu6xEfva_4.11.F14.boolean.opBoolean","SPLIT",EDGE,{"disambiguationData":[TD([subQ6])],"derivedFrom":makeQuery(id+"FyYUAefgu6xEfva_4.10.F14.boolean.opBoolean","SPLIT",EDGE,{"disambiguationData":[TD([subQ6])],"derivedFrom":makeQuery(id+"FyYUAefgu6xEfva_4.9.F14.boolean.opBoolean","SPLIT",EDGE,{"disambiguationData":[TD([subQ6])],"derivedFrom":makeQuery(id+"FyYUAefgu6xEfva_4.8.F14.boolean.opBoolean","SPLIT",EDGE,{"disambiguationData":[TD([subQ6])],"derivedFrom":makeQuery(id+"FyYUAefgu6xEfva_4.7.F14.boolean.opBoolean","SPLIT",EDGE,{"disambiguationData":[TD([subQ6])],"derivedFrom":makeQuery(id+"FyYUAefgu6xEfva_4.6.F14.boolean.opBoolean","SPLIT",EDGE,{"disambiguationData":[TD([subQ6])],"derivedFrom":makeQuery(id+"FyYUAefgu6xEfva_4.5.F14.boolean.opBoolean","SPLIT",EDGE,{"disambiguationData":[TD([subQ6])],"derivedFrom":makeQuery(id+"FyYUAefgu6xEfva_4.4.F14.boolean.opBoolean","SPLIT",EDGE,{"disambiguationData":[TD([subQ6])],"derivedFrom":makeQuery(id+"FyYUAefgu6xEfva_4.3.F14.boolean.opBoolean","SPLIT",EDGE,{"disambiguationData":[TD([subQ6])],"derivedFrom":makeQuery(id+"FyYUAefgu6xEfva_4.2.F14.boolean.opBoolean","SPLIT",EDGE,{"disambiguationData":[TD([subQ6])],"derivedFrom":makeQuery(id+"FyYUAefgu6xEfva_4.1.F14.boolean.opBoolean","SPLIT",EDGE,{"disambiguationData":[TD([subQ6])],"derivedFrom":makeQuery(id+"F12.opExtrude","CAP_EDGE",EDGE,{"disambiguationData":[OSD([subQ1])],"isStart":true})})})})})})})})})})})})})})})})})})})})})})})})})})})})})})})})})})})})})})});}
            var Q470;
            Q470=makeQuery(id+"FyYUAefgu6xEfva_4.38.F14.opExtrude","CAP_EDGE",EDGE,{"disambiguationData":[OSD([sQuery(id+"F13.wireOp",EDGE,"E148.MirrorCS")])],"isStart":true});
            var Q471;
            Q471=makeQuery(id+"FyYUAefgu6xEfva_4.38.F14.opExtrude","CAP_EDGE",EDGE,{"disambiguationData":[OSD([sQuery(id+"F13.wireOp",EDGE,"E147")])],"isStart":true});
            var Q472;
            Q472=makeQuery(id+"FyYUAefgu6xEfva_4.38.F14.opExtrude","SWEPT_EDGE",EDGE,{"disambiguationData":[OSD([sQuery(id+"F11.wireOp",EDGE,"E143"),sQuery(id+"F13.wireOp",EDGE,"E147")])]});
            var Q473;
            Q473=makeQuery(id+"FyYUAefgu6xEfva_4.37.F14.opExtrude","CAP_EDGE",EDGE,{"disambiguationData":[OSD([sQuery(id+"F13.wireOp",EDGE,"E148.MirrorCS")])],"isStart":true});
            var Q474;
            Q474=makeQuery(id+"FyYUAefgu6xEfva_4.37.F14.opExtrude","CAP_EDGE",EDGE,{"disambiguationData":[OSD([sQuery(id+"F13.wireOp",EDGE,"E147")])],"isStart":true});
            var Q475;
            Q475=makeQuery(id+"FyYUAefgu6xEfva_4.37.F14.opExtrude","SWEPT_EDGE",EDGE,{"disambiguationData":[OSD([sQuery(id+"F11.wireOp",EDGE,"E143"),sQuery(id+"F13.wireOp",EDGE,"E147")])]});
            var Q476;
            {var subQ0=sQuery(id+"F9.wireOp",EDGE,"E142");var subQ2=sQuery(id+"F13.wireOp",EDGE,"E148.MirrorCS");var subQ3=makeQuery(id+"FyYUAefgu6xEfva_4.35.F14.opExtrude","SWEPT_FACE",FACE,{"disambiguationData":[OSD([subQ2])]});var subQ5=sQuery(id+"F13.wireOp",EDGE,"E147");var subQ6=makeQuery(id+"F14.opExtrude","SWEPT_FACE",FACE,{"disambiguationData":[OSD([subQ5])]});Q476=makeQuery(id+"FyYUAefgu6xEfva_4.36.F14.boolean.opBoolean","SPLIT",EDGE,{"disambiguationData":[TD([subQ3])],"derivedFrom":makeQuery(id+"FyYUAefgu6xEfva_4.35.F14.boolean.opBoolean","SPLIT",EDGE,{"disambiguationData":[TD([subQ6])],"derivedFrom":makeQuery(id+"FyYUAefgu6xEfva_4.34.F14.boolean.opBoolean","SPLIT",EDGE,{"disambiguationData":[TD([subQ6])],"derivedFrom":makeQuery(id+"FyYUAefgu6xEfva_4.33.F14.boolean.opBoolean","SPLIT",EDGE,{"disambiguationData":[TD([subQ6])],"derivedFrom":makeQuery(id+"FyYUAefgu6xEfva_4.32.F14.boolean.opBoolean","SPLIT",EDGE,{"disambiguationData":[TD([subQ6])],"derivedFrom":makeQuery(id+"FyYUAefgu6xEfva_4.31.F14.boolean.opBoolean","SPLIT",EDGE,{"disambiguationData":[TD([subQ6])],"derivedFrom":makeQuery(id+"FyYUAefgu6xEfva_4.30.F14.boolean.opBoolean","SPLIT",EDGE,{"disambiguationData":[TD([subQ6])],"derivedFrom":makeQuery(id+"FyYUAefgu6xEfva_4.29.F14.boolean.opBoolean","SPLIT",EDGE,{"disambiguationData":[TD([subQ6])],"derivedFrom":makeQuery(id+"FyYUAefgu6xEfva_4.28.F14.boolean.opBoolean","SPLIT",EDGE,{"disambiguationData":[TD([subQ6])],"derivedFrom":makeQuery(id+"FyYUAefgu6xEfva_4.27.F14.boolean.opBoolean","SPLIT",EDGE,{"disambiguationData":[TD([subQ6])],"derivedFrom":makeQuery(id+"FyYUAefgu6xEfva_4.26.F14.boolean.opBoolean","SPLIT",EDGE,{"disambiguationData":[TD([subQ6])],"derivedFrom":makeQuery(id+"FyYUAefgu6xEfva_4.25.F14.boolean.opBoolean","SPLIT",EDGE,{"disambiguationData":[TD([subQ6])],"derivedFrom":makeQuery(id+"FyYUAefgu6xEfva_4.24.F14.boolean.opBoolean","SPLIT",EDGE,{"disambiguationData":[TD([subQ6])],"derivedFrom":makeQuery(id+"FyYUAefgu6xEfva_4.23.F14.boolean.opBoolean","SPLIT",EDGE,{"disambiguationData":[TD([subQ6])],"derivedFrom":makeQuery(id+"FyYUAefgu6xEfva_4.22.F14.boolean.opBoolean","SPLIT",EDGE,{"disambiguationData":[TD([subQ6])],"derivedFrom":makeQuery(id+"FyYUAefgu6xEfva_4.21.F14.boolean.opBoolean","SPLIT",EDGE,{"disambiguationData":[TD([subQ6])],"derivedFrom":makeQuery(id+"FyYUAefgu6xEfva_4.20.F14.boolean.opBoolean","SPLIT",EDGE,{"disambiguationData":[TD([subQ6])],"derivedFrom":makeQuery(id+"FyYUAefgu6xEfva_4.19.F14.boolean.opBoolean","SPLIT",EDGE,{"disambiguationData":[TD([subQ6])],"derivedFrom":makeQuery(id+"FyYUAefgu6xEfva_4.18.F14.boolean.opBoolean","SPLIT",EDGE,{"disambiguationData":[TD([subQ6])],"derivedFrom":makeQuery(id+"FyYUAefgu6xEfva_4.17.F14.boolean.opBoolean","SPLIT",EDGE,{"disambiguationData":[TD([subQ6])],"derivedFrom":makeQuery(id+"FyYUAefgu6xEfva_4.16.F14.boolean.opBoolean","SPLIT",EDGE,{"disambiguationData":[TD([subQ6])],"derivedFrom":makeQuery(id+"FyYUAefgu6xEfva_4.15.F14.boolean.opBoolean","SPLIT",EDGE,{"disambiguationData":[TD([subQ6])],"derivedFrom":makeQuery(id+"FyYUAefgu6xEfva_4.14.F14.boolean.opBoolean","SPLIT",EDGE,{"disambiguationData":[TD([subQ6])],"derivedFrom":makeQuery(id+"FyYUAefgu6xEfva_4.13.F14.boolean.opBoolean","SPLIT",EDGE,{"disambiguationData":[TD([subQ6])],"derivedFrom":makeQuery(id+"FyYUAefgu6xEfva_4.12.F14.boolean.opBoolean","SPLIT",EDGE,{"disambiguationData":[TD([subQ6])],"derivedFrom":makeQuery(id+"FyYUAefgu6xEfva_4.11.F14.boolean.opBoolean","SPLIT",EDGE,{"disambiguationData":[TD([subQ6])],"derivedFrom":makeQuery(id+"FyYUAefgu6xEfva_4.10.F14.boolean.opBoolean","SPLIT",EDGE,{"disambiguationData":[TD([subQ6])],"derivedFrom":makeQuery(id+"FyYUAefgu6xEfva_4.9.F14.boolean.opBoolean","SPLIT",EDGE,{"disambiguationData":[TD([subQ6])],"derivedFrom":makeQuery(id+"FyYUAefgu6xEfva_4.8.F14.boolean.opBoolean","SPLIT",EDGE,{"disambiguationData":[TD([subQ6])],"derivedFrom":makeQuery(id+"FyYUAefgu6xEfva_4.7.F14.boolean.opBoolean","SPLIT",EDGE,{"disambiguationData":[TD([subQ6])],"derivedFrom":makeQuery(id+"FyYUAefgu6xEfva_4.6.F14.boolean.opBoolean","SPLIT",EDGE,{"disambiguationData":[TD([subQ6])],"derivedFrom":makeQuery(id+"FyYUAefgu6xEfva_4.5.F14.boolean.opBoolean","SPLIT",EDGE,{"disambiguationData":[TD([subQ6])],"derivedFrom":makeQuery(id+"FyYUAefgu6xEfva_4.4.F14.boolean.opBoolean","SPLIT",EDGE,{"disambiguationData":[TD([subQ6])],"derivedFrom":makeQuery(id+"FyYUAefgu6xEfva_4.3.F14.boolean.opBoolean","SPLIT",EDGE,{"disambiguationData":[TD([subQ6])],"derivedFrom":makeQuery(id+"FyYUAefgu6xEfva_4.2.F14.boolean.opBoolean","SPLIT",EDGE,{"disambiguationData":[TD([subQ6])],"derivedFrom":makeQuery(id+"FyYUAefgu6xEfva_4.1.F14.boolean.opBoolean","SPLIT",EDGE,{"disambiguationData":[TD([subQ6])],"derivedFrom":makeQuery(id+"F10.boolean.opBoolean","COPY",EDGE,{"derivedFrom":makeQuery(id+"F10.opExtrude","CAP_EDGE",EDGE,{"disambiguationData":[OSD([subQ0])],"isStart":false})})})})})})})})})})})})})})})})})})})})})})})})})})})})})})})})})})})})})});}
            var Q477;
            Q477=makeQuery(id+"FyYUAefgu6xEfva_4.36.F14.opExtrude","CAP_EDGE",EDGE,{"disambiguationData":[OSD([sQuery(id+"F13.wireOp",EDGE,"E148.MirrorCS")])],"isStart":true});
            var Q478;
            Q478=makeQuery(id+"FyYUAefgu6xEfva_4.36.F14.opExtrude","CAP_EDGE",EDGE,{"disambiguationData":[OSD([sQuery(id+"F13.wireOp",EDGE,"E147")])],"isStart":true});
            var Q479;
            Q479=makeQuery(id+"FyYUAefgu6xEfva_4.36.F14.opExtrude","SWEPT_EDGE",EDGE,{"disambiguationData":[OSD([sQuery(id+"F11.wireOp",EDGE,"E143"),sQuery(id+"F13.wireOp",EDGE,"E148.MirrorCS")])]});
            var Q480;
            Q480=makeQuery(id+"FyYUAefgu6xEfva_4.36.F14.opExtrude","SWEPT_EDGE",EDGE,{"disambiguationData":[OSD([sQuery(id+"F11.wireOp",EDGE,"E143"),sQuery(id+"F13.wireOp",EDGE,"E147")])]});
            var Q481;
            {var subQ1=sQuery(id+"F11.wireOp",EDGE,"E143");var subQ3=sQuery(id+"F13.wireOp",EDGE,"E148.MirrorCS");var subQ4=makeQuery(id+"FyYUAefgu6xEfva_4.40.F14.opExtrude","SWEPT_FACE",FACE,{"disambiguationData":[OSD([subQ3])]});var subQ5=sQuery(id+"F13.wireOp",EDGE,"E147");var subQ6=makeQuery(id+"F14.opExtrude","SWEPT_FACE",FACE,{"disambiguationData":[OSD([subQ5])]});Q481=makeQuery(id+"FyYUAefgu6xEfva_4.41.F14.boolean.opBoolean","SPLIT",EDGE,{"disambiguationData":[TD([subQ4])],"derivedFrom":makeQuery(id+"FyYUAefgu6xEfva_4.40.F14.boolean.opBoolean","SPLIT",EDGE,{"disambiguationData":[TD([subQ6])],"derivedFrom":makeQuery(id+"FyYUAefgu6xEfva_4.39.F14.boolean.opBoolean","SPLIT",EDGE,{"disambiguationData":[TD([subQ6])],"derivedFrom":makeQuery(id+"FyYUAefgu6xEfva_4.38.F14.boolean.opBoolean","SPLIT",EDGE,{"disambiguationData":[TD([subQ6])],"derivedFrom":makeQuery(id+"FyYUAefgu6xEfva_4.37.F14.boolean.opBoolean","SPLIT",EDGE,{"disambiguationData":[TD([subQ6])],"derivedFrom":makeQuery(id+"FyYUAefgu6xEfva_4.36.F14.boolean.opBoolean","SPLIT",EDGE,{"disambiguationData":[TD([subQ6])],"derivedFrom":makeQuery(id+"FyYUAefgu6xEfva_4.35.F14.boolean.opBoolean","SPLIT",EDGE,{"disambiguationData":[TD([subQ6])],"derivedFrom":makeQuery(id+"FyYUAefgu6xEfva_4.34.F14.boolean.opBoolean","SPLIT",EDGE,{"disambiguationData":[TD([subQ6])],"derivedFrom":makeQuery(id+"FyYUAefgu6xEfva_4.33.F14.boolean.opBoolean","SPLIT",EDGE,{"disambiguationData":[TD([subQ6])],"derivedFrom":makeQuery(id+"FyYUAefgu6xEfva_4.32.F14.boolean.opBoolean","SPLIT",EDGE,{"disambiguationData":[TD([subQ6])],"derivedFrom":makeQuery(id+"FyYUAefgu6xEfva_4.31.F14.boolean.opBoolean","SPLIT",EDGE,{"disambiguationData":[TD([subQ6])],"derivedFrom":makeQuery(id+"FyYUAefgu6xEfva_4.30.F14.boolean.opBoolean","SPLIT",EDGE,{"disambiguationData":[TD([subQ6])],"derivedFrom":makeQuery(id+"FyYUAefgu6xEfva_4.29.F14.boolean.opBoolean","SPLIT",EDGE,{"disambiguationData":[TD([subQ6])],"derivedFrom":makeQuery(id+"FyYUAefgu6xEfva_4.28.F14.boolean.opBoolean","SPLIT",EDGE,{"disambiguationData":[TD([subQ6])],"derivedFrom":makeQuery(id+"FyYUAefgu6xEfva_4.27.F14.boolean.opBoolean","SPLIT",EDGE,{"disambiguationData":[TD([subQ6])],"derivedFrom":makeQuery(id+"FyYUAefgu6xEfva_4.26.F14.boolean.opBoolean","SPLIT",EDGE,{"disambiguationData":[TD([subQ6])],"derivedFrom":makeQuery(id+"FyYUAefgu6xEfva_4.25.F14.boolean.opBoolean","SPLIT",EDGE,{"disambiguationData":[TD([subQ6])],"derivedFrom":makeQuery(id+"FyYUAefgu6xEfva_4.24.F14.boolean.opBoolean","SPLIT",EDGE,{"disambiguationData":[TD([subQ6])],"derivedFrom":makeQuery(id+"FyYUAefgu6xEfva_4.23.F14.boolean.opBoolean","SPLIT",EDGE,{"disambiguationData":[TD([subQ6])],"derivedFrom":makeQuery(id+"FyYUAefgu6xEfva_4.22.F14.boolean.opBoolean","SPLIT",EDGE,{"disambiguationData":[TD([subQ6])],"derivedFrom":makeQuery(id+"FyYUAefgu6xEfva_4.21.F14.boolean.opBoolean","SPLIT",EDGE,{"disambiguationData":[TD([subQ6])],"derivedFrom":makeQuery(id+"FyYUAefgu6xEfva_4.20.F14.boolean.opBoolean","SPLIT",EDGE,{"disambiguationData":[TD([subQ6])],"derivedFrom":makeQuery(id+"FyYUAefgu6xEfva_4.19.F14.boolean.opBoolean","SPLIT",EDGE,{"disambiguationData":[TD([subQ6])],"derivedFrom":makeQuery(id+"FyYUAefgu6xEfva_4.18.F14.boolean.opBoolean","SPLIT",EDGE,{"disambiguationData":[TD([subQ6])],"derivedFrom":makeQuery(id+"FyYUAefgu6xEfva_4.17.F14.boolean.opBoolean","SPLIT",EDGE,{"disambiguationData":[TD([subQ6])],"derivedFrom":makeQuery(id+"FyYUAefgu6xEfva_4.16.F14.boolean.opBoolean","SPLIT",EDGE,{"disambiguationData":[TD([subQ6])],"derivedFrom":makeQuery(id+"FyYUAefgu6xEfva_4.15.F14.boolean.opBoolean","SPLIT",EDGE,{"disambiguationData":[TD([subQ6])],"derivedFrom":makeQuery(id+"FyYUAefgu6xEfva_4.14.F14.boolean.opBoolean","SPLIT",EDGE,{"disambiguationData":[TD([subQ6])],"derivedFrom":makeQuery(id+"FyYUAefgu6xEfva_4.13.F14.boolean.opBoolean","SPLIT",EDGE,{"disambiguationData":[TD([subQ6])],"derivedFrom":makeQuery(id+"FyYUAefgu6xEfva_4.12.F14.boolean.opBoolean","SPLIT",EDGE,{"disambiguationData":[TD([subQ6])],"derivedFrom":makeQuery(id+"FyYUAefgu6xEfva_4.11.F14.boolean.opBoolean","SPLIT",EDGE,{"disambiguationData":[TD([subQ6])],"derivedFrom":makeQuery(id+"FyYUAefgu6xEfva_4.10.F14.boolean.opBoolean","SPLIT",EDGE,{"disambiguationData":[TD([subQ6])],"derivedFrom":makeQuery(id+"FyYUAefgu6xEfva_4.9.F14.boolean.opBoolean","SPLIT",EDGE,{"disambiguationData":[TD([subQ6])],"derivedFrom":makeQuery(id+"FyYUAefgu6xEfva_4.8.F14.boolean.opBoolean","SPLIT",EDGE,{"disambiguationData":[TD([subQ6])],"derivedFrom":makeQuery(id+"FyYUAefgu6xEfva_4.7.F14.boolean.opBoolean","SPLIT",EDGE,{"disambiguationData":[TD([subQ6])],"derivedFrom":makeQuery(id+"FyYUAefgu6xEfva_4.6.F14.boolean.opBoolean","SPLIT",EDGE,{"disambiguationData":[TD([subQ6])],"derivedFrom":makeQuery(id+"FyYUAefgu6xEfva_4.5.F14.boolean.opBoolean","SPLIT",EDGE,{"disambiguationData":[TD([subQ6])],"derivedFrom":makeQuery(id+"FyYUAefgu6xEfva_4.4.F14.boolean.opBoolean","SPLIT",EDGE,{"disambiguationData":[TD([subQ6])],"derivedFrom":makeQuery(id+"FyYUAefgu6xEfva_4.3.F14.boolean.opBoolean","SPLIT",EDGE,{"disambiguationData":[TD([subQ6])],"derivedFrom":makeQuery(id+"FyYUAefgu6xEfva_4.2.F14.boolean.opBoolean","SPLIT",EDGE,{"disambiguationData":[TD([subQ6])],"derivedFrom":makeQuery(id+"FyYUAefgu6xEfva_4.1.F14.boolean.opBoolean","SPLIT",EDGE,{"disambiguationData":[TD([subQ6])],"derivedFrom":makeQuery(id+"F12.opExtrude","CAP_EDGE",EDGE,{"disambiguationData":[OSD([subQ1])],"isStart":true})})})})})})})})})})})})})})})})})})})})})})})})})})})})})})})})})})})})})})})})})});}
            var Q482;
            Q482=makeQuery(id+"FyYUAefgu6xEfva_4.3.F14.opExtrude","CAP_EDGE",EDGE,{"disambiguationData":[OSD([sQuery(id+"F9.wireOp",EDGE,"E142")])],"isStart":false});
            var Q483;
            {var subQ1=sQuery(id+"F13.wireOp",EDGE,"E147");var subQ2=sQuery(id+"F11.wireOp",EDGE,"E143");var subQ4=makeQuery(id+"FyYUAefgu6xEfva_4.1.F14.opExtrude","SWEPT_FACE",FACE,{"disambiguationData":[OSD([sQuery(id+"F13.wireOp",EDGE,"E148.MirrorCS")])]});Q483=makeQuery(id+"FyYUAefgu6xEfva_4.2.F14.boolean.opBoolean","SPLIT",EDGE,{"disambiguationData":[TD([subQ4])],"derivedFrom":makeQuery(id+"FyYUAefgu6xEfva_4.1.F14.boolean.opBoolean","SPLIT",EDGE,{"disambiguationData":[TD([makeQuery(id+"F14.opExtrude","SWEPT_FACE",FACE,{"disambiguationData":[OSD([subQ1])]})])],"derivedFrom":makeQuery(id+"F12.opExtrude","CAP_EDGE",EDGE,{"disambiguationData":[OSD([subQ2])],"isStart":true})})});}
            var Q484;
            Q484=makeQuery(id+"FyYUAefgu6xEfva_4.2.F14.opExtrude","CAP_EDGE",EDGE,{"disambiguationData":[OSD([sQuery(id+"F13.wireOp",EDGE,"E147")])],"isStart":true});
            var Q485;
            Q485=makeQuery(id+"FyYUAefgu6xEfva_4.40.F14.opExtrude","SWEPT_EDGE",EDGE,{"disambiguationData":[OSD([sQuery(id+"F11.wireOp",EDGE,"E143"),sQuery(id+"F13.wireOp",EDGE,"E147")])]});
            var Q486;
            {var subQ0=sQuery(id+"F11.wireOp",EDGE,"E143");Q486=makeQuery(id+"FyYUAefgu6xEfva_4.1.F14.boolean.opBoolean","SPLIT",EDGE,{"disambiguationData":[TD([makeQuery(id+"F14.opExtrude","SWEPT_FACE",FACE,{"disambiguationData":[OSD([sQuery(id+"F13.wireOp",EDGE,"E148.MirrorCS")])]})])],"derivedFrom":makeQuery(id+"F12.opExtrude","CAP_EDGE",EDGE,{"disambiguationData":[OSD([subQ0])],"isStart":true})});}
            var Q487;
            {var subQ1=sQuery(id+"F13.wireOp",EDGE,"E148.MirrorCS");var subQ2=makeQuery(id+"FyYUAefgu6xEfva_4.38.F14.opExtrude","SWEPT_FACE",FACE,{"disambiguationData":[OSD([subQ1])]});var subQ3=sQuery(id+"F11.wireOp",EDGE,"E143");var subQ5=sQuery(id+"F13.wireOp",EDGE,"E147");var subQ6=makeQuery(id+"F14.opExtrude","SWEPT_FACE",FACE,{"disambiguationData":[OSD([subQ5])]});Q487=makeQuery(id+"FyYUAefgu6xEfva_4.39.F14.boolean.opBoolean","SPLIT",EDGE,{"disambiguationData":[TD([subQ2])],"derivedFrom":makeQuery(id+"FyYUAefgu6xEfva_4.38.F14.boolean.opBoolean","SPLIT",EDGE,{"disambiguationData":[TD([subQ6])],"derivedFrom":makeQuery(id+"FyYUAefgu6xEfva_4.37.F14.boolean.opBoolean","SPLIT",EDGE,{"disambiguationData":[TD([subQ6])],"derivedFrom":makeQuery(id+"FyYUAefgu6xEfva_4.36.F14.boolean.opBoolean","SPLIT",EDGE,{"disambiguationData":[TD([subQ6])],"derivedFrom":makeQuery(id+"FyYUAefgu6xEfva_4.35.F14.boolean.opBoolean","SPLIT",EDGE,{"disambiguationData":[TD([subQ6])],"derivedFrom":makeQuery(id+"FyYUAefgu6xEfva_4.34.F14.boolean.opBoolean","SPLIT",EDGE,{"disambiguationData":[TD([subQ6])],"derivedFrom":makeQuery(id+"FyYUAefgu6xEfva_4.33.F14.boolean.opBoolean","SPLIT",EDGE,{"disambiguationData":[TD([subQ6])],"derivedFrom":makeQuery(id+"FyYUAefgu6xEfva_4.32.F14.boolean.opBoolean","SPLIT",EDGE,{"disambiguationData":[TD([subQ6])],"derivedFrom":makeQuery(id+"FyYUAefgu6xEfva_4.31.F14.boolean.opBoolean","SPLIT",EDGE,{"disambiguationData":[TD([subQ6])],"derivedFrom":makeQuery(id+"FyYUAefgu6xEfva_4.30.F14.boolean.opBoolean","SPLIT",EDGE,{"disambiguationData":[TD([subQ6])],"derivedFrom":makeQuery(id+"FyYUAefgu6xEfva_4.29.F14.boolean.opBoolean","SPLIT",EDGE,{"disambiguationData":[TD([subQ6])],"derivedFrom":makeQuery(id+"FyYUAefgu6xEfva_4.28.F14.boolean.opBoolean","SPLIT",EDGE,{"disambiguationData":[TD([subQ6])],"derivedFrom":makeQuery(id+"FyYUAefgu6xEfva_4.27.F14.boolean.opBoolean","SPLIT",EDGE,{"disambiguationData":[TD([subQ6])],"derivedFrom":makeQuery(id+"FyYUAefgu6xEfva_4.26.F14.boolean.opBoolean","SPLIT",EDGE,{"disambiguationData":[TD([subQ6])],"derivedFrom":makeQuery(id+"FyYUAefgu6xEfva_4.25.F14.boolean.opBoolean","SPLIT",EDGE,{"disambiguationData":[TD([subQ6])],"derivedFrom":makeQuery(id+"FyYUAefgu6xEfva_4.24.F14.boolean.opBoolean","SPLIT",EDGE,{"disambiguationData":[TD([subQ6])],"derivedFrom":makeQuery(id+"FyYUAefgu6xEfva_4.23.F14.boolean.opBoolean","SPLIT",EDGE,{"disambiguationData":[TD([subQ6])],"derivedFrom":makeQuery(id+"FyYUAefgu6xEfva_4.22.F14.boolean.opBoolean","SPLIT",EDGE,{"disambiguationData":[TD([subQ6])],"derivedFrom":makeQuery(id+"FyYUAefgu6xEfva_4.21.F14.boolean.opBoolean","SPLIT",EDGE,{"disambiguationData":[TD([subQ6])],"derivedFrom":makeQuery(id+"FyYUAefgu6xEfva_4.20.F14.boolean.opBoolean","SPLIT",EDGE,{"disambiguationData":[TD([subQ6])],"derivedFrom":makeQuery(id+"FyYUAefgu6xEfva_4.19.F14.boolean.opBoolean","SPLIT",EDGE,{"disambiguationData":[TD([subQ6])],"derivedFrom":makeQuery(id+"FyYUAefgu6xEfva_4.18.F14.boolean.opBoolean","SPLIT",EDGE,{"disambiguationData":[TD([subQ6])],"derivedFrom":makeQuery(id+"FyYUAefgu6xEfva_4.17.F14.boolean.opBoolean","SPLIT",EDGE,{"disambiguationData":[TD([subQ6])],"derivedFrom":makeQuery(id+"FyYUAefgu6xEfva_4.16.F14.boolean.opBoolean","SPLIT",EDGE,{"disambiguationData":[TD([subQ6])],"derivedFrom":makeQuery(id+"FyYUAefgu6xEfva_4.15.F14.boolean.opBoolean","SPLIT",EDGE,{"disambiguationData":[TD([subQ6])],"derivedFrom":makeQuery(id+"FyYUAefgu6xEfva_4.14.F14.boolean.opBoolean","SPLIT",EDGE,{"disambiguationData":[TD([subQ6])],"derivedFrom":makeQuery(id+"FyYUAefgu6xEfva_4.13.F14.boolean.opBoolean","SPLIT",EDGE,{"disambiguationData":[TD([subQ6])],"derivedFrom":makeQuery(id+"FyYUAefgu6xEfva_4.12.F14.boolean.opBoolean","SPLIT",EDGE,{"disambiguationData":[TD([subQ6])],"derivedFrom":makeQuery(id+"FyYUAefgu6xEfva_4.11.F14.boolean.opBoolean","SPLIT",EDGE,{"disambiguationData":[TD([subQ6])],"derivedFrom":makeQuery(id+"FyYUAefgu6xEfva_4.10.F14.boolean.opBoolean","SPLIT",EDGE,{"disambiguationData":[TD([subQ6])],"derivedFrom":makeQuery(id+"FyYUAefgu6xEfva_4.9.F14.boolean.opBoolean","SPLIT",EDGE,{"disambiguationData":[TD([subQ6])],"derivedFrom":makeQuery(id+"FyYUAefgu6xEfva_4.8.F14.boolean.opBoolean","SPLIT",EDGE,{"disambiguationData":[TD([subQ6])],"derivedFrom":makeQuery(id+"FyYUAefgu6xEfva_4.7.F14.boolean.opBoolean","SPLIT",EDGE,{"disambiguationData":[TD([subQ6])],"derivedFrom":makeQuery(id+"FyYUAefgu6xEfva_4.6.F14.boolean.opBoolean","SPLIT",EDGE,{"disambiguationData":[TD([subQ6])],"derivedFrom":makeQuery(id+"FyYUAefgu6xEfva_4.5.F14.boolean.opBoolean","SPLIT",EDGE,{"disambiguationData":[TD([subQ6])],"derivedFrom":makeQuery(id+"FyYUAefgu6xEfva_4.4.F14.boolean.opBoolean","SPLIT",EDGE,{"disambiguationData":[TD([subQ6])],"derivedFrom":makeQuery(id+"FyYUAefgu6xEfva_4.3.F14.boolean.opBoolean","SPLIT",EDGE,{"disambiguationData":[TD([subQ6])],"derivedFrom":makeQuery(id+"FyYUAefgu6xEfva_4.2.F14.boolean.opBoolean","SPLIT",EDGE,{"disambiguationData":[TD([subQ6])],"derivedFrom":makeQuery(id+"FyYUAefgu6xEfva_4.1.F14.boolean.opBoolean","SPLIT",EDGE,{"disambiguationData":[TD([subQ6])],"derivedFrom":makeQuery(id+"F12.opExtrude","CAP_EDGE",EDGE,{"disambiguationData":[OSD([subQ3])],"isStart":true})})})})})})})})})})})})})})})})})})})})})})})})})})})})})})})})})})})})})})})});}
            var Q488;
            Q488=makeQuery(id+"FyYUAefgu6xEfva_4.8.F14.opExtrude","CAP_EDGE",EDGE,{"disambiguationData":[OSD([sQuery(id+"F13.wireOp",EDGE,"E148.MirrorCS")])],"isStart":true});
            var Q489;
            Q489=makeQuery(id+"FyYUAefgu6xEfva_4.8.F14.opExtrude","CAP_EDGE",EDGE,{"disambiguationData":[OSD([sQuery(id+"F13.wireOp",EDGE,"E147")])],"isStart":true});
            var Q490;
            Q490=makeQuery(id+"FyYUAefgu6xEfva_4.8.F14.opExtrude","SWEPT_EDGE",EDGE,{"disambiguationData":[OSD([sQuery(id+"F11.wireOp",EDGE,"E143"),sQuery(id+"F13.wireOp",EDGE,"E148.MirrorCS")])]});
            var Q491;
            Q491=makeQuery(id+"FyYUAefgu6xEfva_4.8.F14.opExtrude","SWEPT_EDGE",EDGE,{"disambiguationData":[OSD([sQuery(id+"F9.wireOp",EDGE,"E142"),sQuery(id+"F13.wireOp",EDGE,"E148.MirrorCS")])]});
            var Q492;
            {var subQ1=sQuery(id+"F13.wireOp",EDGE,"E147");var subQ2=sQuery(id+"F11.wireOp",EDGE,"E143");var subQ4=sQuery(id+"F13.wireOp",EDGE,"E148.MirrorCS");var subQ5=makeQuery(id+"FyYUAefgu6xEfva_4.6.F14.opExtrude","SWEPT_FACE",FACE,{"disambiguationData":[OSD([subQ4])]});var subQ6=makeQuery(id+"F14.opExtrude","SWEPT_FACE",FACE,{"disambiguationData":[OSD([subQ1])]});Q492=makeQuery(id+"FyYUAefgu6xEfva_4.7.F14.boolean.opBoolean","SPLIT",EDGE,{"disambiguationData":[TD([subQ5])],"derivedFrom":makeQuery(id+"FyYUAefgu6xEfva_4.6.F14.boolean.opBoolean","SPLIT",EDGE,{"disambiguationData":[TD([subQ6])],"derivedFrom":makeQuery(id+"FyYUAefgu6xEfva_4.5.F14.boolean.opBoolean","SPLIT",EDGE,{"disambiguationData":[TD([subQ6])],"derivedFrom":makeQuery(id+"FyYUAefgu6xEfva_4.4.F14.boolean.opBoolean","SPLIT",EDGE,{"disambiguationData":[TD([subQ6])],"derivedFrom":makeQuery(id+"FyYUAefgu6xEfva_4.3.F14.boolean.opBoolean","SPLIT",EDGE,{"disambiguationData":[TD([subQ6])],"derivedFrom":makeQuery(id+"FyYUAefgu6xEfva_4.2.F14.boolean.opBoolean","SPLIT",EDGE,{"disambiguationData":[TD([subQ6])],"derivedFrom":makeQuery(id+"FyYUAefgu6xEfva_4.1.F14.boolean.opBoolean","SPLIT",EDGE,{"disambiguationData":[TD([subQ6])],"derivedFrom":makeQuery(id+"F12.opExtrude","CAP_EDGE",EDGE,{"disambiguationData":[OSD([subQ2])],"isStart":true})})})})})})})});}
            var Q493;
            Q493=makeQuery(id+"FyYUAefgu6xEfva_4.7.F14.opExtrude","SWEPT_EDGE",EDGE,{"disambiguationData":[OSD([sQuery(id+"F9.wireOp",EDGE,"E142"),sQuery(id+"F13.wireOp",EDGE,"E148.MirrorCS")])]});
            var Q494;
            Q494=makeQuery(id+"FyYUAefgu6xEfva_4.6.F14.opExtrude","CAP_EDGE",EDGE,{"disambiguationData":[OSD([sQuery(id+"F13.wireOp",EDGE,"E147")])],"isStart":true});
            var Q495;
            Q495=makeQuery(id+"FyYUAefgu6xEfva_4.6.F14.opExtrude","SWEPT_EDGE",EDGE,{"disambiguationData":[OSD([sQuery(id+"F11.wireOp",EDGE,"E143"),sQuery(id+"F13.wireOp",EDGE,"E147")])]});
            var Q496;
            {var subQ1=sQuery(id+"F11.wireOp",EDGE,"E143");var subQ3=sQuery(id+"F13.wireOp",EDGE,"E148.MirrorCS");var subQ4=makeQuery(id+"FyYUAefgu6xEfva_4.4.F14.opExtrude","SWEPT_FACE",FACE,{"disambiguationData":[OSD([subQ3])]});var subQ5=sQuery(id+"F13.wireOp",EDGE,"E147");var subQ6=makeQuery(id+"F14.opExtrude","SWEPT_FACE",FACE,{"disambiguationData":[OSD([subQ5])]});Q496=makeQuery(id+"FyYUAefgu6xEfva_4.5.F14.boolean.opBoolean","SPLIT",EDGE,{"disambiguationData":[TD([subQ4])],"derivedFrom":makeQuery(id+"FyYUAefgu6xEfva_4.4.F14.boolean.opBoolean","SPLIT",EDGE,{"disambiguationData":[TD([subQ6])],"derivedFrom":makeQuery(id+"FyYUAefgu6xEfva_4.3.F14.boolean.opBoolean","SPLIT",EDGE,{"disambiguationData":[TD([subQ6])],"derivedFrom":makeQuery(id+"FyYUAefgu6xEfva_4.2.F14.boolean.opBoolean","SPLIT",EDGE,{"disambiguationData":[TD([subQ6])],"derivedFrom":makeQuery(id+"FyYUAefgu6xEfva_4.1.F14.boolean.opBoolean","SPLIT",EDGE,{"disambiguationData":[TD([subQ6])],"derivedFrom":makeQuery(id+"F12.opExtrude","CAP_EDGE",EDGE,{"disambiguationData":[OSD([subQ1])],"isStart":true})})})})})});}
            var Q497;
            Q497=makeQuery(id+"FyYUAefgu6xEfva_4.5.F14.opExtrude","CAP_EDGE",EDGE,{"disambiguationData":[OSD([sQuery(id+"F9.wireOp",EDGE,"E142")])],"isStart":false});
            var Q498;
            Q498=makeQuery(id+"FyYUAefgu6xEfva_4.5.F14.opExtrude","SWEPT_EDGE",EDGE,{"disambiguationData":[OSD([sQuery(id+"F9.wireOp",EDGE,"E142"),sQuery(id+"F13.wireOp",EDGE,"E148.MirrorCS")])]});
            var Q499;
            Q499=makeQuery(id+"FyYUAefgu6xEfva_4.5.F14.opExtrude","SWEPT_EDGE",EDGE,{"disambiguationData":[OSD([sQuery(id+"F11.wireOp",EDGE,"E143"),sQuery(id+"F13.wireOp",EDGE,"E147")])]});
            var Q500;
            {var subQ1=sQuery(id+"F13.wireOp",EDGE,"E148.MirrorCS");var subQ2=makeQuery(id+"FyYUAefgu6xEfva_4.3.F14.opExtrude","SWEPT_FACE",FACE,{"disambiguationData":[OSD([subQ1])]});var subQ3=sQuery(id+"F11.wireOp",EDGE,"E143");var subQ5=sQuery(id+"F13.wireOp",EDGE,"E147");var subQ6=makeQuery(id+"F14.opExtrude","SWEPT_FACE",FACE,{"disambiguationData":[OSD([subQ5])]});Q500=makeQuery(id+"FyYUAefgu6xEfva_4.4.F14.boolean.opBoolean","SPLIT",EDGE,{"disambiguationData":[TD([subQ2])],"derivedFrom":makeQuery(id+"FyYUAefgu6xEfva_4.3.F14.boolean.opBoolean","SPLIT",EDGE,{"disambiguationData":[TD([subQ6])],"derivedFrom":makeQuery(id+"FyYUAefgu6xEfva_4.2.F14.boolean.opBoolean","SPLIT",EDGE,{"disambiguationData":[TD([subQ6])],"derivedFrom":makeQuery(id+"FyYUAefgu6xEfva_4.1.F14.boolean.opBoolean","SPLIT",EDGE,{"disambiguationData":[TD([subQ6])],"derivedFrom":makeQuery(id+"F12.opExtrude","CAP_EDGE",EDGE,{"disambiguationData":[OSD([subQ3])],"isStart":true})})})})});}
            var Q501;
            Q501=makeQuery(id+"FyYUAefgu6xEfva_4.9.F14.opExtrude","CAP_EDGE",EDGE,{"disambiguationData":[OSD([sQuery(id+"F13.wireOp",EDGE,"E148.MirrorCS")])],"isStart":true});
            var Q502;
            Q502=makeQuery(id+"FyYUAefgu6xEfva_4.9.F14.opExtrude","CAP_EDGE",EDGE,{"disambiguationData":[OSD([sQuery(id+"F13.wireOp",EDGE,"E147")])],"isStart":true});
            var Q503;
            Q503=makeQuery(id+"F14.opExtrude","SWEPT_EDGE",EDGE,{"disambiguationData":[OSD([sQuery(id+"F11.wireOp",EDGE,"E143"),sQuery(id+"F13.wireOp",EDGE,"E148.MirrorCS")])]});
            var Q504;
            Q504=makeQuery(id+"FyYUAefgu6xEfva_4.40.F14.opExtrude","CAP_EDGE",EDGE,{"disambiguationData":[OSD([sQuery(id+"F13.wireOp",EDGE,"E148.MirrorCS")])],"isStart":true});
            var Q505;
            {var subQ1=sQuery(id+"F11.wireOp",EDGE,"E143");var subQ3=sQuery(id+"F13.wireOp",EDGE,"E148.MirrorCS");var subQ4=makeQuery(id+"FyYUAefgu6xEfva_4.39.F14.opExtrude","SWEPT_FACE",FACE,{"disambiguationData":[OSD([subQ3])]});var subQ5=sQuery(id+"F13.wireOp",EDGE,"E147");var subQ6=makeQuery(id+"F14.opExtrude","SWEPT_FACE",FACE,{"disambiguationData":[OSD([subQ5])]});Q505=makeQuery(id+"FyYUAefgu6xEfva_4.40.F14.boolean.opBoolean","SPLIT",EDGE,{"disambiguationData":[TD([subQ4])],"derivedFrom":makeQuery(id+"FyYUAefgu6xEfva_4.39.F14.boolean.opBoolean","SPLIT",EDGE,{"disambiguationData":[TD([subQ6])],"derivedFrom":makeQuery(id+"FyYUAefgu6xEfva_4.38.F14.boolean.opBoolean","SPLIT",EDGE,{"disambiguationData":[TD([subQ6])],"derivedFrom":makeQuery(id+"FyYUAefgu6xEfva_4.37.F14.boolean.opBoolean","SPLIT",EDGE,{"disambiguationData":[TD([subQ6])],"derivedFrom":makeQuery(id+"FyYUAefgu6xEfva_4.36.F14.boolean.opBoolean","SPLIT",EDGE,{"disambiguationData":[TD([subQ6])],"derivedFrom":makeQuery(id+"FyYUAefgu6xEfva_4.35.F14.boolean.opBoolean","SPLIT",EDGE,{"disambiguationData":[TD([subQ6])],"derivedFrom":makeQuery(id+"FyYUAefgu6xEfva_4.34.F14.boolean.opBoolean","SPLIT",EDGE,{"disambiguationData":[TD([subQ6])],"derivedFrom":makeQuery(id+"FyYUAefgu6xEfva_4.33.F14.boolean.opBoolean","SPLIT",EDGE,{"disambiguationData":[TD([subQ6])],"derivedFrom":makeQuery(id+"FyYUAefgu6xEfva_4.32.F14.boolean.opBoolean","SPLIT",EDGE,{"disambiguationData":[TD([subQ6])],"derivedFrom":makeQuery(id+"FyYUAefgu6xEfva_4.31.F14.boolean.opBoolean","SPLIT",EDGE,{"disambiguationData":[TD([subQ6])],"derivedFrom":makeQuery(id+"FyYUAefgu6xEfva_4.30.F14.boolean.opBoolean","SPLIT",EDGE,{"disambiguationData":[TD([subQ6])],"derivedFrom":makeQuery(id+"FyYUAefgu6xEfva_4.29.F14.boolean.opBoolean","SPLIT",EDGE,{"disambiguationData":[TD([subQ6])],"derivedFrom":makeQuery(id+"FyYUAefgu6xEfva_4.28.F14.boolean.opBoolean","SPLIT",EDGE,{"disambiguationData":[TD([subQ6])],"derivedFrom":makeQuery(id+"FyYUAefgu6xEfva_4.27.F14.boolean.opBoolean","SPLIT",EDGE,{"disambiguationData":[TD([subQ6])],"derivedFrom":makeQuery(id+"FyYUAefgu6xEfva_4.26.F14.boolean.opBoolean","SPLIT",EDGE,{"disambiguationData":[TD([subQ6])],"derivedFrom":makeQuery(id+"FyYUAefgu6xEfva_4.25.F14.boolean.opBoolean","SPLIT",EDGE,{"disambiguationData":[TD([subQ6])],"derivedFrom":makeQuery(id+"FyYUAefgu6xEfva_4.24.F14.boolean.opBoolean","SPLIT",EDGE,{"disambiguationData":[TD([subQ6])],"derivedFrom":makeQuery(id+"FyYUAefgu6xEfva_4.23.F14.boolean.opBoolean","SPLIT",EDGE,{"disambiguationData":[TD([subQ6])],"derivedFrom":makeQuery(id+"FyYUAefgu6xEfva_4.22.F14.boolean.opBoolean","SPLIT",EDGE,{"disambiguationData":[TD([subQ6])],"derivedFrom":makeQuery(id+"FyYUAefgu6xEfva_4.21.F14.boolean.opBoolean","SPLIT",EDGE,{"disambiguationData":[TD([subQ6])],"derivedFrom":makeQuery(id+"FyYUAefgu6xEfva_4.20.F14.boolean.opBoolean","SPLIT",EDGE,{"disambiguationData":[TD([subQ6])],"derivedFrom":makeQuery(id+"FyYUAefgu6xEfva_4.19.F14.boolean.opBoolean","SPLIT",EDGE,{"disambiguationData":[TD([subQ6])],"derivedFrom":makeQuery(id+"FyYUAefgu6xEfva_4.18.F14.boolean.opBoolean","SPLIT",EDGE,{"disambiguationData":[TD([subQ6])],"derivedFrom":makeQuery(id+"FyYUAefgu6xEfva_4.17.F14.boolean.opBoolean","SPLIT",EDGE,{"disambiguationData":[TD([subQ6])],"derivedFrom":makeQuery(id+"FyYUAefgu6xEfva_4.16.F14.boolean.opBoolean","SPLIT",EDGE,{"disambiguationData":[TD([subQ6])],"derivedFrom":makeQuery(id+"FyYUAefgu6xEfva_4.15.F14.boolean.opBoolean","SPLIT",EDGE,{"disambiguationData":[TD([subQ6])],"derivedFrom":makeQuery(id+"FyYUAefgu6xEfva_4.14.F14.boolean.opBoolean","SPLIT",EDGE,{"disambiguationData":[TD([subQ6])],"derivedFrom":makeQuery(id+"FyYUAefgu6xEfva_4.13.F14.boolean.opBoolean","SPLIT",EDGE,{"disambiguationData":[TD([subQ6])],"derivedFrom":makeQuery(id+"FyYUAefgu6xEfva_4.12.F14.boolean.opBoolean","SPLIT",EDGE,{"disambiguationData":[TD([subQ6])],"derivedFrom":makeQuery(id+"FyYUAefgu6xEfva_4.11.F14.boolean.opBoolean","SPLIT",EDGE,{"disambiguationData":[TD([subQ6])],"derivedFrom":makeQuery(id+"FyYUAefgu6xEfva_4.10.F14.boolean.opBoolean","SPLIT",EDGE,{"disambiguationData":[TD([subQ6])],"derivedFrom":makeQuery(id+"FyYUAefgu6xEfva_4.9.F14.boolean.opBoolean","SPLIT",EDGE,{"disambiguationData":[TD([subQ6])],"derivedFrom":makeQuery(id+"FyYUAefgu6xEfva_4.8.F14.boolean.opBoolean","SPLIT",EDGE,{"disambiguationData":[TD([subQ6])],"derivedFrom":makeQuery(id+"FyYUAefgu6xEfva_4.7.F14.boolean.opBoolean","SPLIT",EDGE,{"disambiguationData":[TD([subQ6])],"derivedFrom":makeQuery(id+"FyYUAefgu6xEfva_4.6.F14.boolean.opBoolean","SPLIT",EDGE,{"disambiguationData":[TD([subQ6])],"derivedFrom":makeQuery(id+"FyYUAefgu6xEfva_4.5.F14.boolean.opBoolean","SPLIT",EDGE,{"disambiguationData":[TD([subQ6])],"derivedFrom":makeQuery(id+"FyYUAefgu6xEfva_4.4.F14.boolean.opBoolean","SPLIT",EDGE,{"disambiguationData":[TD([subQ6])],"derivedFrom":makeQuery(id+"FyYUAefgu6xEfva_4.3.F14.boolean.opBoolean","SPLIT",EDGE,{"disambiguationData":[TD([subQ6])],"derivedFrom":makeQuery(id+"FyYUAefgu6xEfva_4.2.F14.boolean.opBoolean","SPLIT",EDGE,{"disambiguationData":[TD([subQ6])],"derivedFrom":makeQuery(id+"FyYUAefgu6xEfva_4.1.F14.boolean.opBoolean","SPLIT",EDGE,{"disambiguationData":[TD([subQ6])],"derivedFrom":makeQuery(id+"F12.opExtrude","CAP_EDGE",EDGE,{"disambiguationData":[OSD([subQ1])],"isStart":true})})})})})})})})})})})})})})})})})})})})})})})})})})})})})})})})})})})})})})})})});}
            var Q506;
            Q506=makeQuery(id+"FyYUAefgu6xEfva_4.10.F14.opExtrude","SWEPT_EDGE",EDGE,{"disambiguationData":[OSD([sQuery(id+"F9.wireOp",EDGE,"E142"),sQuery(id+"F13.wireOp",EDGE,"E148.MirrorCS")])]});
            var Q507;
            Q507=makeQuery(id+"FyYUAefgu6xEfva_4.10.F14.opExtrude","CAP_EDGE",EDGE,{"disambiguationData":[OSD([sQuery(id+"F13.wireOp",EDGE,"E147")])],"isStart":true});
            var Q508;
            Q508=makeQuery(id+"FyYUAefgu6xEfva_4.10.F14.opExtrude","CAP_EDGE",EDGE,{"disambiguationData":[OSD([sQuery(id+"F13.wireOp",EDGE,"E148.MirrorCS")])],"isStart":true});
            var Q509;
            Q509=makeQuery(id+"FyYUAefgu6xEfva_4.42.F14.opExtrude","CAP_EDGE",EDGE,{"disambiguationData":[OSD([sQuery(id+"F9.wireOp",EDGE,"E142")])],"isStart":false});
            var Q510;
            {var subQ1=sQuery(id+"F13.wireOp",EDGE,"E147");var subQ2=sQuery(id+"F11.wireOp",EDGE,"E143");var subQ4=sQuery(id+"F13.wireOp",EDGE,"E148.MirrorCS");var subQ5=makeQuery(id+"FyYUAefgu6xEfva_4.41.F14.opExtrude","SWEPT_FACE",FACE,{"disambiguationData":[OSD([subQ4])]});var subQ6=makeQuery(id+"F14.opExtrude","SWEPT_FACE",FACE,{"disambiguationData":[OSD([subQ1])]});Q510=makeQuery(id+"FyYUAefgu6xEfva_4.42.F14.boolean.opBoolean","SPLIT",EDGE,{"disambiguationData":[TD([subQ5])],"derivedFrom":makeQuery(id+"FyYUAefgu6xEfva_4.41.F14.boolean.opBoolean","SPLIT",EDGE,{"disambiguationData":[TD([subQ6])],"derivedFrom":makeQuery(id+"FyYUAefgu6xEfva_4.40.F14.boolean.opBoolean","SPLIT",EDGE,{"disambiguationData":[TD([subQ6])],"derivedFrom":makeQuery(id+"FyYUAefgu6xEfva_4.39.F14.boolean.opBoolean","SPLIT",EDGE,{"disambiguationData":[TD([subQ6])],"derivedFrom":makeQuery(id+"FyYUAefgu6xEfva_4.38.F14.boolean.opBoolean","SPLIT",EDGE,{"disambiguationData":[TD([subQ6])],"derivedFrom":makeQuery(id+"FyYUAefgu6xEfva_4.37.F14.boolean.opBoolean","SPLIT",EDGE,{"disambiguationData":[TD([subQ6])],"derivedFrom":makeQuery(id+"FyYUAefgu6xEfva_4.36.F14.boolean.opBoolean","SPLIT",EDGE,{"disambiguationData":[TD([subQ6])],"derivedFrom":makeQuery(id+"FyYUAefgu6xEfva_4.35.F14.boolean.opBoolean","SPLIT",EDGE,{"disambiguationData":[TD([subQ6])],"derivedFrom":makeQuery(id+"FyYUAefgu6xEfva_4.34.F14.boolean.opBoolean","SPLIT",EDGE,{"disambiguationData":[TD([subQ6])],"derivedFrom":makeQuery(id+"FyYUAefgu6xEfva_4.33.F14.boolean.opBoolean","SPLIT",EDGE,{"disambiguationData":[TD([subQ6])],"derivedFrom":makeQuery(id+"FyYUAefgu6xEfva_4.32.F14.boolean.opBoolean","SPLIT",EDGE,{"disambiguationData":[TD([subQ6])],"derivedFrom":makeQuery(id+"FyYUAefgu6xEfva_4.31.F14.boolean.opBoolean","SPLIT",EDGE,{"disambiguationData":[TD([subQ6])],"derivedFrom":makeQuery(id+"FyYUAefgu6xEfva_4.30.F14.boolean.opBoolean","SPLIT",EDGE,{"disambiguationData":[TD([subQ6])],"derivedFrom":makeQuery(id+"FyYUAefgu6xEfva_4.29.F14.boolean.opBoolean","SPLIT",EDGE,{"disambiguationData":[TD([subQ6])],"derivedFrom":makeQuery(id+"FyYUAefgu6xEfva_4.28.F14.boolean.opBoolean","SPLIT",EDGE,{"disambiguationData":[TD([subQ6])],"derivedFrom":makeQuery(id+"FyYUAefgu6xEfva_4.27.F14.boolean.opBoolean","SPLIT",EDGE,{"disambiguationData":[TD([subQ6])],"derivedFrom":makeQuery(id+"FyYUAefgu6xEfva_4.26.F14.boolean.opBoolean","SPLIT",EDGE,{"disambiguationData":[TD([subQ6])],"derivedFrom":makeQuery(id+"FyYUAefgu6xEfva_4.25.F14.boolean.opBoolean","SPLIT",EDGE,{"disambiguationData":[TD([subQ6])],"derivedFrom":makeQuery(id+"FyYUAefgu6xEfva_4.24.F14.boolean.opBoolean","SPLIT",EDGE,{"disambiguationData":[TD([subQ6])],"derivedFrom":makeQuery(id+"FyYUAefgu6xEfva_4.23.F14.boolean.opBoolean","SPLIT",EDGE,{"disambiguationData":[TD([subQ6])],"derivedFrom":makeQuery(id+"FyYUAefgu6xEfva_4.22.F14.boolean.opBoolean","SPLIT",EDGE,{"disambiguationData":[TD([subQ6])],"derivedFrom":makeQuery(id+"FyYUAefgu6xEfva_4.21.F14.boolean.opBoolean","SPLIT",EDGE,{"disambiguationData":[TD([subQ6])],"derivedFrom":makeQuery(id+"FyYUAefgu6xEfva_4.20.F14.boolean.opBoolean","SPLIT",EDGE,{"disambiguationData":[TD([subQ6])],"derivedFrom":makeQuery(id+"FyYUAefgu6xEfva_4.19.F14.boolean.opBoolean","SPLIT",EDGE,{"disambiguationData":[TD([subQ6])],"derivedFrom":makeQuery(id+"FyYUAefgu6xEfva_4.18.F14.boolean.opBoolean","SPLIT",EDGE,{"disambiguationData":[TD([subQ6])],"derivedFrom":makeQuery(id+"FyYUAefgu6xEfva_4.17.F14.boolean.opBoolean","SPLIT",EDGE,{"disambiguationData":[TD([subQ6])],"derivedFrom":makeQuery(id+"FyYUAefgu6xEfva_4.16.F14.boolean.opBoolean","SPLIT",EDGE,{"disambiguationData":[TD([subQ6])],"derivedFrom":makeQuery(id+"FyYUAefgu6xEfva_4.15.F14.boolean.opBoolean","SPLIT",EDGE,{"disambiguationData":[TD([subQ6])],"derivedFrom":makeQuery(id+"FyYUAefgu6xEfva_4.14.F14.boolean.opBoolean","SPLIT",EDGE,{"disambiguationData":[TD([subQ6])],"derivedFrom":makeQuery(id+"FyYUAefgu6xEfva_4.13.F14.boolean.opBoolean","SPLIT",EDGE,{"disambiguationData":[TD([subQ6])],"derivedFrom":makeQuery(id+"FyYUAefgu6xEfva_4.12.F14.boolean.opBoolean","SPLIT",EDGE,{"disambiguationData":[TD([subQ6])],"derivedFrom":makeQuery(id+"FyYUAefgu6xEfva_4.11.F14.boolean.opBoolean","SPLIT",EDGE,{"disambiguationData":[TD([subQ6])],"derivedFrom":makeQuery(id+"FyYUAefgu6xEfva_4.10.F14.boolean.opBoolean","SPLIT",EDGE,{"disambiguationData":[TD([subQ6])],"derivedFrom":makeQuery(id+"FyYUAefgu6xEfva_4.9.F14.boolean.opBoolean","SPLIT",EDGE,{"disambiguationData":[TD([subQ6])],"derivedFrom":makeQuery(id+"FyYUAefgu6xEfva_4.8.F14.boolean.opBoolean","SPLIT",EDGE,{"disambiguationData":[TD([subQ6])],"derivedFrom":makeQuery(id+"FyYUAefgu6xEfva_4.7.F14.boolean.opBoolean","SPLIT",EDGE,{"disambiguationData":[TD([subQ6])],"derivedFrom":makeQuery(id+"FyYUAefgu6xEfva_4.6.F14.boolean.opBoolean","SPLIT",EDGE,{"disambiguationData":[TD([subQ6])],"derivedFrom":makeQuery(id+"FyYUAefgu6xEfva_4.5.F14.boolean.opBoolean","SPLIT",EDGE,{"disambiguationData":[TD([subQ6])],"derivedFrom":makeQuery(id+"FyYUAefgu6xEfva_4.4.F14.boolean.opBoolean","SPLIT",EDGE,{"disambiguationData":[TD([subQ6])],"derivedFrom":makeQuery(id+"FyYUAefgu6xEfva_4.3.F14.boolean.opBoolean","SPLIT",EDGE,{"disambiguationData":[TD([subQ6])],"derivedFrom":makeQuery(id+"FyYUAefgu6xEfva_4.2.F14.boolean.opBoolean","SPLIT",EDGE,{"disambiguationData":[TD([subQ6])],"derivedFrom":makeQuery(id+"FyYUAefgu6xEfva_4.1.F14.boolean.opBoolean","SPLIT",EDGE,{"disambiguationData":[TD([subQ6])],"derivedFrom":makeQuery(id+"F12.opExtrude","CAP_EDGE",EDGE,{"disambiguationData":[OSD([subQ2])],"isStart":true})})})})})})})})})})})})})})})})})})})})})})})})})})})})})})})})})})})})})})})})})})});}
            var Q511;
            Q511=makeQuery(id+"FyYUAefgu6xEfva_4.11.F14.opExtrude","SWEPT_EDGE",EDGE,{"disambiguationData":[OSD([sQuery(id+"F9.wireOp",EDGE,"E142"),sQuery(id+"F13.wireOp",EDGE,"E148.MirrorCS")])]});
            var Q512;
            Q512=makeQuery(id+"FyYUAefgu6xEfva_4.11.F14.opExtrude","SWEPT_EDGE",EDGE,{"disambiguationData":[OSD([sQuery(id+"F11.wireOp",EDGE,"E143"),sQuery(id+"F13.wireOp",EDGE,"E148.MirrorCS")])]});
            var Q513;
            Q513=makeQuery(id+"FyYUAefgu6xEfva_4.11.F14.opExtrude","CAP_EDGE",EDGE,{"disambiguationData":[OSD([sQuery(id+"F13.wireOp",EDGE,"E147")])],"isStart":true});
            var Q514;
            Q514=makeQuery(id+"FyYUAefgu6xEfva_4.43.F14.opExtrude","CAP_EDGE",EDGE,{"disambiguationData":[OSD([sQuery(id+"F13.wireOp",EDGE,"E148.MirrorCS")])],"isStart":true});
            var Q515;
            Q515=makeQuery(id+"FyYUAefgu6xEfva_4.43.F14.opExtrude","CAP_EDGE",EDGE,{"disambiguationData":[OSD([sQuery(id+"F9.wireOp",EDGE,"E142")])],"isStart":false});
            var Q516;
            {var subQ1=sQuery(id+"F11.wireOp",EDGE,"E143");var subQ3=sQuery(id+"F13.wireOp",EDGE,"E147");var subQ4=sQuery(id+"F13.wireOp",EDGE,"E148.MirrorCS");var subQ5=makeQuery(id+"FyYUAefgu6xEfva_4.42.F14.opExtrude","SWEPT_FACE",FACE,{"disambiguationData":[OSD([subQ4])]});var subQ6=makeQuery(id+"F14.opExtrude","SWEPT_FACE",FACE,{"disambiguationData":[OSD([subQ3])]});Q516=makeQuery(id+"FyYUAefgu6xEfva_4.43.F14.boolean.opBoolean","SPLIT",EDGE,{"disambiguationData":[TD([subQ5])],"derivedFrom":makeQuery(id+"FyYUAefgu6xEfva_4.42.F14.boolean.opBoolean","SPLIT",EDGE,{"disambiguationData":[TD([subQ6])],"derivedFrom":makeQuery(id+"FyYUAefgu6xEfva_4.41.F14.boolean.opBoolean","SPLIT",EDGE,{"disambiguationData":[TD([subQ6])],"derivedFrom":makeQuery(id+"FyYUAefgu6xEfva_4.40.F14.boolean.opBoolean","SPLIT",EDGE,{"disambiguationData":[TD([subQ6])],"derivedFrom":makeQuery(id+"FyYUAefgu6xEfva_4.39.F14.boolean.opBoolean","SPLIT",EDGE,{"disambiguationData":[TD([subQ6])],"derivedFrom":makeQuery(id+"FyYUAefgu6xEfva_4.38.F14.boolean.opBoolean","SPLIT",EDGE,{"disambiguationData":[TD([subQ6])],"derivedFrom":makeQuery(id+"FyYUAefgu6xEfva_4.37.F14.boolean.opBoolean","SPLIT",EDGE,{"disambiguationData":[TD([subQ6])],"derivedFrom":makeQuery(id+"FyYUAefgu6xEfva_4.36.F14.boolean.opBoolean","SPLIT",EDGE,{"disambiguationData":[TD([subQ6])],"derivedFrom":makeQuery(id+"FyYUAefgu6xEfva_4.35.F14.boolean.opBoolean","SPLIT",EDGE,{"disambiguationData":[TD([subQ6])],"derivedFrom":makeQuery(id+"FyYUAefgu6xEfva_4.34.F14.boolean.opBoolean","SPLIT",EDGE,{"disambiguationData":[TD([subQ6])],"derivedFrom":makeQuery(id+"FyYUAefgu6xEfva_4.33.F14.boolean.opBoolean","SPLIT",EDGE,{"disambiguationData":[TD([subQ6])],"derivedFrom":makeQuery(id+"FyYUAefgu6xEfva_4.32.F14.boolean.opBoolean","SPLIT",EDGE,{"disambiguationData":[TD([subQ6])],"derivedFrom":makeQuery(id+"FyYUAefgu6xEfva_4.31.F14.boolean.opBoolean","SPLIT",EDGE,{"disambiguationData":[TD([subQ6])],"derivedFrom":makeQuery(id+"FyYUAefgu6xEfva_4.30.F14.boolean.opBoolean","SPLIT",EDGE,{"disambiguationData":[TD([subQ6])],"derivedFrom":makeQuery(id+"FyYUAefgu6xEfva_4.29.F14.boolean.opBoolean","SPLIT",EDGE,{"disambiguationData":[TD([subQ6])],"derivedFrom":makeQuery(id+"FyYUAefgu6xEfva_4.28.F14.boolean.opBoolean","SPLIT",EDGE,{"disambiguationData":[TD([subQ6])],"derivedFrom":makeQuery(id+"FyYUAefgu6xEfva_4.27.F14.boolean.opBoolean","SPLIT",EDGE,{"disambiguationData":[TD([subQ6])],"derivedFrom":makeQuery(id+"FyYUAefgu6xEfva_4.26.F14.boolean.opBoolean","SPLIT",EDGE,{"disambiguationData":[TD([subQ6])],"derivedFrom":makeQuery(id+"FyYUAefgu6xEfva_4.25.F14.boolean.opBoolean","SPLIT",EDGE,{"disambiguationData":[TD([subQ6])],"derivedFrom":makeQuery(id+"FyYUAefgu6xEfva_4.24.F14.boolean.opBoolean","SPLIT",EDGE,{"disambiguationData":[TD([subQ6])],"derivedFrom":makeQuery(id+"FyYUAefgu6xEfva_4.23.F14.boolean.opBoolean","SPLIT",EDGE,{"disambiguationData":[TD([subQ6])],"derivedFrom":makeQuery(id+"FyYUAefgu6xEfva_4.22.F14.boolean.opBoolean","SPLIT",EDGE,{"disambiguationData":[TD([subQ6])],"derivedFrom":makeQuery(id+"FyYUAefgu6xEfva_4.21.F14.boolean.opBoolean","SPLIT",EDGE,{"disambiguationData":[TD([subQ6])],"derivedFrom":makeQuery(id+"FyYUAefgu6xEfva_4.20.F14.boolean.opBoolean","SPLIT",EDGE,{"disambiguationData":[TD([subQ6])],"derivedFrom":makeQuery(id+"FyYUAefgu6xEfva_4.19.F14.boolean.opBoolean","SPLIT",EDGE,{"disambiguationData":[TD([subQ6])],"derivedFrom":makeQuery(id+"FyYUAefgu6xEfva_4.18.F14.boolean.opBoolean","SPLIT",EDGE,{"disambiguationData":[TD([subQ6])],"derivedFrom":makeQuery(id+"FyYUAefgu6xEfva_4.17.F14.boolean.opBoolean","SPLIT",EDGE,{"disambiguationData":[TD([subQ6])],"derivedFrom":makeQuery(id+"FyYUAefgu6xEfva_4.16.F14.boolean.opBoolean","SPLIT",EDGE,{"disambiguationData":[TD([subQ6])],"derivedFrom":makeQuery(id+"FyYUAefgu6xEfva_4.15.F14.boolean.opBoolean","SPLIT",EDGE,{"disambiguationData":[TD([subQ6])],"derivedFrom":makeQuery(id+"FyYUAefgu6xEfva_4.14.F14.boolean.opBoolean","SPLIT",EDGE,{"disambiguationData":[TD([subQ6])],"derivedFrom":makeQuery(id+"FyYUAefgu6xEfva_4.13.F14.boolean.opBoolean","SPLIT",EDGE,{"disambiguationData":[TD([subQ6])],"derivedFrom":makeQuery(id+"FyYUAefgu6xEfva_4.12.F14.boolean.opBoolean","SPLIT",EDGE,{"disambiguationData":[TD([subQ6])],"derivedFrom":makeQuery(id+"FyYUAefgu6xEfva_4.11.F14.boolean.opBoolean","SPLIT",EDGE,{"disambiguationData":[TD([subQ6])],"derivedFrom":makeQuery(id+"FyYUAefgu6xEfva_4.10.F14.boolean.opBoolean","SPLIT",EDGE,{"disambiguationData":[TD([subQ6])],"derivedFrom":makeQuery(id+"FyYUAefgu6xEfva_4.9.F14.boolean.opBoolean","SPLIT",EDGE,{"disambiguationData":[TD([subQ6])],"derivedFrom":makeQuery(id+"FyYUAefgu6xEfva_4.8.F14.boolean.opBoolean","SPLIT",EDGE,{"disambiguationData":[TD([subQ6])],"derivedFrom":makeQuery(id+"FyYUAefgu6xEfva_4.7.F14.boolean.opBoolean","SPLIT",EDGE,{"disambiguationData":[TD([subQ6])],"derivedFrom":makeQuery(id+"FyYUAefgu6xEfva_4.6.F14.boolean.opBoolean","SPLIT",EDGE,{"disambiguationData":[TD([subQ6])],"derivedFrom":makeQuery(id+"FyYUAefgu6xEfva_4.5.F14.boolean.opBoolean","SPLIT",EDGE,{"disambiguationData":[TD([subQ6])],"derivedFrom":makeQuery(id+"FyYUAefgu6xEfva_4.4.F14.boolean.opBoolean","SPLIT",EDGE,{"disambiguationData":[TD([subQ6])],"derivedFrom":makeQuery(id+"FyYUAefgu6xEfva_4.3.F14.boolean.opBoolean","SPLIT",EDGE,{"disambiguationData":[TD([subQ6])],"derivedFrom":makeQuery(id+"FyYUAefgu6xEfva_4.2.F14.boolean.opBoolean","SPLIT",EDGE,{"disambiguationData":[TD([subQ6])],"derivedFrom":makeQuery(id+"FyYUAefgu6xEfva_4.1.F14.boolean.opBoolean","SPLIT",EDGE,{"disambiguationData":[TD([subQ6])],"derivedFrom":makeQuery(id+"F12.opExtrude","CAP_EDGE",EDGE,{"disambiguationData":[OSD([subQ1])],"isStart":true})})})})})})})})})})})})})})})})})})})})})})})})})})})})})})})})})})})})})})})})})})})});}
            var Q517;
            Q517=makeQuery(id+"FyYUAefgu6xEfva_4.12.F14.opExtrude","SWEPT_EDGE",EDGE,{"disambiguationData":[OSD([sQuery(id+"F11.wireOp",EDGE,"E143"),sQuery(id+"F13.wireOp",EDGE,"E147")])]});
            var Q518;
            Q518=makeQuery(id+"FyYUAefgu6xEfva_4.12.F14.opExtrude","SWEPT_EDGE",EDGE,{"disambiguationData":[OSD([sQuery(id+"F9.wireOp",EDGE,"E142"),sQuery(id+"F13.wireOp",EDGE,"E148.MirrorCS")])]});
            var Q519;
            Q519=makeQuery(id+"FyYUAefgu6xEfva_4.12.F14.opExtrude","SWEPT_EDGE",EDGE,{"disambiguationData":[OSD([sQuery(id+"F11.wireOp",EDGE,"E143"),sQuery(id+"F13.wireOp",EDGE,"E148.MirrorCS")])]});
            var Q520;
            {var subQ0=sQuery(id+"F9.wireOp",EDGE,"E142");var subQ3=sQuery(id+"F13.wireOp",EDGE,"E147");var subQ4=sQuery(id+"F13.wireOp",EDGE,"E148.MirrorCS");var subQ5=makeQuery(id+"FyYUAefgu6xEfva_4.11.F14.opExtrude","SWEPT_FACE",FACE,{"disambiguationData":[OSD([subQ4])]});var subQ6=makeQuery(id+"F14.opExtrude","SWEPT_FACE",FACE,{"disambiguationData":[OSD([subQ3])]});Q520=makeQuery(id+"FyYUAefgu6xEfva_4.12.F14.boolean.opBoolean","SPLIT",EDGE,{"disambiguationData":[TD([subQ5])],"derivedFrom":makeQuery(id+"FyYUAefgu6xEfva_4.11.F14.boolean.opBoolean","SPLIT",EDGE,{"disambiguationData":[TD([subQ6])],"derivedFrom":makeQuery(id+"FyYUAefgu6xEfva_4.10.F14.boolean.opBoolean","SPLIT",EDGE,{"disambiguationData":[TD([subQ6])],"derivedFrom":makeQuery(id+"FyYUAefgu6xEfva_4.9.F14.boolean.opBoolean","SPLIT",EDGE,{"disambiguationData":[TD([subQ6])],"derivedFrom":makeQuery(id+"FyYUAefgu6xEfva_4.8.F14.boolean.opBoolean","SPLIT",EDGE,{"disambiguationData":[TD([subQ6])],"derivedFrom":makeQuery(id+"FyYUAefgu6xEfva_4.7.F14.boolean.opBoolean","SPLIT",EDGE,{"disambiguationData":[TD([subQ6])],"derivedFrom":makeQuery(id+"FyYUAefgu6xEfva_4.6.F14.boolean.opBoolean","SPLIT",EDGE,{"disambiguationData":[TD([subQ6])],"derivedFrom":makeQuery(id+"FyYUAefgu6xEfva_4.5.F14.boolean.opBoolean","SPLIT",EDGE,{"disambiguationData":[TD([subQ6])],"derivedFrom":makeQuery(id+"FyYUAefgu6xEfva_4.4.F14.boolean.opBoolean","SPLIT",EDGE,{"disambiguationData":[TD([subQ6])],"derivedFrom":makeQuery(id+"FyYUAefgu6xEfva_4.3.F14.boolean.opBoolean","SPLIT",EDGE,{"disambiguationData":[TD([subQ6])],"derivedFrom":makeQuery(id+"FyYUAefgu6xEfva_4.2.F14.boolean.opBoolean","SPLIT",EDGE,{"disambiguationData":[TD([subQ6])],"derivedFrom":makeQuery(id+"FyYUAefgu6xEfva_4.1.F14.boolean.opBoolean","SPLIT",EDGE,{"disambiguationData":[TD([subQ6])],"derivedFrom":makeQuery(id+"F10.boolean.opBoolean","COPY",EDGE,{"derivedFrom":makeQuery(id+"F10.opExtrude","CAP_EDGE",EDGE,{"disambiguationData":[OSD([subQ0])],"isStart":false})})})})})})})})})})})})})});}
            var Q521;
            {var subQ1=sQuery(id+"F13.wireOp",EDGE,"E147");var subQ2=sQuery(id+"F11.wireOp",EDGE,"E143");var subQ4=sQuery(id+"F13.wireOp",EDGE,"E148.MirrorCS");var subQ5=makeQuery(id+"FyYUAefgu6xEfva_4.11.F14.opExtrude","SWEPT_FACE",FACE,{"disambiguationData":[OSD([subQ4])]});var subQ6=makeQuery(id+"F14.opExtrude","SWEPT_FACE",FACE,{"disambiguationData":[OSD([subQ1])]});Q521=makeQuery(id+"FyYUAefgu6xEfva_4.12.F14.boolean.opBoolean","SPLIT",EDGE,{"disambiguationData":[TD([subQ5])],"derivedFrom":makeQuery(id+"FyYUAefgu6xEfva_4.11.F14.boolean.opBoolean","SPLIT",EDGE,{"disambiguationData":[TD([subQ6])],"derivedFrom":makeQuery(id+"FyYUAefgu6xEfva_4.10.F14.boolean.opBoolean","SPLIT",EDGE,{"disambiguationData":[TD([subQ6])],"derivedFrom":makeQuery(id+"FyYUAefgu6xEfva_4.9.F14.boolean.opBoolean","SPLIT",EDGE,{"disambiguationData":[TD([subQ6])],"derivedFrom":makeQuery(id+"FyYUAefgu6xEfva_4.8.F14.boolean.opBoolean","SPLIT",EDGE,{"disambiguationData":[TD([subQ6])],"derivedFrom":makeQuery(id+"FyYUAefgu6xEfva_4.7.F14.boolean.opBoolean","SPLIT",EDGE,{"disambiguationData":[TD([subQ6])],"derivedFrom":makeQuery(id+"FyYUAefgu6xEfva_4.6.F14.boolean.opBoolean","SPLIT",EDGE,{"disambiguationData":[TD([subQ6])],"derivedFrom":makeQuery(id+"FyYUAefgu6xEfva_4.5.F14.boolean.opBoolean","SPLIT",EDGE,{"disambiguationData":[TD([subQ6])],"derivedFrom":makeQuery(id+"FyYUAefgu6xEfva_4.4.F14.boolean.opBoolean","SPLIT",EDGE,{"disambiguationData":[TD([subQ6])],"derivedFrom":makeQuery(id+"FyYUAefgu6xEfva_4.3.F14.boolean.opBoolean","SPLIT",EDGE,{"disambiguationData":[TD([subQ6])],"derivedFrom":makeQuery(id+"FyYUAefgu6xEfva_4.2.F14.boolean.opBoolean","SPLIT",EDGE,{"disambiguationData":[TD([subQ6])],"derivedFrom":makeQuery(id+"FyYUAefgu6xEfva_4.1.F14.boolean.opBoolean","SPLIT",EDGE,{"disambiguationData":[TD([subQ6])],"derivedFrom":makeQuery(id+"F12.opExtrude","CAP_EDGE",EDGE,{"disambiguationData":[OSD([subQ2])],"isStart":true})})})})})})})})})})})})});}
            var Q522;
            Q522=makeQuery(id+"FyYUAefgu6xEfva_4.44.F14.opExtrude","CAP_EDGE",EDGE,{"disambiguationData":[OSD([sQuery(id+"F9.wireOp",EDGE,"E142")])],"isStart":false});
            var Q523;
            {var subQ1=sQuery(id+"F13.wireOp",EDGE,"E148.MirrorCS");var subQ2=makeQuery(id+"FyYUAefgu6xEfva_4.43.F14.opExtrude","SWEPT_FACE",FACE,{"disambiguationData":[OSD([subQ1])]});var subQ3=sQuery(id+"F11.wireOp",EDGE,"E143");var subQ5=sQuery(id+"F13.wireOp",EDGE,"E147");var subQ6=makeQuery(id+"F14.opExtrude","SWEPT_FACE",FACE,{"disambiguationData":[OSD([subQ5])]});Q523=makeQuery(id+"FyYUAefgu6xEfva_4.44.F14.boolean.opBoolean","SPLIT",EDGE,{"disambiguationData":[TD([subQ2])],"derivedFrom":makeQuery(id+"FyYUAefgu6xEfva_4.43.F14.boolean.opBoolean","SPLIT",EDGE,{"disambiguationData":[TD([subQ6])],"derivedFrom":makeQuery(id+"FyYUAefgu6xEfva_4.42.F14.boolean.opBoolean","SPLIT",EDGE,{"disambiguationData":[TD([subQ6])],"derivedFrom":makeQuery(id+"FyYUAefgu6xEfva_4.41.F14.boolean.opBoolean","SPLIT",EDGE,{"disambiguationData":[TD([subQ6])],"derivedFrom":makeQuery(id+"FyYUAefgu6xEfva_4.40.F14.boolean.opBoolean","SPLIT",EDGE,{"disambiguationData":[TD([subQ6])],"derivedFrom":makeQuery(id+"FyYUAefgu6xEfva_4.39.F14.boolean.opBoolean","SPLIT",EDGE,{"disambiguationData":[TD([subQ6])],"derivedFrom":makeQuery(id+"FyYUAefgu6xEfva_4.38.F14.boolean.opBoolean","SPLIT",EDGE,{"disambiguationData":[TD([subQ6])],"derivedFrom":makeQuery(id+"FyYUAefgu6xEfva_4.37.F14.boolean.opBoolean","SPLIT",EDGE,{"disambiguationData":[TD([subQ6])],"derivedFrom":makeQuery(id+"FyYUAefgu6xEfva_4.36.F14.boolean.opBoolean","SPLIT",EDGE,{"disambiguationData":[TD([subQ6])],"derivedFrom":makeQuery(id+"FyYUAefgu6xEfva_4.35.F14.boolean.opBoolean","SPLIT",EDGE,{"disambiguationData":[TD([subQ6])],"derivedFrom":makeQuery(id+"FyYUAefgu6xEfva_4.34.F14.boolean.opBoolean","SPLIT",EDGE,{"disambiguationData":[TD([subQ6])],"derivedFrom":makeQuery(id+"FyYUAefgu6xEfva_4.33.F14.boolean.opBoolean","SPLIT",EDGE,{"disambiguationData":[TD([subQ6])],"derivedFrom":makeQuery(id+"FyYUAefgu6xEfva_4.32.F14.boolean.opBoolean","SPLIT",EDGE,{"disambiguationData":[TD([subQ6])],"derivedFrom":makeQuery(id+"FyYUAefgu6xEfva_4.31.F14.boolean.opBoolean","SPLIT",EDGE,{"disambiguationData":[TD([subQ6])],"derivedFrom":makeQuery(id+"FyYUAefgu6xEfva_4.30.F14.boolean.opBoolean","SPLIT",EDGE,{"disambiguationData":[TD([subQ6])],"derivedFrom":makeQuery(id+"FyYUAefgu6xEfva_4.29.F14.boolean.opBoolean","SPLIT",EDGE,{"disambiguationData":[TD([subQ6])],"derivedFrom":makeQuery(id+"FyYUAefgu6xEfva_4.28.F14.boolean.opBoolean","SPLIT",EDGE,{"disambiguationData":[TD([subQ6])],"derivedFrom":makeQuery(id+"FyYUAefgu6xEfva_4.27.F14.boolean.opBoolean","SPLIT",EDGE,{"disambiguationData":[TD([subQ6])],"derivedFrom":makeQuery(id+"FyYUAefgu6xEfva_4.26.F14.boolean.opBoolean","SPLIT",EDGE,{"disambiguationData":[TD([subQ6])],"derivedFrom":makeQuery(id+"FyYUAefgu6xEfva_4.25.F14.boolean.opBoolean","SPLIT",EDGE,{"disambiguationData":[TD([subQ6])],"derivedFrom":makeQuery(id+"FyYUAefgu6xEfva_4.24.F14.boolean.opBoolean","SPLIT",EDGE,{"disambiguationData":[TD([subQ6])],"derivedFrom":makeQuery(id+"FyYUAefgu6xEfva_4.23.F14.boolean.opBoolean","SPLIT",EDGE,{"disambiguationData":[TD([subQ6])],"derivedFrom":makeQuery(id+"FyYUAefgu6xEfva_4.22.F14.boolean.opBoolean","SPLIT",EDGE,{"disambiguationData":[TD([subQ6])],"derivedFrom":makeQuery(id+"FyYUAefgu6xEfva_4.21.F14.boolean.opBoolean","SPLIT",EDGE,{"disambiguationData":[TD([subQ6])],"derivedFrom":makeQuery(id+"FyYUAefgu6xEfva_4.20.F14.boolean.opBoolean","SPLIT",EDGE,{"disambiguationData":[TD([subQ6])],"derivedFrom":makeQuery(id+"FyYUAefgu6xEfva_4.19.F14.boolean.opBoolean","SPLIT",EDGE,{"disambiguationData":[TD([subQ6])],"derivedFrom":makeQuery(id+"FyYUAefgu6xEfva_4.18.F14.boolean.opBoolean","SPLIT",EDGE,{"disambiguationData":[TD([subQ6])],"derivedFrom":makeQuery(id+"FyYUAefgu6xEfva_4.17.F14.boolean.opBoolean","SPLIT",EDGE,{"disambiguationData":[TD([subQ6])],"derivedFrom":makeQuery(id+"FyYUAefgu6xEfva_4.16.F14.boolean.opBoolean","SPLIT",EDGE,{"disambiguationData":[TD([subQ6])],"derivedFrom":makeQuery(id+"FyYUAefgu6xEfva_4.15.F14.boolean.opBoolean","SPLIT",EDGE,{"disambiguationData":[TD([subQ6])],"derivedFrom":makeQuery(id+"FyYUAefgu6xEfva_4.14.F14.boolean.opBoolean","SPLIT",EDGE,{"disambiguationData":[TD([subQ6])],"derivedFrom":makeQuery(id+"FyYUAefgu6xEfva_4.13.F14.boolean.opBoolean","SPLIT",EDGE,{"disambiguationData":[TD([subQ6])],"derivedFrom":makeQuery(id+"FyYUAefgu6xEfva_4.12.F14.boolean.opBoolean","SPLIT",EDGE,{"disambiguationData":[TD([subQ6])],"derivedFrom":makeQuery(id+"FyYUAefgu6xEfva_4.11.F14.boolean.opBoolean","SPLIT",EDGE,{"disambiguationData":[TD([subQ6])],"derivedFrom":makeQuery(id+"FyYUAefgu6xEfva_4.10.F14.boolean.opBoolean","SPLIT",EDGE,{"disambiguationData":[TD([subQ6])],"derivedFrom":makeQuery(id+"FyYUAefgu6xEfva_4.9.F14.boolean.opBoolean","SPLIT",EDGE,{"disambiguationData":[TD([subQ6])],"derivedFrom":makeQuery(id+"FyYUAefgu6xEfva_4.8.F14.boolean.opBoolean","SPLIT",EDGE,{"disambiguationData":[TD([subQ6])],"derivedFrom":makeQuery(id+"FyYUAefgu6xEfva_4.7.F14.boolean.opBoolean","SPLIT",EDGE,{"disambiguationData":[TD([subQ6])],"derivedFrom":makeQuery(id+"FyYUAefgu6xEfva_4.6.F14.boolean.opBoolean","SPLIT",EDGE,{"disambiguationData":[TD([subQ6])],"derivedFrom":makeQuery(id+"FyYUAefgu6xEfva_4.5.F14.boolean.opBoolean","SPLIT",EDGE,{"disambiguationData":[TD([subQ6])],"derivedFrom":makeQuery(id+"FyYUAefgu6xEfva_4.4.F14.boolean.opBoolean","SPLIT",EDGE,{"disambiguationData":[TD([subQ6])],"derivedFrom":makeQuery(id+"FyYUAefgu6xEfva_4.3.F14.boolean.opBoolean","SPLIT",EDGE,{"disambiguationData":[TD([subQ6])],"derivedFrom":makeQuery(id+"FyYUAefgu6xEfva_4.2.F14.boolean.opBoolean","SPLIT",EDGE,{"disambiguationData":[TD([subQ6])],"derivedFrom":makeQuery(id+"FyYUAefgu6xEfva_4.1.F14.boolean.opBoolean","SPLIT",EDGE,{"disambiguationData":[TD([subQ6])],"derivedFrom":makeQuery(id+"F12.opExtrude","CAP_EDGE",EDGE,{"disambiguationData":[OSD([subQ3])],"isStart":true})})})})})})})})})})})})})})})})})})})})})})})})})})})})})})})})})})})})})})})})})})})})});}
            var Q524;
            Q524=makeQuery(id+"FyYUAefgu6xEfva_4.13.F14.opExtrude","SWEPT_EDGE",EDGE,{"disambiguationData":[OSD([sQuery(id+"F11.wireOp",EDGE,"E143"),sQuery(id+"F13.wireOp",EDGE,"E147")])]});
            var Q525;
            Q525=makeQuery(id+"FyYUAefgu6xEfva_4.13.F14.opExtrude","CAP_EDGE",EDGE,{"disambiguationData":[OSD([sQuery(id+"F13.wireOp",EDGE,"E148.MirrorCS")])],"isStart":true});
            var Q526;
            {var subQ0=sQuery(id+"F9.wireOp",EDGE,"E142");var subQ3=sQuery(id+"F13.wireOp",EDGE,"E148.MirrorCS");var subQ4=makeQuery(id+"FyYUAefgu6xEfva_4.12.F14.opExtrude","SWEPT_FACE",FACE,{"disambiguationData":[OSD([subQ3])]});var subQ5=sQuery(id+"F13.wireOp",EDGE,"E147");var subQ6=makeQuery(id+"F14.opExtrude","SWEPT_FACE",FACE,{"disambiguationData":[OSD([subQ5])]});Q526=makeQuery(id+"FyYUAefgu6xEfva_4.13.F14.boolean.opBoolean","SPLIT",EDGE,{"disambiguationData":[TD([subQ4])],"derivedFrom":makeQuery(id+"FyYUAefgu6xEfva_4.12.F14.boolean.opBoolean","SPLIT",EDGE,{"disambiguationData":[TD([subQ6])],"derivedFrom":makeQuery(id+"FyYUAefgu6xEfva_4.11.F14.boolean.opBoolean","SPLIT",EDGE,{"disambiguationData":[TD([subQ6])],"derivedFrom":makeQuery(id+"FyYUAefgu6xEfva_4.10.F14.boolean.opBoolean","SPLIT",EDGE,{"disambiguationData":[TD([subQ6])],"derivedFrom":makeQuery(id+"FyYUAefgu6xEfva_4.9.F14.boolean.opBoolean","SPLIT",EDGE,{"disambiguationData":[TD([subQ6])],"derivedFrom":makeQuery(id+"FyYUAefgu6xEfva_4.8.F14.boolean.opBoolean","SPLIT",EDGE,{"disambiguationData":[TD([subQ6])],"derivedFrom":makeQuery(id+"FyYUAefgu6xEfva_4.7.F14.boolean.opBoolean","SPLIT",EDGE,{"disambiguationData":[TD([subQ6])],"derivedFrom":makeQuery(id+"FyYUAefgu6xEfva_4.6.F14.boolean.opBoolean","SPLIT",EDGE,{"disambiguationData":[TD([subQ6])],"derivedFrom":makeQuery(id+"FyYUAefgu6xEfva_4.5.F14.boolean.opBoolean","SPLIT",EDGE,{"disambiguationData":[TD([subQ6])],"derivedFrom":makeQuery(id+"FyYUAefgu6xEfva_4.4.F14.boolean.opBoolean","SPLIT",EDGE,{"disambiguationData":[TD([subQ6])],"derivedFrom":makeQuery(id+"FyYUAefgu6xEfva_4.3.F14.boolean.opBoolean","SPLIT",EDGE,{"disambiguationData":[TD([subQ6])],"derivedFrom":makeQuery(id+"FyYUAefgu6xEfva_4.2.F14.boolean.opBoolean","SPLIT",EDGE,{"disambiguationData":[TD([subQ6])],"derivedFrom":makeQuery(id+"FyYUAefgu6xEfva_4.1.F14.boolean.opBoolean","SPLIT",EDGE,{"disambiguationData":[TD([subQ6])],"derivedFrom":makeQuery(id+"F10.boolean.opBoolean","COPY",EDGE,{"derivedFrom":makeQuery(id+"F10.opExtrude","CAP_EDGE",EDGE,{"disambiguationData":[OSD([subQ0])],"isStart":false})})})})})})})})})})})})})})});}
            var Q527;
            Q527=makeQuery(id+"FyYUAefgu6xEfva_4.45.F14.opExtrude","CAP_EDGE",EDGE,{"disambiguationData":[OSD([sQuery(id+"F9.wireOp",EDGE,"E142")])],"isStart":false});
            var Q528;
            {var subQ1=sQuery(id+"F11.wireOp",EDGE,"E143");var subQ3=sQuery(id+"F13.wireOp",EDGE,"E148.MirrorCS");var subQ4=makeQuery(id+"FyYUAefgu6xEfva_4.44.F14.opExtrude","SWEPT_FACE",FACE,{"disambiguationData":[OSD([subQ3])]});var subQ5=sQuery(id+"F13.wireOp",EDGE,"E147");var subQ6=makeQuery(id+"F14.opExtrude","SWEPT_FACE",FACE,{"disambiguationData":[OSD([subQ5])]});Q528=makeQuery(id+"FyYUAefgu6xEfva_4.45.F14.boolean.opBoolean","SPLIT",EDGE,{"disambiguationData":[TD([subQ4])],"derivedFrom":makeQuery(id+"FyYUAefgu6xEfva_4.44.F14.boolean.opBoolean","SPLIT",EDGE,{"disambiguationData":[TD([subQ6])],"derivedFrom":makeQuery(id+"FyYUAefgu6xEfva_4.43.F14.boolean.opBoolean","SPLIT",EDGE,{"disambiguationData":[TD([subQ6])],"derivedFrom":makeQuery(id+"FyYUAefgu6xEfva_4.42.F14.boolean.opBoolean","SPLIT",EDGE,{"disambiguationData":[TD([subQ6])],"derivedFrom":makeQuery(id+"FyYUAefgu6xEfva_4.41.F14.boolean.opBoolean","SPLIT",EDGE,{"disambiguationData":[TD([subQ6])],"derivedFrom":makeQuery(id+"FyYUAefgu6xEfva_4.40.F14.boolean.opBoolean","SPLIT",EDGE,{"disambiguationData":[TD([subQ6])],"derivedFrom":makeQuery(id+"FyYUAefgu6xEfva_4.39.F14.boolean.opBoolean","SPLIT",EDGE,{"disambiguationData":[TD([subQ6])],"derivedFrom":makeQuery(id+"FyYUAefgu6xEfva_4.38.F14.boolean.opBoolean","SPLIT",EDGE,{"disambiguationData":[TD([subQ6])],"derivedFrom":makeQuery(id+"FyYUAefgu6xEfva_4.37.F14.boolean.opBoolean","SPLIT",EDGE,{"disambiguationData":[TD([subQ6])],"derivedFrom":makeQuery(id+"FyYUAefgu6xEfva_4.36.F14.boolean.opBoolean","SPLIT",EDGE,{"disambiguationData":[TD([subQ6])],"derivedFrom":makeQuery(id+"FyYUAefgu6xEfva_4.35.F14.boolean.opBoolean","SPLIT",EDGE,{"disambiguationData":[TD([subQ6])],"derivedFrom":makeQuery(id+"FyYUAefgu6xEfva_4.34.F14.boolean.opBoolean","SPLIT",EDGE,{"disambiguationData":[TD([subQ6])],"derivedFrom":makeQuery(id+"FyYUAefgu6xEfva_4.33.F14.boolean.opBoolean","SPLIT",EDGE,{"disambiguationData":[TD([subQ6])],"derivedFrom":makeQuery(id+"FyYUAefgu6xEfva_4.32.F14.boolean.opBoolean","SPLIT",EDGE,{"disambiguationData":[TD([subQ6])],"derivedFrom":makeQuery(id+"FyYUAefgu6xEfva_4.31.F14.boolean.opBoolean","SPLIT",EDGE,{"disambiguationData":[TD([subQ6])],"derivedFrom":makeQuery(id+"FyYUAefgu6xEfva_4.30.F14.boolean.opBoolean","SPLIT",EDGE,{"disambiguationData":[TD([subQ6])],"derivedFrom":makeQuery(id+"FyYUAefgu6xEfva_4.29.F14.boolean.opBoolean","SPLIT",EDGE,{"disambiguationData":[TD([subQ6])],"derivedFrom":makeQuery(id+"FyYUAefgu6xEfva_4.28.F14.boolean.opBoolean","SPLIT",EDGE,{"disambiguationData":[TD([subQ6])],"derivedFrom":makeQuery(id+"FyYUAefgu6xEfva_4.27.F14.boolean.opBoolean","SPLIT",EDGE,{"disambiguationData":[TD([subQ6])],"derivedFrom":makeQuery(id+"FyYUAefgu6xEfva_4.26.F14.boolean.opBoolean","SPLIT",EDGE,{"disambiguationData":[TD([subQ6])],"derivedFrom":makeQuery(id+"FyYUAefgu6xEfva_4.25.F14.boolean.opBoolean","SPLIT",EDGE,{"disambiguationData":[TD([subQ6])],"derivedFrom":makeQuery(id+"FyYUAefgu6xEfva_4.24.F14.boolean.opBoolean","SPLIT",EDGE,{"disambiguationData":[TD([subQ6])],"derivedFrom":makeQuery(id+"FyYUAefgu6xEfva_4.23.F14.boolean.opBoolean","SPLIT",EDGE,{"disambiguationData":[TD([subQ6])],"derivedFrom":makeQuery(id+"FyYUAefgu6xEfva_4.22.F14.boolean.opBoolean","SPLIT",EDGE,{"disambiguationData":[TD([subQ6])],"derivedFrom":makeQuery(id+"FyYUAefgu6xEfva_4.21.F14.boolean.opBoolean","SPLIT",EDGE,{"disambiguationData":[TD([subQ6])],"derivedFrom":makeQuery(id+"FyYUAefgu6xEfva_4.20.F14.boolean.opBoolean","SPLIT",EDGE,{"disambiguationData":[TD([subQ6])],"derivedFrom":makeQuery(id+"FyYUAefgu6xEfva_4.19.F14.boolean.opBoolean","SPLIT",EDGE,{"disambiguationData":[TD([subQ6])],"derivedFrom":makeQuery(id+"FyYUAefgu6xEfva_4.18.F14.boolean.opBoolean","SPLIT",EDGE,{"disambiguationData":[TD([subQ6])],"derivedFrom":makeQuery(id+"FyYUAefgu6xEfva_4.17.F14.boolean.opBoolean","SPLIT",EDGE,{"disambiguationData":[TD([subQ6])],"derivedFrom":makeQuery(id+"FyYUAefgu6xEfva_4.16.F14.boolean.opBoolean","SPLIT",EDGE,{"disambiguationData":[TD([subQ6])],"derivedFrom":makeQuery(id+"FyYUAefgu6xEfva_4.15.F14.boolean.opBoolean","SPLIT",EDGE,{"disambiguationData":[TD([subQ6])],"derivedFrom":makeQuery(id+"FyYUAefgu6xEfva_4.14.F14.boolean.opBoolean","SPLIT",EDGE,{"disambiguationData":[TD([subQ6])],"derivedFrom":makeQuery(id+"FyYUAefgu6xEfva_4.13.F14.boolean.opBoolean","SPLIT",EDGE,{"disambiguationData":[TD([subQ6])],"derivedFrom":makeQuery(id+"FyYUAefgu6xEfva_4.12.F14.boolean.opBoolean","SPLIT",EDGE,{"disambiguationData":[TD([subQ6])],"derivedFrom":makeQuery(id+"FyYUAefgu6xEfva_4.11.F14.boolean.opBoolean","SPLIT",EDGE,{"disambiguationData":[TD([subQ6])],"derivedFrom":makeQuery(id+"FyYUAefgu6xEfva_4.10.F14.boolean.opBoolean","SPLIT",EDGE,{"disambiguationData":[TD([subQ6])],"derivedFrom":makeQuery(id+"FyYUAefgu6xEfva_4.9.F14.boolean.opBoolean","SPLIT",EDGE,{"disambiguationData":[TD([subQ6])],"derivedFrom":makeQuery(id+"FyYUAefgu6xEfva_4.8.F14.boolean.opBoolean","SPLIT",EDGE,{"disambiguationData":[TD([subQ6])],"derivedFrom":makeQuery(id+"FyYUAefgu6xEfva_4.7.F14.boolean.opBoolean","SPLIT",EDGE,{"disambiguationData":[TD([subQ6])],"derivedFrom":makeQuery(id+"FyYUAefgu6xEfva_4.6.F14.boolean.opBoolean","SPLIT",EDGE,{"disambiguationData":[TD([subQ6])],"derivedFrom":makeQuery(id+"FyYUAefgu6xEfva_4.5.F14.boolean.opBoolean","SPLIT",EDGE,{"disambiguationData":[TD([subQ6])],"derivedFrom":makeQuery(id+"FyYUAefgu6xEfva_4.4.F14.boolean.opBoolean","SPLIT",EDGE,{"disambiguationData":[TD([subQ6])],"derivedFrom":makeQuery(id+"FyYUAefgu6xEfva_4.3.F14.boolean.opBoolean","SPLIT",EDGE,{"disambiguationData":[TD([subQ6])],"derivedFrom":makeQuery(id+"FyYUAefgu6xEfva_4.2.F14.boolean.opBoolean","SPLIT",EDGE,{"disambiguationData":[TD([subQ6])],"derivedFrom":makeQuery(id+"FyYUAefgu6xEfva_4.1.F14.boolean.opBoolean","SPLIT",EDGE,{"disambiguationData":[TD([subQ6])],"derivedFrom":makeQuery(id+"F12.opExtrude","CAP_EDGE",EDGE,{"disambiguationData":[OSD([subQ1])],"isStart":true})})})})})})})})})})})})})})})})})})})})})})})})})})})})})})})})})})})})})})})})})})})})})});}
            var Q529;
            Q529=makeQuery(id+"FyYUAefgu6xEfva_4.14.F14.opExtrude","SWEPT_EDGE",EDGE,{"disambiguationData":[OSD([sQuery(id+"F9.wireOp",EDGE,"E142"),sQuery(id+"F13.wireOp",EDGE,"E148.MirrorCS")])]});
            var Q530;
            Q530=makeQuery(id+"FyYUAefgu6xEfva_4.14.F14.opExtrude","SWEPT_EDGE",EDGE,{"disambiguationData":[OSD([sQuery(id+"F11.wireOp",EDGE,"E143"),sQuery(id+"F13.wireOp",EDGE,"E148.MirrorCS")])]});
            var Q531;
            Q531=makeQuery(id+"FyYUAefgu6xEfva_4.14.F14.opExtrude","CAP_EDGE",EDGE,{"disambiguationData":[OSD([sQuery(id+"F13.wireOp",EDGE,"E147")])],"isStart":true});
            var Q532;
            Q532=makeQuery(id+"FyYUAefgu6xEfva_4.14.F14.opExtrude","CAP_EDGE",EDGE,{"disambiguationData":[OSD([sQuery(id+"F13.wireOp",EDGE,"E148.MirrorCS")])],"isStart":true});
            var Q533;
            {var subQ0=sQuery(id+"F9.wireOp",EDGE,"E142");var subQ2=sQuery(id+"F13.wireOp",EDGE,"E147");var subQ4=sQuery(id+"F13.wireOp",EDGE,"E148.MirrorCS");var subQ5=makeQuery(id+"FyYUAefgu6xEfva_4.13.F14.opExtrude","SWEPT_FACE",FACE,{"disambiguationData":[OSD([subQ4])]});var subQ6=makeQuery(id+"F14.opExtrude","SWEPT_FACE",FACE,{"disambiguationData":[OSD([subQ2])]});Q533=makeQuery(id+"FyYUAefgu6xEfva_4.14.F14.boolean.opBoolean","SPLIT",EDGE,{"disambiguationData":[TD([subQ5])],"derivedFrom":makeQuery(id+"FyYUAefgu6xEfva_4.13.F14.boolean.opBoolean","SPLIT",EDGE,{"disambiguationData":[TD([subQ6])],"derivedFrom":makeQuery(id+"FyYUAefgu6xEfva_4.12.F14.boolean.opBoolean","SPLIT",EDGE,{"disambiguationData":[TD([subQ6])],"derivedFrom":makeQuery(id+"FyYUAefgu6xEfva_4.11.F14.boolean.opBoolean","SPLIT",EDGE,{"disambiguationData":[TD([subQ6])],"derivedFrom":makeQuery(id+"FyYUAefgu6xEfva_4.10.F14.boolean.opBoolean","SPLIT",EDGE,{"disambiguationData":[TD([subQ6])],"derivedFrom":makeQuery(id+"FyYUAefgu6xEfva_4.9.F14.boolean.opBoolean","SPLIT",EDGE,{"disambiguationData":[TD([subQ6])],"derivedFrom":makeQuery(id+"FyYUAefgu6xEfva_4.8.F14.boolean.opBoolean","SPLIT",EDGE,{"disambiguationData":[TD([subQ6])],"derivedFrom":makeQuery(id+"FyYUAefgu6xEfva_4.7.F14.boolean.opBoolean","SPLIT",EDGE,{"disambiguationData":[TD([subQ6])],"derivedFrom":makeQuery(id+"FyYUAefgu6xEfva_4.6.F14.boolean.opBoolean","SPLIT",EDGE,{"disambiguationData":[TD([subQ6])],"derivedFrom":makeQuery(id+"FyYUAefgu6xEfva_4.5.F14.boolean.opBoolean","SPLIT",EDGE,{"disambiguationData":[TD([subQ6])],"derivedFrom":makeQuery(id+"FyYUAefgu6xEfva_4.4.F14.boolean.opBoolean","SPLIT",EDGE,{"disambiguationData":[TD([subQ6])],"derivedFrom":makeQuery(id+"FyYUAefgu6xEfva_4.3.F14.boolean.opBoolean","SPLIT",EDGE,{"disambiguationData":[TD([subQ6])],"derivedFrom":makeQuery(id+"FyYUAefgu6xEfva_4.2.F14.boolean.opBoolean","SPLIT",EDGE,{"disambiguationData":[TD([subQ6])],"derivedFrom":makeQuery(id+"FyYUAefgu6xEfva_4.1.F14.boolean.opBoolean","SPLIT",EDGE,{"disambiguationData":[TD([subQ6])],"derivedFrom":makeQuery(id+"F10.boolean.opBoolean","COPY",EDGE,{"derivedFrom":makeQuery(id+"F10.opExtrude","CAP_EDGE",EDGE,{"disambiguationData":[OSD([subQ0])],"isStart":false})})})})})})})})})})})})})})})});}
            var Q534;
            {var subQ1=sQuery(id+"F11.wireOp",EDGE,"E143");var subQ3=sQuery(id+"F13.wireOp",EDGE,"E148.MirrorCS");var subQ4=makeQuery(id+"FyYUAefgu6xEfva_4.45.F14.opExtrude","SWEPT_FACE",FACE,{"disambiguationData":[OSD([subQ3])]});var subQ5=sQuery(id+"F13.wireOp",EDGE,"E147");var subQ6=makeQuery(id+"F14.opExtrude","SWEPT_FACE",FACE,{"disambiguationData":[OSD([subQ5])]});Q534=makeQuery(id+"FyYUAefgu6xEfva_4.46.F14.boolean.opBoolean","SPLIT",EDGE,{"disambiguationData":[TD([subQ4])],"derivedFrom":makeQuery(id+"FyYUAefgu6xEfva_4.45.F14.boolean.opBoolean","SPLIT",EDGE,{"disambiguationData":[TD([subQ6])],"derivedFrom":makeQuery(id+"FyYUAefgu6xEfva_4.44.F14.boolean.opBoolean","SPLIT",EDGE,{"disambiguationData":[TD([subQ6])],"derivedFrom":makeQuery(id+"FyYUAefgu6xEfva_4.43.F14.boolean.opBoolean","SPLIT",EDGE,{"disambiguationData":[TD([subQ6])],"derivedFrom":makeQuery(id+"FyYUAefgu6xEfva_4.42.F14.boolean.opBoolean","SPLIT",EDGE,{"disambiguationData":[TD([subQ6])],"derivedFrom":makeQuery(id+"FyYUAefgu6xEfva_4.41.F14.boolean.opBoolean","SPLIT",EDGE,{"disambiguationData":[TD([subQ6])],"derivedFrom":makeQuery(id+"FyYUAefgu6xEfva_4.40.F14.boolean.opBoolean","SPLIT",EDGE,{"disambiguationData":[TD([subQ6])],"derivedFrom":makeQuery(id+"FyYUAefgu6xEfva_4.39.F14.boolean.opBoolean","SPLIT",EDGE,{"disambiguationData":[TD([subQ6])],"derivedFrom":makeQuery(id+"FyYUAefgu6xEfva_4.38.F14.boolean.opBoolean","SPLIT",EDGE,{"disambiguationData":[TD([subQ6])],"derivedFrom":makeQuery(id+"FyYUAefgu6xEfva_4.37.F14.boolean.opBoolean","SPLIT",EDGE,{"disambiguationData":[TD([subQ6])],"derivedFrom":makeQuery(id+"FyYUAefgu6xEfva_4.36.F14.boolean.opBoolean","SPLIT",EDGE,{"disambiguationData":[TD([subQ6])],"derivedFrom":makeQuery(id+"FyYUAefgu6xEfva_4.35.F14.boolean.opBoolean","SPLIT",EDGE,{"disambiguationData":[TD([subQ6])],"derivedFrom":makeQuery(id+"FyYUAefgu6xEfva_4.34.F14.boolean.opBoolean","SPLIT",EDGE,{"disambiguationData":[TD([subQ6])],"derivedFrom":makeQuery(id+"FyYUAefgu6xEfva_4.33.F14.boolean.opBoolean","SPLIT",EDGE,{"disambiguationData":[TD([subQ6])],"derivedFrom":makeQuery(id+"FyYUAefgu6xEfva_4.32.F14.boolean.opBoolean","SPLIT",EDGE,{"disambiguationData":[TD([subQ6])],"derivedFrom":makeQuery(id+"FyYUAefgu6xEfva_4.31.F14.boolean.opBoolean","SPLIT",EDGE,{"disambiguationData":[TD([subQ6])],"derivedFrom":makeQuery(id+"FyYUAefgu6xEfva_4.30.F14.boolean.opBoolean","SPLIT",EDGE,{"disambiguationData":[TD([subQ6])],"derivedFrom":makeQuery(id+"FyYUAefgu6xEfva_4.29.F14.boolean.opBoolean","SPLIT",EDGE,{"disambiguationData":[TD([subQ6])],"derivedFrom":makeQuery(id+"FyYUAefgu6xEfva_4.28.F14.boolean.opBoolean","SPLIT",EDGE,{"disambiguationData":[TD([subQ6])],"derivedFrom":makeQuery(id+"FyYUAefgu6xEfva_4.27.F14.boolean.opBoolean","SPLIT",EDGE,{"disambiguationData":[TD([subQ6])],"derivedFrom":makeQuery(id+"FyYUAefgu6xEfva_4.26.F14.boolean.opBoolean","SPLIT",EDGE,{"disambiguationData":[TD([subQ6])],"derivedFrom":makeQuery(id+"FyYUAefgu6xEfva_4.25.F14.boolean.opBoolean","SPLIT",EDGE,{"disambiguationData":[TD([subQ6])],"derivedFrom":makeQuery(id+"FyYUAefgu6xEfva_4.24.F14.boolean.opBoolean","SPLIT",EDGE,{"disambiguationData":[TD([subQ6])],"derivedFrom":makeQuery(id+"FyYUAefgu6xEfva_4.23.F14.boolean.opBoolean","SPLIT",EDGE,{"disambiguationData":[TD([subQ6])],"derivedFrom":makeQuery(id+"FyYUAefgu6xEfva_4.22.F14.boolean.opBoolean","SPLIT",EDGE,{"disambiguationData":[TD([subQ6])],"derivedFrom":makeQuery(id+"FyYUAefgu6xEfva_4.21.F14.boolean.opBoolean","SPLIT",EDGE,{"disambiguationData":[TD([subQ6])],"derivedFrom":makeQuery(id+"FyYUAefgu6xEfva_4.20.F14.boolean.opBoolean","SPLIT",EDGE,{"disambiguationData":[TD([subQ6])],"derivedFrom":makeQuery(id+"FyYUAefgu6xEfva_4.19.F14.boolean.opBoolean","SPLIT",EDGE,{"disambiguationData":[TD([subQ6])],"derivedFrom":makeQuery(id+"FyYUAefgu6xEfva_4.18.F14.boolean.opBoolean","SPLIT",EDGE,{"disambiguationData":[TD([subQ6])],"derivedFrom":makeQuery(id+"FyYUAefgu6xEfva_4.17.F14.boolean.opBoolean","SPLIT",EDGE,{"disambiguationData":[TD([subQ6])],"derivedFrom":makeQuery(id+"FyYUAefgu6xEfva_4.16.F14.boolean.opBoolean","SPLIT",EDGE,{"disambiguationData":[TD([subQ6])],"derivedFrom":makeQuery(id+"FyYUAefgu6xEfva_4.15.F14.boolean.opBoolean","SPLIT",EDGE,{"disambiguationData":[TD([subQ6])],"derivedFrom":makeQuery(id+"FyYUAefgu6xEfva_4.14.F14.boolean.opBoolean","SPLIT",EDGE,{"disambiguationData":[TD([subQ6])],"derivedFrom":makeQuery(id+"FyYUAefgu6xEfva_4.13.F14.boolean.opBoolean","SPLIT",EDGE,{"disambiguationData":[TD([subQ6])],"derivedFrom":makeQuery(id+"FyYUAefgu6xEfva_4.12.F14.boolean.opBoolean","SPLIT",EDGE,{"disambiguationData":[TD([subQ6])],"derivedFrom":makeQuery(id+"FyYUAefgu6xEfva_4.11.F14.boolean.opBoolean","SPLIT",EDGE,{"disambiguationData":[TD([subQ6])],"derivedFrom":makeQuery(id+"FyYUAefgu6xEfva_4.10.F14.boolean.opBoolean","SPLIT",EDGE,{"disambiguationData":[TD([subQ6])],"derivedFrom":makeQuery(id+"FyYUAefgu6xEfva_4.9.F14.boolean.opBoolean","SPLIT",EDGE,{"disambiguationData":[TD([subQ6])],"derivedFrom":makeQuery(id+"FyYUAefgu6xEfva_4.8.F14.boolean.opBoolean","SPLIT",EDGE,{"disambiguationData":[TD([subQ6])],"derivedFrom":makeQuery(id+"FyYUAefgu6xEfva_4.7.F14.boolean.opBoolean","SPLIT",EDGE,{"disambiguationData":[TD([subQ6])],"derivedFrom":makeQuery(id+"FyYUAefgu6xEfva_4.6.F14.boolean.opBoolean","SPLIT",EDGE,{"disambiguationData":[TD([subQ6])],"derivedFrom":makeQuery(id+"FyYUAefgu6xEfva_4.5.F14.boolean.opBoolean","SPLIT",EDGE,{"disambiguationData":[TD([subQ6])],"derivedFrom":makeQuery(id+"FyYUAefgu6xEfva_4.4.F14.boolean.opBoolean","SPLIT",EDGE,{"disambiguationData":[TD([subQ6])],"derivedFrom":makeQuery(id+"FyYUAefgu6xEfva_4.3.F14.boolean.opBoolean","SPLIT",EDGE,{"disambiguationData":[TD([subQ6])],"derivedFrom":makeQuery(id+"FyYUAefgu6xEfva_4.2.F14.boolean.opBoolean","SPLIT",EDGE,{"disambiguationData":[TD([subQ6])],"derivedFrom":makeQuery(id+"FyYUAefgu6xEfva_4.1.F14.boolean.opBoolean","SPLIT",EDGE,{"disambiguationData":[TD([subQ6])],"derivedFrom":makeQuery(id+"F12.opExtrude","CAP_EDGE",EDGE,{"disambiguationData":[OSD([subQ1])],"isStart":true})})})})})})})})})})})})})})})})})})})})})})})})})})})})})})})})})})})})})})})})})})})})})})});}
            var Q535;
            Q535=makeQuery(id+"FyYUAefgu6xEfva_4.15.F14.opExtrude","CAP_EDGE",EDGE,{"disambiguationData":[OSD([sQuery(id+"F13.wireOp",EDGE,"E147")])],"isStart":true});
            var Q536;
            Q536=makeQuery(id+"FyYUAefgu6xEfva_4.15.F14.opExtrude","CAP_EDGE",EDGE,{"disambiguationData":[OSD([sQuery(id+"F13.wireOp",EDGE,"E148.MirrorCS")])],"isStart":true});
            var Q537;
            {var subQ0=sQuery(id+"F9.wireOp",EDGE,"E142");var subQ3=sQuery(id+"F13.wireOp",EDGE,"E148.MirrorCS");var subQ4=makeQuery(id+"FyYUAefgu6xEfva_4.14.F14.opExtrude","SWEPT_FACE",FACE,{"disambiguationData":[OSD([subQ3])]});var subQ5=sQuery(id+"F13.wireOp",EDGE,"E147");var subQ6=makeQuery(id+"F14.opExtrude","SWEPT_FACE",FACE,{"disambiguationData":[OSD([subQ5])]});Q537=makeQuery(id+"FyYUAefgu6xEfva_4.15.F14.boolean.opBoolean","SPLIT",EDGE,{"disambiguationData":[TD([subQ4])],"derivedFrom":makeQuery(id+"FyYUAefgu6xEfva_4.14.F14.boolean.opBoolean","SPLIT",EDGE,{"disambiguationData":[TD([subQ6])],"derivedFrom":makeQuery(id+"FyYUAefgu6xEfva_4.13.F14.boolean.opBoolean","SPLIT",EDGE,{"disambiguationData":[TD([subQ6])],"derivedFrom":makeQuery(id+"FyYUAefgu6xEfva_4.12.F14.boolean.opBoolean","SPLIT",EDGE,{"disambiguationData":[TD([subQ6])],"derivedFrom":makeQuery(id+"FyYUAefgu6xEfva_4.11.F14.boolean.opBoolean","SPLIT",EDGE,{"disambiguationData":[TD([subQ6])],"derivedFrom":makeQuery(id+"FyYUAefgu6xEfva_4.10.F14.boolean.opBoolean","SPLIT",EDGE,{"disambiguationData":[TD([subQ6])],"derivedFrom":makeQuery(id+"FyYUAefgu6xEfva_4.9.F14.boolean.opBoolean","SPLIT",EDGE,{"disambiguationData":[TD([subQ6])],"derivedFrom":makeQuery(id+"FyYUAefgu6xEfva_4.8.F14.boolean.opBoolean","SPLIT",EDGE,{"disambiguationData":[TD([subQ6])],"derivedFrom":makeQuery(id+"FyYUAefgu6xEfva_4.7.F14.boolean.opBoolean","SPLIT",EDGE,{"disambiguationData":[TD([subQ6])],"derivedFrom":makeQuery(id+"FyYUAefgu6xEfva_4.6.F14.boolean.opBoolean","SPLIT",EDGE,{"disambiguationData":[TD([subQ6])],"derivedFrom":makeQuery(id+"FyYUAefgu6xEfva_4.5.F14.boolean.opBoolean","SPLIT",EDGE,{"disambiguationData":[TD([subQ6])],"derivedFrom":makeQuery(id+"FyYUAefgu6xEfva_4.4.F14.boolean.opBoolean","SPLIT",EDGE,{"disambiguationData":[TD([subQ6])],"derivedFrom":makeQuery(id+"FyYUAefgu6xEfva_4.3.F14.boolean.opBoolean","SPLIT",EDGE,{"disambiguationData":[TD([subQ6])],"derivedFrom":makeQuery(id+"FyYUAefgu6xEfva_4.2.F14.boolean.opBoolean","SPLIT",EDGE,{"disambiguationData":[TD([subQ6])],"derivedFrom":makeQuery(id+"FyYUAefgu6xEfva_4.1.F14.boolean.opBoolean","SPLIT",EDGE,{"disambiguationData":[TD([subQ6])],"derivedFrom":makeQuery(id+"F10.boolean.opBoolean","COPY",EDGE,{"derivedFrom":makeQuery(id+"F10.opExtrude","CAP_EDGE",EDGE,{"disambiguationData":[OSD([subQ0])],"isStart":false})})})})})})})})})})})})})})})})});}
            var Q538;
            {var subQ1=sQuery(id+"F11.wireOp",EDGE,"E143");var subQ3=sQuery(id+"F13.wireOp",EDGE,"E148.MirrorCS");var subQ4=makeQuery(id+"FyYUAefgu6xEfva_4.14.F14.opExtrude","SWEPT_FACE",FACE,{"disambiguationData":[OSD([subQ3])]});var subQ5=sQuery(id+"F13.wireOp",EDGE,"E147");var subQ6=makeQuery(id+"F14.opExtrude","SWEPT_FACE",FACE,{"disambiguationData":[OSD([subQ5])]});Q538=makeQuery(id+"FyYUAefgu6xEfva_4.15.F14.boolean.opBoolean","SPLIT",EDGE,{"disambiguationData":[TD([subQ4])],"derivedFrom":makeQuery(id+"FyYUAefgu6xEfva_4.14.F14.boolean.opBoolean","SPLIT",EDGE,{"disambiguationData":[TD([subQ6])],"derivedFrom":makeQuery(id+"FyYUAefgu6xEfva_4.13.F14.boolean.opBoolean","SPLIT",EDGE,{"disambiguationData":[TD([subQ6])],"derivedFrom":makeQuery(id+"FyYUAefgu6xEfva_4.12.F14.boolean.opBoolean","SPLIT",EDGE,{"disambiguationData":[TD([subQ6])],"derivedFrom":makeQuery(id+"FyYUAefgu6xEfva_4.11.F14.boolean.opBoolean","SPLIT",EDGE,{"disambiguationData":[TD([subQ6])],"derivedFrom":makeQuery(id+"FyYUAefgu6xEfva_4.10.F14.boolean.opBoolean","SPLIT",EDGE,{"disambiguationData":[TD([subQ6])],"derivedFrom":makeQuery(id+"FyYUAefgu6xEfva_4.9.F14.boolean.opBoolean","SPLIT",EDGE,{"disambiguationData":[TD([subQ6])],"derivedFrom":makeQuery(id+"FyYUAefgu6xEfva_4.8.F14.boolean.opBoolean","SPLIT",EDGE,{"disambiguationData":[TD([subQ6])],"derivedFrom":makeQuery(id+"FyYUAefgu6xEfva_4.7.F14.boolean.opBoolean","SPLIT",EDGE,{"disambiguationData":[TD([subQ6])],"derivedFrom":makeQuery(id+"FyYUAefgu6xEfva_4.6.F14.boolean.opBoolean","SPLIT",EDGE,{"disambiguationData":[TD([subQ6])],"derivedFrom":makeQuery(id+"FyYUAefgu6xEfva_4.5.F14.boolean.opBoolean","SPLIT",EDGE,{"disambiguationData":[TD([subQ6])],"derivedFrom":makeQuery(id+"FyYUAefgu6xEfva_4.4.F14.boolean.opBoolean","SPLIT",EDGE,{"disambiguationData":[TD([subQ6])],"derivedFrom":makeQuery(id+"FyYUAefgu6xEfva_4.3.F14.boolean.opBoolean","SPLIT",EDGE,{"disambiguationData":[TD([subQ6])],"derivedFrom":makeQuery(id+"FyYUAefgu6xEfva_4.2.F14.boolean.opBoolean","SPLIT",EDGE,{"disambiguationData":[TD([subQ6])],"derivedFrom":makeQuery(id+"FyYUAefgu6xEfva_4.1.F14.boolean.opBoolean","SPLIT",EDGE,{"disambiguationData":[TD([subQ6])],"derivedFrom":makeQuery(id+"F12.opExtrude","CAP_EDGE",EDGE,{"disambiguationData":[OSD([subQ1])],"isStart":true})})})})})})})})})})})})})})})});}
            var Q539;
            Q539=makeQuery(id+"FyYUAefgu6xEfva_4.47.F14.opExtrude","CAP_EDGE",EDGE,{"disambiguationData":[OSD([sQuery(id+"F9.wireOp",EDGE,"E142")])],"isStart":false});
            var Q540;
            {var subQ1=sQuery(id+"F13.wireOp",EDGE,"E147");var subQ2=sQuery(id+"F11.wireOp",EDGE,"E143");var subQ4=sQuery(id+"F13.wireOp",EDGE,"E148.MirrorCS");var subQ5=makeQuery(id+"FyYUAefgu6xEfva_4.46.F14.opExtrude","SWEPT_FACE",FACE,{"disambiguationData":[OSD([subQ4])]});var subQ6=makeQuery(id+"F14.opExtrude","SWEPT_FACE",FACE,{"disambiguationData":[OSD([subQ1])]});Q540=makeQuery(id+"FyYUAefgu6xEfva_4.47.F14.boolean.opBoolean","SPLIT",EDGE,{"disambiguationData":[TD([subQ5])],"derivedFrom":makeQuery(id+"FyYUAefgu6xEfva_4.46.F14.boolean.opBoolean","SPLIT",EDGE,{"disambiguationData":[TD([subQ6])],"derivedFrom":makeQuery(id+"FyYUAefgu6xEfva_4.45.F14.boolean.opBoolean","SPLIT",EDGE,{"disambiguationData":[TD([subQ6])],"derivedFrom":makeQuery(id+"FyYUAefgu6xEfva_4.44.F14.boolean.opBoolean","SPLIT",EDGE,{"disambiguationData":[TD([subQ6])],"derivedFrom":makeQuery(id+"FyYUAefgu6xEfva_4.43.F14.boolean.opBoolean","SPLIT",EDGE,{"disambiguationData":[TD([subQ6])],"derivedFrom":makeQuery(id+"FyYUAefgu6xEfva_4.42.F14.boolean.opBoolean","SPLIT",EDGE,{"disambiguationData":[TD([subQ6])],"derivedFrom":makeQuery(id+"FyYUAefgu6xEfva_4.41.F14.boolean.opBoolean","SPLIT",EDGE,{"disambiguationData":[TD([subQ6])],"derivedFrom":makeQuery(id+"FyYUAefgu6xEfva_4.40.F14.boolean.opBoolean","SPLIT",EDGE,{"disambiguationData":[TD([subQ6])],"derivedFrom":makeQuery(id+"FyYUAefgu6xEfva_4.39.F14.boolean.opBoolean","SPLIT",EDGE,{"disambiguationData":[TD([subQ6])],"derivedFrom":makeQuery(id+"FyYUAefgu6xEfva_4.38.F14.boolean.opBoolean","SPLIT",EDGE,{"disambiguationData":[TD([subQ6])],"derivedFrom":makeQuery(id+"FyYUAefgu6xEfva_4.37.F14.boolean.opBoolean","SPLIT",EDGE,{"disambiguationData":[TD([subQ6])],"derivedFrom":makeQuery(id+"FyYUAefgu6xEfva_4.36.F14.boolean.opBoolean","SPLIT",EDGE,{"disambiguationData":[TD([subQ6])],"derivedFrom":makeQuery(id+"FyYUAefgu6xEfva_4.35.F14.boolean.opBoolean","SPLIT",EDGE,{"disambiguationData":[TD([subQ6])],"derivedFrom":makeQuery(id+"FyYUAefgu6xEfva_4.34.F14.boolean.opBoolean","SPLIT",EDGE,{"disambiguationData":[TD([subQ6])],"derivedFrom":makeQuery(id+"FyYUAefgu6xEfva_4.33.F14.boolean.opBoolean","SPLIT",EDGE,{"disambiguationData":[TD([subQ6])],"derivedFrom":makeQuery(id+"FyYUAefgu6xEfva_4.32.F14.boolean.opBoolean","SPLIT",EDGE,{"disambiguationData":[TD([subQ6])],"derivedFrom":makeQuery(id+"FyYUAefgu6xEfva_4.31.F14.boolean.opBoolean","SPLIT",EDGE,{"disambiguationData":[TD([subQ6])],"derivedFrom":makeQuery(id+"FyYUAefgu6xEfva_4.30.F14.boolean.opBoolean","SPLIT",EDGE,{"disambiguationData":[TD([subQ6])],"derivedFrom":makeQuery(id+"FyYUAefgu6xEfva_4.29.F14.boolean.opBoolean","SPLIT",EDGE,{"disambiguationData":[TD([subQ6])],"derivedFrom":makeQuery(id+"FyYUAefgu6xEfva_4.28.F14.boolean.opBoolean","SPLIT",EDGE,{"disambiguationData":[TD([subQ6])],"derivedFrom":makeQuery(id+"FyYUAefgu6xEfva_4.27.F14.boolean.opBoolean","SPLIT",EDGE,{"disambiguationData":[TD([subQ6])],"derivedFrom":makeQuery(id+"FyYUAefgu6xEfva_4.26.F14.boolean.opBoolean","SPLIT",EDGE,{"disambiguationData":[TD([subQ6])],"derivedFrom":makeQuery(id+"FyYUAefgu6xEfva_4.25.F14.boolean.opBoolean","SPLIT",EDGE,{"disambiguationData":[TD([subQ6])],"derivedFrom":makeQuery(id+"FyYUAefgu6xEfva_4.24.F14.boolean.opBoolean","SPLIT",EDGE,{"disambiguationData":[TD([subQ6])],"derivedFrom":makeQuery(id+"FyYUAefgu6xEfva_4.23.F14.boolean.opBoolean","SPLIT",EDGE,{"disambiguationData":[TD([subQ6])],"derivedFrom":makeQuery(id+"FyYUAefgu6xEfva_4.22.F14.boolean.opBoolean","SPLIT",EDGE,{"disambiguationData":[TD([subQ6])],"derivedFrom":makeQuery(id+"FyYUAefgu6xEfva_4.21.F14.boolean.opBoolean","SPLIT",EDGE,{"disambiguationData":[TD([subQ6])],"derivedFrom":makeQuery(id+"FyYUAefgu6xEfva_4.20.F14.boolean.opBoolean","SPLIT",EDGE,{"disambiguationData":[TD([subQ6])],"derivedFrom":makeQuery(id+"FyYUAefgu6xEfva_4.19.F14.boolean.opBoolean","SPLIT",EDGE,{"disambiguationData":[TD([subQ6])],"derivedFrom":makeQuery(id+"FyYUAefgu6xEfva_4.18.F14.boolean.opBoolean","SPLIT",EDGE,{"disambiguationData":[TD([subQ6])],"derivedFrom":makeQuery(id+"FyYUAefgu6xEfva_4.17.F14.boolean.opBoolean","SPLIT",EDGE,{"disambiguationData":[TD([subQ6])],"derivedFrom":makeQuery(id+"FyYUAefgu6xEfva_4.16.F14.boolean.opBoolean","SPLIT",EDGE,{"disambiguationData":[TD([subQ6])],"derivedFrom":makeQuery(id+"FyYUAefgu6xEfva_4.15.F14.boolean.opBoolean","SPLIT",EDGE,{"disambiguationData":[TD([subQ6])],"derivedFrom":makeQuery(id+"FyYUAefgu6xEfva_4.14.F14.boolean.opBoolean","SPLIT",EDGE,{"disambiguationData":[TD([subQ6])],"derivedFrom":makeQuery(id+"FyYUAefgu6xEfva_4.13.F14.boolean.opBoolean","SPLIT",EDGE,{"disambiguationData":[TD([subQ6])],"derivedFrom":makeQuery(id+"FyYUAefgu6xEfva_4.12.F14.boolean.opBoolean","SPLIT",EDGE,{"disambiguationData":[TD([subQ6])],"derivedFrom":makeQuery(id+"FyYUAefgu6xEfva_4.11.F14.boolean.opBoolean","SPLIT",EDGE,{"disambiguationData":[TD([subQ6])],"derivedFrom":makeQuery(id+"FyYUAefgu6xEfva_4.10.F14.boolean.opBoolean","SPLIT",EDGE,{"disambiguationData":[TD([subQ6])],"derivedFrom":makeQuery(id+"FyYUAefgu6xEfva_4.9.F14.boolean.opBoolean","SPLIT",EDGE,{"disambiguationData":[TD([subQ6])],"derivedFrom":makeQuery(id+"FyYUAefgu6xEfva_4.8.F14.boolean.opBoolean","SPLIT",EDGE,{"disambiguationData":[TD([subQ6])],"derivedFrom":makeQuery(id+"FyYUAefgu6xEfva_4.7.F14.boolean.opBoolean","SPLIT",EDGE,{"disambiguationData":[TD([subQ6])],"derivedFrom":makeQuery(id+"FyYUAefgu6xEfva_4.6.F14.boolean.opBoolean","SPLIT",EDGE,{"disambiguationData":[TD([subQ6])],"derivedFrom":makeQuery(id+"FyYUAefgu6xEfva_4.5.F14.boolean.opBoolean","SPLIT",EDGE,{"disambiguationData":[TD([subQ6])],"derivedFrom":makeQuery(id+"FyYUAefgu6xEfva_4.4.F14.boolean.opBoolean","SPLIT",EDGE,{"disambiguationData":[TD([subQ6])],"derivedFrom":makeQuery(id+"FyYUAefgu6xEfva_4.3.F14.boolean.opBoolean","SPLIT",EDGE,{"disambiguationData":[TD([subQ6])],"derivedFrom":makeQuery(id+"FyYUAefgu6xEfva_4.2.F14.boolean.opBoolean","SPLIT",EDGE,{"disambiguationData":[TD([subQ6])],"derivedFrom":makeQuery(id+"FyYUAefgu6xEfva_4.1.F14.boolean.opBoolean","SPLIT",EDGE,{"disambiguationData":[TD([subQ6])],"derivedFrom":makeQuery(id+"F12.opExtrude","CAP_EDGE",EDGE,{"disambiguationData":[OSD([subQ2])],"isStart":true})})})})})})})})})})})})})})})})})})})})})})})})})})})})})})})})})})})})})})})})})})})})})})})});}
            var Q541;
            Q541=makeQuery(id+"FyYUAefgu6xEfva_4.16.F14.opExtrude","CAP_EDGE",EDGE,{"disambiguationData":[OSD([sQuery(id+"F13.wireOp",EDGE,"E147")])],"isStart":true});
            var Q542;
            {var subQ1=sQuery(id+"F11.wireOp",EDGE,"E143");var subQ3=sQuery(id+"F13.wireOp",EDGE,"E148.MirrorCS");var subQ4=makeQuery(id+"FyYUAefgu6xEfva_4.15.F14.opExtrude","SWEPT_FACE",FACE,{"disambiguationData":[OSD([subQ3])]});var subQ5=sQuery(id+"F13.wireOp",EDGE,"E147");var subQ6=makeQuery(id+"F14.opExtrude","SWEPT_FACE",FACE,{"disambiguationData":[OSD([subQ5])]});Q542=makeQuery(id+"FyYUAefgu6xEfva_4.16.F14.boolean.opBoolean","SPLIT",EDGE,{"disambiguationData":[TD([subQ4])],"derivedFrom":makeQuery(id+"FyYUAefgu6xEfva_4.15.F14.boolean.opBoolean","SPLIT",EDGE,{"disambiguationData":[TD([subQ6])],"derivedFrom":makeQuery(id+"FyYUAefgu6xEfva_4.14.F14.boolean.opBoolean","SPLIT",EDGE,{"disambiguationData":[TD([subQ6])],"derivedFrom":makeQuery(id+"FyYUAefgu6xEfva_4.13.F14.boolean.opBoolean","SPLIT",EDGE,{"disambiguationData":[TD([subQ6])],"derivedFrom":makeQuery(id+"FyYUAefgu6xEfva_4.12.F14.boolean.opBoolean","SPLIT",EDGE,{"disambiguationData":[TD([subQ6])],"derivedFrom":makeQuery(id+"FyYUAefgu6xEfva_4.11.F14.boolean.opBoolean","SPLIT",EDGE,{"disambiguationData":[TD([subQ6])],"derivedFrom":makeQuery(id+"FyYUAefgu6xEfva_4.10.F14.boolean.opBoolean","SPLIT",EDGE,{"disambiguationData":[TD([subQ6])],"derivedFrom":makeQuery(id+"FyYUAefgu6xEfva_4.9.F14.boolean.opBoolean","SPLIT",EDGE,{"disambiguationData":[TD([subQ6])],"derivedFrom":makeQuery(id+"FyYUAefgu6xEfva_4.8.F14.boolean.opBoolean","SPLIT",EDGE,{"disambiguationData":[TD([subQ6])],"derivedFrom":makeQuery(id+"FyYUAefgu6xEfva_4.7.F14.boolean.opBoolean","SPLIT",EDGE,{"disambiguationData":[TD([subQ6])],"derivedFrom":makeQuery(id+"FyYUAefgu6xEfva_4.6.F14.boolean.opBoolean","SPLIT",EDGE,{"disambiguationData":[TD([subQ6])],"derivedFrom":makeQuery(id+"FyYUAefgu6xEfva_4.5.F14.boolean.opBoolean","SPLIT",EDGE,{"disambiguationData":[TD([subQ6])],"derivedFrom":makeQuery(id+"FyYUAefgu6xEfva_4.4.F14.boolean.opBoolean","SPLIT",EDGE,{"disambiguationData":[TD([subQ6])],"derivedFrom":makeQuery(id+"FyYUAefgu6xEfva_4.3.F14.boolean.opBoolean","SPLIT",EDGE,{"disambiguationData":[TD([subQ6])],"derivedFrom":makeQuery(id+"FyYUAefgu6xEfva_4.2.F14.boolean.opBoolean","SPLIT",EDGE,{"disambiguationData":[TD([subQ6])],"derivedFrom":makeQuery(id+"FyYUAefgu6xEfva_4.1.F14.boolean.opBoolean","SPLIT",EDGE,{"disambiguationData":[TD([subQ6])],"derivedFrom":makeQuery(id+"F12.opExtrude","CAP_EDGE",EDGE,{"disambiguationData":[OSD([subQ1])],"isStart":true})})})})})})})})})})})})})})})})});}
            var Q543;
            {var subQ1=sQuery(id+"F11.wireOp",EDGE,"E143");var subQ3=sQuery(id+"F13.wireOp",EDGE,"E147");var subQ4=sQuery(id+"F13.wireOp",EDGE,"E148.MirrorCS");var subQ5=makeQuery(id+"FyYUAefgu6xEfva_4.47.F14.opExtrude","SWEPT_FACE",FACE,{"disambiguationData":[OSD([subQ4])]});var subQ6=makeQuery(id+"F14.opExtrude","SWEPT_FACE",FACE,{"disambiguationData":[OSD([subQ3])]});Q543=makeQuery(id+"FyYUAefgu6xEfva_4.48.F14.boolean.opBoolean","SPLIT",EDGE,{"disambiguationData":[TD([subQ5])],"derivedFrom":makeQuery(id+"FyYUAefgu6xEfva_4.47.F14.boolean.opBoolean","SPLIT",EDGE,{"disambiguationData":[TD([subQ6])],"derivedFrom":makeQuery(id+"FyYUAefgu6xEfva_4.46.F14.boolean.opBoolean","SPLIT",EDGE,{"disambiguationData":[TD([subQ6])],"derivedFrom":makeQuery(id+"FyYUAefgu6xEfva_4.45.F14.boolean.opBoolean","SPLIT",EDGE,{"disambiguationData":[TD([subQ6])],"derivedFrom":makeQuery(id+"FyYUAefgu6xEfva_4.44.F14.boolean.opBoolean","SPLIT",EDGE,{"disambiguationData":[TD([subQ6])],"derivedFrom":makeQuery(id+"FyYUAefgu6xEfva_4.43.F14.boolean.opBoolean","SPLIT",EDGE,{"disambiguationData":[TD([subQ6])],"derivedFrom":makeQuery(id+"FyYUAefgu6xEfva_4.42.F14.boolean.opBoolean","SPLIT",EDGE,{"disambiguationData":[TD([subQ6])],"derivedFrom":makeQuery(id+"FyYUAefgu6xEfva_4.41.F14.boolean.opBoolean","SPLIT",EDGE,{"disambiguationData":[TD([subQ6])],"derivedFrom":makeQuery(id+"FyYUAefgu6xEfva_4.40.F14.boolean.opBoolean","SPLIT",EDGE,{"disambiguationData":[TD([subQ6])],"derivedFrom":makeQuery(id+"FyYUAefgu6xEfva_4.39.F14.boolean.opBoolean","SPLIT",EDGE,{"disambiguationData":[TD([subQ6])],"derivedFrom":makeQuery(id+"FyYUAefgu6xEfva_4.38.F14.boolean.opBoolean","SPLIT",EDGE,{"disambiguationData":[TD([subQ6])],"derivedFrom":makeQuery(id+"FyYUAefgu6xEfva_4.37.F14.boolean.opBoolean","SPLIT",EDGE,{"disambiguationData":[TD([subQ6])],"derivedFrom":makeQuery(id+"FyYUAefgu6xEfva_4.36.F14.boolean.opBoolean","SPLIT",EDGE,{"disambiguationData":[TD([subQ6])],"derivedFrom":makeQuery(id+"FyYUAefgu6xEfva_4.35.F14.boolean.opBoolean","SPLIT",EDGE,{"disambiguationData":[TD([subQ6])],"derivedFrom":makeQuery(id+"FyYUAefgu6xEfva_4.34.F14.boolean.opBoolean","SPLIT",EDGE,{"disambiguationData":[TD([subQ6])],"derivedFrom":makeQuery(id+"FyYUAefgu6xEfva_4.33.F14.boolean.opBoolean","SPLIT",EDGE,{"disambiguationData":[TD([subQ6])],"derivedFrom":makeQuery(id+"FyYUAefgu6xEfva_4.32.F14.boolean.opBoolean","SPLIT",EDGE,{"disambiguationData":[TD([subQ6])],"derivedFrom":makeQuery(id+"FyYUAefgu6xEfva_4.31.F14.boolean.opBoolean","SPLIT",EDGE,{"disambiguationData":[TD([subQ6])],"derivedFrom":makeQuery(id+"FyYUAefgu6xEfva_4.30.F14.boolean.opBoolean","SPLIT",EDGE,{"disambiguationData":[TD([subQ6])],"derivedFrom":makeQuery(id+"FyYUAefgu6xEfva_4.29.F14.boolean.opBoolean","SPLIT",EDGE,{"disambiguationData":[TD([subQ6])],"derivedFrom":makeQuery(id+"FyYUAefgu6xEfva_4.28.F14.boolean.opBoolean","SPLIT",EDGE,{"disambiguationData":[TD([subQ6])],"derivedFrom":makeQuery(id+"FyYUAefgu6xEfva_4.27.F14.boolean.opBoolean","SPLIT",EDGE,{"disambiguationData":[TD([subQ6])],"derivedFrom":makeQuery(id+"FyYUAefgu6xEfva_4.26.F14.boolean.opBoolean","SPLIT",EDGE,{"disambiguationData":[TD([subQ6])],"derivedFrom":makeQuery(id+"FyYUAefgu6xEfva_4.25.F14.boolean.opBoolean","SPLIT",EDGE,{"disambiguationData":[TD([subQ6])],"derivedFrom":makeQuery(id+"FyYUAefgu6xEfva_4.24.F14.boolean.opBoolean","SPLIT",EDGE,{"disambiguationData":[TD([subQ6])],"derivedFrom":makeQuery(id+"FyYUAefgu6xEfva_4.23.F14.boolean.opBoolean","SPLIT",EDGE,{"disambiguationData":[TD([subQ6])],"derivedFrom":makeQuery(id+"FyYUAefgu6xEfva_4.22.F14.boolean.opBoolean","SPLIT",EDGE,{"disambiguationData":[TD([subQ6])],"derivedFrom":makeQuery(id+"FyYUAefgu6xEfva_4.21.F14.boolean.opBoolean","SPLIT",EDGE,{"disambiguationData":[TD([subQ6])],"derivedFrom":makeQuery(id+"FyYUAefgu6xEfva_4.20.F14.boolean.opBoolean","SPLIT",EDGE,{"disambiguationData":[TD([subQ6])],"derivedFrom":makeQuery(id+"FyYUAefgu6xEfva_4.19.F14.boolean.opBoolean","SPLIT",EDGE,{"disambiguationData":[TD([subQ6])],"derivedFrom":makeQuery(id+"FyYUAefgu6xEfva_4.18.F14.boolean.opBoolean","SPLIT",EDGE,{"disambiguationData":[TD([subQ6])],"derivedFrom":makeQuery(id+"FyYUAefgu6xEfva_4.17.F14.boolean.opBoolean","SPLIT",EDGE,{"disambiguationData":[TD([subQ6])],"derivedFrom":makeQuery(id+"FyYUAefgu6xEfva_4.16.F14.boolean.opBoolean","SPLIT",EDGE,{"disambiguationData":[TD([subQ6])],"derivedFrom":makeQuery(id+"FyYUAefgu6xEfva_4.15.F14.boolean.opBoolean","SPLIT",EDGE,{"disambiguationData":[TD([subQ6])],"derivedFrom":makeQuery(id+"FyYUAefgu6xEfva_4.14.F14.boolean.opBoolean","SPLIT",EDGE,{"disambiguationData":[TD([subQ6])],"derivedFrom":makeQuery(id+"FyYUAefgu6xEfva_4.13.F14.boolean.opBoolean","SPLIT",EDGE,{"disambiguationData":[TD([subQ6])],"derivedFrom":makeQuery(id+"FyYUAefgu6xEfva_4.12.F14.boolean.opBoolean","SPLIT",EDGE,{"disambiguationData":[TD([subQ6])],"derivedFrom":makeQuery(id+"FyYUAefgu6xEfva_4.11.F14.boolean.opBoolean","SPLIT",EDGE,{"disambiguationData":[TD([subQ6])],"derivedFrom":makeQuery(id+"FyYUAefgu6xEfva_4.10.F14.boolean.opBoolean","SPLIT",EDGE,{"disambiguationData":[TD([subQ6])],"derivedFrom":makeQuery(id+"FyYUAefgu6xEfva_4.9.F14.boolean.opBoolean","SPLIT",EDGE,{"disambiguationData":[TD([subQ6])],"derivedFrom":makeQuery(id+"FyYUAefgu6xEfva_4.8.F14.boolean.opBoolean","SPLIT",EDGE,{"disambiguationData":[TD([subQ6])],"derivedFrom":makeQuery(id+"FyYUAefgu6xEfva_4.7.F14.boolean.opBoolean","SPLIT",EDGE,{"disambiguationData":[TD([subQ6])],"derivedFrom":makeQuery(id+"FyYUAefgu6xEfva_4.6.F14.boolean.opBoolean","SPLIT",EDGE,{"disambiguationData":[TD([subQ6])],"derivedFrom":makeQuery(id+"FyYUAefgu6xEfva_4.5.F14.boolean.opBoolean","SPLIT",EDGE,{"disambiguationData":[TD([subQ6])],"derivedFrom":makeQuery(id+"FyYUAefgu6xEfva_4.4.F14.boolean.opBoolean","SPLIT",EDGE,{"disambiguationData":[TD([subQ6])],"derivedFrom":makeQuery(id+"FyYUAefgu6xEfva_4.3.F14.boolean.opBoolean","SPLIT",EDGE,{"disambiguationData":[TD([subQ6])],"derivedFrom":makeQuery(id+"FyYUAefgu6xEfva_4.2.F14.boolean.opBoolean","SPLIT",EDGE,{"disambiguationData":[TD([subQ6])],"derivedFrom":makeQuery(id+"FyYUAefgu6xEfva_4.1.F14.boolean.opBoolean","SPLIT",EDGE,{"disambiguationData":[TD([subQ6])],"derivedFrom":makeQuery(id+"F12.opExtrude","CAP_EDGE",EDGE,{"disambiguationData":[OSD([subQ1])],"isStart":true})})})})})})})})})})})})})})})})})})})})})})})})})})})})})})})})})})})})})})})})})})})})})})})})});}
            var Q544;
            Q544=makeQuery(id+"FyYUAefgu6xEfva_4.17.F14.opExtrude","SWEPT_EDGE",EDGE,{"disambiguationData":[OSD([sQuery(id+"F11.wireOp",EDGE,"E143"),sQuery(id+"F13.wireOp",EDGE,"E147")])]});
            var Q545;
            Q545=makeQuery(id+"FyYUAefgu6xEfva_4.17.F14.opExtrude","CAP_EDGE",EDGE,{"disambiguationData":[OSD([sQuery(id+"F13.wireOp",EDGE,"E147")])],"isStart":true});
            var Q546;
            {var subQ0=sQuery(id+"F9.wireOp",EDGE,"E142");var subQ3=sQuery(id+"F13.wireOp",EDGE,"E147");var subQ4=sQuery(id+"F13.wireOp",EDGE,"E148.MirrorCS");var subQ5=makeQuery(id+"FyYUAefgu6xEfva_4.16.F14.opExtrude","SWEPT_FACE",FACE,{"disambiguationData":[OSD([subQ4])]});var subQ6=makeQuery(id+"F14.opExtrude","SWEPT_FACE",FACE,{"disambiguationData":[OSD([subQ3])]});Q546=makeQuery(id+"FyYUAefgu6xEfva_4.17.F14.boolean.opBoolean","SPLIT",EDGE,{"disambiguationData":[TD([subQ5])],"derivedFrom":makeQuery(id+"FyYUAefgu6xEfva_4.16.F14.boolean.opBoolean","SPLIT",EDGE,{"disambiguationData":[TD([subQ6])],"derivedFrom":makeQuery(id+"FyYUAefgu6xEfva_4.15.F14.boolean.opBoolean","SPLIT",EDGE,{"disambiguationData":[TD([subQ6])],"derivedFrom":makeQuery(id+"FyYUAefgu6xEfva_4.14.F14.boolean.opBoolean","SPLIT",EDGE,{"disambiguationData":[TD([subQ6])],"derivedFrom":makeQuery(id+"FyYUAefgu6xEfva_4.13.F14.boolean.opBoolean","SPLIT",EDGE,{"disambiguationData":[TD([subQ6])],"derivedFrom":makeQuery(id+"FyYUAefgu6xEfva_4.12.F14.boolean.opBoolean","SPLIT",EDGE,{"disambiguationData":[TD([subQ6])],"derivedFrom":makeQuery(id+"FyYUAefgu6xEfva_4.11.F14.boolean.opBoolean","SPLIT",EDGE,{"disambiguationData":[TD([subQ6])],"derivedFrom":makeQuery(id+"FyYUAefgu6xEfva_4.10.F14.boolean.opBoolean","SPLIT",EDGE,{"disambiguationData":[TD([subQ6])],"derivedFrom":makeQuery(id+"FyYUAefgu6xEfva_4.9.F14.boolean.opBoolean","SPLIT",EDGE,{"disambiguationData":[TD([subQ6])],"derivedFrom":makeQuery(id+"FyYUAefgu6xEfva_4.8.F14.boolean.opBoolean","SPLIT",EDGE,{"disambiguationData":[TD([subQ6])],"derivedFrom":makeQuery(id+"FyYUAefgu6xEfva_4.7.F14.boolean.opBoolean","SPLIT",EDGE,{"disambiguationData":[TD([subQ6])],"derivedFrom":makeQuery(id+"FyYUAefgu6xEfva_4.6.F14.boolean.opBoolean","SPLIT",EDGE,{"disambiguationData":[TD([subQ6])],"derivedFrom":makeQuery(id+"FyYUAefgu6xEfva_4.5.F14.boolean.opBoolean","SPLIT",EDGE,{"disambiguationData":[TD([subQ6])],"derivedFrom":makeQuery(id+"FyYUAefgu6xEfva_4.4.F14.boolean.opBoolean","SPLIT",EDGE,{"disambiguationData":[TD([subQ6])],"derivedFrom":makeQuery(id+"FyYUAefgu6xEfva_4.3.F14.boolean.opBoolean","SPLIT",EDGE,{"disambiguationData":[TD([subQ6])],"derivedFrom":makeQuery(id+"FyYUAefgu6xEfva_4.2.F14.boolean.opBoolean","SPLIT",EDGE,{"disambiguationData":[TD([subQ6])],"derivedFrom":makeQuery(id+"FyYUAefgu6xEfva_4.1.F14.boolean.opBoolean","SPLIT",EDGE,{"disambiguationData":[TD([subQ6])],"derivedFrom":makeQuery(id+"F10.boolean.opBoolean","COPY",EDGE,{"derivedFrom":makeQuery(id+"F10.opExtrude","CAP_EDGE",EDGE,{"disambiguationData":[OSD([subQ0])],"isStart":false})})})})})})})})})})})})})})})})})})});}
            var Q547;
            {var subQ1=sQuery(id+"F13.wireOp",EDGE,"E147");var subQ2=sQuery(id+"F11.wireOp",EDGE,"E143");var subQ4=sQuery(id+"F13.wireOp",EDGE,"E148.MirrorCS");var subQ5=makeQuery(id+"FyYUAefgu6xEfva_4.16.F14.opExtrude","SWEPT_FACE",FACE,{"disambiguationData":[OSD([subQ4])]});var subQ6=makeQuery(id+"F14.opExtrude","SWEPT_FACE",FACE,{"disambiguationData":[OSD([subQ1])]});Q547=makeQuery(id+"FyYUAefgu6xEfva_4.17.F14.boolean.opBoolean","SPLIT",EDGE,{"disambiguationData":[TD([subQ5])],"derivedFrom":makeQuery(id+"FyYUAefgu6xEfva_4.16.F14.boolean.opBoolean","SPLIT",EDGE,{"disambiguationData":[TD([subQ6])],"derivedFrom":makeQuery(id+"FyYUAefgu6xEfva_4.15.F14.boolean.opBoolean","SPLIT",EDGE,{"disambiguationData":[TD([subQ6])],"derivedFrom":makeQuery(id+"FyYUAefgu6xEfva_4.14.F14.boolean.opBoolean","SPLIT",EDGE,{"disambiguationData":[TD([subQ6])],"derivedFrom":makeQuery(id+"FyYUAefgu6xEfva_4.13.F14.boolean.opBoolean","SPLIT",EDGE,{"disambiguationData":[TD([subQ6])],"derivedFrom":makeQuery(id+"FyYUAefgu6xEfva_4.12.F14.boolean.opBoolean","SPLIT",EDGE,{"disambiguationData":[TD([subQ6])],"derivedFrom":makeQuery(id+"FyYUAefgu6xEfva_4.11.F14.boolean.opBoolean","SPLIT",EDGE,{"disambiguationData":[TD([subQ6])],"derivedFrom":makeQuery(id+"FyYUAefgu6xEfva_4.10.F14.boolean.opBoolean","SPLIT",EDGE,{"disambiguationData":[TD([subQ6])],"derivedFrom":makeQuery(id+"FyYUAefgu6xEfva_4.9.F14.boolean.opBoolean","SPLIT",EDGE,{"disambiguationData":[TD([subQ6])],"derivedFrom":makeQuery(id+"FyYUAefgu6xEfva_4.8.F14.boolean.opBoolean","SPLIT",EDGE,{"disambiguationData":[TD([subQ6])],"derivedFrom":makeQuery(id+"FyYUAefgu6xEfva_4.7.F14.boolean.opBoolean","SPLIT",EDGE,{"disambiguationData":[TD([subQ6])],"derivedFrom":makeQuery(id+"FyYUAefgu6xEfva_4.6.F14.boolean.opBoolean","SPLIT",EDGE,{"disambiguationData":[TD([subQ6])],"derivedFrom":makeQuery(id+"FyYUAefgu6xEfva_4.5.F14.boolean.opBoolean","SPLIT",EDGE,{"disambiguationData":[TD([subQ6])],"derivedFrom":makeQuery(id+"FyYUAefgu6xEfva_4.4.F14.boolean.opBoolean","SPLIT",EDGE,{"disambiguationData":[TD([subQ6])],"derivedFrom":makeQuery(id+"FyYUAefgu6xEfva_4.3.F14.boolean.opBoolean","SPLIT",EDGE,{"disambiguationData":[TD([subQ6])],"derivedFrom":makeQuery(id+"FyYUAefgu6xEfva_4.2.F14.boolean.opBoolean","SPLIT",EDGE,{"disambiguationData":[TD([subQ6])],"derivedFrom":makeQuery(id+"FyYUAefgu6xEfva_4.1.F14.boolean.opBoolean","SPLIT",EDGE,{"disambiguationData":[TD([subQ6])],"derivedFrom":makeQuery(id+"F12.opExtrude","CAP_EDGE",EDGE,{"disambiguationData":[OSD([subQ2])],"isStart":true})})})})})})})})})})})})})})})})})});}
            var Q548;
            Q548=makeQuery(id+"FyYUAefgu6xEfva_4.49.F14.opExtrude","CAP_EDGE",EDGE,{"disambiguationData":[OSD([sQuery(id+"F9.wireOp",EDGE,"E142")])],"isStart":false});
            var Q549;
            {var subQ1=sQuery(id+"F13.wireOp",EDGE,"E148.MirrorCS");var subQ2=makeQuery(id+"FyYUAefgu6xEfva_4.48.F14.opExtrude","SWEPT_FACE",FACE,{"disambiguationData":[OSD([subQ1])]});var subQ3=sQuery(id+"F11.wireOp",EDGE,"E143");var subQ5=sQuery(id+"F13.wireOp",EDGE,"E147");var subQ6=makeQuery(id+"F14.opExtrude","SWEPT_FACE",FACE,{"disambiguationData":[OSD([subQ5])]});Q549=makeQuery(id+"FyYUAefgu6xEfva_4.49.F14.boolean.opBoolean","SPLIT",EDGE,{"disambiguationData":[TD([subQ2])],"derivedFrom":makeQuery(id+"FyYUAefgu6xEfva_4.48.F14.boolean.opBoolean","SPLIT",EDGE,{"disambiguationData":[TD([subQ6])],"derivedFrom":makeQuery(id+"FyYUAefgu6xEfva_4.47.F14.boolean.opBoolean","SPLIT",EDGE,{"disambiguationData":[TD([subQ6])],"derivedFrom":makeQuery(id+"FyYUAefgu6xEfva_4.46.F14.boolean.opBoolean","SPLIT",EDGE,{"disambiguationData":[TD([subQ6])],"derivedFrom":makeQuery(id+"FyYUAefgu6xEfva_4.45.F14.boolean.opBoolean","SPLIT",EDGE,{"disambiguationData":[TD([subQ6])],"derivedFrom":makeQuery(id+"FyYUAefgu6xEfva_4.44.F14.boolean.opBoolean","SPLIT",EDGE,{"disambiguationData":[TD([subQ6])],"derivedFrom":makeQuery(id+"FyYUAefgu6xEfva_4.43.F14.boolean.opBoolean","SPLIT",EDGE,{"disambiguationData":[TD([subQ6])],"derivedFrom":makeQuery(id+"FyYUAefgu6xEfva_4.42.F14.boolean.opBoolean","SPLIT",EDGE,{"disambiguationData":[TD([subQ6])],"derivedFrom":makeQuery(id+"FyYUAefgu6xEfva_4.41.F14.boolean.opBoolean","SPLIT",EDGE,{"disambiguationData":[TD([subQ6])],"derivedFrom":makeQuery(id+"FyYUAefgu6xEfva_4.40.F14.boolean.opBoolean","SPLIT",EDGE,{"disambiguationData":[TD([subQ6])],"derivedFrom":makeQuery(id+"FyYUAefgu6xEfva_4.39.F14.boolean.opBoolean","SPLIT",EDGE,{"disambiguationData":[TD([subQ6])],"derivedFrom":makeQuery(id+"FyYUAefgu6xEfva_4.38.F14.boolean.opBoolean","SPLIT",EDGE,{"disambiguationData":[TD([subQ6])],"derivedFrom":makeQuery(id+"FyYUAefgu6xEfva_4.37.F14.boolean.opBoolean","SPLIT",EDGE,{"disambiguationData":[TD([subQ6])],"derivedFrom":makeQuery(id+"FyYUAefgu6xEfva_4.36.F14.boolean.opBoolean","SPLIT",EDGE,{"disambiguationData":[TD([subQ6])],"derivedFrom":makeQuery(id+"FyYUAefgu6xEfva_4.35.F14.boolean.opBoolean","SPLIT",EDGE,{"disambiguationData":[TD([subQ6])],"derivedFrom":makeQuery(id+"FyYUAefgu6xEfva_4.34.F14.boolean.opBoolean","SPLIT",EDGE,{"disambiguationData":[TD([subQ6])],"derivedFrom":makeQuery(id+"FyYUAefgu6xEfva_4.33.F14.boolean.opBoolean","SPLIT",EDGE,{"disambiguationData":[TD([subQ6])],"derivedFrom":makeQuery(id+"FyYUAefgu6xEfva_4.32.F14.boolean.opBoolean","SPLIT",EDGE,{"disambiguationData":[TD([subQ6])],"derivedFrom":makeQuery(id+"FyYUAefgu6xEfva_4.31.F14.boolean.opBoolean","SPLIT",EDGE,{"disambiguationData":[TD([subQ6])],"derivedFrom":makeQuery(id+"FyYUAefgu6xEfva_4.30.F14.boolean.opBoolean","SPLIT",EDGE,{"disambiguationData":[TD([subQ6])],"derivedFrom":makeQuery(id+"FyYUAefgu6xEfva_4.29.F14.boolean.opBoolean","SPLIT",EDGE,{"disambiguationData":[TD([subQ6])],"derivedFrom":makeQuery(id+"FyYUAefgu6xEfva_4.28.F14.boolean.opBoolean","SPLIT",EDGE,{"disambiguationData":[TD([subQ6])],"derivedFrom":makeQuery(id+"FyYUAefgu6xEfva_4.27.F14.boolean.opBoolean","SPLIT",EDGE,{"disambiguationData":[TD([subQ6])],"derivedFrom":makeQuery(id+"FyYUAefgu6xEfva_4.26.F14.boolean.opBoolean","SPLIT",EDGE,{"disambiguationData":[TD([subQ6])],"derivedFrom":makeQuery(id+"FyYUAefgu6xEfva_4.25.F14.boolean.opBoolean","SPLIT",EDGE,{"disambiguationData":[TD([subQ6])],"derivedFrom":makeQuery(id+"FyYUAefgu6xEfva_4.24.F14.boolean.opBoolean","SPLIT",EDGE,{"disambiguationData":[TD([subQ6])],"derivedFrom":makeQuery(id+"FyYUAefgu6xEfva_4.23.F14.boolean.opBoolean","SPLIT",EDGE,{"disambiguationData":[TD([subQ6])],"derivedFrom":makeQuery(id+"FyYUAefgu6xEfva_4.22.F14.boolean.opBoolean","SPLIT",EDGE,{"disambiguationData":[TD([subQ6])],"derivedFrom":makeQuery(id+"FyYUAefgu6xEfva_4.21.F14.boolean.opBoolean","SPLIT",EDGE,{"disambiguationData":[TD([subQ6])],"derivedFrom":makeQuery(id+"FyYUAefgu6xEfva_4.20.F14.boolean.opBoolean","SPLIT",EDGE,{"disambiguationData":[TD([subQ6])],"derivedFrom":makeQuery(id+"FyYUAefgu6xEfva_4.19.F14.boolean.opBoolean","SPLIT",EDGE,{"disambiguationData":[TD([subQ6])],"derivedFrom":makeQuery(id+"FyYUAefgu6xEfva_4.18.F14.boolean.opBoolean","SPLIT",EDGE,{"disambiguationData":[TD([subQ6])],"derivedFrom":makeQuery(id+"FyYUAefgu6xEfva_4.17.F14.boolean.opBoolean","SPLIT",EDGE,{"disambiguationData":[TD([subQ6])],"derivedFrom":makeQuery(id+"FyYUAefgu6xEfva_4.16.F14.boolean.opBoolean","SPLIT",EDGE,{"disambiguationData":[TD([subQ6])],"derivedFrom":makeQuery(id+"FyYUAefgu6xEfva_4.15.F14.boolean.opBoolean","SPLIT",EDGE,{"disambiguationData":[TD([subQ6])],"derivedFrom":makeQuery(id+"FyYUAefgu6xEfva_4.14.F14.boolean.opBoolean","SPLIT",EDGE,{"disambiguationData":[TD([subQ6])],"derivedFrom":makeQuery(id+"FyYUAefgu6xEfva_4.13.F14.boolean.opBoolean","SPLIT",EDGE,{"disambiguationData":[TD([subQ6])],"derivedFrom":makeQuery(id+"FyYUAefgu6xEfva_4.12.F14.boolean.opBoolean","SPLIT",EDGE,{"disambiguationData":[TD([subQ6])],"derivedFrom":makeQuery(id+"FyYUAefgu6xEfva_4.11.F14.boolean.opBoolean","SPLIT",EDGE,{"disambiguationData":[TD([subQ6])],"derivedFrom":makeQuery(id+"FyYUAefgu6xEfva_4.10.F14.boolean.opBoolean","SPLIT",EDGE,{"disambiguationData":[TD([subQ6])],"derivedFrom":makeQuery(id+"FyYUAefgu6xEfva_4.9.F14.boolean.opBoolean","SPLIT",EDGE,{"disambiguationData":[TD([subQ6])],"derivedFrom":makeQuery(id+"FyYUAefgu6xEfva_4.8.F14.boolean.opBoolean","SPLIT",EDGE,{"disambiguationData":[TD([subQ6])],"derivedFrom":makeQuery(id+"FyYUAefgu6xEfva_4.7.F14.boolean.opBoolean","SPLIT",EDGE,{"disambiguationData":[TD([subQ6])],"derivedFrom":makeQuery(id+"FyYUAefgu6xEfva_4.6.F14.boolean.opBoolean","SPLIT",EDGE,{"disambiguationData":[TD([subQ6])],"derivedFrom":makeQuery(id+"FyYUAefgu6xEfva_4.5.F14.boolean.opBoolean","SPLIT",EDGE,{"disambiguationData":[TD([subQ6])],"derivedFrom":makeQuery(id+"FyYUAefgu6xEfva_4.4.F14.boolean.opBoolean","SPLIT",EDGE,{"disambiguationData":[TD([subQ6])],"derivedFrom":makeQuery(id+"FyYUAefgu6xEfva_4.3.F14.boolean.opBoolean","SPLIT",EDGE,{"disambiguationData":[TD([subQ6])],"derivedFrom":makeQuery(id+"FyYUAefgu6xEfva_4.2.F14.boolean.opBoolean","SPLIT",EDGE,{"disambiguationData":[TD([subQ6])],"derivedFrom":makeQuery(id+"FyYUAefgu6xEfva_4.1.F14.boolean.opBoolean","SPLIT",EDGE,{"disambiguationData":[TD([subQ6])],"derivedFrom":makeQuery(id+"F12.opExtrude","CAP_EDGE",EDGE,{"disambiguationData":[OSD([subQ3])],"isStart":true})})})})})})})})})})})})})})})})})})})})})})})})})})})})})})})})})})})})})})})})})})})})})})})})})});}
            var Q550;
            Q550=makeQuery(id+"FyYUAefgu6xEfva_4.18.F14.opExtrude","CAP_EDGE",EDGE,{"disambiguationData":[OSD([sQuery(id+"F13.wireOp",EDGE,"E147")])],"isStart":true});
            var Q551;
            Q551=makeQuery(id+"FyYUAefgu6xEfva_4.18.F14.opExtrude","CAP_EDGE",EDGE,{"disambiguationData":[OSD([sQuery(id+"F13.wireOp",EDGE,"E148.MirrorCS")])],"isStart":true});
            var Q552;
            {var subQ0=sQuery(id+"F9.wireOp",EDGE,"E142");var subQ3=sQuery(id+"F13.wireOp",EDGE,"E148.MirrorCS");var subQ4=makeQuery(id+"FyYUAefgu6xEfva_4.17.F14.opExtrude","SWEPT_FACE",FACE,{"disambiguationData":[OSD([subQ3])]});var subQ5=sQuery(id+"F13.wireOp",EDGE,"E147");var subQ6=makeQuery(id+"F14.opExtrude","SWEPT_FACE",FACE,{"disambiguationData":[OSD([subQ5])]});Q552=makeQuery(id+"FyYUAefgu6xEfva_4.18.F14.boolean.opBoolean","SPLIT",EDGE,{"disambiguationData":[TD([subQ4])],"derivedFrom":makeQuery(id+"FyYUAefgu6xEfva_4.17.F14.boolean.opBoolean","SPLIT",EDGE,{"disambiguationData":[TD([subQ6])],"derivedFrom":makeQuery(id+"FyYUAefgu6xEfva_4.16.F14.boolean.opBoolean","SPLIT",EDGE,{"disambiguationData":[TD([subQ6])],"derivedFrom":makeQuery(id+"FyYUAefgu6xEfva_4.15.F14.boolean.opBoolean","SPLIT",EDGE,{"disambiguationData":[TD([subQ6])],"derivedFrom":makeQuery(id+"FyYUAefgu6xEfva_4.14.F14.boolean.opBoolean","SPLIT",EDGE,{"disambiguationData":[TD([subQ6])],"derivedFrom":makeQuery(id+"FyYUAefgu6xEfva_4.13.F14.boolean.opBoolean","SPLIT",EDGE,{"disambiguationData":[TD([subQ6])],"derivedFrom":makeQuery(id+"FyYUAefgu6xEfva_4.12.F14.boolean.opBoolean","SPLIT",EDGE,{"disambiguationData":[TD([subQ6])],"derivedFrom":makeQuery(id+"FyYUAefgu6xEfva_4.11.F14.boolean.opBoolean","SPLIT",EDGE,{"disambiguationData":[TD([subQ6])],"derivedFrom":makeQuery(id+"FyYUAefgu6xEfva_4.10.F14.boolean.opBoolean","SPLIT",EDGE,{"disambiguationData":[TD([subQ6])],"derivedFrom":makeQuery(id+"FyYUAefgu6xEfva_4.9.F14.boolean.opBoolean","SPLIT",EDGE,{"disambiguationData":[TD([subQ6])],"derivedFrom":makeQuery(id+"FyYUAefgu6xEfva_4.8.F14.boolean.opBoolean","SPLIT",EDGE,{"disambiguationData":[TD([subQ6])],"derivedFrom":makeQuery(id+"FyYUAefgu6xEfva_4.7.F14.boolean.opBoolean","SPLIT",EDGE,{"disambiguationData":[TD([subQ6])],"derivedFrom":makeQuery(id+"FyYUAefgu6xEfva_4.6.F14.boolean.opBoolean","SPLIT",EDGE,{"disambiguationData":[TD([subQ6])],"derivedFrom":makeQuery(id+"FyYUAefgu6xEfva_4.5.F14.boolean.opBoolean","SPLIT",EDGE,{"disambiguationData":[TD([subQ6])],"derivedFrom":makeQuery(id+"FyYUAefgu6xEfva_4.4.F14.boolean.opBoolean","SPLIT",EDGE,{"disambiguationData":[TD([subQ6])],"derivedFrom":makeQuery(id+"FyYUAefgu6xEfva_4.3.F14.boolean.opBoolean","SPLIT",EDGE,{"disambiguationData":[TD([subQ6])],"derivedFrom":makeQuery(id+"FyYUAefgu6xEfva_4.2.F14.boolean.opBoolean","SPLIT",EDGE,{"disambiguationData":[TD([subQ6])],"derivedFrom":makeQuery(id+"FyYUAefgu6xEfva_4.1.F14.boolean.opBoolean","SPLIT",EDGE,{"disambiguationData":[TD([subQ6])],"derivedFrom":makeQuery(id+"F10.boolean.opBoolean","COPY",EDGE,{"derivedFrom":makeQuery(id+"F10.opExtrude","CAP_EDGE",EDGE,{"disambiguationData":[OSD([subQ0])],"isStart":false})})})})})})})})})})})})})})})})})})})});}
            var Q553;
            {var subQ1=sQuery(id+"F11.wireOp",EDGE,"E143");var subQ3=sQuery(id+"F13.wireOp",EDGE,"E147");var subQ4=sQuery(id+"F13.wireOp",EDGE,"E148.MirrorCS");var subQ5=makeQuery(id+"FyYUAefgu6xEfva_4.17.F14.opExtrude","SWEPT_FACE",FACE,{"disambiguationData":[OSD([subQ4])]});var subQ6=makeQuery(id+"F14.opExtrude","SWEPT_FACE",FACE,{"disambiguationData":[OSD([subQ3])]});Q553=makeQuery(id+"FyYUAefgu6xEfva_4.18.F14.boolean.opBoolean","SPLIT",EDGE,{"disambiguationData":[TD([subQ5])],"derivedFrom":makeQuery(id+"FyYUAefgu6xEfva_4.17.F14.boolean.opBoolean","SPLIT",EDGE,{"disambiguationData":[TD([subQ6])],"derivedFrom":makeQuery(id+"FyYUAefgu6xEfva_4.16.F14.boolean.opBoolean","SPLIT",EDGE,{"disambiguationData":[TD([subQ6])],"derivedFrom":makeQuery(id+"FyYUAefgu6xEfva_4.15.F14.boolean.opBoolean","SPLIT",EDGE,{"disambiguationData":[TD([subQ6])],"derivedFrom":makeQuery(id+"FyYUAefgu6xEfva_4.14.F14.boolean.opBoolean","SPLIT",EDGE,{"disambiguationData":[TD([subQ6])],"derivedFrom":makeQuery(id+"FyYUAefgu6xEfva_4.13.F14.boolean.opBoolean","SPLIT",EDGE,{"disambiguationData":[TD([subQ6])],"derivedFrom":makeQuery(id+"FyYUAefgu6xEfva_4.12.F14.boolean.opBoolean","SPLIT",EDGE,{"disambiguationData":[TD([subQ6])],"derivedFrom":makeQuery(id+"FyYUAefgu6xEfva_4.11.F14.boolean.opBoolean","SPLIT",EDGE,{"disambiguationData":[TD([subQ6])],"derivedFrom":makeQuery(id+"FyYUAefgu6xEfva_4.10.F14.boolean.opBoolean","SPLIT",EDGE,{"disambiguationData":[TD([subQ6])],"derivedFrom":makeQuery(id+"FyYUAefgu6xEfva_4.9.F14.boolean.opBoolean","SPLIT",EDGE,{"disambiguationData":[TD([subQ6])],"derivedFrom":makeQuery(id+"FyYUAefgu6xEfva_4.8.F14.boolean.opBoolean","SPLIT",EDGE,{"disambiguationData":[TD([subQ6])],"derivedFrom":makeQuery(id+"FyYUAefgu6xEfva_4.7.F14.boolean.opBoolean","SPLIT",EDGE,{"disambiguationData":[TD([subQ6])],"derivedFrom":makeQuery(id+"FyYUAefgu6xEfva_4.6.F14.boolean.opBoolean","SPLIT",EDGE,{"disambiguationData":[TD([subQ6])],"derivedFrom":makeQuery(id+"FyYUAefgu6xEfva_4.5.F14.boolean.opBoolean","SPLIT",EDGE,{"disambiguationData":[TD([subQ6])],"derivedFrom":makeQuery(id+"FyYUAefgu6xEfva_4.4.F14.boolean.opBoolean","SPLIT",EDGE,{"disambiguationData":[TD([subQ6])],"derivedFrom":makeQuery(id+"FyYUAefgu6xEfva_4.3.F14.boolean.opBoolean","SPLIT",EDGE,{"disambiguationData":[TD([subQ6])],"derivedFrom":makeQuery(id+"FyYUAefgu6xEfva_4.2.F14.boolean.opBoolean","SPLIT",EDGE,{"disambiguationData":[TD([subQ6])],"derivedFrom":makeQuery(id+"FyYUAefgu6xEfva_4.1.F14.boolean.opBoolean","SPLIT",EDGE,{"disambiguationData":[TD([subQ6])],"derivedFrom":makeQuery(id+"F12.opExtrude","CAP_EDGE",EDGE,{"disambiguationData":[OSD([subQ1])],"isStart":true})})})})})})})})})})})})})})})})})})});}
            var Q554;
            Q554=makeQuery(id+"FyYUAefgu6xEfva_4.19.F14.opExtrude","CAP_EDGE",EDGE,{"disambiguationData":[OSD([sQuery(id+"F13.wireOp",EDGE,"E147")])],"isStart":true});
            var Q555;
            {var subQ0=sQuery(id+"F9.wireOp",EDGE,"E142");var subQ2=sQuery(id+"F13.wireOp",EDGE,"E147");var subQ4=sQuery(id+"F13.wireOp",EDGE,"E148.MirrorCS");var subQ5=makeQuery(id+"FyYUAefgu6xEfva_4.18.F14.opExtrude","SWEPT_FACE",FACE,{"disambiguationData":[OSD([subQ4])]});var subQ6=makeQuery(id+"F14.opExtrude","SWEPT_FACE",FACE,{"disambiguationData":[OSD([subQ2])]});Q555=makeQuery(id+"FyYUAefgu6xEfva_4.19.F14.boolean.opBoolean","SPLIT",EDGE,{"disambiguationData":[TD([subQ5])],"derivedFrom":makeQuery(id+"FyYUAefgu6xEfva_4.18.F14.boolean.opBoolean","SPLIT",EDGE,{"disambiguationData":[TD([subQ6])],"derivedFrom":makeQuery(id+"FyYUAefgu6xEfva_4.17.F14.boolean.opBoolean","SPLIT",EDGE,{"disambiguationData":[TD([subQ6])],"derivedFrom":makeQuery(id+"FyYUAefgu6xEfva_4.16.F14.boolean.opBoolean","SPLIT",EDGE,{"disambiguationData":[TD([subQ6])],"derivedFrom":makeQuery(id+"FyYUAefgu6xEfva_4.15.F14.boolean.opBoolean","SPLIT",EDGE,{"disambiguationData":[TD([subQ6])],"derivedFrom":makeQuery(id+"FyYUAefgu6xEfva_4.14.F14.boolean.opBoolean","SPLIT",EDGE,{"disambiguationData":[TD([subQ6])],"derivedFrom":makeQuery(id+"FyYUAefgu6xEfva_4.13.F14.boolean.opBoolean","SPLIT",EDGE,{"disambiguationData":[TD([subQ6])],"derivedFrom":makeQuery(id+"FyYUAefgu6xEfva_4.12.F14.boolean.opBoolean","SPLIT",EDGE,{"disambiguationData":[TD([subQ6])],"derivedFrom":makeQuery(id+"FyYUAefgu6xEfva_4.11.F14.boolean.opBoolean","SPLIT",EDGE,{"disambiguationData":[TD([subQ6])],"derivedFrom":makeQuery(id+"FyYUAefgu6xEfva_4.10.F14.boolean.opBoolean","SPLIT",EDGE,{"disambiguationData":[TD([subQ6])],"derivedFrom":makeQuery(id+"FyYUAefgu6xEfva_4.9.F14.boolean.opBoolean","SPLIT",EDGE,{"disambiguationData":[TD([subQ6])],"derivedFrom":makeQuery(id+"FyYUAefgu6xEfva_4.8.F14.boolean.opBoolean","SPLIT",EDGE,{"disambiguationData":[TD([subQ6])],"derivedFrom":makeQuery(id+"FyYUAefgu6xEfva_4.7.F14.boolean.opBoolean","SPLIT",EDGE,{"disambiguationData":[TD([subQ6])],"derivedFrom":makeQuery(id+"FyYUAefgu6xEfva_4.6.F14.boolean.opBoolean","SPLIT",EDGE,{"disambiguationData":[TD([subQ6])],"derivedFrom":makeQuery(id+"FyYUAefgu6xEfva_4.5.F14.boolean.opBoolean","SPLIT",EDGE,{"disambiguationData":[TD([subQ6])],"derivedFrom":makeQuery(id+"FyYUAefgu6xEfva_4.4.F14.boolean.opBoolean","SPLIT",EDGE,{"disambiguationData":[TD([subQ6])],"derivedFrom":makeQuery(id+"FyYUAefgu6xEfva_4.3.F14.boolean.opBoolean","SPLIT",EDGE,{"disambiguationData":[TD([subQ6])],"derivedFrom":makeQuery(id+"FyYUAefgu6xEfva_4.2.F14.boolean.opBoolean","SPLIT",EDGE,{"disambiguationData":[TD([subQ6])],"derivedFrom":makeQuery(id+"FyYUAefgu6xEfva_4.1.F14.boolean.opBoolean","SPLIT",EDGE,{"disambiguationData":[TD([subQ6])],"derivedFrom":makeQuery(id+"F10.boolean.opBoolean","COPY",EDGE,{"derivedFrom":makeQuery(id+"F10.opExtrude","CAP_EDGE",EDGE,{"disambiguationData":[OSD([subQ0])],"isStart":false})})})})})})})})})})})})})})})})})})})})});}
            var Q556;
            {var subQ1=sQuery(id+"F13.wireOp",EDGE,"E148.MirrorCS");var subQ2=makeQuery(id+"FyYUAefgu6xEfva_4.18.F14.opExtrude","SWEPT_FACE",FACE,{"disambiguationData":[OSD([subQ1])]});var subQ3=sQuery(id+"F11.wireOp",EDGE,"E143");var subQ5=sQuery(id+"F13.wireOp",EDGE,"E147");var subQ6=makeQuery(id+"F14.opExtrude","SWEPT_FACE",FACE,{"disambiguationData":[OSD([subQ5])]});Q556=makeQuery(id+"FyYUAefgu6xEfva_4.19.F14.boolean.opBoolean","SPLIT",EDGE,{"disambiguationData":[TD([subQ2])],"derivedFrom":makeQuery(id+"FyYUAefgu6xEfva_4.18.F14.boolean.opBoolean","SPLIT",EDGE,{"disambiguationData":[TD([subQ6])],"derivedFrom":makeQuery(id+"FyYUAefgu6xEfva_4.17.F14.boolean.opBoolean","SPLIT",EDGE,{"disambiguationData":[TD([subQ6])],"derivedFrom":makeQuery(id+"FyYUAefgu6xEfva_4.16.F14.boolean.opBoolean","SPLIT",EDGE,{"disambiguationData":[TD([subQ6])],"derivedFrom":makeQuery(id+"FyYUAefgu6xEfva_4.15.F14.boolean.opBoolean","SPLIT",EDGE,{"disambiguationData":[TD([subQ6])],"derivedFrom":makeQuery(id+"FyYUAefgu6xEfva_4.14.F14.boolean.opBoolean","SPLIT",EDGE,{"disambiguationData":[TD([subQ6])],"derivedFrom":makeQuery(id+"FyYUAefgu6xEfva_4.13.F14.boolean.opBoolean","SPLIT",EDGE,{"disambiguationData":[TD([subQ6])],"derivedFrom":makeQuery(id+"FyYUAefgu6xEfva_4.12.F14.boolean.opBoolean","SPLIT",EDGE,{"disambiguationData":[TD([subQ6])],"derivedFrom":makeQuery(id+"FyYUAefgu6xEfva_4.11.F14.boolean.opBoolean","SPLIT",EDGE,{"disambiguationData":[TD([subQ6])],"derivedFrom":makeQuery(id+"FyYUAefgu6xEfva_4.10.F14.boolean.opBoolean","SPLIT",EDGE,{"disambiguationData":[TD([subQ6])],"derivedFrom":makeQuery(id+"FyYUAefgu6xEfva_4.9.F14.boolean.opBoolean","SPLIT",EDGE,{"disambiguationData":[TD([subQ6])],"derivedFrom":makeQuery(id+"FyYUAefgu6xEfva_4.8.F14.boolean.opBoolean","SPLIT",EDGE,{"disambiguationData":[TD([subQ6])],"derivedFrom":makeQuery(id+"FyYUAefgu6xEfva_4.7.F14.boolean.opBoolean","SPLIT",EDGE,{"disambiguationData":[TD([subQ6])],"derivedFrom":makeQuery(id+"FyYUAefgu6xEfva_4.6.F14.boolean.opBoolean","SPLIT",EDGE,{"disambiguationData":[TD([subQ6])],"derivedFrom":makeQuery(id+"FyYUAefgu6xEfva_4.5.F14.boolean.opBoolean","SPLIT",EDGE,{"disambiguationData":[TD([subQ6])],"derivedFrom":makeQuery(id+"FyYUAefgu6xEfva_4.4.F14.boolean.opBoolean","SPLIT",EDGE,{"disambiguationData":[TD([subQ6])],"derivedFrom":makeQuery(id+"FyYUAefgu6xEfva_4.3.F14.boolean.opBoolean","SPLIT",EDGE,{"disambiguationData":[TD([subQ6])],"derivedFrom":makeQuery(id+"FyYUAefgu6xEfva_4.2.F14.boolean.opBoolean","SPLIT",EDGE,{"disambiguationData":[TD([subQ6])],"derivedFrom":makeQuery(id+"FyYUAefgu6xEfva_4.1.F14.boolean.opBoolean","SPLIT",EDGE,{"disambiguationData":[TD([subQ6])],"derivedFrom":makeQuery(id+"F12.opExtrude","CAP_EDGE",EDGE,{"disambiguationData":[OSD([subQ3])],"isStart":true})})})})})})})})})})})})})})})})})})})});}
            var Q557;
            {var subQ0=sQuery(id+"F9.wireOp",EDGE,"E142");var subQ3=sQuery(id+"F13.wireOp",EDGE,"E148.MirrorCS");var subQ4=makeQuery(id+"FyYUAefgu6xEfva_4.19.F14.opExtrude","SWEPT_FACE",FACE,{"disambiguationData":[OSD([subQ3])]});var subQ5=sQuery(id+"F13.wireOp",EDGE,"E147");var subQ6=makeQuery(id+"F14.opExtrude","SWEPT_FACE",FACE,{"disambiguationData":[OSD([subQ5])]});Q557=makeQuery(id+"FyYUAefgu6xEfva_4.20.F14.boolean.opBoolean","SPLIT",EDGE,{"disambiguationData":[TD([subQ4])],"derivedFrom":makeQuery(id+"FyYUAefgu6xEfva_4.19.F14.boolean.opBoolean","SPLIT",EDGE,{"disambiguationData":[TD([subQ6])],"derivedFrom":makeQuery(id+"FyYUAefgu6xEfva_4.18.F14.boolean.opBoolean","SPLIT",EDGE,{"disambiguationData":[TD([subQ6])],"derivedFrom":makeQuery(id+"FyYUAefgu6xEfva_4.17.F14.boolean.opBoolean","SPLIT",EDGE,{"disambiguationData":[TD([subQ6])],"derivedFrom":makeQuery(id+"FyYUAefgu6xEfva_4.16.F14.boolean.opBoolean","SPLIT",EDGE,{"disambiguationData":[TD([subQ6])],"derivedFrom":makeQuery(id+"FyYUAefgu6xEfva_4.15.F14.boolean.opBoolean","SPLIT",EDGE,{"disambiguationData":[TD([subQ6])],"derivedFrom":makeQuery(id+"FyYUAefgu6xEfva_4.14.F14.boolean.opBoolean","SPLIT",EDGE,{"disambiguationData":[TD([subQ6])],"derivedFrom":makeQuery(id+"FyYUAefgu6xEfva_4.13.F14.boolean.opBoolean","SPLIT",EDGE,{"disambiguationData":[TD([subQ6])],"derivedFrom":makeQuery(id+"FyYUAefgu6xEfva_4.12.F14.boolean.opBoolean","SPLIT",EDGE,{"disambiguationData":[TD([subQ6])],"derivedFrom":makeQuery(id+"FyYUAefgu6xEfva_4.11.F14.boolean.opBoolean","SPLIT",EDGE,{"disambiguationData":[TD([subQ6])],"derivedFrom":makeQuery(id+"FyYUAefgu6xEfva_4.10.F14.boolean.opBoolean","SPLIT",EDGE,{"disambiguationData":[TD([subQ6])],"derivedFrom":makeQuery(id+"FyYUAefgu6xEfva_4.9.F14.boolean.opBoolean","SPLIT",EDGE,{"disambiguationData":[TD([subQ6])],"derivedFrom":makeQuery(id+"FyYUAefgu6xEfva_4.8.F14.boolean.opBoolean","SPLIT",EDGE,{"disambiguationData":[TD([subQ6])],"derivedFrom":makeQuery(id+"FyYUAefgu6xEfva_4.7.F14.boolean.opBoolean","SPLIT",EDGE,{"disambiguationData":[TD([subQ6])],"derivedFrom":makeQuery(id+"FyYUAefgu6xEfva_4.6.F14.boolean.opBoolean","SPLIT",EDGE,{"disambiguationData":[TD([subQ6])],"derivedFrom":makeQuery(id+"FyYUAefgu6xEfva_4.5.F14.boolean.opBoolean","SPLIT",EDGE,{"disambiguationData":[TD([subQ6])],"derivedFrom":makeQuery(id+"FyYUAefgu6xEfva_4.4.F14.boolean.opBoolean","SPLIT",EDGE,{"disambiguationData":[TD([subQ6])],"derivedFrom":makeQuery(id+"FyYUAefgu6xEfva_4.3.F14.boolean.opBoolean","SPLIT",EDGE,{"disambiguationData":[TD([subQ6])],"derivedFrom":makeQuery(id+"FyYUAefgu6xEfva_4.2.F14.boolean.opBoolean","SPLIT",EDGE,{"disambiguationData":[TD([subQ6])],"derivedFrom":makeQuery(id+"FyYUAefgu6xEfva_4.1.F14.boolean.opBoolean","SPLIT",EDGE,{"disambiguationData":[TD([subQ6])],"derivedFrom":makeQuery(id+"F10.boolean.opBoolean","COPY",EDGE,{"derivedFrom":makeQuery(id+"F10.opExtrude","CAP_EDGE",EDGE,{"disambiguationData":[OSD([subQ0])],"isStart":false})})})})})})})})})})})})})})})})})})})})})});}
            var Q558;
            {var subQ1=sQuery(id+"F11.wireOp",EDGE,"E143");var subQ3=sQuery(id+"F13.wireOp",EDGE,"E148.MirrorCS");var subQ4=makeQuery(id+"FyYUAefgu6xEfva_4.19.F14.opExtrude","SWEPT_FACE",FACE,{"disambiguationData":[OSD([subQ3])]});var subQ5=sQuery(id+"F13.wireOp",EDGE,"E147");var subQ6=makeQuery(id+"F14.opExtrude","SWEPT_FACE",FACE,{"disambiguationData":[OSD([subQ5])]});Q558=makeQuery(id+"FyYUAefgu6xEfva_4.20.F14.boolean.opBoolean","SPLIT",EDGE,{"disambiguationData":[TD([subQ4])],"derivedFrom":makeQuery(id+"FyYUAefgu6xEfva_4.19.F14.boolean.opBoolean","SPLIT",EDGE,{"disambiguationData":[TD([subQ6])],"derivedFrom":makeQuery(id+"FyYUAefgu6xEfva_4.18.F14.boolean.opBoolean","SPLIT",EDGE,{"disambiguationData":[TD([subQ6])],"derivedFrom":makeQuery(id+"FyYUAefgu6xEfva_4.17.F14.boolean.opBoolean","SPLIT",EDGE,{"disambiguationData":[TD([subQ6])],"derivedFrom":makeQuery(id+"FyYUAefgu6xEfva_4.16.F14.boolean.opBoolean","SPLIT",EDGE,{"disambiguationData":[TD([subQ6])],"derivedFrom":makeQuery(id+"FyYUAefgu6xEfva_4.15.F14.boolean.opBoolean","SPLIT",EDGE,{"disambiguationData":[TD([subQ6])],"derivedFrom":makeQuery(id+"FyYUAefgu6xEfva_4.14.F14.boolean.opBoolean","SPLIT",EDGE,{"disambiguationData":[TD([subQ6])],"derivedFrom":makeQuery(id+"FyYUAefgu6xEfva_4.13.F14.boolean.opBoolean","SPLIT",EDGE,{"disambiguationData":[TD([subQ6])],"derivedFrom":makeQuery(id+"FyYUAefgu6xEfva_4.12.F14.boolean.opBoolean","SPLIT",EDGE,{"disambiguationData":[TD([subQ6])],"derivedFrom":makeQuery(id+"FyYUAefgu6xEfva_4.11.F14.boolean.opBoolean","SPLIT",EDGE,{"disambiguationData":[TD([subQ6])],"derivedFrom":makeQuery(id+"FyYUAefgu6xEfva_4.10.F14.boolean.opBoolean","SPLIT",EDGE,{"disambiguationData":[TD([subQ6])],"derivedFrom":makeQuery(id+"FyYUAefgu6xEfva_4.9.F14.boolean.opBoolean","SPLIT",EDGE,{"disambiguationData":[TD([subQ6])],"derivedFrom":makeQuery(id+"FyYUAefgu6xEfva_4.8.F14.boolean.opBoolean","SPLIT",EDGE,{"disambiguationData":[TD([subQ6])],"derivedFrom":makeQuery(id+"FyYUAefgu6xEfva_4.7.F14.boolean.opBoolean","SPLIT",EDGE,{"disambiguationData":[TD([subQ6])],"derivedFrom":makeQuery(id+"FyYUAefgu6xEfva_4.6.F14.boolean.opBoolean","SPLIT",EDGE,{"disambiguationData":[TD([subQ6])],"derivedFrom":makeQuery(id+"FyYUAefgu6xEfva_4.5.F14.boolean.opBoolean","SPLIT",EDGE,{"disambiguationData":[TD([subQ6])],"derivedFrom":makeQuery(id+"FyYUAefgu6xEfva_4.4.F14.boolean.opBoolean","SPLIT",EDGE,{"disambiguationData":[TD([subQ6])],"derivedFrom":makeQuery(id+"FyYUAefgu6xEfva_4.3.F14.boolean.opBoolean","SPLIT",EDGE,{"disambiguationData":[TD([subQ6])],"derivedFrom":makeQuery(id+"FyYUAefgu6xEfva_4.2.F14.boolean.opBoolean","SPLIT",EDGE,{"disambiguationData":[TD([subQ6])],"derivedFrom":makeQuery(id+"FyYUAefgu6xEfva_4.1.F14.boolean.opBoolean","SPLIT",EDGE,{"disambiguationData":[TD([subQ6])],"derivedFrom":makeQuery(id+"F12.opExtrude","CAP_EDGE",EDGE,{"disambiguationData":[OSD([subQ1])],"isStart":true})})})})})})})})})})})})})})})})})})})})});}
            var Q559;
            Q559=makeQuery(id+"FyYUAefgu6xEfva_4.21.F14.opExtrude","SWEPT_EDGE",EDGE,{"disambiguationData":[OSD([sQuery(id+"F11.wireOp",EDGE,"E143"),sQuery(id+"F13.wireOp",EDGE,"E147")])]});
            var Q560;
            Q560=makeQuery(id+"FyYUAefgu6xEfva_4.21.F14.opExtrude","SWEPT_EDGE",EDGE,{"disambiguationData":[OSD([sQuery(id+"F9.wireOp",EDGE,"E142"),sQuery(id+"F13.wireOp",EDGE,"E148.MirrorCS")])]});
            var Q561;
            {var subQ1=sQuery(id+"F11.wireOp",EDGE,"E143");var subQ3=sQuery(id+"F13.wireOp",EDGE,"E148.MirrorCS");var subQ4=makeQuery(id+"FyYUAefgu6xEfva_4.20.F14.opExtrude","SWEPT_FACE",FACE,{"disambiguationData":[OSD([subQ3])]});var subQ5=sQuery(id+"F13.wireOp",EDGE,"E147");var subQ6=makeQuery(id+"F14.opExtrude","SWEPT_FACE",FACE,{"disambiguationData":[OSD([subQ5])]});Q561=makeQuery(id+"FyYUAefgu6xEfva_4.21.F14.boolean.opBoolean","SPLIT",EDGE,{"disambiguationData":[TD([subQ4])],"derivedFrom":makeQuery(id+"FyYUAefgu6xEfva_4.20.F14.boolean.opBoolean","SPLIT",EDGE,{"disambiguationData":[TD([subQ6])],"derivedFrom":makeQuery(id+"FyYUAefgu6xEfva_4.19.F14.boolean.opBoolean","SPLIT",EDGE,{"disambiguationData":[TD([subQ6])],"derivedFrom":makeQuery(id+"FyYUAefgu6xEfva_4.18.F14.boolean.opBoolean","SPLIT",EDGE,{"disambiguationData":[TD([subQ6])],"derivedFrom":makeQuery(id+"FyYUAefgu6xEfva_4.17.F14.boolean.opBoolean","SPLIT",EDGE,{"disambiguationData":[TD([subQ6])],"derivedFrom":makeQuery(id+"FyYUAefgu6xEfva_4.16.F14.boolean.opBoolean","SPLIT",EDGE,{"disambiguationData":[TD([subQ6])],"derivedFrom":makeQuery(id+"FyYUAefgu6xEfva_4.15.F14.boolean.opBoolean","SPLIT",EDGE,{"disambiguationData":[TD([subQ6])],"derivedFrom":makeQuery(id+"FyYUAefgu6xEfva_4.14.F14.boolean.opBoolean","SPLIT",EDGE,{"disambiguationData":[TD([subQ6])],"derivedFrom":makeQuery(id+"FyYUAefgu6xEfva_4.13.F14.boolean.opBoolean","SPLIT",EDGE,{"disambiguationData":[TD([subQ6])],"derivedFrom":makeQuery(id+"FyYUAefgu6xEfva_4.12.F14.boolean.opBoolean","SPLIT",EDGE,{"disambiguationData":[TD([subQ6])],"derivedFrom":makeQuery(id+"FyYUAefgu6xEfva_4.11.F14.boolean.opBoolean","SPLIT",EDGE,{"disambiguationData":[TD([subQ6])],"derivedFrom":makeQuery(id+"FyYUAefgu6xEfva_4.10.F14.boolean.opBoolean","SPLIT",EDGE,{"disambiguationData":[TD([subQ6])],"derivedFrom":makeQuery(id+"FyYUAefgu6xEfva_4.9.F14.boolean.opBoolean","SPLIT",EDGE,{"disambiguationData":[TD([subQ6])],"derivedFrom":makeQuery(id+"FyYUAefgu6xEfva_4.8.F14.boolean.opBoolean","SPLIT",EDGE,{"disambiguationData":[TD([subQ6])],"derivedFrom":makeQuery(id+"FyYUAefgu6xEfva_4.7.F14.boolean.opBoolean","SPLIT",EDGE,{"disambiguationData":[TD([subQ6])],"derivedFrom":makeQuery(id+"FyYUAefgu6xEfva_4.6.F14.boolean.opBoolean","SPLIT",EDGE,{"disambiguationData":[TD([subQ6])],"derivedFrom":makeQuery(id+"FyYUAefgu6xEfva_4.5.F14.boolean.opBoolean","SPLIT",EDGE,{"disambiguationData":[TD([subQ6])],"derivedFrom":makeQuery(id+"FyYUAefgu6xEfva_4.4.F14.boolean.opBoolean","SPLIT",EDGE,{"disambiguationData":[TD([subQ6])],"derivedFrom":makeQuery(id+"FyYUAefgu6xEfva_4.3.F14.boolean.opBoolean","SPLIT",EDGE,{"disambiguationData":[TD([subQ6])],"derivedFrom":makeQuery(id+"FyYUAefgu6xEfva_4.2.F14.boolean.opBoolean","SPLIT",EDGE,{"disambiguationData":[TD([subQ6])],"derivedFrom":makeQuery(id+"FyYUAefgu6xEfva_4.1.F14.boolean.opBoolean","SPLIT",EDGE,{"disambiguationData":[TD([subQ6])],"derivedFrom":makeQuery(id+"F12.opExtrude","CAP_EDGE",EDGE,{"disambiguationData":[OSD([subQ1])],"isStart":true})})})})})})})})})})})})})})})})})})})})})});}
            var Q562;
            {var subQ1=sQuery(id+"F13.wireOp",EDGE,"E147");var subQ2=sQuery(id+"F11.wireOp",EDGE,"E143");var subQ4=sQuery(id+"F13.wireOp",EDGE,"E148.MirrorCS");var subQ5=makeQuery(id+"FyYUAefgu6xEfva_4.21.F14.opExtrude","SWEPT_FACE",FACE,{"disambiguationData":[OSD([subQ4])]});var subQ6=makeQuery(id+"F14.opExtrude","SWEPT_FACE",FACE,{"disambiguationData":[OSD([subQ1])]});Q562=makeQuery(id+"FyYUAefgu6xEfva_4.22.F14.boolean.opBoolean","SPLIT",EDGE,{"disambiguationData":[TD([subQ5])],"derivedFrom":makeQuery(id+"FyYUAefgu6xEfva_4.21.F14.boolean.opBoolean","SPLIT",EDGE,{"disambiguationData":[TD([subQ6])],"derivedFrom":makeQuery(id+"FyYUAefgu6xEfva_4.20.F14.boolean.opBoolean","SPLIT",EDGE,{"disambiguationData":[TD([subQ6])],"derivedFrom":makeQuery(id+"FyYUAefgu6xEfva_4.19.F14.boolean.opBoolean","SPLIT",EDGE,{"disambiguationData":[TD([subQ6])],"derivedFrom":makeQuery(id+"FyYUAefgu6xEfva_4.18.F14.boolean.opBoolean","SPLIT",EDGE,{"disambiguationData":[TD([subQ6])],"derivedFrom":makeQuery(id+"FyYUAefgu6xEfva_4.17.F14.boolean.opBoolean","SPLIT",EDGE,{"disambiguationData":[TD([subQ6])],"derivedFrom":makeQuery(id+"FyYUAefgu6xEfva_4.16.F14.boolean.opBoolean","SPLIT",EDGE,{"disambiguationData":[TD([subQ6])],"derivedFrom":makeQuery(id+"FyYUAefgu6xEfva_4.15.F14.boolean.opBoolean","SPLIT",EDGE,{"disambiguationData":[TD([subQ6])],"derivedFrom":makeQuery(id+"FyYUAefgu6xEfva_4.14.F14.boolean.opBoolean","SPLIT",EDGE,{"disambiguationData":[TD([subQ6])],"derivedFrom":makeQuery(id+"FyYUAefgu6xEfva_4.13.F14.boolean.opBoolean","SPLIT",EDGE,{"disambiguationData":[TD([subQ6])],"derivedFrom":makeQuery(id+"FyYUAefgu6xEfva_4.12.F14.boolean.opBoolean","SPLIT",EDGE,{"disambiguationData":[TD([subQ6])],"derivedFrom":makeQuery(id+"FyYUAefgu6xEfva_4.11.F14.boolean.opBoolean","SPLIT",EDGE,{"disambiguationData":[TD([subQ6])],"derivedFrom":makeQuery(id+"FyYUAefgu6xEfva_4.10.F14.boolean.opBoolean","SPLIT",EDGE,{"disambiguationData":[TD([subQ6])],"derivedFrom":makeQuery(id+"FyYUAefgu6xEfva_4.9.F14.boolean.opBoolean","SPLIT",EDGE,{"disambiguationData":[TD([subQ6])],"derivedFrom":makeQuery(id+"FyYUAefgu6xEfva_4.8.F14.boolean.opBoolean","SPLIT",EDGE,{"disambiguationData":[TD([subQ6])],"derivedFrom":makeQuery(id+"FyYUAefgu6xEfva_4.7.F14.boolean.opBoolean","SPLIT",EDGE,{"disambiguationData":[TD([subQ6])],"derivedFrom":makeQuery(id+"FyYUAefgu6xEfva_4.6.F14.boolean.opBoolean","SPLIT",EDGE,{"disambiguationData":[TD([subQ6])],"derivedFrom":makeQuery(id+"FyYUAefgu6xEfva_4.5.F14.boolean.opBoolean","SPLIT",EDGE,{"disambiguationData":[TD([subQ6])],"derivedFrom":makeQuery(id+"FyYUAefgu6xEfva_4.4.F14.boolean.opBoolean","SPLIT",EDGE,{"disambiguationData":[TD([subQ6])],"derivedFrom":makeQuery(id+"FyYUAefgu6xEfva_4.3.F14.boolean.opBoolean","SPLIT",EDGE,{"disambiguationData":[TD([subQ6])],"derivedFrom":makeQuery(id+"FyYUAefgu6xEfva_4.2.F14.boolean.opBoolean","SPLIT",EDGE,{"disambiguationData":[TD([subQ6])],"derivedFrom":makeQuery(id+"FyYUAefgu6xEfva_4.1.F14.boolean.opBoolean","SPLIT",EDGE,{"disambiguationData":[TD([subQ6])],"derivedFrom":makeQuery(id+"F12.opExtrude","CAP_EDGE",EDGE,{"disambiguationData":[OSD([subQ2])],"isStart":true})})})})})})})})})})})})})})})})})})})})})})});}
            var Q563;
            Q563=makeQuery(id+"FyYUAefgu6xEfva_4.23.F14.opExtrude","SWEPT_EDGE",EDGE,{"disambiguationData":[OSD([sQuery(id+"F11.wireOp",EDGE,"E143"),sQuery(id+"F13.wireOp",EDGE,"E147")])]});
            var Q564;
            Q564=makeQuery(id+"FyYUAefgu6xEfva_4.23.F14.opExtrude","SWEPT_EDGE",EDGE,{"disambiguationData":[OSD([sQuery(id+"F9.wireOp",EDGE,"E142"),sQuery(id+"F13.wireOp",EDGE,"E148.MirrorCS")])]});
            var Q565;
            Q565=makeQuery(id+"FyYUAefgu6xEfva_4.23.F14.opExtrude","SWEPT_EDGE",EDGE,{"disambiguationData":[OSD([sQuery(id+"F11.wireOp",EDGE,"E143"),sQuery(id+"F13.wireOp",EDGE,"E148.MirrorCS")])]});
            var Q566;
            Q566=makeQuery(id+"FyYUAefgu6xEfva_4.23.F14.opExtrude","CAP_EDGE",EDGE,{"disambiguationData":[OSD([sQuery(id+"F13.wireOp",EDGE,"E148.MirrorCS")])],"isStart":true});
            var Q567;
            {var subQ1=sQuery(id+"F11.wireOp",EDGE,"E143");var subQ3=sQuery(id+"F13.wireOp",EDGE,"E147");var subQ4=sQuery(id+"F13.wireOp",EDGE,"E148.MirrorCS");var subQ5=makeQuery(id+"FyYUAefgu6xEfva_4.22.F14.opExtrude","SWEPT_FACE",FACE,{"disambiguationData":[OSD([subQ4])]});var subQ6=makeQuery(id+"F14.opExtrude","SWEPT_FACE",FACE,{"disambiguationData":[OSD([subQ3])]});Q567=makeQuery(id+"FyYUAefgu6xEfva_4.23.F14.boolean.opBoolean","SPLIT",EDGE,{"disambiguationData":[TD([subQ5])],"derivedFrom":makeQuery(id+"FyYUAefgu6xEfva_4.22.F14.boolean.opBoolean","SPLIT",EDGE,{"disambiguationData":[TD([subQ6])],"derivedFrom":makeQuery(id+"FyYUAefgu6xEfva_4.21.F14.boolean.opBoolean","SPLIT",EDGE,{"disambiguationData":[TD([subQ6])],"derivedFrom":makeQuery(id+"FyYUAefgu6xEfva_4.20.F14.boolean.opBoolean","SPLIT",EDGE,{"disambiguationData":[TD([subQ6])],"derivedFrom":makeQuery(id+"FyYUAefgu6xEfva_4.19.F14.boolean.opBoolean","SPLIT",EDGE,{"disambiguationData":[TD([subQ6])],"derivedFrom":makeQuery(id+"FyYUAefgu6xEfva_4.18.F14.boolean.opBoolean","SPLIT",EDGE,{"disambiguationData":[TD([subQ6])],"derivedFrom":makeQuery(id+"FyYUAefgu6xEfva_4.17.F14.boolean.opBoolean","SPLIT",EDGE,{"disambiguationData":[TD([subQ6])],"derivedFrom":makeQuery(id+"FyYUAefgu6xEfva_4.16.F14.boolean.opBoolean","SPLIT",EDGE,{"disambiguationData":[TD([subQ6])],"derivedFrom":makeQuery(id+"FyYUAefgu6xEfva_4.15.F14.boolean.opBoolean","SPLIT",EDGE,{"disambiguationData":[TD([subQ6])],"derivedFrom":makeQuery(id+"FyYUAefgu6xEfva_4.14.F14.boolean.opBoolean","SPLIT",EDGE,{"disambiguationData":[TD([subQ6])],"derivedFrom":makeQuery(id+"FyYUAefgu6xEfva_4.13.F14.boolean.opBoolean","SPLIT",EDGE,{"disambiguationData":[TD([subQ6])],"derivedFrom":makeQuery(id+"FyYUAefgu6xEfva_4.12.F14.boolean.opBoolean","SPLIT",EDGE,{"disambiguationData":[TD([subQ6])],"derivedFrom":makeQuery(id+"FyYUAefgu6xEfva_4.11.F14.boolean.opBoolean","SPLIT",EDGE,{"disambiguationData":[TD([subQ6])],"derivedFrom":makeQuery(id+"FyYUAefgu6xEfva_4.10.F14.boolean.opBoolean","SPLIT",EDGE,{"disambiguationData":[TD([subQ6])],"derivedFrom":makeQuery(id+"FyYUAefgu6xEfva_4.9.F14.boolean.opBoolean","SPLIT",EDGE,{"disambiguationData":[TD([subQ6])],"derivedFrom":makeQuery(id+"FyYUAefgu6xEfva_4.8.F14.boolean.opBoolean","SPLIT",EDGE,{"disambiguationData":[TD([subQ6])],"derivedFrom":makeQuery(id+"FyYUAefgu6xEfva_4.7.F14.boolean.opBoolean","SPLIT",EDGE,{"disambiguationData":[TD([subQ6])],"derivedFrom":makeQuery(id+"FyYUAefgu6xEfva_4.6.F14.boolean.opBoolean","SPLIT",EDGE,{"disambiguationData":[TD([subQ6])],"derivedFrom":makeQuery(id+"FyYUAefgu6xEfva_4.5.F14.boolean.opBoolean","SPLIT",EDGE,{"disambiguationData":[TD([subQ6])],"derivedFrom":makeQuery(id+"FyYUAefgu6xEfva_4.4.F14.boolean.opBoolean","SPLIT",EDGE,{"disambiguationData":[TD([subQ6])],"derivedFrom":makeQuery(id+"FyYUAefgu6xEfva_4.3.F14.boolean.opBoolean","SPLIT",EDGE,{"disambiguationData":[TD([subQ6])],"derivedFrom":makeQuery(id+"FyYUAefgu6xEfva_4.2.F14.boolean.opBoolean","SPLIT",EDGE,{"disambiguationData":[TD([subQ6])],"derivedFrom":makeQuery(id+"FyYUAefgu6xEfva_4.1.F14.boolean.opBoolean","SPLIT",EDGE,{"disambiguationData":[TD([subQ6])],"derivedFrom":makeQuery(id+"F12.opExtrude","CAP_EDGE",EDGE,{"disambiguationData":[OSD([subQ1])],"isStart":true})})})})})})})})})})})})})})})})})})})})})})})});}
            var Q568;
            {var subQ1=sQuery(id+"F13.wireOp",EDGE,"E148.MirrorCS");var subQ2=makeQuery(id+"FyYUAefgu6xEfva_4.23.F14.opExtrude","SWEPT_FACE",FACE,{"disambiguationData":[OSD([subQ1])]});var subQ3=sQuery(id+"F11.wireOp",EDGE,"E143");var subQ5=sQuery(id+"F13.wireOp",EDGE,"E147");var subQ6=makeQuery(id+"F14.opExtrude","SWEPT_FACE",FACE,{"disambiguationData":[OSD([subQ5])]});Q568=makeQuery(id+"FyYUAefgu6xEfva_4.24.F14.boolean.opBoolean","SPLIT",EDGE,{"disambiguationData":[TD([subQ2])],"derivedFrom":makeQuery(id+"FyYUAefgu6xEfva_4.23.F14.boolean.opBoolean","SPLIT",EDGE,{"disambiguationData":[TD([subQ6])],"derivedFrom":makeQuery(id+"FyYUAefgu6xEfva_4.22.F14.boolean.opBoolean","SPLIT",EDGE,{"disambiguationData":[TD([subQ6])],"derivedFrom":makeQuery(id+"FyYUAefgu6xEfva_4.21.F14.boolean.opBoolean","SPLIT",EDGE,{"disambiguationData":[TD([subQ6])],"derivedFrom":makeQuery(id+"FyYUAefgu6xEfva_4.20.F14.boolean.opBoolean","SPLIT",EDGE,{"disambiguationData":[TD([subQ6])],"derivedFrom":makeQuery(id+"FyYUAefgu6xEfva_4.19.F14.boolean.opBoolean","SPLIT",EDGE,{"disambiguationData":[TD([subQ6])],"derivedFrom":makeQuery(id+"FyYUAefgu6xEfva_4.18.F14.boolean.opBoolean","SPLIT",EDGE,{"disambiguationData":[TD([subQ6])],"derivedFrom":makeQuery(id+"FyYUAefgu6xEfva_4.17.F14.boolean.opBoolean","SPLIT",EDGE,{"disambiguationData":[TD([subQ6])],"derivedFrom":makeQuery(id+"FyYUAefgu6xEfva_4.16.F14.boolean.opBoolean","SPLIT",EDGE,{"disambiguationData":[TD([subQ6])],"derivedFrom":makeQuery(id+"FyYUAefgu6xEfva_4.15.F14.boolean.opBoolean","SPLIT",EDGE,{"disambiguationData":[TD([subQ6])],"derivedFrom":makeQuery(id+"FyYUAefgu6xEfva_4.14.F14.boolean.opBoolean","SPLIT",EDGE,{"disambiguationData":[TD([subQ6])],"derivedFrom":makeQuery(id+"FyYUAefgu6xEfva_4.13.F14.boolean.opBoolean","SPLIT",EDGE,{"disambiguationData":[TD([subQ6])],"derivedFrom":makeQuery(id+"FyYUAefgu6xEfva_4.12.F14.boolean.opBoolean","SPLIT",EDGE,{"disambiguationData":[TD([subQ6])],"derivedFrom":makeQuery(id+"FyYUAefgu6xEfva_4.11.F14.boolean.opBoolean","SPLIT",EDGE,{"disambiguationData":[TD([subQ6])],"derivedFrom":makeQuery(id+"FyYUAefgu6xEfva_4.10.F14.boolean.opBoolean","SPLIT",EDGE,{"disambiguationData":[TD([subQ6])],"derivedFrom":makeQuery(id+"FyYUAefgu6xEfva_4.9.F14.boolean.opBoolean","SPLIT",EDGE,{"disambiguationData":[TD([subQ6])],"derivedFrom":makeQuery(id+"FyYUAefgu6xEfva_4.8.F14.boolean.opBoolean","SPLIT",EDGE,{"disambiguationData":[TD([subQ6])],"derivedFrom":makeQuery(id+"FyYUAefgu6xEfva_4.7.F14.boolean.opBoolean","SPLIT",EDGE,{"disambiguationData":[TD([subQ6])],"derivedFrom":makeQuery(id+"FyYUAefgu6xEfva_4.6.F14.boolean.opBoolean","SPLIT",EDGE,{"disambiguationData":[TD([subQ6])],"derivedFrom":makeQuery(id+"FyYUAefgu6xEfva_4.5.F14.boolean.opBoolean","SPLIT",EDGE,{"disambiguationData":[TD([subQ6])],"derivedFrom":makeQuery(id+"FyYUAefgu6xEfva_4.4.F14.boolean.opBoolean","SPLIT",EDGE,{"disambiguationData":[TD([subQ6])],"derivedFrom":makeQuery(id+"FyYUAefgu6xEfva_4.3.F14.boolean.opBoolean","SPLIT",EDGE,{"disambiguationData":[TD([subQ6])],"derivedFrom":makeQuery(id+"FyYUAefgu6xEfva_4.2.F14.boolean.opBoolean","SPLIT",EDGE,{"disambiguationData":[TD([subQ6])],"derivedFrom":makeQuery(id+"FyYUAefgu6xEfva_4.1.F14.boolean.opBoolean","SPLIT",EDGE,{"disambiguationData":[TD([subQ6])],"derivedFrom":makeQuery(id+"F12.opExtrude","CAP_EDGE",EDGE,{"disambiguationData":[OSD([subQ3])],"isStart":true})})})})})})})})})})})})})})})})})})})})})})})})});}
            var Q569;
            Q569=makeQuery(id+"FyYUAefgu6xEfva_4.25.F14.opExtrude","CAP_EDGE",EDGE,{"disambiguationData":[OSD([sQuery(id+"F13.wireOp",EDGE,"E147")])],"isStart":true});
            var Q570;
            {var subQ1=sQuery(id+"F11.wireOp",EDGE,"E143");var subQ3=sQuery(id+"F13.wireOp",EDGE,"E148.MirrorCS");var subQ4=makeQuery(id+"FyYUAefgu6xEfva_4.24.F14.opExtrude","SWEPT_FACE",FACE,{"disambiguationData":[OSD([subQ3])]});var subQ5=sQuery(id+"F13.wireOp",EDGE,"E147");var subQ6=makeQuery(id+"F14.opExtrude","SWEPT_FACE",FACE,{"disambiguationData":[OSD([subQ5])]});Q570=makeQuery(id+"FyYUAefgu6xEfva_4.25.F14.boolean.opBoolean","SPLIT",EDGE,{"disambiguationData":[TD([subQ4])],"derivedFrom":makeQuery(id+"FyYUAefgu6xEfva_4.24.F14.boolean.opBoolean","SPLIT",EDGE,{"disambiguationData":[TD([subQ6])],"derivedFrom":makeQuery(id+"FyYUAefgu6xEfva_4.23.F14.boolean.opBoolean","SPLIT",EDGE,{"disambiguationData":[TD([subQ6])],"derivedFrom":makeQuery(id+"FyYUAefgu6xEfva_4.22.F14.boolean.opBoolean","SPLIT",EDGE,{"disambiguationData":[TD([subQ6])],"derivedFrom":makeQuery(id+"FyYUAefgu6xEfva_4.21.F14.boolean.opBoolean","SPLIT",EDGE,{"disambiguationData":[TD([subQ6])],"derivedFrom":makeQuery(id+"FyYUAefgu6xEfva_4.20.F14.boolean.opBoolean","SPLIT",EDGE,{"disambiguationData":[TD([subQ6])],"derivedFrom":makeQuery(id+"FyYUAefgu6xEfva_4.19.F14.boolean.opBoolean","SPLIT",EDGE,{"disambiguationData":[TD([subQ6])],"derivedFrom":makeQuery(id+"FyYUAefgu6xEfva_4.18.F14.boolean.opBoolean","SPLIT",EDGE,{"disambiguationData":[TD([subQ6])],"derivedFrom":makeQuery(id+"FyYUAefgu6xEfva_4.17.F14.boolean.opBoolean","SPLIT",EDGE,{"disambiguationData":[TD([subQ6])],"derivedFrom":makeQuery(id+"FyYUAefgu6xEfva_4.16.F14.boolean.opBoolean","SPLIT",EDGE,{"disambiguationData":[TD([subQ6])],"derivedFrom":makeQuery(id+"FyYUAefgu6xEfva_4.15.F14.boolean.opBoolean","SPLIT",EDGE,{"disambiguationData":[TD([subQ6])],"derivedFrom":makeQuery(id+"FyYUAefgu6xEfva_4.14.F14.boolean.opBoolean","SPLIT",EDGE,{"disambiguationData":[TD([subQ6])],"derivedFrom":makeQuery(id+"FyYUAefgu6xEfva_4.13.F14.boolean.opBoolean","SPLIT",EDGE,{"disambiguationData":[TD([subQ6])],"derivedFrom":makeQuery(id+"FyYUAefgu6xEfva_4.12.F14.boolean.opBoolean","SPLIT",EDGE,{"disambiguationData":[TD([subQ6])],"derivedFrom":makeQuery(id+"FyYUAefgu6xEfva_4.11.F14.boolean.opBoolean","SPLIT",EDGE,{"disambiguationData":[TD([subQ6])],"derivedFrom":makeQuery(id+"FyYUAefgu6xEfva_4.10.F14.boolean.opBoolean","SPLIT",EDGE,{"disambiguationData":[TD([subQ6])],"derivedFrom":makeQuery(id+"FyYUAefgu6xEfva_4.9.F14.boolean.opBoolean","SPLIT",EDGE,{"disambiguationData":[TD([subQ6])],"derivedFrom":makeQuery(id+"FyYUAefgu6xEfva_4.8.F14.boolean.opBoolean","SPLIT",EDGE,{"disambiguationData":[TD([subQ6])],"derivedFrom":makeQuery(id+"FyYUAefgu6xEfva_4.7.F14.boolean.opBoolean","SPLIT",EDGE,{"disambiguationData":[TD([subQ6])],"derivedFrom":makeQuery(id+"FyYUAefgu6xEfva_4.6.F14.boolean.opBoolean","SPLIT",EDGE,{"disambiguationData":[TD([subQ6])],"derivedFrom":makeQuery(id+"FyYUAefgu6xEfva_4.5.F14.boolean.opBoolean","SPLIT",EDGE,{"disambiguationData":[TD([subQ6])],"derivedFrom":makeQuery(id+"FyYUAefgu6xEfva_4.4.F14.boolean.opBoolean","SPLIT",EDGE,{"disambiguationData":[TD([subQ6])],"derivedFrom":makeQuery(id+"FyYUAefgu6xEfva_4.3.F14.boolean.opBoolean","SPLIT",EDGE,{"disambiguationData":[TD([subQ6])],"derivedFrom":makeQuery(id+"FyYUAefgu6xEfva_4.2.F14.boolean.opBoolean","SPLIT",EDGE,{"disambiguationData":[TD([subQ6])],"derivedFrom":makeQuery(id+"FyYUAefgu6xEfva_4.1.F14.boolean.opBoolean","SPLIT",EDGE,{"disambiguationData":[TD([subQ6])],"derivedFrom":makeQuery(id+"F12.opExtrude","CAP_EDGE",EDGE,{"disambiguationData":[OSD([subQ1])],"isStart":true})})})})})})})})})})})})})})})})})})})})})})})})})});}
            var Q571;
            {var subQ1=sQuery(id+"F11.wireOp",EDGE,"E143");var subQ3=sQuery(id+"F13.wireOp",EDGE,"E148.MirrorCS");var subQ4=makeQuery(id+"FyYUAefgu6xEfva_4.25.F14.opExtrude","SWEPT_FACE",FACE,{"disambiguationData":[OSD([subQ3])]});var subQ5=sQuery(id+"F13.wireOp",EDGE,"E147");var subQ6=makeQuery(id+"F14.opExtrude","SWEPT_FACE",FACE,{"disambiguationData":[OSD([subQ5])]});Q571=makeQuery(id+"FyYUAefgu6xEfva_4.26.F14.boolean.opBoolean","SPLIT",EDGE,{"disambiguationData":[TD([subQ4])],"derivedFrom":makeQuery(id+"FyYUAefgu6xEfva_4.25.F14.boolean.opBoolean","SPLIT",EDGE,{"disambiguationData":[TD([subQ6])],"derivedFrom":makeQuery(id+"FyYUAefgu6xEfva_4.24.F14.boolean.opBoolean","SPLIT",EDGE,{"disambiguationData":[TD([subQ6])],"derivedFrom":makeQuery(id+"FyYUAefgu6xEfva_4.23.F14.boolean.opBoolean","SPLIT",EDGE,{"disambiguationData":[TD([subQ6])],"derivedFrom":makeQuery(id+"FyYUAefgu6xEfva_4.22.F14.boolean.opBoolean","SPLIT",EDGE,{"disambiguationData":[TD([subQ6])],"derivedFrom":makeQuery(id+"FyYUAefgu6xEfva_4.21.F14.boolean.opBoolean","SPLIT",EDGE,{"disambiguationData":[TD([subQ6])],"derivedFrom":makeQuery(id+"FyYUAefgu6xEfva_4.20.F14.boolean.opBoolean","SPLIT",EDGE,{"disambiguationData":[TD([subQ6])],"derivedFrom":makeQuery(id+"FyYUAefgu6xEfva_4.19.F14.boolean.opBoolean","SPLIT",EDGE,{"disambiguationData":[TD([subQ6])],"derivedFrom":makeQuery(id+"FyYUAefgu6xEfva_4.18.F14.boolean.opBoolean","SPLIT",EDGE,{"disambiguationData":[TD([subQ6])],"derivedFrom":makeQuery(id+"FyYUAefgu6xEfva_4.17.F14.boolean.opBoolean","SPLIT",EDGE,{"disambiguationData":[TD([subQ6])],"derivedFrom":makeQuery(id+"FyYUAefgu6xEfva_4.16.F14.boolean.opBoolean","SPLIT",EDGE,{"disambiguationData":[TD([subQ6])],"derivedFrom":makeQuery(id+"FyYUAefgu6xEfva_4.15.F14.boolean.opBoolean","SPLIT",EDGE,{"disambiguationData":[TD([subQ6])],"derivedFrom":makeQuery(id+"FyYUAefgu6xEfva_4.14.F14.boolean.opBoolean","SPLIT",EDGE,{"disambiguationData":[TD([subQ6])],"derivedFrom":makeQuery(id+"FyYUAefgu6xEfva_4.13.F14.boolean.opBoolean","SPLIT",EDGE,{"disambiguationData":[TD([subQ6])],"derivedFrom":makeQuery(id+"FyYUAefgu6xEfva_4.12.F14.boolean.opBoolean","SPLIT",EDGE,{"disambiguationData":[TD([subQ6])],"derivedFrom":makeQuery(id+"FyYUAefgu6xEfva_4.11.F14.boolean.opBoolean","SPLIT",EDGE,{"disambiguationData":[TD([subQ6])],"derivedFrom":makeQuery(id+"FyYUAefgu6xEfva_4.10.F14.boolean.opBoolean","SPLIT",EDGE,{"disambiguationData":[TD([subQ6])],"derivedFrom":makeQuery(id+"FyYUAefgu6xEfva_4.9.F14.boolean.opBoolean","SPLIT",EDGE,{"disambiguationData":[TD([subQ6])],"derivedFrom":makeQuery(id+"FyYUAefgu6xEfva_4.8.F14.boolean.opBoolean","SPLIT",EDGE,{"disambiguationData":[TD([subQ6])],"derivedFrom":makeQuery(id+"FyYUAefgu6xEfva_4.7.F14.boolean.opBoolean","SPLIT",EDGE,{"disambiguationData":[TD([subQ6])],"derivedFrom":makeQuery(id+"FyYUAefgu6xEfva_4.6.F14.boolean.opBoolean","SPLIT",EDGE,{"disambiguationData":[TD([subQ6])],"derivedFrom":makeQuery(id+"FyYUAefgu6xEfva_4.5.F14.boolean.opBoolean","SPLIT",EDGE,{"disambiguationData":[TD([subQ6])],"derivedFrom":makeQuery(id+"FyYUAefgu6xEfva_4.4.F14.boolean.opBoolean","SPLIT",EDGE,{"disambiguationData":[TD([subQ6])],"derivedFrom":makeQuery(id+"FyYUAefgu6xEfva_4.3.F14.boolean.opBoolean","SPLIT",EDGE,{"disambiguationData":[TD([subQ6])],"derivedFrom":makeQuery(id+"FyYUAefgu6xEfva_4.2.F14.boolean.opBoolean","SPLIT",EDGE,{"disambiguationData":[TD([subQ6])],"derivedFrom":makeQuery(id+"FyYUAefgu6xEfva_4.1.F14.boolean.opBoolean","SPLIT",EDGE,{"disambiguationData":[TD([subQ6])],"derivedFrom":makeQuery(id+"F12.opExtrude","CAP_EDGE",EDGE,{"disambiguationData":[OSD([subQ1])],"isStart":true})})})})})})})})})})})})})})})})})})})})})})})})})})});}
            var Q572;
            Q572=makeQuery(id+"FyYUAefgu6xEfva_4.27.F14.opExtrude","CAP_EDGE",EDGE,{"disambiguationData":[OSD([sQuery(id+"F13.wireOp",EDGE,"E147")])],"isStart":true});
            var Q573;
            {var subQ0=sQuery(id+"F9.wireOp",EDGE,"E142");var subQ3=sQuery(id+"F13.wireOp",EDGE,"E147");var subQ4=sQuery(id+"F13.wireOp",EDGE,"E148.MirrorCS");var subQ5=makeQuery(id+"FyYUAefgu6xEfva_4.26.F14.opExtrude","SWEPT_FACE",FACE,{"disambiguationData":[OSD([subQ4])]});var subQ6=makeQuery(id+"F14.opExtrude","SWEPT_FACE",FACE,{"disambiguationData":[OSD([subQ3])]});Q573=makeQuery(id+"FyYUAefgu6xEfva_4.27.F14.boolean.opBoolean","SPLIT",EDGE,{"disambiguationData":[TD([subQ5])],"derivedFrom":makeQuery(id+"FyYUAefgu6xEfva_4.26.F14.boolean.opBoolean","SPLIT",EDGE,{"disambiguationData":[TD([subQ6])],"derivedFrom":makeQuery(id+"FyYUAefgu6xEfva_4.25.F14.boolean.opBoolean","SPLIT",EDGE,{"disambiguationData":[TD([subQ6])],"derivedFrom":makeQuery(id+"FyYUAefgu6xEfva_4.24.F14.boolean.opBoolean","SPLIT",EDGE,{"disambiguationData":[TD([subQ6])],"derivedFrom":makeQuery(id+"FyYUAefgu6xEfva_4.23.F14.boolean.opBoolean","SPLIT",EDGE,{"disambiguationData":[TD([subQ6])],"derivedFrom":makeQuery(id+"FyYUAefgu6xEfva_4.22.F14.boolean.opBoolean","SPLIT",EDGE,{"disambiguationData":[TD([subQ6])],"derivedFrom":makeQuery(id+"FyYUAefgu6xEfva_4.21.F14.boolean.opBoolean","SPLIT",EDGE,{"disambiguationData":[TD([subQ6])],"derivedFrom":makeQuery(id+"FyYUAefgu6xEfva_4.20.F14.boolean.opBoolean","SPLIT",EDGE,{"disambiguationData":[TD([subQ6])],"derivedFrom":makeQuery(id+"FyYUAefgu6xEfva_4.19.F14.boolean.opBoolean","SPLIT",EDGE,{"disambiguationData":[TD([subQ6])],"derivedFrom":makeQuery(id+"FyYUAefgu6xEfva_4.18.F14.boolean.opBoolean","SPLIT",EDGE,{"disambiguationData":[TD([subQ6])],"derivedFrom":makeQuery(id+"FyYUAefgu6xEfva_4.17.F14.boolean.opBoolean","SPLIT",EDGE,{"disambiguationData":[TD([subQ6])],"derivedFrom":makeQuery(id+"FyYUAefgu6xEfva_4.16.F14.boolean.opBoolean","SPLIT",EDGE,{"disambiguationData":[TD([subQ6])],"derivedFrom":makeQuery(id+"FyYUAefgu6xEfva_4.15.F14.boolean.opBoolean","SPLIT",EDGE,{"disambiguationData":[TD([subQ6])],"derivedFrom":makeQuery(id+"FyYUAefgu6xEfva_4.14.F14.boolean.opBoolean","SPLIT",EDGE,{"disambiguationData":[TD([subQ6])],"derivedFrom":makeQuery(id+"FyYUAefgu6xEfva_4.13.F14.boolean.opBoolean","SPLIT",EDGE,{"disambiguationData":[TD([subQ6])],"derivedFrom":makeQuery(id+"FyYUAefgu6xEfva_4.12.F14.boolean.opBoolean","SPLIT",EDGE,{"disambiguationData":[TD([subQ6])],"derivedFrom":makeQuery(id+"FyYUAefgu6xEfva_4.11.F14.boolean.opBoolean","SPLIT",EDGE,{"disambiguationData":[TD([subQ6])],"derivedFrom":makeQuery(id+"FyYUAefgu6xEfva_4.10.F14.boolean.opBoolean","SPLIT",EDGE,{"disambiguationData":[TD([subQ6])],"derivedFrom":makeQuery(id+"FyYUAefgu6xEfva_4.9.F14.boolean.opBoolean","SPLIT",EDGE,{"disambiguationData":[TD([subQ6])],"derivedFrom":makeQuery(id+"FyYUAefgu6xEfva_4.8.F14.boolean.opBoolean","SPLIT",EDGE,{"disambiguationData":[TD([subQ6])],"derivedFrom":makeQuery(id+"FyYUAefgu6xEfva_4.7.F14.boolean.opBoolean","SPLIT",EDGE,{"disambiguationData":[TD([subQ6])],"derivedFrom":makeQuery(id+"FyYUAefgu6xEfva_4.6.F14.boolean.opBoolean","SPLIT",EDGE,{"disambiguationData":[TD([subQ6])],"derivedFrom":makeQuery(id+"FyYUAefgu6xEfva_4.5.F14.boolean.opBoolean","SPLIT",EDGE,{"disambiguationData":[TD([subQ6])],"derivedFrom":makeQuery(id+"FyYUAefgu6xEfva_4.4.F14.boolean.opBoolean","SPLIT",EDGE,{"disambiguationData":[TD([subQ6])],"derivedFrom":makeQuery(id+"FyYUAefgu6xEfva_4.3.F14.boolean.opBoolean","SPLIT",EDGE,{"disambiguationData":[TD([subQ6])],"derivedFrom":makeQuery(id+"FyYUAefgu6xEfva_4.2.F14.boolean.opBoolean","SPLIT",EDGE,{"disambiguationData":[TD([subQ6])],"derivedFrom":makeQuery(id+"FyYUAefgu6xEfva_4.1.F14.boolean.opBoolean","SPLIT",EDGE,{"disambiguationData":[TD([subQ6])],"derivedFrom":makeQuery(id+"F10.boolean.opBoolean","COPY",EDGE,{"derivedFrom":makeQuery(id+"F10.opExtrude","CAP_EDGE",EDGE,{"disambiguationData":[OSD([subQ0])],"isStart":false})})})})})})})})})})})})})})})})})})})})})})})})})})})})});}
            var Q574;
            {var subQ1=sQuery(id+"F13.wireOp",EDGE,"E147");var subQ2=sQuery(id+"F11.wireOp",EDGE,"E143");var subQ4=sQuery(id+"F13.wireOp",EDGE,"E148.MirrorCS");var subQ5=makeQuery(id+"FyYUAefgu6xEfva_4.26.F14.opExtrude","SWEPT_FACE",FACE,{"disambiguationData":[OSD([subQ4])]});var subQ6=makeQuery(id+"F14.opExtrude","SWEPT_FACE",FACE,{"disambiguationData":[OSD([subQ1])]});Q574=makeQuery(id+"FyYUAefgu6xEfva_4.27.F14.boolean.opBoolean","SPLIT",EDGE,{"disambiguationData":[TD([subQ5])],"derivedFrom":makeQuery(id+"FyYUAefgu6xEfva_4.26.F14.boolean.opBoolean","SPLIT",EDGE,{"disambiguationData":[TD([subQ6])],"derivedFrom":makeQuery(id+"FyYUAefgu6xEfva_4.25.F14.boolean.opBoolean","SPLIT",EDGE,{"disambiguationData":[TD([subQ6])],"derivedFrom":makeQuery(id+"FyYUAefgu6xEfva_4.24.F14.boolean.opBoolean","SPLIT",EDGE,{"disambiguationData":[TD([subQ6])],"derivedFrom":makeQuery(id+"FyYUAefgu6xEfva_4.23.F14.boolean.opBoolean","SPLIT",EDGE,{"disambiguationData":[TD([subQ6])],"derivedFrom":makeQuery(id+"FyYUAefgu6xEfva_4.22.F14.boolean.opBoolean","SPLIT",EDGE,{"disambiguationData":[TD([subQ6])],"derivedFrom":makeQuery(id+"FyYUAefgu6xEfva_4.21.F14.boolean.opBoolean","SPLIT",EDGE,{"disambiguationData":[TD([subQ6])],"derivedFrom":makeQuery(id+"FyYUAefgu6xEfva_4.20.F14.boolean.opBoolean","SPLIT",EDGE,{"disambiguationData":[TD([subQ6])],"derivedFrom":makeQuery(id+"FyYUAefgu6xEfva_4.19.F14.boolean.opBoolean","SPLIT",EDGE,{"disambiguationData":[TD([subQ6])],"derivedFrom":makeQuery(id+"FyYUAefgu6xEfva_4.18.F14.boolean.opBoolean","SPLIT",EDGE,{"disambiguationData":[TD([subQ6])],"derivedFrom":makeQuery(id+"FyYUAefgu6xEfva_4.17.F14.boolean.opBoolean","SPLIT",EDGE,{"disambiguationData":[TD([subQ6])],"derivedFrom":makeQuery(id+"FyYUAefgu6xEfva_4.16.F14.boolean.opBoolean","SPLIT",EDGE,{"disambiguationData":[TD([subQ6])],"derivedFrom":makeQuery(id+"FyYUAefgu6xEfva_4.15.F14.boolean.opBoolean","SPLIT",EDGE,{"disambiguationData":[TD([subQ6])],"derivedFrom":makeQuery(id+"FyYUAefgu6xEfva_4.14.F14.boolean.opBoolean","SPLIT",EDGE,{"disambiguationData":[TD([subQ6])],"derivedFrom":makeQuery(id+"FyYUAefgu6xEfva_4.13.F14.boolean.opBoolean","SPLIT",EDGE,{"disambiguationData":[TD([subQ6])],"derivedFrom":makeQuery(id+"FyYUAefgu6xEfva_4.12.F14.boolean.opBoolean","SPLIT",EDGE,{"disambiguationData":[TD([subQ6])],"derivedFrom":makeQuery(id+"FyYUAefgu6xEfva_4.11.F14.boolean.opBoolean","SPLIT",EDGE,{"disambiguationData":[TD([subQ6])],"derivedFrom":makeQuery(id+"FyYUAefgu6xEfva_4.10.F14.boolean.opBoolean","SPLIT",EDGE,{"disambiguationData":[TD([subQ6])],"derivedFrom":makeQuery(id+"FyYUAefgu6xEfva_4.9.F14.boolean.opBoolean","SPLIT",EDGE,{"disambiguationData":[TD([subQ6])],"derivedFrom":makeQuery(id+"FyYUAefgu6xEfva_4.8.F14.boolean.opBoolean","SPLIT",EDGE,{"disambiguationData":[TD([subQ6])],"derivedFrom":makeQuery(id+"FyYUAefgu6xEfva_4.7.F14.boolean.opBoolean","SPLIT",EDGE,{"disambiguationData":[TD([subQ6])],"derivedFrom":makeQuery(id+"FyYUAefgu6xEfva_4.6.F14.boolean.opBoolean","SPLIT",EDGE,{"disambiguationData":[TD([subQ6])],"derivedFrom":makeQuery(id+"FyYUAefgu6xEfva_4.5.F14.boolean.opBoolean","SPLIT",EDGE,{"disambiguationData":[TD([subQ6])],"derivedFrom":makeQuery(id+"FyYUAefgu6xEfva_4.4.F14.boolean.opBoolean","SPLIT",EDGE,{"disambiguationData":[TD([subQ6])],"derivedFrom":makeQuery(id+"FyYUAefgu6xEfva_4.3.F14.boolean.opBoolean","SPLIT",EDGE,{"disambiguationData":[TD([subQ6])],"derivedFrom":makeQuery(id+"FyYUAefgu6xEfva_4.2.F14.boolean.opBoolean","SPLIT",EDGE,{"disambiguationData":[TD([subQ6])],"derivedFrom":makeQuery(id+"FyYUAefgu6xEfva_4.1.F14.boolean.opBoolean","SPLIT",EDGE,{"disambiguationData":[TD([subQ6])],"derivedFrom":makeQuery(id+"F12.opExtrude","CAP_EDGE",EDGE,{"disambiguationData":[OSD([subQ2])],"isStart":true})})})})})})})})})})})})})})})})})})})})})})})})})})})});}
            var Q575;
            {var subQ1=sQuery(id+"F13.wireOp",EDGE,"E148.MirrorCS");var subQ2=makeQuery(id+"FyYUAefgu6xEfva_4.28.F14.opExtrude","SWEPT_FACE",FACE,{"disambiguationData":[OSD([subQ1])]});var subQ3=sQuery(id+"F11.wireOp",EDGE,"E143");var subQ5=sQuery(id+"F13.wireOp",EDGE,"E147");var subQ6=makeQuery(id+"F14.opExtrude","SWEPT_FACE",FACE,{"disambiguationData":[OSD([subQ5])]});Q575=makeQuery(id+"FyYUAefgu6xEfva_4.29.F14.boolean.opBoolean","SPLIT",EDGE,{"disambiguationData":[TD([subQ2])],"derivedFrom":makeQuery(id+"FyYUAefgu6xEfva_4.28.F14.boolean.opBoolean","SPLIT",EDGE,{"disambiguationData":[TD([subQ6])],"derivedFrom":makeQuery(id+"FyYUAefgu6xEfva_4.27.F14.boolean.opBoolean","SPLIT",EDGE,{"disambiguationData":[TD([subQ6])],"derivedFrom":makeQuery(id+"FyYUAefgu6xEfva_4.26.F14.boolean.opBoolean","SPLIT",EDGE,{"disambiguationData":[TD([subQ6])],"derivedFrom":makeQuery(id+"FyYUAefgu6xEfva_4.25.F14.boolean.opBoolean","SPLIT",EDGE,{"disambiguationData":[TD([subQ6])],"derivedFrom":makeQuery(id+"FyYUAefgu6xEfva_4.24.F14.boolean.opBoolean","SPLIT",EDGE,{"disambiguationData":[TD([subQ6])],"derivedFrom":makeQuery(id+"FyYUAefgu6xEfva_4.23.F14.boolean.opBoolean","SPLIT",EDGE,{"disambiguationData":[TD([subQ6])],"derivedFrom":makeQuery(id+"FyYUAefgu6xEfva_4.22.F14.boolean.opBoolean","SPLIT",EDGE,{"disambiguationData":[TD([subQ6])],"derivedFrom":makeQuery(id+"FyYUAefgu6xEfva_4.21.F14.boolean.opBoolean","SPLIT",EDGE,{"disambiguationData":[TD([subQ6])],"derivedFrom":makeQuery(id+"FyYUAefgu6xEfva_4.20.F14.boolean.opBoolean","SPLIT",EDGE,{"disambiguationData":[TD([subQ6])],"derivedFrom":makeQuery(id+"FyYUAefgu6xEfva_4.19.F14.boolean.opBoolean","SPLIT",EDGE,{"disambiguationData":[TD([subQ6])],"derivedFrom":makeQuery(id+"FyYUAefgu6xEfva_4.18.F14.boolean.opBoolean","SPLIT",EDGE,{"disambiguationData":[TD([subQ6])],"derivedFrom":makeQuery(id+"FyYUAefgu6xEfva_4.17.F14.boolean.opBoolean","SPLIT",EDGE,{"disambiguationData":[TD([subQ6])],"derivedFrom":makeQuery(id+"FyYUAefgu6xEfva_4.16.F14.boolean.opBoolean","SPLIT",EDGE,{"disambiguationData":[TD([subQ6])],"derivedFrom":makeQuery(id+"FyYUAefgu6xEfva_4.15.F14.boolean.opBoolean","SPLIT",EDGE,{"disambiguationData":[TD([subQ6])],"derivedFrom":makeQuery(id+"FyYUAefgu6xEfva_4.14.F14.boolean.opBoolean","SPLIT",EDGE,{"disambiguationData":[TD([subQ6])],"derivedFrom":makeQuery(id+"FyYUAefgu6xEfva_4.13.F14.boolean.opBoolean","SPLIT",EDGE,{"disambiguationData":[TD([subQ6])],"derivedFrom":makeQuery(id+"FyYUAefgu6xEfva_4.12.F14.boolean.opBoolean","SPLIT",EDGE,{"disambiguationData":[TD([subQ6])],"derivedFrom":makeQuery(id+"FyYUAefgu6xEfva_4.11.F14.boolean.opBoolean","SPLIT",EDGE,{"disambiguationData":[TD([subQ6])],"derivedFrom":makeQuery(id+"FyYUAefgu6xEfva_4.10.F14.boolean.opBoolean","SPLIT",EDGE,{"disambiguationData":[TD([subQ6])],"derivedFrom":makeQuery(id+"FyYUAefgu6xEfva_4.9.F14.boolean.opBoolean","SPLIT",EDGE,{"disambiguationData":[TD([subQ6])],"derivedFrom":makeQuery(id+"FyYUAefgu6xEfva_4.8.F14.boolean.opBoolean","SPLIT",EDGE,{"disambiguationData":[TD([subQ6])],"derivedFrom":makeQuery(id+"FyYUAefgu6xEfva_4.7.F14.boolean.opBoolean","SPLIT",EDGE,{"disambiguationData":[TD([subQ6])],"derivedFrom":makeQuery(id+"FyYUAefgu6xEfva_4.6.F14.boolean.opBoolean","SPLIT",EDGE,{"disambiguationData":[TD([subQ6])],"derivedFrom":makeQuery(id+"FyYUAefgu6xEfva_4.5.F14.boolean.opBoolean","SPLIT",EDGE,{"disambiguationData":[TD([subQ6])],"derivedFrom":makeQuery(id+"FyYUAefgu6xEfva_4.4.F14.boolean.opBoolean","SPLIT",EDGE,{"disambiguationData":[TD([subQ6])],"derivedFrom":makeQuery(id+"FyYUAefgu6xEfva_4.3.F14.boolean.opBoolean","SPLIT",EDGE,{"disambiguationData":[TD([subQ6])],"derivedFrom":makeQuery(id+"FyYUAefgu6xEfva_4.2.F14.boolean.opBoolean","SPLIT",EDGE,{"disambiguationData":[TD([subQ6])],"derivedFrom":makeQuery(id+"FyYUAefgu6xEfva_4.1.F14.boolean.opBoolean","SPLIT",EDGE,{"disambiguationData":[TD([subQ6])],"derivedFrom":makeQuery(id+"F12.opExtrude","CAP_EDGE",EDGE,{"disambiguationData":[OSD([subQ3])],"isStart":true})})})})})})})})})})})})})})})})})})})})})})})})})})})})})});}
            var Q576;
            {var subQ1=sQuery(id+"F11.wireOp",EDGE,"E143");var subQ3=sQuery(id+"F13.wireOp",EDGE,"E148.MirrorCS");var subQ4=makeQuery(id+"FyYUAefgu6xEfva_4.29.F14.opExtrude","SWEPT_FACE",FACE,{"disambiguationData":[OSD([subQ3])]});var subQ5=sQuery(id+"F13.wireOp",EDGE,"E147");var subQ6=makeQuery(id+"F14.opExtrude","SWEPT_FACE",FACE,{"disambiguationData":[OSD([subQ5])]});Q576=makeQuery(id+"FyYUAefgu6xEfva_4.30.F14.boolean.opBoolean","SPLIT",EDGE,{"disambiguationData":[TD([subQ4])],"derivedFrom":makeQuery(id+"FyYUAefgu6xEfva_4.29.F14.boolean.opBoolean","SPLIT",EDGE,{"disambiguationData":[TD([subQ6])],"derivedFrom":makeQuery(id+"FyYUAefgu6xEfva_4.28.F14.boolean.opBoolean","SPLIT",EDGE,{"disambiguationData":[TD([subQ6])],"derivedFrom":makeQuery(id+"FyYUAefgu6xEfva_4.27.F14.boolean.opBoolean","SPLIT",EDGE,{"disambiguationData":[TD([subQ6])],"derivedFrom":makeQuery(id+"FyYUAefgu6xEfva_4.26.F14.boolean.opBoolean","SPLIT",EDGE,{"disambiguationData":[TD([subQ6])],"derivedFrom":makeQuery(id+"FyYUAefgu6xEfva_4.25.F14.boolean.opBoolean","SPLIT",EDGE,{"disambiguationData":[TD([subQ6])],"derivedFrom":makeQuery(id+"FyYUAefgu6xEfva_4.24.F14.boolean.opBoolean","SPLIT",EDGE,{"disambiguationData":[TD([subQ6])],"derivedFrom":makeQuery(id+"FyYUAefgu6xEfva_4.23.F14.boolean.opBoolean","SPLIT",EDGE,{"disambiguationData":[TD([subQ6])],"derivedFrom":makeQuery(id+"FyYUAefgu6xEfva_4.22.F14.boolean.opBoolean","SPLIT",EDGE,{"disambiguationData":[TD([subQ6])],"derivedFrom":makeQuery(id+"FyYUAefgu6xEfva_4.21.F14.boolean.opBoolean","SPLIT",EDGE,{"disambiguationData":[TD([subQ6])],"derivedFrom":makeQuery(id+"FyYUAefgu6xEfva_4.20.F14.boolean.opBoolean","SPLIT",EDGE,{"disambiguationData":[TD([subQ6])],"derivedFrom":makeQuery(id+"FyYUAefgu6xEfva_4.19.F14.boolean.opBoolean","SPLIT",EDGE,{"disambiguationData":[TD([subQ6])],"derivedFrom":makeQuery(id+"FyYUAefgu6xEfva_4.18.F14.boolean.opBoolean","SPLIT",EDGE,{"disambiguationData":[TD([subQ6])],"derivedFrom":makeQuery(id+"FyYUAefgu6xEfva_4.17.F14.boolean.opBoolean","SPLIT",EDGE,{"disambiguationData":[TD([subQ6])],"derivedFrom":makeQuery(id+"FyYUAefgu6xEfva_4.16.F14.boolean.opBoolean","SPLIT",EDGE,{"disambiguationData":[TD([subQ6])],"derivedFrom":makeQuery(id+"FyYUAefgu6xEfva_4.15.F14.boolean.opBoolean","SPLIT",EDGE,{"disambiguationData":[TD([subQ6])],"derivedFrom":makeQuery(id+"FyYUAefgu6xEfva_4.14.F14.boolean.opBoolean","SPLIT",EDGE,{"disambiguationData":[TD([subQ6])],"derivedFrom":makeQuery(id+"FyYUAefgu6xEfva_4.13.F14.boolean.opBoolean","SPLIT",EDGE,{"disambiguationData":[TD([subQ6])],"derivedFrom":makeQuery(id+"FyYUAefgu6xEfva_4.12.F14.boolean.opBoolean","SPLIT",EDGE,{"disambiguationData":[TD([subQ6])],"derivedFrom":makeQuery(id+"FyYUAefgu6xEfva_4.11.F14.boolean.opBoolean","SPLIT",EDGE,{"disambiguationData":[TD([subQ6])],"derivedFrom":makeQuery(id+"FyYUAefgu6xEfva_4.10.F14.boolean.opBoolean","SPLIT",EDGE,{"disambiguationData":[TD([subQ6])],"derivedFrom":makeQuery(id+"FyYUAefgu6xEfva_4.9.F14.boolean.opBoolean","SPLIT",EDGE,{"disambiguationData":[TD([subQ6])],"derivedFrom":makeQuery(id+"FyYUAefgu6xEfva_4.8.F14.boolean.opBoolean","SPLIT",EDGE,{"disambiguationData":[TD([subQ6])],"derivedFrom":makeQuery(id+"FyYUAefgu6xEfva_4.7.F14.boolean.opBoolean","SPLIT",EDGE,{"disambiguationData":[TD([subQ6])],"derivedFrom":makeQuery(id+"FyYUAefgu6xEfva_4.6.F14.boolean.opBoolean","SPLIT",EDGE,{"disambiguationData":[TD([subQ6])],"derivedFrom":makeQuery(id+"FyYUAefgu6xEfva_4.5.F14.boolean.opBoolean","SPLIT",EDGE,{"disambiguationData":[TD([subQ6])],"derivedFrom":makeQuery(id+"FyYUAefgu6xEfva_4.4.F14.boolean.opBoolean","SPLIT",EDGE,{"disambiguationData":[TD([subQ6])],"derivedFrom":makeQuery(id+"FyYUAefgu6xEfva_4.3.F14.boolean.opBoolean","SPLIT",EDGE,{"disambiguationData":[TD([subQ6])],"derivedFrom":makeQuery(id+"FyYUAefgu6xEfva_4.2.F14.boolean.opBoolean","SPLIT",EDGE,{"disambiguationData":[TD([subQ6])],"derivedFrom":makeQuery(id+"FyYUAefgu6xEfva_4.1.F14.boolean.opBoolean","SPLIT",EDGE,{"disambiguationData":[TD([subQ6])],"derivedFrom":makeQuery(id+"F12.opExtrude","CAP_EDGE",EDGE,{"disambiguationData":[OSD([subQ1])],"isStart":true})})})})})})})})})})})})})})})})})})})})})})})})})})})})})})});}
            var Q577;
            Q577=makeQuery(id+"FyYUAefgu6xEfva_4.31.F14.opExtrude","CAP_EDGE",EDGE,{"disambiguationData":[OSD([sQuery(id+"F13.wireOp",EDGE,"E147")])],"isStart":true});
            var Q578;
            Q578=makeQuery(id+"FyYUAefgu6xEfva_4.31.F14.opExtrude","CAP_EDGE",EDGE,{"disambiguationData":[OSD([sQuery(id+"F13.wireOp",EDGE,"E148.MirrorCS")])],"isStart":true});
            var Q579;
            {var subQ1=sQuery(id+"F11.wireOp",EDGE,"E143");var subQ3=sQuery(id+"F13.wireOp",EDGE,"E148.MirrorCS");var subQ4=makeQuery(id+"FyYUAefgu6xEfva_4.30.F14.opExtrude","SWEPT_FACE",FACE,{"disambiguationData":[OSD([subQ3])]});var subQ5=sQuery(id+"F13.wireOp",EDGE,"E147");var subQ6=makeQuery(id+"F14.opExtrude","SWEPT_FACE",FACE,{"disambiguationData":[OSD([subQ5])]});Q579=makeQuery(id+"FyYUAefgu6xEfva_4.31.F14.boolean.opBoolean","SPLIT",EDGE,{"disambiguationData":[TD([subQ4])],"derivedFrom":makeQuery(id+"FyYUAefgu6xEfva_4.30.F14.boolean.opBoolean","SPLIT",EDGE,{"disambiguationData":[TD([subQ6])],"derivedFrom":makeQuery(id+"FyYUAefgu6xEfva_4.29.F14.boolean.opBoolean","SPLIT",EDGE,{"disambiguationData":[TD([subQ6])],"derivedFrom":makeQuery(id+"FyYUAefgu6xEfva_4.28.F14.boolean.opBoolean","SPLIT",EDGE,{"disambiguationData":[TD([subQ6])],"derivedFrom":makeQuery(id+"FyYUAefgu6xEfva_4.27.F14.boolean.opBoolean","SPLIT",EDGE,{"disambiguationData":[TD([subQ6])],"derivedFrom":makeQuery(id+"FyYUAefgu6xEfva_4.26.F14.boolean.opBoolean","SPLIT",EDGE,{"disambiguationData":[TD([subQ6])],"derivedFrom":makeQuery(id+"FyYUAefgu6xEfva_4.25.F14.boolean.opBoolean","SPLIT",EDGE,{"disambiguationData":[TD([subQ6])],"derivedFrom":makeQuery(id+"FyYUAefgu6xEfva_4.24.F14.boolean.opBoolean","SPLIT",EDGE,{"disambiguationData":[TD([subQ6])],"derivedFrom":makeQuery(id+"FyYUAefgu6xEfva_4.23.F14.boolean.opBoolean","SPLIT",EDGE,{"disambiguationData":[TD([subQ6])],"derivedFrom":makeQuery(id+"FyYUAefgu6xEfva_4.22.F14.boolean.opBoolean","SPLIT",EDGE,{"disambiguationData":[TD([subQ6])],"derivedFrom":makeQuery(id+"FyYUAefgu6xEfva_4.21.F14.boolean.opBoolean","SPLIT",EDGE,{"disambiguationData":[TD([subQ6])],"derivedFrom":makeQuery(id+"FyYUAefgu6xEfva_4.20.F14.boolean.opBoolean","SPLIT",EDGE,{"disambiguationData":[TD([subQ6])],"derivedFrom":makeQuery(id+"FyYUAefgu6xEfva_4.19.F14.boolean.opBoolean","SPLIT",EDGE,{"disambiguationData":[TD([subQ6])],"derivedFrom":makeQuery(id+"FyYUAefgu6xEfva_4.18.F14.boolean.opBoolean","SPLIT",EDGE,{"disambiguationData":[TD([subQ6])],"derivedFrom":makeQuery(id+"FyYUAefgu6xEfva_4.17.F14.boolean.opBoolean","SPLIT",EDGE,{"disambiguationData":[TD([subQ6])],"derivedFrom":makeQuery(id+"FyYUAefgu6xEfva_4.16.F14.boolean.opBoolean","SPLIT",EDGE,{"disambiguationData":[TD([subQ6])],"derivedFrom":makeQuery(id+"FyYUAefgu6xEfva_4.15.F14.boolean.opBoolean","SPLIT",EDGE,{"disambiguationData":[TD([subQ6])],"derivedFrom":makeQuery(id+"FyYUAefgu6xEfva_4.14.F14.boolean.opBoolean","SPLIT",EDGE,{"disambiguationData":[TD([subQ6])],"derivedFrom":makeQuery(id+"FyYUAefgu6xEfva_4.13.F14.boolean.opBoolean","SPLIT",EDGE,{"disambiguationData":[TD([subQ6])],"derivedFrom":makeQuery(id+"FyYUAefgu6xEfva_4.12.F14.boolean.opBoolean","SPLIT",EDGE,{"disambiguationData":[TD([subQ6])],"derivedFrom":makeQuery(id+"FyYUAefgu6xEfva_4.11.F14.boolean.opBoolean","SPLIT",EDGE,{"disambiguationData":[TD([subQ6])],"derivedFrom":makeQuery(id+"FyYUAefgu6xEfva_4.10.F14.boolean.opBoolean","SPLIT",EDGE,{"disambiguationData":[TD([subQ6])],"derivedFrom":makeQuery(id+"FyYUAefgu6xEfva_4.9.F14.boolean.opBoolean","SPLIT",EDGE,{"disambiguationData":[TD([subQ6])],"derivedFrom":makeQuery(id+"FyYUAefgu6xEfva_4.8.F14.boolean.opBoolean","SPLIT",EDGE,{"disambiguationData":[TD([subQ6])],"derivedFrom":makeQuery(id+"FyYUAefgu6xEfva_4.7.F14.boolean.opBoolean","SPLIT",EDGE,{"disambiguationData":[TD([subQ6])],"derivedFrom":makeQuery(id+"FyYUAefgu6xEfva_4.6.F14.boolean.opBoolean","SPLIT",EDGE,{"disambiguationData":[TD([subQ6])],"derivedFrom":makeQuery(id+"FyYUAefgu6xEfva_4.5.F14.boolean.opBoolean","SPLIT",EDGE,{"disambiguationData":[TD([subQ6])],"derivedFrom":makeQuery(id+"FyYUAefgu6xEfva_4.4.F14.boolean.opBoolean","SPLIT",EDGE,{"disambiguationData":[TD([subQ6])],"derivedFrom":makeQuery(id+"FyYUAefgu6xEfva_4.3.F14.boolean.opBoolean","SPLIT",EDGE,{"disambiguationData":[TD([subQ6])],"derivedFrom":makeQuery(id+"FyYUAefgu6xEfva_4.2.F14.boolean.opBoolean","SPLIT",EDGE,{"disambiguationData":[TD([subQ6])],"derivedFrom":makeQuery(id+"FyYUAefgu6xEfva_4.1.F14.boolean.opBoolean","SPLIT",EDGE,{"disambiguationData":[TD([subQ6])],"derivedFrom":makeQuery(id+"F12.opExtrude","CAP_EDGE",EDGE,{"disambiguationData":[OSD([subQ1])],"isStart":true})})})})})})})})})})})})})})})})})})})})})})})})})})})})})})})});}
            var Q580;
            {var subQ0=sQuery(id+"F9.wireOp",EDGE,"E142");var subQ3=sQuery(id+"F13.wireOp",EDGE,"E147");var subQ4=sQuery(id+"F13.wireOp",EDGE,"E148.MirrorCS");var subQ5=makeQuery(id+"FyYUAefgu6xEfva_4.31.F14.opExtrude","SWEPT_FACE",FACE,{"disambiguationData":[OSD([subQ4])]});var subQ6=makeQuery(id+"F14.opExtrude","SWEPT_FACE",FACE,{"disambiguationData":[OSD([subQ3])]});Q580=makeQuery(id+"FyYUAefgu6xEfva_4.32.F14.boolean.opBoolean","SPLIT",EDGE,{"disambiguationData":[TD([subQ5])],"derivedFrom":makeQuery(id+"FyYUAefgu6xEfva_4.31.F14.boolean.opBoolean","SPLIT",EDGE,{"disambiguationData":[TD([subQ6])],"derivedFrom":makeQuery(id+"FyYUAefgu6xEfva_4.30.F14.boolean.opBoolean","SPLIT",EDGE,{"disambiguationData":[TD([subQ6])],"derivedFrom":makeQuery(id+"FyYUAefgu6xEfva_4.29.F14.boolean.opBoolean","SPLIT",EDGE,{"disambiguationData":[TD([subQ6])],"derivedFrom":makeQuery(id+"FyYUAefgu6xEfva_4.28.F14.boolean.opBoolean","SPLIT",EDGE,{"disambiguationData":[TD([subQ6])],"derivedFrom":makeQuery(id+"FyYUAefgu6xEfva_4.27.F14.boolean.opBoolean","SPLIT",EDGE,{"disambiguationData":[TD([subQ6])],"derivedFrom":makeQuery(id+"FyYUAefgu6xEfva_4.26.F14.boolean.opBoolean","SPLIT",EDGE,{"disambiguationData":[TD([subQ6])],"derivedFrom":makeQuery(id+"FyYUAefgu6xEfva_4.25.F14.boolean.opBoolean","SPLIT",EDGE,{"disambiguationData":[TD([subQ6])],"derivedFrom":makeQuery(id+"FyYUAefgu6xEfva_4.24.F14.boolean.opBoolean","SPLIT",EDGE,{"disambiguationData":[TD([subQ6])],"derivedFrom":makeQuery(id+"FyYUAefgu6xEfva_4.23.F14.boolean.opBoolean","SPLIT",EDGE,{"disambiguationData":[TD([subQ6])],"derivedFrom":makeQuery(id+"FyYUAefgu6xEfva_4.22.F14.boolean.opBoolean","SPLIT",EDGE,{"disambiguationData":[TD([subQ6])],"derivedFrom":makeQuery(id+"FyYUAefgu6xEfva_4.21.F14.boolean.opBoolean","SPLIT",EDGE,{"disambiguationData":[TD([subQ6])],"derivedFrom":makeQuery(id+"FyYUAefgu6xEfva_4.20.F14.boolean.opBoolean","SPLIT",EDGE,{"disambiguationData":[TD([subQ6])],"derivedFrom":makeQuery(id+"FyYUAefgu6xEfva_4.19.F14.boolean.opBoolean","SPLIT",EDGE,{"disambiguationData":[TD([subQ6])],"derivedFrom":makeQuery(id+"FyYUAefgu6xEfva_4.18.F14.boolean.opBoolean","SPLIT",EDGE,{"disambiguationData":[TD([subQ6])],"derivedFrom":makeQuery(id+"FyYUAefgu6xEfva_4.17.F14.boolean.opBoolean","SPLIT",EDGE,{"disambiguationData":[TD([subQ6])],"derivedFrom":makeQuery(id+"FyYUAefgu6xEfva_4.16.F14.boolean.opBoolean","SPLIT",EDGE,{"disambiguationData":[TD([subQ6])],"derivedFrom":makeQuery(id+"FyYUAefgu6xEfva_4.15.F14.boolean.opBoolean","SPLIT",EDGE,{"disambiguationData":[TD([subQ6])],"derivedFrom":makeQuery(id+"FyYUAefgu6xEfva_4.14.F14.boolean.opBoolean","SPLIT",EDGE,{"disambiguationData":[TD([subQ6])],"derivedFrom":makeQuery(id+"FyYUAefgu6xEfva_4.13.F14.boolean.opBoolean","SPLIT",EDGE,{"disambiguationData":[TD([subQ6])],"derivedFrom":makeQuery(id+"FyYUAefgu6xEfva_4.12.F14.boolean.opBoolean","SPLIT",EDGE,{"disambiguationData":[TD([subQ6])],"derivedFrom":makeQuery(id+"FyYUAefgu6xEfva_4.11.F14.boolean.opBoolean","SPLIT",EDGE,{"disambiguationData":[TD([subQ6])],"derivedFrom":makeQuery(id+"FyYUAefgu6xEfva_4.10.F14.boolean.opBoolean","SPLIT",EDGE,{"disambiguationData":[TD([subQ6])],"derivedFrom":makeQuery(id+"FyYUAefgu6xEfva_4.9.F14.boolean.opBoolean","SPLIT",EDGE,{"disambiguationData":[TD([subQ6])],"derivedFrom":makeQuery(id+"FyYUAefgu6xEfva_4.8.F14.boolean.opBoolean","SPLIT",EDGE,{"disambiguationData":[TD([subQ6])],"derivedFrom":makeQuery(id+"FyYUAefgu6xEfva_4.7.F14.boolean.opBoolean","SPLIT",EDGE,{"disambiguationData":[TD([subQ6])],"derivedFrom":makeQuery(id+"FyYUAefgu6xEfva_4.6.F14.boolean.opBoolean","SPLIT",EDGE,{"disambiguationData":[TD([subQ6])],"derivedFrom":makeQuery(id+"FyYUAefgu6xEfva_4.5.F14.boolean.opBoolean","SPLIT",EDGE,{"disambiguationData":[TD([subQ6])],"derivedFrom":makeQuery(id+"FyYUAefgu6xEfva_4.4.F14.boolean.opBoolean","SPLIT",EDGE,{"disambiguationData":[TD([subQ6])],"derivedFrom":makeQuery(id+"FyYUAefgu6xEfva_4.3.F14.boolean.opBoolean","SPLIT",EDGE,{"disambiguationData":[TD([subQ6])],"derivedFrom":makeQuery(id+"FyYUAefgu6xEfva_4.2.F14.boolean.opBoolean","SPLIT",EDGE,{"disambiguationData":[TD([subQ6])],"derivedFrom":makeQuery(id+"FyYUAefgu6xEfva_4.1.F14.boolean.opBoolean","SPLIT",EDGE,{"disambiguationData":[TD([subQ6])],"derivedFrom":makeQuery(id+"F10.boolean.opBoolean","COPY",EDGE,{"derivedFrom":makeQuery(id+"F10.opExtrude","CAP_EDGE",EDGE,{"disambiguationData":[OSD([subQ0])],"isStart":false})})})})})})})})})})})})})})})})})})})})})})})})})})})})})})})})})});}
            var Q581;
            {var subQ1=sQuery(id+"F13.wireOp",EDGE,"E147");var subQ2=sQuery(id+"F11.wireOp",EDGE,"E143");var subQ4=sQuery(id+"F13.wireOp",EDGE,"E148.MirrorCS");var subQ5=makeQuery(id+"FyYUAefgu6xEfva_4.31.F14.opExtrude","SWEPT_FACE",FACE,{"disambiguationData":[OSD([subQ4])]});var subQ6=makeQuery(id+"F14.opExtrude","SWEPT_FACE",FACE,{"disambiguationData":[OSD([subQ1])]});Q581=makeQuery(id+"FyYUAefgu6xEfva_4.32.F14.boolean.opBoolean","SPLIT",EDGE,{"disambiguationData":[TD([subQ5])],"derivedFrom":makeQuery(id+"FyYUAefgu6xEfva_4.31.F14.boolean.opBoolean","SPLIT",EDGE,{"disambiguationData":[TD([subQ6])],"derivedFrom":makeQuery(id+"FyYUAefgu6xEfva_4.30.F14.boolean.opBoolean","SPLIT",EDGE,{"disambiguationData":[TD([subQ6])],"derivedFrom":makeQuery(id+"FyYUAefgu6xEfva_4.29.F14.boolean.opBoolean","SPLIT",EDGE,{"disambiguationData":[TD([subQ6])],"derivedFrom":makeQuery(id+"FyYUAefgu6xEfva_4.28.F14.boolean.opBoolean","SPLIT",EDGE,{"disambiguationData":[TD([subQ6])],"derivedFrom":makeQuery(id+"FyYUAefgu6xEfva_4.27.F14.boolean.opBoolean","SPLIT",EDGE,{"disambiguationData":[TD([subQ6])],"derivedFrom":makeQuery(id+"FyYUAefgu6xEfva_4.26.F14.boolean.opBoolean","SPLIT",EDGE,{"disambiguationData":[TD([subQ6])],"derivedFrom":makeQuery(id+"FyYUAefgu6xEfva_4.25.F14.boolean.opBoolean","SPLIT",EDGE,{"disambiguationData":[TD([subQ6])],"derivedFrom":makeQuery(id+"FyYUAefgu6xEfva_4.24.F14.boolean.opBoolean","SPLIT",EDGE,{"disambiguationData":[TD([subQ6])],"derivedFrom":makeQuery(id+"FyYUAefgu6xEfva_4.23.F14.boolean.opBoolean","SPLIT",EDGE,{"disambiguationData":[TD([subQ6])],"derivedFrom":makeQuery(id+"FyYUAefgu6xEfva_4.22.F14.boolean.opBoolean","SPLIT",EDGE,{"disambiguationData":[TD([subQ6])],"derivedFrom":makeQuery(id+"FyYUAefgu6xEfva_4.21.F14.boolean.opBoolean","SPLIT",EDGE,{"disambiguationData":[TD([subQ6])],"derivedFrom":makeQuery(id+"FyYUAefgu6xEfva_4.20.F14.boolean.opBoolean","SPLIT",EDGE,{"disambiguationData":[TD([subQ6])],"derivedFrom":makeQuery(id+"FyYUAefgu6xEfva_4.19.F14.boolean.opBoolean","SPLIT",EDGE,{"disambiguationData":[TD([subQ6])],"derivedFrom":makeQuery(id+"FyYUAefgu6xEfva_4.18.F14.boolean.opBoolean","SPLIT",EDGE,{"disambiguationData":[TD([subQ6])],"derivedFrom":makeQuery(id+"FyYUAefgu6xEfva_4.17.F14.boolean.opBoolean","SPLIT",EDGE,{"disambiguationData":[TD([subQ6])],"derivedFrom":makeQuery(id+"FyYUAefgu6xEfva_4.16.F14.boolean.opBoolean","SPLIT",EDGE,{"disambiguationData":[TD([subQ6])],"derivedFrom":makeQuery(id+"FyYUAefgu6xEfva_4.15.F14.boolean.opBoolean","SPLIT",EDGE,{"disambiguationData":[TD([subQ6])],"derivedFrom":makeQuery(id+"FyYUAefgu6xEfva_4.14.F14.boolean.opBoolean","SPLIT",EDGE,{"disambiguationData":[TD([subQ6])],"derivedFrom":makeQuery(id+"FyYUAefgu6xEfva_4.13.F14.boolean.opBoolean","SPLIT",EDGE,{"disambiguationData":[TD([subQ6])],"derivedFrom":makeQuery(id+"FyYUAefgu6xEfva_4.12.F14.boolean.opBoolean","SPLIT",EDGE,{"disambiguationData":[TD([subQ6])],"derivedFrom":makeQuery(id+"FyYUAefgu6xEfva_4.11.F14.boolean.opBoolean","SPLIT",EDGE,{"disambiguationData":[TD([subQ6])],"derivedFrom":makeQuery(id+"FyYUAefgu6xEfva_4.10.F14.boolean.opBoolean","SPLIT",EDGE,{"disambiguationData":[TD([subQ6])],"derivedFrom":makeQuery(id+"FyYUAefgu6xEfva_4.9.F14.boolean.opBoolean","SPLIT",EDGE,{"disambiguationData":[TD([subQ6])],"derivedFrom":makeQuery(id+"FyYUAefgu6xEfva_4.8.F14.boolean.opBoolean","SPLIT",EDGE,{"disambiguationData":[TD([subQ6])],"derivedFrom":makeQuery(id+"FyYUAefgu6xEfva_4.7.F14.boolean.opBoolean","SPLIT",EDGE,{"disambiguationData":[TD([subQ6])],"derivedFrom":makeQuery(id+"FyYUAefgu6xEfva_4.6.F14.boolean.opBoolean","SPLIT",EDGE,{"disambiguationData":[TD([subQ6])],"derivedFrom":makeQuery(id+"FyYUAefgu6xEfva_4.5.F14.boolean.opBoolean","SPLIT",EDGE,{"disambiguationData":[TD([subQ6])],"derivedFrom":makeQuery(id+"FyYUAefgu6xEfva_4.4.F14.boolean.opBoolean","SPLIT",EDGE,{"disambiguationData":[TD([subQ6])],"derivedFrom":makeQuery(id+"FyYUAefgu6xEfva_4.3.F14.boolean.opBoolean","SPLIT",EDGE,{"disambiguationData":[TD([subQ6])],"derivedFrom":makeQuery(id+"FyYUAefgu6xEfva_4.2.F14.boolean.opBoolean","SPLIT",EDGE,{"disambiguationData":[TD([subQ6])],"derivedFrom":makeQuery(id+"FyYUAefgu6xEfva_4.1.F14.boolean.opBoolean","SPLIT",EDGE,{"disambiguationData":[TD([subQ6])],"derivedFrom":makeQuery(id+"F12.opExtrude","CAP_EDGE",EDGE,{"disambiguationData":[OSD([subQ2])],"isStart":true})})})})})})})})})})})})})})})})})})})})})})})})})})})})})})})})});}
            var Q582;
            Q582=makeQuery(id+"FyYUAefgu6xEfva_4.33.F14.opExtrude","CAP_EDGE",EDGE,{"disambiguationData":[OSD([sQuery(id+"F13.wireOp",EDGE,"E147")])],"isStart":true});
            var Q583;
            Q583=makeQuery(id+"FyYUAefgu6xEfva_4.33.F14.opExtrude","CAP_EDGE",EDGE,{"disambiguationData":[OSD([sQuery(id+"F13.wireOp",EDGE,"E148.MirrorCS")])],"isStart":true});
            var Q584;
            {var subQ1=sQuery(id+"F11.wireOp",EDGE,"E143");var subQ3=sQuery(id+"F13.wireOp",EDGE,"E147");var subQ4=sQuery(id+"F13.wireOp",EDGE,"E148.MirrorCS");var subQ5=makeQuery(id+"FyYUAefgu6xEfva_4.32.F14.opExtrude","SWEPT_FACE",FACE,{"disambiguationData":[OSD([subQ4])]});var subQ6=makeQuery(id+"F14.opExtrude","SWEPT_FACE",FACE,{"disambiguationData":[OSD([subQ3])]});Q584=makeQuery(id+"FyYUAefgu6xEfva_4.33.F14.boolean.opBoolean","SPLIT",EDGE,{"disambiguationData":[TD([subQ5])],"derivedFrom":makeQuery(id+"FyYUAefgu6xEfva_4.32.F14.boolean.opBoolean","SPLIT",EDGE,{"disambiguationData":[TD([subQ6])],"derivedFrom":makeQuery(id+"FyYUAefgu6xEfva_4.31.F14.boolean.opBoolean","SPLIT",EDGE,{"disambiguationData":[TD([subQ6])],"derivedFrom":makeQuery(id+"FyYUAefgu6xEfva_4.30.F14.boolean.opBoolean","SPLIT",EDGE,{"disambiguationData":[TD([subQ6])],"derivedFrom":makeQuery(id+"FyYUAefgu6xEfva_4.29.F14.boolean.opBoolean","SPLIT",EDGE,{"disambiguationData":[TD([subQ6])],"derivedFrom":makeQuery(id+"FyYUAefgu6xEfva_4.28.F14.boolean.opBoolean","SPLIT",EDGE,{"disambiguationData":[TD([subQ6])],"derivedFrom":makeQuery(id+"FyYUAefgu6xEfva_4.27.F14.boolean.opBoolean","SPLIT",EDGE,{"disambiguationData":[TD([subQ6])],"derivedFrom":makeQuery(id+"FyYUAefgu6xEfva_4.26.F14.boolean.opBoolean","SPLIT",EDGE,{"disambiguationData":[TD([subQ6])],"derivedFrom":makeQuery(id+"FyYUAefgu6xEfva_4.25.F14.boolean.opBoolean","SPLIT",EDGE,{"disambiguationData":[TD([subQ6])],"derivedFrom":makeQuery(id+"FyYUAefgu6xEfva_4.24.F14.boolean.opBoolean","SPLIT",EDGE,{"disambiguationData":[TD([subQ6])],"derivedFrom":makeQuery(id+"FyYUAefgu6xEfva_4.23.F14.boolean.opBoolean","SPLIT",EDGE,{"disambiguationData":[TD([subQ6])],"derivedFrom":makeQuery(id+"FyYUAefgu6xEfva_4.22.F14.boolean.opBoolean","SPLIT",EDGE,{"disambiguationData":[TD([subQ6])],"derivedFrom":makeQuery(id+"FyYUAefgu6xEfva_4.21.F14.boolean.opBoolean","SPLIT",EDGE,{"disambiguationData":[TD([subQ6])],"derivedFrom":makeQuery(id+"FyYUAefgu6xEfva_4.20.F14.boolean.opBoolean","SPLIT",EDGE,{"disambiguationData":[TD([subQ6])],"derivedFrom":makeQuery(id+"FyYUAefgu6xEfva_4.19.F14.boolean.opBoolean","SPLIT",EDGE,{"disambiguationData":[TD([subQ6])],"derivedFrom":makeQuery(id+"FyYUAefgu6xEfva_4.18.F14.boolean.opBoolean","SPLIT",EDGE,{"disambiguationData":[TD([subQ6])],"derivedFrom":makeQuery(id+"FyYUAefgu6xEfva_4.17.F14.boolean.opBoolean","SPLIT",EDGE,{"disambiguationData":[TD([subQ6])],"derivedFrom":makeQuery(id+"FyYUAefgu6xEfva_4.16.F14.boolean.opBoolean","SPLIT",EDGE,{"disambiguationData":[TD([subQ6])],"derivedFrom":makeQuery(id+"FyYUAefgu6xEfva_4.15.F14.boolean.opBoolean","SPLIT",EDGE,{"disambiguationData":[TD([subQ6])],"derivedFrom":makeQuery(id+"FyYUAefgu6xEfva_4.14.F14.boolean.opBoolean","SPLIT",EDGE,{"disambiguationData":[TD([subQ6])],"derivedFrom":makeQuery(id+"FyYUAefgu6xEfva_4.13.F14.boolean.opBoolean","SPLIT",EDGE,{"disambiguationData":[TD([subQ6])],"derivedFrom":makeQuery(id+"FyYUAefgu6xEfva_4.12.F14.boolean.opBoolean","SPLIT",EDGE,{"disambiguationData":[TD([subQ6])],"derivedFrom":makeQuery(id+"FyYUAefgu6xEfva_4.11.F14.boolean.opBoolean","SPLIT",EDGE,{"disambiguationData":[TD([subQ6])],"derivedFrom":makeQuery(id+"FyYUAefgu6xEfva_4.10.F14.boolean.opBoolean","SPLIT",EDGE,{"disambiguationData":[TD([subQ6])],"derivedFrom":makeQuery(id+"FyYUAefgu6xEfva_4.9.F14.boolean.opBoolean","SPLIT",EDGE,{"disambiguationData":[TD([subQ6])],"derivedFrom":makeQuery(id+"FyYUAefgu6xEfva_4.8.F14.boolean.opBoolean","SPLIT",EDGE,{"disambiguationData":[TD([subQ6])],"derivedFrom":makeQuery(id+"FyYUAefgu6xEfva_4.7.F14.boolean.opBoolean","SPLIT",EDGE,{"disambiguationData":[TD([subQ6])],"derivedFrom":makeQuery(id+"FyYUAefgu6xEfva_4.6.F14.boolean.opBoolean","SPLIT",EDGE,{"disambiguationData":[TD([subQ6])],"derivedFrom":makeQuery(id+"FyYUAefgu6xEfva_4.5.F14.boolean.opBoolean","SPLIT",EDGE,{"disambiguationData":[TD([subQ6])],"derivedFrom":makeQuery(id+"FyYUAefgu6xEfva_4.4.F14.boolean.opBoolean","SPLIT",EDGE,{"disambiguationData":[TD([subQ6])],"derivedFrom":makeQuery(id+"FyYUAefgu6xEfva_4.3.F14.boolean.opBoolean","SPLIT",EDGE,{"disambiguationData":[TD([subQ6])],"derivedFrom":makeQuery(id+"FyYUAefgu6xEfva_4.2.F14.boolean.opBoolean","SPLIT",EDGE,{"disambiguationData":[TD([subQ6])],"derivedFrom":makeQuery(id+"FyYUAefgu6xEfva_4.1.F14.boolean.opBoolean","SPLIT",EDGE,{"disambiguationData":[TD([subQ6])],"derivedFrom":makeQuery(id+"F12.opExtrude","CAP_EDGE",EDGE,{"disambiguationData":[OSD([subQ1])],"isStart":true})})})})})})})})})})})})})})})})})})})})})})})})})})})})})})})})})});}
            var Q585;
            Q585=makeQuery(id+"FyYUAefgu6xEfva_4.34.F14.opExtrude","SWEPT_EDGE",EDGE,{"disambiguationData":[OSD([sQuery(id+"F11.wireOp",EDGE,"E143"),sQuery(id+"F13.wireOp",EDGE,"E147")])]});
            var Q586;
            {var subQ0=sQuery(id+"F9.wireOp",EDGE,"E142");var subQ2=sQuery(id+"F13.wireOp",EDGE,"E147");var subQ4=sQuery(id+"F13.wireOp",EDGE,"E148.MirrorCS");var subQ5=makeQuery(id+"FyYUAefgu6xEfva_4.33.F14.opExtrude","SWEPT_FACE",FACE,{"disambiguationData":[OSD([subQ4])]});var subQ6=makeQuery(id+"F14.opExtrude","SWEPT_FACE",FACE,{"disambiguationData":[OSD([subQ2])]});Q586=makeQuery(id+"FyYUAefgu6xEfva_4.34.F14.boolean.opBoolean","SPLIT",EDGE,{"disambiguationData":[TD([subQ5])],"derivedFrom":makeQuery(id+"FyYUAefgu6xEfva_4.33.F14.boolean.opBoolean","SPLIT",EDGE,{"disambiguationData":[TD([subQ6])],"derivedFrom":makeQuery(id+"FyYUAefgu6xEfva_4.32.F14.boolean.opBoolean","SPLIT",EDGE,{"disambiguationData":[TD([subQ6])],"derivedFrom":makeQuery(id+"FyYUAefgu6xEfva_4.31.F14.boolean.opBoolean","SPLIT",EDGE,{"disambiguationData":[TD([subQ6])],"derivedFrom":makeQuery(id+"FyYUAefgu6xEfva_4.30.F14.boolean.opBoolean","SPLIT",EDGE,{"disambiguationData":[TD([subQ6])],"derivedFrom":makeQuery(id+"FyYUAefgu6xEfva_4.29.F14.boolean.opBoolean","SPLIT",EDGE,{"disambiguationData":[TD([subQ6])],"derivedFrom":makeQuery(id+"FyYUAefgu6xEfva_4.28.F14.boolean.opBoolean","SPLIT",EDGE,{"disambiguationData":[TD([subQ6])],"derivedFrom":makeQuery(id+"FyYUAefgu6xEfva_4.27.F14.boolean.opBoolean","SPLIT",EDGE,{"disambiguationData":[TD([subQ6])],"derivedFrom":makeQuery(id+"FyYUAefgu6xEfva_4.26.F14.boolean.opBoolean","SPLIT",EDGE,{"disambiguationData":[TD([subQ6])],"derivedFrom":makeQuery(id+"FyYUAefgu6xEfva_4.25.F14.boolean.opBoolean","SPLIT",EDGE,{"disambiguationData":[TD([subQ6])],"derivedFrom":makeQuery(id+"FyYUAefgu6xEfva_4.24.F14.boolean.opBoolean","SPLIT",EDGE,{"disambiguationData":[TD([subQ6])],"derivedFrom":makeQuery(id+"FyYUAefgu6xEfva_4.23.F14.boolean.opBoolean","SPLIT",EDGE,{"disambiguationData":[TD([subQ6])],"derivedFrom":makeQuery(id+"FyYUAefgu6xEfva_4.22.F14.boolean.opBoolean","SPLIT",EDGE,{"disambiguationData":[TD([subQ6])],"derivedFrom":makeQuery(id+"FyYUAefgu6xEfva_4.21.F14.boolean.opBoolean","SPLIT",EDGE,{"disambiguationData":[TD([subQ6])],"derivedFrom":makeQuery(id+"FyYUAefgu6xEfva_4.20.F14.boolean.opBoolean","SPLIT",EDGE,{"disambiguationData":[TD([subQ6])],"derivedFrom":makeQuery(id+"FyYUAefgu6xEfva_4.19.F14.boolean.opBoolean","SPLIT",EDGE,{"disambiguationData":[TD([subQ6])],"derivedFrom":makeQuery(id+"FyYUAefgu6xEfva_4.18.F14.boolean.opBoolean","SPLIT",EDGE,{"disambiguationData":[TD([subQ6])],"derivedFrom":makeQuery(id+"FyYUAefgu6xEfva_4.17.F14.boolean.opBoolean","SPLIT",EDGE,{"disambiguationData":[TD([subQ6])],"derivedFrom":makeQuery(id+"FyYUAefgu6xEfva_4.16.F14.boolean.opBoolean","SPLIT",EDGE,{"disambiguationData":[TD([subQ6])],"derivedFrom":makeQuery(id+"FyYUAefgu6xEfva_4.15.F14.boolean.opBoolean","SPLIT",EDGE,{"disambiguationData":[TD([subQ6])],"derivedFrom":makeQuery(id+"FyYUAefgu6xEfva_4.14.F14.boolean.opBoolean","SPLIT",EDGE,{"disambiguationData":[TD([subQ6])],"derivedFrom":makeQuery(id+"FyYUAefgu6xEfva_4.13.F14.boolean.opBoolean","SPLIT",EDGE,{"disambiguationData":[TD([subQ6])],"derivedFrom":makeQuery(id+"FyYUAefgu6xEfva_4.12.F14.boolean.opBoolean","SPLIT",EDGE,{"disambiguationData":[TD([subQ6])],"derivedFrom":makeQuery(id+"FyYUAefgu6xEfva_4.11.F14.boolean.opBoolean","SPLIT",EDGE,{"disambiguationData":[TD([subQ6])],"derivedFrom":makeQuery(id+"FyYUAefgu6xEfva_4.10.F14.boolean.opBoolean","SPLIT",EDGE,{"disambiguationData":[TD([subQ6])],"derivedFrom":makeQuery(id+"FyYUAefgu6xEfva_4.9.F14.boolean.opBoolean","SPLIT",EDGE,{"disambiguationData":[TD([subQ6])],"derivedFrom":makeQuery(id+"FyYUAefgu6xEfva_4.8.F14.boolean.opBoolean","SPLIT",EDGE,{"disambiguationData":[TD([subQ6])],"derivedFrom":makeQuery(id+"FyYUAefgu6xEfva_4.7.F14.boolean.opBoolean","SPLIT",EDGE,{"disambiguationData":[TD([subQ6])],"derivedFrom":makeQuery(id+"FyYUAefgu6xEfva_4.6.F14.boolean.opBoolean","SPLIT",EDGE,{"disambiguationData":[TD([subQ6])],"derivedFrom":makeQuery(id+"FyYUAefgu6xEfva_4.5.F14.boolean.opBoolean","SPLIT",EDGE,{"disambiguationData":[TD([subQ6])],"derivedFrom":makeQuery(id+"FyYUAefgu6xEfva_4.4.F14.boolean.opBoolean","SPLIT",EDGE,{"disambiguationData":[TD([subQ6])],"derivedFrom":makeQuery(id+"FyYUAefgu6xEfva_4.3.F14.boolean.opBoolean","SPLIT",EDGE,{"disambiguationData":[TD([subQ6])],"derivedFrom":makeQuery(id+"FyYUAefgu6xEfva_4.2.F14.boolean.opBoolean","SPLIT",EDGE,{"disambiguationData":[TD([subQ6])],"derivedFrom":makeQuery(id+"FyYUAefgu6xEfva_4.1.F14.boolean.opBoolean","SPLIT",EDGE,{"disambiguationData":[TD([subQ6])],"derivedFrom":makeQuery(id+"F10.boolean.opBoolean","COPY",EDGE,{"derivedFrom":makeQuery(id+"F10.opExtrude","CAP_EDGE",EDGE,{"disambiguationData":[OSD([subQ0])],"isStart":false})})})})})})})})})})})})})})})})})})})})})})})})})})})})})})})})})})})});}
            var Q587;
            {var subQ1=sQuery(id+"F13.wireOp",EDGE,"E148.MirrorCS");var subQ2=makeQuery(id+"FyYUAefgu6xEfva_4.33.F14.opExtrude","SWEPT_FACE",FACE,{"disambiguationData":[OSD([subQ1])]});var subQ3=sQuery(id+"F11.wireOp",EDGE,"E143");var subQ5=sQuery(id+"F13.wireOp",EDGE,"E147");var subQ6=makeQuery(id+"F14.opExtrude","SWEPT_FACE",FACE,{"disambiguationData":[OSD([subQ5])]});Q587=makeQuery(id+"FyYUAefgu6xEfva_4.34.F14.boolean.opBoolean","SPLIT",EDGE,{"disambiguationData":[TD([subQ2])],"derivedFrom":makeQuery(id+"FyYUAefgu6xEfva_4.33.F14.boolean.opBoolean","SPLIT",EDGE,{"disambiguationData":[TD([subQ6])],"derivedFrom":makeQuery(id+"FyYUAefgu6xEfva_4.32.F14.boolean.opBoolean","SPLIT",EDGE,{"disambiguationData":[TD([subQ6])],"derivedFrom":makeQuery(id+"FyYUAefgu6xEfva_4.31.F14.boolean.opBoolean","SPLIT",EDGE,{"disambiguationData":[TD([subQ6])],"derivedFrom":makeQuery(id+"FyYUAefgu6xEfva_4.30.F14.boolean.opBoolean","SPLIT",EDGE,{"disambiguationData":[TD([subQ6])],"derivedFrom":makeQuery(id+"FyYUAefgu6xEfva_4.29.F14.boolean.opBoolean","SPLIT",EDGE,{"disambiguationData":[TD([subQ6])],"derivedFrom":makeQuery(id+"FyYUAefgu6xEfva_4.28.F14.boolean.opBoolean","SPLIT",EDGE,{"disambiguationData":[TD([subQ6])],"derivedFrom":makeQuery(id+"FyYUAefgu6xEfva_4.27.F14.boolean.opBoolean","SPLIT",EDGE,{"disambiguationData":[TD([subQ6])],"derivedFrom":makeQuery(id+"FyYUAefgu6xEfva_4.26.F14.boolean.opBoolean","SPLIT",EDGE,{"disambiguationData":[TD([subQ6])],"derivedFrom":makeQuery(id+"FyYUAefgu6xEfva_4.25.F14.boolean.opBoolean","SPLIT",EDGE,{"disambiguationData":[TD([subQ6])],"derivedFrom":makeQuery(id+"FyYUAefgu6xEfva_4.24.F14.boolean.opBoolean","SPLIT",EDGE,{"disambiguationData":[TD([subQ6])],"derivedFrom":makeQuery(id+"FyYUAefgu6xEfva_4.23.F14.boolean.opBoolean","SPLIT",EDGE,{"disambiguationData":[TD([subQ6])],"derivedFrom":makeQuery(id+"FyYUAefgu6xEfva_4.22.F14.boolean.opBoolean","SPLIT",EDGE,{"disambiguationData":[TD([subQ6])],"derivedFrom":makeQuery(id+"FyYUAefgu6xEfva_4.21.F14.boolean.opBoolean","SPLIT",EDGE,{"disambiguationData":[TD([subQ6])],"derivedFrom":makeQuery(id+"FyYUAefgu6xEfva_4.20.F14.boolean.opBoolean","SPLIT",EDGE,{"disambiguationData":[TD([subQ6])],"derivedFrom":makeQuery(id+"FyYUAefgu6xEfva_4.19.F14.boolean.opBoolean","SPLIT",EDGE,{"disambiguationData":[TD([subQ6])],"derivedFrom":makeQuery(id+"FyYUAefgu6xEfva_4.18.F14.boolean.opBoolean","SPLIT",EDGE,{"disambiguationData":[TD([subQ6])],"derivedFrom":makeQuery(id+"FyYUAefgu6xEfva_4.17.F14.boolean.opBoolean","SPLIT",EDGE,{"disambiguationData":[TD([subQ6])],"derivedFrom":makeQuery(id+"FyYUAefgu6xEfva_4.16.F14.boolean.opBoolean","SPLIT",EDGE,{"disambiguationData":[TD([subQ6])],"derivedFrom":makeQuery(id+"FyYUAefgu6xEfva_4.15.F14.boolean.opBoolean","SPLIT",EDGE,{"disambiguationData":[TD([subQ6])],"derivedFrom":makeQuery(id+"FyYUAefgu6xEfva_4.14.F14.boolean.opBoolean","SPLIT",EDGE,{"disambiguationData":[TD([subQ6])],"derivedFrom":makeQuery(id+"FyYUAefgu6xEfva_4.13.F14.boolean.opBoolean","SPLIT",EDGE,{"disambiguationData":[TD([subQ6])],"derivedFrom":makeQuery(id+"FyYUAefgu6xEfva_4.12.F14.boolean.opBoolean","SPLIT",EDGE,{"disambiguationData":[TD([subQ6])],"derivedFrom":makeQuery(id+"FyYUAefgu6xEfva_4.11.F14.boolean.opBoolean","SPLIT",EDGE,{"disambiguationData":[TD([subQ6])],"derivedFrom":makeQuery(id+"FyYUAefgu6xEfva_4.10.F14.boolean.opBoolean","SPLIT",EDGE,{"disambiguationData":[TD([subQ6])],"derivedFrom":makeQuery(id+"FyYUAefgu6xEfva_4.9.F14.boolean.opBoolean","SPLIT",EDGE,{"disambiguationData":[TD([subQ6])],"derivedFrom":makeQuery(id+"FyYUAefgu6xEfva_4.8.F14.boolean.opBoolean","SPLIT",EDGE,{"disambiguationData":[TD([subQ6])],"derivedFrom":makeQuery(id+"FyYUAefgu6xEfva_4.7.F14.boolean.opBoolean","SPLIT",EDGE,{"disambiguationData":[TD([subQ6])],"derivedFrom":makeQuery(id+"FyYUAefgu6xEfva_4.6.F14.boolean.opBoolean","SPLIT",EDGE,{"disambiguationData":[TD([subQ6])],"derivedFrom":makeQuery(id+"FyYUAefgu6xEfva_4.5.F14.boolean.opBoolean","SPLIT",EDGE,{"disambiguationData":[TD([subQ6])],"derivedFrom":makeQuery(id+"FyYUAefgu6xEfva_4.4.F14.boolean.opBoolean","SPLIT",EDGE,{"disambiguationData":[TD([subQ6])],"derivedFrom":makeQuery(id+"FyYUAefgu6xEfva_4.3.F14.boolean.opBoolean","SPLIT",EDGE,{"disambiguationData":[TD([subQ6])],"derivedFrom":makeQuery(id+"FyYUAefgu6xEfva_4.2.F14.boolean.opBoolean","SPLIT",EDGE,{"disambiguationData":[TD([subQ6])],"derivedFrom":makeQuery(id+"FyYUAefgu6xEfva_4.1.F14.boolean.opBoolean","SPLIT",EDGE,{"disambiguationData":[TD([subQ6])],"derivedFrom":makeQuery(id+"F12.opExtrude","CAP_EDGE",EDGE,{"disambiguationData":[OSD([subQ3])],"isStart":true})})})})})})})})})})})})})})})})})})})})})})})})})})})})})})})})})})});}
            var Q588;
            Q588=makeQuery(id+"FyYUAefgu6xEfva_4.35.F14.opExtrude","SWEPT_EDGE",EDGE,{"disambiguationData":[OSD([sQuery(id+"F11.wireOp",EDGE,"E143"),sQuery(id+"F13.wireOp",EDGE,"E147")])]});
            var Q589;
            {var subQ0=sQuery(id+"F9.wireOp",EDGE,"E142");var subQ3=sQuery(id+"F13.wireOp",EDGE,"E148.MirrorCS");var subQ4=makeQuery(id+"FyYUAefgu6xEfva_4.34.F14.opExtrude","SWEPT_FACE",FACE,{"disambiguationData":[OSD([subQ3])]});var subQ5=sQuery(id+"F13.wireOp",EDGE,"E147");var subQ6=makeQuery(id+"F14.opExtrude","SWEPT_FACE",FACE,{"disambiguationData":[OSD([subQ5])]});Q589=makeQuery(id+"FyYUAefgu6xEfva_4.35.F14.boolean.opBoolean","SPLIT",EDGE,{"disambiguationData":[TD([subQ4])],"derivedFrom":makeQuery(id+"FyYUAefgu6xEfva_4.34.F14.boolean.opBoolean","SPLIT",EDGE,{"disambiguationData":[TD([subQ6])],"derivedFrom":makeQuery(id+"FyYUAefgu6xEfva_4.33.F14.boolean.opBoolean","SPLIT",EDGE,{"disambiguationData":[TD([subQ6])],"derivedFrom":makeQuery(id+"FyYUAefgu6xEfva_4.32.F14.boolean.opBoolean","SPLIT",EDGE,{"disambiguationData":[TD([subQ6])],"derivedFrom":makeQuery(id+"FyYUAefgu6xEfva_4.31.F14.boolean.opBoolean","SPLIT",EDGE,{"disambiguationData":[TD([subQ6])],"derivedFrom":makeQuery(id+"FyYUAefgu6xEfva_4.30.F14.boolean.opBoolean","SPLIT",EDGE,{"disambiguationData":[TD([subQ6])],"derivedFrom":makeQuery(id+"FyYUAefgu6xEfva_4.29.F14.boolean.opBoolean","SPLIT",EDGE,{"disambiguationData":[TD([subQ6])],"derivedFrom":makeQuery(id+"FyYUAefgu6xEfva_4.28.F14.boolean.opBoolean","SPLIT",EDGE,{"disambiguationData":[TD([subQ6])],"derivedFrom":makeQuery(id+"FyYUAefgu6xEfva_4.27.F14.boolean.opBoolean","SPLIT",EDGE,{"disambiguationData":[TD([subQ6])],"derivedFrom":makeQuery(id+"FyYUAefgu6xEfva_4.26.F14.boolean.opBoolean","SPLIT",EDGE,{"disambiguationData":[TD([subQ6])],"derivedFrom":makeQuery(id+"FyYUAefgu6xEfva_4.25.F14.boolean.opBoolean","SPLIT",EDGE,{"disambiguationData":[TD([subQ6])],"derivedFrom":makeQuery(id+"FyYUAefgu6xEfva_4.24.F14.boolean.opBoolean","SPLIT",EDGE,{"disambiguationData":[TD([subQ6])],"derivedFrom":makeQuery(id+"FyYUAefgu6xEfva_4.23.F14.boolean.opBoolean","SPLIT",EDGE,{"disambiguationData":[TD([subQ6])],"derivedFrom":makeQuery(id+"FyYUAefgu6xEfva_4.22.F14.boolean.opBoolean","SPLIT",EDGE,{"disambiguationData":[TD([subQ6])],"derivedFrom":makeQuery(id+"FyYUAefgu6xEfva_4.21.F14.boolean.opBoolean","SPLIT",EDGE,{"disambiguationData":[TD([subQ6])],"derivedFrom":makeQuery(id+"FyYUAefgu6xEfva_4.20.F14.boolean.opBoolean","SPLIT",EDGE,{"disambiguationData":[TD([subQ6])],"derivedFrom":makeQuery(id+"FyYUAefgu6xEfva_4.19.F14.boolean.opBoolean","SPLIT",EDGE,{"disambiguationData":[TD([subQ6])],"derivedFrom":makeQuery(id+"FyYUAefgu6xEfva_4.18.F14.boolean.opBoolean","SPLIT",EDGE,{"disambiguationData":[TD([subQ6])],"derivedFrom":makeQuery(id+"FyYUAefgu6xEfva_4.17.F14.boolean.opBoolean","SPLIT",EDGE,{"disambiguationData":[TD([subQ6])],"derivedFrom":makeQuery(id+"FyYUAefgu6xEfva_4.16.F14.boolean.opBoolean","SPLIT",EDGE,{"disambiguationData":[TD([subQ6])],"derivedFrom":makeQuery(id+"FyYUAefgu6xEfva_4.15.F14.boolean.opBoolean","SPLIT",EDGE,{"disambiguationData":[TD([subQ6])],"derivedFrom":makeQuery(id+"FyYUAefgu6xEfva_4.14.F14.boolean.opBoolean","SPLIT",EDGE,{"disambiguationData":[TD([subQ6])],"derivedFrom":makeQuery(id+"FyYUAefgu6xEfva_4.13.F14.boolean.opBoolean","SPLIT",EDGE,{"disambiguationData":[TD([subQ6])],"derivedFrom":makeQuery(id+"FyYUAefgu6xEfva_4.12.F14.boolean.opBoolean","SPLIT",EDGE,{"disambiguationData":[TD([subQ6])],"derivedFrom":makeQuery(id+"FyYUAefgu6xEfva_4.11.F14.boolean.opBoolean","SPLIT",EDGE,{"disambiguationData":[TD([subQ6])],"derivedFrom":makeQuery(id+"FyYUAefgu6xEfva_4.10.F14.boolean.opBoolean","SPLIT",EDGE,{"disambiguationData":[TD([subQ6])],"derivedFrom":makeQuery(id+"FyYUAefgu6xEfva_4.9.F14.boolean.opBoolean","SPLIT",EDGE,{"disambiguationData":[TD([subQ6])],"derivedFrom":makeQuery(id+"FyYUAefgu6xEfva_4.8.F14.boolean.opBoolean","SPLIT",EDGE,{"disambiguationData":[TD([subQ6])],"derivedFrom":makeQuery(id+"FyYUAefgu6xEfva_4.7.F14.boolean.opBoolean","SPLIT",EDGE,{"disambiguationData":[TD([subQ6])],"derivedFrom":makeQuery(id+"FyYUAefgu6xEfva_4.6.F14.boolean.opBoolean","SPLIT",EDGE,{"disambiguationData":[TD([subQ6])],"derivedFrom":makeQuery(id+"FyYUAefgu6xEfva_4.5.F14.boolean.opBoolean","SPLIT",EDGE,{"disambiguationData":[TD([subQ6])],"derivedFrom":makeQuery(id+"FyYUAefgu6xEfva_4.4.F14.boolean.opBoolean","SPLIT",EDGE,{"disambiguationData":[TD([subQ6])],"derivedFrom":makeQuery(id+"FyYUAefgu6xEfva_4.3.F14.boolean.opBoolean","SPLIT",EDGE,{"disambiguationData":[TD([subQ6])],"derivedFrom":makeQuery(id+"FyYUAefgu6xEfva_4.2.F14.boolean.opBoolean","SPLIT",EDGE,{"disambiguationData":[TD([subQ6])],"derivedFrom":makeQuery(id+"FyYUAefgu6xEfva_4.1.F14.boolean.opBoolean","SPLIT",EDGE,{"disambiguationData":[TD([subQ6])],"derivedFrom":makeQuery(id+"F10.boolean.opBoolean","COPY",EDGE,{"derivedFrom":makeQuery(id+"F10.opExtrude","CAP_EDGE",EDGE,{"disambiguationData":[OSD([subQ0])],"isStart":false})})})})})})})})})})})})})})})})})})})})})})})})})})})})})})})})})})})})});}
            var Q590;
            {var subQ0=sQuery(id+"F13.wireOp",EDGE,"E148.MirrorCS");var subQ1=sQuery(id+"F13.wireOp",EDGE,"E147");var subQ2=sQuery(id+"F11.wireOp",EDGE,"E143");var subQ23=makeQuery(id+"FyYUAefgu6xEfva_4.34.F14.opExtrude","SWEPT_FACE",FACE,{"disambiguationData":[OSD([subQ0])]});var subQ42=makeQuery(id+"F14.opExtrude","SWEPT_FACE",FACE,{"disambiguationData":[OSD([subQ1])]});Q590=makeQuery(id+"FyYUAefgu6xEfva_4.35.F14.boolean.opBoolean","SPLIT",EDGE,{"disambiguationData":[TD([subQ23])],"derivedFrom":makeQuery(id+"FyYUAefgu6xEfva_4.34.F14.boolean.opBoolean","SPLIT",EDGE,{"disambiguationData":[TD([subQ42])],"derivedFrom":makeQuery(id+"FyYUAefgu6xEfva_4.33.F14.boolean.opBoolean","SPLIT",EDGE,{"disambiguationData":[TD([subQ42])],"derivedFrom":makeQuery(id+"FyYUAefgu6xEfva_4.32.F14.boolean.opBoolean","SPLIT",EDGE,{"disambiguationData":[TD([subQ42])],"derivedFrom":makeQuery(id+"FyYUAefgu6xEfva_4.31.F14.boolean.opBoolean","SPLIT",EDGE,{"disambiguationData":[TD([subQ42])],"derivedFrom":makeQuery(id+"FyYUAefgu6xEfva_4.30.F14.boolean.opBoolean","SPLIT",EDGE,{"disambiguationData":[TD([subQ42])],"derivedFrom":makeQuery(id+"FyYUAefgu6xEfva_4.29.F14.boolean.opBoolean","SPLIT",EDGE,{"disambiguationData":[TD([subQ42])],"derivedFrom":makeQuery(id+"FyYUAefgu6xEfva_4.28.F14.boolean.opBoolean","SPLIT",EDGE,{"disambiguationData":[TD([subQ42])],"derivedFrom":makeQuery(id+"FyYUAefgu6xEfva_4.27.F14.boolean.opBoolean","SPLIT",EDGE,{"disambiguationData":[TD([subQ42])],"derivedFrom":makeQuery(id+"FyYUAefgu6xEfva_4.26.F14.boolean.opBoolean","SPLIT",EDGE,{"disambiguationData":[TD([subQ42])],"derivedFrom":makeQuery(id+"FyYUAefgu6xEfva_4.25.F14.boolean.opBoolean","SPLIT",EDGE,{"disambiguationData":[TD([subQ42])],"derivedFrom":makeQuery(id+"FyYUAefgu6xEfva_4.24.F14.boolean.opBoolean","SPLIT",EDGE,{"disambiguationData":[TD([subQ42])],"derivedFrom":makeQuery(id+"FyYUAefgu6xEfva_4.23.F14.boolean.opBoolean","SPLIT",EDGE,{"disambiguationData":[TD([subQ42])],"derivedFrom":makeQuery(id+"FyYUAefgu6xEfva_4.22.F14.boolean.opBoolean","SPLIT",EDGE,{"disambiguationData":[TD([subQ42])],"derivedFrom":makeQuery(id+"FyYUAefgu6xEfva_4.21.F14.boolean.opBoolean","SPLIT",EDGE,{"disambiguationData":[TD([subQ42])],"derivedFrom":makeQuery(id+"FyYUAefgu6xEfva_4.20.F14.boolean.opBoolean","SPLIT",EDGE,{"disambiguationData":[TD([subQ42])],"derivedFrom":makeQuery(id+"FyYUAefgu6xEfva_4.19.F14.boolean.opBoolean","SPLIT",EDGE,{"disambiguationData":[TD([subQ42])],"derivedFrom":makeQuery(id+"FyYUAefgu6xEfva_4.18.F14.boolean.opBoolean","SPLIT",EDGE,{"disambiguationData":[TD([subQ42])],"derivedFrom":makeQuery(id+"FyYUAefgu6xEfva_4.17.F14.boolean.opBoolean","SPLIT",EDGE,{"disambiguationData":[TD([subQ42])],"derivedFrom":makeQuery(id+"FyYUAefgu6xEfva_4.16.F14.boolean.opBoolean","SPLIT",EDGE,{"disambiguationData":[TD([subQ42])],"derivedFrom":makeQuery(id+"FyYUAefgu6xEfva_4.15.F14.boolean.opBoolean","SPLIT",EDGE,{"disambiguationData":[TD([subQ42])],"derivedFrom":makeQuery(id+"FyYUAefgu6xEfva_4.14.F14.boolean.opBoolean","SPLIT",EDGE,{"disambiguationData":[TD([subQ42])],"derivedFrom":makeQuery(id+"FyYUAefgu6xEfva_4.13.F14.boolean.opBoolean","SPLIT",EDGE,{"disambiguationData":[TD([subQ42])],"derivedFrom":makeQuery(id+"FyYUAefgu6xEfva_4.12.F14.boolean.opBoolean","SPLIT",EDGE,{"disambiguationData":[TD([subQ42])],"derivedFrom":makeQuery(id+"FyYUAefgu6xEfva_4.11.F14.boolean.opBoolean","SPLIT",EDGE,{"disambiguationData":[TD([subQ42])],"derivedFrom":makeQuery(id+"FyYUAefgu6xEfva_4.10.F14.boolean.opBoolean","SPLIT",EDGE,{"disambiguationData":[TD([subQ42])],"derivedFrom":makeQuery(id+"FyYUAefgu6xEfva_4.9.F14.boolean.opBoolean","SPLIT",EDGE,{"disambiguationData":[TD([subQ42])],"derivedFrom":makeQuery(id+"FyYUAefgu6xEfva_4.8.F14.boolean.opBoolean","SPLIT",EDGE,{"disambiguationData":[TD([subQ42])],"derivedFrom":makeQuery(id+"FyYUAefgu6xEfva_4.7.F14.boolean.opBoolean","SPLIT",EDGE,{"disambiguationData":[TD([subQ42])],"derivedFrom":makeQuery(id+"FyYUAefgu6xEfva_4.6.F14.boolean.opBoolean","SPLIT",EDGE,{"disambiguationData":[TD([subQ42])],"derivedFrom":makeQuery(id+"FyYUAefgu6xEfva_4.5.F14.boolean.opBoolean","SPLIT",EDGE,{"disambiguationData":[TD([subQ42])],"derivedFrom":makeQuery(id+"FyYUAefgu6xEfva_4.4.F14.boolean.opBoolean","SPLIT",EDGE,{"disambiguationData":[TD([subQ42])],"derivedFrom":makeQuery(id+"FyYUAefgu6xEfva_4.3.F14.boolean.opBoolean","SPLIT",EDGE,{"disambiguationData":[TD([subQ42])],"derivedFrom":makeQuery(id+"FyYUAefgu6xEfva_4.2.F14.boolean.opBoolean","SPLIT",EDGE,{"disambiguationData":[TD([subQ42])],"derivedFrom":makeQuery(id+"FyYUAefgu6xEfva_4.1.F14.boolean.opBoolean","SPLIT",EDGE,{"disambiguationData":[TD([subQ42])],"derivedFrom":makeQuery(id+"F12.opExtrude","CAP_EDGE",EDGE,{"disambiguationData":[OSD([subQ2])],"isStart":false})})})})})})})})})})})})})})})})})})})})})})})})})})})})})})})})})})})});}
            var Q591;
            {var subQ1=sQuery(id+"F11.wireOp",EDGE,"E143");var subQ3=sQuery(id+"F13.wireOp",EDGE,"E148.MirrorCS");var subQ4=makeQuery(id+"FyYUAefgu6xEfva_4.34.F14.opExtrude","SWEPT_FACE",FACE,{"disambiguationData":[OSD([subQ3])]});var subQ5=sQuery(id+"F13.wireOp",EDGE,"E147");var subQ6=makeQuery(id+"F14.opExtrude","SWEPT_FACE",FACE,{"disambiguationData":[OSD([subQ5])]});Q591=makeQuery(id+"FyYUAefgu6xEfva_4.35.F14.boolean.opBoolean","SPLIT",EDGE,{"disambiguationData":[TD([subQ4])],"derivedFrom":makeQuery(id+"FyYUAefgu6xEfva_4.34.F14.boolean.opBoolean","SPLIT",EDGE,{"disambiguationData":[TD([subQ6])],"derivedFrom":makeQuery(id+"FyYUAefgu6xEfva_4.33.F14.boolean.opBoolean","SPLIT",EDGE,{"disambiguationData":[TD([subQ6])],"derivedFrom":makeQuery(id+"FyYUAefgu6xEfva_4.32.F14.boolean.opBoolean","SPLIT",EDGE,{"disambiguationData":[TD([subQ6])],"derivedFrom":makeQuery(id+"FyYUAefgu6xEfva_4.31.F14.boolean.opBoolean","SPLIT",EDGE,{"disambiguationData":[TD([subQ6])],"derivedFrom":makeQuery(id+"FyYUAefgu6xEfva_4.30.F14.boolean.opBoolean","SPLIT",EDGE,{"disambiguationData":[TD([subQ6])],"derivedFrom":makeQuery(id+"FyYUAefgu6xEfva_4.29.F14.boolean.opBoolean","SPLIT",EDGE,{"disambiguationData":[TD([subQ6])],"derivedFrom":makeQuery(id+"FyYUAefgu6xEfva_4.28.F14.boolean.opBoolean","SPLIT",EDGE,{"disambiguationData":[TD([subQ6])],"derivedFrom":makeQuery(id+"FyYUAefgu6xEfva_4.27.F14.boolean.opBoolean","SPLIT",EDGE,{"disambiguationData":[TD([subQ6])],"derivedFrom":makeQuery(id+"FyYUAefgu6xEfva_4.26.F14.boolean.opBoolean","SPLIT",EDGE,{"disambiguationData":[TD([subQ6])],"derivedFrom":makeQuery(id+"FyYUAefgu6xEfva_4.25.F14.boolean.opBoolean","SPLIT",EDGE,{"disambiguationData":[TD([subQ6])],"derivedFrom":makeQuery(id+"FyYUAefgu6xEfva_4.24.F14.boolean.opBoolean","SPLIT",EDGE,{"disambiguationData":[TD([subQ6])],"derivedFrom":makeQuery(id+"FyYUAefgu6xEfva_4.23.F14.boolean.opBoolean","SPLIT",EDGE,{"disambiguationData":[TD([subQ6])],"derivedFrom":makeQuery(id+"FyYUAefgu6xEfva_4.22.F14.boolean.opBoolean","SPLIT",EDGE,{"disambiguationData":[TD([subQ6])],"derivedFrom":makeQuery(id+"FyYUAefgu6xEfva_4.21.F14.boolean.opBoolean","SPLIT",EDGE,{"disambiguationData":[TD([subQ6])],"derivedFrom":makeQuery(id+"FyYUAefgu6xEfva_4.20.F14.boolean.opBoolean","SPLIT",EDGE,{"disambiguationData":[TD([subQ6])],"derivedFrom":makeQuery(id+"FyYUAefgu6xEfva_4.19.F14.boolean.opBoolean","SPLIT",EDGE,{"disambiguationData":[TD([subQ6])],"derivedFrom":makeQuery(id+"FyYUAefgu6xEfva_4.18.F14.boolean.opBoolean","SPLIT",EDGE,{"disambiguationData":[TD([subQ6])],"derivedFrom":makeQuery(id+"FyYUAefgu6xEfva_4.17.F14.boolean.opBoolean","SPLIT",EDGE,{"disambiguationData":[TD([subQ6])],"derivedFrom":makeQuery(id+"FyYUAefgu6xEfva_4.16.F14.boolean.opBoolean","SPLIT",EDGE,{"disambiguationData":[TD([subQ6])],"derivedFrom":makeQuery(id+"FyYUAefgu6xEfva_4.15.F14.boolean.opBoolean","SPLIT",EDGE,{"disambiguationData":[TD([subQ6])],"derivedFrom":makeQuery(id+"FyYUAefgu6xEfva_4.14.F14.boolean.opBoolean","SPLIT",EDGE,{"disambiguationData":[TD([subQ6])],"derivedFrom":makeQuery(id+"FyYUAefgu6xEfva_4.13.F14.boolean.opBoolean","SPLIT",EDGE,{"disambiguationData":[TD([subQ6])],"derivedFrom":makeQuery(id+"FyYUAefgu6xEfva_4.12.F14.boolean.opBoolean","SPLIT",EDGE,{"disambiguationData":[TD([subQ6])],"derivedFrom":makeQuery(id+"FyYUAefgu6xEfva_4.11.F14.boolean.opBoolean","SPLIT",EDGE,{"disambiguationData":[TD([subQ6])],"derivedFrom":makeQuery(id+"FyYUAefgu6xEfva_4.10.F14.boolean.opBoolean","SPLIT",EDGE,{"disambiguationData":[TD([subQ6])],"derivedFrom":makeQuery(id+"FyYUAefgu6xEfva_4.9.F14.boolean.opBoolean","SPLIT",EDGE,{"disambiguationData":[TD([subQ6])],"derivedFrom":makeQuery(id+"FyYUAefgu6xEfva_4.8.F14.boolean.opBoolean","SPLIT",EDGE,{"disambiguationData":[TD([subQ6])],"derivedFrom":makeQuery(id+"FyYUAefgu6xEfva_4.7.F14.boolean.opBoolean","SPLIT",EDGE,{"disambiguationData":[TD([subQ6])],"derivedFrom":makeQuery(id+"FyYUAefgu6xEfva_4.6.F14.boolean.opBoolean","SPLIT",EDGE,{"disambiguationData":[TD([subQ6])],"derivedFrom":makeQuery(id+"FyYUAefgu6xEfva_4.5.F14.boolean.opBoolean","SPLIT",EDGE,{"disambiguationData":[TD([subQ6])],"derivedFrom":makeQuery(id+"FyYUAefgu6xEfva_4.4.F14.boolean.opBoolean","SPLIT",EDGE,{"disambiguationData":[TD([subQ6])],"derivedFrom":makeQuery(id+"FyYUAefgu6xEfva_4.3.F14.boolean.opBoolean","SPLIT",EDGE,{"disambiguationData":[TD([subQ6])],"derivedFrom":makeQuery(id+"FyYUAefgu6xEfva_4.2.F14.boolean.opBoolean","SPLIT",EDGE,{"disambiguationData":[TD([subQ6])],"derivedFrom":makeQuery(id+"FyYUAefgu6xEfva_4.1.F14.boolean.opBoolean","SPLIT",EDGE,{"disambiguationData":[TD([subQ6])],"derivedFrom":makeQuery(id+"F12.opExtrude","CAP_EDGE",EDGE,{"disambiguationData":[OSD([subQ1])],"isStart":true})})})})})})})})})})})})})})})})})})})})})})})})})})})})})})})})})})})});}
            var Q592;
            {var subQ1=sQuery(id+"F13.wireOp",EDGE,"E147");var subQ2=sQuery(id+"F11.wireOp",EDGE,"E143");var subQ4=sQuery(id+"F13.wireOp",EDGE,"E148.MirrorCS");var subQ5=makeQuery(id+"FyYUAefgu6xEfva_4.36.F14.opExtrude","SWEPT_FACE",FACE,{"disambiguationData":[OSD([subQ4])]});var subQ6=makeQuery(id+"F14.opExtrude","SWEPT_FACE",FACE,{"disambiguationData":[OSD([subQ1])]});Q592=makeQuery(id+"FyYUAefgu6xEfva_4.37.F14.boolean.opBoolean","SPLIT",EDGE,{"disambiguationData":[TD([subQ5])],"derivedFrom":makeQuery(id+"FyYUAefgu6xEfva_4.36.F14.boolean.opBoolean","SPLIT",EDGE,{"disambiguationData":[TD([subQ6])],"derivedFrom":makeQuery(id+"FyYUAefgu6xEfva_4.35.F14.boolean.opBoolean","SPLIT",EDGE,{"disambiguationData":[TD([subQ6])],"derivedFrom":makeQuery(id+"FyYUAefgu6xEfva_4.34.F14.boolean.opBoolean","SPLIT",EDGE,{"disambiguationData":[TD([subQ6])],"derivedFrom":makeQuery(id+"FyYUAefgu6xEfva_4.33.F14.boolean.opBoolean","SPLIT",EDGE,{"disambiguationData":[TD([subQ6])],"derivedFrom":makeQuery(id+"FyYUAefgu6xEfva_4.32.F14.boolean.opBoolean","SPLIT",EDGE,{"disambiguationData":[TD([subQ6])],"derivedFrom":makeQuery(id+"FyYUAefgu6xEfva_4.31.F14.boolean.opBoolean","SPLIT",EDGE,{"disambiguationData":[TD([subQ6])],"derivedFrom":makeQuery(id+"FyYUAefgu6xEfva_4.30.F14.boolean.opBoolean","SPLIT",EDGE,{"disambiguationData":[TD([subQ6])],"derivedFrom":makeQuery(id+"FyYUAefgu6xEfva_4.29.F14.boolean.opBoolean","SPLIT",EDGE,{"disambiguationData":[TD([subQ6])],"derivedFrom":makeQuery(id+"FyYUAefgu6xEfva_4.28.F14.boolean.opBoolean","SPLIT",EDGE,{"disambiguationData":[TD([subQ6])],"derivedFrom":makeQuery(id+"FyYUAefgu6xEfva_4.27.F14.boolean.opBoolean","SPLIT",EDGE,{"disambiguationData":[TD([subQ6])],"derivedFrom":makeQuery(id+"FyYUAefgu6xEfva_4.26.F14.boolean.opBoolean","SPLIT",EDGE,{"disambiguationData":[TD([subQ6])],"derivedFrom":makeQuery(id+"FyYUAefgu6xEfva_4.25.F14.boolean.opBoolean","SPLIT",EDGE,{"disambiguationData":[TD([subQ6])],"derivedFrom":makeQuery(id+"FyYUAefgu6xEfva_4.24.F14.boolean.opBoolean","SPLIT",EDGE,{"disambiguationData":[TD([subQ6])],"derivedFrom":makeQuery(id+"FyYUAefgu6xEfva_4.23.F14.boolean.opBoolean","SPLIT",EDGE,{"disambiguationData":[TD([subQ6])],"derivedFrom":makeQuery(id+"FyYUAefgu6xEfva_4.22.F14.boolean.opBoolean","SPLIT",EDGE,{"disambiguationData":[TD([subQ6])],"derivedFrom":makeQuery(id+"FyYUAefgu6xEfva_4.21.F14.boolean.opBoolean","SPLIT",EDGE,{"disambiguationData":[TD([subQ6])],"derivedFrom":makeQuery(id+"FyYUAefgu6xEfva_4.20.F14.boolean.opBoolean","SPLIT",EDGE,{"disambiguationData":[TD([subQ6])],"derivedFrom":makeQuery(id+"FyYUAefgu6xEfva_4.19.F14.boolean.opBoolean","SPLIT",EDGE,{"disambiguationData":[TD([subQ6])],"derivedFrom":makeQuery(id+"FyYUAefgu6xEfva_4.18.F14.boolean.opBoolean","SPLIT",EDGE,{"disambiguationData":[TD([subQ6])],"derivedFrom":makeQuery(id+"FyYUAefgu6xEfva_4.17.F14.boolean.opBoolean","SPLIT",EDGE,{"disambiguationData":[TD([subQ6])],"derivedFrom":makeQuery(id+"FyYUAefgu6xEfva_4.16.F14.boolean.opBoolean","SPLIT",EDGE,{"disambiguationData":[TD([subQ6])],"derivedFrom":makeQuery(id+"FyYUAefgu6xEfva_4.15.F14.boolean.opBoolean","SPLIT",EDGE,{"disambiguationData":[TD([subQ6])],"derivedFrom":makeQuery(id+"FyYUAefgu6xEfva_4.14.F14.boolean.opBoolean","SPLIT",EDGE,{"disambiguationData":[TD([subQ6])],"derivedFrom":makeQuery(id+"FyYUAefgu6xEfva_4.13.F14.boolean.opBoolean","SPLIT",EDGE,{"disambiguationData":[TD([subQ6])],"derivedFrom":makeQuery(id+"FyYUAefgu6xEfva_4.12.F14.boolean.opBoolean","SPLIT",EDGE,{"disambiguationData":[TD([subQ6])],"derivedFrom":makeQuery(id+"FyYUAefgu6xEfva_4.11.F14.boolean.opBoolean","SPLIT",EDGE,{"disambiguationData":[TD([subQ6])],"derivedFrom":makeQuery(id+"FyYUAefgu6xEfva_4.10.F14.boolean.opBoolean","SPLIT",EDGE,{"disambiguationData":[TD([subQ6])],"derivedFrom":makeQuery(id+"FyYUAefgu6xEfva_4.9.F14.boolean.opBoolean","SPLIT",EDGE,{"disambiguationData":[TD([subQ6])],"derivedFrom":makeQuery(id+"FyYUAefgu6xEfva_4.8.F14.boolean.opBoolean","SPLIT",EDGE,{"disambiguationData":[TD([subQ6])],"derivedFrom":makeQuery(id+"FyYUAefgu6xEfva_4.7.F14.boolean.opBoolean","SPLIT",EDGE,{"disambiguationData":[TD([subQ6])],"derivedFrom":makeQuery(id+"FyYUAefgu6xEfva_4.6.F14.boolean.opBoolean","SPLIT",EDGE,{"disambiguationData":[TD([subQ6])],"derivedFrom":makeQuery(id+"FyYUAefgu6xEfva_4.5.F14.boolean.opBoolean","SPLIT",EDGE,{"disambiguationData":[TD([subQ6])],"derivedFrom":makeQuery(id+"FyYUAefgu6xEfva_4.4.F14.boolean.opBoolean","SPLIT",EDGE,{"disambiguationData":[TD([subQ6])],"derivedFrom":makeQuery(id+"FyYUAefgu6xEfva_4.3.F14.boolean.opBoolean","SPLIT",EDGE,{"disambiguationData":[TD([subQ6])],"derivedFrom":makeQuery(id+"FyYUAefgu6xEfva_4.2.F14.boolean.opBoolean","SPLIT",EDGE,{"disambiguationData":[TD([subQ6])],"derivedFrom":makeQuery(id+"FyYUAefgu6xEfva_4.1.F14.boolean.opBoolean","SPLIT",EDGE,{"disambiguationData":[TD([subQ6])],"derivedFrom":makeQuery(id+"F12.opExtrude","CAP_EDGE",EDGE,{"disambiguationData":[OSD([subQ2])],"isStart":true})})})})})})})})})})})})})})})})})})})})})})})})})})})})})})})})})})})})})});}
            var Q593;
            {var subQ1=sQuery(id+"F11.wireOp",EDGE,"E143");var subQ3=sQuery(id+"F13.wireOp",EDGE,"E148.MirrorCS");var subQ4=makeQuery(id+"FyYUAefgu6xEfva_4.35.F14.opExtrude","SWEPT_FACE",FACE,{"disambiguationData":[OSD([subQ3])]});var subQ5=sQuery(id+"F13.wireOp",EDGE,"E147");var subQ6=makeQuery(id+"F14.opExtrude","SWEPT_FACE",FACE,{"disambiguationData":[OSD([subQ5])]});Q593=makeQuery(id+"FyYUAefgu6xEfva_4.36.F14.boolean.opBoolean","SPLIT",EDGE,{"disambiguationData":[TD([subQ4])],"derivedFrom":makeQuery(id+"FyYUAefgu6xEfva_4.35.F14.boolean.opBoolean","SPLIT",EDGE,{"disambiguationData":[TD([subQ6])],"derivedFrom":makeQuery(id+"FyYUAefgu6xEfva_4.34.F14.boolean.opBoolean","SPLIT",EDGE,{"disambiguationData":[TD([subQ6])],"derivedFrom":makeQuery(id+"FyYUAefgu6xEfva_4.33.F14.boolean.opBoolean","SPLIT",EDGE,{"disambiguationData":[TD([subQ6])],"derivedFrom":makeQuery(id+"FyYUAefgu6xEfva_4.32.F14.boolean.opBoolean","SPLIT",EDGE,{"disambiguationData":[TD([subQ6])],"derivedFrom":makeQuery(id+"FyYUAefgu6xEfva_4.31.F14.boolean.opBoolean","SPLIT",EDGE,{"disambiguationData":[TD([subQ6])],"derivedFrom":makeQuery(id+"FyYUAefgu6xEfva_4.30.F14.boolean.opBoolean","SPLIT",EDGE,{"disambiguationData":[TD([subQ6])],"derivedFrom":makeQuery(id+"FyYUAefgu6xEfva_4.29.F14.boolean.opBoolean","SPLIT",EDGE,{"disambiguationData":[TD([subQ6])],"derivedFrom":makeQuery(id+"FyYUAefgu6xEfva_4.28.F14.boolean.opBoolean","SPLIT",EDGE,{"disambiguationData":[TD([subQ6])],"derivedFrom":makeQuery(id+"FyYUAefgu6xEfva_4.27.F14.boolean.opBoolean","SPLIT",EDGE,{"disambiguationData":[TD([subQ6])],"derivedFrom":makeQuery(id+"FyYUAefgu6xEfva_4.26.F14.boolean.opBoolean","SPLIT",EDGE,{"disambiguationData":[TD([subQ6])],"derivedFrom":makeQuery(id+"FyYUAefgu6xEfva_4.25.F14.boolean.opBoolean","SPLIT",EDGE,{"disambiguationData":[TD([subQ6])],"derivedFrom":makeQuery(id+"FyYUAefgu6xEfva_4.24.F14.boolean.opBoolean","SPLIT",EDGE,{"disambiguationData":[TD([subQ6])],"derivedFrom":makeQuery(id+"FyYUAefgu6xEfva_4.23.F14.boolean.opBoolean","SPLIT",EDGE,{"disambiguationData":[TD([subQ6])],"derivedFrom":makeQuery(id+"FyYUAefgu6xEfva_4.22.F14.boolean.opBoolean","SPLIT",EDGE,{"disambiguationData":[TD([subQ6])],"derivedFrom":makeQuery(id+"FyYUAefgu6xEfva_4.21.F14.boolean.opBoolean","SPLIT",EDGE,{"disambiguationData":[TD([subQ6])],"derivedFrom":makeQuery(id+"FyYUAefgu6xEfva_4.20.F14.boolean.opBoolean","SPLIT",EDGE,{"disambiguationData":[TD([subQ6])],"derivedFrom":makeQuery(id+"FyYUAefgu6xEfva_4.19.F14.boolean.opBoolean","SPLIT",EDGE,{"disambiguationData":[TD([subQ6])],"derivedFrom":makeQuery(id+"FyYUAefgu6xEfva_4.18.F14.boolean.opBoolean","SPLIT",EDGE,{"disambiguationData":[TD([subQ6])],"derivedFrom":makeQuery(id+"FyYUAefgu6xEfva_4.17.F14.boolean.opBoolean","SPLIT",EDGE,{"disambiguationData":[TD([subQ6])],"derivedFrom":makeQuery(id+"FyYUAefgu6xEfva_4.16.F14.boolean.opBoolean","SPLIT",EDGE,{"disambiguationData":[TD([subQ6])],"derivedFrom":makeQuery(id+"FyYUAefgu6xEfva_4.15.F14.boolean.opBoolean","SPLIT",EDGE,{"disambiguationData":[TD([subQ6])],"derivedFrom":makeQuery(id+"FyYUAefgu6xEfva_4.14.F14.boolean.opBoolean","SPLIT",EDGE,{"disambiguationData":[TD([subQ6])],"derivedFrom":makeQuery(id+"FyYUAefgu6xEfva_4.13.F14.boolean.opBoolean","SPLIT",EDGE,{"disambiguationData":[TD([subQ6])],"derivedFrom":makeQuery(id+"FyYUAefgu6xEfva_4.12.F14.boolean.opBoolean","SPLIT",EDGE,{"disambiguationData":[TD([subQ6])],"derivedFrom":makeQuery(id+"FyYUAefgu6xEfva_4.11.F14.boolean.opBoolean","SPLIT",EDGE,{"disambiguationData":[TD([subQ6])],"derivedFrom":makeQuery(id+"FyYUAefgu6xEfva_4.10.F14.boolean.opBoolean","SPLIT",EDGE,{"disambiguationData":[TD([subQ6])],"derivedFrom":makeQuery(id+"FyYUAefgu6xEfva_4.9.F14.boolean.opBoolean","SPLIT",EDGE,{"disambiguationData":[TD([subQ6])],"derivedFrom":makeQuery(id+"FyYUAefgu6xEfva_4.8.F14.boolean.opBoolean","SPLIT",EDGE,{"disambiguationData":[TD([subQ6])],"derivedFrom":makeQuery(id+"FyYUAefgu6xEfva_4.7.F14.boolean.opBoolean","SPLIT",EDGE,{"disambiguationData":[TD([subQ6])],"derivedFrom":makeQuery(id+"FyYUAefgu6xEfva_4.6.F14.boolean.opBoolean","SPLIT",EDGE,{"disambiguationData":[TD([subQ6])],"derivedFrom":makeQuery(id+"FyYUAefgu6xEfva_4.5.F14.boolean.opBoolean","SPLIT",EDGE,{"disambiguationData":[TD([subQ6])],"derivedFrom":makeQuery(id+"FyYUAefgu6xEfva_4.4.F14.boolean.opBoolean","SPLIT",EDGE,{"disambiguationData":[TD([subQ6])],"derivedFrom":makeQuery(id+"FyYUAefgu6xEfva_4.3.F14.boolean.opBoolean","SPLIT",EDGE,{"disambiguationData":[TD([subQ6])],"derivedFrom":makeQuery(id+"FyYUAefgu6xEfva_4.2.F14.boolean.opBoolean","SPLIT",EDGE,{"disambiguationData":[TD([subQ6])],"derivedFrom":makeQuery(id+"FyYUAefgu6xEfva_4.1.F14.boolean.opBoolean","SPLIT",EDGE,{"disambiguationData":[TD([subQ6])],"derivedFrom":makeQuery(id+"F12.opExtrude","CAP_EDGE",EDGE,{"disambiguationData":[OSD([subQ1])],"isStart":true})})})})})})})})})})})})})})})})})})})})})})})})})})})})})})})})})})})})});}
            var Q594;
            {var subQ1=sQuery(id+"F11.wireOp",EDGE,"E143");var subQ3=sQuery(id+"F13.wireOp",EDGE,"E147");var subQ4=sQuery(id+"F13.wireOp",EDGE,"E148.MirrorCS");var subQ5=makeQuery(id+"FyYUAefgu6xEfva_4.7.F14.opExtrude","SWEPT_FACE",FACE,{"disambiguationData":[OSD([subQ4])]});var subQ6=makeQuery(id+"F14.opExtrude","SWEPT_FACE",FACE,{"disambiguationData":[OSD([subQ3])]});Q594=makeQuery(id+"FyYUAefgu6xEfva_4.8.F14.boolean.opBoolean","SPLIT",EDGE,{"disambiguationData":[TD([subQ5])],"derivedFrom":makeQuery(id+"FyYUAefgu6xEfva_4.7.F14.boolean.opBoolean","SPLIT",EDGE,{"disambiguationData":[TD([subQ6])],"derivedFrom":makeQuery(id+"FyYUAefgu6xEfva_4.6.F14.boolean.opBoolean","SPLIT",EDGE,{"disambiguationData":[TD([subQ6])],"derivedFrom":makeQuery(id+"FyYUAefgu6xEfva_4.5.F14.boolean.opBoolean","SPLIT",EDGE,{"disambiguationData":[TD([subQ6])],"derivedFrom":makeQuery(id+"FyYUAefgu6xEfva_4.4.F14.boolean.opBoolean","SPLIT",EDGE,{"disambiguationData":[TD([subQ6])],"derivedFrom":makeQuery(id+"FyYUAefgu6xEfva_4.3.F14.boolean.opBoolean","SPLIT",EDGE,{"disambiguationData":[TD([subQ6])],"derivedFrom":makeQuery(id+"FyYUAefgu6xEfva_4.2.F14.boolean.opBoolean","SPLIT",EDGE,{"disambiguationData":[TD([subQ6])],"derivedFrom":makeQuery(id+"FyYUAefgu6xEfva_4.1.F14.boolean.opBoolean","SPLIT",EDGE,{"disambiguationData":[TD([subQ6])],"derivedFrom":makeQuery(id+"F12.opExtrude","CAP_EDGE",EDGE,{"disambiguationData":[OSD([subQ1])],"isStart":true})})})})})})})})});}
            var Q595;
            {var subQ1=sQuery(id+"F11.wireOp",EDGE,"E143");var subQ3=sQuery(id+"F13.wireOp",EDGE,"E148.MirrorCS");var subQ4=makeQuery(id+"FyYUAefgu6xEfva_4.5.F14.opExtrude","SWEPT_FACE",FACE,{"disambiguationData":[OSD([subQ3])]});var subQ5=sQuery(id+"F13.wireOp",EDGE,"E147");var subQ6=makeQuery(id+"F14.opExtrude","SWEPT_FACE",FACE,{"disambiguationData":[OSD([subQ5])]});Q595=makeQuery(id+"FyYUAefgu6xEfva_4.6.F14.boolean.opBoolean","SPLIT",EDGE,{"disambiguationData":[TD([subQ4])],"derivedFrom":makeQuery(id+"FyYUAefgu6xEfva_4.5.F14.boolean.opBoolean","SPLIT",EDGE,{"disambiguationData":[TD([subQ6])],"derivedFrom":makeQuery(id+"FyYUAefgu6xEfva_4.4.F14.boolean.opBoolean","SPLIT",EDGE,{"disambiguationData":[TD([subQ6])],"derivedFrom":makeQuery(id+"FyYUAefgu6xEfva_4.3.F14.boolean.opBoolean","SPLIT",EDGE,{"disambiguationData":[TD([subQ6])],"derivedFrom":makeQuery(id+"FyYUAefgu6xEfva_4.2.F14.boolean.opBoolean","SPLIT",EDGE,{"disambiguationData":[TD([subQ6])],"derivedFrom":makeQuery(id+"FyYUAefgu6xEfva_4.1.F14.boolean.opBoolean","SPLIT",EDGE,{"disambiguationData":[TD([subQ6])],"derivedFrom":makeQuery(id+"F12.opExtrude","CAP_EDGE",EDGE,{"disambiguationData":[OSD([subQ1])],"isStart":true})})})})})})});}
            var Q596;
            {var subQ1=sQuery(id+"F13.wireOp",EDGE,"E148.MirrorCS");var subQ2=makeQuery(id+"FyYUAefgu6xEfva_4.8.F14.opExtrude","SWEPT_FACE",FACE,{"disambiguationData":[OSD([subQ1])]});var subQ3=sQuery(id+"F11.wireOp",EDGE,"E143");var subQ5=sQuery(id+"F13.wireOp",EDGE,"E147");var subQ6=makeQuery(id+"F14.opExtrude","SWEPT_FACE",FACE,{"disambiguationData":[OSD([subQ5])]});Q596=makeQuery(id+"FyYUAefgu6xEfva_4.9.F14.boolean.opBoolean","SPLIT",EDGE,{"disambiguationData":[TD([subQ2])],"derivedFrom":makeQuery(id+"FyYUAefgu6xEfva_4.8.F14.boolean.opBoolean","SPLIT",EDGE,{"disambiguationData":[TD([subQ6])],"derivedFrom":makeQuery(id+"FyYUAefgu6xEfva_4.7.F14.boolean.opBoolean","SPLIT",EDGE,{"disambiguationData":[TD([subQ6])],"derivedFrom":makeQuery(id+"FyYUAefgu6xEfva_4.6.F14.boolean.opBoolean","SPLIT",EDGE,{"disambiguationData":[TD([subQ6])],"derivedFrom":makeQuery(id+"FyYUAefgu6xEfva_4.5.F14.boolean.opBoolean","SPLIT",EDGE,{"disambiguationData":[TD([subQ6])],"derivedFrom":makeQuery(id+"FyYUAefgu6xEfva_4.4.F14.boolean.opBoolean","SPLIT",EDGE,{"disambiguationData":[TD([subQ6])],"derivedFrom":makeQuery(id+"FyYUAefgu6xEfva_4.3.F14.boolean.opBoolean","SPLIT",EDGE,{"disambiguationData":[TD([subQ6])],"derivedFrom":makeQuery(id+"FyYUAefgu6xEfva_4.2.F14.boolean.opBoolean","SPLIT",EDGE,{"disambiguationData":[TD([subQ6])],"derivedFrom":makeQuery(id+"FyYUAefgu6xEfva_4.1.F14.boolean.opBoolean","SPLIT",EDGE,{"disambiguationData":[TD([subQ6])],"derivedFrom":makeQuery(id+"F12.opExtrude","CAP_EDGE",EDGE,{"disambiguationData":[OSD([subQ3])],"isStart":true})})})})})})})})})});}
            var Q597;
            {var subQ1=sQuery(id+"F11.wireOp",EDGE,"E143");var subQ3=sQuery(id+"F13.wireOp",EDGE,"E148.MirrorCS");var subQ4=makeQuery(id+"FyYUAefgu6xEfva_4.9.F14.opExtrude","SWEPT_FACE",FACE,{"disambiguationData":[OSD([subQ3])]});var subQ5=sQuery(id+"F13.wireOp",EDGE,"E147");var subQ6=makeQuery(id+"F14.opExtrude","SWEPT_FACE",FACE,{"disambiguationData":[OSD([subQ5])]});Q597=makeQuery(id+"FyYUAefgu6xEfva_4.10.F14.boolean.opBoolean","SPLIT",EDGE,{"disambiguationData":[TD([subQ4])],"derivedFrom":makeQuery(id+"FyYUAefgu6xEfva_4.9.F14.boolean.opBoolean","SPLIT",EDGE,{"disambiguationData":[TD([subQ6])],"derivedFrom":makeQuery(id+"FyYUAefgu6xEfva_4.8.F14.boolean.opBoolean","SPLIT",EDGE,{"disambiguationData":[TD([subQ6])],"derivedFrom":makeQuery(id+"FyYUAefgu6xEfva_4.7.F14.boolean.opBoolean","SPLIT",EDGE,{"disambiguationData":[TD([subQ6])],"derivedFrom":makeQuery(id+"FyYUAefgu6xEfva_4.6.F14.boolean.opBoolean","SPLIT",EDGE,{"disambiguationData":[TD([subQ6])],"derivedFrom":makeQuery(id+"FyYUAefgu6xEfva_4.5.F14.boolean.opBoolean","SPLIT",EDGE,{"disambiguationData":[TD([subQ6])],"derivedFrom":makeQuery(id+"FyYUAefgu6xEfva_4.4.F14.boolean.opBoolean","SPLIT",EDGE,{"disambiguationData":[TD([subQ6])],"derivedFrom":makeQuery(id+"FyYUAefgu6xEfva_4.3.F14.boolean.opBoolean","SPLIT",EDGE,{"disambiguationData":[TD([subQ6])],"derivedFrom":makeQuery(id+"FyYUAefgu6xEfva_4.2.F14.boolean.opBoolean","SPLIT",EDGE,{"disambiguationData":[TD([subQ6])],"derivedFrom":makeQuery(id+"FyYUAefgu6xEfva_4.1.F14.boolean.opBoolean","SPLIT",EDGE,{"disambiguationData":[TD([subQ6])],"derivedFrom":makeQuery(id+"F12.opExtrude","CAP_EDGE",EDGE,{"disambiguationData":[OSD([subQ1])],"isStart":true})})})})})})})})})})});}
            var Q598;
            Q598=makeQuery(id+"FyYUAefgu6xEfva_4.11.F14.opExtrude","CAP_EDGE",EDGE,{"disambiguationData":[OSD([sQuery(id+"F13.wireOp",EDGE,"E148.MirrorCS")])],"isStart":true});
            var Q599;
            {var subQ1=sQuery(id+"F11.wireOp",EDGE,"E143");var subQ3=sQuery(id+"F13.wireOp",EDGE,"E148.MirrorCS");var subQ4=makeQuery(id+"FyYUAefgu6xEfva_4.10.F14.opExtrude","SWEPT_FACE",FACE,{"disambiguationData":[OSD([subQ3])]});var subQ5=sQuery(id+"F13.wireOp",EDGE,"E147");var subQ6=makeQuery(id+"F14.opExtrude","SWEPT_FACE",FACE,{"disambiguationData":[OSD([subQ5])]});Q599=makeQuery(id+"FyYUAefgu6xEfva_4.11.F14.boolean.opBoolean","SPLIT",EDGE,{"disambiguationData":[TD([subQ4])],"derivedFrom":makeQuery(id+"FyYUAefgu6xEfva_4.10.F14.boolean.opBoolean","SPLIT",EDGE,{"disambiguationData":[TD([subQ6])],"derivedFrom":makeQuery(id+"FyYUAefgu6xEfva_4.9.F14.boolean.opBoolean","SPLIT",EDGE,{"disambiguationData":[TD([subQ6])],"derivedFrom":makeQuery(id+"FyYUAefgu6xEfva_4.8.F14.boolean.opBoolean","SPLIT",EDGE,{"disambiguationData":[TD([subQ6])],"derivedFrom":makeQuery(id+"FyYUAefgu6xEfva_4.7.F14.boolean.opBoolean","SPLIT",EDGE,{"disambiguationData":[TD([subQ6])],"derivedFrom":makeQuery(id+"FyYUAefgu6xEfva_4.6.F14.boolean.opBoolean","SPLIT",EDGE,{"disambiguationData":[TD([subQ6])],"derivedFrom":makeQuery(id+"FyYUAefgu6xEfva_4.5.F14.boolean.opBoolean","SPLIT",EDGE,{"disambiguationData":[TD([subQ6])],"derivedFrom":makeQuery(id+"FyYUAefgu6xEfva_4.4.F14.boolean.opBoolean","SPLIT",EDGE,{"disambiguationData":[TD([subQ6])],"derivedFrom":makeQuery(id+"FyYUAefgu6xEfva_4.3.F14.boolean.opBoolean","SPLIT",EDGE,{"disambiguationData":[TD([subQ6])],"derivedFrom":makeQuery(id+"FyYUAefgu6xEfva_4.2.F14.boolean.opBoolean","SPLIT",EDGE,{"disambiguationData":[TD([subQ6])],"derivedFrom":makeQuery(id+"FyYUAefgu6xEfva_4.1.F14.boolean.opBoolean","SPLIT",EDGE,{"disambiguationData":[TD([subQ6])],"derivedFrom":makeQuery(id+"F12.opExtrude","CAP_EDGE",EDGE,{"disambiguationData":[OSD([subQ1])],"isStart":true})})})})})})})})})})})});}
            var Q600;
            Q600=makeQuery(id+"FyYUAefgu6xEfva_4.12.F14.opExtrude","CAP_EDGE",EDGE,{"disambiguationData":[OSD([sQuery(id+"F13.wireOp",EDGE,"E147")])],"isStart":true});
            var Q601;
            Q601=makeQuery(id+"FyYUAefgu6xEfva_4.12.F14.opExtrude","CAP_EDGE",EDGE,{"disambiguationData":[OSD([sQuery(id+"F13.wireOp",EDGE,"E148.MirrorCS")])],"isStart":true});
            var Q602;
            Q602=makeQuery(id+"FyYUAefgu6xEfva_4.13.F14.opExtrude","CAP_EDGE",EDGE,{"disambiguationData":[OSD([sQuery(id+"F13.wireOp",EDGE,"E147")])],"isStart":true});
            var Q603;
            {var subQ1=sQuery(id+"F11.wireOp",EDGE,"E143");var subQ3=sQuery(id+"F13.wireOp",EDGE,"E147");var subQ4=sQuery(id+"F13.wireOp",EDGE,"E148.MirrorCS");var subQ5=makeQuery(id+"FyYUAefgu6xEfva_4.12.F14.opExtrude","SWEPT_FACE",FACE,{"disambiguationData":[OSD([subQ4])]});var subQ6=makeQuery(id+"F14.opExtrude","SWEPT_FACE",FACE,{"disambiguationData":[OSD([subQ3])]});Q603=makeQuery(id+"FyYUAefgu6xEfva_4.13.F14.boolean.opBoolean","SPLIT",EDGE,{"disambiguationData":[TD([subQ5])],"derivedFrom":makeQuery(id+"FyYUAefgu6xEfva_4.12.F14.boolean.opBoolean","SPLIT",EDGE,{"disambiguationData":[TD([subQ6])],"derivedFrom":makeQuery(id+"FyYUAefgu6xEfva_4.11.F14.boolean.opBoolean","SPLIT",EDGE,{"disambiguationData":[TD([subQ6])],"derivedFrom":makeQuery(id+"FyYUAefgu6xEfva_4.10.F14.boolean.opBoolean","SPLIT",EDGE,{"disambiguationData":[TD([subQ6])],"derivedFrom":makeQuery(id+"FyYUAefgu6xEfva_4.9.F14.boolean.opBoolean","SPLIT",EDGE,{"disambiguationData":[TD([subQ6])],"derivedFrom":makeQuery(id+"FyYUAefgu6xEfva_4.8.F14.boolean.opBoolean","SPLIT",EDGE,{"disambiguationData":[TD([subQ6])],"derivedFrom":makeQuery(id+"FyYUAefgu6xEfva_4.7.F14.boolean.opBoolean","SPLIT",EDGE,{"disambiguationData":[TD([subQ6])],"derivedFrom":makeQuery(id+"FyYUAefgu6xEfva_4.6.F14.boolean.opBoolean","SPLIT",EDGE,{"disambiguationData":[TD([subQ6])],"derivedFrom":makeQuery(id+"FyYUAefgu6xEfva_4.5.F14.boolean.opBoolean","SPLIT",EDGE,{"disambiguationData":[TD([subQ6])],"derivedFrom":makeQuery(id+"FyYUAefgu6xEfva_4.4.F14.boolean.opBoolean","SPLIT",EDGE,{"disambiguationData":[TD([subQ6])],"derivedFrom":makeQuery(id+"FyYUAefgu6xEfva_4.3.F14.boolean.opBoolean","SPLIT",EDGE,{"disambiguationData":[TD([subQ6])],"derivedFrom":makeQuery(id+"FyYUAefgu6xEfva_4.2.F14.boolean.opBoolean","SPLIT",EDGE,{"disambiguationData":[TD([subQ6])],"derivedFrom":makeQuery(id+"FyYUAefgu6xEfva_4.1.F14.boolean.opBoolean","SPLIT",EDGE,{"disambiguationData":[TD([subQ6])],"derivedFrom":makeQuery(id+"F12.opExtrude","CAP_EDGE",EDGE,{"disambiguationData":[OSD([subQ1])],"isStart":true})})})})})})})})})})})})})});}
            var Q604;
            {var subQ1=sQuery(id+"F13.wireOp",EDGE,"E148.MirrorCS");var subQ2=makeQuery(id+"FyYUAefgu6xEfva_4.13.F14.opExtrude","SWEPT_FACE",FACE,{"disambiguationData":[OSD([subQ1])]});var subQ3=sQuery(id+"F11.wireOp",EDGE,"E143");var subQ5=sQuery(id+"F13.wireOp",EDGE,"E147");var subQ6=makeQuery(id+"F14.opExtrude","SWEPT_FACE",FACE,{"disambiguationData":[OSD([subQ5])]});Q604=makeQuery(id+"FyYUAefgu6xEfva_4.14.F14.boolean.opBoolean","SPLIT",EDGE,{"disambiguationData":[TD([subQ2])],"derivedFrom":makeQuery(id+"FyYUAefgu6xEfva_4.13.F14.boolean.opBoolean","SPLIT",EDGE,{"disambiguationData":[TD([subQ6])],"derivedFrom":makeQuery(id+"FyYUAefgu6xEfva_4.12.F14.boolean.opBoolean","SPLIT",EDGE,{"disambiguationData":[TD([subQ6])],"derivedFrom":makeQuery(id+"FyYUAefgu6xEfva_4.11.F14.boolean.opBoolean","SPLIT",EDGE,{"disambiguationData":[TD([subQ6])],"derivedFrom":makeQuery(id+"FyYUAefgu6xEfva_4.10.F14.boolean.opBoolean","SPLIT",EDGE,{"disambiguationData":[TD([subQ6])],"derivedFrom":makeQuery(id+"FyYUAefgu6xEfva_4.9.F14.boolean.opBoolean","SPLIT",EDGE,{"disambiguationData":[TD([subQ6])],"derivedFrom":makeQuery(id+"FyYUAefgu6xEfva_4.8.F14.boolean.opBoolean","SPLIT",EDGE,{"disambiguationData":[TD([subQ6])],"derivedFrom":makeQuery(id+"FyYUAefgu6xEfva_4.7.F14.boolean.opBoolean","SPLIT",EDGE,{"disambiguationData":[TD([subQ6])],"derivedFrom":makeQuery(id+"FyYUAefgu6xEfva_4.6.F14.boolean.opBoolean","SPLIT",EDGE,{"disambiguationData":[TD([subQ6])],"derivedFrom":makeQuery(id+"FyYUAefgu6xEfva_4.5.F14.boolean.opBoolean","SPLIT",EDGE,{"disambiguationData":[TD([subQ6])],"derivedFrom":makeQuery(id+"FyYUAefgu6xEfva_4.4.F14.boolean.opBoolean","SPLIT",EDGE,{"disambiguationData":[TD([subQ6])],"derivedFrom":makeQuery(id+"FyYUAefgu6xEfva_4.3.F14.boolean.opBoolean","SPLIT",EDGE,{"disambiguationData":[TD([subQ6])],"derivedFrom":makeQuery(id+"FyYUAefgu6xEfva_4.2.F14.boolean.opBoolean","SPLIT",EDGE,{"disambiguationData":[TD([subQ6])],"derivedFrom":makeQuery(id+"FyYUAefgu6xEfva_4.1.F14.boolean.opBoolean","SPLIT",EDGE,{"disambiguationData":[TD([subQ6])],"derivedFrom":makeQuery(id+"F12.opExtrude","CAP_EDGE",EDGE,{"disambiguationData":[OSD([subQ3])],"isStart":true})})})})})})})})})})})})})})});}
            var Q605;
            Q605=makeQuery(id+"F2.opRevolve","SWEPT_EDGE",EDGE,{"disambiguationData":[OSD([sQuery(id+"F0.wireOp",EDGE,"E71"),sQuery(id+"F0.wireOp",EDGE,"E77.filletArc")])]});
            fillet(context, id + "F15", {"entities" : qUnion([Q0, Q1, Q2, Q3, Q4, Q5, Q6, Q7, Q8, Q9, Q10, Q11, Q12, Q13, Q14, Q15, Q16, Q17, Q18, Q19, Q20, Q21, Q22, Q23, Q24, Q25, Q26, Q27, Q28, Q29, Q30, Q31, Q32, Q33, Q34, Q35, Q36, Q37, Q38, Q39, Q40, Q41, Q42, Q43, Q44, Q45, Q46, Q47, Q48, Q49, Q50, Q51, Q52, Q53, Q54, Q55, Q56, Q57, Q58, Q59, Q60, Q61, Q62, Q63, Q64, Q65, Q66, Q67, Q68, Q69, Q70, Q71, Q72, Q73, Q74, Q75, Q76, Q77, Q78, Q79, Q80, Q81, Q82, Q83, Q84, Q85, Q86, Q87, Q88, Q89, Q90, Q91, Q92, Q93, Q94, Q95, Q96, Q97, Q98, Q99, Q100, Q101, Q102, Q103, Q104, Q105, Q106, Q107, Q108, Q109, Q110, Q111, Q112, Q113, Q114, Q115, Q116, Q117, Q118, Q119, Q120, Q121, Q122, Q123, Q124, Q125, Q126, Q127, Q128, Q129, Q130, Q131, Q132, Q133, Q134, Q135, Q136, Q137, Q138, Q139, Q140, Q141, Q142, Q143, Q144, Q145, Q146, Q147, Q148, Q149, Q150, Q151, Q152, Q153, Q154, Q155, Q156, Q157, Q158, Q159, Q160, Q161, Q162, Q163, Q164, Q165, Q166, Q167, Q168, Q169, Q170, Q171, Q172, Q173, Q174, Q175, Q176, Q177, Q178, Q179, Q180, Q181, Q182, Q183, Q184, Q185, Q186, Q187, Q188, Q189, Q190, Q191, Q192, Q193, Q194, Q195, Q196, Q197, Q198, Q199, Q200, Q201, Q202, Q203, Q204, Q205, Q206, Q207, Q208, Q209, Q210, Q211, Q212, Q213, Q214, Q215, Q216, Q217, Q218, Q219, Q220, Q221, Q222, Q223, Q224, Q225, Q226, Q227, Q228, Q229, Q230, Q231, Q232, Q233, Q234, Q235, Q236, Q237, Q238, Q239, Q240, Q241, Q242, Q243, Q244, Q245, Q246, Q247, Q248, Q249, Q250, Q251, Q252, Q253, Q254, Q255, Q256, Q257, Q258, Q259, Q260, Q261, Q262, Q263, Q264, Q265, Q266, Q267, Q268, Q269, Q270, Q271, Q272, Q273, Q274, Q275, Q276, Q277, Q278, Q279, Q280, Q281, Q282, Q283, Q284, Q285, Q286, Q287, Q288, Q289, Q290, Q291, Q292, Q293, Q294, Q295, Q296, Q297, Q298, Q299, Q300, Q301, Q302, Q303, Q304, Q305, Q306, Q307, Q308, Q309, Q310, Q311, Q312, Q313, Q314, Q315, Q316, Q317, Q318, Q319, Q320, Q321, Q322, Q323, Q324, Q325, Q326, Q327, Q328, Q329, Q330, Q331, Q332, Q333, Q334, Q335, Q336, Q337, Q338, Q339, Q340, Q341, Q342, Q343, Q344, Q345, Q346, Q347, Q348, Q349, Q350, Q351, Q352, Q353, Q354, Q355, Q356, Q357, Q358, Q359, Q360, Q361, Q362, Q363, Q364, Q365, Q366, Q367, Q368, Q369, Q370, Q371, Q372, Q373, Q374, Q375, Q376, Q377, Q378, Q379, Q380, Q381, Q382, Q383, Q384, Q385, Q386, Q387, Q388, Q389, Q390, Q391, Q392, Q393, Q394, Q395, Q396, Q397, Q398, Q399, Q400, Q401, Q402, Q403, Q404, Q405, Q406, Q407, Q408, Q409, Q410, Q411, Q412, Q413, Q414, Q415, Q416, Q417, Q418, Q419, Q420, Q421, Q422, Q423, Q424, Q425, Q426, Q427, Q428, Q429, Q430, Q431, Q432, Q433, Q434, Q435, Q436, Q437, Q438, Q439, Q440, Q441, Q442, Q443, Q444, Q445, Q446, Q447, Q448, Q449, Q450, Q451, Q452, Q453, Q454, Q455, Q456, Q457, Q458, Q459, Q460, Q461, Q462, Q463, Q464, Q465, Q466, Q467, Q468, Q469, Q470, Q471, Q472, Q473, Q474, Q475, Q476, Q477, Q478, Q479, Q480, Q481, Q482, Q483, Q484, Q485, Q486, Q487, Q488, Q489, Q490, Q491, Q492, Q493, Q494, Q495, Q496, Q497, Q498, Q499, Q500, Q501, Q502, Q503, Q504, Q505, Q506, Q507, Q508, Q509, Q510, Q511, Q512, Q513, Q514, Q515, Q516, Q517, Q518, Q519, Q520, Q521, Q522, Q523, Q524, Q525, Q526, Q527, Q528, Q529, Q530, Q531, Q532, Q533, Q534, Q535, Q536, Q537, Q538, Q539, Q540, Q541, Q542, Q543, Q544, Q545, Q546, Q547, Q548, Q549, Q550, Q551, Q552, Q553, Q554, Q555, Q556, Q557, Q558, Q559, Q560, Q561, Q562, Q563, Q564, Q565, Q566, Q567, Q568, Q569, Q570, Q571, Q572, Q573, Q574, Q575, Q576, Q577, Q578, Q579, Q580, Q581, Q582, Q583, Q584, Q585, Q586, Q587, Q588, Q589, Q590, Q591, Q592, Q593, Q594, Q595, Q596, Q597, Q598, Q599, Q600, Q601, Q602, Q603, Q604, Q605]), "radius" : .3 * mm, "tangentPropagation" : true, "allowEdgeOverflow" : false});
        }
        {
            var Q0;
            Q0=makeQuery(id+"F1.opRevolve","SWEPT_FACE",FACE,{"disambiguationData":[OSD([sQuery(id+"F0.wireOp",EDGE,"E95"),sQuery(id+"F0.wireOp",EDGE,"E97")])]});
            var sketch = newSketch(context, id + "F16", { "sketchPlane" : qUnion([Q0])});
            skCircle(sketch, "E149.0", {"center": v(0, 26.12) * mm, "radius": 35 * mm});
            skCircle(sketch, "E150.0", {"center": v(0, 26.12) * mm, "radius": 10 * mm});
            skCircle(sketch, "E151", {"center": v(0, 26.12) * mm, "radius": 17.5 * mm});
            skCircle(sketch, "E152", {"center": v(0, 26.12) * mm, "radius": 32.5 * mm});
            skSolve(sketch);
        }
        {
            var Q0;
            Q0=makeQuery(id+"F16.imprint","IMPRINT",FACE,{"disambiguationData":[TD([[makeQuery(id+"F16.imprint","IMPRINT",EDGE,{"derivedFrom":sQuery(id+"F16.wireOp",EDGE,"E151")}),-1.0]])]});
            extrude(context, id + "F17", {"entities" : qUnion([Q0]), "operationType" : NewBodyOperationType.REMOVE, "oppositeDirection" : true, "depth" : 40 * mm, "offsetDistance" : 25 * mm});
        }
        {
            var Q0;
            Q0=makeQuery(id+"F17.boolean.opBoolean","SPLIT",FACE,{"disambiguationData":[TD([makeQuery(id+"F1.opRevolve","SWEPT_FACE",FACE,{"disambiguationData":[OSD([sQuery(id+"F0.wireOp",EDGE,"E94")])]})])],"derivedFrom":makeQuery(id+"F1.opRevolve","SWEPT_FACE",FACE,{"disambiguationData":[OSD([sQuery(id+"F0.wireOp",EDGE,"E95"),sQuery(id+"F0.wireOp",EDGE,"E97")])]})});
            extrude(context, id + "F18", {"entities" : qUnion([Q0]), "operationType" : NewBodyOperationType.REMOVE, "oppositeDirection" : true, "depth" : 5 * mm, "offsetDistance" : 25 * mm});
        }
        {
            var Q0;
            Q0=makeQuery(id+"F17.boolean.opBoolean","COPY",FACE,{"derivedFrom":makeQuery(id+"F17.opExtrude","CAP_FACE",FACE,{"disambiguationData":[OSD([sQuery(id+"F16.wireOp",EDGE,"E151"),sQuery(id+"F16.wireOp",EDGE,"E152")])],"isStart":false})});
            var sketch = newSketch(context, id + "F19", { "sketchPlane" : qUnion([Q0])});
            skCircle(sketch, "E153.0", {"center": v(0, 26.12) * mm, "radius": 32.5 * mm, "construction": true});
            skCircle(sketch, "E154.0", {"center": v(0, 26.12) * mm, "radius": 17.5 * mm, "construction": true});
            skLineSegment(sketch, "E155", {"start": v(0, 58.62) * mm, "end": v(0, -6.38) * mm, "construction": true});
            skLineSegment(sketch, "E156", {"start": v(-32.5, 26.12) * mm, "end": v(32.5, 26.12) * mm, "construction": true});
            skLineSegment(sketch, "E157", {"start": v(-0.75, 58.6) * mm, "end": v(-0.5, 43.61) * mm});
            skLineSegment(sketch, "E158.MirrorCS", {"start": v(0.75, 58.6) * mm, "end": v(0.5, 43.61) * mm});
            skSolve(sketch);
        }
        {
            var Q0;
            {var subQ0=sQuery(id+"F19.wireOp",EDGE,"E157");Q0=makeQuery(id+"F19.imprint","IMPRINT",FACE,{"disambiguationData":[TD([[makeQuery(id+"F19.imprint","IMPRINT",EDGE,{"derivedFrom":subQ0}),1.0]])]});}
            var Q1;
            Q1=makeQuery(id+"F18.boolean.opBoolean","COPY",FACE,{"derivedFrom":makeQuery(id+"F18.opExtrude","CAP_FACE",FACE,{"disambiguationData":[OSD([sQuery(id+"F0.wireOp",EDGE,"E95"),sQuery(id+"F0.wireOp",EDGE,"E97")])],"isStart":false})});
            extrude(context, id + "F20", {"entities" : qUnion([Q0]), "operationType" : NewBodyOperationType.ADD, "endBound" : BoundingType.UP_TO_SURFACE, "depth" : 25 * mm, "endBoundEntityFace" : qUnion([Q1]), "offsetDistance" : 25 * mm});
        }
        {
            var Q0;
            Q0=makeQuery(id+"F1.opRevolve","SWEPT_FACE",FACE,{"disambiguationData":[OSD([sQuery(id+"F0.wireOp",EDGE,"E102")])]});
            var Q1;
            Q1=makeQuery(id+"F1.opRevolve","SWEPT_FACE",FACE,{"disambiguationData":[OSD([sQuery(id+"F0.wireOp",EDGE,"E107.filletArc")])]});
            var Q2;
            {var subQ0=sQuery(id+"F16.wireOp",EDGE,"E151");var subQ2=sQuery(id+"F16.wireOp",EDGE,"E152");var subQ4=sQuery(id+"F19.wireOp",EDGE,"E158.MirrorCS");var subQ5=makeQuery(id+"F0Hq7nSFAMYVZvY_4.17.F20.opExtrude","SWEPT_FACE",FACE,{"disambiguationData":[OSD([subQ4])]});var subQ6=sQuery(id+"F19.wireOp",EDGE,"E157");var subQ7=makeQuery(id+"F20.opExtrude","SWEPT_FACE",FACE,{"disambiguationData":[OSD([subQ6])]});Q2=makeQuery(id+"F0Hq7nSFAMYVZvY_4.18.F20.boolean.opBoolean","SPLIT",FACE,{"disambiguationData":[TD([subQ5])],"derivedFrom":makeQuery(id+"F0Hq7nSFAMYVZvY_4.17.F20.boolean.opBoolean","SPLIT",FACE,{"disambiguationData":[TD([subQ7])],"derivedFrom":makeQuery(id+"F0Hq7nSFAMYVZvY_4.16.F20.boolean.opBoolean","SPLIT",FACE,{"disambiguationData":[TD([subQ7])],"derivedFrom":makeQuery(id+"F0Hq7nSFAMYVZvY_4.15.F20.boolean.opBoolean","SPLIT",FACE,{"disambiguationData":[TD([subQ7])],"derivedFrom":makeQuery(id+"F0Hq7nSFAMYVZvY_4.14.F20.boolean.opBoolean","SPLIT",FACE,{"disambiguationData":[TD([subQ7])],"derivedFrom":makeQuery(id+"F0Hq7nSFAMYVZvY_4.13.F20.boolean.opBoolean","SPLIT",FACE,{"disambiguationData":[TD([subQ7])],"derivedFrom":makeQuery(id+"F0Hq7nSFAMYVZvY_4.12.F20.boolean.opBoolean","SPLIT",FACE,{"disambiguationData":[TD([subQ7])],"derivedFrom":makeQuery(id+"F0Hq7nSFAMYVZvY_4.11.F20.boolean.opBoolean","SPLIT",FACE,{"disambiguationData":[TD([subQ7])],"derivedFrom":makeQuery(id+"F0Hq7nSFAMYVZvY_4.10.F20.boolean.opBoolean","SPLIT",FACE,{"disambiguationData":[TD([subQ7])],"derivedFrom":makeQuery(id+"F0Hq7nSFAMYVZvY_4.9.F20.boolean.opBoolean","SPLIT",FACE,{"disambiguationData":[TD([subQ7])],"derivedFrom":makeQuery(id+"F0Hq7nSFAMYVZvY_4.8.F20.boolean.opBoolean","SPLIT",FACE,{"disambiguationData":[TD([subQ7])],"derivedFrom":makeQuery(id+"F0Hq7nSFAMYVZvY_4.7.F20.boolean.opBoolean","SPLIT",FACE,{"disambiguationData":[TD([subQ7])],"derivedFrom":makeQuery(id+"F0Hq7nSFAMYVZvY_4.6.F20.boolean.opBoolean","SPLIT",FACE,{"disambiguationData":[TD([subQ7])],"derivedFrom":makeQuery(id+"F0Hq7nSFAMYVZvY_4.5.F20.boolean.opBoolean","SPLIT",FACE,{"disambiguationData":[TD([subQ7])],"derivedFrom":makeQuery(id+"F0Hq7nSFAMYVZvY_4.4.F20.boolean.opBoolean","SPLIT",FACE,{"disambiguationData":[TD([subQ7])],"derivedFrom":makeQuery(id+"F0Hq7nSFAMYVZvY_4.3.F20.boolean.opBoolean","SPLIT",FACE,{"disambiguationData":[TD([subQ7])],"derivedFrom":makeQuery(id+"F0Hq7nSFAMYVZvY_4.2.F20.boolean.opBoolean","SPLIT",FACE,{"disambiguationData":[TD([subQ7])],"derivedFrom":makeQuery(id+"F0Hq7nSFAMYVZvY_4.1.F20.boolean.opBoolean","SPLIT",FACE,{"disambiguationData":[TD([subQ7])],"derivedFrom":makeQuery(id+"F17.boolean.opBoolean","COPY",FACE,{"derivedFrom":makeQuery(id+"F17.opExtrude","CAP_FACE",FACE,{"disambiguationData":[OSD([subQ0,subQ2])],"isStart":false})})})})})})})})})})})})})})})})})})})});}
            var Q3;
            Q3=makeQuery(id+"F18.boolean.opBoolean","COPY",EDGE,{"derivedFrom":makeQuery(id+"F18.opExtrude","CAP_EDGE",EDGE,{"disambiguationData":[OSD([sQuery(id+"F0.wireOp",EDGE,"E94"),sQuery(id+"F0.wireOp",EDGE,"E95")])],"isStart":false})});
            var Q4;
            Q4=makeQuery(id+"F20.opExtrude","SWEPT_FACE",FACE,{"disambiguationData":[OSD([sQuery(id+"F19.wireOp",EDGE,"E157")])]});
            var Q5;
            Q5=makeQuery(id+"F20.opExtrude","SWEPT_FACE",FACE,{"disambiguationData":[OSD([sQuery(id+"F19.wireOp",EDGE,"E158.MirrorCS")])]});
            var Q6;
            Q6=makeQuery(id+"F20.opExtrude","CAP_EDGE",EDGE,{"disambiguationData":[OSD([sQuery(id+"F19.wireOp",EDGE,"E158.MirrorCS")])],"isStart":false});
            var Q7;
            {var subQ0=sQuery(id+"F16.wireOp",EDGE,"E151");var subQ2=sQuery(id+"F16.wireOp",EDGE,"E152");var subQ4=sQuery(id+"F19.wireOp",EDGE,"E157");var subQ5=sQuery(id+"F19.wireOp",EDGE,"E158.MirrorCS");var subQ6=makeQuery(id+"F0Hq7nSFAMYVZvY_4.15.F20.opExtrude","SWEPT_FACE",FACE,{"disambiguationData":[OSD([subQ5])]});var subQ7=makeQuery(id+"F20.opExtrude","SWEPT_FACE",FACE,{"disambiguationData":[OSD([subQ4])]});Q7=makeQuery(id+"F0Hq7nSFAMYVZvY_4.16.F20.boolean.opBoolean","SPLIT",FACE,{"disambiguationData":[TD([subQ6])],"derivedFrom":makeQuery(id+"F0Hq7nSFAMYVZvY_4.15.F20.boolean.opBoolean","SPLIT",FACE,{"disambiguationData":[TD([subQ7])],"derivedFrom":makeQuery(id+"F0Hq7nSFAMYVZvY_4.14.F20.boolean.opBoolean","SPLIT",FACE,{"disambiguationData":[TD([subQ7])],"derivedFrom":makeQuery(id+"F0Hq7nSFAMYVZvY_4.13.F20.boolean.opBoolean","SPLIT",FACE,{"disambiguationData":[TD([subQ7])],"derivedFrom":makeQuery(id+"F0Hq7nSFAMYVZvY_4.12.F20.boolean.opBoolean","SPLIT",FACE,{"disambiguationData":[TD([subQ7])],"derivedFrom":makeQuery(id+"F0Hq7nSFAMYVZvY_4.11.F20.boolean.opBoolean","SPLIT",FACE,{"disambiguationData":[TD([subQ7])],"derivedFrom":makeQuery(id+"F0Hq7nSFAMYVZvY_4.10.F20.boolean.opBoolean","SPLIT",FACE,{"disambiguationData":[TD([subQ7])],"derivedFrom":makeQuery(id+"F0Hq7nSFAMYVZvY_4.9.F20.boolean.opBoolean","SPLIT",FACE,{"disambiguationData":[TD([subQ7])],"derivedFrom":makeQuery(id+"F0Hq7nSFAMYVZvY_4.8.F20.boolean.opBoolean","SPLIT",FACE,{"disambiguationData":[TD([subQ7])],"derivedFrom":makeQuery(id+"F0Hq7nSFAMYVZvY_4.7.F20.boolean.opBoolean","SPLIT",FACE,{"disambiguationData":[TD([subQ7])],"derivedFrom":makeQuery(id+"F0Hq7nSFAMYVZvY_4.6.F20.boolean.opBoolean","SPLIT",FACE,{"disambiguationData":[TD([subQ7])],"derivedFrom":makeQuery(id+"F0Hq7nSFAMYVZvY_4.5.F20.boolean.opBoolean","SPLIT",FACE,{"disambiguationData":[TD([subQ7])],"derivedFrom":makeQuery(id+"F0Hq7nSFAMYVZvY_4.4.F20.boolean.opBoolean","SPLIT",FACE,{"disambiguationData":[TD([subQ7])],"derivedFrom":makeQuery(id+"F0Hq7nSFAMYVZvY_4.3.F20.boolean.opBoolean","SPLIT",FACE,{"disambiguationData":[TD([subQ7])],"derivedFrom":makeQuery(id+"F0Hq7nSFAMYVZvY_4.2.F20.boolean.opBoolean","SPLIT",FACE,{"disambiguationData":[TD([subQ7])],"derivedFrom":makeQuery(id+"F0Hq7nSFAMYVZvY_4.1.F20.boolean.opBoolean","SPLIT",FACE,{"disambiguationData":[TD([subQ7])],"derivedFrom":makeQuery(id+"F17.boolean.opBoolean","COPY",FACE,{"derivedFrom":makeQuery(id+"F17.opExtrude","CAP_FACE",FACE,{"disambiguationData":[OSD([subQ0,subQ2])],"isStart":false})})})})})})})})})})})})})})})})})});}
            var Q8;
            {var subQ0=sQuery(id+"F19.wireOp",EDGE,"E158.MirrorCS");var subQ1=sQuery(id+"F19.wireOp",EDGE,"E157");var subQ3=sQuery(id+"F16.wireOp",EDGE,"E151");var subQ15=makeQuery(id+"F0Hq7nSFAMYVZvY_4.17.F20.opExtrude","SWEPT_FACE",FACE,{"disambiguationData":[OSD([subQ0])]});var subQ25=makeQuery(id+"F20.opExtrude","SWEPT_FACE",FACE,{"disambiguationData":[OSD([subQ1])]});Q8=makeQuery(id+"F0Hq7nSFAMYVZvY_4.18.F20.boolean.opBoolean","SPLIT",EDGE,{"disambiguationData":[TD([subQ15])],"derivedFrom":makeQuery(id+"F0Hq7nSFAMYVZvY_4.17.F20.boolean.opBoolean","SPLIT",EDGE,{"disambiguationData":[TD([subQ25])],"derivedFrom":makeQuery(id+"F0Hq7nSFAMYVZvY_4.16.F20.boolean.opBoolean","SPLIT",EDGE,{"disambiguationData":[TD([subQ25])],"derivedFrom":makeQuery(id+"F0Hq7nSFAMYVZvY_4.15.F20.boolean.opBoolean","SPLIT",EDGE,{"disambiguationData":[TD([subQ25])],"derivedFrom":makeQuery(id+"F0Hq7nSFAMYVZvY_4.14.F20.boolean.opBoolean","SPLIT",EDGE,{"disambiguationData":[TD([subQ25])],"derivedFrom":makeQuery(id+"F0Hq7nSFAMYVZvY_4.13.F20.boolean.opBoolean","SPLIT",EDGE,{"disambiguationData":[TD([subQ25])],"derivedFrom":makeQuery(id+"F0Hq7nSFAMYVZvY_4.12.F20.boolean.opBoolean","SPLIT",EDGE,{"disambiguationData":[TD([subQ25])],"derivedFrom":makeQuery(id+"F0Hq7nSFAMYVZvY_4.11.F20.boolean.opBoolean","SPLIT",EDGE,{"disambiguationData":[TD([subQ25])],"derivedFrom":makeQuery(id+"F0Hq7nSFAMYVZvY_4.10.F20.boolean.opBoolean","SPLIT",EDGE,{"disambiguationData":[TD([subQ25])],"derivedFrom":makeQuery(id+"F0Hq7nSFAMYVZvY_4.9.F20.boolean.opBoolean","SPLIT",EDGE,{"disambiguationData":[TD([subQ25])],"derivedFrom":makeQuery(id+"F0Hq7nSFAMYVZvY_4.8.F20.boolean.opBoolean","SPLIT",EDGE,{"disambiguationData":[TD([subQ25])],"derivedFrom":makeQuery(id+"F0Hq7nSFAMYVZvY_4.7.F20.boolean.opBoolean","SPLIT",EDGE,{"disambiguationData":[TD([subQ25])],"derivedFrom":makeQuery(id+"F0Hq7nSFAMYVZvY_4.6.F20.boolean.opBoolean","SPLIT",EDGE,{"disambiguationData":[TD([subQ25])],"derivedFrom":makeQuery(id+"F0Hq7nSFAMYVZvY_4.5.F20.boolean.opBoolean","SPLIT",EDGE,{"disambiguationData":[TD([subQ25])],"derivedFrom":makeQuery(id+"F0Hq7nSFAMYVZvY_4.4.F20.boolean.opBoolean","SPLIT",EDGE,{"disambiguationData":[TD([subQ25])],"derivedFrom":makeQuery(id+"F0Hq7nSFAMYVZvY_4.3.F20.boolean.opBoolean","SPLIT",EDGE,{"disambiguationData":[TD([subQ25])],"derivedFrom":makeQuery(id+"F0Hq7nSFAMYVZvY_4.2.F20.boolean.opBoolean","SPLIT",EDGE,{"disambiguationData":[TD([subQ25])],"derivedFrom":makeQuery(id+"F0Hq7nSFAMYVZvY_4.1.F20.boolean.opBoolean","SPLIT",EDGE,{"disambiguationData":[TD([subQ25])],"derivedFrom":makeQuery(id+"F18.boolean.opBoolean","COPY",EDGE,{"derivedFrom":makeQuery(id+"F18.opExtrude","CAP_EDGE",EDGE,{"disambiguationData":[OSD([subQ3])],"isStart":false})})})})})})})})})})})})})})})})})})})});}
            var Q9;
            {var subQ0=sQuery(id+"F19.wireOp",EDGE,"E158.MirrorCS");var subQ1=sQuery(id+"F19.wireOp",EDGE,"E157");var subQ3=sQuery(id+"F16.wireOp",EDGE,"E151");var subQ19=makeQuery(id+"F0Hq7nSFAMYVZvY_4.12.F20.opExtrude","SWEPT_FACE",FACE,{"disambiguationData":[OSD([subQ0])]});var subQ20=makeQuery(id+"F20.opExtrude","SWEPT_FACE",FACE,{"disambiguationData":[OSD([subQ1])]});Q9=makeQuery(id+"F0Hq7nSFAMYVZvY_4.13.F20.boolean.opBoolean","SPLIT",FACE,{"disambiguationData":[TD([subQ19])],"derivedFrom":makeQuery(id+"F0Hq7nSFAMYVZvY_4.12.F20.boolean.opBoolean","SPLIT",FACE,{"disambiguationData":[TD([subQ20])],"derivedFrom":makeQuery(id+"F0Hq7nSFAMYVZvY_4.11.F20.boolean.opBoolean","SPLIT",FACE,{"disambiguationData":[TD([subQ20])],"derivedFrom":makeQuery(id+"F0Hq7nSFAMYVZvY_4.10.F20.boolean.opBoolean","SPLIT",FACE,{"disambiguationData":[TD([subQ20])],"derivedFrom":makeQuery(id+"F0Hq7nSFAMYVZvY_4.9.F20.boolean.opBoolean","SPLIT",FACE,{"disambiguationData":[TD([subQ20])],"derivedFrom":makeQuery(id+"F0Hq7nSFAMYVZvY_4.8.F20.boolean.opBoolean","SPLIT",FACE,{"disambiguationData":[TD([subQ20])],"derivedFrom":makeQuery(id+"F0Hq7nSFAMYVZvY_4.7.F20.boolean.opBoolean","SPLIT",FACE,{"disambiguationData":[TD([subQ20])],"derivedFrom":makeQuery(id+"F0Hq7nSFAMYVZvY_4.6.F20.boolean.opBoolean","SPLIT",FACE,{"disambiguationData":[TD([subQ20])],"derivedFrom":makeQuery(id+"F0Hq7nSFAMYVZvY_4.5.F20.boolean.opBoolean","SPLIT",FACE,{"disambiguationData":[TD([subQ20])],"derivedFrom":makeQuery(id+"F0Hq7nSFAMYVZvY_4.4.F20.boolean.opBoolean","SPLIT",FACE,{"disambiguationData":[TD([subQ20])],"derivedFrom":makeQuery(id+"F0Hq7nSFAMYVZvY_4.3.F20.boolean.opBoolean","SPLIT",FACE,{"disambiguationData":[TD([subQ20])],"derivedFrom":makeQuery(id+"F0Hq7nSFAMYVZvY_4.2.F20.boolean.opBoolean","SPLIT",FACE,{"disambiguationData":[TD([subQ20])],"derivedFrom":makeQuery(id+"F0Hq7nSFAMYVZvY_4.1.F20.boolean.opBoolean","SPLIT",FACE,{"disambiguationData":[TD([subQ20])],"derivedFrom":makeQuery(id+"F17.boolean.opBoolean","COPY",FACE,{"derivedFrom":makeQuery(id+"F17.opExtrude","SWEPT_FACE",FACE,{"disambiguationData":[OSD([subQ3])]})})})})})})})})})})})})})})});}
            var Q10;
            {var subQ0=sQuery(id+"F19.wireOp",EDGE,"E158.MirrorCS");var subQ1=sQuery(id+"F19.wireOp",EDGE,"E157");var subQ3=sQuery(id+"F16.wireOp",EDGE,"E151");var subQ16=makeQuery(id+"F0Hq7nSFAMYVZvY_4.17.F20.opExtrude","SWEPT_FACE",FACE,{"disambiguationData":[OSD([subQ0])]});var subQ25=makeQuery(id+"F20.opExtrude","SWEPT_FACE",FACE,{"disambiguationData":[OSD([subQ1])]});Q10=makeQuery(id+"F0Hq7nSFAMYVZvY_4.18.F20.boolean.opBoolean","SPLIT",FACE,{"disambiguationData":[TD([subQ16])],"derivedFrom":makeQuery(id+"F0Hq7nSFAMYVZvY_4.17.F20.boolean.opBoolean","SPLIT",FACE,{"disambiguationData":[TD([subQ25])],"derivedFrom":makeQuery(id+"F0Hq7nSFAMYVZvY_4.16.F20.boolean.opBoolean","SPLIT",FACE,{"disambiguationData":[TD([subQ25])],"derivedFrom":makeQuery(id+"F0Hq7nSFAMYVZvY_4.15.F20.boolean.opBoolean","SPLIT",FACE,{"disambiguationData":[TD([subQ25])],"derivedFrom":makeQuery(id+"F0Hq7nSFAMYVZvY_4.14.F20.boolean.opBoolean","SPLIT",FACE,{"disambiguationData":[TD([subQ25])],"derivedFrom":makeQuery(id+"F0Hq7nSFAMYVZvY_4.13.F20.boolean.opBoolean","SPLIT",FACE,{"disambiguationData":[TD([subQ25])],"derivedFrom":makeQuery(id+"F0Hq7nSFAMYVZvY_4.12.F20.boolean.opBoolean","SPLIT",FACE,{"disambiguationData":[TD([subQ25])],"derivedFrom":makeQuery(id+"F0Hq7nSFAMYVZvY_4.11.F20.boolean.opBoolean","SPLIT",FACE,{"disambiguationData":[TD([subQ25])],"derivedFrom":makeQuery(id+"F0Hq7nSFAMYVZvY_4.10.F20.boolean.opBoolean","SPLIT",FACE,{"disambiguationData":[TD([subQ25])],"derivedFrom":makeQuery(id+"F0Hq7nSFAMYVZvY_4.9.F20.boolean.opBoolean","SPLIT",FACE,{"disambiguationData":[TD([subQ25])],"derivedFrom":makeQuery(id+"F0Hq7nSFAMYVZvY_4.8.F20.boolean.opBoolean","SPLIT",FACE,{"disambiguationData":[TD([subQ25])],"derivedFrom":makeQuery(id+"F0Hq7nSFAMYVZvY_4.7.F20.boolean.opBoolean","SPLIT",FACE,{"disambiguationData":[TD([subQ25])],"derivedFrom":makeQuery(id+"F0Hq7nSFAMYVZvY_4.6.F20.boolean.opBoolean","SPLIT",FACE,{"disambiguationData":[TD([subQ25])],"derivedFrom":makeQuery(id+"F0Hq7nSFAMYVZvY_4.5.F20.boolean.opBoolean","SPLIT",FACE,{"disambiguationData":[TD([subQ25])],"derivedFrom":makeQuery(id+"F0Hq7nSFAMYVZvY_4.4.F20.boolean.opBoolean","SPLIT",FACE,{"disambiguationData":[TD([subQ25])],"derivedFrom":makeQuery(id+"F0Hq7nSFAMYVZvY_4.3.F20.boolean.opBoolean","SPLIT",FACE,{"disambiguationData":[TD([subQ25])],"derivedFrom":makeQuery(id+"F0Hq7nSFAMYVZvY_4.2.F20.boolean.opBoolean","SPLIT",FACE,{"disambiguationData":[TD([subQ25])],"derivedFrom":makeQuery(id+"F0Hq7nSFAMYVZvY_4.1.F20.boolean.opBoolean","SPLIT",FACE,{"disambiguationData":[TD([subQ25])],"derivedFrom":makeQuery(id+"F17.boolean.opBoolean","COPY",FACE,{"derivedFrom":makeQuery(id+"F17.opExtrude","SWEPT_FACE",FACE,{"disambiguationData":[OSD([subQ3])]})})})})})})})})})})})})})})})})})})})});}
            var Q11;
            Q11=makeQuery(id+"F0Hq7nSFAMYVZvY_4.19.F20.opExtrude","SWEPT_FACE",FACE,{"disambiguationData":[OSD([sQuery(id+"F19.wireOp",EDGE,"E158.MirrorCS")])]});
            var Q12;
            Q12=makeQuery(id+"F1.opRevolve","SWEPT_FACE",FACE,{"disambiguationData":[OSD([sQuery(id+"F0.wireOp",EDGE,"E94")])]});
            var Q13;
            {var subQ0=sQuery(id+"F16.wireOp",EDGE,"E151");var subQ3=sQuery(id+"F19.wireOp",EDGE,"E157");var subQ4=sQuery(id+"F19.wireOp",EDGE,"E158.MirrorCS");var subQ5=makeQuery(id+"F0Hq7nSFAMYVZvY_4.17.F20.opExtrude","SWEPT_FACE",FACE,{"disambiguationData":[OSD([subQ4])]});var subQ6=makeQuery(id+"F20.opExtrude","SWEPT_FACE",FACE,{"disambiguationData":[OSD([subQ3])]});Q13=makeQuery(id+"F0Hq7nSFAMYVZvY_4.18.F20.boolean.opBoolean","SPLIT",EDGE,{"disambiguationData":[TD([subQ5])],"derivedFrom":makeQuery(id+"F0Hq7nSFAMYVZvY_4.17.F20.boolean.opBoolean","SPLIT",EDGE,{"disambiguationData":[TD([subQ6])],"derivedFrom":makeQuery(id+"F0Hq7nSFAMYVZvY_4.16.F20.boolean.opBoolean","SPLIT",EDGE,{"disambiguationData":[TD([subQ6])],"derivedFrom":makeQuery(id+"F0Hq7nSFAMYVZvY_4.15.F20.boolean.opBoolean","SPLIT",EDGE,{"disambiguationData":[TD([subQ6])],"derivedFrom":makeQuery(id+"F0Hq7nSFAMYVZvY_4.14.F20.boolean.opBoolean","SPLIT",EDGE,{"disambiguationData":[TD([subQ6])],"derivedFrom":makeQuery(id+"F0Hq7nSFAMYVZvY_4.13.F20.boolean.opBoolean","SPLIT",EDGE,{"disambiguationData":[TD([subQ6])],"derivedFrom":makeQuery(id+"F0Hq7nSFAMYVZvY_4.12.F20.boolean.opBoolean","SPLIT",EDGE,{"disambiguationData":[TD([subQ6])],"derivedFrom":makeQuery(id+"F0Hq7nSFAMYVZvY_4.11.F20.boolean.opBoolean","SPLIT",EDGE,{"disambiguationData":[TD([subQ6])],"derivedFrom":makeQuery(id+"F0Hq7nSFAMYVZvY_4.10.F20.boolean.opBoolean","SPLIT",EDGE,{"disambiguationData":[TD([subQ6])],"derivedFrom":makeQuery(id+"F0Hq7nSFAMYVZvY_4.9.F20.boolean.opBoolean","SPLIT",EDGE,{"disambiguationData":[TD([subQ6])],"derivedFrom":makeQuery(id+"F0Hq7nSFAMYVZvY_4.8.F20.boolean.opBoolean","SPLIT",EDGE,{"disambiguationData":[TD([subQ6])],"derivedFrom":makeQuery(id+"F0Hq7nSFAMYVZvY_4.7.F20.boolean.opBoolean","SPLIT",EDGE,{"disambiguationData":[TD([subQ6])],"derivedFrom":makeQuery(id+"F0Hq7nSFAMYVZvY_4.6.F20.boolean.opBoolean","SPLIT",EDGE,{"disambiguationData":[TD([subQ6])],"derivedFrom":makeQuery(id+"F0Hq7nSFAMYVZvY_4.5.F20.boolean.opBoolean","SPLIT",EDGE,{"disambiguationData":[TD([subQ6])],"derivedFrom":makeQuery(id+"F0Hq7nSFAMYVZvY_4.4.F20.boolean.opBoolean","SPLIT",EDGE,{"disambiguationData":[TD([subQ6])],"derivedFrom":makeQuery(id+"F0Hq7nSFAMYVZvY_4.3.F20.boolean.opBoolean","SPLIT",EDGE,{"disambiguationData":[TD([subQ6])],"derivedFrom":makeQuery(id+"F0Hq7nSFAMYVZvY_4.2.F20.boolean.opBoolean","SPLIT",EDGE,{"disambiguationData":[TD([subQ6])],"derivedFrom":makeQuery(id+"F0Hq7nSFAMYVZvY_4.1.F20.boolean.opBoolean","SPLIT",EDGE,{"disambiguationData":[TD([subQ6])],"derivedFrom":makeQuery(id+"F17.boolean.opBoolean","COPY",EDGE,{"derivedFrom":makeQuery(id+"F17.opExtrude","CAP_EDGE",EDGE,{"disambiguationData":[OSD([subQ0])],"isStart":false})})})})})})})})})})})})})})})})})})})});}
            var Q14;
            {var subQ0=sQuery(id+"F16.wireOp",EDGE,"E151");var subQ2=sQuery(id+"F16.wireOp",EDGE,"E152");var subQ4=sQuery(id+"F19.wireOp",EDGE,"E158.MirrorCS");var subQ5=makeQuery(id+"F0Hq7nSFAMYVZvY_4.12.F20.opExtrude","SWEPT_FACE",FACE,{"disambiguationData":[OSD([subQ4])]});var subQ6=sQuery(id+"F19.wireOp",EDGE,"E157");var subQ7=makeQuery(id+"F20.opExtrude","SWEPT_FACE",FACE,{"disambiguationData":[OSD([subQ6])]});Q14=makeQuery(id+"F0Hq7nSFAMYVZvY_4.13.F20.boolean.opBoolean","SPLIT",FACE,{"disambiguationData":[TD([subQ5])],"derivedFrom":makeQuery(id+"F0Hq7nSFAMYVZvY_4.12.F20.boolean.opBoolean","SPLIT",FACE,{"disambiguationData":[TD([subQ7])],"derivedFrom":makeQuery(id+"F0Hq7nSFAMYVZvY_4.11.F20.boolean.opBoolean","SPLIT",FACE,{"disambiguationData":[TD([subQ7])],"derivedFrom":makeQuery(id+"F0Hq7nSFAMYVZvY_4.10.F20.boolean.opBoolean","SPLIT",FACE,{"disambiguationData":[TD([subQ7])],"derivedFrom":makeQuery(id+"F0Hq7nSFAMYVZvY_4.9.F20.boolean.opBoolean","SPLIT",FACE,{"disambiguationData":[TD([subQ7])],"derivedFrom":makeQuery(id+"F0Hq7nSFAMYVZvY_4.8.F20.boolean.opBoolean","SPLIT",FACE,{"disambiguationData":[TD([subQ7])],"derivedFrom":makeQuery(id+"F0Hq7nSFAMYVZvY_4.7.F20.boolean.opBoolean","SPLIT",FACE,{"disambiguationData":[TD([subQ7])],"derivedFrom":makeQuery(id+"F0Hq7nSFAMYVZvY_4.6.F20.boolean.opBoolean","SPLIT",FACE,{"disambiguationData":[TD([subQ7])],"derivedFrom":makeQuery(id+"F0Hq7nSFAMYVZvY_4.5.F20.boolean.opBoolean","SPLIT",FACE,{"disambiguationData":[TD([subQ7])],"derivedFrom":makeQuery(id+"F0Hq7nSFAMYVZvY_4.4.F20.boolean.opBoolean","SPLIT",FACE,{"disambiguationData":[TD([subQ7])],"derivedFrom":makeQuery(id+"F0Hq7nSFAMYVZvY_4.3.F20.boolean.opBoolean","SPLIT",FACE,{"disambiguationData":[TD([subQ7])],"derivedFrom":makeQuery(id+"F0Hq7nSFAMYVZvY_4.2.F20.boolean.opBoolean","SPLIT",FACE,{"disambiguationData":[TD([subQ7])],"derivedFrom":makeQuery(id+"F0Hq7nSFAMYVZvY_4.1.F20.boolean.opBoolean","SPLIT",FACE,{"disambiguationData":[TD([subQ7])],"derivedFrom":makeQuery(id+"F17.boolean.opBoolean","COPY",FACE,{"derivedFrom":makeQuery(id+"F17.opExtrude","CAP_FACE",FACE,{"disambiguationData":[OSD([subQ0,subQ2])],"isStart":false})})})})})})})})})})})})})})});}
            var Q15;
            Q15=makeQuery(id+"F0Hq7nSFAMYVZvY_4.19.F20.opExtrude","SWEPT_FACE",FACE,{"disambiguationData":[OSD([sQuery(id+"F19.wireOp",EDGE,"E157")])]});
            var Q16;
            {var subQ0=sQuery(id+"F16.wireOp",EDGE,"E151");var subQ2=sQuery(id+"F19.wireOp",EDGE,"E157");var subQ3=sQuery(id+"F16.wireOp",EDGE,"E152");var subQ5=sQuery(id+"F19.wireOp",EDGE,"E158.MirrorCS");var subQ6=makeQuery(id+"F0Hq7nSFAMYVZvY_4.14.F20.opExtrude","SWEPT_FACE",FACE,{"disambiguationData":[OSD([subQ5])]});var subQ7=makeQuery(id+"F20.opExtrude","SWEPT_FACE",FACE,{"disambiguationData":[OSD([subQ2])]});Q16=makeQuery(id+"F0Hq7nSFAMYVZvY_4.15.F20.boolean.opBoolean","SPLIT",FACE,{"disambiguationData":[TD([subQ6])],"derivedFrom":makeQuery(id+"F0Hq7nSFAMYVZvY_4.14.F20.boolean.opBoolean","SPLIT",FACE,{"disambiguationData":[TD([subQ7])],"derivedFrom":makeQuery(id+"F0Hq7nSFAMYVZvY_4.13.F20.boolean.opBoolean","SPLIT",FACE,{"disambiguationData":[TD([subQ7])],"derivedFrom":makeQuery(id+"F0Hq7nSFAMYVZvY_4.12.F20.boolean.opBoolean","SPLIT",FACE,{"disambiguationData":[TD([subQ7])],"derivedFrom":makeQuery(id+"F0Hq7nSFAMYVZvY_4.11.F20.boolean.opBoolean","SPLIT",FACE,{"disambiguationData":[TD([subQ7])],"derivedFrom":makeQuery(id+"F0Hq7nSFAMYVZvY_4.10.F20.boolean.opBoolean","SPLIT",FACE,{"disambiguationData":[TD([subQ7])],"derivedFrom":makeQuery(id+"F0Hq7nSFAMYVZvY_4.9.F20.boolean.opBoolean","SPLIT",FACE,{"disambiguationData":[TD([subQ7])],"derivedFrom":makeQuery(id+"F0Hq7nSFAMYVZvY_4.8.F20.boolean.opBoolean","SPLIT",FACE,{"disambiguationData":[TD([subQ7])],"derivedFrom":makeQuery(id+"F0Hq7nSFAMYVZvY_4.7.F20.boolean.opBoolean","SPLIT",FACE,{"disambiguationData":[TD([subQ7])],"derivedFrom":makeQuery(id+"F0Hq7nSFAMYVZvY_4.6.F20.boolean.opBoolean","SPLIT",FACE,{"disambiguationData":[TD([subQ7])],"derivedFrom":makeQuery(id+"F0Hq7nSFAMYVZvY_4.5.F20.boolean.opBoolean","SPLIT",FACE,{"disambiguationData":[TD([subQ7])],"derivedFrom":makeQuery(id+"F0Hq7nSFAMYVZvY_4.4.F20.boolean.opBoolean","SPLIT",FACE,{"disambiguationData":[TD([subQ7])],"derivedFrom":makeQuery(id+"F0Hq7nSFAMYVZvY_4.3.F20.boolean.opBoolean","SPLIT",FACE,{"disambiguationData":[TD([subQ7])],"derivedFrom":makeQuery(id+"F0Hq7nSFAMYVZvY_4.2.F20.boolean.opBoolean","SPLIT",FACE,{"disambiguationData":[TD([subQ7])],"derivedFrom":makeQuery(id+"F0Hq7nSFAMYVZvY_4.1.F20.boolean.opBoolean","SPLIT",FACE,{"disambiguationData":[TD([subQ7])],"derivedFrom":makeQuery(id+"F17.boolean.opBoolean","COPY",FACE,{"derivedFrom":makeQuery(id+"F17.opExtrude","CAP_FACE",FACE,{"disambiguationData":[OSD([subQ0,subQ3])],"isStart":false})})})})})})})})})})})})})})})})});}
            var Q17;
            Q17=makeQuery(id+"F0Hq7nSFAMYVZvY_4.14.F20.opExtrude","CAP_EDGE",EDGE,{"disambiguationData":[OSD([sQuery(id+"F19.wireOp",EDGE,"E158.MirrorCS")])],"isStart":true});
            var Q18;
            {var subQ0=sQuery(id+"F19.wireOp",EDGE,"E158.MirrorCS");var subQ1=sQuery(id+"F19.wireOp",EDGE,"E157");var subQ3=sQuery(id+"F16.wireOp",EDGE,"E151");var subQ20=makeQuery(id+"F0Hq7nSFAMYVZvY_4.13.F20.opExtrude","SWEPT_FACE",FACE,{"disambiguationData":[OSD([subQ0])]});var subQ21=makeQuery(id+"F20.opExtrude","SWEPT_FACE",FACE,{"disambiguationData":[OSD([subQ1])]});Q18=makeQuery(id+"F0Hq7nSFAMYVZvY_4.14.F20.boolean.opBoolean","SPLIT",FACE,{"disambiguationData":[TD([subQ20])],"derivedFrom":makeQuery(id+"F0Hq7nSFAMYVZvY_4.13.F20.boolean.opBoolean","SPLIT",FACE,{"disambiguationData":[TD([subQ21])],"derivedFrom":makeQuery(id+"F0Hq7nSFAMYVZvY_4.12.F20.boolean.opBoolean","SPLIT",FACE,{"disambiguationData":[TD([subQ21])],"derivedFrom":makeQuery(id+"F0Hq7nSFAMYVZvY_4.11.F20.boolean.opBoolean","SPLIT",FACE,{"disambiguationData":[TD([subQ21])],"derivedFrom":makeQuery(id+"F0Hq7nSFAMYVZvY_4.10.F20.boolean.opBoolean","SPLIT",FACE,{"disambiguationData":[TD([subQ21])],"derivedFrom":makeQuery(id+"F0Hq7nSFAMYVZvY_4.9.F20.boolean.opBoolean","SPLIT",FACE,{"disambiguationData":[TD([subQ21])],"derivedFrom":makeQuery(id+"F0Hq7nSFAMYVZvY_4.8.F20.boolean.opBoolean","SPLIT",FACE,{"disambiguationData":[TD([subQ21])],"derivedFrom":makeQuery(id+"F0Hq7nSFAMYVZvY_4.7.F20.boolean.opBoolean","SPLIT",FACE,{"disambiguationData":[TD([subQ21])],"derivedFrom":makeQuery(id+"F0Hq7nSFAMYVZvY_4.6.F20.boolean.opBoolean","SPLIT",FACE,{"disambiguationData":[TD([subQ21])],"derivedFrom":makeQuery(id+"F0Hq7nSFAMYVZvY_4.5.F20.boolean.opBoolean","SPLIT",FACE,{"disambiguationData":[TD([subQ21])],"derivedFrom":makeQuery(id+"F0Hq7nSFAMYVZvY_4.4.F20.boolean.opBoolean","SPLIT",FACE,{"disambiguationData":[TD([subQ21])],"derivedFrom":makeQuery(id+"F0Hq7nSFAMYVZvY_4.3.F20.boolean.opBoolean","SPLIT",FACE,{"disambiguationData":[TD([subQ21])],"derivedFrom":makeQuery(id+"F0Hq7nSFAMYVZvY_4.2.F20.boolean.opBoolean","SPLIT",FACE,{"disambiguationData":[TD([subQ21])],"derivedFrom":makeQuery(id+"F0Hq7nSFAMYVZvY_4.1.F20.boolean.opBoolean","SPLIT",FACE,{"disambiguationData":[TD([subQ21])],"derivedFrom":makeQuery(id+"F17.boolean.opBoolean","COPY",FACE,{"derivedFrom":makeQuery(id+"F17.opExtrude","SWEPT_FACE",FACE,{"disambiguationData":[OSD([subQ3])]})})})})})})})})})})})})})})})});}
            var Q19;
            {var subQ0=sQuery(id+"F16.wireOp",EDGE,"E151");var subQ2=sQuery(id+"F19.wireOp",EDGE,"E158.MirrorCS");var subQ3=makeQuery(id+"F0Hq7nSFAMYVZvY_4.16.F20.opExtrude","SWEPT_FACE",FACE,{"disambiguationData":[OSD([subQ2])]});var subQ5=sQuery(id+"F19.wireOp",EDGE,"E157");var subQ6=makeQuery(id+"F20.opExtrude","SWEPT_FACE",FACE,{"disambiguationData":[OSD([subQ5])]});Q19=makeQuery(id+"F0Hq7nSFAMYVZvY_4.17.F20.boolean.opBoolean","SPLIT",EDGE,{"disambiguationData":[TD([subQ3])],"derivedFrom":makeQuery(id+"F0Hq7nSFAMYVZvY_4.16.F20.boolean.opBoolean","SPLIT",EDGE,{"disambiguationData":[TD([subQ6])],"derivedFrom":makeQuery(id+"F0Hq7nSFAMYVZvY_4.15.F20.boolean.opBoolean","SPLIT",EDGE,{"disambiguationData":[TD([subQ6])],"derivedFrom":makeQuery(id+"F0Hq7nSFAMYVZvY_4.14.F20.boolean.opBoolean","SPLIT",EDGE,{"disambiguationData":[TD([subQ6])],"derivedFrom":makeQuery(id+"F0Hq7nSFAMYVZvY_4.13.F20.boolean.opBoolean","SPLIT",EDGE,{"disambiguationData":[TD([subQ6])],"derivedFrom":makeQuery(id+"F0Hq7nSFAMYVZvY_4.12.F20.boolean.opBoolean","SPLIT",EDGE,{"disambiguationData":[TD([subQ6])],"derivedFrom":makeQuery(id+"F0Hq7nSFAMYVZvY_4.11.F20.boolean.opBoolean","SPLIT",EDGE,{"disambiguationData":[TD([subQ6])],"derivedFrom":makeQuery(id+"F0Hq7nSFAMYVZvY_4.10.F20.boolean.opBoolean","SPLIT",EDGE,{"disambiguationData":[TD([subQ6])],"derivedFrom":makeQuery(id+"F0Hq7nSFAMYVZvY_4.9.F20.boolean.opBoolean","SPLIT",EDGE,{"disambiguationData":[TD([subQ6])],"derivedFrom":makeQuery(id+"F0Hq7nSFAMYVZvY_4.8.F20.boolean.opBoolean","SPLIT",EDGE,{"disambiguationData":[TD([subQ6])],"derivedFrom":makeQuery(id+"F0Hq7nSFAMYVZvY_4.7.F20.boolean.opBoolean","SPLIT",EDGE,{"disambiguationData":[TD([subQ6])],"derivedFrom":makeQuery(id+"F0Hq7nSFAMYVZvY_4.6.F20.boolean.opBoolean","SPLIT",EDGE,{"disambiguationData":[TD([subQ6])],"derivedFrom":makeQuery(id+"F0Hq7nSFAMYVZvY_4.5.F20.boolean.opBoolean","SPLIT",EDGE,{"disambiguationData":[TD([subQ6])],"derivedFrom":makeQuery(id+"F0Hq7nSFAMYVZvY_4.4.F20.boolean.opBoolean","SPLIT",EDGE,{"disambiguationData":[TD([subQ6])],"derivedFrom":makeQuery(id+"F0Hq7nSFAMYVZvY_4.3.F20.boolean.opBoolean","SPLIT",EDGE,{"disambiguationData":[TD([subQ6])],"derivedFrom":makeQuery(id+"F0Hq7nSFAMYVZvY_4.2.F20.boolean.opBoolean","SPLIT",EDGE,{"disambiguationData":[TD([subQ6])],"derivedFrom":makeQuery(id+"F0Hq7nSFAMYVZvY_4.1.F20.boolean.opBoolean","SPLIT",EDGE,{"disambiguationData":[TD([subQ6])],"derivedFrom":makeQuery(id+"F17.boolean.opBoolean","COPY",EDGE,{"derivedFrom":makeQuery(id+"F17.opExtrude","CAP_EDGE",EDGE,{"disambiguationData":[OSD([subQ0])],"isStart":false})})})})})})})})})})})})})})})})})})});}
            var Q20;
            {var subQ0=sQuery(id+"F16.wireOp",EDGE,"E151");var subQ2=sQuery(id+"F19.wireOp",EDGE,"E158.MirrorCS");var subQ3=makeQuery(id+"F0Hq7nSFAMYVZvY_4.16.F20.opExtrude","SWEPT_FACE",FACE,{"disambiguationData":[OSD([subQ2])]});var subQ4=sQuery(id+"F16.wireOp",EDGE,"E152");var subQ6=sQuery(id+"F19.wireOp",EDGE,"E157");var subQ7=makeQuery(id+"F20.opExtrude","SWEPT_FACE",FACE,{"disambiguationData":[OSD([subQ6])]});Q20=makeQuery(id+"F0Hq7nSFAMYVZvY_4.17.F20.boolean.opBoolean","SPLIT",FACE,{"disambiguationData":[TD([subQ3])],"derivedFrom":makeQuery(id+"F0Hq7nSFAMYVZvY_4.16.F20.boolean.opBoolean","SPLIT",FACE,{"disambiguationData":[TD([subQ7])],"derivedFrom":makeQuery(id+"F0Hq7nSFAMYVZvY_4.15.F20.boolean.opBoolean","SPLIT",FACE,{"disambiguationData":[TD([subQ7])],"derivedFrom":makeQuery(id+"F0Hq7nSFAMYVZvY_4.14.F20.boolean.opBoolean","SPLIT",FACE,{"disambiguationData":[TD([subQ7])],"derivedFrom":makeQuery(id+"F0Hq7nSFAMYVZvY_4.13.F20.boolean.opBoolean","SPLIT",FACE,{"disambiguationData":[TD([subQ7])],"derivedFrom":makeQuery(id+"F0Hq7nSFAMYVZvY_4.12.F20.boolean.opBoolean","SPLIT",FACE,{"disambiguationData":[TD([subQ7])],"derivedFrom":makeQuery(id+"F0Hq7nSFAMYVZvY_4.11.F20.boolean.opBoolean","SPLIT",FACE,{"disambiguationData":[TD([subQ7])],"derivedFrom":makeQuery(id+"F0Hq7nSFAMYVZvY_4.10.F20.boolean.opBoolean","SPLIT",FACE,{"disambiguationData":[TD([subQ7])],"derivedFrom":makeQuery(id+"F0Hq7nSFAMYVZvY_4.9.F20.boolean.opBoolean","SPLIT",FACE,{"disambiguationData":[TD([subQ7])],"derivedFrom":makeQuery(id+"F0Hq7nSFAMYVZvY_4.8.F20.boolean.opBoolean","SPLIT",FACE,{"disambiguationData":[TD([subQ7])],"derivedFrom":makeQuery(id+"F0Hq7nSFAMYVZvY_4.7.F20.boolean.opBoolean","SPLIT",FACE,{"disambiguationData":[TD([subQ7])],"derivedFrom":makeQuery(id+"F0Hq7nSFAMYVZvY_4.6.F20.boolean.opBoolean","SPLIT",FACE,{"disambiguationData":[TD([subQ7])],"derivedFrom":makeQuery(id+"F0Hq7nSFAMYVZvY_4.5.F20.boolean.opBoolean","SPLIT",FACE,{"disambiguationData":[TD([subQ7])],"derivedFrom":makeQuery(id+"F0Hq7nSFAMYVZvY_4.4.F20.boolean.opBoolean","SPLIT",FACE,{"disambiguationData":[TD([subQ7])],"derivedFrom":makeQuery(id+"F0Hq7nSFAMYVZvY_4.3.F20.boolean.opBoolean","SPLIT",FACE,{"disambiguationData":[TD([subQ7])],"derivedFrom":makeQuery(id+"F0Hq7nSFAMYVZvY_4.2.F20.boolean.opBoolean","SPLIT",FACE,{"disambiguationData":[TD([subQ7])],"derivedFrom":makeQuery(id+"F0Hq7nSFAMYVZvY_4.1.F20.boolean.opBoolean","SPLIT",FACE,{"disambiguationData":[TD([subQ7])],"derivedFrom":makeQuery(id+"F17.boolean.opBoolean","COPY",FACE,{"derivedFrom":makeQuery(id+"F17.opExtrude","CAP_FACE",FACE,{"disambiguationData":[OSD([subQ0,subQ4])],"isStart":false})})})})})})})})})})})})})})})})})})});}
            var Q21;
            {var subQ0=sQuery(id+"F19.wireOp",EDGE,"E158.MirrorCS");var subQ1=sQuery(id+"F19.wireOp",EDGE,"E157");var subQ3=sQuery(id+"F16.wireOp",EDGE,"E151");var subQ9=makeQuery(id+"F0Hq7nSFAMYVZvY_4.16.F20.opExtrude","SWEPT_FACE",FACE,{"disambiguationData":[OSD([subQ0])]});var subQ24=makeQuery(id+"F20.opExtrude","SWEPT_FACE",FACE,{"disambiguationData":[OSD([subQ1])]});Q21=makeQuery(id+"F0Hq7nSFAMYVZvY_4.17.F20.boolean.opBoolean","SPLIT",FACE,{"disambiguationData":[TD([subQ9])],"derivedFrom":makeQuery(id+"F0Hq7nSFAMYVZvY_4.16.F20.boolean.opBoolean","SPLIT",FACE,{"disambiguationData":[TD([subQ24])],"derivedFrom":makeQuery(id+"F0Hq7nSFAMYVZvY_4.15.F20.boolean.opBoolean","SPLIT",FACE,{"disambiguationData":[TD([subQ24])],"derivedFrom":makeQuery(id+"F0Hq7nSFAMYVZvY_4.14.F20.boolean.opBoolean","SPLIT",FACE,{"disambiguationData":[TD([subQ24])],"derivedFrom":makeQuery(id+"F0Hq7nSFAMYVZvY_4.13.F20.boolean.opBoolean","SPLIT",FACE,{"disambiguationData":[TD([subQ24])],"derivedFrom":makeQuery(id+"F0Hq7nSFAMYVZvY_4.12.F20.boolean.opBoolean","SPLIT",FACE,{"disambiguationData":[TD([subQ24])],"derivedFrom":makeQuery(id+"F0Hq7nSFAMYVZvY_4.11.F20.boolean.opBoolean","SPLIT",FACE,{"disambiguationData":[TD([subQ24])],"derivedFrom":makeQuery(id+"F0Hq7nSFAMYVZvY_4.10.F20.boolean.opBoolean","SPLIT",FACE,{"disambiguationData":[TD([subQ24])],"derivedFrom":makeQuery(id+"F0Hq7nSFAMYVZvY_4.9.F20.boolean.opBoolean","SPLIT",FACE,{"disambiguationData":[TD([subQ24])],"derivedFrom":makeQuery(id+"F0Hq7nSFAMYVZvY_4.8.F20.boolean.opBoolean","SPLIT",FACE,{"disambiguationData":[TD([subQ24])],"derivedFrom":makeQuery(id+"F0Hq7nSFAMYVZvY_4.7.F20.boolean.opBoolean","SPLIT",FACE,{"disambiguationData":[TD([subQ24])],"derivedFrom":makeQuery(id+"F0Hq7nSFAMYVZvY_4.6.F20.boolean.opBoolean","SPLIT",FACE,{"disambiguationData":[TD([subQ24])],"derivedFrom":makeQuery(id+"F0Hq7nSFAMYVZvY_4.5.F20.boolean.opBoolean","SPLIT",FACE,{"disambiguationData":[TD([subQ24])],"derivedFrom":makeQuery(id+"F0Hq7nSFAMYVZvY_4.4.F20.boolean.opBoolean","SPLIT",FACE,{"disambiguationData":[TD([subQ24])],"derivedFrom":makeQuery(id+"F0Hq7nSFAMYVZvY_4.3.F20.boolean.opBoolean","SPLIT",FACE,{"disambiguationData":[TD([subQ24])],"derivedFrom":makeQuery(id+"F0Hq7nSFAMYVZvY_4.2.F20.boolean.opBoolean","SPLIT",FACE,{"disambiguationData":[TD([subQ24])],"derivedFrom":makeQuery(id+"F0Hq7nSFAMYVZvY_4.1.F20.boolean.opBoolean","SPLIT",FACE,{"disambiguationData":[TD([subQ24])],"derivedFrom":makeQuery(id+"F17.boolean.opBoolean","COPY",FACE,{"derivedFrom":makeQuery(id+"F17.opExtrude","SWEPT_FACE",FACE,{"disambiguationData":[OSD([subQ3])]})})})})})})})})})})})})})})})})})})});}
            var Q22;
            Q22=makeQuery(id+"F0Hq7nSFAMYVZvY_4.17.F20.opExtrude","CAP_EDGE",EDGE,{"disambiguationData":[OSD([sQuery(id+"F19.wireOp",EDGE,"E157")])],"isStart":false});
            var Q23;
            Q23=makeQuery(id+"F0Hq7nSFAMYVZvY_4.17.F20.opExtrude","SWEPT_FACE",FACE,{"disambiguationData":[OSD([sQuery(id+"F19.wireOp",EDGE,"E158.MirrorCS")])]});
            var Q24;
            Q24=makeQuery(id+"F0Hq7nSFAMYVZvY_4.16.F20.opExtrude","SWEPT_FACE",FACE,{"disambiguationData":[OSD([sQuery(id+"F19.wireOp",EDGE,"E157")])]});
            var Q25;
            {var subQ0=sQuery(id+"F16.wireOp",EDGE,"E151");var subQ2=sQuery(id+"F19.wireOp",EDGE,"E157");var subQ4=sQuery(id+"F19.wireOp",EDGE,"E158.MirrorCS");var subQ5=makeQuery(id+"F0Hq7nSFAMYVZvY_4.14.F20.opExtrude","SWEPT_FACE",FACE,{"disambiguationData":[OSD([subQ4])]});var subQ6=makeQuery(id+"F20.opExtrude","SWEPT_FACE",FACE,{"disambiguationData":[OSD([subQ2])]});Q25=makeQuery(id+"F0Hq7nSFAMYVZvY_4.15.F20.boolean.opBoolean","SPLIT",EDGE,{"disambiguationData":[TD([subQ5])],"derivedFrom":makeQuery(id+"F0Hq7nSFAMYVZvY_4.14.F20.boolean.opBoolean","SPLIT",EDGE,{"disambiguationData":[TD([subQ6])],"derivedFrom":makeQuery(id+"F0Hq7nSFAMYVZvY_4.13.F20.boolean.opBoolean","SPLIT",EDGE,{"disambiguationData":[TD([subQ6])],"derivedFrom":makeQuery(id+"F0Hq7nSFAMYVZvY_4.12.F20.boolean.opBoolean","SPLIT",EDGE,{"disambiguationData":[TD([subQ6])],"derivedFrom":makeQuery(id+"F0Hq7nSFAMYVZvY_4.11.F20.boolean.opBoolean","SPLIT",EDGE,{"disambiguationData":[TD([subQ6])],"derivedFrom":makeQuery(id+"F0Hq7nSFAMYVZvY_4.10.F20.boolean.opBoolean","SPLIT",EDGE,{"disambiguationData":[TD([subQ6])],"derivedFrom":makeQuery(id+"F0Hq7nSFAMYVZvY_4.9.F20.boolean.opBoolean","SPLIT",EDGE,{"disambiguationData":[TD([subQ6])],"derivedFrom":makeQuery(id+"F0Hq7nSFAMYVZvY_4.8.F20.boolean.opBoolean","SPLIT",EDGE,{"disambiguationData":[TD([subQ6])],"derivedFrom":makeQuery(id+"F0Hq7nSFAMYVZvY_4.7.F20.boolean.opBoolean","SPLIT",EDGE,{"disambiguationData":[TD([subQ6])],"derivedFrom":makeQuery(id+"F0Hq7nSFAMYVZvY_4.6.F20.boolean.opBoolean","SPLIT",EDGE,{"disambiguationData":[TD([subQ6])],"derivedFrom":makeQuery(id+"F0Hq7nSFAMYVZvY_4.5.F20.boolean.opBoolean","SPLIT",EDGE,{"disambiguationData":[TD([subQ6])],"derivedFrom":makeQuery(id+"F0Hq7nSFAMYVZvY_4.4.F20.boolean.opBoolean","SPLIT",EDGE,{"disambiguationData":[TD([subQ6])],"derivedFrom":makeQuery(id+"F0Hq7nSFAMYVZvY_4.3.F20.boolean.opBoolean","SPLIT",EDGE,{"disambiguationData":[TD([subQ6])],"derivedFrom":makeQuery(id+"F0Hq7nSFAMYVZvY_4.2.F20.boolean.opBoolean","SPLIT",EDGE,{"disambiguationData":[TD([subQ6])],"derivedFrom":makeQuery(id+"F0Hq7nSFAMYVZvY_4.1.F20.boolean.opBoolean","SPLIT",EDGE,{"disambiguationData":[TD([subQ6])],"derivedFrom":makeQuery(id+"F17.boolean.opBoolean","COPY",EDGE,{"derivedFrom":makeQuery(id+"F17.opExtrude","CAP_EDGE",EDGE,{"disambiguationData":[OSD([subQ0])],"isStart":false})})})})})})})})})})})})})})})})});}
            var Q26;
            Q26=makeQuery(id+"F0Hq7nSFAMYVZvY_4.16.F20.opExtrude","CAP_EDGE",EDGE,{"disambiguationData":[OSD([sQuery(id+"F19.wireOp",EDGE,"E158.MirrorCS")])],"isStart":false});
            var Q27;
            {var subQ0=sQuery(id+"F19.wireOp",EDGE,"E158.MirrorCS");var subQ1=sQuery(id+"F19.wireOp",EDGE,"E157");var subQ3=sQuery(id+"F16.wireOp",EDGE,"E151");var subQ12=makeQuery(id+"F0Hq7nSFAMYVZvY_4.14.F20.opExtrude","SWEPT_FACE",FACE,{"disambiguationData":[OSD([subQ0])]});var subQ22=makeQuery(id+"F20.opExtrude","SWEPT_FACE",FACE,{"disambiguationData":[OSD([subQ1])]});Q27=makeQuery(id+"F0Hq7nSFAMYVZvY_4.15.F20.boolean.opBoolean","SPLIT",FACE,{"disambiguationData":[TD([subQ12])],"derivedFrom":makeQuery(id+"F0Hq7nSFAMYVZvY_4.14.F20.boolean.opBoolean","SPLIT",FACE,{"disambiguationData":[TD([subQ22])],"derivedFrom":makeQuery(id+"F0Hq7nSFAMYVZvY_4.13.F20.boolean.opBoolean","SPLIT",FACE,{"disambiguationData":[TD([subQ22])],"derivedFrom":makeQuery(id+"F0Hq7nSFAMYVZvY_4.12.F20.boolean.opBoolean","SPLIT",FACE,{"disambiguationData":[TD([subQ22])],"derivedFrom":makeQuery(id+"F0Hq7nSFAMYVZvY_4.11.F20.boolean.opBoolean","SPLIT",FACE,{"disambiguationData":[TD([subQ22])],"derivedFrom":makeQuery(id+"F0Hq7nSFAMYVZvY_4.10.F20.boolean.opBoolean","SPLIT",FACE,{"disambiguationData":[TD([subQ22])],"derivedFrom":makeQuery(id+"F0Hq7nSFAMYVZvY_4.9.F20.boolean.opBoolean","SPLIT",FACE,{"disambiguationData":[TD([subQ22])],"derivedFrom":makeQuery(id+"F0Hq7nSFAMYVZvY_4.8.F20.boolean.opBoolean","SPLIT",FACE,{"disambiguationData":[TD([subQ22])],"derivedFrom":makeQuery(id+"F0Hq7nSFAMYVZvY_4.7.F20.boolean.opBoolean","SPLIT",FACE,{"disambiguationData":[TD([subQ22])],"derivedFrom":makeQuery(id+"F0Hq7nSFAMYVZvY_4.6.F20.boolean.opBoolean","SPLIT",FACE,{"disambiguationData":[TD([subQ22])],"derivedFrom":makeQuery(id+"F0Hq7nSFAMYVZvY_4.5.F20.boolean.opBoolean","SPLIT",FACE,{"disambiguationData":[TD([subQ22])],"derivedFrom":makeQuery(id+"F0Hq7nSFAMYVZvY_4.4.F20.boolean.opBoolean","SPLIT",FACE,{"disambiguationData":[TD([subQ22])],"derivedFrom":makeQuery(id+"F0Hq7nSFAMYVZvY_4.3.F20.boolean.opBoolean","SPLIT",FACE,{"disambiguationData":[TD([subQ22])],"derivedFrom":makeQuery(id+"F0Hq7nSFAMYVZvY_4.2.F20.boolean.opBoolean","SPLIT",FACE,{"disambiguationData":[TD([subQ22])],"derivedFrom":makeQuery(id+"F0Hq7nSFAMYVZvY_4.1.F20.boolean.opBoolean","SPLIT",FACE,{"disambiguationData":[TD([subQ22])],"derivedFrom":makeQuery(id+"F17.boolean.opBoolean","COPY",FACE,{"derivedFrom":makeQuery(id+"F17.opExtrude","SWEPT_FACE",FACE,{"disambiguationData":[OSD([subQ3])]})})})})})})})})})})})})})})})})});}
            var Q28;
            Q28=makeQuery(id+"F0Hq7nSFAMYVZvY_4.16.F20.opExtrude","CAP_EDGE",EDGE,{"disambiguationData":[OSD([sQuery(id+"F19.wireOp",EDGE,"E158.MirrorCS")])],"isStart":true});
            var Q29;
            Q29=makeQuery(id+"F0Hq7nSFAMYVZvY_4.14.F20.opExtrude","CAP_EDGE",EDGE,{"disambiguationData":[OSD([sQuery(id+"F19.wireOp",EDGE,"E157")])],"isStart":false});
            var Q30;
            Q30=makeQuery(id+"F0Hq7nSFAMYVZvY_4.14.F20.opExtrude","SWEPT_FACE",FACE,{"disambiguationData":[OSD([sQuery(id+"F19.wireOp",EDGE,"E157")])]});
            var Q31;
            Q31=makeQuery(id+"F0Hq7nSFAMYVZvY_4.14.F20.opExtrude","SWEPT_FACE",FACE,{"disambiguationData":[OSD([sQuery(id+"F19.wireOp",EDGE,"E158.MirrorCS")])]});
            var Q32;
            {var subQ0=sQuery(id+"F19.wireOp",EDGE,"E158.MirrorCS");var subQ1=sQuery(id+"F19.wireOp",EDGE,"E157");var subQ3=sQuery(id+"F16.wireOp",EDGE,"E151");var subQ16=makeQuery(id+"F0Hq7nSFAMYVZvY_4.15.F20.opExtrude","SWEPT_FACE",FACE,{"disambiguationData":[OSD([subQ0])]});var subQ23=makeQuery(id+"F20.opExtrude","SWEPT_FACE",FACE,{"disambiguationData":[OSD([subQ1])]});Q32=makeQuery(id+"F0Hq7nSFAMYVZvY_4.16.F20.boolean.opBoolean","SPLIT",EDGE,{"disambiguationData":[TD([subQ16])],"derivedFrom":makeQuery(id+"F0Hq7nSFAMYVZvY_4.15.F20.boolean.opBoolean","SPLIT",EDGE,{"disambiguationData":[TD([subQ23])],"derivedFrom":makeQuery(id+"F0Hq7nSFAMYVZvY_4.14.F20.boolean.opBoolean","SPLIT",EDGE,{"disambiguationData":[TD([subQ23])],"derivedFrom":makeQuery(id+"F0Hq7nSFAMYVZvY_4.13.F20.boolean.opBoolean","SPLIT",EDGE,{"disambiguationData":[TD([subQ23])],"derivedFrom":makeQuery(id+"F0Hq7nSFAMYVZvY_4.12.F20.boolean.opBoolean","SPLIT",EDGE,{"disambiguationData":[TD([subQ23])],"derivedFrom":makeQuery(id+"F0Hq7nSFAMYVZvY_4.11.F20.boolean.opBoolean","SPLIT",EDGE,{"disambiguationData":[TD([subQ23])],"derivedFrom":makeQuery(id+"F0Hq7nSFAMYVZvY_4.10.F20.boolean.opBoolean","SPLIT",EDGE,{"disambiguationData":[TD([subQ23])],"derivedFrom":makeQuery(id+"F0Hq7nSFAMYVZvY_4.9.F20.boolean.opBoolean","SPLIT",EDGE,{"disambiguationData":[TD([subQ23])],"derivedFrom":makeQuery(id+"F0Hq7nSFAMYVZvY_4.8.F20.boolean.opBoolean","SPLIT",EDGE,{"disambiguationData":[TD([subQ23])],"derivedFrom":makeQuery(id+"F0Hq7nSFAMYVZvY_4.7.F20.boolean.opBoolean","SPLIT",EDGE,{"disambiguationData":[TD([subQ23])],"derivedFrom":makeQuery(id+"F0Hq7nSFAMYVZvY_4.6.F20.boolean.opBoolean","SPLIT",EDGE,{"disambiguationData":[TD([subQ23])],"derivedFrom":makeQuery(id+"F0Hq7nSFAMYVZvY_4.5.F20.boolean.opBoolean","SPLIT",EDGE,{"disambiguationData":[TD([subQ23])],"derivedFrom":makeQuery(id+"F0Hq7nSFAMYVZvY_4.4.F20.boolean.opBoolean","SPLIT",EDGE,{"disambiguationData":[TD([subQ23])],"derivedFrom":makeQuery(id+"F0Hq7nSFAMYVZvY_4.3.F20.boolean.opBoolean","SPLIT",EDGE,{"disambiguationData":[TD([subQ23])],"derivedFrom":makeQuery(id+"F0Hq7nSFAMYVZvY_4.2.F20.boolean.opBoolean","SPLIT",EDGE,{"disambiguationData":[TD([subQ23])],"derivedFrom":makeQuery(id+"F0Hq7nSFAMYVZvY_4.1.F20.boolean.opBoolean","SPLIT",EDGE,{"disambiguationData":[TD([subQ23])],"derivedFrom":makeQuery(id+"F18.boolean.opBoolean","COPY",EDGE,{"derivedFrom":makeQuery(id+"F18.opExtrude","CAP_EDGE",EDGE,{"disambiguationData":[OSD([subQ3])],"isStart":false})})})})})})})})})})})})})})})})})});}
            var Q33;
            {var subQ0=sQuery(id+"F16.wireOp",EDGE,"E151");var subQ3=sQuery(id+"F19.wireOp",EDGE,"E158.MirrorCS");var subQ4=makeQuery(id+"F0Hq7nSFAMYVZvY_4.15.F20.opExtrude","SWEPT_FACE",FACE,{"disambiguationData":[OSD([subQ3])]});var subQ5=sQuery(id+"F19.wireOp",EDGE,"E157");var subQ6=makeQuery(id+"F20.opExtrude","SWEPT_FACE",FACE,{"disambiguationData":[OSD([subQ5])]});Q33=makeQuery(id+"F0Hq7nSFAMYVZvY_4.16.F20.boolean.opBoolean","SPLIT",EDGE,{"disambiguationData":[TD([subQ4])],"derivedFrom":makeQuery(id+"F0Hq7nSFAMYVZvY_4.15.F20.boolean.opBoolean","SPLIT",EDGE,{"disambiguationData":[TD([subQ6])],"derivedFrom":makeQuery(id+"F0Hq7nSFAMYVZvY_4.14.F20.boolean.opBoolean","SPLIT",EDGE,{"disambiguationData":[TD([subQ6])],"derivedFrom":makeQuery(id+"F0Hq7nSFAMYVZvY_4.13.F20.boolean.opBoolean","SPLIT",EDGE,{"disambiguationData":[TD([subQ6])],"derivedFrom":makeQuery(id+"F0Hq7nSFAMYVZvY_4.12.F20.boolean.opBoolean","SPLIT",EDGE,{"disambiguationData":[TD([subQ6])],"derivedFrom":makeQuery(id+"F0Hq7nSFAMYVZvY_4.11.F20.boolean.opBoolean","SPLIT",EDGE,{"disambiguationData":[TD([subQ6])],"derivedFrom":makeQuery(id+"F0Hq7nSFAMYVZvY_4.10.F20.boolean.opBoolean","SPLIT",EDGE,{"disambiguationData":[TD([subQ6])],"derivedFrom":makeQuery(id+"F0Hq7nSFAMYVZvY_4.9.F20.boolean.opBoolean","SPLIT",EDGE,{"disambiguationData":[TD([subQ6])],"derivedFrom":makeQuery(id+"F0Hq7nSFAMYVZvY_4.8.F20.boolean.opBoolean","SPLIT",EDGE,{"disambiguationData":[TD([subQ6])],"derivedFrom":makeQuery(id+"F0Hq7nSFAMYVZvY_4.7.F20.boolean.opBoolean","SPLIT",EDGE,{"disambiguationData":[TD([subQ6])],"derivedFrom":makeQuery(id+"F0Hq7nSFAMYVZvY_4.6.F20.boolean.opBoolean","SPLIT",EDGE,{"disambiguationData":[TD([subQ6])],"derivedFrom":makeQuery(id+"F0Hq7nSFAMYVZvY_4.5.F20.boolean.opBoolean","SPLIT",EDGE,{"disambiguationData":[TD([subQ6])],"derivedFrom":makeQuery(id+"F0Hq7nSFAMYVZvY_4.4.F20.boolean.opBoolean","SPLIT",EDGE,{"disambiguationData":[TD([subQ6])],"derivedFrom":makeQuery(id+"F0Hq7nSFAMYVZvY_4.3.F20.boolean.opBoolean","SPLIT",EDGE,{"disambiguationData":[TD([subQ6])],"derivedFrom":makeQuery(id+"F0Hq7nSFAMYVZvY_4.2.F20.boolean.opBoolean","SPLIT",EDGE,{"disambiguationData":[TD([subQ6])],"derivedFrom":makeQuery(id+"F0Hq7nSFAMYVZvY_4.1.F20.boolean.opBoolean","SPLIT",EDGE,{"disambiguationData":[TD([subQ6])],"derivedFrom":makeQuery(id+"F17.boolean.opBoolean","COPY",EDGE,{"derivedFrom":makeQuery(id+"F17.opExtrude","CAP_EDGE",EDGE,{"disambiguationData":[OSD([subQ0])],"isStart":false})})})})})})})})})})})})})})})})})});}
            var Q34;
            Q34=makeQuery(id+"F0Hq7nSFAMYVZvY_4.15.F20.opExtrude","CAP_EDGE",EDGE,{"disambiguationData":[OSD([sQuery(id+"F19.wireOp",EDGE,"E158.MirrorCS")])],"isStart":false});
            var Q35;
            Q35=makeQuery(id+"F0Hq7nSFAMYVZvY_4.15.F20.opExtrude","CAP_EDGE",EDGE,{"disambiguationData":[OSD([sQuery(id+"F19.wireOp",EDGE,"E157")])],"isStart":false});
            var Q36;
            {var subQ0=sQuery(id+"F19.wireOp",EDGE,"E158.MirrorCS");var subQ1=sQuery(id+"F19.wireOp",EDGE,"E157");var subQ3=sQuery(id+"F16.wireOp",EDGE,"E151");var subQ20=makeQuery(id+"F0Hq7nSFAMYVZvY_4.13.F20.opExtrude","SWEPT_FACE",FACE,{"disambiguationData":[OSD([subQ0])]});var subQ21=makeQuery(id+"F20.opExtrude","SWEPT_FACE",FACE,{"disambiguationData":[OSD([subQ1])]});Q36=makeQuery(id+"F0Hq7nSFAMYVZvY_4.14.F20.boolean.opBoolean","SPLIT",EDGE,{"disambiguationData":[TD([subQ20])],"derivedFrom":makeQuery(id+"F0Hq7nSFAMYVZvY_4.13.F20.boolean.opBoolean","SPLIT",EDGE,{"disambiguationData":[TD([subQ21])],"derivedFrom":makeQuery(id+"F0Hq7nSFAMYVZvY_4.12.F20.boolean.opBoolean","SPLIT",EDGE,{"disambiguationData":[TD([subQ21])],"derivedFrom":makeQuery(id+"F0Hq7nSFAMYVZvY_4.11.F20.boolean.opBoolean","SPLIT",EDGE,{"disambiguationData":[TD([subQ21])],"derivedFrom":makeQuery(id+"F0Hq7nSFAMYVZvY_4.10.F20.boolean.opBoolean","SPLIT",EDGE,{"disambiguationData":[TD([subQ21])],"derivedFrom":makeQuery(id+"F0Hq7nSFAMYVZvY_4.9.F20.boolean.opBoolean","SPLIT",EDGE,{"disambiguationData":[TD([subQ21])],"derivedFrom":makeQuery(id+"F0Hq7nSFAMYVZvY_4.8.F20.boolean.opBoolean","SPLIT",EDGE,{"disambiguationData":[TD([subQ21])],"derivedFrom":makeQuery(id+"F0Hq7nSFAMYVZvY_4.7.F20.boolean.opBoolean","SPLIT",EDGE,{"disambiguationData":[TD([subQ21])],"derivedFrom":makeQuery(id+"F0Hq7nSFAMYVZvY_4.6.F20.boolean.opBoolean","SPLIT",EDGE,{"disambiguationData":[TD([subQ21])],"derivedFrom":makeQuery(id+"F0Hq7nSFAMYVZvY_4.5.F20.boolean.opBoolean","SPLIT",EDGE,{"disambiguationData":[TD([subQ21])],"derivedFrom":makeQuery(id+"F0Hq7nSFAMYVZvY_4.4.F20.boolean.opBoolean","SPLIT",EDGE,{"disambiguationData":[TD([subQ21])],"derivedFrom":makeQuery(id+"F0Hq7nSFAMYVZvY_4.3.F20.boolean.opBoolean","SPLIT",EDGE,{"disambiguationData":[TD([subQ21])],"derivedFrom":makeQuery(id+"F0Hq7nSFAMYVZvY_4.2.F20.boolean.opBoolean","SPLIT",EDGE,{"disambiguationData":[TD([subQ21])],"derivedFrom":makeQuery(id+"F0Hq7nSFAMYVZvY_4.1.F20.boolean.opBoolean","SPLIT",EDGE,{"disambiguationData":[TD([subQ21])],"derivedFrom":makeQuery(id+"F18.boolean.opBoolean","COPY",EDGE,{"derivedFrom":makeQuery(id+"F18.opExtrude","CAP_EDGE",EDGE,{"disambiguationData":[OSD([subQ3])],"isStart":false})})})})})})})})})})})})})})})});}
            var Q37;
            Q37=makeQuery(id+"F0Hq7nSFAMYVZvY_4.15.F20.opExtrude","SWEPT_FACE",FACE,{"disambiguationData":[OSD([sQuery(id+"F19.wireOp",EDGE,"E158.MirrorCS")])]});
            var Q38;
            Q38=makeQuery(id+"F0Hq7nSFAMYVZvY_4.15.F20.opExtrude","SWEPT_FACE",FACE,{"disambiguationData":[OSD([sQuery(id+"F19.wireOp",EDGE,"E157")])]});
            var Q39;
            {var subQ0=sQuery(id+"F16.wireOp",EDGE,"E151");var subQ3=sQuery(id+"F19.wireOp",EDGE,"E158.MirrorCS");var subQ4=makeQuery(id+"F0Hq7nSFAMYVZvY_4.13.F20.opExtrude","SWEPT_FACE",FACE,{"disambiguationData":[OSD([subQ3])]});var subQ5=sQuery(id+"F19.wireOp",EDGE,"E157");var subQ6=makeQuery(id+"F20.opExtrude","SWEPT_FACE",FACE,{"disambiguationData":[OSD([subQ5])]});Q39=makeQuery(id+"F0Hq7nSFAMYVZvY_4.14.F20.boolean.opBoolean","SPLIT",EDGE,{"disambiguationData":[TD([subQ4])],"derivedFrom":makeQuery(id+"F0Hq7nSFAMYVZvY_4.13.F20.boolean.opBoolean","SPLIT",EDGE,{"disambiguationData":[TD([subQ6])],"derivedFrom":makeQuery(id+"F0Hq7nSFAMYVZvY_4.12.F20.boolean.opBoolean","SPLIT",EDGE,{"disambiguationData":[TD([subQ6])],"derivedFrom":makeQuery(id+"F0Hq7nSFAMYVZvY_4.11.F20.boolean.opBoolean","SPLIT",EDGE,{"disambiguationData":[TD([subQ6])],"derivedFrom":makeQuery(id+"F0Hq7nSFAMYVZvY_4.10.F20.boolean.opBoolean","SPLIT",EDGE,{"disambiguationData":[TD([subQ6])],"derivedFrom":makeQuery(id+"F0Hq7nSFAMYVZvY_4.9.F20.boolean.opBoolean","SPLIT",EDGE,{"disambiguationData":[TD([subQ6])],"derivedFrom":makeQuery(id+"F0Hq7nSFAMYVZvY_4.8.F20.boolean.opBoolean","SPLIT",EDGE,{"disambiguationData":[TD([subQ6])],"derivedFrom":makeQuery(id+"F0Hq7nSFAMYVZvY_4.7.F20.boolean.opBoolean","SPLIT",EDGE,{"disambiguationData":[TD([subQ6])],"derivedFrom":makeQuery(id+"F0Hq7nSFAMYVZvY_4.6.F20.boolean.opBoolean","SPLIT",EDGE,{"disambiguationData":[TD([subQ6])],"derivedFrom":makeQuery(id+"F0Hq7nSFAMYVZvY_4.5.F20.boolean.opBoolean","SPLIT",EDGE,{"disambiguationData":[TD([subQ6])],"derivedFrom":makeQuery(id+"F0Hq7nSFAMYVZvY_4.4.F20.boolean.opBoolean","SPLIT",EDGE,{"disambiguationData":[TD([subQ6])],"derivedFrom":makeQuery(id+"F0Hq7nSFAMYVZvY_4.3.F20.boolean.opBoolean","SPLIT",EDGE,{"disambiguationData":[TD([subQ6])],"derivedFrom":makeQuery(id+"F0Hq7nSFAMYVZvY_4.2.F20.boolean.opBoolean","SPLIT",EDGE,{"disambiguationData":[TD([subQ6])],"derivedFrom":makeQuery(id+"F0Hq7nSFAMYVZvY_4.1.F20.boolean.opBoolean","SPLIT",EDGE,{"disambiguationData":[TD([subQ6])],"derivedFrom":makeQuery(id+"F17.boolean.opBoolean","COPY",EDGE,{"derivedFrom":makeQuery(id+"F17.opExtrude","CAP_EDGE",EDGE,{"disambiguationData":[OSD([subQ0])],"isStart":false})})})})})})})})})})})})})})})});}
            var Q40;
            Q40=makeQuery(id+"F0Hq7nSFAMYVZvY_4.14.F20.opExtrude","CAP_EDGE",EDGE,{"disambiguationData":[OSD([sQuery(id+"F19.wireOp",EDGE,"E158.MirrorCS")])],"isStart":false});
            var Q41;
            {var subQ0=sQuery(id+"F16.wireOp",EDGE,"E151");var subQ2=sQuery(id+"F16.wireOp",EDGE,"E152");var subQ4=sQuery(id+"F19.wireOp",EDGE,"E158.MirrorCS");var subQ5=makeQuery(id+"F0Hq7nSFAMYVZvY_4.13.F20.opExtrude","SWEPT_FACE",FACE,{"disambiguationData":[OSD([subQ4])]});var subQ6=sQuery(id+"F19.wireOp",EDGE,"E157");var subQ7=makeQuery(id+"F20.opExtrude","SWEPT_FACE",FACE,{"disambiguationData":[OSD([subQ6])]});Q41=makeQuery(id+"F0Hq7nSFAMYVZvY_4.14.F20.boolean.opBoolean","SPLIT",FACE,{"disambiguationData":[TD([subQ5])],"derivedFrom":makeQuery(id+"F0Hq7nSFAMYVZvY_4.13.F20.boolean.opBoolean","SPLIT",FACE,{"disambiguationData":[TD([subQ7])],"derivedFrom":makeQuery(id+"F0Hq7nSFAMYVZvY_4.12.F20.boolean.opBoolean","SPLIT",FACE,{"disambiguationData":[TD([subQ7])],"derivedFrom":makeQuery(id+"F0Hq7nSFAMYVZvY_4.11.F20.boolean.opBoolean","SPLIT",FACE,{"disambiguationData":[TD([subQ7])],"derivedFrom":makeQuery(id+"F0Hq7nSFAMYVZvY_4.10.F20.boolean.opBoolean","SPLIT",FACE,{"disambiguationData":[TD([subQ7])],"derivedFrom":makeQuery(id+"F0Hq7nSFAMYVZvY_4.9.F20.boolean.opBoolean","SPLIT",FACE,{"disambiguationData":[TD([subQ7])],"derivedFrom":makeQuery(id+"F0Hq7nSFAMYVZvY_4.8.F20.boolean.opBoolean","SPLIT",FACE,{"disambiguationData":[TD([subQ7])],"derivedFrom":makeQuery(id+"F0Hq7nSFAMYVZvY_4.7.F20.boolean.opBoolean","SPLIT",FACE,{"disambiguationData":[TD([subQ7])],"derivedFrom":makeQuery(id+"F0Hq7nSFAMYVZvY_4.6.F20.boolean.opBoolean","SPLIT",FACE,{"disambiguationData":[TD([subQ7])],"derivedFrom":makeQuery(id+"F0Hq7nSFAMYVZvY_4.5.F20.boolean.opBoolean","SPLIT",FACE,{"disambiguationData":[TD([subQ7])],"derivedFrom":makeQuery(id+"F0Hq7nSFAMYVZvY_4.4.F20.boolean.opBoolean","SPLIT",FACE,{"disambiguationData":[TD([subQ7])],"derivedFrom":makeQuery(id+"F0Hq7nSFAMYVZvY_4.3.F20.boolean.opBoolean","SPLIT",FACE,{"disambiguationData":[TD([subQ7])],"derivedFrom":makeQuery(id+"F0Hq7nSFAMYVZvY_4.2.F20.boolean.opBoolean","SPLIT",FACE,{"disambiguationData":[TD([subQ7])],"derivedFrom":makeQuery(id+"F0Hq7nSFAMYVZvY_4.1.F20.boolean.opBoolean","SPLIT",FACE,{"disambiguationData":[TD([subQ7])],"derivedFrom":makeQuery(id+"F17.boolean.opBoolean","COPY",FACE,{"derivedFrom":makeQuery(id+"F17.opExtrude","CAP_FACE",FACE,{"disambiguationData":[OSD([subQ0,subQ2])],"isStart":false})})})})})})})})})})})})})})})});}
            var Q42;
            {var subQ0=sQuery(id+"F19.wireOp",EDGE,"E158.MirrorCS");var subQ1=sQuery(id+"F19.wireOp",EDGE,"E157");var subQ3=sQuery(id+"F16.wireOp",EDGE,"E151");var subQ10=makeQuery(id+"F0Hq7nSFAMYVZvY_4.16.F20.opExtrude","SWEPT_FACE",FACE,{"disambiguationData":[OSD([subQ0])]});var subQ24=makeQuery(id+"F20.opExtrude","SWEPT_FACE",FACE,{"disambiguationData":[OSD([subQ1])]});Q42=makeQuery(id+"F0Hq7nSFAMYVZvY_4.17.F20.boolean.opBoolean","SPLIT",EDGE,{"disambiguationData":[TD([subQ10])],"derivedFrom":makeQuery(id+"F0Hq7nSFAMYVZvY_4.16.F20.boolean.opBoolean","SPLIT",EDGE,{"disambiguationData":[TD([subQ24])],"derivedFrom":makeQuery(id+"F0Hq7nSFAMYVZvY_4.15.F20.boolean.opBoolean","SPLIT",EDGE,{"disambiguationData":[TD([subQ24])],"derivedFrom":makeQuery(id+"F0Hq7nSFAMYVZvY_4.14.F20.boolean.opBoolean","SPLIT",EDGE,{"disambiguationData":[TD([subQ24])],"derivedFrom":makeQuery(id+"F0Hq7nSFAMYVZvY_4.13.F20.boolean.opBoolean","SPLIT",EDGE,{"disambiguationData":[TD([subQ24])],"derivedFrom":makeQuery(id+"F0Hq7nSFAMYVZvY_4.12.F20.boolean.opBoolean","SPLIT",EDGE,{"disambiguationData":[TD([subQ24])],"derivedFrom":makeQuery(id+"F0Hq7nSFAMYVZvY_4.11.F20.boolean.opBoolean","SPLIT",EDGE,{"disambiguationData":[TD([subQ24])],"derivedFrom":makeQuery(id+"F0Hq7nSFAMYVZvY_4.10.F20.boolean.opBoolean","SPLIT",EDGE,{"disambiguationData":[TD([subQ24])],"derivedFrom":makeQuery(id+"F0Hq7nSFAMYVZvY_4.9.F20.boolean.opBoolean","SPLIT",EDGE,{"disambiguationData":[TD([subQ24])],"derivedFrom":makeQuery(id+"F0Hq7nSFAMYVZvY_4.8.F20.boolean.opBoolean","SPLIT",EDGE,{"disambiguationData":[TD([subQ24])],"derivedFrom":makeQuery(id+"F0Hq7nSFAMYVZvY_4.7.F20.boolean.opBoolean","SPLIT",EDGE,{"disambiguationData":[TD([subQ24])],"derivedFrom":makeQuery(id+"F0Hq7nSFAMYVZvY_4.6.F20.boolean.opBoolean","SPLIT",EDGE,{"disambiguationData":[TD([subQ24])],"derivedFrom":makeQuery(id+"F0Hq7nSFAMYVZvY_4.5.F20.boolean.opBoolean","SPLIT",EDGE,{"disambiguationData":[TD([subQ24])],"derivedFrom":makeQuery(id+"F0Hq7nSFAMYVZvY_4.4.F20.boolean.opBoolean","SPLIT",EDGE,{"disambiguationData":[TD([subQ24])],"derivedFrom":makeQuery(id+"F0Hq7nSFAMYVZvY_4.3.F20.boolean.opBoolean","SPLIT",EDGE,{"disambiguationData":[TD([subQ24])],"derivedFrom":makeQuery(id+"F0Hq7nSFAMYVZvY_4.2.F20.boolean.opBoolean","SPLIT",EDGE,{"disambiguationData":[TD([subQ24])],"derivedFrom":makeQuery(id+"F0Hq7nSFAMYVZvY_4.1.F20.boolean.opBoolean","SPLIT",EDGE,{"disambiguationData":[TD([subQ24])],"derivedFrom":makeQuery(id+"F18.boolean.opBoolean","COPY",EDGE,{"derivedFrom":makeQuery(id+"F18.opExtrude","CAP_EDGE",EDGE,{"disambiguationData":[OSD([subQ3])],"isStart":false})})})})})})})})})})})})})})})})})})});}
            var Q43;
            Q43=makeQuery(id+"F0Hq7nSFAMYVZvY_4.17.F20.opExtrude","CAP_EDGE",EDGE,{"disambiguationData":[OSD([sQuery(id+"F19.wireOp",EDGE,"E158.MirrorCS")])],"isStart":false});
            var Q44;
            Q44=makeQuery(id+"F0Hq7nSFAMYVZvY_4.17.F20.opExtrude","SWEPT_FACE",FACE,{"disambiguationData":[OSD([sQuery(id+"F19.wireOp",EDGE,"E157")])]});
            var Q45;
            {var subQ0=sQuery(id+"F19.wireOp",EDGE,"E158.MirrorCS");var subQ1=sQuery(id+"F19.wireOp",EDGE,"E157");var subQ3=sQuery(id+"F16.wireOp",EDGE,"E151");var subQ13=makeQuery(id+"F0Hq7nSFAMYVZvY_4.14.F20.opExtrude","SWEPT_FACE",FACE,{"disambiguationData":[OSD([subQ0])]});var subQ22=makeQuery(id+"F20.opExtrude","SWEPT_FACE",FACE,{"disambiguationData":[OSD([subQ1])]});Q45=makeQuery(id+"F0Hq7nSFAMYVZvY_4.15.F20.boolean.opBoolean","SPLIT",EDGE,{"disambiguationData":[TD([subQ13])],"derivedFrom":makeQuery(id+"F0Hq7nSFAMYVZvY_4.14.F20.boolean.opBoolean","SPLIT",EDGE,{"disambiguationData":[TD([subQ22])],"derivedFrom":makeQuery(id+"F0Hq7nSFAMYVZvY_4.13.F20.boolean.opBoolean","SPLIT",EDGE,{"disambiguationData":[TD([subQ22])],"derivedFrom":makeQuery(id+"F0Hq7nSFAMYVZvY_4.12.F20.boolean.opBoolean","SPLIT",EDGE,{"disambiguationData":[TD([subQ22])],"derivedFrom":makeQuery(id+"F0Hq7nSFAMYVZvY_4.11.F20.boolean.opBoolean","SPLIT",EDGE,{"disambiguationData":[TD([subQ22])],"derivedFrom":makeQuery(id+"F0Hq7nSFAMYVZvY_4.10.F20.boolean.opBoolean","SPLIT",EDGE,{"disambiguationData":[TD([subQ22])],"derivedFrom":makeQuery(id+"F0Hq7nSFAMYVZvY_4.9.F20.boolean.opBoolean","SPLIT",EDGE,{"disambiguationData":[TD([subQ22])],"derivedFrom":makeQuery(id+"F0Hq7nSFAMYVZvY_4.8.F20.boolean.opBoolean","SPLIT",EDGE,{"disambiguationData":[TD([subQ22])],"derivedFrom":makeQuery(id+"F0Hq7nSFAMYVZvY_4.7.F20.boolean.opBoolean","SPLIT",EDGE,{"disambiguationData":[TD([subQ22])],"derivedFrom":makeQuery(id+"F0Hq7nSFAMYVZvY_4.6.F20.boolean.opBoolean","SPLIT",EDGE,{"disambiguationData":[TD([subQ22])],"derivedFrom":makeQuery(id+"F0Hq7nSFAMYVZvY_4.5.F20.boolean.opBoolean","SPLIT",EDGE,{"disambiguationData":[TD([subQ22])],"derivedFrom":makeQuery(id+"F0Hq7nSFAMYVZvY_4.4.F20.boolean.opBoolean","SPLIT",EDGE,{"disambiguationData":[TD([subQ22])],"derivedFrom":makeQuery(id+"F0Hq7nSFAMYVZvY_4.3.F20.boolean.opBoolean","SPLIT",EDGE,{"disambiguationData":[TD([subQ22])],"derivedFrom":makeQuery(id+"F0Hq7nSFAMYVZvY_4.2.F20.boolean.opBoolean","SPLIT",EDGE,{"disambiguationData":[TD([subQ22])],"derivedFrom":makeQuery(id+"F0Hq7nSFAMYVZvY_4.1.F20.boolean.opBoolean","SPLIT",EDGE,{"disambiguationData":[TD([subQ22])],"derivedFrom":makeQuery(id+"F18.boolean.opBoolean","COPY",EDGE,{"derivedFrom":makeQuery(id+"F18.opExtrude","CAP_EDGE",EDGE,{"disambiguationData":[OSD([subQ3])],"isStart":false})})})})})})})})})})})})})})})})});}
            var Q46;
            Q46=makeQuery(id+"F0Hq7nSFAMYVZvY_4.16.F20.opExtrude","SWEPT_FACE",FACE,{"disambiguationData":[OSD([sQuery(id+"F19.wireOp",EDGE,"E158.MirrorCS")])]});
            var Q47;
            Q47=makeQuery(id+"F0Hq7nSFAMYVZvY_4.16.F20.opExtrude","CAP_EDGE",EDGE,{"disambiguationData":[OSD([sQuery(id+"F19.wireOp",EDGE,"E157")])],"isStart":false});
            var Q48;
            Q48=makeQuery(id+"F0Hq7nSFAMYVZvY_4.15.F20.opExtrude","CAP_EDGE",EDGE,{"disambiguationData":[OSD([sQuery(id+"F19.wireOp",EDGE,"E158.MirrorCS")])],"isStart":true});
            var Q49;
            {var subQ0=sQuery(id+"F19.wireOp",EDGE,"E158.MirrorCS");var subQ1=sQuery(id+"F19.wireOp",EDGE,"E157");var subQ3=sQuery(id+"F16.wireOp",EDGE,"E151");var subQ15=makeQuery(id+"F0Hq7nSFAMYVZvY_4.15.F20.opExtrude","SWEPT_FACE",FACE,{"disambiguationData":[OSD([subQ0])]});var subQ23=makeQuery(id+"F20.opExtrude","SWEPT_FACE",FACE,{"disambiguationData":[OSD([subQ1])]});Q49=makeQuery(id+"F0Hq7nSFAMYVZvY_4.16.F20.boolean.opBoolean","SPLIT",FACE,{"disambiguationData":[TD([subQ15])],"derivedFrom":makeQuery(id+"F0Hq7nSFAMYVZvY_4.15.F20.boolean.opBoolean","SPLIT",FACE,{"disambiguationData":[TD([subQ23])],"derivedFrom":makeQuery(id+"F0Hq7nSFAMYVZvY_4.14.F20.boolean.opBoolean","SPLIT",FACE,{"disambiguationData":[TD([subQ23])],"derivedFrom":makeQuery(id+"F0Hq7nSFAMYVZvY_4.13.F20.boolean.opBoolean","SPLIT",FACE,{"disambiguationData":[TD([subQ23])],"derivedFrom":makeQuery(id+"F0Hq7nSFAMYVZvY_4.12.F20.boolean.opBoolean","SPLIT",FACE,{"disambiguationData":[TD([subQ23])],"derivedFrom":makeQuery(id+"F0Hq7nSFAMYVZvY_4.11.F20.boolean.opBoolean","SPLIT",FACE,{"disambiguationData":[TD([subQ23])],"derivedFrom":makeQuery(id+"F0Hq7nSFAMYVZvY_4.10.F20.boolean.opBoolean","SPLIT",FACE,{"disambiguationData":[TD([subQ23])],"derivedFrom":makeQuery(id+"F0Hq7nSFAMYVZvY_4.9.F20.boolean.opBoolean","SPLIT",FACE,{"disambiguationData":[TD([subQ23])],"derivedFrom":makeQuery(id+"F0Hq7nSFAMYVZvY_4.8.F20.boolean.opBoolean","SPLIT",FACE,{"disambiguationData":[TD([subQ23])],"derivedFrom":makeQuery(id+"F0Hq7nSFAMYVZvY_4.7.F20.boolean.opBoolean","SPLIT",FACE,{"disambiguationData":[TD([subQ23])],"derivedFrom":makeQuery(id+"F0Hq7nSFAMYVZvY_4.6.F20.boolean.opBoolean","SPLIT",FACE,{"disambiguationData":[TD([subQ23])],"derivedFrom":makeQuery(id+"F0Hq7nSFAMYVZvY_4.5.F20.boolean.opBoolean","SPLIT",FACE,{"disambiguationData":[TD([subQ23])],"derivedFrom":makeQuery(id+"F0Hq7nSFAMYVZvY_4.4.F20.boolean.opBoolean","SPLIT",FACE,{"disambiguationData":[TD([subQ23])],"derivedFrom":makeQuery(id+"F0Hq7nSFAMYVZvY_4.3.F20.boolean.opBoolean","SPLIT",FACE,{"disambiguationData":[TD([subQ23])],"derivedFrom":makeQuery(id+"F0Hq7nSFAMYVZvY_4.2.F20.boolean.opBoolean","SPLIT",FACE,{"disambiguationData":[TD([subQ23])],"derivedFrom":makeQuery(id+"F0Hq7nSFAMYVZvY_4.1.F20.boolean.opBoolean","SPLIT",FACE,{"disambiguationData":[TD([subQ23])],"derivedFrom":makeQuery(id+"F17.boolean.opBoolean","COPY",FACE,{"derivedFrom":makeQuery(id+"F17.opExtrude","SWEPT_FACE",FACE,{"disambiguationData":[OSD([subQ3])]})})})})})})})})})})})})})})})})})});}
            var Q50;
            Q50=makeQuery(id+"F0Hq7nSFAMYVZvY_4.18.F20.opExtrude","SWEPT_FACE",FACE,{"disambiguationData":[OSD([sQuery(id+"F19.wireOp",EDGE,"E157")])]});
            var Q51;
            Q51=makeQuery(id+"F0Hq7nSFAMYVZvY_4.18.F20.opExtrude","SWEPT_FACE",FACE,{"disambiguationData":[OSD([sQuery(id+"F19.wireOp",EDGE,"E158.MirrorCS")])]});
            var Q52;
            Q52=makeQuery(id+"F0Hq7nSFAMYVZvY_4.18.F20.opExtrude","CAP_EDGE",EDGE,{"disambiguationData":[OSD([sQuery(id+"F19.wireOp",EDGE,"E157")])],"isStart":false});
            var Q53;
            Q53=makeQuery(id+"F0Hq7nSFAMYVZvY_4.18.F20.opExtrude","CAP_EDGE",EDGE,{"disambiguationData":[OSD([sQuery(id+"F19.wireOp",EDGE,"E158.MirrorCS")])],"isStart":false});
            var Q54;
            {var subQ0=sQuery(id+"F16.wireOp",EDGE,"E151");var subQ2=sQuery(id+"F16.wireOp",EDGE,"E152");var subQ4=sQuery(id+"F19.wireOp",EDGE,"E158.MirrorCS");var subQ5=makeQuery(id+"F0Hq7nSFAMYVZvY_4.18.F20.opExtrude","SWEPT_FACE",FACE,{"disambiguationData":[OSD([subQ4])]});var subQ6=sQuery(id+"F19.wireOp",EDGE,"E157");var subQ7=makeQuery(id+"F20.opExtrude","SWEPT_FACE",FACE,{"disambiguationData":[OSD([subQ6])]});Q54=makeQuery(id+"F0Hq7nSFAMYVZvY_4.19.F20.boolean.opBoolean","SPLIT",FACE,{"disambiguationData":[TD([subQ5])],"derivedFrom":makeQuery(id+"F0Hq7nSFAMYVZvY_4.18.F20.boolean.opBoolean","SPLIT",FACE,{"disambiguationData":[TD([subQ7])],"derivedFrom":makeQuery(id+"F0Hq7nSFAMYVZvY_4.17.F20.boolean.opBoolean","SPLIT",FACE,{"disambiguationData":[TD([subQ7])],"derivedFrom":makeQuery(id+"F0Hq7nSFAMYVZvY_4.16.F20.boolean.opBoolean","SPLIT",FACE,{"disambiguationData":[TD([subQ7])],"derivedFrom":makeQuery(id+"F0Hq7nSFAMYVZvY_4.15.F20.boolean.opBoolean","SPLIT",FACE,{"disambiguationData":[TD([subQ7])],"derivedFrom":makeQuery(id+"F0Hq7nSFAMYVZvY_4.14.F20.boolean.opBoolean","SPLIT",FACE,{"disambiguationData":[TD([subQ7])],"derivedFrom":makeQuery(id+"F0Hq7nSFAMYVZvY_4.13.F20.boolean.opBoolean","SPLIT",FACE,{"disambiguationData":[TD([subQ7])],"derivedFrom":makeQuery(id+"F0Hq7nSFAMYVZvY_4.12.F20.boolean.opBoolean","SPLIT",FACE,{"disambiguationData":[TD([subQ7])],"derivedFrom":makeQuery(id+"F0Hq7nSFAMYVZvY_4.11.F20.boolean.opBoolean","SPLIT",FACE,{"disambiguationData":[TD([subQ7])],"derivedFrom":makeQuery(id+"F0Hq7nSFAMYVZvY_4.10.F20.boolean.opBoolean","SPLIT",FACE,{"disambiguationData":[TD([subQ7])],"derivedFrom":makeQuery(id+"F0Hq7nSFAMYVZvY_4.9.F20.boolean.opBoolean","SPLIT",FACE,{"disambiguationData":[TD([subQ7])],"derivedFrom":makeQuery(id+"F0Hq7nSFAMYVZvY_4.8.F20.boolean.opBoolean","SPLIT",FACE,{"disambiguationData":[TD([subQ7])],"derivedFrom":makeQuery(id+"F0Hq7nSFAMYVZvY_4.7.F20.boolean.opBoolean","SPLIT",FACE,{"disambiguationData":[TD([subQ7])],"derivedFrom":makeQuery(id+"F0Hq7nSFAMYVZvY_4.6.F20.boolean.opBoolean","SPLIT",FACE,{"disambiguationData":[TD([subQ7])],"derivedFrom":makeQuery(id+"F0Hq7nSFAMYVZvY_4.5.F20.boolean.opBoolean","SPLIT",FACE,{"disambiguationData":[TD([subQ7])],"derivedFrom":makeQuery(id+"F0Hq7nSFAMYVZvY_4.4.F20.boolean.opBoolean","SPLIT",FACE,{"disambiguationData":[TD([subQ7])],"derivedFrom":makeQuery(id+"F0Hq7nSFAMYVZvY_4.3.F20.boolean.opBoolean","SPLIT",FACE,{"disambiguationData":[TD([subQ7])],"derivedFrom":makeQuery(id+"F0Hq7nSFAMYVZvY_4.2.F20.boolean.opBoolean","SPLIT",FACE,{"disambiguationData":[TD([subQ7])],"derivedFrom":makeQuery(id+"F0Hq7nSFAMYVZvY_4.1.F20.boolean.opBoolean","SPLIT",FACE,{"disambiguationData":[TD([subQ7])],"derivedFrom":makeQuery(id+"F17.boolean.opBoolean","COPY",FACE,{"derivedFrom":makeQuery(id+"F17.opExtrude","CAP_FACE",FACE,{"disambiguationData":[OSD([subQ0,subQ2])],"isStart":false})})})})})})})})})})})})})})})})})})})})});}
            var Q55;
            {var subQ0=sQuery(id+"F19.wireOp",EDGE,"E158.MirrorCS");var subQ1=sQuery(id+"F19.wireOp",EDGE,"E157");var subQ3=sQuery(id+"F16.wireOp",EDGE,"E151");var subQ23=makeQuery(id+"F0Hq7nSFAMYVZvY_4.18.F20.opExtrude","SWEPT_FACE",FACE,{"disambiguationData":[OSD([subQ0])]});var subQ26=makeQuery(id+"F20.opExtrude","SWEPT_FACE",FACE,{"disambiguationData":[OSD([subQ1])]});Q55=makeQuery(id+"F0Hq7nSFAMYVZvY_4.19.F20.boolean.opBoolean","SPLIT",FACE,{"disambiguationData":[TD([subQ23])],"derivedFrom":makeQuery(id+"F0Hq7nSFAMYVZvY_4.18.F20.boolean.opBoolean","SPLIT",FACE,{"disambiguationData":[TD([subQ26])],"derivedFrom":makeQuery(id+"F0Hq7nSFAMYVZvY_4.17.F20.boolean.opBoolean","SPLIT",FACE,{"disambiguationData":[TD([subQ26])],"derivedFrom":makeQuery(id+"F0Hq7nSFAMYVZvY_4.16.F20.boolean.opBoolean","SPLIT",FACE,{"disambiguationData":[TD([subQ26])],"derivedFrom":makeQuery(id+"F0Hq7nSFAMYVZvY_4.15.F20.boolean.opBoolean","SPLIT",FACE,{"disambiguationData":[TD([subQ26])],"derivedFrom":makeQuery(id+"F0Hq7nSFAMYVZvY_4.14.F20.boolean.opBoolean","SPLIT",FACE,{"disambiguationData":[TD([subQ26])],"derivedFrom":makeQuery(id+"F0Hq7nSFAMYVZvY_4.13.F20.boolean.opBoolean","SPLIT",FACE,{"disambiguationData":[TD([subQ26])],"derivedFrom":makeQuery(id+"F0Hq7nSFAMYVZvY_4.12.F20.boolean.opBoolean","SPLIT",FACE,{"disambiguationData":[TD([subQ26])],"derivedFrom":makeQuery(id+"F0Hq7nSFAMYVZvY_4.11.F20.boolean.opBoolean","SPLIT",FACE,{"disambiguationData":[TD([subQ26])],"derivedFrom":makeQuery(id+"F0Hq7nSFAMYVZvY_4.10.F20.boolean.opBoolean","SPLIT",FACE,{"disambiguationData":[TD([subQ26])],"derivedFrom":makeQuery(id+"F0Hq7nSFAMYVZvY_4.9.F20.boolean.opBoolean","SPLIT",FACE,{"disambiguationData":[TD([subQ26])],"derivedFrom":makeQuery(id+"F0Hq7nSFAMYVZvY_4.8.F20.boolean.opBoolean","SPLIT",FACE,{"disambiguationData":[TD([subQ26])],"derivedFrom":makeQuery(id+"F0Hq7nSFAMYVZvY_4.7.F20.boolean.opBoolean","SPLIT",FACE,{"disambiguationData":[TD([subQ26])],"derivedFrom":makeQuery(id+"F0Hq7nSFAMYVZvY_4.6.F20.boolean.opBoolean","SPLIT",FACE,{"disambiguationData":[TD([subQ26])],"derivedFrom":makeQuery(id+"F0Hq7nSFAMYVZvY_4.5.F20.boolean.opBoolean","SPLIT",FACE,{"disambiguationData":[TD([subQ26])],"derivedFrom":makeQuery(id+"F0Hq7nSFAMYVZvY_4.4.F20.boolean.opBoolean","SPLIT",FACE,{"disambiguationData":[TD([subQ26])],"derivedFrom":makeQuery(id+"F0Hq7nSFAMYVZvY_4.3.F20.boolean.opBoolean","SPLIT",FACE,{"disambiguationData":[TD([subQ26])],"derivedFrom":makeQuery(id+"F0Hq7nSFAMYVZvY_4.2.F20.boolean.opBoolean","SPLIT",FACE,{"disambiguationData":[TD([subQ26])],"derivedFrom":makeQuery(id+"F0Hq7nSFAMYVZvY_4.1.F20.boolean.opBoolean","SPLIT",FACE,{"disambiguationData":[TD([subQ26])],"derivedFrom":makeQuery(id+"F17.boolean.opBoolean","COPY",FACE,{"derivedFrom":makeQuery(id+"F17.opExtrude","SWEPT_FACE",FACE,{"disambiguationData":[OSD([subQ3])]})})})})})})})})})})})})})})})})})})})})});}
            var Q56;
            {var subQ0=sQuery(id+"F16.wireOp",EDGE,"E151");var subQ3=sQuery(id+"F19.wireOp",EDGE,"E158.MirrorCS");var subQ4=makeQuery(id+"F0Hq7nSFAMYVZvY_4.18.F20.opExtrude","SWEPT_FACE",FACE,{"disambiguationData":[OSD([subQ3])]});var subQ5=sQuery(id+"F19.wireOp",EDGE,"E157");var subQ6=makeQuery(id+"F20.opExtrude","SWEPT_FACE",FACE,{"disambiguationData":[OSD([subQ5])]});Q56=makeQuery(id+"F0Hq7nSFAMYVZvY_4.19.F20.boolean.opBoolean","SPLIT",EDGE,{"disambiguationData":[TD([subQ4])],"derivedFrom":makeQuery(id+"F0Hq7nSFAMYVZvY_4.18.F20.boolean.opBoolean","SPLIT",EDGE,{"disambiguationData":[TD([subQ6])],"derivedFrom":makeQuery(id+"F0Hq7nSFAMYVZvY_4.17.F20.boolean.opBoolean","SPLIT",EDGE,{"disambiguationData":[TD([subQ6])],"derivedFrom":makeQuery(id+"F0Hq7nSFAMYVZvY_4.16.F20.boolean.opBoolean","SPLIT",EDGE,{"disambiguationData":[TD([subQ6])],"derivedFrom":makeQuery(id+"F0Hq7nSFAMYVZvY_4.15.F20.boolean.opBoolean","SPLIT",EDGE,{"disambiguationData":[TD([subQ6])],"derivedFrom":makeQuery(id+"F0Hq7nSFAMYVZvY_4.14.F20.boolean.opBoolean","SPLIT",EDGE,{"disambiguationData":[TD([subQ6])],"derivedFrom":makeQuery(id+"F0Hq7nSFAMYVZvY_4.13.F20.boolean.opBoolean","SPLIT",EDGE,{"disambiguationData":[TD([subQ6])],"derivedFrom":makeQuery(id+"F0Hq7nSFAMYVZvY_4.12.F20.boolean.opBoolean","SPLIT",EDGE,{"disambiguationData":[TD([subQ6])],"derivedFrom":makeQuery(id+"F0Hq7nSFAMYVZvY_4.11.F20.boolean.opBoolean","SPLIT",EDGE,{"disambiguationData":[TD([subQ6])],"derivedFrom":makeQuery(id+"F0Hq7nSFAMYVZvY_4.10.F20.boolean.opBoolean","SPLIT",EDGE,{"disambiguationData":[TD([subQ6])],"derivedFrom":makeQuery(id+"F0Hq7nSFAMYVZvY_4.9.F20.boolean.opBoolean","SPLIT",EDGE,{"disambiguationData":[TD([subQ6])],"derivedFrom":makeQuery(id+"F0Hq7nSFAMYVZvY_4.8.F20.boolean.opBoolean","SPLIT",EDGE,{"disambiguationData":[TD([subQ6])],"derivedFrom":makeQuery(id+"F0Hq7nSFAMYVZvY_4.7.F20.boolean.opBoolean","SPLIT",EDGE,{"disambiguationData":[TD([subQ6])],"derivedFrom":makeQuery(id+"F0Hq7nSFAMYVZvY_4.6.F20.boolean.opBoolean","SPLIT",EDGE,{"disambiguationData":[TD([subQ6])],"derivedFrom":makeQuery(id+"F0Hq7nSFAMYVZvY_4.5.F20.boolean.opBoolean","SPLIT",EDGE,{"disambiguationData":[TD([subQ6])],"derivedFrom":makeQuery(id+"F0Hq7nSFAMYVZvY_4.4.F20.boolean.opBoolean","SPLIT",EDGE,{"disambiguationData":[TD([subQ6])],"derivedFrom":makeQuery(id+"F0Hq7nSFAMYVZvY_4.3.F20.boolean.opBoolean","SPLIT",EDGE,{"disambiguationData":[TD([subQ6])],"derivedFrom":makeQuery(id+"F0Hq7nSFAMYVZvY_4.2.F20.boolean.opBoolean","SPLIT",EDGE,{"disambiguationData":[TD([subQ6])],"derivedFrom":makeQuery(id+"F0Hq7nSFAMYVZvY_4.1.F20.boolean.opBoolean","SPLIT",EDGE,{"disambiguationData":[TD([subQ6])],"derivedFrom":makeQuery(id+"F17.boolean.opBoolean","COPY",EDGE,{"derivedFrom":makeQuery(id+"F17.opExtrude","CAP_EDGE",EDGE,{"disambiguationData":[OSD([subQ0])],"isStart":false})})})})})})})})})})})})})})})})})})})})});}
            var Q57;
            {var subQ0=sQuery(id+"F19.wireOp",EDGE,"E158.MirrorCS");var subQ1=sQuery(id+"F19.wireOp",EDGE,"E157");var subQ3=sQuery(id+"F16.wireOp",EDGE,"E151");var subQ21=makeQuery(id+"F0Hq7nSFAMYVZvY_4.18.F20.opExtrude","SWEPT_FACE",FACE,{"disambiguationData":[OSD([subQ0])]});var subQ26=makeQuery(id+"F20.opExtrude","SWEPT_FACE",FACE,{"disambiguationData":[OSD([subQ1])]});Q57=makeQuery(id+"F0Hq7nSFAMYVZvY_4.19.F20.boolean.opBoolean","SPLIT",EDGE,{"disambiguationData":[TD([subQ21])],"derivedFrom":makeQuery(id+"F0Hq7nSFAMYVZvY_4.18.F20.boolean.opBoolean","SPLIT",EDGE,{"disambiguationData":[TD([subQ26])],"derivedFrom":makeQuery(id+"F0Hq7nSFAMYVZvY_4.17.F20.boolean.opBoolean","SPLIT",EDGE,{"disambiguationData":[TD([subQ26])],"derivedFrom":makeQuery(id+"F0Hq7nSFAMYVZvY_4.16.F20.boolean.opBoolean","SPLIT",EDGE,{"disambiguationData":[TD([subQ26])],"derivedFrom":makeQuery(id+"F0Hq7nSFAMYVZvY_4.15.F20.boolean.opBoolean","SPLIT",EDGE,{"disambiguationData":[TD([subQ26])],"derivedFrom":makeQuery(id+"F0Hq7nSFAMYVZvY_4.14.F20.boolean.opBoolean","SPLIT",EDGE,{"disambiguationData":[TD([subQ26])],"derivedFrom":makeQuery(id+"F0Hq7nSFAMYVZvY_4.13.F20.boolean.opBoolean","SPLIT",EDGE,{"disambiguationData":[TD([subQ26])],"derivedFrom":makeQuery(id+"F0Hq7nSFAMYVZvY_4.12.F20.boolean.opBoolean","SPLIT",EDGE,{"disambiguationData":[TD([subQ26])],"derivedFrom":makeQuery(id+"F0Hq7nSFAMYVZvY_4.11.F20.boolean.opBoolean","SPLIT",EDGE,{"disambiguationData":[TD([subQ26])],"derivedFrom":makeQuery(id+"F0Hq7nSFAMYVZvY_4.10.F20.boolean.opBoolean","SPLIT",EDGE,{"disambiguationData":[TD([subQ26])],"derivedFrom":makeQuery(id+"F0Hq7nSFAMYVZvY_4.9.F20.boolean.opBoolean","SPLIT",EDGE,{"disambiguationData":[TD([subQ26])],"derivedFrom":makeQuery(id+"F0Hq7nSFAMYVZvY_4.8.F20.boolean.opBoolean","SPLIT",EDGE,{"disambiguationData":[TD([subQ26])],"derivedFrom":makeQuery(id+"F0Hq7nSFAMYVZvY_4.7.F20.boolean.opBoolean","SPLIT",EDGE,{"disambiguationData":[TD([subQ26])],"derivedFrom":makeQuery(id+"F0Hq7nSFAMYVZvY_4.6.F20.boolean.opBoolean","SPLIT",EDGE,{"disambiguationData":[TD([subQ26])],"derivedFrom":makeQuery(id+"F0Hq7nSFAMYVZvY_4.5.F20.boolean.opBoolean","SPLIT",EDGE,{"disambiguationData":[TD([subQ26])],"derivedFrom":makeQuery(id+"F0Hq7nSFAMYVZvY_4.4.F20.boolean.opBoolean","SPLIT",EDGE,{"disambiguationData":[TD([subQ26])],"derivedFrom":makeQuery(id+"F0Hq7nSFAMYVZvY_4.3.F20.boolean.opBoolean","SPLIT",EDGE,{"disambiguationData":[TD([subQ26])],"derivedFrom":makeQuery(id+"F0Hq7nSFAMYVZvY_4.2.F20.boolean.opBoolean","SPLIT",EDGE,{"disambiguationData":[TD([subQ26])],"derivedFrom":makeQuery(id+"F0Hq7nSFAMYVZvY_4.1.F20.boolean.opBoolean","SPLIT",EDGE,{"disambiguationData":[TD([subQ26])],"derivedFrom":makeQuery(id+"F18.boolean.opBoolean","COPY",EDGE,{"derivedFrom":makeQuery(id+"F18.opExtrude","CAP_EDGE",EDGE,{"disambiguationData":[OSD([subQ3])],"isStart":false})})})})})})})})})})})})})})})})})})})})});}
            var Q58;
            Q58=makeQuery(id+"F0Hq7nSFAMYVZvY_4.20.F20.opExtrude","SWEPT_FACE",FACE,{"disambiguationData":[OSD([sQuery(id+"F19.wireOp",EDGE,"E157")])]});
            var Q59;
            Q59=makeQuery(id+"F0Hq7nSFAMYVZvY_4.20.F20.opExtrude","SWEPT_FACE",FACE,{"disambiguationData":[OSD([sQuery(id+"F19.wireOp",EDGE,"E158.MirrorCS")])]});
            var Q60;
            {var subQ0=sQuery(id+"F16.wireOp",EDGE,"E151");var subQ2=sQuery(id+"F19.wireOp",EDGE,"E157");var subQ3=sQuery(id+"F16.wireOp",EDGE,"E152");var subQ5=sQuery(id+"F19.wireOp",EDGE,"E158.MirrorCS");var subQ6=makeQuery(id+"F0Hq7nSFAMYVZvY_4.19.F20.opExtrude","SWEPT_FACE",FACE,{"disambiguationData":[OSD([subQ5])]});var subQ7=makeQuery(id+"F20.opExtrude","SWEPT_FACE",FACE,{"disambiguationData":[OSD([subQ2])]});Q60=makeQuery(id+"F0Hq7nSFAMYVZvY_4.20.F20.boolean.opBoolean","SPLIT",FACE,{"disambiguationData":[TD([subQ6])],"derivedFrom":makeQuery(id+"F0Hq7nSFAMYVZvY_4.19.F20.boolean.opBoolean","SPLIT",FACE,{"disambiguationData":[TD([subQ7])],"derivedFrom":makeQuery(id+"F0Hq7nSFAMYVZvY_4.18.F20.boolean.opBoolean","SPLIT",FACE,{"disambiguationData":[TD([subQ7])],"derivedFrom":makeQuery(id+"F0Hq7nSFAMYVZvY_4.17.F20.boolean.opBoolean","SPLIT",FACE,{"disambiguationData":[TD([subQ7])],"derivedFrom":makeQuery(id+"F0Hq7nSFAMYVZvY_4.16.F20.boolean.opBoolean","SPLIT",FACE,{"disambiguationData":[TD([subQ7])],"derivedFrom":makeQuery(id+"F0Hq7nSFAMYVZvY_4.15.F20.boolean.opBoolean","SPLIT",FACE,{"disambiguationData":[TD([subQ7])],"derivedFrom":makeQuery(id+"F0Hq7nSFAMYVZvY_4.14.F20.boolean.opBoolean","SPLIT",FACE,{"disambiguationData":[TD([subQ7])],"derivedFrom":makeQuery(id+"F0Hq7nSFAMYVZvY_4.13.F20.boolean.opBoolean","SPLIT",FACE,{"disambiguationData":[TD([subQ7])],"derivedFrom":makeQuery(id+"F0Hq7nSFAMYVZvY_4.12.F20.boolean.opBoolean","SPLIT",FACE,{"disambiguationData":[TD([subQ7])],"derivedFrom":makeQuery(id+"F0Hq7nSFAMYVZvY_4.11.F20.boolean.opBoolean","SPLIT",FACE,{"disambiguationData":[TD([subQ7])],"derivedFrom":makeQuery(id+"F0Hq7nSFAMYVZvY_4.10.F20.boolean.opBoolean","SPLIT",FACE,{"disambiguationData":[TD([subQ7])],"derivedFrom":makeQuery(id+"F0Hq7nSFAMYVZvY_4.9.F20.boolean.opBoolean","SPLIT",FACE,{"disambiguationData":[TD([subQ7])],"derivedFrom":makeQuery(id+"F0Hq7nSFAMYVZvY_4.8.F20.boolean.opBoolean","SPLIT",FACE,{"disambiguationData":[TD([subQ7])],"derivedFrom":makeQuery(id+"F0Hq7nSFAMYVZvY_4.7.F20.boolean.opBoolean","SPLIT",FACE,{"disambiguationData":[TD([subQ7])],"derivedFrom":makeQuery(id+"F0Hq7nSFAMYVZvY_4.6.F20.boolean.opBoolean","SPLIT",FACE,{"disambiguationData":[TD([subQ7])],"derivedFrom":makeQuery(id+"F0Hq7nSFAMYVZvY_4.5.F20.boolean.opBoolean","SPLIT",FACE,{"disambiguationData":[TD([subQ7])],"derivedFrom":makeQuery(id+"F0Hq7nSFAMYVZvY_4.4.F20.boolean.opBoolean","SPLIT",FACE,{"disambiguationData":[TD([subQ7])],"derivedFrom":makeQuery(id+"F0Hq7nSFAMYVZvY_4.3.F20.boolean.opBoolean","SPLIT",FACE,{"disambiguationData":[TD([subQ7])],"derivedFrom":makeQuery(id+"F0Hq7nSFAMYVZvY_4.2.F20.boolean.opBoolean","SPLIT",FACE,{"disambiguationData":[TD([subQ7])],"derivedFrom":makeQuery(id+"F0Hq7nSFAMYVZvY_4.1.F20.boolean.opBoolean","SPLIT",FACE,{"disambiguationData":[TD([subQ7])],"derivedFrom":makeQuery(id+"F17.boolean.opBoolean","COPY",FACE,{"derivedFrom":makeQuery(id+"F17.opExtrude","CAP_FACE",FACE,{"disambiguationData":[OSD([subQ0,subQ3])],"isStart":false})})})})})})})})})})})})})})})})})})})})})});}
            var Q61;
            {var subQ0=sQuery(id+"F19.wireOp",EDGE,"E158.MirrorCS");var subQ1=sQuery(id+"F19.wireOp",EDGE,"E157");var subQ3=sQuery(id+"F16.wireOp",EDGE,"E151");var subQ26=makeQuery(id+"F0Hq7nSFAMYVZvY_4.19.F20.opExtrude","SWEPT_FACE",FACE,{"disambiguationData":[OSD([subQ0])]});var subQ27=makeQuery(id+"F20.opExtrude","SWEPT_FACE",FACE,{"disambiguationData":[OSD([subQ1])]});Q61=makeQuery(id+"F0Hq7nSFAMYVZvY_4.20.F20.boolean.opBoolean","SPLIT",FACE,{"disambiguationData":[TD([subQ26])],"derivedFrom":makeQuery(id+"F0Hq7nSFAMYVZvY_4.19.F20.boolean.opBoolean","SPLIT",FACE,{"disambiguationData":[TD([subQ27])],"derivedFrom":makeQuery(id+"F0Hq7nSFAMYVZvY_4.18.F20.boolean.opBoolean","SPLIT",FACE,{"disambiguationData":[TD([subQ27])],"derivedFrom":makeQuery(id+"F0Hq7nSFAMYVZvY_4.17.F20.boolean.opBoolean","SPLIT",FACE,{"disambiguationData":[TD([subQ27])],"derivedFrom":makeQuery(id+"F0Hq7nSFAMYVZvY_4.16.F20.boolean.opBoolean","SPLIT",FACE,{"disambiguationData":[TD([subQ27])],"derivedFrom":makeQuery(id+"F0Hq7nSFAMYVZvY_4.15.F20.boolean.opBoolean","SPLIT",FACE,{"disambiguationData":[TD([subQ27])],"derivedFrom":makeQuery(id+"F0Hq7nSFAMYVZvY_4.14.F20.boolean.opBoolean","SPLIT",FACE,{"disambiguationData":[TD([subQ27])],"derivedFrom":makeQuery(id+"F0Hq7nSFAMYVZvY_4.13.F20.boolean.opBoolean","SPLIT",FACE,{"disambiguationData":[TD([subQ27])],"derivedFrom":makeQuery(id+"F0Hq7nSFAMYVZvY_4.12.F20.boolean.opBoolean","SPLIT",FACE,{"disambiguationData":[TD([subQ27])],"derivedFrom":makeQuery(id+"F0Hq7nSFAMYVZvY_4.11.F20.boolean.opBoolean","SPLIT",FACE,{"disambiguationData":[TD([subQ27])],"derivedFrom":makeQuery(id+"F0Hq7nSFAMYVZvY_4.10.F20.boolean.opBoolean","SPLIT",FACE,{"disambiguationData":[TD([subQ27])],"derivedFrom":makeQuery(id+"F0Hq7nSFAMYVZvY_4.9.F20.boolean.opBoolean","SPLIT",FACE,{"disambiguationData":[TD([subQ27])],"derivedFrom":makeQuery(id+"F0Hq7nSFAMYVZvY_4.8.F20.boolean.opBoolean","SPLIT",FACE,{"disambiguationData":[TD([subQ27])],"derivedFrom":makeQuery(id+"F0Hq7nSFAMYVZvY_4.7.F20.boolean.opBoolean","SPLIT",FACE,{"disambiguationData":[TD([subQ27])],"derivedFrom":makeQuery(id+"F0Hq7nSFAMYVZvY_4.6.F20.boolean.opBoolean","SPLIT",FACE,{"disambiguationData":[TD([subQ27])],"derivedFrom":makeQuery(id+"F0Hq7nSFAMYVZvY_4.5.F20.boolean.opBoolean","SPLIT",FACE,{"disambiguationData":[TD([subQ27])],"derivedFrom":makeQuery(id+"F0Hq7nSFAMYVZvY_4.4.F20.boolean.opBoolean","SPLIT",FACE,{"disambiguationData":[TD([subQ27])],"derivedFrom":makeQuery(id+"F0Hq7nSFAMYVZvY_4.3.F20.boolean.opBoolean","SPLIT",FACE,{"disambiguationData":[TD([subQ27])],"derivedFrom":makeQuery(id+"F0Hq7nSFAMYVZvY_4.2.F20.boolean.opBoolean","SPLIT",FACE,{"disambiguationData":[TD([subQ27])],"derivedFrom":makeQuery(id+"F0Hq7nSFAMYVZvY_4.1.F20.boolean.opBoolean","SPLIT",FACE,{"disambiguationData":[TD([subQ27])],"derivedFrom":makeQuery(id+"F17.boolean.opBoolean","COPY",FACE,{"derivedFrom":makeQuery(id+"F17.opExtrude","SWEPT_FACE",FACE,{"disambiguationData":[OSD([subQ3])]})})})})})})})})})})})})})})})})})})})})})});}
            var Q62;
            {var subQ0=sQuery(id+"F16.wireOp",EDGE,"E151");var subQ2=sQuery(id+"F19.wireOp",EDGE,"E157");var subQ4=sQuery(id+"F19.wireOp",EDGE,"E158.MirrorCS");var subQ5=makeQuery(id+"F0Hq7nSFAMYVZvY_4.19.F20.opExtrude","SWEPT_FACE",FACE,{"disambiguationData":[OSD([subQ4])]});var subQ6=makeQuery(id+"F20.opExtrude","SWEPT_FACE",FACE,{"disambiguationData":[OSD([subQ2])]});Q62=makeQuery(id+"F0Hq7nSFAMYVZvY_4.20.F20.boolean.opBoolean","SPLIT",EDGE,{"disambiguationData":[TD([subQ5])],"derivedFrom":makeQuery(id+"F0Hq7nSFAMYVZvY_4.19.F20.boolean.opBoolean","SPLIT",EDGE,{"disambiguationData":[TD([subQ6])],"derivedFrom":makeQuery(id+"F0Hq7nSFAMYVZvY_4.18.F20.boolean.opBoolean","SPLIT",EDGE,{"disambiguationData":[TD([subQ6])],"derivedFrom":makeQuery(id+"F0Hq7nSFAMYVZvY_4.17.F20.boolean.opBoolean","SPLIT",EDGE,{"disambiguationData":[TD([subQ6])],"derivedFrom":makeQuery(id+"F0Hq7nSFAMYVZvY_4.16.F20.boolean.opBoolean","SPLIT",EDGE,{"disambiguationData":[TD([subQ6])],"derivedFrom":makeQuery(id+"F0Hq7nSFAMYVZvY_4.15.F20.boolean.opBoolean","SPLIT",EDGE,{"disambiguationData":[TD([subQ6])],"derivedFrom":makeQuery(id+"F0Hq7nSFAMYVZvY_4.14.F20.boolean.opBoolean","SPLIT",EDGE,{"disambiguationData":[TD([subQ6])],"derivedFrom":makeQuery(id+"F0Hq7nSFAMYVZvY_4.13.F20.boolean.opBoolean","SPLIT",EDGE,{"disambiguationData":[TD([subQ6])],"derivedFrom":makeQuery(id+"F0Hq7nSFAMYVZvY_4.12.F20.boolean.opBoolean","SPLIT",EDGE,{"disambiguationData":[TD([subQ6])],"derivedFrom":makeQuery(id+"F0Hq7nSFAMYVZvY_4.11.F20.boolean.opBoolean","SPLIT",EDGE,{"disambiguationData":[TD([subQ6])],"derivedFrom":makeQuery(id+"F0Hq7nSFAMYVZvY_4.10.F20.boolean.opBoolean","SPLIT",EDGE,{"disambiguationData":[TD([subQ6])],"derivedFrom":makeQuery(id+"F0Hq7nSFAMYVZvY_4.9.F20.boolean.opBoolean","SPLIT",EDGE,{"disambiguationData":[TD([subQ6])],"derivedFrom":makeQuery(id+"F0Hq7nSFAMYVZvY_4.8.F20.boolean.opBoolean","SPLIT",EDGE,{"disambiguationData":[TD([subQ6])],"derivedFrom":makeQuery(id+"F0Hq7nSFAMYVZvY_4.7.F20.boolean.opBoolean","SPLIT",EDGE,{"disambiguationData":[TD([subQ6])],"derivedFrom":makeQuery(id+"F0Hq7nSFAMYVZvY_4.6.F20.boolean.opBoolean","SPLIT",EDGE,{"disambiguationData":[TD([subQ6])],"derivedFrom":makeQuery(id+"F0Hq7nSFAMYVZvY_4.5.F20.boolean.opBoolean","SPLIT",EDGE,{"disambiguationData":[TD([subQ6])],"derivedFrom":makeQuery(id+"F0Hq7nSFAMYVZvY_4.4.F20.boolean.opBoolean","SPLIT",EDGE,{"disambiguationData":[TD([subQ6])],"derivedFrom":makeQuery(id+"F0Hq7nSFAMYVZvY_4.3.F20.boolean.opBoolean","SPLIT",EDGE,{"disambiguationData":[TD([subQ6])],"derivedFrom":makeQuery(id+"F0Hq7nSFAMYVZvY_4.2.F20.boolean.opBoolean","SPLIT",EDGE,{"disambiguationData":[TD([subQ6])],"derivedFrom":makeQuery(id+"F0Hq7nSFAMYVZvY_4.1.F20.boolean.opBoolean","SPLIT",EDGE,{"disambiguationData":[TD([subQ6])],"derivedFrom":makeQuery(id+"F17.boolean.opBoolean","COPY",EDGE,{"derivedFrom":makeQuery(id+"F17.opExtrude","CAP_EDGE",EDGE,{"disambiguationData":[OSD([subQ0])],"isStart":false})})})})})})})})})})})})})})})})})})})})})});}
            var Q63;
            {var subQ0=sQuery(id+"F19.wireOp",EDGE,"E158.MirrorCS");var subQ1=sQuery(id+"F19.wireOp",EDGE,"E157");var subQ3=sQuery(id+"F16.wireOp",EDGE,"E151");var subQ26=makeQuery(id+"F0Hq7nSFAMYVZvY_4.19.F20.opExtrude","SWEPT_FACE",FACE,{"disambiguationData":[OSD([subQ0])]});var subQ27=makeQuery(id+"F20.opExtrude","SWEPT_FACE",FACE,{"disambiguationData":[OSD([subQ1])]});Q63=makeQuery(id+"F0Hq7nSFAMYVZvY_4.20.F20.boolean.opBoolean","SPLIT",EDGE,{"disambiguationData":[TD([subQ26])],"derivedFrom":makeQuery(id+"F0Hq7nSFAMYVZvY_4.19.F20.boolean.opBoolean","SPLIT",EDGE,{"disambiguationData":[TD([subQ27])],"derivedFrom":makeQuery(id+"F0Hq7nSFAMYVZvY_4.18.F20.boolean.opBoolean","SPLIT",EDGE,{"disambiguationData":[TD([subQ27])],"derivedFrom":makeQuery(id+"F0Hq7nSFAMYVZvY_4.17.F20.boolean.opBoolean","SPLIT",EDGE,{"disambiguationData":[TD([subQ27])],"derivedFrom":makeQuery(id+"F0Hq7nSFAMYVZvY_4.16.F20.boolean.opBoolean","SPLIT",EDGE,{"disambiguationData":[TD([subQ27])],"derivedFrom":makeQuery(id+"F0Hq7nSFAMYVZvY_4.15.F20.boolean.opBoolean","SPLIT",EDGE,{"disambiguationData":[TD([subQ27])],"derivedFrom":makeQuery(id+"F0Hq7nSFAMYVZvY_4.14.F20.boolean.opBoolean","SPLIT",EDGE,{"disambiguationData":[TD([subQ27])],"derivedFrom":makeQuery(id+"F0Hq7nSFAMYVZvY_4.13.F20.boolean.opBoolean","SPLIT",EDGE,{"disambiguationData":[TD([subQ27])],"derivedFrom":makeQuery(id+"F0Hq7nSFAMYVZvY_4.12.F20.boolean.opBoolean","SPLIT",EDGE,{"disambiguationData":[TD([subQ27])],"derivedFrom":makeQuery(id+"F0Hq7nSFAMYVZvY_4.11.F20.boolean.opBoolean","SPLIT",EDGE,{"disambiguationData":[TD([subQ27])],"derivedFrom":makeQuery(id+"F0Hq7nSFAMYVZvY_4.10.F20.boolean.opBoolean","SPLIT",EDGE,{"disambiguationData":[TD([subQ27])],"derivedFrom":makeQuery(id+"F0Hq7nSFAMYVZvY_4.9.F20.boolean.opBoolean","SPLIT",EDGE,{"disambiguationData":[TD([subQ27])],"derivedFrom":makeQuery(id+"F0Hq7nSFAMYVZvY_4.8.F20.boolean.opBoolean","SPLIT",EDGE,{"disambiguationData":[TD([subQ27])],"derivedFrom":makeQuery(id+"F0Hq7nSFAMYVZvY_4.7.F20.boolean.opBoolean","SPLIT",EDGE,{"disambiguationData":[TD([subQ27])],"derivedFrom":makeQuery(id+"F0Hq7nSFAMYVZvY_4.6.F20.boolean.opBoolean","SPLIT",EDGE,{"disambiguationData":[TD([subQ27])],"derivedFrom":makeQuery(id+"F0Hq7nSFAMYVZvY_4.5.F20.boolean.opBoolean","SPLIT",EDGE,{"disambiguationData":[TD([subQ27])],"derivedFrom":makeQuery(id+"F0Hq7nSFAMYVZvY_4.4.F20.boolean.opBoolean","SPLIT",EDGE,{"disambiguationData":[TD([subQ27])],"derivedFrom":makeQuery(id+"F0Hq7nSFAMYVZvY_4.3.F20.boolean.opBoolean","SPLIT",EDGE,{"disambiguationData":[TD([subQ27])],"derivedFrom":makeQuery(id+"F0Hq7nSFAMYVZvY_4.2.F20.boolean.opBoolean","SPLIT",EDGE,{"disambiguationData":[TD([subQ27])],"derivedFrom":makeQuery(id+"F0Hq7nSFAMYVZvY_4.1.F20.boolean.opBoolean","SPLIT",EDGE,{"disambiguationData":[TD([subQ27])],"derivedFrom":makeQuery(id+"F18.boolean.opBoolean","COPY",EDGE,{"derivedFrom":makeQuery(id+"F18.opExtrude","CAP_EDGE",EDGE,{"disambiguationData":[OSD([subQ3])],"isStart":false})})})})})})})})})})})})})})})})})})})})})});}
            var Q64;
            Q64=makeQuery(id+"F0Hq7nSFAMYVZvY_4.21.F20.opExtrude","SWEPT_FACE",FACE,{"disambiguationData":[OSD([sQuery(id+"F19.wireOp",EDGE,"E157")])]});
            var Q65;
            Q65=makeQuery(id+"F0Hq7nSFAMYVZvY_4.21.F20.opExtrude","SWEPT_FACE",FACE,{"disambiguationData":[OSD([sQuery(id+"F19.wireOp",EDGE,"E158.MirrorCS")])]});
            var Q66;
            Q66=makeQuery(id+"F0Hq7nSFAMYVZvY_4.21.F20.opExtrude","CAP_EDGE",EDGE,{"disambiguationData":[OSD([sQuery(id+"F19.wireOp",EDGE,"E158.MirrorCS")])],"isStart":false});
            var Q67;
            {var subQ0=sQuery(id+"F16.wireOp",EDGE,"E151");var subQ2=sQuery(id+"F16.wireOp",EDGE,"E152");var subQ4=sQuery(id+"F19.wireOp",EDGE,"E157");var subQ5=sQuery(id+"F19.wireOp",EDGE,"E158.MirrorCS");var subQ6=makeQuery(id+"F0Hq7nSFAMYVZvY_4.20.F20.opExtrude","SWEPT_FACE",FACE,{"disambiguationData":[OSD([subQ5])]});var subQ7=makeQuery(id+"F20.opExtrude","SWEPT_FACE",FACE,{"disambiguationData":[OSD([subQ4])]});Q67=makeQuery(id+"F0Hq7nSFAMYVZvY_4.21.F20.boolean.opBoolean","SPLIT",FACE,{"disambiguationData":[TD([subQ6])],"derivedFrom":makeQuery(id+"F0Hq7nSFAMYVZvY_4.20.F20.boolean.opBoolean","SPLIT",FACE,{"disambiguationData":[TD([subQ7])],"derivedFrom":makeQuery(id+"F0Hq7nSFAMYVZvY_4.19.F20.boolean.opBoolean","SPLIT",FACE,{"disambiguationData":[TD([subQ7])],"derivedFrom":makeQuery(id+"F0Hq7nSFAMYVZvY_4.18.F20.boolean.opBoolean","SPLIT",FACE,{"disambiguationData":[TD([subQ7])],"derivedFrom":makeQuery(id+"F0Hq7nSFAMYVZvY_4.17.F20.boolean.opBoolean","SPLIT",FACE,{"disambiguationData":[TD([subQ7])],"derivedFrom":makeQuery(id+"F0Hq7nSFAMYVZvY_4.16.F20.boolean.opBoolean","SPLIT",FACE,{"disambiguationData":[TD([subQ7])],"derivedFrom":makeQuery(id+"F0Hq7nSFAMYVZvY_4.15.F20.boolean.opBoolean","SPLIT",FACE,{"disambiguationData":[TD([subQ7])],"derivedFrom":makeQuery(id+"F0Hq7nSFAMYVZvY_4.14.F20.boolean.opBoolean","SPLIT",FACE,{"disambiguationData":[TD([subQ7])],"derivedFrom":makeQuery(id+"F0Hq7nSFAMYVZvY_4.13.F20.boolean.opBoolean","SPLIT",FACE,{"disambiguationData":[TD([subQ7])],"derivedFrom":makeQuery(id+"F0Hq7nSFAMYVZvY_4.12.F20.boolean.opBoolean","SPLIT",FACE,{"disambiguationData":[TD([subQ7])],"derivedFrom":makeQuery(id+"F0Hq7nSFAMYVZvY_4.11.F20.boolean.opBoolean","SPLIT",FACE,{"disambiguationData":[TD([subQ7])],"derivedFrom":makeQuery(id+"F0Hq7nSFAMYVZvY_4.10.F20.boolean.opBoolean","SPLIT",FACE,{"disambiguationData":[TD([subQ7])],"derivedFrom":makeQuery(id+"F0Hq7nSFAMYVZvY_4.9.F20.boolean.opBoolean","SPLIT",FACE,{"disambiguationData":[TD([subQ7])],"derivedFrom":makeQuery(id+"F0Hq7nSFAMYVZvY_4.8.F20.boolean.opBoolean","SPLIT",FACE,{"disambiguationData":[TD([subQ7])],"derivedFrom":makeQuery(id+"F0Hq7nSFAMYVZvY_4.7.F20.boolean.opBoolean","SPLIT",FACE,{"disambiguationData":[TD([subQ7])],"derivedFrom":makeQuery(id+"F0Hq7nSFAMYVZvY_4.6.F20.boolean.opBoolean","SPLIT",FACE,{"disambiguationData":[TD([subQ7])],"derivedFrom":makeQuery(id+"F0Hq7nSFAMYVZvY_4.5.F20.boolean.opBoolean","SPLIT",FACE,{"disambiguationData":[TD([subQ7])],"derivedFrom":makeQuery(id+"F0Hq7nSFAMYVZvY_4.4.F20.boolean.opBoolean","SPLIT",FACE,{"disambiguationData":[TD([subQ7])],"derivedFrom":makeQuery(id+"F0Hq7nSFAMYVZvY_4.3.F20.boolean.opBoolean","SPLIT",FACE,{"disambiguationData":[TD([subQ7])],"derivedFrom":makeQuery(id+"F0Hq7nSFAMYVZvY_4.2.F20.boolean.opBoolean","SPLIT",FACE,{"disambiguationData":[TD([subQ7])],"derivedFrom":makeQuery(id+"F0Hq7nSFAMYVZvY_4.1.F20.boolean.opBoolean","SPLIT",FACE,{"disambiguationData":[TD([subQ7])],"derivedFrom":makeQuery(id+"F17.boolean.opBoolean","COPY",FACE,{"derivedFrom":makeQuery(id+"F17.opExtrude","CAP_FACE",FACE,{"disambiguationData":[OSD([subQ0,subQ2])],"isStart":false})})})})})})})})})})})})})})})})})})})})})})});}
            var Q68;
            {var subQ0=sQuery(id+"F19.wireOp",EDGE,"E158.MirrorCS");var subQ1=sQuery(id+"F19.wireOp",EDGE,"E157");var subQ3=sQuery(id+"F16.wireOp",EDGE,"E151");var subQ27=makeQuery(id+"F0Hq7nSFAMYVZvY_4.20.F20.opExtrude","SWEPT_FACE",FACE,{"disambiguationData":[OSD([subQ0])]});var subQ28=makeQuery(id+"F20.opExtrude","SWEPT_FACE",FACE,{"disambiguationData":[OSD([subQ1])]});Q68=makeQuery(id+"F0Hq7nSFAMYVZvY_4.21.F20.boolean.opBoolean","SPLIT",FACE,{"disambiguationData":[TD([subQ27])],"derivedFrom":makeQuery(id+"F0Hq7nSFAMYVZvY_4.20.F20.boolean.opBoolean","SPLIT",FACE,{"disambiguationData":[TD([subQ28])],"derivedFrom":makeQuery(id+"F0Hq7nSFAMYVZvY_4.19.F20.boolean.opBoolean","SPLIT",FACE,{"disambiguationData":[TD([subQ28])],"derivedFrom":makeQuery(id+"F0Hq7nSFAMYVZvY_4.18.F20.boolean.opBoolean","SPLIT",FACE,{"disambiguationData":[TD([subQ28])],"derivedFrom":makeQuery(id+"F0Hq7nSFAMYVZvY_4.17.F20.boolean.opBoolean","SPLIT",FACE,{"disambiguationData":[TD([subQ28])],"derivedFrom":makeQuery(id+"F0Hq7nSFAMYVZvY_4.16.F20.boolean.opBoolean","SPLIT",FACE,{"disambiguationData":[TD([subQ28])],"derivedFrom":makeQuery(id+"F0Hq7nSFAMYVZvY_4.15.F20.boolean.opBoolean","SPLIT",FACE,{"disambiguationData":[TD([subQ28])],"derivedFrom":makeQuery(id+"F0Hq7nSFAMYVZvY_4.14.F20.boolean.opBoolean","SPLIT",FACE,{"disambiguationData":[TD([subQ28])],"derivedFrom":makeQuery(id+"F0Hq7nSFAMYVZvY_4.13.F20.boolean.opBoolean","SPLIT",FACE,{"disambiguationData":[TD([subQ28])],"derivedFrom":makeQuery(id+"F0Hq7nSFAMYVZvY_4.12.F20.boolean.opBoolean","SPLIT",FACE,{"disambiguationData":[TD([subQ28])],"derivedFrom":makeQuery(id+"F0Hq7nSFAMYVZvY_4.11.F20.boolean.opBoolean","SPLIT",FACE,{"disambiguationData":[TD([subQ28])],"derivedFrom":makeQuery(id+"F0Hq7nSFAMYVZvY_4.10.F20.boolean.opBoolean","SPLIT",FACE,{"disambiguationData":[TD([subQ28])],"derivedFrom":makeQuery(id+"F0Hq7nSFAMYVZvY_4.9.F20.boolean.opBoolean","SPLIT",FACE,{"disambiguationData":[TD([subQ28])],"derivedFrom":makeQuery(id+"F0Hq7nSFAMYVZvY_4.8.F20.boolean.opBoolean","SPLIT",FACE,{"disambiguationData":[TD([subQ28])],"derivedFrom":makeQuery(id+"F0Hq7nSFAMYVZvY_4.7.F20.boolean.opBoolean","SPLIT",FACE,{"disambiguationData":[TD([subQ28])],"derivedFrom":makeQuery(id+"F0Hq7nSFAMYVZvY_4.6.F20.boolean.opBoolean","SPLIT",FACE,{"disambiguationData":[TD([subQ28])],"derivedFrom":makeQuery(id+"F0Hq7nSFAMYVZvY_4.5.F20.boolean.opBoolean","SPLIT",FACE,{"disambiguationData":[TD([subQ28])],"derivedFrom":makeQuery(id+"F0Hq7nSFAMYVZvY_4.4.F20.boolean.opBoolean","SPLIT",FACE,{"disambiguationData":[TD([subQ28])],"derivedFrom":makeQuery(id+"F0Hq7nSFAMYVZvY_4.3.F20.boolean.opBoolean","SPLIT",FACE,{"disambiguationData":[TD([subQ28])],"derivedFrom":makeQuery(id+"F0Hq7nSFAMYVZvY_4.2.F20.boolean.opBoolean","SPLIT",FACE,{"disambiguationData":[TD([subQ28])],"derivedFrom":makeQuery(id+"F0Hq7nSFAMYVZvY_4.1.F20.boolean.opBoolean","SPLIT",FACE,{"disambiguationData":[TD([subQ28])],"derivedFrom":makeQuery(id+"F17.boolean.opBoolean","COPY",FACE,{"derivedFrom":makeQuery(id+"F17.opExtrude","SWEPT_FACE",FACE,{"disambiguationData":[OSD([subQ3])]})})})})})})})})})})})})})})})})})})})})})})});}
            var Q69;
            {var subQ0=sQuery(id+"F16.wireOp",EDGE,"E151");var subQ3=sQuery(id+"F19.wireOp",EDGE,"E158.MirrorCS");var subQ4=makeQuery(id+"F0Hq7nSFAMYVZvY_4.20.F20.opExtrude","SWEPT_FACE",FACE,{"disambiguationData":[OSD([subQ3])]});var subQ5=sQuery(id+"F19.wireOp",EDGE,"E157");var subQ6=makeQuery(id+"F20.opExtrude","SWEPT_FACE",FACE,{"disambiguationData":[OSD([subQ5])]});Q69=makeQuery(id+"F0Hq7nSFAMYVZvY_4.21.F20.boolean.opBoolean","SPLIT",EDGE,{"disambiguationData":[TD([subQ4])],"derivedFrom":makeQuery(id+"F0Hq7nSFAMYVZvY_4.20.F20.boolean.opBoolean","SPLIT",EDGE,{"disambiguationData":[TD([subQ6])],"derivedFrom":makeQuery(id+"F0Hq7nSFAMYVZvY_4.19.F20.boolean.opBoolean","SPLIT",EDGE,{"disambiguationData":[TD([subQ6])],"derivedFrom":makeQuery(id+"F0Hq7nSFAMYVZvY_4.18.F20.boolean.opBoolean","SPLIT",EDGE,{"disambiguationData":[TD([subQ6])],"derivedFrom":makeQuery(id+"F0Hq7nSFAMYVZvY_4.17.F20.boolean.opBoolean","SPLIT",EDGE,{"disambiguationData":[TD([subQ6])],"derivedFrom":makeQuery(id+"F0Hq7nSFAMYVZvY_4.16.F20.boolean.opBoolean","SPLIT",EDGE,{"disambiguationData":[TD([subQ6])],"derivedFrom":makeQuery(id+"F0Hq7nSFAMYVZvY_4.15.F20.boolean.opBoolean","SPLIT",EDGE,{"disambiguationData":[TD([subQ6])],"derivedFrom":makeQuery(id+"F0Hq7nSFAMYVZvY_4.14.F20.boolean.opBoolean","SPLIT",EDGE,{"disambiguationData":[TD([subQ6])],"derivedFrom":makeQuery(id+"F0Hq7nSFAMYVZvY_4.13.F20.boolean.opBoolean","SPLIT",EDGE,{"disambiguationData":[TD([subQ6])],"derivedFrom":makeQuery(id+"F0Hq7nSFAMYVZvY_4.12.F20.boolean.opBoolean","SPLIT",EDGE,{"disambiguationData":[TD([subQ6])],"derivedFrom":makeQuery(id+"F0Hq7nSFAMYVZvY_4.11.F20.boolean.opBoolean","SPLIT",EDGE,{"disambiguationData":[TD([subQ6])],"derivedFrom":makeQuery(id+"F0Hq7nSFAMYVZvY_4.10.F20.boolean.opBoolean","SPLIT",EDGE,{"disambiguationData":[TD([subQ6])],"derivedFrom":makeQuery(id+"F0Hq7nSFAMYVZvY_4.9.F20.boolean.opBoolean","SPLIT",EDGE,{"disambiguationData":[TD([subQ6])],"derivedFrom":makeQuery(id+"F0Hq7nSFAMYVZvY_4.8.F20.boolean.opBoolean","SPLIT",EDGE,{"disambiguationData":[TD([subQ6])],"derivedFrom":makeQuery(id+"F0Hq7nSFAMYVZvY_4.7.F20.boolean.opBoolean","SPLIT",EDGE,{"disambiguationData":[TD([subQ6])],"derivedFrom":makeQuery(id+"F0Hq7nSFAMYVZvY_4.6.F20.boolean.opBoolean","SPLIT",EDGE,{"disambiguationData":[TD([subQ6])],"derivedFrom":makeQuery(id+"F0Hq7nSFAMYVZvY_4.5.F20.boolean.opBoolean","SPLIT",EDGE,{"disambiguationData":[TD([subQ6])],"derivedFrom":makeQuery(id+"F0Hq7nSFAMYVZvY_4.4.F20.boolean.opBoolean","SPLIT",EDGE,{"disambiguationData":[TD([subQ6])],"derivedFrom":makeQuery(id+"F0Hq7nSFAMYVZvY_4.3.F20.boolean.opBoolean","SPLIT",EDGE,{"disambiguationData":[TD([subQ6])],"derivedFrom":makeQuery(id+"F0Hq7nSFAMYVZvY_4.2.F20.boolean.opBoolean","SPLIT",EDGE,{"disambiguationData":[TD([subQ6])],"derivedFrom":makeQuery(id+"F0Hq7nSFAMYVZvY_4.1.F20.boolean.opBoolean","SPLIT",EDGE,{"disambiguationData":[TD([subQ6])],"derivedFrom":makeQuery(id+"F17.boolean.opBoolean","COPY",EDGE,{"derivedFrom":makeQuery(id+"F17.opExtrude","CAP_EDGE",EDGE,{"disambiguationData":[OSD([subQ0])],"isStart":false})})})})})})})})})})})})})})})})})})})})})})});}
            var Q70;
            Q70=makeQuery(id+"F0Hq7nSFAMYVZvY_4.22.F20.opExtrude","SWEPT_FACE",FACE,{"disambiguationData":[OSD([sQuery(id+"F19.wireOp",EDGE,"E157")])]});
            var Q71;
            Q71=makeQuery(id+"F0Hq7nSFAMYVZvY_4.22.F20.opExtrude","CAP_EDGE",EDGE,{"disambiguationData":[OSD([sQuery(id+"F19.wireOp",EDGE,"E158.MirrorCS")])],"isStart":false});
            var Q72;
            {var subQ0=sQuery(id+"F16.wireOp",EDGE,"E151");var subQ2=sQuery(id+"F19.wireOp",EDGE,"E158.MirrorCS");var subQ3=makeQuery(id+"F0Hq7nSFAMYVZvY_4.21.F20.opExtrude","SWEPT_FACE",FACE,{"disambiguationData":[OSD([subQ2])]});var subQ4=sQuery(id+"F16.wireOp",EDGE,"E152");var subQ6=sQuery(id+"F19.wireOp",EDGE,"E157");var subQ7=makeQuery(id+"F20.opExtrude","SWEPT_FACE",FACE,{"disambiguationData":[OSD([subQ6])]});Q72=makeQuery(id+"F0Hq7nSFAMYVZvY_4.22.F20.boolean.opBoolean","SPLIT",FACE,{"disambiguationData":[TD([subQ3])],"derivedFrom":makeQuery(id+"F0Hq7nSFAMYVZvY_4.21.F20.boolean.opBoolean","SPLIT",FACE,{"disambiguationData":[TD([subQ7])],"derivedFrom":makeQuery(id+"F0Hq7nSFAMYVZvY_4.20.F20.boolean.opBoolean","SPLIT",FACE,{"disambiguationData":[TD([subQ7])],"derivedFrom":makeQuery(id+"F0Hq7nSFAMYVZvY_4.19.F20.boolean.opBoolean","SPLIT",FACE,{"disambiguationData":[TD([subQ7])],"derivedFrom":makeQuery(id+"F0Hq7nSFAMYVZvY_4.18.F20.boolean.opBoolean","SPLIT",FACE,{"disambiguationData":[TD([subQ7])],"derivedFrom":makeQuery(id+"F0Hq7nSFAMYVZvY_4.17.F20.boolean.opBoolean","SPLIT",FACE,{"disambiguationData":[TD([subQ7])],"derivedFrom":makeQuery(id+"F0Hq7nSFAMYVZvY_4.16.F20.boolean.opBoolean","SPLIT",FACE,{"disambiguationData":[TD([subQ7])],"derivedFrom":makeQuery(id+"F0Hq7nSFAMYVZvY_4.15.F20.boolean.opBoolean","SPLIT",FACE,{"disambiguationData":[TD([subQ7])],"derivedFrom":makeQuery(id+"F0Hq7nSFAMYVZvY_4.14.F20.boolean.opBoolean","SPLIT",FACE,{"disambiguationData":[TD([subQ7])],"derivedFrom":makeQuery(id+"F0Hq7nSFAMYVZvY_4.13.F20.boolean.opBoolean","SPLIT",FACE,{"disambiguationData":[TD([subQ7])],"derivedFrom":makeQuery(id+"F0Hq7nSFAMYVZvY_4.12.F20.boolean.opBoolean","SPLIT",FACE,{"disambiguationData":[TD([subQ7])],"derivedFrom":makeQuery(id+"F0Hq7nSFAMYVZvY_4.11.F20.boolean.opBoolean","SPLIT",FACE,{"disambiguationData":[TD([subQ7])],"derivedFrom":makeQuery(id+"F0Hq7nSFAMYVZvY_4.10.F20.boolean.opBoolean","SPLIT",FACE,{"disambiguationData":[TD([subQ7])],"derivedFrom":makeQuery(id+"F0Hq7nSFAMYVZvY_4.9.F20.boolean.opBoolean","SPLIT",FACE,{"disambiguationData":[TD([subQ7])],"derivedFrom":makeQuery(id+"F0Hq7nSFAMYVZvY_4.8.F20.boolean.opBoolean","SPLIT",FACE,{"disambiguationData":[TD([subQ7])],"derivedFrom":makeQuery(id+"F0Hq7nSFAMYVZvY_4.7.F20.boolean.opBoolean","SPLIT",FACE,{"disambiguationData":[TD([subQ7])],"derivedFrom":makeQuery(id+"F0Hq7nSFAMYVZvY_4.6.F20.boolean.opBoolean","SPLIT",FACE,{"disambiguationData":[TD([subQ7])],"derivedFrom":makeQuery(id+"F0Hq7nSFAMYVZvY_4.5.F20.boolean.opBoolean","SPLIT",FACE,{"disambiguationData":[TD([subQ7])],"derivedFrom":makeQuery(id+"F0Hq7nSFAMYVZvY_4.4.F20.boolean.opBoolean","SPLIT",FACE,{"disambiguationData":[TD([subQ7])],"derivedFrom":makeQuery(id+"F0Hq7nSFAMYVZvY_4.3.F20.boolean.opBoolean","SPLIT",FACE,{"disambiguationData":[TD([subQ7])],"derivedFrom":makeQuery(id+"F0Hq7nSFAMYVZvY_4.2.F20.boolean.opBoolean","SPLIT",FACE,{"disambiguationData":[TD([subQ7])],"derivedFrom":makeQuery(id+"F0Hq7nSFAMYVZvY_4.1.F20.boolean.opBoolean","SPLIT",FACE,{"disambiguationData":[TD([subQ7])],"derivedFrom":makeQuery(id+"F17.boolean.opBoolean","COPY",FACE,{"derivedFrom":makeQuery(id+"F17.opExtrude","CAP_FACE",FACE,{"disambiguationData":[OSD([subQ0,subQ4])],"isStart":false})})})})})})})})})})})})})})})})})})})})})})})});}
            var Q73;
            {var subQ0=sQuery(id+"F19.wireOp",EDGE,"E158.MirrorCS");var subQ1=sQuery(id+"F19.wireOp",EDGE,"E157");var subQ3=sQuery(id+"F16.wireOp",EDGE,"E151");var subQ18=makeQuery(id+"F0Hq7nSFAMYVZvY_4.21.F20.opExtrude","SWEPT_FACE",FACE,{"disambiguationData":[OSD([subQ0])]});var subQ29=makeQuery(id+"F20.opExtrude","SWEPT_FACE",FACE,{"disambiguationData":[OSD([subQ1])]});Q73=makeQuery(id+"F0Hq7nSFAMYVZvY_4.22.F20.boolean.opBoolean","SPLIT",FACE,{"disambiguationData":[TD([subQ18])],"derivedFrom":makeQuery(id+"F0Hq7nSFAMYVZvY_4.21.F20.boolean.opBoolean","SPLIT",FACE,{"disambiguationData":[TD([subQ29])],"derivedFrom":makeQuery(id+"F0Hq7nSFAMYVZvY_4.20.F20.boolean.opBoolean","SPLIT",FACE,{"disambiguationData":[TD([subQ29])],"derivedFrom":makeQuery(id+"F0Hq7nSFAMYVZvY_4.19.F20.boolean.opBoolean","SPLIT",FACE,{"disambiguationData":[TD([subQ29])],"derivedFrom":makeQuery(id+"F0Hq7nSFAMYVZvY_4.18.F20.boolean.opBoolean","SPLIT",FACE,{"disambiguationData":[TD([subQ29])],"derivedFrom":makeQuery(id+"F0Hq7nSFAMYVZvY_4.17.F20.boolean.opBoolean","SPLIT",FACE,{"disambiguationData":[TD([subQ29])],"derivedFrom":makeQuery(id+"F0Hq7nSFAMYVZvY_4.16.F20.boolean.opBoolean","SPLIT",FACE,{"disambiguationData":[TD([subQ29])],"derivedFrom":makeQuery(id+"F0Hq7nSFAMYVZvY_4.15.F20.boolean.opBoolean","SPLIT",FACE,{"disambiguationData":[TD([subQ29])],"derivedFrom":makeQuery(id+"F0Hq7nSFAMYVZvY_4.14.F20.boolean.opBoolean","SPLIT",FACE,{"disambiguationData":[TD([subQ29])],"derivedFrom":makeQuery(id+"F0Hq7nSFAMYVZvY_4.13.F20.boolean.opBoolean","SPLIT",FACE,{"disambiguationData":[TD([subQ29])],"derivedFrom":makeQuery(id+"F0Hq7nSFAMYVZvY_4.12.F20.boolean.opBoolean","SPLIT",FACE,{"disambiguationData":[TD([subQ29])],"derivedFrom":makeQuery(id+"F0Hq7nSFAMYVZvY_4.11.F20.boolean.opBoolean","SPLIT",FACE,{"disambiguationData":[TD([subQ29])],"derivedFrom":makeQuery(id+"F0Hq7nSFAMYVZvY_4.10.F20.boolean.opBoolean","SPLIT",FACE,{"disambiguationData":[TD([subQ29])],"derivedFrom":makeQuery(id+"F0Hq7nSFAMYVZvY_4.9.F20.boolean.opBoolean","SPLIT",FACE,{"disambiguationData":[TD([subQ29])],"derivedFrom":makeQuery(id+"F0Hq7nSFAMYVZvY_4.8.F20.boolean.opBoolean","SPLIT",FACE,{"disambiguationData":[TD([subQ29])],"derivedFrom":makeQuery(id+"F0Hq7nSFAMYVZvY_4.7.F20.boolean.opBoolean","SPLIT",FACE,{"disambiguationData":[TD([subQ29])],"derivedFrom":makeQuery(id+"F0Hq7nSFAMYVZvY_4.6.F20.boolean.opBoolean","SPLIT",FACE,{"disambiguationData":[TD([subQ29])],"derivedFrom":makeQuery(id+"F0Hq7nSFAMYVZvY_4.5.F20.boolean.opBoolean","SPLIT",FACE,{"disambiguationData":[TD([subQ29])],"derivedFrom":makeQuery(id+"F0Hq7nSFAMYVZvY_4.4.F20.boolean.opBoolean","SPLIT",FACE,{"disambiguationData":[TD([subQ29])],"derivedFrom":makeQuery(id+"F0Hq7nSFAMYVZvY_4.3.F20.boolean.opBoolean","SPLIT",FACE,{"disambiguationData":[TD([subQ29])],"derivedFrom":makeQuery(id+"F0Hq7nSFAMYVZvY_4.2.F20.boolean.opBoolean","SPLIT",FACE,{"disambiguationData":[TD([subQ29])],"derivedFrom":makeQuery(id+"F0Hq7nSFAMYVZvY_4.1.F20.boolean.opBoolean","SPLIT",FACE,{"disambiguationData":[TD([subQ29])],"derivedFrom":makeQuery(id+"F17.boolean.opBoolean","COPY",FACE,{"derivedFrom":makeQuery(id+"F17.opExtrude","SWEPT_FACE",FACE,{"disambiguationData":[OSD([subQ3])]})})})})})})})})})})})})})})})})})})})})})})})});}
            var Q74;
            {var subQ0=sQuery(id+"F16.wireOp",EDGE,"E151");var subQ2=sQuery(id+"F19.wireOp",EDGE,"E158.MirrorCS");var subQ3=makeQuery(id+"F0Hq7nSFAMYVZvY_4.21.F20.opExtrude","SWEPT_FACE",FACE,{"disambiguationData":[OSD([subQ2])]});var subQ5=sQuery(id+"F19.wireOp",EDGE,"E157");var subQ6=makeQuery(id+"F20.opExtrude","SWEPT_FACE",FACE,{"disambiguationData":[OSD([subQ5])]});Q74=makeQuery(id+"F0Hq7nSFAMYVZvY_4.22.F20.boolean.opBoolean","SPLIT",EDGE,{"disambiguationData":[TD([subQ3])],"derivedFrom":makeQuery(id+"F0Hq7nSFAMYVZvY_4.21.F20.boolean.opBoolean","SPLIT",EDGE,{"disambiguationData":[TD([subQ6])],"derivedFrom":makeQuery(id+"F0Hq7nSFAMYVZvY_4.20.F20.boolean.opBoolean","SPLIT",EDGE,{"disambiguationData":[TD([subQ6])],"derivedFrom":makeQuery(id+"F0Hq7nSFAMYVZvY_4.19.F20.boolean.opBoolean","SPLIT",EDGE,{"disambiguationData":[TD([subQ6])],"derivedFrom":makeQuery(id+"F0Hq7nSFAMYVZvY_4.18.F20.boolean.opBoolean","SPLIT",EDGE,{"disambiguationData":[TD([subQ6])],"derivedFrom":makeQuery(id+"F0Hq7nSFAMYVZvY_4.17.F20.boolean.opBoolean","SPLIT",EDGE,{"disambiguationData":[TD([subQ6])],"derivedFrom":makeQuery(id+"F0Hq7nSFAMYVZvY_4.16.F20.boolean.opBoolean","SPLIT",EDGE,{"disambiguationData":[TD([subQ6])],"derivedFrom":makeQuery(id+"F0Hq7nSFAMYVZvY_4.15.F20.boolean.opBoolean","SPLIT",EDGE,{"disambiguationData":[TD([subQ6])],"derivedFrom":makeQuery(id+"F0Hq7nSFAMYVZvY_4.14.F20.boolean.opBoolean","SPLIT",EDGE,{"disambiguationData":[TD([subQ6])],"derivedFrom":makeQuery(id+"F0Hq7nSFAMYVZvY_4.13.F20.boolean.opBoolean","SPLIT",EDGE,{"disambiguationData":[TD([subQ6])],"derivedFrom":makeQuery(id+"F0Hq7nSFAMYVZvY_4.12.F20.boolean.opBoolean","SPLIT",EDGE,{"disambiguationData":[TD([subQ6])],"derivedFrom":makeQuery(id+"F0Hq7nSFAMYVZvY_4.11.F20.boolean.opBoolean","SPLIT",EDGE,{"disambiguationData":[TD([subQ6])],"derivedFrom":makeQuery(id+"F0Hq7nSFAMYVZvY_4.10.F20.boolean.opBoolean","SPLIT",EDGE,{"disambiguationData":[TD([subQ6])],"derivedFrom":makeQuery(id+"F0Hq7nSFAMYVZvY_4.9.F20.boolean.opBoolean","SPLIT",EDGE,{"disambiguationData":[TD([subQ6])],"derivedFrom":makeQuery(id+"F0Hq7nSFAMYVZvY_4.8.F20.boolean.opBoolean","SPLIT",EDGE,{"disambiguationData":[TD([subQ6])],"derivedFrom":makeQuery(id+"F0Hq7nSFAMYVZvY_4.7.F20.boolean.opBoolean","SPLIT",EDGE,{"disambiguationData":[TD([subQ6])],"derivedFrom":makeQuery(id+"F0Hq7nSFAMYVZvY_4.6.F20.boolean.opBoolean","SPLIT",EDGE,{"disambiguationData":[TD([subQ6])],"derivedFrom":makeQuery(id+"F0Hq7nSFAMYVZvY_4.5.F20.boolean.opBoolean","SPLIT",EDGE,{"disambiguationData":[TD([subQ6])],"derivedFrom":makeQuery(id+"F0Hq7nSFAMYVZvY_4.4.F20.boolean.opBoolean","SPLIT",EDGE,{"disambiguationData":[TD([subQ6])],"derivedFrom":makeQuery(id+"F0Hq7nSFAMYVZvY_4.3.F20.boolean.opBoolean","SPLIT",EDGE,{"disambiguationData":[TD([subQ6])],"derivedFrom":makeQuery(id+"F0Hq7nSFAMYVZvY_4.2.F20.boolean.opBoolean","SPLIT",EDGE,{"disambiguationData":[TD([subQ6])],"derivedFrom":makeQuery(id+"F0Hq7nSFAMYVZvY_4.1.F20.boolean.opBoolean","SPLIT",EDGE,{"disambiguationData":[TD([subQ6])],"derivedFrom":makeQuery(id+"F17.boolean.opBoolean","COPY",EDGE,{"derivedFrom":makeQuery(id+"F17.opExtrude","CAP_EDGE",EDGE,{"disambiguationData":[OSD([subQ0])],"isStart":false})})})})})})})})})})})})})})})})})})})})})})})});}
            var Q75;
            Q75=makeQuery(id+"F0Hq7nSFAMYVZvY_4.23.F20.opExtrude","SWEPT_FACE",FACE,{"disambiguationData":[OSD([sQuery(id+"F19.wireOp",EDGE,"E157")])]});
            var Q76;
            Q76=makeQuery(id+"F0Hq7nSFAMYVZvY_4.23.F20.opExtrude","CAP_EDGE",EDGE,{"disambiguationData":[OSD([sQuery(id+"F19.wireOp",EDGE,"E158.MirrorCS")])],"isStart":false});
            var Q77;
            {var subQ0=sQuery(id+"F16.wireOp",EDGE,"E151");var subQ2=sQuery(id+"F16.wireOp",EDGE,"E152");var subQ4=sQuery(id+"F19.wireOp",EDGE,"E158.MirrorCS");var subQ5=makeQuery(id+"F0Hq7nSFAMYVZvY_4.22.F20.opExtrude","SWEPT_FACE",FACE,{"disambiguationData":[OSD([subQ4])]});var subQ6=sQuery(id+"F19.wireOp",EDGE,"E157");var subQ7=makeQuery(id+"F20.opExtrude","SWEPT_FACE",FACE,{"disambiguationData":[OSD([subQ6])]});Q77=makeQuery(id+"F0Hq7nSFAMYVZvY_4.23.F20.boolean.opBoolean","SPLIT",FACE,{"disambiguationData":[TD([subQ5])],"derivedFrom":makeQuery(id+"F0Hq7nSFAMYVZvY_4.22.F20.boolean.opBoolean","SPLIT",FACE,{"disambiguationData":[TD([subQ7])],"derivedFrom":makeQuery(id+"F0Hq7nSFAMYVZvY_4.21.F20.boolean.opBoolean","SPLIT",FACE,{"disambiguationData":[TD([subQ7])],"derivedFrom":makeQuery(id+"F0Hq7nSFAMYVZvY_4.20.F20.boolean.opBoolean","SPLIT",FACE,{"disambiguationData":[TD([subQ7])],"derivedFrom":makeQuery(id+"F0Hq7nSFAMYVZvY_4.19.F20.boolean.opBoolean","SPLIT",FACE,{"disambiguationData":[TD([subQ7])],"derivedFrom":makeQuery(id+"F0Hq7nSFAMYVZvY_4.18.F20.boolean.opBoolean","SPLIT",FACE,{"disambiguationData":[TD([subQ7])],"derivedFrom":makeQuery(id+"F0Hq7nSFAMYVZvY_4.17.F20.boolean.opBoolean","SPLIT",FACE,{"disambiguationData":[TD([subQ7])],"derivedFrom":makeQuery(id+"F0Hq7nSFAMYVZvY_4.16.F20.boolean.opBoolean","SPLIT",FACE,{"disambiguationData":[TD([subQ7])],"derivedFrom":makeQuery(id+"F0Hq7nSFAMYVZvY_4.15.F20.boolean.opBoolean","SPLIT",FACE,{"disambiguationData":[TD([subQ7])],"derivedFrom":makeQuery(id+"F0Hq7nSFAMYVZvY_4.14.F20.boolean.opBoolean","SPLIT",FACE,{"disambiguationData":[TD([subQ7])],"derivedFrom":makeQuery(id+"F0Hq7nSFAMYVZvY_4.13.F20.boolean.opBoolean","SPLIT",FACE,{"disambiguationData":[TD([subQ7])],"derivedFrom":makeQuery(id+"F0Hq7nSFAMYVZvY_4.12.F20.boolean.opBoolean","SPLIT",FACE,{"disambiguationData":[TD([subQ7])],"derivedFrom":makeQuery(id+"F0Hq7nSFAMYVZvY_4.11.F20.boolean.opBoolean","SPLIT",FACE,{"disambiguationData":[TD([subQ7])],"derivedFrom":makeQuery(id+"F0Hq7nSFAMYVZvY_4.10.F20.boolean.opBoolean","SPLIT",FACE,{"disambiguationData":[TD([subQ7])],"derivedFrom":makeQuery(id+"F0Hq7nSFAMYVZvY_4.9.F20.boolean.opBoolean","SPLIT",FACE,{"disambiguationData":[TD([subQ7])],"derivedFrom":makeQuery(id+"F0Hq7nSFAMYVZvY_4.8.F20.boolean.opBoolean","SPLIT",FACE,{"disambiguationData":[TD([subQ7])],"derivedFrom":makeQuery(id+"F0Hq7nSFAMYVZvY_4.7.F20.boolean.opBoolean","SPLIT",FACE,{"disambiguationData":[TD([subQ7])],"derivedFrom":makeQuery(id+"F0Hq7nSFAMYVZvY_4.6.F20.boolean.opBoolean","SPLIT",FACE,{"disambiguationData":[TD([subQ7])],"derivedFrom":makeQuery(id+"F0Hq7nSFAMYVZvY_4.5.F20.boolean.opBoolean","SPLIT",FACE,{"disambiguationData":[TD([subQ7])],"derivedFrom":makeQuery(id+"F0Hq7nSFAMYVZvY_4.4.F20.boolean.opBoolean","SPLIT",FACE,{"disambiguationData":[TD([subQ7])],"derivedFrom":makeQuery(id+"F0Hq7nSFAMYVZvY_4.3.F20.boolean.opBoolean","SPLIT",FACE,{"disambiguationData":[TD([subQ7])],"derivedFrom":makeQuery(id+"F0Hq7nSFAMYVZvY_4.2.F20.boolean.opBoolean","SPLIT",FACE,{"disambiguationData":[TD([subQ7])],"derivedFrom":makeQuery(id+"F0Hq7nSFAMYVZvY_4.1.F20.boolean.opBoolean","SPLIT",FACE,{"disambiguationData":[TD([subQ7])],"derivedFrom":makeQuery(id+"F17.boolean.opBoolean","COPY",FACE,{"derivedFrom":makeQuery(id+"F17.opExtrude","CAP_FACE",FACE,{"disambiguationData":[OSD([subQ0,subQ2])],"isStart":false})})})})})})})})})})})})})})})})})})})})})})})})});}
            var Q78;
            {var subQ0=sQuery(id+"F19.wireOp",EDGE,"E158.MirrorCS");var subQ1=sQuery(id+"F19.wireOp",EDGE,"E157");var subQ3=sQuery(id+"F16.wireOp",EDGE,"E151");var subQ29=makeQuery(id+"F0Hq7nSFAMYVZvY_4.22.F20.opExtrude","SWEPT_FACE",FACE,{"disambiguationData":[OSD([subQ0])]});var subQ30=makeQuery(id+"F20.opExtrude","SWEPT_FACE",FACE,{"disambiguationData":[OSD([subQ1])]});Q78=makeQuery(id+"F0Hq7nSFAMYVZvY_4.23.F20.boolean.opBoolean","SPLIT",FACE,{"disambiguationData":[TD([subQ29])],"derivedFrom":makeQuery(id+"F0Hq7nSFAMYVZvY_4.22.F20.boolean.opBoolean","SPLIT",FACE,{"disambiguationData":[TD([subQ30])],"derivedFrom":makeQuery(id+"F0Hq7nSFAMYVZvY_4.21.F20.boolean.opBoolean","SPLIT",FACE,{"disambiguationData":[TD([subQ30])],"derivedFrom":makeQuery(id+"F0Hq7nSFAMYVZvY_4.20.F20.boolean.opBoolean","SPLIT",FACE,{"disambiguationData":[TD([subQ30])],"derivedFrom":makeQuery(id+"F0Hq7nSFAMYVZvY_4.19.F20.boolean.opBoolean","SPLIT",FACE,{"disambiguationData":[TD([subQ30])],"derivedFrom":makeQuery(id+"F0Hq7nSFAMYVZvY_4.18.F20.boolean.opBoolean","SPLIT",FACE,{"disambiguationData":[TD([subQ30])],"derivedFrom":makeQuery(id+"F0Hq7nSFAMYVZvY_4.17.F20.boolean.opBoolean","SPLIT",FACE,{"disambiguationData":[TD([subQ30])],"derivedFrom":makeQuery(id+"F0Hq7nSFAMYVZvY_4.16.F20.boolean.opBoolean","SPLIT",FACE,{"disambiguationData":[TD([subQ30])],"derivedFrom":makeQuery(id+"F0Hq7nSFAMYVZvY_4.15.F20.boolean.opBoolean","SPLIT",FACE,{"disambiguationData":[TD([subQ30])],"derivedFrom":makeQuery(id+"F0Hq7nSFAMYVZvY_4.14.F20.boolean.opBoolean","SPLIT",FACE,{"disambiguationData":[TD([subQ30])],"derivedFrom":makeQuery(id+"F0Hq7nSFAMYVZvY_4.13.F20.boolean.opBoolean","SPLIT",FACE,{"disambiguationData":[TD([subQ30])],"derivedFrom":makeQuery(id+"F0Hq7nSFAMYVZvY_4.12.F20.boolean.opBoolean","SPLIT",FACE,{"disambiguationData":[TD([subQ30])],"derivedFrom":makeQuery(id+"F0Hq7nSFAMYVZvY_4.11.F20.boolean.opBoolean","SPLIT",FACE,{"disambiguationData":[TD([subQ30])],"derivedFrom":makeQuery(id+"F0Hq7nSFAMYVZvY_4.10.F20.boolean.opBoolean","SPLIT",FACE,{"disambiguationData":[TD([subQ30])],"derivedFrom":makeQuery(id+"F0Hq7nSFAMYVZvY_4.9.F20.boolean.opBoolean","SPLIT",FACE,{"disambiguationData":[TD([subQ30])],"derivedFrom":makeQuery(id+"F0Hq7nSFAMYVZvY_4.8.F20.boolean.opBoolean","SPLIT",FACE,{"disambiguationData":[TD([subQ30])],"derivedFrom":makeQuery(id+"F0Hq7nSFAMYVZvY_4.7.F20.boolean.opBoolean","SPLIT",FACE,{"disambiguationData":[TD([subQ30])],"derivedFrom":makeQuery(id+"F0Hq7nSFAMYVZvY_4.6.F20.boolean.opBoolean","SPLIT",FACE,{"disambiguationData":[TD([subQ30])],"derivedFrom":makeQuery(id+"F0Hq7nSFAMYVZvY_4.5.F20.boolean.opBoolean","SPLIT",FACE,{"disambiguationData":[TD([subQ30])],"derivedFrom":makeQuery(id+"F0Hq7nSFAMYVZvY_4.4.F20.boolean.opBoolean","SPLIT",FACE,{"disambiguationData":[TD([subQ30])],"derivedFrom":makeQuery(id+"F0Hq7nSFAMYVZvY_4.3.F20.boolean.opBoolean","SPLIT",FACE,{"disambiguationData":[TD([subQ30])],"derivedFrom":makeQuery(id+"F0Hq7nSFAMYVZvY_4.2.F20.boolean.opBoolean","SPLIT",FACE,{"disambiguationData":[TD([subQ30])],"derivedFrom":makeQuery(id+"F0Hq7nSFAMYVZvY_4.1.F20.boolean.opBoolean","SPLIT",FACE,{"disambiguationData":[TD([subQ30])],"derivedFrom":makeQuery(id+"F17.boolean.opBoolean","COPY",FACE,{"derivedFrom":makeQuery(id+"F17.opExtrude","SWEPT_FACE",FACE,{"disambiguationData":[OSD([subQ3])]})})})})})})})})})})})})})})})})})})})})})})})})});}
            var Q79;
            {var subQ0=sQuery(id+"F16.wireOp",EDGE,"E151");var subQ3=sQuery(id+"F19.wireOp",EDGE,"E157");var subQ4=sQuery(id+"F19.wireOp",EDGE,"E158.MirrorCS");var subQ5=makeQuery(id+"F0Hq7nSFAMYVZvY_4.22.F20.opExtrude","SWEPT_FACE",FACE,{"disambiguationData":[OSD([subQ4])]});var subQ6=makeQuery(id+"F20.opExtrude","SWEPT_FACE",FACE,{"disambiguationData":[OSD([subQ3])]});Q79=makeQuery(id+"F0Hq7nSFAMYVZvY_4.23.F20.boolean.opBoolean","SPLIT",EDGE,{"disambiguationData":[TD([subQ5])],"derivedFrom":makeQuery(id+"F0Hq7nSFAMYVZvY_4.22.F20.boolean.opBoolean","SPLIT",EDGE,{"disambiguationData":[TD([subQ6])],"derivedFrom":makeQuery(id+"F0Hq7nSFAMYVZvY_4.21.F20.boolean.opBoolean","SPLIT",EDGE,{"disambiguationData":[TD([subQ6])],"derivedFrom":makeQuery(id+"F0Hq7nSFAMYVZvY_4.20.F20.boolean.opBoolean","SPLIT",EDGE,{"disambiguationData":[TD([subQ6])],"derivedFrom":makeQuery(id+"F0Hq7nSFAMYVZvY_4.19.F20.boolean.opBoolean","SPLIT",EDGE,{"disambiguationData":[TD([subQ6])],"derivedFrom":makeQuery(id+"F0Hq7nSFAMYVZvY_4.18.F20.boolean.opBoolean","SPLIT",EDGE,{"disambiguationData":[TD([subQ6])],"derivedFrom":makeQuery(id+"F0Hq7nSFAMYVZvY_4.17.F20.boolean.opBoolean","SPLIT",EDGE,{"disambiguationData":[TD([subQ6])],"derivedFrom":makeQuery(id+"F0Hq7nSFAMYVZvY_4.16.F20.boolean.opBoolean","SPLIT",EDGE,{"disambiguationData":[TD([subQ6])],"derivedFrom":makeQuery(id+"F0Hq7nSFAMYVZvY_4.15.F20.boolean.opBoolean","SPLIT",EDGE,{"disambiguationData":[TD([subQ6])],"derivedFrom":makeQuery(id+"F0Hq7nSFAMYVZvY_4.14.F20.boolean.opBoolean","SPLIT",EDGE,{"disambiguationData":[TD([subQ6])],"derivedFrom":makeQuery(id+"F0Hq7nSFAMYVZvY_4.13.F20.boolean.opBoolean","SPLIT",EDGE,{"disambiguationData":[TD([subQ6])],"derivedFrom":makeQuery(id+"F0Hq7nSFAMYVZvY_4.12.F20.boolean.opBoolean","SPLIT",EDGE,{"disambiguationData":[TD([subQ6])],"derivedFrom":makeQuery(id+"F0Hq7nSFAMYVZvY_4.11.F20.boolean.opBoolean","SPLIT",EDGE,{"disambiguationData":[TD([subQ6])],"derivedFrom":makeQuery(id+"F0Hq7nSFAMYVZvY_4.10.F20.boolean.opBoolean","SPLIT",EDGE,{"disambiguationData":[TD([subQ6])],"derivedFrom":makeQuery(id+"F0Hq7nSFAMYVZvY_4.9.F20.boolean.opBoolean","SPLIT",EDGE,{"disambiguationData":[TD([subQ6])],"derivedFrom":makeQuery(id+"F0Hq7nSFAMYVZvY_4.8.F20.boolean.opBoolean","SPLIT",EDGE,{"disambiguationData":[TD([subQ6])],"derivedFrom":makeQuery(id+"F0Hq7nSFAMYVZvY_4.7.F20.boolean.opBoolean","SPLIT",EDGE,{"disambiguationData":[TD([subQ6])],"derivedFrom":makeQuery(id+"F0Hq7nSFAMYVZvY_4.6.F20.boolean.opBoolean","SPLIT",EDGE,{"disambiguationData":[TD([subQ6])],"derivedFrom":makeQuery(id+"F0Hq7nSFAMYVZvY_4.5.F20.boolean.opBoolean","SPLIT",EDGE,{"disambiguationData":[TD([subQ6])],"derivedFrom":makeQuery(id+"F0Hq7nSFAMYVZvY_4.4.F20.boolean.opBoolean","SPLIT",EDGE,{"disambiguationData":[TD([subQ6])],"derivedFrom":makeQuery(id+"F0Hq7nSFAMYVZvY_4.3.F20.boolean.opBoolean","SPLIT",EDGE,{"disambiguationData":[TD([subQ6])],"derivedFrom":makeQuery(id+"F0Hq7nSFAMYVZvY_4.2.F20.boolean.opBoolean","SPLIT",EDGE,{"disambiguationData":[TD([subQ6])],"derivedFrom":makeQuery(id+"F0Hq7nSFAMYVZvY_4.1.F20.boolean.opBoolean","SPLIT",EDGE,{"disambiguationData":[TD([subQ6])],"derivedFrom":makeQuery(id+"F17.boolean.opBoolean","COPY",EDGE,{"derivedFrom":makeQuery(id+"F17.opExtrude","CAP_EDGE",EDGE,{"disambiguationData":[OSD([subQ0])],"isStart":false})})})})})})})})})})})})})})})})})})})})})})})})});}
            var Q80;
            Q80=makeQuery(id+"F0Hq7nSFAMYVZvY_4.24.F20.opExtrude","SWEPT_FACE",FACE,{"disambiguationData":[OSD([sQuery(id+"F19.wireOp",EDGE,"E157")])]});
            var Q81;
            Q81=makeQuery(id+"F0Hq7nSFAMYVZvY_4.24.F20.opExtrude","SWEPT_FACE",FACE,{"disambiguationData":[OSD([sQuery(id+"F19.wireOp",EDGE,"E158.MirrorCS")])]});
            var Q82;
            Q82=makeQuery(id+"F0Hq7nSFAMYVZvY_4.24.F20.opExtrude","CAP_EDGE",EDGE,{"disambiguationData":[OSD([sQuery(id+"F19.wireOp",EDGE,"E157")])],"isStart":false});
            var Q83;
            Q83=makeQuery(id+"F0Hq7nSFAMYVZvY_4.24.F20.opExtrude","CAP_EDGE",EDGE,{"disambiguationData":[OSD([sQuery(id+"F19.wireOp",EDGE,"E158.MirrorCS")])],"isStart":false});
            var Q84;
            {var subQ0=sQuery(id+"F16.wireOp",EDGE,"E151");var subQ2=sQuery(id+"F16.wireOp",EDGE,"E152");var subQ4=sQuery(id+"F19.wireOp",EDGE,"E158.MirrorCS");var subQ5=makeQuery(id+"F0Hq7nSFAMYVZvY_4.23.F20.opExtrude","SWEPT_FACE",FACE,{"disambiguationData":[OSD([subQ4])]});var subQ6=sQuery(id+"F19.wireOp",EDGE,"E157");var subQ7=makeQuery(id+"F20.opExtrude","SWEPT_FACE",FACE,{"disambiguationData":[OSD([subQ6])]});Q84=makeQuery(id+"F0Hq7nSFAMYVZvY_4.24.F20.boolean.opBoolean","SPLIT",FACE,{"disambiguationData":[TD([subQ5])],"derivedFrom":makeQuery(id+"F0Hq7nSFAMYVZvY_4.23.F20.boolean.opBoolean","SPLIT",FACE,{"disambiguationData":[TD([subQ7])],"derivedFrom":makeQuery(id+"F0Hq7nSFAMYVZvY_4.22.F20.boolean.opBoolean","SPLIT",FACE,{"disambiguationData":[TD([subQ7])],"derivedFrom":makeQuery(id+"F0Hq7nSFAMYVZvY_4.21.F20.boolean.opBoolean","SPLIT",FACE,{"disambiguationData":[TD([subQ7])],"derivedFrom":makeQuery(id+"F0Hq7nSFAMYVZvY_4.20.F20.boolean.opBoolean","SPLIT",FACE,{"disambiguationData":[TD([subQ7])],"derivedFrom":makeQuery(id+"F0Hq7nSFAMYVZvY_4.19.F20.boolean.opBoolean","SPLIT",FACE,{"disambiguationData":[TD([subQ7])],"derivedFrom":makeQuery(id+"F0Hq7nSFAMYVZvY_4.18.F20.boolean.opBoolean","SPLIT",FACE,{"disambiguationData":[TD([subQ7])],"derivedFrom":makeQuery(id+"F0Hq7nSFAMYVZvY_4.17.F20.boolean.opBoolean","SPLIT",FACE,{"disambiguationData":[TD([subQ7])],"derivedFrom":makeQuery(id+"F0Hq7nSFAMYVZvY_4.16.F20.boolean.opBoolean","SPLIT",FACE,{"disambiguationData":[TD([subQ7])],"derivedFrom":makeQuery(id+"F0Hq7nSFAMYVZvY_4.15.F20.boolean.opBoolean","SPLIT",FACE,{"disambiguationData":[TD([subQ7])],"derivedFrom":makeQuery(id+"F0Hq7nSFAMYVZvY_4.14.F20.boolean.opBoolean","SPLIT",FACE,{"disambiguationData":[TD([subQ7])],"derivedFrom":makeQuery(id+"F0Hq7nSFAMYVZvY_4.13.F20.boolean.opBoolean","SPLIT",FACE,{"disambiguationData":[TD([subQ7])],"derivedFrom":makeQuery(id+"F0Hq7nSFAMYVZvY_4.12.F20.boolean.opBoolean","SPLIT",FACE,{"disambiguationData":[TD([subQ7])],"derivedFrom":makeQuery(id+"F0Hq7nSFAMYVZvY_4.11.F20.boolean.opBoolean","SPLIT",FACE,{"disambiguationData":[TD([subQ7])],"derivedFrom":makeQuery(id+"F0Hq7nSFAMYVZvY_4.10.F20.boolean.opBoolean","SPLIT",FACE,{"disambiguationData":[TD([subQ7])],"derivedFrom":makeQuery(id+"F0Hq7nSFAMYVZvY_4.9.F20.boolean.opBoolean","SPLIT",FACE,{"disambiguationData":[TD([subQ7])],"derivedFrom":makeQuery(id+"F0Hq7nSFAMYVZvY_4.8.F20.boolean.opBoolean","SPLIT",FACE,{"disambiguationData":[TD([subQ7])],"derivedFrom":makeQuery(id+"F0Hq7nSFAMYVZvY_4.7.F20.boolean.opBoolean","SPLIT",FACE,{"disambiguationData":[TD([subQ7])],"derivedFrom":makeQuery(id+"F0Hq7nSFAMYVZvY_4.6.F20.boolean.opBoolean","SPLIT",FACE,{"disambiguationData":[TD([subQ7])],"derivedFrom":makeQuery(id+"F0Hq7nSFAMYVZvY_4.5.F20.boolean.opBoolean","SPLIT",FACE,{"disambiguationData":[TD([subQ7])],"derivedFrom":makeQuery(id+"F0Hq7nSFAMYVZvY_4.4.F20.boolean.opBoolean","SPLIT",FACE,{"disambiguationData":[TD([subQ7])],"derivedFrom":makeQuery(id+"F0Hq7nSFAMYVZvY_4.3.F20.boolean.opBoolean","SPLIT",FACE,{"disambiguationData":[TD([subQ7])],"derivedFrom":makeQuery(id+"F0Hq7nSFAMYVZvY_4.2.F20.boolean.opBoolean","SPLIT",FACE,{"disambiguationData":[TD([subQ7])],"derivedFrom":makeQuery(id+"F0Hq7nSFAMYVZvY_4.1.F20.boolean.opBoolean","SPLIT",FACE,{"disambiguationData":[TD([subQ7])],"derivedFrom":makeQuery(id+"F17.boolean.opBoolean","COPY",FACE,{"derivedFrom":makeQuery(id+"F17.opExtrude","CAP_FACE",FACE,{"disambiguationData":[OSD([subQ0,subQ2])],"isStart":false})})})})})})})})})})})})})})})})})})})})})})})})})});}
            var Q85;
            Q85=makeQuery(id+"F0Hq7nSFAMYVZvY_4.24.F20.opExtrude","CAP_EDGE",EDGE,{"disambiguationData":[OSD([sQuery(id+"F19.wireOp",EDGE,"E157")])],"isStart":true});
            var Q86;
            {var subQ0=sQuery(id+"F19.wireOp",EDGE,"E158.MirrorCS");var subQ1=sQuery(id+"F19.wireOp",EDGE,"E157");var subQ3=sQuery(id+"F16.wireOp",EDGE,"E151");var subQ30=makeQuery(id+"F0Hq7nSFAMYVZvY_4.23.F20.opExtrude","SWEPT_FACE",FACE,{"disambiguationData":[OSD([subQ0])]});var subQ31=makeQuery(id+"F20.opExtrude","SWEPT_FACE",FACE,{"disambiguationData":[OSD([subQ1])]});Q86=makeQuery(id+"F0Hq7nSFAMYVZvY_4.24.F20.boolean.opBoolean","SPLIT",FACE,{"disambiguationData":[TD([subQ30])],"derivedFrom":makeQuery(id+"F0Hq7nSFAMYVZvY_4.23.F20.boolean.opBoolean","SPLIT",FACE,{"disambiguationData":[TD([subQ31])],"derivedFrom":makeQuery(id+"F0Hq7nSFAMYVZvY_4.22.F20.boolean.opBoolean","SPLIT",FACE,{"disambiguationData":[TD([subQ31])],"derivedFrom":makeQuery(id+"F0Hq7nSFAMYVZvY_4.21.F20.boolean.opBoolean","SPLIT",FACE,{"disambiguationData":[TD([subQ31])],"derivedFrom":makeQuery(id+"F0Hq7nSFAMYVZvY_4.20.F20.boolean.opBoolean","SPLIT",FACE,{"disambiguationData":[TD([subQ31])],"derivedFrom":makeQuery(id+"F0Hq7nSFAMYVZvY_4.19.F20.boolean.opBoolean","SPLIT",FACE,{"disambiguationData":[TD([subQ31])],"derivedFrom":makeQuery(id+"F0Hq7nSFAMYVZvY_4.18.F20.boolean.opBoolean","SPLIT",FACE,{"disambiguationData":[TD([subQ31])],"derivedFrom":makeQuery(id+"F0Hq7nSFAMYVZvY_4.17.F20.boolean.opBoolean","SPLIT",FACE,{"disambiguationData":[TD([subQ31])],"derivedFrom":makeQuery(id+"F0Hq7nSFAMYVZvY_4.16.F20.boolean.opBoolean","SPLIT",FACE,{"disambiguationData":[TD([subQ31])],"derivedFrom":makeQuery(id+"F0Hq7nSFAMYVZvY_4.15.F20.boolean.opBoolean","SPLIT",FACE,{"disambiguationData":[TD([subQ31])],"derivedFrom":makeQuery(id+"F0Hq7nSFAMYVZvY_4.14.F20.boolean.opBoolean","SPLIT",FACE,{"disambiguationData":[TD([subQ31])],"derivedFrom":makeQuery(id+"F0Hq7nSFAMYVZvY_4.13.F20.boolean.opBoolean","SPLIT",FACE,{"disambiguationData":[TD([subQ31])],"derivedFrom":makeQuery(id+"F0Hq7nSFAMYVZvY_4.12.F20.boolean.opBoolean","SPLIT",FACE,{"disambiguationData":[TD([subQ31])],"derivedFrom":makeQuery(id+"F0Hq7nSFAMYVZvY_4.11.F20.boolean.opBoolean","SPLIT",FACE,{"disambiguationData":[TD([subQ31])],"derivedFrom":makeQuery(id+"F0Hq7nSFAMYVZvY_4.10.F20.boolean.opBoolean","SPLIT",FACE,{"disambiguationData":[TD([subQ31])],"derivedFrom":makeQuery(id+"F0Hq7nSFAMYVZvY_4.9.F20.boolean.opBoolean","SPLIT",FACE,{"disambiguationData":[TD([subQ31])],"derivedFrom":makeQuery(id+"F0Hq7nSFAMYVZvY_4.8.F20.boolean.opBoolean","SPLIT",FACE,{"disambiguationData":[TD([subQ31])],"derivedFrom":makeQuery(id+"F0Hq7nSFAMYVZvY_4.7.F20.boolean.opBoolean","SPLIT",FACE,{"disambiguationData":[TD([subQ31])],"derivedFrom":makeQuery(id+"F0Hq7nSFAMYVZvY_4.6.F20.boolean.opBoolean","SPLIT",FACE,{"disambiguationData":[TD([subQ31])],"derivedFrom":makeQuery(id+"F0Hq7nSFAMYVZvY_4.5.F20.boolean.opBoolean","SPLIT",FACE,{"disambiguationData":[TD([subQ31])],"derivedFrom":makeQuery(id+"F0Hq7nSFAMYVZvY_4.4.F20.boolean.opBoolean","SPLIT",FACE,{"disambiguationData":[TD([subQ31])],"derivedFrom":makeQuery(id+"F0Hq7nSFAMYVZvY_4.3.F20.boolean.opBoolean","SPLIT",FACE,{"disambiguationData":[TD([subQ31])],"derivedFrom":makeQuery(id+"F0Hq7nSFAMYVZvY_4.2.F20.boolean.opBoolean","SPLIT",FACE,{"disambiguationData":[TD([subQ31])],"derivedFrom":makeQuery(id+"F0Hq7nSFAMYVZvY_4.1.F20.boolean.opBoolean","SPLIT",FACE,{"disambiguationData":[TD([subQ31])],"derivedFrom":makeQuery(id+"F17.boolean.opBoolean","COPY",FACE,{"derivedFrom":makeQuery(id+"F17.opExtrude","SWEPT_FACE",FACE,{"disambiguationData":[OSD([subQ3])]})})})})})})})})})})})})})})})})})})})})})})})})})});}
            var Q87;
            {var subQ0=sQuery(id+"F16.wireOp",EDGE,"E151");var subQ3=sQuery(id+"F19.wireOp",EDGE,"E158.MirrorCS");var subQ4=makeQuery(id+"F0Hq7nSFAMYVZvY_4.23.F20.opExtrude","SWEPT_FACE",FACE,{"disambiguationData":[OSD([subQ3])]});var subQ5=sQuery(id+"F19.wireOp",EDGE,"E157");var subQ6=makeQuery(id+"F20.opExtrude","SWEPT_FACE",FACE,{"disambiguationData":[OSD([subQ5])]});Q87=makeQuery(id+"F0Hq7nSFAMYVZvY_4.24.F20.boolean.opBoolean","SPLIT",EDGE,{"disambiguationData":[TD([subQ4])],"derivedFrom":makeQuery(id+"F0Hq7nSFAMYVZvY_4.23.F20.boolean.opBoolean","SPLIT",EDGE,{"disambiguationData":[TD([subQ6])],"derivedFrom":makeQuery(id+"F0Hq7nSFAMYVZvY_4.22.F20.boolean.opBoolean","SPLIT",EDGE,{"disambiguationData":[TD([subQ6])],"derivedFrom":makeQuery(id+"F0Hq7nSFAMYVZvY_4.21.F20.boolean.opBoolean","SPLIT",EDGE,{"disambiguationData":[TD([subQ6])],"derivedFrom":makeQuery(id+"F0Hq7nSFAMYVZvY_4.20.F20.boolean.opBoolean","SPLIT",EDGE,{"disambiguationData":[TD([subQ6])],"derivedFrom":makeQuery(id+"F0Hq7nSFAMYVZvY_4.19.F20.boolean.opBoolean","SPLIT",EDGE,{"disambiguationData":[TD([subQ6])],"derivedFrom":makeQuery(id+"F0Hq7nSFAMYVZvY_4.18.F20.boolean.opBoolean","SPLIT",EDGE,{"disambiguationData":[TD([subQ6])],"derivedFrom":makeQuery(id+"F0Hq7nSFAMYVZvY_4.17.F20.boolean.opBoolean","SPLIT",EDGE,{"disambiguationData":[TD([subQ6])],"derivedFrom":makeQuery(id+"F0Hq7nSFAMYVZvY_4.16.F20.boolean.opBoolean","SPLIT",EDGE,{"disambiguationData":[TD([subQ6])],"derivedFrom":makeQuery(id+"F0Hq7nSFAMYVZvY_4.15.F20.boolean.opBoolean","SPLIT",EDGE,{"disambiguationData":[TD([subQ6])],"derivedFrom":makeQuery(id+"F0Hq7nSFAMYVZvY_4.14.F20.boolean.opBoolean","SPLIT",EDGE,{"disambiguationData":[TD([subQ6])],"derivedFrom":makeQuery(id+"F0Hq7nSFAMYVZvY_4.13.F20.boolean.opBoolean","SPLIT",EDGE,{"disambiguationData":[TD([subQ6])],"derivedFrom":makeQuery(id+"F0Hq7nSFAMYVZvY_4.12.F20.boolean.opBoolean","SPLIT",EDGE,{"disambiguationData":[TD([subQ6])],"derivedFrom":makeQuery(id+"F0Hq7nSFAMYVZvY_4.11.F20.boolean.opBoolean","SPLIT",EDGE,{"disambiguationData":[TD([subQ6])],"derivedFrom":makeQuery(id+"F0Hq7nSFAMYVZvY_4.10.F20.boolean.opBoolean","SPLIT",EDGE,{"disambiguationData":[TD([subQ6])],"derivedFrom":makeQuery(id+"F0Hq7nSFAMYVZvY_4.9.F20.boolean.opBoolean","SPLIT",EDGE,{"disambiguationData":[TD([subQ6])],"derivedFrom":makeQuery(id+"F0Hq7nSFAMYVZvY_4.8.F20.boolean.opBoolean","SPLIT",EDGE,{"disambiguationData":[TD([subQ6])],"derivedFrom":makeQuery(id+"F0Hq7nSFAMYVZvY_4.7.F20.boolean.opBoolean","SPLIT",EDGE,{"disambiguationData":[TD([subQ6])],"derivedFrom":makeQuery(id+"F0Hq7nSFAMYVZvY_4.6.F20.boolean.opBoolean","SPLIT",EDGE,{"disambiguationData":[TD([subQ6])],"derivedFrom":makeQuery(id+"F0Hq7nSFAMYVZvY_4.5.F20.boolean.opBoolean","SPLIT",EDGE,{"disambiguationData":[TD([subQ6])],"derivedFrom":makeQuery(id+"F0Hq7nSFAMYVZvY_4.4.F20.boolean.opBoolean","SPLIT",EDGE,{"disambiguationData":[TD([subQ6])],"derivedFrom":makeQuery(id+"F0Hq7nSFAMYVZvY_4.3.F20.boolean.opBoolean","SPLIT",EDGE,{"disambiguationData":[TD([subQ6])],"derivedFrom":makeQuery(id+"F0Hq7nSFAMYVZvY_4.2.F20.boolean.opBoolean","SPLIT",EDGE,{"disambiguationData":[TD([subQ6])],"derivedFrom":makeQuery(id+"F0Hq7nSFAMYVZvY_4.1.F20.boolean.opBoolean","SPLIT",EDGE,{"disambiguationData":[TD([subQ6])],"derivedFrom":makeQuery(id+"F17.boolean.opBoolean","COPY",EDGE,{"derivedFrom":makeQuery(id+"F17.opExtrude","CAP_EDGE",EDGE,{"disambiguationData":[OSD([subQ0])],"isStart":false})})})})})})})})})})})})})})})})})})})})})})})})})});}
            var Q88;
            {var subQ0=sQuery(id+"F19.wireOp",EDGE,"E158.MirrorCS");var subQ1=sQuery(id+"F19.wireOp",EDGE,"E157");var subQ3=sQuery(id+"F16.wireOp",EDGE,"E151");var subQ30=makeQuery(id+"F0Hq7nSFAMYVZvY_4.23.F20.opExtrude","SWEPT_FACE",FACE,{"disambiguationData":[OSD([subQ0])]});var subQ31=makeQuery(id+"F20.opExtrude","SWEPT_FACE",FACE,{"disambiguationData":[OSD([subQ1])]});Q88=makeQuery(id+"F0Hq7nSFAMYVZvY_4.24.F20.boolean.opBoolean","SPLIT",EDGE,{"disambiguationData":[TD([subQ30])],"derivedFrom":makeQuery(id+"F0Hq7nSFAMYVZvY_4.23.F20.boolean.opBoolean","SPLIT",EDGE,{"disambiguationData":[TD([subQ31])],"derivedFrom":makeQuery(id+"F0Hq7nSFAMYVZvY_4.22.F20.boolean.opBoolean","SPLIT",EDGE,{"disambiguationData":[TD([subQ31])],"derivedFrom":makeQuery(id+"F0Hq7nSFAMYVZvY_4.21.F20.boolean.opBoolean","SPLIT",EDGE,{"disambiguationData":[TD([subQ31])],"derivedFrom":makeQuery(id+"F0Hq7nSFAMYVZvY_4.20.F20.boolean.opBoolean","SPLIT",EDGE,{"disambiguationData":[TD([subQ31])],"derivedFrom":makeQuery(id+"F0Hq7nSFAMYVZvY_4.19.F20.boolean.opBoolean","SPLIT",EDGE,{"disambiguationData":[TD([subQ31])],"derivedFrom":makeQuery(id+"F0Hq7nSFAMYVZvY_4.18.F20.boolean.opBoolean","SPLIT",EDGE,{"disambiguationData":[TD([subQ31])],"derivedFrom":makeQuery(id+"F0Hq7nSFAMYVZvY_4.17.F20.boolean.opBoolean","SPLIT",EDGE,{"disambiguationData":[TD([subQ31])],"derivedFrom":makeQuery(id+"F0Hq7nSFAMYVZvY_4.16.F20.boolean.opBoolean","SPLIT",EDGE,{"disambiguationData":[TD([subQ31])],"derivedFrom":makeQuery(id+"F0Hq7nSFAMYVZvY_4.15.F20.boolean.opBoolean","SPLIT",EDGE,{"disambiguationData":[TD([subQ31])],"derivedFrom":makeQuery(id+"F0Hq7nSFAMYVZvY_4.14.F20.boolean.opBoolean","SPLIT",EDGE,{"disambiguationData":[TD([subQ31])],"derivedFrom":makeQuery(id+"F0Hq7nSFAMYVZvY_4.13.F20.boolean.opBoolean","SPLIT",EDGE,{"disambiguationData":[TD([subQ31])],"derivedFrom":makeQuery(id+"F0Hq7nSFAMYVZvY_4.12.F20.boolean.opBoolean","SPLIT",EDGE,{"disambiguationData":[TD([subQ31])],"derivedFrom":makeQuery(id+"F0Hq7nSFAMYVZvY_4.11.F20.boolean.opBoolean","SPLIT",EDGE,{"disambiguationData":[TD([subQ31])],"derivedFrom":makeQuery(id+"F0Hq7nSFAMYVZvY_4.10.F20.boolean.opBoolean","SPLIT",EDGE,{"disambiguationData":[TD([subQ31])],"derivedFrom":makeQuery(id+"F0Hq7nSFAMYVZvY_4.9.F20.boolean.opBoolean","SPLIT",EDGE,{"disambiguationData":[TD([subQ31])],"derivedFrom":makeQuery(id+"F0Hq7nSFAMYVZvY_4.8.F20.boolean.opBoolean","SPLIT",EDGE,{"disambiguationData":[TD([subQ31])],"derivedFrom":makeQuery(id+"F0Hq7nSFAMYVZvY_4.7.F20.boolean.opBoolean","SPLIT",EDGE,{"disambiguationData":[TD([subQ31])],"derivedFrom":makeQuery(id+"F0Hq7nSFAMYVZvY_4.6.F20.boolean.opBoolean","SPLIT",EDGE,{"disambiguationData":[TD([subQ31])],"derivedFrom":makeQuery(id+"F0Hq7nSFAMYVZvY_4.5.F20.boolean.opBoolean","SPLIT",EDGE,{"disambiguationData":[TD([subQ31])],"derivedFrom":makeQuery(id+"F0Hq7nSFAMYVZvY_4.4.F20.boolean.opBoolean","SPLIT",EDGE,{"disambiguationData":[TD([subQ31])],"derivedFrom":makeQuery(id+"F0Hq7nSFAMYVZvY_4.3.F20.boolean.opBoolean","SPLIT",EDGE,{"disambiguationData":[TD([subQ31])],"derivedFrom":makeQuery(id+"F0Hq7nSFAMYVZvY_4.2.F20.boolean.opBoolean","SPLIT",EDGE,{"disambiguationData":[TD([subQ31])],"derivedFrom":makeQuery(id+"F0Hq7nSFAMYVZvY_4.1.F20.boolean.opBoolean","SPLIT",EDGE,{"disambiguationData":[TD([subQ31])],"derivedFrom":makeQuery(id+"F18.boolean.opBoolean","COPY",EDGE,{"derivedFrom":makeQuery(id+"F18.opExtrude","CAP_EDGE",EDGE,{"disambiguationData":[OSD([subQ3])],"isStart":false})})})})})})})})})})})})})})})})})})})})})})})})})});}
            var Q89;
            Q89=makeQuery(id+"F0Hq7nSFAMYVZvY_4.25.F20.opExtrude","SWEPT_FACE",FACE,{"disambiguationData":[OSD([sQuery(id+"F19.wireOp",EDGE,"E157")])]});
            var Q90;
            Q90=makeQuery(id+"F0Hq7nSFAMYVZvY_4.25.F20.opExtrude","CAP_EDGE",EDGE,{"disambiguationData":[OSD([sQuery(id+"F19.wireOp",EDGE,"E157")])],"isStart":false});
            var Q91;
            Q91=makeQuery(id+"F0Hq7nSFAMYVZvY_4.25.F20.opExtrude","CAP_EDGE",EDGE,{"disambiguationData":[OSD([sQuery(id+"F19.wireOp",EDGE,"E158.MirrorCS")])],"isStart":false});
            var Q92;
            {var subQ0=sQuery(id+"F16.wireOp",EDGE,"E151");var subQ2=sQuery(id+"F19.wireOp",EDGE,"E157");var subQ3=sQuery(id+"F16.wireOp",EDGE,"E152");var subQ5=sQuery(id+"F19.wireOp",EDGE,"E158.MirrorCS");var subQ6=makeQuery(id+"F0Hq7nSFAMYVZvY_4.24.F20.opExtrude","SWEPT_FACE",FACE,{"disambiguationData":[OSD([subQ5])]});var subQ7=makeQuery(id+"F20.opExtrude","SWEPT_FACE",FACE,{"disambiguationData":[OSD([subQ2])]});Q92=makeQuery(id+"F0Hq7nSFAMYVZvY_4.25.F20.boolean.opBoolean","SPLIT",FACE,{"disambiguationData":[TD([subQ6])],"derivedFrom":makeQuery(id+"F0Hq7nSFAMYVZvY_4.24.F20.boolean.opBoolean","SPLIT",FACE,{"disambiguationData":[TD([subQ7])],"derivedFrom":makeQuery(id+"F0Hq7nSFAMYVZvY_4.23.F20.boolean.opBoolean","SPLIT",FACE,{"disambiguationData":[TD([subQ7])],"derivedFrom":makeQuery(id+"F0Hq7nSFAMYVZvY_4.22.F20.boolean.opBoolean","SPLIT",FACE,{"disambiguationData":[TD([subQ7])],"derivedFrom":makeQuery(id+"F0Hq7nSFAMYVZvY_4.21.F20.boolean.opBoolean","SPLIT",FACE,{"disambiguationData":[TD([subQ7])],"derivedFrom":makeQuery(id+"F0Hq7nSFAMYVZvY_4.20.F20.boolean.opBoolean","SPLIT",FACE,{"disambiguationData":[TD([subQ7])],"derivedFrom":makeQuery(id+"F0Hq7nSFAMYVZvY_4.19.F20.boolean.opBoolean","SPLIT",FACE,{"disambiguationData":[TD([subQ7])],"derivedFrom":makeQuery(id+"F0Hq7nSFAMYVZvY_4.18.F20.boolean.opBoolean","SPLIT",FACE,{"disambiguationData":[TD([subQ7])],"derivedFrom":makeQuery(id+"F0Hq7nSFAMYVZvY_4.17.F20.boolean.opBoolean","SPLIT",FACE,{"disambiguationData":[TD([subQ7])],"derivedFrom":makeQuery(id+"F0Hq7nSFAMYVZvY_4.16.F20.boolean.opBoolean","SPLIT",FACE,{"disambiguationData":[TD([subQ7])],"derivedFrom":makeQuery(id+"F0Hq7nSFAMYVZvY_4.15.F20.boolean.opBoolean","SPLIT",FACE,{"disambiguationData":[TD([subQ7])],"derivedFrom":makeQuery(id+"F0Hq7nSFAMYVZvY_4.14.F20.boolean.opBoolean","SPLIT",FACE,{"disambiguationData":[TD([subQ7])],"derivedFrom":makeQuery(id+"F0Hq7nSFAMYVZvY_4.13.F20.boolean.opBoolean","SPLIT",FACE,{"disambiguationData":[TD([subQ7])],"derivedFrom":makeQuery(id+"F0Hq7nSFAMYVZvY_4.12.F20.boolean.opBoolean","SPLIT",FACE,{"disambiguationData":[TD([subQ7])],"derivedFrom":makeQuery(id+"F0Hq7nSFAMYVZvY_4.11.F20.boolean.opBoolean","SPLIT",FACE,{"disambiguationData":[TD([subQ7])],"derivedFrom":makeQuery(id+"F0Hq7nSFAMYVZvY_4.10.F20.boolean.opBoolean","SPLIT",FACE,{"disambiguationData":[TD([subQ7])],"derivedFrom":makeQuery(id+"F0Hq7nSFAMYVZvY_4.9.F20.boolean.opBoolean","SPLIT",FACE,{"disambiguationData":[TD([subQ7])],"derivedFrom":makeQuery(id+"F0Hq7nSFAMYVZvY_4.8.F20.boolean.opBoolean","SPLIT",FACE,{"disambiguationData":[TD([subQ7])],"derivedFrom":makeQuery(id+"F0Hq7nSFAMYVZvY_4.7.F20.boolean.opBoolean","SPLIT",FACE,{"disambiguationData":[TD([subQ7])],"derivedFrom":makeQuery(id+"F0Hq7nSFAMYVZvY_4.6.F20.boolean.opBoolean","SPLIT",FACE,{"disambiguationData":[TD([subQ7])],"derivedFrom":makeQuery(id+"F0Hq7nSFAMYVZvY_4.5.F20.boolean.opBoolean","SPLIT",FACE,{"disambiguationData":[TD([subQ7])],"derivedFrom":makeQuery(id+"F0Hq7nSFAMYVZvY_4.4.F20.boolean.opBoolean","SPLIT",FACE,{"disambiguationData":[TD([subQ7])],"derivedFrom":makeQuery(id+"F0Hq7nSFAMYVZvY_4.3.F20.boolean.opBoolean","SPLIT",FACE,{"disambiguationData":[TD([subQ7])],"derivedFrom":makeQuery(id+"F0Hq7nSFAMYVZvY_4.2.F20.boolean.opBoolean","SPLIT",FACE,{"disambiguationData":[TD([subQ7])],"derivedFrom":makeQuery(id+"F0Hq7nSFAMYVZvY_4.1.F20.boolean.opBoolean","SPLIT",FACE,{"disambiguationData":[TD([subQ7])],"derivedFrom":makeQuery(id+"F17.boolean.opBoolean","COPY",FACE,{"derivedFrom":makeQuery(id+"F17.opExtrude","CAP_FACE",FACE,{"disambiguationData":[OSD([subQ0,subQ3])],"isStart":false})})})})})})})})})})})})})})})})})})})})})})})})})})});}
            var Q93;
            Q93=makeQuery(id+"F0Hq7nSFAMYVZvY_4.25.F20.opExtrude","CAP_EDGE",EDGE,{"disambiguationData":[OSD([sQuery(id+"F19.wireOp",EDGE,"E157")])],"isStart":true});
            var Q94;
            {var subQ0=sQuery(id+"F19.wireOp",EDGE,"E158.MirrorCS");var subQ1=sQuery(id+"F19.wireOp",EDGE,"E157");var subQ3=sQuery(id+"F16.wireOp",EDGE,"E151");var subQ31=makeQuery(id+"F0Hq7nSFAMYVZvY_4.24.F20.opExtrude","SWEPT_FACE",FACE,{"disambiguationData":[OSD([subQ0])]});var subQ32=makeQuery(id+"F20.opExtrude","SWEPT_FACE",FACE,{"disambiguationData":[OSD([subQ1])]});Q94=makeQuery(id+"F0Hq7nSFAMYVZvY_4.25.F20.boolean.opBoolean","SPLIT",FACE,{"disambiguationData":[TD([subQ31])],"derivedFrom":makeQuery(id+"F0Hq7nSFAMYVZvY_4.24.F20.boolean.opBoolean","SPLIT",FACE,{"disambiguationData":[TD([subQ32])],"derivedFrom":makeQuery(id+"F0Hq7nSFAMYVZvY_4.23.F20.boolean.opBoolean","SPLIT",FACE,{"disambiguationData":[TD([subQ32])],"derivedFrom":makeQuery(id+"F0Hq7nSFAMYVZvY_4.22.F20.boolean.opBoolean","SPLIT",FACE,{"disambiguationData":[TD([subQ32])],"derivedFrom":makeQuery(id+"F0Hq7nSFAMYVZvY_4.21.F20.boolean.opBoolean","SPLIT",FACE,{"disambiguationData":[TD([subQ32])],"derivedFrom":makeQuery(id+"F0Hq7nSFAMYVZvY_4.20.F20.boolean.opBoolean","SPLIT",FACE,{"disambiguationData":[TD([subQ32])],"derivedFrom":makeQuery(id+"F0Hq7nSFAMYVZvY_4.19.F20.boolean.opBoolean","SPLIT",FACE,{"disambiguationData":[TD([subQ32])],"derivedFrom":makeQuery(id+"F0Hq7nSFAMYVZvY_4.18.F20.boolean.opBoolean","SPLIT",FACE,{"disambiguationData":[TD([subQ32])],"derivedFrom":makeQuery(id+"F0Hq7nSFAMYVZvY_4.17.F20.boolean.opBoolean","SPLIT",FACE,{"disambiguationData":[TD([subQ32])],"derivedFrom":makeQuery(id+"F0Hq7nSFAMYVZvY_4.16.F20.boolean.opBoolean","SPLIT",FACE,{"disambiguationData":[TD([subQ32])],"derivedFrom":makeQuery(id+"F0Hq7nSFAMYVZvY_4.15.F20.boolean.opBoolean","SPLIT",FACE,{"disambiguationData":[TD([subQ32])],"derivedFrom":makeQuery(id+"F0Hq7nSFAMYVZvY_4.14.F20.boolean.opBoolean","SPLIT",FACE,{"disambiguationData":[TD([subQ32])],"derivedFrom":makeQuery(id+"F0Hq7nSFAMYVZvY_4.13.F20.boolean.opBoolean","SPLIT",FACE,{"disambiguationData":[TD([subQ32])],"derivedFrom":makeQuery(id+"F0Hq7nSFAMYVZvY_4.12.F20.boolean.opBoolean","SPLIT",FACE,{"disambiguationData":[TD([subQ32])],"derivedFrom":makeQuery(id+"F0Hq7nSFAMYVZvY_4.11.F20.boolean.opBoolean","SPLIT",FACE,{"disambiguationData":[TD([subQ32])],"derivedFrom":makeQuery(id+"F0Hq7nSFAMYVZvY_4.10.F20.boolean.opBoolean","SPLIT",FACE,{"disambiguationData":[TD([subQ32])],"derivedFrom":makeQuery(id+"F0Hq7nSFAMYVZvY_4.9.F20.boolean.opBoolean","SPLIT",FACE,{"disambiguationData":[TD([subQ32])],"derivedFrom":makeQuery(id+"F0Hq7nSFAMYVZvY_4.8.F20.boolean.opBoolean","SPLIT",FACE,{"disambiguationData":[TD([subQ32])],"derivedFrom":makeQuery(id+"F0Hq7nSFAMYVZvY_4.7.F20.boolean.opBoolean","SPLIT",FACE,{"disambiguationData":[TD([subQ32])],"derivedFrom":makeQuery(id+"F0Hq7nSFAMYVZvY_4.6.F20.boolean.opBoolean","SPLIT",FACE,{"disambiguationData":[TD([subQ32])],"derivedFrom":makeQuery(id+"F0Hq7nSFAMYVZvY_4.5.F20.boolean.opBoolean","SPLIT",FACE,{"disambiguationData":[TD([subQ32])],"derivedFrom":makeQuery(id+"F0Hq7nSFAMYVZvY_4.4.F20.boolean.opBoolean","SPLIT",FACE,{"disambiguationData":[TD([subQ32])],"derivedFrom":makeQuery(id+"F0Hq7nSFAMYVZvY_4.3.F20.boolean.opBoolean","SPLIT",FACE,{"disambiguationData":[TD([subQ32])],"derivedFrom":makeQuery(id+"F0Hq7nSFAMYVZvY_4.2.F20.boolean.opBoolean","SPLIT",FACE,{"disambiguationData":[TD([subQ32])],"derivedFrom":makeQuery(id+"F0Hq7nSFAMYVZvY_4.1.F20.boolean.opBoolean","SPLIT",FACE,{"disambiguationData":[TD([subQ32])],"derivedFrom":makeQuery(id+"F17.boolean.opBoolean","COPY",FACE,{"derivedFrom":makeQuery(id+"F17.opExtrude","SWEPT_FACE",FACE,{"disambiguationData":[OSD([subQ3])]})})})})})})})})})})})})})})})})})})})})})})})})})})});}
            var Q95;
            {var subQ0=sQuery(id+"F16.wireOp",EDGE,"E151");var subQ2=sQuery(id+"F19.wireOp",EDGE,"E157");var subQ4=sQuery(id+"F19.wireOp",EDGE,"E158.MirrorCS");var subQ5=makeQuery(id+"F0Hq7nSFAMYVZvY_4.24.F20.opExtrude","SWEPT_FACE",FACE,{"disambiguationData":[OSD([subQ4])]});var subQ6=makeQuery(id+"F20.opExtrude","SWEPT_FACE",FACE,{"disambiguationData":[OSD([subQ2])]});Q95=makeQuery(id+"F0Hq7nSFAMYVZvY_4.25.F20.boolean.opBoolean","SPLIT",EDGE,{"disambiguationData":[TD([subQ5])],"derivedFrom":makeQuery(id+"F0Hq7nSFAMYVZvY_4.24.F20.boolean.opBoolean","SPLIT",EDGE,{"disambiguationData":[TD([subQ6])],"derivedFrom":makeQuery(id+"F0Hq7nSFAMYVZvY_4.23.F20.boolean.opBoolean","SPLIT",EDGE,{"disambiguationData":[TD([subQ6])],"derivedFrom":makeQuery(id+"F0Hq7nSFAMYVZvY_4.22.F20.boolean.opBoolean","SPLIT",EDGE,{"disambiguationData":[TD([subQ6])],"derivedFrom":makeQuery(id+"F0Hq7nSFAMYVZvY_4.21.F20.boolean.opBoolean","SPLIT",EDGE,{"disambiguationData":[TD([subQ6])],"derivedFrom":makeQuery(id+"F0Hq7nSFAMYVZvY_4.20.F20.boolean.opBoolean","SPLIT",EDGE,{"disambiguationData":[TD([subQ6])],"derivedFrom":makeQuery(id+"F0Hq7nSFAMYVZvY_4.19.F20.boolean.opBoolean","SPLIT",EDGE,{"disambiguationData":[TD([subQ6])],"derivedFrom":makeQuery(id+"F0Hq7nSFAMYVZvY_4.18.F20.boolean.opBoolean","SPLIT",EDGE,{"disambiguationData":[TD([subQ6])],"derivedFrom":makeQuery(id+"F0Hq7nSFAMYVZvY_4.17.F20.boolean.opBoolean","SPLIT",EDGE,{"disambiguationData":[TD([subQ6])],"derivedFrom":makeQuery(id+"F0Hq7nSFAMYVZvY_4.16.F20.boolean.opBoolean","SPLIT",EDGE,{"disambiguationData":[TD([subQ6])],"derivedFrom":makeQuery(id+"F0Hq7nSFAMYVZvY_4.15.F20.boolean.opBoolean","SPLIT",EDGE,{"disambiguationData":[TD([subQ6])],"derivedFrom":makeQuery(id+"F0Hq7nSFAMYVZvY_4.14.F20.boolean.opBoolean","SPLIT",EDGE,{"disambiguationData":[TD([subQ6])],"derivedFrom":makeQuery(id+"F0Hq7nSFAMYVZvY_4.13.F20.boolean.opBoolean","SPLIT",EDGE,{"disambiguationData":[TD([subQ6])],"derivedFrom":makeQuery(id+"F0Hq7nSFAMYVZvY_4.12.F20.boolean.opBoolean","SPLIT",EDGE,{"disambiguationData":[TD([subQ6])],"derivedFrom":makeQuery(id+"F0Hq7nSFAMYVZvY_4.11.F20.boolean.opBoolean","SPLIT",EDGE,{"disambiguationData":[TD([subQ6])],"derivedFrom":makeQuery(id+"F0Hq7nSFAMYVZvY_4.10.F20.boolean.opBoolean","SPLIT",EDGE,{"disambiguationData":[TD([subQ6])],"derivedFrom":makeQuery(id+"F0Hq7nSFAMYVZvY_4.9.F20.boolean.opBoolean","SPLIT",EDGE,{"disambiguationData":[TD([subQ6])],"derivedFrom":makeQuery(id+"F0Hq7nSFAMYVZvY_4.8.F20.boolean.opBoolean","SPLIT",EDGE,{"disambiguationData":[TD([subQ6])],"derivedFrom":makeQuery(id+"F0Hq7nSFAMYVZvY_4.7.F20.boolean.opBoolean","SPLIT",EDGE,{"disambiguationData":[TD([subQ6])],"derivedFrom":makeQuery(id+"F0Hq7nSFAMYVZvY_4.6.F20.boolean.opBoolean","SPLIT",EDGE,{"disambiguationData":[TD([subQ6])],"derivedFrom":makeQuery(id+"F0Hq7nSFAMYVZvY_4.5.F20.boolean.opBoolean","SPLIT",EDGE,{"disambiguationData":[TD([subQ6])],"derivedFrom":makeQuery(id+"F0Hq7nSFAMYVZvY_4.4.F20.boolean.opBoolean","SPLIT",EDGE,{"disambiguationData":[TD([subQ6])],"derivedFrom":makeQuery(id+"F0Hq7nSFAMYVZvY_4.3.F20.boolean.opBoolean","SPLIT",EDGE,{"disambiguationData":[TD([subQ6])],"derivedFrom":makeQuery(id+"F0Hq7nSFAMYVZvY_4.2.F20.boolean.opBoolean","SPLIT",EDGE,{"disambiguationData":[TD([subQ6])],"derivedFrom":makeQuery(id+"F0Hq7nSFAMYVZvY_4.1.F20.boolean.opBoolean","SPLIT",EDGE,{"disambiguationData":[TD([subQ6])],"derivedFrom":makeQuery(id+"F17.boolean.opBoolean","COPY",EDGE,{"derivedFrom":makeQuery(id+"F17.opExtrude","CAP_EDGE",EDGE,{"disambiguationData":[OSD([subQ0])],"isStart":false})})})})})})})})})})})})})})})})})})})})})})})})})})});}
            var Q96;
            {var subQ0=sQuery(id+"F19.wireOp",EDGE,"E158.MirrorCS");var subQ1=sQuery(id+"F19.wireOp",EDGE,"E157");var subQ3=sQuery(id+"F16.wireOp",EDGE,"E151");var subQ31=makeQuery(id+"F0Hq7nSFAMYVZvY_4.24.F20.opExtrude","SWEPT_FACE",FACE,{"disambiguationData":[OSD([subQ0])]});var subQ32=makeQuery(id+"F20.opExtrude","SWEPT_FACE",FACE,{"disambiguationData":[OSD([subQ1])]});Q96=makeQuery(id+"F0Hq7nSFAMYVZvY_4.25.F20.boolean.opBoolean","SPLIT",EDGE,{"disambiguationData":[TD([subQ31])],"derivedFrom":makeQuery(id+"F0Hq7nSFAMYVZvY_4.24.F20.boolean.opBoolean","SPLIT",EDGE,{"disambiguationData":[TD([subQ32])],"derivedFrom":makeQuery(id+"F0Hq7nSFAMYVZvY_4.23.F20.boolean.opBoolean","SPLIT",EDGE,{"disambiguationData":[TD([subQ32])],"derivedFrom":makeQuery(id+"F0Hq7nSFAMYVZvY_4.22.F20.boolean.opBoolean","SPLIT",EDGE,{"disambiguationData":[TD([subQ32])],"derivedFrom":makeQuery(id+"F0Hq7nSFAMYVZvY_4.21.F20.boolean.opBoolean","SPLIT",EDGE,{"disambiguationData":[TD([subQ32])],"derivedFrom":makeQuery(id+"F0Hq7nSFAMYVZvY_4.20.F20.boolean.opBoolean","SPLIT",EDGE,{"disambiguationData":[TD([subQ32])],"derivedFrom":makeQuery(id+"F0Hq7nSFAMYVZvY_4.19.F20.boolean.opBoolean","SPLIT",EDGE,{"disambiguationData":[TD([subQ32])],"derivedFrom":makeQuery(id+"F0Hq7nSFAMYVZvY_4.18.F20.boolean.opBoolean","SPLIT",EDGE,{"disambiguationData":[TD([subQ32])],"derivedFrom":makeQuery(id+"F0Hq7nSFAMYVZvY_4.17.F20.boolean.opBoolean","SPLIT",EDGE,{"disambiguationData":[TD([subQ32])],"derivedFrom":makeQuery(id+"F0Hq7nSFAMYVZvY_4.16.F20.boolean.opBoolean","SPLIT",EDGE,{"disambiguationData":[TD([subQ32])],"derivedFrom":makeQuery(id+"F0Hq7nSFAMYVZvY_4.15.F20.boolean.opBoolean","SPLIT",EDGE,{"disambiguationData":[TD([subQ32])],"derivedFrom":makeQuery(id+"F0Hq7nSFAMYVZvY_4.14.F20.boolean.opBoolean","SPLIT",EDGE,{"disambiguationData":[TD([subQ32])],"derivedFrom":makeQuery(id+"F0Hq7nSFAMYVZvY_4.13.F20.boolean.opBoolean","SPLIT",EDGE,{"disambiguationData":[TD([subQ32])],"derivedFrom":makeQuery(id+"F0Hq7nSFAMYVZvY_4.12.F20.boolean.opBoolean","SPLIT",EDGE,{"disambiguationData":[TD([subQ32])],"derivedFrom":makeQuery(id+"F0Hq7nSFAMYVZvY_4.11.F20.boolean.opBoolean","SPLIT",EDGE,{"disambiguationData":[TD([subQ32])],"derivedFrom":makeQuery(id+"F0Hq7nSFAMYVZvY_4.10.F20.boolean.opBoolean","SPLIT",EDGE,{"disambiguationData":[TD([subQ32])],"derivedFrom":makeQuery(id+"F0Hq7nSFAMYVZvY_4.9.F20.boolean.opBoolean","SPLIT",EDGE,{"disambiguationData":[TD([subQ32])],"derivedFrom":makeQuery(id+"F0Hq7nSFAMYVZvY_4.8.F20.boolean.opBoolean","SPLIT",EDGE,{"disambiguationData":[TD([subQ32])],"derivedFrom":makeQuery(id+"F0Hq7nSFAMYVZvY_4.7.F20.boolean.opBoolean","SPLIT",EDGE,{"disambiguationData":[TD([subQ32])],"derivedFrom":makeQuery(id+"F0Hq7nSFAMYVZvY_4.6.F20.boolean.opBoolean","SPLIT",EDGE,{"disambiguationData":[TD([subQ32])],"derivedFrom":makeQuery(id+"F0Hq7nSFAMYVZvY_4.5.F20.boolean.opBoolean","SPLIT",EDGE,{"disambiguationData":[TD([subQ32])],"derivedFrom":makeQuery(id+"F0Hq7nSFAMYVZvY_4.4.F20.boolean.opBoolean","SPLIT",EDGE,{"disambiguationData":[TD([subQ32])],"derivedFrom":makeQuery(id+"F0Hq7nSFAMYVZvY_4.3.F20.boolean.opBoolean","SPLIT",EDGE,{"disambiguationData":[TD([subQ32])],"derivedFrom":makeQuery(id+"F0Hq7nSFAMYVZvY_4.2.F20.boolean.opBoolean","SPLIT",EDGE,{"disambiguationData":[TD([subQ32])],"derivedFrom":makeQuery(id+"F0Hq7nSFAMYVZvY_4.1.F20.boolean.opBoolean","SPLIT",EDGE,{"disambiguationData":[TD([subQ32])],"derivedFrom":makeQuery(id+"F18.boolean.opBoolean","COPY",EDGE,{"derivedFrom":makeQuery(id+"F18.opExtrude","CAP_EDGE",EDGE,{"disambiguationData":[OSD([subQ3])],"isStart":false})})})})})})})})})})})})})})})})})})})})})})})})})})});}
            var Q97;
            Q97=makeQuery(id+"F0Hq7nSFAMYVZvY_4.26.F20.opExtrude","SWEPT_FACE",FACE,{"disambiguationData":[OSD([sQuery(id+"F19.wireOp",EDGE,"E157")])]});
            var Q98;
            Q98=makeQuery(id+"F0Hq7nSFAMYVZvY_4.26.F20.opExtrude","SWEPT_FACE",FACE,{"disambiguationData":[OSD([sQuery(id+"F19.wireOp",EDGE,"E158.MirrorCS")])]});
            var Q99;
            Q99=makeQuery(id+"F0Hq7nSFAMYVZvY_4.26.F20.opExtrude","CAP_EDGE",EDGE,{"disambiguationData":[OSD([sQuery(id+"F19.wireOp",EDGE,"E157")])],"isStart":false});
            var Q100;
            Q100=makeQuery(id+"F0Hq7nSFAMYVZvY_4.26.F20.opExtrude","CAP_EDGE",EDGE,{"disambiguationData":[OSD([sQuery(id+"F19.wireOp",EDGE,"E158.MirrorCS")])],"isStart":false});
            var Q101;
            {var subQ0=sQuery(id+"F16.wireOp",EDGE,"E151");var subQ2=sQuery(id+"F16.wireOp",EDGE,"E152");var subQ4=sQuery(id+"F19.wireOp",EDGE,"E157");var subQ5=sQuery(id+"F19.wireOp",EDGE,"E158.MirrorCS");var subQ6=makeQuery(id+"F0Hq7nSFAMYVZvY_4.25.F20.opExtrude","SWEPT_FACE",FACE,{"disambiguationData":[OSD([subQ5])]});var subQ7=makeQuery(id+"F20.opExtrude","SWEPT_FACE",FACE,{"disambiguationData":[OSD([subQ4])]});Q101=makeQuery(id+"F0Hq7nSFAMYVZvY_4.26.F20.boolean.opBoolean","SPLIT",FACE,{"disambiguationData":[TD([subQ6])],"derivedFrom":makeQuery(id+"F0Hq7nSFAMYVZvY_4.25.F20.boolean.opBoolean","SPLIT",FACE,{"disambiguationData":[TD([subQ7])],"derivedFrom":makeQuery(id+"F0Hq7nSFAMYVZvY_4.24.F20.boolean.opBoolean","SPLIT",FACE,{"disambiguationData":[TD([subQ7])],"derivedFrom":makeQuery(id+"F0Hq7nSFAMYVZvY_4.23.F20.boolean.opBoolean","SPLIT",FACE,{"disambiguationData":[TD([subQ7])],"derivedFrom":makeQuery(id+"F0Hq7nSFAMYVZvY_4.22.F20.boolean.opBoolean","SPLIT",FACE,{"disambiguationData":[TD([subQ7])],"derivedFrom":makeQuery(id+"F0Hq7nSFAMYVZvY_4.21.F20.boolean.opBoolean","SPLIT",FACE,{"disambiguationData":[TD([subQ7])],"derivedFrom":makeQuery(id+"F0Hq7nSFAMYVZvY_4.20.F20.boolean.opBoolean","SPLIT",FACE,{"disambiguationData":[TD([subQ7])],"derivedFrom":makeQuery(id+"F0Hq7nSFAMYVZvY_4.19.F20.boolean.opBoolean","SPLIT",FACE,{"disambiguationData":[TD([subQ7])],"derivedFrom":makeQuery(id+"F0Hq7nSFAMYVZvY_4.18.F20.boolean.opBoolean","SPLIT",FACE,{"disambiguationData":[TD([subQ7])],"derivedFrom":makeQuery(id+"F0Hq7nSFAMYVZvY_4.17.F20.boolean.opBoolean","SPLIT",FACE,{"disambiguationData":[TD([subQ7])],"derivedFrom":makeQuery(id+"F0Hq7nSFAMYVZvY_4.16.F20.boolean.opBoolean","SPLIT",FACE,{"disambiguationData":[TD([subQ7])],"derivedFrom":makeQuery(id+"F0Hq7nSFAMYVZvY_4.15.F20.boolean.opBoolean","SPLIT",FACE,{"disambiguationData":[TD([subQ7])],"derivedFrom":makeQuery(id+"F0Hq7nSFAMYVZvY_4.14.F20.boolean.opBoolean","SPLIT",FACE,{"disambiguationData":[TD([subQ7])],"derivedFrom":makeQuery(id+"F0Hq7nSFAMYVZvY_4.13.F20.boolean.opBoolean","SPLIT",FACE,{"disambiguationData":[TD([subQ7])],"derivedFrom":makeQuery(id+"F0Hq7nSFAMYVZvY_4.12.F20.boolean.opBoolean","SPLIT",FACE,{"disambiguationData":[TD([subQ7])],"derivedFrom":makeQuery(id+"F0Hq7nSFAMYVZvY_4.11.F20.boolean.opBoolean","SPLIT",FACE,{"disambiguationData":[TD([subQ7])],"derivedFrom":makeQuery(id+"F0Hq7nSFAMYVZvY_4.10.F20.boolean.opBoolean","SPLIT",FACE,{"disambiguationData":[TD([subQ7])],"derivedFrom":makeQuery(id+"F0Hq7nSFAMYVZvY_4.9.F20.boolean.opBoolean","SPLIT",FACE,{"disambiguationData":[TD([subQ7])],"derivedFrom":makeQuery(id+"F0Hq7nSFAMYVZvY_4.8.F20.boolean.opBoolean","SPLIT",FACE,{"disambiguationData":[TD([subQ7])],"derivedFrom":makeQuery(id+"F0Hq7nSFAMYVZvY_4.7.F20.boolean.opBoolean","SPLIT",FACE,{"disambiguationData":[TD([subQ7])],"derivedFrom":makeQuery(id+"F0Hq7nSFAMYVZvY_4.6.F20.boolean.opBoolean","SPLIT",FACE,{"disambiguationData":[TD([subQ7])],"derivedFrom":makeQuery(id+"F0Hq7nSFAMYVZvY_4.5.F20.boolean.opBoolean","SPLIT",FACE,{"disambiguationData":[TD([subQ7])],"derivedFrom":makeQuery(id+"F0Hq7nSFAMYVZvY_4.4.F20.boolean.opBoolean","SPLIT",FACE,{"disambiguationData":[TD([subQ7])],"derivedFrom":makeQuery(id+"F0Hq7nSFAMYVZvY_4.3.F20.boolean.opBoolean","SPLIT",FACE,{"disambiguationData":[TD([subQ7])],"derivedFrom":makeQuery(id+"F0Hq7nSFAMYVZvY_4.2.F20.boolean.opBoolean","SPLIT",FACE,{"disambiguationData":[TD([subQ7])],"derivedFrom":makeQuery(id+"F0Hq7nSFAMYVZvY_4.1.F20.boolean.opBoolean","SPLIT",FACE,{"disambiguationData":[TD([subQ7])],"derivedFrom":makeQuery(id+"F17.boolean.opBoolean","COPY",FACE,{"derivedFrom":makeQuery(id+"F17.opExtrude","CAP_FACE",FACE,{"disambiguationData":[OSD([subQ0,subQ2])],"isStart":false})})})})})})})})})})})})})})})})})})})})})})})})})})})});}
            var Q102;
            Q102=makeQuery(id+"F0Hq7nSFAMYVZvY_4.26.F20.opExtrude","CAP_EDGE",EDGE,{"disambiguationData":[OSD([sQuery(id+"F19.wireOp",EDGE,"E157")])],"isStart":true});
            var Q103;
            {var subQ0=sQuery(id+"F19.wireOp",EDGE,"E158.MirrorCS");var subQ1=sQuery(id+"F19.wireOp",EDGE,"E157");var subQ3=sQuery(id+"F16.wireOp",EDGE,"E151");var subQ32=makeQuery(id+"F0Hq7nSFAMYVZvY_4.25.F20.opExtrude","SWEPT_FACE",FACE,{"disambiguationData":[OSD([subQ0])]});var subQ33=makeQuery(id+"F20.opExtrude","SWEPT_FACE",FACE,{"disambiguationData":[OSD([subQ1])]});Q103=makeQuery(id+"F0Hq7nSFAMYVZvY_4.26.F20.boolean.opBoolean","SPLIT",FACE,{"disambiguationData":[TD([subQ32])],"derivedFrom":makeQuery(id+"F0Hq7nSFAMYVZvY_4.25.F20.boolean.opBoolean","SPLIT",FACE,{"disambiguationData":[TD([subQ33])],"derivedFrom":makeQuery(id+"F0Hq7nSFAMYVZvY_4.24.F20.boolean.opBoolean","SPLIT",FACE,{"disambiguationData":[TD([subQ33])],"derivedFrom":makeQuery(id+"F0Hq7nSFAMYVZvY_4.23.F20.boolean.opBoolean","SPLIT",FACE,{"disambiguationData":[TD([subQ33])],"derivedFrom":makeQuery(id+"F0Hq7nSFAMYVZvY_4.22.F20.boolean.opBoolean","SPLIT",FACE,{"disambiguationData":[TD([subQ33])],"derivedFrom":makeQuery(id+"F0Hq7nSFAMYVZvY_4.21.F20.boolean.opBoolean","SPLIT",FACE,{"disambiguationData":[TD([subQ33])],"derivedFrom":makeQuery(id+"F0Hq7nSFAMYVZvY_4.20.F20.boolean.opBoolean","SPLIT",FACE,{"disambiguationData":[TD([subQ33])],"derivedFrom":makeQuery(id+"F0Hq7nSFAMYVZvY_4.19.F20.boolean.opBoolean","SPLIT",FACE,{"disambiguationData":[TD([subQ33])],"derivedFrom":makeQuery(id+"F0Hq7nSFAMYVZvY_4.18.F20.boolean.opBoolean","SPLIT",FACE,{"disambiguationData":[TD([subQ33])],"derivedFrom":makeQuery(id+"F0Hq7nSFAMYVZvY_4.17.F20.boolean.opBoolean","SPLIT",FACE,{"disambiguationData":[TD([subQ33])],"derivedFrom":makeQuery(id+"F0Hq7nSFAMYVZvY_4.16.F20.boolean.opBoolean","SPLIT",FACE,{"disambiguationData":[TD([subQ33])],"derivedFrom":makeQuery(id+"F0Hq7nSFAMYVZvY_4.15.F20.boolean.opBoolean","SPLIT",FACE,{"disambiguationData":[TD([subQ33])],"derivedFrom":makeQuery(id+"F0Hq7nSFAMYVZvY_4.14.F20.boolean.opBoolean","SPLIT",FACE,{"disambiguationData":[TD([subQ33])],"derivedFrom":makeQuery(id+"F0Hq7nSFAMYVZvY_4.13.F20.boolean.opBoolean","SPLIT",FACE,{"disambiguationData":[TD([subQ33])],"derivedFrom":makeQuery(id+"F0Hq7nSFAMYVZvY_4.12.F20.boolean.opBoolean","SPLIT",FACE,{"disambiguationData":[TD([subQ33])],"derivedFrom":makeQuery(id+"F0Hq7nSFAMYVZvY_4.11.F20.boolean.opBoolean","SPLIT",FACE,{"disambiguationData":[TD([subQ33])],"derivedFrom":makeQuery(id+"F0Hq7nSFAMYVZvY_4.10.F20.boolean.opBoolean","SPLIT",FACE,{"disambiguationData":[TD([subQ33])],"derivedFrom":makeQuery(id+"F0Hq7nSFAMYVZvY_4.9.F20.boolean.opBoolean","SPLIT",FACE,{"disambiguationData":[TD([subQ33])],"derivedFrom":makeQuery(id+"F0Hq7nSFAMYVZvY_4.8.F20.boolean.opBoolean","SPLIT",FACE,{"disambiguationData":[TD([subQ33])],"derivedFrom":makeQuery(id+"F0Hq7nSFAMYVZvY_4.7.F20.boolean.opBoolean","SPLIT",FACE,{"disambiguationData":[TD([subQ33])],"derivedFrom":makeQuery(id+"F0Hq7nSFAMYVZvY_4.6.F20.boolean.opBoolean","SPLIT",FACE,{"disambiguationData":[TD([subQ33])],"derivedFrom":makeQuery(id+"F0Hq7nSFAMYVZvY_4.5.F20.boolean.opBoolean","SPLIT",FACE,{"disambiguationData":[TD([subQ33])],"derivedFrom":makeQuery(id+"F0Hq7nSFAMYVZvY_4.4.F20.boolean.opBoolean","SPLIT",FACE,{"disambiguationData":[TD([subQ33])],"derivedFrom":makeQuery(id+"F0Hq7nSFAMYVZvY_4.3.F20.boolean.opBoolean","SPLIT",FACE,{"disambiguationData":[TD([subQ33])],"derivedFrom":makeQuery(id+"F0Hq7nSFAMYVZvY_4.2.F20.boolean.opBoolean","SPLIT",FACE,{"disambiguationData":[TD([subQ33])],"derivedFrom":makeQuery(id+"F0Hq7nSFAMYVZvY_4.1.F20.boolean.opBoolean","SPLIT",FACE,{"disambiguationData":[TD([subQ33])],"derivedFrom":makeQuery(id+"F17.boolean.opBoolean","COPY",FACE,{"derivedFrom":makeQuery(id+"F17.opExtrude","SWEPT_FACE",FACE,{"disambiguationData":[OSD([subQ3])]})})})})})})})})})})})})})})})})})})})})})})})})})})})});}
            var Q104;
            Q104=makeQuery(id+"F0Hq7nSFAMYVZvY_4.27.F20.opExtrude","SWEPT_FACE",FACE,{"disambiguationData":[OSD([sQuery(id+"F19.wireOp",EDGE,"E157")])]});
            var Q105;
            Q105=makeQuery(id+"F0Hq7nSFAMYVZvY_4.27.F20.opExtrude","CAP_EDGE",EDGE,{"disambiguationData":[OSD([sQuery(id+"F19.wireOp",EDGE,"E157")])],"isStart":false});
            var Q106;
            Q106=makeQuery(id+"F0Hq7nSFAMYVZvY_4.27.F20.opExtrude","CAP_EDGE",EDGE,{"disambiguationData":[OSD([sQuery(id+"F19.wireOp",EDGE,"E158.MirrorCS")])],"isStart":false});
            var Q107;
            {var subQ0=sQuery(id+"F16.wireOp",EDGE,"E151");var subQ2=sQuery(id+"F19.wireOp",EDGE,"E158.MirrorCS");var subQ3=makeQuery(id+"F0Hq7nSFAMYVZvY_4.26.F20.opExtrude","SWEPT_FACE",FACE,{"disambiguationData":[OSD([subQ2])]});var subQ4=sQuery(id+"F16.wireOp",EDGE,"E152");var subQ6=sQuery(id+"F19.wireOp",EDGE,"E157");var subQ7=makeQuery(id+"F20.opExtrude","SWEPT_FACE",FACE,{"disambiguationData":[OSD([subQ6])]});Q107=makeQuery(id+"F0Hq7nSFAMYVZvY_4.27.F20.boolean.opBoolean","SPLIT",FACE,{"disambiguationData":[TD([subQ3])],"derivedFrom":makeQuery(id+"F0Hq7nSFAMYVZvY_4.26.F20.boolean.opBoolean","SPLIT",FACE,{"disambiguationData":[TD([subQ7])],"derivedFrom":makeQuery(id+"F0Hq7nSFAMYVZvY_4.25.F20.boolean.opBoolean","SPLIT",FACE,{"disambiguationData":[TD([subQ7])],"derivedFrom":makeQuery(id+"F0Hq7nSFAMYVZvY_4.24.F20.boolean.opBoolean","SPLIT",FACE,{"disambiguationData":[TD([subQ7])],"derivedFrom":makeQuery(id+"F0Hq7nSFAMYVZvY_4.23.F20.boolean.opBoolean","SPLIT",FACE,{"disambiguationData":[TD([subQ7])],"derivedFrom":makeQuery(id+"F0Hq7nSFAMYVZvY_4.22.F20.boolean.opBoolean","SPLIT",FACE,{"disambiguationData":[TD([subQ7])],"derivedFrom":makeQuery(id+"F0Hq7nSFAMYVZvY_4.21.F20.boolean.opBoolean","SPLIT",FACE,{"disambiguationData":[TD([subQ7])],"derivedFrom":makeQuery(id+"F0Hq7nSFAMYVZvY_4.20.F20.boolean.opBoolean","SPLIT",FACE,{"disambiguationData":[TD([subQ7])],"derivedFrom":makeQuery(id+"F0Hq7nSFAMYVZvY_4.19.F20.boolean.opBoolean","SPLIT",FACE,{"disambiguationData":[TD([subQ7])],"derivedFrom":makeQuery(id+"F0Hq7nSFAMYVZvY_4.18.F20.boolean.opBoolean","SPLIT",FACE,{"disambiguationData":[TD([subQ7])],"derivedFrom":makeQuery(id+"F0Hq7nSFAMYVZvY_4.17.F20.boolean.opBoolean","SPLIT",FACE,{"disambiguationData":[TD([subQ7])],"derivedFrom":makeQuery(id+"F0Hq7nSFAMYVZvY_4.16.F20.boolean.opBoolean","SPLIT",FACE,{"disambiguationData":[TD([subQ7])],"derivedFrom":makeQuery(id+"F0Hq7nSFAMYVZvY_4.15.F20.boolean.opBoolean","SPLIT",FACE,{"disambiguationData":[TD([subQ7])],"derivedFrom":makeQuery(id+"F0Hq7nSFAMYVZvY_4.14.F20.boolean.opBoolean","SPLIT",FACE,{"disambiguationData":[TD([subQ7])],"derivedFrom":makeQuery(id+"F0Hq7nSFAMYVZvY_4.13.F20.boolean.opBoolean","SPLIT",FACE,{"disambiguationData":[TD([subQ7])],"derivedFrom":makeQuery(id+"F0Hq7nSFAMYVZvY_4.12.F20.boolean.opBoolean","SPLIT",FACE,{"disambiguationData":[TD([subQ7])],"derivedFrom":makeQuery(id+"F0Hq7nSFAMYVZvY_4.11.F20.boolean.opBoolean","SPLIT",FACE,{"disambiguationData":[TD([subQ7])],"derivedFrom":makeQuery(id+"F0Hq7nSFAMYVZvY_4.10.F20.boolean.opBoolean","SPLIT",FACE,{"disambiguationData":[TD([subQ7])],"derivedFrom":makeQuery(id+"F0Hq7nSFAMYVZvY_4.9.F20.boolean.opBoolean","SPLIT",FACE,{"disambiguationData":[TD([subQ7])],"derivedFrom":makeQuery(id+"F0Hq7nSFAMYVZvY_4.8.F20.boolean.opBoolean","SPLIT",FACE,{"disambiguationData":[TD([subQ7])],"derivedFrom":makeQuery(id+"F0Hq7nSFAMYVZvY_4.7.F20.boolean.opBoolean","SPLIT",FACE,{"disambiguationData":[TD([subQ7])],"derivedFrom":makeQuery(id+"F0Hq7nSFAMYVZvY_4.6.F20.boolean.opBoolean","SPLIT",FACE,{"disambiguationData":[TD([subQ7])],"derivedFrom":makeQuery(id+"F0Hq7nSFAMYVZvY_4.5.F20.boolean.opBoolean","SPLIT",FACE,{"disambiguationData":[TD([subQ7])],"derivedFrom":makeQuery(id+"F0Hq7nSFAMYVZvY_4.4.F20.boolean.opBoolean","SPLIT",FACE,{"disambiguationData":[TD([subQ7])],"derivedFrom":makeQuery(id+"F0Hq7nSFAMYVZvY_4.3.F20.boolean.opBoolean","SPLIT",FACE,{"disambiguationData":[TD([subQ7])],"derivedFrom":makeQuery(id+"F0Hq7nSFAMYVZvY_4.2.F20.boolean.opBoolean","SPLIT",FACE,{"disambiguationData":[TD([subQ7])],"derivedFrom":makeQuery(id+"F0Hq7nSFAMYVZvY_4.1.F20.boolean.opBoolean","SPLIT",FACE,{"disambiguationData":[TD([subQ7])],"derivedFrom":makeQuery(id+"F17.boolean.opBoolean","COPY",FACE,{"derivedFrom":makeQuery(id+"F17.opExtrude","CAP_FACE",FACE,{"disambiguationData":[OSD([subQ0,subQ4])],"isStart":false})})})})})})})})})})})})})})})})})})})})})})})})})})})})});}
            var Q108;
            Q108=makeQuery(id+"F0Hq7nSFAMYVZvY_4.27.F20.opExtrude","CAP_EDGE",EDGE,{"disambiguationData":[OSD([sQuery(id+"F19.wireOp",EDGE,"E157")])],"isStart":true});
            var Q109;
            {var subQ0=sQuery(id+"F19.wireOp",EDGE,"E158.MirrorCS");var subQ1=sQuery(id+"F19.wireOp",EDGE,"E157");var subQ3=sQuery(id+"F16.wireOp",EDGE,"E151");var subQ33=makeQuery(id+"F0Hq7nSFAMYVZvY_4.26.F20.opExtrude","SWEPT_FACE",FACE,{"disambiguationData":[OSD([subQ0])]});var subQ34=makeQuery(id+"F20.opExtrude","SWEPT_FACE",FACE,{"disambiguationData":[OSD([subQ1])]});Q109=makeQuery(id+"F0Hq7nSFAMYVZvY_4.27.F20.boolean.opBoolean","SPLIT",FACE,{"disambiguationData":[TD([subQ33])],"derivedFrom":makeQuery(id+"F0Hq7nSFAMYVZvY_4.26.F20.boolean.opBoolean","SPLIT",FACE,{"disambiguationData":[TD([subQ34])],"derivedFrom":makeQuery(id+"F0Hq7nSFAMYVZvY_4.25.F20.boolean.opBoolean","SPLIT",FACE,{"disambiguationData":[TD([subQ34])],"derivedFrom":makeQuery(id+"F0Hq7nSFAMYVZvY_4.24.F20.boolean.opBoolean","SPLIT",FACE,{"disambiguationData":[TD([subQ34])],"derivedFrom":makeQuery(id+"F0Hq7nSFAMYVZvY_4.23.F20.boolean.opBoolean","SPLIT",FACE,{"disambiguationData":[TD([subQ34])],"derivedFrom":makeQuery(id+"F0Hq7nSFAMYVZvY_4.22.F20.boolean.opBoolean","SPLIT",FACE,{"disambiguationData":[TD([subQ34])],"derivedFrom":makeQuery(id+"F0Hq7nSFAMYVZvY_4.21.F20.boolean.opBoolean","SPLIT",FACE,{"disambiguationData":[TD([subQ34])],"derivedFrom":makeQuery(id+"F0Hq7nSFAMYVZvY_4.20.F20.boolean.opBoolean","SPLIT",FACE,{"disambiguationData":[TD([subQ34])],"derivedFrom":makeQuery(id+"F0Hq7nSFAMYVZvY_4.19.F20.boolean.opBoolean","SPLIT",FACE,{"disambiguationData":[TD([subQ34])],"derivedFrom":makeQuery(id+"F0Hq7nSFAMYVZvY_4.18.F20.boolean.opBoolean","SPLIT",FACE,{"disambiguationData":[TD([subQ34])],"derivedFrom":makeQuery(id+"F0Hq7nSFAMYVZvY_4.17.F20.boolean.opBoolean","SPLIT",FACE,{"disambiguationData":[TD([subQ34])],"derivedFrom":makeQuery(id+"F0Hq7nSFAMYVZvY_4.16.F20.boolean.opBoolean","SPLIT",FACE,{"disambiguationData":[TD([subQ34])],"derivedFrom":makeQuery(id+"F0Hq7nSFAMYVZvY_4.15.F20.boolean.opBoolean","SPLIT",FACE,{"disambiguationData":[TD([subQ34])],"derivedFrom":makeQuery(id+"F0Hq7nSFAMYVZvY_4.14.F20.boolean.opBoolean","SPLIT",FACE,{"disambiguationData":[TD([subQ34])],"derivedFrom":makeQuery(id+"F0Hq7nSFAMYVZvY_4.13.F20.boolean.opBoolean","SPLIT",FACE,{"disambiguationData":[TD([subQ34])],"derivedFrom":makeQuery(id+"F0Hq7nSFAMYVZvY_4.12.F20.boolean.opBoolean","SPLIT",FACE,{"disambiguationData":[TD([subQ34])],"derivedFrom":makeQuery(id+"F0Hq7nSFAMYVZvY_4.11.F20.boolean.opBoolean","SPLIT",FACE,{"disambiguationData":[TD([subQ34])],"derivedFrom":makeQuery(id+"F0Hq7nSFAMYVZvY_4.10.F20.boolean.opBoolean","SPLIT",FACE,{"disambiguationData":[TD([subQ34])],"derivedFrom":makeQuery(id+"F0Hq7nSFAMYVZvY_4.9.F20.boolean.opBoolean","SPLIT",FACE,{"disambiguationData":[TD([subQ34])],"derivedFrom":makeQuery(id+"F0Hq7nSFAMYVZvY_4.8.F20.boolean.opBoolean","SPLIT",FACE,{"disambiguationData":[TD([subQ34])],"derivedFrom":makeQuery(id+"F0Hq7nSFAMYVZvY_4.7.F20.boolean.opBoolean","SPLIT",FACE,{"disambiguationData":[TD([subQ34])],"derivedFrom":makeQuery(id+"F0Hq7nSFAMYVZvY_4.6.F20.boolean.opBoolean","SPLIT",FACE,{"disambiguationData":[TD([subQ34])],"derivedFrom":makeQuery(id+"F0Hq7nSFAMYVZvY_4.5.F20.boolean.opBoolean","SPLIT",FACE,{"disambiguationData":[TD([subQ34])],"derivedFrom":makeQuery(id+"F0Hq7nSFAMYVZvY_4.4.F20.boolean.opBoolean","SPLIT",FACE,{"disambiguationData":[TD([subQ34])],"derivedFrom":makeQuery(id+"F0Hq7nSFAMYVZvY_4.3.F20.boolean.opBoolean","SPLIT",FACE,{"disambiguationData":[TD([subQ34])],"derivedFrom":makeQuery(id+"F0Hq7nSFAMYVZvY_4.2.F20.boolean.opBoolean","SPLIT",FACE,{"disambiguationData":[TD([subQ34])],"derivedFrom":makeQuery(id+"F0Hq7nSFAMYVZvY_4.1.F20.boolean.opBoolean","SPLIT",FACE,{"disambiguationData":[TD([subQ34])],"derivedFrom":makeQuery(id+"F17.boolean.opBoolean","COPY",FACE,{"derivedFrom":makeQuery(id+"F17.opExtrude","SWEPT_FACE",FACE,{"disambiguationData":[OSD([subQ3])]})})})})})})})})})})})})})})})})})})})})})})})})})})})})});}
            var Q110;
            Q110=makeQuery(id+"F0Hq7nSFAMYVZvY_4.28.F20.opExtrude","SWEPT_FACE",FACE,{"disambiguationData":[OSD([sQuery(id+"F19.wireOp",EDGE,"E157")])]});
            var Q111;
            Q111=makeQuery(id+"F0Hq7nSFAMYVZvY_4.28.F20.opExtrude","CAP_EDGE",EDGE,{"disambiguationData":[OSD([sQuery(id+"F19.wireOp",EDGE,"E157")])],"isStart":false});
            var Q112;
            Q112=makeQuery(id+"F0Hq7nSFAMYVZvY_4.28.F20.opExtrude","CAP_EDGE",EDGE,{"disambiguationData":[OSD([sQuery(id+"F19.wireOp",EDGE,"E158.MirrorCS")])],"isStart":false});
            var Q113;
            {var subQ0=sQuery(id+"F16.wireOp",EDGE,"E151");var subQ2=sQuery(id+"F16.wireOp",EDGE,"E152");var subQ4=sQuery(id+"F19.wireOp",EDGE,"E158.MirrorCS");var subQ5=makeQuery(id+"F0Hq7nSFAMYVZvY_4.27.F20.opExtrude","SWEPT_FACE",FACE,{"disambiguationData":[OSD([subQ4])]});var subQ6=sQuery(id+"F19.wireOp",EDGE,"E157");var subQ7=makeQuery(id+"F20.opExtrude","SWEPT_FACE",FACE,{"disambiguationData":[OSD([subQ6])]});Q113=makeQuery(id+"F0Hq7nSFAMYVZvY_4.28.F20.boolean.opBoolean","SPLIT",FACE,{"disambiguationData":[TD([subQ5])],"derivedFrom":makeQuery(id+"F0Hq7nSFAMYVZvY_4.27.F20.boolean.opBoolean","SPLIT",FACE,{"disambiguationData":[TD([subQ7])],"derivedFrom":makeQuery(id+"F0Hq7nSFAMYVZvY_4.26.F20.boolean.opBoolean","SPLIT",FACE,{"disambiguationData":[TD([subQ7])],"derivedFrom":makeQuery(id+"F0Hq7nSFAMYVZvY_4.25.F20.boolean.opBoolean","SPLIT",FACE,{"disambiguationData":[TD([subQ7])],"derivedFrom":makeQuery(id+"F0Hq7nSFAMYVZvY_4.24.F20.boolean.opBoolean","SPLIT",FACE,{"disambiguationData":[TD([subQ7])],"derivedFrom":makeQuery(id+"F0Hq7nSFAMYVZvY_4.23.F20.boolean.opBoolean","SPLIT",FACE,{"disambiguationData":[TD([subQ7])],"derivedFrom":makeQuery(id+"F0Hq7nSFAMYVZvY_4.22.F20.boolean.opBoolean","SPLIT",FACE,{"disambiguationData":[TD([subQ7])],"derivedFrom":makeQuery(id+"F0Hq7nSFAMYVZvY_4.21.F20.boolean.opBoolean","SPLIT",FACE,{"disambiguationData":[TD([subQ7])],"derivedFrom":makeQuery(id+"F0Hq7nSFAMYVZvY_4.20.F20.boolean.opBoolean","SPLIT",FACE,{"disambiguationData":[TD([subQ7])],"derivedFrom":makeQuery(id+"F0Hq7nSFAMYVZvY_4.19.F20.boolean.opBoolean","SPLIT",FACE,{"disambiguationData":[TD([subQ7])],"derivedFrom":makeQuery(id+"F0Hq7nSFAMYVZvY_4.18.F20.boolean.opBoolean","SPLIT",FACE,{"disambiguationData":[TD([subQ7])],"derivedFrom":makeQuery(id+"F0Hq7nSFAMYVZvY_4.17.F20.boolean.opBoolean","SPLIT",FACE,{"disambiguationData":[TD([subQ7])],"derivedFrom":makeQuery(id+"F0Hq7nSFAMYVZvY_4.16.F20.boolean.opBoolean","SPLIT",FACE,{"disambiguationData":[TD([subQ7])],"derivedFrom":makeQuery(id+"F0Hq7nSFAMYVZvY_4.15.F20.boolean.opBoolean","SPLIT",FACE,{"disambiguationData":[TD([subQ7])],"derivedFrom":makeQuery(id+"F0Hq7nSFAMYVZvY_4.14.F20.boolean.opBoolean","SPLIT",FACE,{"disambiguationData":[TD([subQ7])],"derivedFrom":makeQuery(id+"F0Hq7nSFAMYVZvY_4.13.F20.boolean.opBoolean","SPLIT",FACE,{"disambiguationData":[TD([subQ7])],"derivedFrom":makeQuery(id+"F0Hq7nSFAMYVZvY_4.12.F20.boolean.opBoolean","SPLIT",FACE,{"disambiguationData":[TD([subQ7])],"derivedFrom":makeQuery(id+"F0Hq7nSFAMYVZvY_4.11.F20.boolean.opBoolean","SPLIT",FACE,{"disambiguationData":[TD([subQ7])],"derivedFrom":makeQuery(id+"F0Hq7nSFAMYVZvY_4.10.F20.boolean.opBoolean","SPLIT",FACE,{"disambiguationData":[TD([subQ7])],"derivedFrom":makeQuery(id+"F0Hq7nSFAMYVZvY_4.9.F20.boolean.opBoolean","SPLIT",FACE,{"disambiguationData":[TD([subQ7])],"derivedFrom":makeQuery(id+"F0Hq7nSFAMYVZvY_4.8.F20.boolean.opBoolean","SPLIT",FACE,{"disambiguationData":[TD([subQ7])],"derivedFrom":makeQuery(id+"F0Hq7nSFAMYVZvY_4.7.F20.boolean.opBoolean","SPLIT",FACE,{"disambiguationData":[TD([subQ7])],"derivedFrom":makeQuery(id+"F0Hq7nSFAMYVZvY_4.6.F20.boolean.opBoolean","SPLIT",FACE,{"disambiguationData":[TD([subQ7])],"derivedFrom":makeQuery(id+"F0Hq7nSFAMYVZvY_4.5.F20.boolean.opBoolean","SPLIT",FACE,{"disambiguationData":[TD([subQ7])],"derivedFrom":makeQuery(id+"F0Hq7nSFAMYVZvY_4.4.F20.boolean.opBoolean","SPLIT",FACE,{"disambiguationData":[TD([subQ7])],"derivedFrom":makeQuery(id+"F0Hq7nSFAMYVZvY_4.3.F20.boolean.opBoolean","SPLIT",FACE,{"disambiguationData":[TD([subQ7])],"derivedFrom":makeQuery(id+"F0Hq7nSFAMYVZvY_4.2.F20.boolean.opBoolean","SPLIT",FACE,{"disambiguationData":[TD([subQ7])],"derivedFrom":makeQuery(id+"F0Hq7nSFAMYVZvY_4.1.F20.boolean.opBoolean","SPLIT",FACE,{"disambiguationData":[TD([subQ7])],"derivedFrom":makeQuery(id+"F17.boolean.opBoolean","COPY",FACE,{"derivedFrom":makeQuery(id+"F17.opExtrude","CAP_FACE",FACE,{"disambiguationData":[OSD([subQ0,subQ2])],"isStart":false})})})})})})})})})})})})})})})})})})})})})})})})})})})})})});}
            var Q114;
            Q114=makeQuery(id+"F0Hq7nSFAMYVZvY_4.28.F20.opExtrude","CAP_EDGE",EDGE,{"disambiguationData":[OSD([sQuery(id+"F19.wireOp",EDGE,"E157")])],"isStart":true});
            var Q115;
            {var subQ0=sQuery(id+"F19.wireOp",EDGE,"E158.MirrorCS");var subQ1=sQuery(id+"F19.wireOp",EDGE,"E157");var subQ3=sQuery(id+"F16.wireOp",EDGE,"E151");var subQ34=makeQuery(id+"F0Hq7nSFAMYVZvY_4.27.F20.opExtrude","SWEPT_FACE",FACE,{"disambiguationData":[OSD([subQ0])]});var subQ35=makeQuery(id+"F20.opExtrude","SWEPT_FACE",FACE,{"disambiguationData":[OSD([subQ1])]});Q115=makeQuery(id+"F0Hq7nSFAMYVZvY_4.28.F20.boolean.opBoolean","SPLIT",FACE,{"disambiguationData":[TD([subQ34])],"derivedFrom":makeQuery(id+"F0Hq7nSFAMYVZvY_4.27.F20.boolean.opBoolean","SPLIT",FACE,{"disambiguationData":[TD([subQ35])],"derivedFrom":makeQuery(id+"F0Hq7nSFAMYVZvY_4.26.F20.boolean.opBoolean","SPLIT",FACE,{"disambiguationData":[TD([subQ35])],"derivedFrom":makeQuery(id+"F0Hq7nSFAMYVZvY_4.25.F20.boolean.opBoolean","SPLIT",FACE,{"disambiguationData":[TD([subQ35])],"derivedFrom":makeQuery(id+"F0Hq7nSFAMYVZvY_4.24.F20.boolean.opBoolean","SPLIT",FACE,{"disambiguationData":[TD([subQ35])],"derivedFrom":makeQuery(id+"F0Hq7nSFAMYVZvY_4.23.F20.boolean.opBoolean","SPLIT",FACE,{"disambiguationData":[TD([subQ35])],"derivedFrom":makeQuery(id+"F0Hq7nSFAMYVZvY_4.22.F20.boolean.opBoolean","SPLIT",FACE,{"disambiguationData":[TD([subQ35])],"derivedFrom":makeQuery(id+"F0Hq7nSFAMYVZvY_4.21.F20.boolean.opBoolean","SPLIT",FACE,{"disambiguationData":[TD([subQ35])],"derivedFrom":makeQuery(id+"F0Hq7nSFAMYVZvY_4.20.F20.boolean.opBoolean","SPLIT",FACE,{"disambiguationData":[TD([subQ35])],"derivedFrom":makeQuery(id+"F0Hq7nSFAMYVZvY_4.19.F20.boolean.opBoolean","SPLIT",FACE,{"disambiguationData":[TD([subQ35])],"derivedFrom":makeQuery(id+"F0Hq7nSFAMYVZvY_4.18.F20.boolean.opBoolean","SPLIT",FACE,{"disambiguationData":[TD([subQ35])],"derivedFrom":makeQuery(id+"F0Hq7nSFAMYVZvY_4.17.F20.boolean.opBoolean","SPLIT",FACE,{"disambiguationData":[TD([subQ35])],"derivedFrom":makeQuery(id+"F0Hq7nSFAMYVZvY_4.16.F20.boolean.opBoolean","SPLIT",FACE,{"disambiguationData":[TD([subQ35])],"derivedFrom":makeQuery(id+"F0Hq7nSFAMYVZvY_4.15.F20.boolean.opBoolean","SPLIT",FACE,{"disambiguationData":[TD([subQ35])],"derivedFrom":makeQuery(id+"F0Hq7nSFAMYVZvY_4.14.F20.boolean.opBoolean","SPLIT",FACE,{"disambiguationData":[TD([subQ35])],"derivedFrom":makeQuery(id+"F0Hq7nSFAMYVZvY_4.13.F20.boolean.opBoolean","SPLIT",FACE,{"disambiguationData":[TD([subQ35])],"derivedFrom":makeQuery(id+"F0Hq7nSFAMYVZvY_4.12.F20.boolean.opBoolean","SPLIT",FACE,{"disambiguationData":[TD([subQ35])],"derivedFrom":makeQuery(id+"F0Hq7nSFAMYVZvY_4.11.F20.boolean.opBoolean","SPLIT",FACE,{"disambiguationData":[TD([subQ35])],"derivedFrom":makeQuery(id+"F0Hq7nSFAMYVZvY_4.10.F20.boolean.opBoolean","SPLIT",FACE,{"disambiguationData":[TD([subQ35])],"derivedFrom":makeQuery(id+"F0Hq7nSFAMYVZvY_4.9.F20.boolean.opBoolean","SPLIT",FACE,{"disambiguationData":[TD([subQ35])],"derivedFrom":makeQuery(id+"F0Hq7nSFAMYVZvY_4.8.F20.boolean.opBoolean","SPLIT",FACE,{"disambiguationData":[TD([subQ35])],"derivedFrom":makeQuery(id+"F0Hq7nSFAMYVZvY_4.7.F20.boolean.opBoolean","SPLIT",FACE,{"disambiguationData":[TD([subQ35])],"derivedFrom":makeQuery(id+"F0Hq7nSFAMYVZvY_4.6.F20.boolean.opBoolean","SPLIT",FACE,{"disambiguationData":[TD([subQ35])],"derivedFrom":makeQuery(id+"F0Hq7nSFAMYVZvY_4.5.F20.boolean.opBoolean","SPLIT",FACE,{"disambiguationData":[TD([subQ35])],"derivedFrom":makeQuery(id+"F0Hq7nSFAMYVZvY_4.4.F20.boolean.opBoolean","SPLIT",FACE,{"disambiguationData":[TD([subQ35])],"derivedFrom":makeQuery(id+"F0Hq7nSFAMYVZvY_4.3.F20.boolean.opBoolean","SPLIT",FACE,{"disambiguationData":[TD([subQ35])],"derivedFrom":makeQuery(id+"F0Hq7nSFAMYVZvY_4.2.F20.boolean.opBoolean","SPLIT",FACE,{"disambiguationData":[TD([subQ35])],"derivedFrom":makeQuery(id+"F0Hq7nSFAMYVZvY_4.1.F20.boolean.opBoolean","SPLIT",FACE,{"disambiguationData":[TD([subQ35])],"derivedFrom":makeQuery(id+"F17.boolean.opBoolean","COPY",FACE,{"derivedFrom":makeQuery(id+"F17.opExtrude","SWEPT_FACE",FACE,{"disambiguationData":[OSD([subQ3])]})})})})})})})})})})})})})})})})})})})})})})})})})})})})})});}
            var Q116;
            Q116=makeQuery(id+"F0Hq7nSFAMYVZvY_4.29.F20.opExtrude","SWEPT_FACE",FACE,{"disambiguationData":[OSD([sQuery(id+"F19.wireOp",EDGE,"E157")])]});
            var Q117;
            {var subQ0=sQuery(id+"F16.wireOp",EDGE,"E151");var subQ2=sQuery(id+"F16.wireOp",EDGE,"E152");var subQ4=sQuery(id+"F19.wireOp",EDGE,"E158.MirrorCS");var subQ5=makeQuery(id+"F0Hq7nSFAMYVZvY_4.28.F20.opExtrude","SWEPT_FACE",FACE,{"disambiguationData":[OSD([subQ4])]});var subQ6=sQuery(id+"F19.wireOp",EDGE,"E157");var subQ7=makeQuery(id+"F20.opExtrude","SWEPT_FACE",FACE,{"disambiguationData":[OSD([subQ6])]});Q117=makeQuery(id+"F0Hq7nSFAMYVZvY_4.29.F20.boolean.opBoolean","SPLIT",FACE,{"disambiguationData":[TD([subQ5])],"derivedFrom":makeQuery(id+"F0Hq7nSFAMYVZvY_4.28.F20.boolean.opBoolean","SPLIT",FACE,{"disambiguationData":[TD([subQ7])],"derivedFrom":makeQuery(id+"F0Hq7nSFAMYVZvY_4.27.F20.boolean.opBoolean","SPLIT",FACE,{"disambiguationData":[TD([subQ7])],"derivedFrom":makeQuery(id+"F0Hq7nSFAMYVZvY_4.26.F20.boolean.opBoolean","SPLIT",FACE,{"disambiguationData":[TD([subQ7])],"derivedFrom":makeQuery(id+"F0Hq7nSFAMYVZvY_4.25.F20.boolean.opBoolean","SPLIT",FACE,{"disambiguationData":[TD([subQ7])],"derivedFrom":makeQuery(id+"F0Hq7nSFAMYVZvY_4.24.F20.boolean.opBoolean","SPLIT",FACE,{"disambiguationData":[TD([subQ7])],"derivedFrom":makeQuery(id+"F0Hq7nSFAMYVZvY_4.23.F20.boolean.opBoolean","SPLIT",FACE,{"disambiguationData":[TD([subQ7])],"derivedFrom":makeQuery(id+"F0Hq7nSFAMYVZvY_4.22.F20.boolean.opBoolean","SPLIT",FACE,{"disambiguationData":[TD([subQ7])],"derivedFrom":makeQuery(id+"F0Hq7nSFAMYVZvY_4.21.F20.boolean.opBoolean","SPLIT",FACE,{"disambiguationData":[TD([subQ7])],"derivedFrom":makeQuery(id+"F0Hq7nSFAMYVZvY_4.20.F20.boolean.opBoolean","SPLIT",FACE,{"disambiguationData":[TD([subQ7])],"derivedFrom":makeQuery(id+"F0Hq7nSFAMYVZvY_4.19.F20.boolean.opBoolean","SPLIT",FACE,{"disambiguationData":[TD([subQ7])],"derivedFrom":makeQuery(id+"F0Hq7nSFAMYVZvY_4.18.F20.boolean.opBoolean","SPLIT",FACE,{"disambiguationData":[TD([subQ7])],"derivedFrom":makeQuery(id+"F0Hq7nSFAMYVZvY_4.17.F20.boolean.opBoolean","SPLIT",FACE,{"disambiguationData":[TD([subQ7])],"derivedFrom":makeQuery(id+"F0Hq7nSFAMYVZvY_4.16.F20.boolean.opBoolean","SPLIT",FACE,{"disambiguationData":[TD([subQ7])],"derivedFrom":makeQuery(id+"F0Hq7nSFAMYVZvY_4.15.F20.boolean.opBoolean","SPLIT",FACE,{"disambiguationData":[TD([subQ7])],"derivedFrom":makeQuery(id+"F0Hq7nSFAMYVZvY_4.14.F20.boolean.opBoolean","SPLIT",FACE,{"disambiguationData":[TD([subQ7])],"derivedFrom":makeQuery(id+"F0Hq7nSFAMYVZvY_4.13.F20.boolean.opBoolean","SPLIT",FACE,{"disambiguationData":[TD([subQ7])],"derivedFrom":makeQuery(id+"F0Hq7nSFAMYVZvY_4.12.F20.boolean.opBoolean","SPLIT",FACE,{"disambiguationData":[TD([subQ7])],"derivedFrom":makeQuery(id+"F0Hq7nSFAMYVZvY_4.11.F20.boolean.opBoolean","SPLIT",FACE,{"disambiguationData":[TD([subQ7])],"derivedFrom":makeQuery(id+"F0Hq7nSFAMYVZvY_4.10.F20.boolean.opBoolean","SPLIT",FACE,{"disambiguationData":[TD([subQ7])],"derivedFrom":makeQuery(id+"F0Hq7nSFAMYVZvY_4.9.F20.boolean.opBoolean","SPLIT",FACE,{"disambiguationData":[TD([subQ7])],"derivedFrom":makeQuery(id+"F0Hq7nSFAMYVZvY_4.8.F20.boolean.opBoolean","SPLIT",FACE,{"disambiguationData":[TD([subQ7])],"derivedFrom":makeQuery(id+"F0Hq7nSFAMYVZvY_4.7.F20.boolean.opBoolean","SPLIT",FACE,{"disambiguationData":[TD([subQ7])],"derivedFrom":makeQuery(id+"F0Hq7nSFAMYVZvY_4.6.F20.boolean.opBoolean","SPLIT",FACE,{"disambiguationData":[TD([subQ7])],"derivedFrom":makeQuery(id+"F0Hq7nSFAMYVZvY_4.5.F20.boolean.opBoolean","SPLIT",FACE,{"disambiguationData":[TD([subQ7])],"derivedFrom":makeQuery(id+"F0Hq7nSFAMYVZvY_4.4.F20.boolean.opBoolean","SPLIT",FACE,{"disambiguationData":[TD([subQ7])],"derivedFrom":makeQuery(id+"F0Hq7nSFAMYVZvY_4.3.F20.boolean.opBoolean","SPLIT",FACE,{"disambiguationData":[TD([subQ7])],"derivedFrom":makeQuery(id+"F0Hq7nSFAMYVZvY_4.2.F20.boolean.opBoolean","SPLIT",FACE,{"disambiguationData":[TD([subQ7])],"derivedFrom":makeQuery(id+"F0Hq7nSFAMYVZvY_4.1.F20.boolean.opBoolean","SPLIT",FACE,{"disambiguationData":[TD([subQ7])],"derivedFrom":makeQuery(id+"F17.boolean.opBoolean","COPY",FACE,{"derivedFrom":makeQuery(id+"F17.opExtrude","CAP_FACE",FACE,{"disambiguationData":[OSD([subQ0,subQ2])],"isStart":false})})})})})})})})})})})})})})})})})})})})})})})})})})})})})})});}
            var Q118;
            Q118=makeQuery(id+"F0Hq7nSFAMYVZvY_4.29.F20.opExtrude","CAP_EDGE",EDGE,{"disambiguationData":[OSD([sQuery(id+"F19.wireOp",EDGE,"E157")])],"isStart":true});
            var Q119;
            {var subQ0=sQuery(id+"F19.wireOp",EDGE,"E158.MirrorCS");var subQ1=sQuery(id+"F19.wireOp",EDGE,"E157");var subQ3=sQuery(id+"F16.wireOp",EDGE,"E151");var subQ35=makeQuery(id+"F0Hq7nSFAMYVZvY_4.28.F20.opExtrude","SWEPT_FACE",FACE,{"disambiguationData":[OSD([subQ0])]});var subQ36=makeQuery(id+"F20.opExtrude","SWEPT_FACE",FACE,{"disambiguationData":[OSD([subQ1])]});Q119=makeQuery(id+"F0Hq7nSFAMYVZvY_4.29.F20.boolean.opBoolean","SPLIT",FACE,{"disambiguationData":[TD([subQ35])],"derivedFrom":makeQuery(id+"F0Hq7nSFAMYVZvY_4.28.F20.boolean.opBoolean","SPLIT",FACE,{"disambiguationData":[TD([subQ36])],"derivedFrom":makeQuery(id+"F0Hq7nSFAMYVZvY_4.27.F20.boolean.opBoolean","SPLIT",FACE,{"disambiguationData":[TD([subQ36])],"derivedFrom":makeQuery(id+"F0Hq7nSFAMYVZvY_4.26.F20.boolean.opBoolean","SPLIT",FACE,{"disambiguationData":[TD([subQ36])],"derivedFrom":makeQuery(id+"F0Hq7nSFAMYVZvY_4.25.F20.boolean.opBoolean","SPLIT",FACE,{"disambiguationData":[TD([subQ36])],"derivedFrom":makeQuery(id+"F0Hq7nSFAMYVZvY_4.24.F20.boolean.opBoolean","SPLIT",FACE,{"disambiguationData":[TD([subQ36])],"derivedFrom":makeQuery(id+"F0Hq7nSFAMYVZvY_4.23.F20.boolean.opBoolean","SPLIT",FACE,{"disambiguationData":[TD([subQ36])],"derivedFrom":makeQuery(id+"F0Hq7nSFAMYVZvY_4.22.F20.boolean.opBoolean","SPLIT",FACE,{"disambiguationData":[TD([subQ36])],"derivedFrom":makeQuery(id+"F0Hq7nSFAMYVZvY_4.21.F20.boolean.opBoolean","SPLIT",FACE,{"disambiguationData":[TD([subQ36])],"derivedFrom":makeQuery(id+"F0Hq7nSFAMYVZvY_4.20.F20.boolean.opBoolean","SPLIT",FACE,{"disambiguationData":[TD([subQ36])],"derivedFrom":makeQuery(id+"F0Hq7nSFAMYVZvY_4.19.F20.boolean.opBoolean","SPLIT",FACE,{"disambiguationData":[TD([subQ36])],"derivedFrom":makeQuery(id+"F0Hq7nSFAMYVZvY_4.18.F20.boolean.opBoolean","SPLIT",FACE,{"disambiguationData":[TD([subQ36])],"derivedFrom":makeQuery(id+"F0Hq7nSFAMYVZvY_4.17.F20.boolean.opBoolean","SPLIT",FACE,{"disambiguationData":[TD([subQ36])],"derivedFrom":makeQuery(id+"F0Hq7nSFAMYVZvY_4.16.F20.boolean.opBoolean","SPLIT",FACE,{"disambiguationData":[TD([subQ36])],"derivedFrom":makeQuery(id+"F0Hq7nSFAMYVZvY_4.15.F20.boolean.opBoolean","SPLIT",FACE,{"disambiguationData":[TD([subQ36])],"derivedFrom":makeQuery(id+"F0Hq7nSFAMYVZvY_4.14.F20.boolean.opBoolean","SPLIT",FACE,{"disambiguationData":[TD([subQ36])],"derivedFrom":makeQuery(id+"F0Hq7nSFAMYVZvY_4.13.F20.boolean.opBoolean","SPLIT",FACE,{"disambiguationData":[TD([subQ36])],"derivedFrom":makeQuery(id+"F0Hq7nSFAMYVZvY_4.12.F20.boolean.opBoolean","SPLIT",FACE,{"disambiguationData":[TD([subQ36])],"derivedFrom":makeQuery(id+"F0Hq7nSFAMYVZvY_4.11.F20.boolean.opBoolean","SPLIT",FACE,{"disambiguationData":[TD([subQ36])],"derivedFrom":makeQuery(id+"F0Hq7nSFAMYVZvY_4.10.F20.boolean.opBoolean","SPLIT",FACE,{"disambiguationData":[TD([subQ36])],"derivedFrom":makeQuery(id+"F0Hq7nSFAMYVZvY_4.9.F20.boolean.opBoolean","SPLIT",FACE,{"disambiguationData":[TD([subQ36])],"derivedFrom":makeQuery(id+"F0Hq7nSFAMYVZvY_4.8.F20.boolean.opBoolean","SPLIT",FACE,{"disambiguationData":[TD([subQ36])],"derivedFrom":makeQuery(id+"F0Hq7nSFAMYVZvY_4.7.F20.boolean.opBoolean","SPLIT",FACE,{"disambiguationData":[TD([subQ36])],"derivedFrom":makeQuery(id+"F0Hq7nSFAMYVZvY_4.6.F20.boolean.opBoolean","SPLIT",FACE,{"disambiguationData":[TD([subQ36])],"derivedFrom":makeQuery(id+"F0Hq7nSFAMYVZvY_4.5.F20.boolean.opBoolean","SPLIT",FACE,{"disambiguationData":[TD([subQ36])],"derivedFrom":makeQuery(id+"F0Hq7nSFAMYVZvY_4.4.F20.boolean.opBoolean","SPLIT",FACE,{"disambiguationData":[TD([subQ36])],"derivedFrom":makeQuery(id+"F0Hq7nSFAMYVZvY_4.3.F20.boolean.opBoolean","SPLIT",FACE,{"disambiguationData":[TD([subQ36])],"derivedFrom":makeQuery(id+"F0Hq7nSFAMYVZvY_4.2.F20.boolean.opBoolean","SPLIT",FACE,{"disambiguationData":[TD([subQ36])],"derivedFrom":makeQuery(id+"F0Hq7nSFAMYVZvY_4.1.F20.boolean.opBoolean","SPLIT",FACE,{"disambiguationData":[TD([subQ36])],"derivedFrom":makeQuery(id+"F17.boolean.opBoolean","COPY",FACE,{"derivedFrom":makeQuery(id+"F17.opExtrude","SWEPT_FACE",FACE,{"disambiguationData":[OSD([subQ3])]})})})})})})})})})})})})})})})})})})})})})})})})})})})})})})});}
            var Q120;
            {var subQ0=sQuery(id+"F19.wireOp",EDGE,"E158.MirrorCS");var subQ1=sQuery(id+"F19.wireOp",EDGE,"E157");var subQ3=sQuery(id+"F16.wireOp",EDGE,"E151");var subQ35=makeQuery(id+"F0Hq7nSFAMYVZvY_4.28.F20.opExtrude","SWEPT_FACE",FACE,{"disambiguationData":[OSD([subQ0])]});var subQ36=makeQuery(id+"F20.opExtrude","SWEPT_FACE",FACE,{"disambiguationData":[OSD([subQ1])]});Q120=makeQuery(id+"F0Hq7nSFAMYVZvY_4.29.F20.boolean.opBoolean","SPLIT",EDGE,{"disambiguationData":[TD([subQ35])],"derivedFrom":makeQuery(id+"F0Hq7nSFAMYVZvY_4.28.F20.boolean.opBoolean","SPLIT",EDGE,{"disambiguationData":[TD([subQ36])],"derivedFrom":makeQuery(id+"F0Hq7nSFAMYVZvY_4.27.F20.boolean.opBoolean","SPLIT",EDGE,{"disambiguationData":[TD([subQ36])],"derivedFrom":makeQuery(id+"F0Hq7nSFAMYVZvY_4.26.F20.boolean.opBoolean","SPLIT",EDGE,{"disambiguationData":[TD([subQ36])],"derivedFrom":makeQuery(id+"F0Hq7nSFAMYVZvY_4.25.F20.boolean.opBoolean","SPLIT",EDGE,{"disambiguationData":[TD([subQ36])],"derivedFrom":makeQuery(id+"F0Hq7nSFAMYVZvY_4.24.F20.boolean.opBoolean","SPLIT",EDGE,{"disambiguationData":[TD([subQ36])],"derivedFrom":makeQuery(id+"F0Hq7nSFAMYVZvY_4.23.F20.boolean.opBoolean","SPLIT",EDGE,{"disambiguationData":[TD([subQ36])],"derivedFrom":makeQuery(id+"F0Hq7nSFAMYVZvY_4.22.F20.boolean.opBoolean","SPLIT",EDGE,{"disambiguationData":[TD([subQ36])],"derivedFrom":makeQuery(id+"F0Hq7nSFAMYVZvY_4.21.F20.boolean.opBoolean","SPLIT",EDGE,{"disambiguationData":[TD([subQ36])],"derivedFrom":makeQuery(id+"F0Hq7nSFAMYVZvY_4.20.F20.boolean.opBoolean","SPLIT",EDGE,{"disambiguationData":[TD([subQ36])],"derivedFrom":makeQuery(id+"F0Hq7nSFAMYVZvY_4.19.F20.boolean.opBoolean","SPLIT",EDGE,{"disambiguationData":[TD([subQ36])],"derivedFrom":makeQuery(id+"F0Hq7nSFAMYVZvY_4.18.F20.boolean.opBoolean","SPLIT",EDGE,{"disambiguationData":[TD([subQ36])],"derivedFrom":makeQuery(id+"F0Hq7nSFAMYVZvY_4.17.F20.boolean.opBoolean","SPLIT",EDGE,{"disambiguationData":[TD([subQ36])],"derivedFrom":makeQuery(id+"F0Hq7nSFAMYVZvY_4.16.F20.boolean.opBoolean","SPLIT",EDGE,{"disambiguationData":[TD([subQ36])],"derivedFrom":makeQuery(id+"F0Hq7nSFAMYVZvY_4.15.F20.boolean.opBoolean","SPLIT",EDGE,{"disambiguationData":[TD([subQ36])],"derivedFrom":makeQuery(id+"F0Hq7nSFAMYVZvY_4.14.F20.boolean.opBoolean","SPLIT",EDGE,{"disambiguationData":[TD([subQ36])],"derivedFrom":makeQuery(id+"F0Hq7nSFAMYVZvY_4.13.F20.boolean.opBoolean","SPLIT",EDGE,{"disambiguationData":[TD([subQ36])],"derivedFrom":makeQuery(id+"F0Hq7nSFAMYVZvY_4.12.F20.boolean.opBoolean","SPLIT",EDGE,{"disambiguationData":[TD([subQ36])],"derivedFrom":makeQuery(id+"F0Hq7nSFAMYVZvY_4.11.F20.boolean.opBoolean","SPLIT",EDGE,{"disambiguationData":[TD([subQ36])],"derivedFrom":makeQuery(id+"F0Hq7nSFAMYVZvY_4.10.F20.boolean.opBoolean","SPLIT",EDGE,{"disambiguationData":[TD([subQ36])],"derivedFrom":makeQuery(id+"F0Hq7nSFAMYVZvY_4.9.F20.boolean.opBoolean","SPLIT",EDGE,{"disambiguationData":[TD([subQ36])],"derivedFrom":makeQuery(id+"F0Hq7nSFAMYVZvY_4.8.F20.boolean.opBoolean","SPLIT",EDGE,{"disambiguationData":[TD([subQ36])],"derivedFrom":makeQuery(id+"F0Hq7nSFAMYVZvY_4.7.F20.boolean.opBoolean","SPLIT",EDGE,{"disambiguationData":[TD([subQ36])],"derivedFrom":makeQuery(id+"F0Hq7nSFAMYVZvY_4.6.F20.boolean.opBoolean","SPLIT",EDGE,{"disambiguationData":[TD([subQ36])],"derivedFrom":makeQuery(id+"F0Hq7nSFAMYVZvY_4.5.F20.boolean.opBoolean","SPLIT",EDGE,{"disambiguationData":[TD([subQ36])],"derivedFrom":makeQuery(id+"F0Hq7nSFAMYVZvY_4.4.F20.boolean.opBoolean","SPLIT",EDGE,{"disambiguationData":[TD([subQ36])],"derivedFrom":makeQuery(id+"F0Hq7nSFAMYVZvY_4.3.F20.boolean.opBoolean","SPLIT",EDGE,{"disambiguationData":[TD([subQ36])],"derivedFrom":makeQuery(id+"F0Hq7nSFAMYVZvY_4.2.F20.boolean.opBoolean","SPLIT",EDGE,{"disambiguationData":[TD([subQ36])],"derivedFrom":makeQuery(id+"F0Hq7nSFAMYVZvY_4.1.F20.boolean.opBoolean","SPLIT",EDGE,{"disambiguationData":[TD([subQ36])],"derivedFrom":makeQuery(id+"F18.boolean.opBoolean","COPY",EDGE,{"derivedFrom":makeQuery(id+"F18.opExtrude","CAP_EDGE",EDGE,{"disambiguationData":[OSD([subQ3])],"isStart":false})})})})})})})})})})})})})})})})})})})})})})})})})})})})})})});}
            var Q121;
            Q121=makeQuery(id+"F0Hq7nSFAMYVZvY_4.30.F20.opExtrude","SWEPT_FACE",FACE,{"disambiguationData":[OSD([sQuery(id+"F19.wireOp",EDGE,"E157")])]});
            var Q122;
            {var subQ0=sQuery(id+"F16.wireOp",EDGE,"E151");var subQ2=sQuery(id+"F19.wireOp",EDGE,"E157");var subQ3=sQuery(id+"F16.wireOp",EDGE,"E152");var subQ5=sQuery(id+"F19.wireOp",EDGE,"E158.MirrorCS");var subQ6=makeQuery(id+"F0Hq7nSFAMYVZvY_4.29.F20.opExtrude","SWEPT_FACE",FACE,{"disambiguationData":[OSD([subQ5])]});var subQ7=makeQuery(id+"F20.opExtrude","SWEPT_FACE",FACE,{"disambiguationData":[OSD([subQ2])]});Q122=makeQuery(id+"F0Hq7nSFAMYVZvY_4.30.F20.boolean.opBoolean","SPLIT",FACE,{"disambiguationData":[TD([subQ6])],"derivedFrom":makeQuery(id+"F0Hq7nSFAMYVZvY_4.29.F20.boolean.opBoolean","SPLIT",FACE,{"disambiguationData":[TD([subQ7])],"derivedFrom":makeQuery(id+"F0Hq7nSFAMYVZvY_4.28.F20.boolean.opBoolean","SPLIT",FACE,{"disambiguationData":[TD([subQ7])],"derivedFrom":makeQuery(id+"F0Hq7nSFAMYVZvY_4.27.F20.boolean.opBoolean","SPLIT",FACE,{"disambiguationData":[TD([subQ7])],"derivedFrom":makeQuery(id+"F0Hq7nSFAMYVZvY_4.26.F20.boolean.opBoolean","SPLIT",FACE,{"disambiguationData":[TD([subQ7])],"derivedFrom":makeQuery(id+"F0Hq7nSFAMYVZvY_4.25.F20.boolean.opBoolean","SPLIT",FACE,{"disambiguationData":[TD([subQ7])],"derivedFrom":makeQuery(id+"F0Hq7nSFAMYVZvY_4.24.F20.boolean.opBoolean","SPLIT",FACE,{"disambiguationData":[TD([subQ7])],"derivedFrom":makeQuery(id+"F0Hq7nSFAMYVZvY_4.23.F20.boolean.opBoolean","SPLIT",FACE,{"disambiguationData":[TD([subQ7])],"derivedFrom":makeQuery(id+"F0Hq7nSFAMYVZvY_4.22.F20.boolean.opBoolean","SPLIT",FACE,{"disambiguationData":[TD([subQ7])],"derivedFrom":makeQuery(id+"F0Hq7nSFAMYVZvY_4.21.F20.boolean.opBoolean","SPLIT",FACE,{"disambiguationData":[TD([subQ7])],"derivedFrom":makeQuery(id+"F0Hq7nSFAMYVZvY_4.20.F20.boolean.opBoolean","SPLIT",FACE,{"disambiguationData":[TD([subQ7])],"derivedFrom":makeQuery(id+"F0Hq7nSFAMYVZvY_4.19.F20.boolean.opBoolean","SPLIT",FACE,{"disambiguationData":[TD([subQ7])],"derivedFrom":makeQuery(id+"F0Hq7nSFAMYVZvY_4.18.F20.boolean.opBoolean","SPLIT",FACE,{"disambiguationData":[TD([subQ7])],"derivedFrom":makeQuery(id+"F0Hq7nSFAMYVZvY_4.17.F20.boolean.opBoolean","SPLIT",FACE,{"disambiguationData":[TD([subQ7])],"derivedFrom":makeQuery(id+"F0Hq7nSFAMYVZvY_4.16.F20.boolean.opBoolean","SPLIT",FACE,{"disambiguationData":[TD([subQ7])],"derivedFrom":makeQuery(id+"F0Hq7nSFAMYVZvY_4.15.F20.boolean.opBoolean","SPLIT",FACE,{"disambiguationData":[TD([subQ7])],"derivedFrom":makeQuery(id+"F0Hq7nSFAMYVZvY_4.14.F20.boolean.opBoolean","SPLIT",FACE,{"disambiguationData":[TD([subQ7])],"derivedFrom":makeQuery(id+"F0Hq7nSFAMYVZvY_4.13.F20.boolean.opBoolean","SPLIT",FACE,{"disambiguationData":[TD([subQ7])],"derivedFrom":makeQuery(id+"F0Hq7nSFAMYVZvY_4.12.F20.boolean.opBoolean","SPLIT",FACE,{"disambiguationData":[TD([subQ7])],"derivedFrom":makeQuery(id+"F0Hq7nSFAMYVZvY_4.11.F20.boolean.opBoolean","SPLIT",FACE,{"disambiguationData":[TD([subQ7])],"derivedFrom":makeQuery(id+"F0Hq7nSFAMYVZvY_4.10.F20.boolean.opBoolean","SPLIT",FACE,{"disambiguationData":[TD([subQ7])],"derivedFrom":makeQuery(id+"F0Hq7nSFAMYVZvY_4.9.F20.boolean.opBoolean","SPLIT",FACE,{"disambiguationData":[TD([subQ7])],"derivedFrom":makeQuery(id+"F0Hq7nSFAMYVZvY_4.8.F20.boolean.opBoolean","SPLIT",FACE,{"disambiguationData":[TD([subQ7])],"derivedFrom":makeQuery(id+"F0Hq7nSFAMYVZvY_4.7.F20.boolean.opBoolean","SPLIT",FACE,{"disambiguationData":[TD([subQ7])],"derivedFrom":makeQuery(id+"F0Hq7nSFAMYVZvY_4.6.F20.boolean.opBoolean","SPLIT",FACE,{"disambiguationData":[TD([subQ7])],"derivedFrom":makeQuery(id+"F0Hq7nSFAMYVZvY_4.5.F20.boolean.opBoolean","SPLIT",FACE,{"disambiguationData":[TD([subQ7])],"derivedFrom":makeQuery(id+"F0Hq7nSFAMYVZvY_4.4.F20.boolean.opBoolean","SPLIT",FACE,{"disambiguationData":[TD([subQ7])],"derivedFrom":makeQuery(id+"F0Hq7nSFAMYVZvY_4.3.F20.boolean.opBoolean","SPLIT",FACE,{"disambiguationData":[TD([subQ7])],"derivedFrom":makeQuery(id+"F0Hq7nSFAMYVZvY_4.2.F20.boolean.opBoolean","SPLIT",FACE,{"disambiguationData":[TD([subQ7])],"derivedFrom":makeQuery(id+"F0Hq7nSFAMYVZvY_4.1.F20.boolean.opBoolean","SPLIT",FACE,{"disambiguationData":[TD([subQ7])],"derivedFrom":makeQuery(id+"F17.boolean.opBoolean","COPY",FACE,{"derivedFrom":makeQuery(id+"F17.opExtrude","CAP_FACE",FACE,{"disambiguationData":[OSD([subQ0,subQ3])],"isStart":false})})})})})})})})})})})})})})})})})})})})})})})})})})})})})})})});}
            var Q123;
            {var subQ0=sQuery(id+"F19.wireOp",EDGE,"E158.MirrorCS");var subQ1=sQuery(id+"F19.wireOp",EDGE,"E157");var subQ3=sQuery(id+"F16.wireOp",EDGE,"E151");var subQ36=makeQuery(id+"F0Hq7nSFAMYVZvY_4.29.F20.opExtrude","SWEPT_FACE",FACE,{"disambiguationData":[OSD([subQ0])]});var subQ37=makeQuery(id+"F20.opExtrude","SWEPT_FACE",FACE,{"disambiguationData":[OSD([subQ1])]});Q123=makeQuery(id+"F0Hq7nSFAMYVZvY_4.30.F20.boolean.opBoolean","SPLIT",FACE,{"disambiguationData":[TD([subQ36])],"derivedFrom":makeQuery(id+"F0Hq7nSFAMYVZvY_4.29.F20.boolean.opBoolean","SPLIT",FACE,{"disambiguationData":[TD([subQ37])],"derivedFrom":makeQuery(id+"F0Hq7nSFAMYVZvY_4.28.F20.boolean.opBoolean","SPLIT",FACE,{"disambiguationData":[TD([subQ37])],"derivedFrom":makeQuery(id+"F0Hq7nSFAMYVZvY_4.27.F20.boolean.opBoolean","SPLIT",FACE,{"disambiguationData":[TD([subQ37])],"derivedFrom":makeQuery(id+"F0Hq7nSFAMYVZvY_4.26.F20.boolean.opBoolean","SPLIT",FACE,{"disambiguationData":[TD([subQ37])],"derivedFrom":makeQuery(id+"F0Hq7nSFAMYVZvY_4.25.F20.boolean.opBoolean","SPLIT",FACE,{"disambiguationData":[TD([subQ37])],"derivedFrom":makeQuery(id+"F0Hq7nSFAMYVZvY_4.24.F20.boolean.opBoolean","SPLIT",FACE,{"disambiguationData":[TD([subQ37])],"derivedFrom":makeQuery(id+"F0Hq7nSFAMYVZvY_4.23.F20.boolean.opBoolean","SPLIT",FACE,{"disambiguationData":[TD([subQ37])],"derivedFrom":makeQuery(id+"F0Hq7nSFAMYVZvY_4.22.F20.boolean.opBoolean","SPLIT",FACE,{"disambiguationData":[TD([subQ37])],"derivedFrom":makeQuery(id+"F0Hq7nSFAMYVZvY_4.21.F20.boolean.opBoolean","SPLIT",FACE,{"disambiguationData":[TD([subQ37])],"derivedFrom":makeQuery(id+"F0Hq7nSFAMYVZvY_4.20.F20.boolean.opBoolean","SPLIT",FACE,{"disambiguationData":[TD([subQ37])],"derivedFrom":makeQuery(id+"F0Hq7nSFAMYVZvY_4.19.F20.boolean.opBoolean","SPLIT",FACE,{"disambiguationData":[TD([subQ37])],"derivedFrom":makeQuery(id+"F0Hq7nSFAMYVZvY_4.18.F20.boolean.opBoolean","SPLIT",FACE,{"disambiguationData":[TD([subQ37])],"derivedFrom":makeQuery(id+"F0Hq7nSFAMYVZvY_4.17.F20.boolean.opBoolean","SPLIT",FACE,{"disambiguationData":[TD([subQ37])],"derivedFrom":makeQuery(id+"F0Hq7nSFAMYVZvY_4.16.F20.boolean.opBoolean","SPLIT",FACE,{"disambiguationData":[TD([subQ37])],"derivedFrom":makeQuery(id+"F0Hq7nSFAMYVZvY_4.15.F20.boolean.opBoolean","SPLIT",FACE,{"disambiguationData":[TD([subQ37])],"derivedFrom":makeQuery(id+"F0Hq7nSFAMYVZvY_4.14.F20.boolean.opBoolean","SPLIT",FACE,{"disambiguationData":[TD([subQ37])],"derivedFrom":makeQuery(id+"F0Hq7nSFAMYVZvY_4.13.F20.boolean.opBoolean","SPLIT",FACE,{"disambiguationData":[TD([subQ37])],"derivedFrom":makeQuery(id+"F0Hq7nSFAMYVZvY_4.12.F20.boolean.opBoolean","SPLIT",FACE,{"disambiguationData":[TD([subQ37])],"derivedFrom":makeQuery(id+"F0Hq7nSFAMYVZvY_4.11.F20.boolean.opBoolean","SPLIT",FACE,{"disambiguationData":[TD([subQ37])],"derivedFrom":makeQuery(id+"F0Hq7nSFAMYVZvY_4.10.F20.boolean.opBoolean","SPLIT",FACE,{"disambiguationData":[TD([subQ37])],"derivedFrom":makeQuery(id+"F0Hq7nSFAMYVZvY_4.9.F20.boolean.opBoolean","SPLIT",FACE,{"disambiguationData":[TD([subQ37])],"derivedFrom":makeQuery(id+"F0Hq7nSFAMYVZvY_4.8.F20.boolean.opBoolean","SPLIT",FACE,{"disambiguationData":[TD([subQ37])],"derivedFrom":makeQuery(id+"F0Hq7nSFAMYVZvY_4.7.F20.boolean.opBoolean","SPLIT",FACE,{"disambiguationData":[TD([subQ37])],"derivedFrom":makeQuery(id+"F0Hq7nSFAMYVZvY_4.6.F20.boolean.opBoolean","SPLIT",FACE,{"disambiguationData":[TD([subQ37])],"derivedFrom":makeQuery(id+"F0Hq7nSFAMYVZvY_4.5.F20.boolean.opBoolean","SPLIT",FACE,{"disambiguationData":[TD([subQ37])],"derivedFrom":makeQuery(id+"F0Hq7nSFAMYVZvY_4.4.F20.boolean.opBoolean","SPLIT",FACE,{"disambiguationData":[TD([subQ37])],"derivedFrom":makeQuery(id+"F0Hq7nSFAMYVZvY_4.3.F20.boolean.opBoolean","SPLIT",FACE,{"disambiguationData":[TD([subQ37])],"derivedFrom":makeQuery(id+"F0Hq7nSFAMYVZvY_4.2.F20.boolean.opBoolean","SPLIT",FACE,{"disambiguationData":[TD([subQ37])],"derivedFrom":makeQuery(id+"F0Hq7nSFAMYVZvY_4.1.F20.boolean.opBoolean","SPLIT",FACE,{"disambiguationData":[TD([subQ37])],"derivedFrom":makeQuery(id+"F17.boolean.opBoolean","COPY",FACE,{"derivedFrom":makeQuery(id+"F17.opExtrude","SWEPT_FACE",FACE,{"disambiguationData":[OSD([subQ3])]})})})})})})})})})})})})})})})})})})})})})})})})})})})})})})})});}
            var Q124;
            {var subQ0=sQuery(id+"F19.wireOp",EDGE,"E158.MirrorCS");var subQ1=sQuery(id+"F19.wireOp",EDGE,"E157");var subQ3=sQuery(id+"F16.wireOp",EDGE,"E151");var subQ36=makeQuery(id+"F0Hq7nSFAMYVZvY_4.29.F20.opExtrude","SWEPT_FACE",FACE,{"disambiguationData":[OSD([subQ0])]});var subQ37=makeQuery(id+"F20.opExtrude","SWEPT_FACE",FACE,{"disambiguationData":[OSD([subQ1])]});Q124=makeQuery(id+"F0Hq7nSFAMYVZvY_4.30.F20.boolean.opBoolean","SPLIT",EDGE,{"disambiguationData":[TD([subQ36])],"derivedFrom":makeQuery(id+"F0Hq7nSFAMYVZvY_4.29.F20.boolean.opBoolean","SPLIT",EDGE,{"disambiguationData":[TD([subQ37])],"derivedFrom":makeQuery(id+"F0Hq7nSFAMYVZvY_4.28.F20.boolean.opBoolean","SPLIT",EDGE,{"disambiguationData":[TD([subQ37])],"derivedFrom":makeQuery(id+"F0Hq7nSFAMYVZvY_4.27.F20.boolean.opBoolean","SPLIT",EDGE,{"disambiguationData":[TD([subQ37])],"derivedFrom":makeQuery(id+"F0Hq7nSFAMYVZvY_4.26.F20.boolean.opBoolean","SPLIT",EDGE,{"disambiguationData":[TD([subQ37])],"derivedFrom":makeQuery(id+"F0Hq7nSFAMYVZvY_4.25.F20.boolean.opBoolean","SPLIT",EDGE,{"disambiguationData":[TD([subQ37])],"derivedFrom":makeQuery(id+"F0Hq7nSFAMYVZvY_4.24.F20.boolean.opBoolean","SPLIT",EDGE,{"disambiguationData":[TD([subQ37])],"derivedFrom":makeQuery(id+"F0Hq7nSFAMYVZvY_4.23.F20.boolean.opBoolean","SPLIT",EDGE,{"disambiguationData":[TD([subQ37])],"derivedFrom":makeQuery(id+"F0Hq7nSFAMYVZvY_4.22.F20.boolean.opBoolean","SPLIT",EDGE,{"disambiguationData":[TD([subQ37])],"derivedFrom":makeQuery(id+"F0Hq7nSFAMYVZvY_4.21.F20.boolean.opBoolean","SPLIT",EDGE,{"disambiguationData":[TD([subQ37])],"derivedFrom":makeQuery(id+"F0Hq7nSFAMYVZvY_4.20.F20.boolean.opBoolean","SPLIT",EDGE,{"disambiguationData":[TD([subQ37])],"derivedFrom":makeQuery(id+"F0Hq7nSFAMYVZvY_4.19.F20.boolean.opBoolean","SPLIT",EDGE,{"disambiguationData":[TD([subQ37])],"derivedFrom":makeQuery(id+"F0Hq7nSFAMYVZvY_4.18.F20.boolean.opBoolean","SPLIT",EDGE,{"disambiguationData":[TD([subQ37])],"derivedFrom":makeQuery(id+"F0Hq7nSFAMYVZvY_4.17.F20.boolean.opBoolean","SPLIT",EDGE,{"disambiguationData":[TD([subQ37])],"derivedFrom":makeQuery(id+"F0Hq7nSFAMYVZvY_4.16.F20.boolean.opBoolean","SPLIT",EDGE,{"disambiguationData":[TD([subQ37])],"derivedFrom":makeQuery(id+"F0Hq7nSFAMYVZvY_4.15.F20.boolean.opBoolean","SPLIT",EDGE,{"disambiguationData":[TD([subQ37])],"derivedFrom":makeQuery(id+"F0Hq7nSFAMYVZvY_4.14.F20.boolean.opBoolean","SPLIT",EDGE,{"disambiguationData":[TD([subQ37])],"derivedFrom":makeQuery(id+"F0Hq7nSFAMYVZvY_4.13.F20.boolean.opBoolean","SPLIT",EDGE,{"disambiguationData":[TD([subQ37])],"derivedFrom":makeQuery(id+"F0Hq7nSFAMYVZvY_4.12.F20.boolean.opBoolean","SPLIT",EDGE,{"disambiguationData":[TD([subQ37])],"derivedFrom":makeQuery(id+"F0Hq7nSFAMYVZvY_4.11.F20.boolean.opBoolean","SPLIT",EDGE,{"disambiguationData":[TD([subQ37])],"derivedFrom":makeQuery(id+"F0Hq7nSFAMYVZvY_4.10.F20.boolean.opBoolean","SPLIT",EDGE,{"disambiguationData":[TD([subQ37])],"derivedFrom":makeQuery(id+"F0Hq7nSFAMYVZvY_4.9.F20.boolean.opBoolean","SPLIT",EDGE,{"disambiguationData":[TD([subQ37])],"derivedFrom":makeQuery(id+"F0Hq7nSFAMYVZvY_4.8.F20.boolean.opBoolean","SPLIT",EDGE,{"disambiguationData":[TD([subQ37])],"derivedFrom":makeQuery(id+"F0Hq7nSFAMYVZvY_4.7.F20.boolean.opBoolean","SPLIT",EDGE,{"disambiguationData":[TD([subQ37])],"derivedFrom":makeQuery(id+"F0Hq7nSFAMYVZvY_4.6.F20.boolean.opBoolean","SPLIT",EDGE,{"disambiguationData":[TD([subQ37])],"derivedFrom":makeQuery(id+"F0Hq7nSFAMYVZvY_4.5.F20.boolean.opBoolean","SPLIT",EDGE,{"disambiguationData":[TD([subQ37])],"derivedFrom":makeQuery(id+"F0Hq7nSFAMYVZvY_4.4.F20.boolean.opBoolean","SPLIT",EDGE,{"disambiguationData":[TD([subQ37])],"derivedFrom":makeQuery(id+"F0Hq7nSFAMYVZvY_4.3.F20.boolean.opBoolean","SPLIT",EDGE,{"disambiguationData":[TD([subQ37])],"derivedFrom":makeQuery(id+"F0Hq7nSFAMYVZvY_4.2.F20.boolean.opBoolean","SPLIT",EDGE,{"disambiguationData":[TD([subQ37])],"derivedFrom":makeQuery(id+"F0Hq7nSFAMYVZvY_4.1.F20.boolean.opBoolean","SPLIT",EDGE,{"disambiguationData":[TD([subQ37])],"derivedFrom":makeQuery(id+"F18.boolean.opBoolean","COPY",EDGE,{"derivedFrom":makeQuery(id+"F18.opExtrude","CAP_EDGE",EDGE,{"disambiguationData":[OSD([subQ3])],"isStart":false})})})})})})})})})})})})})})})})})})})})})})})})})})})})})})})});}
            var Q125;
            Q125=makeQuery(id+"F0Hq7nSFAMYVZvY_4.31.F20.opExtrude","SWEPT_FACE",FACE,{"disambiguationData":[OSD([sQuery(id+"F19.wireOp",EDGE,"E157")])]});
            var Q126;
            {var subQ0=sQuery(id+"F16.wireOp",EDGE,"E151");var subQ2=sQuery(id+"F16.wireOp",EDGE,"E152");var subQ4=sQuery(id+"F19.wireOp",EDGE,"E157");var subQ5=sQuery(id+"F19.wireOp",EDGE,"E158.MirrorCS");var subQ6=makeQuery(id+"F0Hq7nSFAMYVZvY_4.30.F20.opExtrude","SWEPT_FACE",FACE,{"disambiguationData":[OSD([subQ5])]});var subQ7=makeQuery(id+"F20.opExtrude","SWEPT_FACE",FACE,{"disambiguationData":[OSD([subQ4])]});Q126=makeQuery(id+"F0Hq7nSFAMYVZvY_4.31.F20.boolean.opBoolean","SPLIT",FACE,{"disambiguationData":[TD([subQ6])],"derivedFrom":makeQuery(id+"F0Hq7nSFAMYVZvY_4.30.F20.boolean.opBoolean","SPLIT",FACE,{"disambiguationData":[TD([subQ7])],"derivedFrom":makeQuery(id+"F0Hq7nSFAMYVZvY_4.29.F20.boolean.opBoolean","SPLIT",FACE,{"disambiguationData":[TD([subQ7])],"derivedFrom":makeQuery(id+"F0Hq7nSFAMYVZvY_4.28.F20.boolean.opBoolean","SPLIT",FACE,{"disambiguationData":[TD([subQ7])],"derivedFrom":makeQuery(id+"F0Hq7nSFAMYVZvY_4.27.F20.boolean.opBoolean","SPLIT",FACE,{"disambiguationData":[TD([subQ7])],"derivedFrom":makeQuery(id+"F0Hq7nSFAMYVZvY_4.26.F20.boolean.opBoolean","SPLIT",FACE,{"disambiguationData":[TD([subQ7])],"derivedFrom":makeQuery(id+"F0Hq7nSFAMYVZvY_4.25.F20.boolean.opBoolean","SPLIT",FACE,{"disambiguationData":[TD([subQ7])],"derivedFrom":makeQuery(id+"F0Hq7nSFAMYVZvY_4.24.F20.boolean.opBoolean","SPLIT",FACE,{"disambiguationData":[TD([subQ7])],"derivedFrom":makeQuery(id+"F0Hq7nSFAMYVZvY_4.23.F20.boolean.opBoolean","SPLIT",FACE,{"disambiguationData":[TD([subQ7])],"derivedFrom":makeQuery(id+"F0Hq7nSFAMYVZvY_4.22.F20.boolean.opBoolean","SPLIT",FACE,{"disambiguationData":[TD([subQ7])],"derivedFrom":makeQuery(id+"F0Hq7nSFAMYVZvY_4.21.F20.boolean.opBoolean","SPLIT",FACE,{"disambiguationData":[TD([subQ7])],"derivedFrom":makeQuery(id+"F0Hq7nSFAMYVZvY_4.20.F20.boolean.opBoolean","SPLIT",FACE,{"disambiguationData":[TD([subQ7])],"derivedFrom":makeQuery(id+"F0Hq7nSFAMYVZvY_4.19.F20.boolean.opBoolean","SPLIT",FACE,{"disambiguationData":[TD([subQ7])],"derivedFrom":makeQuery(id+"F0Hq7nSFAMYVZvY_4.18.F20.boolean.opBoolean","SPLIT",FACE,{"disambiguationData":[TD([subQ7])],"derivedFrom":makeQuery(id+"F0Hq7nSFAMYVZvY_4.17.F20.boolean.opBoolean","SPLIT",FACE,{"disambiguationData":[TD([subQ7])],"derivedFrom":makeQuery(id+"F0Hq7nSFAMYVZvY_4.16.F20.boolean.opBoolean","SPLIT",FACE,{"disambiguationData":[TD([subQ7])],"derivedFrom":makeQuery(id+"F0Hq7nSFAMYVZvY_4.15.F20.boolean.opBoolean","SPLIT",FACE,{"disambiguationData":[TD([subQ7])],"derivedFrom":makeQuery(id+"F0Hq7nSFAMYVZvY_4.14.F20.boolean.opBoolean","SPLIT",FACE,{"disambiguationData":[TD([subQ7])],"derivedFrom":makeQuery(id+"F0Hq7nSFAMYVZvY_4.13.F20.boolean.opBoolean","SPLIT",FACE,{"disambiguationData":[TD([subQ7])],"derivedFrom":makeQuery(id+"F0Hq7nSFAMYVZvY_4.12.F20.boolean.opBoolean","SPLIT",FACE,{"disambiguationData":[TD([subQ7])],"derivedFrom":makeQuery(id+"F0Hq7nSFAMYVZvY_4.11.F20.boolean.opBoolean","SPLIT",FACE,{"disambiguationData":[TD([subQ7])],"derivedFrom":makeQuery(id+"F0Hq7nSFAMYVZvY_4.10.F20.boolean.opBoolean","SPLIT",FACE,{"disambiguationData":[TD([subQ7])],"derivedFrom":makeQuery(id+"F0Hq7nSFAMYVZvY_4.9.F20.boolean.opBoolean","SPLIT",FACE,{"disambiguationData":[TD([subQ7])],"derivedFrom":makeQuery(id+"F0Hq7nSFAMYVZvY_4.8.F20.boolean.opBoolean","SPLIT",FACE,{"disambiguationData":[TD([subQ7])],"derivedFrom":makeQuery(id+"F0Hq7nSFAMYVZvY_4.7.F20.boolean.opBoolean","SPLIT",FACE,{"disambiguationData":[TD([subQ7])],"derivedFrom":makeQuery(id+"F0Hq7nSFAMYVZvY_4.6.F20.boolean.opBoolean","SPLIT",FACE,{"disambiguationData":[TD([subQ7])],"derivedFrom":makeQuery(id+"F0Hq7nSFAMYVZvY_4.5.F20.boolean.opBoolean","SPLIT",FACE,{"disambiguationData":[TD([subQ7])],"derivedFrom":makeQuery(id+"F0Hq7nSFAMYVZvY_4.4.F20.boolean.opBoolean","SPLIT",FACE,{"disambiguationData":[TD([subQ7])],"derivedFrom":makeQuery(id+"F0Hq7nSFAMYVZvY_4.3.F20.boolean.opBoolean","SPLIT",FACE,{"disambiguationData":[TD([subQ7])],"derivedFrom":makeQuery(id+"F0Hq7nSFAMYVZvY_4.2.F20.boolean.opBoolean","SPLIT",FACE,{"disambiguationData":[TD([subQ7])],"derivedFrom":makeQuery(id+"F0Hq7nSFAMYVZvY_4.1.F20.boolean.opBoolean","SPLIT",FACE,{"disambiguationData":[TD([subQ7])],"derivedFrom":makeQuery(id+"F17.boolean.opBoolean","COPY",FACE,{"derivedFrom":makeQuery(id+"F17.opExtrude","CAP_FACE",FACE,{"disambiguationData":[OSD([subQ0,subQ2])],"isStart":false})})})})})})})})})})})})})})})})})})})})})})})})})})})})})})})})});}
            var Q127;
            {var subQ0=sQuery(id+"F19.wireOp",EDGE,"E158.MirrorCS");var subQ1=sQuery(id+"F19.wireOp",EDGE,"E157");var subQ3=sQuery(id+"F16.wireOp",EDGE,"E151");var subQ37=makeQuery(id+"F0Hq7nSFAMYVZvY_4.30.F20.opExtrude","SWEPT_FACE",FACE,{"disambiguationData":[OSD([subQ0])]});var subQ38=makeQuery(id+"F20.opExtrude","SWEPT_FACE",FACE,{"disambiguationData":[OSD([subQ1])]});Q127=makeQuery(id+"F0Hq7nSFAMYVZvY_4.31.F20.boolean.opBoolean","SPLIT",FACE,{"disambiguationData":[TD([subQ37])],"derivedFrom":makeQuery(id+"F0Hq7nSFAMYVZvY_4.30.F20.boolean.opBoolean","SPLIT",FACE,{"disambiguationData":[TD([subQ38])],"derivedFrom":makeQuery(id+"F0Hq7nSFAMYVZvY_4.29.F20.boolean.opBoolean","SPLIT",FACE,{"disambiguationData":[TD([subQ38])],"derivedFrom":makeQuery(id+"F0Hq7nSFAMYVZvY_4.28.F20.boolean.opBoolean","SPLIT",FACE,{"disambiguationData":[TD([subQ38])],"derivedFrom":makeQuery(id+"F0Hq7nSFAMYVZvY_4.27.F20.boolean.opBoolean","SPLIT",FACE,{"disambiguationData":[TD([subQ38])],"derivedFrom":makeQuery(id+"F0Hq7nSFAMYVZvY_4.26.F20.boolean.opBoolean","SPLIT",FACE,{"disambiguationData":[TD([subQ38])],"derivedFrom":makeQuery(id+"F0Hq7nSFAMYVZvY_4.25.F20.boolean.opBoolean","SPLIT",FACE,{"disambiguationData":[TD([subQ38])],"derivedFrom":makeQuery(id+"F0Hq7nSFAMYVZvY_4.24.F20.boolean.opBoolean","SPLIT",FACE,{"disambiguationData":[TD([subQ38])],"derivedFrom":makeQuery(id+"F0Hq7nSFAMYVZvY_4.23.F20.boolean.opBoolean","SPLIT",FACE,{"disambiguationData":[TD([subQ38])],"derivedFrom":makeQuery(id+"F0Hq7nSFAMYVZvY_4.22.F20.boolean.opBoolean","SPLIT",FACE,{"disambiguationData":[TD([subQ38])],"derivedFrom":makeQuery(id+"F0Hq7nSFAMYVZvY_4.21.F20.boolean.opBoolean","SPLIT",FACE,{"disambiguationData":[TD([subQ38])],"derivedFrom":makeQuery(id+"F0Hq7nSFAMYVZvY_4.20.F20.boolean.opBoolean","SPLIT",FACE,{"disambiguationData":[TD([subQ38])],"derivedFrom":makeQuery(id+"F0Hq7nSFAMYVZvY_4.19.F20.boolean.opBoolean","SPLIT",FACE,{"disambiguationData":[TD([subQ38])],"derivedFrom":makeQuery(id+"F0Hq7nSFAMYVZvY_4.18.F20.boolean.opBoolean","SPLIT",FACE,{"disambiguationData":[TD([subQ38])],"derivedFrom":makeQuery(id+"F0Hq7nSFAMYVZvY_4.17.F20.boolean.opBoolean","SPLIT",FACE,{"disambiguationData":[TD([subQ38])],"derivedFrom":makeQuery(id+"F0Hq7nSFAMYVZvY_4.16.F20.boolean.opBoolean","SPLIT",FACE,{"disambiguationData":[TD([subQ38])],"derivedFrom":makeQuery(id+"F0Hq7nSFAMYVZvY_4.15.F20.boolean.opBoolean","SPLIT",FACE,{"disambiguationData":[TD([subQ38])],"derivedFrom":makeQuery(id+"F0Hq7nSFAMYVZvY_4.14.F20.boolean.opBoolean","SPLIT",FACE,{"disambiguationData":[TD([subQ38])],"derivedFrom":makeQuery(id+"F0Hq7nSFAMYVZvY_4.13.F20.boolean.opBoolean","SPLIT",FACE,{"disambiguationData":[TD([subQ38])],"derivedFrom":makeQuery(id+"F0Hq7nSFAMYVZvY_4.12.F20.boolean.opBoolean","SPLIT",FACE,{"disambiguationData":[TD([subQ38])],"derivedFrom":makeQuery(id+"F0Hq7nSFAMYVZvY_4.11.F20.boolean.opBoolean","SPLIT",FACE,{"disambiguationData":[TD([subQ38])],"derivedFrom":makeQuery(id+"F0Hq7nSFAMYVZvY_4.10.F20.boolean.opBoolean","SPLIT",FACE,{"disambiguationData":[TD([subQ38])],"derivedFrom":makeQuery(id+"F0Hq7nSFAMYVZvY_4.9.F20.boolean.opBoolean","SPLIT",FACE,{"disambiguationData":[TD([subQ38])],"derivedFrom":makeQuery(id+"F0Hq7nSFAMYVZvY_4.8.F20.boolean.opBoolean","SPLIT",FACE,{"disambiguationData":[TD([subQ38])],"derivedFrom":makeQuery(id+"F0Hq7nSFAMYVZvY_4.7.F20.boolean.opBoolean","SPLIT",FACE,{"disambiguationData":[TD([subQ38])],"derivedFrom":makeQuery(id+"F0Hq7nSFAMYVZvY_4.6.F20.boolean.opBoolean","SPLIT",FACE,{"disambiguationData":[TD([subQ38])],"derivedFrom":makeQuery(id+"F0Hq7nSFAMYVZvY_4.5.F20.boolean.opBoolean","SPLIT",FACE,{"disambiguationData":[TD([subQ38])],"derivedFrom":makeQuery(id+"F0Hq7nSFAMYVZvY_4.4.F20.boolean.opBoolean","SPLIT",FACE,{"disambiguationData":[TD([subQ38])],"derivedFrom":makeQuery(id+"F0Hq7nSFAMYVZvY_4.3.F20.boolean.opBoolean","SPLIT",FACE,{"disambiguationData":[TD([subQ38])],"derivedFrom":makeQuery(id+"F0Hq7nSFAMYVZvY_4.2.F20.boolean.opBoolean","SPLIT",FACE,{"disambiguationData":[TD([subQ38])],"derivedFrom":makeQuery(id+"F0Hq7nSFAMYVZvY_4.1.F20.boolean.opBoolean","SPLIT",FACE,{"disambiguationData":[TD([subQ38])],"derivedFrom":makeQuery(id+"F17.boolean.opBoolean","COPY",FACE,{"derivedFrom":makeQuery(id+"F17.opExtrude","SWEPT_FACE",FACE,{"disambiguationData":[OSD([subQ3])]})})})})})})})})})})})})})})})})})})})})})})})})})})})})})})})})});}
            var Q128;
            {var subQ0=sQuery(id+"F19.wireOp",EDGE,"E158.MirrorCS");var subQ1=sQuery(id+"F19.wireOp",EDGE,"E157");var subQ3=sQuery(id+"F16.wireOp",EDGE,"E151");var subQ37=makeQuery(id+"F0Hq7nSFAMYVZvY_4.30.F20.opExtrude","SWEPT_FACE",FACE,{"disambiguationData":[OSD([subQ0])]});var subQ38=makeQuery(id+"F20.opExtrude","SWEPT_FACE",FACE,{"disambiguationData":[OSD([subQ1])]});Q128=makeQuery(id+"F0Hq7nSFAMYVZvY_4.31.F20.boolean.opBoolean","SPLIT",EDGE,{"disambiguationData":[TD([subQ37])],"derivedFrom":makeQuery(id+"F0Hq7nSFAMYVZvY_4.30.F20.boolean.opBoolean","SPLIT",EDGE,{"disambiguationData":[TD([subQ38])],"derivedFrom":makeQuery(id+"F0Hq7nSFAMYVZvY_4.29.F20.boolean.opBoolean","SPLIT",EDGE,{"disambiguationData":[TD([subQ38])],"derivedFrom":makeQuery(id+"F0Hq7nSFAMYVZvY_4.28.F20.boolean.opBoolean","SPLIT",EDGE,{"disambiguationData":[TD([subQ38])],"derivedFrom":makeQuery(id+"F0Hq7nSFAMYVZvY_4.27.F20.boolean.opBoolean","SPLIT",EDGE,{"disambiguationData":[TD([subQ38])],"derivedFrom":makeQuery(id+"F0Hq7nSFAMYVZvY_4.26.F20.boolean.opBoolean","SPLIT",EDGE,{"disambiguationData":[TD([subQ38])],"derivedFrom":makeQuery(id+"F0Hq7nSFAMYVZvY_4.25.F20.boolean.opBoolean","SPLIT",EDGE,{"disambiguationData":[TD([subQ38])],"derivedFrom":makeQuery(id+"F0Hq7nSFAMYVZvY_4.24.F20.boolean.opBoolean","SPLIT",EDGE,{"disambiguationData":[TD([subQ38])],"derivedFrom":makeQuery(id+"F0Hq7nSFAMYVZvY_4.23.F20.boolean.opBoolean","SPLIT",EDGE,{"disambiguationData":[TD([subQ38])],"derivedFrom":makeQuery(id+"F0Hq7nSFAMYVZvY_4.22.F20.boolean.opBoolean","SPLIT",EDGE,{"disambiguationData":[TD([subQ38])],"derivedFrom":makeQuery(id+"F0Hq7nSFAMYVZvY_4.21.F20.boolean.opBoolean","SPLIT",EDGE,{"disambiguationData":[TD([subQ38])],"derivedFrom":makeQuery(id+"F0Hq7nSFAMYVZvY_4.20.F20.boolean.opBoolean","SPLIT",EDGE,{"disambiguationData":[TD([subQ38])],"derivedFrom":makeQuery(id+"F0Hq7nSFAMYVZvY_4.19.F20.boolean.opBoolean","SPLIT",EDGE,{"disambiguationData":[TD([subQ38])],"derivedFrom":makeQuery(id+"F0Hq7nSFAMYVZvY_4.18.F20.boolean.opBoolean","SPLIT",EDGE,{"disambiguationData":[TD([subQ38])],"derivedFrom":makeQuery(id+"F0Hq7nSFAMYVZvY_4.17.F20.boolean.opBoolean","SPLIT",EDGE,{"disambiguationData":[TD([subQ38])],"derivedFrom":makeQuery(id+"F0Hq7nSFAMYVZvY_4.16.F20.boolean.opBoolean","SPLIT",EDGE,{"disambiguationData":[TD([subQ38])],"derivedFrom":makeQuery(id+"F0Hq7nSFAMYVZvY_4.15.F20.boolean.opBoolean","SPLIT",EDGE,{"disambiguationData":[TD([subQ38])],"derivedFrom":makeQuery(id+"F0Hq7nSFAMYVZvY_4.14.F20.boolean.opBoolean","SPLIT",EDGE,{"disambiguationData":[TD([subQ38])],"derivedFrom":makeQuery(id+"F0Hq7nSFAMYVZvY_4.13.F20.boolean.opBoolean","SPLIT",EDGE,{"disambiguationData":[TD([subQ38])],"derivedFrom":makeQuery(id+"F0Hq7nSFAMYVZvY_4.12.F20.boolean.opBoolean","SPLIT",EDGE,{"disambiguationData":[TD([subQ38])],"derivedFrom":makeQuery(id+"F0Hq7nSFAMYVZvY_4.11.F20.boolean.opBoolean","SPLIT",EDGE,{"disambiguationData":[TD([subQ38])],"derivedFrom":makeQuery(id+"F0Hq7nSFAMYVZvY_4.10.F20.boolean.opBoolean","SPLIT",EDGE,{"disambiguationData":[TD([subQ38])],"derivedFrom":makeQuery(id+"F0Hq7nSFAMYVZvY_4.9.F20.boolean.opBoolean","SPLIT",EDGE,{"disambiguationData":[TD([subQ38])],"derivedFrom":makeQuery(id+"F0Hq7nSFAMYVZvY_4.8.F20.boolean.opBoolean","SPLIT",EDGE,{"disambiguationData":[TD([subQ38])],"derivedFrom":makeQuery(id+"F0Hq7nSFAMYVZvY_4.7.F20.boolean.opBoolean","SPLIT",EDGE,{"disambiguationData":[TD([subQ38])],"derivedFrom":makeQuery(id+"F0Hq7nSFAMYVZvY_4.6.F20.boolean.opBoolean","SPLIT",EDGE,{"disambiguationData":[TD([subQ38])],"derivedFrom":makeQuery(id+"F0Hq7nSFAMYVZvY_4.5.F20.boolean.opBoolean","SPLIT",EDGE,{"disambiguationData":[TD([subQ38])],"derivedFrom":makeQuery(id+"F0Hq7nSFAMYVZvY_4.4.F20.boolean.opBoolean","SPLIT",EDGE,{"disambiguationData":[TD([subQ38])],"derivedFrom":makeQuery(id+"F0Hq7nSFAMYVZvY_4.3.F20.boolean.opBoolean","SPLIT",EDGE,{"disambiguationData":[TD([subQ38])],"derivedFrom":makeQuery(id+"F0Hq7nSFAMYVZvY_4.2.F20.boolean.opBoolean","SPLIT",EDGE,{"disambiguationData":[TD([subQ38])],"derivedFrom":makeQuery(id+"F0Hq7nSFAMYVZvY_4.1.F20.boolean.opBoolean","SPLIT",EDGE,{"disambiguationData":[TD([subQ38])],"derivedFrom":makeQuery(id+"F18.boolean.opBoolean","COPY",EDGE,{"derivedFrom":makeQuery(id+"F18.opExtrude","CAP_EDGE",EDGE,{"disambiguationData":[OSD([subQ3])],"isStart":false})})})})})})})})})})})})})})})})})})})})})})})})})})})})})})})})});}
            var Q129;
            Q129=makeQuery(id+"F0Hq7nSFAMYVZvY_4.32.F20.opExtrude","SWEPT_FACE",FACE,{"disambiguationData":[OSD([sQuery(id+"F19.wireOp",EDGE,"E157")])]});
            var Q130;
            {var subQ0=sQuery(id+"F16.wireOp",EDGE,"E151");var subQ2=sQuery(id+"F19.wireOp",EDGE,"E158.MirrorCS");var subQ3=makeQuery(id+"F0Hq7nSFAMYVZvY_4.31.F20.opExtrude","SWEPT_FACE",FACE,{"disambiguationData":[OSD([subQ2])]});var subQ4=sQuery(id+"F16.wireOp",EDGE,"E152");var subQ6=sQuery(id+"F19.wireOp",EDGE,"E157");var subQ7=makeQuery(id+"F20.opExtrude","SWEPT_FACE",FACE,{"disambiguationData":[OSD([subQ6])]});Q130=makeQuery(id+"F0Hq7nSFAMYVZvY_4.32.F20.boolean.opBoolean","SPLIT",FACE,{"disambiguationData":[TD([subQ3])],"derivedFrom":makeQuery(id+"F0Hq7nSFAMYVZvY_4.31.F20.boolean.opBoolean","SPLIT",FACE,{"disambiguationData":[TD([subQ7])],"derivedFrom":makeQuery(id+"F0Hq7nSFAMYVZvY_4.30.F20.boolean.opBoolean","SPLIT",FACE,{"disambiguationData":[TD([subQ7])],"derivedFrom":makeQuery(id+"F0Hq7nSFAMYVZvY_4.29.F20.boolean.opBoolean","SPLIT",FACE,{"disambiguationData":[TD([subQ7])],"derivedFrom":makeQuery(id+"F0Hq7nSFAMYVZvY_4.28.F20.boolean.opBoolean","SPLIT",FACE,{"disambiguationData":[TD([subQ7])],"derivedFrom":makeQuery(id+"F0Hq7nSFAMYVZvY_4.27.F20.boolean.opBoolean","SPLIT",FACE,{"disambiguationData":[TD([subQ7])],"derivedFrom":makeQuery(id+"F0Hq7nSFAMYVZvY_4.26.F20.boolean.opBoolean","SPLIT",FACE,{"disambiguationData":[TD([subQ7])],"derivedFrom":makeQuery(id+"F0Hq7nSFAMYVZvY_4.25.F20.boolean.opBoolean","SPLIT",FACE,{"disambiguationData":[TD([subQ7])],"derivedFrom":makeQuery(id+"F0Hq7nSFAMYVZvY_4.24.F20.boolean.opBoolean","SPLIT",FACE,{"disambiguationData":[TD([subQ7])],"derivedFrom":makeQuery(id+"F0Hq7nSFAMYVZvY_4.23.F20.boolean.opBoolean","SPLIT",FACE,{"disambiguationData":[TD([subQ7])],"derivedFrom":makeQuery(id+"F0Hq7nSFAMYVZvY_4.22.F20.boolean.opBoolean","SPLIT",FACE,{"disambiguationData":[TD([subQ7])],"derivedFrom":makeQuery(id+"F0Hq7nSFAMYVZvY_4.21.F20.boolean.opBoolean","SPLIT",FACE,{"disambiguationData":[TD([subQ7])],"derivedFrom":makeQuery(id+"F0Hq7nSFAMYVZvY_4.20.F20.boolean.opBoolean","SPLIT",FACE,{"disambiguationData":[TD([subQ7])],"derivedFrom":makeQuery(id+"F0Hq7nSFAMYVZvY_4.19.F20.boolean.opBoolean","SPLIT",FACE,{"disambiguationData":[TD([subQ7])],"derivedFrom":makeQuery(id+"F0Hq7nSFAMYVZvY_4.18.F20.boolean.opBoolean","SPLIT",FACE,{"disambiguationData":[TD([subQ7])],"derivedFrom":makeQuery(id+"F0Hq7nSFAMYVZvY_4.17.F20.boolean.opBoolean","SPLIT",FACE,{"disambiguationData":[TD([subQ7])],"derivedFrom":makeQuery(id+"F0Hq7nSFAMYVZvY_4.16.F20.boolean.opBoolean","SPLIT",FACE,{"disambiguationData":[TD([subQ7])],"derivedFrom":makeQuery(id+"F0Hq7nSFAMYVZvY_4.15.F20.boolean.opBoolean","SPLIT",FACE,{"disambiguationData":[TD([subQ7])],"derivedFrom":makeQuery(id+"F0Hq7nSFAMYVZvY_4.14.F20.boolean.opBoolean","SPLIT",FACE,{"disambiguationData":[TD([subQ7])],"derivedFrom":makeQuery(id+"F0Hq7nSFAMYVZvY_4.13.F20.boolean.opBoolean","SPLIT",FACE,{"disambiguationData":[TD([subQ7])],"derivedFrom":makeQuery(id+"F0Hq7nSFAMYVZvY_4.12.F20.boolean.opBoolean","SPLIT",FACE,{"disambiguationData":[TD([subQ7])],"derivedFrom":makeQuery(id+"F0Hq7nSFAMYVZvY_4.11.F20.boolean.opBoolean","SPLIT",FACE,{"disambiguationData":[TD([subQ7])],"derivedFrom":makeQuery(id+"F0Hq7nSFAMYVZvY_4.10.F20.boolean.opBoolean","SPLIT",FACE,{"disambiguationData":[TD([subQ7])],"derivedFrom":makeQuery(id+"F0Hq7nSFAMYVZvY_4.9.F20.boolean.opBoolean","SPLIT",FACE,{"disambiguationData":[TD([subQ7])],"derivedFrom":makeQuery(id+"F0Hq7nSFAMYVZvY_4.8.F20.boolean.opBoolean","SPLIT",FACE,{"disambiguationData":[TD([subQ7])],"derivedFrom":makeQuery(id+"F0Hq7nSFAMYVZvY_4.7.F20.boolean.opBoolean","SPLIT",FACE,{"disambiguationData":[TD([subQ7])],"derivedFrom":makeQuery(id+"F0Hq7nSFAMYVZvY_4.6.F20.boolean.opBoolean","SPLIT",FACE,{"disambiguationData":[TD([subQ7])],"derivedFrom":makeQuery(id+"F0Hq7nSFAMYVZvY_4.5.F20.boolean.opBoolean","SPLIT",FACE,{"disambiguationData":[TD([subQ7])],"derivedFrom":makeQuery(id+"F0Hq7nSFAMYVZvY_4.4.F20.boolean.opBoolean","SPLIT",FACE,{"disambiguationData":[TD([subQ7])],"derivedFrom":makeQuery(id+"F0Hq7nSFAMYVZvY_4.3.F20.boolean.opBoolean","SPLIT",FACE,{"disambiguationData":[TD([subQ7])],"derivedFrom":makeQuery(id+"F0Hq7nSFAMYVZvY_4.2.F20.boolean.opBoolean","SPLIT",FACE,{"disambiguationData":[TD([subQ7])],"derivedFrom":makeQuery(id+"F0Hq7nSFAMYVZvY_4.1.F20.boolean.opBoolean","SPLIT",FACE,{"disambiguationData":[TD([subQ7])],"derivedFrom":makeQuery(id+"F17.boolean.opBoolean","COPY",FACE,{"derivedFrom":makeQuery(id+"F17.opExtrude","CAP_FACE",FACE,{"disambiguationData":[OSD([subQ0,subQ4])],"isStart":false})})})})})})})})})})})})})})})})})})})})})})})})})})})})})})})})})});}
            var Q131;
            {var subQ0=sQuery(id+"F19.wireOp",EDGE,"E158.MirrorCS");var subQ1=sQuery(id+"F19.wireOp",EDGE,"E157");var subQ3=sQuery(id+"F16.wireOp",EDGE,"E151");var subQ19=makeQuery(id+"F0Hq7nSFAMYVZvY_4.31.F20.opExtrude","SWEPT_FACE",FACE,{"disambiguationData":[OSD([subQ0])]});var subQ39=makeQuery(id+"F20.opExtrude","SWEPT_FACE",FACE,{"disambiguationData":[OSD([subQ1])]});Q131=makeQuery(id+"F0Hq7nSFAMYVZvY_4.32.F20.boolean.opBoolean","SPLIT",FACE,{"disambiguationData":[TD([subQ19])],"derivedFrom":makeQuery(id+"F0Hq7nSFAMYVZvY_4.31.F20.boolean.opBoolean","SPLIT",FACE,{"disambiguationData":[TD([subQ39])],"derivedFrom":makeQuery(id+"F0Hq7nSFAMYVZvY_4.30.F20.boolean.opBoolean","SPLIT",FACE,{"disambiguationData":[TD([subQ39])],"derivedFrom":makeQuery(id+"F0Hq7nSFAMYVZvY_4.29.F20.boolean.opBoolean","SPLIT",FACE,{"disambiguationData":[TD([subQ39])],"derivedFrom":makeQuery(id+"F0Hq7nSFAMYVZvY_4.28.F20.boolean.opBoolean","SPLIT",FACE,{"disambiguationData":[TD([subQ39])],"derivedFrom":makeQuery(id+"F0Hq7nSFAMYVZvY_4.27.F20.boolean.opBoolean","SPLIT",FACE,{"disambiguationData":[TD([subQ39])],"derivedFrom":makeQuery(id+"F0Hq7nSFAMYVZvY_4.26.F20.boolean.opBoolean","SPLIT",FACE,{"disambiguationData":[TD([subQ39])],"derivedFrom":makeQuery(id+"F0Hq7nSFAMYVZvY_4.25.F20.boolean.opBoolean","SPLIT",FACE,{"disambiguationData":[TD([subQ39])],"derivedFrom":makeQuery(id+"F0Hq7nSFAMYVZvY_4.24.F20.boolean.opBoolean","SPLIT",FACE,{"disambiguationData":[TD([subQ39])],"derivedFrom":makeQuery(id+"F0Hq7nSFAMYVZvY_4.23.F20.boolean.opBoolean","SPLIT",FACE,{"disambiguationData":[TD([subQ39])],"derivedFrom":makeQuery(id+"F0Hq7nSFAMYVZvY_4.22.F20.boolean.opBoolean","SPLIT",FACE,{"disambiguationData":[TD([subQ39])],"derivedFrom":makeQuery(id+"F0Hq7nSFAMYVZvY_4.21.F20.boolean.opBoolean","SPLIT",FACE,{"disambiguationData":[TD([subQ39])],"derivedFrom":makeQuery(id+"F0Hq7nSFAMYVZvY_4.20.F20.boolean.opBoolean","SPLIT",FACE,{"disambiguationData":[TD([subQ39])],"derivedFrom":makeQuery(id+"F0Hq7nSFAMYVZvY_4.19.F20.boolean.opBoolean","SPLIT",FACE,{"disambiguationData":[TD([subQ39])],"derivedFrom":makeQuery(id+"F0Hq7nSFAMYVZvY_4.18.F20.boolean.opBoolean","SPLIT",FACE,{"disambiguationData":[TD([subQ39])],"derivedFrom":makeQuery(id+"F0Hq7nSFAMYVZvY_4.17.F20.boolean.opBoolean","SPLIT",FACE,{"disambiguationData":[TD([subQ39])],"derivedFrom":makeQuery(id+"F0Hq7nSFAMYVZvY_4.16.F20.boolean.opBoolean","SPLIT",FACE,{"disambiguationData":[TD([subQ39])],"derivedFrom":makeQuery(id+"F0Hq7nSFAMYVZvY_4.15.F20.boolean.opBoolean","SPLIT",FACE,{"disambiguationData":[TD([subQ39])],"derivedFrom":makeQuery(id+"F0Hq7nSFAMYVZvY_4.14.F20.boolean.opBoolean","SPLIT",FACE,{"disambiguationData":[TD([subQ39])],"derivedFrom":makeQuery(id+"F0Hq7nSFAMYVZvY_4.13.F20.boolean.opBoolean","SPLIT",FACE,{"disambiguationData":[TD([subQ39])],"derivedFrom":makeQuery(id+"F0Hq7nSFAMYVZvY_4.12.F20.boolean.opBoolean","SPLIT",FACE,{"disambiguationData":[TD([subQ39])],"derivedFrom":makeQuery(id+"F0Hq7nSFAMYVZvY_4.11.F20.boolean.opBoolean","SPLIT",FACE,{"disambiguationData":[TD([subQ39])],"derivedFrom":makeQuery(id+"F0Hq7nSFAMYVZvY_4.10.F20.boolean.opBoolean","SPLIT",FACE,{"disambiguationData":[TD([subQ39])],"derivedFrom":makeQuery(id+"F0Hq7nSFAMYVZvY_4.9.F20.boolean.opBoolean","SPLIT",FACE,{"disambiguationData":[TD([subQ39])],"derivedFrom":makeQuery(id+"F0Hq7nSFAMYVZvY_4.8.F20.boolean.opBoolean","SPLIT",FACE,{"disambiguationData":[TD([subQ39])],"derivedFrom":makeQuery(id+"F0Hq7nSFAMYVZvY_4.7.F20.boolean.opBoolean","SPLIT",FACE,{"disambiguationData":[TD([subQ39])],"derivedFrom":makeQuery(id+"F0Hq7nSFAMYVZvY_4.6.F20.boolean.opBoolean","SPLIT",FACE,{"disambiguationData":[TD([subQ39])],"derivedFrom":makeQuery(id+"F0Hq7nSFAMYVZvY_4.5.F20.boolean.opBoolean","SPLIT",FACE,{"disambiguationData":[TD([subQ39])],"derivedFrom":makeQuery(id+"F0Hq7nSFAMYVZvY_4.4.F20.boolean.opBoolean","SPLIT",FACE,{"disambiguationData":[TD([subQ39])],"derivedFrom":makeQuery(id+"F0Hq7nSFAMYVZvY_4.3.F20.boolean.opBoolean","SPLIT",FACE,{"disambiguationData":[TD([subQ39])],"derivedFrom":makeQuery(id+"F0Hq7nSFAMYVZvY_4.2.F20.boolean.opBoolean","SPLIT",FACE,{"disambiguationData":[TD([subQ39])],"derivedFrom":makeQuery(id+"F0Hq7nSFAMYVZvY_4.1.F20.boolean.opBoolean","SPLIT",FACE,{"disambiguationData":[TD([subQ39])],"derivedFrom":makeQuery(id+"F17.boolean.opBoolean","COPY",FACE,{"derivedFrom":makeQuery(id+"F17.opExtrude","SWEPT_FACE",FACE,{"disambiguationData":[OSD([subQ3])]})})})})})})})})})})})})})})})})})})})})})})})})})})})})})})})})})});}
            var Q132;
            Q132=makeQuery(id+"F0Hq7nSFAMYVZvY_4.1.F20.opExtrude","SWEPT_FACE",FACE,{"disambiguationData":[OSD([sQuery(id+"F19.wireOp",EDGE,"E157")])]});
            var Q133;
            Q133=makeQuery(id+"F0Hq7nSFAMYVZvY_4.1.F20.opExtrude","SWEPT_FACE",FACE,{"disambiguationData":[OSD([sQuery(id+"F19.wireOp",EDGE,"E158.MirrorCS")])]});
            var Q134;
            Q134=makeQuery(id+"F0Hq7nSFAMYVZvY_4.33.F20.opExtrude","SWEPT_FACE",FACE,{"disambiguationData":[OSD([sQuery(id+"F19.wireOp",EDGE,"E157")])]});
            var Q135;
            Q135=makeQuery(id+"F0Hq7nSFAMYVZvY_4.33.F20.opExtrude","SWEPT_FACE",FACE,{"disambiguationData":[OSD([sQuery(id+"F19.wireOp",EDGE,"E158.MirrorCS")])]});
            var Q136;
            Q136=makeQuery(id+"F0Hq7nSFAMYVZvY_4.33.F20.opExtrude","CAP_EDGE",EDGE,{"disambiguationData":[OSD([sQuery(id+"F19.wireOp",EDGE,"E158.MirrorCS")])],"isStart":false});
            var Q137;
            {var subQ0=sQuery(id+"F16.wireOp",EDGE,"E151");var subQ1=sQuery(id+"F16.wireOp",EDGE,"E152");Q137=makeQuery(id+"F0Hq7nSFAMYVZvY_4.1.F20.boolean.opBoolean","SPLIT",FACE,{"disambiguationData":[TD([makeQuery(id+"F20.opExtrude","SWEPT_FACE",FACE,{"disambiguationData":[OSD([sQuery(id+"F19.wireOp",EDGE,"E158.MirrorCS")])]})])],"derivedFrom":makeQuery(id+"F17.boolean.opBoolean","COPY",FACE,{"derivedFrom":makeQuery(id+"F17.opExtrude","CAP_FACE",FACE,{"disambiguationData":[OSD([subQ0,subQ1])],"isStart":false})})});}
            var Q138;
            {var subQ0=sQuery(id+"F19.wireOp",EDGE,"E158.MirrorCS");var subQ2=sQuery(id+"F16.wireOp",EDGE,"E151");Q138=makeQuery(id+"F0Hq7nSFAMYVZvY_4.1.F20.boolean.opBoolean","SPLIT",FACE,{"disambiguationData":[TD([makeQuery(id+"F20.opExtrude","SWEPT_FACE",FACE,{"disambiguationData":[OSD([subQ0])]})])],"derivedFrom":makeQuery(id+"F17.boolean.opBoolean","COPY",FACE,{"derivedFrom":makeQuery(id+"F17.opExtrude","SWEPT_FACE",FACE,{"disambiguationData":[OSD([subQ2])]})})});}
            var Q139;
            {var subQ0=sQuery(id+"F16.wireOp",EDGE,"E151");var subQ2=sQuery(id+"F16.wireOp",EDGE,"E152");var subQ4=sQuery(id+"F19.wireOp",EDGE,"E158.MirrorCS");var subQ5=makeQuery(id+"F0Hq7nSFAMYVZvY_4.32.F20.opExtrude","SWEPT_FACE",FACE,{"disambiguationData":[OSD([subQ4])]});var subQ6=sQuery(id+"F19.wireOp",EDGE,"E157");var subQ7=makeQuery(id+"F20.opExtrude","SWEPT_FACE",FACE,{"disambiguationData":[OSD([subQ6])]});Q139=makeQuery(id+"F0Hq7nSFAMYVZvY_4.33.F20.boolean.opBoolean","SPLIT",FACE,{"disambiguationData":[TD([subQ5])],"derivedFrom":makeQuery(id+"F0Hq7nSFAMYVZvY_4.32.F20.boolean.opBoolean","SPLIT",FACE,{"disambiguationData":[TD([subQ7])],"derivedFrom":makeQuery(id+"F0Hq7nSFAMYVZvY_4.31.F20.boolean.opBoolean","SPLIT",FACE,{"disambiguationData":[TD([subQ7])],"derivedFrom":makeQuery(id+"F0Hq7nSFAMYVZvY_4.30.F20.boolean.opBoolean","SPLIT",FACE,{"disambiguationData":[TD([subQ7])],"derivedFrom":makeQuery(id+"F0Hq7nSFAMYVZvY_4.29.F20.boolean.opBoolean","SPLIT",FACE,{"disambiguationData":[TD([subQ7])],"derivedFrom":makeQuery(id+"F0Hq7nSFAMYVZvY_4.28.F20.boolean.opBoolean","SPLIT",FACE,{"disambiguationData":[TD([subQ7])],"derivedFrom":makeQuery(id+"F0Hq7nSFAMYVZvY_4.27.F20.boolean.opBoolean","SPLIT",FACE,{"disambiguationData":[TD([subQ7])],"derivedFrom":makeQuery(id+"F0Hq7nSFAMYVZvY_4.26.F20.boolean.opBoolean","SPLIT",FACE,{"disambiguationData":[TD([subQ7])],"derivedFrom":makeQuery(id+"F0Hq7nSFAMYVZvY_4.25.F20.boolean.opBoolean","SPLIT",FACE,{"disambiguationData":[TD([subQ7])],"derivedFrom":makeQuery(id+"F0Hq7nSFAMYVZvY_4.24.F20.boolean.opBoolean","SPLIT",FACE,{"disambiguationData":[TD([subQ7])],"derivedFrom":makeQuery(id+"F0Hq7nSFAMYVZvY_4.23.F20.boolean.opBoolean","SPLIT",FACE,{"disambiguationData":[TD([subQ7])],"derivedFrom":makeQuery(id+"F0Hq7nSFAMYVZvY_4.22.F20.boolean.opBoolean","SPLIT",FACE,{"disambiguationData":[TD([subQ7])],"derivedFrom":makeQuery(id+"F0Hq7nSFAMYVZvY_4.21.F20.boolean.opBoolean","SPLIT",FACE,{"disambiguationData":[TD([subQ7])],"derivedFrom":makeQuery(id+"F0Hq7nSFAMYVZvY_4.20.F20.boolean.opBoolean","SPLIT",FACE,{"disambiguationData":[TD([subQ7])],"derivedFrom":makeQuery(id+"F0Hq7nSFAMYVZvY_4.19.F20.boolean.opBoolean","SPLIT",FACE,{"disambiguationData":[TD([subQ7])],"derivedFrom":makeQuery(id+"F0Hq7nSFAMYVZvY_4.18.F20.boolean.opBoolean","SPLIT",FACE,{"disambiguationData":[TD([subQ7])],"derivedFrom":makeQuery(id+"F0Hq7nSFAMYVZvY_4.17.F20.boolean.opBoolean","SPLIT",FACE,{"disambiguationData":[TD([subQ7])],"derivedFrom":makeQuery(id+"F0Hq7nSFAMYVZvY_4.16.F20.boolean.opBoolean","SPLIT",FACE,{"disambiguationData":[TD([subQ7])],"derivedFrom":makeQuery(id+"F0Hq7nSFAMYVZvY_4.15.F20.boolean.opBoolean","SPLIT",FACE,{"disambiguationData":[TD([subQ7])],"derivedFrom":makeQuery(id+"F0Hq7nSFAMYVZvY_4.14.F20.boolean.opBoolean","SPLIT",FACE,{"disambiguationData":[TD([subQ7])],"derivedFrom":makeQuery(id+"F0Hq7nSFAMYVZvY_4.13.F20.boolean.opBoolean","SPLIT",FACE,{"disambiguationData":[TD([subQ7])],"derivedFrom":makeQuery(id+"F0Hq7nSFAMYVZvY_4.12.F20.boolean.opBoolean","SPLIT",FACE,{"disambiguationData":[TD([subQ7])],"derivedFrom":makeQuery(id+"F0Hq7nSFAMYVZvY_4.11.F20.boolean.opBoolean","SPLIT",FACE,{"disambiguationData":[TD([subQ7])],"derivedFrom":makeQuery(id+"F0Hq7nSFAMYVZvY_4.10.F20.boolean.opBoolean","SPLIT",FACE,{"disambiguationData":[TD([subQ7])],"derivedFrom":makeQuery(id+"F0Hq7nSFAMYVZvY_4.9.F20.boolean.opBoolean","SPLIT",FACE,{"disambiguationData":[TD([subQ7])],"derivedFrom":makeQuery(id+"F0Hq7nSFAMYVZvY_4.8.F20.boolean.opBoolean","SPLIT",FACE,{"disambiguationData":[TD([subQ7])],"derivedFrom":makeQuery(id+"F0Hq7nSFAMYVZvY_4.7.F20.boolean.opBoolean","SPLIT",FACE,{"disambiguationData":[TD([subQ7])],"derivedFrom":makeQuery(id+"F0Hq7nSFAMYVZvY_4.6.F20.boolean.opBoolean","SPLIT",FACE,{"disambiguationData":[TD([subQ7])],"derivedFrom":makeQuery(id+"F0Hq7nSFAMYVZvY_4.5.F20.boolean.opBoolean","SPLIT",FACE,{"disambiguationData":[TD([subQ7])],"derivedFrom":makeQuery(id+"F0Hq7nSFAMYVZvY_4.4.F20.boolean.opBoolean","SPLIT",FACE,{"disambiguationData":[TD([subQ7])],"derivedFrom":makeQuery(id+"F0Hq7nSFAMYVZvY_4.3.F20.boolean.opBoolean","SPLIT",FACE,{"disambiguationData":[TD([subQ7])],"derivedFrom":makeQuery(id+"F0Hq7nSFAMYVZvY_4.2.F20.boolean.opBoolean","SPLIT",FACE,{"disambiguationData":[TD([subQ7])],"derivedFrom":makeQuery(id+"F0Hq7nSFAMYVZvY_4.1.F20.boolean.opBoolean","SPLIT",FACE,{"disambiguationData":[TD([subQ7])],"derivedFrom":makeQuery(id+"F17.boolean.opBoolean","COPY",FACE,{"derivedFrom":makeQuery(id+"F17.opExtrude","CAP_FACE",FACE,{"disambiguationData":[OSD([subQ0,subQ2])],"isStart":false})})})})})})})})})})})})})})})})})})})})})})})})})})})})})})})})})})});}
            var Q140;
            {var subQ0=sQuery(id+"F19.wireOp",EDGE,"E158.MirrorCS");var subQ1=sQuery(id+"F19.wireOp",EDGE,"E157");var subQ3=sQuery(id+"F16.wireOp",EDGE,"E151");var subQ16=makeQuery(id+"F0Hq7nSFAMYVZvY_4.32.F20.opExtrude","SWEPT_FACE",FACE,{"disambiguationData":[OSD([subQ0])]});var subQ40=makeQuery(id+"F20.opExtrude","SWEPT_FACE",FACE,{"disambiguationData":[OSD([subQ1])]});Q140=makeQuery(id+"F0Hq7nSFAMYVZvY_4.33.F20.boolean.opBoolean","SPLIT",FACE,{"disambiguationData":[TD([subQ16])],"derivedFrom":makeQuery(id+"F0Hq7nSFAMYVZvY_4.32.F20.boolean.opBoolean","SPLIT",FACE,{"disambiguationData":[TD([subQ40])],"derivedFrom":makeQuery(id+"F0Hq7nSFAMYVZvY_4.31.F20.boolean.opBoolean","SPLIT",FACE,{"disambiguationData":[TD([subQ40])],"derivedFrom":makeQuery(id+"F0Hq7nSFAMYVZvY_4.30.F20.boolean.opBoolean","SPLIT",FACE,{"disambiguationData":[TD([subQ40])],"derivedFrom":makeQuery(id+"F0Hq7nSFAMYVZvY_4.29.F20.boolean.opBoolean","SPLIT",FACE,{"disambiguationData":[TD([subQ40])],"derivedFrom":makeQuery(id+"F0Hq7nSFAMYVZvY_4.28.F20.boolean.opBoolean","SPLIT",FACE,{"disambiguationData":[TD([subQ40])],"derivedFrom":makeQuery(id+"F0Hq7nSFAMYVZvY_4.27.F20.boolean.opBoolean","SPLIT",FACE,{"disambiguationData":[TD([subQ40])],"derivedFrom":makeQuery(id+"F0Hq7nSFAMYVZvY_4.26.F20.boolean.opBoolean","SPLIT",FACE,{"disambiguationData":[TD([subQ40])],"derivedFrom":makeQuery(id+"F0Hq7nSFAMYVZvY_4.25.F20.boolean.opBoolean","SPLIT",FACE,{"disambiguationData":[TD([subQ40])],"derivedFrom":makeQuery(id+"F0Hq7nSFAMYVZvY_4.24.F20.boolean.opBoolean","SPLIT",FACE,{"disambiguationData":[TD([subQ40])],"derivedFrom":makeQuery(id+"F0Hq7nSFAMYVZvY_4.23.F20.boolean.opBoolean","SPLIT",FACE,{"disambiguationData":[TD([subQ40])],"derivedFrom":makeQuery(id+"F0Hq7nSFAMYVZvY_4.22.F20.boolean.opBoolean","SPLIT",FACE,{"disambiguationData":[TD([subQ40])],"derivedFrom":makeQuery(id+"F0Hq7nSFAMYVZvY_4.21.F20.boolean.opBoolean","SPLIT",FACE,{"disambiguationData":[TD([subQ40])],"derivedFrom":makeQuery(id+"F0Hq7nSFAMYVZvY_4.20.F20.boolean.opBoolean","SPLIT",FACE,{"disambiguationData":[TD([subQ40])],"derivedFrom":makeQuery(id+"F0Hq7nSFAMYVZvY_4.19.F20.boolean.opBoolean","SPLIT",FACE,{"disambiguationData":[TD([subQ40])],"derivedFrom":makeQuery(id+"F0Hq7nSFAMYVZvY_4.18.F20.boolean.opBoolean","SPLIT",FACE,{"disambiguationData":[TD([subQ40])],"derivedFrom":makeQuery(id+"F0Hq7nSFAMYVZvY_4.17.F20.boolean.opBoolean","SPLIT",FACE,{"disambiguationData":[TD([subQ40])],"derivedFrom":makeQuery(id+"F0Hq7nSFAMYVZvY_4.16.F20.boolean.opBoolean","SPLIT",FACE,{"disambiguationData":[TD([subQ40])],"derivedFrom":makeQuery(id+"F0Hq7nSFAMYVZvY_4.15.F20.boolean.opBoolean","SPLIT",FACE,{"disambiguationData":[TD([subQ40])],"derivedFrom":makeQuery(id+"F0Hq7nSFAMYVZvY_4.14.F20.boolean.opBoolean","SPLIT",FACE,{"disambiguationData":[TD([subQ40])],"derivedFrom":makeQuery(id+"F0Hq7nSFAMYVZvY_4.13.F20.boolean.opBoolean","SPLIT",FACE,{"disambiguationData":[TD([subQ40])],"derivedFrom":makeQuery(id+"F0Hq7nSFAMYVZvY_4.12.F20.boolean.opBoolean","SPLIT",FACE,{"disambiguationData":[TD([subQ40])],"derivedFrom":makeQuery(id+"F0Hq7nSFAMYVZvY_4.11.F20.boolean.opBoolean","SPLIT",FACE,{"disambiguationData":[TD([subQ40])],"derivedFrom":makeQuery(id+"F0Hq7nSFAMYVZvY_4.10.F20.boolean.opBoolean","SPLIT",FACE,{"disambiguationData":[TD([subQ40])],"derivedFrom":makeQuery(id+"F0Hq7nSFAMYVZvY_4.9.F20.boolean.opBoolean","SPLIT",FACE,{"disambiguationData":[TD([subQ40])],"derivedFrom":makeQuery(id+"F0Hq7nSFAMYVZvY_4.8.F20.boolean.opBoolean","SPLIT",FACE,{"disambiguationData":[TD([subQ40])],"derivedFrom":makeQuery(id+"F0Hq7nSFAMYVZvY_4.7.F20.boolean.opBoolean","SPLIT",FACE,{"disambiguationData":[TD([subQ40])],"derivedFrom":makeQuery(id+"F0Hq7nSFAMYVZvY_4.6.F20.boolean.opBoolean","SPLIT",FACE,{"disambiguationData":[TD([subQ40])],"derivedFrom":makeQuery(id+"F0Hq7nSFAMYVZvY_4.5.F20.boolean.opBoolean","SPLIT",FACE,{"disambiguationData":[TD([subQ40])],"derivedFrom":makeQuery(id+"F0Hq7nSFAMYVZvY_4.4.F20.boolean.opBoolean","SPLIT",FACE,{"disambiguationData":[TD([subQ40])],"derivedFrom":makeQuery(id+"F0Hq7nSFAMYVZvY_4.3.F20.boolean.opBoolean","SPLIT",FACE,{"disambiguationData":[TD([subQ40])],"derivedFrom":makeQuery(id+"F0Hq7nSFAMYVZvY_4.2.F20.boolean.opBoolean","SPLIT",FACE,{"disambiguationData":[TD([subQ40])],"derivedFrom":makeQuery(id+"F0Hq7nSFAMYVZvY_4.1.F20.boolean.opBoolean","SPLIT",FACE,{"disambiguationData":[TD([subQ40])],"derivedFrom":makeQuery(id+"F17.boolean.opBoolean","COPY",FACE,{"derivedFrom":makeQuery(id+"F17.opExtrude","SWEPT_FACE",FACE,{"disambiguationData":[OSD([subQ3])]})})})})})})})})})})})})})})})})})})})})})})})})})})})})})})})})})})});}
            var Q141;
            Q141=makeQuery(id+"F0Hq7nSFAMYVZvY_4.2.F20.opExtrude","SWEPT_FACE",FACE,{"disambiguationData":[OSD([sQuery(id+"F19.wireOp",EDGE,"E157")])]});
            var Q142;
            Q142=makeQuery(id+"F0Hq7nSFAMYVZvY_4.2.F20.opExtrude","SWEPT_FACE",FACE,{"disambiguationData":[OSD([sQuery(id+"F19.wireOp",EDGE,"E158.MirrorCS")])]});
            var Q143;
            Q143=makeQuery(id+"F0Hq7nSFAMYVZvY_4.2.F20.opExtrude","CAP_EDGE",EDGE,{"disambiguationData":[OSD([sQuery(id+"F19.wireOp",EDGE,"E158.MirrorCS")])],"isStart":false});
            var Q144;
            Q144=makeQuery(id+"F0Hq7nSFAMYVZvY_4.34.F20.opExtrude","SWEPT_FACE",FACE,{"disambiguationData":[OSD([sQuery(id+"F19.wireOp",EDGE,"E157")])]});
            var Q145;
            Q145=makeQuery(id+"F0Hq7nSFAMYVZvY_4.34.F20.opExtrude","CAP_EDGE",EDGE,{"disambiguationData":[OSD([sQuery(id+"F19.wireOp",EDGE,"E157")])],"isStart":false});
            var Q146;
            Q146=makeQuery(id+"F0Hq7nSFAMYVZvY_4.34.F20.opExtrude","CAP_EDGE",EDGE,{"disambiguationData":[OSD([sQuery(id+"F19.wireOp",EDGE,"E158.MirrorCS")])],"isStart":false});
            var Q147;
            {var subQ0=sQuery(id+"F16.wireOp",EDGE,"E151");var subQ2=makeQuery(id+"F0Hq7nSFAMYVZvY_4.1.F20.opExtrude","SWEPT_FACE",FACE,{"disambiguationData":[OSD([sQuery(id+"F19.wireOp",EDGE,"E158.MirrorCS")])]});var subQ3=sQuery(id+"F16.wireOp",EDGE,"E152");var subQ5=sQuery(id+"F19.wireOp",EDGE,"E157");Q147=makeQuery(id+"F0Hq7nSFAMYVZvY_4.2.F20.boolean.opBoolean","SPLIT",FACE,{"disambiguationData":[TD([subQ2])],"derivedFrom":makeQuery(id+"F0Hq7nSFAMYVZvY_4.1.F20.boolean.opBoolean","SPLIT",FACE,{"disambiguationData":[TD([makeQuery(id+"F20.opExtrude","SWEPT_FACE",FACE,{"disambiguationData":[OSD([subQ5])]})])],"derivedFrom":makeQuery(id+"F17.boolean.opBoolean","COPY",FACE,{"derivedFrom":makeQuery(id+"F17.opExtrude","CAP_FACE",FACE,{"disambiguationData":[OSD([subQ0,subQ3])],"isStart":false})})})});}
            var Q148;
            {var subQ0=sQuery(id+"F19.wireOp",EDGE,"E158.MirrorCS");var subQ1=sQuery(id+"F19.wireOp",EDGE,"E157");var subQ3=sQuery(id+"F16.wireOp",EDGE,"E151");var subQ8=makeQuery(id+"F0Hq7nSFAMYVZvY_4.1.F20.opExtrude","SWEPT_FACE",FACE,{"disambiguationData":[OSD([subQ0])]});Q148=makeQuery(id+"F0Hq7nSFAMYVZvY_4.2.F20.boolean.opBoolean","SPLIT",FACE,{"disambiguationData":[TD([subQ8])],"derivedFrom":makeQuery(id+"F0Hq7nSFAMYVZvY_4.1.F20.boolean.opBoolean","SPLIT",FACE,{"disambiguationData":[TD([makeQuery(id+"F20.opExtrude","SWEPT_FACE",FACE,{"disambiguationData":[OSD([subQ1])]})])],"derivedFrom":makeQuery(id+"F17.boolean.opBoolean","COPY",FACE,{"derivedFrom":makeQuery(id+"F17.opExtrude","SWEPT_FACE",FACE,{"disambiguationData":[OSD([subQ3])]})})})});}
            var Q149;
            {var subQ0=sQuery(id+"F16.wireOp",EDGE,"E151");var subQ2=sQuery(id+"F16.wireOp",EDGE,"E152");var subQ4=sQuery(id+"F19.wireOp",EDGE,"E158.MirrorCS");var subQ5=makeQuery(id+"F0Hq7nSFAMYVZvY_4.33.F20.opExtrude","SWEPT_FACE",FACE,{"disambiguationData":[OSD([subQ4])]});var subQ6=sQuery(id+"F19.wireOp",EDGE,"E157");var subQ7=makeQuery(id+"F20.opExtrude","SWEPT_FACE",FACE,{"disambiguationData":[OSD([subQ6])]});Q149=makeQuery(id+"F0Hq7nSFAMYVZvY_4.34.F20.boolean.opBoolean","SPLIT",FACE,{"disambiguationData":[TD([subQ5])],"derivedFrom":makeQuery(id+"F0Hq7nSFAMYVZvY_4.33.F20.boolean.opBoolean","SPLIT",FACE,{"disambiguationData":[TD([subQ7])],"derivedFrom":makeQuery(id+"F0Hq7nSFAMYVZvY_4.32.F20.boolean.opBoolean","SPLIT",FACE,{"disambiguationData":[TD([subQ7])],"derivedFrom":makeQuery(id+"F0Hq7nSFAMYVZvY_4.31.F20.boolean.opBoolean","SPLIT",FACE,{"disambiguationData":[TD([subQ7])],"derivedFrom":makeQuery(id+"F0Hq7nSFAMYVZvY_4.30.F20.boolean.opBoolean","SPLIT",FACE,{"disambiguationData":[TD([subQ7])],"derivedFrom":makeQuery(id+"F0Hq7nSFAMYVZvY_4.29.F20.boolean.opBoolean","SPLIT",FACE,{"disambiguationData":[TD([subQ7])],"derivedFrom":makeQuery(id+"F0Hq7nSFAMYVZvY_4.28.F20.boolean.opBoolean","SPLIT",FACE,{"disambiguationData":[TD([subQ7])],"derivedFrom":makeQuery(id+"F0Hq7nSFAMYVZvY_4.27.F20.boolean.opBoolean","SPLIT",FACE,{"disambiguationData":[TD([subQ7])],"derivedFrom":makeQuery(id+"F0Hq7nSFAMYVZvY_4.26.F20.boolean.opBoolean","SPLIT",FACE,{"disambiguationData":[TD([subQ7])],"derivedFrom":makeQuery(id+"F0Hq7nSFAMYVZvY_4.25.F20.boolean.opBoolean","SPLIT",FACE,{"disambiguationData":[TD([subQ7])],"derivedFrom":makeQuery(id+"F0Hq7nSFAMYVZvY_4.24.F20.boolean.opBoolean","SPLIT",FACE,{"disambiguationData":[TD([subQ7])],"derivedFrom":makeQuery(id+"F0Hq7nSFAMYVZvY_4.23.F20.boolean.opBoolean","SPLIT",FACE,{"disambiguationData":[TD([subQ7])],"derivedFrom":makeQuery(id+"F0Hq7nSFAMYVZvY_4.22.F20.boolean.opBoolean","SPLIT",FACE,{"disambiguationData":[TD([subQ7])],"derivedFrom":makeQuery(id+"F0Hq7nSFAMYVZvY_4.21.F20.boolean.opBoolean","SPLIT",FACE,{"disambiguationData":[TD([subQ7])],"derivedFrom":makeQuery(id+"F0Hq7nSFAMYVZvY_4.20.F20.boolean.opBoolean","SPLIT",FACE,{"disambiguationData":[TD([subQ7])],"derivedFrom":makeQuery(id+"F0Hq7nSFAMYVZvY_4.19.F20.boolean.opBoolean","SPLIT",FACE,{"disambiguationData":[TD([subQ7])],"derivedFrom":makeQuery(id+"F0Hq7nSFAMYVZvY_4.18.F20.boolean.opBoolean","SPLIT",FACE,{"disambiguationData":[TD([subQ7])],"derivedFrom":makeQuery(id+"F0Hq7nSFAMYVZvY_4.17.F20.boolean.opBoolean","SPLIT",FACE,{"disambiguationData":[TD([subQ7])],"derivedFrom":makeQuery(id+"F0Hq7nSFAMYVZvY_4.16.F20.boolean.opBoolean","SPLIT",FACE,{"disambiguationData":[TD([subQ7])],"derivedFrom":makeQuery(id+"F0Hq7nSFAMYVZvY_4.15.F20.boolean.opBoolean","SPLIT",FACE,{"disambiguationData":[TD([subQ7])],"derivedFrom":makeQuery(id+"F0Hq7nSFAMYVZvY_4.14.F20.boolean.opBoolean","SPLIT",FACE,{"disambiguationData":[TD([subQ7])],"derivedFrom":makeQuery(id+"F0Hq7nSFAMYVZvY_4.13.F20.boolean.opBoolean","SPLIT",FACE,{"disambiguationData":[TD([subQ7])],"derivedFrom":makeQuery(id+"F0Hq7nSFAMYVZvY_4.12.F20.boolean.opBoolean","SPLIT",FACE,{"disambiguationData":[TD([subQ7])],"derivedFrom":makeQuery(id+"F0Hq7nSFAMYVZvY_4.11.F20.boolean.opBoolean","SPLIT",FACE,{"disambiguationData":[TD([subQ7])],"derivedFrom":makeQuery(id+"F0Hq7nSFAMYVZvY_4.10.F20.boolean.opBoolean","SPLIT",FACE,{"disambiguationData":[TD([subQ7])],"derivedFrom":makeQuery(id+"F0Hq7nSFAMYVZvY_4.9.F20.boolean.opBoolean","SPLIT",FACE,{"disambiguationData":[TD([subQ7])],"derivedFrom":makeQuery(id+"F0Hq7nSFAMYVZvY_4.8.F20.boolean.opBoolean","SPLIT",FACE,{"disambiguationData":[TD([subQ7])],"derivedFrom":makeQuery(id+"F0Hq7nSFAMYVZvY_4.7.F20.boolean.opBoolean","SPLIT",FACE,{"disambiguationData":[TD([subQ7])],"derivedFrom":makeQuery(id+"F0Hq7nSFAMYVZvY_4.6.F20.boolean.opBoolean","SPLIT",FACE,{"disambiguationData":[TD([subQ7])],"derivedFrom":makeQuery(id+"F0Hq7nSFAMYVZvY_4.5.F20.boolean.opBoolean","SPLIT",FACE,{"disambiguationData":[TD([subQ7])],"derivedFrom":makeQuery(id+"F0Hq7nSFAMYVZvY_4.4.F20.boolean.opBoolean","SPLIT",FACE,{"disambiguationData":[TD([subQ7])],"derivedFrom":makeQuery(id+"F0Hq7nSFAMYVZvY_4.3.F20.boolean.opBoolean","SPLIT",FACE,{"disambiguationData":[TD([subQ7])],"derivedFrom":makeQuery(id+"F0Hq7nSFAMYVZvY_4.2.F20.boolean.opBoolean","SPLIT",FACE,{"disambiguationData":[TD([subQ7])],"derivedFrom":makeQuery(id+"F0Hq7nSFAMYVZvY_4.1.F20.boolean.opBoolean","SPLIT",FACE,{"disambiguationData":[TD([subQ7])],"derivedFrom":makeQuery(id+"F17.boolean.opBoolean","COPY",FACE,{"derivedFrom":makeQuery(id+"F17.opExtrude","CAP_FACE",FACE,{"disambiguationData":[OSD([subQ0,subQ2])],"isStart":false})})})})})})})})})})})})})})})})})})})})})})})})})})})})})})})})})})})});}
            var Q150;
            Q150=makeQuery(id+"F0Hq7nSFAMYVZvY_4.34.F20.opExtrude","CAP_EDGE",EDGE,{"disambiguationData":[OSD([sQuery(id+"F19.wireOp",EDGE,"E157")])],"isStart":true});
            var Q151;
            {var subQ0=sQuery(id+"F19.wireOp",EDGE,"E158.MirrorCS");var subQ1=sQuery(id+"F19.wireOp",EDGE,"E157");var subQ3=sQuery(id+"F16.wireOp",EDGE,"E151");var subQ21=makeQuery(id+"F0Hq7nSFAMYVZvY_4.33.F20.opExtrude","SWEPT_FACE",FACE,{"disambiguationData":[OSD([subQ0])]});var subQ41=makeQuery(id+"F20.opExtrude","SWEPT_FACE",FACE,{"disambiguationData":[OSD([subQ1])]});Q151=makeQuery(id+"F0Hq7nSFAMYVZvY_4.34.F20.boolean.opBoolean","SPLIT",EDGE,{"disambiguationData":[TD([subQ21])],"derivedFrom":makeQuery(id+"F0Hq7nSFAMYVZvY_4.33.F20.boolean.opBoolean","SPLIT",EDGE,{"disambiguationData":[TD([subQ41])],"derivedFrom":makeQuery(id+"F0Hq7nSFAMYVZvY_4.32.F20.boolean.opBoolean","SPLIT",EDGE,{"disambiguationData":[TD([subQ41])],"derivedFrom":makeQuery(id+"F0Hq7nSFAMYVZvY_4.31.F20.boolean.opBoolean","SPLIT",EDGE,{"disambiguationData":[TD([subQ41])],"derivedFrom":makeQuery(id+"F0Hq7nSFAMYVZvY_4.30.F20.boolean.opBoolean","SPLIT",EDGE,{"disambiguationData":[TD([subQ41])],"derivedFrom":makeQuery(id+"F0Hq7nSFAMYVZvY_4.29.F20.boolean.opBoolean","SPLIT",EDGE,{"disambiguationData":[TD([subQ41])],"derivedFrom":makeQuery(id+"F0Hq7nSFAMYVZvY_4.28.F20.boolean.opBoolean","SPLIT",EDGE,{"disambiguationData":[TD([subQ41])],"derivedFrom":makeQuery(id+"F0Hq7nSFAMYVZvY_4.27.F20.boolean.opBoolean","SPLIT",EDGE,{"disambiguationData":[TD([subQ41])],"derivedFrom":makeQuery(id+"F0Hq7nSFAMYVZvY_4.26.F20.boolean.opBoolean","SPLIT",EDGE,{"disambiguationData":[TD([subQ41])],"derivedFrom":makeQuery(id+"F0Hq7nSFAMYVZvY_4.25.F20.boolean.opBoolean","SPLIT",EDGE,{"disambiguationData":[TD([subQ41])],"derivedFrom":makeQuery(id+"F0Hq7nSFAMYVZvY_4.24.F20.boolean.opBoolean","SPLIT",EDGE,{"disambiguationData":[TD([subQ41])],"derivedFrom":makeQuery(id+"F0Hq7nSFAMYVZvY_4.23.F20.boolean.opBoolean","SPLIT",EDGE,{"disambiguationData":[TD([subQ41])],"derivedFrom":makeQuery(id+"F0Hq7nSFAMYVZvY_4.22.F20.boolean.opBoolean","SPLIT",EDGE,{"disambiguationData":[TD([subQ41])],"derivedFrom":makeQuery(id+"F0Hq7nSFAMYVZvY_4.21.F20.boolean.opBoolean","SPLIT",EDGE,{"disambiguationData":[TD([subQ41])],"derivedFrom":makeQuery(id+"F0Hq7nSFAMYVZvY_4.20.F20.boolean.opBoolean","SPLIT",EDGE,{"disambiguationData":[TD([subQ41])],"derivedFrom":makeQuery(id+"F0Hq7nSFAMYVZvY_4.19.F20.boolean.opBoolean","SPLIT",EDGE,{"disambiguationData":[TD([subQ41])],"derivedFrom":makeQuery(id+"F0Hq7nSFAMYVZvY_4.18.F20.boolean.opBoolean","SPLIT",EDGE,{"disambiguationData":[TD([subQ41])],"derivedFrom":makeQuery(id+"F0Hq7nSFAMYVZvY_4.17.F20.boolean.opBoolean","SPLIT",EDGE,{"disambiguationData":[TD([subQ41])],"derivedFrom":makeQuery(id+"F0Hq7nSFAMYVZvY_4.16.F20.boolean.opBoolean","SPLIT",EDGE,{"disambiguationData":[TD([subQ41])],"derivedFrom":makeQuery(id+"F0Hq7nSFAMYVZvY_4.15.F20.boolean.opBoolean","SPLIT",EDGE,{"disambiguationData":[TD([subQ41])],"derivedFrom":makeQuery(id+"F0Hq7nSFAMYVZvY_4.14.F20.boolean.opBoolean","SPLIT",EDGE,{"disambiguationData":[TD([subQ41])],"derivedFrom":makeQuery(id+"F0Hq7nSFAMYVZvY_4.13.F20.boolean.opBoolean","SPLIT",EDGE,{"disambiguationData":[TD([subQ41])],"derivedFrom":makeQuery(id+"F0Hq7nSFAMYVZvY_4.12.F20.boolean.opBoolean","SPLIT",EDGE,{"disambiguationData":[TD([subQ41])],"derivedFrom":makeQuery(id+"F0Hq7nSFAMYVZvY_4.11.F20.boolean.opBoolean","SPLIT",EDGE,{"disambiguationData":[TD([subQ41])],"derivedFrom":makeQuery(id+"F0Hq7nSFAMYVZvY_4.10.F20.boolean.opBoolean","SPLIT",EDGE,{"disambiguationData":[TD([subQ41])],"derivedFrom":makeQuery(id+"F0Hq7nSFAMYVZvY_4.9.F20.boolean.opBoolean","SPLIT",EDGE,{"disambiguationData":[TD([subQ41])],"derivedFrom":makeQuery(id+"F0Hq7nSFAMYVZvY_4.8.F20.boolean.opBoolean","SPLIT",EDGE,{"disambiguationData":[TD([subQ41])],"derivedFrom":makeQuery(id+"F0Hq7nSFAMYVZvY_4.7.F20.boolean.opBoolean","SPLIT",EDGE,{"disambiguationData":[TD([subQ41])],"derivedFrom":makeQuery(id+"F0Hq7nSFAMYVZvY_4.6.F20.boolean.opBoolean","SPLIT",EDGE,{"disambiguationData":[TD([subQ41])],"derivedFrom":makeQuery(id+"F0Hq7nSFAMYVZvY_4.5.F20.boolean.opBoolean","SPLIT",EDGE,{"disambiguationData":[TD([subQ41])],"derivedFrom":makeQuery(id+"F0Hq7nSFAMYVZvY_4.4.F20.boolean.opBoolean","SPLIT",EDGE,{"disambiguationData":[TD([subQ41])],"derivedFrom":makeQuery(id+"F0Hq7nSFAMYVZvY_4.3.F20.boolean.opBoolean","SPLIT",EDGE,{"disambiguationData":[TD([subQ41])],"derivedFrom":makeQuery(id+"F0Hq7nSFAMYVZvY_4.2.F20.boolean.opBoolean","SPLIT",EDGE,{"disambiguationData":[TD([subQ41])],"derivedFrom":makeQuery(id+"F0Hq7nSFAMYVZvY_4.1.F20.boolean.opBoolean","SPLIT",EDGE,{"disambiguationData":[TD([subQ41])],"derivedFrom":makeQuery(id+"F18.boolean.opBoolean","COPY",EDGE,{"derivedFrom":makeQuery(id+"F18.opExtrude","CAP_EDGE",EDGE,{"disambiguationData":[OSD([subQ3])],"isStart":false})})})})})})})})})})})})})})})})})})})})})})})})})})})})})})})})})})})});}
            var Q152;
            Q152=makeQuery(id+"F0Hq7nSFAMYVZvY_4.3.F20.opExtrude","SWEPT_FACE",FACE,{"disambiguationData":[OSD([sQuery(id+"F19.wireOp",EDGE,"E157")])]});
            var Q153;
            Q153=makeQuery(id+"F0Hq7nSFAMYVZvY_4.3.F20.opExtrude","SWEPT_FACE",FACE,{"disambiguationData":[OSD([sQuery(id+"F19.wireOp",EDGE,"E158.MirrorCS")])]});
            var Q154;
            Q154=makeQuery(id+"F0Hq7nSFAMYVZvY_4.3.F20.opExtrude","CAP_EDGE",EDGE,{"disambiguationData":[OSD([sQuery(id+"F19.wireOp",EDGE,"E157")])],"isStart":false});
            var Q155;
            Q155=makeQuery(id+"F0Hq7nSFAMYVZvY_4.3.F20.opExtrude","CAP_EDGE",EDGE,{"disambiguationData":[OSD([sQuery(id+"F19.wireOp",EDGE,"E158.MirrorCS")])],"isStart":false});
            var Q156;
            Q156=makeQuery(id+"F0Hq7nSFAMYVZvY_4.35.F20.opExtrude","SWEPT_FACE",FACE,{"disambiguationData":[OSD([sQuery(id+"F19.wireOp",EDGE,"E157")])]});
            var Q157;
            Q157=makeQuery(id+"F0Hq7nSFAMYVZvY_4.35.F20.opExtrude","CAP_EDGE",EDGE,{"disambiguationData":[OSD([sQuery(id+"F19.wireOp",EDGE,"E157")])],"isStart":false});
            var Q158;
            Q158=makeQuery(id+"F0Hq7nSFAMYVZvY_4.35.F20.opExtrude","CAP_EDGE",EDGE,{"disambiguationData":[OSD([sQuery(id+"F19.wireOp",EDGE,"E158.MirrorCS")])],"isStart":false});
            var Q159;
            {var subQ0=sQuery(id+"F16.wireOp",EDGE,"E151");var subQ2=sQuery(id+"F16.wireOp",EDGE,"E152");var subQ4=sQuery(id+"F19.wireOp",EDGE,"E158.MirrorCS");var subQ5=makeQuery(id+"F0Hq7nSFAMYVZvY_4.2.F20.opExtrude","SWEPT_FACE",FACE,{"disambiguationData":[OSD([subQ4])]});var subQ6=sQuery(id+"F19.wireOp",EDGE,"E157");var subQ7=makeQuery(id+"F20.opExtrude","SWEPT_FACE",FACE,{"disambiguationData":[OSD([subQ6])]});Q159=makeQuery(id+"F0Hq7nSFAMYVZvY_4.3.F20.boolean.opBoolean","SPLIT",FACE,{"disambiguationData":[TD([subQ5])],"derivedFrom":makeQuery(id+"F0Hq7nSFAMYVZvY_4.2.F20.boolean.opBoolean","SPLIT",FACE,{"disambiguationData":[TD([subQ7])],"derivedFrom":makeQuery(id+"F0Hq7nSFAMYVZvY_4.1.F20.boolean.opBoolean","SPLIT",FACE,{"disambiguationData":[TD([subQ7])],"derivedFrom":makeQuery(id+"F17.boolean.opBoolean","COPY",FACE,{"derivedFrom":makeQuery(id+"F17.opExtrude","CAP_FACE",FACE,{"disambiguationData":[OSD([subQ0,subQ2])],"isStart":false})})})})});}
            var Q160;
            {var subQ0=sQuery(id+"F19.wireOp",EDGE,"E158.MirrorCS");var subQ1=sQuery(id+"F19.wireOp",EDGE,"E157");var subQ3=sQuery(id+"F16.wireOp",EDGE,"E151");var subQ9=makeQuery(id+"F0Hq7nSFAMYVZvY_4.2.F20.opExtrude","SWEPT_FACE",FACE,{"disambiguationData":[OSD([subQ0])]});var subQ10=makeQuery(id+"F20.opExtrude","SWEPT_FACE",FACE,{"disambiguationData":[OSD([subQ1])]});Q160=makeQuery(id+"F0Hq7nSFAMYVZvY_4.3.F20.boolean.opBoolean","SPLIT",FACE,{"disambiguationData":[TD([subQ9])],"derivedFrom":makeQuery(id+"F0Hq7nSFAMYVZvY_4.2.F20.boolean.opBoolean","SPLIT",FACE,{"disambiguationData":[TD([subQ10])],"derivedFrom":makeQuery(id+"F0Hq7nSFAMYVZvY_4.1.F20.boolean.opBoolean","SPLIT",FACE,{"disambiguationData":[TD([subQ10])],"derivedFrom":makeQuery(id+"F17.boolean.opBoolean","COPY",FACE,{"derivedFrom":makeQuery(id+"F17.opExtrude","SWEPT_FACE",FACE,{"disambiguationData":[OSD([subQ3])]})})})})});}
            var Q161;
            {var subQ0=sQuery(id+"F16.wireOp",EDGE,"E151");var subQ2=sQuery(id+"F19.wireOp",EDGE,"E157");var subQ3=sQuery(id+"F16.wireOp",EDGE,"E152");var subQ5=sQuery(id+"F19.wireOp",EDGE,"E158.MirrorCS");var subQ6=makeQuery(id+"F0Hq7nSFAMYVZvY_4.34.F20.opExtrude","SWEPT_FACE",FACE,{"disambiguationData":[OSD([subQ5])]});var subQ7=makeQuery(id+"F20.opExtrude","SWEPT_FACE",FACE,{"disambiguationData":[OSD([subQ2])]});Q161=makeQuery(id+"F0Hq7nSFAMYVZvY_4.35.F20.boolean.opBoolean","SPLIT",FACE,{"disambiguationData":[TD([subQ6])],"derivedFrom":makeQuery(id+"F0Hq7nSFAMYVZvY_4.34.F20.boolean.opBoolean","SPLIT",FACE,{"disambiguationData":[TD([subQ7])],"derivedFrom":makeQuery(id+"F0Hq7nSFAMYVZvY_4.33.F20.boolean.opBoolean","SPLIT",FACE,{"disambiguationData":[TD([subQ7])],"derivedFrom":makeQuery(id+"F0Hq7nSFAMYVZvY_4.32.F20.boolean.opBoolean","SPLIT",FACE,{"disambiguationData":[TD([subQ7])],"derivedFrom":makeQuery(id+"F0Hq7nSFAMYVZvY_4.31.F20.boolean.opBoolean","SPLIT",FACE,{"disambiguationData":[TD([subQ7])],"derivedFrom":makeQuery(id+"F0Hq7nSFAMYVZvY_4.30.F20.boolean.opBoolean","SPLIT",FACE,{"disambiguationData":[TD([subQ7])],"derivedFrom":makeQuery(id+"F0Hq7nSFAMYVZvY_4.29.F20.boolean.opBoolean","SPLIT",FACE,{"disambiguationData":[TD([subQ7])],"derivedFrom":makeQuery(id+"F0Hq7nSFAMYVZvY_4.28.F20.boolean.opBoolean","SPLIT",FACE,{"disambiguationData":[TD([subQ7])],"derivedFrom":makeQuery(id+"F0Hq7nSFAMYVZvY_4.27.F20.boolean.opBoolean","SPLIT",FACE,{"disambiguationData":[TD([subQ7])],"derivedFrom":makeQuery(id+"F0Hq7nSFAMYVZvY_4.26.F20.boolean.opBoolean","SPLIT",FACE,{"disambiguationData":[TD([subQ7])],"derivedFrom":makeQuery(id+"F0Hq7nSFAMYVZvY_4.25.F20.boolean.opBoolean","SPLIT",FACE,{"disambiguationData":[TD([subQ7])],"derivedFrom":makeQuery(id+"F0Hq7nSFAMYVZvY_4.24.F20.boolean.opBoolean","SPLIT",FACE,{"disambiguationData":[TD([subQ7])],"derivedFrom":makeQuery(id+"F0Hq7nSFAMYVZvY_4.23.F20.boolean.opBoolean","SPLIT",FACE,{"disambiguationData":[TD([subQ7])],"derivedFrom":makeQuery(id+"F0Hq7nSFAMYVZvY_4.22.F20.boolean.opBoolean","SPLIT",FACE,{"disambiguationData":[TD([subQ7])],"derivedFrom":makeQuery(id+"F0Hq7nSFAMYVZvY_4.21.F20.boolean.opBoolean","SPLIT",FACE,{"disambiguationData":[TD([subQ7])],"derivedFrom":makeQuery(id+"F0Hq7nSFAMYVZvY_4.20.F20.boolean.opBoolean","SPLIT",FACE,{"disambiguationData":[TD([subQ7])],"derivedFrom":makeQuery(id+"F0Hq7nSFAMYVZvY_4.19.F20.boolean.opBoolean","SPLIT",FACE,{"disambiguationData":[TD([subQ7])],"derivedFrom":makeQuery(id+"F0Hq7nSFAMYVZvY_4.18.F20.boolean.opBoolean","SPLIT",FACE,{"disambiguationData":[TD([subQ7])],"derivedFrom":makeQuery(id+"F0Hq7nSFAMYVZvY_4.17.F20.boolean.opBoolean","SPLIT",FACE,{"disambiguationData":[TD([subQ7])],"derivedFrom":makeQuery(id+"F0Hq7nSFAMYVZvY_4.16.F20.boolean.opBoolean","SPLIT",FACE,{"disambiguationData":[TD([subQ7])],"derivedFrom":makeQuery(id+"F0Hq7nSFAMYVZvY_4.15.F20.boolean.opBoolean","SPLIT",FACE,{"disambiguationData":[TD([subQ7])],"derivedFrom":makeQuery(id+"F0Hq7nSFAMYVZvY_4.14.F20.boolean.opBoolean","SPLIT",FACE,{"disambiguationData":[TD([subQ7])],"derivedFrom":makeQuery(id+"F0Hq7nSFAMYVZvY_4.13.F20.boolean.opBoolean","SPLIT",FACE,{"disambiguationData":[TD([subQ7])],"derivedFrom":makeQuery(id+"F0Hq7nSFAMYVZvY_4.12.F20.boolean.opBoolean","SPLIT",FACE,{"disambiguationData":[TD([subQ7])],"derivedFrom":makeQuery(id+"F0Hq7nSFAMYVZvY_4.11.F20.boolean.opBoolean","SPLIT",FACE,{"disambiguationData":[TD([subQ7])],"derivedFrom":makeQuery(id+"F0Hq7nSFAMYVZvY_4.10.F20.boolean.opBoolean","SPLIT",FACE,{"disambiguationData":[TD([subQ7])],"derivedFrom":makeQuery(id+"F0Hq7nSFAMYVZvY_4.9.F20.boolean.opBoolean","SPLIT",FACE,{"disambiguationData":[TD([subQ7])],"derivedFrom":makeQuery(id+"F0Hq7nSFAMYVZvY_4.8.F20.boolean.opBoolean","SPLIT",FACE,{"disambiguationData":[TD([subQ7])],"derivedFrom":makeQuery(id+"F0Hq7nSFAMYVZvY_4.7.F20.boolean.opBoolean","SPLIT",FACE,{"disambiguationData":[TD([subQ7])],"derivedFrom":makeQuery(id+"F0Hq7nSFAMYVZvY_4.6.F20.boolean.opBoolean","SPLIT",FACE,{"disambiguationData":[TD([subQ7])],"derivedFrom":makeQuery(id+"F0Hq7nSFAMYVZvY_4.5.F20.boolean.opBoolean","SPLIT",FACE,{"disambiguationData":[TD([subQ7])],"derivedFrom":makeQuery(id+"F0Hq7nSFAMYVZvY_4.4.F20.boolean.opBoolean","SPLIT",FACE,{"disambiguationData":[TD([subQ7])],"derivedFrom":makeQuery(id+"F0Hq7nSFAMYVZvY_4.3.F20.boolean.opBoolean","SPLIT",FACE,{"disambiguationData":[TD([subQ7])],"derivedFrom":makeQuery(id+"F0Hq7nSFAMYVZvY_4.2.F20.boolean.opBoolean","SPLIT",FACE,{"disambiguationData":[TD([subQ7])],"derivedFrom":makeQuery(id+"F0Hq7nSFAMYVZvY_4.1.F20.boolean.opBoolean","SPLIT",FACE,{"disambiguationData":[TD([subQ7])],"derivedFrom":makeQuery(id+"F17.boolean.opBoolean","COPY",FACE,{"derivedFrom":makeQuery(id+"F17.opExtrude","CAP_FACE",FACE,{"disambiguationData":[OSD([subQ0,subQ3])],"isStart":false})})})})})})})})})})})})})})})})})})})})})})})})})})})})})})})})})})})})});}
            var Q162;
            Q162=makeQuery(id+"F0Hq7nSFAMYVZvY_4.35.F20.opExtrude","CAP_EDGE",EDGE,{"disambiguationData":[OSD([sQuery(id+"F19.wireOp",EDGE,"E157")])],"isStart":true});
            var Q163;
            {var subQ0=sQuery(id+"F19.wireOp",EDGE,"E158.MirrorCS");var subQ1=sQuery(id+"F19.wireOp",EDGE,"E157");var subQ3=sQuery(id+"F16.wireOp",EDGE,"E151");var subQ24=makeQuery(id+"F0Hq7nSFAMYVZvY_4.34.F20.opExtrude","SWEPT_FACE",FACE,{"disambiguationData":[OSD([subQ0])]});var subQ42=makeQuery(id+"F20.opExtrude","SWEPT_FACE",FACE,{"disambiguationData":[OSD([subQ1])]});Q163=makeQuery(id+"F0Hq7nSFAMYVZvY_4.35.F20.boolean.opBoolean","SPLIT",FACE,{"disambiguationData":[TD([subQ24])],"derivedFrom":makeQuery(id+"F0Hq7nSFAMYVZvY_4.34.F20.boolean.opBoolean","SPLIT",FACE,{"disambiguationData":[TD([subQ42])],"derivedFrom":makeQuery(id+"F0Hq7nSFAMYVZvY_4.33.F20.boolean.opBoolean","SPLIT",FACE,{"disambiguationData":[TD([subQ42])],"derivedFrom":makeQuery(id+"F0Hq7nSFAMYVZvY_4.32.F20.boolean.opBoolean","SPLIT",FACE,{"disambiguationData":[TD([subQ42])],"derivedFrom":makeQuery(id+"F0Hq7nSFAMYVZvY_4.31.F20.boolean.opBoolean","SPLIT",FACE,{"disambiguationData":[TD([subQ42])],"derivedFrom":makeQuery(id+"F0Hq7nSFAMYVZvY_4.30.F20.boolean.opBoolean","SPLIT",FACE,{"disambiguationData":[TD([subQ42])],"derivedFrom":makeQuery(id+"F0Hq7nSFAMYVZvY_4.29.F20.boolean.opBoolean","SPLIT",FACE,{"disambiguationData":[TD([subQ42])],"derivedFrom":makeQuery(id+"F0Hq7nSFAMYVZvY_4.28.F20.boolean.opBoolean","SPLIT",FACE,{"disambiguationData":[TD([subQ42])],"derivedFrom":makeQuery(id+"F0Hq7nSFAMYVZvY_4.27.F20.boolean.opBoolean","SPLIT",FACE,{"disambiguationData":[TD([subQ42])],"derivedFrom":makeQuery(id+"F0Hq7nSFAMYVZvY_4.26.F20.boolean.opBoolean","SPLIT",FACE,{"disambiguationData":[TD([subQ42])],"derivedFrom":makeQuery(id+"F0Hq7nSFAMYVZvY_4.25.F20.boolean.opBoolean","SPLIT",FACE,{"disambiguationData":[TD([subQ42])],"derivedFrom":makeQuery(id+"F0Hq7nSFAMYVZvY_4.24.F20.boolean.opBoolean","SPLIT",FACE,{"disambiguationData":[TD([subQ42])],"derivedFrom":makeQuery(id+"F0Hq7nSFAMYVZvY_4.23.F20.boolean.opBoolean","SPLIT",FACE,{"disambiguationData":[TD([subQ42])],"derivedFrom":makeQuery(id+"F0Hq7nSFAMYVZvY_4.22.F20.boolean.opBoolean","SPLIT",FACE,{"disambiguationData":[TD([subQ42])],"derivedFrom":makeQuery(id+"F0Hq7nSFAMYVZvY_4.21.F20.boolean.opBoolean","SPLIT",FACE,{"disambiguationData":[TD([subQ42])],"derivedFrom":makeQuery(id+"F0Hq7nSFAMYVZvY_4.20.F20.boolean.opBoolean","SPLIT",FACE,{"disambiguationData":[TD([subQ42])],"derivedFrom":makeQuery(id+"F0Hq7nSFAMYVZvY_4.19.F20.boolean.opBoolean","SPLIT",FACE,{"disambiguationData":[TD([subQ42])],"derivedFrom":makeQuery(id+"F0Hq7nSFAMYVZvY_4.18.F20.boolean.opBoolean","SPLIT",FACE,{"disambiguationData":[TD([subQ42])],"derivedFrom":makeQuery(id+"F0Hq7nSFAMYVZvY_4.17.F20.boolean.opBoolean","SPLIT",FACE,{"disambiguationData":[TD([subQ42])],"derivedFrom":makeQuery(id+"F0Hq7nSFAMYVZvY_4.16.F20.boolean.opBoolean","SPLIT",FACE,{"disambiguationData":[TD([subQ42])],"derivedFrom":makeQuery(id+"F0Hq7nSFAMYVZvY_4.15.F20.boolean.opBoolean","SPLIT",FACE,{"disambiguationData":[TD([subQ42])],"derivedFrom":makeQuery(id+"F0Hq7nSFAMYVZvY_4.14.F20.boolean.opBoolean","SPLIT",FACE,{"disambiguationData":[TD([subQ42])],"derivedFrom":makeQuery(id+"F0Hq7nSFAMYVZvY_4.13.F20.boolean.opBoolean","SPLIT",FACE,{"disambiguationData":[TD([subQ42])],"derivedFrom":makeQuery(id+"F0Hq7nSFAMYVZvY_4.12.F20.boolean.opBoolean","SPLIT",FACE,{"disambiguationData":[TD([subQ42])],"derivedFrom":makeQuery(id+"F0Hq7nSFAMYVZvY_4.11.F20.boolean.opBoolean","SPLIT",FACE,{"disambiguationData":[TD([subQ42])],"derivedFrom":makeQuery(id+"F0Hq7nSFAMYVZvY_4.10.F20.boolean.opBoolean","SPLIT",FACE,{"disambiguationData":[TD([subQ42])],"derivedFrom":makeQuery(id+"F0Hq7nSFAMYVZvY_4.9.F20.boolean.opBoolean","SPLIT",FACE,{"disambiguationData":[TD([subQ42])],"derivedFrom":makeQuery(id+"F0Hq7nSFAMYVZvY_4.8.F20.boolean.opBoolean","SPLIT",FACE,{"disambiguationData":[TD([subQ42])],"derivedFrom":makeQuery(id+"F0Hq7nSFAMYVZvY_4.7.F20.boolean.opBoolean","SPLIT",FACE,{"disambiguationData":[TD([subQ42])],"derivedFrom":makeQuery(id+"F0Hq7nSFAMYVZvY_4.6.F20.boolean.opBoolean","SPLIT",FACE,{"disambiguationData":[TD([subQ42])],"derivedFrom":makeQuery(id+"F0Hq7nSFAMYVZvY_4.5.F20.boolean.opBoolean","SPLIT",FACE,{"disambiguationData":[TD([subQ42])],"derivedFrom":makeQuery(id+"F0Hq7nSFAMYVZvY_4.4.F20.boolean.opBoolean","SPLIT",FACE,{"disambiguationData":[TD([subQ42])],"derivedFrom":makeQuery(id+"F0Hq7nSFAMYVZvY_4.3.F20.boolean.opBoolean","SPLIT",FACE,{"disambiguationData":[TD([subQ42])],"derivedFrom":makeQuery(id+"F0Hq7nSFAMYVZvY_4.2.F20.boolean.opBoolean","SPLIT",FACE,{"disambiguationData":[TD([subQ42])],"derivedFrom":makeQuery(id+"F0Hq7nSFAMYVZvY_4.1.F20.boolean.opBoolean","SPLIT",FACE,{"disambiguationData":[TD([subQ42])],"derivedFrom":makeQuery(id+"F17.boolean.opBoolean","COPY",FACE,{"derivedFrom":makeQuery(id+"F17.opExtrude","SWEPT_FACE",FACE,{"disambiguationData":[OSD([subQ3])]})})})})})})})})})})})})})})})})})})})})})})})})})})})})})})})})})})})})});}
            var Q164;
            {var subQ0=sQuery(id+"F19.wireOp",EDGE,"E158.MirrorCS");var subQ1=sQuery(id+"F19.wireOp",EDGE,"E157");var subQ3=sQuery(id+"F16.wireOp",EDGE,"E151");var subQ22=makeQuery(id+"F0Hq7nSFAMYVZvY_4.34.F20.opExtrude","SWEPT_FACE",FACE,{"disambiguationData":[OSD([subQ0])]});var subQ42=makeQuery(id+"F20.opExtrude","SWEPT_FACE",FACE,{"disambiguationData":[OSD([subQ1])]});Q164=makeQuery(id+"F0Hq7nSFAMYVZvY_4.35.F20.boolean.opBoolean","SPLIT",EDGE,{"disambiguationData":[TD([subQ22])],"derivedFrom":makeQuery(id+"F0Hq7nSFAMYVZvY_4.34.F20.boolean.opBoolean","SPLIT",EDGE,{"disambiguationData":[TD([subQ42])],"derivedFrom":makeQuery(id+"F0Hq7nSFAMYVZvY_4.33.F20.boolean.opBoolean","SPLIT",EDGE,{"disambiguationData":[TD([subQ42])],"derivedFrom":makeQuery(id+"F0Hq7nSFAMYVZvY_4.32.F20.boolean.opBoolean","SPLIT",EDGE,{"disambiguationData":[TD([subQ42])],"derivedFrom":makeQuery(id+"F0Hq7nSFAMYVZvY_4.31.F20.boolean.opBoolean","SPLIT",EDGE,{"disambiguationData":[TD([subQ42])],"derivedFrom":makeQuery(id+"F0Hq7nSFAMYVZvY_4.30.F20.boolean.opBoolean","SPLIT",EDGE,{"disambiguationData":[TD([subQ42])],"derivedFrom":makeQuery(id+"F0Hq7nSFAMYVZvY_4.29.F20.boolean.opBoolean","SPLIT",EDGE,{"disambiguationData":[TD([subQ42])],"derivedFrom":makeQuery(id+"F0Hq7nSFAMYVZvY_4.28.F20.boolean.opBoolean","SPLIT",EDGE,{"disambiguationData":[TD([subQ42])],"derivedFrom":makeQuery(id+"F0Hq7nSFAMYVZvY_4.27.F20.boolean.opBoolean","SPLIT",EDGE,{"disambiguationData":[TD([subQ42])],"derivedFrom":makeQuery(id+"F0Hq7nSFAMYVZvY_4.26.F20.boolean.opBoolean","SPLIT",EDGE,{"disambiguationData":[TD([subQ42])],"derivedFrom":makeQuery(id+"F0Hq7nSFAMYVZvY_4.25.F20.boolean.opBoolean","SPLIT",EDGE,{"disambiguationData":[TD([subQ42])],"derivedFrom":makeQuery(id+"F0Hq7nSFAMYVZvY_4.24.F20.boolean.opBoolean","SPLIT",EDGE,{"disambiguationData":[TD([subQ42])],"derivedFrom":makeQuery(id+"F0Hq7nSFAMYVZvY_4.23.F20.boolean.opBoolean","SPLIT",EDGE,{"disambiguationData":[TD([subQ42])],"derivedFrom":makeQuery(id+"F0Hq7nSFAMYVZvY_4.22.F20.boolean.opBoolean","SPLIT",EDGE,{"disambiguationData":[TD([subQ42])],"derivedFrom":makeQuery(id+"F0Hq7nSFAMYVZvY_4.21.F20.boolean.opBoolean","SPLIT",EDGE,{"disambiguationData":[TD([subQ42])],"derivedFrom":makeQuery(id+"F0Hq7nSFAMYVZvY_4.20.F20.boolean.opBoolean","SPLIT",EDGE,{"disambiguationData":[TD([subQ42])],"derivedFrom":makeQuery(id+"F0Hq7nSFAMYVZvY_4.19.F20.boolean.opBoolean","SPLIT",EDGE,{"disambiguationData":[TD([subQ42])],"derivedFrom":makeQuery(id+"F0Hq7nSFAMYVZvY_4.18.F20.boolean.opBoolean","SPLIT",EDGE,{"disambiguationData":[TD([subQ42])],"derivedFrom":makeQuery(id+"F0Hq7nSFAMYVZvY_4.17.F20.boolean.opBoolean","SPLIT",EDGE,{"disambiguationData":[TD([subQ42])],"derivedFrom":makeQuery(id+"F0Hq7nSFAMYVZvY_4.16.F20.boolean.opBoolean","SPLIT",EDGE,{"disambiguationData":[TD([subQ42])],"derivedFrom":makeQuery(id+"F0Hq7nSFAMYVZvY_4.15.F20.boolean.opBoolean","SPLIT",EDGE,{"disambiguationData":[TD([subQ42])],"derivedFrom":makeQuery(id+"F0Hq7nSFAMYVZvY_4.14.F20.boolean.opBoolean","SPLIT",EDGE,{"disambiguationData":[TD([subQ42])],"derivedFrom":makeQuery(id+"F0Hq7nSFAMYVZvY_4.13.F20.boolean.opBoolean","SPLIT",EDGE,{"disambiguationData":[TD([subQ42])],"derivedFrom":makeQuery(id+"F0Hq7nSFAMYVZvY_4.12.F20.boolean.opBoolean","SPLIT",EDGE,{"disambiguationData":[TD([subQ42])],"derivedFrom":makeQuery(id+"F0Hq7nSFAMYVZvY_4.11.F20.boolean.opBoolean","SPLIT",EDGE,{"disambiguationData":[TD([subQ42])],"derivedFrom":makeQuery(id+"F0Hq7nSFAMYVZvY_4.10.F20.boolean.opBoolean","SPLIT",EDGE,{"disambiguationData":[TD([subQ42])],"derivedFrom":makeQuery(id+"F0Hq7nSFAMYVZvY_4.9.F20.boolean.opBoolean","SPLIT",EDGE,{"disambiguationData":[TD([subQ42])],"derivedFrom":makeQuery(id+"F0Hq7nSFAMYVZvY_4.8.F20.boolean.opBoolean","SPLIT",EDGE,{"disambiguationData":[TD([subQ42])],"derivedFrom":makeQuery(id+"F0Hq7nSFAMYVZvY_4.7.F20.boolean.opBoolean","SPLIT",EDGE,{"disambiguationData":[TD([subQ42])],"derivedFrom":makeQuery(id+"F0Hq7nSFAMYVZvY_4.6.F20.boolean.opBoolean","SPLIT",EDGE,{"disambiguationData":[TD([subQ42])],"derivedFrom":makeQuery(id+"F0Hq7nSFAMYVZvY_4.5.F20.boolean.opBoolean","SPLIT",EDGE,{"disambiguationData":[TD([subQ42])],"derivedFrom":makeQuery(id+"F0Hq7nSFAMYVZvY_4.4.F20.boolean.opBoolean","SPLIT",EDGE,{"disambiguationData":[TD([subQ42])],"derivedFrom":makeQuery(id+"F0Hq7nSFAMYVZvY_4.3.F20.boolean.opBoolean","SPLIT",EDGE,{"disambiguationData":[TD([subQ42])],"derivedFrom":makeQuery(id+"F0Hq7nSFAMYVZvY_4.2.F20.boolean.opBoolean","SPLIT",EDGE,{"disambiguationData":[TD([subQ42])],"derivedFrom":makeQuery(id+"F0Hq7nSFAMYVZvY_4.1.F20.boolean.opBoolean","SPLIT",EDGE,{"disambiguationData":[TD([subQ42])],"derivedFrom":makeQuery(id+"F18.boolean.opBoolean","COPY",EDGE,{"derivedFrom":makeQuery(id+"F18.opExtrude","CAP_EDGE",EDGE,{"disambiguationData":[OSD([subQ3])],"isStart":false})})})})})})})})})})})})})})})})})})})})})})})})})})})})})})})})})})})})});}
            var Q165;
            Q165=makeQuery(id+"F0Hq7nSFAMYVZvY_4.4.F20.opExtrude","SWEPT_FACE",FACE,{"disambiguationData":[OSD([sQuery(id+"F19.wireOp",EDGE,"E157")])]});
            var Q166;
            Q166=makeQuery(id+"F0Hq7nSFAMYVZvY_4.4.F20.opExtrude","SWEPT_FACE",FACE,{"disambiguationData":[OSD([sQuery(id+"F19.wireOp",EDGE,"E158.MirrorCS")])]});
            var Q167;
            Q167=makeQuery(id+"F0Hq7nSFAMYVZvY_4.4.F20.opExtrude","CAP_EDGE",EDGE,{"disambiguationData":[OSD([sQuery(id+"F19.wireOp",EDGE,"E157")])],"isStart":false});
            var Q168;
            Q168=makeQuery(id+"F0Hq7nSFAMYVZvY_4.4.F20.opExtrude","CAP_EDGE",EDGE,{"disambiguationData":[OSD([sQuery(id+"F19.wireOp",EDGE,"E158.MirrorCS")])],"isStart":false});
            var Q169;
            Q169=makeQuery(id+"F0Hq7nSFAMYVZvY_4.36.F20.opExtrude","SWEPT_FACE",FACE,{"disambiguationData":[OSD([sQuery(id+"F19.wireOp",EDGE,"E157")])]});
            var Q170;
            Q170=makeQuery(id+"F0Hq7nSFAMYVZvY_4.36.F20.opExtrude","SWEPT_FACE",FACE,{"disambiguationData":[OSD([sQuery(id+"F19.wireOp",EDGE,"E158.MirrorCS")])]});
            var Q171;
            Q171=makeQuery(id+"F0Hq7nSFAMYVZvY_4.36.F20.opExtrude","CAP_EDGE",EDGE,{"disambiguationData":[OSD([sQuery(id+"F19.wireOp",EDGE,"E157")])],"isStart":false});
            var Q172;
            Q172=makeQuery(id+"F0Hq7nSFAMYVZvY_4.36.F20.opExtrude","CAP_EDGE",EDGE,{"disambiguationData":[OSD([sQuery(id+"F19.wireOp",EDGE,"E158.MirrorCS")])],"isStart":false});
            var Q173;
            {var subQ0=sQuery(id+"F16.wireOp",EDGE,"E151");var subQ2=sQuery(id+"F16.wireOp",EDGE,"E152");var subQ4=sQuery(id+"F19.wireOp",EDGE,"E158.MirrorCS");var subQ5=makeQuery(id+"F0Hq7nSFAMYVZvY_4.3.F20.opExtrude","SWEPT_FACE",FACE,{"disambiguationData":[OSD([subQ4])]});var subQ6=sQuery(id+"F19.wireOp",EDGE,"E157");var subQ7=makeQuery(id+"F20.opExtrude","SWEPT_FACE",FACE,{"disambiguationData":[OSD([subQ6])]});Q173=makeQuery(id+"F0Hq7nSFAMYVZvY_4.4.F20.boolean.opBoolean","SPLIT",FACE,{"disambiguationData":[TD([subQ5])],"derivedFrom":makeQuery(id+"F0Hq7nSFAMYVZvY_4.3.F20.boolean.opBoolean","SPLIT",FACE,{"disambiguationData":[TD([subQ7])],"derivedFrom":makeQuery(id+"F0Hq7nSFAMYVZvY_4.2.F20.boolean.opBoolean","SPLIT",FACE,{"disambiguationData":[TD([subQ7])],"derivedFrom":makeQuery(id+"F0Hq7nSFAMYVZvY_4.1.F20.boolean.opBoolean","SPLIT",FACE,{"disambiguationData":[TD([subQ7])],"derivedFrom":makeQuery(id+"F17.boolean.opBoolean","COPY",FACE,{"derivedFrom":makeQuery(id+"F17.opExtrude","CAP_FACE",FACE,{"disambiguationData":[OSD([subQ0,subQ2])],"isStart":false})})})})})});}
            var Q174;
            Q174=makeQuery(id+"F0Hq7nSFAMYVZvY_4.4.F20.opExtrude","CAP_EDGE",EDGE,{"disambiguationData":[OSD([sQuery(id+"F19.wireOp",EDGE,"E158.MirrorCS")])],"isStart":true});
            var Q175;
            {var subQ0=sQuery(id+"F19.wireOp",EDGE,"E158.MirrorCS");var subQ1=sQuery(id+"F19.wireOp",EDGE,"E157");var subQ3=sQuery(id+"F16.wireOp",EDGE,"E151");var subQ10=makeQuery(id+"F0Hq7nSFAMYVZvY_4.3.F20.opExtrude","SWEPT_FACE",FACE,{"disambiguationData":[OSD([subQ0])]});var subQ11=makeQuery(id+"F20.opExtrude","SWEPT_FACE",FACE,{"disambiguationData":[OSD([subQ1])]});Q175=makeQuery(id+"F0Hq7nSFAMYVZvY_4.4.F20.boolean.opBoolean","SPLIT",FACE,{"disambiguationData":[TD([subQ10])],"derivedFrom":makeQuery(id+"F0Hq7nSFAMYVZvY_4.3.F20.boolean.opBoolean","SPLIT",FACE,{"disambiguationData":[TD([subQ11])],"derivedFrom":makeQuery(id+"F0Hq7nSFAMYVZvY_4.2.F20.boolean.opBoolean","SPLIT",FACE,{"disambiguationData":[TD([subQ11])],"derivedFrom":makeQuery(id+"F0Hq7nSFAMYVZvY_4.1.F20.boolean.opBoolean","SPLIT",FACE,{"disambiguationData":[TD([subQ11])],"derivedFrom":makeQuery(id+"F17.boolean.opBoolean","COPY",FACE,{"derivedFrom":makeQuery(id+"F17.opExtrude","SWEPT_FACE",FACE,{"disambiguationData":[OSD([subQ3])]})})})})})});}
            var Q176;
            {var subQ0=sQuery(id+"F16.wireOp",EDGE,"E151");var subQ2=sQuery(id+"F16.wireOp",EDGE,"E152");var subQ4=sQuery(id+"F19.wireOp",EDGE,"E157");var subQ5=sQuery(id+"F19.wireOp",EDGE,"E158.MirrorCS");var subQ6=makeQuery(id+"F0Hq7nSFAMYVZvY_4.35.F20.opExtrude","SWEPT_FACE",FACE,{"disambiguationData":[OSD([subQ5])]});var subQ7=makeQuery(id+"F20.opExtrude","SWEPT_FACE",FACE,{"disambiguationData":[OSD([subQ4])]});Q176=makeQuery(id+"F0Hq7nSFAMYVZvY_4.36.F20.boolean.opBoolean","SPLIT",FACE,{"disambiguationData":[TD([subQ6])],"derivedFrom":makeQuery(id+"F0Hq7nSFAMYVZvY_4.35.F20.boolean.opBoolean","SPLIT",FACE,{"disambiguationData":[TD([subQ7])],"derivedFrom":makeQuery(id+"F0Hq7nSFAMYVZvY_4.34.F20.boolean.opBoolean","SPLIT",FACE,{"disambiguationData":[TD([subQ7])],"derivedFrom":makeQuery(id+"F0Hq7nSFAMYVZvY_4.33.F20.boolean.opBoolean","SPLIT",FACE,{"disambiguationData":[TD([subQ7])],"derivedFrom":makeQuery(id+"F0Hq7nSFAMYVZvY_4.32.F20.boolean.opBoolean","SPLIT",FACE,{"disambiguationData":[TD([subQ7])],"derivedFrom":makeQuery(id+"F0Hq7nSFAMYVZvY_4.31.F20.boolean.opBoolean","SPLIT",FACE,{"disambiguationData":[TD([subQ7])],"derivedFrom":makeQuery(id+"F0Hq7nSFAMYVZvY_4.30.F20.boolean.opBoolean","SPLIT",FACE,{"disambiguationData":[TD([subQ7])],"derivedFrom":makeQuery(id+"F0Hq7nSFAMYVZvY_4.29.F20.boolean.opBoolean","SPLIT",FACE,{"disambiguationData":[TD([subQ7])],"derivedFrom":makeQuery(id+"F0Hq7nSFAMYVZvY_4.28.F20.boolean.opBoolean","SPLIT",FACE,{"disambiguationData":[TD([subQ7])],"derivedFrom":makeQuery(id+"F0Hq7nSFAMYVZvY_4.27.F20.boolean.opBoolean","SPLIT",FACE,{"disambiguationData":[TD([subQ7])],"derivedFrom":makeQuery(id+"F0Hq7nSFAMYVZvY_4.26.F20.boolean.opBoolean","SPLIT",FACE,{"disambiguationData":[TD([subQ7])],"derivedFrom":makeQuery(id+"F0Hq7nSFAMYVZvY_4.25.F20.boolean.opBoolean","SPLIT",FACE,{"disambiguationData":[TD([subQ7])],"derivedFrom":makeQuery(id+"F0Hq7nSFAMYVZvY_4.24.F20.boolean.opBoolean","SPLIT",FACE,{"disambiguationData":[TD([subQ7])],"derivedFrom":makeQuery(id+"F0Hq7nSFAMYVZvY_4.23.F20.boolean.opBoolean","SPLIT",FACE,{"disambiguationData":[TD([subQ7])],"derivedFrom":makeQuery(id+"F0Hq7nSFAMYVZvY_4.22.F20.boolean.opBoolean","SPLIT",FACE,{"disambiguationData":[TD([subQ7])],"derivedFrom":makeQuery(id+"F0Hq7nSFAMYVZvY_4.21.F20.boolean.opBoolean","SPLIT",FACE,{"disambiguationData":[TD([subQ7])],"derivedFrom":makeQuery(id+"F0Hq7nSFAMYVZvY_4.20.F20.boolean.opBoolean","SPLIT",FACE,{"disambiguationData":[TD([subQ7])],"derivedFrom":makeQuery(id+"F0Hq7nSFAMYVZvY_4.19.F20.boolean.opBoolean","SPLIT",FACE,{"disambiguationData":[TD([subQ7])],"derivedFrom":makeQuery(id+"F0Hq7nSFAMYVZvY_4.18.F20.boolean.opBoolean","SPLIT",FACE,{"disambiguationData":[TD([subQ7])],"derivedFrom":makeQuery(id+"F0Hq7nSFAMYVZvY_4.17.F20.boolean.opBoolean","SPLIT",FACE,{"disambiguationData":[TD([subQ7])],"derivedFrom":makeQuery(id+"F0Hq7nSFAMYVZvY_4.16.F20.boolean.opBoolean","SPLIT",FACE,{"disambiguationData":[TD([subQ7])],"derivedFrom":makeQuery(id+"F0Hq7nSFAMYVZvY_4.15.F20.boolean.opBoolean","SPLIT",FACE,{"disambiguationData":[TD([subQ7])],"derivedFrom":makeQuery(id+"F0Hq7nSFAMYVZvY_4.14.F20.boolean.opBoolean","SPLIT",FACE,{"disambiguationData":[TD([subQ7])],"derivedFrom":makeQuery(id+"F0Hq7nSFAMYVZvY_4.13.F20.boolean.opBoolean","SPLIT",FACE,{"disambiguationData":[TD([subQ7])],"derivedFrom":makeQuery(id+"F0Hq7nSFAMYVZvY_4.12.F20.boolean.opBoolean","SPLIT",FACE,{"disambiguationData":[TD([subQ7])],"derivedFrom":makeQuery(id+"F0Hq7nSFAMYVZvY_4.11.F20.boolean.opBoolean","SPLIT",FACE,{"disambiguationData":[TD([subQ7])],"derivedFrom":makeQuery(id+"F0Hq7nSFAMYVZvY_4.10.F20.boolean.opBoolean","SPLIT",FACE,{"disambiguationData":[TD([subQ7])],"derivedFrom":makeQuery(id+"F0Hq7nSFAMYVZvY_4.9.F20.boolean.opBoolean","SPLIT",FACE,{"disambiguationData":[TD([subQ7])],"derivedFrom":makeQuery(id+"F0Hq7nSFAMYVZvY_4.8.F20.boolean.opBoolean","SPLIT",FACE,{"disambiguationData":[TD([subQ7])],"derivedFrom":makeQuery(id+"F0Hq7nSFAMYVZvY_4.7.F20.boolean.opBoolean","SPLIT",FACE,{"disambiguationData":[TD([subQ7])],"derivedFrom":makeQuery(id+"F0Hq7nSFAMYVZvY_4.6.F20.boolean.opBoolean","SPLIT",FACE,{"disambiguationData":[TD([subQ7])],"derivedFrom":makeQuery(id+"F0Hq7nSFAMYVZvY_4.5.F20.boolean.opBoolean","SPLIT",FACE,{"disambiguationData":[TD([subQ7])],"derivedFrom":makeQuery(id+"F0Hq7nSFAMYVZvY_4.4.F20.boolean.opBoolean","SPLIT",FACE,{"disambiguationData":[TD([subQ7])],"derivedFrom":makeQuery(id+"F0Hq7nSFAMYVZvY_4.3.F20.boolean.opBoolean","SPLIT",FACE,{"disambiguationData":[TD([subQ7])],"derivedFrom":makeQuery(id+"F0Hq7nSFAMYVZvY_4.2.F20.boolean.opBoolean","SPLIT",FACE,{"disambiguationData":[TD([subQ7])],"derivedFrom":makeQuery(id+"F0Hq7nSFAMYVZvY_4.1.F20.boolean.opBoolean","SPLIT",FACE,{"disambiguationData":[TD([subQ7])],"derivedFrom":makeQuery(id+"F17.boolean.opBoolean","COPY",FACE,{"derivedFrom":makeQuery(id+"F17.opExtrude","CAP_FACE",FACE,{"disambiguationData":[OSD([subQ0,subQ2])],"isStart":false})})})})})})})})})})})})})})})})})})})})})})})})})})})})})})})})})})})})})});}
            var Q177;
            Q177=makeQuery(id+"F0Hq7nSFAMYVZvY_4.36.F20.opExtrude","CAP_EDGE",EDGE,{"disambiguationData":[OSD([sQuery(id+"F19.wireOp",EDGE,"E157")])],"isStart":true});
            var Q178;
            {var subQ0=sQuery(id+"F19.wireOp",EDGE,"E158.MirrorCS");var subQ1=sQuery(id+"F19.wireOp",EDGE,"E157");var subQ3=sQuery(id+"F16.wireOp",EDGE,"E151");var subQ25=makeQuery(id+"F0Hq7nSFAMYVZvY_4.35.F20.opExtrude","SWEPT_FACE",FACE,{"disambiguationData":[OSD([subQ0])]});var subQ43=makeQuery(id+"F20.opExtrude","SWEPT_FACE",FACE,{"disambiguationData":[OSD([subQ1])]});Q178=makeQuery(id+"F0Hq7nSFAMYVZvY_4.36.F20.boolean.opBoolean","SPLIT",FACE,{"disambiguationData":[TD([subQ25])],"derivedFrom":makeQuery(id+"F0Hq7nSFAMYVZvY_4.35.F20.boolean.opBoolean","SPLIT",FACE,{"disambiguationData":[TD([subQ43])],"derivedFrom":makeQuery(id+"F0Hq7nSFAMYVZvY_4.34.F20.boolean.opBoolean","SPLIT",FACE,{"disambiguationData":[TD([subQ43])],"derivedFrom":makeQuery(id+"F0Hq7nSFAMYVZvY_4.33.F20.boolean.opBoolean","SPLIT",FACE,{"disambiguationData":[TD([subQ43])],"derivedFrom":makeQuery(id+"F0Hq7nSFAMYVZvY_4.32.F20.boolean.opBoolean","SPLIT",FACE,{"disambiguationData":[TD([subQ43])],"derivedFrom":makeQuery(id+"F0Hq7nSFAMYVZvY_4.31.F20.boolean.opBoolean","SPLIT",FACE,{"disambiguationData":[TD([subQ43])],"derivedFrom":makeQuery(id+"F0Hq7nSFAMYVZvY_4.30.F20.boolean.opBoolean","SPLIT",FACE,{"disambiguationData":[TD([subQ43])],"derivedFrom":makeQuery(id+"F0Hq7nSFAMYVZvY_4.29.F20.boolean.opBoolean","SPLIT",FACE,{"disambiguationData":[TD([subQ43])],"derivedFrom":makeQuery(id+"F0Hq7nSFAMYVZvY_4.28.F20.boolean.opBoolean","SPLIT",FACE,{"disambiguationData":[TD([subQ43])],"derivedFrom":makeQuery(id+"F0Hq7nSFAMYVZvY_4.27.F20.boolean.opBoolean","SPLIT",FACE,{"disambiguationData":[TD([subQ43])],"derivedFrom":makeQuery(id+"F0Hq7nSFAMYVZvY_4.26.F20.boolean.opBoolean","SPLIT",FACE,{"disambiguationData":[TD([subQ43])],"derivedFrom":makeQuery(id+"F0Hq7nSFAMYVZvY_4.25.F20.boolean.opBoolean","SPLIT",FACE,{"disambiguationData":[TD([subQ43])],"derivedFrom":makeQuery(id+"F0Hq7nSFAMYVZvY_4.24.F20.boolean.opBoolean","SPLIT",FACE,{"disambiguationData":[TD([subQ43])],"derivedFrom":makeQuery(id+"F0Hq7nSFAMYVZvY_4.23.F20.boolean.opBoolean","SPLIT",FACE,{"disambiguationData":[TD([subQ43])],"derivedFrom":makeQuery(id+"F0Hq7nSFAMYVZvY_4.22.F20.boolean.opBoolean","SPLIT",FACE,{"disambiguationData":[TD([subQ43])],"derivedFrom":makeQuery(id+"F0Hq7nSFAMYVZvY_4.21.F20.boolean.opBoolean","SPLIT",FACE,{"disambiguationData":[TD([subQ43])],"derivedFrom":makeQuery(id+"F0Hq7nSFAMYVZvY_4.20.F20.boolean.opBoolean","SPLIT",FACE,{"disambiguationData":[TD([subQ43])],"derivedFrom":makeQuery(id+"F0Hq7nSFAMYVZvY_4.19.F20.boolean.opBoolean","SPLIT",FACE,{"disambiguationData":[TD([subQ43])],"derivedFrom":makeQuery(id+"F0Hq7nSFAMYVZvY_4.18.F20.boolean.opBoolean","SPLIT",FACE,{"disambiguationData":[TD([subQ43])],"derivedFrom":makeQuery(id+"F0Hq7nSFAMYVZvY_4.17.F20.boolean.opBoolean","SPLIT",FACE,{"disambiguationData":[TD([subQ43])],"derivedFrom":makeQuery(id+"F0Hq7nSFAMYVZvY_4.16.F20.boolean.opBoolean","SPLIT",FACE,{"disambiguationData":[TD([subQ43])],"derivedFrom":makeQuery(id+"F0Hq7nSFAMYVZvY_4.15.F20.boolean.opBoolean","SPLIT",FACE,{"disambiguationData":[TD([subQ43])],"derivedFrom":makeQuery(id+"F0Hq7nSFAMYVZvY_4.14.F20.boolean.opBoolean","SPLIT",FACE,{"disambiguationData":[TD([subQ43])],"derivedFrom":makeQuery(id+"F0Hq7nSFAMYVZvY_4.13.F20.boolean.opBoolean","SPLIT",FACE,{"disambiguationData":[TD([subQ43])],"derivedFrom":makeQuery(id+"F0Hq7nSFAMYVZvY_4.12.F20.boolean.opBoolean","SPLIT",FACE,{"disambiguationData":[TD([subQ43])],"derivedFrom":makeQuery(id+"F0Hq7nSFAMYVZvY_4.11.F20.boolean.opBoolean","SPLIT",FACE,{"disambiguationData":[TD([subQ43])],"derivedFrom":makeQuery(id+"F0Hq7nSFAMYVZvY_4.10.F20.boolean.opBoolean","SPLIT",FACE,{"disambiguationData":[TD([subQ43])],"derivedFrom":makeQuery(id+"F0Hq7nSFAMYVZvY_4.9.F20.boolean.opBoolean","SPLIT",FACE,{"disambiguationData":[TD([subQ43])],"derivedFrom":makeQuery(id+"F0Hq7nSFAMYVZvY_4.8.F20.boolean.opBoolean","SPLIT",FACE,{"disambiguationData":[TD([subQ43])],"derivedFrom":makeQuery(id+"F0Hq7nSFAMYVZvY_4.7.F20.boolean.opBoolean","SPLIT",FACE,{"disambiguationData":[TD([subQ43])],"derivedFrom":makeQuery(id+"F0Hq7nSFAMYVZvY_4.6.F20.boolean.opBoolean","SPLIT",FACE,{"disambiguationData":[TD([subQ43])],"derivedFrom":makeQuery(id+"F0Hq7nSFAMYVZvY_4.5.F20.boolean.opBoolean","SPLIT",FACE,{"disambiguationData":[TD([subQ43])],"derivedFrom":makeQuery(id+"F0Hq7nSFAMYVZvY_4.4.F20.boolean.opBoolean","SPLIT",FACE,{"disambiguationData":[TD([subQ43])],"derivedFrom":makeQuery(id+"F0Hq7nSFAMYVZvY_4.3.F20.boolean.opBoolean","SPLIT",FACE,{"disambiguationData":[TD([subQ43])],"derivedFrom":makeQuery(id+"F0Hq7nSFAMYVZvY_4.2.F20.boolean.opBoolean","SPLIT",FACE,{"disambiguationData":[TD([subQ43])],"derivedFrom":makeQuery(id+"F0Hq7nSFAMYVZvY_4.1.F20.boolean.opBoolean","SPLIT",FACE,{"disambiguationData":[TD([subQ43])],"derivedFrom":makeQuery(id+"F17.boolean.opBoolean","COPY",FACE,{"derivedFrom":makeQuery(id+"F17.opExtrude","SWEPT_FACE",FACE,{"disambiguationData":[OSD([subQ3])]})})})})})})})})})})})})})})})})})})})})})})})})})})})})})})})})})})})})})});}
            var Q179;
            {var subQ0=sQuery(id+"F19.wireOp",EDGE,"E158.MirrorCS");var subQ1=sQuery(id+"F19.wireOp",EDGE,"E157");var subQ3=sQuery(id+"F16.wireOp",EDGE,"E151");var subQ23=makeQuery(id+"F0Hq7nSFAMYVZvY_4.35.F20.opExtrude","SWEPT_FACE",FACE,{"disambiguationData":[OSD([subQ0])]});var subQ43=makeQuery(id+"F20.opExtrude","SWEPT_FACE",FACE,{"disambiguationData":[OSD([subQ1])]});Q179=makeQuery(id+"F0Hq7nSFAMYVZvY_4.36.F20.boolean.opBoolean","SPLIT",EDGE,{"disambiguationData":[TD([subQ23])],"derivedFrom":makeQuery(id+"F0Hq7nSFAMYVZvY_4.35.F20.boolean.opBoolean","SPLIT",EDGE,{"disambiguationData":[TD([subQ43])],"derivedFrom":makeQuery(id+"F0Hq7nSFAMYVZvY_4.34.F20.boolean.opBoolean","SPLIT",EDGE,{"disambiguationData":[TD([subQ43])],"derivedFrom":makeQuery(id+"F0Hq7nSFAMYVZvY_4.33.F20.boolean.opBoolean","SPLIT",EDGE,{"disambiguationData":[TD([subQ43])],"derivedFrom":makeQuery(id+"F0Hq7nSFAMYVZvY_4.32.F20.boolean.opBoolean","SPLIT",EDGE,{"disambiguationData":[TD([subQ43])],"derivedFrom":makeQuery(id+"F0Hq7nSFAMYVZvY_4.31.F20.boolean.opBoolean","SPLIT",EDGE,{"disambiguationData":[TD([subQ43])],"derivedFrom":makeQuery(id+"F0Hq7nSFAMYVZvY_4.30.F20.boolean.opBoolean","SPLIT",EDGE,{"disambiguationData":[TD([subQ43])],"derivedFrom":makeQuery(id+"F0Hq7nSFAMYVZvY_4.29.F20.boolean.opBoolean","SPLIT",EDGE,{"disambiguationData":[TD([subQ43])],"derivedFrom":makeQuery(id+"F0Hq7nSFAMYVZvY_4.28.F20.boolean.opBoolean","SPLIT",EDGE,{"disambiguationData":[TD([subQ43])],"derivedFrom":makeQuery(id+"F0Hq7nSFAMYVZvY_4.27.F20.boolean.opBoolean","SPLIT",EDGE,{"disambiguationData":[TD([subQ43])],"derivedFrom":makeQuery(id+"F0Hq7nSFAMYVZvY_4.26.F20.boolean.opBoolean","SPLIT",EDGE,{"disambiguationData":[TD([subQ43])],"derivedFrom":makeQuery(id+"F0Hq7nSFAMYVZvY_4.25.F20.boolean.opBoolean","SPLIT",EDGE,{"disambiguationData":[TD([subQ43])],"derivedFrom":makeQuery(id+"F0Hq7nSFAMYVZvY_4.24.F20.boolean.opBoolean","SPLIT",EDGE,{"disambiguationData":[TD([subQ43])],"derivedFrom":makeQuery(id+"F0Hq7nSFAMYVZvY_4.23.F20.boolean.opBoolean","SPLIT",EDGE,{"disambiguationData":[TD([subQ43])],"derivedFrom":makeQuery(id+"F0Hq7nSFAMYVZvY_4.22.F20.boolean.opBoolean","SPLIT",EDGE,{"disambiguationData":[TD([subQ43])],"derivedFrom":makeQuery(id+"F0Hq7nSFAMYVZvY_4.21.F20.boolean.opBoolean","SPLIT",EDGE,{"disambiguationData":[TD([subQ43])],"derivedFrom":makeQuery(id+"F0Hq7nSFAMYVZvY_4.20.F20.boolean.opBoolean","SPLIT",EDGE,{"disambiguationData":[TD([subQ43])],"derivedFrom":makeQuery(id+"F0Hq7nSFAMYVZvY_4.19.F20.boolean.opBoolean","SPLIT",EDGE,{"disambiguationData":[TD([subQ43])],"derivedFrom":makeQuery(id+"F0Hq7nSFAMYVZvY_4.18.F20.boolean.opBoolean","SPLIT",EDGE,{"disambiguationData":[TD([subQ43])],"derivedFrom":makeQuery(id+"F0Hq7nSFAMYVZvY_4.17.F20.boolean.opBoolean","SPLIT",EDGE,{"disambiguationData":[TD([subQ43])],"derivedFrom":makeQuery(id+"F0Hq7nSFAMYVZvY_4.16.F20.boolean.opBoolean","SPLIT",EDGE,{"disambiguationData":[TD([subQ43])],"derivedFrom":makeQuery(id+"F0Hq7nSFAMYVZvY_4.15.F20.boolean.opBoolean","SPLIT",EDGE,{"disambiguationData":[TD([subQ43])],"derivedFrom":makeQuery(id+"F0Hq7nSFAMYVZvY_4.14.F20.boolean.opBoolean","SPLIT",EDGE,{"disambiguationData":[TD([subQ43])],"derivedFrom":makeQuery(id+"F0Hq7nSFAMYVZvY_4.13.F20.boolean.opBoolean","SPLIT",EDGE,{"disambiguationData":[TD([subQ43])],"derivedFrom":makeQuery(id+"F0Hq7nSFAMYVZvY_4.12.F20.boolean.opBoolean","SPLIT",EDGE,{"disambiguationData":[TD([subQ43])],"derivedFrom":makeQuery(id+"F0Hq7nSFAMYVZvY_4.11.F20.boolean.opBoolean","SPLIT",EDGE,{"disambiguationData":[TD([subQ43])],"derivedFrom":makeQuery(id+"F0Hq7nSFAMYVZvY_4.10.F20.boolean.opBoolean","SPLIT",EDGE,{"disambiguationData":[TD([subQ43])],"derivedFrom":makeQuery(id+"F0Hq7nSFAMYVZvY_4.9.F20.boolean.opBoolean","SPLIT",EDGE,{"disambiguationData":[TD([subQ43])],"derivedFrom":makeQuery(id+"F0Hq7nSFAMYVZvY_4.8.F20.boolean.opBoolean","SPLIT",EDGE,{"disambiguationData":[TD([subQ43])],"derivedFrom":makeQuery(id+"F0Hq7nSFAMYVZvY_4.7.F20.boolean.opBoolean","SPLIT",EDGE,{"disambiguationData":[TD([subQ43])],"derivedFrom":makeQuery(id+"F0Hq7nSFAMYVZvY_4.6.F20.boolean.opBoolean","SPLIT",EDGE,{"disambiguationData":[TD([subQ43])],"derivedFrom":makeQuery(id+"F0Hq7nSFAMYVZvY_4.5.F20.boolean.opBoolean","SPLIT",EDGE,{"disambiguationData":[TD([subQ43])],"derivedFrom":makeQuery(id+"F0Hq7nSFAMYVZvY_4.4.F20.boolean.opBoolean","SPLIT",EDGE,{"disambiguationData":[TD([subQ43])],"derivedFrom":makeQuery(id+"F0Hq7nSFAMYVZvY_4.3.F20.boolean.opBoolean","SPLIT",EDGE,{"disambiguationData":[TD([subQ43])],"derivedFrom":makeQuery(id+"F0Hq7nSFAMYVZvY_4.2.F20.boolean.opBoolean","SPLIT",EDGE,{"disambiguationData":[TD([subQ43])],"derivedFrom":makeQuery(id+"F0Hq7nSFAMYVZvY_4.1.F20.boolean.opBoolean","SPLIT",EDGE,{"disambiguationData":[TD([subQ43])],"derivedFrom":makeQuery(id+"F18.boolean.opBoolean","COPY",EDGE,{"derivedFrom":makeQuery(id+"F18.opExtrude","CAP_EDGE",EDGE,{"disambiguationData":[OSD([subQ3])],"isStart":false})})})})})})})})})})})})})})})})})})})})})})})})})})})})})})})})})})})})})});}
            var Q180;
            Q180=makeQuery(id+"F0Hq7nSFAMYVZvY_4.5.F20.opExtrude","SWEPT_FACE",FACE,{"disambiguationData":[OSD([sQuery(id+"F19.wireOp",EDGE,"E157")])]});
            var Q181;
            Q181=makeQuery(id+"F0Hq7nSFAMYVZvY_4.5.F20.opExtrude","SWEPT_FACE",FACE,{"disambiguationData":[OSD([sQuery(id+"F19.wireOp",EDGE,"E158.MirrorCS")])]});
            var Q182;
            Q182=makeQuery(id+"F0Hq7nSFAMYVZvY_4.5.F20.opExtrude","CAP_EDGE",EDGE,{"disambiguationData":[OSD([sQuery(id+"F19.wireOp",EDGE,"E157")])],"isStart":false});
            var Q183;
            Q183=makeQuery(id+"F0Hq7nSFAMYVZvY_4.5.F20.opExtrude","CAP_EDGE",EDGE,{"disambiguationData":[OSD([sQuery(id+"F19.wireOp",EDGE,"E158.MirrorCS")])],"isStart":false});
            var Q184;
            Q184=makeQuery(id+"F0Hq7nSFAMYVZvY_4.37.F20.opExtrude","SWEPT_FACE",FACE,{"disambiguationData":[OSD([sQuery(id+"F19.wireOp",EDGE,"E157")])]});
            var Q185;
            Q185=makeQuery(id+"F0Hq7nSFAMYVZvY_4.37.F20.opExtrude","CAP_EDGE",EDGE,{"disambiguationData":[OSD([sQuery(id+"F19.wireOp",EDGE,"E157")])],"isStart":false});
            var Q186;
            Q186=makeQuery(id+"F0Hq7nSFAMYVZvY_4.37.F20.opExtrude","CAP_EDGE",EDGE,{"disambiguationData":[OSD([sQuery(id+"F19.wireOp",EDGE,"E158.MirrorCS")])],"isStart":false});
            var Q187;
            {var subQ0=sQuery(id+"F16.wireOp",EDGE,"E151");var subQ2=sQuery(id+"F19.wireOp",EDGE,"E157");var subQ3=sQuery(id+"F16.wireOp",EDGE,"E152");var subQ5=sQuery(id+"F19.wireOp",EDGE,"E158.MirrorCS");var subQ6=makeQuery(id+"F0Hq7nSFAMYVZvY_4.4.F20.opExtrude","SWEPT_FACE",FACE,{"disambiguationData":[OSD([subQ5])]});var subQ7=makeQuery(id+"F20.opExtrude","SWEPT_FACE",FACE,{"disambiguationData":[OSD([subQ2])]});Q187=makeQuery(id+"F0Hq7nSFAMYVZvY_4.5.F20.boolean.opBoolean","SPLIT",FACE,{"disambiguationData":[TD([subQ6])],"derivedFrom":makeQuery(id+"F0Hq7nSFAMYVZvY_4.4.F20.boolean.opBoolean","SPLIT",FACE,{"disambiguationData":[TD([subQ7])],"derivedFrom":makeQuery(id+"F0Hq7nSFAMYVZvY_4.3.F20.boolean.opBoolean","SPLIT",FACE,{"disambiguationData":[TD([subQ7])],"derivedFrom":makeQuery(id+"F0Hq7nSFAMYVZvY_4.2.F20.boolean.opBoolean","SPLIT",FACE,{"disambiguationData":[TD([subQ7])],"derivedFrom":makeQuery(id+"F0Hq7nSFAMYVZvY_4.1.F20.boolean.opBoolean","SPLIT",FACE,{"disambiguationData":[TD([subQ7])],"derivedFrom":makeQuery(id+"F17.boolean.opBoolean","COPY",FACE,{"derivedFrom":makeQuery(id+"F17.opExtrude","CAP_FACE",FACE,{"disambiguationData":[OSD([subQ0,subQ3])],"isStart":false})})})})})})});}
            var Q188;
            Q188=makeQuery(id+"F0Hq7nSFAMYVZvY_4.5.F20.opExtrude","CAP_EDGE",EDGE,{"disambiguationData":[OSD([sQuery(id+"F19.wireOp",EDGE,"E158.MirrorCS")])],"isStart":true});
            var Q189;
            {var subQ0=sQuery(id+"F19.wireOp",EDGE,"E158.MirrorCS");var subQ1=sQuery(id+"F19.wireOp",EDGE,"E157");var subQ3=sQuery(id+"F16.wireOp",EDGE,"E151");var subQ7=makeQuery(id+"F0Hq7nSFAMYVZvY_4.4.F20.opExtrude","SWEPT_FACE",FACE,{"disambiguationData":[OSD([subQ0])]});var subQ12=makeQuery(id+"F20.opExtrude","SWEPT_FACE",FACE,{"disambiguationData":[OSD([subQ1])]});Q189=makeQuery(id+"F0Hq7nSFAMYVZvY_4.5.F20.boolean.opBoolean","SPLIT",FACE,{"disambiguationData":[TD([subQ7])],"derivedFrom":makeQuery(id+"F0Hq7nSFAMYVZvY_4.4.F20.boolean.opBoolean","SPLIT",FACE,{"disambiguationData":[TD([subQ12])],"derivedFrom":makeQuery(id+"F0Hq7nSFAMYVZvY_4.3.F20.boolean.opBoolean","SPLIT",FACE,{"disambiguationData":[TD([subQ12])],"derivedFrom":makeQuery(id+"F0Hq7nSFAMYVZvY_4.2.F20.boolean.opBoolean","SPLIT",FACE,{"disambiguationData":[TD([subQ12])],"derivedFrom":makeQuery(id+"F0Hq7nSFAMYVZvY_4.1.F20.boolean.opBoolean","SPLIT",FACE,{"disambiguationData":[TD([subQ12])],"derivedFrom":makeQuery(id+"F17.boolean.opBoolean","COPY",FACE,{"derivedFrom":makeQuery(id+"F17.opExtrude","SWEPT_FACE",FACE,{"disambiguationData":[OSD([subQ3])]})})})})})})});}
            var Q190;
            {var subQ0=sQuery(id+"F19.wireOp",EDGE,"E158.MirrorCS");var subQ1=sQuery(id+"F19.wireOp",EDGE,"E157");var subQ3=sQuery(id+"F16.wireOp",EDGE,"E151");var subQ8=makeQuery(id+"F0Hq7nSFAMYVZvY_4.4.F20.opExtrude","SWEPT_FACE",FACE,{"disambiguationData":[OSD([subQ0])]});var subQ12=makeQuery(id+"F20.opExtrude","SWEPT_FACE",FACE,{"disambiguationData":[OSD([subQ1])]});Q190=makeQuery(id+"F0Hq7nSFAMYVZvY_4.5.F20.boolean.opBoolean","SPLIT",EDGE,{"disambiguationData":[TD([subQ8])],"derivedFrom":makeQuery(id+"F0Hq7nSFAMYVZvY_4.4.F20.boolean.opBoolean","SPLIT",EDGE,{"disambiguationData":[TD([subQ12])],"derivedFrom":makeQuery(id+"F0Hq7nSFAMYVZvY_4.3.F20.boolean.opBoolean","SPLIT",EDGE,{"disambiguationData":[TD([subQ12])],"derivedFrom":makeQuery(id+"F0Hq7nSFAMYVZvY_4.2.F20.boolean.opBoolean","SPLIT",EDGE,{"disambiguationData":[TD([subQ12])],"derivedFrom":makeQuery(id+"F0Hq7nSFAMYVZvY_4.1.F20.boolean.opBoolean","SPLIT",EDGE,{"disambiguationData":[TD([subQ12])],"derivedFrom":makeQuery(id+"F18.boolean.opBoolean","COPY",EDGE,{"derivedFrom":makeQuery(id+"F18.opExtrude","CAP_EDGE",EDGE,{"disambiguationData":[OSD([subQ3])],"isStart":false})})})})})})});}
            var Q191;
            {var subQ0=sQuery(id+"F16.wireOp",EDGE,"E151");var subQ2=sQuery(id+"F19.wireOp",EDGE,"E158.MirrorCS");var subQ3=makeQuery(id+"F0Hq7nSFAMYVZvY_4.36.F20.opExtrude","SWEPT_FACE",FACE,{"disambiguationData":[OSD([subQ2])]});var subQ4=sQuery(id+"F16.wireOp",EDGE,"E152");var subQ6=sQuery(id+"F19.wireOp",EDGE,"E157");var subQ7=makeQuery(id+"F20.opExtrude","SWEPT_FACE",FACE,{"disambiguationData":[OSD([subQ6])]});Q191=makeQuery(id+"F0Hq7nSFAMYVZvY_4.37.F20.boolean.opBoolean","SPLIT",FACE,{"disambiguationData":[TD([subQ3])],"derivedFrom":makeQuery(id+"F0Hq7nSFAMYVZvY_4.36.F20.boolean.opBoolean","SPLIT",FACE,{"disambiguationData":[TD([subQ7])],"derivedFrom":makeQuery(id+"F0Hq7nSFAMYVZvY_4.35.F20.boolean.opBoolean","SPLIT",FACE,{"disambiguationData":[TD([subQ7])],"derivedFrom":makeQuery(id+"F0Hq7nSFAMYVZvY_4.34.F20.boolean.opBoolean","SPLIT",FACE,{"disambiguationData":[TD([subQ7])],"derivedFrom":makeQuery(id+"F0Hq7nSFAMYVZvY_4.33.F20.boolean.opBoolean","SPLIT",FACE,{"disambiguationData":[TD([subQ7])],"derivedFrom":makeQuery(id+"F0Hq7nSFAMYVZvY_4.32.F20.boolean.opBoolean","SPLIT",FACE,{"disambiguationData":[TD([subQ7])],"derivedFrom":makeQuery(id+"F0Hq7nSFAMYVZvY_4.31.F20.boolean.opBoolean","SPLIT",FACE,{"disambiguationData":[TD([subQ7])],"derivedFrom":makeQuery(id+"F0Hq7nSFAMYVZvY_4.30.F20.boolean.opBoolean","SPLIT",FACE,{"disambiguationData":[TD([subQ7])],"derivedFrom":makeQuery(id+"F0Hq7nSFAMYVZvY_4.29.F20.boolean.opBoolean","SPLIT",FACE,{"disambiguationData":[TD([subQ7])],"derivedFrom":makeQuery(id+"F0Hq7nSFAMYVZvY_4.28.F20.boolean.opBoolean","SPLIT",FACE,{"disambiguationData":[TD([subQ7])],"derivedFrom":makeQuery(id+"F0Hq7nSFAMYVZvY_4.27.F20.boolean.opBoolean","SPLIT",FACE,{"disambiguationData":[TD([subQ7])],"derivedFrom":makeQuery(id+"F0Hq7nSFAMYVZvY_4.26.F20.boolean.opBoolean","SPLIT",FACE,{"disambiguationData":[TD([subQ7])],"derivedFrom":makeQuery(id+"F0Hq7nSFAMYVZvY_4.25.F20.boolean.opBoolean","SPLIT",FACE,{"disambiguationData":[TD([subQ7])],"derivedFrom":makeQuery(id+"F0Hq7nSFAMYVZvY_4.24.F20.boolean.opBoolean","SPLIT",FACE,{"disambiguationData":[TD([subQ7])],"derivedFrom":makeQuery(id+"F0Hq7nSFAMYVZvY_4.23.F20.boolean.opBoolean","SPLIT",FACE,{"disambiguationData":[TD([subQ7])],"derivedFrom":makeQuery(id+"F0Hq7nSFAMYVZvY_4.22.F20.boolean.opBoolean","SPLIT",FACE,{"disambiguationData":[TD([subQ7])],"derivedFrom":makeQuery(id+"F0Hq7nSFAMYVZvY_4.21.F20.boolean.opBoolean","SPLIT",FACE,{"disambiguationData":[TD([subQ7])],"derivedFrom":makeQuery(id+"F0Hq7nSFAMYVZvY_4.20.F20.boolean.opBoolean","SPLIT",FACE,{"disambiguationData":[TD([subQ7])],"derivedFrom":makeQuery(id+"F0Hq7nSFAMYVZvY_4.19.F20.boolean.opBoolean","SPLIT",FACE,{"disambiguationData":[TD([subQ7])],"derivedFrom":makeQuery(id+"F0Hq7nSFAMYVZvY_4.18.F20.boolean.opBoolean","SPLIT",FACE,{"disambiguationData":[TD([subQ7])],"derivedFrom":makeQuery(id+"F0Hq7nSFAMYVZvY_4.17.F20.boolean.opBoolean","SPLIT",FACE,{"disambiguationData":[TD([subQ7])],"derivedFrom":makeQuery(id+"F0Hq7nSFAMYVZvY_4.16.F20.boolean.opBoolean","SPLIT",FACE,{"disambiguationData":[TD([subQ7])],"derivedFrom":makeQuery(id+"F0Hq7nSFAMYVZvY_4.15.F20.boolean.opBoolean","SPLIT",FACE,{"disambiguationData":[TD([subQ7])],"derivedFrom":makeQuery(id+"F0Hq7nSFAMYVZvY_4.14.F20.boolean.opBoolean","SPLIT",FACE,{"disambiguationData":[TD([subQ7])],"derivedFrom":makeQuery(id+"F0Hq7nSFAMYVZvY_4.13.F20.boolean.opBoolean","SPLIT",FACE,{"disambiguationData":[TD([subQ7])],"derivedFrom":makeQuery(id+"F0Hq7nSFAMYVZvY_4.12.F20.boolean.opBoolean","SPLIT",FACE,{"disambiguationData":[TD([subQ7])],"derivedFrom":makeQuery(id+"F0Hq7nSFAMYVZvY_4.11.F20.boolean.opBoolean","SPLIT",FACE,{"disambiguationData":[TD([subQ7])],"derivedFrom":makeQuery(id+"F0Hq7nSFAMYVZvY_4.10.F20.boolean.opBoolean","SPLIT",FACE,{"disambiguationData":[TD([subQ7])],"derivedFrom":makeQuery(id+"F0Hq7nSFAMYVZvY_4.9.F20.boolean.opBoolean","SPLIT",FACE,{"disambiguationData":[TD([subQ7])],"derivedFrom":makeQuery(id+"F0Hq7nSFAMYVZvY_4.8.F20.boolean.opBoolean","SPLIT",FACE,{"disambiguationData":[TD([subQ7])],"derivedFrom":makeQuery(id+"F0Hq7nSFAMYVZvY_4.7.F20.boolean.opBoolean","SPLIT",FACE,{"disambiguationData":[TD([subQ7])],"derivedFrom":makeQuery(id+"F0Hq7nSFAMYVZvY_4.6.F20.boolean.opBoolean","SPLIT",FACE,{"disambiguationData":[TD([subQ7])],"derivedFrom":makeQuery(id+"F0Hq7nSFAMYVZvY_4.5.F20.boolean.opBoolean","SPLIT",FACE,{"disambiguationData":[TD([subQ7])],"derivedFrom":makeQuery(id+"F0Hq7nSFAMYVZvY_4.4.F20.boolean.opBoolean","SPLIT",FACE,{"disambiguationData":[TD([subQ7])],"derivedFrom":makeQuery(id+"F0Hq7nSFAMYVZvY_4.3.F20.boolean.opBoolean","SPLIT",FACE,{"disambiguationData":[TD([subQ7])],"derivedFrom":makeQuery(id+"F0Hq7nSFAMYVZvY_4.2.F20.boolean.opBoolean","SPLIT",FACE,{"disambiguationData":[TD([subQ7])],"derivedFrom":makeQuery(id+"F0Hq7nSFAMYVZvY_4.1.F20.boolean.opBoolean","SPLIT",FACE,{"disambiguationData":[TD([subQ7])],"derivedFrom":makeQuery(id+"F17.boolean.opBoolean","COPY",FACE,{"derivedFrom":makeQuery(id+"F17.opExtrude","CAP_FACE",FACE,{"disambiguationData":[OSD([subQ0,subQ4])],"isStart":false})})})})})})})})})})})})})})})})})})})})})})})})})})})})})})})})})})})})})})});}
            var Q192;
            Q192=makeQuery(id+"F0Hq7nSFAMYVZvY_4.37.F20.opExtrude","CAP_EDGE",EDGE,{"disambiguationData":[OSD([sQuery(id+"F19.wireOp",EDGE,"E157")])],"isStart":true});
            var Q193;
            {var subQ0=sQuery(id+"F19.wireOp",EDGE,"E158.MirrorCS");var subQ1=sQuery(id+"F19.wireOp",EDGE,"E157");var subQ3=sQuery(id+"F16.wireOp",EDGE,"E151");var subQ21=makeQuery(id+"F0Hq7nSFAMYVZvY_4.36.F20.opExtrude","SWEPT_FACE",FACE,{"disambiguationData":[OSD([subQ0])]});var subQ44=makeQuery(id+"F20.opExtrude","SWEPT_FACE",FACE,{"disambiguationData":[OSD([subQ1])]});Q193=makeQuery(id+"F0Hq7nSFAMYVZvY_4.37.F20.boolean.opBoolean","SPLIT",FACE,{"disambiguationData":[TD([subQ21])],"derivedFrom":makeQuery(id+"F0Hq7nSFAMYVZvY_4.36.F20.boolean.opBoolean","SPLIT",FACE,{"disambiguationData":[TD([subQ44])],"derivedFrom":makeQuery(id+"F0Hq7nSFAMYVZvY_4.35.F20.boolean.opBoolean","SPLIT",FACE,{"disambiguationData":[TD([subQ44])],"derivedFrom":makeQuery(id+"F0Hq7nSFAMYVZvY_4.34.F20.boolean.opBoolean","SPLIT",FACE,{"disambiguationData":[TD([subQ44])],"derivedFrom":makeQuery(id+"F0Hq7nSFAMYVZvY_4.33.F20.boolean.opBoolean","SPLIT",FACE,{"disambiguationData":[TD([subQ44])],"derivedFrom":makeQuery(id+"F0Hq7nSFAMYVZvY_4.32.F20.boolean.opBoolean","SPLIT",FACE,{"disambiguationData":[TD([subQ44])],"derivedFrom":makeQuery(id+"F0Hq7nSFAMYVZvY_4.31.F20.boolean.opBoolean","SPLIT",FACE,{"disambiguationData":[TD([subQ44])],"derivedFrom":makeQuery(id+"F0Hq7nSFAMYVZvY_4.30.F20.boolean.opBoolean","SPLIT",FACE,{"disambiguationData":[TD([subQ44])],"derivedFrom":makeQuery(id+"F0Hq7nSFAMYVZvY_4.29.F20.boolean.opBoolean","SPLIT",FACE,{"disambiguationData":[TD([subQ44])],"derivedFrom":makeQuery(id+"F0Hq7nSFAMYVZvY_4.28.F20.boolean.opBoolean","SPLIT",FACE,{"disambiguationData":[TD([subQ44])],"derivedFrom":makeQuery(id+"F0Hq7nSFAMYVZvY_4.27.F20.boolean.opBoolean","SPLIT",FACE,{"disambiguationData":[TD([subQ44])],"derivedFrom":makeQuery(id+"F0Hq7nSFAMYVZvY_4.26.F20.boolean.opBoolean","SPLIT",FACE,{"disambiguationData":[TD([subQ44])],"derivedFrom":makeQuery(id+"F0Hq7nSFAMYVZvY_4.25.F20.boolean.opBoolean","SPLIT",FACE,{"disambiguationData":[TD([subQ44])],"derivedFrom":makeQuery(id+"F0Hq7nSFAMYVZvY_4.24.F20.boolean.opBoolean","SPLIT",FACE,{"disambiguationData":[TD([subQ44])],"derivedFrom":makeQuery(id+"F0Hq7nSFAMYVZvY_4.23.F20.boolean.opBoolean","SPLIT",FACE,{"disambiguationData":[TD([subQ44])],"derivedFrom":makeQuery(id+"F0Hq7nSFAMYVZvY_4.22.F20.boolean.opBoolean","SPLIT",FACE,{"disambiguationData":[TD([subQ44])],"derivedFrom":makeQuery(id+"F0Hq7nSFAMYVZvY_4.21.F20.boolean.opBoolean","SPLIT",FACE,{"disambiguationData":[TD([subQ44])],"derivedFrom":makeQuery(id+"F0Hq7nSFAMYVZvY_4.20.F20.boolean.opBoolean","SPLIT",FACE,{"disambiguationData":[TD([subQ44])],"derivedFrom":makeQuery(id+"F0Hq7nSFAMYVZvY_4.19.F20.boolean.opBoolean","SPLIT",FACE,{"disambiguationData":[TD([subQ44])],"derivedFrom":makeQuery(id+"F0Hq7nSFAMYVZvY_4.18.F20.boolean.opBoolean","SPLIT",FACE,{"disambiguationData":[TD([subQ44])],"derivedFrom":makeQuery(id+"F0Hq7nSFAMYVZvY_4.17.F20.boolean.opBoolean","SPLIT",FACE,{"disambiguationData":[TD([subQ44])],"derivedFrom":makeQuery(id+"F0Hq7nSFAMYVZvY_4.16.F20.boolean.opBoolean","SPLIT",FACE,{"disambiguationData":[TD([subQ44])],"derivedFrom":makeQuery(id+"F0Hq7nSFAMYVZvY_4.15.F20.boolean.opBoolean","SPLIT",FACE,{"disambiguationData":[TD([subQ44])],"derivedFrom":makeQuery(id+"F0Hq7nSFAMYVZvY_4.14.F20.boolean.opBoolean","SPLIT",FACE,{"disambiguationData":[TD([subQ44])],"derivedFrom":makeQuery(id+"F0Hq7nSFAMYVZvY_4.13.F20.boolean.opBoolean","SPLIT",FACE,{"disambiguationData":[TD([subQ44])],"derivedFrom":makeQuery(id+"F0Hq7nSFAMYVZvY_4.12.F20.boolean.opBoolean","SPLIT",FACE,{"disambiguationData":[TD([subQ44])],"derivedFrom":makeQuery(id+"F0Hq7nSFAMYVZvY_4.11.F20.boolean.opBoolean","SPLIT",FACE,{"disambiguationData":[TD([subQ44])],"derivedFrom":makeQuery(id+"F0Hq7nSFAMYVZvY_4.10.F20.boolean.opBoolean","SPLIT",FACE,{"disambiguationData":[TD([subQ44])],"derivedFrom":makeQuery(id+"F0Hq7nSFAMYVZvY_4.9.F20.boolean.opBoolean","SPLIT",FACE,{"disambiguationData":[TD([subQ44])],"derivedFrom":makeQuery(id+"F0Hq7nSFAMYVZvY_4.8.F20.boolean.opBoolean","SPLIT",FACE,{"disambiguationData":[TD([subQ44])],"derivedFrom":makeQuery(id+"F0Hq7nSFAMYVZvY_4.7.F20.boolean.opBoolean","SPLIT",FACE,{"disambiguationData":[TD([subQ44])],"derivedFrom":makeQuery(id+"F0Hq7nSFAMYVZvY_4.6.F20.boolean.opBoolean","SPLIT",FACE,{"disambiguationData":[TD([subQ44])],"derivedFrom":makeQuery(id+"F0Hq7nSFAMYVZvY_4.5.F20.boolean.opBoolean","SPLIT",FACE,{"disambiguationData":[TD([subQ44])],"derivedFrom":makeQuery(id+"F0Hq7nSFAMYVZvY_4.4.F20.boolean.opBoolean","SPLIT",FACE,{"disambiguationData":[TD([subQ44])],"derivedFrom":makeQuery(id+"F0Hq7nSFAMYVZvY_4.3.F20.boolean.opBoolean","SPLIT",FACE,{"disambiguationData":[TD([subQ44])],"derivedFrom":makeQuery(id+"F0Hq7nSFAMYVZvY_4.2.F20.boolean.opBoolean","SPLIT",FACE,{"disambiguationData":[TD([subQ44])],"derivedFrom":makeQuery(id+"F0Hq7nSFAMYVZvY_4.1.F20.boolean.opBoolean","SPLIT",FACE,{"disambiguationData":[TD([subQ44])],"derivedFrom":makeQuery(id+"F17.boolean.opBoolean","COPY",FACE,{"derivedFrom":makeQuery(id+"F17.opExtrude","SWEPT_FACE",FACE,{"disambiguationData":[OSD([subQ3])]})})})})})})})})})})})})})})})})})})})})})})})})})})})})})})})})})})})})})})});}
            var Q194;
            {var subQ0=sQuery(id+"F19.wireOp",EDGE,"E158.MirrorCS");var subQ1=sQuery(id+"F19.wireOp",EDGE,"E157");var subQ3=sQuery(id+"F16.wireOp",EDGE,"E151");var subQ25=makeQuery(id+"F0Hq7nSFAMYVZvY_4.36.F20.opExtrude","SWEPT_FACE",FACE,{"disambiguationData":[OSD([subQ0])]});var subQ44=makeQuery(id+"F20.opExtrude","SWEPT_FACE",FACE,{"disambiguationData":[OSD([subQ1])]});Q194=makeQuery(id+"F0Hq7nSFAMYVZvY_4.37.F20.boolean.opBoolean","SPLIT",EDGE,{"disambiguationData":[TD([subQ25])],"derivedFrom":makeQuery(id+"F0Hq7nSFAMYVZvY_4.36.F20.boolean.opBoolean","SPLIT",EDGE,{"disambiguationData":[TD([subQ44])],"derivedFrom":makeQuery(id+"F0Hq7nSFAMYVZvY_4.35.F20.boolean.opBoolean","SPLIT",EDGE,{"disambiguationData":[TD([subQ44])],"derivedFrom":makeQuery(id+"F0Hq7nSFAMYVZvY_4.34.F20.boolean.opBoolean","SPLIT",EDGE,{"disambiguationData":[TD([subQ44])],"derivedFrom":makeQuery(id+"F0Hq7nSFAMYVZvY_4.33.F20.boolean.opBoolean","SPLIT",EDGE,{"disambiguationData":[TD([subQ44])],"derivedFrom":makeQuery(id+"F0Hq7nSFAMYVZvY_4.32.F20.boolean.opBoolean","SPLIT",EDGE,{"disambiguationData":[TD([subQ44])],"derivedFrom":makeQuery(id+"F0Hq7nSFAMYVZvY_4.31.F20.boolean.opBoolean","SPLIT",EDGE,{"disambiguationData":[TD([subQ44])],"derivedFrom":makeQuery(id+"F0Hq7nSFAMYVZvY_4.30.F20.boolean.opBoolean","SPLIT",EDGE,{"disambiguationData":[TD([subQ44])],"derivedFrom":makeQuery(id+"F0Hq7nSFAMYVZvY_4.29.F20.boolean.opBoolean","SPLIT",EDGE,{"disambiguationData":[TD([subQ44])],"derivedFrom":makeQuery(id+"F0Hq7nSFAMYVZvY_4.28.F20.boolean.opBoolean","SPLIT",EDGE,{"disambiguationData":[TD([subQ44])],"derivedFrom":makeQuery(id+"F0Hq7nSFAMYVZvY_4.27.F20.boolean.opBoolean","SPLIT",EDGE,{"disambiguationData":[TD([subQ44])],"derivedFrom":makeQuery(id+"F0Hq7nSFAMYVZvY_4.26.F20.boolean.opBoolean","SPLIT",EDGE,{"disambiguationData":[TD([subQ44])],"derivedFrom":makeQuery(id+"F0Hq7nSFAMYVZvY_4.25.F20.boolean.opBoolean","SPLIT",EDGE,{"disambiguationData":[TD([subQ44])],"derivedFrom":makeQuery(id+"F0Hq7nSFAMYVZvY_4.24.F20.boolean.opBoolean","SPLIT",EDGE,{"disambiguationData":[TD([subQ44])],"derivedFrom":makeQuery(id+"F0Hq7nSFAMYVZvY_4.23.F20.boolean.opBoolean","SPLIT",EDGE,{"disambiguationData":[TD([subQ44])],"derivedFrom":makeQuery(id+"F0Hq7nSFAMYVZvY_4.22.F20.boolean.opBoolean","SPLIT",EDGE,{"disambiguationData":[TD([subQ44])],"derivedFrom":makeQuery(id+"F0Hq7nSFAMYVZvY_4.21.F20.boolean.opBoolean","SPLIT",EDGE,{"disambiguationData":[TD([subQ44])],"derivedFrom":makeQuery(id+"F0Hq7nSFAMYVZvY_4.20.F20.boolean.opBoolean","SPLIT",EDGE,{"disambiguationData":[TD([subQ44])],"derivedFrom":makeQuery(id+"F0Hq7nSFAMYVZvY_4.19.F20.boolean.opBoolean","SPLIT",EDGE,{"disambiguationData":[TD([subQ44])],"derivedFrom":makeQuery(id+"F0Hq7nSFAMYVZvY_4.18.F20.boolean.opBoolean","SPLIT",EDGE,{"disambiguationData":[TD([subQ44])],"derivedFrom":makeQuery(id+"F0Hq7nSFAMYVZvY_4.17.F20.boolean.opBoolean","SPLIT",EDGE,{"disambiguationData":[TD([subQ44])],"derivedFrom":makeQuery(id+"F0Hq7nSFAMYVZvY_4.16.F20.boolean.opBoolean","SPLIT",EDGE,{"disambiguationData":[TD([subQ44])],"derivedFrom":makeQuery(id+"F0Hq7nSFAMYVZvY_4.15.F20.boolean.opBoolean","SPLIT",EDGE,{"disambiguationData":[TD([subQ44])],"derivedFrom":makeQuery(id+"F0Hq7nSFAMYVZvY_4.14.F20.boolean.opBoolean","SPLIT",EDGE,{"disambiguationData":[TD([subQ44])],"derivedFrom":makeQuery(id+"F0Hq7nSFAMYVZvY_4.13.F20.boolean.opBoolean","SPLIT",EDGE,{"disambiguationData":[TD([subQ44])],"derivedFrom":makeQuery(id+"F0Hq7nSFAMYVZvY_4.12.F20.boolean.opBoolean","SPLIT",EDGE,{"disambiguationData":[TD([subQ44])],"derivedFrom":makeQuery(id+"F0Hq7nSFAMYVZvY_4.11.F20.boolean.opBoolean","SPLIT",EDGE,{"disambiguationData":[TD([subQ44])],"derivedFrom":makeQuery(id+"F0Hq7nSFAMYVZvY_4.10.F20.boolean.opBoolean","SPLIT",EDGE,{"disambiguationData":[TD([subQ44])],"derivedFrom":makeQuery(id+"F0Hq7nSFAMYVZvY_4.9.F20.boolean.opBoolean","SPLIT",EDGE,{"disambiguationData":[TD([subQ44])],"derivedFrom":makeQuery(id+"F0Hq7nSFAMYVZvY_4.8.F20.boolean.opBoolean","SPLIT",EDGE,{"disambiguationData":[TD([subQ44])],"derivedFrom":makeQuery(id+"F0Hq7nSFAMYVZvY_4.7.F20.boolean.opBoolean","SPLIT",EDGE,{"disambiguationData":[TD([subQ44])],"derivedFrom":makeQuery(id+"F0Hq7nSFAMYVZvY_4.6.F20.boolean.opBoolean","SPLIT",EDGE,{"disambiguationData":[TD([subQ44])],"derivedFrom":makeQuery(id+"F0Hq7nSFAMYVZvY_4.5.F20.boolean.opBoolean","SPLIT",EDGE,{"disambiguationData":[TD([subQ44])],"derivedFrom":makeQuery(id+"F0Hq7nSFAMYVZvY_4.4.F20.boolean.opBoolean","SPLIT",EDGE,{"disambiguationData":[TD([subQ44])],"derivedFrom":makeQuery(id+"F0Hq7nSFAMYVZvY_4.3.F20.boolean.opBoolean","SPLIT",EDGE,{"disambiguationData":[TD([subQ44])],"derivedFrom":makeQuery(id+"F0Hq7nSFAMYVZvY_4.2.F20.boolean.opBoolean","SPLIT",EDGE,{"disambiguationData":[TD([subQ44])],"derivedFrom":makeQuery(id+"F0Hq7nSFAMYVZvY_4.1.F20.boolean.opBoolean","SPLIT",EDGE,{"disambiguationData":[TD([subQ44])],"derivedFrom":makeQuery(id+"F18.boolean.opBoolean","COPY",EDGE,{"derivedFrom":makeQuery(id+"F18.opExtrude","CAP_EDGE",EDGE,{"disambiguationData":[OSD([subQ3])],"isStart":false})})})})})})})})})})})})})})})})})})})})})})})})})})})})})})})})})})})})})})});}
            var Q195;
            Q195=makeQuery(id+"F0Hq7nSFAMYVZvY_4.6.F20.opExtrude","SWEPT_FACE",FACE,{"disambiguationData":[OSD([sQuery(id+"F19.wireOp",EDGE,"E157")])]});
            var Q196;
            Q196=makeQuery(id+"F0Hq7nSFAMYVZvY_4.6.F20.opExtrude","SWEPT_FACE",FACE,{"disambiguationData":[OSD([sQuery(id+"F19.wireOp",EDGE,"E158.MirrorCS")])]});
            var Q197;
            Q197=makeQuery(id+"F0Hq7nSFAMYVZvY_4.6.F20.opExtrude","CAP_EDGE",EDGE,{"disambiguationData":[OSD([sQuery(id+"F19.wireOp",EDGE,"E157")])],"isStart":false});
            var Q198;
            Q198=makeQuery(id+"F0Hq7nSFAMYVZvY_4.6.F20.opExtrude","CAP_EDGE",EDGE,{"disambiguationData":[OSD([sQuery(id+"F19.wireOp",EDGE,"E158.MirrorCS")])],"isStart":false});
            var Q199;
            Q199=makeQuery(id+"F0Hq7nSFAMYVZvY_4.38.F20.opExtrude","SWEPT_FACE",FACE,{"disambiguationData":[OSD([sQuery(id+"F19.wireOp",EDGE,"E157")])]});
            var Q200;
            Q200=makeQuery(id+"F0Hq7nSFAMYVZvY_4.38.F20.opExtrude","CAP_EDGE",EDGE,{"disambiguationData":[OSD([sQuery(id+"F19.wireOp",EDGE,"E157")])],"isStart":false});
            var Q201;
            Q201=makeQuery(id+"F0Hq7nSFAMYVZvY_4.38.F20.opExtrude","CAP_EDGE",EDGE,{"disambiguationData":[OSD([sQuery(id+"F19.wireOp",EDGE,"E158.MirrorCS")])],"isStart":false});
            var Q202;
            {var subQ0=sQuery(id+"F16.wireOp",EDGE,"E151");var subQ2=sQuery(id+"F16.wireOp",EDGE,"E152");var subQ4=sQuery(id+"F19.wireOp",EDGE,"E157");var subQ5=sQuery(id+"F19.wireOp",EDGE,"E158.MirrorCS");var subQ6=makeQuery(id+"F0Hq7nSFAMYVZvY_4.5.F20.opExtrude","SWEPT_FACE",FACE,{"disambiguationData":[OSD([subQ5])]});var subQ7=makeQuery(id+"F20.opExtrude","SWEPT_FACE",FACE,{"disambiguationData":[OSD([subQ4])]});Q202=makeQuery(id+"F0Hq7nSFAMYVZvY_4.6.F20.boolean.opBoolean","SPLIT",FACE,{"disambiguationData":[TD([subQ6])],"derivedFrom":makeQuery(id+"F0Hq7nSFAMYVZvY_4.5.F20.boolean.opBoolean","SPLIT",FACE,{"disambiguationData":[TD([subQ7])],"derivedFrom":makeQuery(id+"F0Hq7nSFAMYVZvY_4.4.F20.boolean.opBoolean","SPLIT",FACE,{"disambiguationData":[TD([subQ7])],"derivedFrom":makeQuery(id+"F0Hq7nSFAMYVZvY_4.3.F20.boolean.opBoolean","SPLIT",FACE,{"disambiguationData":[TD([subQ7])],"derivedFrom":makeQuery(id+"F0Hq7nSFAMYVZvY_4.2.F20.boolean.opBoolean","SPLIT",FACE,{"disambiguationData":[TD([subQ7])],"derivedFrom":makeQuery(id+"F0Hq7nSFAMYVZvY_4.1.F20.boolean.opBoolean","SPLIT",FACE,{"disambiguationData":[TD([subQ7])],"derivedFrom":makeQuery(id+"F17.boolean.opBoolean","COPY",FACE,{"derivedFrom":makeQuery(id+"F17.opExtrude","CAP_FACE",FACE,{"disambiguationData":[OSD([subQ0,subQ2])],"isStart":false})})})})})})})});}
            var Q203;
            Q203=makeQuery(id+"F0Hq7nSFAMYVZvY_4.6.F20.opExtrude","CAP_EDGE",EDGE,{"disambiguationData":[OSD([sQuery(id+"F19.wireOp",EDGE,"E158.MirrorCS")])],"isStart":true});
            var Q204;
            {var subQ0=sQuery(id+"F19.wireOp",EDGE,"E158.MirrorCS");var subQ1=sQuery(id+"F19.wireOp",EDGE,"E157");var subQ3=sQuery(id+"F16.wireOp",EDGE,"E151");var subQ10=makeQuery(id+"F0Hq7nSFAMYVZvY_4.5.F20.opExtrude","SWEPT_FACE",FACE,{"disambiguationData":[OSD([subQ0])]});var subQ13=makeQuery(id+"F20.opExtrude","SWEPT_FACE",FACE,{"disambiguationData":[OSD([subQ1])]});Q204=makeQuery(id+"F0Hq7nSFAMYVZvY_4.6.F20.boolean.opBoolean","SPLIT",FACE,{"disambiguationData":[TD([subQ10])],"derivedFrom":makeQuery(id+"F0Hq7nSFAMYVZvY_4.5.F20.boolean.opBoolean","SPLIT",FACE,{"disambiguationData":[TD([subQ13])],"derivedFrom":makeQuery(id+"F0Hq7nSFAMYVZvY_4.4.F20.boolean.opBoolean","SPLIT",FACE,{"disambiguationData":[TD([subQ13])],"derivedFrom":makeQuery(id+"F0Hq7nSFAMYVZvY_4.3.F20.boolean.opBoolean","SPLIT",FACE,{"disambiguationData":[TD([subQ13])],"derivedFrom":makeQuery(id+"F0Hq7nSFAMYVZvY_4.2.F20.boolean.opBoolean","SPLIT",FACE,{"disambiguationData":[TD([subQ13])],"derivedFrom":makeQuery(id+"F0Hq7nSFAMYVZvY_4.1.F20.boolean.opBoolean","SPLIT",FACE,{"disambiguationData":[TD([subQ13])],"derivedFrom":makeQuery(id+"F17.boolean.opBoolean","COPY",FACE,{"derivedFrom":makeQuery(id+"F17.opExtrude","SWEPT_FACE",FACE,{"disambiguationData":[OSD([subQ3])]})})})})})})})});}
            var Q205;
            {var subQ0=sQuery(id+"F19.wireOp",EDGE,"E158.MirrorCS");var subQ1=sQuery(id+"F19.wireOp",EDGE,"E157");var subQ3=sQuery(id+"F16.wireOp",EDGE,"E151");var subQ9=makeQuery(id+"F0Hq7nSFAMYVZvY_4.5.F20.opExtrude","SWEPT_FACE",FACE,{"disambiguationData":[OSD([subQ0])]});var subQ13=makeQuery(id+"F20.opExtrude","SWEPT_FACE",FACE,{"disambiguationData":[OSD([subQ1])]});Q205=makeQuery(id+"F0Hq7nSFAMYVZvY_4.6.F20.boolean.opBoolean","SPLIT",EDGE,{"disambiguationData":[TD([subQ9])],"derivedFrom":makeQuery(id+"F0Hq7nSFAMYVZvY_4.5.F20.boolean.opBoolean","SPLIT",EDGE,{"disambiguationData":[TD([subQ13])],"derivedFrom":makeQuery(id+"F0Hq7nSFAMYVZvY_4.4.F20.boolean.opBoolean","SPLIT",EDGE,{"disambiguationData":[TD([subQ13])],"derivedFrom":makeQuery(id+"F0Hq7nSFAMYVZvY_4.3.F20.boolean.opBoolean","SPLIT",EDGE,{"disambiguationData":[TD([subQ13])],"derivedFrom":makeQuery(id+"F0Hq7nSFAMYVZvY_4.2.F20.boolean.opBoolean","SPLIT",EDGE,{"disambiguationData":[TD([subQ13])],"derivedFrom":makeQuery(id+"F0Hq7nSFAMYVZvY_4.1.F20.boolean.opBoolean","SPLIT",EDGE,{"disambiguationData":[TD([subQ13])],"derivedFrom":makeQuery(id+"F18.boolean.opBoolean","COPY",EDGE,{"derivedFrom":makeQuery(id+"F18.opExtrude","CAP_EDGE",EDGE,{"disambiguationData":[OSD([subQ3])],"isStart":false})})})})})})})});}
            var Q206;
            {var subQ0=sQuery(id+"F16.wireOp",EDGE,"E151");var subQ2=sQuery(id+"F16.wireOp",EDGE,"E152");var subQ4=sQuery(id+"F19.wireOp",EDGE,"E158.MirrorCS");var subQ5=makeQuery(id+"F0Hq7nSFAMYVZvY_4.37.F20.opExtrude","SWEPT_FACE",FACE,{"disambiguationData":[OSD([subQ4])]});var subQ6=sQuery(id+"F19.wireOp",EDGE,"E157");var subQ7=makeQuery(id+"F20.opExtrude","SWEPT_FACE",FACE,{"disambiguationData":[OSD([subQ6])]});Q206=makeQuery(id+"F0Hq7nSFAMYVZvY_4.38.F20.boolean.opBoolean","SPLIT",FACE,{"disambiguationData":[TD([subQ5])],"derivedFrom":makeQuery(id+"F0Hq7nSFAMYVZvY_4.37.F20.boolean.opBoolean","SPLIT",FACE,{"disambiguationData":[TD([subQ7])],"derivedFrom":makeQuery(id+"F0Hq7nSFAMYVZvY_4.36.F20.boolean.opBoolean","SPLIT",FACE,{"disambiguationData":[TD([subQ7])],"derivedFrom":makeQuery(id+"F0Hq7nSFAMYVZvY_4.35.F20.boolean.opBoolean","SPLIT",FACE,{"disambiguationData":[TD([subQ7])],"derivedFrom":makeQuery(id+"F0Hq7nSFAMYVZvY_4.34.F20.boolean.opBoolean","SPLIT",FACE,{"disambiguationData":[TD([subQ7])],"derivedFrom":makeQuery(id+"F0Hq7nSFAMYVZvY_4.33.F20.boolean.opBoolean","SPLIT",FACE,{"disambiguationData":[TD([subQ7])],"derivedFrom":makeQuery(id+"F0Hq7nSFAMYVZvY_4.32.F20.boolean.opBoolean","SPLIT",FACE,{"disambiguationData":[TD([subQ7])],"derivedFrom":makeQuery(id+"F0Hq7nSFAMYVZvY_4.31.F20.boolean.opBoolean","SPLIT",FACE,{"disambiguationData":[TD([subQ7])],"derivedFrom":makeQuery(id+"F0Hq7nSFAMYVZvY_4.30.F20.boolean.opBoolean","SPLIT",FACE,{"disambiguationData":[TD([subQ7])],"derivedFrom":makeQuery(id+"F0Hq7nSFAMYVZvY_4.29.F20.boolean.opBoolean","SPLIT",FACE,{"disambiguationData":[TD([subQ7])],"derivedFrom":makeQuery(id+"F0Hq7nSFAMYVZvY_4.28.F20.boolean.opBoolean","SPLIT",FACE,{"disambiguationData":[TD([subQ7])],"derivedFrom":makeQuery(id+"F0Hq7nSFAMYVZvY_4.27.F20.boolean.opBoolean","SPLIT",FACE,{"disambiguationData":[TD([subQ7])],"derivedFrom":makeQuery(id+"F0Hq7nSFAMYVZvY_4.26.F20.boolean.opBoolean","SPLIT",FACE,{"disambiguationData":[TD([subQ7])],"derivedFrom":makeQuery(id+"F0Hq7nSFAMYVZvY_4.25.F20.boolean.opBoolean","SPLIT",FACE,{"disambiguationData":[TD([subQ7])],"derivedFrom":makeQuery(id+"F0Hq7nSFAMYVZvY_4.24.F20.boolean.opBoolean","SPLIT",FACE,{"disambiguationData":[TD([subQ7])],"derivedFrom":makeQuery(id+"F0Hq7nSFAMYVZvY_4.23.F20.boolean.opBoolean","SPLIT",FACE,{"disambiguationData":[TD([subQ7])],"derivedFrom":makeQuery(id+"F0Hq7nSFAMYVZvY_4.22.F20.boolean.opBoolean","SPLIT",FACE,{"disambiguationData":[TD([subQ7])],"derivedFrom":makeQuery(id+"F0Hq7nSFAMYVZvY_4.21.F20.boolean.opBoolean","SPLIT",FACE,{"disambiguationData":[TD([subQ7])],"derivedFrom":makeQuery(id+"F0Hq7nSFAMYVZvY_4.20.F20.boolean.opBoolean","SPLIT",FACE,{"disambiguationData":[TD([subQ7])],"derivedFrom":makeQuery(id+"F0Hq7nSFAMYVZvY_4.19.F20.boolean.opBoolean","SPLIT",FACE,{"disambiguationData":[TD([subQ7])],"derivedFrom":makeQuery(id+"F0Hq7nSFAMYVZvY_4.18.F20.boolean.opBoolean","SPLIT",FACE,{"disambiguationData":[TD([subQ7])],"derivedFrom":makeQuery(id+"F0Hq7nSFAMYVZvY_4.17.F20.boolean.opBoolean","SPLIT",FACE,{"disambiguationData":[TD([subQ7])],"derivedFrom":makeQuery(id+"F0Hq7nSFAMYVZvY_4.16.F20.boolean.opBoolean","SPLIT",FACE,{"disambiguationData":[TD([subQ7])],"derivedFrom":makeQuery(id+"F0Hq7nSFAMYVZvY_4.15.F20.boolean.opBoolean","SPLIT",FACE,{"disambiguationData":[TD([subQ7])],"derivedFrom":makeQuery(id+"F0Hq7nSFAMYVZvY_4.14.F20.boolean.opBoolean","SPLIT",FACE,{"disambiguationData":[TD([subQ7])],"derivedFrom":makeQuery(id+"F0Hq7nSFAMYVZvY_4.13.F20.boolean.opBoolean","SPLIT",FACE,{"disambiguationData":[TD([subQ7])],"derivedFrom":makeQuery(id+"F0Hq7nSFAMYVZvY_4.12.F20.boolean.opBoolean","SPLIT",FACE,{"disambiguationData":[TD([subQ7])],"derivedFrom":makeQuery(id+"F0Hq7nSFAMYVZvY_4.11.F20.boolean.opBoolean","SPLIT",FACE,{"disambiguationData":[TD([subQ7])],"derivedFrom":makeQuery(id+"F0Hq7nSFAMYVZvY_4.10.F20.boolean.opBoolean","SPLIT",FACE,{"disambiguationData":[TD([subQ7])],"derivedFrom":makeQuery(id+"F0Hq7nSFAMYVZvY_4.9.F20.boolean.opBoolean","SPLIT",FACE,{"disambiguationData":[TD([subQ7])],"derivedFrom":makeQuery(id+"F0Hq7nSFAMYVZvY_4.8.F20.boolean.opBoolean","SPLIT",FACE,{"disambiguationData":[TD([subQ7])],"derivedFrom":makeQuery(id+"F0Hq7nSFAMYVZvY_4.7.F20.boolean.opBoolean","SPLIT",FACE,{"disambiguationData":[TD([subQ7])],"derivedFrom":makeQuery(id+"F0Hq7nSFAMYVZvY_4.6.F20.boolean.opBoolean","SPLIT",FACE,{"disambiguationData":[TD([subQ7])],"derivedFrom":makeQuery(id+"F0Hq7nSFAMYVZvY_4.5.F20.boolean.opBoolean","SPLIT",FACE,{"disambiguationData":[TD([subQ7])],"derivedFrom":makeQuery(id+"F0Hq7nSFAMYVZvY_4.4.F20.boolean.opBoolean","SPLIT",FACE,{"disambiguationData":[TD([subQ7])],"derivedFrom":makeQuery(id+"F0Hq7nSFAMYVZvY_4.3.F20.boolean.opBoolean","SPLIT",FACE,{"disambiguationData":[TD([subQ7])],"derivedFrom":makeQuery(id+"F0Hq7nSFAMYVZvY_4.2.F20.boolean.opBoolean","SPLIT",FACE,{"disambiguationData":[TD([subQ7])],"derivedFrom":makeQuery(id+"F0Hq7nSFAMYVZvY_4.1.F20.boolean.opBoolean","SPLIT",FACE,{"disambiguationData":[TD([subQ7])],"derivedFrom":makeQuery(id+"F17.boolean.opBoolean","COPY",FACE,{"derivedFrom":makeQuery(id+"F17.opExtrude","CAP_FACE",FACE,{"disambiguationData":[OSD([subQ0,subQ2])],"isStart":false})})})})})})})})})})})})})})})})})})})})})})})})})})})})})})})})})})})})})})})});}
            var Q207;
            Q207=makeQuery(id+"F0Hq7nSFAMYVZvY_4.38.F20.opExtrude","CAP_EDGE",EDGE,{"disambiguationData":[OSD([sQuery(id+"F19.wireOp",EDGE,"E157")])],"isStart":true});
            var Q208;
            {var subQ0=sQuery(id+"F19.wireOp",EDGE,"E158.MirrorCS");var subQ1=sQuery(id+"F19.wireOp",EDGE,"E157");var subQ3=sQuery(id+"F16.wireOp",EDGE,"E151");var subQ27=makeQuery(id+"F0Hq7nSFAMYVZvY_4.37.F20.opExtrude","SWEPT_FACE",FACE,{"disambiguationData":[OSD([subQ0])]});var subQ45=makeQuery(id+"F20.opExtrude","SWEPT_FACE",FACE,{"disambiguationData":[OSD([subQ1])]});Q208=makeQuery(id+"F0Hq7nSFAMYVZvY_4.38.F20.boolean.opBoolean","SPLIT",EDGE,{"disambiguationData":[TD([subQ27])],"derivedFrom":makeQuery(id+"F0Hq7nSFAMYVZvY_4.37.F20.boolean.opBoolean","SPLIT",EDGE,{"disambiguationData":[TD([subQ45])],"derivedFrom":makeQuery(id+"F0Hq7nSFAMYVZvY_4.36.F20.boolean.opBoolean","SPLIT",EDGE,{"disambiguationData":[TD([subQ45])],"derivedFrom":makeQuery(id+"F0Hq7nSFAMYVZvY_4.35.F20.boolean.opBoolean","SPLIT",EDGE,{"disambiguationData":[TD([subQ45])],"derivedFrom":makeQuery(id+"F0Hq7nSFAMYVZvY_4.34.F20.boolean.opBoolean","SPLIT",EDGE,{"disambiguationData":[TD([subQ45])],"derivedFrom":makeQuery(id+"F0Hq7nSFAMYVZvY_4.33.F20.boolean.opBoolean","SPLIT",EDGE,{"disambiguationData":[TD([subQ45])],"derivedFrom":makeQuery(id+"F0Hq7nSFAMYVZvY_4.32.F20.boolean.opBoolean","SPLIT",EDGE,{"disambiguationData":[TD([subQ45])],"derivedFrom":makeQuery(id+"F0Hq7nSFAMYVZvY_4.31.F20.boolean.opBoolean","SPLIT",EDGE,{"disambiguationData":[TD([subQ45])],"derivedFrom":makeQuery(id+"F0Hq7nSFAMYVZvY_4.30.F20.boolean.opBoolean","SPLIT",EDGE,{"disambiguationData":[TD([subQ45])],"derivedFrom":makeQuery(id+"F0Hq7nSFAMYVZvY_4.29.F20.boolean.opBoolean","SPLIT",EDGE,{"disambiguationData":[TD([subQ45])],"derivedFrom":makeQuery(id+"F0Hq7nSFAMYVZvY_4.28.F20.boolean.opBoolean","SPLIT",EDGE,{"disambiguationData":[TD([subQ45])],"derivedFrom":makeQuery(id+"F0Hq7nSFAMYVZvY_4.27.F20.boolean.opBoolean","SPLIT",EDGE,{"disambiguationData":[TD([subQ45])],"derivedFrom":makeQuery(id+"F0Hq7nSFAMYVZvY_4.26.F20.boolean.opBoolean","SPLIT",EDGE,{"disambiguationData":[TD([subQ45])],"derivedFrom":makeQuery(id+"F0Hq7nSFAMYVZvY_4.25.F20.boolean.opBoolean","SPLIT",EDGE,{"disambiguationData":[TD([subQ45])],"derivedFrom":makeQuery(id+"F0Hq7nSFAMYVZvY_4.24.F20.boolean.opBoolean","SPLIT",EDGE,{"disambiguationData":[TD([subQ45])],"derivedFrom":makeQuery(id+"F0Hq7nSFAMYVZvY_4.23.F20.boolean.opBoolean","SPLIT",EDGE,{"disambiguationData":[TD([subQ45])],"derivedFrom":makeQuery(id+"F0Hq7nSFAMYVZvY_4.22.F20.boolean.opBoolean","SPLIT",EDGE,{"disambiguationData":[TD([subQ45])],"derivedFrom":makeQuery(id+"F0Hq7nSFAMYVZvY_4.21.F20.boolean.opBoolean","SPLIT",EDGE,{"disambiguationData":[TD([subQ45])],"derivedFrom":makeQuery(id+"F0Hq7nSFAMYVZvY_4.20.F20.boolean.opBoolean","SPLIT",EDGE,{"disambiguationData":[TD([subQ45])],"derivedFrom":makeQuery(id+"F0Hq7nSFAMYVZvY_4.19.F20.boolean.opBoolean","SPLIT",EDGE,{"disambiguationData":[TD([subQ45])],"derivedFrom":makeQuery(id+"F0Hq7nSFAMYVZvY_4.18.F20.boolean.opBoolean","SPLIT",EDGE,{"disambiguationData":[TD([subQ45])],"derivedFrom":makeQuery(id+"F0Hq7nSFAMYVZvY_4.17.F20.boolean.opBoolean","SPLIT",EDGE,{"disambiguationData":[TD([subQ45])],"derivedFrom":makeQuery(id+"F0Hq7nSFAMYVZvY_4.16.F20.boolean.opBoolean","SPLIT",EDGE,{"disambiguationData":[TD([subQ45])],"derivedFrom":makeQuery(id+"F0Hq7nSFAMYVZvY_4.15.F20.boolean.opBoolean","SPLIT",EDGE,{"disambiguationData":[TD([subQ45])],"derivedFrom":makeQuery(id+"F0Hq7nSFAMYVZvY_4.14.F20.boolean.opBoolean","SPLIT",EDGE,{"disambiguationData":[TD([subQ45])],"derivedFrom":makeQuery(id+"F0Hq7nSFAMYVZvY_4.13.F20.boolean.opBoolean","SPLIT",EDGE,{"disambiguationData":[TD([subQ45])],"derivedFrom":makeQuery(id+"F0Hq7nSFAMYVZvY_4.12.F20.boolean.opBoolean","SPLIT",EDGE,{"disambiguationData":[TD([subQ45])],"derivedFrom":makeQuery(id+"F0Hq7nSFAMYVZvY_4.11.F20.boolean.opBoolean","SPLIT",EDGE,{"disambiguationData":[TD([subQ45])],"derivedFrom":makeQuery(id+"F0Hq7nSFAMYVZvY_4.10.F20.boolean.opBoolean","SPLIT",EDGE,{"disambiguationData":[TD([subQ45])],"derivedFrom":makeQuery(id+"F0Hq7nSFAMYVZvY_4.9.F20.boolean.opBoolean","SPLIT",EDGE,{"disambiguationData":[TD([subQ45])],"derivedFrom":makeQuery(id+"F0Hq7nSFAMYVZvY_4.8.F20.boolean.opBoolean","SPLIT",EDGE,{"disambiguationData":[TD([subQ45])],"derivedFrom":makeQuery(id+"F0Hq7nSFAMYVZvY_4.7.F20.boolean.opBoolean","SPLIT",EDGE,{"disambiguationData":[TD([subQ45])],"derivedFrom":makeQuery(id+"F0Hq7nSFAMYVZvY_4.6.F20.boolean.opBoolean","SPLIT",EDGE,{"disambiguationData":[TD([subQ45])],"derivedFrom":makeQuery(id+"F0Hq7nSFAMYVZvY_4.5.F20.boolean.opBoolean","SPLIT",EDGE,{"disambiguationData":[TD([subQ45])],"derivedFrom":makeQuery(id+"F0Hq7nSFAMYVZvY_4.4.F20.boolean.opBoolean","SPLIT",EDGE,{"disambiguationData":[TD([subQ45])],"derivedFrom":makeQuery(id+"F0Hq7nSFAMYVZvY_4.3.F20.boolean.opBoolean","SPLIT",EDGE,{"disambiguationData":[TD([subQ45])],"derivedFrom":makeQuery(id+"F0Hq7nSFAMYVZvY_4.2.F20.boolean.opBoolean","SPLIT",EDGE,{"disambiguationData":[TD([subQ45])],"derivedFrom":makeQuery(id+"F0Hq7nSFAMYVZvY_4.1.F20.boolean.opBoolean","SPLIT",EDGE,{"disambiguationData":[TD([subQ45])],"derivedFrom":makeQuery(id+"F18.boolean.opBoolean","COPY",EDGE,{"derivedFrom":makeQuery(id+"F18.opExtrude","CAP_EDGE",EDGE,{"disambiguationData":[OSD([subQ3])],"isStart":false})})})})})})})})})})})})})})})})})})})})})})})})})})})})})})})})})})})})})})})});}
            var Q209;
            Q209=makeQuery(id+"F0Hq7nSFAMYVZvY_4.7.F20.opExtrude","SWEPT_FACE",FACE,{"disambiguationData":[OSD([sQuery(id+"F19.wireOp",EDGE,"E157")])]});
            var Q210;
            Q210=makeQuery(id+"F0Hq7nSFAMYVZvY_4.7.F20.opExtrude","SWEPT_FACE",FACE,{"disambiguationData":[OSD([sQuery(id+"F19.wireOp",EDGE,"E158.MirrorCS")])]});
            var Q211;
            Q211=makeQuery(id+"F0Hq7nSFAMYVZvY_4.7.F20.opExtrude","CAP_EDGE",EDGE,{"disambiguationData":[OSD([sQuery(id+"F19.wireOp",EDGE,"E157")])],"isStart":false});
            var Q212;
            Q212=makeQuery(id+"F0Hq7nSFAMYVZvY_4.7.F20.opExtrude","CAP_EDGE",EDGE,{"disambiguationData":[OSD([sQuery(id+"F19.wireOp",EDGE,"E158.MirrorCS")])],"isStart":false});
            var Q213;
            Q213=makeQuery(id+"F0Hq7nSFAMYVZvY_4.39.F20.opExtrude","SWEPT_FACE",FACE,{"disambiguationData":[OSD([sQuery(id+"F19.wireOp",EDGE,"E157")])]});
            var Q214;
            Q214=makeQuery(id+"F0Hq7nSFAMYVZvY_4.39.F20.opExtrude","CAP_EDGE",EDGE,{"disambiguationData":[OSD([sQuery(id+"F19.wireOp",EDGE,"E157")])],"isStart":false});
            var Q215;
            {var subQ0=sQuery(id+"F16.wireOp",EDGE,"E151");var subQ2=sQuery(id+"F19.wireOp",EDGE,"E158.MirrorCS");var subQ3=makeQuery(id+"F0Hq7nSFAMYVZvY_4.6.F20.opExtrude","SWEPT_FACE",FACE,{"disambiguationData":[OSD([subQ2])]});var subQ4=sQuery(id+"F16.wireOp",EDGE,"E152");var subQ6=sQuery(id+"F19.wireOp",EDGE,"E157");var subQ7=makeQuery(id+"F20.opExtrude","SWEPT_FACE",FACE,{"disambiguationData":[OSD([subQ6])]});Q215=makeQuery(id+"F0Hq7nSFAMYVZvY_4.7.F20.boolean.opBoolean","SPLIT",FACE,{"disambiguationData":[TD([subQ3])],"derivedFrom":makeQuery(id+"F0Hq7nSFAMYVZvY_4.6.F20.boolean.opBoolean","SPLIT",FACE,{"disambiguationData":[TD([subQ7])],"derivedFrom":makeQuery(id+"F0Hq7nSFAMYVZvY_4.5.F20.boolean.opBoolean","SPLIT",FACE,{"disambiguationData":[TD([subQ7])],"derivedFrom":makeQuery(id+"F0Hq7nSFAMYVZvY_4.4.F20.boolean.opBoolean","SPLIT",FACE,{"disambiguationData":[TD([subQ7])],"derivedFrom":makeQuery(id+"F0Hq7nSFAMYVZvY_4.3.F20.boolean.opBoolean","SPLIT",FACE,{"disambiguationData":[TD([subQ7])],"derivedFrom":makeQuery(id+"F0Hq7nSFAMYVZvY_4.2.F20.boolean.opBoolean","SPLIT",FACE,{"disambiguationData":[TD([subQ7])],"derivedFrom":makeQuery(id+"F0Hq7nSFAMYVZvY_4.1.F20.boolean.opBoolean","SPLIT",FACE,{"disambiguationData":[TD([subQ7])],"derivedFrom":makeQuery(id+"F17.boolean.opBoolean","COPY",FACE,{"derivedFrom":makeQuery(id+"F17.opExtrude","CAP_FACE",FACE,{"disambiguationData":[OSD([subQ0,subQ4])],"isStart":false})})})})})})})})});}
            var Q216;
            Q216=makeQuery(id+"F0Hq7nSFAMYVZvY_4.7.F20.opExtrude","CAP_EDGE",EDGE,{"disambiguationData":[OSD([sQuery(id+"F19.wireOp",EDGE,"E158.MirrorCS")])],"isStart":true});
            var Q217;
            {var subQ0=sQuery(id+"F19.wireOp",EDGE,"E158.MirrorCS");var subQ1=sQuery(id+"F19.wireOp",EDGE,"E157");var subQ3=sQuery(id+"F16.wireOp",EDGE,"E151");var subQ8=makeQuery(id+"F0Hq7nSFAMYVZvY_4.6.F20.opExtrude","SWEPT_FACE",FACE,{"disambiguationData":[OSD([subQ0])]});var subQ14=makeQuery(id+"F20.opExtrude","SWEPT_FACE",FACE,{"disambiguationData":[OSD([subQ1])]});Q217=makeQuery(id+"F0Hq7nSFAMYVZvY_4.7.F20.boolean.opBoolean","SPLIT",FACE,{"disambiguationData":[TD([subQ8])],"derivedFrom":makeQuery(id+"F0Hq7nSFAMYVZvY_4.6.F20.boolean.opBoolean","SPLIT",FACE,{"disambiguationData":[TD([subQ14])],"derivedFrom":makeQuery(id+"F0Hq7nSFAMYVZvY_4.5.F20.boolean.opBoolean","SPLIT",FACE,{"disambiguationData":[TD([subQ14])],"derivedFrom":makeQuery(id+"F0Hq7nSFAMYVZvY_4.4.F20.boolean.opBoolean","SPLIT",FACE,{"disambiguationData":[TD([subQ14])],"derivedFrom":makeQuery(id+"F0Hq7nSFAMYVZvY_4.3.F20.boolean.opBoolean","SPLIT",FACE,{"disambiguationData":[TD([subQ14])],"derivedFrom":makeQuery(id+"F0Hq7nSFAMYVZvY_4.2.F20.boolean.opBoolean","SPLIT",FACE,{"disambiguationData":[TD([subQ14])],"derivedFrom":makeQuery(id+"F0Hq7nSFAMYVZvY_4.1.F20.boolean.opBoolean","SPLIT",FACE,{"disambiguationData":[TD([subQ14])],"derivedFrom":makeQuery(id+"F17.boolean.opBoolean","COPY",FACE,{"derivedFrom":makeQuery(id+"F17.opExtrude","SWEPT_FACE",FACE,{"disambiguationData":[OSD([subQ3])]})})})})})})})})});}
            var Q218;
            {var subQ0=sQuery(id+"F19.wireOp",EDGE,"E158.MirrorCS");var subQ1=sQuery(id+"F19.wireOp",EDGE,"E157");var subQ2=sQuery(id+"F16.wireOp",EDGE,"E152");var subQ3=sQuery(id+"F16.wireOp",EDGE,"E151");Q218=makeQuery(id+"F0Hq7nSFAMYVZvY_4.39.F20.boolean.opBoolean","MERGE",FACE,{"derivedFrom":[makeQuery(id+"F0Hq7nSFAMYVZvY_4.38.F20.boolean.opBoolean","MERGE",FACE,{"derivedFrom":[makeQuery(id+"F0Hq7nSFAMYVZvY_4.37.F20.boolean.opBoolean","MERGE",FACE,{"derivedFrom":[makeQuery(id+"F0Hq7nSFAMYVZvY_4.36.F20.boolean.opBoolean","MERGE",FACE,{"derivedFrom":[makeQuery(id+"F0Hq7nSFAMYVZvY_4.35.F20.boolean.opBoolean","MERGE",FACE,{"derivedFrom":[makeQuery(id+"F0Hq7nSFAMYVZvY_4.34.F20.boolean.opBoolean","MERGE",FACE,{"derivedFrom":[makeQuery(id+"F0Hq7nSFAMYVZvY_4.33.F20.boolean.opBoolean","MERGE",FACE,{"derivedFrom":[makeQuery(id+"F0Hq7nSFAMYVZvY_4.32.F20.boolean.opBoolean","MERGE",FACE,{"derivedFrom":[makeQuery(id+"F0Hq7nSFAMYVZvY_4.31.F20.boolean.opBoolean","MERGE",FACE,{"derivedFrom":[makeQuery(id+"F0Hq7nSFAMYVZvY_4.30.F20.boolean.opBoolean","MERGE",FACE,{"derivedFrom":[makeQuery(id+"F0Hq7nSFAMYVZvY_4.29.F20.boolean.opBoolean","MERGE",FACE,{"derivedFrom":[makeQuery(id+"F0Hq7nSFAMYVZvY_4.28.F20.boolean.opBoolean","MERGE",FACE,{"derivedFrom":[makeQuery(id+"F0Hq7nSFAMYVZvY_4.27.F20.boolean.opBoolean","MERGE",FACE,{"derivedFrom":[makeQuery(id+"F0Hq7nSFAMYVZvY_4.26.F20.boolean.opBoolean","MERGE",FACE,{"derivedFrom":[makeQuery(id+"F0Hq7nSFAMYVZvY_4.25.F20.boolean.opBoolean","MERGE",FACE,{"derivedFrom":[makeQuery(id+"F0Hq7nSFAMYVZvY_4.24.F20.boolean.opBoolean","MERGE",FACE,{"derivedFrom":[makeQuery(id+"F0Hq7nSFAMYVZvY_4.23.F20.boolean.opBoolean","MERGE",FACE,{"derivedFrom":[makeQuery(id+"F0Hq7nSFAMYVZvY_4.22.F20.boolean.opBoolean","MERGE",FACE,{"derivedFrom":[makeQuery(id+"F0Hq7nSFAMYVZvY_4.21.F20.boolean.opBoolean","MERGE",FACE,{"derivedFrom":[makeQuery(id+"F0Hq7nSFAMYVZvY_4.20.F20.boolean.opBoolean","MERGE",FACE,{"derivedFrom":[makeQuery(id+"F0Hq7nSFAMYVZvY_4.19.F20.boolean.opBoolean","MERGE",FACE,{"derivedFrom":[makeQuery(id+"F0Hq7nSFAMYVZvY_4.18.F20.boolean.opBoolean","MERGE",FACE,{"derivedFrom":[makeQuery(id+"F0Hq7nSFAMYVZvY_4.17.F20.boolean.opBoolean","MERGE",FACE,{"derivedFrom":[makeQuery(id+"F0Hq7nSFAMYVZvY_4.16.F20.boolean.opBoolean","MERGE",FACE,{"derivedFrom":[makeQuery(id+"F0Hq7nSFAMYVZvY_4.15.F20.boolean.opBoolean","MERGE",FACE,{"derivedFrom":[makeQuery(id+"F0Hq7nSFAMYVZvY_4.14.F20.boolean.opBoolean","MERGE",FACE,{"derivedFrom":[makeQuery(id+"F0Hq7nSFAMYVZvY_4.13.F20.boolean.opBoolean","MERGE",FACE,{"derivedFrom":[makeQuery(id+"F0Hq7nSFAMYVZvY_4.12.F20.boolean.opBoolean","MERGE",FACE,{"derivedFrom":[makeQuery(id+"F0Hq7nSFAMYVZvY_4.11.F20.boolean.opBoolean","MERGE",FACE,{"derivedFrom":[makeQuery(id+"F0Hq7nSFAMYVZvY_4.10.F20.boolean.opBoolean","MERGE",FACE,{"derivedFrom":[makeQuery(id+"F0Hq7nSFAMYVZvY_4.9.F20.boolean.opBoolean","MERGE",FACE,{"derivedFrom":[makeQuery(id+"F0Hq7nSFAMYVZvY_4.8.F20.boolean.opBoolean","MERGE",FACE,{"derivedFrom":[makeQuery(id+"F0Hq7nSFAMYVZvY_4.7.F20.boolean.opBoolean","MERGE",FACE,{"derivedFrom":[makeQuery(id+"F0Hq7nSFAMYVZvY_4.6.F20.boolean.opBoolean","MERGE",FACE,{"derivedFrom":[makeQuery(id+"F0Hq7nSFAMYVZvY_4.5.F20.boolean.opBoolean","MERGE",FACE,{"derivedFrom":[makeQuery(id+"F0Hq7nSFAMYVZvY_4.4.F20.boolean.opBoolean","MERGE",FACE,{"derivedFrom":[makeQuery(id+"F0Hq7nSFAMYVZvY_4.3.F20.boolean.opBoolean","MERGE",FACE,{"derivedFrom":[makeQuery(id+"F0Hq7nSFAMYVZvY_4.2.F20.boolean.opBoolean","MERGE",FACE,{"derivedFrom":[makeQuery(id+"F0Hq7nSFAMYVZvY_4.1.F20.boolean.opBoolean","MERGE",FACE,{"derivedFrom":[makeQuery(id+"F20.boolean.opBoolean","MERGE",FACE,{"derivedFrom":[makeQuery(id+"F18.boolean.opBoolean","COPY",FACE,{"derivedFrom":makeQuery(id+"F18.opExtrude","CAP_FACE",FACE,{"disambiguationData":[OSD([sQuery(id+"F0.wireOp",EDGE,"E95"),sQuery(id+"F0.wireOp",EDGE,"E97")])],"isStart":false})}),makeQuery(id+"F20.opExtrude","CAP_FACE",FACE,{"disambiguationData":[OSD([subQ3,subQ2,subQ1,subQ0])],"isStart":false})]}),makeQuery(id+"F0Hq7nSFAMYVZvY_4.1.F20.opExtrude","CAP_FACE",FACE,{"disambiguationData":[OSD([subQ3,subQ2,subQ1,subQ0])],"isStart":false})]}),makeQuery(id+"F0Hq7nSFAMYVZvY_4.2.F20.opExtrude","CAP_FACE",FACE,{"disambiguationData":[OSD([subQ3,subQ2,subQ1,subQ0])],"isStart":false})]}),makeQuery(id+"F0Hq7nSFAMYVZvY_4.3.F20.opExtrude","CAP_FACE",FACE,{"disambiguationData":[OSD([subQ3,subQ2,subQ1,subQ0])],"isStart":false})]}),makeQuery(id+"F0Hq7nSFAMYVZvY_4.4.F20.opExtrude","CAP_FACE",FACE,{"disambiguationData":[OSD([subQ3,subQ2,subQ1,subQ0])],"isStart":false})]}),makeQuery(id+"F0Hq7nSFAMYVZvY_4.5.F20.opExtrude","CAP_FACE",FACE,{"disambiguationData":[OSD([subQ3,subQ2,subQ1,subQ0])],"isStart":false})]}),makeQuery(id+"F0Hq7nSFAMYVZvY_4.6.F20.opExtrude","CAP_FACE",FACE,{"disambiguationData":[OSD([subQ3,subQ2,subQ1,subQ0])],"isStart":false})]}),makeQuery(id+"F0Hq7nSFAMYVZvY_4.7.F20.opExtrude","CAP_FACE",FACE,{"disambiguationData":[OSD([subQ3,subQ2,subQ1,subQ0])],"isStart":false})]}),makeQuery(id+"F0Hq7nSFAMYVZvY_4.8.F20.opExtrude","CAP_FACE",FACE,{"disambiguationData":[OSD([subQ3,subQ2,subQ1,subQ0])],"isStart":false})]}),makeQuery(id+"F0Hq7nSFAMYVZvY_4.9.F20.opExtrude","CAP_FACE",FACE,{"disambiguationData":[OSD([subQ3,subQ2,subQ1,subQ0])],"isStart":false})]}),makeQuery(id+"F0Hq7nSFAMYVZvY_4.10.F20.opExtrude","CAP_FACE",FACE,{"disambiguationData":[OSD([subQ3,subQ2,subQ1,subQ0])],"isStart":false})]}),makeQuery(id+"F0Hq7nSFAMYVZvY_4.11.F20.opExtrude","CAP_FACE",FACE,{"disambiguationData":[OSD([subQ3,subQ2,subQ1,subQ0])],"isStart":false})]}),makeQuery(id+"F0Hq7nSFAMYVZvY_4.12.F20.opExtrude","CAP_FACE",FACE,{"disambiguationData":[OSD([subQ3,subQ2,subQ1,subQ0])],"isStart":false})]}),makeQuery(id+"F0Hq7nSFAMYVZvY_4.13.F20.opExtrude","CAP_FACE",FACE,{"disambiguationData":[OSD([subQ3,subQ2,subQ1,subQ0])],"isStart":false})]}),makeQuery(id+"F0Hq7nSFAMYVZvY_4.14.F20.opExtrude","CAP_FACE",FACE,{"disambiguationData":[OSD([subQ3,subQ2,subQ1,subQ0])],"isStart":false})]}),makeQuery(id+"F0Hq7nSFAMYVZvY_4.15.F20.opExtrude","CAP_FACE",FACE,{"disambiguationData":[OSD([subQ3,subQ2,subQ1,subQ0])],"isStart":false})]}),makeQuery(id+"F0Hq7nSFAMYVZvY_4.16.F20.opExtrude","CAP_FACE",FACE,{"disambiguationData":[OSD([subQ3,subQ2,subQ1,subQ0])],"isStart":false})]}),makeQuery(id+"F0Hq7nSFAMYVZvY_4.17.F20.opExtrude","CAP_FACE",FACE,{"disambiguationData":[OSD([subQ3,subQ2,subQ1,subQ0])],"isStart":false})]}),makeQuery(id+"F0Hq7nSFAMYVZvY_4.18.F20.opExtrude","CAP_FACE",FACE,{"disambiguationData":[OSD([subQ3,subQ2,subQ1,subQ0])],"isStart":false})]}),makeQuery(id+"F0Hq7nSFAMYVZvY_4.19.F20.opExtrude","CAP_FACE",FACE,{"disambiguationData":[OSD([subQ3,subQ2,subQ1,subQ0])],"isStart":false})]}),makeQuery(id+"F0Hq7nSFAMYVZvY_4.20.F20.opExtrude","CAP_FACE",FACE,{"disambiguationData":[OSD([subQ3,subQ2,subQ1,subQ0])],"isStart":false})]}),makeQuery(id+"F0Hq7nSFAMYVZvY_4.21.F20.opExtrude","CAP_FACE",FACE,{"disambiguationData":[OSD([subQ3,subQ2,subQ1,subQ0])],"isStart":false})]}),makeQuery(id+"F0Hq7nSFAMYVZvY_4.22.F20.opExtrude","CAP_FACE",FACE,{"disambiguationData":[OSD([subQ3,subQ2,subQ1,subQ0])],"isStart":false})]}),makeQuery(id+"F0Hq7nSFAMYVZvY_4.23.F20.opExtrude","CAP_FACE",FACE,{"disambiguationData":[OSD([subQ3,subQ2,subQ1,subQ0])],"isStart":false})]}),makeQuery(id+"F0Hq7nSFAMYVZvY_4.24.F20.opExtrude","CAP_FACE",FACE,{"disambiguationData":[OSD([subQ3,subQ2,subQ1,subQ0])],"isStart":false})]}),makeQuery(id+"F0Hq7nSFAMYVZvY_4.25.F20.opExtrude","CAP_FACE",FACE,{"disambiguationData":[OSD([subQ3,subQ2,subQ1,subQ0])],"isStart":false})]}),makeQuery(id+"F0Hq7nSFAMYVZvY_4.26.F20.opExtrude","CAP_FACE",FACE,{"disambiguationData":[OSD([subQ3,subQ2,subQ1,subQ0])],"isStart":false})]}),makeQuery(id+"F0Hq7nSFAMYVZvY_4.27.F20.opExtrude","CAP_FACE",FACE,{"disambiguationData":[OSD([subQ3,subQ2,subQ1,subQ0])],"isStart":false})]}),makeQuery(id+"F0Hq7nSFAMYVZvY_4.28.F20.opExtrude","CAP_FACE",FACE,{"disambiguationData":[OSD([subQ3,subQ2,subQ1,subQ0])],"isStart":false})]}),makeQuery(id+"F0Hq7nSFAMYVZvY_4.29.F20.opExtrude","CAP_FACE",FACE,{"disambiguationData":[OSD([subQ3,subQ2,subQ1,subQ0])],"isStart":false})]}),makeQuery(id+"F0Hq7nSFAMYVZvY_4.30.F20.opExtrude","CAP_FACE",FACE,{"disambiguationData":[OSD([subQ3,subQ2,subQ1,subQ0])],"isStart":false})]}),makeQuery(id+"F0Hq7nSFAMYVZvY_4.31.F20.opExtrude","CAP_FACE",FACE,{"disambiguationData":[OSD([subQ3,subQ2,subQ1,subQ0])],"isStart":false})]}),makeQuery(id+"F0Hq7nSFAMYVZvY_4.32.F20.opExtrude","CAP_FACE",FACE,{"disambiguationData":[OSD([subQ3,subQ2,subQ1,subQ0])],"isStart":false})]}),makeQuery(id+"F0Hq7nSFAMYVZvY_4.33.F20.opExtrude","CAP_FACE",FACE,{"disambiguationData":[OSD([subQ3,subQ2,subQ1,subQ0])],"isStart":false})]}),makeQuery(id+"F0Hq7nSFAMYVZvY_4.34.F20.opExtrude","CAP_FACE",FACE,{"disambiguationData":[OSD([subQ3,subQ2,subQ1,subQ0])],"isStart":false})]}),makeQuery(id+"F0Hq7nSFAMYVZvY_4.35.F20.opExtrude","CAP_FACE",FACE,{"disambiguationData":[OSD([subQ3,subQ2,subQ1,subQ0])],"isStart":false})]}),makeQuery(id+"F0Hq7nSFAMYVZvY_4.36.F20.opExtrude","CAP_FACE",FACE,{"disambiguationData":[OSD([subQ3,subQ2,subQ1,subQ0])],"isStart":false})]}),makeQuery(id+"F0Hq7nSFAMYVZvY_4.37.F20.opExtrude","CAP_FACE",FACE,{"disambiguationData":[OSD([subQ3,subQ2,subQ1,subQ0])],"isStart":false})]}),makeQuery(id+"F0Hq7nSFAMYVZvY_4.38.F20.opExtrude","CAP_FACE",FACE,{"disambiguationData":[OSD([subQ3,subQ2,subQ1,subQ0])],"isStart":false})]}),makeQuery(id+"F0Hq7nSFAMYVZvY_4.39.F20.opExtrude","CAP_FACE",FACE,{"disambiguationData":[OSD([subQ3,subQ2,subQ1,subQ0])],"isStart":false})]});}
            var Q219;
            {var subQ0=sQuery(id+"F16.wireOp",EDGE,"E151");var subQ2=makeQuery(id+"F20.opExtrude","SWEPT_FACE",FACE,{"disambiguationData":[OSD([sQuery(id+"F19.wireOp",EDGE,"E157")])]});var subQ3=sQuery(id+"F16.wireOp",EDGE,"E152");Q219=makeQuery(id+"F0Hq7nSFAMYVZvY_4.39.F20.boolean.opBoolean","SPLIT",FACE,{"disambiguationData":[TD([subQ2])],"derivedFrom":makeQuery(id+"F0Hq7nSFAMYVZvY_4.38.F20.boolean.opBoolean","SPLIT",FACE,{"disambiguationData":[TD([subQ2])],"derivedFrom":makeQuery(id+"F0Hq7nSFAMYVZvY_4.37.F20.boolean.opBoolean","SPLIT",FACE,{"disambiguationData":[TD([subQ2])],"derivedFrom":makeQuery(id+"F0Hq7nSFAMYVZvY_4.36.F20.boolean.opBoolean","SPLIT",FACE,{"disambiguationData":[TD([subQ2])],"derivedFrom":makeQuery(id+"F0Hq7nSFAMYVZvY_4.35.F20.boolean.opBoolean","SPLIT",FACE,{"disambiguationData":[TD([subQ2])],"derivedFrom":makeQuery(id+"F0Hq7nSFAMYVZvY_4.34.F20.boolean.opBoolean","SPLIT",FACE,{"disambiguationData":[TD([subQ2])],"derivedFrom":makeQuery(id+"F0Hq7nSFAMYVZvY_4.33.F20.boolean.opBoolean","SPLIT",FACE,{"disambiguationData":[TD([subQ2])],"derivedFrom":makeQuery(id+"F0Hq7nSFAMYVZvY_4.32.F20.boolean.opBoolean","SPLIT",FACE,{"disambiguationData":[TD([subQ2])],"derivedFrom":makeQuery(id+"F0Hq7nSFAMYVZvY_4.31.F20.boolean.opBoolean","SPLIT",FACE,{"disambiguationData":[TD([subQ2])],"derivedFrom":makeQuery(id+"F0Hq7nSFAMYVZvY_4.30.F20.boolean.opBoolean","SPLIT",FACE,{"disambiguationData":[TD([subQ2])],"derivedFrom":makeQuery(id+"F0Hq7nSFAMYVZvY_4.29.F20.boolean.opBoolean","SPLIT",FACE,{"disambiguationData":[TD([subQ2])],"derivedFrom":makeQuery(id+"F0Hq7nSFAMYVZvY_4.28.F20.boolean.opBoolean","SPLIT",FACE,{"disambiguationData":[TD([subQ2])],"derivedFrom":makeQuery(id+"F0Hq7nSFAMYVZvY_4.27.F20.boolean.opBoolean","SPLIT",FACE,{"disambiguationData":[TD([subQ2])],"derivedFrom":makeQuery(id+"F0Hq7nSFAMYVZvY_4.26.F20.boolean.opBoolean","SPLIT",FACE,{"disambiguationData":[TD([subQ2])],"derivedFrom":makeQuery(id+"F0Hq7nSFAMYVZvY_4.25.F20.boolean.opBoolean","SPLIT",FACE,{"disambiguationData":[TD([subQ2])],"derivedFrom":makeQuery(id+"F0Hq7nSFAMYVZvY_4.24.F20.boolean.opBoolean","SPLIT",FACE,{"disambiguationData":[TD([subQ2])],"derivedFrom":makeQuery(id+"F0Hq7nSFAMYVZvY_4.23.F20.boolean.opBoolean","SPLIT",FACE,{"disambiguationData":[TD([subQ2])],"derivedFrom":makeQuery(id+"F0Hq7nSFAMYVZvY_4.22.F20.boolean.opBoolean","SPLIT",FACE,{"disambiguationData":[TD([subQ2])],"derivedFrom":makeQuery(id+"F0Hq7nSFAMYVZvY_4.21.F20.boolean.opBoolean","SPLIT",FACE,{"disambiguationData":[TD([subQ2])],"derivedFrom":makeQuery(id+"F0Hq7nSFAMYVZvY_4.20.F20.boolean.opBoolean","SPLIT",FACE,{"disambiguationData":[TD([subQ2])],"derivedFrom":makeQuery(id+"F0Hq7nSFAMYVZvY_4.19.F20.boolean.opBoolean","SPLIT",FACE,{"disambiguationData":[TD([subQ2])],"derivedFrom":makeQuery(id+"F0Hq7nSFAMYVZvY_4.18.F20.boolean.opBoolean","SPLIT",FACE,{"disambiguationData":[TD([subQ2])],"derivedFrom":makeQuery(id+"F0Hq7nSFAMYVZvY_4.17.F20.boolean.opBoolean","SPLIT",FACE,{"disambiguationData":[TD([subQ2])],"derivedFrom":makeQuery(id+"F0Hq7nSFAMYVZvY_4.16.F20.boolean.opBoolean","SPLIT",FACE,{"disambiguationData":[TD([subQ2])],"derivedFrom":makeQuery(id+"F0Hq7nSFAMYVZvY_4.15.F20.boolean.opBoolean","SPLIT",FACE,{"disambiguationData":[TD([subQ2])],"derivedFrom":makeQuery(id+"F0Hq7nSFAMYVZvY_4.14.F20.boolean.opBoolean","SPLIT",FACE,{"disambiguationData":[TD([subQ2])],"derivedFrom":makeQuery(id+"F0Hq7nSFAMYVZvY_4.13.F20.boolean.opBoolean","SPLIT",FACE,{"disambiguationData":[TD([subQ2])],"derivedFrom":makeQuery(id+"F0Hq7nSFAMYVZvY_4.12.F20.boolean.opBoolean","SPLIT",FACE,{"disambiguationData":[TD([subQ2])],"derivedFrom":makeQuery(id+"F0Hq7nSFAMYVZvY_4.11.F20.boolean.opBoolean","SPLIT",FACE,{"disambiguationData":[TD([subQ2])],"derivedFrom":makeQuery(id+"F0Hq7nSFAMYVZvY_4.10.F20.boolean.opBoolean","SPLIT",FACE,{"disambiguationData":[TD([subQ2])],"derivedFrom":makeQuery(id+"F0Hq7nSFAMYVZvY_4.9.F20.boolean.opBoolean","SPLIT",FACE,{"disambiguationData":[TD([subQ2])],"derivedFrom":makeQuery(id+"F0Hq7nSFAMYVZvY_4.8.F20.boolean.opBoolean","SPLIT",FACE,{"disambiguationData":[TD([subQ2])],"derivedFrom":makeQuery(id+"F0Hq7nSFAMYVZvY_4.7.F20.boolean.opBoolean","SPLIT",FACE,{"disambiguationData":[TD([subQ2])],"derivedFrom":makeQuery(id+"F0Hq7nSFAMYVZvY_4.6.F20.boolean.opBoolean","SPLIT",FACE,{"disambiguationData":[TD([subQ2])],"derivedFrom":makeQuery(id+"F0Hq7nSFAMYVZvY_4.5.F20.boolean.opBoolean","SPLIT",FACE,{"disambiguationData":[TD([subQ2])],"derivedFrom":makeQuery(id+"F0Hq7nSFAMYVZvY_4.4.F20.boolean.opBoolean","SPLIT",FACE,{"disambiguationData":[TD([subQ2])],"derivedFrom":makeQuery(id+"F0Hq7nSFAMYVZvY_4.3.F20.boolean.opBoolean","SPLIT",FACE,{"disambiguationData":[TD([subQ2])],"derivedFrom":makeQuery(id+"F0Hq7nSFAMYVZvY_4.2.F20.boolean.opBoolean","SPLIT",FACE,{"disambiguationData":[TD([subQ2])],"derivedFrom":makeQuery(id+"F0Hq7nSFAMYVZvY_4.1.F20.boolean.opBoolean","SPLIT",FACE,{"disambiguationData":[TD([subQ2])],"derivedFrom":makeQuery(id+"F17.boolean.opBoolean","COPY",FACE,{"derivedFrom":makeQuery(id+"F17.opExtrude","CAP_FACE",FACE,{"disambiguationData":[OSD([subQ0,subQ3])],"isStart":false})})})})})})})})})})})})})})})})})})})})})})})})})})})})})})})})})})})})})})})})});}
            var Q220;
            {var subQ0=sQuery(id+"F16.wireOp",EDGE,"E151");var subQ2=sQuery(id+"F16.wireOp",EDGE,"E152");var subQ4=sQuery(id+"F19.wireOp",EDGE,"E158.MirrorCS");var subQ5=makeQuery(id+"F0Hq7nSFAMYVZvY_4.38.F20.opExtrude","SWEPT_FACE",FACE,{"disambiguationData":[OSD([subQ4])]});var subQ6=sQuery(id+"F19.wireOp",EDGE,"E157");var subQ7=makeQuery(id+"F20.opExtrude","SWEPT_FACE",FACE,{"disambiguationData":[OSD([subQ6])]});Q220=makeQuery(id+"F0Hq7nSFAMYVZvY_4.39.F20.boolean.opBoolean","SPLIT",FACE,{"disambiguationData":[TD([subQ5])],"derivedFrom":makeQuery(id+"F0Hq7nSFAMYVZvY_4.38.F20.boolean.opBoolean","SPLIT",FACE,{"disambiguationData":[TD([subQ7])],"derivedFrom":makeQuery(id+"F0Hq7nSFAMYVZvY_4.37.F20.boolean.opBoolean","SPLIT",FACE,{"disambiguationData":[TD([subQ7])],"derivedFrom":makeQuery(id+"F0Hq7nSFAMYVZvY_4.36.F20.boolean.opBoolean","SPLIT",FACE,{"disambiguationData":[TD([subQ7])],"derivedFrom":makeQuery(id+"F0Hq7nSFAMYVZvY_4.35.F20.boolean.opBoolean","SPLIT",FACE,{"disambiguationData":[TD([subQ7])],"derivedFrom":makeQuery(id+"F0Hq7nSFAMYVZvY_4.34.F20.boolean.opBoolean","SPLIT",FACE,{"disambiguationData":[TD([subQ7])],"derivedFrom":makeQuery(id+"F0Hq7nSFAMYVZvY_4.33.F20.boolean.opBoolean","SPLIT",FACE,{"disambiguationData":[TD([subQ7])],"derivedFrom":makeQuery(id+"F0Hq7nSFAMYVZvY_4.32.F20.boolean.opBoolean","SPLIT",FACE,{"disambiguationData":[TD([subQ7])],"derivedFrom":makeQuery(id+"F0Hq7nSFAMYVZvY_4.31.F20.boolean.opBoolean","SPLIT",FACE,{"disambiguationData":[TD([subQ7])],"derivedFrom":makeQuery(id+"F0Hq7nSFAMYVZvY_4.30.F20.boolean.opBoolean","SPLIT",FACE,{"disambiguationData":[TD([subQ7])],"derivedFrom":makeQuery(id+"F0Hq7nSFAMYVZvY_4.29.F20.boolean.opBoolean","SPLIT",FACE,{"disambiguationData":[TD([subQ7])],"derivedFrom":makeQuery(id+"F0Hq7nSFAMYVZvY_4.28.F20.boolean.opBoolean","SPLIT",FACE,{"disambiguationData":[TD([subQ7])],"derivedFrom":makeQuery(id+"F0Hq7nSFAMYVZvY_4.27.F20.boolean.opBoolean","SPLIT",FACE,{"disambiguationData":[TD([subQ7])],"derivedFrom":makeQuery(id+"F0Hq7nSFAMYVZvY_4.26.F20.boolean.opBoolean","SPLIT",FACE,{"disambiguationData":[TD([subQ7])],"derivedFrom":makeQuery(id+"F0Hq7nSFAMYVZvY_4.25.F20.boolean.opBoolean","SPLIT",FACE,{"disambiguationData":[TD([subQ7])],"derivedFrom":makeQuery(id+"F0Hq7nSFAMYVZvY_4.24.F20.boolean.opBoolean","SPLIT",FACE,{"disambiguationData":[TD([subQ7])],"derivedFrom":makeQuery(id+"F0Hq7nSFAMYVZvY_4.23.F20.boolean.opBoolean","SPLIT",FACE,{"disambiguationData":[TD([subQ7])],"derivedFrom":makeQuery(id+"F0Hq7nSFAMYVZvY_4.22.F20.boolean.opBoolean","SPLIT",FACE,{"disambiguationData":[TD([subQ7])],"derivedFrom":makeQuery(id+"F0Hq7nSFAMYVZvY_4.21.F20.boolean.opBoolean","SPLIT",FACE,{"disambiguationData":[TD([subQ7])],"derivedFrom":makeQuery(id+"F0Hq7nSFAMYVZvY_4.20.F20.boolean.opBoolean","SPLIT",FACE,{"disambiguationData":[TD([subQ7])],"derivedFrom":makeQuery(id+"F0Hq7nSFAMYVZvY_4.19.F20.boolean.opBoolean","SPLIT",FACE,{"disambiguationData":[TD([subQ7])],"derivedFrom":makeQuery(id+"F0Hq7nSFAMYVZvY_4.18.F20.boolean.opBoolean","SPLIT",FACE,{"disambiguationData":[TD([subQ7])],"derivedFrom":makeQuery(id+"F0Hq7nSFAMYVZvY_4.17.F20.boolean.opBoolean","SPLIT",FACE,{"disambiguationData":[TD([subQ7])],"derivedFrom":makeQuery(id+"F0Hq7nSFAMYVZvY_4.16.F20.boolean.opBoolean","SPLIT",FACE,{"disambiguationData":[TD([subQ7])],"derivedFrom":makeQuery(id+"F0Hq7nSFAMYVZvY_4.15.F20.boolean.opBoolean","SPLIT",FACE,{"disambiguationData":[TD([subQ7])],"derivedFrom":makeQuery(id+"F0Hq7nSFAMYVZvY_4.14.F20.boolean.opBoolean","SPLIT",FACE,{"disambiguationData":[TD([subQ7])],"derivedFrom":makeQuery(id+"F0Hq7nSFAMYVZvY_4.13.F20.boolean.opBoolean","SPLIT",FACE,{"disambiguationData":[TD([subQ7])],"derivedFrom":makeQuery(id+"F0Hq7nSFAMYVZvY_4.12.F20.boolean.opBoolean","SPLIT",FACE,{"disambiguationData":[TD([subQ7])],"derivedFrom":makeQuery(id+"F0Hq7nSFAMYVZvY_4.11.F20.boolean.opBoolean","SPLIT",FACE,{"disambiguationData":[TD([subQ7])],"derivedFrom":makeQuery(id+"F0Hq7nSFAMYVZvY_4.10.F20.boolean.opBoolean","SPLIT",FACE,{"disambiguationData":[TD([subQ7])],"derivedFrom":makeQuery(id+"F0Hq7nSFAMYVZvY_4.9.F20.boolean.opBoolean","SPLIT",FACE,{"disambiguationData":[TD([subQ7])],"derivedFrom":makeQuery(id+"F0Hq7nSFAMYVZvY_4.8.F20.boolean.opBoolean","SPLIT",FACE,{"disambiguationData":[TD([subQ7])],"derivedFrom":makeQuery(id+"F0Hq7nSFAMYVZvY_4.7.F20.boolean.opBoolean","SPLIT",FACE,{"disambiguationData":[TD([subQ7])],"derivedFrom":makeQuery(id+"F0Hq7nSFAMYVZvY_4.6.F20.boolean.opBoolean","SPLIT",FACE,{"disambiguationData":[TD([subQ7])],"derivedFrom":makeQuery(id+"F0Hq7nSFAMYVZvY_4.5.F20.boolean.opBoolean","SPLIT",FACE,{"disambiguationData":[TD([subQ7])],"derivedFrom":makeQuery(id+"F0Hq7nSFAMYVZvY_4.4.F20.boolean.opBoolean","SPLIT",FACE,{"disambiguationData":[TD([subQ7])],"derivedFrom":makeQuery(id+"F0Hq7nSFAMYVZvY_4.3.F20.boolean.opBoolean","SPLIT",FACE,{"disambiguationData":[TD([subQ7])],"derivedFrom":makeQuery(id+"F0Hq7nSFAMYVZvY_4.2.F20.boolean.opBoolean","SPLIT",FACE,{"disambiguationData":[TD([subQ7])],"derivedFrom":makeQuery(id+"F0Hq7nSFAMYVZvY_4.1.F20.boolean.opBoolean","SPLIT",FACE,{"disambiguationData":[TD([subQ7])],"derivedFrom":makeQuery(id+"F17.boolean.opBoolean","COPY",FACE,{"derivedFrom":makeQuery(id+"F17.opExtrude","CAP_FACE",FACE,{"disambiguationData":[OSD([subQ0,subQ2])],"isStart":false})})})})})})})})})})})})})})})})})})})})})})})})})})})})})})})})})})})})})})})})});}
            var Q221;
            Q221=makeQuery(id+"F0Hq7nSFAMYVZvY_4.39.F20.opExtrude","CAP_EDGE",EDGE,{"disambiguationData":[OSD([sQuery(id+"F19.wireOp",EDGE,"E157")])],"isStart":true});
            var Q222;
            {var subQ1=sQuery(id+"F19.wireOp",EDGE,"E157");var subQ3=sQuery(id+"F16.wireOp",EDGE,"E151");var subQ16=makeQuery(id+"F20.opExtrude","SWEPT_FACE",FACE,{"disambiguationData":[OSD([subQ1])]});Q222=makeQuery(id+"F0Hq7nSFAMYVZvY_4.39.F20.boolean.opBoolean","SPLIT",FACE,{"disambiguationData":[TD([subQ16])],"derivedFrom":makeQuery(id+"F0Hq7nSFAMYVZvY_4.38.F20.boolean.opBoolean","SPLIT",FACE,{"disambiguationData":[TD([subQ16])],"derivedFrom":makeQuery(id+"F0Hq7nSFAMYVZvY_4.37.F20.boolean.opBoolean","SPLIT",FACE,{"disambiguationData":[TD([subQ16])],"derivedFrom":makeQuery(id+"F0Hq7nSFAMYVZvY_4.36.F20.boolean.opBoolean","SPLIT",FACE,{"disambiguationData":[TD([subQ16])],"derivedFrom":makeQuery(id+"F0Hq7nSFAMYVZvY_4.35.F20.boolean.opBoolean","SPLIT",FACE,{"disambiguationData":[TD([subQ16])],"derivedFrom":makeQuery(id+"F0Hq7nSFAMYVZvY_4.34.F20.boolean.opBoolean","SPLIT",FACE,{"disambiguationData":[TD([subQ16])],"derivedFrom":makeQuery(id+"F0Hq7nSFAMYVZvY_4.33.F20.boolean.opBoolean","SPLIT",FACE,{"disambiguationData":[TD([subQ16])],"derivedFrom":makeQuery(id+"F0Hq7nSFAMYVZvY_4.32.F20.boolean.opBoolean","SPLIT",FACE,{"disambiguationData":[TD([subQ16])],"derivedFrom":makeQuery(id+"F0Hq7nSFAMYVZvY_4.31.F20.boolean.opBoolean","SPLIT",FACE,{"disambiguationData":[TD([subQ16])],"derivedFrom":makeQuery(id+"F0Hq7nSFAMYVZvY_4.30.F20.boolean.opBoolean","SPLIT",FACE,{"disambiguationData":[TD([subQ16])],"derivedFrom":makeQuery(id+"F0Hq7nSFAMYVZvY_4.29.F20.boolean.opBoolean","SPLIT",FACE,{"disambiguationData":[TD([subQ16])],"derivedFrom":makeQuery(id+"F0Hq7nSFAMYVZvY_4.28.F20.boolean.opBoolean","SPLIT",FACE,{"disambiguationData":[TD([subQ16])],"derivedFrom":makeQuery(id+"F0Hq7nSFAMYVZvY_4.27.F20.boolean.opBoolean","SPLIT",FACE,{"disambiguationData":[TD([subQ16])],"derivedFrom":makeQuery(id+"F0Hq7nSFAMYVZvY_4.26.F20.boolean.opBoolean","SPLIT",FACE,{"disambiguationData":[TD([subQ16])],"derivedFrom":makeQuery(id+"F0Hq7nSFAMYVZvY_4.25.F20.boolean.opBoolean","SPLIT",FACE,{"disambiguationData":[TD([subQ16])],"derivedFrom":makeQuery(id+"F0Hq7nSFAMYVZvY_4.24.F20.boolean.opBoolean","SPLIT",FACE,{"disambiguationData":[TD([subQ16])],"derivedFrom":makeQuery(id+"F0Hq7nSFAMYVZvY_4.23.F20.boolean.opBoolean","SPLIT",FACE,{"disambiguationData":[TD([subQ16])],"derivedFrom":makeQuery(id+"F0Hq7nSFAMYVZvY_4.22.F20.boolean.opBoolean","SPLIT",FACE,{"disambiguationData":[TD([subQ16])],"derivedFrom":makeQuery(id+"F0Hq7nSFAMYVZvY_4.21.F20.boolean.opBoolean","SPLIT",FACE,{"disambiguationData":[TD([subQ16])],"derivedFrom":makeQuery(id+"F0Hq7nSFAMYVZvY_4.20.F20.boolean.opBoolean","SPLIT",FACE,{"disambiguationData":[TD([subQ16])],"derivedFrom":makeQuery(id+"F0Hq7nSFAMYVZvY_4.19.F20.boolean.opBoolean","SPLIT",FACE,{"disambiguationData":[TD([subQ16])],"derivedFrom":makeQuery(id+"F0Hq7nSFAMYVZvY_4.18.F20.boolean.opBoolean","SPLIT",FACE,{"disambiguationData":[TD([subQ16])],"derivedFrom":makeQuery(id+"F0Hq7nSFAMYVZvY_4.17.F20.boolean.opBoolean","SPLIT",FACE,{"disambiguationData":[TD([subQ16])],"derivedFrom":makeQuery(id+"F0Hq7nSFAMYVZvY_4.16.F20.boolean.opBoolean","SPLIT",FACE,{"disambiguationData":[TD([subQ16])],"derivedFrom":makeQuery(id+"F0Hq7nSFAMYVZvY_4.15.F20.boolean.opBoolean","SPLIT",FACE,{"disambiguationData":[TD([subQ16])],"derivedFrom":makeQuery(id+"F0Hq7nSFAMYVZvY_4.14.F20.boolean.opBoolean","SPLIT",FACE,{"disambiguationData":[TD([subQ16])],"derivedFrom":makeQuery(id+"F0Hq7nSFAMYVZvY_4.13.F20.boolean.opBoolean","SPLIT",FACE,{"disambiguationData":[TD([subQ16])],"derivedFrom":makeQuery(id+"F0Hq7nSFAMYVZvY_4.12.F20.boolean.opBoolean","SPLIT",FACE,{"disambiguationData":[TD([subQ16])],"derivedFrom":makeQuery(id+"F0Hq7nSFAMYVZvY_4.11.F20.boolean.opBoolean","SPLIT",FACE,{"disambiguationData":[TD([subQ16])],"derivedFrom":makeQuery(id+"F0Hq7nSFAMYVZvY_4.10.F20.boolean.opBoolean","SPLIT",FACE,{"disambiguationData":[TD([subQ16])],"derivedFrom":makeQuery(id+"F0Hq7nSFAMYVZvY_4.9.F20.boolean.opBoolean","SPLIT",FACE,{"disambiguationData":[TD([subQ16])],"derivedFrom":makeQuery(id+"F0Hq7nSFAMYVZvY_4.8.F20.boolean.opBoolean","SPLIT",FACE,{"disambiguationData":[TD([subQ16])],"derivedFrom":makeQuery(id+"F0Hq7nSFAMYVZvY_4.7.F20.boolean.opBoolean","SPLIT",FACE,{"disambiguationData":[TD([subQ16])],"derivedFrom":makeQuery(id+"F0Hq7nSFAMYVZvY_4.6.F20.boolean.opBoolean","SPLIT",FACE,{"disambiguationData":[TD([subQ16])],"derivedFrom":makeQuery(id+"F0Hq7nSFAMYVZvY_4.5.F20.boolean.opBoolean","SPLIT",FACE,{"disambiguationData":[TD([subQ16])],"derivedFrom":makeQuery(id+"F0Hq7nSFAMYVZvY_4.4.F20.boolean.opBoolean","SPLIT",FACE,{"disambiguationData":[TD([subQ16])],"derivedFrom":makeQuery(id+"F0Hq7nSFAMYVZvY_4.3.F20.boolean.opBoolean","SPLIT",FACE,{"disambiguationData":[TD([subQ16])],"derivedFrom":makeQuery(id+"F0Hq7nSFAMYVZvY_4.2.F20.boolean.opBoolean","SPLIT",FACE,{"disambiguationData":[TD([subQ16])],"derivedFrom":makeQuery(id+"F0Hq7nSFAMYVZvY_4.1.F20.boolean.opBoolean","SPLIT",FACE,{"disambiguationData":[TD([subQ16])],"derivedFrom":makeQuery(id+"F17.boolean.opBoolean","COPY",FACE,{"derivedFrom":makeQuery(id+"F17.opExtrude","SWEPT_FACE",FACE,{"disambiguationData":[OSD([subQ3])]})})})})})})})})})})})})})})})})})})})})})})})})})})})})})})})})})})})})})})})})});}
            var Q223;
            {var subQ0=sQuery(id+"F19.wireOp",EDGE,"E158.MirrorCS");var subQ1=sQuery(id+"F19.wireOp",EDGE,"E157");var subQ3=sQuery(id+"F16.wireOp",EDGE,"E151");var subQ23=makeQuery(id+"F0Hq7nSFAMYVZvY_4.38.F20.opExtrude","SWEPT_FACE",FACE,{"disambiguationData":[OSD([subQ0])]});var subQ46=makeQuery(id+"F20.opExtrude","SWEPT_FACE",FACE,{"disambiguationData":[OSD([subQ1])]});Q223=makeQuery(id+"F0Hq7nSFAMYVZvY_4.39.F20.boolean.opBoolean","SPLIT",FACE,{"disambiguationData":[TD([subQ23])],"derivedFrom":makeQuery(id+"F0Hq7nSFAMYVZvY_4.38.F20.boolean.opBoolean","SPLIT",FACE,{"disambiguationData":[TD([subQ46])],"derivedFrom":makeQuery(id+"F0Hq7nSFAMYVZvY_4.37.F20.boolean.opBoolean","SPLIT",FACE,{"disambiguationData":[TD([subQ46])],"derivedFrom":makeQuery(id+"F0Hq7nSFAMYVZvY_4.36.F20.boolean.opBoolean","SPLIT",FACE,{"disambiguationData":[TD([subQ46])],"derivedFrom":makeQuery(id+"F0Hq7nSFAMYVZvY_4.35.F20.boolean.opBoolean","SPLIT",FACE,{"disambiguationData":[TD([subQ46])],"derivedFrom":makeQuery(id+"F0Hq7nSFAMYVZvY_4.34.F20.boolean.opBoolean","SPLIT",FACE,{"disambiguationData":[TD([subQ46])],"derivedFrom":makeQuery(id+"F0Hq7nSFAMYVZvY_4.33.F20.boolean.opBoolean","SPLIT",FACE,{"disambiguationData":[TD([subQ46])],"derivedFrom":makeQuery(id+"F0Hq7nSFAMYVZvY_4.32.F20.boolean.opBoolean","SPLIT",FACE,{"disambiguationData":[TD([subQ46])],"derivedFrom":makeQuery(id+"F0Hq7nSFAMYVZvY_4.31.F20.boolean.opBoolean","SPLIT",FACE,{"disambiguationData":[TD([subQ46])],"derivedFrom":makeQuery(id+"F0Hq7nSFAMYVZvY_4.30.F20.boolean.opBoolean","SPLIT",FACE,{"disambiguationData":[TD([subQ46])],"derivedFrom":makeQuery(id+"F0Hq7nSFAMYVZvY_4.29.F20.boolean.opBoolean","SPLIT",FACE,{"disambiguationData":[TD([subQ46])],"derivedFrom":makeQuery(id+"F0Hq7nSFAMYVZvY_4.28.F20.boolean.opBoolean","SPLIT",FACE,{"disambiguationData":[TD([subQ46])],"derivedFrom":makeQuery(id+"F0Hq7nSFAMYVZvY_4.27.F20.boolean.opBoolean","SPLIT",FACE,{"disambiguationData":[TD([subQ46])],"derivedFrom":makeQuery(id+"F0Hq7nSFAMYVZvY_4.26.F20.boolean.opBoolean","SPLIT",FACE,{"disambiguationData":[TD([subQ46])],"derivedFrom":makeQuery(id+"F0Hq7nSFAMYVZvY_4.25.F20.boolean.opBoolean","SPLIT",FACE,{"disambiguationData":[TD([subQ46])],"derivedFrom":makeQuery(id+"F0Hq7nSFAMYVZvY_4.24.F20.boolean.opBoolean","SPLIT",FACE,{"disambiguationData":[TD([subQ46])],"derivedFrom":makeQuery(id+"F0Hq7nSFAMYVZvY_4.23.F20.boolean.opBoolean","SPLIT",FACE,{"disambiguationData":[TD([subQ46])],"derivedFrom":makeQuery(id+"F0Hq7nSFAMYVZvY_4.22.F20.boolean.opBoolean","SPLIT",FACE,{"disambiguationData":[TD([subQ46])],"derivedFrom":makeQuery(id+"F0Hq7nSFAMYVZvY_4.21.F20.boolean.opBoolean","SPLIT",FACE,{"disambiguationData":[TD([subQ46])],"derivedFrom":makeQuery(id+"F0Hq7nSFAMYVZvY_4.20.F20.boolean.opBoolean","SPLIT",FACE,{"disambiguationData":[TD([subQ46])],"derivedFrom":makeQuery(id+"F0Hq7nSFAMYVZvY_4.19.F20.boolean.opBoolean","SPLIT",FACE,{"disambiguationData":[TD([subQ46])],"derivedFrom":makeQuery(id+"F0Hq7nSFAMYVZvY_4.18.F20.boolean.opBoolean","SPLIT",FACE,{"disambiguationData":[TD([subQ46])],"derivedFrom":makeQuery(id+"F0Hq7nSFAMYVZvY_4.17.F20.boolean.opBoolean","SPLIT",FACE,{"disambiguationData":[TD([subQ46])],"derivedFrom":makeQuery(id+"F0Hq7nSFAMYVZvY_4.16.F20.boolean.opBoolean","SPLIT",FACE,{"disambiguationData":[TD([subQ46])],"derivedFrom":makeQuery(id+"F0Hq7nSFAMYVZvY_4.15.F20.boolean.opBoolean","SPLIT",FACE,{"disambiguationData":[TD([subQ46])],"derivedFrom":makeQuery(id+"F0Hq7nSFAMYVZvY_4.14.F20.boolean.opBoolean","SPLIT",FACE,{"disambiguationData":[TD([subQ46])],"derivedFrom":makeQuery(id+"F0Hq7nSFAMYVZvY_4.13.F20.boolean.opBoolean","SPLIT",FACE,{"disambiguationData":[TD([subQ46])],"derivedFrom":makeQuery(id+"F0Hq7nSFAMYVZvY_4.12.F20.boolean.opBoolean","SPLIT",FACE,{"disambiguationData":[TD([subQ46])],"derivedFrom":makeQuery(id+"F0Hq7nSFAMYVZvY_4.11.F20.boolean.opBoolean","SPLIT",FACE,{"disambiguationData":[TD([subQ46])],"derivedFrom":makeQuery(id+"F0Hq7nSFAMYVZvY_4.10.F20.boolean.opBoolean","SPLIT",FACE,{"disambiguationData":[TD([subQ46])],"derivedFrom":makeQuery(id+"F0Hq7nSFAMYVZvY_4.9.F20.boolean.opBoolean","SPLIT",FACE,{"disambiguationData":[TD([subQ46])],"derivedFrom":makeQuery(id+"F0Hq7nSFAMYVZvY_4.8.F20.boolean.opBoolean","SPLIT",FACE,{"disambiguationData":[TD([subQ46])],"derivedFrom":makeQuery(id+"F0Hq7nSFAMYVZvY_4.7.F20.boolean.opBoolean","SPLIT",FACE,{"disambiguationData":[TD([subQ46])],"derivedFrom":makeQuery(id+"F0Hq7nSFAMYVZvY_4.6.F20.boolean.opBoolean","SPLIT",FACE,{"disambiguationData":[TD([subQ46])],"derivedFrom":makeQuery(id+"F0Hq7nSFAMYVZvY_4.5.F20.boolean.opBoolean","SPLIT",FACE,{"disambiguationData":[TD([subQ46])],"derivedFrom":makeQuery(id+"F0Hq7nSFAMYVZvY_4.4.F20.boolean.opBoolean","SPLIT",FACE,{"disambiguationData":[TD([subQ46])],"derivedFrom":makeQuery(id+"F0Hq7nSFAMYVZvY_4.3.F20.boolean.opBoolean","SPLIT",FACE,{"disambiguationData":[TD([subQ46])],"derivedFrom":makeQuery(id+"F0Hq7nSFAMYVZvY_4.2.F20.boolean.opBoolean","SPLIT",FACE,{"disambiguationData":[TD([subQ46])],"derivedFrom":makeQuery(id+"F0Hq7nSFAMYVZvY_4.1.F20.boolean.opBoolean","SPLIT",FACE,{"disambiguationData":[TD([subQ46])],"derivedFrom":makeQuery(id+"F17.boolean.opBoolean","COPY",FACE,{"derivedFrom":makeQuery(id+"F17.opExtrude","SWEPT_FACE",FACE,{"disambiguationData":[OSD([subQ3])]})})})})})})})})})})})})})})})})})})})})})})})})})})})})})})})})})})})})})})})})});}
            var Q224;
            {var subQ1=sQuery(id+"F19.wireOp",EDGE,"E157");var subQ3=sQuery(id+"F16.wireOp",EDGE,"E151");var subQ19=makeQuery(id+"F20.opExtrude","SWEPT_FACE",FACE,{"disambiguationData":[OSD([subQ1])]});Q224=makeQuery(id+"F0Hq7nSFAMYVZvY_4.39.F20.boolean.opBoolean","SPLIT",EDGE,{"disambiguationData":[TD([subQ19])],"derivedFrom":makeQuery(id+"F0Hq7nSFAMYVZvY_4.38.F20.boolean.opBoolean","SPLIT",EDGE,{"disambiguationData":[TD([subQ19])],"derivedFrom":makeQuery(id+"F0Hq7nSFAMYVZvY_4.37.F20.boolean.opBoolean","SPLIT",EDGE,{"disambiguationData":[TD([subQ19])],"derivedFrom":makeQuery(id+"F0Hq7nSFAMYVZvY_4.36.F20.boolean.opBoolean","SPLIT",EDGE,{"disambiguationData":[TD([subQ19])],"derivedFrom":makeQuery(id+"F0Hq7nSFAMYVZvY_4.35.F20.boolean.opBoolean","SPLIT",EDGE,{"disambiguationData":[TD([subQ19])],"derivedFrom":makeQuery(id+"F0Hq7nSFAMYVZvY_4.34.F20.boolean.opBoolean","SPLIT",EDGE,{"disambiguationData":[TD([subQ19])],"derivedFrom":makeQuery(id+"F0Hq7nSFAMYVZvY_4.33.F20.boolean.opBoolean","SPLIT",EDGE,{"disambiguationData":[TD([subQ19])],"derivedFrom":makeQuery(id+"F0Hq7nSFAMYVZvY_4.32.F20.boolean.opBoolean","SPLIT",EDGE,{"disambiguationData":[TD([subQ19])],"derivedFrom":makeQuery(id+"F0Hq7nSFAMYVZvY_4.31.F20.boolean.opBoolean","SPLIT",EDGE,{"disambiguationData":[TD([subQ19])],"derivedFrom":makeQuery(id+"F0Hq7nSFAMYVZvY_4.30.F20.boolean.opBoolean","SPLIT",EDGE,{"disambiguationData":[TD([subQ19])],"derivedFrom":makeQuery(id+"F0Hq7nSFAMYVZvY_4.29.F20.boolean.opBoolean","SPLIT",EDGE,{"disambiguationData":[TD([subQ19])],"derivedFrom":makeQuery(id+"F0Hq7nSFAMYVZvY_4.28.F20.boolean.opBoolean","SPLIT",EDGE,{"disambiguationData":[TD([subQ19])],"derivedFrom":makeQuery(id+"F0Hq7nSFAMYVZvY_4.27.F20.boolean.opBoolean","SPLIT",EDGE,{"disambiguationData":[TD([subQ19])],"derivedFrom":makeQuery(id+"F0Hq7nSFAMYVZvY_4.26.F20.boolean.opBoolean","SPLIT",EDGE,{"disambiguationData":[TD([subQ19])],"derivedFrom":makeQuery(id+"F0Hq7nSFAMYVZvY_4.25.F20.boolean.opBoolean","SPLIT",EDGE,{"disambiguationData":[TD([subQ19])],"derivedFrom":makeQuery(id+"F0Hq7nSFAMYVZvY_4.24.F20.boolean.opBoolean","SPLIT",EDGE,{"disambiguationData":[TD([subQ19])],"derivedFrom":makeQuery(id+"F0Hq7nSFAMYVZvY_4.23.F20.boolean.opBoolean","SPLIT",EDGE,{"disambiguationData":[TD([subQ19])],"derivedFrom":makeQuery(id+"F0Hq7nSFAMYVZvY_4.22.F20.boolean.opBoolean","SPLIT",EDGE,{"disambiguationData":[TD([subQ19])],"derivedFrom":makeQuery(id+"F0Hq7nSFAMYVZvY_4.21.F20.boolean.opBoolean","SPLIT",EDGE,{"disambiguationData":[TD([subQ19])],"derivedFrom":makeQuery(id+"F0Hq7nSFAMYVZvY_4.20.F20.boolean.opBoolean","SPLIT",EDGE,{"disambiguationData":[TD([subQ19])],"derivedFrom":makeQuery(id+"F0Hq7nSFAMYVZvY_4.19.F20.boolean.opBoolean","SPLIT",EDGE,{"disambiguationData":[TD([subQ19])],"derivedFrom":makeQuery(id+"F0Hq7nSFAMYVZvY_4.18.F20.boolean.opBoolean","SPLIT",EDGE,{"disambiguationData":[TD([subQ19])],"derivedFrom":makeQuery(id+"F0Hq7nSFAMYVZvY_4.17.F20.boolean.opBoolean","SPLIT",EDGE,{"disambiguationData":[TD([subQ19])],"derivedFrom":makeQuery(id+"F0Hq7nSFAMYVZvY_4.16.F20.boolean.opBoolean","SPLIT",EDGE,{"disambiguationData":[TD([subQ19])],"derivedFrom":makeQuery(id+"F0Hq7nSFAMYVZvY_4.15.F20.boolean.opBoolean","SPLIT",EDGE,{"disambiguationData":[TD([subQ19])],"derivedFrom":makeQuery(id+"F0Hq7nSFAMYVZvY_4.14.F20.boolean.opBoolean","SPLIT",EDGE,{"disambiguationData":[TD([subQ19])],"derivedFrom":makeQuery(id+"F0Hq7nSFAMYVZvY_4.13.F20.boolean.opBoolean","SPLIT",EDGE,{"disambiguationData":[TD([subQ19])],"derivedFrom":makeQuery(id+"F0Hq7nSFAMYVZvY_4.12.F20.boolean.opBoolean","SPLIT",EDGE,{"disambiguationData":[TD([subQ19])],"derivedFrom":makeQuery(id+"F0Hq7nSFAMYVZvY_4.11.F20.boolean.opBoolean","SPLIT",EDGE,{"disambiguationData":[TD([subQ19])],"derivedFrom":makeQuery(id+"F0Hq7nSFAMYVZvY_4.10.F20.boolean.opBoolean","SPLIT",EDGE,{"disambiguationData":[TD([subQ19])],"derivedFrom":makeQuery(id+"F0Hq7nSFAMYVZvY_4.9.F20.boolean.opBoolean","SPLIT",EDGE,{"disambiguationData":[TD([subQ19])],"derivedFrom":makeQuery(id+"F0Hq7nSFAMYVZvY_4.8.F20.boolean.opBoolean","SPLIT",EDGE,{"disambiguationData":[TD([subQ19])],"derivedFrom":makeQuery(id+"F0Hq7nSFAMYVZvY_4.7.F20.boolean.opBoolean","SPLIT",EDGE,{"disambiguationData":[TD([subQ19])],"derivedFrom":makeQuery(id+"F0Hq7nSFAMYVZvY_4.6.F20.boolean.opBoolean","SPLIT",EDGE,{"disambiguationData":[TD([subQ19])],"derivedFrom":makeQuery(id+"F0Hq7nSFAMYVZvY_4.5.F20.boolean.opBoolean","SPLIT",EDGE,{"disambiguationData":[TD([subQ19])],"derivedFrom":makeQuery(id+"F0Hq7nSFAMYVZvY_4.4.F20.boolean.opBoolean","SPLIT",EDGE,{"disambiguationData":[TD([subQ19])],"derivedFrom":makeQuery(id+"F0Hq7nSFAMYVZvY_4.3.F20.boolean.opBoolean","SPLIT",EDGE,{"disambiguationData":[TD([subQ19])],"derivedFrom":makeQuery(id+"F0Hq7nSFAMYVZvY_4.2.F20.boolean.opBoolean","SPLIT",EDGE,{"disambiguationData":[TD([subQ19])],"derivedFrom":makeQuery(id+"F0Hq7nSFAMYVZvY_4.1.F20.boolean.opBoolean","SPLIT",EDGE,{"disambiguationData":[TD([subQ19])],"derivedFrom":makeQuery(id+"F18.boolean.opBoolean","COPY",EDGE,{"derivedFrom":makeQuery(id+"F18.opExtrude","CAP_EDGE",EDGE,{"disambiguationData":[OSD([subQ3])],"isStart":false})})})})})})})})})})})})})})})})})})})})})})})})})})})})})})})})})})})})})})})})});}
            var Q225;
            Q225=makeQuery(id+"F0Hq7nSFAMYVZvY_4.8.F20.opExtrude","SWEPT_FACE",FACE,{"disambiguationData":[OSD([sQuery(id+"F19.wireOp",EDGE,"E157")])]});
            var Q226;
            Q226=makeQuery(id+"F0Hq7nSFAMYVZvY_4.8.F20.opExtrude","SWEPT_FACE",FACE,{"disambiguationData":[OSD([sQuery(id+"F19.wireOp",EDGE,"E158.MirrorCS")])]});
            var Q227;
            Q227=makeQuery(id+"F0Hq7nSFAMYVZvY_4.8.F20.opExtrude","CAP_EDGE",EDGE,{"disambiguationData":[OSD([sQuery(id+"F19.wireOp",EDGE,"E157")])],"isStart":false});
            var Q228;
            Q228=makeQuery(id+"F0Hq7nSFAMYVZvY_4.8.F20.opExtrude","CAP_EDGE",EDGE,{"disambiguationData":[OSD([sQuery(id+"F19.wireOp",EDGE,"E158.MirrorCS")])],"isStart":false});
            var Q229;
            {var subQ0=sQuery(id+"F16.wireOp",EDGE,"E151");var subQ2=sQuery(id+"F16.wireOp",EDGE,"E152");var subQ4=sQuery(id+"F19.wireOp",EDGE,"E158.MirrorCS");var subQ5=makeQuery(id+"F0Hq7nSFAMYVZvY_4.7.F20.opExtrude","SWEPT_FACE",FACE,{"disambiguationData":[OSD([subQ4])]});var subQ6=sQuery(id+"F19.wireOp",EDGE,"E157");var subQ7=makeQuery(id+"F20.opExtrude","SWEPT_FACE",FACE,{"disambiguationData":[OSD([subQ6])]});Q229=makeQuery(id+"F0Hq7nSFAMYVZvY_4.8.F20.boolean.opBoolean","SPLIT",FACE,{"disambiguationData":[TD([subQ5])],"derivedFrom":makeQuery(id+"F0Hq7nSFAMYVZvY_4.7.F20.boolean.opBoolean","SPLIT",FACE,{"disambiguationData":[TD([subQ7])],"derivedFrom":makeQuery(id+"F0Hq7nSFAMYVZvY_4.6.F20.boolean.opBoolean","SPLIT",FACE,{"disambiguationData":[TD([subQ7])],"derivedFrom":makeQuery(id+"F0Hq7nSFAMYVZvY_4.5.F20.boolean.opBoolean","SPLIT",FACE,{"disambiguationData":[TD([subQ7])],"derivedFrom":makeQuery(id+"F0Hq7nSFAMYVZvY_4.4.F20.boolean.opBoolean","SPLIT",FACE,{"disambiguationData":[TD([subQ7])],"derivedFrom":makeQuery(id+"F0Hq7nSFAMYVZvY_4.3.F20.boolean.opBoolean","SPLIT",FACE,{"disambiguationData":[TD([subQ7])],"derivedFrom":makeQuery(id+"F0Hq7nSFAMYVZvY_4.2.F20.boolean.opBoolean","SPLIT",FACE,{"disambiguationData":[TD([subQ7])],"derivedFrom":makeQuery(id+"F0Hq7nSFAMYVZvY_4.1.F20.boolean.opBoolean","SPLIT",FACE,{"disambiguationData":[TD([subQ7])],"derivedFrom":makeQuery(id+"F17.boolean.opBoolean","COPY",FACE,{"derivedFrom":makeQuery(id+"F17.opExtrude","CAP_FACE",FACE,{"disambiguationData":[OSD([subQ0,subQ2])],"isStart":false})})})})})})})})})});}
            var Q230;
            {var subQ0=sQuery(id+"F19.wireOp",EDGE,"E158.MirrorCS");var subQ1=sQuery(id+"F19.wireOp",EDGE,"E157");var subQ3=sQuery(id+"F16.wireOp",EDGE,"E151");var subQ14=makeQuery(id+"F0Hq7nSFAMYVZvY_4.7.F20.opExtrude","SWEPT_FACE",FACE,{"disambiguationData":[OSD([subQ0])]});var subQ15=makeQuery(id+"F20.opExtrude","SWEPT_FACE",FACE,{"disambiguationData":[OSD([subQ1])]});Q230=makeQuery(id+"F0Hq7nSFAMYVZvY_4.8.F20.boolean.opBoolean","SPLIT",FACE,{"disambiguationData":[TD([subQ14])],"derivedFrom":makeQuery(id+"F0Hq7nSFAMYVZvY_4.7.F20.boolean.opBoolean","SPLIT",FACE,{"disambiguationData":[TD([subQ15])],"derivedFrom":makeQuery(id+"F0Hq7nSFAMYVZvY_4.6.F20.boolean.opBoolean","SPLIT",FACE,{"disambiguationData":[TD([subQ15])],"derivedFrom":makeQuery(id+"F0Hq7nSFAMYVZvY_4.5.F20.boolean.opBoolean","SPLIT",FACE,{"disambiguationData":[TD([subQ15])],"derivedFrom":makeQuery(id+"F0Hq7nSFAMYVZvY_4.4.F20.boolean.opBoolean","SPLIT",FACE,{"disambiguationData":[TD([subQ15])],"derivedFrom":makeQuery(id+"F0Hq7nSFAMYVZvY_4.3.F20.boolean.opBoolean","SPLIT",FACE,{"disambiguationData":[TD([subQ15])],"derivedFrom":makeQuery(id+"F0Hq7nSFAMYVZvY_4.2.F20.boolean.opBoolean","SPLIT",FACE,{"disambiguationData":[TD([subQ15])],"derivedFrom":makeQuery(id+"F0Hq7nSFAMYVZvY_4.1.F20.boolean.opBoolean","SPLIT",FACE,{"disambiguationData":[TD([subQ15])],"derivedFrom":makeQuery(id+"F17.boolean.opBoolean","COPY",FACE,{"derivedFrom":makeQuery(id+"F17.opExtrude","SWEPT_FACE",FACE,{"disambiguationData":[OSD([subQ3])]})})})})})})})})})});}
            var Q231;
            Q231=makeQuery(id+"F0Hq7nSFAMYVZvY_4.9.F20.opExtrude","SWEPT_FACE",FACE,{"disambiguationData":[OSD([sQuery(id+"F19.wireOp",EDGE,"E158.MirrorCS")])]});
            var Q232;
            Q232=makeQuery(id+"F0Hq7nSFAMYVZvY_4.9.F20.opExtrude","CAP_EDGE",EDGE,{"disambiguationData":[OSD([sQuery(id+"F19.wireOp",EDGE,"E158.MirrorCS")])],"isStart":false});
            var Q233;
            {var subQ0=sQuery(id+"F16.wireOp",EDGE,"E151");var subQ2=sQuery(id+"F16.wireOp",EDGE,"E152");var subQ4=sQuery(id+"F19.wireOp",EDGE,"E158.MirrorCS");var subQ5=makeQuery(id+"F0Hq7nSFAMYVZvY_4.8.F20.opExtrude","SWEPT_FACE",FACE,{"disambiguationData":[OSD([subQ4])]});var subQ6=sQuery(id+"F19.wireOp",EDGE,"E157");var subQ7=makeQuery(id+"F20.opExtrude","SWEPT_FACE",FACE,{"disambiguationData":[OSD([subQ6])]});Q233=makeQuery(id+"F0Hq7nSFAMYVZvY_4.9.F20.boolean.opBoolean","SPLIT",FACE,{"disambiguationData":[TD([subQ5])],"derivedFrom":makeQuery(id+"F0Hq7nSFAMYVZvY_4.8.F20.boolean.opBoolean","SPLIT",FACE,{"disambiguationData":[TD([subQ7])],"derivedFrom":makeQuery(id+"F0Hq7nSFAMYVZvY_4.7.F20.boolean.opBoolean","SPLIT",FACE,{"disambiguationData":[TD([subQ7])],"derivedFrom":makeQuery(id+"F0Hq7nSFAMYVZvY_4.6.F20.boolean.opBoolean","SPLIT",FACE,{"disambiguationData":[TD([subQ7])],"derivedFrom":makeQuery(id+"F0Hq7nSFAMYVZvY_4.5.F20.boolean.opBoolean","SPLIT",FACE,{"disambiguationData":[TD([subQ7])],"derivedFrom":makeQuery(id+"F0Hq7nSFAMYVZvY_4.4.F20.boolean.opBoolean","SPLIT",FACE,{"disambiguationData":[TD([subQ7])],"derivedFrom":makeQuery(id+"F0Hq7nSFAMYVZvY_4.3.F20.boolean.opBoolean","SPLIT",FACE,{"disambiguationData":[TD([subQ7])],"derivedFrom":makeQuery(id+"F0Hq7nSFAMYVZvY_4.2.F20.boolean.opBoolean","SPLIT",FACE,{"disambiguationData":[TD([subQ7])],"derivedFrom":makeQuery(id+"F0Hq7nSFAMYVZvY_4.1.F20.boolean.opBoolean","SPLIT",FACE,{"disambiguationData":[TD([subQ7])],"derivedFrom":makeQuery(id+"F17.boolean.opBoolean","COPY",FACE,{"derivedFrom":makeQuery(id+"F17.opExtrude","CAP_FACE",FACE,{"disambiguationData":[OSD([subQ0,subQ2])],"isStart":false})})})})})})})})})})});}
            var Q234;
            {var subQ0=sQuery(id+"F19.wireOp",EDGE,"E158.MirrorCS");var subQ1=sQuery(id+"F19.wireOp",EDGE,"E157");var subQ3=sQuery(id+"F16.wireOp",EDGE,"E151");var subQ15=makeQuery(id+"F0Hq7nSFAMYVZvY_4.8.F20.opExtrude","SWEPT_FACE",FACE,{"disambiguationData":[OSD([subQ0])]});var subQ16=makeQuery(id+"F20.opExtrude","SWEPT_FACE",FACE,{"disambiguationData":[OSD([subQ1])]});Q234=makeQuery(id+"F0Hq7nSFAMYVZvY_4.9.F20.boolean.opBoolean","SPLIT",EDGE,{"disambiguationData":[TD([subQ15])],"derivedFrom":makeQuery(id+"F0Hq7nSFAMYVZvY_4.8.F20.boolean.opBoolean","SPLIT",EDGE,{"disambiguationData":[TD([subQ16])],"derivedFrom":makeQuery(id+"F0Hq7nSFAMYVZvY_4.7.F20.boolean.opBoolean","SPLIT",EDGE,{"disambiguationData":[TD([subQ16])],"derivedFrom":makeQuery(id+"F0Hq7nSFAMYVZvY_4.6.F20.boolean.opBoolean","SPLIT",EDGE,{"disambiguationData":[TD([subQ16])],"derivedFrom":makeQuery(id+"F0Hq7nSFAMYVZvY_4.5.F20.boolean.opBoolean","SPLIT",EDGE,{"disambiguationData":[TD([subQ16])],"derivedFrom":makeQuery(id+"F0Hq7nSFAMYVZvY_4.4.F20.boolean.opBoolean","SPLIT",EDGE,{"disambiguationData":[TD([subQ16])],"derivedFrom":makeQuery(id+"F0Hq7nSFAMYVZvY_4.3.F20.boolean.opBoolean","SPLIT",EDGE,{"disambiguationData":[TD([subQ16])],"derivedFrom":makeQuery(id+"F0Hq7nSFAMYVZvY_4.2.F20.boolean.opBoolean","SPLIT",EDGE,{"disambiguationData":[TD([subQ16])],"derivedFrom":makeQuery(id+"F0Hq7nSFAMYVZvY_4.1.F20.boolean.opBoolean","SPLIT",EDGE,{"disambiguationData":[TD([subQ16])],"derivedFrom":makeQuery(id+"F18.boolean.opBoolean","COPY",EDGE,{"derivedFrom":makeQuery(id+"F18.opExtrude","CAP_EDGE",EDGE,{"disambiguationData":[OSD([subQ3])],"isStart":false})})})})})})})})})})});}
            var Q235;
            Q235=makeQuery(id+"F0Hq7nSFAMYVZvY_4.10.F20.opExtrude","SWEPT_FACE",FACE,{"disambiguationData":[OSD([sQuery(id+"F19.wireOp",EDGE,"E158.MirrorCS")])]});
            var Q236;
            Q236=makeQuery(id+"F0Hq7nSFAMYVZvY_4.10.F20.opExtrude","CAP_EDGE",EDGE,{"disambiguationData":[OSD([sQuery(id+"F19.wireOp",EDGE,"E158.MirrorCS")])],"isStart":false});
            var Q237;
            {var subQ0=sQuery(id+"F16.wireOp",EDGE,"E151");var subQ2=sQuery(id+"F19.wireOp",EDGE,"E157");var subQ3=sQuery(id+"F16.wireOp",EDGE,"E152");var subQ5=sQuery(id+"F19.wireOp",EDGE,"E158.MirrorCS");var subQ6=makeQuery(id+"F0Hq7nSFAMYVZvY_4.9.F20.opExtrude","SWEPT_FACE",FACE,{"disambiguationData":[OSD([subQ5])]});var subQ7=makeQuery(id+"F20.opExtrude","SWEPT_FACE",FACE,{"disambiguationData":[OSD([subQ2])]});Q237=makeQuery(id+"F0Hq7nSFAMYVZvY_4.10.F20.boolean.opBoolean","SPLIT",FACE,{"disambiguationData":[TD([subQ6])],"derivedFrom":makeQuery(id+"F0Hq7nSFAMYVZvY_4.9.F20.boolean.opBoolean","SPLIT",FACE,{"disambiguationData":[TD([subQ7])],"derivedFrom":makeQuery(id+"F0Hq7nSFAMYVZvY_4.8.F20.boolean.opBoolean","SPLIT",FACE,{"disambiguationData":[TD([subQ7])],"derivedFrom":makeQuery(id+"F0Hq7nSFAMYVZvY_4.7.F20.boolean.opBoolean","SPLIT",FACE,{"disambiguationData":[TD([subQ7])],"derivedFrom":makeQuery(id+"F0Hq7nSFAMYVZvY_4.6.F20.boolean.opBoolean","SPLIT",FACE,{"disambiguationData":[TD([subQ7])],"derivedFrom":makeQuery(id+"F0Hq7nSFAMYVZvY_4.5.F20.boolean.opBoolean","SPLIT",FACE,{"disambiguationData":[TD([subQ7])],"derivedFrom":makeQuery(id+"F0Hq7nSFAMYVZvY_4.4.F20.boolean.opBoolean","SPLIT",FACE,{"disambiguationData":[TD([subQ7])],"derivedFrom":makeQuery(id+"F0Hq7nSFAMYVZvY_4.3.F20.boolean.opBoolean","SPLIT",FACE,{"disambiguationData":[TD([subQ7])],"derivedFrom":makeQuery(id+"F0Hq7nSFAMYVZvY_4.2.F20.boolean.opBoolean","SPLIT",FACE,{"disambiguationData":[TD([subQ7])],"derivedFrom":makeQuery(id+"F0Hq7nSFAMYVZvY_4.1.F20.boolean.opBoolean","SPLIT",FACE,{"disambiguationData":[TD([subQ7])],"derivedFrom":makeQuery(id+"F17.boolean.opBoolean","COPY",FACE,{"derivedFrom":makeQuery(id+"F17.opExtrude","CAP_FACE",FACE,{"disambiguationData":[OSD([subQ0,subQ3])],"isStart":false})})})})})})})})})})})});}
            var Q238;
            {var subQ0=sQuery(id+"F19.wireOp",EDGE,"E158.MirrorCS");var subQ1=sQuery(id+"F19.wireOp",EDGE,"E157");var subQ3=sQuery(id+"F16.wireOp",EDGE,"E151");var subQ16=makeQuery(id+"F0Hq7nSFAMYVZvY_4.9.F20.opExtrude","SWEPT_FACE",FACE,{"disambiguationData":[OSD([subQ0])]});var subQ17=makeQuery(id+"F20.opExtrude","SWEPT_FACE",FACE,{"disambiguationData":[OSD([subQ1])]});Q238=makeQuery(id+"F0Hq7nSFAMYVZvY_4.10.F20.boolean.opBoolean","SPLIT",EDGE,{"disambiguationData":[TD([subQ16])],"derivedFrom":makeQuery(id+"F0Hq7nSFAMYVZvY_4.9.F20.boolean.opBoolean","SPLIT",EDGE,{"disambiguationData":[TD([subQ17])],"derivedFrom":makeQuery(id+"F0Hq7nSFAMYVZvY_4.8.F20.boolean.opBoolean","SPLIT",EDGE,{"disambiguationData":[TD([subQ17])],"derivedFrom":makeQuery(id+"F0Hq7nSFAMYVZvY_4.7.F20.boolean.opBoolean","SPLIT",EDGE,{"disambiguationData":[TD([subQ17])],"derivedFrom":makeQuery(id+"F0Hq7nSFAMYVZvY_4.6.F20.boolean.opBoolean","SPLIT",EDGE,{"disambiguationData":[TD([subQ17])],"derivedFrom":makeQuery(id+"F0Hq7nSFAMYVZvY_4.5.F20.boolean.opBoolean","SPLIT",EDGE,{"disambiguationData":[TD([subQ17])],"derivedFrom":makeQuery(id+"F0Hq7nSFAMYVZvY_4.4.F20.boolean.opBoolean","SPLIT",EDGE,{"disambiguationData":[TD([subQ17])],"derivedFrom":makeQuery(id+"F0Hq7nSFAMYVZvY_4.3.F20.boolean.opBoolean","SPLIT",EDGE,{"disambiguationData":[TD([subQ17])],"derivedFrom":makeQuery(id+"F0Hq7nSFAMYVZvY_4.2.F20.boolean.opBoolean","SPLIT",EDGE,{"disambiguationData":[TD([subQ17])],"derivedFrom":makeQuery(id+"F0Hq7nSFAMYVZvY_4.1.F20.boolean.opBoolean","SPLIT",EDGE,{"disambiguationData":[TD([subQ17])],"derivedFrom":makeQuery(id+"F18.boolean.opBoolean","COPY",EDGE,{"derivedFrom":makeQuery(id+"F18.opExtrude","CAP_EDGE",EDGE,{"disambiguationData":[OSD([subQ3])],"isStart":false})})})})})})})})})})})});}
            var Q239;
            Q239=makeQuery(id+"F0Hq7nSFAMYVZvY_4.11.F20.opExtrude","SWEPT_FACE",FACE,{"disambiguationData":[OSD([sQuery(id+"F19.wireOp",EDGE,"E158.MirrorCS")])]});
            var Q240;
            Q240=makeQuery(id+"F0Hq7nSFAMYVZvY_4.11.F20.opExtrude","CAP_EDGE",EDGE,{"disambiguationData":[OSD([sQuery(id+"F19.wireOp",EDGE,"E158.MirrorCS")])],"isStart":false});
            var Q241;
            {var subQ0=sQuery(id+"F16.wireOp",EDGE,"E151");var subQ2=sQuery(id+"F16.wireOp",EDGE,"E152");var subQ4=sQuery(id+"F19.wireOp",EDGE,"E157");var subQ5=sQuery(id+"F19.wireOp",EDGE,"E158.MirrorCS");var subQ6=makeQuery(id+"F0Hq7nSFAMYVZvY_4.10.F20.opExtrude","SWEPT_FACE",FACE,{"disambiguationData":[OSD([subQ5])]});var subQ7=makeQuery(id+"F20.opExtrude","SWEPT_FACE",FACE,{"disambiguationData":[OSD([subQ4])]});Q241=makeQuery(id+"F0Hq7nSFAMYVZvY_4.11.F20.boolean.opBoolean","SPLIT",FACE,{"disambiguationData":[TD([subQ6])],"derivedFrom":makeQuery(id+"F0Hq7nSFAMYVZvY_4.10.F20.boolean.opBoolean","SPLIT",FACE,{"disambiguationData":[TD([subQ7])],"derivedFrom":makeQuery(id+"F0Hq7nSFAMYVZvY_4.9.F20.boolean.opBoolean","SPLIT",FACE,{"disambiguationData":[TD([subQ7])],"derivedFrom":makeQuery(id+"F0Hq7nSFAMYVZvY_4.8.F20.boolean.opBoolean","SPLIT",FACE,{"disambiguationData":[TD([subQ7])],"derivedFrom":makeQuery(id+"F0Hq7nSFAMYVZvY_4.7.F20.boolean.opBoolean","SPLIT",FACE,{"disambiguationData":[TD([subQ7])],"derivedFrom":makeQuery(id+"F0Hq7nSFAMYVZvY_4.6.F20.boolean.opBoolean","SPLIT",FACE,{"disambiguationData":[TD([subQ7])],"derivedFrom":makeQuery(id+"F0Hq7nSFAMYVZvY_4.5.F20.boolean.opBoolean","SPLIT",FACE,{"disambiguationData":[TD([subQ7])],"derivedFrom":makeQuery(id+"F0Hq7nSFAMYVZvY_4.4.F20.boolean.opBoolean","SPLIT",FACE,{"disambiguationData":[TD([subQ7])],"derivedFrom":makeQuery(id+"F0Hq7nSFAMYVZvY_4.3.F20.boolean.opBoolean","SPLIT",FACE,{"disambiguationData":[TD([subQ7])],"derivedFrom":makeQuery(id+"F0Hq7nSFAMYVZvY_4.2.F20.boolean.opBoolean","SPLIT",FACE,{"disambiguationData":[TD([subQ7])],"derivedFrom":makeQuery(id+"F0Hq7nSFAMYVZvY_4.1.F20.boolean.opBoolean","SPLIT",FACE,{"disambiguationData":[TD([subQ7])],"derivedFrom":makeQuery(id+"F17.boolean.opBoolean","COPY",FACE,{"derivedFrom":makeQuery(id+"F17.opExtrude","CAP_FACE",FACE,{"disambiguationData":[OSD([subQ0,subQ2])],"isStart":false})})})})})})})})})})})})});}
            var Q242;
            Q242=makeQuery(id+"F0Hq7nSFAMYVZvY_4.12.F20.opExtrude","SWEPT_FACE",FACE,{"disambiguationData":[OSD([sQuery(id+"F19.wireOp",EDGE,"E157")])]});
            var Q243;
            Q243=makeQuery(id+"F0Hq7nSFAMYVZvY_4.12.F20.opExtrude","SWEPT_FACE",FACE,{"disambiguationData":[OSD([sQuery(id+"F19.wireOp",EDGE,"E158.MirrorCS")])]});
            var Q244;
            Q244=makeQuery(id+"F0Hq7nSFAMYVZvY_4.12.F20.opExtrude","CAP_EDGE",EDGE,{"disambiguationData":[OSD([sQuery(id+"F19.wireOp",EDGE,"E158.MirrorCS")])],"isStart":false});
            var Q245;
            {var subQ0=sQuery(id+"F16.wireOp",EDGE,"E151");var subQ2=sQuery(id+"F19.wireOp",EDGE,"E158.MirrorCS");var subQ3=makeQuery(id+"F0Hq7nSFAMYVZvY_4.11.F20.opExtrude","SWEPT_FACE",FACE,{"disambiguationData":[OSD([subQ2])]});var subQ4=sQuery(id+"F16.wireOp",EDGE,"E152");var subQ6=sQuery(id+"F19.wireOp",EDGE,"E157");var subQ7=makeQuery(id+"F20.opExtrude","SWEPT_FACE",FACE,{"disambiguationData":[OSD([subQ6])]});Q245=makeQuery(id+"F0Hq7nSFAMYVZvY_4.12.F20.boolean.opBoolean","SPLIT",FACE,{"disambiguationData":[TD([subQ3])],"derivedFrom":makeQuery(id+"F0Hq7nSFAMYVZvY_4.11.F20.boolean.opBoolean","SPLIT",FACE,{"disambiguationData":[TD([subQ7])],"derivedFrom":makeQuery(id+"F0Hq7nSFAMYVZvY_4.10.F20.boolean.opBoolean","SPLIT",FACE,{"disambiguationData":[TD([subQ7])],"derivedFrom":makeQuery(id+"F0Hq7nSFAMYVZvY_4.9.F20.boolean.opBoolean","SPLIT",FACE,{"disambiguationData":[TD([subQ7])],"derivedFrom":makeQuery(id+"F0Hq7nSFAMYVZvY_4.8.F20.boolean.opBoolean","SPLIT",FACE,{"disambiguationData":[TD([subQ7])],"derivedFrom":makeQuery(id+"F0Hq7nSFAMYVZvY_4.7.F20.boolean.opBoolean","SPLIT",FACE,{"disambiguationData":[TD([subQ7])],"derivedFrom":makeQuery(id+"F0Hq7nSFAMYVZvY_4.6.F20.boolean.opBoolean","SPLIT",FACE,{"disambiguationData":[TD([subQ7])],"derivedFrom":makeQuery(id+"F0Hq7nSFAMYVZvY_4.5.F20.boolean.opBoolean","SPLIT",FACE,{"disambiguationData":[TD([subQ7])],"derivedFrom":makeQuery(id+"F0Hq7nSFAMYVZvY_4.4.F20.boolean.opBoolean","SPLIT",FACE,{"disambiguationData":[TD([subQ7])],"derivedFrom":makeQuery(id+"F0Hq7nSFAMYVZvY_4.3.F20.boolean.opBoolean","SPLIT",FACE,{"disambiguationData":[TD([subQ7])],"derivedFrom":makeQuery(id+"F0Hq7nSFAMYVZvY_4.2.F20.boolean.opBoolean","SPLIT",FACE,{"disambiguationData":[TD([subQ7])],"derivedFrom":makeQuery(id+"F0Hq7nSFAMYVZvY_4.1.F20.boolean.opBoolean","SPLIT",FACE,{"disambiguationData":[TD([subQ7])],"derivedFrom":makeQuery(id+"F17.boolean.opBoolean","COPY",FACE,{"derivedFrom":makeQuery(id+"F17.opExtrude","CAP_FACE",FACE,{"disambiguationData":[OSD([subQ0,subQ4])],"isStart":false})})})})})})})})})})})})})});}
            var Q246;
            Q246=makeQuery(id+"F0Hq7nSFAMYVZvY_4.13.F20.opExtrude","SWEPT_FACE",FACE,{"disambiguationData":[OSD([sQuery(id+"F19.wireOp",EDGE,"E157")])]});
            var Q247;
            Q247=makeQuery(id+"F0Hq7nSFAMYVZvY_4.13.F20.opExtrude","SWEPT_FACE",FACE,{"disambiguationData":[OSD([sQuery(id+"F19.wireOp",EDGE,"E158.MirrorCS")])]});
            var Q248;
            Q248=makeQuery(id+"F0Hq7nSFAMYVZvY_4.13.F20.opExtrude","CAP_EDGE",EDGE,{"disambiguationData":[OSD([sQuery(id+"F19.wireOp",EDGE,"E157")])],"isStart":false});
            var Q249;
            Q249=makeQuery(id+"F0Hq7nSFAMYVZvY_4.13.F20.opExtrude","CAP_EDGE",EDGE,{"disambiguationData":[OSD([sQuery(id+"F19.wireOp",EDGE,"E158.MirrorCS")])],"isStart":false});
            var Q250;
            Q250=makeQuery(id+"F1.opRevolve","SWEPT_EDGE",EDGE,{"disambiguationData":[OSD([sQuery(id+"F0.wireOp",EDGE,"E103"),sQuery(id+"F0.wireOp",EDGE,"E106.filletArc")])]});
            var Q251;
            Q251=makeQuery(id+"F1.opRevolve","SWEPT_EDGE",EDGE,{"disambiguationData":[OSD([sQuery(id+"F0.wireOp",EDGE,"E103"),sQuery(id+"F0.wireOp",EDGE,"E107.filletArc")])]});
            var Q252;
            Q252=makeQuery(id+"F1.opRevolve","SWEPT_EDGE",EDGE,{"disambiguationData":[OSD([sQuery(id+"F0.wireOp",EDGE,"E101"),sQuery(id+"F0.wireOp",EDGE,"E107.filletArc")])]});
            var Q253;
            Q253=makeQuery(id+"F1.opRevolve","SWEPT_FACE",FACE,{"disambiguationData":[OSD([sQuery(id+"F0.wireOp",EDGE,"E103")])]});
            var Q254;
            Q254=makeQuery(id+"F1.opRevolve","SWEPT_FACE",FACE,{"disambiguationData":[OSD([sQuery(id+"F0.wireOp",EDGE,"E101")])]});
            var Q255;
            Q255=makeQuery(id+"F0Hq7nSFAMYVZvY_4.18.F20.opExtrude","SWEPT_EDGE",EDGE,{"disambiguationData":[OSD([sQuery(id+"F16.wireOp",EDGE,"E151"),sQuery(id+"F19.wireOp",EDGE,"E157")])]});
            var Q256;
            Q256=makeQuery(id+"F0Hq7nSFAMYVZvY_4.18.F20.opExtrude","CAP_EDGE",EDGE,{"disambiguationData":[OSD([sQuery(id+"F19.wireOp",EDGE,"E157")])],"isStart":true});
            var Q257;
            Q257=makeQuery(id+"F0Hq7nSFAMYVZvY_4.18.F20.opExtrude","CAP_EDGE",EDGE,{"disambiguationData":[OSD([sQuery(id+"F19.wireOp",EDGE,"E158.MirrorCS")])],"isStart":true});
            var Q258;
            Q258=makeQuery(id+"F0Hq7nSFAMYVZvY_4.18.F20.opExtrude","SWEPT_EDGE",EDGE,{"disambiguationData":[OSD([sQuery(id+"F16.wireOp",EDGE,"E151"),sQuery(id+"F19.wireOp",EDGE,"E158.MirrorCS")])]});
            var Q259;
            Q259=makeQuery(id+"F20.opExtrude","SWEPT_EDGE",EDGE,{"disambiguationData":[OSD([sQuery(id+"F16.wireOp",EDGE,"E151"),sQuery(id+"F19.wireOp",EDGE,"E157")])]});
            var Q260;
            Q260=makeQuery(id+"F20.opExtrude","CAP_EDGE",EDGE,{"disambiguationData":[OSD([sQuery(id+"F19.wireOp",EDGE,"E157")])],"isStart":false});
            var Q261;
            Q261=makeQuery(id+"F20.opExtrude","CAP_EDGE",EDGE,{"disambiguationData":[OSD([sQuery(id+"F19.wireOp",EDGE,"E157")])],"isStart":true});
            var Q262;
            Q262=makeQuery(id+"F0Hq7nSFAMYVZvY_4.13.F20.opExtrude","SWEPT_EDGE",EDGE,{"disambiguationData":[OSD([sQuery(id+"F16.wireOp",EDGE,"E151"),sQuery(id+"F19.wireOp",EDGE,"E158.MirrorCS")])]});
            var Q263;
            Q263=makeQuery(id+"F0Hq7nSFAMYVZvY_4.13.F20.opExtrude","SWEPT_EDGE",EDGE,{"disambiguationData":[OSD([sQuery(id+"F16.wireOp",EDGE,"E151"),sQuery(id+"F19.wireOp",EDGE,"E157")])]});
            var Q264;
            Q264=makeQuery(id+"F0Hq7nSFAMYVZvY_4.19.F20.opExtrude","CAP_EDGE",EDGE,{"disambiguationData":[OSD([sQuery(id+"F19.wireOp",EDGE,"E157")])],"isStart":false});
            var Q265;
            Q265=makeQuery(id+"F0Hq7nSFAMYVZvY_4.13.F20.opExtrude","CAP_EDGE",EDGE,{"disambiguationData":[OSD([sQuery(id+"F19.wireOp",EDGE,"E157")])],"isStart":true});
            var Q266;
            Q266=makeQuery(id+"F20.opExtrude","SWEPT_EDGE",EDGE,{"disambiguationData":[OSD([sQuery(id+"F16.wireOp",EDGE,"E151"),sQuery(id+"F19.wireOp",EDGE,"E158.MirrorCS")])]});
            var Q267;
            Q267=makeQuery(id+"F0Hq7nSFAMYVZvY_4.14.F20.opExtrude","SWEPT_EDGE",EDGE,{"disambiguationData":[OSD([sQuery(id+"F16.wireOp",EDGE,"E151"),sQuery(id+"F19.wireOp",EDGE,"E158.MirrorCS")])]});
            var Q268;
            Q268=makeQuery(id+"F0Hq7nSFAMYVZvY_4.13.F20.opExtrude","CAP_EDGE",EDGE,{"disambiguationData":[OSD([sQuery(id+"F19.wireOp",EDGE,"E158.MirrorCS")])],"isStart":true});
            var Q269;
            Q269=makeQuery(id+"F20.opExtrude","CAP_EDGE",EDGE,{"disambiguationData":[OSD([sQuery(id+"F19.wireOp",EDGE,"E158.MirrorCS")])],"isStart":true});
            var Q270;
            Q270=makeQuery(id+"F0Hq7nSFAMYVZvY_4.16.F20.opExtrude","SWEPT_EDGE",EDGE,{"disambiguationData":[OSD([sQuery(id+"F16.wireOp",EDGE,"E151"),sQuery(id+"F19.wireOp",EDGE,"E158.MirrorCS")])]});
            var Q271;
            Q271=makeQuery(id+"F0Hq7nSFAMYVZvY_4.14.F20.opExtrude","SWEPT_EDGE",EDGE,{"disambiguationData":[OSD([sQuery(id+"F16.wireOp",EDGE,"E151"),sQuery(id+"F19.wireOp",EDGE,"E157")])]});
            var Q272;
            Q272=makeQuery(id+"F0Hq7nSFAMYVZvY_4.17.F20.opExtrude","CAP_EDGE",EDGE,{"disambiguationData":[OSD([sQuery(id+"F19.wireOp",EDGE,"E157")])],"isStart":true});
            var Q273;
            Q273=makeQuery(id+"F0Hq7nSFAMYVZvY_4.17.F20.opExtrude","SWEPT_EDGE",EDGE,{"disambiguationData":[OSD([sQuery(id+"F16.wireOp",EDGE,"E151"),sQuery(id+"F19.wireOp",EDGE,"E157")])]});
            var Q274;
            Q274=makeQuery(id+"F0Hq7nSFAMYVZvY_4.17.F20.opExtrude","SWEPT_EDGE",EDGE,{"disambiguationData":[OSD([sQuery(id+"F16.wireOp",EDGE,"E151"),sQuery(id+"F19.wireOp",EDGE,"E158.MirrorCS")])]});
            var Q275;
            Q275=makeQuery(id+"F0Hq7nSFAMYVZvY_4.15.F20.opExtrude","SWEPT_EDGE",EDGE,{"disambiguationData":[OSD([sQuery(id+"F16.wireOp",EDGE,"E151"),sQuery(id+"F19.wireOp",EDGE,"E158.MirrorCS")])]});
            var Q276;
            {var subQ0=sQuery(id+"F16.wireOp",EDGE,"E151");var subQ3=sQuery(id+"F19.wireOp",EDGE,"E157");var subQ4=sQuery(id+"F19.wireOp",EDGE,"E158.MirrorCS");var subQ5=makeQuery(id+"F0Hq7nSFAMYVZvY_4.12.F20.opExtrude","SWEPT_FACE",FACE,{"disambiguationData":[OSD([subQ4])]});var subQ6=makeQuery(id+"F20.opExtrude","SWEPT_FACE",FACE,{"disambiguationData":[OSD([subQ3])]});Q276=makeQuery(id+"F0Hq7nSFAMYVZvY_4.13.F20.boolean.opBoolean","SPLIT",EDGE,{"disambiguationData":[TD([subQ5])],"derivedFrom":makeQuery(id+"F0Hq7nSFAMYVZvY_4.12.F20.boolean.opBoolean","SPLIT",EDGE,{"disambiguationData":[TD([subQ6])],"derivedFrom":makeQuery(id+"F0Hq7nSFAMYVZvY_4.11.F20.boolean.opBoolean","SPLIT",EDGE,{"disambiguationData":[TD([subQ6])],"derivedFrom":makeQuery(id+"F0Hq7nSFAMYVZvY_4.10.F20.boolean.opBoolean","SPLIT",EDGE,{"disambiguationData":[TD([subQ6])],"derivedFrom":makeQuery(id+"F0Hq7nSFAMYVZvY_4.9.F20.boolean.opBoolean","SPLIT",EDGE,{"disambiguationData":[TD([subQ6])],"derivedFrom":makeQuery(id+"F0Hq7nSFAMYVZvY_4.8.F20.boolean.opBoolean","SPLIT",EDGE,{"disambiguationData":[TD([subQ6])],"derivedFrom":makeQuery(id+"F0Hq7nSFAMYVZvY_4.7.F20.boolean.opBoolean","SPLIT",EDGE,{"disambiguationData":[TD([subQ6])],"derivedFrom":makeQuery(id+"F0Hq7nSFAMYVZvY_4.6.F20.boolean.opBoolean","SPLIT",EDGE,{"disambiguationData":[TD([subQ6])],"derivedFrom":makeQuery(id+"F0Hq7nSFAMYVZvY_4.5.F20.boolean.opBoolean","SPLIT",EDGE,{"disambiguationData":[TD([subQ6])],"derivedFrom":makeQuery(id+"F0Hq7nSFAMYVZvY_4.4.F20.boolean.opBoolean","SPLIT",EDGE,{"disambiguationData":[TD([subQ6])],"derivedFrom":makeQuery(id+"F0Hq7nSFAMYVZvY_4.3.F20.boolean.opBoolean","SPLIT",EDGE,{"disambiguationData":[TD([subQ6])],"derivedFrom":makeQuery(id+"F0Hq7nSFAMYVZvY_4.2.F20.boolean.opBoolean","SPLIT",EDGE,{"disambiguationData":[TD([subQ6])],"derivedFrom":makeQuery(id+"F0Hq7nSFAMYVZvY_4.1.F20.boolean.opBoolean","SPLIT",EDGE,{"disambiguationData":[TD([subQ6])],"derivedFrom":makeQuery(id+"F17.boolean.opBoolean","COPY",EDGE,{"derivedFrom":makeQuery(id+"F17.opExtrude","CAP_EDGE",EDGE,{"disambiguationData":[OSD([subQ0])],"isStart":false})})})})})})})})})})})})})})});}
            var Q277;
            {var subQ0=sQuery(id+"F19.wireOp",EDGE,"E158.MirrorCS");var subQ1=sQuery(id+"F19.wireOp",EDGE,"E157");var subQ3=sQuery(id+"F16.wireOp",EDGE,"E151");var subQ19=makeQuery(id+"F0Hq7nSFAMYVZvY_4.12.F20.opExtrude","SWEPT_FACE",FACE,{"disambiguationData":[OSD([subQ0])]});var subQ20=makeQuery(id+"F20.opExtrude","SWEPT_FACE",FACE,{"disambiguationData":[OSD([subQ1])]});Q277=makeQuery(id+"F0Hq7nSFAMYVZvY_4.13.F20.boolean.opBoolean","SPLIT",EDGE,{"disambiguationData":[TD([subQ19])],"derivedFrom":makeQuery(id+"F0Hq7nSFAMYVZvY_4.12.F20.boolean.opBoolean","SPLIT",EDGE,{"disambiguationData":[TD([subQ20])],"derivedFrom":makeQuery(id+"F0Hq7nSFAMYVZvY_4.11.F20.boolean.opBoolean","SPLIT",EDGE,{"disambiguationData":[TD([subQ20])],"derivedFrom":makeQuery(id+"F0Hq7nSFAMYVZvY_4.10.F20.boolean.opBoolean","SPLIT",EDGE,{"disambiguationData":[TD([subQ20])],"derivedFrom":makeQuery(id+"F0Hq7nSFAMYVZvY_4.9.F20.boolean.opBoolean","SPLIT",EDGE,{"disambiguationData":[TD([subQ20])],"derivedFrom":makeQuery(id+"F0Hq7nSFAMYVZvY_4.8.F20.boolean.opBoolean","SPLIT",EDGE,{"disambiguationData":[TD([subQ20])],"derivedFrom":makeQuery(id+"F0Hq7nSFAMYVZvY_4.7.F20.boolean.opBoolean","SPLIT",EDGE,{"disambiguationData":[TD([subQ20])],"derivedFrom":makeQuery(id+"F0Hq7nSFAMYVZvY_4.6.F20.boolean.opBoolean","SPLIT",EDGE,{"disambiguationData":[TD([subQ20])],"derivedFrom":makeQuery(id+"F0Hq7nSFAMYVZvY_4.5.F20.boolean.opBoolean","SPLIT",EDGE,{"disambiguationData":[TD([subQ20])],"derivedFrom":makeQuery(id+"F0Hq7nSFAMYVZvY_4.4.F20.boolean.opBoolean","SPLIT",EDGE,{"disambiguationData":[TD([subQ20])],"derivedFrom":makeQuery(id+"F0Hq7nSFAMYVZvY_4.3.F20.boolean.opBoolean","SPLIT",EDGE,{"disambiguationData":[TD([subQ20])],"derivedFrom":makeQuery(id+"F0Hq7nSFAMYVZvY_4.2.F20.boolean.opBoolean","SPLIT",EDGE,{"disambiguationData":[TD([subQ20])],"derivedFrom":makeQuery(id+"F0Hq7nSFAMYVZvY_4.1.F20.boolean.opBoolean","SPLIT",EDGE,{"disambiguationData":[TD([subQ20])],"derivedFrom":makeQuery(id+"F18.boolean.opBoolean","COPY",EDGE,{"derivedFrom":makeQuery(id+"F18.opExtrude","CAP_EDGE",EDGE,{"disambiguationData":[OSD([subQ3])],"isStart":false})})})})})})})})})})})})})})});}
            var Q278;
            Q278=makeQuery(id+"F0Hq7nSFAMYVZvY_4.19.F20.opExtrude","CAP_EDGE",EDGE,{"disambiguationData":[OSD([sQuery(id+"F19.wireOp",EDGE,"E158.MirrorCS")])],"isStart":false});
            var Q279;
            Q279=makeQuery(id+"F0Hq7nSFAMYVZvY_4.14.F20.opExtrude","CAP_EDGE",EDGE,{"disambiguationData":[OSD([sQuery(id+"F19.wireOp",EDGE,"E157")])],"isStart":true});
            var Q280;
            Q280=makeQuery(id+"F0Hq7nSFAMYVZvY_4.17.F20.opExtrude","CAP_EDGE",EDGE,{"disambiguationData":[OSD([sQuery(id+"F19.wireOp",EDGE,"E158.MirrorCS")])],"isStart":true});
            var Q281;
            Q281=makeQuery(id+"F0Hq7nSFAMYVZvY_4.16.F20.opExtrude","SWEPT_EDGE",EDGE,{"disambiguationData":[OSD([sQuery(id+"F16.wireOp",EDGE,"E151"),sQuery(id+"F19.wireOp",EDGE,"E157")])]});
            var Q282;
            Q282=makeQuery(id+"F0Hq7nSFAMYVZvY_4.15.F20.opExtrude","CAP_EDGE",EDGE,{"disambiguationData":[OSD([sQuery(id+"F19.wireOp",EDGE,"E157")])],"isStart":true});
            var Q283;
            Q283=makeQuery(id+"F0Hq7nSFAMYVZvY_4.15.F20.opExtrude","SWEPT_EDGE",EDGE,{"disambiguationData":[OSD([sQuery(id+"F16.wireOp",EDGE,"E151"),sQuery(id+"F19.wireOp",EDGE,"E157")])]});
            var Q284;
            Q284=makeQuery(id+"F0Hq7nSFAMYVZvY_4.16.F20.opExtrude","CAP_EDGE",EDGE,{"disambiguationData":[OSD([sQuery(id+"F19.wireOp",EDGE,"E157")])],"isStart":true});
            var Q285;
            Q285=makeQuery(id+"F0Hq7nSFAMYVZvY_4.19.F20.opExtrude","SWEPT_EDGE",EDGE,{"disambiguationData":[OSD([sQuery(id+"F16.wireOp",EDGE,"E151"),sQuery(id+"F19.wireOp",EDGE,"E157")])]});
            var Q286;
            Q286=makeQuery(id+"F0Hq7nSFAMYVZvY_4.19.F20.opExtrude","CAP_EDGE",EDGE,{"disambiguationData":[OSD([sQuery(id+"F19.wireOp",EDGE,"E157")])],"isStart":true});
            var Q287;
            Q287=makeQuery(id+"F0Hq7nSFAMYVZvY_4.19.F20.opExtrude","CAP_EDGE",EDGE,{"disambiguationData":[OSD([sQuery(id+"F19.wireOp",EDGE,"E158.MirrorCS")])],"isStart":true});
            var Q288;
            Q288=makeQuery(id+"F0Hq7nSFAMYVZvY_4.20.F20.opExtrude","CAP_EDGE",EDGE,{"disambiguationData":[OSD([sQuery(id+"F19.wireOp",EDGE,"E157")])],"isStart":false});
            var Q289;
            Q289=makeQuery(id+"F0Hq7nSFAMYVZvY_4.20.F20.opExtrude","CAP_EDGE",EDGE,{"disambiguationData":[OSD([sQuery(id+"F19.wireOp",EDGE,"E158.MirrorCS")])],"isStart":false});
            var Q290;
            Q290=makeQuery(id+"F0Hq7nSFAMYVZvY_4.20.F20.opExtrude","SWEPT_EDGE",EDGE,{"disambiguationData":[OSD([sQuery(id+"F16.wireOp",EDGE,"E151"),sQuery(id+"F19.wireOp",EDGE,"E158.MirrorCS")])]});
            var Q291;
            Q291=makeQuery(id+"F0Hq7nSFAMYVZvY_4.20.F20.opExtrude","CAP_EDGE",EDGE,{"disambiguationData":[OSD([sQuery(id+"F19.wireOp",EDGE,"E157")])],"isStart":true});
            var Q292;
            Q292=makeQuery(id+"F0Hq7nSFAMYVZvY_4.21.F20.opExtrude","CAP_EDGE",EDGE,{"disambiguationData":[OSD([sQuery(id+"F19.wireOp",EDGE,"E157")])],"isStart":false});
            var Q293;
            Q293=makeQuery(id+"F0Hq7nSFAMYVZvY_4.21.F20.opExtrude","SWEPT_EDGE",EDGE,{"disambiguationData":[OSD([sQuery(id+"F16.wireOp",EDGE,"E151"),sQuery(id+"F19.wireOp",EDGE,"E157")])]});
            var Q294;
            Q294=makeQuery(id+"F0Hq7nSFAMYVZvY_4.21.F20.opExtrude","SWEPT_EDGE",EDGE,{"disambiguationData":[OSD([sQuery(id+"F16.wireOp",EDGE,"E151"),sQuery(id+"F19.wireOp",EDGE,"E158.MirrorCS")])]});
            var Q295;
            Q295=makeQuery(id+"F0Hq7nSFAMYVZvY_4.21.F20.opExtrude","CAP_EDGE",EDGE,{"disambiguationData":[OSD([sQuery(id+"F19.wireOp",EDGE,"E157")])],"isStart":true});
            var Q296;
            Q296=makeQuery(id+"F0Hq7nSFAMYVZvY_4.21.F20.opExtrude","CAP_EDGE",EDGE,{"disambiguationData":[OSD([sQuery(id+"F19.wireOp",EDGE,"E158.MirrorCS")])],"isStart":true});
            var Q297;
            {var subQ0=sQuery(id+"F19.wireOp",EDGE,"E158.MirrorCS");var subQ1=sQuery(id+"F19.wireOp",EDGE,"E157");var subQ3=sQuery(id+"F16.wireOp",EDGE,"E151");var subQ20=makeQuery(id+"F0Hq7nSFAMYVZvY_4.20.F20.opExtrude","SWEPT_FACE",FACE,{"disambiguationData":[OSD([subQ0])]});var subQ28=makeQuery(id+"F20.opExtrude","SWEPT_FACE",FACE,{"disambiguationData":[OSD([subQ1])]});Q297=makeQuery(id+"F0Hq7nSFAMYVZvY_4.21.F20.boolean.opBoolean","SPLIT",EDGE,{"disambiguationData":[TD([subQ20])],"derivedFrom":makeQuery(id+"F0Hq7nSFAMYVZvY_4.20.F20.boolean.opBoolean","SPLIT",EDGE,{"disambiguationData":[TD([subQ28])],"derivedFrom":makeQuery(id+"F0Hq7nSFAMYVZvY_4.19.F20.boolean.opBoolean","SPLIT",EDGE,{"disambiguationData":[TD([subQ28])],"derivedFrom":makeQuery(id+"F0Hq7nSFAMYVZvY_4.18.F20.boolean.opBoolean","SPLIT",EDGE,{"disambiguationData":[TD([subQ28])],"derivedFrom":makeQuery(id+"F0Hq7nSFAMYVZvY_4.17.F20.boolean.opBoolean","SPLIT",EDGE,{"disambiguationData":[TD([subQ28])],"derivedFrom":makeQuery(id+"F0Hq7nSFAMYVZvY_4.16.F20.boolean.opBoolean","SPLIT",EDGE,{"disambiguationData":[TD([subQ28])],"derivedFrom":makeQuery(id+"F0Hq7nSFAMYVZvY_4.15.F20.boolean.opBoolean","SPLIT",EDGE,{"disambiguationData":[TD([subQ28])],"derivedFrom":makeQuery(id+"F0Hq7nSFAMYVZvY_4.14.F20.boolean.opBoolean","SPLIT",EDGE,{"disambiguationData":[TD([subQ28])],"derivedFrom":makeQuery(id+"F0Hq7nSFAMYVZvY_4.13.F20.boolean.opBoolean","SPLIT",EDGE,{"disambiguationData":[TD([subQ28])],"derivedFrom":makeQuery(id+"F0Hq7nSFAMYVZvY_4.12.F20.boolean.opBoolean","SPLIT",EDGE,{"disambiguationData":[TD([subQ28])],"derivedFrom":makeQuery(id+"F0Hq7nSFAMYVZvY_4.11.F20.boolean.opBoolean","SPLIT",EDGE,{"disambiguationData":[TD([subQ28])],"derivedFrom":makeQuery(id+"F0Hq7nSFAMYVZvY_4.10.F20.boolean.opBoolean","SPLIT",EDGE,{"disambiguationData":[TD([subQ28])],"derivedFrom":makeQuery(id+"F0Hq7nSFAMYVZvY_4.9.F20.boolean.opBoolean","SPLIT",EDGE,{"disambiguationData":[TD([subQ28])],"derivedFrom":makeQuery(id+"F0Hq7nSFAMYVZvY_4.8.F20.boolean.opBoolean","SPLIT",EDGE,{"disambiguationData":[TD([subQ28])],"derivedFrom":makeQuery(id+"F0Hq7nSFAMYVZvY_4.7.F20.boolean.opBoolean","SPLIT",EDGE,{"disambiguationData":[TD([subQ28])],"derivedFrom":makeQuery(id+"F0Hq7nSFAMYVZvY_4.6.F20.boolean.opBoolean","SPLIT",EDGE,{"disambiguationData":[TD([subQ28])],"derivedFrom":makeQuery(id+"F0Hq7nSFAMYVZvY_4.5.F20.boolean.opBoolean","SPLIT",EDGE,{"disambiguationData":[TD([subQ28])],"derivedFrom":makeQuery(id+"F0Hq7nSFAMYVZvY_4.4.F20.boolean.opBoolean","SPLIT",EDGE,{"disambiguationData":[TD([subQ28])],"derivedFrom":makeQuery(id+"F0Hq7nSFAMYVZvY_4.3.F20.boolean.opBoolean","SPLIT",EDGE,{"disambiguationData":[TD([subQ28])],"derivedFrom":makeQuery(id+"F0Hq7nSFAMYVZvY_4.2.F20.boolean.opBoolean","SPLIT",EDGE,{"disambiguationData":[TD([subQ28])],"derivedFrom":makeQuery(id+"F0Hq7nSFAMYVZvY_4.1.F20.boolean.opBoolean","SPLIT",EDGE,{"disambiguationData":[TD([subQ28])],"derivedFrom":makeQuery(id+"F18.boolean.opBoolean","COPY",EDGE,{"derivedFrom":makeQuery(id+"F18.opExtrude","CAP_EDGE",EDGE,{"disambiguationData":[OSD([subQ3])],"isStart":false})})})})})})})})})})})})})})})})})})})})})})});}
            var Q298;
            Q298=makeQuery(id+"F0Hq7nSFAMYVZvY_4.22.F20.opExtrude","SWEPT_FACE",FACE,{"disambiguationData":[OSD([sQuery(id+"F19.wireOp",EDGE,"E158.MirrorCS")])]});
            var Q299;
            Q299=makeQuery(id+"F0Hq7nSFAMYVZvY_4.22.F20.opExtrude","CAP_EDGE",EDGE,{"disambiguationData":[OSD([sQuery(id+"F19.wireOp",EDGE,"E157")])],"isStart":false});
            var Q300;
            Q300=makeQuery(id+"F0Hq7nSFAMYVZvY_4.22.F20.opExtrude","SWEPT_EDGE",EDGE,{"disambiguationData":[OSD([sQuery(id+"F16.wireOp",EDGE,"E151"),sQuery(id+"F19.wireOp",EDGE,"E157")])]});
            var Q301;
            Q301=makeQuery(id+"F0Hq7nSFAMYVZvY_4.22.F20.opExtrude","SWEPT_EDGE",EDGE,{"disambiguationData":[OSD([sQuery(id+"F16.wireOp",EDGE,"E151"),sQuery(id+"F19.wireOp",EDGE,"E158.MirrorCS")])]});
            var Q302;
            Q302=makeQuery(id+"F0Hq7nSFAMYVZvY_4.22.F20.opExtrude","CAP_EDGE",EDGE,{"disambiguationData":[OSD([sQuery(id+"F19.wireOp",EDGE,"E157")])],"isStart":true});
            var Q303;
            Q303=makeQuery(id+"F0Hq7nSFAMYVZvY_4.22.F20.opExtrude","CAP_EDGE",EDGE,{"disambiguationData":[OSD([sQuery(id+"F19.wireOp",EDGE,"E158.MirrorCS")])],"isStart":true});
            var Q304;
            {var subQ0=sQuery(id+"F19.wireOp",EDGE,"E158.MirrorCS");var subQ1=sQuery(id+"F19.wireOp",EDGE,"E157");var subQ3=sQuery(id+"F16.wireOp",EDGE,"E151");var subQ17=makeQuery(id+"F0Hq7nSFAMYVZvY_4.21.F20.opExtrude","SWEPT_FACE",FACE,{"disambiguationData":[OSD([subQ0])]});var subQ29=makeQuery(id+"F20.opExtrude","SWEPT_FACE",FACE,{"disambiguationData":[OSD([subQ1])]});Q304=makeQuery(id+"F0Hq7nSFAMYVZvY_4.22.F20.boolean.opBoolean","SPLIT",EDGE,{"disambiguationData":[TD([subQ17])],"derivedFrom":makeQuery(id+"F0Hq7nSFAMYVZvY_4.21.F20.boolean.opBoolean","SPLIT",EDGE,{"disambiguationData":[TD([subQ29])],"derivedFrom":makeQuery(id+"F0Hq7nSFAMYVZvY_4.20.F20.boolean.opBoolean","SPLIT",EDGE,{"disambiguationData":[TD([subQ29])],"derivedFrom":makeQuery(id+"F0Hq7nSFAMYVZvY_4.19.F20.boolean.opBoolean","SPLIT",EDGE,{"disambiguationData":[TD([subQ29])],"derivedFrom":makeQuery(id+"F0Hq7nSFAMYVZvY_4.18.F20.boolean.opBoolean","SPLIT",EDGE,{"disambiguationData":[TD([subQ29])],"derivedFrom":makeQuery(id+"F0Hq7nSFAMYVZvY_4.17.F20.boolean.opBoolean","SPLIT",EDGE,{"disambiguationData":[TD([subQ29])],"derivedFrom":makeQuery(id+"F0Hq7nSFAMYVZvY_4.16.F20.boolean.opBoolean","SPLIT",EDGE,{"disambiguationData":[TD([subQ29])],"derivedFrom":makeQuery(id+"F0Hq7nSFAMYVZvY_4.15.F20.boolean.opBoolean","SPLIT",EDGE,{"disambiguationData":[TD([subQ29])],"derivedFrom":makeQuery(id+"F0Hq7nSFAMYVZvY_4.14.F20.boolean.opBoolean","SPLIT",EDGE,{"disambiguationData":[TD([subQ29])],"derivedFrom":makeQuery(id+"F0Hq7nSFAMYVZvY_4.13.F20.boolean.opBoolean","SPLIT",EDGE,{"disambiguationData":[TD([subQ29])],"derivedFrom":makeQuery(id+"F0Hq7nSFAMYVZvY_4.12.F20.boolean.opBoolean","SPLIT",EDGE,{"disambiguationData":[TD([subQ29])],"derivedFrom":makeQuery(id+"F0Hq7nSFAMYVZvY_4.11.F20.boolean.opBoolean","SPLIT",EDGE,{"disambiguationData":[TD([subQ29])],"derivedFrom":makeQuery(id+"F0Hq7nSFAMYVZvY_4.10.F20.boolean.opBoolean","SPLIT",EDGE,{"disambiguationData":[TD([subQ29])],"derivedFrom":makeQuery(id+"F0Hq7nSFAMYVZvY_4.9.F20.boolean.opBoolean","SPLIT",EDGE,{"disambiguationData":[TD([subQ29])],"derivedFrom":makeQuery(id+"F0Hq7nSFAMYVZvY_4.8.F20.boolean.opBoolean","SPLIT",EDGE,{"disambiguationData":[TD([subQ29])],"derivedFrom":makeQuery(id+"F0Hq7nSFAMYVZvY_4.7.F20.boolean.opBoolean","SPLIT",EDGE,{"disambiguationData":[TD([subQ29])],"derivedFrom":makeQuery(id+"F0Hq7nSFAMYVZvY_4.6.F20.boolean.opBoolean","SPLIT",EDGE,{"disambiguationData":[TD([subQ29])],"derivedFrom":makeQuery(id+"F0Hq7nSFAMYVZvY_4.5.F20.boolean.opBoolean","SPLIT",EDGE,{"disambiguationData":[TD([subQ29])],"derivedFrom":makeQuery(id+"F0Hq7nSFAMYVZvY_4.4.F20.boolean.opBoolean","SPLIT",EDGE,{"disambiguationData":[TD([subQ29])],"derivedFrom":makeQuery(id+"F0Hq7nSFAMYVZvY_4.3.F20.boolean.opBoolean","SPLIT",EDGE,{"disambiguationData":[TD([subQ29])],"derivedFrom":makeQuery(id+"F0Hq7nSFAMYVZvY_4.2.F20.boolean.opBoolean","SPLIT",EDGE,{"disambiguationData":[TD([subQ29])],"derivedFrom":makeQuery(id+"F0Hq7nSFAMYVZvY_4.1.F20.boolean.opBoolean","SPLIT",EDGE,{"disambiguationData":[TD([subQ29])],"derivedFrom":makeQuery(id+"F18.boolean.opBoolean","COPY",EDGE,{"derivedFrom":makeQuery(id+"F18.opExtrude","CAP_EDGE",EDGE,{"disambiguationData":[OSD([subQ3])],"isStart":false})})})})})})})})})})})})})})})})})})})})})})})});}
            var Q305;
            Q305=makeQuery(id+"F0Hq7nSFAMYVZvY_4.23.F20.opExtrude","SWEPT_FACE",FACE,{"disambiguationData":[OSD([sQuery(id+"F19.wireOp",EDGE,"E158.MirrorCS")])]});
            var Q306;
            Q306=makeQuery(id+"F0Hq7nSFAMYVZvY_4.23.F20.opExtrude","CAP_EDGE",EDGE,{"disambiguationData":[OSD([sQuery(id+"F19.wireOp",EDGE,"E157")])],"isStart":false});
            var Q307;
            Q307=makeQuery(id+"F0Hq7nSFAMYVZvY_4.23.F20.opExtrude","SWEPT_EDGE",EDGE,{"disambiguationData":[OSD([sQuery(id+"F16.wireOp",EDGE,"E151"),sQuery(id+"F19.wireOp",EDGE,"E157")])]});
            var Q308;
            Q308=makeQuery(id+"F0Hq7nSFAMYVZvY_4.23.F20.opExtrude","SWEPT_EDGE",EDGE,{"disambiguationData":[OSD([sQuery(id+"F16.wireOp",EDGE,"E151"),sQuery(id+"F19.wireOp",EDGE,"E158.MirrorCS")])]});
            var Q309;
            Q309=makeQuery(id+"F0Hq7nSFAMYVZvY_4.23.F20.opExtrude","CAP_EDGE",EDGE,{"disambiguationData":[OSD([sQuery(id+"F19.wireOp",EDGE,"E157")])],"isStart":true});
            var Q310;
            Q310=makeQuery(id+"F0Hq7nSFAMYVZvY_4.23.F20.opExtrude","CAP_EDGE",EDGE,{"disambiguationData":[OSD([sQuery(id+"F19.wireOp",EDGE,"E158.MirrorCS")])],"isStart":true});
            var Q311;
            {var subQ0=sQuery(id+"F19.wireOp",EDGE,"E158.MirrorCS");var subQ1=sQuery(id+"F19.wireOp",EDGE,"E157");var subQ3=sQuery(id+"F16.wireOp",EDGE,"E151");var subQ29=makeQuery(id+"F0Hq7nSFAMYVZvY_4.22.F20.opExtrude","SWEPT_FACE",FACE,{"disambiguationData":[OSD([subQ0])]});var subQ30=makeQuery(id+"F20.opExtrude","SWEPT_FACE",FACE,{"disambiguationData":[OSD([subQ1])]});Q311=makeQuery(id+"F0Hq7nSFAMYVZvY_4.23.F20.boolean.opBoolean","SPLIT",EDGE,{"disambiguationData":[TD([subQ29])],"derivedFrom":makeQuery(id+"F0Hq7nSFAMYVZvY_4.22.F20.boolean.opBoolean","SPLIT",EDGE,{"disambiguationData":[TD([subQ30])],"derivedFrom":makeQuery(id+"F0Hq7nSFAMYVZvY_4.21.F20.boolean.opBoolean","SPLIT",EDGE,{"disambiguationData":[TD([subQ30])],"derivedFrom":makeQuery(id+"F0Hq7nSFAMYVZvY_4.20.F20.boolean.opBoolean","SPLIT",EDGE,{"disambiguationData":[TD([subQ30])],"derivedFrom":makeQuery(id+"F0Hq7nSFAMYVZvY_4.19.F20.boolean.opBoolean","SPLIT",EDGE,{"disambiguationData":[TD([subQ30])],"derivedFrom":makeQuery(id+"F0Hq7nSFAMYVZvY_4.18.F20.boolean.opBoolean","SPLIT",EDGE,{"disambiguationData":[TD([subQ30])],"derivedFrom":makeQuery(id+"F0Hq7nSFAMYVZvY_4.17.F20.boolean.opBoolean","SPLIT",EDGE,{"disambiguationData":[TD([subQ30])],"derivedFrom":makeQuery(id+"F0Hq7nSFAMYVZvY_4.16.F20.boolean.opBoolean","SPLIT",EDGE,{"disambiguationData":[TD([subQ30])],"derivedFrom":makeQuery(id+"F0Hq7nSFAMYVZvY_4.15.F20.boolean.opBoolean","SPLIT",EDGE,{"disambiguationData":[TD([subQ30])],"derivedFrom":makeQuery(id+"F0Hq7nSFAMYVZvY_4.14.F20.boolean.opBoolean","SPLIT",EDGE,{"disambiguationData":[TD([subQ30])],"derivedFrom":makeQuery(id+"F0Hq7nSFAMYVZvY_4.13.F20.boolean.opBoolean","SPLIT",EDGE,{"disambiguationData":[TD([subQ30])],"derivedFrom":makeQuery(id+"F0Hq7nSFAMYVZvY_4.12.F20.boolean.opBoolean","SPLIT",EDGE,{"disambiguationData":[TD([subQ30])],"derivedFrom":makeQuery(id+"F0Hq7nSFAMYVZvY_4.11.F20.boolean.opBoolean","SPLIT",EDGE,{"disambiguationData":[TD([subQ30])],"derivedFrom":makeQuery(id+"F0Hq7nSFAMYVZvY_4.10.F20.boolean.opBoolean","SPLIT",EDGE,{"disambiguationData":[TD([subQ30])],"derivedFrom":makeQuery(id+"F0Hq7nSFAMYVZvY_4.9.F20.boolean.opBoolean","SPLIT",EDGE,{"disambiguationData":[TD([subQ30])],"derivedFrom":makeQuery(id+"F0Hq7nSFAMYVZvY_4.8.F20.boolean.opBoolean","SPLIT",EDGE,{"disambiguationData":[TD([subQ30])],"derivedFrom":makeQuery(id+"F0Hq7nSFAMYVZvY_4.7.F20.boolean.opBoolean","SPLIT",EDGE,{"disambiguationData":[TD([subQ30])],"derivedFrom":makeQuery(id+"F0Hq7nSFAMYVZvY_4.6.F20.boolean.opBoolean","SPLIT",EDGE,{"disambiguationData":[TD([subQ30])],"derivedFrom":makeQuery(id+"F0Hq7nSFAMYVZvY_4.5.F20.boolean.opBoolean","SPLIT",EDGE,{"disambiguationData":[TD([subQ30])],"derivedFrom":makeQuery(id+"F0Hq7nSFAMYVZvY_4.4.F20.boolean.opBoolean","SPLIT",EDGE,{"disambiguationData":[TD([subQ30])],"derivedFrom":makeQuery(id+"F0Hq7nSFAMYVZvY_4.3.F20.boolean.opBoolean","SPLIT",EDGE,{"disambiguationData":[TD([subQ30])],"derivedFrom":makeQuery(id+"F0Hq7nSFAMYVZvY_4.2.F20.boolean.opBoolean","SPLIT",EDGE,{"disambiguationData":[TD([subQ30])],"derivedFrom":makeQuery(id+"F0Hq7nSFAMYVZvY_4.1.F20.boolean.opBoolean","SPLIT",EDGE,{"disambiguationData":[TD([subQ30])],"derivedFrom":makeQuery(id+"F18.boolean.opBoolean","COPY",EDGE,{"derivedFrom":makeQuery(id+"F18.opExtrude","CAP_EDGE",EDGE,{"disambiguationData":[OSD([subQ3])],"isStart":false})})})})})})})})})})})})})})})})})})})})})})})})});}
            var Q312;
            Q312=makeQuery(id+"F0Hq7nSFAMYVZvY_4.24.F20.opExtrude","SWEPT_EDGE",EDGE,{"disambiguationData":[OSD([sQuery(id+"F16.wireOp",EDGE,"E151"),sQuery(id+"F19.wireOp",EDGE,"E157")])]});
            var Q313;
            Q313=makeQuery(id+"F0Hq7nSFAMYVZvY_4.24.F20.opExtrude","SWEPT_EDGE",EDGE,{"disambiguationData":[OSD([sQuery(id+"F16.wireOp",EDGE,"E151"),sQuery(id+"F19.wireOp",EDGE,"E158.MirrorCS")])]});
            var Q314;
            Q314=makeQuery(id+"F0Hq7nSFAMYVZvY_4.24.F20.opExtrude","CAP_EDGE",EDGE,{"disambiguationData":[OSD([sQuery(id+"F19.wireOp",EDGE,"E158.MirrorCS")])],"isStart":true});
            var Q315;
            Q315=makeQuery(id+"F0Hq7nSFAMYVZvY_4.25.F20.opExtrude","SWEPT_FACE",FACE,{"disambiguationData":[OSD([sQuery(id+"F19.wireOp",EDGE,"E158.MirrorCS")])]});
            var Q316;
            Q316=makeQuery(id+"F0Hq7nSFAMYVZvY_4.25.F20.opExtrude","SWEPT_EDGE",EDGE,{"disambiguationData":[OSD([sQuery(id+"F16.wireOp",EDGE,"E151"),sQuery(id+"F19.wireOp",EDGE,"E157")])]});
            var Q317;
            Q317=makeQuery(id+"F0Hq7nSFAMYVZvY_4.25.F20.opExtrude","SWEPT_EDGE",EDGE,{"disambiguationData":[OSD([sQuery(id+"F16.wireOp",EDGE,"E151"),sQuery(id+"F19.wireOp",EDGE,"E158.MirrorCS")])]});
            var Q318;
            Q318=makeQuery(id+"F0Hq7nSFAMYVZvY_4.25.F20.opExtrude","CAP_EDGE",EDGE,{"disambiguationData":[OSD([sQuery(id+"F19.wireOp",EDGE,"E158.MirrorCS")])],"isStart":true});
            var Q319;
            Q319=makeQuery(id+"F0Hq7nSFAMYVZvY_4.26.F20.opExtrude","SWEPT_EDGE",EDGE,{"disambiguationData":[OSD([sQuery(id+"F16.wireOp",EDGE,"E151"),sQuery(id+"F19.wireOp",EDGE,"E157")])]});
            var Q320;
            Q320=makeQuery(id+"F0Hq7nSFAMYVZvY_4.26.F20.opExtrude","SWEPT_EDGE",EDGE,{"disambiguationData":[OSD([sQuery(id+"F16.wireOp",EDGE,"E151"),sQuery(id+"F19.wireOp",EDGE,"E158.MirrorCS")])]});
            var Q321;
            Q321=makeQuery(id+"F0Hq7nSFAMYVZvY_4.26.F20.opExtrude","CAP_EDGE",EDGE,{"disambiguationData":[OSD([sQuery(id+"F19.wireOp",EDGE,"E158.MirrorCS")])],"isStart":true});
            var Q322;
            {var subQ0=sQuery(id+"F16.wireOp",EDGE,"E151");var subQ3=sQuery(id+"F19.wireOp",EDGE,"E158.MirrorCS");var subQ4=makeQuery(id+"F0Hq7nSFAMYVZvY_4.25.F20.opExtrude","SWEPT_FACE",FACE,{"disambiguationData":[OSD([subQ3])]});var subQ5=sQuery(id+"F19.wireOp",EDGE,"E157");var subQ6=makeQuery(id+"F20.opExtrude","SWEPT_FACE",FACE,{"disambiguationData":[OSD([subQ5])]});Q322=makeQuery(id+"F0Hq7nSFAMYVZvY_4.26.F20.boolean.opBoolean","SPLIT",EDGE,{"disambiguationData":[TD([subQ4])],"derivedFrom":makeQuery(id+"F0Hq7nSFAMYVZvY_4.25.F20.boolean.opBoolean","SPLIT",EDGE,{"disambiguationData":[TD([subQ6])],"derivedFrom":makeQuery(id+"F0Hq7nSFAMYVZvY_4.24.F20.boolean.opBoolean","SPLIT",EDGE,{"disambiguationData":[TD([subQ6])],"derivedFrom":makeQuery(id+"F0Hq7nSFAMYVZvY_4.23.F20.boolean.opBoolean","SPLIT",EDGE,{"disambiguationData":[TD([subQ6])],"derivedFrom":makeQuery(id+"F0Hq7nSFAMYVZvY_4.22.F20.boolean.opBoolean","SPLIT",EDGE,{"disambiguationData":[TD([subQ6])],"derivedFrom":makeQuery(id+"F0Hq7nSFAMYVZvY_4.21.F20.boolean.opBoolean","SPLIT",EDGE,{"disambiguationData":[TD([subQ6])],"derivedFrom":makeQuery(id+"F0Hq7nSFAMYVZvY_4.20.F20.boolean.opBoolean","SPLIT",EDGE,{"disambiguationData":[TD([subQ6])],"derivedFrom":makeQuery(id+"F0Hq7nSFAMYVZvY_4.19.F20.boolean.opBoolean","SPLIT",EDGE,{"disambiguationData":[TD([subQ6])],"derivedFrom":makeQuery(id+"F0Hq7nSFAMYVZvY_4.18.F20.boolean.opBoolean","SPLIT",EDGE,{"disambiguationData":[TD([subQ6])],"derivedFrom":makeQuery(id+"F0Hq7nSFAMYVZvY_4.17.F20.boolean.opBoolean","SPLIT",EDGE,{"disambiguationData":[TD([subQ6])],"derivedFrom":makeQuery(id+"F0Hq7nSFAMYVZvY_4.16.F20.boolean.opBoolean","SPLIT",EDGE,{"disambiguationData":[TD([subQ6])],"derivedFrom":makeQuery(id+"F0Hq7nSFAMYVZvY_4.15.F20.boolean.opBoolean","SPLIT",EDGE,{"disambiguationData":[TD([subQ6])],"derivedFrom":makeQuery(id+"F0Hq7nSFAMYVZvY_4.14.F20.boolean.opBoolean","SPLIT",EDGE,{"disambiguationData":[TD([subQ6])],"derivedFrom":makeQuery(id+"F0Hq7nSFAMYVZvY_4.13.F20.boolean.opBoolean","SPLIT",EDGE,{"disambiguationData":[TD([subQ6])],"derivedFrom":makeQuery(id+"F0Hq7nSFAMYVZvY_4.12.F20.boolean.opBoolean","SPLIT",EDGE,{"disambiguationData":[TD([subQ6])],"derivedFrom":makeQuery(id+"F0Hq7nSFAMYVZvY_4.11.F20.boolean.opBoolean","SPLIT",EDGE,{"disambiguationData":[TD([subQ6])],"derivedFrom":makeQuery(id+"F0Hq7nSFAMYVZvY_4.10.F20.boolean.opBoolean","SPLIT",EDGE,{"disambiguationData":[TD([subQ6])],"derivedFrom":makeQuery(id+"F0Hq7nSFAMYVZvY_4.9.F20.boolean.opBoolean","SPLIT",EDGE,{"disambiguationData":[TD([subQ6])],"derivedFrom":makeQuery(id+"F0Hq7nSFAMYVZvY_4.8.F20.boolean.opBoolean","SPLIT",EDGE,{"disambiguationData":[TD([subQ6])],"derivedFrom":makeQuery(id+"F0Hq7nSFAMYVZvY_4.7.F20.boolean.opBoolean","SPLIT",EDGE,{"disambiguationData":[TD([subQ6])],"derivedFrom":makeQuery(id+"F0Hq7nSFAMYVZvY_4.6.F20.boolean.opBoolean","SPLIT",EDGE,{"disambiguationData":[TD([subQ6])],"derivedFrom":makeQuery(id+"F0Hq7nSFAMYVZvY_4.5.F20.boolean.opBoolean","SPLIT",EDGE,{"disambiguationData":[TD([subQ6])],"derivedFrom":makeQuery(id+"F0Hq7nSFAMYVZvY_4.4.F20.boolean.opBoolean","SPLIT",EDGE,{"disambiguationData":[TD([subQ6])],"derivedFrom":makeQuery(id+"F0Hq7nSFAMYVZvY_4.3.F20.boolean.opBoolean","SPLIT",EDGE,{"disambiguationData":[TD([subQ6])],"derivedFrom":makeQuery(id+"F0Hq7nSFAMYVZvY_4.2.F20.boolean.opBoolean","SPLIT",EDGE,{"disambiguationData":[TD([subQ6])],"derivedFrom":makeQuery(id+"F0Hq7nSFAMYVZvY_4.1.F20.boolean.opBoolean","SPLIT",EDGE,{"disambiguationData":[TD([subQ6])],"derivedFrom":makeQuery(id+"F17.boolean.opBoolean","COPY",EDGE,{"derivedFrom":makeQuery(id+"F17.opExtrude","CAP_EDGE",EDGE,{"disambiguationData":[OSD([subQ0])],"isStart":false})})})})})})})})})})})})})})})})})})})})})})})})})})})});}
            var Q323;
            {var subQ0=sQuery(id+"F19.wireOp",EDGE,"E158.MirrorCS");var subQ1=sQuery(id+"F19.wireOp",EDGE,"E157");var subQ3=sQuery(id+"F16.wireOp",EDGE,"E151");var subQ32=makeQuery(id+"F0Hq7nSFAMYVZvY_4.25.F20.opExtrude","SWEPT_FACE",FACE,{"disambiguationData":[OSD([subQ0])]});var subQ33=makeQuery(id+"F20.opExtrude","SWEPT_FACE",FACE,{"disambiguationData":[OSD([subQ1])]});Q323=makeQuery(id+"F0Hq7nSFAMYVZvY_4.26.F20.boolean.opBoolean","SPLIT",EDGE,{"disambiguationData":[TD([subQ32])],"derivedFrom":makeQuery(id+"F0Hq7nSFAMYVZvY_4.25.F20.boolean.opBoolean","SPLIT",EDGE,{"disambiguationData":[TD([subQ33])],"derivedFrom":makeQuery(id+"F0Hq7nSFAMYVZvY_4.24.F20.boolean.opBoolean","SPLIT",EDGE,{"disambiguationData":[TD([subQ33])],"derivedFrom":makeQuery(id+"F0Hq7nSFAMYVZvY_4.23.F20.boolean.opBoolean","SPLIT",EDGE,{"disambiguationData":[TD([subQ33])],"derivedFrom":makeQuery(id+"F0Hq7nSFAMYVZvY_4.22.F20.boolean.opBoolean","SPLIT",EDGE,{"disambiguationData":[TD([subQ33])],"derivedFrom":makeQuery(id+"F0Hq7nSFAMYVZvY_4.21.F20.boolean.opBoolean","SPLIT",EDGE,{"disambiguationData":[TD([subQ33])],"derivedFrom":makeQuery(id+"F0Hq7nSFAMYVZvY_4.20.F20.boolean.opBoolean","SPLIT",EDGE,{"disambiguationData":[TD([subQ33])],"derivedFrom":makeQuery(id+"F0Hq7nSFAMYVZvY_4.19.F20.boolean.opBoolean","SPLIT",EDGE,{"disambiguationData":[TD([subQ33])],"derivedFrom":makeQuery(id+"F0Hq7nSFAMYVZvY_4.18.F20.boolean.opBoolean","SPLIT",EDGE,{"disambiguationData":[TD([subQ33])],"derivedFrom":makeQuery(id+"F0Hq7nSFAMYVZvY_4.17.F20.boolean.opBoolean","SPLIT",EDGE,{"disambiguationData":[TD([subQ33])],"derivedFrom":makeQuery(id+"F0Hq7nSFAMYVZvY_4.16.F20.boolean.opBoolean","SPLIT",EDGE,{"disambiguationData":[TD([subQ33])],"derivedFrom":makeQuery(id+"F0Hq7nSFAMYVZvY_4.15.F20.boolean.opBoolean","SPLIT",EDGE,{"disambiguationData":[TD([subQ33])],"derivedFrom":makeQuery(id+"F0Hq7nSFAMYVZvY_4.14.F20.boolean.opBoolean","SPLIT",EDGE,{"disambiguationData":[TD([subQ33])],"derivedFrom":makeQuery(id+"F0Hq7nSFAMYVZvY_4.13.F20.boolean.opBoolean","SPLIT",EDGE,{"disambiguationData":[TD([subQ33])],"derivedFrom":makeQuery(id+"F0Hq7nSFAMYVZvY_4.12.F20.boolean.opBoolean","SPLIT",EDGE,{"disambiguationData":[TD([subQ33])],"derivedFrom":makeQuery(id+"F0Hq7nSFAMYVZvY_4.11.F20.boolean.opBoolean","SPLIT",EDGE,{"disambiguationData":[TD([subQ33])],"derivedFrom":makeQuery(id+"F0Hq7nSFAMYVZvY_4.10.F20.boolean.opBoolean","SPLIT",EDGE,{"disambiguationData":[TD([subQ33])],"derivedFrom":makeQuery(id+"F0Hq7nSFAMYVZvY_4.9.F20.boolean.opBoolean","SPLIT",EDGE,{"disambiguationData":[TD([subQ33])],"derivedFrom":makeQuery(id+"F0Hq7nSFAMYVZvY_4.8.F20.boolean.opBoolean","SPLIT",EDGE,{"disambiguationData":[TD([subQ33])],"derivedFrom":makeQuery(id+"F0Hq7nSFAMYVZvY_4.7.F20.boolean.opBoolean","SPLIT",EDGE,{"disambiguationData":[TD([subQ33])],"derivedFrom":makeQuery(id+"F0Hq7nSFAMYVZvY_4.6.F20.boolean.opBoolean","SPLIT",EDGE,{"disambiguationData":[TD([subQ33])],"derivedFrom":makeQuery(id+"F0Hq7nSFAMYVZvY_4.5.F20.boolean.opBoolean","SPLIT",EDGE,{"disambiguationData":[TD([subQ33])],"derivedFrom":makeQuery(id+"F0Hq7nSFAMYVZvY_4.4.F20.boolean.opBoolean","SPLIT",EDGE,{"disambiguationData":[TD([subQ33])],"derivedFrom":makeQuery(id+"F0Hq7nSFAMYVZvY_4.3.F20.boolean.opBoolean","SPLIT",EDGE,{"disambiguationData":[TD([subQ33])],"derivedFrom":makeQuery(id+"F0Hq7nSFAMYVZvY_4.2.F20.boolean.opBoolean","SPLIT",EDGE,{"disambiguationData":[TD([subQ33])],"derivedFrom":makeQuery(id+"F0Hq7nSFAMYVZvY_4.1.F20.boolean.opBoolean","SPLIT",EDGE,{"disambiguationData":[TD([subQ33])],"derivedFrom":makeQuery(id+"F18.boolean.opBoolean","COPY",EDGE,{"derivedFrom":makeQuery(id+"F18.opExtrude","CAP_EDGE",EDGE,{"disambiguationData":[OSD([subQ3])],"isStart":false})})})})})})})})})})})})})})})})})})})})})})})})})})})});}
            var Q324;
            Q324=makeQuery(id+"F0Hq7nSFAMYVZvY_4.27.F20.opExtrude","SWEPT_FACE",FACE,{"disambiguationData":[OSD([sQuery(id+"F19.wireOp",EDGE,"E158.MirrorCS")])]});
            var Q325;
            Q325=makeQuery(id+"F0Hq7nSFAMYVZvY_4.27.F20.opExtrude","SWEPT_EDGE",EDGE,{"disambiguationData":[OSD([sQuery(id+"F16.wireOp",EDGE,"E151"),sQuery(id+"F19.wireOp",EDGE,"E157")])]});
            var Q326;
            Q326=makeQuery(id+"F0Hq7nSFAMYVZvY_4.27.F20.opExtrude","SWEPT_EDGE",EDGE,{"disambiguationData":[OSD([sQuery(id+"F16.wireOp",EDGE,"E151"),sQuery(id+"F19.wireOp",EDGE,"E158.MirrorCS")])]});
            var Q327;
            Q327=makeQuery(id+"F0Hq7nSFAMYVZvY_4.27.F20.opExtrude","CAP_EDGE",EDGE,{"disambiguationData":[OSD([sQuery(id+"F19.wireOp",EDGE,"E158.MirrorCS")])],"isStart":true});
            var Q328;
            {var subQ0=sQuery(id+"F16.wireOp",EDGE,"E151");var subQ2=sQuery(id+"F19.wireOp",EDGE,"E158.MirrorCS");var subQ3=makeQuery(id+"F0Hq7nSFAMYVZvY_4.26.F20.opExtrude","SWEPT_FACE",FACE,{"disambiguationData":[OSD([subQ2])]});var subQ5=sQuery(id+"F19.wireOp",EDGE,"E157");var subQ6=makeQuery(id+"F20.opExtrude","SWEPT_FACE",FACE,{"disambiguationData":[OSD([subQ5])]});Q328=makeQuery(id+"F0Hq7nSFAMYVZvY_4.27.F20.boolean.opBoolean","SPLIT",EDGE,{"disambiguationData":[TD([subQ3])],"derivedFrom":makeQuery(id+"F0Hq7nSFAMYVZvY_4.26.F20.boolean.opBoolean","SPLIT",EDGE,{"disambiguationData":[TD([subQ6])],"derivedFrom":makeQuery(id+"F0Hq7nSFAMYVZvY_4.25.F20.boolean.opBoolean","SPLIT",EDGE,{"disambiguationData":[TD([subQ6])],"derivedFrom":makeQuery(id+"F0Hq7nSFAMYVZvY_4.24.F20.boolean.opBoolean","SPLIT",EDGE,{"disambiguationData":[TD([subQ6])],"derivedFrom":makeQuery(id+"F0Hq7nSFAMYVZvY_4.23.F20.boolean.opBoolean","SPLIT",EDGE,{"disambiguationData":[TD([subQ6])],"derivedFrom":makeQuery(id+"F0Hq7nSFAMYVZvY_4.22.F20.boolean.opBoolean","SPLIT",EDGE,{"disambiguationData":[TD([subQ6])],"derivedFrom":makeQuery(id+"F0Hq7nSFAMYVZvY_4.21.F20.boolean.opBoolean","SPLIT",EDGE,{"disambiguationData":[TD([subQ6])],"derivedFrom":makeQuery(id+"F0Hq7nSFAMYVZvY_4.20.F20.boolean.opBoolean","SPLIT",EDGE,{"disambiguationData":[TD([subQ6])],"derivedFrom":makeQuery(id+"F0Hq7nSFAMYVZvY_4.19.F20.boolean.opBoolean","SPLIT",EDGE,{"disambiguationData":[TD([subQ6])],"derivedFrom":makeQuery(id+"F0Hq7nSFAMYVZvY_4.18.F20.boolean.opBoolean","SPLIT",EDGE,{"disambiguationData":[TD([subQ6])],"derivedFrom":makeQuery(id+"F0Hq7nSFAMYVZvY_4.17.F20.boolean.opBoolean","SPLIT",EDGE,{"disambiguationData":[TD([subQ6])],"derivedFrom":makeQuery(id+"F0Hq7nSFAMYVZvY_4.16.F20.boolean.opBoolean","SPLIT",EDGE,{"disambiguationData":[TD([subQ6])],"derivedFrom":makeQuery(id+"F0Hq7nSFAMYVZvY_4.15.F20.boolean.opBoolean","SPLIT",EDGE,{"disambiguationData":[TD([subQ6])],"derivedFrom":makeQuery(id+"F0Hq7nSFAMYVZvY_4.14.F20.boolean.opBoolean","SPLIT",EDGE,{"disambiguationData":[TD([subQ6])],"derivedFrom":makeQuery(id+"F0Hq7nSFAMYVZvY_4.13.F20.boolean.opBoolean","SPLIT",EDGE,{"disambiguationData":[TD([subQ6])],"derivedFrom":makeQuery(id+"F0Hq7nSFAMYVZvY_4.12.F20.boolean.opBoolean","SPLIT",EDGE,{"disambiguationData":[TD([subQ6])],"derivedFrom":makeQuery(id+"F0Hq7nSFAMYVZvY_4.11.F20.boolean.opBoolean","SPLIT",EDGE,{"disambiguationData":[TD([subQ6])],"derivedFrom":makeQuery(id+"F0Hq7nSFAMYVZvY_4.10.F20.boolean.opBoolean","SPLIT",EDGE,{"disambiguationData":[TD([subQ6])],"derivedFrom":makeQuery(id+"F0Hq7nSFAMYVZvY_4.9.F20.boolean.opBoolean","SPLIT",EDGE,{"disambiguationData":[TD([subQ6])],"derivedFrom":makeQuery(id+"F0Hq7nSFAMYVZvY_4.8.F20.boolean.opBoolean","SPLIT",EDGE,{"disambiguationData":[TD([subQ6])],"derivedFrom":makeQuery(id+"F0Hq7nSFAMYVZvY_4.7.F20.boolean.opBoolean","SPLIT",EDGE,{"disambiguationData":[TD([subQ6])],"derivedFrom":makeQuery(id+"F0Hq7nSFAMYVZvY_4.6.F20.boolean.opBoolean","SPLIT",EDGE,{"disambiguationData":[TD([subQ6])],"derivedFrom":makeQuery(id+"F0Hq7nSFAMYVZvY_4.5.F20.boolean.opBoolean","SPLIT",EDGE,{"disambiguationData":[TD([subQ6])],"derivedFrom":makeQuery(id+"F0Hq7nSFAMYVZvY_4.4.F20.boolean.opBoolean","SPLIT",EDGE,{"disambiguationData":[TD([subQ6])],"derivedFrom":makeQuery(id+"F0Hq7nSFAMYVZvY_4.3.F20.boolean.opBoolean","SPLIT",EDGE,{"disambiguationData":[TD([subQ6])],"derivedFrom":makeQuery(id+"F0Hq7nSFAMYVZvY_4.2.F20.boolean.opBoolean","SPLIT",EDGE,{"disambiguationData":[TD([subQ6])],"derivedFrom":makeQuery(id+"F0Hq7nSFAMYVZvY_4.1.F20.boolean.opBoolean","SPLIT",EDGE,{"disambiguationData":[TD([subQ6])],"derivedFrom":makeQuery(id+"F17.boolean.opBoolean","COPY",EDGE,{"derivedFrom":makeQuery(id+"F17.opExtrude","CAP_EDGE",EDGE,{"disambiguationData":[OSD([subQ0])],"isStart":false})})})})})})})})})})})})})})})})})})})})})})})})})})})})});}
            var Q329;
            {var subQ0=sQuery(id+"F19.wireOp",EDGE,"E158.MirrorCS");var subQ1=sQuery(id+"F19.wireOp",EDGE,"E157");var subQ3=sQuery(id+"F16.wireOp",EDGE,"E151");var subQ33=makeQuery(id+"F0Hq7nSFAMYVZvY_4.26.F20.opExtrude","SWEPT_FACE",FACE,{"disambiguationData":[OSD([subQ0])]});var subQ34=makeQuery(id+"F20.opExtrude","SWEPT_FACE",FACE,{"disambiguationData":[OSD([subQ1])]});Q329=makeQuery(id+"F0Hq7nSFAMYVZvY_4.27.F20.boolean.opBoolean","SPLIT",EDGE,{"disambiguationData":[TD([subQ33])],"derivedFrom":makeQuery(id+"F0Hq7nSFAMYVZvY_4.26.F20.boolean.opBoolean","SPLIT",EDGE,{"disambiguationData":[TD([subQ34])],"derivedFrom":makeQuery(id+"F0Hq7nSFAMYVZvY_4.25.F20.boolean.opBoolean","SPLIT",EDGE,{"disambiguationData":[TD([subQ34])],"derivedFrom":makeQuery(id+"F0Hq7nSFAMYVZvY_4.24.F20.boolean.opBoolean","SPLIT",EDGE,{"disambiguationData":[TD([subQ34])],"derivedFrom":makeQuery(id+"F0Hq7nSFAMYVZvY_4.23.F20.boolean.opBoolean","SPLIT",EDGE,{"disambiguationData":[TD([subQ34])],"derivedFrom":makeQuery(id+"F0Hq7nSFAMYVZvY_4.22.F20.boolean.opBoolean","SPLIT",EDGE,{"disambiguationData":[TD([subQ34])],"derivedFrom":makeQuery(id+"F0Hq7nSFAMYVZvY_4.21.F20.boolean.opBoolean","SPLIT",EDGE,{"disambiguationData":[TD([subQ34])],"derivedFrom":makeQuery(id+"F0Hq7nSFAMYVZvY_4.20.F20.boolean.opBoolean","SPLIT",EDGE,{"disambiguationData":[TD([subQ34])],"derivedFrom":makeQuery(id+"F0Hq7nSFAMYVZvY_4.19.F20.boolean.opBoolean","SPLIT",EDGE,{"disambiguationData":[TD([subQ34])],"derivedFrom":makeQuery(id+"F0Hq7nSFAMYVZvY_4.18.F20.boolean.opBoolean","SPLIT",EDGE,{"disambiguationData":[TD([subQ34])],"derivedFrom":makeQuery(id+"F0Hq7nSFAMYVZvY_4.17.F20.boolean.opBoolean","SPLIT",EDGE,{"disambiguationData":[TD([subQ34])],"derivedFrom":makeQuery(id+"F0Hq7nSFAMYVZvY_4.16.F20.boolean.opBoolean","SPLIT",EDGE,{"disambiguationData":[TD([subQ34])],"derivedFrom":makeQuery(id+"F0Hq7nSFAMYVZvY_4.15.F20.boolean.opBoolean","SPLIT",EDGE,{"disambiguationData":[TD([subQ34])],"derivedFrom":makeQuery(id+"F0Hq7nSFAMYVZvY_4.14.F20.boolean.opBoolean","SPLIT",EDGE,{"disambiguationData":[TD([subQ34])],"derivedFrom":makeQuery(id+"F0Hq7nSFAMYVZvY_4.13.F20.boolean.opBoolean","SPLIT",EDGE,{"disambiguationData":[TD([subQ34])],"derivedFrom":makeQuery(id+"F0Hq7nSFAMYVZvY_4.12.F20.boolean.opBoolean","SPLIT",EDGE,{"disambiguationData":[TD([subQ34])],"derivedFrom":makeQuery(id+"F0Hq7nSFAMYVZvY_4.11.F20.boolean.opBoolean","SPLIT",EDGE,{"disambiguationData":[TD([subQ34])],"derivedFrom":makeQuery(id+"F0Hq7nSFAMYVZvY_4.10.F20.boolean.opBoolean","SPLIT",EDGE,{"disambiguationData":[TD([subQ34])],"derivedFrom":makeQuery(id+"F0Hq7nSFAMYVZvY_4.9.F20.boolean.opBoolean","SPLIT",EDGE,{"disambiguationData":[TD([subQ34])],"derivedFrom":makeQuery(id+"F0Hq7nSFAMYVZvY_4.8.F20.boolean.opBoolean","SPLIT",EDGE,{"disambiguationData":[TD([subQ34])],"derivedFrom":makeQuery(id+"F0Hq7nSFAMYVZvY_4.7.F20.boolean.opBoolean","SPLIT",EDGE,{"disambiguationData":[TD([subQ34])],"derivedFrom":makeQuery(id+"F0Hq7nSFAMYVZvY_4.6.F20.boolean.opBoolean","SPLIT",EDGE,{"disambiguationData":[TD([subQ34])],"derivedFrom":makeQuery(id+"F0Hq7nSFAMYVZvY_4.5.F20.boolean.opBoolean","SPLIT",EDGE,{"disambiguationData":[TD([subQ34])],"derivedFrom":makeQuery(id+"F0Hq7nSFAMYVZvY_4.4.F20.boolean.opBoolean","SPLIT",EDGE,{"disambiguationData":[TD([subQ34])],"derivedFrom":makeQuery(id+"F0Hq7nSFAMYVZvY_4.3.F20.boolean.opBoolean","SPLIT",EDGE,{"disambiguationData":[TD([subQ34])],"derivedFrom":makeQuery(id+"F0Hq7nSFAMYVZvY_4.2.F20.boolean.opBoolean","SPLIT",EDGE,{"disambiguationData":[TD([subQ34])],"derivedFrom":makeQuery(id+"F0Hq7nSFAMYVZvY_4.1.F20.boolean.opBoolean","SPLIT",EDGE,{"disambiguationData":[TD([subQ34])],"derivedFrom":makeQuery(id+"F18.boolean.opBoolean","COPY",EDGE,{"derivedFrom":makeQuery(id+"F18.opExtrude","CAP_EDGE",EDGE,{"disambiguationData":[OSD([subQ3])],"isStart":false})})})})})})})})})})})})})})})})})})})})})})})})})})})})});}
            var Q330;
            Q330=makeQuery(id+"F0Hq7nSFAMYVZvY_4.28.F20.opExtrude","SWEPT_FACE",FACE,{"disambiguationData":[OSD([sQuery(id+"F19.wireOp",EDGE,"E158.MirrorCS")])]});
            var Q331;
            Q331=makeQuery(id+"F0Hq7nSFAMYVZvY_4.28.F20.opExtrude","SWEPT_EDGE",EDGE,{"disambiguationData":[OSD([sQuery(id+"F16.wireOp",EDGE,"E151"),sQuery(id+"F19.wireOp",EDGE,"E157")])]});
            var Q332;
            Q332=makeQuery(id+"F0Hq7nSFAMYVZvY_4.28.F20.opExtrude","SWEPT_EDGE",EDGE,{"disambiguationData":[OSD([sQuery(id+"F16.wireOp",EDGE,"E151"),sQuery(id+"F19.wireOp",EDGE,"E158.MirrorCS")])]});
            var Q333;
            Q333=makeQuery(id+"F0Hq7nSFAMYVZvY_4.28.F20.opExtrude","CAP_EDGE",EDGE,{"disambiguationData":[OSD([sQuery(id+"F19.wireOp",EDGE,"E158.MirrorCS")])],"isStart":true});
            var Q334;
            {var subQ0=sQuery(id+"F16.wireOp",EDGE,"E151");var subQ3=sQuery(id+"F19.wireOp",EDGE,"E157");var subQ4=sQuery(id+"F19.wireOp",EDGE,"E158.MirrorCS");var subQ5=makeQuery(id+"F0Hq7nSFAMYVZvY_4.27.F20.opExtrude","SWEPT_FACE",FACE,{"disambiguationData":[OSD([subQ4])]});var subQ6=makeQuery(id+"F20.opExtrude","SWEPT_FACE",FACE,{"disambiguationData":[OSD([subQ3])]});Q334=makeQuery(id+"F0Hq7nSFAMYVZvY_4.28.F20.boolean.opBoolean","SPLIT",EDGE,{"disambiguationData":[TD([subQ5])],"derivedFrom":makeQuery(id+"F0Hq7nSFAMYVZvY_4.27.F20.boolean.opBoolean","SPLIT",EDGE,{"disambiguationData":[TD([subQ6])],"derivedFrom":makeQuery(id+"F0Hq7nSFAMYVZvY_4.26.F20.boolean.opBoolean","SPLIT",EDGE,{"disambiguationData":[TD([subQ6])],"derivedFrom":makeQuery(id+"F0Hq7nSFAMYVZvY_4.25.F20.boolean.opBoolean","SPLIT",EDGE,{"disambiguationData":[TD([subQ6])],"derivedFrom":makeQuery(id+"F0Hq7nSFAMYVZvY_4.24.F20.boolean.opBoolean","SPLIT",EDGE,{"disambiguationData":[TD([subQ6])],"derivedFrom":makeQuery(id+"F0Hq7nSFAMYVZvY_4.23.F20.boolean.opBoolean","SPLIT",EDGE,{"disambiguationData":[TD([subQ6])],"derivedFrom":makeQuery(id+"F0Hq7nSFAMYVZvY_4.22.F20.boolean.opBoolean","SPLIT",EDGE,{"disambiguationData":[TD([subQ6])],"derivedFrom":makeQuery(id+"F0Hq7nSFAMYVZvY_4.21.F20.boolean.opBoolean","SPLIT",EDGE,{"disambiguationData":[TD([subQ6])],"derivedFrom":makeQuery(id+"F0Hq7nSFAMYVZvY_4.20.F20.boolean.opBoolean","SPLIT",EDGE,{"disambiguationData":[TD([subQ6])],"derivedFrom":makeQuery(id+"F0Hq7nSFAMYVZvY_4.19.F20.boolean.opBoolean","SPLIT",EDGE,{"disambiguationData":[TD([subQ6])],"derivedFrom":makeQuery(id+"F0Hq7nSFAMYVZvY_4.18.F20.boolean.opBoolean","SPLIT",EDGE,{"disambiguationData":[TD([subQ6])],"derivedFrom":makeQuery(id+"F0Hq7nSFAMYVZvY_4.17.F20.boolean.opBoolean","SPLIT",EDGE,{"disambiguationData":[TD([subQ6])],"derivedFrom":makeQuery(id+"F0Hq7nSFAMYVZvY_4.16.F20.boolean.opBoolean","SPLIT",EDGE,{"disambiguationData":[TD([subQ6])],"derivedFrom":makeQuery(id+"F0Hq7nSFAMYVZvY_4.15.F20.boolean.opBoolean","SPLIT",EDGE,{"disambiguationData":[TD([subQ6])],"derivedFrom":makeQuery(id+"F0Hq7nSFAMYVZvY_4.14.F20.boolean.opBoolean","SPLIT",EDGE,{"disambiguationData":[TD([subQ6])],"derivedFrom":makeQuery(id+"F0Hq7nSFAMYVZvY_4.13.F20.boolean.opBoolean","SPLIT",EDGE,{"disambiguationData":[TD([subQ6])],"derivedFrom":makeQuery(id+"F0Hq7nSFAMYVZvY_4.12.F20.boolean.opBoolean","SPLIT",EDGE,{"disambiguationData":[TD([subQ6])],"derivedFrom":makeQuery(id+"F0Hq7nSFAMYVZvY_4.11.F20.boolean.opBoolean","SPLIT",EDGE,{"disambiguationData":[TD([subQ6])],"derivedFrom":makeQuery(id+"F0Hq7nSFAMYVZvY_4.10.F20.boolean.opBoolean","SPLIT",EDGE,{"disambiguationData":[TD([subQ6])],"derivedFrom":makeQuery(id+"F0Hq7nSFAMYVZvY_4.9.F20.boolean.opBoolean","SPLIT",EDGE,{"disambiguationData":[TD([subQ6])],"derivedFrom":makeQuery(id+"F0Hq7nSFAMYVZvY_4.8.F20.boolean.opBoolean","SPLIT",EDGE,{"disambiguationData":[TD([subQ6])],"derivedFrom":makeQuery(id+"F0Hq7nSFAMYVZvY_4.7.F20.boolean.opBoolean","SPLIT",EDGE,{"disambiguationData":[TD([subQ6])],"derivedFrom":makeQuery(id+"F0Hq7nSFAMYVZvY_4.6.F20.boolean.opBoolean","SPLIT",EDGE,{"disambiguationData":[TD([subQ6])],"derivedFrom":makeQuery(id+"F0Hq7nSFAMYVZvY_4.5.F20.boolean.opBoolean","SPLIT",EDGE,{"disambiguationData":[TD([subQ6])],"derivedFrom":makeQuery(id+"F0Hq7nSFAMYVZvY_4.4.F20.boolean.opBoolean","SPLIT",EDGE,{"disambiguationData":[TD([subQ6])],"derivedFrom":makeQuery(id+"F0Hq7nSFAMYVZvY_4.3.F20.boolean.opBoolean","SPLIT",EDGE,{"disambiguationData":[TD([subQ6])],"derivedFrom":makeQuery(id+"F0Hq7nSFAMYVZvY_4.2.F20.boolean.opBoolean","SPLIT",EDGE,{"disambiguationData":[TD([subQ6])],"derivedFrom":makeQuery(id+"F0Hq7nSFAMYVZvY_4.1.F20.boolean.opBoolean","SPLIT",EDGE,{"disambiguationData":[TD([subQ6])],"derivedFrom":makeQuery(id+"F17.boolean.opBoolean","COPY",EDGE,{"derivedFrom":makeQuery(id+"F17.opExtrude","CAP_EDGE",EDGE,{"disambiguationData":[OSD([subQ0])],"isStart":false})})})})})})})})})})})})})})})})})})})})})})})})})})})})})});}
            var Q335;
            {var subQ0=sQuery(id+"F19.wireOp",EDGE,"E158.MirrorCS");var subQ1=sQuery(id+"F19.wireOp",EDGE,"E157");var subQ3=sQuery(id+"F16.wireOp",EDGE,"E151");var subQ34=makeQuery(id+"F0Hq7nSFAMYVZvY_4.27.F20.opExtrude","SWEPT_FACE",FACE,{"disambiguationData":[OSD([subQ0])]});var subQ35=makeQuery(id+"F20.opExtrude","SWEPT_FACE",FACE,{"disambiguationData":[OSD([subQ1])]});Q335=makeQuery(id+"F0Hq7nSFAMYVZvY_4.28.F20.boolean.opBoolean","SPLIT",EDGE,{"disambiguationData":[TD([subQ34])],"derivedFrom":makeQuery(id+"F0Hq7nSFAMYVZvY_4.27.F20.boolean.opBoolean","SPLIT",EDGE,{"disambiguationData":[TD([subQ35])],"derivedFrom":makeQuery(id+"F0Hq7nSFAMYVZvY_4.26.F20.boolean.opBoolean","SPLIT",EDGE,{"disambiguationData":[TD([subQ35])],"derivedFrom":makeQuery(id+"F0Hq7nSFAMYVZvY_4.25.F20.boolean.opBoolean","SPLIT",EDGE,{"disambiguationData":[TD([subQ35])],"derivedFrom":makeQuery(id+"F0Hq7nSFAMYVZvY_4.24.F20.boolean.opBoolean","SPLIT",EDGE,{"disambiguationData":[TD([subQ35])],"derivedFrom":makeQuery(id+"F0Hq7nSFAMYVZvY_4.23.F20.boolean.opBoolean","SPLIT",EDGE,{"disambiguationData":[TD([subQ35])],"derivedFrom":makeQuery(id+"F0Hq7nSFAMYVZvY_4.22.F20.boolean.opBoolean","SPLIT",EDGE,{"disambiguationData":[TD([subQ35])],"derivedFrom":makeQuery(id+"F0Hq7nSFAMYVZvY_4.21.F20.boolean.opBoolean","SPLIT",EDGE,{"disambiguationData":[TD([subQ35])],"derivedFrom":makeQuery(id+"F0Hq7nSFAMYVZvY_4.20.F20.boolean.opBoolean","SPLIT",EDGE,{"disambiguationData":[TD([subQ35])],"derivedFrom":makeQuery(id+"F0Hq7nSFAMYVZvY_4.19.F20.boolean.opBoolean","SPLIT",EDGE,{"disambiguationData":[TD([subQ35])],"derivedFrom":makeQuery(id+"F0Hq7nSFAMYVZvY_4.18.F20.boolean.opBoolean","SPLIT",EDGE,{"disambiguationData":[TD([subQ35])],"derivedFrom":makeQuery(id+"F0Hq7nSFAMYVZvY_4.17.F20.boolean.opBoolean","SPLIT",EDGE,{"disambiguationData":[TD([subQ35])],"derivedFrom":makeQuery(id+"F0Hq7nSFAMYVZvY_4.16.F20.boolean.opBoolean","SPLIT",EDGE,{"disambiguationData":[TD([subQ35])],"derivedFrom":makeQuery(id+"F0Hq7nSFAMYVZvY_4.15.F20.boolean.opBoolean","SPLIT",EDGE,{"disambiguationData":[TD([subQ35])],"derivedFrom":makeQuery(id+"F0Hq7nSFAMYVZvY_4.14.F20.boolean.opBoolean","SPLIT",EDGE,{"disambiguationData":[TD([subQ35])],"derivedFrom":makeQuery(id+"F0Hq7nSFAMYVZvY_4.13.F20.boolean.opBoolean","SPLIT",EDGE,{"disambiguationData":[TD([subQ35])],"derivedFrom":makeQuery(id+"F0Hq7nSFAMYVZvY_4.12.F20.boolean.opBoolean","SPLIT",EDGE,{"disambiguationData":[TD([subQ35])],"derivedFrom":makeQuery(id+"F0Hq7nSFAMYVZvY_4.11.F20.boolean.opBoolean","SPLIT",EDGE,{"disambiguationData":[TD([subQ35])],"derivedFrom":makeQuery(id+"F0Hq7nSFAMYVZvY_4.10.F20.boolean.opBoolean","SPLIT",EDGE,{"disambiguationData":[TD([subQ35])],"derivedFrom":makeQuery(id+"F0Hq7nSFAMYVZvY_4.9.F20.boolean.opBoolean","SPLIT",EDGE,{"disambiguationData":[TD([subQ35])],"derivedFrom":makeQuery(id+"F0Hq7nSFAMYVZvY_4.8.F20.boolean.opBoolean","SPLIT",EDGE,{"disambiguationData":[TD([subQ35])],"derivedFrom":makeQuery(id+"F0Hq7nSFAMYVZvY_4.7.F20.boolean.opBoolean","SPLIT",EDGE,{"disambiguationData":[TD([subQ35])],"derivedFrom":makeQuery(id+"F0Hq7nSFAMYVZvY_4.6.F20.boolean.opBoolean","SPLIT",EDGE,{"disambiguationData":[TD([subQ35])],"derivedFrom":makeQuery(id+"F0Hq7nSFAMYVZvY_4.5.F20.boolean.opBoolean","SPLIT",EDGE,{"disambiguationData":[TD([subQ35])],"derivedFrom":makeQuery(id+"F0Hq7nSFAMYVZvY_4.4.F20.boolean.opBoolean","SPLIT",EDGE,{"disambiguationData":[TD([subQ35])],"derivedFrom":makeQuery(id+"F0Hq7nSFAMYVZvY_4.3.F20.boolean.opBoolean","SPLIT",EDGE,{"disambiguationData":[TD([subQ35])],"derivedFrom":makeQuery(id+"F0Hq7nSFAMYVZvY_4.2.F20.boolean.opBoolean","SPLIT",EDGE,{"disambiguationData":[TD([subQ35])],"derivedFrom":makeQuery(id+"F0Hq7nSFAMYVZvY_4.1.F20.boolean.opBoolean","SPLIT",EDGE,{"disambiguationData":[TD([subQ35])],"derivedFrom":makeQuery(id+"F18.boolean.opBoolean","COPY",EDGE,{"derivedFrom":makeQuery(id+"F18.opExtrude","CAP_EDGE",EDGE,{"disambiguationData":[OSD([subQ3])],"isStart":false})})})})})})})})})})})})})})})})})})})})})})})})})})})})})});}
            var Q336;
            Q336=makeQuery(id+"F0Hq7nSFAMYVZvY_4.29.F20.opExtrude","SWEPT_FACE",FACE,{"disambiguationData":[OSD([sQuery(id+"F19.wireOp",EDGE,"E158.MirrorCS")])]});
            var Q337;
            Q337=makeQuery(id+"F0Hq7nSFAMYVZvY_4.29.F20.opExtrude","CAP_EDGE",EDGE,{"disambiguationData":[OSD([sQuery(id+"F19.wireOp",EDGE,"E157")])],"isStart":false});
            var Q338;
            Q338=makeQuery(id+"F0Hq7nSFAMYVZvY_4.29.F20.opExtrude","CAP_EDGE",EDGE,{"disambiguationData":[OSD([sQuery(id+"F19.wireOp",EDGE,"E158.MirrorCS")])],"isStart":false});
            var Q339;
            Q339=makeQuery(id+"F0Hq7nSFAMYVZvY_4.29.F20.opExtrude","SWEPT_EDGE",EDGE,{"disambiguationData":[OSD([sQuery(id+"F16.wireOp",EDGE,"E151"),sQuery(id+"F19.wireOp",EDGE,"E157")])]});
            var Q340;
            Q340=makeQuery(id+"F0Hq7nSFAMYVZvY_4.29.F20.opExtrude","CAP_EDGE",EDGE,{"disambiguationData":[OSD([sQuery(id+"F19.wireOp",EDGE,"E158.MirrorCS")])],"isStart":true});
            var Q341;
            Q341=makeQuery(id+"F0Hq7nSFAMYVZvY_4.30.F20.opExtrude","SWEPT_FACE",FACE,{"disambiguationData":[OSD([sQuery(id+"F19.wireOp",EDGE,"E158.MirrorCS")])]});
            var Q342;
            Q342=makeQuery(id+"F0Hq7nSFAMYVZvY_4.30.F20.opExtrude","CAP_EDGE",EDGE,{"disambiguationData":[OSD([sQuery(id+"F19.wireOp",EDGE,"E157")])],"isStart":false});
            var Q343;
            Q343=makeQuery(id+"F0Hq7nSFAMYVZvY_4.30.F20.opExtrude","CAP_EDGE",EDGE,{"disambiguationData":[OSD([sQuery(id+"F19.wireOp",EDGE,"E158.MirrorCS")])],"isStart":false});
            var Q344;
            Q344=makeQuery(id+"F0Hq7nSFAMYVZvY_4.30.F20.opExtrude","SWEPT_EDGE",EDGE,{"disambiguationData":[OSD([sQuery(id+"F16.wireOp",EDGE,"E151"),sQuery(id+"F19.wireOp",EDGE,"E157")])]});
            var Q345;
            Q345=makeQuery(id+"F0Hq7nSFAMYVZvY_4.30.F20.opExtrude","CAP_EDGE",EDGE,{"disambiguationData":[OSD([sQuery(id+"F19.wireOp",EDGE,"E157")])],"isStart":true});
            var Q346;
            Q346=makeQuery(id+"F0Hq7nSFAMYVZvY_4.30.F20.opExtrude","CAP_EDGE",EDGE,{"disambiguationData":[OSD([sQuery(id+"F19.wireOp",EDGE,"E158.MirrorCS")])],"isStart":true});
            var Q347;
            Q347=makeQuery(id+"F0Hq7nSFAMYVZvY_4.31.F20.opExtrude","SWEPT_FACE",FACE,{"disambiguationData":[OSD([sQuery(id+"F19.wireOp",EDGE,"E158.MirrorCS")])]});
            var Q348;
            Q348=makeQuery(id+"F0Hq7nSFAMYVZvY_4.31.F20.opExtrude","CAP_EDGE",EDGE,{"disambiguationData":[OSD([sQuery(id+"F19.wireOp",EDGE,"E157")])],"isStart":false});
            var Q349;
            Q349=makeQuery(id+"F0Hq7nSFAMYVZvY_4.31.F20.opExtrude","CAP_EDGE",EDGE,{"disambiguationData":[OSD([sQuery(id+"F19.wireOp",EDGE,"E158.MirrorCS")])],"isStart":false});
            var Q350;
            Q350=makeQuery(id+"F0Hq7nSFAMYVZvY_4.31.F20.opExtrude","SWEPT_EDGE",EDGE,{"disambiguationData":[OSD([sQuery(id+"F16.wireOp",EDGE,"E151"),sQuery(id+"F19.wireOp",EDGE,"E157")])]});
            var Q351;
            Q351=makeQuery(id+"F0Hq7nSFAMYVZvY_4.31.F20.opExtrude","SWEPT_EDGE",EDGE,{"disambiguationData":[OSD([sQuery(id+"F16.wireOp",EDGE,"E151"),sQuery(id+"F19.wireOp",EDGE,"E158.MirrorCS")])]});
            var Q352;
            Q352=makeQuery(id+"F0Hq7nSFAMYVZvY_4.31.F20.opExtrude","CAP_EDGE",EDGE,{"disambiguationData":[OSD([sQuery(id+"F19.wireOp",EDGE,"E157")])],"isStart":true});
            var Q353;
            Q353=makeQuery(id+"F0Hq7nSFAMYVZvY_4.31.F20.opExtrude","CAP_EDGE",EDGE,{"disambiguationData":[OSD([sQuery(id+"F19.wireOp",EDGE,"E158.MirrorCS")])],"isStart":true});
            var Q354;
            {var subQ0=sQuery(id+"F16.wireOp",EDGE,"E151");var subQ3=sQuery(id+"F19.wireOp",EDGE,"E158.MirrorCS");var subQ4=makeQuery(id+"F0Hq7nSFAMYVZvY_4.30.F20.opExtrude","SWEPT_FACE",FACE,{"disambiguationData":[OSD([subQ3])]});var subQ5=sQuery(id+"F19.wireOp",EDGE,"E157");var subQ6=makeQuery(id+"F20.opExtrude","SWEPT_FACE",FACE,{"disambiguationData":[OSD([subQ5])]});Q354=makeQuery(id+"F0Hq7nSFAMYVZvY_4.31.F20.boolean.opBoolean","SPLIT",EDGE,{"disambiguationData":[TD([subQ4])],"derivedFrom":makeQuery(id+"F0Hq7nSFAMYVZvY_4.30.F20.boolean.opBoolean","SPLIT",EDGE,{"disambiguationData":[TD([subQ6])],"derivedFrom":makeQuery(id+"F0Hq7nSFAMYVZvY_4.29.F20.boolean.opBoolean","SPLIT",EDGE,{"disambiguationData":[TD([subQ6])],"derivedFrom":makeQuery(id+"F0Hq7nSFAMYVZvY_4.28.F20.boolean.opBoolean","SPLIT",EDGE,{"disambiguationData":[TD([subQ6])],"derivedFrom":makeQuery(id+"F0Hq7nSFAMYVZvY_4.27.F20.boolean.opBoolean","SPLIT",EDGE,{"disambiguationData":[TD([subQ6])],"derivedFrom":makeQuery(id+"F0Hq7nSFAMYVZvY_4.26.F20.boolean.opBoolean","SPLIT",EDGE,{"disambiguationData":[TD([subQ6])],"derivedFrom":makeQuery(id+"F0Hq7nSFAMYVZvY_4.25.F20.boolean.opBoolean","SPLIT",EDGE,{"disambiguationData":[TD([subQ6])],"derivedFrom":makeQuery(id+"F0Hq7nSFAMYVZvY_4.24.F20.boolean.opBoolean","SPLIT",EDGE,{"disambiguationData":[TD([subQ6])],"derivedFrom":makeQuery(id+"F0Hq7nSFAMYVZvY_4.23.F20.boolean.opBoolean","SPLIT",EDGE,{"disambiguationData":[TD([subQ6])],"derivedFrom":makeQuery(id+"F0Hq7nSFAMYVZvY_4.22.F20.boolean.opBoolean","SPLIT",EDGE,{"disambiguationData":[TD([subQ6])],"derivedFrom":makeQuery(id+"F0Hq7nSFAMYVZvY_4.21.F20.boolean.opBoolean","SPLIT",EDGE,{"disambiguationData":[TD([subQ6])],"derivedFrom":makeQuery(id+"F0Hq7nSFAMYVZvY_4.20.F20.boolean.opBoolean","SPLIT",EDGE,{"disambiguationData":[TD([subQ6])],"derivedFrom":makeQuery(id+"F0Hq7nSFAMYVZvY_4.19.F20.boolean.opBoolean","SPLIT",EDGE,{"disambiguationData":[TD([subQ6])],"derivedFrom":makeQuery(id+"F0Hq7nSFAMYVZvY_4.18.F20.boolean.opBoolean","SPLIT",EDGE,{"disambiguationData":[TD([subQ6])],"derivedFrom":makeQuery(id+"F0Hq7nSFAMYVZvY_4.17.F20.boolean.opBoolean","SPLIT",EDGE,{"disambiguationData":[TD([subQ6])],"derivedFrom":makeQuery(id+"F0Hq7nSFAMYVZvY_4.16.F20.boolean.opBoolean","SPLIT",EDGE,{"disambiguationData":[TD([subQ6])],"derivedFrom":makeQuery(id+"F0Hq7nSFAMYVZvY_4.15.F20.boolean.opBoolean","SPLIT",EDGE,{"disambiguationData":[TD([subQ6])],"derivedFrom":makeQuery(id+"F0Hq7nSFAMYVZvY_4.14.F20.boolean.opBoolean","SPLIT",EDGE,{"disambiguationData":[TD([subQ6])],"derivedFrom":makeQuery(id+"F0Hq7nSFAMYVZvY_4.13.F20.boolean.opBoolean","SPLIT",EDGE,{"disambiguationData":[TD([subQ6])],"derivedFrom":makeQuery(id+"F0Hq7nSFAMYVZvY_4.12.F20.boolean.opBoolean","SPLIT",EDGE,{"disambiguationData":[TD([subQ6])],"derivedFrom":makeQuery(id+"F0Hq7nSFAMYVZvY_4.11.F20.boolean.opBoolean","SPLIT",EDGE,{"disambiguationData":[TD([subQ6])],"derivedFrom":makeQuery(id+"F0Hq7nSFAMYVZvY_4.10.F20.boolean.opBoolean","SPLIT",EDGE,{"disambiguationData":[TD([subQ6])],"derivedFrom":makeQuery(id+"F0Hq7nSFAMYVZvY_4.9.F20.boolean.opBoolean","SPLIT",EDGE,{"disambiguationData":[TD([subQ6])],"derivedFrom":makeQuery(id+"F0Hq7nSFAMYVZvY_4.8.F20.boolean.opBoolean","SPLIT",EDGE,{"disambiguationData":[TD([subQ6])],"derivedFrom":makeQuery(id+"F0Hq7nSFAMYVZvY_4.7.F20.boolean.opBoolean","SPLIT",EDGE,{"disambiguationData":[TD([subQ6])],"derivedFrom":makeQuery(id+"F0Hq7nSFAMYVZvY_4.6.F20.boolean.opBoolean","SPLIT",EDGE,{"disambiguationData":[TD([subQ6])],"derivedFrom":makeQuery(id+"F0Hq7nSFAMYVZvY_4.5.F20.boolean.opBoolean","SPLIT",EDGE,{"disambiguationData":[TD([subQ6])],"derivedFrom":makeQuery(id+"F0Hq7nSFAMYVZvY_4.4.F20.boolean.opBoolean","SPLIT",EDGE,{"disambiguationData":[TD([subQ6])],"derivedFrom":makeQuery(id+"F0Hq7nSFAMYVZvY_4.3.F20.boolean.opBoolean","SPLIT",EDGE,{"disambiguationData":[TD([subQ6])],"derivedFrom":makeQuery(id+"F0Hq7nSFAMYVZvY_4.2.F20.boolean.opBoolean","SPLIT",EDGE,{"disambiguationData":[TD([subQ6])],"derivedFrom":makeQuery(id+"F0Hq7nSFAMYVZvY_4.1.F20.boolean.opBoolean","SPLIT",EDGE,{"disambiguationData":[TD([subQ6])],"derivedFrom":makeQuery(id+"F17.boolean.opBoolean","COPY",EDGE,{"derivedFrom":makeQuery(id+"F17.opExtrude","CAP_EDGE",EDGE,{"disambiguationData":[OSD([subQ0])],"isStart":false})})})})})})})})})})})})})})})})})})})})})})})})})})})})})})})})});}
            var Q355;
            Q355=makeQuery(id+"F0Hq7nSFAMYVZvY_4.32.F20.opExtrude","SWEPT_FACE",FACE,{"disambiguationData":[OSD([sQuery(id+"F19.wireOp",EDGE,"E158.MirrorCS")])]});
            var Q356;
            Q356=makeQuery(id+"F0Hq7nSFAMYVZvY_4.32.F20.opExtrude","CAP_EDGE",EDGE,{"disambiguationData":[OSD([sQuery(id+"F19.wireOp",EDGE,"E157")])],"isStart":false});
            var Q357;
            Q357=makeQuery(id+"F0Hq7nSFAMYVZvY_4.32.F20.opExtrude","CAP_EDGE",EDGE,{"disambiguationData":[OSD([sQuery(id+"F19.wireOp",EDGE,"E158.MirrorCS")])],"isStart":false});
            var Q358;
            Q358=makeQuery(id+"F0Hq7nSFAMYVZvY_4.32.F20.opExtrude","SWEPT_EDGE",EDGE,{"disambiguationData":[OSD([sQuery(id+"F16.wireOp",EDGE,"E151"),sQuery(id+"F19.wireOp",EDGE,"E157")])]});
            var Q359;
            Q359=makeQuery(id+"F0Hq7nSFAMYVZvY_4.32.F20.opExtrude","CAP_EDGE",EDGE,{"disambiguationData":[OSD([sQuery(id+"F19.wireOp",EDGE,"E157")])],"isStart":true});
            var Q360;
            Q360=makeQuery(id+"F0Hq7nSFAMYVZvY_4.32.F20.opExtrude","CAP_EDGE",EDGE,{"disambiguationData":[OSD([sQuery(id+"F19.wireOp",EDGE,"E158.MirrorCS")])],"isStart":true});
            var Q361;
            {var subQ0=sQuery(id+"F16.wireOp",EDGE,"E151");var subQ2=sQuery(id+"F19.wireOp",EDGE,"E158.MirrorCS");var subQ3=makeQuery(id+"F0Hq7nSFAMYVZvY_4.31.F20.opExtrude","SWEPT_FACE",FACE,{"disambiguationData":[OSD([subQ2])]});var subQ5=sQuery(id+"F19.wireOp",EDGE,"E157");var subQ6=makeQuery(id+"F20.opExtrude","SWEPT_FACE",FACE,{"disambiguationData":[OSD([subQ5])]});Q361=makeQuery(id+"F0Hq7nSFAMYVZvY_4.32.F20.boolean.opBoolean","SPLIT",EDGE,{"disambiguationData":[TD([subQ3])],"derivedFrom":makeQuery(id+"F0Hq7nSFAMYVZvY_4.31.F20.boolean.opBoolean","SPLIT",EDGE,{"disambiguationData":[TD([subQ6])],"derivedFrom":makeQuery(id+"F0Hq7nSFAMYVZvY_4.30.F20.boolean.opBoolean","SPLIT",EDGE,{"disambiguationData":[TD([subQ6])],"derivedFrom":makeQuery(id+"F0Hq7nSFAMYVZvY_4.29.F20.boolean.opBoolean","SPLIT",EDGE,{"disambiguationData":[TD([subQ6])],"derivedFrom":makeQuery(id+"F0Hq7nSFAMYVZvY_4.28.F20.boolean.opBoolean","SPLIT",EDGE,{"disambiguationData":[TD([subQ6])],"derivedFrom":makeQuery(id+"F0Hq7nSFAMYVZvY_4.27.F20.boolean.opBoolean","SPLIT",EDGE,{"disambiguationData":[TD([subQ6])],"derivedFrom":makeQuery(id+"F0Hq7nSFAMYVZvY_4.26.F20.boolean.opBoolean","SPLIT",EDGE,{"disambiguationData":[TD([subQ6])],"derivedFrom":makeQuery(id+"F0Hq7nSFAMYVZvY_4.25.F20.boolean.opBoolean","SPLIT",EDGE,{"disambiguationData":[TD([subQ6])],"derivedFrom":makeQuery(id+"F0Hq7nSFAMYVZvY_4.24.F20.boolean.opBoolean","SPLIT",EDGE,{"disambiguationData":[TD([subQ6])],"derivedFrom":makeQuery(id+"F0Hq7nSFAMYVZvY_4.23.F20.boolean.opBoolean","SPLIT",EDGE,{"disambiguationData":[TD([subQ6])],"derivedFrom":makeQuery(id+"F0Hq7nSFAMYVZvY_4.22.F20.boolean.opBoolean","SPLIT",EDGE,{"disambiguationData":[TD([subQ6])],"derivedFrom":makeQuery(id+"F0Hq7nSFAMYVZvY_4.21.F20.boolean.opBoolean","SPLIT",EDGE,{"disambiguationData":[TD([subQ6])],"derivedFrom":makeQuery(id+"F0Hq7nSFAMYVZvY_4.20.F20.boolean.opBoolean","SPLIT",EDGE,{"disambiguationData":[TD([subQ6])],"derivedFrom":makeQuery(id+"F0Hq7nSFAMYVZvY_4.19.F20.boolean.opBoolean","SPLIT",EDGE,{"disambiguationData":[TD([subQ6])],"derivedFrom":makeQuery(id+"F0Hq7nSFAMYVZvY_4.18.F20.boolean.opBoolean","SPLIT",EDGE,{"disambiguationData":[TD([subQ6])],"derivedFrom":makeQuery(id+"F0Hq7nSFAMYVZvY_4.17.F20.boolean.opBoolean","SPLIT",EDGE,{"disambiguationData":[TD([subQ6])],"derivedFrom":makeQuery(id+"F0Hq7nSFAMYVZvY_4.16.F20.boolean.opBoolean","SPLIT",EDGE,{"disambiguationData":[TD([subQ6])],"derivedFrom":makeQuery(id+"F0Hq7nSFAMYVZvY_4.15.F20.boolean.opBoolean","SPLIT",EDGE,{"disambiguationData":[TD([subQ6])],"derivedFrom":makeQuery(id+"F0Hq7nSFAMYVZvY_4.14.F20.boolean.opBoolean","SPLIT",EDGE,{"disambiguationData":[TD([subQ6])],"derivedFrom":makeQuery(id+"F0Hq7nSFAMYVZvY_4.13.F20.boolean.opBoolean","SPLIT",EDGE,{"disambiguationData":[TD([subQ6])],"derivedFrom":makeQuery(id+"F0Hq7nSFAMYVZvY_4.12.F20.boolean.opBoolean","SPLIT",EDGE,{"disambiguationData":[TD([subQ6])],"derivedFrom":makeQuery(id+"F0Hq7nSFAMYVZvY_4.11.F20.boolean.opBoolean","SPLIT",EDGE,{"disambiguationData":[TD([subQ6])],"derivedFrom":makeQuery(id+"F0Hq7nSFAMYVZvY_4.10.F20.boolean.opBoolean","SPLIT",EDGE,{"disambiguationData":[TD([subQ6])],"derivedFrom":makeQuery(id+"F0Hq7nSFAMYVZvY_4.9.F20.boolean.opBoolean","SPLIT",EDGE,{"disambiguationData":[TD([subQ6])],"derivedFrom":makeQuery(id+"F0Hq7nSFAMYVZvY_4.8.F20.boolean.opBoolean","SPLIT",EDGE,{"disambiguationData":[TD([subQ6])],"derivedFrom":makeQuery(id+"F0Hq7nSFAMYVZvY_4.7.F20.boolean.opBoolean","SPLIT",EDGE,{"disambiguationData":[TD([subQ6])],"derivedFrom":makeQuery(id+"F0Hq7nSFAMYVZvY_4.6.F20.boolean.opBoolean","SPLIT",EDGE,{"disambiguationData":[TD([subQ6])],"derivedFrom":makeQuery(id+"F0Hq7nSFAMYVZvY_4.5.F20.boolean.opBoolean","SPLIT",EDGE,{"disambiguationData":[TD([subQ6])],"derivedFrom":makeQuery(id+"F0Hq7nSFAMYVZvY_4.4.F20.boolean.opBoolean","SPLIT",EDGE,{"disambiguationData":[TD([subQ6])],"derivedFrom":makeQuery(id+"F0Hq7nSFAMYVZvY_4.3.F20.boolean.opBoolean","SPLIT",EDGE,{"disambiguationData":[TD([subQ6])],"derivedFrom":makeQuery(id+"F0Hq7nSFAMYVZvY_4.2.F20.boolean.opBoolean","SPLIT",EDGE,{"disambiguationData":[TD([subQ6])],"derivedFrom":makeQuery(id+"F0Hq7nSFAMYVZvY_4.1.F20.boolean.opBoolean","SPLIT",EDGE,{"disambiguationData":[TD([subQ6])],"derivedFrom":makeQuery(id+"F17.boolean.opBoolean","COPY",EDGE,{"derivedFrom":makeQuery(id+"F17.opExtrude","CAP_EDGE",EDGE,{"disambiguationData":[OSD([subQ0])],"isStart":false})})})})})})})})})})})})})})})})})})})})})})})})})})})})})})})})})});}
            var Q362;
            {var subQ0=sQuery(id+"F19.wireOp",EDGE,"E158.MirrorCS");var subQ1=sQuery(id+"F19.wireOp",EDGE,"E157");var subQ3=sQuery(id+"F16.wireOp",EDGE,"E151");var subQ18=makeQuery(id+"F0Hq7nSFAMYVZvY_4.31.F20.opExtrude","SWEPT_FACE",FACE,{"disambiguationData":[OSD([subQ0])]});var subQ39=makeQuery(id+"F20.opExtrude","SWEPT_FACE",FACE,{"disambiguationData":[OSD([subQ1])]});Q362=makeQuery(id+"F0Hq7nSFAMYVZvY_4.32.F20.boolean.opBoolean","SPLIT",EDGE,{"disambiguationData":[TD([subQ18])],"derivedFrom":makeQuery(id+"F0Hq7nSFAMYVZvY_4.31.F20.boolean.opBoolean","SPLIT",EDGE,{"disambiguationData":[TD([subQ39])],"derivedFrom":makeQuery(id+"F0Hq7nSFAMYVZvY_4.30.F20.boolean.opBoolean","SPLIT",EDGE,{"disambiguationData":[TD([subQ39])],"derivedFrom":makeQuery(id+"F0Hq7nSFAMYVZvY_4.29.F20.boolean.opBoolean","SPLIT",EDGE,{"disambiguationData":[TD([subQ39])],"derivedFrom":makeQuery(id+"F0Hq7nSFAMYVZvY_4.28.F20.boolean.opBoolean","SPLIT",EDGE,{"disambiguationData":[TD([subQ39])],"derivedFrom":makeQuery(id+"F0Hq7nSFAMYVZvY_4.27.F20.boolean.opBoolean","SPLIT",EDGE,{"disambiguationData":[TD([subQ39])],"derivedFrom":makeQuery(id+"F0Hq7nSFAMYVZvY_4.26.F20.boolean.opBoolean","SPLIT",EDGE,{"disambiguationData":[TD([subQ39])],"derivedFrom":makeQuery(id+"F0Hq7nSFAMYVZvY_4.25.F20.boolean.opBoolean","SPLIT",EDGE,{"disambiguationData":[TD([subQ39])],"derivedFrom":makeQuery(id+"F0Hq7nSFAMYVZvY_4.24.F20.boolean.opBoolean","SPLIT",EDGE,{"disambiguationData":[TD([subQ39])],"derivedFrom":makeQuery(id+"F0Hq7nSFAMYVZvY_4.23.F20.boolean.opBoolean","SPLIT",EDGE,{"disambiguationData":[TD([subQ39])],"derivedFrom":makeQuery(id+"F0Hq7nSFAMYVZvY_4.22.F20.boolean.opBoolean","SPLIT",EDGE,{"disambiguationData":[TD([subQ39])],"derivedFrom":makeQuery(id+"F0Hq7nSFAMYVZvY_4.21.F20.boolean.opBoolean","SPLIT",EDGE,{"disambiguationData":[TD([subQ39])],"derivedFrom":makeQuery(id+"F0Hq7nSFAMYVZvY_4.20.F20.boolean.opBoolean","SPLIT",EDGE,{"disambiguationData":[TD([subQ39])],"derivedFrom":makeQuery(id+"F0Hq7nSFAMYVZvY_4.19.F20.boolean.opBoolean","SPLIT",EDGE,{"disambiguationData":[TD([subQ39])],"derivedFrom":makeQuery(id+"F0Hq7nSFAMYVZvY_4.18.F20.boolean.opBoolean","SPLIT",EDGE,{"disambiguationData":[TD([subQ39])],"derivedFrom":makeQuery(id+"F0Hq7nSFAMYVZvY_4.17.F20.boolean.opBoolean","SPLIT",EDGE,{"disambiguationData":[TD([subQ39])],"derivedFrom":makeQuery(id+"F0Hq7nSFAMYVZvY_4.16.F20.boolean.opBoolean","SPLIT",EDGE,{"disambiguationData":[TD([subQ39])],"derivedFrom":makeQuery(id+"F0Hq7nSFAMYVZvY_4.15.F20.boolean.opBoolean","SPLIT",EDGE,{"disambiguationData":[TD([subQ39])],"derivedFrom":makeQuery(id+"F0Hq7nSFAMYVZvY_4.14.F20.boolean.opBoolean","SPLIT",EDGE,{"disambiguationData":[TD([subQ39])],"derivedFrom":makeQuery(id+"F0Hq7nSFAMYVZvY_4.13.F20.boolean.opBoolean","SPLIT",EDGE,{"disambiguationData":[TD([subQ39])],"derivedFrom":makeQuery(id+"F0Hq7nSFAMYVZvY_4.12.F20.boolean.opBoolean","SPLIT",EDGE,{"disambiguationData":[TD([subQ39])],"derivedFrom":makeQuery(id+"F0Hq7nSFAMYVZvY_4.11.F20.boolean.opBoolean","SPLIT",EDGE,{"disambiguationData":[TD([subQ39])],"derivedFrom":makeQuery(id+"F0Hq7nSFAMYVZvY_4.10.F20.boolean.opBoolean","SPLIT",EDGE,{"disambiguationData":[TD([subQ39])],"derivedFrom":makeQuery(id+"F0Hq7nSFAMYVZvY_4.9.F20.boolean.opBoolean","SPLIT",EDGE,{"disambiguationData":[TD([subQ39])],"derivedFrom":makeQuery(id+"F0Hq7nSFAMYVZvY_4.8.F20.boolean.opBoolean","SPLIT",EDGE,{"disambiguationData":[TD([subQ39])],"derivedFrom":makeQuery(id+"F0Hq7nSFAMYVZvY_4.7.F20.boolean.opBoolean","SPLIT",EDGE,{"disambiguationData":[TD([subQ39])],"derivedFrom":makeQuery(id+"F0Hq7nSFAMYVZvY_4.6.F20.boolean.opBoolean","SPLIT",EDGE,{"disambiguationData":[TD([subQ39])],"derivedFrom":makeQuery(id+"F0Hq7nSFAMYVZvY_4.5.F20.boolean.opBoolean","SPLIT",EDGE,{"disambiguationData":[TD([subQ39])],"derivedFrom":makeQuery(id+"F0Hq7nSFAMYVZvY_4.4.F20.boolean.opBoolean","SPLIT",EDGE,{"disambiguationData":[TD([subQ39])],"derivedFrom":makeQuery(id+"F0Hq7nSFAMYVZvY_4.3.F20.boolean.opBoolean","SPLIT",EDGE,{"disambiguationData":[TD([subQ39])],"derivedFrom":makeQuery(id+"F0Hq7nSFAMYVZvY_4.2.F20.boolean.opBoolean","SPLIT",EDGE,{"disambiguationData":[TD([subQ39])],"derivedFrom":makeQuery(id+"F0Hq7nSFAMYVZvY_4.1.F20.boolean.opBoolean","SPLIT",EDGE,{"disambiguationData":[TD([subQ39])],"derivedFrom":makeQuery(id+"F18.boolean.opBoolean","COPY",EDGE,{"derivedFrom":makeQuery(id+"F18.opExtrude","CAP_EDGE",EDGE,{"disambiguationData":[OSD([subQ3])],"isStart":false})})})})})})})})})})})})})})})})})})})})})})})})})})})})})})})})})});}
            var Q363;
            Q363=makeQuery(id+"F0Hq7nSFAMYVZvY_4.1.F20.opExtrude","CAP_EDGE",EDGE,{"disambiguationData":[OSD([sQuery(id+"F19.wireOp",EDGE,"E157")])],"isStart":false});
            var Q364;
            Q364=makeQuery(id+"F0Hq7nSFAMYVZvY_4.1.F20.opExtrude","CAP_EDGE",EDGE,{"disambiguationData":[OSD([sQuery(id+"F19.wireOp",EDGE,"E158.MirrorCS")])],"isStart":false});
            var Q365;
            Q365=makeQuery(id+"F0Hq7nSFAMYVZvY_4.33.F20.opExtrude","CAP_EDGE",EDGE,{"disambiguationData":[OSD([sQuery(id+"F19.wireOp",EDGE,"E157")])],"isStart":false});
            var Q366;
            Q366=makeQuery(id+"F0Hq7nSFAMYVZvY_4.1.F20.opExtrude","SWEPT_EDGE",EDGE,{"disambiguationData":[OSD([sQuery(id+"F16.wireOp",EDGE,"E151"),sQuery(id+"F19.wireOp",EDGE,"E157")])]});
            var Q367;
            Q367=makeQuery(id+"F0Hq7nSFAMYVZvY_4.1.F20.opExtrude","SWEPT_EDGE",EDGE,{"disambiguationData":[OSD([sQuery(id+"F16.wireOp",EDGE,"E151"),sQuery(id+"F19.wireOp",EDGE,"E158.MirrorCS")])]});
            var Q368;
            Q368=makeQuery(id+"F0Hq7nSFAMYVZvY_4.1.F20.opExtrude","CAP_EDGE",EDGE,{"disambiguationData":[OSD([sQuery(id+"F19.wireOp",EDGE,"E157")])],"isStart":true});
            var Q369;
            Q369=makeQuery(id+"F0Hq7nSFAMYVZvY_4.1.F20.opExtrude","CAP_EDGE",EDGE,{"disambiguationData":[OSD([sQuery(id+"F19.wireOp",EDGE,"E158.MirrorCS")])],"isStart":true});
            var Q370;
            {var subQ0=sQuery(id+"F16.wireOp",EDGE,"E151");Q370=makeQuery(id+"F0Hq7nSFAMYVZvY_4.1.F20.boolean.opBoolean","SPLIT",EDGE,{"disambiguationData":[TD([makeQuery(id+"F20.opExtrude","SWEPT_FACE",FACE,{"disambiguationData":[OSD([sQuery(id+"F19.wireOp",EDGE,"E158.MirrorCS")])]})])],"derivedFrom":makeQuery(id+"F17.boolean.opBoolean","COPY",EDGE,{"derivedFrom":makeQuery(id+"F17.opExtrude","CAP_EDGE",EDGE,{"disambiguationData":[OSD([subQ0])],"isStart":false})})});}
            var Q371;
            {var subQ0=sQuery(id+"F19.wireOp",EDGE,"E158.MirrorCS");var subQ3=sQuery(id+"F16.wireOp",EDGE,"E151");Q371=makeQuery(id+"F0Hq7nSFAMYVZvY_4.1.F20.boolean.opBoolean","SPLIT",EDGE,{"disambiguationData":[TD([makeQuery(id+"F20.opExtrude","SWEPT_FACE",FACE,{"disambiguationData":[OSD([subQ0])]})])],"derivedFrom":makeQuery(id+"F18.boolean.opBoolean","COPY",EDGE,{"derivedFrom":makeQuery(id+"F18.opExtrude","CAP_EDGE",EDGE,{"disambiguationData":[OSD([subQ3])],"isStart":false})})});}
            var Q372;
            Q372=makeQuery(id+"F0Hq7nSFAMYVZvY_4.33.F20.opExtrude","SWEPT_EDGE",EDGE,{"disambiguationData":[OSD([sQuery(id+"F16.wireOp",EDGE,"E151"),sQuery(id+"F19.wireOp",EDGE,"E157")])]});
            var Q373;
            Q373=makeQuery(id+"F0Hq7nSFAMYVZvY_4.33.F20.opExtrude","SWEPT_EDGE",EDGE,{"disambiguationData":[OSD([sQuery(id+"F16.wireOp",EDGE,"E151"),sQuery(id+"F19.wireOp",EDGE,"E158.MirrorCS")])]});
            var Q374;
            Q374=makeQuery(id+"F0Hq7nSFAMYVZvY_4.33.F20.opExtrude","CAP_EDGE",EDGE,{"disambiguationData":[OSD([sQuery(id+"F19.wireOp",EDGE,"E157")])],"isStart":true});
            var Q375;
            Q375=makeQuery(id+"F0Hq7nSFAMYVZvY_4.33.F20.opExtrude","CAP_EDGE",EDGE,{"disambiguationData":[OSD([sQuery(id+"F19.wireOp",EDGE,"E158.MirrorCS")])],"isStart":true});
            var Q376;
            {var subQ0=sQuery(id+"F16.wireOp",EDGE,"E151");var subQ3=sQuery(id+"F19.wireOp",EDGE,"E157");var subQ4=sQuery(id+"F19.wireOp",EDGE,"E158.MirrorCS");var subQ5=makeQuery(id+"F0Hq7nSFAMYVZvY_4.32.F20.opExtrude","SWEPT_FACE",FACE,{"disambiguationData":[OSD([subQ4])]});var subQ6=makeQuery(id+"F20.opExtrude","SWEPT_FACE",FACE,{"disambiguationData":[OSD([subQ3])]});Q376=makeQuery(id+"F0Hq7nSFAMYVZvY_4.33.F20.boolean.opBoolean","SPLIT",EDGE,{"disambiguationData":[TD([subQ5])],"derivedFrom":makeQuery(id+"F0Hq7nSFAMYVZvY_4.32.F20.boolean.opBoolean","SPLIT",EDGE,{"disambiguationData":[TD([subQ6])],"derivedFrom":makeQuery(id+"F0Hq7nSFAMYVZvY_4.31.F20.boolean.opBoolean","SPLIT",EDGE,{"disambiguationData":[TD([subQ6])],"derivedFrom":makeQuery(id+"F0Hq7nSFAMYVZvY_4.30.F20.boolean.opBoolean","SPLIT",EDGE,{"disambiguationData":[TD([subQ6])],"derivedFrom":makeQuery(id+"F0Hq7nSFAMYVZvY_4.29.F20.boolean.opBoolean","SPLIT",EDGE,{"disambiguationData":[TD([subQ6])],"derivedFrom":makeQuery(id+"F0Hq7nSFAMYVZvY_4.28.F20.boolean.opBoolean","SPLIT",EDGE,{"disambiguationData":[TD([subQ6])],"derivedFrom":makeQuery(id+"F0Hq7nSFAMYVZvY_4.27.F20.boolean.opBoolean","SPLIT",EDGE,{"disambiguationData":[TD([subQ6])],"derivedFrom":makeQuery(id+"F0Hq7nSFAMYVZvY_4.26.F20.boolean.opBoolean","SPLIT",EDGE,{"disambiguationData":[TD([subQ6])],"derivedFrom":makeQuery(id+"F0Hq7nSFAMYVZvY_4.25.F20.boolean.opBoolean","SPLIT",EDGE,{"disambiguationData":[TD([subQ6])],"derivedFrom":makeQuery(id+"F0Hq7nSFAMYVZvY_4.24.F20.boolean.opBoolean","SPLIT",EDGE,{"disambiguationData":[TD([subQ6])],"derivedFrom":makeQuery(id+"F0Hq7nSFAMYVZvY_4.23.F20.boolean.opBoolean","SPLIT",EDGE,{"disambiguationData":[TD([subQ6])],"derivedFrom":makeQuery(id+"F0Hq7nSFAMYVZvY_4.22.F20.boolean.opBoolean","SPLIT",EDGE,{"disambiguationData":[TD([subQ6])],"derivedFrom":makeQuery(id+"F0Hq7nSFAMYVZvY_4.21.F20.boolean.opBoolean","SPLIT",EDGE,{"disambiguationData":[TD([subQ6])],"derivedFrom":makeQuery(id+"F0Hq7nSFAMYVZvY_4.20.F20.boolean.opBoolean","SPLIT",EDGE,{"disambiguationData":[TD([subQ6])],"derivedFrom":makeQuery(id+"F0Hq7nSFAMYVZvY_4.19.F20.boolean.opBoolean","SPLIT",EDGE,{"disambiguationData":[TD([subQ6])],"derivedFrom":makeQuery(id+"F0Hq7nSFAMYVZvY_4.18.F20.boolean.opBoolean","SPLIT",EDGE,{"disambiguationData":[TD([subQ6])],"derivedFrom":makeQuery(id+"F0Hq7nSFAMYVZvY_4.17.F20.boolean.opBoolean","SPLIT",EDGE,{"disambiguationData":[TD([subQ6])],"derivedFrom":makeQuery(id+"F0Hq7nSFAMYVZvY_4.16.F20.boolean.opBoolean","SPLIT",EDGE,{"disambiguationData":[TD([subQ6])],"derivedFrom":makeQuery(id+"F0Hq7nSFAMYVZvY_4.15.F20.boolean.opBoolean","SPLIT",EDGE,{"disambiguationData":[TD([subQ6])],"derivedFrom":makeQuery(id+"F0Hq7nSFAMYVZvY_4.14.F20.boolean.opBoolean","SPLIT",EDGE,{"disambiguationData":[TD([subQ6])],"derivedFrom":makeQuery(id+"F0Hq7nSFAMYVZvY_4.13.F20.boolean.opBoolean","SPLIT",EDGE,{"disambiguationData":[TD([subQ6])],"derivedFrom":makeQuery(id+"F0Hq7nSFAMYVZvY_4.12.F20.boolean.opBoolean","SPLIT",EDGE,{"disambiguationData":[TD([subQ6])],"derivedFrom":makeQuery(id+"F0Hq7nSFAMYVZvY_4.11.F20.boolean.opBoolean","SPLIT",EDGE,{"disambiguationData":[TD([subQ6])],"derivedFrom":makeQuery(id+"F0Hq7nSFAMYVZvY_4.10.F20.boolean.opBoolean","SPLIT",EDGE,{"disambiguationData":[TD([subQ6])],"derivedFrom":makeQuery(id+"F0Hq7nSFAMYVZvY_4.9.F20.boolean.opBoolean","SPLIT",EDGE,{"disambiguationData":[TD([subQ6])],"derivedFrom":makeQuery(id+"F0Hq7nSFAMYVZvY_4.8.F20.boolean.opBoolean","SPLIT",EDGE,{"disambiguationData":[TD([subQ6])],"derivedFrom":makeQuery(id+"F0Hq7nSFAMYVZvY_4.7.F20.boolean.opBoolean","SPLIT",EDGE,{"disambiguationData":[TD([subQ6])],"derivedFrom":makeQuery(id+"F0Hq7nSFAMYVZvY_4.6.F20.boolean.opBoolean","SPLIT",EDGE,{"disambiguationData":[TD([subQ6])],"derivedFrom":makeQuery(id+"F0Hq7nSFAMYVZvY_4.5.F20.boolean.opBoolean","SPLIT",EDGE,{"disambiguationData":[TD([subQ6])],"derivedFrom":makeQuery(id+"F0Hq7nSFAMYVZvY_4.4.F20.boolean.opBoolean","SPLIT",EDGE,{"disambiguationData":[TD([subQ6])],"derivedFrom":makeQuery(id+"F0Hq7nSFAMYVZvY_4.3.F20.boolean.opBoolean","SPLIT",EDGE,{"disambiguationData":[TD([subQ6])],"derivedFrom":makeQuery(id+"F0Hq7nSFAMYVZvY_4.2.F20.boolean.opBoolean","SPLIT",EDGE,{"disambiguationData":[TD([subQ6])],"derivedFrom":makeQuery(id+"F0Hq7nSFAMYVZvY_4.1.F20.boolean.opBoolean","SPLIT",EDGE,{"disambiguationData":[TD([subQ6])],"derivedFrom":makeQuery(id+"F17.boolean.opBoolean","COPY",EDGE,{"derivedFrom":makeQuery(id+"F17.opExtrude","CAP_EDGE",EDGE,{"disambiguationData":[OSD([subQ0])],"isStart":false})})})})})})})})})})})})})})})})})})})})})})})})})})})})})})})})})})});}
            var Q377;
            {var subQ0=sQuery(id+"F19.wireOp",EDGE,"E158.MirrorCS");var subQ1=sQuery(id+"F19.wireOp",EDGE,"E157");var subQ3=sQuery(id+"F16.wireOp",EDGE,"E151");var subQ15=makeQuery(id+"F0Hq7nSFAMYVZvY_4.32.F20.opExtrude","SWEPT_FACE",FACE,{"disambiguationData":[OSD([subQ0])]});var subQ40=makeQuery(id+"F20.opExtrude","SWEPT_FACE",FACE,{"disambiguationData":[OSD([subQ1])]});Q377=makeQuery(id+"F0Hq7nSFAMYVZvY_4.33.F20.boolean.opBoolean","SPLIT",EDGE,{"disambiguationData":[TD([subQ15])],"derivedFrom":makeQuery(id+"F0Hq7nSFAMYVZvY_4.32.F20.boolean.opBoolean","SPLIT",EDGE,{"disambiguationData":[TD([subQ40])],"derivedFrom":makeQuery(id+"F0Hq7nSFAMYVZvY_4.31.F20.boolean.opBoolean","SPLIT",EDGE,{"disambiguationData":[TD([subQ40])],"derivedFrom":makeQuery(id+"F0Hq7nSFAMYVZvY_4.30.F20.boolean.opBoolean","SPLIT",EDGE,{"disambiguationData":[TD([subQ40])],"derivedFrom":makeQuery(id+"F0Hq7nSFAMYVZvY_4.29.F20.boolean.opBoolean","SPLIT",EDGE,{"disambiguationData":[TD([subQ40])],"derivedFrom":makeQuery(id+"F0Hq7nSFAMYVZvY_4.28.F20.boolean.opBoolean","SPLIT",EDGE,{"disambiguationData":[TD([subQ40])],"derivedFrom":makeQuery(id+"F0Hq7nSFAMYVZvY_4.27.F20.boolean.opBoolean","SPLIT",EDGE,{"disambiguationData":[TD([subQ40])],"derivedFrom":makeQuery(id+"F0Hq7nSFAMYVZvY_4.26.F20.boolean.opBoolean","SPLIT",EDGE,{"disambiguationData":[TD([subQ40])],"derivedFrom":makeQuery(id+"F0Hq7nSFAMYVZvY_4.25.F20.boolean.opBoolean","SPLIT",EDGE,{"disambiguationData":[TD([subQ40])],"derivedFrom":makeQuery(id+"F0Hq7nSFAMYVZvY_4.24.F20.boolean.opBoolean","SPLIT",EDGE,{"disambiguationData":[TD([subQ40])],"derivedFrom":makeQuery(id+"F0Hq7nSFAMYVZvY_4.23.F20.boolean.opBoolean","SPLIT",EDGE,{"disambiguationData":[TD([subQ40])],"derivedFrom":makeQuery(id+"F0Hq7nSFAMYVZvY_4.22.F20.boolean.opBoolean","SPLIT",EDGE,{"disambiguationData":[TD([subQ40])],"derivedFrom":makeQuery(id+"F0Hq7nSFAMYVZvY_4.21.F20.boolean.opBoolean","SPLIT",EDGE,{"disambiguationData":[TD([subQ40])],"derivedFrom":makeQuery(id+"F0Hq7nSFAMYVZvY_4.20.F20.boolean.opBoolean","SPLIT",EDGE,{"disambiguationData":[TD([subQ40])],"derivedFrom":makeQuery(id+"F0Hq7nSFAMYVZvY_4.19.F20.boolean.opBoolean","SPLIT",EDGE,{"disambiguationData":[TD([subQ40])],"derivedFrom":makeQuery(id+"F0Hq7nSFAMYVZvY_4.18.F20.boolean.opBoolean","SPLIT",EDGE,{"disambiguationData":[TD([subQ40])],"derivedFrom":makeQuery(id+"F0Hq7nSFAMYVZvY_4.17.F20.boolean.opBoolean","SPLIT",EDGE,{"disambiguationData":[TD([subQ40])],"derivedFrom":makeQuery(id+"F0Hq7nSFAMYVZvY_4.16.F20.boolean.opBoolean","SPLIT",EDGE,{"disambiguationData":[TD([subQ40])],"derivedFrom":makeQuery(id+"F0Hq7nSFAMYVZvY_4.15.F20.boolean.opBoolean","SPLIT",EDGE,{"disambiguationData":[TD([subQ40])],"derivedFrom":makeQuery(id+"F0Hq7nSFAMYVZvY_4.14.F20.boolean.opBoolean","SPLIT",EDGE,{"disambiguationData":[TD([subQ40])],"derivedFrom":makeQuery(id+"F0Hq7nSFAMYVZvY_4.13.F20.boolean.opBoolean","SPLIT",EDGE,{"disambiguationData":[TD([subQ40])],"derivedFrom":makeQuery(id+"F0Hq7nSFAMYVZvY_4.12.F20.boolean.opBoolean","SPLIT",EDGE,{"disambiguationData":[TD([subQ40])],"derivedFrom":makeQuery(id+"F0Hq7nSFAMYVZvY_4.11.F20.boolean.opBoolean","SPLIT",EDGE,{"disambiguationData":[TD([subQ40])],"derivedFrom":makeQuery(id+"F0Hq7nSFAMYVZvY_4.10.F20.boolean.opBoolean","SPLIT",EDGE,{"disambiguationData":[TD([subQ40])],"derivedFrom":makeQuery(id+"F0Hq7nSFAMYVZvY_4.9.F20.boolean.opBoolean","SPLIT",EDGE,{"disambiguationData":[TD([subQ40])],"derivedFrom":makeQuery(id+"F0Hq7nSFAMYVZvY_4.8.F20.boolean.opBoolean","SPLIT",EDGE,{"disambiguationData":[TD([subQ40])],"derivedFrom":makeQuery(id+"F0Hq7nSFAMYVZvY_4.7.F20.boolean.opBoolean","SPLIT",EDGE,{"disambiguationData":[TD([subQ40])],"derivedFrom":makeQuery(id+"F0Hq7nSFAMYVZvY_4.6.F20.boolean.opBoolean","SPLIT",EDGE,{"disambiguationData":[TD([subQ40])],"derivedFrom":makeQuery(id+"F0Hq7nSFAMYVZvY_4.5.F20.boolean.opBoolean","SPLIT",EDGE,{"disambiguationData":[TD([subQ40])],"derivedFrom":makeQuery(id+"F0Hq7nSFAMYVZvY_4.4.F20.boolean.opBoolean","SPLIT",EDGE,{"disambiguationData":[TD([subQ40])],"derivedFrom":makeQuery(id+"F0Hq7nSFAMYVZvY_4.3.F20.boolean.opBoolean","SPLIT",EDGE,{"disambiguationData":[TD([subQ40])],"derivedFrom":makeQuery(id+"F0Hq7nSFAMYVZvY_4.2.F20.boolean.opBoolean","SPLIT",EDGE,{"disambiguationData":[TD([subQ40])],"derivedFrom":makeQuery(id+"F0Hq7nSFAMYVZvY_4.1.F20.boolean.opBoolean","SPLIT",EDGE,{"disambiguationData":[TD([subQ40])],"derivedFrom":makeQuery(id+"F18.boolean.opBoolean","COPY",EDGE,{"derivedFrom":makeQuery(id+"F18.opExtrude","CAP_EDGE",EDGE,{"disambiguationData":[OSD([subQ3])],"isStart":false})})})})})})})})})})})})})})})})})})})})})})})})})})})})})})})})})})});}
            var Q378;
            Q378=makeQuery(id+"F0Hq7nSFAMYVZvY_4.2.F20.opExtrude","CAP_EDGE",EDGE,{"disambiguationData":[OSD([sQuery(id+"F19.wireOp",EDGE,"E157")])],"isStart":false});
            var Q379;
            Q379=makeQuery(id+"F0Hq7nSFAMYVZvY_4.34.F20.opExtrude","SWEPT_FACE",FACE,{"disambiguationData":[OSD([sQuery(id+"F19.wireOp",EDGE,"E158.MirrorCS")])]});
            var Q380;
            Q380=makeQuery(id+"F0Hq7nSFAMYVZvY_4.2.F20.opExtrude","SWEPT_EDGE",EDGE,{"disambiguationData":[OSD([sQuery(id+"F16.wireOp",EDGE,"E151"),sQuery(id+"F19.wireOp",EDGE,"E157")])]});
            var Q381;
            Q381=makeQuery(id+"F0Hq7nSFAMYVZvY_4.2.F20.opExtrude","SWEPT_EDGE",EDGE,{"disambiguationData":[OSD([sQuery(id+"F16.wireOp",EDGE,"E151"),sQuery(id+"F19.wireOp",EDGE,"E158.MirrorCS")])]});
            var Q382;
            Q382=makeQuery(id+"F0Hq7nSFAMYVZvY_4.2.F20.opExtrude","CAP_EDGE",EDGE,{"disambiguationData":[OSD([sQuery(id+"F19.wireOp",EDGE,"E157")])],"isStart":true});
            var Q383;
            Q383=makeQuery(id+"F0Hq7nSFAMYVZvY_4.2.F20.opExtrude","CAP_EDGE",EDGE,{"disambiguationData":[OSD([sQuery(id+"F19.wireOp",EDGE,"E158.MirrorCS")])],"isStart":true});
            var Q384;
            {var subQ0=sQuery(id+"F16.wireOp",EDGE,"E151");var subQ2=makeQuery(id+"F0Hq7nSFAMYVZvY_4.1.F20.opExtrude","SWEPT_FACE",FACE,{"disambiguationData":[OSD([sQuery(id+"F19.wireOp",EDGE,"E158.MirrorCS")])]});var subQ4=sQuery(id+"F19.wireOp",EDGE,"E157");Q384=makeQuery(id+"F0Hq7nSFAMYVZvY_4.2.F20.boolean.opBoolean","SPLIT",EDGE,{"disambiguationData":[TD([subQ2])],"derivedFrom":makeQuery(id+"F0Hq7nSFAMYVZvY_4.1.F20.boolean.opBoolean","SPLIT",EDGE,{"disambiguationData":[TD([makeQuery(id+"F20.opExtrude","SWEPT_FACE",FACE,{"disambiguationData":[OSD([subQ4])]})])],"derivedFrom":makeQuery(id+"F17.boolean.opBoolean","COPY",EDGE,{"derivedFrom":makeQuery(id+"F17.opExtrude","CAP_EDGE",EDGE,{"disambiguationData":[OSD([subQ0])],"isStart":false})})})});}
            var Q385;
            {var subQ0=sQuery(id+"F19.wireOp",EDGE,"E158.MirrorCS");var subQ1=sQuery(id+"F19.wireOp",EDGE,"E157");var subQ3=sQuery(id+"F16.wireOp",EDGE,"E151");var subQ8=makeQuery(id+"F0Hq7nSFAMYVZvY_4.1.F20.opExtrude","SWEPT_FACE",FACE,{"disambiguationData":[OSD([subQ0])]});Q385=makeQuery(id+"F0Hq7nSFAMYVZvY_4.2.F20.boolean.opBoolean","SPLIT",EDGE,{"disambiguationData":[TD([subQ8])],"derivedFrom":makeQuery(id+"F0Hq7nSFAMYVZvY_4.1.F20.boolean.opBoolean","SPLIT",EDGE,{"disambiguationData":[TD([makeQuery(id+"F20.opExtrude","SWEPT_FACE",FACE,{"disambiguationData":[OSD([subQ1])]})])],"derivedFrom":makeQuery(id+"F18.boolean.opBoolean","COPY",EDGE,{"derivedFrom":makeQuery(id+"F18.opExtrude","CAP_EDGE",EDGE,{"disambiguationData":[OSD([subQ3])],"isStart":false})})})});}
            var Q386;
            Q386=makeQuery(id+"F0Hq7nSFAMYVZvY_4.34.F20.opExtrude","SWEPT_EDGE",EDGE,{"disambiguationData":[OSD([sQuery(id+"F16.wireOp",EDGE,"E151"),sQuery(id+"F19.wireOp",EDGE,"E157")])]});
            var Q387;
            Q387=makeQuery(id+"F0Hq7nSFAMYVZvY_4.34.F20.opExtrude","SWEPT_EDGE",EDGE,{"disambiguationData":[OSD([sQuery(id+"F16.wireOp",EDGE,"E151"),sQuery(id+"F19.wireOp",EDGE,"E158.MirrorCS")])]});
            var Q388;
            Q388=makeQuery(id+"F0Hq7nSFAMYVZvY_4.34.F20.opExtrude","CAP_EDGE",EDGE,{"disambiguationData":[OSD([sQuery(id+"F19.wireOp",EDGE,"E158.MirrorCS")])],"isStart":true});
            var Q389;
            {var subQ0=sQuery(id+"F19.wireOp",EDGE,"E158.MirrorCS");var subQ1=sQuery(id+"F19.wireOp",EDGE,"E157");var subQ3=sQuery(id+"F16.wireOp",EDGE,"E151");var subQ23=makeQuery(id+"F0Hq7nSFAMYVZvY_4.33.F20.opExtrude","SWEPT_FACE",FACE,{"disambiguationData":[OSD([subQ0])]});var subQ41=makeQuery(id+"F20.opExtrude","SWEPT_FACE",FACE,{"disambiguationData":[OSD([subQ1])]});Q389=makeQuery(id+"F0Hq7nSFAMYVZvY_4.34.F20.boolean.opBoolean","SPLIT",FACE,{"disambiguationData":[TD([subQ23])],"derivedFrom":makeQuery(id+"F0Hq7nSFAMYVZvY_4.33.F20.boolean.opBoolean","SPLIT",FACE,{"disambiguationData":[TD([subQ41])],"derivedFrom":makeQuery(id+"F0Hq7nSFAMYVZvY_4.32.F20.boolean.opBoolean","SPLIT",FACE,{"disambiguationData":[TD([subQ41])],"derivedFrom":makeQuery(id+"F0Hq7nSFAMYVZvY_4.31.F20.boolean.opBoolean","SPLIT",FACE,{"disambiguationData":[TD([subQ41])],"derivedFrom":makeQuery(id+"F0Hq7nSFAMYVZvY_4.30.F20.boolean.opBoolean","SPLIT",FACE,{"disambiguationData":[TD([subQ41])],"derivedFrom":makeQuery(id+"F0Hq7nSFAMYVZvY_4.29.F20.boolean.opBoolean","SPLIT",FACE,{"disambiguationData":[TD([subQ41])],"derivedFrom":makeQuery(id+"F0Hq7nSFAMYVZvY_4.28.F20.boolean.opBoolean","SPLIT",FACE,{"disambiguationData":[TD([subQ41])],"derivedFrom":makeQuery(id+"F0Hq7nSFAMYVZvY_4.27.F20.boolean.opBoolean","SPLIT",FACE,{"disambiguationData":[TD([subQ41])],"derivedFrom":makeQuery(id+"F0Hq7nSFAMYVZvY_4.26.F20.boolean.opBoolean","SPLIT",FACE,{"disambiguationData":[TD([subQ41])],"derivedFrom":makeQuery(id+"F0Hq7nSFAMYVZvY_4.25.F20.boolean.opBoolean","SPLIT",FACE,{"disambiguationData":[TD([subQ41])],"derivedFrom":makeQuery(id+"F0Hq7nSFAMYVZvY_4.24.F20.boolean.opBoolean","SPLIT",FACE,{"disambiguationData":[TD([subQ41])],"derivedFrom":makeQuery(id+"F0Hq7nSFAMYVZvY_4.23.F20.boolean.opBoolean","SPLIT",FACE,{"disambiguationData":[TD([subQ41])],"derivedFrom":makeQuery(id+"F0Hq7nSFAMYVZvY_4.22.F20.boolean.opBoolean","SPLIT",FACE,{"disambiguationData":[TD([subQ41])],"derivedFrom":makeQuery(id+"F0Hq7nSFAMYVZvY_4.21.F20.boolean.opBoolean","SPLIT",FACE,{"disambiguationData":[TD([subQ41])],"derivedFrom":makeQuery(id+"F0Hq7nSFAMYVZvY_4.20.F20.boolean.opBoolean","SPLIT",FACE,{"disambiguationData":[TD([subQ41])],"derivedFrom":makeQuery(id+"F0Hq7nSFAMYVZvY_4.19.F20.boolean.opBoolean","SPLIT",FACE,{"disambiguationData":[TD([subQ41])],"derivedFrom":makeQuery(id+"F0Hq7nSFAMYVZvY_4.18.F20.boolean.opBoolean","SPLIT",FACE,{"disambiguationData":[TD([subQ41])],"derivedFrom":makeQuery(id+"F0Hq7nSFAMYVZvY_4.17.F20.boolean.opBoolean","SPLIT",FACE,{"disambiguationData":[TD([subQ41])],"derivedFrom":makeQuery(id+"F0Hq7nSFAMYVZvY_4.16.F20.boolean.opBoolean","SPLIT",FACE,{"disambiguationData":[TD([subQ41])],"derivedFrom":makeQuery(id+"F0Hq7nSFAMYVZvY_4.15.F20.boolean.opBoolean","SPLIT",FACE,{"disambiguationData":[TD([subQ41])],"derivedFrom":makeQuery(id+"F0Hq7nSFAMYVZvY_4.14.F20.boolean.opBoolean","SPLIT",FACE,{"disambiguationData":[TD([subQ41])],"derivedFrom":makeQuery(id+"F0Hq7nSFAMYVZvY_4.13.F20.boolean.opBoolean","SPLIT",FACE,{"disambiguationData":[TD([subQ41])],"derivedFrom":makeQuery(id+"F0Hq7nSFAMYVZvY_4.12.F20.boolean.opBoolean","SPLIT",FACE,{"disambiguationData":[TD([subQ41])],"derivedFrom":makeQuery(id+"F0Hq7nSFAMYVZvY_4.11.F20.boolean.opBoolean","SPLIT",FACE,{"disambiguationData":[TD([subQ41])],"derivedFrom":makeQuery(id+"F0Hq7nSFAMYVZvY_4.10.F20.boolean.opBoolean","SPLIT",FACE,{"disambiguationData":[TD([subQ41])],"derivedFrom":makeQuery(id+"F0Hq7nSFAMYVZvY_4.9.F20.boolean.opBoolean","SPLIT",FACE,{"disambiguationData":[TD([subQ41])],"derivedFrom":makeQuery(id+"F0Hq7nSFAMYVZvY_4.8.F20.boolean.opBoolean","SPLIT",FACE,{"disambiguationData":[TD([subQ41])],"derivedFrom":makeQuery(id+"F0Hq7nSFAMYVZvY_4.7.F20.boolean.opBoolean","SPLIT",FACE,{"disambiguationData":[TD([subQ41])],"derivedFrom":makeQuery(id+"F0Hq7nSFAMYVZvY_4.6.F20.boolean.opBoolean","SPLIT",FACE,{"disambiguationData":[TD([subQ41])],"derivedFrom":makeQuery(id+"F0Hq7nSFAMYVZvY_4.5.F20.boolean.opBoolean","SPLIT",FACE,{"disambiguationData":[TD([subQ41])],"derivedFrom":makeQuery(id+"F0Hq7nSFAMYVZvY_4.4.F20.boolean.opBoolean","SPLIT",FACE,{"disambiguationData":[TD([subQ41])],"derivedFrom":makeQuery(id+"F0Hq7nSFAMYVZvY_4.3.F20.boolean.opBoolean","SPLIT",FACE,{"disambiguationData":[TD([subQ41])],"derivedFrom":makeQuery(id+"F0Hq7nSFAMYVZvY_4.2.F20.boolean.opBoolean","SPLIT",FACE,{"disambiguationData":[TD([subQ41])],"derivedFrom":makeQuery(id+"F0Hq7nSFAMYVZvY_4.1.F20.boolean.opBoolean","SPLIT",FACE,{"disambiguationData":[TD([subQ41])],"derivedFrom":makeQuery(id+"F17.boolean.opBoolean","COPY",FACE,{"derivedFrom":makeQuery(id+"F17.opExtrude","SWEPT_FACE",FACE,{"disambiguationData":[OSD([subQ3])]})})})})})})})})})})})})})})})})})})})})})})})})})})})})})})})})})})})});}
            var Q390;
            {var subQ0=sQuery(id+"F16.wireOp",EDGE,"E151");var subQ3=sQuery(id+"F19.wireOp",EDGE,"E158.MirrorCS");var subQ4=makeQuery(id+"F0Hq7nSFAMYVZvY_4.33.F20.opExtrude","SWEPT_FACE",FACE,{"disambiguationData":[OSD([subQ3])]});var subQ5=sQuery(id+"F19.wireOp",EDGE,"E157");var subQ6=makeQuery(id+"F20.opExtrude","SWEPT_FACE",FACE,{"disambiguationData":[OSD([subQ5])]});Q390=makeQuery(id+"F0Hq7nSFAMYVZvY_4.34.F20.boolean.opBoolean","SPLIT",EDGE,{"disambiguationData":[TD([subQ4])],"derivedFrom":makeQuery(id+"F0Hq7nSFAMYVZvY_4.33.F20.boolean.opBoolean","SPLIT",EDGE,{"disambiguationData":[TD([subQ6])],"derivedFrom":makeQuery(id+"F0Hq7nSFAMYVZvY_4.32.F20.boolean.opBoolean","SPLIT",EDGE,{"disambiguationData":[TD([subQ6])],"derivedFrom":makeQuery(id+"F0Hq7nSFAMYVZvY_4.31.F20.boolean.opBoolean","SPLIT",EDGE,{"disambiguationData":[TD([subQ6])],"derivedFrom":makeQuery(id+"F0Hq7nSFAMYVZvY_4.30.F20.boolean.opBoolean","SPLIT",EDGE,{"disambiguationData":[TD([subQ6])],"derivedFrom":makeQuery(id+"F0Hq7nSFAMYVZvY_4.29.F20.boolean.opBoolean","SPLIT",EDGE,{"disambiguationData":[TD([subQ6])],"derivedFrom":makeQuery(id+"F0Hq7nSFAMYVZvY_4.28.F20.boolean.opBoolean","SPLIT",EDGE,{"disambiguationData":[TD([subQ6])],"derivedFrom":makeQuery(id+"F0Hq7nSFAMYVZvY_4.27.F20.boolean.opBoolean","SPLIT",EDGE,{"disambiguationData":[TD([subQ6])],"derivedFrom":makeQuery(id+"F0Hq7nSFAMYVZvY_4.26.F20.boolean.opBoolean","SPLIT",EDGE,{"disambiguationData":[TD([subQ6])],"derivedFrom":makeQuery(id+"F0Hq7nSFAMYVZvY_4.25.F20.boolean.opBoolean","SPLIT",EDGE,{"disambiguationData":[TD([subQ6])],"derivedFrom":makeQuery(id+"F0Hq7nSFAMYVZvY_4.24.F20.boolean.opBoolean","SPLIT",EDGE,{"disambiguationData":[TD([subQ6])],"derivedFrom":makeQuery(id+"F0Hq7nSFAMYVZvY_4.23.F20.boolean.opBoolean","SPLIT",EDGE,{"disambiguationData":[TD([subQ6])],"derivedFrom":makeQuery(id+"F0Hq7nSFAMYVZvY_4.22.F20.boolean.opBoolean","SPLIT",EDGE,{"disambiguationData":[TD([subQ6])],"derivedFrom":makeQuery(id+"F0Hq7nSFAMYVZvY_4.21.F20.boolean.opBoolean","SPLIT",EDGE,{"disambiguationData":[TD([subQ6])],"derivedFrom":makeQuery(id+"F0Hq7nSFAMYVZvY_4.20.F20.boolean.opBoolean","SPLIT",EDGE,{"disambiguationData":[TD([subQ6])],"derivedFrom":makeQuery(id+"F0Hq7nSFAMYVZvY_4.19.F20.boolean.opBoolean","SPLIT",EDGE,{"disambiguationData":[TD([subQ6])],"derivedFrom":makeQuery(id+"F0Hq7nSFAMYVZvY_4.18.F20.boolean.opBoolean","SPLIT",EDGE,{"disambiguationData":[TD([subQ6])],"derivedFrom":makeQuery(id+"F0Hq7nSFAMYVZvY_4.17.F20.boolean.opBoolean","SPLIT",EDGE,{"disambiguationData":[TD([subQ6])],"derivedFrom":makeQuery(id+"F0Hq7nSFAMYVZvY_4.16.F20.boolean.opBoolean","SPLIT",EDGE,{"disambiguationData":[TD([subQ6])],"derivedFrom":makeQuery(id+"F0Hq7nSFAMYVZvY_4.15.F20.boolean.opBoolean","SPLIT",EDGE,{"disambiguationData":[TD([subQ6])],"derivedFrom":makeQuery(id+"F0Hq7nSFAMYVZvY_4.14.F20.boolean.opBoolean","SPLIT",EDGE,{"disambiguationData":[TD([subQ6])],"derivedFrom":makeQuery(id+"F0Hq7nSFAMYVZvY_4.13.F20.boolean.opBoolean","SPLIT",EDGE,{"disambiguationData":[TD([subQ6])],"derivedFrom":makeQuery(id+"F0Hq7nSFAMYVZvY_4.12.F20.boolean.opBoolean","SPLIT",EDGE,{"disambiguationData":[TD([subQ6])],"derivedFrom":makeQuery(id+"F0Hq7nSFAMYVZvY_4.11.F20.boolean.opBoolean","SPLIT",EDGE,{"disambiguationData":[TD([subQ6])],"derivedFrom":makeQuery(id+"F0Hq7nSFAMYVZvY_4.10.F20.boolean.opBoolean","SPLIT",EDGE,{"disambiguationData":[TD([subQ6])],"derivedFrom":makeQuery(id+"F0Hq7nSFAMYVZvY_4.9.F20.boolean.opBoolean","SPLIT",EDGE,{"disambiguationData":[TD([subQ6])],"derivedFrom":makeQuery(id+"F0Hq7nSFAMYVZvY_4.8.F20.boolean.opBoolean","SPLIT",EDGE,{"disambiguationData":[TD([subQ6])],"derivedFrom":makeQuery(id+"F0Hq7nSFAMYVZvY_4.7.F20.boolean.opBoolean","SPLIT",EDGE,{"disambiguationData":[TD([subQ6])],"derivedFrom":makeQuery(id+"F0Hq7nSFAMYVZvY_4.6.F20.boolean.opBoolean","SPLIT",EDGE,{"disambiguationData":[TD([subQ6])],"derivedFrom":makeQuery(id+"F0Hq7nSFAMYVZvY_4.5.F20.boolean.opBoolean","SPLIT",EDGE,{"disambiguationData":[TD([subQ6])],"derivedFrom":makeQuery(id+"F0Hq7nSFAMYVZvY_4.4.F20.boolean.opBoolean","SPLIT",EDGE,{"disambiguationData":[TD([subQ6])],"derivedFrom":makeQuery(id+"F0Hq7nSFAMYVZvY_4.3.F20.boolean.opBoolean","SPLIT",EDGE,{"disambiguationData":[TD([subQ6])],"derivedFrom":makeQuery(id+"F0Hq7nSFAMYVZvY_4.2.F20.boolean.opBoolean","SPLIT",EDGE,{"disambiguationData":[TD([subQ6])],"derivedFrom":makeQuery(id+"F0Hq7nSFAMYVZvY_4.1.F20.boolean.opBoolean","SPLIT",EDGE,{"disambiguationData":[TD([subQ6])],"derivedFrom":makeQuery(id+"F17.boolean.opBoolean","COPY",EDGE,{"derivedFrom":makeQuery(id+"F17.opExtrude","CAP_EDGE",EDGE,{"disambiguationData":[OSD([subQ0])],"isStart":false})})})})})})})})})})})})})})})})})})})})})})})})})})})})})})})})})})})});}
            var Q391;
            Q391=makeQuery(id+"F0Hq7nSFAMYVZvY_4.35.F20.opExtrude","SWEPT_FACE",FACE,{"disambiguationData":[OSD([sQuery(id+"F19.wireOp",EDGE,"E158.MirrorCS")])]});
            var Q392;
            Q392=makeQuery(id+"F0Hq7nSFAMYVZvY_4.3.F20.opExtrude","SWEPT_EDGE",EDGE,{"disambiguationData":[OSD([sQuery(id+"F16.wireOp",EDGE,"E151"),sQuery(id+"F19.wireOp",EDGE,"E157")])]});
            var Q393;
            Q393=makeQuery(id+"F0Hq7nSFAMYVZvY_4.3.F20.opExtrude","SWEPT_EDGE",EDGE,{"disambiguationData":[OSD([sQuery(id+"F16.wireOp",EDGE,"E151"),sQuery(id+"F19.wireOp",EDGE,"E158.MirrorCS")])]});
            var Q394;
            Q394=makeQuery(id+"F0Hq7nSFAMYVZvY_4.3.F20.opExtrude","CAP_EDGE",EDGE,{"disambiguationData":[OSD([sQuery(id+"F19.wireOp",EDGE,"E157")])],"isStart":true});
            var Q395;
            Q395=makeQuery(id+"F0Hq7nSFAMYVZvY_4.3.F20.opExtrude","CAP_EDGE",EDGE,{"disambiguationData":[OSD([sQuery(id+"F19.wireOp",EDGE,"E158.MirrorCS")])],"isStart":true});
            var Q396;
            {var subQ0=sQuery(id+"F16.wireOp",EDGE,"E151");var subQ3=sQuery(id+"F19.wireOp",EDGE,"E157");var subQ4=sQuery(id+"F19.wireOp",EDGE,"E158.MirrorCS");var subQ5=makeQuery(id+"F0Hq7nSFAMYVZvY_4.2.F20.opExtrude","SWEPT_FACE",FACE,{"disambiguationData":[OSD([subQ4])]});var subQ6=makeQuery(id+"F20.opExtrude","SWEPT_FACE",FACE,{"disambiguationData":[OSD([subQ3])]});Q396=makeQuery(id+"F0Hq7nSFAMYVZvY_4.3.F20.boolean.opBoolean","SPLIT",EDGE,{"disambiguationData":[TD([subQ5])],"derivedFrom":makeQuery(id+"F0Hq7nSFAMYVZvY_4.2.F20.boolean.opBoolean","SPLIT",EDGE,{"disambiguationData":[TD([subQ6])],"derivedFrom":makeQuery(id+"F0Hq7nSFAMYVZvY_4.1.F20.boolean.opBoolean","SPLIT",EDGE,{"disambiguationData":[TD([subQ6])],"derivedFrom":makeQuery(id+"F17.boolean.opBoolean","COPY",EDGE,{"derivedFrom":makeQuery(id+"F17.opExtrude","CAP_EDGE",EDGE,{"disambiguationData":[OSD([subQ0])],"isStart":false})})})})});}
            var Q397;
            {var subQ0=sQuery(id+"F19.wireOp",EDGE,"E158.MirrorCS");var subQ1=sQuery(id+"F19.wireOp",EDGE,"E157");var subQ3=sQuery(id+"F16.wireOp",EDGE,"E151");var subQ9=makeQuery(id+"F0Hq7nSFAMYVZvY_4.2.F20.opExtrude","SWEPT_FACE",FACE,{"disambiguationData":[OSD([subQ0])]});var subQ10=makeQuery(id+"F20.opExtrude","SWEPT_FACE",FACE,{"disambiguationData":[OSD([subQ1])]});Q397=makeQuery(id+"F0Hq7nSFAMYVZvY_4.3.F20.boolean.opBoolean","SPLIT",EDGE,{"disambiguationData":[TD([subQ9])],"derivedFrom":makeQuery(id+"F0Hq7nSFAMYVZvY_4.2.F20.boolean.opBoolean","SPLIT",EDGE,{"disambiguationData":[TD([subQ10])],"derivedFrom":makeQuery(id+"F0Hq7nSFAMYVZvY_4.1.F20.boolean.opBoolean","SPLIT",EDGE,{"disambiguationData":[TD([subQ10])],"derivedFrom":makeQuery(id+"F18.boolean.opBoolean","COPY",EDGE,{"derivedFrom":makeQuery(id+"F18.opExtrude","CAP_EDGE",EDGE,{"disambiguationData":[OSD([subQ3])],"isStart":false})})})})});}
            var Q398;
            Q398=makeQuery(id+"F0Hq7nSFAMYVZvY_4.35.F20.opExtrude","SWEPT_EDGE",EDGE,{"disambiguationData":[OSD([sQuery(id+"F16.wireOp",EDGE,"E151"),sQuery(id+"F19.wireOp",EDGE,"E157")])]});
            var Q399;
            Q399=makeQuery(id+"F0Hq7nSFAMYVZvY_4.35.F20.opExtrude","SWEPT_EDGE",EDGE,{"disambiguationData":[OSD([sQuery(id+"F16.wireOp",EDGE,"E151"),sQuery(id+"F19.wireOp",EDGE,"E158.MirrorCS")])]});
            var Q400;
            Q400=makeQuery(id+"F0Hq7nSFAMYVZvY_4.35.F20.opExtrude","CAP_EDGE",EDGE,{"disambiguationData":[OSD([sQuery(id+"F19.wireOp",EDGE,"E158.MirrorCS")])],"isStart":true});
            var Q401;
            {var subQ0=sQuery(id+"F16.wireOp",EDGE,"E151");var subQ2=sQuery(id+"F19.wireOp",EDGE,"E157");var subQ4=sQuery(id+"F19.wireOp",EDGE,"E158.MirrorCS");var subQ5=makeQuery(id+"F0Hq7nSFAMYVZvY_4.34.F20.opExtrude","SWEPT_FACE",FACE,{"disambiguationData":[OSD([subQ4])]});var subQ6=makeQuery(id+"F20.opExtrude","SWEPT_FACE",FACE,{"disambiguationData":[OSD([subQ2])]});Q401=makeQuery(id+"F0Hq7nSFAMYVZvY_4.35.F20.boolean.opBoolean","SPLIT",EDGE,{"disambiguationData":[TD([subQ5])],"derivedFrom":makeQuery(id+"F0Hq7nSFAMYVZvY_4.34.F20.boolean.opBoolean","SPLIT",EDGE,{"disambiguationData":[TD([subQ6])],"derivedFrom":makeQuery(id+"F0Hq7nSFAMYVZvY_4.33.F20.boolean.opBoolean","SPLIT",EDGE,{"disambiguationData":[TD([subQ6])],"derivedFrom":makeQuery(id+"F0Hq7nSFAMYVZvY_4.32.F20.boolean.opBoolean","SPLIT",EDGE,{"disambiguationData":[TD([subQ6])],"derivedFrom":makeQuery(id+"F0Hq7nSFAMYVZvY_4.31.F20.boolean.opBoolean","SPLIT",EDGE,{"disambiguationData":[TD([subQ6])],"derivedFrom":makeQuery(id+"F0Hq7nSFAMYVZvY_4.30.F20.boolean.opBoolean","SPLIT",EDGE,{"disambiguationData":[TD([subQ6])],"derivedFrom":makeQuery(id+"F0Hq7nSFAMYVZvY_4.29.F20.boolean.opBoolean","SPLIT",EDGE,{"disambiguationData":[TD([subQ6])],"derivedFrom":makeQuery(id+"F0Hq7nSFAMYVZvY_4.28.F20.boolean.opBoolean","SPLIT",EDGE,{"disambiguationData":[TD([subQ6])],"derivedFrom":makeQuery(id+"F0Hq7nSFAMYVZvY_4.27.F20.boolean.opBoolean","SPLIT",EDGE,{"disambiguationData":[TD([subQ6])],"derivedFrom":makeQuery(id+"F0Hq7nSFAMYVZvY_4.26.F20.boolean.opBoolean","SPLIT",EDGE,{"disambiguationData":[TD([subQ6])],"derivedFrom":makeQuery(id+"F0Hq7nSFAMYVZvY_4.25.F20.boolean.opBoolean","SPLIT",EDGE,{"disambiguationData":[TD([subQ6])],"derivedFrom":makeQuery(id+"F0Hq7nSFAMYVZvY_4.24.F20.boolean.opBoolean","SPLIT",EDGE,{"disambiguationData":[TD([subQ6])],"derivedFrom":makeQuery(id+"F0Hq7nSFAMYVZvY_4.23.F20.boolean.opBoolean","SPLIT",EDGE,{"disambiguationData":[TD([subQ6])],"derivedFrom":makeQuery(id+"F0Hq7nSFAMYVZvY_4.22.F20.boolean.opBoolean","SPLIT",EDGE,{"disambiguationData":[TD([subQ6])],"derivedFrom":makeQuery(id+"F0Hq7nSFAMYVZvY_4.21.F20.boolean.opBoolean","SPLIT",EDGE,{"disambiguationData":[TD([subQ6])],"derivedFrom":makeQuery(id+"F0Hq7nSFAMYVZvY_4.20.F20.boolean.opBoolean","SPLIT",EDGE,{"disambiguationData":[TD([subQ6])],"derivedFrom":makeQuery(id+"F0Hq7nSFAMYVZvY_4.19.F20.boolean.opBoolean","SPLIT",EDGE,{"disambiguationData":[TD([subQ6])],"derivedFrom":makeQuery(id+"F0Hq7nSFAMYVZvY_4.18.F20.boolean.opBoolean","SPLIT",EDGE,{"disambiguationData":[TD([subQ6])],"derivedFrom":makeQuery(id+"F0Hq7nSFAMYVZvY_4.17.F20.boolean.opBoolean","SPLIT",EDGE,{"disambiguationData":[TD([subQ6])],"derivedFrom":makeQuery(id+"F0Hq7nSFAMYVZvY_4.16.F20.boolean.opBoolean","SPLIT",EDGE,{"disambiguationData":[TD([subQ6])],"derivedFrom":makeQuery(id+"F0Hq7nSFAMYVZvY_4.15.F20.boolean.opBoolean","SPLIT",EDGE,{"disambiguationData":[TD([subQ6])],"derivedFrom":makeQuery(id+"F0Hq7nSFAMYVZvY_4.14.F20.boolean.opBoolean","SPLIT",EDGE,{"disambiguationData":[TD([subQ6])],"derivedFrom":makeQuery(id+"F0Hq7nSFAMYVZvY_4.13.F20.boolean.opBoolean","SPLIT",EDGE,{"disambiguationData":[TD([subQ6])],"derivedFrom":makeQuery(id+"F0Hq7nSFAMYVZvY_4.12.F20.boolean.opBoolean","SPLIT",EDGE,{"disambiguationData":[TD([subQ6])],"derivedFrom":makeQuery(id+"F0Hq7nSFAMYVZvY_4.11.F20.boolean.opBoolean","SPLIT",EDGE,{"disambiguationData":[TD([subQ6])],"derivedFrom":makeQuery(id+"F0Hq7nSFAMYVZvY_4.10.F20.boolean.opBoolean","SPLIT",EDGE,{"disambiguationData":[TD([subQ6])],"derivedFrom":makeQuery(id+"F0Hq7nSFAMYVZvY_4.9.F20.boolean.opBoolean","SPLIT",EDGE,{"disambiguationData":[TD([subQ6])],"derivedFrom":makeQuery(id+"F0Hq7nSFAMYVZvY_4.8.F20.boolean.opBoolean","SPLIT",EDGE,{"disambiguationData":[TD([subQ6])],"derivedFrom":makeQuery(id+"F0Hq7nSFAMYVZvY_4.7.F20.boolean.opBoolean","SPLIT",EDGE,{"disambiguationData":[TD([subQ6])],"derivedFrom":makeQuery(id+"F0Hq7nSFAMYVZvY_4.6.F20.boolean.opBoolean","SPLIT",EDGE,{"disambiguationData":[TD([subQ6])],"derivedFrom":makeQuery(id+"F0Hq7nSFAMYVZvY_4.5.F20.boolean.opBoolean","SPLIT",EDGE,{"disambiguationData":[TD([subQ6])],"derivedFrom":makeQuery(id+"F0Hq7nSFAMYVZvY_4.4.F20.boolean.opBoolean","SPLIT",EDGE,{"disambiguationData":[TD([subQ6])],"derivedFrom":makeQuery(id+"F0Hq7nSFAMYVZvY_4.3.F20.boolean.opBoolean","SPLIT",EDGE,{"disambiguationData":[TD([subQ6])],"derivedFrom":makeQuery(id+"F0Hq7nSFAMYVZvY_4.2.F20.boolean.opBoolean","SPLIT",EDGE,{"disambiguationData":[TD([subQ6])],"derivedFrom":makeQuery(id+"F0Hq7nSFAMYVZvY_4.1.F20.boolean.opBoolean","SPLIT",EDGE,{"disambiguationData":[TD([subQ6])],"derivedFrom":makeQuery(id+"F17.boolean.opBoolean","COPY",EDGE,{"derivedFrom":makeQuery(id+"F17.opExtrude","CAP_EDGE",EDGE,{"disambiguationData":[OSD([subQ0])],"isStart":false})})})})})})})})})})})})})})})})})})})})})})})})})})})})})})})})})})})})});}
            var Q402;
            Q402=makeQuery(id+"F0Hq7nSFAMYVZvY_4.4.F20.opExtrude","SWEPT_EDGE",EDGE,{"disambiguationData":[OSD([sQuery(id+"F16.wireOp",EDGE,"E151"),sQuery(id+"F19.wireOp",EDGE,"E157")])]});
            var Q403;
            Q403=makeQuery(id+"F0Hq7nSFAMYVZvY_4.4.F20.opExtrude","SWEPT_EDGE",EDGE,{"disambiguationData":[OSD([sQuery(id+"F16.wireOp",EDGE,"E151"),sQuery(id+"F19.wireOp",EDGE,"E158.MirrorCS")])]});
            var Q404;
            Q404=makeQuery(id+"F0Hq7nSFAMYVZvY_4.4.F20.opExtrude","CAP_EDGE",EDGE,{"disambiguationData":[OSD([sQuery(id+"F19.wireOp",EDGE,"E157")])],"isStart":true});
            var Q405;
            {var subQ0=sQuery(id+"F16.wireOp",EDGE,"E151");var subQ3=sQuery(id+"F19.wireOp",EDGE,"E158.MirrorCS");var subQ4=makeQuery(id+"F0Hq7nSFAMYVZvY_4.3.F20.opExtrude","SWEPT_FACE",FACE,{"disambiguationData":[OSD([subQ3])]});var subQ5=sQuery(id+"F19.wireOp",EDGE,"E157");var subQ6=makeQuery(id+"F20.opExtrude","SWEPT_FACE",FACE,{"disambiguationData":[OSD([subQ5])]});Q405=makeQuery(id+"F0Hq7nSFAMYVZvY_4.4.F20.boolean.opBoolean","SPLIT",EDGE,{"disambiguationData":[TD([subQ4])],"derivedFrom":makeQuery(id+"F0Hq7nSFAMYVZvY_4.3.F20.boolean.opBoolean","SPLIT",EDGE,{"disambiguationData":[TD([subQ6])],"derivedFrom":makeQuery(id+"F0Hq7nSFAMYVZvY_4.2.F20.boolean.opBoolean","SPLIT",EDGE,{"disambiguationData":[TD([subQ6])],"derivedFrom":makeQuery(id+"F0Hq7nSFAMYVZvY_4.1.F20.boolean.opBoolean","SPLIT",EDGE,{"disambiguationData":[TD([subQ6])],"derivedFrom":makeQuery(id+"F17.boolean.opBoolean","COPY",EDGE,{"derivedFrom":makeQuery(id+"F17.opExtrude","CAP_EDGE",EDGE,{"disambiguationData":[OSD([subQ0])],"isStart":false})})})})})});}
            var Q406;
            {var subQ0=sQuery(id+"F19.wireOp",EDGE,"E158.MirrorCS");var subQ1=sQuery(id+"F19.wireOp",EDGE,"E157");var subQ3=sQuery(id+"F16.wireOp",EDGE,"E151");var subQ10=makeQuery(id+"F0Hq7nSFAMYVZvY_4.3.F20.opExtrude","SWEPT_FACE",FACE,{"disambiguationData":[OSD([subQ0])]});var subQ11=makeQuery(id+"F20.opExtrude","SWEPT_FACE",FACE,{"disambiguationData":[OSD([subQ1])]});Q406=makeQuery(id+"F0Hq7nSFAMYVZvY_4.4.F20.boolean.opBoolean","SPLIT",EDGE,{"disambiguationData":[TD([subQ10])],"derivedFrom":makeQuery(id+"F0Hq7nSFAMYVZvY_4.3.F20.boolean.opBoolean","SPLIT",EDGE,{"disambiguationData":[TD([subQ11])],"derivedFrom":makeQuery(id+"F0Hq7nSFAMYVZvY_4.2.F20.boolean.opBoolean","SPLIT",EDGE,{"disambiguationData":[TD([subQ11])],"derivedFrom":makeQuery(id+"F0Hq7nSFAMYVZvY_4.1.F20.boolean.opBoolean","SPLIT",EDGE,{"disambiguationData":[TD([subQ11])],"derivedFrom":makeQuery(id+"F18.boolean.opBoolean","COPY",EDGE,{"derivedFrom":makeQuery(id+"F18.opExtrude","CAP_EDGE",EDGE,{"disambiguationData":[OSD([subQ3])],"isStart":false})})})})})});}
            var Q407;
            Q407=makeQuery(id+"F0Hq7nSFAMYVZvY_4.36.F20.opExtrude","SWEPT_EDGE",EDGE,{"disambiguationData":[OSD([sQuery(id+"F16.wireOp",EDGE,"E151"),sQuery(id+"F19.wireOp",EDGE,"E157")])]});
            var Q408;
            Q408=makeQuery(id+"F0Hq7nSFAMYVZvY_4.36.F20.opExtrude","SWEPT_EDGE",EDGE,{"disambiguationData":[OSD([sQuery(id+"F16.wireOp",EDGE,"E151"),sQuery(id+"F19.wireOp",EDGE,"E158.MirrorCS")])]});
            var Q409;
            Q409=makeQuery(id+"F0Hq7nSFAMYVZvY_4.36.F20.opExtrude","CAP_EDGE",EDGE,{"disambiguationData":[OSD([sQuery(id+"F19.wireOp",EDGE,"E158.MirrorCS")])],"isStart":true});
            var Q410;
            {var subQ0=sQuery(id+"F16.wireOp",EDGE,"E151");var subQ3=sQuery(id+"F19.wireOp",EDGE,"E158.MirrorCS");var subQ4=makeQuery(id+"F0Hq7nSFAMYVZvY_4.35.F20.opExtrude","SWEPT_FACE",FACE,{"disambiguationData":[OSD([subQ3])]});var subQ5=sQuery(id+"F19.wireOp",EDGE,"E157");var subQ6=makeQuery(id+"F20.opExtrude","SWEPT_FACE",FACE,{"disambiguationData":[OSD([subQ5])]});Q410=makeQuery(id+"F0Hq7nSFAMYVZvY_4.36.F20.boolean.opBoolean","SPLIT",EDGE,{"disambiguationData":[TD([subQ4])],"derivedFrom":makeQuery(id+"F0Hq7nSFAMYVZvY_4.35.F20.boolean.opBoolean","SPLIT",EDGE,{"disambiguationData":[TD([subQ6])],"derivedFrom":makeQuery(id+"F0Hq7nSFAMYVZvY_4.34.F20.boolean.opBoolean","SPLIT",EDGE,{"disambiguationData":[TD([subQ6])],"derivedFrom":makeQuery(id+"F0Hq7nSFAMYVZvY_4.33.F20.boolean.opBoolean","SPLIT",EDGE,{"disambiguationData":[TD([subQ6])],"derivedFrom":makeQuery(id+"F0Hq7nSFAMYVZvY_4.32.F20.boolean.opBoolean","SPLIT",EDGE,{"disambiguationData":[TD([subQ6])],"derivedFrom":makeQuery(id+"F0Hq7nSFAMYVZvY_4.31.F20.boolean.opBoolean","SPLIT",EDGE,{"disambiguationData":[TD([subQ6])],"derivedFrom":makeQuery(id+"F0Hq7nSFAMYVZvY_4.30.F20.boolean.opBoolean","SPLIT",EDGE,{"disambiguationData":[TD([subQ6])],"derivedFrom":makeQuery(id+"F0Hq7nSFAMYVZvY_4.29.F20.boolean.opBoolean","SPLIT",EDGE,{"disambiguationData":[TD([subQ6])],"derivedFrom":makeQuery(id+"F0Hq7nSFAMYVZvY_4.28.F20.boolean.opBoolean","SPLIT",EDGE,{"disambiguationData":[TD([subQ6])],"derivedFrom":makeQuery(id+"F0Hq7nSFAMYVZvY_4.27.F20.boolean.opBoolean","SPLIT",EDGE,{"disambiguationData":[TD([subQ6])],"derivedFrom":makeQuery(id+"F0Hq7nSFAMYVZvY_4.26.F20.boolean.opBoolean","SPLIT",EDGE,{"disambiguationData":[TD([subQ6])],"derivedFrom":makeQuery(id+"F0Hq7nSFAMYVZvY_4.25.F20.boolean.opBoolean","SPLIT",EDGE,{"disambiguationData":[TD([subQ6])],"derivedFrom":makeQuery(id+"F0Hq7nSFAMYVZvY_4.24.F20.boolean.opBoolean","SPLIT",EDGE,{"disambiguationData":[TD([subQ6])],"derivedFrom":makeQuery(id+"F0Hq7nSFAMYVZvY_4.23.F20.boolean.opBoolean","SPLIT",EDGE,{"disambiguationData":[TD([subQ6])],"derivedFrom":makeQuery(id+"F0Hq7nSFAMYVZvY_4.22.F20.boolean.opBoolean","SPLIT",EDGE,{"disambiguationData":[TD([subQ6])],"derivedFrom":makeQuery(id+"F0Hq7nSFAMYVZvY_4.21.F20.boolean.opBoolean","SPLIT",EDGE,{"disambiguationData":[TD([subQ6])],"derivedFrom":makeQuery(id+"F0Hq7nSFAMYVZvY_4.20.F20.boolean.opBoolean","SPLIT",EDGE,{"disambiguationData":[TD([subQ6])],"derivedFrom":makeQuery(id+"F0Hq7nSFAMYVZvY_4.19.F20.boolean.opBoolean","SPLIT",EDGE,{"disambiguationData":[TD([subQ6])],"derivedFrom":makeQuery(id+"F0Hq7nSFAMYVZvY_4.18.F20.boolean.opBoolean","SPLIT",EDGE,{"disambiguationData":[TD([subQ6])],"derivedFrom":makeQuery(id+"F0Hq7nSFAMYVZvY_4.17.F20.boolean.opBoolean","SPLIT",EDGE,{"disambiguationData":[TD([subQ6])],"derivedFrom":makeQuery(id+"F0Hq7nSFAMYVZvY_4.16.F20.boolean.opBoolean","SPLIT",EDGE,{"disambiguationData":[TD([subQ6])],"derivedFrom":makeQuery(id+"F0Hq7nSFAMYVZvY_4.15.F20.boolean.opBoolean","SPLIT",EDGE,{"disambiguationData":[TD([subQ6])],"derivedFrom":makeQuery(id+"F0Hq7nSFAMYVZvY_4.14.F20.boolean.opBoolean","SPLIT",EDGE,{"disambiguationData":[TD([subQ6])],"derivedFrom":makeQuery(id+"F0Hq7nSFAMYVZvY_4.13.F20.boolean.opBoolean","SPLIT",EDGE,{"disambiguationData":[TD([subQ6])],"derivedFrom":makeQuery(id+"F0Hq7nSFAMYVZvY_4.12.F20.boolean.opBoolean","SPLIT",EDGE,{"disambiguationData":[TD([subQ6])],"derivedFrom":makeQuery(id+"F0Hq7nSFAMYVZvY_4.11.F20.boolean.opBoolean","SPLIT",EDGE,{"disambiguationData":[TD([subQ6])],"derivedFrom":makeQuery(id+"F0Hq7nSFAMYVZvY_4.10.F20.boolean.opBoolean","SPLIT",EDGE,{"disambiguationData":[TD([subQ6])],"derivedFrom":makeQuery(id+"F0Hq7nSFAMYVZvY_4.9.F20.boolean.opBoolean","SPLIT",EDGE,{"disambiguationData":[TD([subQ6])],"derivedFrom":makeQuery(id+"F0Hq7nSFAMYVZvY_4.8.F20.boolean.opBoolean","SPLIT",EDGE,{"disambiguationData":[TD([subQ6])],"derivedFrom":makeQuery(id+"F0Hq7nSFAMYVZvY_4.7.F20.boolean.opBoolean","SPLIT",EDGE,{"disambiguationData":[TD([subQ6])],"derivedFrom":makeQuery(id+"F0Hq7nSFAMYVZvY_4.6.F20.boolean.opBoolean","SPLIT",EDGE,{"disambiguationData":[TD([subQ6])],"derivedFrom":makeQuery(id+"F0Hq7nSFAMYVZvY_4.5.F20.boolean.opBoolean","SPLIT",EDGE,{"disambiguationData":[TD([subQ6])],"derivedFrom":makeQuery(id+"F0Hq7nSFAMYVZvY_4.4.F20.boolean.opBoolean","SPLIT",EDGE,{"disambiguationData":[TD([subQ6])],"derivedFrom":makeQuery(id+"F0Hq7nSFAMYVZvY_4.3.F20.boolean.opBoolean","SPLIT",EDGE,{"disambiguationData":[TD([subQ6])],"derivedFrom":makeQuery(id+"F0Hq7nSFAMYVZvY_4.2.F20.boolean.opBoolean","SPLIT",EDGE,{"disambiguationData":[TD([subQ6])],"derivedFrom":makeQuery(id+"F0Hq7nSFAMYVZvY_4.1.F20.boolean.opBoolean","SPLIT",EDGE,{"disambiguationData":[TD([subQ6])],"derivedFrom":makeQuery(id+"F17.boolean.opBoolean","COPY",EDGE,{"derivedFrom":makeQuery(id+"F17.opExtrude","CAP_EDGE",EDGE,{"disambiguationData":[OSD([subQ0])],"isStart":false})})})})})})})})})})})})})})})})})})})})})})})})})})})})})})})})})})})})})});}
            var Q411;
            Q411=makeQuery(id+"F0Hq7nSFAMYVZvY_4.37.F20.opExtrude","SWEPT_FACE",FACE,{"disambiguationData":[OSD([sQuery(id+"F19.wireOp",EDGE,"E158.MirrorCS")])]});
            var Q412;
            Q412=makeQuery(id+"F0Hq7nSFAMYVZvY_4.5.F20.opExtrude","SWEPT_EDGE",EDGE,{"disambiguationData":[OSD([sQuery(id+"F16.wireOp",EDGE,"E151"),sQuery(id+"F19.wireOp",EDGE,"E157")])]});
            var Q413;
            Q413=makeQuery(id+"F0Hq7nSFAMYVZvY_4.5.F20.opExtrude","SWEPT_EDGE",EDGE,{"disambiguationData":[OSD([sQuery(id+"F16.wireOp",EDGE,"E151"),sQuery(id+"F19.wireOp",EDGE,"E158.MirrorCS")])]});
            var Q414;
            Q414=makeQuery(id+"F0Hq7nSFAMYVZvY_4.5.F20.opExtrude","CAP_EDGE",EDGE,{"disambiguationData":[OSD([sQuery(id+"F19.wireOp",EDGE,"E157")])],"isStart":true});
            var Q415;
            {var subQ0=sQuery(id+"F16.wireOp",EDGE,"E151");var subQ2=sQuery(id+"F19.wireOp",EDGE,"E157");var subQ4=sQuery(id+"F19.wireOp",EDGE,"E158.MirrorCS");var subQ5=makeQuery(id+"F0Hq7nSFAMYVZvY_4.4.F20.opExtrude","SWEPT_FACE",FACE,{"disambiguationData":[OSD([subQ4])]});var subQ6=makeQuery(id+"F20.opExtrude","SWEPT_FACE",FACE,{"disambiguationData":[OSD([subQ2])]});Q415=makeQuery(id+"F0Hq7nSFAMYVZvY_4.5.F20.boolean.opBoolean","SPLIT",EDGE,{"disambiguationData":[TD([subQ5])],"derivedFrom":makeQuery(id+"F0Hq7nSFAMYVZvY_4.4.F20.boolean.opBoolean","SPLIT",EDGE,{"disambiguationData":[TD([subQ6])],"derivedFrom":makeQuery(id+"F0Hq7nSFAMYVZvY_4.3.F20.boolean.opBoolean","SPLIT",EDGE,{"disambiguationData":[TD([subQ6])],"derivedFrom":makeQuery(id+"F0Hq7nSFAMYVZvY_4.2.F20.boolean.opBoolean","SPLIT",EDGE,{"disambiguationData":[TD([subQ6])],"derivedFrom":makeQuery(id+"F0Hq7nSFAMYVZvY_4.1.F20.boolean.opBoolean","SPLIT",EDGE,{"disambiguationData":[TD([subQ6])],"derivedFrom":makeQuery(id+"F17.boolean.opBoolean","COPY",EDGE,{"derivedFrom":makeQuery(id+"F17.opExtrude","CAP_EDGE",EDGE,{"disambiguationData":[OSD([subQ0])],"isStart":false})})})})})})});}
            var Q416;
            Q416=makeQuery(id+"F0Hq7nSFAMYVZvY_4.37.F20.opExtrude","SWEPT_EDGE",EDGE,{"disambiguationData":[OSD([sQuery(id+"F16.wireOp",EDGE,"E151"),sQuery(id+"F19.wireOp",EDGE,"E157")])]});
            var Q417;
            Q417=makeQuery(id+"F0Hq7nSFAMYVZvY_4.37.F20.opExtrude","CAP_EDGE",EDGE,{"disambiguationData":[OSD([sQuery(id+"F19.wireOp",EDGE,"E158.MirrorCS")])],"isStart":true});
            var Q418;
            {var subQ0=sQuery(id+"F16.wireOp",EDGE,"E151");var subQ2=sQuery(id+"F19.wireOp",EDGE,"E158.MirrorCS");var subQ3=makeQuery(id+"F0Hq7nSFAMYVZvY_4.36.F20.opExtrude","SWEPT_FACE",FACE,{"disambiguationData":[OSD([subQ2])]});var subQ5=sQuery(id+"F19.wireOp",EDGE,"E157");var subQ6=makeQuery(id+"F20.opExtrude","SWEPT_FACE",FACE,{"disambiguationData":[OSD([subQ5])]});Q418=makeQuery(id+"F0Hq7nSFAMYVZvY_4.37.F20.boolean.opBoolean","SPLIT",EDGE,{"disambiguationData":[TD([subQ3])],"derivedFrom":makeQuery(id+"F0Hq7nSFAMYVZvY_4.36.F20.boolean.opBoolean","SPLIT",EDGE,{"disambiguationData":[TD([subQ6])],"derivedFrom":makeQuery(id+"F0Hq7nSFAMYVZvY_4.35.F20.boolean.opBoolean","SPLIT",EDGE,{"disambiguationData":[TD([subQ6])],"derivedFrom":makeQuery(id+"F0Hq7nSFAMYVZvY_4.34.F20.boolean.opBoolean","SPLIT",EDGE,{"disambiguationData":[TD([subQ6])],"derivedFrom":makeQuery(id+"F0Hq7nSFAMYVZvY_4.33.F20.boolean.opBoolean","SPLIT",EDGE,{"disambiguationData":[TD([subQ6])],"derivedFrom":makeQuery(id+"F0Hq7nSFAMYVZvY_4.32.F20.boolean.opBoolean","SPLIT",EDGE,{"disambiguationData":[TD([subQ6])],"derivedFrom":makeQuery(id+"F0Hq7nSFAMYVZvY_4.31.F20.boolean.opBoolean","SPLIT",EDGE,{"disambiguationData":[TD([subQ6])],"derivedFrom":makeQuery(id+"F0Hq7nSFAMYVZvY_4.30.F20.boolean.opBoolean","SPLIT",EDGE,{"disambiguationData":[TD([subQ6])],"derivedFrom":makeQuery(id+"F0Hq7nSFAMYVZvY_4.29.F20.boolean.opBoolean","SPLIT",EDGE,{"disambiguationData":[TD([subQ6])],"derivedFrom":makeQuery(id+"F0Hq7nSFAMYVZvY_4.28.F20.boolean.opBoolean","SPLIT",EDGE,{"disambiguationData":[TD([subQ6])],"derivedFrom":makeQuery(id+"F0Hq7nSFAMYVZvY_4.27.F20.boolean.opBoolean","SPLIT",EDGE,{"disambiguationData":[TD([subQ6])],"derivedFrom":makeQuery(id+"F0Hq7nSFAMYVZvY_4.26.F20.boolean.opBoolean","SPLIT",EDGE,{"disambiguationData":[TD([subQ6])],"derivedFrom":makeQuery(id+"F0Hq7nSFAMYVZvY_4.25.F20.boolean.opBoolean","SPLIT",EDGE,{"disambiguationData":[TD([subQ6])],"derivedFrom":makeQuery(id+"F0Hq7nSFAMYVZvY_4.24.F20.boolean.opBoolean","SPLIT",EDGE,{"disambiguationData":[TD([subQ6])],"derivedFrom":makeQuery(id+"F0Hq7nSFAMYVZvY_4.23.F20.boolean.opBoolean","SPLIT",EDGE,{"disambiguationData":[TD([subQ6])],"derivedFrom":makeQuery(id+"F0Hq7nSFAMYVZvY_4.22.F20.boolean.opBoolean","SPLIT",EDGE,{"disambiguationData":[TD([subQ6])],"derivedFrom":makeQuery(id+"F0Hq7nSFAMYVZvY_4.21.F20.boolean.opBoolean","SPLIT",EDGE,{"disambiguationData":[TD([subQ6])],"derivedFrom":makeQuery(id+"F0Hq7nSFAMYVZvY_4.20.F20.boolean.opBoolean","SPLIT",EDGE,{"disambiguationData":[TD([subQ6])],"derivedFrom":makeQuery(id+"F0Hq7nSFAMYVZvY_4.19.F20.boolean.opBoolean","SPLIT",EDGE,{"disambiguationData":[TD([subQ6])],"derivedFrom":makeQuery(id+"F0Hq7nSFAMYVZvY_4.18.F20.boolean.opBoolean","SPLIT",EDGE,{"disambiguationData":[TD([subQ6])],"derivedFrom":makeQuery(id+"F0Hq7nSFAMYVZvY_4.17.F20.boolean.opBoolean","SPLIT",EDGE,{"disambiguationData":[TD([subQ6])],"derivedFrom":makeQuery(id+"F0Hq7nSFAMYVZvY_4.16.F20.boolean.opBoolean","SPLIT",EDGE,{"disambiguationData":[TD([subQ6])],"derivedFrom":makeQuery(id+"F0Hq7nSFAMYVZvY_4.15.F20.boolean.opBoolean","SPLIT",EDGE,{"disambiguationData":[TD([subQ6])],"derivedFrom":makeQuery(id+"F0Hq7nSFAMYVZvY_4.14.F20.boolean.opBoolean","SPLIT",EDGE,{"disambiguationData":[TD([subQ6])],"derivedFrom":makeQuery(id+"F0Hq7nSFAMYVZvY_4.13.F20.boolean.opBoolean","SPLIT",EDGE,{"disambiguationData":[TD([subQ6])],"derivedFrom":makeQuery(id+"F0Hq7nSFAMYVZvY_4.12.F20.boolean.opBoolean","SPLIT",EDGE,{"disambiguationData":[TD([subQ6])],"derivedFrom":makeQuery(id+"F0Hq7nSFAMYVZvY_4.11.F20.boolean.opBoolean","SPLIT",EDGE,{"disambiguationData":[TD([subQ6])],"derivedFrom":makeQuery(id+"F0Hq7nSFAMYVZvY_4.10.F20.boolean.opBoolean","SPLIT",EDGE,{"disambiguationData":[TD([subQ6])],"derivedFrom":makeQuery(id+"F0Hq7nSFAMYVZvY_4.9.F20.boolean.opBoolean","SPLIT",EDGE,{"disambiguationData":[TD([subQ6])],"derivedFrom":makeQuery(id+"F0Hq7nSFAMYVZvY_4.8.F20.boolean.opBoolean","SPLIT",EDGE,{"disambiguationData":[TD([subQ6])],"derivedFrom":makeQuery(id+"F0Hq7nSFAMYVZvY_4.7.F20.boolean.opBoolean","SPLIT",EDGE,{"disambiguationData":[TD([subQ6])],"derivedFrom":makeQuery(id+"F0Hq7nSFAMYVZvY_4.6.F20.boolean.opBoolean","SPLIT",EDGE,{"disambiguationData":[TD([subQ6])],"derivedFrom":makeQuery(id+"F0Hq7nSFAMYVZvY_4.5.F20.boolean.opBoolean","SPLIT",EDGE,{"disambiguationData":[TD([subQ6])],"derivedFrom":makeQuery(id+"F0Hq7nSFAMYVZvY_4.4.F20.boolean.opBoolean","SPLIT",EDGE,{"disambiguationData":[TD([subQ6])],"derivedFrom":makeQuery(id+"F0Hq7nSFAMYVZvY_4.3.F20.boolean.opBoolean","SPLIT",EDGE,{"disambiguationData":[TD([subQ6])],"derivedFrom":makeQuery(id+"F0Hq7nSFAMYVZvY_4.2.F20.boolean.opBoolean","SPLIT",EDGE,{"disambiguationData":[TD([subQ6])],"derivedFrom":makeQuery(id+"F0Hq7nSFAMYVZvY_4.1.F20.boolean.opBoolean","SPLIT",EDGE,{"disambiguationData":[TD([subQ6])],"derivedFrom":makeQuery(id+"F17.boolean.opBoolean","COPY",EDGE,{"derivedFrom":makeQuery(id+"F17.opExtrude","CAP_EDGE",EDGE,{"disambiguationData":[OSD([subQ0])],"isStart":false})})})})})})})})})})})})})})})})})})})})})})})})})})})})})})})})})})})})})})});}
            var Q419;
            Q419=makeQuery(id+"F0Hq7nSFAMYVZvY_4.38.F20.opExtrude","SWEPT_FACE",FACE,{"disambiguationData":[OSD([sQuery(id+"F19.wireOp",EDGE,"E158.MirrorCS")])]});
            var Q420;
            Q420=makeQuery(id+"F0Hq7nSFAMYVZvY_4.6.F20.opExtrude","SWEPT_EDGE",EDGE,{"disambiguationData":[OSD([sQuery(id+"F16.wireOp",EDGE,"E151"),sQuery(id+"F19.wireOp",EDGE,"E157")])]});
            var Q421;
            Q421=makeQuery(id+"F0Hq7nSFAMYVZvY_4.6.F20.opExtrude","SWEPT_EDGE",EDGE,{"disambiguationData":[OSD([sQuery(id+"F16.wireOp",EDGE,"E151"),sQuery(id+"F19.wireOp",EDGE,"E158.MirrorCS")])]});
            var Q422;
            Q422=makeQuery(id+"F0Hq7nSFAMYVZvY_4.6.F20.opExtrude","CAP_EDGE",EDGE,{"disambiguationData":[OSD([sQuery(id+"F19.wireOp",EDGE,"E157")])],"isStart":true});
            var Q423;
            {var subQ0=sQuery(id+"F16.wireOp",EDGE,"E151");var subQ3=sQuery(id+"F19.wireOp",EDGE,"E158.MirrorCS");var subQ4=makeQuery(id+"F0Hq7nSFAMYVZvY_4.5.F20.opExtrude","SWEPT_FACE",FACE,{"disambiguationData":[OSD([subQ3])]});var subQ5=sQuery(id+"F19.wireOp",EDGE,"E157");var subQ6=makeQuery(id+"F20.opExtrude","SWEPT_FACE",FACE,{"disambiguationData":[OSD([subQ5])]});Q423=makeQuery(id+"F0Hq7nSFAMYVZvY_4.6.F20.boolean.opBoolean","SPLIT",EDGE,{"disambiguationData":[TD([subQ4])],"derivedFrom":makeQuery(id+"F0Hq7nSFAMYVZvY_4.5.F20.boolean.opBoolean","SPLIT",EDGE,{"disambiguationData":[TD([subQ6])],"derivedFrom":makeQuery(id+"F0Hq7nSFAMYVZvY_4.4.F20.boolean.opBoolean","SPLIT",EDGE,{"disambiguationData":[TD([subQ6])],"derivedFrom":makeQuery(id+"F0Hq7nSFAMYVZvY_4.3.F20.boolean.opBoolean","SPLIT",EDGE,{"disambiguationData":[TD([subQ6])],"derivedFrom":makeQuery(id+"F0Hq7nSFAMYVZvY_4.2.F20.boolean.opBoolean","SPLIT",EDGE,{"disambiguationData":[TD([subQ6])],"derivedFrom":makeQuery(id+"F0Hq7nSFAMYVZvY_4.1.F20.boolean.opBoolean","SPLIT",EDGE,{"disambiguationData":[TD([subQ6])],"derivedFrom":makeQuery(id+"F17.boolean.opBoolean","COPY",EDGE,{"derivedFrom":makeQuery(id+"F17.opExtrude","CAP_EDGE",EDGE,{"disambiguationData":[OSD([subQ0])],"isStart":false})})})})})})})});}
            var Q424;
            Q424=makeQuery(id+"F0Hq7nSFAMYVZvY_4.38.F20.opExtrude","SWEPT_EDGE",EDGE,{"disambiguationData":[OSD([sQuery(id+"F16.wireOp",EDGE,"E151"),sQuery(id+"F19.wireOp",EDGE,"E157")])]});
            var Q425;
            Q425=makeQuery(id+"F0Hq7nSFAMYVZvY_4.38.F20.opExtrude","SWEPT_EDGE",EDGE,{"disambiguationData":[OSD([sQuery(id+"F16.wireOp",EDGE,"E151"),sQuery(id+"F19.wireOp",EDGE,"E158.MirrorCS")])]});
            var Q426;
            Q426=makeQuery(id+"F0Hq7nSFAMYVZvY_4.38.F20.opExtrude","CAP_EDGE",EDGE,{"disambiguationData":[OSD([sQuery(id+"F19.wireOp",EDGE,"E158.MirrorCS")])],"isStart":true});
            var Q427;
            {var subQ0=sQuery(id+"F19.wireOp",EDGE,"E158.MirrorCS");var subQ1=sQuery(id+"F19.wireOp",EDGE,"E157");var subQ3=sQuery(id+"F16.wireOp",EDGE,"E151");var subQ27=makeQuery(id+"F0Hq7nSFAMYVZvY_4.37.F20.opExtrude","SWEPT_FACE",FACE,{"disambiguationData":[OSD([subQ0])]});var subQ45=makeQuery(id+"F20.opExtrude","SWEPT_FACE",FACE,{"disambiguationData":[OSD([subQ1])]});Q427=makeQuery(id+"F0Hq7nSFAMYVZvY_4.38.F20.boolean.opBoolean","SPLIT",FACE,{"disambiguationData":[TD([subQ27])],"derivedFrom":makeQuery(id+"F0Hq7nSFAMYVZvY_4.37.F20.boolean.opBoolean","SPLIT",FACE,{"disambiguationData":[TD([subQ45])],"derivedFrom":makeQuery(id+"F0Hq7nSFAMYVZvY_4.36.F20.boolean.opBoolean","SPLIT",FACE,{"disambiguationData":[TD([subQ45])],"derivedFrom":makeQuery(id+"F0Hq7nSFAMYVZvY_4.35.F20.boolean.opBoolean","SPLIT",FACE,{"disambiguationData":[TD([subQ45])],"derivedFrom":makeQuery(id+"F0Hq7nSFAMYVZvY_4.34.F20.boolean.opBoolean","SPLIT",FACE,{"disambiguationData":[TD([subQ45])],"derivedFrom":makeQuery(id+"F0Hq7nSFAMYVZvY_4.33.F20.boolean.opBoolean","SPLIT",FACE,{"disambiguationData":[TD([subQ45])],"derivedFrom":makeQuery(id+"F0Hq7nSFAMYVZvY_4.32.F20.boolean.opBoolean","SPLIT",FACE,{"disambiguationData":[TD([subQ45])],"derivedFrom":makeQuery(id+"F0Hq7nSFAMYVZvY_4.31.F20.boolean.opBoolean","SPLIT",FACE,{"disambiguationData":[TD([subQ45])],"derivedFrom":makeQuery(id+"F0Hq7nSFAMYVZvY_4.30.F20.boolean.opBoolean","SPLIT",FACE,{"disambiguationData":[TD([subQ45])],"derivedFrom":makeQuery(id+"F0Hq7nSFAMYVZvY_4.29.F20.boolean.opBoolean","SPLIT",FACE,{"disambiguationData":[TD([subQ45])],"derivedFrom":makeQuery(id+"F0Hq7nSFAMYVZvY_4.28.F20.boolean.opBoolean","SPLIT",FACE,{"disambiguationData":[TD([subQ45])],"derivedFrom":makeQuery(id+"F0Hq7nSFAMYVZvY_4.27.F20.boolean.opBoolean","SPLIT",FACE,{"disambiguationData":[TD([subQ45])],"derivedFrom":makeQuery(id+"F0Hq7nSFAMYVZvY_4.26.F20.boolean.opBoolean","SPLIT",FACE,{"disambiguationData":[TD([subQ45])],"derivedFrom":makeQuery(id+"F0Hq7nSFAMYVZvY_4.25.F20.boolean.opBoolean","SPLIT",FACE,{"disambiguationData":[TD([subQ45])],"derivedFrom":makeQuery(id+"F0Hq7nSFAMYVZvY_4.24.F20.boolean.opBoolean","SPLIT",FACE,{"disambiguationData":[TD([subQ45])],"derivedFrom":makeQuery(id+"F0Hq7nSFAMYVZvY_4.23.F20.boolean.opBoolean","SPLIT",FACE,{"disambiguationData":[TD([subQ45])],"derivedFrom":makeQuery(id+"F0Hq7nSFAMYVZvY_4.22.F20.boolean.opBoolean","SPLIT",FACE,{"disambiguationData":[TD([subQ45])],"derivedFrom":makeQuery(id+"F0Hq7nSFAMYVZvY_4.21.F20.boolean.opBoolean","SPLIT",FACE,{"disambiguationData":[TD([subQ45])],"derivedFrom":makeQuery(id+"F0Hq7nSFAMYVZvY_4.20.F20.boolean.opBoolean","SPLIT",FACE,{"disambiguationData":[TD([subQ45])],"derivedFrom":makeQuery(id+"F0Hq7nSFAMYVZvY_4.19.F20.boolean.opBoolean","SPLIT",FACE,{"disambiguationData":[TD([subQ45])],"derivedFrom":makeQuery(id+"F0Hq7nSFAMYVZvY_4.18.F20.boolean.opBoolean","SPLIT",FACE,{"disambiguationData":[TD([subQ45])],"derivedFrom":makeQuery(id+"F0Hq7nSFAMYVZvY_4.17.F20.boolean.opBoolean","SPLIT",FACE,{"disambiguationData":[TD([subQ45])],"derivedFrom":makeQuery(id+"F0Hq7nSFAMYVZvY_4.16.F20.boolean.opBoolean","SPLIT",FACE,{"disambiguationData":[TD([subQ45])],"derivedFrom":makeQuery(id+"F0Hq7nSFAMYVZvY_4.15.F20.boolean.opBoolean","SPLIT",FACE,{"disambiguationData":[TD([subQ45])],"derivedFrom":makeQuery(id+"F0Hq7nSFAMYVZvY_4.14.F20.boolean.opBoolean","SPLIT",FACE,{"disambiguationData":[TD([subQ45])],"derivedFrom":makeQuery(id+"F0Hq7nSFAMYVZvY_4.13.F20.boolean.opBoolean","SPLIT",FACE,{"disambiguationData":[TD([subQ45])],"derivedFrom":makeQuery(id+"F0Hq7nSFAMYVZvY_4.12.F20.boolean.opBoolean","SPLIT",FACE,{"disambiguationData":[TD([subQ45])],"derivedFrom":makeQuery(id+"F0Hq7nSFAMYVZvY_4.11.F20.boolean.opBoolean","SPLIT",FACE,{"disambiguationData":[TD([subQ45])],"derivedFrom":makeQuery(id+"F0Hq7nSFAMYVZvY_4.10.F20.boolean.opBoolean","SPLIT",FACE,{"disambiguationData":[TD([subQ45])],"derivedFrom":makeQuery(id+"F0Hq7nSFAMYVZvY_4.9.F20.boolean.opBoolean","SPLIT",FACE,{"disambiguationData":[TD([subQ45])],"derivedFrom":makeQuery(id+"F0Hq7nSFAMYVZvY_4.8.F20.boolean.opBoolean","SPLIT",FACE,{"disambiguationData":[TD([subQ45])],"derivedFrom":makeQuery(id+"F0Hq7nSFAMYVZvY_4.7.F20.boolean.opBoolean","SPLIT",FACE,{"disambiguationData":[TD([subQ45])],"derivedFrom":makeQuery(id+"F0Hq7nSFAMYVZvY_4.6.F20.boolean.opBoolean","SPLIT",FACE,{"disambiguationData":[TD([subQ45])],"derivedFrom":makeQuery(id+"F0Hq7nSFAMYVZvY_4.5.F20.boolean.opBoolean","SPLIT",FACE,{"disambiguationData":[TD([subQ45])],"derivedFrom":makeQuery(id+"F0Hq7nSFAMYVZvY_4.4.F20.boolean.opBoolean","SPLIT",FACE,{"disambiguationData":[TD([subQ45])],"derivedFrom":makeQuery(id+"F0Hq7nSFAMYVZvY_4.3.F20.boolean.opBoolean","SPLIT",FACE,{"disambiguationData":[TD([subQ45])],"derivedFrom":makeQuery(id+"F0Hq7nSFAMYVZvY_4.2.F20.boolean.opBoolean","SPLIT",FACE,{"disambiguationData":[TD([subQ45])],"derivedFrom":makeQuery(id+"F0Hq7nSFAMYVZvY_4.1.F20.boolean.opBoolean","SPLIT",FACE,{"disambiguationData":[TD([subQ45])],"derivedFrom":makeQuery(id+"F17.boolean.opBoolean","COPY",FACE,{"derivedFrom":makeQuery(id+"F17.opExtrude","SWEPT_FACE",FACE,{"disambiguationData":[OSD([subQ3])]})})})})})})})})})})})})})})})})})})})})})})})})})})})})})})})})})})})})})})})});}
            var Q428;
            {var subQ0=sQuery(id+"F16.wireOp",EDGE,"E151");var subQ3=sQuery(id+"F19.wireOp",EDGE,"E157");var subQ4=sQuery(id+"F19.wireOp",EDGE,"E158.MirrorCS");var subQ5=makeQuery(id+"F0Hq7nSFAMYVZvY_4.37.F20.opExtrude","SWEPT_FACE",FACE,{"disambiguationData":[OSD([subQ4])]});var subQ6=makeQuery(id+"F20.opExtrude","SWEPT_FACE",FACE,{"disambiguationData":[OSD([subQ3])]});Q428=makeQuery(id+"F0Hq7nSFAMYVZvY_4.38.F20.boolean.opBoolean","SPLIT",EDGE,{"disambiguationData":[TD([subQ5])],"derivedFrom":makeQuery(id+"F0Hq7nSFAMYVZvY_4.37.F20.boolean.opBoolean","SPLIT",EDGE,{"disambiguationData":[TD([subQ6])],"derivedFrom":makeQuery(id+"F0Hq7nSFAMYVZvY_4.36.F20.boolean.opBoolean","SPLIT",EDGE,{"disambiguationData":[TD([subQ6])],"derivedFrom":makeQuery(id+"F0Hq7nSFAMYVZvY_4.35.F20.boolean.opBoolean","SPLIT",EDGE,{"disambiguationData":[TD([subQ6])],"derivedFrom":makeQuery(id+"F0Hq7nSFAMYVZvY_4.34.F20.boolean.opBoolean","SPLIT",EDGE,{"disambiguationData":[TD([subQ6])],"derivedFrom":makeQuery(id+"F0Hq7nSFAMYVZvY_4.33.F20.boolean.opBoolean","SPLIT",EDGE,{"disambiguationData":[TD([subQ6])],"derivedFrom":makeQuery(id+"F0Hq7nSFAMYVZvY_4.32.F20.boolean.opBoolean","SPLIT",EDGE,{"disambiguationData":[TD([subQ6])],"derivedFrom":makeQuery(id+"F0Hq7nSFAMYVZvY_4.31.F20.boolean.opBoolean","SPLIT",EDGE,{"disambiguationData":[TD([subQ6])],"derivedFrom":makeQuery(id+"F0Hq7nSFAMYVZvY_4.30.F20.boolean.opBoolean","SPLIT",EDGE,{"disambiguationData":[TD([subQ6])],"derivedFrom":makeQuery(id+"F0Hq7nSFAMYVZvY_4.29.F20.boolean.opBoolean","SPLIT",EDGE,{"disambiguationData":[TD([subQ6])],"derivedFrom":makeQuery(id+"F0Hq7nSFAMYVZvY_4.28.F20.boolean.opBoolean","SPLIT",EDGE,{"disambiguationData":[TD([subQ6])],"derivedFrom":makeQuery(id+"F0Hq7nSFAMYVZvY_4.27.F20.boolean.opBoolean","SPLIT",EDGE,{"disambiguationData":[TD([subQ6])],"derivedFrom":makeQuery(id+"F0Hq7nSFAMYVZvY_4.26.F20.boolean.opBoolean","SPLIT",EDGE,{"disambiguationData":[TD([subQ6])],"derivedFrom":makeQuery(id+"F0Hq7nSFAMYVZvY_4.25.F20.boolean.opBoolean","SPLIT",EDGE,{"disambiguationData":[TD([subQ6])],"derivedFrom":makeQuery(id+"F0Hq7nSFAMYVZvY_4.24.F20.boolean.opBoolean","SPLIT",EDGE,{"disambiguationData":[TD([subQ6])],"derivedFrom":makeQuery(id+"F0Hq7nSFAMYVZvY_4.23.F20.boolean.opBoolean","SPLIT",EDGE,{"disambiguationData":[TD([subQ6])],"derivedFrom":makeQuery(id+"F0Hq7nSFAMYVZvY_4.22.F20.boolean.opBoolean","SPLIT",EDGE,{"disambiguationData":[TD([subQ6])],"derivedFrom":makeQuery(id+"F0Hq7nSFAMYVZvY_4.21.F20.boolean.opBoolean","SPLIT",EDGE,{"disambiguationData":[TD([subQ6])],"derivedFrom":makeQuery(id+"F0Hq7nSFAMYVZvY_4.20.F20.boolean.opBoolean","SPLIT",EDGE,{"disambiguationData":[TD([subQ6])],"derivedFrom":makeQuery(id+"F0Hq7nSFAMYVZvY_4.19.F20.boolean.opBoolean","SPLIT",EDGE,{"disambiguationData":[TD([subQ6])],"derivedFrom":makeQuery(id+"F0Hq7nSFAMYVZvY_4.18.F20.boolean.opBoolean","SPLIT",EDGE,{"disambiguationData":[TD([subQ6])],"derivedFrom":makeQuery(id+"F0Hq7nSFAMYVZvY_4.17.F20.boolean.opBoolean","SPLIT",EDGE,{"disambiguationData":[TD([subQ6])],"derivedFrom":makeQuery(id+"F0Hq7nSFAMYVZvY_4.16.F20.boolean.opBoolean","SPLIT",EDGE,{"disambiguationData":[TD([subQ6])],"derivedFrom":makeQuery(id+"F0Hq7nSFAMYVZvY_4.15.F20.boolean.opBoolean","SPLIT",EDGE,{"disambiguationData":[TD([subQ6])],"derivedFrom":makeQuery(id+"F0Hq7nSFAMYVZvY_4.14.F20.boolean.opBoolean","SPLIT",EDGE,{"disambiguationData":[TD([subQ6])],"derivedFrom":makeQuery(id+"F0Hq7nSFAMYVZvY_4.13.F20.boolean.opBoolean","SPLIT",EDGE,{"disambiguationData":[TD([subQ6])],"derivedFrom":makeQuery(id+"F0Hq7nSFAMYVZvY_4.12.F20.boolean.opBoolean","SPLIT",EDGE,{"disambiguationData":[TD([subQ6])],"derivedFrom":makeQuery(id+"F0Hq7nSFAMYVZvY_4.11.F20.boolean.opBoolean","SPLIT",EDGE,{"disambiguationData":[TD([subQ6])],"derivedFrom":makeQuery(id+"F0Hq7nSFAMYVZvY_4.10.F20.boolean.opBoolean","SPLIT",EDGE,{"disambiguationData":[TD([subQ6])],"derivedFrom":makeQuery(id+"F0Hq7nSFAMYVZvY_4.9.F20.boolean.opBoolean","SPLIT",EDGE,{"disambiguationData":[TD([subQ6])],"derivedFrom":makeQuery(id+"F0Hq7nSFAMYVZvY_4.8.F20.boolean.opBoolean","SPLIT",EDGE,{"disambiguationData":[TD([subQ6])],"derivedFrom":makeQuery(id+"F0Hq7nSFAMYVZvY_4.7.F20.boolean.opBoolean","SPLIT",EDGE,{"disambiguationData":[TD([subQ6])],"derivedFrom":makeQuery(id+"F0Hq7nSFAMYVZvY_4.6.F20.boolean.opBoolean","SPLIT",EDGE,{"disambiguationData":[TD([subQ6])],"derivedFrom":makeQuery(id+"F0Hq7nSFAMYVZvY_4.5.F20.boolean.opBoolean","SPLIT",EDGE,{"disambiguationData":[TD([subQ6])],"derivedFrom":makeQuery(id+"F0Hq7nSFAMYVZvY_4.4.F20.boolean.opBoolean","SPLIT",EDGE,{"disambiguationData":[TD([subQ6])],"derivedFrom":makeQuery(id+"F0Hq7nSFAMYVZvY_4.3.F20.boolean.opBoolean","SPLIT",EDGE,{"disambiguationData":[TD([subQ6])],"derivedFrom":makeQuery(id+"F0Hq7nSFAMYVZvY_4.2.F20.boolean.opBoolean","SPLIT",EDGE,{"disambiguationData":[TD([subQ6])],"derivedFrom":makeQuery(id+"F0Hq7nSFAMYVZvY_4.1.F20.boolean.opBoolean","SPLIT",EDGE,{"disambiguationData":[TD([subQ6])],"derivedFrom":makeQuery(id+"F17.boolean.opBoolean","COPY",EDGE,{"derivedFrom":makeQuery(id+"F17.opExtrude","CAP_EDGE",EDGE,{"disambiguationData":[OSD([subQ0])],"isStart":false})})})})})})})})})})})})})})})})})})})})})})})})})})})})})})})})})})})})})})})});}
            var Q429;
            Q429=makeQuery(id+"F0Hq7nSFAMYVZvY_4.39.F20.opExtrude","SWEPT_FACE",FACE,{"disambiguationData":[OSD([sQuery(id+"F19.wireOp",EDGE,"E158.MirrorCS")])]});
            var Q430;
            Q430=makeQuery(id+"F0Hq7nSFAMYVZvY_4.39.F20.opExtrude","CAP_EDGE",EDGE,{"disambiguationData":[OSD([sQuery(id+"F19.wireOp",EDGE,"E158.MirrorCS")])],"isStart":false});
            var Q431;
            Q431=makeQuery(id+"F0Hq7nSFAMYVZvY_4.7.F20.opExtrude","SWEPT_EDGE",EDGE,{"disambiguationData":[OSD([sQuery(id+"F16.wireOp",EDGE,"E151"),sQuery(id+"F19.wireOp",EDGE,"E157")])]});
            var Q432;
            Q432=makeQuery(id+"F0Hq7nSFAMYVZvY_4.7.F20.opExtrude","SWEPT_EDGE",EDGE,{"disambiguationData":[OSD([sQuery(id+"F16.wireOp",EDGE,"E151"),sQuery(id+"F19.wireOp",EDGE,"E158.MirrorCS")])]});
            var Q433;
            Q433=makeQuery(id+"F0Hq7nSFAMYVZvY_4.7.F20.opExtrude","CAP_EDGE",EDGE,{"disambiguationData":[OSD([sQuery(id+"F19.wireOp",EDGE,"E157")])],"isStart":true});
            var Q434;
            {var subQ0=sQuery(id+"F16.wireOp",EDGE,"E151");var subQ2=sQuery(id+"F19.wireOp",EDGE,"E158.MirrorCS");var subQ3=makeQuery(id+"F0Hq7nSFAMYVZvY_4.6.F20.opExtrude","SWEPT_FACE",FACE,{"disambiguationData":[OSD([subQ2])]});var subQ5=sQuery(id+"F19.wireOp",EDGE,"E157");var subQ6=makeQuery(id+"F20.opExtrude","SWEPT_FACE",FACE,{"disambiguationData":[OSD([subQ5])]});Q434=makeQuery(id+"F0Hq7nSFAMYVZvY_4.7.F20.boolean.opBoolean","SPLIT",EDGE,{"disambiguationData":[TD([subQ3])],"derivedFrom":makeQuery(id+"F0Hq7nSFAMYVZvY_4.6.F20.boolean.opBoolean","SPLIT",EDGE,{"disambiguationData":[TD([subQ6])],"derivedFrom":makeQuery(id+"F0Hq7nSFAMYVZvY_4.5.F20.boolean.opBoolean","SPLIT",EDGE,{"disambiguationData":[TD([subQ6])],"derivedFrom":makeQuery(id+"F0Hq7nSFAMYVZvY_4.4.F20.boolean.opBoolean","SPLIT",EDGE,{"disambiguationData":[TD([subQ6])],"derivedFrom":makeQuery(id+"F0Hq7nSFAMYVZvY_4.3.F20.boolean.opBoolean","SPLIT",EDGE,{"disambiguationData":[TD([subQ6])],"derivedFrom":makeQuery(id+"F0Hq7nSFAMYVZvY_4.2.F20.boolean.opBoolean","SPLIT",EDGE,{"disambiguationData":[TD([subQ6])],"derivedFrom":makeQuery(id+"F0Hq7nSFAMYVZvY_4.1.F20.boolean.opBoolean","SPLIT",EDGE,{"disambiguationData":[TD([subQ6])],"derivedFrom":makeQuery(id+"F17.boolean.opBoolean","COPY",EDGE,{"derivedFrom":makeQuery(id+"F17.opExtrude","CAP_EDGE",EDGE,{"disambiguationData":[OSD([subQ0])],"isStart":false})})})})})})})})});}
            var Q435;
            {var subQ0=sQuery(id+"F19.wireOp",EDGE,"E158.MirrorCS");var subQ1=sQuery(id+"F19.wireOp",EDGE,"E157");var subQ3=sQuery(id+"F16.wireOp",EDGE,"E151");var subQ8=makeQuery(id+"F0Hq7nSFAMYVZvY_4.6.F20.opExtrude","SWEPT_FACE",FACE,{"disambiguationData":[OSD([subQ0])]});var subQ14=makeQuery(id+"F20.opExtrude","SWEPT_FACE",FACE,{"disambiguationData":[OSD([subQ1])]});Q435=makeQuery(id+"F0Hq7nSFAMYVZvY_4.7.F20.boolean.opBoolean","SPLIT",EDGE,{"disambiguationData":[TD([subQ8])],"derivedFrom":makeQuery(id+"F0Hq7nSFAMYVZvY_4.6.F20.boolean.opBoolean","SPLIT",EDGE,{"disambiguationData":[TD([subQ14])],"derivedFrom":makeQuery(id+"F0Hq7nSFAMYVZvY_4.5.F20.boolean.opBoolean","SPLIT",EDGE,{"disambiguationData":[TD([subQ14])],"derivedFrom":makeQuery(id+"F0Hq7nSFAMYVZvY_4.4.F20.boolean.opBoolean","SPLIT",EDGE,{"disambiguationData":[TD([subQ14])],"derivedFrom":makeQuery(id+"F0Hq7nSFAMYVZvY_4.3.F20.boolean.opBoolean","SPLIT",EDGE,{"disambiguationData":[TD([subQ14])],"derivedFrom":makeQuery(id+"F0Hq7nSFAMYVZvY_4.2.F20.boolean.opBoolean","SPLIT",EDGE,{"disambiguationData":[TD([subQ14])],"derivedFrom":makeQuery(id+"F0Hq7nSFAMYVZvY_4.1.F20.boolean.opBoolean","SPLIT",EDGE,{"disambiguationData":[TD([subQ14])],"derivedFrom":makeQuery(id+"F18.boolean.opBoolean","COPY",EDGE,{"derivedFrom":makeQuery(id+"F18.opExtrude","CAP_EDGE",EDGE,{"disambiguationData":[OSD([subQ3])],"isStart":false})})})})})})})})});}
            var Q436;
            Q436=makeQuery(id+"F0Hq7nSFAMYVZvY_4.39.F20.opExtrude","SWEPT_EDGE",EDGE,{"disambiguationData":[OSD([sQuery(id+"F16.wireOp",EDGE,"E151"),sQuery(id+"F19.wireOp",EDGE,"E157")])]});
            var Q437;
            Q437=makeQuery(id+"F0Hq7nSFAMYVZvY_4.39.F20.opExtrude","CAP_EDGE",EDGE,{"disambiguationData":[OSD([sQuery(id+"F19.wireOp",EDGE,"E158.MirrorCS")])],"isStart":true});
            var Q438;
            {var subQ0=sQuery(id+"F16.wireOp",EDGE,"E151");var subQ2=makeQuery(id+"F20.opExtrude","SWEPT_FACE",FACE,{"disambiguationData":[OSD([sQuery(id+"F19.wireOp",EDGE,"E157")])]});Q438=makeQuery(id+"F0Hq7nSFAMYVZvY_4.39.F20.boolean.opBoolean","SPLIT",EDGE,{"disambiguationData":[TD([subQ2])],"derivedFrom":makeQuery(id+"F0Hq7nSFAMYVZvY_4.38.F20.boolean.opBoolean","SPLIT",EDGE,{"disambiguationData":[TD([subQ2])],"derivedFrom":makeQuery(id+"F0Hq7nSFAMYVZvY_4.37.F20.boolean.opBoolean","SPLIT",EDGE,{"disambiguationData":[TD([subQ2])],"derivedFrom":makeQuery(id+"F0Hq7nSFAMYVZvY_4.36.F20.boolean.opBoolean","SPLIT",EDGE,{"disambiguationData":[TD([subQ2])],"derivedFrom":makeQuery(id+"F0Hq7nSFAMYVZvY_4.35.F20.boolean.opBoolean","SPLIT",EDGE,{"disambiguationData":[TD([subQ2])],"derivedFrom":makeQuery(id+"F0Hq7nSFAMYVZvY_4.34.F20.boolean.opBoolean","SPLIT",EDGE,{"disambiguationData":[TD([subQ2])],"derivedFrom":makeQuery(id+"F0Hq7nSFAMYVZvY_4.33.F20.boolean.opBoolean","SPLIT",EDGE,{"disambiguationData":[TD([subQ2])],"derivedFrom":makeQuery(id+"F0Hq7nSFAMYVZvY_4.32.F20.boolean.opBoolean","SPLIT",EDGE,{"disambiguationData":[TD([subQ2])],"derivedFrom":makeQuery(id+"F0Hq7nSFAMYVZvY_4.31.F20.boolean.opBoolean","SPLIT",EDGE,{"disambiguationData":[TD([subQ2])],"derivedFrom":makeQuery(id+"F0Hq7nSFAMYVZvY_4.30.F20.boolean.opBoolean","SPLIT",EDGE,{"disambiguationData":[TD([subQ2])],"derivedFrom":makeQuery(id+"F0Hq7nSFAMYVZvY_4.29.F20.boolean.opBoolean","SPLIT",EDGE,{"disambiguationData":[TD([subQ2])],"derivedFrom":makeQuery(id+"F0Hq7nSFAMYVZvY_4.28.F20.boolean.opBoolean","SPLIT",EDGE,{"disambiguationData":[TD([subQ2])],"derivedFrom":makeQuery(id+"F0Hq7nSFAMYVZvY_4.27.F20.boolean.opBoolean","SPLIT",EDGE,{"disambiguationData":[TD([subQ2])],"derivedFrom":makeQuery(id+"F0Hq7nSFAMYVZvY_4.26.F20.boolean.opBoolean","SPLIT",EDGE,{"disambiguationData":[TD([subQ2])],"derivedFrom":makeQuery(id+"F0Hq7nSFAMYVZvY_4.25.F20.boolean.opBoolean","SPLIT",EDGE,{"disambiguationData":[TD([subQ2])],"derivedFrom":makeQuery(id+"F0Hq7nSFAMYVZvY_4.24.F20.boolean.opBoolean","SPLIT",EDGE,{"disambiguationData":[TD([subQ2])],"derivedFrom":makeQuery(id+"F0Hq7nSFAMYVZvY_4.23.F20.boolean.opBoolean","SPLIT",EDGE,{"disambiguationData":[TD([subQ2])],"derivedFrom":makeQuery(id+"F0Hq7nSFAMYVZvY_4.22.F20.boolean.opBoolean","SPLIT",EDGE,{"disambiguationData":[TD([subQ2])],"derivedFrom":makeQuery(id+"F0Hq7nSFAMYVZvY_4.21.F20.boolean.opBoolean","SPLIT",EDGE,{"disambiguationData":[TD([subQ2])],"derivedFrom":makeQuery(id+"F0Hq7nSFAMYVZvY_4.20.F20.boolean.opBoolean","SPLIT",EDGE,{"disambiguationData":[TD([subQ2])],"derivedFrom":makeQuery(id+"F0Hq7nSFAMYVZvY_4.19.F20.boolean.opBoolean","SPLIT",EDGE,{"disambiguationData":[TD([subQ2])],"derivedFrom":makeQuery(id+"F0Hq7nSFAMYVZvY_4.18.F20.boolean.opBoolean","SPLIT",EDGE,{"disambiguationData":[TD([subQ2])],"derivedFrom":makeQuery(id+"F0Hq7nSFAMYVZvY_4.17.F20.boolean.opBoolean","SPLIT",EDGE,{"disambiguationData":[TD([subQ2])],"derivedFrom":makeQuery(id+"F0Hq7nSFAMYVZvY_4.16.F20.boolean.opBoolean","SPLIT",EDGE,{"disambiguationData":[TD([subQ2])],"derivedFrom":makeQuery(id+"F0Hq7nSFAMYVZvY_4.15.F20.boolean.opBoolean","SPLIT",EDGE,{"disambiguationData":[TD([subQ2])],"derivedFrom":makeQuery(id+"F0Hq7nSFAMYVZvY_4.14.F20.boolean.opBoolean","SPLIT",EDGE,{"disambiguationData":[TD([subQ2])],"derivedFrom":makeQuery(id+"F0Hq7nSFAMYVZvY_4.13.F20.boolean.opBoolean","SPLIT",EDGE,{"disambiguationData":[TD([subQ2])],"derivedFrom":makeQuery(id+"F0Hq7nSFAMYVZvY_4.12.F20.boolean.opBoolean","SPLIT",EDGE,{"disambiguationData":[TD([subQ2])],"derivedFrom":makeQuery(id+"F0Hq7nSFAMYVZvY_4.11.F20.boolean.opBoolean","SPLIT",EDGE,{"disambiguationData":[TD([subQ2])],"derivedFrom":makeQuery(id+"F0Hq7nSFAMYVZvY_4.10.F20.boolean.opBoolean","SPLIT",EDGE,{"disambiguationData":[TD([subQ2])],"derivedFrom":makeQuery(id+"F0Hq7nSFAMYVZvY_4.9.F20.boolean.opBoolean","SPLIT",EDGE,{"disambiguationData":[TD([subQ2])],"derivedFrom":makeQuery(id+"F0Hq7nSFAMYVZvY_4.8.F20.boolean.opBoolean","SPLIT",EDGE,{"disambiguationData":[TD([subQ2])],"derivedFrom":makeQuery(id+"F0Hq7nSFAMYVZvY_4.7.F20.boolean.opBoolean","SPLIT",EDGE,{"disambiguationData":[TD([subQ2])],"derivedFrom":makeQuery(id+"F0Hq7nSFAMYVZvY_4.6.F20.boolean.opBoolean","SPLIT",EDGE,{"disambiguationData":[TD([subQ2])],"derivedFrom":makeQuery(id+"F0Hq7nSFAMYVZvY_4.5.F20.boolean.opBoolean","SPLIT",EDGE,{"disambiguationData":[TD([subQ2])],"derivedFrom":makeQuery(id+"F0Hq7nSFAMYVZvY_4.4.F20.boolean.opBoolean","SPLIT",EDGE,{"disambiguationData":[TD([subQ2])],"derivedFrom":makeQuery(id+"F0Hq7nSFAMYVZvY_4.3.F20.boolean.opBoolean","SPLIT",EDGE,{"disambiguationData":[TD([subQ2])],"derivedFrom":makeQuery(id+"F0Hq7nSFAMYVZvY_4.2.F20.boolean.opBoolean","SPLIT",EDGE,{"disambiguationData":[TD([subQ2])],"derivedFrom":makeQuery(id+"F0Hq7nSFAMYVZvY_4.1.F20.boolean.opBoolean","SPLIT",EDGE,{"disambiguationData":[TD([subQ2])],"derivedFrom":makeQuery(id+"F17.boolean.opBoolean","COPY",EDGE,{"derivedFrom":makeQuery(id+"F17.opExtrude","CAP_EDGE",EDGE,{"disambiguationData":[OSD([subQ0])],"isStart":false})})})})})})})})})})})})})})})})})})})})})})})})})})})})})})})})})})})})})})})})});}
            var Q439;
            {var subQ0=sQuery(id+"F16.wireOp",EDGE,"E151");var subQ3=sQuery(id+"F19.wireOp",EDGE,"E158.MirrorCS");var subQ4=makeQuery(id+"F0Hq7nSFAMYVZvY_4.38.F20.opExtrude","SWEPT_FACE",FACE,{"disambiguationData":[OSD([subQ3])]});var subQ5=sQuery(id+"F19.wireOp",EDGE,"E157");var subQ6=makeQuery(id+"F20.opExtrude","SWEPT_FACE",FACE,{"disambiguationData":[OSD([subQ5])]});Q439=makeQuery(id+"F0Hq7nSFAMYVZvY_4.39.F20.boolean.opBoolean","SPLIT",EDGE,{"disambiguationData":[TD([subQ4])],"derivedFrom":makeQuery(id+"F0Hq7nSFAMYVZvY_4.38.F20.boolean.opBoolean","SPLIT",EDGE,{"disambiguationData":[TD([subQ6])],"derivedFrom":makeQuery(id+"F0Hq7nSFAMYVZvY_4.37.F20.boolean.opBoolean","SPLIT",EDGE,{"disambiguationData":[TD([subQ6])],"derivedFrom":makeQuery(id+"F0Hq7nSFAMYVZvY_4.36.F20.boolean.opBoolean","SPLIT",EDGE,{"disambiguationData":[TD([subQ6])],"derivedFrom":makeQuery(id+"F0Hq7nSFAMYVZvY_4.35.F20.boolean.opBoolean","SPLIT",EDGE,{"disambiguationData":[TD([subQ6])],"derivedFrom":makeQuery(id+"F0Hq7nSFAMYVZvY_4.34.F20.boolean.opBoolean","SPLIT",EDGE,{"disambiguationData":[TD([subQ6])],"derivedFrom":makeQuery(id+"F0Hq7nSFAMYVZvY_4.33.F20.boolean.opBoolean","SPLIT",EDGE,{"disambiguationData":[TD([subQ6])],"derivedFrom":makeQuery(id+"F0Hq7nSFAMYVZvY_4.32.F20.boolean.opBoolean","SPLIT",EDGE,{"disambiguationData":[TD([subQ6])],"derivedFrom":makeQuery(id+"F0Hq7nSFAMYVZvY_4.31.F20.boolean.opBoolean","SPLIT",EDGE,{"disambiguationData":[TD([subQ6])],"derivedFrom":makeQuery(id+"F0Hq7nSFAMYVZvY_4.30.F20.boolean.opBoolean","SPLIT",EDGE,{"disambiguationData":[TD([subQ6])],"derivedFrom":makeQuery(id+"F0Hq7nSFAMYVZvY_4.29.F20.boolean.opBoolean","SPLIT",EDGE,{"disambiguationData":[TD([subQ6])],"derivedFrom":makeQuery(id+"F0Hq7nSFAMYVZvY_4.28.F20.boolean.opBoolean","SPLIT",EDGE,{"disambiguationData":[TD([subQ6])],"derivedFrom":makeQuery(id+"F0Hq7nSFAMYVZvY_4.27.F20.boolean.opBoolean","SPLIT",EDGE,{"disambiguationData":[TD([subQ6])],"derivedFrom":makeQuery(id+"F0Hq7nSFAMYVZvY_4.26.F20.boolean.opBoolean","SPLIT",EDGE,{"disambiguationData":[TD([subQ6])],"derivedFrom":makeQuery(id+"F0Hq7nSFAMYVZvY_4.25.F20.boolean.opBoolean","SPLIT",EDGE,{"disambiguationData":[TD([subQ6])],"derivedFrom":makeQuery(id+"F0Hq7nSFAMYVZvY_4.24.F20.boolean.opBoolean","SPLIT",EDGE,{"disambiguationData":[TD([subQ6])],"derivedFrom":makeQuery(id+"F0Hq7nSFAMYVZvY_4.23.F20.boolean.opBoolean","SPLIT",EDGE,{"disambiguationData":[TD([subQ6])],"derivedFrom":makeQuery(id+"F0Hq7nSFAMYVZvY_4.22.F20.boolean.opBoolean","SPLIT",EDGE,{"disambiguationData":[TD([subQ6])],"derivedFrom":makeQuery(id+"F0Hq7nSFAMYVZvY_4.21.F20.boolean.opBoolean","SPLIT",EDGE,{"disambiguationData":[TD([subQ6])],"derivedFrom":makeQuery(id+"F0Hq7nSFAMYVZvY_4.20.F20.boolean.opBoolean","SPLIT",EDGE,{"disambiguationData":[TD([subQ6])],"derivedFrom":makeQuery(id+"F0Hq7nSFAMYVZvY_4.19.F20.boolean.opBoolean","SPLIT",EDGE,{"disambiguationData":[TD([subQ6])],"derivedFrom":makeQuery(id+"F0Hq7nSFAMYVZvY_4.18.F20.boolean.opBoolean","SPLIT",EDGE,{"disambiguationData":[TD([subQ6])],"derivedFrom":makeQuery(id+"F0Hq7nSFAMYVZvY_4.17.F20.boolean.opBoolean","SPLIT",EDGE,{"disambiguationData":[TD([subQ6])],"derivedFrom":makeQuery(id+"F0Hq7nSFAMYVZvY_4.16.F20.boolean.opBoolean","SPLIT",EDGE,{"disambiguationData":[TD([subQ6])],"derivedFrom":makeQuery(id+"F0Hq7nSFAMYVZvY_4.15.F20.boolean.opBoolean","SPLIT",EDGE,{"disambiguationData":[TD([subQ6])],"derivedFrom":makeQuery(id+"F0Hq7nSFAMYVZvY_4.14.F20.boolean.opBoolean","SPLIT",EDGE,{"disambiguationData":[TD([subQ6])],"derivedFrom":makeQuery(id+"F0Hq7nSFAMYVZvY_4.13.F20.boolean.opBoolean","SPLIT",EDGE,{"disambiguationData":[TD([subQ6])],"derivedFrom":makeQuery(id+"F0Hq7nSFAMYVZvY_4.12.F20.boolean.opBoolean","SPLIT",EDGE,{"disambiguationData":[TD([subQ6])],"derivedFrom":makeQuery(id+"F0Hq7nSFAMYVZvY_4.11.F20.boolean.opBoolean","SPLIT",EDGE,{"disambiguationData":[TD([subQ6])],"derivedFrom":makeQuery(id+"F0Hq7nSFAMYVZvY_4.10.F20.boolean.opBoolean","SPLIT",EDGE,{"disambiguationData":[TD([subQ6])],"derivedFrom":makeQuery(id+"F0Hq7nSFAMYVZvY_4.9.F20.boolean.opBoolean","SPLIT",EDGE,{"disambiguationData":[TD([subQ6])],"derivedFrom":makeQuery(id+"F0Hq7nSFAMYVZvY_4.8.F20.boolean.opBoolean","SPLIT",EDGE,{"disambiguationData":[TD([subQ6])],"derivedFrom":makeQuery(id+"F0Hq7nSFAMYVZvY_4.7.F20.boolean.opBoolean","SPLIT",EDGE,{"disambiguationData":[TD([subQ6])],"derivedFrom":makeQuery(id+"F0Hq7nSFAMYVZvY_4.6.F20.boolean.opBoolean","SPLIT",EDGE,{"disambiguationData":[TD([subQ6])],"derivedFrom":makeQuery(id+"F0Hq7nSFAMYVZvY_4.5.F20.boolean.opBoolean","SPLIT",EDGE,{"disambiguationData":[TD([subQ6])],"derivedFrom":makeQuery(id+"F0Hq7nSFAMYVZvY_4.4.F20.boolean.opBoolean","SPLIT",EDGE,{"disambiguationData":[TD([subQ6])],"derivedFrom":makeQuery(id+"F0Hq7nSFAMYVZvY_4.3.F20.boolean.opBoolean","SPLIT",EDGE,{"disambiguationData":[TD([subQ6])],"derivedFrom":makeQuery(id+"F0Hq7nSFAMYVZvY_4.2.F20.boolean.opBoolean","SPLIT",EDGE,{"disambiguationData":[TD([subQ6])],"derivedFrom":makeQuery(id+"F0Hq7nSFAMYVZvY_4.1.F20.boolean.opBoolean","SPLIT",EDGE,{"disambiguationData":[TD([subQ6])],"derivedFrom":makeQuery(id+"F17.boolean.opBoolean","COPY",EDGE,{"derivedFrom":makeQuery(id+"F17.opExtrude","CAP_EDGE",EDGE,{"disambiguationData":[OSD([subQ0])],"isStart":false})})})})})})})})})})})})})})})})})})})})})})})})})})})})})})})})})})})})})})})})});}
            var Q440;
            {var subQ0=sQuery(id+"F19.wireOp",EDGE,"E158.MirrorCS");var subQ1=sQuery(id+"F19.wireOp",EDGE,"E157");var subQ3=sQuery(id+"F16.wireOp",EDGE,"E151");var subQ28=makeQuery(id+"F0Hq7nSFAMYVZvY_4.38.F20.opExtrude","SWEPT_FACE",FACE,{"disambiguationData":[OSD([subQ0])]});var subQ46=makeQuery(id+"F20.opExtrude","SWEPT_FACE",FACE,{"disambiguationData":[OSD([subQ1])]});Q440=makeQuery(id+"F0Hq7nSFAMYVZvY_4.39.F20.boolean.opBoolean","SPLIT",EDGE,{"disambiguationData":[TD([subQ28])],"derivedFrom":makeQuery(id+"F0Hq7nSFAMYVZvY_4.38.F20.boolean.opBoolean","SPLIT",EDGE,{"disambiguationData":[TD([subQ46])],"derivedFrom":makeQuery(id+"F0Hq7nSFAMYVZvY_4.37.F20.boolean.opBoolean","SPLIT",EDGE,{"disambiguationData":[TD([subQ46])],"derivedFrom":makeQuery(id+"F0Hq7nSFAMYVZvY_4.36.F20.boolean.opBoolean","SPLIT",EDGE,{"disambiguationData":[TD([subQ46])],"derivedFrom":makeQuery(id+"F0Hq7nSFAMYVZvY_4.35.F20.boolean.opBoolean","SPLIT",EDGE,{"disambiguationData":[TD([subQ46])],"derivedFrom":makeQuery(id+"F0Hq7nSFAMYVZvY_4.34.F20.boolean.opBoolean","SPLIT",EDGE,{"disambiguationData":[TD([subQ46])],"derivedFrom":makeQuery(id+"F0Hq7nSFAMYVZvY_4.33.F20.boolean.opBoolean","SPLIT",EDGE,{"disambiguationData":[TD([subQ46])],"derivedFrom":makeQuery(id+"F0Hq7nSFAMYVZvY_4.32.F20.boolean.opBoolean","SPLIT",EDGE,{"disambiguationData":[TD([subQ46])],"derivedFrom":makeQuery(id+"F0Hq7nSFAMYVZvY_4.31.F20.boolean.opBoolean","SPLIT",EDGE,{"disambiguationData":[TD([subQ46])],"derivedFrom":makeQuery(id+"F0Hq7nSFAMYVZvY_4.30.F20.boolean.opBoolean","SPLIT",EDGE,{"disambiguationData":[TD([subQ46])],"derivedFrom":makeQuery(id+"F0Hq7nSFAMYVZvY_4.29.F20.boolean.opBoolean","SPLIT",EDGE,{"disambiguationData":[TD([subQ46])],"derivedFrom":makeQuery(id+"F0Hq7nSFAMYVZvY_4.28.F20.boolean.opBoolean","SPLIT",EDGE,{"disambiguationData":[TD([subQ46])],"derivedFrom":makeQuery(id+"F0Hq7nSFAMYVZvY_4.27.F20.boolean.opBoolean","SPLIT",EDGE,{"disambiguationData":[TD([subQ46])],"derivedFrom":makeQuery(id+"F0Hq7nSFAMYVZvY_4.26.F20.boolean.opBoolean","SPLIT",EDGE,{"disambiguationData":[TD([subQ46])],"derivedFrom":makeQuery(id+"F0Hq7nSFAMYVZvY_4.25.F20.boolean.opBoolean","SPLIT",EDGE,{"disambiguationData":[TD([subQ46])],"derivedFrom":makeQuery(id+"F0Hq7nSFAMYVZvY_4.24.F20.boolean.opBoolean","SPLIT",EDGE,{"disambiguationData":[TD([subQ46])],"derivedFrom":makeQuery(id+"F0Hq7nSFAMYVZvY_4.23.F20.boolean.opBoolean","SPLIT",EDGE,{"disambiguationData":[TD([subQ46])],"derivedFrom":makeQuery(id+"F0Hq7nSFAMYVZvY_4.22.F20.boolean.opBoolean","SPLIT",EDGE,{"disambiguationData":[TD([subQ46])],"derivedFrom":makeQuery(id+"F0Hq7nSFAMYVZvY_4.21.F20.boolean.opBoolean","SPLIT",EDGE,{"disambiguationData":[TD([subQ46])],"derivedFrom":makeQuery(id+"F0Hq7nSFAMYVZvY_4.20.F20.boolean.opBoolean","SPLIT",EDGE,{"disambiguationData":[TD([subQ46])],"derivedFrom":makeQuery(id+"F0Hq7nSFAMYVZvY_4.19.F20.boolean.opBoolean","SPLIT",EDGE,{"disambiguationData":[TD([subQ46])],"derivedFrom":makeQuery(id+"F0Hq7nSFAMYVZvY_4.18.F20.boolean.opBoolean","SPLIT",EDGE,{"disambiguationData":[TD([subQ46])],"derivedFrom":makeQuery(id+"F0Hq7nSFAMYVZvY_4.17.F20.boolean.opBoolean","SPLIT",EDGE,{"disambiguationData":[TD([subQ46])],"derivedFrom":makeQuery(id+"F0Hq7nSFAMYVZvY_4.16.F20.boolean.opBoolean","SPLIT",EDGE,{"disambiguationData":[TD([subQ46])],"derivedFrom":makeQuery(id+"F0Hq7nSFAMYVZvY_4.15.F20.boolean.opBoolean","SPLIT",EDGE,{"disambiguationData":[TD([subQ46])],"derivedFrom":makeQuery(id+"F0Hq7nSFAMYVZvY_4.14.F20.boolean.opBoolean","SPLIT",EDGE,{"disambiguationData":[TD([subQ46])],"derivedFrom":makeQuery(id+"F0Hq7nSFAMYVZvY_4.13.F20.boolean.opBoolean","SPLIT",EDGE,{"disambiguationData":[TD([subQ46])],"derivedFrom":makeQuery(id+"F0Hq7nSFAMYVZvY_4.12.F20.boolean.opBoolean","SPLIT",EDGE,{"disambiguationData":[TD([subQ46])],"derivedFrom":makeQuery(id+"F0Hq7nSFAMYVZvY_4.11.F20.boolean.opBoolean","SPLIT",EDGE,{"disambiguationData":[TD([subQ46])],"derivedFrom":makeQuery(id+"F0Hq7nSFAMYVZvY_4.10.F20.boolean.opBoolean","SPLIT",EDGE,{"disambiguationData":[TD([subQ46])],"derivedFrom":makeQuery(id+"F0Hq7nSFAMYVZvY_4.9.F20.boolean.opBoolean","SPLIT",EDGE,{"disambiguationData":[TD([subQ46])],"derivedFrom":makeQuery(id+"F0Hq7nSFAMYVZvY_4.8.F20.boolean.opBoolean","SPLIT",EDGE,{"disambiguationData":[TD([subQ46])],"derivedFrom":makeQuery(id+"F0Hq7nSFAMYVZvY_4.7.F20.boolean.opBoolean","SPLIT",EDGE,{"disambiguationData":[TD([subQ46])],"derivedFrom":makeQuery(id+"F0Hq7nSFAMYVZvY_4.6.F20.boolean.opBoolean","SPLIT",EDGE,{"disambiguationData":[TD([subQ46])],"derivedFrom":makeQuery(id+"F0Hq7nSFAMYVZvY_4.5.F20.boolean.opBoolean","SPLIT",EDGE,{"disambiguationData":[TD([subQ46])],"derivedFrom":makeQuery(id+"F0Hq7nSFAMYVZvY_4.4.F20.boolean.opBoolean","SPLIT",EDGE,{"disambiguationData":[TD([subQ46])],"derivedFrom":makeQuery(id+"F0Hq7nSFAMYVZvY_4.3.F20.boolean.opBoolean","SPLIT",EDGE,{"disambiguationData":[TD([subQ46])],"derivedFrom":makeQuery(id+"F0Hq7nSFAMYVZvY_4.2.F20.boolean.opBoolean","SPLIT",EDGE,{"disambiguationData":[TD([subQ46])],"derivedFrom":makeQuery(id+"F0Hq7nSFAMYVZvY_4.1.F20.boolean.opBoolean","SPLIT",EDGE,{"disambiguationData":[TD([subQ46])],"derivedFrom":makeQuery(id+"F18.boolean.opBoolean","COPY",EDGE,{"derivedFrom":makeQuery(id+"F18.opExtrude","CAP_EDGE",EDGE,{"disambiguationData":[OSD([subQ3])],"isStart":false})})})})})})})})})})})})})})})})})})})})})})})})})})})})})})})})})})})})})})})})});}
            var Q441;
            Q441=makeQuery(id+"F0Hq7nSFAMYVZvY_4.8.F20.opExtrude","SWEPT_EDGE",EDGE,{"disambiguationData":[OSD([sQuery(id+"F16.wireOp",EDGE,"E151"),sQuery(id+"F19.wireOp",EDGE,"E157")])]});
            var Q442;
            Q442=makeQuery(id+"F0Hq7nSFAMYVZvY_4.8.F20.opExtrude","SWEPT_EDGE",EDGE,{"disambiguationData":[OSD([sQuery(id+"F16.wireOp",EDGE,"E151"),sQuery(id+"F19.wireOp",EDGE,"E158.MirrorCS")])]});
            var Q443;
            Q443=makeQuery(id+"F0Hq7nSFAMYVZvY_4.8.F20.opExtrude","CAP_EDGE",EDGE,{"disambiguationData":[OSD([sQuery(id+"F19.wireOp",EDGE,"E157")])],"isStart":true});
            var Q444;
            Q444=makeQuery(id+"F0Hq7nSFAMYVZvY_4.8.F20.opExtrude","CAP_EDGE",EDGE,{"disambiguationData":[OSD([sQuery(id+"F19.wireOp",EDGE,"E158.MirrorCS")])],"isStart":true});
            var Q445;
            {var subQ0=sQuery(id+"F16.wireOp",EDGE,"E151");var subQ3=sQuery(id+"F19.wireOp",EDGE,"E157");var subQ4=sQuery(id+"F19.wireOp",EDGE,"E158.MirrorCS");var subQ5=makeQuery(id+"F0Hq7nSFAMYVZvY_4.7.F20.opExtrude","SWEPT_FACE",FACE,{"disambiguationData":[OSD([subQ4])]});var subQ6=makeQuery(id+"F20.opExtrude","SWEPT_FACE",FACE,{"disambiguationData":[OSD([subQ3])]});Q445=makeQuery(id+"F0Hq7nSFAMYVZvY_4.8.F20.boolean.opBoolean","SPLIT",EDGE,{"disambiguationData":[TD([subQ5])],"derivedFrom":makeQuery(id+"F0Hq7nSFAMYVZvY_4.7.F20.boolean.opBoolean","SPLIT",EDGE,{"disambiguationData":[TD([subQ6])],"derivedFrom":makeQuery(id+"F0Hq7nSFAMYVZvY_4.6.F20.boolean.opBoolean","SPLIT",EDGE,{"disambiguationData":[TD([subQ6])],"derivedFrom":makeQuery(id+"F0Hq7nSFAMYVZvY_4.5.F20.boolean.opBoolean","SPLIT",EDGE,{"disambiguationData":[TD([subQ6])],"derivedFrom":makeQuery(id+"F0Hq7nSFAMYVZvY_4.4.F20.boolean.opBoolean","SPLIT",EDGE,{"disambiguationData":[TD([subQ6])],"derivedFrom":makeQuery(id+"F0Hq7nSFAMYVZvY_4.3.F20.boolean.opBoolean","SPLIT",EDGE,{"disambiguationData":[TD([subQ6])],"derivedFrom":makeQuery(id+"F0Hq7nSFAMYVZvY_4.2.F20.boolean.opBoolean","SPLIT",EDGE,{"disambiguationData":[TD([subQ6])],"derivedFrom":makeQuery(id+"F0Hq7nSFAMYVZvY_4.1.F20.boolean.opBoolean","SPLIT",EDGE,{"disambiguationData":[TD([subQ6])],"derivedFrom":makeQuery(id+"F17.boolean.opBoolean","COPY",EDGE,{"derivedFrom":makeQuery(id+"F17.opExtrude","CAP_EDGE",EDGE,{"disambiguationData":[OSD([subQ0])],"isStart":false})})})})})})})})})});}
            var Q446;
            {var subQ0=sQuery(id+"F19.wireOp",EDGE,"E158.MirrorCS");var subQ1=sQuery(id+"F19.wireOp",EDGE,"E157");var subQ3=sQuery(id+"F16.wireOp",EDGE,"E151");var subQ14=makeQuery(id+"F0Hq7nSFAMYVZvY_4.7.F20.opExtrude","SWEPT_FACE",FACE,{"disambiguationData":[OSD([subQ0])]});var subQ15=makeQuery(id+"F20.opExtrude","SWEPT_FACE",FACE,{"disambiguationData":[OSD([subQ1])]});Q446=makeQuery(id+"F0Hq7nSFAMYVZvY_4.8.F20.boolean.opBoolean","SPLIT",EDGE,{"disambiguationData":[TD([subQ14])],"derivedFrom":makeQuery(id+"F0Hq7nSFAMYVZvY_4.7.F20.boolean.opBoolean","SPLIT",EDGE,{"disambiguationData":[TD([subQ15])],"derivedFrom":makeQuery(id+"F0Hq7nSFAMYVZvY_4.6.F20.boolean.opBoolean","SPLIT",EDGE,{"disambiguationData":[TD([subQ15])],"derivedFrom":makeQuery(id+"F0Hq7nSFAMYVZvY_4.5.F20.boolean.opBoolean","SPLIT",EDGE,{"disambiguationData":[TD([subQ15])],"derivedFrom":makeQuery(id+"F0Hq7nSFAMYVZvY_4.4.F20.boolean.opBoolean","SPLIT",EDGE,{"disambiguationData":[TD([subQ15])],"derivedFrom":makeQuery(id+"F0Hq7nSFAMYVZvY_4.3.F20.boolean.opBoolean","SPLIT",EDGE,{"disambiguationData":[TD([subQ15])],"derivedFrom":makeQuery(id+"F0Hq7nSFAMYVZvY_4.2.F20.boolean.opBoolean","SPLIT",EDGE,{"disambiguationData":[TD([subQ15])],"derivedFrom":makeQuery(id+"F0Hq7nSFAMYVZvY_4.1.F20.boolean.opBoolean","SPLIT",EDGE,{"disambiguationData":[TD([subQ15])],"derivedFrom":makeQuery(id+"F18.boolean.opBoolean","COPY",EDGE,{"derivedFrom":makeQuery(id+"F18.opExtrude","CAP_EDGE",EDGE,{"disambiguationData":[OSD([subQ3])],"isStart":false})})})})})})})})})});}
            var Q447;
            Q447=makeQuery(id+"F0Hq7nSFAMYVZvY_4.9.F20.opExtrude","SWEPT_FACE",FACE,{"disambiguationData":[OSD([sQuery(id+"F19.wireOp",EDGE,"E157")])]});
            var Q448;
            Q448=makeQuery(id+"F0Hq7nSFAMYVZvY_4.9.F20.opExtrude","CAP_EDGE",EDGE,{"disambiguationData":[OSD([sQuery(id+"F19.wireOp",EDGE,"E157")])],"isStart":false});
            var Q449;
            Q449=makeQuery(id+"F0Hq7nSFAMYVZvY_4.9.F20.opExtrude","CAP_EDGE",EDGE,{"disambiguationData":[OSD([sQuery(id+"F19.wireOp",EDGE,"E157")])],"isStart":true});
            var Q450;
            Q450=makeQuery(id+"F0Hq7nSFAMYVZvY_4.9.F20.opExtrude","CAP_EDGE",EDGE,{"disambiguationData":[OSD([sQuery(id+"F19.wireOp",EDGE,"E158.MirrorCS")])],"isStart":true});
            var Q451;
            {var subQ0=sQuery(id+"F19.wireOp",EDGE,"E158.MirrorCS");var subQ1=sQuery(id+"F19.wireOp",EDGE,"E157");var subQ3=sQuery(id+"F16.wireOp",EDGE,"E151");var subQ15=makeQuery(id+"F0Hq7nSFAMYVZvY_4.8.F20.opExtrude","SWEPT_FACE",FACE,{"disambiguationData":[OSD([subQ0])]});var subQ16=makeQuery(id+"F20.opExtrude","SWEPT_FACE",FACE,{"disambiguationData":[OSD([subQ1])]});Q451=makeQuery(id+"F0Hq7nSFAMYVZvY_4.9.F20.boolean.opBoolean","SPLIT",FACE,{"disambiguationData":[TD([subQ15])],"derivedFrom":makeQuery(id+"F0Hq7nSFAMYVZvY_4.8.F20.boolean.opBoolean","SPLIT",FACE,{"disambiguationData":[TD([subQ16])],"derivedFrom":makeQuery(id+"F0Hq7nSFAMYVZvY_4.7.F20.boolean.opBoolean","SPLIT",FACE,{"disambiguationData":[TD([subQ16])],"derivedFrom":makeQuery(id+"F0Hq7nSFAMYVZvY_4.6.F20.boolean.opBoolean","SPLIT",FACE,{"disambiguationData":[TD([subQ16])],"derivedFrom":makeQuery(id+"F0Hq7nSFAMYVZvY_4.5.F20.boolean.opBoolean","SPLIT",FACE,{"disambiguationData":[TD([subQ16])],"derivedFrom":makeQuery(id+"F0Hq7nSFAMYVZvY_4.4.F20.boolean.opBoolean","SPLIT",FACE,{"disambiguationData":[TD([subQ16])],"derivedFrom":makeQuery(id+"F0Hq7nSFAMYVZvY_4.3.F20.boolean.opBoolean","SPLIT",FACE,{"disambiguationData":[TD([subQ16])],"derivedFrom":makeQuery(id+"F0Hq7nSFAMYVZvY_4.2.F20.boolean.opBoolean","SPLIT",FACE,{"disambiguationData":[TD([subQ16])],"derivedFrom":makeQuery(id+"F0Hq7nSFAMYVZvY_4.1.F20.boolean.opBoolean","SPLIT",FACE,{"disambiguationData":[TD([subQ16])],"derivedFrom":makeQuery(id+"F17.boolean.opBoolean","COPY",FACE,{"derivedFrom":makeQuery(id+"F17.opExtrude","SWEPT_FACE",FACE,{"disambiguationData":[OSD([subQ3])]})})})})})})})})})})});}
            var Q452;
            {var subQ0=sQuery(id+"F16.wireOp",EDGE,"E151");var subQ3=sQuery(id+"F19.wireOp",EDGE,"E158.MirrorCS");var subQ4=makeQuery(id+"F0Hq7nSFAMYVZvY_4.8.F20.opExtrude","SWEPT_FACE",FACE,{"disambiguationData":[OSD([subQ3])]});var subQ5=sQuery(id+"F19.wireOp",EDGE,"E157");var subQ6=makeQuery(id+"F20.opExtrude","SWEPT_FACE",FACE,{"disambiguationData":[OSD([subQ5])]});Q452=makeQuery(id+"F0Hq7nSFAMYVZvY_4.9.F20.boolean.opBoolean","SPLIT",EDGE,{"disambiguationData":[TD([subQ4])],"derivedFrom":makeQuery(id+"F0Hq7nSFAMYVZvY_4.8.F20.boolean.opBoolean","SPLIT",EDGE,{"disambiguationData":[TD([subQ6])],"derivedFrom":makeQuery(id+"F0Hq7nSFAMYVZvY_4.7.F20.boolean.opBoolean","SPLIT",EDGE,{"disambiguationData":[TD([subQ6])],"derivedFrom":makeQuery(id+"F0Hq7nSFAMYVZvY_4.6.F20.boolean.opBoolean","SPLIT",EDGE,{"disambiguationData":[TD([subQ6])],"derivedFrom":makeQuery(id+"F0Hq7nSFAMYVZvY_4.5.F20.boolean.opBoolean","SPLIT",EDGE,{"disambiguationData":[TD([subQ6])],"derivedFrom":makeQuery(id+"F0Hq7nSFAMYVZvY_4.4.F20.boolean.opBoolean","SPLIT",EDGE,{"disambiguationData":[TD([subQ6])],"derivedFrom":makeQuery(id+"F0Hq7nSFAMYVZvY_4.3.F20.boolean.opBoolean","SPLIT",EDGE,{"disambiguationData":[TD([subQ6])],"derivedFrom":makeQuery(id+"F0Hq7nSFAMYVZvY_4.2.F20.boolean.opBoolean","SPLIT",EDGE,{"disambiguationData":[TD([subQ6])],"derivedFrom":makeQuery(id+"F0Hq7nSFAMYVZvY_4.1.F20.boolean.opBoolean","SPLIT",EDGE,{"disambiguationData":[TD([subQ6])],"derivedFrom":makeQuery(id+"F17.boolean.opBoolean","COPY",EDGE,{"derivedFrom":makeQuery(id+"F17.opExtrude","CAP_EDGE",EDGE,{"disambiguationData":[OSD([subQ0])],"isStart":false})})})})})})})})})})});}
            var Q453;
            Q453=makeQuery(id+"F0Hq7nSFAMYVZvY_4.10.F20.opExtrude","SWEPT_FACE",FACE,{"disambiguationData":[OSD([sQuery(id+"F19.wireOp",EDGE,"E157")])]});
            var Q454;
            Q454=makeQuery(id+"F0Hq7nSFAMYVZvY_4.10.F20.opExtrude","CAP_EDGE",EDGE,{"disambiguationData":[OSD([sQuery(id+"F19.wireOp",EDGE,"E157")])],"isStart":false});
            var Q455;
            Q455=makeQuery(id+"F0Hq7nSFAMYVZvY_4.10.F20.opExtrude","CAP_EDGE",EDGE,{"disambiguationData":[OSD([sQuery(id+"F19.wireOp",EDGE,"E158.MirrorCS")])],"isStart":true});
            var Q456;
            {var subQ0=sQuery(id+"F19.wireOp",EDGE,"E158.MirrorCS");var subQ1=sQuery(id+"F19.wireOp",EDGE,"E157");var subQ3=sQuery(id+"F16.wireOp",EDGE,"E151");var subQ16=makeQuery(id+"F0Hq7nSFAMYVZvY_4.9.F20.opExtrude","SWEPT_FACE",FACE,{"disambiguationData":[OSD([subQ0])]});var subQ17=makeQuery(id+"F20.opExtrude","SWEPT_FACE",FACE,{"disambiguationData":[OSD([subQ1])]});Q456=makeQuery(id+"F0Hq7nSFAMYVZvY_4.10.F20.boolean.opBoolean","SPLIT",FACE,{"disambiguationData":[TD([subQ16])],"derivedFrom":makeQuery(id+"F0Hq7nSFAMYVZvY_4.9.F20.boolean.opBoolean","SPLIT",FACE,{"disambiguationData":[TD([subQ17])],"derivedFrom":makeQuery(id+"F0Hq7nSFAMYVZvY_4.8.F20.boolean.opBoolean","SPLIT",FACE,{"disambiguationData":[TD([subQ17])],"derivedFrom":makeQuery(id+"F0Hq7nSFAMYVZvY_4.7.F20.boolean.opBoolean","SPLIT",FACE,{"disambiguationData":[TD([subQ17])],"derivedFrom":makeQuery(id+"F0Hq7nSFAMYVZvY_4.6.F20.boolean.opBoolean","SPLIT",FACE,{"disambiguationData":[TD([subQ17])],"derivedFrom":makeQuery(id+"F0Hq7nSFAMYVZvY_4.5.F20.boolean.opBoolean","SPLIT",FACE,{"disambiguationData":[TD([subQ17])],"derivedFrom":makeQuery(id+"F0Hq7nSFAMYVZvY_4.4.F20.boolean.opBoolean","SPLIT",FACE,{"disambiguationData":[TD([subQ17])],"derivedFrom":makeQuery(id+"F0Hq7nSFAMYVZvY_4.3.F20.boolean.opBoolean","SPLIT",FACE,{"disambiguationData":[TD([subQ17])],"derivedFrom":makeQuery(id+"F0Hq7nSFAMYVZvY_4.2.F20.boolean.opBoolean","SPLIT",FACE,{"disambiguationData":[TD([subQ17])],"derivedFrom":makeQuery(id+"F0Hq7nSFAMYVZvY_4.1.F20.boolean.opBoolean","SPLIT",FACE,{"disambiguationData":[TD([subQ17])],"derivedFrom":makeQuery(id+"F17.boolean.opBoolean","COPY",FACE,{"derivedFrom":makeQuery(id+"F17.opExtrude","SWEPT_FACE",FACE,{"disambiguationData":[OSD([subQ3])]})})})})})})})})})})})});}
            var Q457;
            Q457=makeQuery(id+"F0Hq7nSFAMYVZvY_4.11.F20.opExtrude","SWEPT_FACE",FACE,{"disambiguationData":[OSD([sQuery(id+"F19.wireOp",EDGE,"E157")])]});
            var Q458;
            Q458=makeQuery(id+"F0Hq7nSFAMYVZvY_4.11.F20.opExtrude","CAP_EDGE",EDGE,{"disambiguationData":[OSD([sQuery(id+"F19.wireOp",EDGE,"E158.MirrorCS")])],"isStart":true});
            var Q459;
            {var subQ0=sQuery(id+"F19.wireOp",EDGE,"E158.MirrorCS");var subQ1=sQuery(id+"F19.wireOp",EDGE,"E157");var subQ3=sQuery(id+"F16.wireOp",EDGE,"E151");var subQ17=makeQuery(id+"F0Hq7nSFAMYVZvY_4.10.F20.opExtrude","SWEPT_FACE",FACE,{"disambiguationData":[OSD([subQ0])]});var subQ18=makeQuery(id+"F20.opExtrude","SWEPT_FACE",FACE,{"disambiguationData":[OSD([subQ1])]});Q459=makeQuery(id+"F0Hq7nSFAMYVZvY_4.11.F20.boolean.opBoolean","SPLIT",FACE,{"disambiguationData":[TD([subQ17])],"derivedFrom":makeQuery(id+"F0Hq7nSFAMYVZvY_4.10.F20.boolean.opBoolean","SPLIT",FACE,{"disambiguationData":[TD([subQ18])],"derivedFrom":makeQuery(id+"F0Hq7nSFAMYVZvY_4.9.F20.boolean.opBoolean","SPLIT",FACE,{"disambiguationData":[TD([subQ18])],"derivedFrom":makeQuery(id+"F0Hq7nSFAMYVZvY_4.8.F20.boolean.opBoolean","SPLIT",FACE,{"disambiguationData":[TD([subQ18])],"derivedFrom":makeQuery(id+"F0Hq7nSFAMYVZvY_4.7.F20.boolean.opBoolean","SPLIT",FACE,{"disambiguationData":[TD([subQ18])],"derivedFrom":makeQuery(id+"F0Hq7nSFAMYVZvY_4.6.F20.boolean.opBoolean","SPLIT",FACE,{"disambiguationData":[TD([subQ18])],"derivedFrom":makeQuery(id+"F0Hq7nSFAMYVZvY_4.5.F20.boolean.opBoolean","SPLIT",FACE,{"disambiguationData":[TD([subQ18])],"derivedFrom":makeQuery(id+"F0Hq7nSFAMYVZvY_4.4.F20.boolean.opBoolean","SPLIT",FACE,{"disambiguationData":[TD([subQ18])],"derivedFrom":makeQuery(id+"F0Hq7nSFAMYVZvY_4.3.F20.boolean.opBoolean","SPLIT",FACE,{"disambiguationData":[TD([subQ18])],"derivedFrom":makeQuery(id+"F0Hq7nSFAMYVZvY_4.2.F20.boolean.opBoolean","SPLIT",FACE,{"disambiguationData":[TD([subQ18])],"derivedFrom":makeQuery(id+"F0Hq7nSFAMYVZvY_4.1.F20.boolean.opBoolean","SPLIT",FACE,{"disambiguationData":[TD([subQ18])],"derivedFrom":makeQuery(id+"F17.boolean.opBoolean","COPY",FACE,{"derivedFrom":makeQuery(id+"F17.opExtrude","SWEPT_FACE",FACE,{"disambiguationData":[OSD([subQ3])]})})})})})})})})})})})})});}
            var Q460;
            {var subQ0=sQuery(id+"F19.wireOp",EDGE,"E158.MirrorCS");var subQ1=sQuery(id+"F19.wireOp",EDGE,"E157");var subQ3=sQuery(id+"F16.wireOp",EDGE,"E151");var subQ17=makeQuery(id+"F0Hq7nSFAMYVZvY_4.10.F20.opExtrude","SWEPT_FACE",FACE,{"disambiguationData":[OSD([subQ0])]});var subQ18=makeQuery(id+"F20.opExtrude","SWEPT_FACE",FACE,{"disambiguationData":[OSD([subQ1])]});Q460=makeQuery(id+"F0Hq7nSFAMYVZvY_4.11.F20.boolean.opBoolean","SPLIT",EDGE,{"disambiguationData":[TD([subQ17])],"derivedFrom":makeQuery(id+"F0Hq7nSFAMYVZvY_4.10.F20.boolean.opBoolean","SPLIT",EDGE,{"disambiguationData":[TD([subQ18])],"derivedFrom":makeQuery(id+"F0Hq7nSFAMYVZvY_4.9.F20.boolean.opBoolean","SPLIT",EDGE,{"disambiguationData":[TD([subQ18])],"derivedFrom":makeQuery(id+"F0Hq7nSFAMYVZvY_4.8.F20.boolean.opBoolean","SPLIT",EDGE,{"disambiguationData":[TD([subQ18])],"derivedFrom":makeQuery(id+"F0Hq7nSFAMYVZvY_4.7.F20.boolean.opBoolean","SPLIT",EDGE,{"disambiguationData":[TD([subQ18])],"derivedFrom":makeQuery(id+"F0Hq7nSFAMYVZvY_4.6.F20.boolean.opBoolean","SPLIT",EDGE,{"disambiguationData":[TD([subQ18])],"derivedFrom":makeQuery(id+"F0Hq7nSFAMYVZvY_4.5.F20.boolean.opBoolean","SPLIT",EDGE,{"disambiguationData":[TD([subQ18])],"derivedFrom":makeQuery(id+"F0Hq7nSFAMYVZvY_4.4.F20.boolean.opBoolean","SPLIT",EDGE,{"disambiguationData":[TD([subQ18])],"derivedFrom":makeQuery(id+"F0Hq7nSFAMYVZvY_4.3.F20.boolean.opBoolean","SPLIT",EDGE,{"disambiguationData":[TD([subQ18])],"derivedFrom":makeQuery(id+"F0Hq7nSFAMYVZvY_4.2.F20.boolean.opBoolean","SPLIT",EDGE,{"disambiguationData":[TD([subQ18])],"derivedFrom":makeQuery(id+"F0Hq7nSFAMYVZvY_4.1.F20.boolean.opBoolean","SPLIT",EDGE,{"disambiguationData":[TD([subQ18])],"derivedFrom":makeQuery(id+"F18.boolean.opBoolean","COPY",EDGE,{"derivedFrom":makeQuery(id+"F18.opExtrude","CAP_EDGE",EDGE,{"disambiguationData":[OSD([subQ3])],"isStart":false})})})})})})})})})})})})});}
            var Q461;
            Q461=makeQuery(id+"F0Hq7nSFAMYVZvY_4.12.F20.opExtrude","CAP_EDGE",EDGE,{"disambiguationData":[OSD([sQuery(id+"F19.wireOp",EDGE,"E157")])],"isStart":false});
            var Q462;
            Q462=makeQuery(id+"F0Hq7nSFAMYVZvY_4.12.F20.opExtrude","SWEPT_EDGE",EDGE,{"disambiguationData":[OSD([sQuery(id+"F16.wireOp",EDGE,"E151"),sQuery(id+"F19.wireOp",EDGE,"E158.MirrorCS")])]});
            var Q463;
            Q463=makeQuery(id+"F0Hq7nSFAMYVZvY_4.12.F20.opExtrude","CAP_EDGE",EDGE,{"disambiguationData":[OSD([sQuery(id+"F19.wireOp",EDGE,"E157")])],"isStart":true});
            var Q464;
            Q464=makeQuery(id+"F0Hq7nSFAMYVZvY_4.12.F20.opExtrude","CAP_EDGE",EDGE,{"disambiguationData":[OSD([sQuery(id+"F19.wireOp",EDGE,"E158.MirrorCS")])],"isStart":true});
            var Q465;
            {var subQ0=sQuery(id+"F19.wireOp",EDGE,"E158.MirrorCS");var subQ1=sQuery(id+"F19.wireOp",EDGE,"E157");var subQ3=sQuery(id+"F16.wireOp",EDGE,"E151");var subQ18=makeQuery(id+"F0Hq7nSFAMYVZvY_4.11.F20.opExtrude","SWEPT_FACE",FACE,{"disambiguationData":[OSD([subQ0])]});var subQ19=makeQuery(id+"F20.opExtrude","SWEPT_FACE",FACE,{"disambiguationData":[OSD([subQ1])]});Q465=makeQuery(id+"F0Hq7nSFAMYVZvY_4.12.F20.boolean.opBoolean","SPLIT",FACE,{"disambiguationData":[TD([subQ18])],"derivedFrom":makeQuery(id+"F0Hq7nSFAMYVZvY_4.11.F20.boolean.opBoolean","SPLIT",FACE,{"disambiguationData":[TD([subQ19])],"derivedFrom":makeQuery(id+"F0Hq7nSFAMYVZvY_4.10.F20.boolean.opBoolean","SPLIT",FACE,{"disambiguationData":[TD([subQ19])],"derivedFrom":makeQuery(id+"F0Hq7nSFAMYVZvY_4.9.F20.boolean.opBoolean","SPLIT",FACE,{"disambiguationData":[TD([subQ19])],"derivedFrom":makeQuery(id+"F0Hq7nSFAMYVZvY_4.8.F20.boolean.opBoolean","SPLIT",FACE,{"disambiguationData":[TD([subQ19])],"derivedFrom":makeQuery(id+"F0Hq7nSFAMYVZvY_4.7.F20.boolean.opBoolean","SPLIT",FACE,{"disambiguationData":[TD([subQ19])],"derivedFrom":makeQuery(id+"F0Hq7nSFAMYVZvY_4.6.F20.boolean.opBoolean","SPLIT",FACE,{"disambiguationData":[TD([subQ19])],"derivedFrom":makeQuery(id+"F0Hq7nSFAMYVZvY_4.5.F20.boolean.opBoolean","SPLIT",FACE,{"disambiguationData":[TD([subQ19])],"derivedFrom":makeQuery(id+"F0Hq7nSFAMYVZvY_4.4.F20.boolean.opBoolean","SPLIT",FACE,{"disambiguationData":[TD([subQ19])],"derivedFrom":makeQuery(id+"F0Hq7nSFAMYVZvY_4.3.F20.boolean.opBoolean","SPLIT",FACE,{"disambiguationData":[TD([subQ19])],"derivedFrom":makeQuery(id+"F0Hq7nSFAMYVZvY_4.2.F20.boolean.opBoolean","SPLIT",FACE,{"disambiguationData":[TD([subQ19])],"derivedFrom":makeQuery(id+"F0Hq7nSFAMYVZvY_4.1.F20.boolean.opBoolean","SPLIT",FACE,{"disambiguationData":[TD([subQ19])],"derivedFrom":makeQuery(id+"F17.boolean.opBoolean","COPY",FACE,{"derivedFrom":makeQuery(id+"F17.opExtrude","SWEPT_FACE",FACE,{"disambiguationData":[OSD([subQ3])]})})})})})})})})})})})})})});}
            var Q466;
            {var subQ0=sQuery(id+"F16.wireOp",EDGE,"E151");var subQ2=sQuery(id+"F19.wireOp",EDGE,"E158.MirrorCS");var subQ3=makeQuery(id+"F0Hq7nSFAMYVZvY_4.11.F20.opExtrude","SWEPT_FACE",FACE,{"disambiguationData":[OSD([subQ2])]});var subQ5=sQuery(id+"F19.wireOp",EDGE,"E157");var subQ6=makeQuery(id+"F20.opExtrude","SWEPT_FACE",FACE,{"disambiguationData":[OSD([subQ5])]});Q466=makeQuery(id+"F0Hq7nSFAMYVZvY_4.12.F20.boolean.opBoolean","SPLIT",EDGE,{"disambiguationData":[TD([subQ3])],"derivedFrom":makeQuery(id+"F0Hq7nSFAMYVZvY_4.11.F20.boolean.opBoolean","SPLIT",EDGE,{"disambiguationData":[TD([subQ6])],"derivedFrom":makeQuery(id+"F0Hq7nSFAMYVZvY_4.10.F20.boolean.opBoolean","SPLIT",EDGE,{"disambiguationData":[TD([subQ6])],"derivedFrom":makeQuery(id+"F0Hq7nSFAMYVZvY_4.9.F20.boolean.opBoolean","SPLIT",EDGE,{"disambiguationData":[TD([subQ6])],"derivedFrom":makeQuery(id+"F0Hq7nSFAMYVZvY_4.8.F20.boolean.opBoolean","SPLIT",EDGE,{"disambiguationData":[TD([subQ6])],"derivedFrom":makeQuery(id+"F0Hq7nSFAMYVZvY_4.7.F20.boolean.opBoolean","SPLIT",EDGE,{"disambiguationData":[TD([subQ6])],"derivedFrom":makeQuery(id+"F0Hq7nSFAMYVZvY_4.6.F20.boolean.opBoolean","SPLIT",EDGE,{"disambiguationData":[TD([subQ6])],"derivedFrom":makeQuery(id+"F0Hq7nSFAMYVZvY_4.5.F20.boolean.opBoolean","SPLIT",EDGE,{"disambiguationData":[TD([subQ6])],"derivedFrom":makeQuery(id+"F0Hq7nSFAMYVZvY_4.4.F20.boolean.opBoolean","SPLIT",EDGE,{"disambiguationData":[TD([subQ6])],"derivedFrom":makeQuery(id+"F0Hq7nSFAMYVZvY_4.3.F20.boolean.opBoolean","SPLIT",EDGE,{"disambiguationData":[TD([subQ6])],"derivedFrom":makeQuery(id+"F0Hq7nSFAMYVZvY_4.2.F20.boolean.opBoolean","SPLIT",EDGE,{"disambiguationData":[TD([subQ6])],"derivedFrom":makeQuery(id+"F0Hq7nSFAMYVZvY_4.1.F20.boolean.opBoolean","SPLIT",EDGE,{"disambiguationData":[TD([subQ6])],"derivedFrom":makeQuery(id+"F17.boolean.opBoolean","COPY",EDGE,{"derivedFrom":makeQuery(id+"F17.opExtrude","CAP_EDGE",EDGE,{"disambiguationData":[OSD([subQ0])],"isStart":false})})})})})})})})})})})})})});}
            var Q467;
            {var subQ0=sQuery(id+"F19.wireOp",EDGE,"E158.MirrorCS");var subQ1=sQuery(id+"F19.wireOp",EDGE,"E157");var subQ3=sQuery(id+"F16.wireOp",EDGE,"E151");var subQ18=makeQuery(id+"F0Hq7nSFAMYVZvY_4.11.F20.opExtrude","SWEPT_FACE",FACE,{"disambiguationData":[OSD([subQ0])]});var subQ19=makeQuery(id+"F20.opExtrude","SWEPT_FACE",FACE,{"disambiguationData":[OSD([subQ1])]});Q467=makeQuery(id+"F0Hq7nSFAMYVZvY_4.12.F20.boolean.opBoolean","SPLIT",EDGE,{"disambiguationData":[TD([subQ18])],"derivedFrom":makeQuery(id+"F0Hq7nSFAMYVZvY_4.11.F20.boolean.opBoolean","SPLIT",EDGE,{"disambiguationData":[TD([subQ19])],"derivedFrom":makeQuery(id+"F0Hq7nSFAMYVZvY_4.10.F20.boolean.opBoolean","SPLIT",EDGE,{"disambiguationData":[TD([subQ19])],"derivedFrom":makeQuery(id+"F0Hq7nSFAMYVZvY_4.9.F20.boolean.opBoolean","SPLIT",EDGE,{"disambiguationData":[TD([subQ19])],"derivedFrom":makeQuery(id+"F0Hq7nSFAMYVZvY_4.8.F20.boolean.opBoolean","SPLIT",EDGE,{"disambiguationData":[TD([subQ19])],"derivedFrom":makeQuery(id+"F0Hq7nSFAMYVZvY_4.7.F20.boolean.opBoolean","SPLIT",EDGE,{"disambiguationData":[TD([subQ19])],"derivedFrom":makeQuery(id+"F0Hq7nSFAMYVZvY_4.6.F20.boolean.opBoolean","SPLIT",EDGE,{"disambiguationData":[TD([subQ19])],"derivedFrom":makeQuery(id+"F0Hq7nSFAMYVZvY_4.5.F20.boolean.opBoolean","SPLIT",EDGE,{"disambiguationData":[TD([subQ19])],"derivedFrom":makeQuery(id+"F0Hq7nSFAMYVZvY_4.4.F20.boolean.opBoolean","SPLIT",EDGE,{"disambiguationData":[TD([subQ19])],"derivedFrom":makeQuery(id+"F0Hq7nSFAMYVZvY_4.3.F20.boolean.opBoolean","SPLIT",EDGE,{"disambiguationData":[TD([subQ19])],"derivedFrom":makeQuery(id+"F0Hq7nSFAMYVZvY_4.2.F20.boolean.opBoolean","SPLIT",EDGE,{"disambiguationData":[TD([subQ19])],"derivedFrom":makeQuery(id+"F0Hq7nSFAMYVZvY_4.1.F20.boolean.opBoolean","SPLIT",EDGE,{"disambiguationData":[TD([subQ19])],"derivedFrom":makeQuery(id+"F18.boolean.opBoolean","COPY",EDGE,{"derivedFrom":makeQuery(id+"F18.opExtrude","CAP_EDGE",EDGE,{"disambiguationData":[OSD([subQ3])],"isStart":false})})})})})})})})})})})})})});}
            var Q468;
            Q468=makeQuery(id+"F1.opRevolve","SWEPT_FACE",FACE,{"disambiguationData":[OSD([sQuery(id+"F0.wireOp",EDGE,"E105")])]});
            var Q469;
            Q469=makeQuery(id+"F0Hq7nSFAMYVZvY_4.19.F20.opExtrude","SWEPT_EDGE",EDGE,{"disambiguationData":[OSD([sQuery(id+"F16.wireOp",EDGE,"E151"),sQuery(id+"F19.wireOp",EDGE,"E158.MirrorCS")])]});
            var Q470;
            Q470=makeQuery(id+"F0Hq7nSFAMYVZvY_4.20.F20.opExtrude","SWEPT_EDGE",EDGE,{"disambiguationData":[OSD([sQuery(id+"F16.wireOp",EDGE,"E151"),sQuery(id+"F19.wireOp",EDGE,"E157")])]});
            var Q471;
            Q471=makeQuery(id+"F0Hq7nSFAMYVZvY_4.20.F20.opExtrude","CAP_EDGE",EDGE,{"disambiguationData":[OSD([sQuery(id+"F19.wireOp",EDGE,"E158.MirrorCS")])],"isStart":true});
            var Q472;
            Q472=makeQuery(id+"F0Hq7nSFAMYVZvY_4.29.F20.opExtrude","SWEPT_EDGE",EDGE,{"disambiguationData":[OSD([sQuery(id+"F16.wireOp",EDGE,"E151"),sQuery(id+"F19.wireOp",EDGE,"E158.MirrorCS")])]});
            var Q473;
            {var subQ0=sQuery(id+"F16.wireOp",EDGE,"E151");var subQ3=sQuery(id+"F19.wireOp",EDGE,"E158.MirrorCS");var subQ4=makeQuery(id+"F0Hq7nSFAMYVZvY_4.28.F20.opExtrude","SWEPT_FACE",FACE,{"disambiguationData":[OSD([subQ3])]});var subQ5=sQuery(id+"F19.wireOp",EDGE,"E157");var subQ6=makeQuery(id+"F20.opExtrude","SWEPT_FACE",FACE,{"disambiguationData":[OSD([subQ5])]});Q473=makeQuery(id+"F0Hq7nSFAMYVZvY_4.29.F20.boolean.opBoolean","SPLIT",EDGE,{"disambiguationData":[TD([subQ4])],"derivedFrom":makeQuery(id+"F0Hq7nSFAMYVZvY_4.28.F20.boolean.opBoolean","SPLIT",EDGE,{"disambiguationData":[TD([subQ6])],"derivedFrom":makeQuery(id+"F0Hq7nSFAMYVZvY_4.27.F20.boolean.opBoolean","SPLIT",EDGE,{"disambiguationData":[TD([subQ6])],"derivedFrom":makeQuery(id+"F0Hq7nSFAMYVZvY_4.26.F20.boolean.opBoolean","SPLIT",EDGE,{"disambiguationData":[TD([subQ6])],"derivedFrom":makeQuery(id+"F0Hq7nSFAMYVZvY_4.25.F20.boolean.opBoolean","SPLIT",EDGE,{"disambiguationData":[TD([subQ6])],"derivedFrom":makeQuery(id+"F0Hq7nSFAMYVZvY_4.24.F20.boolean.opBoolean","SPLIT",EDGE,{"disambiguationData":[TD([subQ6])],"derivedFrom":makeQuery(id+"F0Hq7nSFAMYVZvY_4.23.F20.boolean.opBoolean","SPLIT",EDGE,{"disambiguationData":[TD([subQ6])],"derivedFrom":makeQuery(id+"F0Hq7nSFAMYVZvY_4.22.F20.boolean.opBoolean","SPLIT",EDGE,{"disambiguationData":[TD([subQ6])],"derivedFrom":makeQuery(id+"F0Hq7nSFAMYVZvY_4.21.F20.boolean.opBoolean","SPLIT",EDGE,{"disambiguationData":[TD([subQ6])],"derivedFrom":makeQuery(id+"F0Hq7nSFAMYVZvY_4.20.F20.boolean.opBoolean","SPLIT",EDGE,{"disambiguationData":[TD([subQ6])],"derivedFrom":makeQuery(id+"F0Hq7nSFAMYVZvY_4.19.F20.boolean.opBoolean","SPLIT",EDGE,{"disambiguationData":[TD([subQ6])],"derivedFrom":makeQuery(id+"F0Hq7nSFAMYVZvY_4.18.F20.boolean.opBoolean","SPLIT",EDGE,{"disambiguationData":[TD([subQ6])],"derivedFrom":makeQuery(id+"F0Hq7nSFAMYVZvY_4.17.F20.boolean.opBoolean","SPLIT",EDGE,{"disambiguationData":[TD([subQ6])],"derivedFrom":makeQuery(id+"F0Hq7nSFAMYVZvY_4.16.F20.boolean.opBoolean","SPLIT",EDGE,{"disambiguationData":[TD([subQ6])],"derivedFrom":makeQuery(id+"F0Hq7nSFAMYVZvY_4.15.F20.boolean.opBoolean","SPLIT",EDGE,{"disambiguationData":[TD([subQ6])],"derivedFrom":makeQuery(id+"F0Hq7nSFAMYVZvY_4.14.F20.boolean.opBoolean","SPLIT",EDGE,{"disambiguationData":[TD([subQ6])],"derivedFrom":makeQuery(id+"F0Hq7nSFAMYVZvY_4.13.F20.boolean.opBoolean","SPLIT",EDGE,{"disambiguationData":[TD([subQ6])],"derivedFrom":makeQuery(id+"F0Hq7nSFAMYVZvY_4.12.F20.boolean.opBoolean","SPLIT",EDGE,{"disambiguationData":[TD([subQ6])],"derivedFrom":makeQuery(id+"F0Hq7nSFAMYVZvY_4.11.F20.boolean.opBoolean","SPLIT",EDGE,{"disambiguationData":[TD([subQ6])],"derivedFrom":makeQuery(id+"F0Hq7nSFAMYVZvY_4.10.F20.boolean.opBoolean","SPLIT",EDGE,{"disambiguationData":[TD([subQ6])],"derivedFrom":makeQuery(id+"F0Hq7nSFAMYVZvY_4.9.F20.boolean.opBoolean","SPLIT",EDGE,{"disambiguationData":[TD([subQ6])],"derivedFrom":makeQuery(id+"F0Hq7nSFAMYVZvY_4.8.F20.boolean.opBoolean","SPLIT",EDGE,{"disambiguationData":[TD([subQ6])],"derivedFrom":makeQuery(id+"F0Hq7nSFAMYVZvY_4.7.F20.boolean.opBoolean","SPLIT",EDGE,{"disambiguationData":[TD([subQ6])],"derivedFrom":makeQuery(id+"F0Hq7nSFAMYVZvY_4.6.F20.boolean.opBoolean","SPLIT",EDGE,{"disambiguationData":[TD([subQ6])],"derivedFrom":makeQuery(id+"F0Hq7nSFAMYVZvY_4.5.F20.boolean.opBoolean","SPLIT",EDGE,{"disambiguationData":[TD([subQ6])],"derivedFrom":makeQuery(id+"F0Hq7nSFAMYVZvY_4.4.F20.boolean.opBoolean","SPLIT",EDGE,{"disambiguationData":[TD([subQ6])],"derivedFrom":makeQuery(id+"F0Hq7nSFAMYVZvY_4.3.F20.boolean.opBoolean","SPLIT",EDGE,{"disambiguationData":[TD([subQ6])],"derivedFrom":makeQuery(id+"F0Hq7nSFAMYVZvY_4.2.F20.boolean.opBoolean","SPLIT",EDGE,{"disambiguationData":[TD([subQ6])],"derivedFrom":makeQuery(id+"F0Hq7nSFAMYVZvY_4.1.F20.boolean.opBoolean","SPLIT",EDGE,{"disambiguationData":[TD([subQ6])],"derivedFrom":makeQuery(id+"F17.boolean.opBoolean","COPY",EDGE,{"derivedFrom":makeQuery(id+"F17.opExtrude","CAP_EDGE",EDGE,{"disambiguationData":[OSD([subQ0])],"isStart":false})})})})})})})})})})})})})})})})})})})})})})})})})})})})})})});}
            var Q474;
            Q474=makeQuery(id+"F0Hq7nSFAMYVZvY_4.30.F20.opExtrude","SWEPT_EDGE",EDGE,{"disambiguationData":[OSD([sQuery(id+"F16.wireOp",EDGE,"E151"),sQuery(id+"F19.wireOp",EDGE,"E158.MirrorCS")])]});
            var Q475;
            {var subQ0=sQuery(id+"F16.wireOp",EDGE,"E151");var subQ2=sQuery(id+"F19.wireOp",EDGE,"E157");var subQ4=sQuery(id+"F19.wireOp",EDGE,"E158.MirrorCS");var subQ5=makeQuery(id+"F0Hq7nSFAMYVZvY_4.29.F20.opExtrude","SWEPT_FACE",FACE,{"disambiguationData":[OSD([subQ4])]});var subQ6=makeQuery(id+"F20.opExtrude","SWEPT_FACE",FACE,{"disambiguationData":[OSD([subQ2])]});Q475=makeQuery(id+"F0Hq7nSFAMYVZvY_4.30.F20.boolean.opBoolean","SPLIT",EDGE,{"disambiguationData":[TD([subQ5])],"derivedFrom":makeQuery(id+"F0Hq7nSFAMYVZvY_4.29.F20.boolean.opBoolean","SPLIT",EDGE,{"disambiguationData":[TD([subQ6])],"derivedFrom":makeQuery(id+"F0Hq7nSFAMYVZvY_4.28.F20.boolean.opBoolean","SPLIT",EDGE,{"disambiguationData":[TD([subQ6])],"derivedFrom":makeQuery(id+"F0Hq7nSFAMYVZvY_4.27.F20.boolean.opBoolean","SPLIT",EDGE,{"disambiguationData":[TD([subQ6])],"derivedFrom":makeQuery(id+"F0Hq7nSFAMYVZvY_4.26.F20.boolean.opBoolean","SPLIT",EDGE,{"disambiguationData":[TD([subQ6])],"derivedFrom":makeQuery(id+"F0Hq7nSFAMYVZvY_4.25.F20.boolean.opBoolean","SPLIT",EDGE,{"disambiguationData":[TD([subQ6])],"derivedFrom":makeQuery(id+"F0Hq7nSFAMYVZvY_4.24.F20.boolean.opBoolean","SPLIT",EDGE,{"disambiguationData":[TD([subQ6])],"derivedFrom":makeQuery(id+"F0Hq7nSFAMYVZvY_4.23.F20.boolean.opBoolean","SPLIT",EDGE,{"disambiguationData":[TD([subQ6])],"derivedFrom":makeQuery(id+"F0Hq7nSFAMYVZvY_4.22.F20.boolean.opBoolean","SPLIT",EDGE,{"disambiguationData":[TD([subQ6])],"derivedFrom":makeQuery(id+"F0Hq7nSFAMYVZvY_4.21.F20.boolean.opBoolean","SPLIT",EDGE,{"disambiguationData":[TD([subQ6])],"derivedFrom":makeQuery(id+"F0Hq7nSFAMYVZvY_4.20.F20.boolean.opBoolean","SPLIT",EDGE,{"disambiguationData":[TD([subQ6])],"derivedFrom":makeQuery(id+"F0Hq7nSFAMYVZvY_4.19.F20.boolean.opBoolean","SPLIT",EDGE,{"disambiguationData":[TD([subQ6])],"derivedFrom":makeQuery(id+"F0Hq7nSFAMYVZvY_4.18.F20.boolean.opBoolean","SPLIT",EDGE,{"disambiguationData":[TD([subQ6])],"derivedFrom":makeQuery(id+"F0Hq7nSFAMYVZvY_4.17.F20.boolean.opBoolean","SPLIT",EDGE,{"disambiguationData":[TD([subQ6])],"derivedFrom":makeQuery(id+"F0Hq7nSFAMYVZvY_4.16.F20.boolean.opBoolean","SPLIT",EDGE,{"disambiguationData":[TD([subQ6])],"derivedFrom":makeQuery(id+"F0Hq7nSFAMYVZvY_4.15.F20.boolean.opBoolean","SPLIT",EDGE,{"disambiguationData":[TD([subQ6])],"derivedFrom":makeQuery(id+"F0Hq7nSFAMYVZvY_4.14.F20.boolean.opBoolean","SPLIT",EDGE,{"disambiguationData":[TD([subQ6])],"derivedFrom":makeQuery(id+"F0Hq7nSFAMYVZvY_4.13.F20.boolean.opBoolean","SPLIT",EDGE,{"disambiguationData":[TD([subQ6])],"derivedFrom":makeQuery(id+"F0Hq7nSFAMYVZvY_4.12.F20.boolean.opBoolean","SPLIT",EDGE,{"disambiguationData":[TD([subQ6])],"derivedFrom":makeQuery(id+"F0Hq7nSFAMYVZvY_4.11.F20.boolean.opBoolean","SPLIT",EDGE,{"disambiguationData":[TD([subQ6])],"derivedFrom":makeQuery(id+"F0Hq7nSFAMYVZvY_4.10.F20.boolean.opBoolean","SPLIT",EDGE,{"disambiguationData":[TD([subQ6])],"derivedFrom":makeQuery(id+"F0Hq7nSFAMYVZvY_4.9.F20.boolean.opBoolean","SPLIT",EDGE,{"disambiguationData":[TD([subQ6])],"derivedFrom":makeQuery(id+"F0Hq7nSFAMYVZvY_4.8.F20.boolean.opBoolean","SPLIT",EDGE,{"disambiguationData":[TD([subQ6])],"derivedFrom":makeQuery(id+"F0Hq7nSFAMYVZvY_4.7.F20.boolean.opBoolean","SPLIT",EDGE,{"disambiguationData":[TD([subQ6])],"derivedFrom":makeQuery(id+"F0Hq7nSFAMYVZvY_4.6.F20.boolean.opBoolean","SPLIT",EDGE,{"disambiguationData":[TD([subQ6])],"derivedFrom":makeQuery(id+"F0Hq7nSFAMYVZvY_4.5.F20.boolean.opBoolean","SPLIT",EDGE,{"disambiguationData":[TD([subQ6])],"derivedFrom":makeQuery(id+"F0Hq7nSFAMYVZvY_4.4.F20.boolean.opBoolean","SPLIT",EDGE,{"disambiguationData":[TD([subQ6])],"derivedFrom":makeQuery(id+"F0Hq7nSFAMYVZvY_4.3.F20.boolean.opBoolean","SPLIT",EDGE,{"disambiguationData":[TD([subQ6])],"derivedFrom":makeQuery(id+"F0Hq7nSFAMYVZvY_4.2.F20.boolean.opBoolean","SPLIT",EDGE,{"disambiguationData":[TD([subQ6])],"derivedFrom":makeQuery(id+"F0Hq7nSFAMYVZvY_4.1.F20.boolean.opBoolean","SPLIT",EDGE,{"disambiguationData":[TD([subQ6])],"derivedFrom":makeQuery(id+"F17.boolean.opBoolean","COPY",EDGE,{"derivedFrom":makeQuery(id+"F17.opExtrude","CAP_EDGE",EDGE,{"disambiguationData":[OSD([subQ0])],"isStart":false})})})})})})})})})})})})})})})})})})})})})})})})})})})})})})})});}
            var Q476;
            Q476=makeQuery(id+"F0Hq7nSFAMYVZvY_4.32.F20.opExtrude","SWEPT_EDGE",EDGE,{"disambiguationData":[OSD([sQuery(id+"F16.wireOp",EDGE,"E151"),sQuery(id+"F19.wireOp",EDGE,"E158.MirrorCS")])]});
            var Q477;
            Q477=makeQuery(id+"F0Hq7nSFAMYVZvY_4.37.F20.opExtrude","SWEPT_EDGE",EDGE,{"disambiguationData":[OSD([sQuery(id+"F16.wireOp",EDGE,"E151"),sQuery(id+"F19.wireOp",EDGE,"E158.MirrorCS")])]});
            var Q478;
            Q478=makeQuery(id+"F0Hq7nSFAMYVZvY_4.39.F20.opExtrude","SWEPT_EDGE",EDGE,{"disambiguationData":[OSD([sQuery(id+"F16.wireOp",EDGE,"E151"),sQuery(id+"F19.wireOp",EDGE,"E158.MirrorCS")])]});
            var Q479;
            Q479=makeQuery(id+"F0Hq7nSFAMYVZvY_4.9.F20.opExtrude","SWEPT_EDGE",EDGE,{"disambiguationData":[OSD([sQuery(id+"F16.wireOp",EDGE,"E151"),sQuery(id+"F19.wireOp",EDGE,"E157")])]});
            var Q480;
            Q480=makeQuery(id+"F0Hq7nSFAMYVZvY_4.9.F20.opExtrude","SWEPT_EDGE",EDGE,{"disambiguationData":[OSD([sQuery(id+"F16.wireOp",EDGE,"E151"),sQuery(id+"F19.wireOp",EDGE,"E158.MirrorCS")])]});
            var Q481;
            Q481=makeQuery(id+"F0Hq7nSFAMYVZvY_4.10.F20.opExtrude","SWEPT_EDGE",EDGE,{"disambiguationData":[OSD([sQuery(id+"F16.wireOp",EDGE,"E151"),sQuery(id+"F19.wireOp",EDGE,"E157")])]});
            var Q482;
            Q482=makeQuery(id+"F0Hq7nSFAMYVZvY_4.10.F20.opExtrude","SWEPT_EDGE",EDGE,{"disambiguationData":[OSD([sQuery(id+"F16.wireOp",EDGE,"E151"),sQuery(id+"F19.wireOp",EDGE,"E158.MirrorCS")])]});
            var Q483;
            Q483=makeQuery(id+"F0Hq7nSFAMYVZvY_4.10.F20.opExtrude","CAP_EDGE",EDGE,{"disambiguationData":[OSD([sQuery(id+"F19.wireOp",EDGE,"E157")])],"isStart":true});
            var Q484;
            {var subQ0=sQuery(id+"F16.wireOp",EDGE,"E151");var subQ2=sQuery(id+"F19.wireOp",EDGE,"E157");var subQ4=sQuery(id+"F19.wireOp",EDGE,"E158.MirrorCS");var subQ5=makeQuery(id+"F0Hq7nSFAMYVZvY_4.9.F20.opExtrude","SWEPT_FACE",FACE,{"disambiguationData":[OSD([subQ4])]});var subQ6=makeQuery(id+"F20.opExtrude","SWEPT_FACE",FACE,{"disambiguationData":[OSD([subQ2])]});Q484=makeQuery(id+"F0Hq7nSFAMYVZvY_4.10.F20.boolean.opBoolean","SPLIT",EDGE,{"disambiguationData":[TD([subQ5])],"derivedFrom":makeQuery(id+"F0Hq7nSFAMYVZvY_4.9.F20.boolean.opBoolean","SPLIT",EDGE,{"disambiguationData":[TD([subQ6])],"derivedFrom":makeQuery(id+"F0Hq7nSFAMYVZvY_4.8.F20.boolean.opBoolean","SPLIT",EDGE,{"disambiguationData":[TD([subQ6])],"derivedFrom":makeQuery(id+"F0Hq7nSFAMYVZvY_4.7.F20.boolean.opBoolean","SPLIT",EDGE,{"disambiguationData":[TD([subQ6])],"derivedFrom":makeQuery(id+"F0Hq7nSFAMYVZvY_4.6.F20.boolean.opBoolean","SPLIT",EDGE,{"disambiguationData":[TD([subQ6])],"derivedFrom":makeQuery(id+"F0Hq7nSFAMYVZvY_4.5.F20.boolean.opBoolean","SPLIT",EDGE,{"disambiguationData":[TD([subQ6])],"derivedFrom":makeQuery(id+"F0Hq7nSFAMYVZvY_4.4.F20.boolean.opBoolean","SPLIT",EDGE,{"disambiguationData":[TD([subQ6])],"derivedFrom":makeQuery(id+"F0Hq7nSFAMYVZvY_4.3.F20.boolean.opBoolean","SPLIT",EDGE,{"disambiguationData":[TD([subQ6])],"derivedFrom":makeQuery(id+"F0Hq7nSFAMYVZvY_4.2.F20.boolean.opBoolean","SPLIT",EDGE,{"disambiguationData":[TD([subQ6])],"derivedFrom":makeQuery(id+"F0Hq7nSFAMYVZvY_4.1.F20.boolean.opBoolean","SPLIT",EDGE,{"disambiguationData":[TD([subQ6])],"derivedFrom":makeQuery(id+"F17.boolean.opBoolean","COPY",EDGE,{"derivedFrom":makeQuery(id+"F17.opExtrude","CAP_EDGE",EDGE,{"disambiguationData":[OSD([subQ0])],"isStart":false})})})})})})})})})})})});}
            var Q485;
            Q485=makeQuery(id+"F0Hq7nSFAMYVZvY_4.11.F20.opExtrude","CAP_EDGE",EDGE,{"disambiguationData":[OSD([sQuery(id+"F19.wireOp",EDGE,"E157")])],"isStart":false});
            var Q486;
            Q486=makeQuery(id+"F0Hq7nSFAMYVZvY_4.11.F20.opExtrude","SWEPT_EDGE",EDGE,{"disambiguationData":[OSD([sQuery(id+"F16.wireOp",EDGE,"E151"),sQuery(id+"F19.wireOp",EDGE,"E157")])]});
            var Q487;
            Q487=makeQuery(id+"F0Hq7nSFAMYVZvY_4.11.F20.opExtrude","SWEPT_EDGE",EDGE,{"disambiguationData":[OSD([sQuery(id+"F16.wireOp",EDGE,"E151"),sQuery(id+"F19.wireOp",EDGE,"E158.MirrorCS")])]});
            var Q488;
            Q488=makeQuery(id+"F0Hq7nSFAMYVZvY_4.11.F20.opExtrude","CAP_EDGE",EDGE,{"disambiguationData":[OSD([sQuery(id+"F19.wireOp",EDGE,"E157")])],"isStart":true});
            var Q489;
            {var subQ0=sQuery(id+"F16.wireOp",EDGE,"E151");var subQ3=sQuery(id+"F19.wireOp",EDGE,"E158.MirrorCS");var subQ4=makeQuery(id+"F0Hq7nSFAMYVZvY_4.10.F20.opExtrude","SWEPT_FACE",FACE,{"disambiguationData":[OSD([subQ3])]});var subQ5=sQuery(id+"F19.wireOp",EDGE,"E157");var subQ6=makeQuery(id+"F20.opExtrude","SWEPT_FACE",FACE,{"disambiguationData":[OSD([subQ5])]});Q489=makeQuery(id+"F0Hq7nSFAMYVZvY_4.11.F20.boolean.opBoolean","SPLIT",EDGE,{"disambiguationData":[TD([subQ4])],"derivedFrom":makeQuery(id+"F0Hq7nSFAMYVZvY_4.10.F20.boolean.opBoolean","SPLIT",EDGE,{"disambiguationData":[TD([subQ6])],"derivedFrom":makeQuery(id+"F0Hq7nSFAMYVZvY_4.9.F20.boolean.opBoolean","SPLIT",EDGE,{"disambiguationData":[TD([subQ6])],"derivedFrom":makeQuery(id+"F0Hq7nSFAMYVZvY_4.8.F20.boolean.opBoolean","SPLIT",EDGE,{"disambiguationData":[TD([subQ6])],"derivedFrom":makeQuery(id+"F0Hq7nSFAMYVZvY_4.7.F20.boolean.opBoolean","SPLIT",EDGE,{"disambiguationData":[TD([subQ6])],"derivedFrom":makeQuery(id+"F0Hq7nSFAMYVZvY_4.6.F20.boolean.opBoolean","SPLIT",EDGE,{"disambiguationData":[TD([subQ6])],"derivedFrom":makeQuery(id+"F0Hq7nSFAMYVZvY_4.5.F20.boolean.opBoolean","SPLIT",EDGE,{"disambiguationData":[TD([subQ6])],"derivedFrom":makeQuery(id+"F0Hq7nSFAMYVZvY_4.4.F20.boolean.opBoolean","SPLIT",EDGE,{"disambiguationData":[TD([subQ6])],"derivedFrom":makeQuery(id+"F0Hq7nSFAMYVZvY_4.3.F20.boolean.opBoolean","SPLIT",EDGE,{"disambiguationData":[TD([subQ6])],"derivedFrom":makeQuery(id+"F0Hq7nSFAMYVZvY_4.2.F20.boolean.opBoolean","SPLIT",EDGE,{"disambiguationData":[TD([subQ6])],"derivedFrom":makeQuery(id+"F0Hq7nSFAMYVZvY_4.1.F20.boolean.opBoolean","SPLIT",EDGE,{"disambiguationData":[TD([subQ6])],"derivedFrom":makeQuery(id+"F17.boolean.opBoolean","COPY",EDGE,{"derivedFrom":makeQuery(id+"F17.opExtrude","CAP_EDGE",EDGE,{"disambiguationData":[OSD([subQ0])],"isStart":false})})})})})})})})})})})})});}
            var Q490;
            Q490=makeQuery(id+"F0Hq7nSFAMYVZvY_4.12.F20.opExtrude","SWEPT_EDGE",EDGE,{"disambiguationData":[OSD([sQuery(id+"F16.wireOp",EDGE,"E151"),sQuery(id+"F19.wireOp",EDGE,"E157")])]});
            var Q491;
            Q491=makeQuery(id+"F1.opRevolve","SWEPT_EDGE",EDGE,{"disambiguationData":[OSD([sQuery(id+"F0.wireOp",EDGE,"E104"),sQuery(id+"F0.wireOp",EDGE,"E105")])]});
            var Q492;
            Q492=makeQuery(id+"F1.opRevolve","SWEPT_EDGE",EDGE,{"disambiguationData":[OSD([sQuery(id+"F0.wireOp",EDGE,"E105"),sQuery(id+"F0.wireOp",EDGE,"E106.filletArc")])]});
            fillet(context, id + "F21", {"entities" : qUnion([Q0, Q1, Q2, Q3, Q4, Q5, Q6, Q7, Q8, Q9, Q10, Q11, Q12, Q13, Q14, Q15, Q16, Q17, Q18, Q19, Q20, Q21, Q22, Q23, Q24, Q25, Q26, Q27, Q28, Q29, Q30, Q31, Q32, Q33, Q34, Q35, Q36, Q37, Q38, Q39, Q40, Q41, Q42, Q43, Q44, Q45, Q46, Q47, Q48, Q49, Q50, Q51, Q52, Q53, Q54, Q55, Q56, Q57, Q58, Q59, Q60, Q61, Q62, Q63, Q64, Q65, Q66, Q67, Q68, Q69, Q70, Q71, Q72, Q73, Q74, Q75, Q76, Q77, Q78, Q79, Q80, Q81, Q82, Q83, Q84, Q85, Q86, Q87, Q88, Q89, Q90, Q91, Q92, Q93, Q94, Q95, Q96, Q97, Q98, Q99, Q100, Q101, Q102, Q103, Q104, Q105, Q106, Q107, Q108, Q109, Q110, Q111, Q112, Q113, Q114, Q115, Q116, Q117, Q118, Q119, Q120, Q121, Q122, Q123, Q124, Q125, Q126, Q127, Q128, Q129, Q130, Q131, Q132, Q133, Q134, Q135, Q136, Q137, Q138, Q139, Q140, Q141, Q142, Q143, Q144, Q145, Q146, Q147, Q148, Q149, Q150, Q151, Q152, Q153, Q154, Q155, Q156, Q157, Q158, Q159, Q160, Q161, Q162, Q163, Q164, Q165, Q166, Q167, Q168, Q169, Q170, Q171, Q172, Q173, Q174, Q175, Q176, Q177, Q178, Q179, Q180, Q181, Q182, Q183, Q184, Q185, Q186, Q187, Q188, Q189, Q190, Q191, Q192, Q193, Q194, Q195, Q196, Q197, Q198, Q199, Q200, Q201, Q202, Q203, Q204, Q205, Q206, Q207, Q208, Q209, Q210, Q211, Q212, Q213, Q214, Q215, Q216, Q217, Q218, Q219, Q220, Q221, Q222, Q223, Q224, Q225, Q226, Q227, Q228, Q229, Q230, Q231, Q232, Q233, Q234, Q235, Q236, Q237, Q238, Q239, Q240, Q241, Q242, Q243, Q244, Q245, Q246, Q247, Q248, Q249, Q250, Q251, Q252, Q253, Q254, Q255, Q256, Q257, Q258, Q259, Q260, Q261, Q262, Q263, Q264, Q265, Q266, Q267, Q268, Q269, Q270, Q271, Q272, Q273, Q274, Q275, Q276, Q277, Q278, Q279, Q280, Q281, Q282, Q283, Q284, Q285, Q286, Q287, Q288, Q289, Q290, Q291, Q292, Q293, Q294, Q295, Q296, Q297, Q298, Q299, Q300, Q301, Q302, Q303, Q304, Q305, Q306, Q307, Q308, Q309, Q310, Q311, Q312, Q313, Q314, Q315, Q316, Q317, Q318, Q319, Q320, Q321, Q322, Q323, Q324, Q325, Q326, Q327, Q328, Q329, Q330, Q331, Q332, Q333, Q334, Q335, Q336, Q337, Q338, Q339, Q340, Q341, Q342, Q343, Q344, Q345, Q346, Q347, Q348, Q349, Q350, Q351, Q352, Q353, Q354, Q355, Q356, Q357, Q358, Q359, Q360, Q361, Q362, Q363, Q364, Q365, Q366, Q367, Q368, Q369, Q370, Q371, Q372, Q373, Q374, Q375, Q376, Q377, Q378, Q379, Q380, Q381, Q382, Q383, Q384, Q385, Q386, Q387, Q388, Q389, Q390, Q391, Q392, Q393, Q394, Q395, Q396, Q397, Q398, Q399, Q400, Q401, Q402, Q403, Q404, Q405, Q406, Q407, Q408, Q409, Q410, Q411, Q412, Q413, Q414, Q415, Q416, Q417, Q418, Q419, Q420, Q421, Q422, Q423, Q424, Q425, Q426, Q427, Q428, Q429, Q430, Q431, Q432, Q433, Q434, Q435, Q436, Q437, Q438, Q439, Q440, Q441, Q442, Q443, Q444, Q445, Q446, Q447, Q448, Q449, Q450, Q451, Q452, Q453, Q454, Q455, Q456, Q457, Q458, Q459, Q460, Q461, Q462, Q463, Q464, Q465, Q466, Q467, Q468, Q469, Q470, Q471, Q472, Q473, Q474, Q475, Q476, Q477, Q478, Q479, Q480, Q481, Q482, Q483, Q484, Q485, Q486, Q487, Q488, Q489, Q490, Q491, Q492]), "radius" : .2 * mm, "tangentPropagation" : true, "allowEdgeOverflow" : false});
        }
    });
